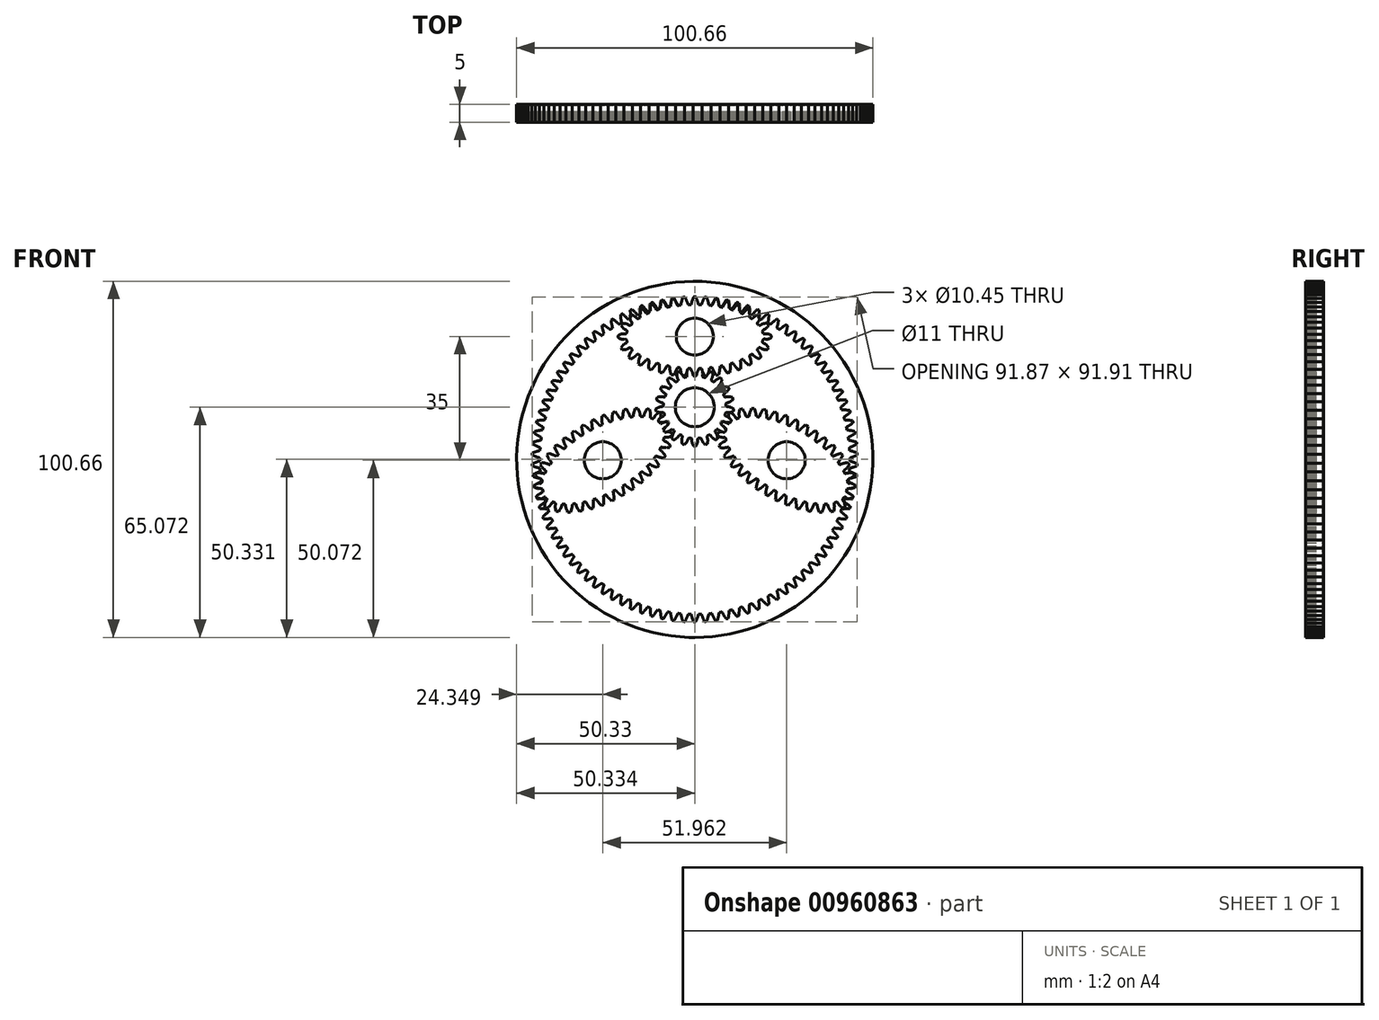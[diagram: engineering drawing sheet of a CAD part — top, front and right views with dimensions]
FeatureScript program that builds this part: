
annotation { "Feature Type Name" : "Feature", "Feature Type Description" : "" }
export const myFeature = defineFeature(function(context is Context, id is Id, definition is map)
    precondition{}
    {
        {
            var Q0;
            Q0=qCreatedBy(makeId("Front.planeOp"),FACE);
            var sketch = newSketch(context, id + "F0", { "sketchPlane" : qUnion([Q0])});
            skCircle(sketch, "E0", {"center": v(0, 0) * mm, "radius": 44.74 * mm});
            skCircle(sketch, "E1", {"center": v(0, 14.74) * mm, "radius": 10 * mm});
            skLineSegment(sketch, "E2", {"start": v(0, 14.74) * mm, "end": v(43.52, -10.38) * mm, "construction": true});
            skEllipse(sketch, "E3", {"center": v(0, 34.74) * mm, "majorRadius": 2 * mm, "minorRadius": 1 * mm, "majorAxis": v(1, 0)});
            skPoint(sketch, "E4", {"position": v(8.66, 9.74) * mm});
            skPoint(sketch, "E5", {"position": v(20.98, -8.92) * mm});
            skPoint(sketch, "E6", {"position": v(-20, 34.74) * mm});
            skPoint(sketch, "E7", {"position": v(0, 24.74) * mm});
            skPoint(sketch, "E8.center.orphan", {"position": v(25.98, -0.26) * mm});
            skLineSegment(sketch, "E9", {"start": v(25.98, -0.26) * mm, "end": v(20.98, -8.92) * mm, "construction": true});
            skEllipse(sketch, "E10", {"center": v(25.98, -0.26) * mm, "majorRadius": 2 * mm, "minorRadius": 1 * mm, "majorAxis": v(-0.87, 0.5)});
            skPoint(sketch, "E11", {"position": v(0, 4.74) * mm});
            skPoint(sketch, "E12", {"position": v(43.9, -8.66) * mm});
            skPoint(sketch, "E13", {"position": v(0, -44.74) * mm});
            skEllipse(sketch, "E14.MirrorC", {"center": v(-25.98, -0.26) * mm, "majorRadius": 2 * mm, "minorRadius": 1 * mm, "majorAxis": v(0.87, 0.5)});
            skSolve(sketch);
        }
        {
            var Q0;
            Q0=qCreatedBy(makeId("Front.planeOp"),FACE);
            var sketch = newSketch(context, id + "F1", { "sketchPlane" : qUnion([Q0])});
            skLineSegment(sketch, "E15", {"start": v(0.42, -11.95) * mm, "end": v(0.63, -11.4) * mm});
            skLineSegment(sketch, "E16", {"start": v(0.63, -11.4) * mm, "end": v(0.66, -11.33) * mm});
            skLineSegment(sketch, "E17", {"start": v(0.66, -11.33) * mm, "end": v(0.7, -11.25) * mm});
            skLineSegment(sketch, "E18", {"start": v(0.7, -11.25) * mm, "end": v(0.72, -11.18) * mm});
            skLineSegment(sketch, "E19", {"start": v(0.72, -11.18) * mm, "end": v(0.75, -11.1) * mm});
            skLineSegment(sketch, "E20", {"start": v(0.75, -11.1) * mm, "end": v(0.77, -11.03) * mm});
            skLineSegment(sketch, "E21", {"start": v(0.77, -11.03) * mm, "end": v(0.8, -10.96) * mm});
            skLineSegment(sketch, "E22", {"start": v(0.8, -10.96) * mm, "end": v(0.83, -10.86) * mm});
            skLineSegment(sketch, "E23", {"start": v(0.83, -10.86) * mm, "end": v(0.88, -10.72) * mm});
            skLineSegment(sketch, "E24", {"start": v(0.88, -10.72) * mm, "end": v(0.9, -10.63) * mm});
            skLineSegment(sketch, "E25", {"start": v(0.9, -10.63) * mm, "end": v(0.93, -10.57) * mm});
            skLineSegment(sketch, "E26", {"start": v(0.93, -10.57) * mm, "end": v(0.96, -10.47) * mm});
            skLineSegment(sketch, "E27", {"start": v(0.96, -10.47) * mm, "end": v(1, -10.36) * mm});
            skLineSegment(sketch, "E28", {"start": v(1, -10.36) * mm, "end": v(1.03, -10.24) * mm});
            skLineSegment(sketch, "E29", {"start": v(1.03, -10.24) * mm, "end": v(1.06, -10.14) * mm});
            skLineSegment(sketch, "E30", {"start": v(1.06, -10.14) * mm, "end": v(1.09, -10.04) * mm});
            skLineSegment(sketch, "E31", {"start": v(1.09, -10.04) * mm, "end": v(1.11, -9.94) * mm});
            skLineSegment(sketch, "E32", {"start": v(1.11, -9.94) * mm, "end": v(1.2, -9.64) * mm});
            skLineSegment(sketch, "E33", {"start": v(1.2, -9.64) * mm, "end": v(1.2, -9.62) * mm});
            skLineSegment(sketch, "E34", {"start": v(1.2, -9.62) * mm, "end": v(1.2, -9.6) * mm});
            skLineSegment(sketch, "E35", {"start": v(1.2, -9.6) * mm, "end": v(1.22, -9.58) * mm});
            skLineSegment(sketch, "E36", {"start": v(1.22, -9.58) * mm, "end": v(1.23, -9.57) * mm});
            skLineSegment(sketch, "E37", {"start": v(1.23, -9.57) * mm, "end": v(1.24, -9.55) * mm});
            skLineSegment(sketch, "E38", {"start": v(1.24, -9.55) * mm, "end": v(1.25, -9.54) * mm});
            skLineSegment(sketch, "E39", {"start": v(1.25, -9.54) * mm, "end": v(1.26, -9.54) * mm});
            skLineSegment(sketch, "E40", {"start": v(1.26, -9.54) * mm, "end": v(1.26, -9.54) * mm});
            skLineSegment(sketch, "E41", {"start": v(1.26, -9.54) * mm, "end": v(1.27, -9.54) * mm});
            skLineSegment(sketch, "E42", {"start": v(1.27, -9.54) * mm, "end": v(1.5, -9.53) * mm});
            skLineSegment(sketch, "E43", {"start": v(1.5, -9.53) * mm, "end": v(1.7, -9.52) * mm});
            skLineSegment(sketch, "E44", {"start": v(1.7, -9.52) * mm, "end": v(1.95, -9.51) * mm});
            skLineSegment(sketch, "E45", {"start": v(1.95, -9.51) * mm, "end": v(1.95, -9.51) * mm});
            skLineSegment(sketch, "E46", {"start": v(1.95, -9.51) * mm, "end": v(1.96, -9.52) * mm});
            skLineSegment(sketch, "E47", {"start": v(1.96, -9.52) * mm, "end": v(1.97, -9.53) * mm});
            skLineSegment(sketch, "E48", {"start": v(1.97, -9.53) * mm, "end": v(1.98, -9.54) * mm});
            skLineSegment(sketch, "E49", {"start": v(1.98, -9.54) * mm, "end": v(2, -9.54) * mm});
            skLineSegment(sketch, "E50", {"start": v(2, -9.54) * mm, "end": v(2, -9.55) * mm});
            skLineSegment(sketch, "E51", {"start": v(2, -9.55) * mm, "end": v(2, -9.56) * mm});
            skLineSegment(sketch, "E52", {"start": v(2, -9.56) * mm, "end": v(2.01, -9.57) * mm});
            skLineSegment(sketch, "E53", {"start": v(2.01, -9.57) * mm, "end": v(2.02, -9.59) * mm});
            skLineSegment(sketch, "E54", {"start": v(2.02, -9.59) * mm, "end": v(2.03, -9.6) * mm});
            skLineSegment(sketch, "E55", {"start": v(2.03, -9.6) * mm, "end": v(2.03, -9.6) * mm});
            skLineSegment(sketch, "E56", {"start": v(2.03, -9.6) * mm, "end": v(2.11, -9.86) * mm});
            skLineSegment(sketch, "E57", {"start": v(2.11, -9.86) * mm, "end": v(2.13, -9.91) * mm});
            skLineSegment(sketch, "E58", {"start": v(2.13, -9.91) * mm, "end": v(2.16, -9.98) * mm});
            skLineSegment(sketch, "E59", {"start": v(2.16, -9.98) * mm, "end": v(2.17, -10.03) * mm});
            skLineSegment(sketch, "E60", {"start": v(2.17, -10.03) * mm, "end": v(2.2, -10.1) * mm});
            skLineSegment(sketch, "E61", {"start": v(2.2, -10.1) * mm, "end": v(2.22, -10.16) * mm});
            skLineSegment(sketch, "E62", {"start": v(2.22, -10.16) * mm, "end": v(2.24, -10.2) * mm});
            skLineSegment(sketch, "E63", {"start": v(2.24, -10.2) * mm, "end": v(2.27, -10.3) * mm});
            skLineSegment(sketch, "E64", {"start": v(2.27, -10.3) * mm, "end": v(2.32, -10.42) * mm});
            skLineSegment(sketch, "E65", {"start": v(2.32, -10.42) * mm, "end": v(2.36, -10.5) * mm});
            skLineSegment(sketch, "E66", {"start": v(2.36, -10.5) * mm, "end": v(2.38, -10.57) * mm});
            skLineSegment(sketch, "E67", {"start": v(2.38, -10.57) * mm, "end": v(2.42, -10.66) * mm});
            skLineSegment(sketch, "E68", {"start": v(2.42, -10.66) * mm, "end": v(2.47, -10.78) * mm});
            skLineSegment(sketch, "E69", {"start": v(2.47, -10.78) * mm, "end": v(2.53, -10.9) * mm});
            skLineSegment(sketch, "E70", {"start": v(2.53, -10.9) * mm, "end": v(2.58, -11.03) * mm});
            skLineSegment(sketch, "E71", {"start": v(2.58, -11.03) * mm, "end": v(2.64, -11.15) * mm});
            skLineSegment(sketch, "E72", {"start": v(2.64, -11.15) * mm, "end": v(2.7, -11.28) * mm});
            skLineSegment(sketch, "E73", {"start": v(2.7, -11.28) * mm, "end": v(2.97, -11.85) * mm});
            skLineSegment(sketch, "E74", {"start": v(2.97, -11.85) * mm, "end": v(3.11, -11.84) * mm});
            skLineSegment(sketch, "E75", {"start": v(3.11, -11.84) * mm, "end": v(3.5, -11.81) * mm});
            skLineSegment(sketch, "E76", {"start": v(3.5, -11.81) * mm, "end": v(3.79, -11.8) * mm});
            skLineSegment(sketch, "E77", {"start": v(3.79, -11.8) * mm, "end": v(3.95, -11.28) * mm});
            skLineSegment(sketch, "E78", {"start": v(3.95, -11.28) * mm, "end": v(3.99, -11.13) * mm});
            skLineSegment(sketch, "E79", {"start": v(3.99, -11.13) * mm, "end": v(4.03, -11) * mm});
            skLineSegment(sketch, "E80", {"start": v(4.03, -11) * mm, "end": v(4.06, -10.88) * mm});
            skLineSegment(sketch, "E81", {"start": v(4.06, -10.88) * mm, "end": v(4.1, -10.74) * mm});
            skLineSegment(sketch, "E82", {"start": v(4.1, -10.74) * mm, "end": v(4.13, -10.63) * mm});
            skLineSegment(sketch, "E83", {"start": v(4.13, -10.63) * mm, "end": v(4.16, -10.51) * mm});
            skLineSegment(sketch, "E84", {"start": v(4.16, -10.51) * mm, "end": v(4.18, -10.42) * mm});
            skLineSegment(sketch, "E85", {"start": v(4.18, -10.42) * mm, "end": v(4.19, -10.38) * mm});
            skLineSegment(sketch, "E86", {"start": v(4.19, -10.38) * mm, "end": v(4.2, -10.3) * mm});
            skLineSegment(sketch, "E87", {"start": v(4.2, -10.3) * mm, "end": v(4.23, -10.2) * mm});
            skLineSegment(sketch, "E88", {"start": v(4.23, -10.2) * mm, "end": v(4.25, -10.1) * mm});
            skLineSegment(sketch, "E89", {"start": v(4.25, -10.1) * mm, "end": v(4.27, -10.01) * mm});
            skLineSegment(sketch, "E90", {"start": v(4.27, -10.01) * mm, "end": v(4.29, -9.92) * mm});
            skLineSegment(sketch, "E91", {"start": v(4.29, -9.92) * mm, "end": v(4.3, -9.84) * mm});
            skLineSegment(sketch, "E92", {"start": v(4.3, -9.84) * mm, "end": v(4.32, -9.76) * mm});
            skLineSegment(sketch, "E93", {"start": v(4.32, -9.76) * mm, "end": v(4.33, -9.68) * mm});
            skLineSegment(sketch, "E94", {"start": v(4.33, -9.68) * mm, "end": v(4.37, -9.45) * mm});
            skLineSegment(sketch, "E95", {"start": v(4.37, -9.45) * mm, "end": v(4.37, -9.44) * mm});
            skLineSegment(sketch, "E96", {"start": v(4.37, -9.44) * mm, "end": v(4.38, -9.41) * mm});
            skLineSegment(sketch, "E97", {"start": v(4.38, -9.41) * mm, "end": v(4.39, -9.4) * mm});
            skLineSegment(sketch, "E98", {"start": v(4.39, -9.4) * mm, "end": v(4.4, -9.38) * mm});
            skLineSegment(sketch, "E99", {"start": v(4.4, -9.38) * mm, "end": v(4.4, -9.36) * mm});
            skLineSegment(sketch, "E100", {"start": v(4.4, -9.36) * mm, "end": v(4.41, -9.35) * mm});
            skLineSegment(sketch, "E101", {"start": v(4.41, -9.35) * mm, "end": v(4.42, -9.33) * mm});
            skLineSegment(sketch, "E102", {"start": v(4.42, -9.33) * mm, "end": v(4.43, -9.33) * mm});
            skLineSegment(sketch, "E103", {"start": v(4.43, -9.33) * mm, "end": v(4.44, -9.32) * mm});
            skLineSegment(sketch, "E104", {"start": v(4.44, -9.32) * mm, "end": v(4.44, -9.32) * mm});
            skLineSegment(sketch, "E105", {"start": v(4.44, -9.32) * mm, "end": v(4.7, -9.3) * mm});
            skLineSegment(sketch, "E106", {"start": v(4.7, -9.3) * mm, "end": v(4.87, -9.27) * mm});
            skLineSegment(sketch, "E107", {"start": v(4.87, -9.27) * mm, "end": v(5.12, -9.24) * mm});
            skLineSegment(sketch, "E108", {"start": v(5.12, -9.24) * mm, "end": v(5.12, -9.24) * mm});
            skLineSegment(sketch, "E109", {"start": v(5.12, -9.24) * mm, "end": v(5.13, -9.24) * mm});
            skLineSegment(sketch, "E110", {"start": v(5.13, -9.24) * mm, "end": v(5.13, -9.24) * mm});
            skLineSegment(sketch, "E111", {"start": v(5.13, -9.24) * mm, "end": v(5.15, -9.25) * mm});
            skLineSegment(sketch, "E112", {"start": v(5.15, -9.25) * mm, "end": v(5.16, -9.26) * mm});
            skLineSegment(sketch, "E113", {"start": v(5.16, -9.26) * mm, "end": v(5.17, -9.27) * mm});
            skLineSegment(sketch, "E114", {"start": v(5.17, -9.27) * mm, "end": v(5.19, -9.29) * mm});
            skLineSegment(sketch, "E115", {"start": v(5.19, -9.29) * mm, "end": v(5.2, -9.3) * mm});
            skLineSegment(sketch, "E116", {"start": v(5.2, -9.3) * mm, "end": v(5.21, -9.33) * mm});
            skLineSegment(sketch, "E117", {"start": v(5.21, -9.33) * mm, "end": v(5.22, -9.35) * mm});
            skLineSegment(sketch, "E118", {"start": v(5.22, -9.35) * mm, "end": v(5.3, -9.55) * mm});
            skLineSegment(sketch, "E119", {"start": v(5.3, -9.55) * mm, "end": v(5.35, -9.65) * mm});
            skLineSegment(sketch, "E120", {"start": v(5.35, -9.65) * mm, "end": v(5.4, -9.74) * mm});
            skLineSegment(sketch, "E121", {"start": v(5.4, -9.74) * mm, "end": v(5.43, -9.84) * mm});
            skLineSegment(sketch, "E122", {"start": v(5.43, -9.84) * mm, "end": v(5.48, -9.94) * mm});
            skLineSegment(sketch, "E123", {"start": v(5.48, -9.94) * mm, "end": v(5.53, -10.04) * mm});
            skLineSegment(sketch, "E124", {"start": v(5.53, -10.04) * mm, "end": v(5.57, -10.13) * mm});
            skLineSegment(sketch, "E125", {"start": v(5.57, -10.13) * mm, "end": v(5.6, -10.2) * mm});
            skLineSegment(sketch, "E126", {"start": v(5.6, -10.2) * mm, "end": v(5.64, -10.26) * mm});
            skLineSegment(sketch, "E127", {"start": v(5.64, -10.26) * mm, "end": v(5.68, -10.34) * mm});
            skLineSegment(sketch, "E128", {"start": v(5.68, -10.34) * mm, "end": v(5.73, -10.43) * mm});
            skLineSegment(sketch, "E129", {"start": v(5.73, -10.43) * mm, "end": v(5.78, -10.53) * mm});
            skLineSegment(sketch, "E130", {"start": v(5.78, -10.53) * mm, "end": v(5.83, -10.63) * mm});
            skLineSegment(sketch, "E131", {"start": v(5.83, -10.63) * mm, "end": v(5.88, -10.72) * mm});
            skLineSegment(sketch, "E132", {"start": v(5.88, -10.72) * mm, "end": v(5.94, -10.82) * mm});
            skLineSegment(sketch, "E133", {"start": v(5.94, -10.82) * mm, "end": v(6, -10.92) * mm});
            skLineSegment(sketch, "E134", {"start": v(6, -10.92) * mm, "end": v(6.05, -11.02) * mm});
            skLineSegment(sketch, "E135", {"start": v(6.05, -11.02) * mm, "end": v(6.33, -11.5) * mm});
            skLineSegment(sketch, "E136", {"start": v(6.33, -11.5) * mm, "end": v(6.63, -11.45) * mm});
            skLineSegment(sketch, "E137", {"start": v(6.63, -11.45) * mm, "end": v(6.94, -11.4) * mm});
            skLineSegment(sketch, "E138", {"start": v(6.94, -11.4) * mm, "end": v(7.14, -11.37) * mm});
            skLineSegment(sketch, "E139", {"start": v(7.14, -11.37) * mm, "end": v(7.27, -10.78) * mm});
            skLineSegment(sketch, "E140", {"start": v(7.27, -10.78) * mm, "end": v(7.3, -10.66) * mm});
            skLineSegment(sketch, "E141", {"start": v(7.3, -10.66) * mm, "end": v(7.31, -10.55) * mm});
            skLineSegment(sketch, "E142", {"start": v(7.31, -10.55) * mm, "end": v(7.33, -10.44) * mm});
            skLineSegment(sketch, "E143", {"start": v(7.33, -10.44) * mm, "end": v(7.36, -10.33) * mm});
            skLineSegment(sketch, "E144", {"start": v(7.36, -10.33) * mm, "end": v(7.37, -10.23) * mm});
            skLineSegment(sketch, "E145", {"start": v(7.37, -10.23) * mm, "end": v(7.39, -10.14) * mm});
            skLineSegment(sketch, "E146", {"start": v(7.39, -10.14) * mm, "end": v(7.4, -10.03) * mm});
            skLineSegment(sketch, "E147", {"start": v(7.4, -10.03) * mm, "end": v(7.41, -9.98) * mm});
            skLineSegment(sketch, "E148", {"start": v(7.41, -9.98) * mm, "end": v(7.42, -9.93) * mm});
            skLineSegment(sketch, "E149", {"start": v(7.42, -9.93) * mm, "end": v(7.43, -9.86) * mm});
            skLineSegment(sketch, "E150", {"start": v(7.43, -9.86) * mm, "end": v(7.44, -9.78) * mm});
            skLineSegment(sketch, "E151", {"start": v(7.44, -9.78) * mm, "end": v(7.45, -9.7) * mm});
            skLineSegment(sketch, "E152", {"start": v(7.45, -9.7) * mm, "end": v(7.46, -9.62) * mm});
            skLineSegment(sketch, "E153", {"start": v(7.46, -9.62) * mm, "end": v(7.47, -9.55) * mm});
            skLineSegment(sketch, "E154", {"start": v(7.47, -9.55) * mm, "end": v(7.48, -9.5) * mm});
            skLineSegment(sketch, "E155", {"start": v(7.48, -9.5) * mm, "end": v(7.48, -9.42) * mm});
            skLineSegment(sketch, "E156", {"start": v(7.48, -9.42) * mm, "end": v(7.49, -9.36) * mm});
            skLineSegment(sketch, "E157", {"start": v(7.49, -9.36) * mm, "end": v(7.5, -9.3) * mm});
            skLineSegment(sketch, "E158", {"start": v(7.5, -9.3) * mm, "end": v(7.5, -9.24) * mm});
            skLineSegment(sketch, "E159", {"start": v(7.5, -9.24) * mm, "end": v(7.52, -9) * mm});
            skLineSegment(sketch, "E160", {"start": v(7.52, -9) * mm, "end": v(7.52, -8.99) * mm});
            skLineSegment(sketch, "E161", {"start": v(7.52, -8.99) * mm, "end": v(7.52, -8.97) * mm});
            skLineSegment(sketch, "E162", {"start": v(7.52, -8.97) * mm, "end": v(7.53, -8.95) * mm});
            skLineSegment(sketch, "E163", {"start": v(7.53, -8.95) * mm, "end": v(7.53, -8.93) * mm});
            skLineSegment(sketch, "E164", {"start": v(7.53, -8.93) * mm, "end": v(7.54, -8.91) * mm});
            skLineSegment(sketch, "E165", {"start": v(7.54, -8.91) * mm, "end": v(7.55, -8.9) * mm});
            skLineSegment(sketch, "E166", {"start": v(7.55, -8.9) * mm, "end": v(7.55, -8.88) * mm});
            skLineSegment(sketch, "E167", {"start": v(7.55, -8.88) * mm, "end": v(7.56, -8.87) * mm});
            skLineSegment(sketch, "E168", {"start": v(7.56, -8.87) * mm, "end": v(7.57, -8.86) * mm});
            skLineSegment(sketch, "E169", {"start": v(7.57, -8.86) * mm, "end": v(7.58, -8.86) * mm});
            skLineSegment(sketch, "E170", {"start": v(7.58, -8.86) * mm, "end": v(7.58, -8.85) * mm});
            skLineSegment(sketch, "E171", {"start": v(7.58, -8.85) * mm, "end": v(7.58, -8.85) * mm});
            skLineSegment(sketch, "E172", {"start": v(7.58, -8.85) * mm, "end": v(7.6, -8.85) * mm});
            skLineSegment(sketch, "E173", {"start": v(7.6, -8.85) * mm, "end": v(7.6, -8.85) * mm});
            skLineSegment(sketch, "E174", {"start": v(7.6, -8.85) * mm, "end": v(7.65, -8.84) * mm});
            skLineSegment(sketch, "E175", {"start": v(7.65, -8.84) * mm, "end": v(7.85, -8.8) * mm});
            skLineSegment(sketch, "E176", {"start": v(7.85, -8.8) * mm, "end": v(8, -8.77) * mm});
            skLineSegment(sketch, "E177", {"start": v(8, -8.77) * mm, "end": v(8.18, -8.73) * mm});
            skLineSegment(sketch, "E178", {"start": v(8.18, -8.73) * mm, "end": v(8.25, -8.72) * mm});
            skLineSegment(sketch, "E179", {"start": v(8.25, -8.72) * mm, "end": v(8.25, -8.71) * mm});
            skLineSegment(sketch, "E180", {"start": v(8.25, -8.71) * mm, "end": v(8.26, -8.71) * mm});
            skLineSegment(sketch, "E181", {"start": v(8.26, -8.71) * mm, "end": v(8.26, -8.71) * mm});
            skLineSegment(sketch, "E182", {"start": v(8.26, -8.71) * mm, "end": v(8.27, -8.72) * mm});
            skLineSegment(sketch, "E183", {"start": v(8.27, -8.72) * mm, "end": v(8.28, -8.72) * mm});
            skLineSegment(sketch, "E184", {"start": v(8.28, -8.72) * mm, "end": v(8.29, -8.73) * mm});
            skLineSegment(sketch, "E185", {"start": v(8.29, -8.73) * mm, "end": v(8.3, -8.73) * mm});
            skLineSegment(sketch, "E186", {"start": v(8.3, -8.73) * mm, "end": v(8.31, -8.75) * mm});
            skLineSegment(sketch, "E187", {"start": v(8.31, -8.75) * mm, "end": v(8.33, -8.76) * mm});
            skLineSegment(sketch, "E188", {"start": v(8.33, -8.76) * mm, "end": v(8.34, -8.78) * mm});
            skLineSegment(sketch, "E189", {"start": v(8.34, -8.78) * mm, "end": v(8.36, -8.8) * mm});
            skLineSegment(sketch, "E190", {"start": v(8.36, -8.8) * mm, "end": v(8.36, -8.8) * mm});
            skLineSegment(sketch, "E191", {"start": v(8.36, -8.8) * mm, "end": v(8.5, -9.05) * mm});
            skLineSegment(sketch, "E192", {"start": v(8.5, -9.05) * mm, "end": v(8.53, -9.13) * mm});
            skLineSegment(sketch, "E193", {"start": v(8.53, -9.13) * mm, "end": v(8.57, -9.2) * mm});
            skLineSegment(sketch, "E194", {"start": v(8.57, -9.2) * mm, "end": v(8.62, -9.28) * mm});
            skLineSegment(sketch, "E195", {"start": v(8.62, -9.28) * mm, "end": v(8.66, -9.35) * mm});
            skLineSegment(sketch, "E196", {"start": v(8.66, -9.35) * mm, "end": v(8.7, -9.43) * mm});
            skLineSegment(sketch, "E197", {"start": v(8.7, -9.43) * mm, "end": v(8.75, -9.51) * mm});
            skLineSegment(sketch, "E198", {"start": v(8.75, -9.51) * mm, "end": v(8.8, -9.59) * mm});
            skLineSegment(sketch, "E199", {"start": v(8.8, -9.59) * mm, "end": v(8.83, -9.64) * mm});
            skLineSegment(sketch, "E200", {"start": v(8.83, -9.64) * mm, "end": v(8.85, -9.68) * mm});
            skLineSegment(sketch, "E201", {"start": v(8.85, -9.68) * mm, "end": v(8.89, -9.73) * mm});
            skLineSegment(sketch, "E202", {"start": v(8.89, -9.73) * mm, "end": v(8.94, -9.81) * mm});
            skLineSegment(sketch, "E203", {"start": v(8.94, -9.81) * mm, "end": v(8.98, -9.88) * mm});
            skLineSegment(sketch, "E204", {"start": v(8.98, -9.88) * mm, "end": v(9.03, -9.96) * mm});
            skLineSegment(sketch, "E205", {"start": v(9.03, -9.96) * mm, "end": v(9.08, -10.04) * mm});
            skLineSegment(sketch, "E206", {"start": v(9.08, -10.04) * mm, "end": v(9.13, -10.1) * mm});
            skLineSegment(sketch, "E207", {"start": v(9.13, -10.1) * mm, "end": v(9.18, -10.19) * mm});
            skLineSegment(sketch, "E208", {"start": v(9.18, -10.19) * mm, "end": v(9.23, -10.25) * mm});
            skLineSegment(sketch, "E209", {"start": v(9.23, -10.25) * mm, "end": v(9.28, -10.33) * mm});
            skLineSegment(sketch, "E210", {"start": v(9.28, -10.33) * mm, "end": v(9.34, -10.4) * mm});
            skLineSegment(sketch, "E211", {"start": v(9.34, -10.4) * mm, "end": v(9.66, -10.85) * mm});
            skLineSegment(sketch, "E212", {"start": v(9.66, -10.85) * mm, "end": v(9.74, -10.83) * mm});
            skLineSegment(sketch, "E213", {"start": v(9.74, -10.83) * mm, "end": v(9.98, -10.77) * mm});
            skLineSegment(sketch, "E214", {"start": v(9.98, -10.77) * mm, "end": v(10.23, -10.71) * mm});
            skLineSegment(sketch, "E215", {"start": v(10.23, -10.71) * mm, "end": v(10.45, -10.65) * mm});
            skLineSegment(sketch, "E216", {"start": v(10.45, -10.65) * mm, "end": v(10.53, -10.04) * mm});
            skLineSegment(sketch, "E217", {"start": v(10.53, -10.04) * mm, "end": v(10.54, -9.94) * mm});
            skLineSegment(sketch, "E218", {"start": v(10.54, -9.94) * mm, "end": v(10.55, -9.85) * mm});
            skLineSegment(sketch, "E219", {"start": v(10.55, -9.85) * mm, "end": v(10.56, -9.75) * mm});
            skLineSegment(sketch, "E220", {"start": v(10.56, -9.75) * mm, "end": v(10.56, -9.68) * mm});
            skLineSegment(sketch, "E221", {"start": v(10.56, -9.68) * mm, "end": v(10.57, -9.59) * mm});
            skLineSegment(sketch, "E222", {"start": v(10.57, -9.59) * mm, "end": v(10.58, -9.51) * mm});
            skLineSegment(sketch, "E223", {"start": v(10.58, -9.51) * mm, "end": v(10.58, -9.43) * mm});
            skLineSegment(sketch, "E224", {"start": v(10.58, -9.43) * mm, "end": v(10.6, -9.35) * mm});
            skLineSegment(sketch, "E225", {"start": v(10.6, -9.35) * mm, "end": v(10.6, -9.29) * mm});
            skLineSegment(sketch, "E226", {"start": v(10.6, -9.29) * mm, "end": v(10.6, -9.24) * mm});
            skLineSegment(sketch, "E227", {"start": v(10.6, -9.24) * mm, "end": v(10.6, -9.2) * mm});
            skLineSegment(sketch, "E228", {"start": v(10.6, -9.2) * mm, "end": v(10.6, -9.14) * mm});
            skLineSegment(sketch, "E229", {"start": v(10.6, -9.14) * mm, "end": v(10.6, -9.04) * mm});
            skLineSegment(sketch, "E230", {"start": v(10.6, -9.04) * mm, "end": v(10.6, -8.96) * mm});
            skLineSegment(sketch, "E231", {"start": v(10.6, -8.96) * mm, "end": v(10.6, -8.87) * mm});
            skLineSegment(sketch, "E232", {"start": v(10.6, -8.87) * mm, "end": v(10.6, -8.8) * mm});
            skLineSegment(sketch, "E233", {"start": v(10.6, -8.8) * mm, "end": v(10.6, -8.73) * mm});
            skLineSegment(sketch, "E234", {"start": v(10.6, -8.73) * mm, "end": v(10.6, -8.66) * mm});
            skLineSegment(sketch, "E235", {"start": v(10.6, -8.66) * mm, "end": v(10.6, -8.6) * mm});
            skLineSegment(sketch, "E236", {"start": v(10.6, -8.6) * mm, "end": v(10.6, -8.55) * mm});
            skLineSegment(sketch, "E237", {"start": v(10.6, -8.55) * mm, "end": v(10.6, -8.3) * mm});
            skLineSegment(sketch, "E238", {"start": v(10.6, -8.3) * mm, "end": v(10.6, -8.28) * mm});
            skLineSegment(sketch, "E239", {"start": v(10.6, -8.28) * mm, "end": v(10.6, -8.25) * mm});
            skLineSegment(sketch, "E240", {"start": v(10.6, -8.25) * mm, "end": v(10.6, -8.23) * mm});
            skLineSegment(sketch, "E241", {"start": v(10.6, -8.23) * mm, "end": v(10.6, -8.2) * mm});
            skLineSegment(sketch, "E242", {"start": v(10.6, -8.2) * mm, "end": v(10.61, -8.18) * mm});
            skLineSegment(sketch, "E243", {"start": v(10.61, -8.18) * mm, "end": v(10.62, -8.16) * mm});
            skLineSegment(sketch, "E244", {"start": v(10.62, -8.16) * mm, "end": v(10.63, -8.14) * mm});
            skLineSegment(sketch, "E245", {"start": v(10.63, -8.14) * mm, "end": v(10.64, -8.13) * mm});
            skLineSegment(sketch, "E246", {"start": v(10.64, -8.13) * mm, "end": v(10.65, -8.11) * mm});
            skLineSegment(sketch, "E247", {"start": v(10.65, -8.11) * mm, "end": v(10.65, -8.11) * mm});
            skLineSegment(sketch, "E248", {"start": v(10.65, -8.11) * mm, "end": v(10.66, -8.1) * mm});
            skLineSegment(sketch, "E249", {"start": v(10.66, -8.1) * mm, "end": v(10.66, -8.1) * mm});
            skLineSegment(sketch, "E250", {"start": v(10.66, -8.1) * mm, "end": v(10.67, -8.1) * mm});
            skLineSegment(sketch, "E251", {"start": v(10.67, -8.1) * mm, "end": v(10.78, -8.07) * mm});
            skLineSegment(sketch, "E252", {"start": v(10.78, -8.07) * mm, "end": v(10.93, -8.02) * mm});
            skLineSegment(sketch, "E253", {"start": v(10.93, -8.02) * mm, "end": v(11.04, -8) * mm});
            skLineSegment(sketch, "E254", {"start": v(11.04, -8) * mm, "end": v(11.23, -7.93) * mm});
            skLineSegment(sketch, "E255", {"start": v(11.23, -7.93) * mm, "end": v(11.3, -7.9) * mm});
            skLineSegment(sketch, "E256", {"start": v(11.3, -7.9) * mm, "end": v(11.3, -7.9) * mm});
            skLineSegment(sketch, "E257", {"start": v(11.3, -7.9) * mm, "end": v(11.31, -7.9) * mm});
            skLineSegment(sketch, "E258", {"start": v(11.31, -7.9) * mm, "end": v(11.32, -7.9) * mm});
            skLineSegment(sketch, "E259", {"start": v(11.32, -7.9) * mm, "end": v(11.32, -7.9) * mm});
            skLineSegment(sketch, "E260", {"start": v(11.32, -7.9) * mm, "end": v(11.33, -7.9) * mm});
            skLineSegment(sketch, "E261", {"start": v(11.33, -7.9) * mm, "end": v(11.34, -7.91) * mm});
            skLineSegment(sketch, "E262", {"start": v(11.34, -7.91) * mm, "end": v(11.35, -7.92) * mm});
            skLineSegment(sketch, "E263", {"start": v(11.35, -7.92) * mm, "end": v(11.37, -7.92) * mm});
            skLineSegment(sketch, "E264", {"start": v(11.37, -7.92) * mm, "end": v(11.38, -7.93) * mm});
            skLineSegment(sketch, "E265", {"start": v(11.38, -7.93) * mm, "end": v(11.4, -7.94) * mm});
            skLineSegment(sketch, "E266", {"start": v(11.4, -7.94) * mm, "end": v(11.4, -7.95) * mm});
            skLineSegment(sketch, "E267", {"start": v(11.4, -7.95) * mm, "end": v(11.42, -7.97) * mm});
            skLineSegment(sketch, "E268", {"start": v(11.42, -7.97) * mm, "end": v(11.43, -7.98) * mm});
            skLineSegment(sketch, "E269", {"start": v(11.43, -7.98) * mm, "end": v(11.44, -8) * mm});
            skLineSegment(sketch, "E270", {"start": v(11.44, -8) * mm, "end": v(11.6, -8.24) * mm});
            skLineSegment(sketch, "E271", {"start": v(11.6, -8.24) * mm, "end": v(11.64, -8.3) * mm});
            skLineSegment(sketch, "E272", {"start": v(11.64, -8.3) * mm, "end": v(11.68, -8.36) * mm});
            skLineSegment(sketch, "E273", {"start": v(11.68, -8.36) * mm, "end": v(11.71, -8.41) * mm});
            skLineSegment(sketch, "E274", {"start": v(11.71, -8.41) * mm, "end": v(11.75, -8.47) * mm});
            skLineSegment(sketch, "E275", {"start": v(11.75, -8.47) * mm, "end": v(11.78, -8.51) * mm});
            skLineSegment(sketch, "E276", {"start": v(11.78, -8.51) * mm, "end": v(11.83, -8.58) * mm});
            skLineSegment(sketch, "E277", {"start": v(11.83, -8.58) * mm, "end": v(11.86, -8.63) * mm});
            skLineSegment(sketch, "E278", {"start": v(11.86, -8.63) * mm, "end": v(11.9, -8.69) * mm});
            skLineSegment(sketch, "E279", {"start": v(11.9, -8.69) * mm, "end": v(11.94, -8.73) * mm});
            skLineSegment(sketch, "E280", {"start": v(11.94, -8.73) * mm, "end": v(11.97, -8.78) * mm});
            skLineSegment(sketch, "E281", {"start": v(11.97, -8.78) * mm, "end": v(12, -8.8) * mm});
            skLineSegment(sketch, "E282", {"start": v(12, -8.8) * mm, "end": v(12.04, -8.86) * mm});
            skLineSegment(sketch, "E283", {"start": v(12.04, -8.86) * mm, "end": v(12.1, -8.94) * mm});
            skLineSegment(sketch, "E284", {"start": v(12.1, -8.94) * mm, "end": v(12.16, -9.02) * mm});
            skLineSegment(sketch, "E285", {"start": v(12.16, -9.02) * mm, "end": v(12.22, -9.1) * mm});
            skLineSegment(sketch, "E286", {"start": v(12.22, -9.1) * mm, "end": v(12.3, -9.18) * mm});
            skLineSegment(sketch, "E287", {"start": v(12.3, -9.18) * mm, "end": v(12.35, -9.25) * mm});
            skLineSegment(sketch, "E288", {"start": v(12.35, -9.25) * mm, "end": v(12.42, -9.33) * mm});
            skLineSegment(sketch, "E289", {"start": v(12.42, -9.33) * mm, "end": v(12.49, -9.4) * mm});
            skLineSegment(sketch, "E290", {"start": v(12.49, -9.4) * mm, "end": v(12.55, -9.48) * mm});
            skLineSegment(sketch, "E291", {"start": v(12.55, -9.48) * mm, "end": v(12.93, -9.89) * mm});
            skLineSegment(sketch, "E292", {"start": v(12.93, -9.89) * mm, "end": v(12.96, -9.88) * mm});
            skLineSegment(sketch, "E293", {"start": v(12.96, -9.88) * mm, "end": v(13.14, -9.81) * mm});
            skLineSegment(sketch, "E294", {"start": v(13.14, -9.81) * mm, "end": v(13.32, -9.75) * mm});
            skLineSegment(sketch, "E295", {"start": v(13.32, -9.75) * mm, "end": v(13.5, -9.68) * mm});
            skLineSegment(sketch, "E296", {"start": v(13.5, -9.68) * mm, "end": v(13.67, -9.62) * mm});
            skLineSegment(sketch, "E297", {"start": v(13.67, -9.62) * mm, "end": v(13.68, -9.61) * mm});
            skLineSegment(sketch, "E298", {"start": v(13.68, -9.61) * mm, "end": v(13.7, -9.08) * mm});
            skLineSegment(sketch, "E299", {"start": v(13.7, -9.08) * mm, "end": v(13.7, -8.96) * mm});
            skLineSegment(sketch, "E300", {"start": v(13.7, -8.96) * mm, "end": v(13.7, -8.85) * mm});
            skLineSegment(sketch, "E301", {"start": v(13.7, -8.85) * mm, "end": v(13.7, -8.75) * mm});
            skLineSegment(sketch, "E302", {"start": v(13.7, -8.75) * mm, "end": v(13.7, -8.65) * mm});
            skLineSegment(sketch, "E303", {"start": v(13.7, -8.65) * mm, "end": v(13.7, -8.56) * mm});
            skLineSegment(sketch, "E304", {"start": v(13.7, -8.56) * mm, "end": v(13.7, -8.46) * mm});
            skLineSegment(sketch, "E305", {"start": v(13.7, -8.46) * mm, "end": v(13.7, -8.38) * mm});
            skLineSegment(sketch, "E306", {"start": v(13.7, -8.38) * mm, "end": v(13.69, -8.3) * mm});
            skLineSegment(sketch, "E307", {"start": v(13.69, -8.3) * mm, "end": v(13.68, -8.22) * mm});
            skLineSegment(sketch, "E308", {"start": v(13.68, -8.22) * mm, "end": v(13.68, -8.17) * mm});
            skLineSegment(sketch, "E309", {"start": v(13.68, -8.17) * mm, "end": v(13.68, -8.14) * mm});
            skLineSegment(sketch, "E310", {"start": v(13.68, -8.14) * mm, "end": v(13.68, -8.12) * mm});
            skLineSegment(sketch, "E311", {"start": v(13.68, -8.12) * mm, "end": v(13.67, -8.05) * mm});
            skLineSegment(sketch, "E312", {"start": v(13.67, -8.05) * mm, "end": v(13.66, -7.98) * mm});
            skLineSegment(sketch, "E313", {"start": v(13.66, -7.98) * mm, "end": v(13.66, -7.92) * mm});
            skLineSegment(sketch, "E314", {"start": v(13.66, -7.92) * mm, "end": v(13.65, -7.85) * mm});
            skLineSegment(sketch, "E315", {"start": v(13.65, -7.85) * mm, "end": v(13.64, -7.78) * mm});
            skLineSegment(sketch, "E316", {"start": v(13.64, -7.78) * mm, "end": v(13.63, -7.73) * mm});
            skLineSegment(sketch, "E317", {"start": v(13.63, -7.73) * mm, "end": v(13.63, -7.68) * mm});
            skLineSegment(sketch, "E318", {"start": v(13.63, -7.68) * mm, "end": v(13.62, -7.63) * mm});
            skLineSegment(sketch, "E319", {"start": v(13.62, -7.63) * mm, "end": v(13.61, -7.58) * mm});
            skLineSegment(sketch, "E320", {"start": v(13.61, -7.58) * mm, "end": v(13.6, -7.55) * mm});
            skLineSegment(sketch, "E321", {"start": v(13.6, -7.55) * mm, "end": v(13.56, -7.33) * mm});
            skLineSegment(sketch, "E322", {"start": v(13.56, -7.33) * mm, "end": v(13.56, -7.31) * mm});
            skLineSegment(sketch, "E323", {"start": v(13.56, -7.31) * mm, "end": v(13.56, -7.3) * mm});
            skLineSegment(sketch, "E324", {"start": v(13.56, -7.3) * mm, "end": v(13.55, -7.26) * mm});
            skLineSegment(sketch, "E325", {"start": v(13.55, -7.26) * mm, "end": v(13.56, -7.24) * mm});
            skLineSegment(sketch, "E326", {"start": v(13.56, -7.24) * mm, "end": v(13.56, -7.2) * mm});
            skLineSegment(sketch, "E327", {"start": v(13.56, -7.2) * mm, "end": v(13.56, -7.18) * mm});
            skLineSegment(sketch, "E328", {"start": v(13.56, -7.18) * mm, "end": v(13.56, -7.15) * mm});
            skLineSegment(sketch, "E329", {"start": v(13.56, -7.15) * mm, "end": v(13.57, -7.13) * mm});
            skLineSegment(sketch, "E330", {"start": v(13.57, -7.13) * mm, "end": v(13.58, -7.1) * mm});
            skLineSegment(sketch, "E331", {"start": v(13.58, -7.1) * mm, "end": v(13.58, -7.09) * mm});
            skLineSegment(sketch, "E332", {"start": v(13.58, -7.09) * mm, "end": v(13.6, -7.07) * mm});
            skLineSegment(sketch, "E333", {"start": v(13.6, -7.07) * mm, "end": v(13.6, -7.06) * mm});
            skLineSegment(sketch, "E334", {"start": v(13.6, -7.06) * mm, "end": v(13.6, -7.06) * mm});
            skLineSegment(sketch, "E335", {"start": v(13.6, -7.06) * mm, "end": v(13.61, -7.05) * mm});
            skLineSegment(sketch, "E336", {"start": v(13.61, -7.05) * mm, "end": v(13.62, -7.05) * mm});
            skLineSegment(sketch, "E337", {"start": v(13.62, -7.05) * mm, "end": v(13.76, -6.99) * mm});
            skLineSegment(sketch, "E338", {"start": v(13.76, -6.99) * mm, "end": v(13.87, -6.94) * mm});
            skLineSegment(sketch, "E339", {"start": v(13.87, -6.94) * mm, "end": v(13.96, -6.9) * mm});
            skLineSegment(sketch, "E340", {"start": v(13.96, -6.9) * mm, "end": v(14.08, -6.85) * mm});
            skLineSegment(sketch, "E341", {"start": v(14.08, -6.85) * mm, "end": v(14.22, -6.78) * mm});
            skLineSegment(sketch, "E342", {"start": v(14.22, -6.78) * mm, "end": v(14.22, -6.78) * mm});
            skLineSegment(sketch, "E343", {"start": v(14.22, -6.78) * mm, "end": v(14.23, -6.78) * mm});
            skLineSegment(sketch, "E344", {"start": v(14.23, -6.78) * mm, "end": v(14.23, -6.78) * mm});
            skLineSegment(sketch, "E345", {"start": v(14.23, -6.78) * mm, "end": v(14.24, -6.78) * mm});
            skLineSegment(sketch, "E346", {"start": v(14.24, -6.78) * mm, "end": v(14.25, -6.78) * mm});
            skLineSegment(sketch, "E347", {"start": v(14.25, -6.78) * mm, "end": v(14.27, -6.78) * mm});
            skLineSegment(sketch, "E348", {"start": v(14.27, -6.78) * mm, "end": v(14.29, -6.79) * mm});
            skLineSegment(sketch, "E349", {"start": v(14.29, -6.79) * mm, "end": v(14.3, -6.8) * mm});
            skLineSegment(sketch, "E350", {"start": v(14.3, -6.8) * mm, "end": v(14.32, -6.8) * mm});
            skLineSegment(sketch, "E351", {"start": v(14.32, -6.8) * mm, "end": v(14.34, -6.82) * mm});
            skLineSegment(sketch, "E352", {"start": v(14.34, -6.82) * mm, "end": v(14.36, -6.83) * mm});
            skLineSegment(sketch, "E353", {"start": v(14.36, -6.83) * mm, "end": v(14.38, -6.85) * mm});
            skLineSegment(sketch, "E354", {"start": v(14.38, -6.85) * mm, "end": v(14.4, -6.87) * mm});
            skLineSegment(sketch, "E355", {"start": v(14.4, -6.87) * mm, "end": v(14.42, -6.89) * mm});
            skLineSegment(sketch, "E356", {"start": v(14.42, -6.89) * mm, "end": v(14.55, -7.06) * mm});
            skLineSegment(sketch, "E357", {"start": v(14.55, -7.06) * mm, "end": v(14.6, -7.12) * mm});
            skLineSegment(sketch, "E358", {"start": v(14.6, -7.12) * mm, "end": v(14.64, -7.17) * mm});
            skLineSegment(sketch, "E359", {"start": v(14.64, -7.17) * mm, "end": v(14.69, -7.22) * mm});
            skLineSegment(sketch, "E360", {"start": v(14.69, -7.22) * mm, "end": v(14.73, -7.28) * mm});
            skLineSegment(sketch, "E361", {"start": v(14.73, -7.28) * mm, "end": v(14.77, -7.32) * mm});
            skLineSegment(sketch, "E362", {"start": v(14.77, -7.32) * mm, "end": v(14.82, -7.38) * mm});
            skLineSegment(sketch, "E363", {"start": v(14.82, -7.38) * mm, "end": v(14.87, -7.43) * mm});
            skLineSegment(sketch, "E364", {"start": v(14.87, -7.43) * mm, "end": v(14.92, -7.48) * mm});
            skLineSegment(sketch, "E365", {"start": v(14.92, -7.48) * mm, "end": v(14.97, -7.53) * mm});
            skLineSegment(sketch, "E366", {"start": v(14.97, -7.53) * mm, "end": v(15, -7.57) * mm});
            skLineSegment(sketch, "E367", {"start": v(15, -7.57) * mm, "end": v(15.02, -7.59) * mm});
            skLineSegment(sketch, "E368", {"start": v(15.02, -7.59) * mm, "end": v(15.05, -7.62) * mm});
            skLineSegment(sketch, "E369", {"start": v(15.05, -7.62) * mm, "end": v(15.1, -7.67) * mm});
            skLineSegment(sketch, "E370", {"start": v(15.1, -7.67) * mm, "end": v(15.15, -7.72) * mm});
            skLineSegment(sketch, "E371", {"start": v(15.15, -7.72) * mm, "end": v(15.2, -7.77) * mm});
            skLineSegment(sketch, "E372", {"start": v(15.2, -7.77) * mm, "end": v(15.27, -7.84) * mm});
            skLineSegment(sketch, "E373", {"start": v(15.27, -7.84) * mm, "end": v(15.34, -7.9) * mm});
            skLineSegment(sketch, "E374", {"start": v(15.34, -7.9) * mm, "end": v(15.4, -7.96) * mm});
            skLineSegment(sketch, "E375", {"start": v(15.4, -7.96) * mm, "end": v(15.48, -8.03) * mm});
            skLineSegment(sketch, "E376", {"start": v(15.48, -8.03) * mm, "end": v(15.55, -8.09) * mm});
            skLineSegment(sketch, "E377", {"start": v(15.55, -8.09) * mm, "end": v(15.62, -8.15) * mm});
            skLineSegment(sketch, "E378", {"start": v(15.62, -8.15) * mm, "end": v(15.7, -8.2) * mm});
            skLineSegment(sketch, "E379", {"start": v(15.7, -8.2) * mm, "end": v(16.1, -8.53) * mm});
            skLineSegment(sketch, "E380", {"start": v(16.1, -8.53) * mm, "end": v(16.21, -8.47) * mm});
            skLineSegment(sketch, "E381", {"start": v(16.21, -8.47) * mm, "end": v(16.33, -8.4) * mm});
            skLineSegment(sketch, "E382", {"start": v(16.33, -8.4) * mm, "end": v(16.45, -8.35) * mm});
            skLineSegment(sketch, "E383", {"start": v(16.45, -8.35) * mm, "end": v(16.56, -8.29) * mm});
            skLineSegment(sketch, "E384", {"start": v(16.56, -8.29) * mm, "end": v(16.67, -8.22) * mm});
            skLineSegment(sketch, "E385", {"start": v(16.67, -8.22) * mm, "end": v(16.78, -8.16) * mm});
            skLineSegment(sketch, "E386", {"start": v(16.78, -8.16) * mm, "end": v(16.8, -8.16) * mm});
            skLineSegment(sketch, "E387", {"start": v(16.8, -8.16) * mm, "end": v(16.73, -7.55) * mm});
            skLineSegment(sketch, "E388", {"start": v(16.73, -7.55) * mm, "end": v(16.71, -7.44) * mm});
            skLineSegment(sketch, "E389", {"start": v(16.71, -7.44) * mm, "end": v(16.7, -7.35) * mm});
            skLineSegment(sketch, "E390", {"start": v(16.7, -7.35) * mm, "end": v(16.69, -7.25) * mm});
            skLineSegment(sketch, "E391", {"start": v(16.69, -7.25) * mm, "end": v(16.67, -7.16) * mm});
            skLineSegment(sketch, "E392", {"start": v(16.67, -7.16) * mm, "end": v(16.66, -7.08) * mm});
            skLineSegment(sketch, "E393", {"start": v(16.66, -7.08) * mm, "end": v(16.65, -7) * mm});
            skLineSegment(sketch, "E394", {"start": v(16.65, -7) * mm, "end": v(16.63, -6.93) * mm});
            skLineSegment(sketch, "E395", {"start": v(16.63, -6.93) * mm, "end": v(16.62, -6.85) * mm});
            skLineSegment(sketch, "E396", {"start": v(16.62, -6.85) * mm, "end": v(16.6, -6.78) * mm});
            skLineSegment(sketch, "E397", {"start": v(16.6, -6.78) * mm, "end": v(16.59, -6.73) * mm});
            skLineSegment(sketch, "E398", {"start": v(16.59, -6.73) * mm, "end": v(16.58, -6.71) * mm});
            skLineSegment(sketch, "E399", {"start": v(16.58, -6.71) * mm, "end": v(16.58, -6.68) * mm});
            skLineSegment(sketch, "E400", {"start": v(16.58, -6.68) * mm, "end": v(16.56, -6.62) * mm});
            skLineSegment(sketch, "E401", {"start": v(16.56, -6.62) * mm, "end": v(16.54, -6.56) * mm});
            skLineSegment(sketch, "E402", {"start": v(16.54, -6.56) * mm, "end": v(16.53, -6.51) * mm});
            skLineSegment(sketch, "E403", {"start": v(16.53, -6.51) * mm, "end": v(16.52, -6.46) * mm});
            skLineSegment(sketch, "E404", {"start": v(16.52, -6.46) * mm, "end": v(16.5, -6.42) * mm});
            skLineSegment(sketch, "E405", {"start": v(16.5, -6.42) * mm, "end": v(16.48, -6.37) * mm});
            skLineSegment(sketch, "E406", {"start": v(16.48, -6.37) * mm, "end": v(16.47, -6.34) * mm});
            skLineSegment(sketch, "E407", {"start": v(16.47, -6.34) * mm, "end": v(16.46, -6.31) * mm});
            skLineSegment(sketch, "E408", {"start": v(16.46, -6.31) * mm, "end": v(16.45, -6.29) * mm});
            skLineSegment(sketch, "E409", {"start": v(16.45, -6.29) * mm, "end": v(16.45, -6.27) * mm});
            skLineSegment(sketch, "E410", {"start": v(16.45, -6.27) * mm, "end": v(16.34, -6.04) * mm});
            skLineSegment(sketch, "E411", {"start": v(16.34, -6.04) * mm, "end": v(16.35, -6.04) * mm});
            skLineSegment(sketch, "E412", {"start": v(16.35, -6.04) * mm, "end": v(16.32, -5.99) * mm});
            skLineSegment(sketch, "E413", {"start": v(16.32, -5.99) * mm, "end": v(16.33, -5.98) * mm});
            skLineSegment(sketch, "E414", {"start": v(16.33, -5.98) * mm, "end": v(16.3, -5.93) * mm});
            skLineSegment(sketch, "E415", {"start": v(16.3, -5.93) * mm, "end": v(16.3, -5.9) * mm});
            skLineSegment(sketch, "E416", {"start": v(16.3, -5.9) * mm, "end": v(16.3, -5.88) * mm});
            skLineSegment(sketch, "E417", {"start": v(16.3, -5.88) * mm, "end": v(16.3, -5.84) * mm});
            skLineSegment(sketch, "E418", {"start": v(16.3, -5.84) * mm, "end": v(16.3, -5.82) * mm});
            skLineSegment(sketch, "E419", {"start": v(16.3, -5.82) * mm, "end": v(16.3, -5.8) * mm});
            skLineSegment(sketch, "E420", {"start": v(16.3, -5.8) * mm, "end": v(16.29, -5.77) * mm});
            skLineSegment(sketch, "E421", {"start": v(16.29, -5.77) * mm, "end": v(16.3, -5.75) * mm});
            skLineSegment(sketch, "E422", {"start": v(16.3, -5.75) * mm, "end": v(16.3, -5.72) * mm});
            skLineSegment(sketch, "E423", {"start": v(16.3, -5.72) * mm, "end": v(16.3, -5.7) * mm});
            skLineSegment(sketch, "E424", {"start": v(16.3, -5.7) * mm, "end": v(16.32, -5.67) * mm});
            skLineSegment(sketch, "E425", {"start": v(16.32, -5.67) * mm, "end": v(16.33, -5.65) * mm});
            skLineSegment(sketch, "E426", {"start": v(16.33, -5.65) * mm, "end": v(16.33, -5.65) * mm});
            skLineSegment(sketch, "E427", {"start": v(16.33, -5.65) * mm, "end": v(16.34, -5.64) * mm});
            skLineSegment(sketch, "E428", {"start": v(16.34, -5.64) * mm, "end": v(16.35, -5.63) * mm});
            skLineSegment(sketch, "E429", {"start": v(16.35, -5.63) * mm, "end": v(16.48, -5.54) * mm});
            skLineSegment(sketch, "E430", {"start": v(16.48, -5.54) * mm, "end": v(16.6, -5.47) * mm});
            skLineSegment(sketch, "E431", {"start": v(16.6, -5.47) * mm, "end": v(16.64, -5.44) * mm});
            skLineSegment(sketch, "E432", {"start": v(16.64, -5.44) * mm, "end": v(16.74, -5.37) * mm});
            skLineSegment(sketch, "E433", {"start": v(16.74, -5.37) * mm, "end": v(16.88, -5.27) * mm});
            skLineSegment(sketch, "E434", {"start": v(16.88, -5.27) * mm, "end": v(16.9, -5.27) * mm});
            skLineSegment(sketch, "E435", {"start": v(16.9, -5.27) * mm, "end": v(16.9, -5.27) * mm});
            skLineSegment(sketch, "E436", {"start": v(16.9, -5.27) * mm, "end": v(16.91, -5.27) * mm});
            skLineSegment(sketch, "E437", {"start": v(16.91, -5.27) * mm, "end": v(16.93, -5.26) * mm});
            skLineSegment(sketch, "E438", {"start": v(16.93, -5.26) * mm, "end": v(16.96, -5.26) * mm});
            skLineSegment(sketch, "E439", {"start": v(16.96, -5.26) * mm, "end": v(16.98, -5.27) * mm});
            skLineSegment(sketch, "E440", {"start": v(16.98, -5.27) * mm, "end": v(17, -5.27) * mm});
            skLineSegment(sketch, "E441", {"start": v(17, -5.27) * mm, "end": v(17.02, -5.28) * mm});
            skLineSegment(sketch, "E442", {"start": v(17.02, -5.28) * mm, "end": v(17.05, -5.3) * mm});
            skLineSegment(sketch, "E443", {"start": v(17.05, -5.3) * mm, "end": v(17.08, -5.3) * mm});
            skLineSegment(sketch, "E444", {"start": v(17.08, -5.3) * mm, "end": v(17.1, -5.32) * mm});
            skLineSegment(sketch, "E445", {"start": v(17.1, -5.32) * mm, "end": v(17.12, -5.33) * mm});
            skLineSegment(sketch, "E446", {"start": v(17.12, -5.33) * mm, "end": v(17.15, -5.36) * mm});
            skLineSegment(sketch, "E447", {"start": v(17.15, -5.36) * mm, "end": v(17.15, -5.35) * mm});
            skLineSegment(sketch, "E448", {"start": v(17.15, -5.35) * mm, "end": v(17.36, -5.56) * mm});
            skLineSegment(sketch, "E449", {"start": v(17.36, -5.56) * mm, "end": v(17.4, -5.6) * mm});
            skLineSegment(sketch, "E450", {"start": v(17.4, -5.6) * mm, "end": v(17.44, -5.63) * mm});
            skLineSegment(sketch, "E451", {"start": v(17.44, -5.63) * mm, "end": v(17.48, -5.67) * mm});
            skLineSegment(sketch, "E452", {"start": v(17.48, -5.67) * mm, "end": v(17.52, -5.7) * mm});
            skLineSegment(sketch, "E453", {"start": v(17.52, -5.7) * mm, "end": v(17.57, -5.74) * mm});
            skLineSegment(sketch, "E454", {"start": v(17.57, -5.74) * mm, "end": v(17.6, -5.78) * mm});
            skLineSegment(sketch, "E455", {"start": v(17.6, -5.78) * mm, "end": v(17.65, -5.81) * mm});
            skLineSegment(sketch, "E456", {"start": v(17.65, -5.81) * mm, "end": v(17.7, -5.85) * mm});
            skLineSegment(sketch, "E457", {"start": v(17.7, -5.85) * mm, "end": v(17.76, -5.9) * mm});
            skLineSegment(sketch, "E458", {"start": v(17.76, -5.9) * mm, "end": v(17.78, -5.92) * mm});
            skLineSegment(sketch, "E459", {"start": v(17.78, -5.92) * mm, "end": v(17.8, -5.93) * mm});
            skLineSegment(sketch, "E460", {"start": v(17.8, -5.93) * mm, "end": v(17.84, -5.96) * mm});
            skLineSegment(sketch, "E461", {"start": v(17.84, -5.96) * mm, "end": v(17.9, -6) * mm});
            skLineSegment(sketch, "E462", {"start": v(17.9, -6) * mm, "end": v(17.96, -6.04) * mm});
            skLineSegment(sketch, "E463", {"start": v(17.96, -6.04) * mm, "end": v(18.02, -6.08) * mm});
            skLineSegment(sketch, "E464", {"start": v(18.02, -6.08) * mm, "end": v(18.08, -6.12) * mm});
            skLineSegment(sketch, "E465", {"start": v(18.08, -6.12) * mm, "end": v(18.16, -6.17) * mm});
            skLineSegment(sketch, "E466", {"start": v(18.16, -6.17) * mm, "end": v(18.24, -6.22) * mm});
            skLineSegment(sketch, "E467", {"start": v(18.24, -6.22) * mm, "end": v(18.31, -6.26) * mm});
            skLineSegment(sketch, "E468", {"start": v(18.31, -6.26) * mm, "end": v(18.4, -6.3) * mm});
            skLineSegment(sketch, "E469", {"start": v(18.4, -6.3) * mm, "end": v(18.48, -6.35) * mm});
            skLineSegment(sketch, "E470", {"start": v(18.48, -6.35) * mm, "end": v(18.58, -6.4) * mm});
            skLineSegment(sketch, "E471", {"start": v(18.58, -6.4) * mm, "end": v(19.07, -6.64) * mm});
            skLineSegment(sketch, "E472", {"start": v(19.07, -6.64) * mm, "end": v(19.07, -6.63) * mm});
            skLineSegment(sketch, "E473", {"start": v(19.07, -6.63) * mm, "end": v(19.14, -6.58) * mm});
            skLineSegment(sketch, "E474", {"start": v(19.14, -6.58) * mm, "end": v(19.2, -6.53) * mm});
            skLineSegment(sketch, "E475", {"start": v(19.2, -6.53) * mm, "end": v(19.27, -6.47) * mm});
            skLineSegment(sketch, "E476", {"start": v(19.27, -6.47) * mm, "end": v(19.33, -6.42) * mm});
            skLineSegment(sketch, "E477", {"start": v(19.33, -6.42) * mm, "end": v(19.4, -6.37) * mm});
            skLineSegment(sketch, "E478", {"start": v(19.4, -6.37) * mm, "end": v(19.45, -6.32) * mm});
            skLineSegment(sketch, "E479", {"start": v(19.45, -6.32) * mm, "end": v(19.51, -6.27) * mm});
            skLineSegment(sketch, "E480", {"start": v(19.51, -6.27) * mm, "end": v(19.57, -6.22) * mm});
            skLineSegment(sketch, "E481", {"start": v(19.57, -6.22) * mm, "end": v(19.63, -6.17) * mm});
            skLineSegment(sketch, "E482", {"start": v(19.63, -6.17) * mm, "end": v(19.65, -6.15) * mm});
            skLineSegment(sketch, "E483", {"start": v(19.65, -6.15) * mm, "end": v(19.49, -5.61) * mm});
            skLineSegment(sketch, "E484", {"start": v(19.49, -5.61) * mm, "end": v(19.46, -5.51) * mm});
            skLineSegment(sketch, "E485", {"start": v(19.46, -5.51) * mm, "end": v(19.43, -5.42) * mm});
            skLineSegment(sketch, "E486", {"start": v(19.43, -5.42) * mm, "end": v(19.4, -5.33) * mm});
            skLineSegment(sketch, "E487", {"start": v(19.4, -5.33) * mm, "end": v(19.36, -5.25) * mm});
            skLineSegment(sketch, "E488", {"start": v(19.36, -5.25) * mm, "end": v(19.33, -5.17) * mm});
            skLineSegment(sketch, "E489", {"start": v(19.33, -5.17) * mm, "end": v(19.3, -5.1) * mm});
            skLineSegment(sketch, "E490", {"start": v(19.3, -5.1) * mm, "end": v(19.27, -5.02) * mm});
            skLineSegment(sketch, "E491", {"start": v(19.27, -5.02) * mm, "end": v(19.24, -4.95) * mm});
            skLineSegment(sketch, "E492", {"start": v(19.24, -4.95) * mm, "end": v(19.21, -4.89) * mm});
            skLineSegment(sketch, "E493", {"start": v(19.21, -4.89) * mm, "end": v(19.18, -4.83) * mm});
            skLineSegment(sketch, "E494", {"start": v(19.18, -4.83) * mm, "end": v(19.16, -4.8) * mm});
            skLineSegment(sketch, "E495", {"start": v(19.16, -4.8) * mm, "end": v(19.14, -4.76) * mm});
            skLineSegment(sketch, "E496", {"start": v(19.14, -4.76) * mm, "end": v(19.12, -4.72) * mm});
            skLineSegment(sketch, "E497", {"start": v(19.12, -4.72) * mm, "end": v(19.1, -4.67) * mm});
            skLineSegment(sketch, "E498", {"start": v(19.1, -4.67) * mm, "end": v(19.07, -4.64) * mm});
            skLineSegment(sketch, "E499", {"start": v(19.07, -4.64) * mm, "end": v(19.05, -4.61) * mm});
            skLineSegment(sketch, "E500", {"start": v(19.05, -4.61) * mm, "end": v(19.03, -4.59) * mm});
            skLineSegment(sketch, "E501", {"start": v(19.03, -4.59) * mm, "end": v(19.03, -4.58) * mm});
            skLineSegment(sketch, "E502", {"start": v(19.03, -4.58) * mm, "end": v(18.86, -4.41) * mm});
            skLineSegment(sketch, "E503", {"start": v(18.86, -4.41) * mm, "end": v(18.86, -4.4) * mm});
            skLineSegment(sketch, "E504", {"start": v(18.86, -4.4) * mm, "end": v(18.8, -4.33) * mm});
            skLineSegment(sketch, "E505", {"start": v(18.8, -4.33) * mm, "end": v(18.8, -4.32) * mm});
            skLineSegment(sketch, "E506", {"start": v(18.8, -4.32) * mm, "end": v(18.74, -4.26) * mm});
            skLineSegment(sketch, "E507", {"start": v(18.74, -4.26) * mm, "end": v(18.75, -4.25) * mm});
            skLineSegment(sketch, "E508", {"start": v(18.75, -4.25) * mm, "end": v(18.7, -4.2) * mm});
            skLineSegment(sketch, "E509", {"start": v(18.7, -4.2) * mm, "end": v(18.7, -4.18) * mm});
            skLineSegment(sketch, "E510", {"start": v(18.7, -4.18) * mm, "end": v(18.67, -4.13) * mm});
            skLineSegment(sketch, "E511", {"start": v(18.67, -4.13) * mm, "end": v(18.68, -4.11) * mm});
            skLineSegment(sketch, "E512", {"start": v(18.68, -4.11) * mm, "end": v(18.64, -4.07) * mm});
            skLineSegment(sketch, "E513", {"start": v(18.64, -4.07) * mm, "end": v(18.66, -4.06) * mm});
            skLineSegment(sketch, "E514", {"start": v(18.66, -4.06) * mm, "end": v(18.63, -4.02) * mm});
            skLineSegment(sketch, "E515", {"start": v(18.63, -4.02) * mm, "end": v(18.64, -4) * mm});
            skLineSegment(sketch, "E516", {"start": v(18.64, -4) * mm, "end": v(18.62, -3.97) * mm});
            skLineSegment(sketch, "E517", {"start": v(18.62, -3.97) * mm, "end": v(18.63, -3.95) * mm});
            skLineSegment(sketch, "E518", {"start": v(18.63, -3.95) * mm, "end": v(18.61, -3.92) * mm});
            skLineSegment(sketch, "E519", {"start": v(18.61, -3.92) * mm, "end": v(18.63, -3.9) * mm});
            skLineSegment(sketch, "E520", {"start": v(18.63, -3.9) * mm, "end": v(18.62, -3.88) * mm});
            skLineSegment(sketch, "E521", {"start": v(18.62, -3.88) * mm, "end": v(18.63, -3.86) * mm});
            skLineSegment(sketch, "E522", {"start": v(18.63, -3.86) * mm, "end": v(18.63, -3.84) * mm});
            skLineSegment(sketch, "E523", {"start": v(18.63, -3.84) * mm, "end": v(18.63, -3.82) * mm});
            skLineSegment(sketch, "E524", {"start": v(18.63, -3.82) * mm, "end": v(18.64, -3.81) * mm});
            skLineSegment(sketch, "E525", {"start": v(18.64, -3.81) * mm, "end": v(18.65, -3.8) * mm});
            skLineSegment(sketch, "E526", {"start": v(18.65, -3.8) * mm, "end": v(18.65, -3.79) * mm});
            skLineSegment(sketch, "E527", {"start": v(18.65, -3.79) * mm, "end": v(18.78, -3.65) * mm});
            skLineSegment(sketch, "E528", {"start": v(18.78, -3.65) * mm, "end": v(18.85, -3.57) * mm});
            skLineSegment(sketch, "E529", {"start": v(18.85, -3.57) * mm, "end": v(18.88, -3.54) * mm});
            skLineSegment(sketch, "E530", {"start": v(18.88, -3.54) * mm, "end": v(18.94, -3.47) * mm});
            skLineSegment(sketch, "E531", {"start": v(18.94, -3.47) * mm, "end": v(19.07, -3.32) * mm});
            skLineSegment(sketch, "E532", {"start": v(19.07, -3.32) * mm, "end": v(19.08, -3.3) * mm});
            skLineSegment(sketch, "E533", {"start": v(19.08, -3.3) * mm, "end": v(19.1, -3.3) * mm});
            skLineSegment(sketch, "E534", {"start": v(19.1, -3.3) * mm, "end": v(19.1, -3.3) * mm});
            skLineSegment(sketch, "E535", {"start": v(19.1, -3.3) * mm, "end": v(19.13, -3.28) * mm});
            skLineSegment(sketch, "E536", {"start": v(19.13, -3.28) * mm, "end": v(19.15, -3.28) * mm});
            skLineSegment(sketch, "E537", {"start": v(19.15, -3.28) * mm, "end": v(19.18, -3.28) * mm});
            skLineSegment(sketch, "E538", {"start": v(19.18, -3.28) * mm, "end": v(19.2, -3.27) * mm});
            skLineSegment(sketch, "E539", {"start": v(19.2, -3.27) * mm, "end": v(19.23, -3.26) * mm});
            skLineSegment(sketch, "E540", {"start": v(19.23, -3.26) * mm, "end": v(19.25, -3.28) * mm});
            skLineSegment(sketch, "E541", {"start": v(19.25, -3.28) * mm, "end": v(19.28, -3.27) * mm});
            skLineSegment(sketch, "E542", {"start": v(19.28, -3.27) * mm, "end": v(19.3, -3.27) * mm});
            skLineSegment(sketch, "E543", {"start": v(19.3, -3.27) * mm, "end": v(19.33, -3.29) * mm});
            skLineSegment(sketch, "E544", {"start": v(19.33, -3.29) * mm, "end": v(19.35, -3.3) * mm});
            skLineSegment(sketch, "E545", {"start": v(19.35, -3.3) * mm, "end": v(19.38, -3.3) * mm});
            skLineSegment(sketch, "E546", {"start": v(19.38, -3.3) * mm, "end": v(19.41, -3.32) * mm});
            skLineSegment(sketch, "E547", {"start": v(19.41, -3.32) * mm, "end": v(19.44, -3.32) * mm});
            skLineSegment(sketch, "E548", {"start": v(19.44, -3.32) * mm, "end": v(19.46, -3.33) * mm});
            skLineSegment(sketch, "E549", {"start": v(19.46, -3.33) * mm, "end": v(19.5, -3.36) * mm});
            skLineSegment(sketch, "E550", {"start": v(19.5, -3.36) * mm, "end": v(19.5, -3.35) * mm});
            skLineSegment(sketch, "E551", {"start": v(19.5, -3.35) * mm, "end": v(19.72, -3.5) * mm});
            skLineSegment(sketch, "E552", {"start": v(19.72, -3.5) * mm, "end": v(19.75, -3.52) * mm});
            skLineSegment(sketch, "E553", {"start": v(19.75, -3.52) * mm, "end": v(19.78, -3.54) * mm});
            skLineSegment(sketch, "E554", {"start": v(19.78, -3.54) * mm, "end": v(19.8, -3.55) * mm});
            skLineSegment(sketch, "E555", {"start": v(19.8, -3.55) * mm, "end": v(19.84, -3.57) * mm});
            skLineSegment(sketch, "E556", {"start": v(19.84, -3.57) * mm, "end": v(19.88, -3.6) * mm});
            skLineSegment(sketch, "E557", {"start": v(19.88, -3.6) * mm, "end": v(19.9, -3.6) * mm});
            skLineSegment(sketch, "E558", {"start": v(19.9, -3.6) * mm, "end": v(19.95, -3.63) * mm});
            skLineSegment(sketch, "E559", {"start": v(19.95, -3.63) * mm, "end": v(20, -3.65) * mm});
            skLineSegment(sketch, "E560", {"start": v(20, -3.65) * mm, "end": v(20.04, -3.67) * mm});
            skLineSegment(sketch, "E561", {"start": v(20.04, -3.67) * mm, "end": v(20.1, -3.7) * mm});
            skLineSegment(sketch, "E562", {"start": v(20.1, -3.7) * mm, "end": v(20.13, -3.7) * mm});
            skLineSegment(sketch, "E563", {"start": v(20.13, -3.7) * mm, "end": v(20.14, -3.71) * mm});
            skLineSegment(sketch, "E564", {"start": v(20.14, -3.71) * mm, "end": v(20.16, -3.72) * mm});
            skLineSegment(sketch, "E565", {"start": v(20.16, -3.72) * mm, "end": v(20.22, -3.74) * mm});
            skLineSegment(sketch, "E566", {"start": v(20.22, -3.74) * mm, "end": v(20.3, -3.77) * mm});
            skLineSegment(sketch, "E567", {"start": v(20.3, -3.77) * mm, "end": v(20.36, -3.79) * mm});
            skLineSegment(sketch, "E568", {"start": v(20.36, -3.79) * mm, "end": v(20.44, -3.81) * mm});
            skLineSegment(sketch, "E569", {"start": v(20.44, -3.81) * mm, "end": v(20.52, -3.83) * mm});
            skLineSegment(sketch, "E570", {"start": v(20.52, -3.83) * mm, "end": v(20.6, -3.85) * mm});
            skLineSegment(sketch, "E571", {"start": v(20.6, -3.85) * mm, "end": v(20.7, -3.87) * mm});
            skLineSegment(sketch, "E572", {"start": v(20.7, -3.87) * mm, "end": v(20.8, -3.89) * mm});
            skLineSegment(sketch, "E573", {"start": v(20.8, -3.89) * mm, "end": v(20.9, -3.9) * mm});
            skLineSegment(sketch, "E574", {"start": v(20.9, -3.9) * mm, "end": v(21.03, -3.92) * mm});
            skLineSegment(sketch, "E575", {"start": v(21.03, -3.92) * mm, "end": v(21.57, -3.95) * mm});
            skLineSegment(sketch, "E576", {"start": v(21.57, -3.95) * mm, "end": v(21.59, -3.93) * mm});
            skLineSegment(sketch, "E577", {"start": v(21.59, -3.93) * mm, "end": v(21.61, -3.9) * mm});
            skLineSegment(sketch, "E578", {"start": v(21.61, -3.9) * mm, "end": v(21.64, -3.85) * mm});
            skLineSegment(sketch, "E579", {"start": v(21.64, -3.85) * mm, "end": v(21.67, -3.8) * mm});
            skLineSegment(sketch, "E580", {"start": v(21.67, -3.8) * mm, "end": v(21.7, -3.77) * mm});
            skLineSegment(sketch, "E581", {"start": v(21.7, -3.77) * mm, "end": v(21.72, -3.73) * mm});
            skLineSegment(sketch, "E582", {"start": v(21.72, -3.73) * mm, "end": v(21.74, -3.69) * mm});
            skLineSegment(sketch, "E583", {"start": v(21.74, -3.69) * mm, "end": v(21.77, -3.65) * mm});
            skLineSegment(sketch, "E584", {"start": v(21.77, -3.65) * mm, "end": v(21.79, -3.6) * mm});
            skLineSegment(sketch, "E585", {"start": v(21.79, -3.6) * mm, "end": v(21.81, -3.56) * mm});
            skLineSegment(sketch, "E586", {"start": v(21.81, -3.56) * mm, "end": v(21.84, -3.52) * mm});
            skLineSegment(sketch, "E587", {"start": v(21.84, -3.52) * mm, "end": v(21.86, -3.48) * mm});
            skLineSegment(sketch, "E588", {"start": v(21.86, -3.48) * mm, "end": v(21.88, -3.44) * mm});
            skLineSegment(sketch, "E589", {"start": v(21.88, -3.44) * mm, "end": v(21.9, -3.4) * mm});
            skLineSegment(sketch, "E590", {"start": v(21.9, -3.4) * mm, "end": v(21.92, -3.37) * mm});
            skLineSegment(sketch, "E591", {"start": v(21.92, -3.37) * mm, "end": v(21.68, -2.97) * mm});
            skLineSegment(sketch, "E592", {"start": v(21.68, -2.97) * mm, "end": v(21.61, -2.88) * mm});
            skLineSegment(sketch, "E593", {"start": v(21.61, -2.88) * mm, "end": v(21.55, -2.78) * mm});
            skLineSegment(sketch, "E594", {"start": v(21.55, -2.78) * mm, "end": v(21.48, -2.7) * mm});
            skLineSegment(sketch, "E595", {"start": v(21.48, -2.7) * mm, "end": v(21.42, -2.62) * mm});
            skLineSegment(sketch, "E596", {"start": v(21.42, -2.62) * mm, "end": v(21.36, -2.55) * mm});
            skLineSegment(sketch, "E597", {"start": v(21.36, -2.55) * mm, "end": v(21.3, -2.48) * mm});
            skLineSegment(sketch, "E598", {"start": v(21.3, -2.48) * mm, "end": v(21.24, -2.42) * mm});
            skLineSegment(sketch, "E599", {"start": v(21.24, -2.42) * mm, "end": v(21.2, -2.37) * mm});
            skLineSegment(sketch, "E600", {"start": v(21.2, -2.37) * mm, "end": v(21.14, -2.32) * mm});
            skLineSegment(sketch, "E601", {"start": v(21.14, -2.32) * mm, "end": v(21.09, -2.28) * mm});
            skLineSegment(sketch, "E602", {"start": v(21.09, -2.28) * mm, "end": v(21.05, -2.24) * mm});
            skLineSegment(sketch, "E603", {"start": v(21.05, -2.24) * mm, "end": v(21.03, -2.23) * mm});
            skLineSegment(sketch, "E604", {"start": v(21.03, -2.23) * mm, "end": v(21.02, -2.22) * mm});
            skLineSegment(sketch, "E605", {"start": v(21.02, -2.22) * mm, "end": v(21, -2.21) * mm});
            skLineSegment(sketch, "E606", {"start": v(21, -2.21) * mm, "end": v(20.97, -2.2) * mm});
            skLineSegment(sketch, "E607", {"start": v(20.97, -2.2) * mm, "end": v(20.96, -2.18) * mm});
            skLineSegment(sketch, "E608", {"start": v(20.96, -2.18) * mm, "end": v(20.89, -2.17) * mm});
            skLineSegment(sketch, "E609", {"start": v(20.89, -2.17) * mm, "end": v(20.88, -2.16) * mm});
            skLineSegment(sketch, "E610", {"start": v(20.88, -2.16) * mm, "end": v(20.77, -2.14) * mm});
            skLineSegment(sketch, "E611", {"start": v(20.77, -2.14) * mm, "end": v(20.77, -2.13) * mm});
            skLineSegment(sketch, "E612", {"start": v(20.77, -2.13) * mm, "end": v(20.66, -2.1) * mm});
            skLineSegment(sketch, "E613", {"start": v(20.66, -2.1) * mm, "end": v(20.66, -2.09) * mm});
            skLineSegment(sketch, "E614", {"start": v(20.66, -2.09) * mm, "end": v(20.56, -2.06) * mm});
            skLineSegment(sketch, "E615", {"start": v(20.56, -2.06) * mm, "end": v(20.56, -2.04) * mm});
            skLineSegment(sketch, "E616", {"start": v(20.56, -2.04) * mm, "end": v(20.47, -2) * mm});
            skLineSegment(sketch, "E617", {"start": v(20.47, -2) * mm, "end": v(20.47, -1.99) * mm});
            skLineSegment(sketch, "E618", {"start": v(20.47, -1.99) * mm, "end": v(20.39, -1.96) * mm});
            skLineSegment(sketch, "E619", {"start": v(20.39, -1.96) * mm, "end": v(20.39, -1.93) * mm});
            skLineSegment(sketch, "E620", {"start": v(20.39, -1.93) * mm, "end": v(20.32, -1.9) * mm});
            skLineSegment(sketch, "E621", {"start": v(20.32, -1.9) * mm, "end": v(20.32, -1.87) * mm});
            skLineSegment(sketch, "E622", {"start": v(20.32, -1.87) * mm, "end": v(20.26, -1.84) * mm});
            skLineSegment(sketch, "E623", {"start": v(20.26, -1.84) * mm, "end": v(20.26, -1.81) * mm});
            skLineSegment(sketch, "E624", {"start": v(20.26, -1.81) * mm, "end": v(20.21, -1.78) * mm});
            skLineSegment(sketch, "E625", {"start": v(20.21, -1.78) * mm, "end": v(20.22, -1.75) * mm});
            skLineSegment(sketch, "E626", {"start": v(20.22, -1.75) * mm, "end": v(20.18, -1.73) * mm});
            skLineSegment(sketch, "E627", {"start": v(20.18, -1.73) * mm, "end": v(20.18, -1.7) * mm});
            skLineSegment(sketch, "E628", {"start": v(20.18, -1.7) * mm, "end": v(20.15, -1.67) * mm});
            skLineSegment(sketch, "E629", {"start": v(20.15, -1.67) * mm, "end": v(20.16, -1.64) * mm});
            skLineSegment(sketch, "E630", {"start": v(20.16, -1.64) * mm, "end": v(20.14, -1.62) * mm});
            skLineSegment(sketch, "E631", {"start": v(20.14, -1.62) * mm, "end": v(20.15, -1.58) * mm});
            skLineSegment(sketch, "E632", {"start": v(20.15, -1.58) * mm, "end": v(20.14, -1.57) * mm});
            skLineSegment(sketch, "E633", {"start": v(20.14, -1.57) * mm, "end": v(20.14, -1.56) * mm});
            skLineSegment(sketch, "E634", {"start": v(20.14, -1.56) * mm, "end": v(20.14, -1.54) * mm});
            skLineSegment(sketch, "E635", {"start": v(20.14, -1.54) * mm, "end": v(20.14, -1.51) * mm});
            skLineSegment(sketch, "E636", {"start": v(20.14, -1.51) * mm, "end": v(20.2, -1.32) * mm});
            skLineSegment(sketch, "E637", {"start": v(20.2, -1.32) * mm, "end": v(20.23, -1.25) * mm});
            skLineSegment(sketch, "E638", {"start": v(20.23, -1.25) * mm, "end": v(20.24, -1.21) * mm});
            skLineSegment(sketch, "E639", {"start": v(20.24, -1.21) * mm, "end": v(20.26, -1.14) * mm});
            skLineSegment(sketch, "E640", {"start": v(20.26, -1.14) * mm, "end": v(20.31, -0.95) * mm});
            skLineSegment(sketch, "E641", {"start": v(20.31, -0.95) * mm, "end": v(20.32, -0.93) * mm});
            skLineSegment(sketch, "E642", {"start": v(20.32, -0.93) * mm, "end": v(20.33, -0.9) * mm});
            skLineSegment(sketch, "E643", {"start": v(20.33, -0.9) * mm, "end": v(20.33, -0.9) * mm});
            skLineSegment(sketch, "E644", {"start": v(20.33, -0.9) * mm, "end": v(20.34, -0.9) * mm});
            skLineSegment(sketch, "E645", {"start": v(20.34, -0.9) * mm, "end": v(20.36, -0.86) * mm});
            skLineSegment(sketch, "E646", {"start": v(20.36, -0.86) * mm, "end": v(20.39, -0.86) * mm});
            skLineSegment(sketch, "E647", {"start": v(20.39, -0.86) * mm, "end": v(20.4, -0.83) * mm});
            skLineSegment(sketch, "E648", {"start": v(20.4, -0.83) * mm, "end": v(20.44, -0.83) * mm});
            skLineSegment(sketch, "E649", {"start": v(20.44, -0.83) * mm, "end": v(20.45, -0.8) * mm});
            skLineSegment(sketch, "E650", {"start": v(20.45, -0.8) * mm, "end": v(20.49, -0.8) * mm});
            skLineSegment(sketch, "E651", {"start": v(20.49, -0.8) * mm, "end": v(20.5, -0.77) * mm});
            skLineSegment(sketch, "E652", {"start": v(20.5, -0.77) * mm, "end": v(20.55, -0.77) * mm});
            skLineSegment(sketch, "E653", {"start": v(20.55, -0.77) * mm, "end": v(20.56, -0.75) * mm});
            skLineSegment(sketch, "E654", {"start": v(20.56, -0.75) * mm, "end": v(20.6, -0.76) * mm});
            skLineSegment(sketch, "E655", {"start": v(20.6, -0.76) * mm, "end": v(20.62, -0.74) * mm});
            skLineSegment(sketch, "E656", {"start": v(20.62, -0.74) * mm, "end": v(20.67, -0.75) * mm});
            skLineSegment(sketch, "E657", {"start": v(20.67, -0.75) * mm, "end": v(20.68, -0.73) * mm});
            skLineSegment(sketch, "E658", {"start": v(20.68, -0.73) * mm, "end": v(20.75, -0.74) * mm});
            skLineSegment(sketch, "E659", {"start": v(20.75, -0.74) * mm, "end": v(20.75, -0.73) * mm});
            skLineSegment(sketch, "E660", {"start": v(20.75, -0.73) * mm, "end": v(20.82, -0.74) * mm});
            skLineSegment(sketch, "E661", {"start": v(20.82, -0.74) * mm, "end": v(20.83, -0.73) * mm});
            skLineSegment(sketch, "E662", {"start": v(20.83, -0.73) * mm, "end": v(20.9, -0.74) * mm});
            skLineSegment(sketch, "E663", {"start": v(20.9, -0.74) * mm, "end": v(20.9, -0.74) * mm});
            skLineSegment(sketch, "E664", {"start": v(20.9, -0.74) * mm, "end": v(20.98, -0.76) * mm});
            skLineSegment(sketch, "E665", {"start": v(20.98, -0.76) * mm, "end": v(20.98, -0.75) * mm});
            skLineSegment(sketch, "E666", {"start": v(20.98, -0.75) * mm, "end": v(21.05, -0.77) * mm});
            skLineSegment(sketch, "E667", {"start": v(21.05, -0.77) * mm, "end": v(21.06, -0.77) * mm});
            skLineSegment(sketch, "E668", {"start": v(21.06, -0.77) * mm, "end": v(21.25, -0.83) * mm});
            skLineSegment(sketch, "E669", {"start": v(21.25, -0.83) * mm, "end": v(21.25, -0.83) * mm});
            skLineSegment(sketch, "E670", {"start": v(21.25, -0.83) * mm, "end": v(21.26, -0.83) * mm});
            skLineSegment(sketch, "E671", {"start": v(21.26, -0.83) * mm, "end": v(21.26, -0.83) * mm});
            skLineSegment(sketch, "E672", {"start": v(21.26, -0.83) * mm, "end": v(21.28, -0.83) * mm});
            skLineSegment(sketch, "E673", {"start": v(21.28, -0.83) * mm, "end": v(21.3, -0.84) * mm});
            skLineSegment(sketch, "E674", {"start": v(21.3, -0.84) * mm, "end": v(21.32, -0.84) * mm});
            skLineSegment(sketch, "E675", {"start": v(21.32, -0.84) * mm, "end": v(21.35, -0.84) * mm});
            skLineSegment(sketch, "E676", {"start": v(21.35, -0.84) * mm, "end": v(21.38, -0.84) * mm});
            skLineSegment(sketch, "E677", {"start": v(21.38, -0.84) * mm, "end": v(21.42, -0.84) * mm});
            skLineSegment(sketch, "E678", {"start": v(21.42, -0.84) * mm, "end": v(21.45, -0.84) * mm});
            skLineSegment(sketch, "E679", {"start": v(21.45, -0.84) * mm, "end": v(21.47, -0.84) * mm});
            skLineSegment(sketch, "E680", {"start": v(21.47, -0.84) * mm, "end": v(21.53, -0.83) * mm});
            skLineSegment(sketch, "E681", {"start": v(21.53, -0.83) * mm, "end": v(21.58, -0.82) * mm});
            skLineSegment(sketch, "E682", {"start": v(21.58, -0.82) * mm, "end": v(21.65, -0.81) * mm});
            skLineSegment(sketch, "E683", {"start": v(21.65, -0.81) * mm, "end": v(21.73, -0.8) * mm});
            skLineSegment(sketch, "E684", {"start": v(21.73, -0.8) * mm, "end": v(21.8, -0.77) * mm});
            skLineSegment(sketch, "E685", {"start": v(21.8, -0.77) * mm, "end": v(21.9, -0.75) * mm});
            skLineSegment(sketch, "E686", {"start": v(21.9, -0.75) * mm, "end": v(22, -0.71) * mm});
            skLineSegment(sketch, "E687", {"start": v(22, -0.71) * mm, "end": v(22.1, -0.67) * mm});
            skLineSegment(sketch, "E688", {"start": v(22.1, -0.67) * mm, "end": v(22.2, -0.62) * mm});
            skLineSegment(sketch, "E689", {"start": v(22.2, -0.62) * mm, "end": v(22.32, -0.57) * mm});
            skLineSegment(sketch, "E690", {"start": v(22.32, -0.57) * mm, "end": v(22.44, -0.5) * mm});
            skLineSegment(sketch, "E691", {"start": v(22.44, -0.5) * mm, "end": v(22.8, -0.29) * mm});
            skLineSegment(sketch, "E692", {"start": v(22.8, -0.29) * mm, "end": v(22.81, -0.26) * mm});
            skLineSegment(sketch, "E693", {"start": v(22.81, -0.26) * mm, "end": v(22.81, -0.22) * mm});
            skLineSegment(sketch, "E694", {"start": v(22.81, -0.22) * mm, "end": v(22.81, -0.19) * mm});
            skLineSegment(sketch, "E695", {"start": v(22.81, -0.19) * mm, "end": v(22.81, -0.15) * mm});
            skLineSegment(sketch, "E696", {"start": v(22.81, -0.15) * mm, "end": v(22.81, -0.12) * mm});
            skLineSegment(sketch, "E697", {"start": v(22.81, -0.12) * mm, "end": v(22.81, -0.08) * mm});
            skLineSegment(sketch, "E698", {"start": v(22.81, -0.08) * mm, "end": v(22.82, -0.05) * mm});
            skLineSegment(sketch, "E699", {"start": v(22.82, -0.05) * mm, "end": v(22.82, -0.01) * mm});
            skLineSegment(sketch, "E700", {"start": v(22.82, -0.01) * mm, "end": v(22.82, 0) * mm});
            skLineSegment(sketch, "E701", {"start": v(22.82, 0) * mm, "end": v(22.82, 0.03) * mm});
            skLineSegment(sketch, "E702", {"start": v(22.82, 0.03) * mm, "end": v(22.81, 0.07) * mm});
            skLineSegment(sketch, "E703", {"start": v(22.81, 0.07) * mm, "end": v(22.81, 0.1) * mm});
            skLineSegment(sketch, "E704", {"start": v(22.81, 0.1) * mm, "end": v(22.81, 0.14) * mm});
            skLineSegment(sketch, "E705", {"start": v(22.81, 0.14) * mm, "end": v(22.81, 0.17) * mm});
            skLineSegment(sketch, "E706", {"start": v(22.81, 0.17) * mm, "end": v(22.81, 0.2) * mm});
            skLineSegment(sketch, "E707", {"start": v(22.81, 0.2) * mm, "end": v(22.81, 0.24) * mm});
            skLineSegment(sketch, "E708", {"start": v(22.81, 0.24) * mm, "end": v(22.8, 0.28) * mm});
            skLineSegment(sketch, "E709", {"start": v(22.8, 0.28) * mm, "end": v(22.8, 0.3) * mm});
            skLineSegment(sketch, "E710", {"start": v(22.8, 0.3) * mm, "end": v(22.44, 0.52) * mm});
            skLineSegment(sketch, "E711", {"start": v(22.44, 0.52) * mm, "end": v(22.32, 0.58) * mm});
            skLineSegment(sketch, "E712", {"start": v(22.32, 0.58) * mm, "end": v(22.2, 0.64) * mm});
            skLineSegment(sketch, "E713", {"start": v(22.2, 0.64) * mm, "end": v(22.1, 0.69) * mm});
            skLineSegment(sketch, "E714", {"start": v(22.1, 0.69) * mm, "end": v(22, 0.73) * mm});
            skLineSegment(sketch, "E715", {"start": v(22, 0.73) * mm, "end": v(21.9, 0.76) * mm});
            skLineSegment(sketch, "E716", {"start": v(21.9, 0.76) * mm, "end": v(21.8, 0.79) * mm});
            skLineSegment(sketch, "E717", {"start": v(21.8, 0.79) * mm, "end": v(21.72, 0.8) * mm});
            skLineSegment(sketch, "E718", {"start": v(21.72, 0.8) * mm, "end": v(21.65, 0.82) * mm});
            skLineSegment(sketch, "E719", {"start": v(21.65, 0.82) * mm, "end": v(21.58, 0.83) * mm});
            skLineSegment(sketch, "E720", {"start": v(21.58, 0.83) * mm, "end": v(21.52, 0.84) * mm});
            skLineSegment(sketch, "E721", {"start": v(21.52, 0.84) * mm, "end": v(21.47, 0.85) * mm});
            skLineSegment(sketch, "E722", {"start": v(21.47, 0.85) * mm, "end": v(21.45, 0.85) * mm});
            skLineSegment(sketch, "E723", {"start": v(21.45, 0.85) * mm, "end": v(21.43, 0.85) * mm});
            skLineSegment(sketch, "E724", {"start": v(21.43, 0.85) * mm, "end": v(21.42, 0.85) * mm});
            skLineSegment(sketch, "E725", {"start": v(21.42, 0.85) * mm, "end": v(21.38, 0.85) * mm});
            skLineSegment(sketch, "E726", {"start": v(21.38, 0.85) * mm, "end": v(21.34, 0.85) * mm});
            skLineSegment(sketch, "E727", {"start": v(21.34, 0.85) * mm, "end": v(21.31, 0.85) * mm});
            skLineSegment(sketch, "E728", {"start": v(21.31, 0.85) * mm, "end": v(21.3, 0.85) * mm});
            skLineSegment(sketch, "E729", {"start": v(21.3, 0.85) * mm, "end": v(21.27, 0.84) * mm});
            skLineSegment(sketch, "E730", {"start": v(21.27, 0.84) * mm, "end": v(21.26, 0.84) * mm});
            skLineSegment(sketch, "E731", {"start": v(21.26, 0.84) * mm, "end": v(21.25, 0.84) * mm});
            skLineSegment(sketch, "E732", {"start": v(21.25, 0.84) * mm, "end": v(21.25, 0.84) * mm});
            skLineSegment(sketch, "E733", {"start": v(21.25, 0.84) * mm, "end": v(21.24, 0.84) * mm});
            skLineSegment(sketch, "E734", {"start": v(21.24, 0.84) * mm, "end": v(21.05, 0.78) * mm});
            skLineSegment(sketch, "E735", {"start": v(21.05, 0.78) * mm, "end": v(21.05, 0.78) * mm});
            skLineSegment(sketch, "E736", {"start": v(21.05, 0.78) * mm, "end": v(20.97, 0.76) * mm});
            skLineSegment(sketch, "E737", {"start": v(20.97, 0.76) * mm, "end": v(20.97, 0.77) * mm});
            skLineSegment(sketch, "E738", {"start": v(20.97, 0.77) * mm, "end": v(20.9, 0.75) * mm});
            skLineSegment(sketch, "E739", {"start": v(20.9, 0.75) * mm, "end": v(20.9, 0.76) * mm});
            skLineSegment(sketch, "E740", {"start": v(20.9, 0.76) * mm, "end": v(20.82, 0.74) * mm});
            skLineSegment(sketch, "E741", {"start": v(20.82, 0.74) * mm, "end": v(20.82, 0.75) * mm});
            skLineSegment(sketch, "E742", {"start": v(20.82, 0.75) * mm, "end": v(20.75, 0.74) * mm});
            skLineSegment(sketch, "E743", {"start": v(20.75, 0.74) * mm, "end": v(20.74, 0.75) * mm});
            skLineSegment(sketch, "E744", {"start": v(20.74, 0.75) * mm, "end": v(20.68, 0.74) * mm});
            skLineSegment(sketch, "E745", {"start": v(20.68, 0.74) * mm, "end": v(20.67, 0.76) * mm});
            skLineSegment(sketch, "E746", {"start": v(20.67, 0.76) * mm, "end": v(20.62, 0.75) * mm});
            skLineSegment(sketch, "E747", {"start": v(20.62, 0.75) * mm, "end": v(20.6, 0.77) * mm});
            skLineSegment(sketch, "E748", {"start": v(20.6, 0.77) * mm, "end": v(20.56, 0.76) * mm});
            skLineSegment(sketch, "E749", {"start": v(20.56, 0.76) * mm, "end": v(20.54, 0.78) * mm});
            skLineSegment(sketch, "E750", {"start": v(20.54, 0.78) * mm, "end": v(20.5, 0.78) * mm});
            skLineSegment(sketch, "E751", {"start": v(20.5, 0.78) * mm, "end": v(20.49, 0.8) * mm});
            skLineSegment(sketch, "E752", {"start": v(20.49, 0.8) * mm, "end": v(20.45, 0.8) * mm});
            skLineSegment(sketch, "E753", {"start": v(20.45, 0.8) * mm, "end": v(20.43, 0.84) * mm});
            skLineSegment(sketch, "E754", {"start": v(20.43, 0.84) * mm, "end": v(20.4, 0.83) * mm});
            skLineSegment(sketch, "E755", {"start": v(20.4, 0.83) * mm, "end": v(20.39, 0.87) * mm});
            skLineSegment(sketch, "E756", {"start": v(20.39, 0.87) * mm, "end": v(20.36, 0.87) * mm});
            skLineSegment(sketch, "E757", {"start": v(20.36, 0.87) * mm, "end": v(20.34, 0.9) * mm});
            skLineSegment(sketch, "E758", {"start": v(20.34, 0.9) * mm, "end": v(20.33, 0.91) * mm});
            skLineSegment(sketch, "E759", {"start": v(20.33, 0.91) * mm, "end": v(20.33, 0.91) * mm});
            skLineSegment(sketch, "E760", {"start": v(20.33, 0.91) * mm, "end": v(20.32, 0.94) * mm});
            skLineSegment(sketch, "E761", {"start": v(20.32, 0.94) * mm, "end": v(20.3, 0.96) * mm});
            skLineSegment(sketch, "E762", {"start": v(20.3, 0.96) * mm, "end": v(20.26, 1.15) * mm});
            skLineSegment(sketch, "E763", {"start": v(20.26, 1.15) * mm, "end": v(20.24, 1.22) * mm});
            skLineSegment(sketch, "E764", {"start": v(20.24, 1.22) * mm, "end": v(20.22, 1.26) * mm});
            skLineSegment(sketch, "E765", {"start": v(20.22, 1.26) * mm, "end": v(20.2, 1.33) * mm});
            skLineSegment(sketch, "E766", {"start": v(20.2, 1.33) * mm, "end": v(20.14, 1.52) * mm});
            skLineSegment(sketch, "E767", {"start": v(20.14, 1.52) * mm, "end": v(20.14, 1.55) * mm});
            skLineSegment(sketch, "E768", {"start": v(20.14, 1.55) * mm, "end": v(20.13, 1.57) * mm});
            skLineSegment(sketch, "E769", {"start": v(20.13, 1.57) * mm, "end": v(20.13, 1.57) * mm});
            skLineSegment(sketch, "E770", {"start": v(20.13, 1.57) * mm, "end": v(20.13, 1.58) * mm});
            skLineSegment(sketch, "E771", {"start": v(20.13, 1.58) * mm, "end": v(20.15, 1.59) * mm});
            skLineSegment(sketch, "E772", {"start": v(20.15, 1.59) * mm, "end": v(20.13, 1.63) * mm});
            skLineSegment(sketch, "E773", {"start": v(20.13, 1.63) * mm, "end": v(20.16, 1.64) * mm});
            skLineSegment(sketch, "E774", {"start": v(20.16, 1.64) * mm, "end": v(20.15, 1.68) * mm});
            skLineSegment(sketch, "E775", {"start": v(20.15, 1.68) * mm, "end": v(20.18, 1.7) * mm});
            skLineSegment(sketch, "E776", {"start": v(20.18, 1.7) * mm, "end": v(20.17, 1.74) * mm});
            skLineSegment(sketch, "E777", {"start": v(20.17, 1.74) * mm, "end": v(20.21, 1.76) * mm});
            skLineSegment(sketch, "E778", {"start": v(20.21, 1.76) * mm, "end": v(20.2, 1.8) * mm});
            skLineSegment(sketch, "E779", {"start": v(20.2, 1.8) * mm, "end": v(20.26, 1.82) * mm});
            skLineSegment(sketch, "E780", {"start": v(20.26, 1.82) * mm, "end": v(20.25, 1.85) * mm});
            skLineSegment(sketch, "E781", {"start": v(20.25, 1.85) * mm, "end": v(20.31, 1.88) * mm});
            skLineSegment(sketch, "E782", {"start": v(20.31, 1.88) * mm, "end": v(20.31, 1.9) * mm});
            skLineSegment(sketch, "E783", {"start": v(20.31, 1.9) * mm, "end": v(20.38, 1.94) * mm});
            skLineSegment(sketch, "E784", {"start": v(20.38, 1.94) * mm, "end": v(20.38, 1.96) * mm});
            skLineSegment(sketch, "E785", {"start": v(20.38, 1.96) * mm, "end": v(20.46, 2) * mm});
            skLineSegment(sketch, "E786", {"start": v(20.46, 2) * mm, "end": v(20.46, 2.02) * mm});
            skLineSegment(sketch, "E787", {"start": v(20.46, 2.02) * mm, "end": v(20.55, 2.05) * mm});
            skLineSegment(sketch, "E788", {"start": v(20.55, 2.05) * mm, "end": v(20.55, 2.07) * mm});
            skLineSegment(sketch, "E789", {"start": v(20.55, 2.07) * mm, "end": v(20.65, 2.1) * mm});
            skLineSegment(sketch, "E790", {"start": v(20.65, 2.1) * mm, "end": v(20.65, 2.11) * mm});
            skLineSegment(sketch, "E791", {"start": v(20.65, 2.11) * mm, "end": v(20.77, 2.14) * mm});
            skLineSegment(sketch, "E792", {"start": v(20.77, 2.14) * mm, "end": v(20.77, 2.15) * mm});
            skLineSegment(sketch, "E793", {"start": v(20.77, 2.15) * mm, "end": v(20.88, 2.17) * mm});
            skLineSegment(sketch, "E794", {"start": v(20.88, 2.17) * mm, "end": v(20.88, 2.18) * mm});
            skLineSegment(sketch, "E795", {"start": v(20.88, 2.18) * mm, "end": v(20.96, 2.2) * mm});
            skLineSegment(sketch, "E796", {"start": v(20.96, 2.2) * mm, "end": v(20.97, 2.2) * mm});
            skLineSegment(sketch, "E797", {"start": v(20.97, 2.2) * mm, "end": v(21, 2.22) * mm});
            skLineSegment(sketch, "E798", {"start": v(21, 2.22) * mm, "end": v(21.03, 2.25) * mm});
            skLineSegment(sketch, "E799", {"start": v(21.03, 2.25) * mm, "end": v(21.04, 2.26) * mm});
            skLineSegment(sketch, "E800", {"start": v(21.04, 2.26) * mm, "end": v(21.09, 2.29) * mm});
            skLineSegment(sketch, "E801", {"start": v(21.09, 2.29) * mm, "end": v(21.13, 2.33) * mm});
            skLineSegment(sketch, "E802", {"start": v(21.13, 2.33) * mm, "end": v(21.18, 2.38) * mm});
            skLineSegment(sketch, "E803", {"start": v(21.18, 2.38) * mm, "end": v(21.24, 2.44) * mm});
            skLineSegment(sketch, "E804", {"start": v(21.24, 2.44) * mm, "end": v(21.3, 2.5) * mm});
            skLineSegment(sketch, "E805", {"start": v(21.3, 2.5) * mm, "end": v(21.35, 2.56) * mm});
            skLineSegment(sketch, "E806", {"start": v(21.35, 2.56) * mm, "end": v(21.42, 2.63) * mm});
            skLineSegment(sketch, "E807", {"start": v(21.42, 2.63) * mm, "end": v(21.48, 2.71) * mm});
            skLineSegment(sketch, "E808", {"start": v(21.48, 2.71) * mm, "end": v(21.54, 2.8) * mm});
            skLineSegment(sketch, "E809", {"start": v(21.54, 2.8) * mm, "end": v(21.6, 2.88) * mm});
            skLineSegment(sketch, "E810", {"start": v(21.6, 2.88) * mm, "end": v(21.66, 2.98) * mm});
            skLineSegment(sketch, "E811", {"start": v(21.66, 2.98) * mm, "end": v(21.92, 3.38) * mm});
            skLineSegment(sketch, "E812", {"start": v(21.92, 3.38) * mm, "end": v(21.91, 3.4) * mm});
            skLineSegment(sketch, "E813", {"start": v(21.91, 3.4) * mm, "end": v(21.89, 3.43) * mm});
            skLineSegment(sketch, "E814", {"start": v(21.89, 3.43) * mm, "end": v(21.87, 3.47) * mm});
            skLineSegment(sketch, "E815", {"start": v(21.87, 3.47) * mm, "end": v(21.84, 3.51) * mm});
            skLineSegment(sketch, "E816", {"start": v(21.84, 3.51) * mm, "end": v(21.82, 3.55) * mm});
            skLineSegment(sketch, "E817", {"start": v(21.82, 3.55) * mm, "end": v(21.8, 3.6) * mm});
            skLineSegment(sketch, "E818", {"start": v(21.8, 3.6) * mm, "end": v(21.77, 3.63) * mm});
            skLineSegment(sketch, "E819", {"start": v(21.77, 3.63) * mm, "end": v(21.75, 3.67) * mm});
            skLineSegment(sketch, "E820", {"start": v(21.75, 3.67) * mm, "end": v(21.72, 3.71) * mm});
            skLineSegment(sketch, "E821", {"start": v(21.72, 3.71) * mm, "end": v(21.7, 3.75) * mm});
            skLineSegment(sketch, "E822", {"start": v(21.7, 3.75) * mm, "end": v(21.67, 3.8) * mm});
            skLineSegment(sketch, "E823", {"start": v(21.67, 3.8) * mm, "end": v(21.65, 3.84) * mm});
            skLineSegment(sketch, "E824", {"start": v(21.65, 3.84) * mm, "end": v(21.62, 3.88) * mm});
            skLineSegment(sketch, "E825", {"start": v(21.62, 3.88) * mm, "end": v(21.6, 3.92) * mm});
            skLineSegment(sketch, "E826", {"start": v(21.6, 3.92) * mm, "end": v(21.57, 3.96) * mm});
            skLineSegment(sketch, "E827", {"start": v(21.57, 3.96) * mm, "end": v(21.57, 3.97) * mm});
            skLineSegment(sketch, "E828", {"start": v(21.57, 3.97) * mm, "end": v(21.02, 3.93) * mm});
            skLineSegment(sketch, "E829", {"start": v(21.02, 3.93) * mm, "end": v(20.9, 3.91) * mm});
            skLineSegment(sketch, "E830", {"start": v(20.9, 3.91) * mm, "end": v(20.8, 3.9) * mm});
            skLineSegment(sketch, "E831", {"start": v(20.8, 3.9) * mm, "end": v(20.7, 3.88) * mm});
            skLineSegment(sketch, "E832", {"start": v(20.7, 3.88) * mm, "end": v(20.6, 3.86) * mm});
            skLineSegment(sketch, "E833", {"start": v(20.6, 3.86) * mm, "end": v(20.51, 3.84) * mm});
            skLineSegment(sketch, "E834", {"start": v(20.51, 3.84) * mm, "end": v(20.43, 3.82) * mm});
            skLineSegment(sketch, "E835", {"start": v(20.43, 3.82) * mm, "end": v(20.35, 3.8) * mm});
            skLineSegment(sketch, "E836", {"start": v(20.35, 3.8) * mm, "end": v(20.28, 3.78) * mm});
            skLineSegment(sketch, "E837", {"start": v(20.28, 3.78) * mm, "end": v(20.22, 3.75) * mm});
            skLineSegment(sketch, "E838", {"start": v(20.22, 3.75) * mm, "end": v(20.16, 3.73) * mm});
            skLineSegment(sketch, "E839", {"start": v(20.16, 3.73) * mm, "end": v(20.12, 3.72) * mm});
            skLineSegment(sketch, "E840", {"start": v(20.12, 3.72) * mm, "end": v(20.09, 3.7) * mm});
            skLineSegment(sketch, "E841", {"start": v(20.09, 3.7) * mm, "end": v(20.03, 3.68) * mm});
            skLineSegment(sketch, "E842", {"start": v(20.03, 3.68) * mm, "end": v(19.99, 3.66) * mm});
            skLineSegment(sketch, "E843", {"start": v(19.99, 3.66) * mm, "end": v(19.94, 3.64) * mm});
            skLineSegment(sketch, "E844", {"start": v(19.94, 3.64) * mm, "end": v(19.9, 3.62) * mm});
            skLineSegment(sketch, "E845", {"start": v(19.9, 3.62) * mm, "end": v(19.87, 3.6) * mm});
            skLineSegment(sketch, "E846", {"start": v(19.87, 3.6) * mm, "end": v(19.83, 3.58) * mm});
            skLineSegment(sketch, "E847", {"start": v(19.83, 3.58) * mm, "end": v(19.8, 3.56) * mm});
            skLineSegment(sketch, "E848", {"start": v(19.8, 3.56) * mm, "end": v(19.77, 3.54) * mm});
            skLineSegment(sketch, "E849", {"start": v(19.77, 3.54) * mm, "end": v(19.74, 3.52) * mm});
            skLineSegment(sketch, "E850", {"start": v(19.74, 3.52) * mm, "end": v(19.71, 3.5) * mm});
            skLineSegment(sketch, "E851", {"start": v(19.71, 3.5) * mm, "end": v(19.5, 3.36) * mm});
            skLineSegment(sketch, "E852", {"start": v(19.5, 3.36) * mm, "end": v(19.5, 3.37) * mm});
            skLineSegment(sketch, "E853", {"start": v(19.5, 3.37) * mm, "end": v(19.46, 3.34) * mm});
            skLineSegment(sketch, "E854", {"start": v(19.46, 3.34) * mm, "end": v(19.45, 3.35) * mm});
            skLineSegment(sketch, "E855", {"start": v(19.45, 3.35) * mm, "end": v(19.41, 3.32) * mm});
            skLineSegment(sketch, "E856", {"start": v(19.41, 3.32) * mm, "end": v(19.4, 3.33) * mm});
            skLineSegment(sketch, "E857", {"start": v(19.4, 3.33) * mm, "end": v(19.37, 3.3) * mm});
            skLineSegment(sketch, "E858", {"start": v(19.37, 3.3) * mm, "end": v(19.36, 3.31) * mm});
            skLineSegment(sketch, "E859", {"start": v(19.36, 3.31) * mm, "end": v(19.33, 3.3) * mm});
            skLineSegment(sketch, "E860", {"start": v(19.33, 3.3) * mm, "end": v(19.32, 3.3) * mm});
            skLineSegment(sketch, "E861", {"start": v(19.32, 3.3) * mm, "end": v(19.3, 3.28) * mm});
            skLineSegment(sketch, "E862", {"start": v(19.3, 3.28) * mm, "end": v(19.28, 3.29) * mm});
            skLineSegment(sketch, "E863", {"start": v(19.28, 3.29) * mm, "end": v(19.26, 3.28) * mm});
            skLineSegment(sketch, "E864", {"start": v(19.26, 3.28) * mm, "end": v(19.24, 3.29) * mm});
            skLineSegment(sketch, "E865", {"start": v(19.24, 3.29) * mm, "end": v(19.22, 3.27) * mm});
            skLineSegment(sketch, "E866", {"start": v(19.22, 3.27) * mm, "end": v(19.2, 3.28) * mm});
            skLineSegment(sketch, "E867", {"start": v(19.2, 3.28) * mm, "end": v(19.17, 3.29) * mm});
            skLineSegment(sketch, "E868", {"start": v(19.17, 3.29) * mm, "end": v(19.15, 3.28) * mm});
            skLineSegment(sketch, "E869", {"start": v(19.15, 3.28) * mm, "end": v(19.14, 3.3) * mm});
            skLineSegment(sketch, "E870", {"start": v(19.14, 3.3) * mm, "end": v(19.12, 3.29) * mm});
            skLineSegment(sketch, "E871", {"start": v(19.12, 3.29) * mm, "end": v(19.1, 3.3) * mm});
            skLineSegment(sketch, "E872", {"start": v(19.1, 3.3) * mm, "end": v(19.09, 3.3) * mm});
            skLineSegment(sketch, "E873", {"start": v(19.09, 3.3) * mm, "end": v(19.09, 3.3) * mm});
            skLineSegment(sketch, "E874", {"start": v(19.09, 3.3) * mm, "end": v(19.07, 3.33) * mm});
            skLineSegment(sketch, "E875", {"start": v(19.07, 3.33) * mm, "end": v(19.06, 3.33) * mm});
            skLineSegment(sketch, "E876", {"start": v(19.06, 3.33) * mm, "end": v(18.94, 3.48) * mm});
            skLineSegment(sketch, "E877", {"start": v(18.94, 3.48) * mm, "end": v(18.87, 3.55) * mm});
            skLineSegment(sketch, "E878", {"start": v(18.87, 3.55) * mm, "end": v(18.84, 3.58) * mm});
            skLineSegment(sketch, "E879", {"start": v(18.84, 3.58) * mm, "end": v(18.78, 3.66) * mm});
            skLineSegment(sketch, "E880", {"start": v(18.78, 3.66) * mm, "end": v(18.65, 3.8) * mm});
            skLineSegment(sketch, "E881", {"start": v(18.65, 3.8) * mm, "end": v(18.64, 3.8) * mm});
            skLineSegment(sketch, "E882", {"start": v(18.64, 3.8) * mm, "end": v(18.63, 3.82) * mm});
            skLineSegment(sketch, "E883", {"start": v(18.63, 3.82) * mm, "end": v(18.63, 3.82) * mm});
            skLineSegment(sketch, "E884", {"start": v(18.63, 3.82) * mm, "end": v(18.63, 3.83) * mm});
            skLineSegment(sketch, "E885", {"start": v(18.63, 3.83) * mm, "end": v(18.61, 3.85) * mm});
            skLineSegment(sketch, "E886", {"start": v(18.61, 3.85) * mm, "end": v(18.62, 3.87) * mm});
            skLineSegment(sketch, "E887", {"start": v(18.62, 3.87) * mm, "end": v(18.6, 3.89) * mm});
            skLineSegment(sketch, "E888", {"start": v(18.6, 3.89) * mm, "end": v(18.62, 3.91) * mm});
            skLineSegment(sketch, "E889", {"start": v(18.62, 3.91) * mm, "end": v(18.6, 3.93) * mm});
            skLineSegment(sketch, "E890", {"start": v(18.6, 3.93) * mm, "end": v(18.62, 3.96) * mm});
            skLineSegment(sketch, "E891", {"start": v(18.62, 3.96) * mm, "end": v(18.6, 3.97) * mm});
            skLineSegment(sketch, "E892", {"start": v(18.6, 3.97) * mm, "end": v(18.63, 4) * mm});
            skLineSegment(sketch, "E893", {"start": v(18.63, 4) * mm, "end": v(18.62, 4.02) * mm});
            skLineSegment(sketch, "E894", {"start": v(18.62, 4.02) * mm, "end": v(18.65, 4.06) * mm});
            skLineSegment(sketch, "E895", {"start": v(18.65, 4.06) * mm, "end": v(18.64, 4.08) * mm});
            skLineSegment(sketch, "E896", {"start": v(18.64, 4.08) * mm, "end": v(18.67, 4.12) * mm});
            skLineSegment(sketch, "E897", {"start": v(18.67, 4.12) * mm, "end": v(18.66, 4.14) * mm});
            skLineSegment(sketch, "E898", {"start": v(18.66, 4.14) * mm, "end": v(18.7, 4.19) * mm});
            skLineSegment(sketch, "E899", {"start": v(18.7, 4.19) * mm, "end": v(18.7, 4.2) * mm});
            skLineSegment(sketch, "E900", {"start": v(18.7, 4.2) * mm, "end": v(18.74, 4.26) * mm});
            skLineSegment(sketch, "E901", {"start": v(18.74, 4.26) * mm, "end": v(18.73, 4.27) * mm});
            skLineSegment(sketch, "E902", {"start": v(18.73, 4.27) * mm, "end": v(18.8, 4.33) * mm});
            skLineSegment(sketch, "E903", {"start": v(18.8, 4.33) * mm, "end": v(18.79, 4.34) * mm});
            skLineSegment(sketch, "E904", {"start": v(18.79, 4.34) * mm, "end": v(18.85, 4.41) * mm});
            skLineSegment(sketch, "E905", {"start": v(18.85, 4.41) * mm, "end": v(18.85, 4.42) * mm});
            skLineSegment(sketch, "E906", {"start": v(18.85, 4.42) * mm, "end": v(19.02, 4.58) * mm});
            skLineSegment(sketch, "E907", {"start": v(19.02, 4.58) * mm, "end": v(19.02, 4.58) * mm});
            skLineSegment(sketch, "E908", {"start": v(19.02, 4.58) * mm, "end": v(19.03, 4.6) * mm});
            skLineSegment(sketch, "E909", {"start": v(19.03, 4.6) * mm, "end": v(19.04, 4.62) * mm});
            skLineSegment(sketch, "E910", {"start": v(19.04, 4.62) * mm, "end": v(19.06, 4.65) * mm});
            skLineSegment(sketch, "E911", {"start": v(19.06, 4.65) * mm, "end": v(19.08, 4.68) * mm});
            skLineSegment(sketch, "E912", {"start": v(19.08, 4.68) * mm, "end": v(19.11, 4.72) * mm});
            skLineSegment(sketch, "E913", {"start": v(19.11, 4.72) * mm, "end": v(19.13, 4.77) * mm});
            skLineSegment(sketch, "E914", {"start": v(19.13, 4.77) * mm, "end": v(19.15, 4.8) * mm});
            skLineSegment(sketch, "E915", {"start": v(19.15, 4.8) * mm, "end": v(19.16, 4.8) * mm});
            skLineSegment(sketch, "E916", {"start": v(19.16, 4.8) * mm, "end": v(19.17, 4.83) * mm});
            skLineSegment(sketch, "E917", {"start": v(19.17, 4.83) * mm, "end": v(19.2, 4.9) * mm});
            skLineSegment(sketch, "E918", {"start": v(19.2, 4.9) * mm, "end": v(19.23, 4.96) * mm});
            skLineSegment(sketch, "E919", {"start": v(19.23, 4.96) * mm, "end": v(19.26, 5.03) * mm});
            skLineSegment(sketch, "E920", {"start": v(19.26, 5.03) * mm, "end": v(19.3, 5.1) * mm});
            skLineSegment(sketch, "E921", {"start": v(19.3, 5.1) * mm, "end": v(19.33, 5.18) * mm});
            skLineSegment(sketch, "E922", {"start": v(19.33, 5.18) * mm, "end": v(19.36, 5.26) * mm});
            skLineSegment(sketch, "E923", {"start": v(19.36, 5.26) * mm, "end": v(19.39, 5.34) * mm});
            skLineSegment(sketch, "E924", {"start": v(19.39, 5.34) * mm, "end": v(19.42, 5.43) * mm});
            skLineSegment(sketch, "E925", {"start": v(19.42, 5.43) * mm, "end": v(19.45, 5.52) * mm});
            skLineSegment(sketch, "E926", {"start": v(19.45, 5.52) * mm, "end": v(19.48, 5.63) * mm});
            skLineSegment(sketch, "E927", {"start": v(19.48, 5.63) * mm, "end": v(19.64, 6.16) * mm});
            skLineSegment(sketch, "E928", {"start": v(19.64, 6.16) * mm, "end": v(19.6, 6.2) * mm});
            skLineSegment(sketch, "E929", {"start": v(19.6, 6.2) * mm, "end": v(19.53, 6.25) * mm});
            skLineSegment(sketch, "E930", {"start": v(19.53, 6.25) * mm, "end": v(19.47, 6.3) * mm});
            skLineSegment(sketch, "E931", {"start": v(19.47, 6.3) * mm, "end": v(19.41, 6.35) * mm});
            skLineSegment(sketch, "E932", {"start": v(19.41, 6.35) * mm, "end": v(19.35, 6.4) * mm});
            skLineSegment(sketch, "E933", {"start": v(19.35, 6.4) * mm, "end": v(19.29, 6.46) * mm});
            skLineSegment(sketch, "E934", {"start": v(19.29, 6.46) * mm, "end": v(19.23, 6.5) * mm});
            skLineSegment(sketch, "E935", {"start": v(19.23, 6.5) * mm, "end": v(19.16, 6.56) * mm});
            skLineSegment(sketch, "E936", {"start": v(19.16, 6.56) * mm, "end": v(19.1, 6.62) * mm});
            skLineSegment(sketch, "E937", {"start": v(19.1, 6.62) * mm, "end": v(19.06, 6.64) * mm});
            skLineSegment(sketch, "E938", {"start": v(19.06, 6.64) * mm, "end": v(18.57, 6.4) * mm});
            skLineSegment(sketch, "E939", {"start": v(18.57, 6.4) * mm, "end": v(18.47, 6.36) * mm});
            skLineSegment(sketch, "E940", {"start": v(18.47, 6.36) * mm, "end": v(18.38, 6.31) * mm});
            skLineSegment(sketch, "E941", {"start": v(18.38, 6.31) * mm, "end": v(18.3, 6.27) * mm});
            skLineSegment(sketch, "E942", {"start": v(18.3, 6.27) * mm, "end": v(18.23, 6.23) * mm});
            skLineSegment(sketch, "E943", {"start": v(18.23, 6.23) * mm, "end": v(18.15, 6.18) * mm});
            skLineSegment(sketch, "E944", {"start": v(18.15, 6.18) * mm, "end": v(18.08, 6.13) * mm});
            skLineSegment(sketch, "E945", {"start": v(18.08, 6.13) * mm, "end": v(18, 6.09) * mm});
            skLineSegment(sketch, "E946", {"start": v(18, 6.09) * mm, "end": v(17.95, 6.05) * mm});
            skLineSegment(sketch, "E947", {"start": v(17.95, 6.05) * mm, "end": v(17.89, 6) * mm});
            skLineSegment(sketch, "E948", {"start": v(17.89, 6) * mm, "end": v(17.83, 5.96) * mm});
            skLineSegment(sketch, "E949", {"start": v(17.83, 5.96) * mm, "end": v(17.8, 5.94) * mm});
            skLineSegment(sketch, "E950", {"start": v(17.8, 5.94) * mm, "end": v(17.78, 5.92) * mm});
            skLineSegment(sketch, "E951", {"start": v(17.78, 5.92) * mm, "end": v(17.75, 5.9) * mm});
            skLineSegment(sketch, "E952", {"start": v(17.75, 5.9) * mm, "end": v(17.7, 5.86) * mm});
            skLineSegment(sketch, "E953", {"start": v(17.7, 5.86) * mm, "end": v(17.64, 5.82) * mm});
            skLineSegment(sketch, "E954", {"start": v(17.64, 5.82) * mm, "end": v(17.6, 5.79) * mm});
            skLineSegment(sketch, "E955", {"start": v(17.6, 5.79) * mm, "end": v(17.56, 5.75) * mm});
            skLineSegment(sketch, "E956", {"start": v(17.56, 5.75) * mm, "end": v(17.5, 5.7) * mm});
            skLineSegment(sketch, "E957", {"start": v(17.5, 5.7) * mm, "end": v(17.47, 5.68) * mm});
            skLineSegment(sketch, "E958", {"start": v(17.47, 5.68) * mm, "end": v(17.43, 5.64) * mm});
            skLineSegment(sketch, "E959", {"start": v(17.43, 5.64) * mm, "end": v(17.39, 5.6) * mm});
            skLineSegment(sketch, "E960", {"start": v(17.39, 5.6) * mm, "end": v(17.35, 5.56) * mm});
            skLineSegment(sketch, "E961", {"start": v(17.35, 5.56) * mm, "end": v(17.14, 5.36) * mm});
            skLineSegment(sketch, "E962", {"start": v(17.14, 5.36) * mm, "end": v(17.14, 5.36) * mm});
            skLineSegment(sketch, "E963", {"start": v(17.14, 5.36) * mm, "end": v(17.1, 5.34) * mm});
            skLineSegment(sketch, "E964", {"start": v(17.1, 5.34) * mm, "end": v(17.1, 5.34) * mm});
            skLineSegment(sketch, "E965", {"start": v(17.1, 5.34) * mm, "end": v(17.08, 5.32) * mm});
            skLineSegment(sketch, "E966", {"start": v(17.08, 5.32) * mm, "end": v(17.08, 5.32) * mm});
            skLineSegment(sketch, "E967", {"start": v(17.08, 5.32) * mm, "end": v(17.05, 5.3) * mm});
            skLineSegment(sketch, "E968", {"start": v(17.05, 5.3) * mm, "end": v(17.05, 5.3) * mm});
            skLineSegment(sketch, "E969", {"start": v(17.05, 5.3) * mm, "end": v(17.03, 5.3) * mm});
            skLineSegment(sketch, "E970", {"start": v(17.03, 5.3) * mm, "end": v(17, 5.28) * mm});
            skLineSegment(sketch, "E971", {"start": v(17, 5.28) * mm, "end": v(16.98, 5.27) * mm});
            skLineSegment(sketch, "E972", {"start": v(16.98, 5.27) * mm, "end": v(16.96, 5.27) * mm});
            skLineSegment(sketch, "E973", {"start": v(16.96, 5.27) * mm, "end": v(16.94, 5.27) * mm});
            skLineSegment(sketch, "E974", {"start": v(16.94, 5.27) * mm, "end": v(16.92, 5.27) * mm});
            skLineSegment(sketch, "E975", {"start": v(16.92, 5.27) * mm, "end": v(16.9, 5.27) * mm});
            skLineSegment(sketch, "E976", {"start": v(16.9, 5.27) * mm, "end": v(16.9, 5.27) * mm});
            skLineSegment(sketch, "E977", {"start": v(16.9, 5.27) * mm, "end": v(16.88, 5.28) * mm});
            skLineSegment(sketch, "E978", {"start": v(16.88, 5.28) * mm, "end": v(16.87, 5.28) * mm});
            skLineSegment(sketch, "E979", {"start": v(16.87, 5.28) * mm, "end": v(16.74, 5.38) * mm});
            skLineSegment(sketch, "E980", {"start": v(16.74, 5.38) * mm, "end": v(16.63, 5.45) * mm});
            skLineSegment(sketch, "E981", {"start": v(16.63, 5.45) * mm, "end": v(16.58, 5.48) * mm});
            skLineSegment(sketch, "E982", {"start": v(16.58, 5.48) * mm, "end": v(16.47, 5.55) * mm});
            skLineSegment(sketch, "E983", {"start": v(16.47, 5.55) * mm, "end": v(16.34, 5.64) * mm});
            skLineSegment(sketch, "E984", {"start": v(16.34, 5.64) * mm, "end": v(16.33, 5.64) * mm});
            skLineSegment(sketch, "E985", {"start": v(16.33, 5.64) * mm, "end": v(16.32, 5.65) * mm});
            skLineSegment(sketch, "E986", {"start": v(16.32, 5.65) * mm, "end": v(16.32, 5.65) * mm});
            skLineSegment(sketch, "E987", {"start": v(16.32, 5.65) * mm, "end": v(16.32, 5.66) * mm});
            skLineSegment(sketch, "E988", {"start": v(16.32, 5.66) * mm, "end": v(16.3, 5.68) * mm});
            skLineSegment(sketch, "E989", {"start": v(16.3, 5.68) * mm, "end": v(16.3, 5.7) * mm});
            skLineSegment(sketch, "E990", {"start": v(16.3, 5.7) * mm, "end": v(16.29, 5.72) * mm});
            skLineSegment(sketch, "E991", {"start": v(16.29, 5.72) * mm, "end": v(16.29, 5.75) * mm});
            skLineSegment(sketch, "E992", {"start": v(16.29, 5.75) * mm, "end": v(16.28, 5.77) * mm});
            skLineSegment(sketch, "E993", {"start": v(16.28, 5.77) * mm, "end": v(16.29, 5.8) * mm});
            skLineSegment(sketch, "E994", {"start": v(16.29, 5.8) * mm, "end": v(16.28, 5.83) * mm});
            skLineSegment(sketch, "E995", {"start": v(16.28, 5.83) * mm, "end": v(16.28, 5.85) * mm});
            skLineSegment(sketch, "E996", {"start": v(16.28, 5.85) * mm, "end": v(16.3, 5.89) * mm});
            skLineSegment(sketch, "E997", {"start": v(16.3, 5.89) * mm, "end": v(16.3, 5.91) * mm});
            skLineSegment(sketch, "E998", {"start": v(16.3, 5.91) * mm, "end": v(16.3, 5.94) * mm});
            skLineSegment(sketch, "E999", {"start": v(16.3, 5.94) * mm, "end": v(16.32, 5.99) * mm});
            skLineSegment(sketch, "E1000", {"start": v(16.32, 5.99) * mm, "end": v(16.31, 6) * mm});
            skLineSegment(sketch, "E1001", {"start": v(16.31, 6) * mm, "end": v(16.34, 6.05) * mm});
            skLineSegment(sketch, "E1002", {"start": v(16.34, 6.05) * mm, "end": v(16.33, 6.05) * mm});
            skLineSegment(sketch, "E1003", {"start": v(16.33, 6.05) * mm, "end": v(16.43, 6.28) * mm});
            skLineSegment(sketch, "E1004", {"start": v(16.43, 6.28) * mm, "end": v(16.44, 6.3) * mm});
            skLineSegment(sketch, "E1005", {"start": v(16.44, 6.3) * mm, "end": v(16.45, 6.32) * mm});
            skLineSegment(sketch, "E1006", {"start": v(16.45, 6.32) * mm, "end": v(16.46, 6.34) * mm});
            skLineSegment(sketch, "E1007", {"start": v(16.46, 6.34) * mm, "end": v(16.48, 6.38) * mm});
            skLineSegment(sketch, "E1008", {"start": v(16.48, 6.38) * mm, "end": v(16.49, 6.42) * mm});
            skLineSegment(sketch, "E1009", {"start": v(16.49, 6.42) * mm, "end": v(16.5, 6.47) * mm});
            skLineSegment(sketch, "E1010", {"start": v(16.5, 6.47) * mm, "end": v(16.52, 6.51) * mm});
            skLineSegment(sketch, "E1011", {"start": v(16.52, 6.51) * mm, "end": v(16.53, 6.57) * mm});
            skLineSegment(sketch, "E1012", {"start": v(16.53, 6.57) * mm, "end": v(16.55, 6.63) * mm});
            skLineSegment(sketch, "E1013", {"start": v(16.55, 6.63) * mm, "end": v(16.56, 6.68) * mm});
            skLineSegment(sketch, "E1014", {"start": v(16.56, 6.68) * mm, "end": v(16.57, 6.72) * mm});
            skLineSegment(sketch, "E1015", {"start": v(16.57, 6.72) * mm, "end": v(16.58, 6.74) * mm});
            skLineSegment(sketch, "E1016", {"start": v(16.58, 6.74) * mm, "end": v(16.59, 6.79) * mm});
            skLineSegment(sketch, "E1017", {"start": v(16.59, 6.79) * mm, "end": v(16.6, 6.86) * mm});
            skLineSegment(sketch, "E1018", {"start": v(16.6, 6.86) * mm, "end": v(16.62, 6.93) * mm});
            skLineSegment(sketch, "E1019", {"start": v(16.62, 6.93) * mm, "end": v(16.64, 7.01) * mm});
            skLineSegment(sketch, "E1020", {"start": v(16.64, 7.01) * mm, "end": v(16.65, 7.1) * mm});
            skLineSegment(sketch, "E1021", {"start": v(16.65, 7.1) * mm, "end": v(16.66, 7.17) * mm});
            skLineSegment(sketch, "E1022", {"start": v(16.66, 7.17) * mm, "end": v(16.68, 7.26) * mm});
            skLineSegment(sketch, "E1023", {"start": v(16.68, 7.26) * mm, "end": v(16.7, 7.35) * mm});
            skLineSegment(sketch, "E1024", {"start": v(16.7, 7.35) * mm, "end": v(16.7, 7.45) * mm});
            skLineSegment(sketch, "E1025", {"start": v(16.7, 7.45) * mm, "end": v(16.72, 7.56) * mm});
            skLineSegment(sketch, "E1026", {"start": v(16.72, 7.56) * mm, "end": v(16.78, 8.16) * mm});
            skLineSegment(sketch, "E1027", {"start": v(16.78, 8.16) * mm, "end": v(16.7, 8.2) * mm});
            skLineSegment(sketch, "E1028", {"start": v(16.7, 8.2) * mm, "end": v(16.6, 8.27) * mm});
            skLineSegment(sketch, "E1029", {"start": v(16.6, 8.27) * mm, "end": v(16.48, 8.33) * mm});
            skLineSegment(sketch, "E1030", {"start": v(16.48, 8.33) * mm, "end": v(16.37, 8.39) * mm});
            skLineSegment(sketch, "E1031", {"start": v(16.37, 8.39) * mm, "end": v(16.25, 8.45) * mm});
            skLineSegment(sketch, "E1032", {"start": v(16.25, 8.45) * mm, "end": v(16.13, 8.51) * mm});
            skLineSegment(sketch, "E1033", {"start": v(16.13, 8.51) * mm, "end": v(16.09, 8.53) * mm});
            skLineSegment(sketch, "E1034", {"start": v(16.09, 8.53) * mm, "end": v(15.69, 8.21) * mm});
            skLineSegment(sketch, "E1035", {"start": v(15.69, 8.21) * mm, "end": v(15.61, 8.15) * mm});
            skLineSegment(sketch, "E1036", {"start": v(15.61, 8.15) * mm, "end": v(15.54, 8.1) * mm});
            skLineSegment(sketch, "E1037", {"start": v(15.54, 8.1) * mm, "end": v(15.47, 8.03) * mm});
            skLineSegment(sketch, "E1038", {"start": v(15.47, 8.03) * mm, "end": v(15.4, 7.97) * mm});
            skLineSegment(sketch, "E1039", {"start": v(15.4, 7.97) * mm, "end": v(15.33, 7.9) * mm});
            skLineSegment(sketch, "E1040", {"start": v(15.33, 7.9) * mm, "end": v(15.26, 7.84) * mm});
            skLineSegment(sketch, "E1041", {"start": v(15.26, 7.84) * mm, "end": v(15.2, 7.78) * mm});
            skLineSegment(sketch, "E1042", {"start": v(15.2, 7.78) * mm, "end": v(15.13, 7.72) * mm});
            skLineSegment(sketch, "E1043", {"start": v(15.13, 7.72) * mm, "end": v(15.09, 7.67) * mm});
            skLineSegment(sketch, "E1044", {"start": v(15.09, 7.67) * mm, "end": v(15.03, 7.62) * mm});
            skLineSegment(sketch, "E1045", {"start": v(15.03, 7.62) * mm, "end": v(15, 7.6) * mm});
            skLineSegment(sketch, "E1046", {"start": v(15, 7.6) * mm, "end": v(14.99, 7.57) * mm});
            skLineSegment(sketch, "E1047", {"start": v(14.99, 7.57) * mm, "end": v(14.95, 7.54) * mm});
            skLineSegment(sketch, "E1048", {"start": v(14.95, 7.54) * mm, "end": v(14.9, 7.5) * mm});
            skLineSegment(sketch, "E1049", {"start": v(14.9, 7.5) * mm, "end": v(14.86, 7.44) * mm});
            skLineSegment(sketch, "E1050", {"start": v(14.86, 7.44) * mm, "end": v(14.8, 7.38) * mm});
            skLineSegment(sketch, "E1051", {"start": v(14.8, 7.38) * mm, "end": v(14.77, 7.33) * mm});
            skLineSegment(sketch, "E1052", {"start": v(14.77, 7.33) * mm, "end": v(14.72, 7.28) * mm});
            skLineSegment(sketch, "E1053", {"start": v(14.72, 7.28) * mm, "end": v(14.68, 7.23) * mm});
            skLineSegment(sketch, "E1054", {"start": v(14.68, 7.23) * mm, "end": v(14.63, 7.17) * mm});
            skLineSegment(sketch, "E1055", {"start": v(14.63, 7.17) * mm, "end": v(14.59, 7.12) * mm});
            skLineSegment(sketch, "E1056", {"start": v(14.59, 7.12) * mm, "end": v(14.55, 7.07) * mm});
            skLineSegment(sketch, "E1057", {"start": v(14.55, 7.07) * mm, "end": v(14.4, 6.9) * mm});
            skLineSegment(sketch, "E1058", {"start": v(14.4, 6.9) * mm, "end": v(14.4, 6.9) * mm});
            skLineSegment(sketch, "E1059", {"start": v(14.4, 6.9) * mm, "end": v(14.38, 6.87) * mm});
            skLineSegment(sketch, "E1060", {"start": v(14.38, 6.87) * mm, "end": v(14.38, 6.87) * mm});
            skLineSegment(sketch, "E1061", {"start": v(14.38, 6.87) * mm, "end": v(14.36, 6.85) * mm});
            skLineSegment(sketch, "E1062", {"start": v(14.36, 6.85) * mm, "end": v(14.34, 6.83) * mm});
            skLineSegment(sketch, "E1063", {"start": v(14.34, 6.83) * mm, "end": v(14.32, 6.82) * mm});
            skLineSegment(sketch, "E1064", {"start": v(14.32, 6.82) * mm, "end": v(14.3, 6.8) * mm});
            skLineSegment(sketch, "E1065", {"start": v(14.3, 6.8) * mm, "end": v(14.28, 6.8) * mm});
            skLineSegment(sketch, "E1066", {"start": v(14.28, 6.8) * mm, "end": v(14.27, 6.79) * mm});
            skLineSegment(sketch, "E1067", {"start": v(14.27, 6.79) * mm, "end": v(14.25, 6.78) * mm});
            skLineSegment(sketch, "E1068", {"start": v(14.25, 6.78) * mm, "end": v(14.24, 6.78) * mm});
            skLineSegment(sketch, "E1069", {"start": v(14.24, 6.78) * mm, "end": v(14.23, 6.78) * mm});
            skLineSegment(sketch, "E1070", {"start": v(14.23, 6.78) * mm, "end": v(14.22, 6.78) * mm});
            skLineSegment(sketch, "E1071", {"start": v(14.22, 6.78) * mm, "end": v(14.22, 6.78) * mm});
            skLineSegment(sketch, "E1072", {"start": v(14.22, 6.78) * mm, "end": v(14.2, 6.79) * mm});
            skLineSegment(sketch, "E1073", {"start": v(14.2, 6.79) * mm, "end": v(14.2, 6.79) * mm});
            skLineSegment(sketch, "E1074", {"start": v(14.2, 6.79) * mm, "end": v(14.07, 6.85) * mm});
            skLineSegment(sketch, "E1075", {"start": v(14.07, 6.85) * mm, "end": v(13.95, 6.9) * mm});
            skLineSegment(sketch, "E1076", {"start": v(13.95, 6.9) * mm, "end": v(13.86, 6.94) * mm});
            skLineSegment(sketch, "E1077", {"start": v(13.86, 6.94) * mm, "end": v(13.74, 7) * mm});
            skLineSegment(sketch, "E1078", {"start": v(13.74, 7) * mm, "end": v(13.6, 7.05) * mm});
            skLineSegment(sketch, "E1079", {"start": v(13.6, 7.05) * mm, "end": v(13.6, 7.06) * mm});
            skLineSegment(sketch, "E1080", {"start": v(13.6, 7.06) * mm, "end": v(13.6, 7.06) * mm});
            skLineSegment(sketch, "E1081", {"start": v(13.6, 7.06) * mm, "end": v(13.59, 7.07) * mm});
            skLineSegment(sketch, "E1082", {"start": v(13.59, 7.07) * mm, "end": v(13.58, 7.08) * mm});
            skLineSegment(sketch, "E1083", {"start": v(13.58, 7.08) * mm, "end": v(13.57, 7.1) * mm});
            skLineSegment(sketch, "E1084", {"start": v(13.57, 7.1) * mm, "end": v(13.56, 7.1) * mm});
            skLineSegment(sketch, "E1085", {"start": v(13.56, 7.1) * mm, "end": v(13.56, 7.13) * mm});
            skLineSegment(sketch, "E1086", {"start": v(13.56, 7.13) * mm, "end": v(13.55, 7.16) * mm});
            skLineSegment(sketch, "E1087", {"start": v(13.55, 7.16) * mm, "end": v(13.55, 7.18) * mm});
            skLineSegment(sketch, "E1088", {"start": v(13.55, 7.18) * mm, "end": v(13.54, 7.21) * mm});
            skLineSegment(sketch, "E1089", {"start": v(13.54, 7.21) * mm, "end": v(13.54, 7.25) * mm});
            skLineSegment(sketch, "E1090", {"start": v(13.54, 7.25) * mm, "end": v(13.55, 7.28) * mm});
            skLineSegment(sketch, "E1091", {"start": v(13.55, 7.28) * mm, "end": v(13.54, 7.3) * mm});
            skLineSegment(sketch, "E1092", {"start": v(13.54, 7.3) * mm, "end": v(13.55, 7.34) * mm});
            skLineSegment(sketch, "E1093", {"start": v(13.55, 7.34) * mm, "end": v(13.55, 7.34) * mm});
            skLineSegment(sketch, "E1094", {"start": v(13.55, 7.34) * mm, "end": v(13.6, 7.56) * mm});
            skLineSegment(sketch, "E1095", {"start": v(13.6, 7.56) * mm, "end": v(13.6, 7.59) * mm});
            skLineSegment(sketch, "E1096", {"start": v(13.6, 7.59) * mm, "end": v(13.6, 7.63) * mm});
            skLineSegment(sketch, "E1097", {"start": v(13.6, 7.63) * mm, "end": v(13.62, 7.68) * mm});
            skLineSegment(sketch, "E1098", {"start": v(13.62, 7.68) * mm, "end": v(13.62, 7.73) * mm});
            skLineSegment(sketch, "E1099", {"start": v(13.62, 7.73) * mm, "end": v(13.63, 7.79) * mm});
            skLineSegment(sketch, "E1100", {"start": v(13.63, 7.79) * mm, "end": v(13.64, 7.86) * mm});
            skLineSegment(sketch, "E1101", {"start": v(13.64, 7.86) * mm, "end": v(13.65, 7.92) * mm});
            skLineSegment(sketch, "E1102", {"start": v(13.65, 7.92) * mm, "end": v(13.65, 7.99) * mm});
            skLineSegment(sketch, "E1103", {"start": v(13.65, 7.99) * mm, "end": v(13.66, 8.05) * mm});
            skLineSegment(sketch, "E1104", {"start": v(13.66, 8.05) * mm, "end": v(13.66, 8.12) * mm});
            skLineSegment(sketch, "E1105", {"start": v(13.66, 8.12) * mm, "end": v(13.67, 8.16) * mm});
            skLineSegment(sketch, "E1106", {"start": v(13.67, 8.16) * mm, "end": v(13.67, 8.19) * mm});
            skLineSegment(sketch, "E1107", {"start": v(13.67, 8.19) * mm, "end": v(13.67, 8.23) * mm});
            skLineSegment(sketch, "E1108", {"start": v(13.67, 8.23) * mm, "end": v(13.68, 8.31) * mm});
            skLineSegment(sketch, "E1109", {"start": v(13.68, 8.31) * mm, "end": v(13.68, 8.39) * mm});
            skLineSegment(sketch, "E1110", {"start": v(13.68, 8.39) * mm, "end": v(13.68, 8.47) * mm});
            skLineSegment(sketch, "E1111", {"start": v(13.68, 8.47) * mm, "end": v(13.69, 8.56) * mm});
            skLineSegment(sketch, "E1112", {"start": v(13.69, 8.56) * mm, "end": v(13.69, 8.66) * mm});
            skLineSegment(sketch, "E1113", {"start": v(13.69, 8.66) * mm, "end": v(13.69, 8.75) * mm});
            skLineSegment(sketch, "E1114", {"start": v(13.69, 8.75) * mm, "end": v(13.69, 8.86) * mm});
            skLineSegment(sketch, "E1115", {"start": v(13.69, 8.86) * mm, "end": v(13.69, 8.97) * mm});
            skLineSegment(sketch, "E1116", {"start": v(13.69, 8.97) * mm, "end": v(13.68, 9.08) * mm});
            skLineSegment(sketch, "E1117", {"start": v(13.68, 9.08) * mm, "end": v(13.67, 9.62) * mm});
            skLineSegment(sketch, "E1118", {"start": v(13.67, 9.62) * mm, "end": v(13.55, 9.66) * mm});
            skLineSegment(sketch, "E1119", {"start": v(13.55, 9.66) * mm, "end": v(13.38, 9.73) * mm});
            skLineSegment(sketch, "E1120", {"start": v(13.38, 9.73) * mm, "end": v(13.2, 9.8) * mm});
            skLineSegment(sketch, "E1121", {"start": v(13.2, 9.8) * mm, "end": v(13.02, 9.86) * mm});
            skLineSegment(sketch, "E1122", {"start": v(13.02, 9.86) * mm, "end": v(12.92, 9.9) * mm});
            skLineSegment(sketch, "E1123", {"start": v(12.92, 9.9) * mm, "end": v(12.54, 9.48) * mm});
            skLineSegment(sketch, "E1124", {"start": v(12.54, 9.48) * mm, "end": v(12.47, 9.4) * mm});
            skLineSegment(sketch, "E1125", {"start": v(12.47, 9.4) * mm, "end": v(12.4, 9.33) * mm});
            skLineSegment(sketch, "E1126", {"start": v(12.4, 9.33) * mm, "end": v(12.34, 9.26) * mm});
            skLineSegment(sketch, "E1127", {"start": v(12.34, 9.26) * mm, "end": v(12.28, 9.18) * mm});
            skLineSegment(sketch, "E1128", {"start": v(12.28, 9.18) * mm, "end": v(12.21, 9.1) * mm});
            skLineSegment(sketch, "E1129", {"start": v(12.21, 9.1) * mm, "end": v(12.15, 9.02) * mm});
            skLineSegment(sketch, "E1130", {"start": v(12.15, 9.02) * mm, "end": v(12.09, 8.95) * mm});
            skLineSegment(sketch, "E1131", {"start": v(12.09, 8.95) * mm, "end": v(12.03, 8.87) * mm});
            skLineSegment(sketch, "E1132", {"start": v(12.03, 8.87) * mm, "end": v(11.98, 8.8) * mm});
            skLineSegment(sketch, "E1133", {"start": v(11.98, 8.8) * mm, "end": v(11.97, 8.78) * mm});
            skLineSegment(sketch, "E1134", {"start": v(11.97, 8.78) * mm, "end": v(11.93, 8.74) * mm});
            skLineSegment(sketch, "E1135", {"start": v(11.93, 8.74) * mm, "end": v(11.9, 8.7) * mm});
            skLineSegment(sketch, "E1136", {"start": v(11.9, 8.7) * mm, "end": v(11.86, 8.64) * mm});
            skLineSegment(sketch, "E1137", {"start": v(11.86, 8.64) * mm, "end": v(11.81, 8.57) * mm});
            skLineSegment(sketch, "E1138", {"start": v(11.81, 8.57) * mm, "end": v(11.78, 8.53) * mm});
            skLineSegment(sketch, "E1139", {"start": v(11.78, 8.53) * mm, "end": v(11.74, 8.47) * mm});
            skLineSegment(sketch, "E1140", {"start": v(11.74, 8.47) * mm, "end": v(11.7, 8.41) * mm});
            skLineSegment(sketch, "E1141", {"start": v(11.7, 8.41) * mm, "end": v(11.66, 8.36) * mm});
            skLineSegment(sketch, "E1142", {"start": v(11.66, 8.36) * mm, "end": v(11.63, 8.3) * mm});
            skLineSegment(sketch, "E1143", {"start": v(11.63, 8.3) * mm, "end": v(11.59, 8.25) * mm});
            skLineSegment(sketch, "E1144", {"start": v(11.59, 8.25) * mm, "end": v(11.43, 8) * mm});
            skLineSegment(sketch, "E1145", {"start": v(11.43, 8) * mm, "end": v(11.43, 8) * mm});
            skLineSegment(sketch, "E1146", {"start": v(11.43, 8) * mm, "end": v(11.41, 7.98) * mm});
            skLineSegment(sketch, "E1147", {"start": v(11.41, 7.98) * mm, "end": v(11.4, 7.96) * mm});
            skLineSegment(sketch, "E1148", {"start": v(11.4, 7.96) * mm, "end": v(11.39, 7.95) * mm});
            skLineSegment(sketch, "E1149", {"start": v(11.39, 7.95) * mm, "end": v(11.37, 7.94) * mm});
            skLineSegment(sketch, "E1150", {"start": v(11.37, 7.94) * mm, "end": v(11.36, 7.93) * mm});
            skLineSegment(sketch, "E1151", {"start": v(11.36, 7.93) * mm, "end": v(11.35, 7.92) * mm});
            skLineSegment(sketch, "E1152", {"start": v(11.35, 7.92) * mm, "end": v(11.34, 7.92) * mm});
            skLineSegment(sketch, "E1153", {"start": v(11.34, 7.92) * mm, "end": v(11.33, 7.91) * mm});
            skLineSegment(sketch, "E1154", {"start": v(11.33, 7.91) * mm, "end": v(11.32, 7.91) * mm});
            skLineSegment(sketch, "E1155", {"start": v(11.32, 7.91) * mm, "end": v(11.3, 7.9) * mm});
            skLineSegment(sketch, "E1156", {"start": v(11.3, 7.9) * mm, "end": v(11.3, 7.9) * mm});
            skLineSegment(sketch, "E1157", {"start": v(11.3, 7.9) * mm, "end": v(11.29, 7.91) * mm});
            skLineSegment(sketch, "E1158", {"start": v(11.29, 7.91) * mm, "end": v(11.29, 7.91) * mm});
            skLineSegment(sketch, "E1159", {"start": v(11.29, 7.91) * mm, "end": v(11.21, 7.94) * mm});
            skLineSegment(sketch, "E1160", {"start": v(11.21, 7.94) * mm, "end": v(11.02, 8) * mm});
            skLineSegment(sketch, "E1161", {"start": v(11.02, 8) * mm, "end": v(10.92, 8.03) * mm});
            skLineSegment(sketch, "E1162", {"start": v(10.92, 8.03) * mm, "end": v(10.77, 8.07) * mm});
            skLineSegment(sketch, "E1163", {"start": v(10.77, 8.07) * mm, "end": v(10.66, 8.1) * mm});
            skLineSegment(sketch, "E1164", {"start": v(10.66, 8.1) * mm, "end": v(10.65, 8.1) * mm});
            skLineSegment(sketch, "E1165", {"start": v(10.65, 8.1) * mm, "end": v(10.65, 8.11) * mm});
            skLineSegment(sketch, "E1166", {"start": v(10.65, 8.11) * mm, "end": v(10.64, 8.11) * mm});
            skLineSegment(sketch, "E1167", {"start": v(10.64, 8.11) * mm, "end": v(10.64, 8.12) * mm});
            skLineSegment(sketch, "E1168", {"start": v(10.64, 8.12) * mm, "end": v(10.63, 8.13) * mm});
            skLineSegment(sketch, "E1169", {"start": v(10.63, 8.13) * mm, "end": v(10.62, 8.14) * mm});
            skLineSegment(sketch, "E1170", {"start": v(10.62, 8.14) * mm, "end": v(10.6, 8.16) * mm});
            skLineSegment(sketch, "E1171", {"start": v(10.6, 8.16) * mm, "end": v(10.6, 8.18) * mm});
            skLineSegment(sketch, "E1172", {"start": v(10.6, 8.18) * mm, "end": v(10.6, 8.2) * mm});
            skLineSegment(sketch, "E1173", {"start": v(10.6, 8.2) * mm, "end": v(10.6, 8.23) * mm});
            skLineSegment(sketch, "E1174", {"start": v(10.6, 8.23) * mm, "end": v(10.59, 8.26) * mm});
            skLineSegment(sketch, "E1175", {"start": v(10.59, 8.26) * mm, "end": v(10.59, 8.29) * mm});
            skLineSegment(sketch, "E1176", {"start": v(10.59, 8.29) * mm, "end": v(10.58, 8.3) * mm});
            skLineSegment(sketch, "E1177", {"start": v(10.58, 8.3) * mm, "end": v(10.6, 8.55) * mm});
            skLineSegment(sketch, "E1178", {"start": v(10.6, 8.55) * mm, "end": v(10.6, 8.6) * mm});
            skLineSegment(sketch, "E1179", {"start": v(10.6, 8.6) * mm, "end": v(10.6, 8.66) * mm});
            skLineSegment(sketch, "E1180", {"start": v(10.6, 8.66) * mm, "end": v(10.6, 8.73) * mm});
            skLineSegment(sketch, "E1181", {"start": v(10.6, 8.73) * mm, "end": v(10.6, 8.8) * mm});
            skLineSegment(sketch, "E1182", {"start": v(10.6, 8.8) * mm, "end": v(10.6, 8.88) * mm});
            skLineSegment(sketch, "E1183", {"start": v(10.6, 8.88) * mm, "end": v(10.6, 8.96) * mm});
            skLineSegment(sketch, "E1184", {"start": v(10.6, 8.96) * mm, "end": v(10.6, 9.04) * mm});
            skLineSegment(sketch, "E1185", {"start": v(10.6, 9.04) * mm, "end": v(10.59, 9.14) * mm});
            skLineSegment(sketch, "E1186", {"start": v(10.59, 9.14) * mm, "end": v(10.59, 9.22) * mm});
            skLineSegment(sketch, "E1187", {"start": v(10.59, 9.22) * mm, "end": v(10.58, 9.24) * mm});
            skLineSegment(sketch, "E1188", {"start": v(10.58, 9.24) * mm, "end": v(10.58, 9.3) * mm});
            skLineSegment(sketch, "E1189", {"start": v(10.58, 9.3) * mm, "end": v(10.58, 9.36) * mm});
            skLineSegment(sketch, "E1190", {"start": v(10.58, 9.36) * mm, "end": v(10.57, 9.44) * mm});
            skLineSegment(sketch, "E1191", {"start": v(10.57, 9.44) * mm, "end": v(10.57, 9.52) * mm});
            skLineSegment(sketch, "E1192", {"start": v(10.57, 9.52) * mm, "end": v(10.56, 9.6) * mm});
            skLineSegment(sketch, "E1193", {"start": v(10.56, 9.6) * mm, "end": v(10.55, 9.68) * mm});
            skLineSegment(sketch, "E1194", {"start": v(10.55, 9.68) * mm, "end": v(10.54, 9.76) * mm});
            skLineSegment(sketch, "E1195", {"start": v(10.54, 9.76) * mm, "end": v(10.53, 9.85) * mm});
            skLineSegment(sketch, "E1196", {"start": v(10.53, 9.85) * mm, "end": v(10.52, 9.95) * mm});
            skLineSegment(sketch, "E1197", {"start": v(10.52, 9.95) * mm, "end": v(10.51, 10.04) * mm});
            skLineSegment(sketch, "E1198", {"start": v(10.51, 10.04) * mm, "end": v(10.43, 10.66) * mm});
            skLineSegment(sketch, "E1199", {"start": v(10.43, 10.66) * mm, "end": v(10.3, 10.7) * mm});
            skLineSegment(sketch, "E1200", {"start": v(10.3, 10.7) * mm, "end": v(10.06, 10.75) * mm});
            skLineSegment(sketch, "E1201", {"start": v(10.06, 10.75) * mm, "end": v(9.82, 10.81) * mm});
            skLineSegment(sketch, "E1202", {"start": v(9.82, 10.81) * mm, "end": v(9.65, 10.85) * mm});
            skLineSegment(sketch, "E1203", {"start": v(9.65, 10.85) * mm, "end": v(9.32, 10.4) * mm});
            skLineSegment(sketch, "E1204", {"start": v(9.32, 10.4) * mm, "end": v(9.27, 10.33) * mm});
            skLineSegment(sketch, "E1205", {"start": v(9.27, 10.33) * mm, "end": v(9.22, 10.26) * mm});
            skLineSegment(sketch, "E1206", {"start": v(9.22, 10.26) * mm, "end": v(9.17, 10.19) * mm});
            skLineSegment(sketch, "E1207", {"start": v(9.17, 10.19) * mm, "end": v(9.12, 10.11) * mm});
            skLineSegment(sketch, "E1208", {"start": v(9.12, 10.11) * mm, "end": v(9.07, 10.04) * mm});
            skLineSegment(sketch, "E1209", {"start": v(9.07, 10.04) * mm, "end": v(9.02, 9.96) * mm});
            skLineSegment(sketch, "E1210", {"start": v(9.02, 9.96) * mm, "end": v(8.97, 9.9) * mm});
            skLineSegment(sketch, "E1211", {"start": v(8.97, 9.9) * mm, "end": v(8.92, 9.81) * mm});
            skLineSegment(sketch, "E1212", {"start": v(8.92, 9.81) * mm, "end": v(8.88, 9.74) * mm});
            skLineSegment(sketch, "E1213", {"start": v(8.88, 9.74) * mm, "end": v(8.85, 9.7) * mm});
            skLineSegment(sketch, "E1214", {"start": v(8.85, 9.7) * mm, "end": v(8.81, 9.64) * mm});
            skLineSegment(sketch, "E1215", {"start": v(8.81, 9.64) * mm, "end": v(8.78, 9.59) * mm});
            skLineSegment(sketch, "E1216", {"start": v(8.78, 9.59) * mm, "end": v(8.74, 9.52) * mm});
            skLineSegment(sketch, "E1217", {"start": v(8.74, 9.52) * mm, "end": v(8.7, 9.44) * mm});
            skLineSegment(sketch, "E1218", {"start": v(8.7, 9.44) * mm, "end": v(8.65, 9.36) * mm});
            skLineSegment(sketch, "E1219", {"start": v(8.65, 9.36) * mm, "end": v(8.6, 9.28) * mm});
            skLineSegment(sketch, "E1220", {"start": v(8.6, 9.28) * mm, "end": v(8.56, 9.2) * mm});
            skLineSegment(sketch, "E1221", {"start": v(8.56, 9.2) * mm, "end": v(8.52, 9.13) * mm});
            skLineSegment(sketch, "E1222", {"start": v(8.52, 9.13) * mm, "end": v(8.48, 9.06) * mm});
            skLineSegment(sketch, "E1223", {"start": v(8.48, 9.06) * mm, "end": v(8.35, 8.8) * mm});
            skLineSegment(sketch, "E1224", {"start": v(8.35, 8.8) * mm, "end": v(8.35, 8.8) * mm});
            skLineSegment(sketch, "E1225", {"start": v(8.35, 8.8) * mm, "end": v(8.34, 8.79) * mm});
            skLineSegment(sketch, "E1226", {"start": v(8.34, 8.79) * mm, "end": v(8.32, 8.77) * mm});
            skLineSegment(sketch, "E1227", {"start": v(8.32, 8.77) * mm, "end": v(8.3, 8.75) * mm});
            skLineSegment(sketch, "E1228", {"start": v(8.3, 8.75) * mm, "end": v(8.3, 8.74) * mm});
            skLineSegment(sketch, "E1229", {"start": v(8.3, 8.74) * mm, "end": v(8.28, 8.73) * mm});
            skLineSegment(sketch, "E1230", {"start": v(8.28, 8.73) * mm, "end": v(8.27, 8.72) * mm});
            skLineSegment(sketch, "E1231", {"start": v(8.27, 8.72) * mm, "end": v(8.26, 8.72) * mm});
            skLineSegment(sketch, "E1232", {"start": v(8.26, 8.72) * mm, "end": v(8.25, 8.72) * mm});
            skLineSegment(sketch, "E1233", {"start": v(8.25, 8.72) * mm, "end": v(8.25, 8.72) * mm});
            skLineSegment(sketch, "E1234", {"start": v(8.25, 8.72) * mm, "end": v(8.24, 8.72) * mm});
            skLineSegment(sketch, "E1235", {"start": v(8.24, 8.72) * mm, "end": v(8.23, 8.72) * mm});
            skLineSegment(sketch, "E1236", {"start": v(8.23, 8.72) * mm, "end": v(8.23, 8.72) * mm});
            skLineSegment(sketch, "E1237", {"start": v(8.23, 8.72) * mm, "end": v(8.17, 8.73) * mm});
            skLineSegment(sketch, "E1238", {"start": v(8.17, 8.73) * mm, "end": v(7.98, 8.77) * mm});
            skLineSegment(sketch, "E1239", {"start": v(7.98, 8.77) * mm, "end": v(7.84, 8.8) * mm});
            skLineSegment(sketch, "E1240", {"start": v(7.84, 8.8) * mm, "end": v(7.64, 8.84) * mm});
            skLineSegment(sketch, "E1241", {"start": v(7.64, 8.84) * mm, "end": v(7.58, 8.85) * mm});
            skLineSegment(sketch, "E1242", {"start": v(7.58, 8.85) * mm, "end": v(7.58, 8.85) * mm});
            skLineSegment(sketch, "E1243", {"start": v(7.58, 8.85) * mm, "end": v(7.57, 8.85) * mm});
            skLineSegment(sketch, "E1244", {"start": v(7.57, 8.85) * mm, "end": v(7.57, 8.85) * mm});
            skLineSegment(sketch, "E1245", {"start": v(7.57, 8.85) * mm, "end": v(7.57, 8.86) * mm});
            skLineSegment(sketch, "E1246", {"start": v(7.57, 8.86) * mm, "end": v(7.56, 8.87) * mm});
            skLineSegment(sketch, "E1247", {"start": v(7.56, 8.87) * mm, "end": v(7.55, 8.88) * mm});
            skLineSegment(sketch, "E1248", {"start": v(7.55, 8.88) * mm, "end": v(7.54, 8.89) * mm});
            skLineSegment(sketch, "E1249", {"start": v(7.54, 8.89) * mm, "end": v(7.53, 8.9) * mm});
            skLineSegment(sketch, "E1250", {"start": v(7.53, 8.9) * mm, "end": v(7.53, 8.91) * mm});
            skLineSegment(sketch, "E1251", {"start": v(7.53, 8.91) * mm, "end": v(7.52, 8.93) * mm});
            skLineSegment(sketch, "E1252", {"start": v(7.52, 8.93) * mm, "end": v(7.52, 8.95) * mm});
            skLineSegment(sketch, "E1253", {"start": v(7.52, 8.95) * mm, "end": v(7.51, 8.97) * mm});
            skLineSegment(sketch, "E1254", {"start": v(7.51, 8.97) * mm, "end": v(7.5, 9) * mm});
            skLineSegment(sketch, "E1255", {"start": v(7.5, 9) * mm, "end": v(7.5, 9) * mm});
            skLineSegment(sketch, "E1256", {"start": v(7.5, 9) * mm, "end": v(7.49, 9.24) * mm});
            skLineSegment(sketch, "E1257", {"start": v(7.49, 9.24) * mm, "end": v(7.48, 9.3) * mm});
            skLineSegment(sketch, "E1258", {"start": v(7.48, 9.3) * mm, "end": v(7.48, 9.35) * mm});
            skLineSegment(sketch, "E1259", {"start": v(7.48, 9.35) * mm, "end": v(7.47, 9.42) * mm});
            skLineSegment(sketch, "E1260", {"start": v(7.47, 9.42) * mm, "end": v(7.46, 9.5) * mm});
            skLineSegment(sketch, "E1261", {"start": v(7.46, 9.5) * mm, "end": v(7.46, 9.55) * mm});
            skLineSegment(sketch, "E1262", {"start": v(7.46, 9.55) * mm, "end": v(7.45, 9.63) * mm});
            skLineSegment(sketch, "E1263", {"start": v(7.45, 9.63) * mm, "end": v(7.44, 9.7) * mm});
            skLineSegment(sketch, "E1264", {"start": v(7.44, 9.7) * mm, "end": v(7.43, 9.79) * mm});
            skLineSegment(sketch, "E1265", {"start": v(7.43, 9.79) * mm, "end": v(7.42, 9.86) * mm});
            skLineSegment(sketch, "E1266", {"start": v(7.42, 9.86) * mm, "end": v(7.4, 9.94) * mm});
            skLineSegment(sketch, "E1267", {"start": v(7.4, 9.94) * mm, "end": v(7.4, 9.98) * mm});
            skLineSegment(sketch, "E1268", {"start": v(7.4, 9.98) * mm, "end": v(7.4, 10.04) * mm});
            skLineSegment(sketch, "E1269", {"start": v(7.4, 10.04) * mm, "end": v(7.38, 10.13) * mm});
            skLineSegment(sketch, "E1270", {"start": v(7.38, 10.13) * mm, "end": v(7.36, 10.23) * mm});
            skLineSegment(sketch, "E1271", {"start": v(7.36, 10.23) * mm, "end": v(7.34, 10.33) * mm});
            skLineSegment(sketch, "E1272", {"start": v(7.34, 10.33) * mm, "end": v(7.32, 10.44) * mm});
            skLineSegment(sketch, "E1273", {"start": v(7.32, 10.44) * mm, "end": v(7.3, 10.54) * mm});
            skLineSegment(sketch, "E1274", {"start": v(7.3, 10.54) * mm, "end": v(7.28, 10.66) * mm});
            skLineSegment(sketch, "E1275", {"start": v(7.28, 10.66) * mm, "end": v(7.25, 10.78) * mm});
            skLineSegment(sketch, "E1276", {"start": v(7.25, 10.78) * mm, "end": v(7.13, 11.37) * mm});
            skLineSegment(sketch, "E1277", {"start": v(7.13, 11.37) * mm, "end": v(7.04, 11.38) * mm});
            skLineSegment(sketch, "E1278", {"start": v(7.04, 11.38) * mm, "end": v(6.73, 11.43) * mm});
            skLineSegment(sketch, "E1279", {"start": v(6.73, 11.43) * mm, "end": v(6.41, 11.48) * mm});
            skLineSegment(sketch, "E1280", {"start": v(6.41, 11.48) * mm, "end": v(6.32, 11.5) * mm});
            skLineSegment(sketch, "E1281", {"start": v(6.32, 11.5) * mm, "end": v(6.04, 11.02) * mm});
            skLineSegment(sketch, "E1282", {"start": v(6.04, 11.02) * mm, "end": v(5.98, 10.92) * mm});
            skLineSegment(sketch, "E1283", {"start": v(5.98, 10.92) * mm, "end": v(5.93, 10.82) * mm});
            skLineSegment(sketch, "E1284", {"start": v(5.93, 10.82) * mm, "end": v(5.87, 10.73) * mm});
            skLineSegment(sketch, "E1285", {"start": v(5.87, 10.73) * mm, "end": v(5.82, 10.63) * mm});
            skLineSegment(sketch, "E1286", {"start": v(5.82, 10.63) * mm, "end": v(5.77, 10.53) * mm});
            skLineSegment(sketch, "E1287", {"start": v(5.77, 10.53) * mm, "end": v(5.71, 10.43) * mm});
            skLineSegment(sketch, "E1288", {"start": v(5.71, 10.43) * mm, "end": v(5.66, 10.34) * mm});
            skLineSegment(sketch, "E1289", {"start": v(5.66, 10.34) * mm, "end": v(5.62, 10.26) * mm});
            skLineSegment(sketch, "E1290", {"start": v(5.62, 10.26) * mm, "end": v(5.6, 10.2) * mm});
            skLineSegment(sketch, "E1291", {"start": v(5.6, 10.2) * mm, "end": v(5.56, 10.14) * mm});
            skLineSegment(sketch, "E1292", {"start": v(5.56, 10.14) * mm, "end": v(5.51, 10.04) * mm});
            skLineSegment(sketch, "E1293", {"start": v(5.51, 10.04) * mm, "end": v(5.47, 9.94) * mm});
            skLineSegment(sketch, "E1294", {"start": v(5.47, 9.94) * mm, "end": v(5.42, 9.84) * mm});
            skLineSegment(sketch, "E1295", {"start": v(5.42, 9.84) * mm, "end": v(5.38, 9.74) * mm});
            skLineSegment(sketch, "E1296", {"start": v(5.38, 9.74) * mm, "end": v(5.34, 9.65) * mm});
            skLineSegment(sketch, "E1297", {"start": v(5.34, 9.65) * mm, "end": v(5.3, 9.55) * mm});
            skLineSegment(sketch, "E1298", {"start": v(5.3, 9.55) * mm, "end": v(5.2, 9.35) * mm});
            skLineSegment(sketch, "E1299", {"start": v(5.2, 9.35) * mm, "end": v(5.2, 9.35) * mm});
            skLineSegment(sketch, "E1300", {"start": v(5.2, 9.35) * mm, "end": v(5.2, 9.32) * mm});
            skLineSegment(sketch, "E1301", {"start": v(5.2, 9.32) * mm, "end": v(5.18, 9.3) * mm});
            skLineSegment(sketch, "E1302", {"start": v(5.18, 9.3) * mm, "end": v(5.17, 9.28) * mm});
            skLineSegment(sketch, "E1303", {"start": v(5.17, 9.28) * mm, "end": v(5.15, 9.27) * mm});
            skLineSegment(sketch, "E1304", {"start": v(5.15, 9.27) * mm, "end": v(5.14, 9.26) * mm});
            skLineSegment(sketch, "E1305", {"start": v(5.14, 9.26) * mm, "end": v(5.13, 9.25) * mm});
            skLineSegment(sketch, "E1306", {"start": v(5.13, 9.25) * mm, "end": v(5.12, 9.24) * mm});
            skLineSegment(sketch, "E1307", {"start": v(5.12, 9.24) * mm, "end": v(5.11, 9.24) * mm});
            skLineSegment(sketch, "E1308", {"start": v(5.11, 9.24) * mm, "end": v(5.1, 9.24) * mm});
            skLineSegment(sketch, "E1309", {"start": v(5.1, 9.24) * mm, "end": v(4.85, 9.27) * mm});
            skLineSegment(sketch, "E1310", {"start": v(4.85, 9.27) * mm, "end": v(4.69, 9.3) * mm});
            skLineSegment(sketch, "E1311", {"start": v(4.69, 9.3) * mm, "end": v(4.43, 9.32) * mm});
            skLineSegment(sketch, "E1312", {"start": v(4.43, 9.32) * mm, "end": v(4.43, 9.32) * mm});
            skLineSegment(sketch, "E1313", {"start": v(4.43, 9.32) * mm, "end": v(4.42, 9.33) * mm});
            skLineSegment(sketch, "E1314", {"start": v(4.42, 9.33) * mm, "end": v(4.41, 9.34) * mm});
            skLineSegment(sketch, "E1315", {"start": v(4.41, 9.34) * mm, "end": v(4.4, 9.35) * mm});
            skLineSegment(sketch, "E1316", {"start": v(4.4, 9.35) * mm, "end": v(4.4, 9.36) * mm});
            skLineSegment(sketch, "E1317", {"start": v(4.4, 9.36) * mm, "end": v(4.38, 9.38) * mm});
            skLineSegment(sketch, "E1318", {"start": v(4.38, 9.38) * mm, "end": v(4.38, 9.4) * mm});
            skLineSegment(sketch, "E1319", {"start": v(4.38, 9.4) * mm, "end": v(4.37, 9.41) * mm});
            skLineSegment(sketch, "E1320", {"start": v(4.37, 9.41) * mm, "end": v(4.36, 9.44) * mm});
            skLineSegment(sketch, "E1321", {"start": v(4.36, 9.44) * mm, "end": v(4.36, 9.45) * mm});
            skLineSegment(sketch, "E1322", {"start": v(4.36, 9.45) * mm, "end": v(4.32, 9.68) * mm});
            skLineSegment(sketch, "E1323", {"start": v(4.32, 9.68) * mm, "end": v(4.3, 9.76) * mm});
            skLineSegment(sketch, "E1324", {"start": v(4.3, 9.76) * mm, "end": v(4.3, 9.84) * mm});
            skLineSegment(sketch, "E1325", {"start": v(4.3, 9.84) * mm, "end": v(4.27, 9.92) * mm});
            skLineSegment(sketch, "E1326", {"start": v(4.27, 9.92) * mm, "end": v(4.26, 10) * mm});
            skLineSegment(sketch, "E1327", {"start": v(4.26, 10) * mm, "end": v(4.24, 10.1) * mm});
            skLineSegment(sketch, "E1328", {"start": v(4.24, 10.1) * mm, "end": v(4.22, 10.2) * mm});
            skLineSegment(sketch, "E1329", {"start": v(4.22, 10.2) * mm, "end": v(4.2, 10.3) * mm});
            skLineSegment(sketch, "E1330", {"start": v(4.2, 10.3) * mm, "end": v(4.17, 10.39) * mm});
            skLineSegment(sketch, "E1331", {"start": v(4.17, 10.39) * mm, "end": v(4.16, 10.43) * mm});
            skLineSegment(sketch, "E1332", {"start": v(4.16, 10.43) * mm, "end": v(4.14, 10.5) * mm});
            skLineSegment(sketch, "E1333", {"start": v(4.14, 10.5) * mm, "end": v(4.11, 10.63) * mm});
            skLineSegment(sketch, "E1334", {"start": v(4.11, 10.63) * mm, "end": v(4.08, 10.75) * mm});
            skLineSegment(sketch, "E1335", {"start": v(4.08, 10.75) * mm, "end": v(4.05, 10.87) * mm});
            skLineSegment(sketch, "E1336", {"start": v(4.05, 10.87) * mm, "end": v(4.01, 11) * mm});
            skLineSegment(sketch, "E1337", {"start": v(4.01, 11) * mm, "end": v(3.98, 11.13) * mm});
            skLineSegment(sketch, "E1338", {"start": v(3.98, 11.13) * mm, "end": v(3.93, 11.28) * mm});
            skLineSegment(sketch, "E1339", {"start": v(3.93, 11.28) * mm, "end": v(3.77, 11.8) * mm});
            skLineSegment(sketch, "E1340", {"start": v(3.77, 11.8) * mm, "end": v(3.62, 11.8) * mm});
            skLineSegment(sketch, "E1341", {"start": v(3.62, 11.8) * mm, "end": v(3.24, 11.83) * mm});
            skLineSegment(sketch, "E1342", {"start": v(3.24, 11.83) * mm, "end": v(2.96, 11.85) * mm});
            skLineSegment(sketch, "E1343", {"start": v(2.96, 11.85) * mm, "end": v(2.68, 11.28) * mm});
            skLineSegment(sketch, "E1344", {"start": v(2.68, 11.28) * mm, "end": v(2.63, 11.16) * mm});
            skLineSegment(sketch, "E1345", {"start": v(2.63, 11.16) * mm, "end": v(2.57, 11.03) * mm});
            skLineSegment(sketch, "E1346", {"start": v(2.57, 11.03) * mm, "end": v(2.51, 10.91) * mm});
            skLineSegment(sketch, "E1347", {"start": v(2.51, 10.91) * mm, "end": v(2.46, 10.78) * mm});
            skLineSegment(sketch, "E1348", {"start": v(2.46, 10.78) * mm, "end": v(2.4, 10.66) * mm});
            skLineSegment(sketch, "E1349", {"start": v(2.4, 10.66) * mm, "end": v(2.37, 10.57) * mm});
            skLineSegment(sketch, "E1350", {"start": v(2.37, 10.57) * mm, "end": v(2.34, 10.5) * mm});
            skLineSegment(sketch, "E1351", {"start": v(2.34, 10.5) * mm, "end": v(2.31, 10.43) * mm});
            skLineSegment(sketch, "E1352", {"start": v(2.31, 10.43) * mm, "end": v(2.26, 10.3) * mm});
            skLineSegment(sketch, "E1353", {"start": v(2.26, 10.3) * mm, "end": v(2.23, 10.21) * mm});
            skLineSegment(sketch, "E1354", {"start": v(2.23, 10.21) * mm, "end": v(2.2, 10.14) * mm});
            skLineSegment(sketch, "E1355", {"start": v(2.2, 10.14) * mm, "end": v(2.19, 10.1) * mm});
            skLineSegment(sketch, "E1356", {"start": v(2.19, 10.1) * mm, "end": v(2.16, 10.03) * mm});
            skLineSegment(sketch, "E1357", {"start": v(2.16, 10.03) * mm, "end": v(2.14, 9.97) * mm});
            skLineSegment(sketch, "E1358", {"start": v(2.14, 9.97) * mm, "end": v(2.12, 9.92) * mm});
            skLineSegment(sketch, "E1359", {"start": v(2.12, 9.92) * mm, "end": v(2.1, 9.85) * mm});
            skLineSegment(sketch, "E1360", {"start": v(2.1, 9.85) * mm, "end": v(2.02, 9.6) * mm});
            skLineSegment(sketch, "E1361", {"start": v(2.02, 9.6) * mm, "end": v(2.01, 9.6) * mm});
            skLineSegment(sketch, "E1362", {"start": v(2.01, 9.6) * mm, "end": v(2, 9.59) * mm});
            skLineSegment(sketch, "E1363", {"start": v(2, 9.59) * mm, "end": v(2, 9.57) * mm});
            skLineSegment(sketch, "E1364", {"start": v(2, 9.57) * mm, "end": v(2, 9.56) * mm});
            skLineSegment(sketch, "E1365", {"start": v(2, 9.56) * mm, "end": v(1.99, 9.55) * mm});
            skLineSegment(sketch, "E1366", {"start": v(1.99, 9.55) * mm, "end": v(1.98, 9.54) * mm});
            skLineSegment(sketch, "E1367", {"start": v(1.98, 9.54) * mm, "end": v(1.97, 9.54) * mm});
            skLineSegment(sketch, "E1368", {"start": v(1.97, 9.54) * mm, "end": v(1.97, 9.53) * mm});
            skLineSegment(sketch, "E1369", {"start": v(1.97, 9.53) * mm, "end": v(1.95, 9.52) * mm});
            skLineSegment(sketch, "E1370", {"start": v(1.95, 9.52) * mm, "end": v(1.94, 9.51) * mm});
            skLineSegment(sketch, "E1371", {"start": v(1.94, 9.51) * mm, "end": v(1.94, 9.51) * mm});
            skLineSegment(sketch, "E1372", {"start": v(1.94, 9.51) * mm, "end": v(1.93, 9.51) * mm});
            skLineSegment(sketch, "E1373", {"start": v(1.93, 9.51) * mm, "end": v(1.7, 9.52) * mm});
            skLineSegment(sketch, "E1374", {"start": v(1.7, 9.52) * mm, "end": v(1.5, 9.53) * mm});
            skLineSegment(sketch, "E1375", {"start": v(1.5, 9.53) * mm, "end": v(1.25, 9.54) * mm});
            skLineSegment(sketch, "E1376", {"start": v(1.25, 9.54) * mm, "end": v(1.25, 9.54) * mm});
            skLineSegment(sketch, "E1377", {"start": v(1.25, 9.54) * mm, "end": v(1.24, 9.54) * mm});
            skLineSegment(sketch, "E1378", {"start": v(1.24, 9.54) * mm, "end": v(1.23, 9.55) * mm});
            skLineSegment(sketch, "E1379", {"start": v(1.23, 9.55) * mm, "end": v(1.22, 9.57) * mm});
            skLineSegment(sketch, "E1380", {"start": v(1.22, 9.57) * mm, "end": v(1.2, 9.58) * mm});
            skLineSegment(sketch, "E1381", {"start": v(1.2, 9.58) * mm, "end": v(1.2, 9.6) * mm});
            skLineSegment(sketch, "E1382", {"start": v(1.2, 9.6) * mm, "end": v(1.18, 9.62) * mm});
            skLineSegment(sketch, "E1383", {"start": v(1.18, 9.62) * mm, "end": v(1.18, 9.64) * mm});
            skLineSegment(sketch, "E1384", {"start": v(1.18, 9.64) * mm, "end": v(1.1, 9.94) * mm});
            skLineSegment(sketch, "E1385", {"start": v(1.1, 9.94) * mm, "end": v(1.07, 10.04) * mm});
            skLineSegment(sketch, "E1386", {"start": v(1.07, 10.04) * mm, "end": v(1.05, 10.14) * mm});
            skLineSegment(sketch, "E1387", {"start": v(1.05, 10.14) * mm, "end": v(1.02, 10.25) * mm});
            skLineSegment(sketch, "E1388", {"start": v(1.02, 10.25) * mm, "end": v(0.98, 10.36) * mm});
            skLineSegment(sketch, "E1389", {"start": v(0.98, 10.36) * mm, "end": v(0.95, 10.47) * mm});
            skLineSegment(sketch, "E1390", {"start": v(0.95, 10.47) * mm, "end": v(0.92, 10.56) * mm});
            skLineSegment(sketch, "E1391", {"start": v(0.92, 10.56) * mm, "end": v(0.9, 10.63) * mm});
            skLineSegment(sketch, "E1392", {"start": v(0.9, 10.63) * mm, "end": v(0.87, 10.73) * mm});
            skLineSegment(sketch, "E1393", {"start": v(0.87, 10.73) * mm, "end": v(0.82, 10.86) * mm});
            skLineSegment(sketch, "E1394", {"start": v(0.82, 10.86) * mm, "end": v(0.78, 10.97) * mm});
            skLineSegment(sketch, "E1395", {"start": v(0.78, 10.97) * mm, "end": v(0.76, 11.03) * mm});
            skLineSegment(sketch, "E1396", {"start": v(0.76, 11.03) * mm, "end": v(0.73, 11.1) * mm});
            skLineSegment(sketch, "E1397", {"start": v(0.73, 11.1) * mm, "end": v(0.7, 11.17) * mm});
            skLineSegment(sketch, "E1398", {"start": v(0.7, 11.17) * mm, "end": v(0.68, 11.25) * mm});
            skLineSegment(sketch, "E1399", {"start": v(0.68, 11.25) * mm, "end": v(0.65, 11.32) * mm});
            skLineSegment(sketch, "E1400", {"start": v(0.65, 11.32) * mm, "end": v(0.62, 11.41) * mm});
            skLineSegment(sketch, "E1401", {"start": v(0.62, 11.41) * mm, "end": v(0.4, 11.95) * mm});
            skLineSegment(sketch, "E1402", {"start": v(0.4, 11.95) * mm, "end": v(0.35, 11.95) * mm});
            skLineSegment(sketch, "E1403", {"start": v(0.35, 11.95) * mm, "end": v(-0.1, 11.95) * mm});
            skLineSegment(sketch, "E1404", {"start": v(-0.1, 11.95) * mm, "end": v(-0.41, 11.95) * mm});
            skLineSegment(sketch, "E1405", {"start": v(-0.41, 11.95) * mm, "end": v(-0.62, 11.43) * mm});
            skLineSegment(sketch, "E1406", {"start": v(-0.62, 11.43) * mm, "end": v(-0.64, 11.36) * mm});
            skLineSegment(sketch, "E1407", {"start": v(-0.64, 11.36) * mm, "end": v(-0.67, 11.3) * mm});
            skLineSegment(sketch, "E1408", {"start": v(-0.67, 11.3) * mm, "end": v(-0.7, 11.2) * mm});
            skLineSegment(sketch, "E1409", {"start": v(-0.7, 11.2) * mm, "end": v(-0.72, 11.15) * mm});
            skLineSegment(sketch, "E1410", {"start": v(-0.72, 11.15) * mm, "end": v(-0.75, 11.06) * mm});
            skLineSegment(sketch, "E1411", {"start": v(-0.75, 11.06) * mm, "end": v(-0.78, 11) * mm});
            skLineSegment(sketch, "E1412", {"start": v(-0.78, 11) * mm, "end": v(-0.8, 10.92) * mm});
            skLineSegment(sketch, "E1413", {"start": v(-0.8, 10.92) * mm, "end": v(-0.83, 10.85) * mm});
            skLineSegment(sketch, "E1414", {"start": v(-0.83, 10.85) * mm, "end": v(-0.85, 10.78) * mm});
            skLineSegment(sketch, "E1415", {"start": v(-0.85, 10.78) * mm, "end": v(-0.88, 10.7) * mm});
            skLineSegment(sketch, "E1416", {"start": v(-0.88, 10.7) * mm, "end": v(-0.9, 10.63) * mm});
            skLineSegment(sketch, "E1417", {"start": v(-0.9, 10.63) * mm, "end": v(-0.92, 10.56) * mm});
            skLineSegment(sketch, "E1418", {"start": v(-0.92, 10.56) * mm, "end": v(-0.94, 10.5) * mm});
            skLineSegment(sketch, "E1419", {"start": v(-0.94, 10.5) * mm, "end": v(-0.96, 10.42) * mm});
            skLineSegment(sketch, "E1420", {"start": v(-0.96, 10.42) * mm, "end": v(-0.99, 10.35) * mm});
            skLineSegment(sketch, "E1421", {"start": v(-0.99, 10.35) * mm, "end": v(-1, 10.28) * mm});
            skLineSegment(sketch, "E1422", {"start": v(-1, 10.28) * mm, "end": v(-1.03, 10.21) * mm});
            skLineSegment(sketch, "E1423", {"start": v(-1.03, 10.21) * mm, "end": v(-1.05, 10.14) * mm});
            skLineSegment(sketch, "E1424", {"start": v(-1.05, 10.14) * mm, "end": v(-1.07, 10.07) * mm});
            skLineSegment(sketch, "E1425", {"start": v(-1.07, 10.07) * mm, "end": v(-1.08, 10) * mm});
            skLineSegment(sketch, "E1426", {"start": v(-1.08, 10) * mm, "end": v(-1.1, 9.94) * mm});
            skLineSegment(sketch, "E1427", {"start": v(-1.1, 9.94) * mm, "end": v(-1.12, 9.87) * mm});
            skLineSegment(sketch, "E1428", {"start": v(-1.12, 9.87) * mm, "end": v(-1.18, 9.65) * mm});
            skLineSegment(sketch, "E1429", {"start": v(-1.18, 9.65) * mm, "end": v(-1.18, 9.64) * mm});
            skLineSegment(sketch, "E1430", {"start": v(-1.18, 9.64) * mm, "end": v(-1.19, 9.62) * mm});
            skLineSegment(sketch, "E1431", {"start": v(-1.19, 9.62) * mm, "end": v(-1.2, 9.6) * mm});
            skLineSegment(sketch, "E1432", {"start": v(-1.2, 9.6) * mm, "end": v(-1.2, 9.6) * mm});
            skLineSegment(sketch, "E1433", {"start": v(-1.2, 9.6) * mm, "end": v(-1.2, 9.58) * mm});
            skLineSegment(sketch, "E1434", {"start": v(-1.2, 9.58) * mm, "end": v(-1.21, 9.57) * mm});
            skLineSegment(sketch, "E1435", {"start": v(-1.21, 9.57) * mm, "end": v(-1.22, 9.56) * mm});
            skLineSegment(sketch, "E1436", {"start": v(-1.22, 9.56) * mm, "end": v(-1.23, 9.55) * mm});
            skLineSegment(sketch, "E1437", {"start": v(-1.23, 9.55) * mm, "end": v(-1.24, 9.55) * mm});
            skLineSegment(sketch, "E1438", {"start": v(-1.24, 9.55) * mm, "end": v(-1.24, 9.54) * mm});
            skLineSegment(sketch, "E1439", {"start": v(-1.24, 9.54) * mm, "end": v(-1.25, 9.54) * mm});
            skLineSegment(sketch, "E1440", {"start": v(-1.25, 9.54) * mm, "end": v(-1.26, 9.54) * mm});
            skLineSegment(sketch, "E1441", {"start": v(-1.26, 9.54) * mm, "end": v(-1.26, 9.54) * mm});
            skLineSegment(sketch, "E1442", {"start": v(-1.26, 9.54) * mm, "end": v(-1.48, 9.53) * mm});
            skLineSegment(sketch, "E1443", {"start": v(-1.48, 9.53) * mm, "end": v(-1.71, 9.52) * mm});
            skLineSegment(sketch, "E1444", {"start": v(-1.71, 9.52) * mm, "end": v(-1.93, 9.51) * mm});
            skLineSegment(sketch, "E1445", {"start": v(-1.93, 9.51) * mm, "end": v(-1.94, 9.51) * mm});
            skLineSegment(sketch, "E1446", {"start": v(-1.94, 9.51) * mm, "end": v(-1.95, 9.51) * mm});
            skLineSegment(sketch, "E1447", {"start": v(-1.95, 9.51) * mm, "end": v(-1.95, 9.52) * mm});
            skLineSegment(sketch, "E1448", {"start": v(-1.95, 9.52) * mm, "end": v(-1.96, 9.52) * mm});
            skLineSegment(sketch, "E1449", {"start": v(-1.96, 9.52) * mm, "end": v(-1.97, 9.53) * mm});
            skLineSegment(sketch, "E1450", {"start": v(-1.97, 9.53) * mm, "end": v(-1.97, 9.54) * mm});
            skLineSegment(sketch, "E1451", {"start": v(-1.97, 9.54) * mm, "end": v(-1.98, 9.54) * mm});
            skLineSegment(sketch, "E1452", {"start": v(-1.98, 9.54) * mm, "end": v(-1.99, 9.55) * mm});
            skLineSegment(sketch, "E1453", {"start": v(-1.99, 9.55) * mm, "end": v(-2, 9.56) * mm});
            skLineSegment(sketch, "E1454", {"start": v(-2, 9.56) * mm, "end": v(-2, 9.57) * mm});
            skLineSegment(sketch, "E1455", {"start": v(-2, 9.57) * mm, "end": v(-2, 9.59) * mm});
            skLineSegment(sketch, "E1456", {"start": v(-2, 9.59) * mm, "end": v(-2.01, 9.6) * mm});
            skLineSegment(sketch, "E1457", {"start": v(-2.01, 9.6) * mm, "end": v(-2.02, 9.61) * mm});
            skLineSegment(sketch, "E1458", {"start": v(-2.02, 9.61) * mm, "end": v(-2.02, 9.61) * mm});
            skLineSegment(sketch, "E1459", {"start": v(-2.02, 9.61) * mm, "end": v(-2.1, 9.84) * mm});
            skLineSegment(sketch, "E1460", {"start": v(-2.1, 9.84) * mm, "end": v(-2.12, 9.9) * mm});
            skLineSegment(sketch, "E1461", {"start": v(-2.12, 9.9) * mm, "end": v(-2.14, 9.95) * mm});
            skLineSegment(sketch, "E1462", {"start": v(-2.14, 9.95) * mm, "end": v(-2.16, 10) * mm});
            skLineSegment(sketch, "E1463", {"start": v(-2.16, 10) * mm, "end": v(-2.17, 10.06) * mm});
            skLineSegment(sketch, "E1464", {"start": v(-2.17, 10.06) * mm, "end": v(-2.2, 10.12) * mm});
            skLineSegment(sketch, "E1465", {"start": v(-2.2, 10.12) * mm, "end": v(-2.22, 10.18) * mm});
            skLineSegment(sketch, "E1466", {"start": v(-2.22, 10.18) * mm, "end": v(-2.25, 10.25) * mm});
            skLineSegment(sketch, "E1467", {"start": v(-2.25, 10.25) * mm, "end": v(-2.27, 10.3) * mm});
            skLineSegment(sketch, "E1468", {"start": v(-2.27, 10.3) * mm, "end": v(-2.3, 10.37) * mm});
            skLineSegment(sketch, "E1469", {"start": v(-2.3, 10.37) * mm, "end": v(-2.32, 10.44) * mm});
            skLineSegment(sketch, "E1470", {"start": v(-2.32, 10.44) * mm, "end": v(-2.34, 10.5) * mm});
            skLineSegment(sketch, "E1471", {"start": v(-2.34, 10.5) * mm, "end": v(-2.38, 10.58) * mm});
            skLineSegment(sketch, "E1472", {"start": v(-2.38, 10.58) * mm, "end": v(-2.4, 10.64) * mm});
            skLineSegment(sketch, "E1473", {"start": v(-2.4, 10.64) * mm, "end": v(-2.44, 10.72) * mm});
            skLineSegment(sketch, "E1474", {"start": v(-2.44, 10.72) * mm, "end": v(-2.47, 10.8) * mm});
            skLineSegment(sketch, "E1475", {"start": v(-2.47, 10.8) * mm, "end": v(-2.5, 10.87) * mm});
            skLineSegment(sketch, "E1476", {"start": v(-2.5, 10.87) * mm, "end": v(-2.53, 10.94) * mm});
            skLineSegment(sketch, "E1477", {"start": v(-2.53, 10.94) * mm, "end": v(-2.57, 11.03) * mm});
            skLineSegment(sketch, "E1478", {"start": v(-2.57, 11.03) * mm, "end": v(-2.6, 11.11) * mm});
            skLineSegment(sketch, "E1479", {"start": v(-2.6, 11.11) * mm, "end": v(-2.64, 11.18) * mm});
            skLineSegment(sketch, "E1480", {"start": v(-2.64, 11.18) * mm, "end": v(-2.68, 11.26) * mm});
            skLineSegment(sketch, "E1481", {"start": v(-2.68, 11.26) * mm, "end": v(-2.72, 11.35) * mm});
            skLineSegment(sketch, "E1482", {"start": v(-2.72, 11.35) * mm, "end": v(-2.96, 11.85) * mm});
            skLineSegment(sketch, "E1483", {"start": v(-2.96, 11.85) * mm, "end": v(-3.4, 11.82) * mm});
            skLineSegment(sketch, "E1484", {"start": v(-3.4, 11.82) * mm, "end": v(-3.78, 11.8) * mm});
            skLineSegment(sketch, "E1485", {"start": v(-3.78, 11.8) * mm, "end": v(-3.93, 11.28) * mm});
            skLineSegment(sketch, "E1486", {"start": v(-3.93, 11.28) * mm, "end": v(-3.96, 11.2) * mm});
            skLineSegment(sketch, "E1487", {"start": v(-3.96, 11.2) * mm, "end": v(-3.98, 11.11) * mm});
            skLineSegment(sketch, "E1488", {"start": v(-3.98, 11.11) * mm, "end": v(-4, 11.03) * mm});
            skLineSegment(sketch, "E1489", {"start": v(-4, 11.03) * mm, "end": v(-4.03, 10.94) * mm});
            skLineSegment(sketch, "E1490", {"start": v(-4.03, 10.94) * mm, "end": v(-4.06, 10.85) * mm});
            skLineSegment(sketch, "E1491", {"start": v(-4.06, 10.85) * mm, "end": v(-4.08, 10.77) * mm});
            skLineSegment(sketch, "E1492", {"start": v(-4.08, 10.77) * mm, "end": v(-4.1, 10.7) * mm});
            skLineSegment(sketch, "E1493", {"start": v(-4.1, 10.7) * mm, "end": v(-4.12, 10.6) * mm});
            skLineSegment(sketch, "E1494", {"start": v(-4.12, 10.6) * mm, "end": v(-4.14, 10.52) * mm});
            skLineSegment(sketch, "E1495", {"start": v(-4.14, 10.52) * mm, "end": v(-4.16, 10.45) * mm});
            skLineSegment(sketch, "E1496", {"start": v(-4.16, 10.45) * mm, "end": v(-4.18, 10.36) * mm});
            skLineSegment(sketch, "E1497", {"start": v(-4.18, 10.36) * mm, "end": v(-4.2, 10.28) * mm});
            skLineSegment(sketch, "E1498", {"start": v(-4.2, 10.28) * mm, "end": v(-4.22, 10.2) * mm});
            skLineSegment(sketch, "E1499", {"start": v(-4.22, 10.2) * mm, "end": v(-4.23, 10.13) * mm});
            skLineSegment(sketch, "E1500", {"start": v(-4.23, 10.13) * mm, "end": v(-4.25, 10.05) * mm});
            skLineSegment(sketch, "E1501", {"start": v(-4.25, 10.05) * mm, "end": v(-4.27, 9.97) * mm});
            skLineSegment(sketch, "E1502", {"start": v(-4.27, 9.97) * mm, "end": v(-4.28, 9.9) * mm});
            skLineSegment(sketch, "E1503", {"start": v(-4.28, 9.9) * mm, "end": v(-4.3, 9.83) * mm});
            skLineSegment(sketch, "E1504", {"start": v(-4.3, 9.83) * mm, "end": v(-4.3, 9.76) * mm});
            skLineSegment(sketch, "E1505", {"start": v(-4.3, 9.76) * mm, "end": v(-4.32, 9.7) * mm});
            skLineSegment(sketch, "E1506", {"start": v(-4.32, 9.7) * mm, "end": v(-4.36, 9.44) * mm});
            skLineSegment(sketch, "E1507", {"start": v(-4.36, 9.44) * mm, "end": v(-4.36, 9.43) * mm});
            skLineSegment(sketch, "E1508", {"start": v(-4.36, 9.43) * mm, "end": v(-4.37, 9.41) * mm});
            skLineSegment(sketch, "E1509", {"start": v(-4.37, 9.41) * mm, "end": v(-4.38, 9.4) * mm});
            skLineSegment(sketch, "E1510", {"start": v(-4.38, 9.4) * mm, "end": v(-4.38, 9.38) * mm});
            skLineSegment(sketch, "E1511", {"start": v(-4.38, 9.38) * mm, "end": v(-4.4, 9.37) * mm});
            skLineSegment(sketch, "E1512", {"start": v(-4.4, 9.37) * mm, "end": v(-4.4, 9.35) * mm});
            skLineSegment(sketch, "E1513", {"start": v(-4.4, 9.35) * mm, "end": v(-4.4, 9.34) * mm});
            skLineSegment(sketch, "E1514", {"start": v(-4.4, 9.34) * mm, "end": v(-4.41, 9.33) * mm});
            skLineSegment(sketch, "E1515", {"start": v(-4.41, 9.33) * mm, "end": v(-4.42, 9.33) * mm});
            skLineSegment(sketch, "E1516", {"start": v(-4.42, 9.33) * mm, "end": v(-4.43, 9.32) * mm});
            skLineSegment(sketch, "E1517", {"start": v(-4.43, 9.32) * mm, "end": v(-4.44, 9.32) * mm});
            skLineSegment(sketch, "E1518", {"start": v(-4.44, 9.32) * mm, "end": v(-4.44, 9.32) * mm});
            skLineSegment(sketch, "E1519", {"start": v(-4.44, 9.32) * mm, "end": v(-4.64, 9.3) * mm});
            skLineSegment(sketch, "E1520", {"start": v(-4.64, 9.3) * mm, "end": v(-4.9, 9.27) * mm});
            skLineSegment(sketch, "E1521", {"start": v(-4.9, 9.27) * mm, "end": v(-5.1, 9.24) * mm});
            skLineSegment(sketch, "E1522", {"start": v(-5.1, 9.24) * mm, "end": v(-5.11, 9.24) * mm});
            skLineSegment(sketch, "E1523", {"start": v(-5.11, 9.24) * mm, "end": v(-5.12, 9.24) * mm});
            skLineSegment(sketch, "E1524", {"start": v(-5.12, 9.24) * mm, "end": v(-5.13, 9.25) * mm});
            skLineSegment(sketch, "E1525", {"start": v(-5.13, 9.25) * mm, "end": v(-5.14, 9.25) * mm});
            skLineSegment(sketch, "E1526", {"start": v(-5.14, 9.25) * mm, "end": v(-5.15, 9.26) * mm});
            skLineSegment(sketch, "E1527", {"start": v(-5.15, 9.26) * mm, "end": v(-5.16, 9.27) * mm});
            skLineSegment(sketch, "E1528", {"start": v(-5.16, 9.27) * mm, "end": v(-5.17, 9.28) * mm});
            skLineSegment(sketch, "E1529", {"start": v(-5.17, 9.28) * mm, "end": v(-5.17, 9.29) * mm});
            skLineSegment(sketch, "E1530", {"start": v(-5.17, 9.29) * mm, "end": v(-5.18, 9.3) * mm});
            skLineSegment(sketch, "E1531", {"start": v(-5.18, 9.3) * mm, "end": v(-5.2, 9.31) * mm});
            skLineSegment(sketch, "E1532", {"start": v(-5.2, 9.31) * mm, "end": v(-5.2, 9.33) * mm});
            skLineSegment(sketch, "E1533", {"start": v(-5.2, 9.33) * mm, "end": v(-5.2, 9.34) * mm});
            skLineSegment(sketch, "E1534", {"start": v(-5.2, 9.34) * mm, "end": v(-5.2, 9.34) * mm});
            skLineSegment(sketch, "E1535", {"start": v(-5.2, 9.34) * mm, "end": v(-5.3, 9.54) * mm});
            skLineSegment(sketch, "E1536", {"start": v(-5.3, 9.54) * mm, "end": v(-5.33, 9.62) * mm});
            skLineSegment(sketch, "E1537", {"start": v(-5.33, 9.62) * mm, "end": v(-5.34, 9.66) * mm});
            skLineSegment(sketch, "E1538", {"start": v(-5.34, 9.66) * mm, "end": v(-5.38, 9.73) * mm});
            skLineSegment(sketch, "E1539", {"start": v(-5.38, 9.73) * mm, "end": v(-5.4, 9.78) * mm});
            skLineSegment(sketch, "E1540", {"start": v(-5.4, 9.78) * mm, "end": v(-5.43, 9.86) * mm});
            skLineSegment(sketch, "E1541", {"start": v(-5.43, 9.86) * mm, "end": v(-5.46, 9.92) * mm});
            skLineSegment(sketch, "E1542", {"start": v(-5.46, 9.92) * mm, "end": v(-5.5, 9.98) * mm});
            skLineSegment(sketch, "E1543", {"start": v(-5.5, 9.98) * mm, "end": v(-5.53, 10.06) * mm});
            skLineSegment(sketch, "E1544", {"start": v(-5.53, 10.06) * mm, "end": v(-5.56, 10.13) * mm});
            skLineSegment(sketch, "E1545", {"start": v(-5.56, 10.13) * mm, "end": v(-5.6, 10.2) * mm});
            skLineSegment(sketch, "E1546", {"start": v(-5.6, 10.2) * mm, "end": v(-5.63, 10.27) * mm});
            skLineSegment(sketch, "E1547", {"start": v(-5.63, 10.27) * mm, "end": v(-5.67, 10.35) * mm});
            skLineSegment(sketch, "E1548", {"start": v(-5.67, 10.35) * mm, "end": v(-5.71, 10.43) * mm});
            skLineSegment(sketch, "E1549", {"start": v(-5.71, 10.43) * mm, "end": v(-5.75, 10.5) * mm});
            skLineSegment(sketch, "E1550", {"start": v(-5.75, 10.5) * mm, "end": v(-5.8, 10.58) * mm});
            skLineSegment(sketch, "E1551", {"start": v(-5.8, 10.58) * mm, "end": v(-5.84, 10.67) * mm});
            skLineSegment(sketch, "E1552", {"start": v(-5.84, 10.67) * mm, "end": v(-5.89, 10.75) * mm});
            skLineSegment(sketch, "E1553", {"start": v(-5.89, 10.75) * mm, "end": v(-5.93, 10.83) * mm});
            skLineSegment(sketch, "E1554", {"start": v(-5.93, 10.83) * mm, "end": v(-5.98, 10.92) * mm});
            skLineSegment(sketch, "E1555", {"start": v(-5.98, 10.92) * mm, "end": v(-6.03, 11) * mm});
            skLineSegment(sketch, "E1556", {"start": v(-6.03, 11) * mm, "end": v(-6.32, 11.5) * mm});
            skLineSegment(sketch, "E1557", {"start": v(-6.32, 11.5) * mm, "end": v(-6.51, 11.47) * mm});
            skLineSegment(sketch, "E1558", {"start": v(-6.51, 11.47) * mm, "end": v(-7.05, 11.38) * mm});
            skLineSegment(sketch, "E1559", {"start": v(-7.05, 11.38) * mm, "end": v(-7.13, 11.37) * mm});
            skLineSegment(sketch, "E1560", {"start": v(-7.13, 11.37) * mm, "end": v(-7.25, 10.82) * mm});
            skLineSegment(sketch, "E1561", {"start": v(-7.25, 10.82) * mm, "end": v(-7.27, 10.73) * mm});
            skLineSegment(sketch, "E1562", {"start": v(-7.27, 10.73) * mm, "end": v(-7.29, 10.63) * mm});
            skLineSegment(sketch, "E1563", {"start": v(-7.29, 10.63) * mm, "end": v(-7.3, 10.54) * mm});
            skLineSegment(sketch, "E1564", {"start": v(-7.3, 10.54) * mm, "end": v(-7.32, 10.44) * mm});
            skLineSegment(sketch, "E1565", {"start": v(-7.32, 10.44) * mm, "end": v(-7.34, 10.36) * mm});
            skLineSegment(sketch, "E1566", {"start": v(-7.34, 10.36) * mm, "end": v(-7.36, 10.26) * mm});
            skLineSegment(sketch, "E1567", {"start": v(-7.36, 10.26) * mm, "end": v(-7.37, 10.18) * mm});
            skLineSegment(sketch, "E1568", {"start": v(-7.37, 10.18) * mm, "end": v(-7.39, 10.08) * mm});
            skLineSegment(sketch, "E1569", {"start": v(-7.39, 10.08) * mm, "end": v(-7.4, 10) * mm});
            skLineSegment(sketch, "E1570", {"start": v(-7.4, 10) * mm, "end": v(-7.41, 9.9) * mm});
            skLineSegment(sketch, "E1571", {"start": v(-7.41, 9.9) * mm, "end": v(-7.43, 9.83) * mm});
            skLineSegment(sketch, "E1572", {"start": v(-7.43, 9.83) * mm, "end": v(-7.44, 9.75) * mm});
            skLineSegment(sketch, "E1573", {"start": v(-7.44, 9.75) * mm, "end": v(-7.45, 9.66) * mm});
            skLineSegment(sketch, "E1574", {"start": v(-7.45, 9.66) * mm, "end": v(-7.46, 9.58) * mm});
            skLineSegment(sketch, "E1575", {"start": v(-7.46, 9.58) * mm, "end": v(-7.47, 9.5) * mm});
            skLineSegment(sketch, "E1576", {"start": v(-7.47, 9.5) * mm, "end": v(-7.47, 9.43) * mm});
            skLineSegment(sketch, "E1577", {"start": v(-7.47, 9.43) * mm, "end": v(-7.48, 9.35) * mm});
            skLineSegment(sketch, "E1578", {"start": v(-7.48, 9.35) * mm, "end": v(-7.49, 9.28) * mm});
            skLineSegment(sketch, "E1579", {"start": v(-7.49, 9.28) * mm, "end": v(-7.5, 8.99) * mm});
            skLineSegment(sketch, "E1580", {"start": v(-7.5, 8.99) * mm, "end": v(-7.51, 8.97) * mm});
            skLineSegment(sketch, "E1581", {"start": v(-7.51, 8.97) * mm, "end": v(-7.52, 8.95) * mm});
            skLineSegment(sketch, "E1582", {"start": v(-7.52, 8.95) * mm, "end": v(-7.52, 8.93) * mm});
            skLineSegment(sketch, "E1583", {"start": v(-7.52, 8.93) * mm, "end": v(-7.53, 8.91) * mm});
            skLineSegment(sketch, "E1584", {"start": v(-7.53, 8.91) * mm, "end": v(-7.54, 8.9) * mm});
            skLineSegment(sketch, "E1585", {"start": v(-7.54, 8.9) * mm, "end": v(-7.55, 8.88) * mm});
            skLineSegment(sketch, "E1586", {"start": v(-7.55, 8.88) * mm, "end": v(-7.55, 8.87) * mm});
            skLineSegment(sketch, "E1587", {"start": v(-7.55, 8.87) * mm, "end": v(-7.56, 8.86) * mm});
            skLineSegment(sketch, "E1588", {"start": v(-7.56, 8.86) * mm, "end": v(-7.57, 8.85) * mm});
            skLineSegment(sketch, "E1589", {"start": v(-7.57, 8.85) * mm, "end": v(-7.58, 8.85) * mm});
            skLineSegment(sketch, "E1590", {"start": v(-7.58, 8.85) * mm, "end": v(-7.58, 8.85) * mm});
            skLineSegment(sketch, "E1591", {"start": v(-7.58, 8.85) * mm, "end": v(-7.78, 8.81) * mm});
            skLineSegment(sketch, "E1592", {"start": v(-7.78, 8.81) * mm, "end": v(-8.05, 8.76) * mm});
            skLineSegment(sketch, "E1593", {"start": v(-8.05, 8.76) * mm, "end": v(-8.24, 8.72) * mm});
            skLineSegment(sketch, "E1594", {"start": v(-8.24, 8.72) * mm, "end": v(-8.24, 8.72) * mm});
            skLineSegment(sketch, "E1595", {"start": v(-8.24, 8.72) * mm, "end": v(-8.25, 8.72) * mm});
            skLineSegment(sketch, "E1596", {"start": v(-8.25, 8.72) * mm, "end": v(-8.26, 8.72) * mm});
            skLineSegment(sketch, "E1597", {"start": v(-8.26, 8.72) * mm, "end": v(-8.27, 8.72) * mm});
            skLineSegment(sketch, "E1598", {"start": v(-8.27, 8.72) * mm, "end": v(-8.28, 8.73) * mm});
            skLineSegment(sketch, "E1599", {"start": v(-8.28, 8.73) * mm, "end": v(-8.29, 8.73) * mm});
            skLineSegment(sketch, "E1600", {"start": v(-8.29, 8.73) * mm, "end": v(-8.3, 8.74) * mm});
            skLineSegment(sketch, "E1601", {"start": v(-8.3, 8.74) * mm, "end": v(-8.31, 8.75) * mm});
            skLineSegment(sketch, "E1602", {"start": v(-8.31, 8.75) * mm, "end": v(-8.32, 8.77) * mm});
            skLineSegment(sketch, "E1603", {"start": v(-8.32, 8.77) * mm, "end": v(-8.33, 8.78) * mm});
            skLineSegment(sketch, "E1604", {"start": v(-8.33, 8.78) * mm, "end": v(-8.35, 8.8) * mm});
            skLineSegment(sketch, "E1605", {"start": v(-8.35, 8.8) * mm, "end": v(-8.36, 8.81) * mm});
            skLineSegment(sketch, "E1606", {"start": v(-8.36, 8.81) * mm, "end": v(-8.36, 8.81) * mm});
            skLineSegment(sketch, "E1607", {"start": v(-8.36, 8.81) * mm, "end": v(-8.47, 9.02) * mm});
            skLineSegment(sketch, "E1608", {"start": v(-8.47, 9.02) * mm, "end": v(-8.5, 9.09) * mm});
            skLineSegment(sketch, "E1609", {"start": v(-8.5, 9.09) * mm, "end": v(-8.53, 9.15) * mm});
            skLineSegment(sketch, "E1610", {"start": v(-8.53, 9.15) * mm, "end": v(-8.57, 9.2) * mm});
            skLineSegment(sketch, "E1611", {"start": v(-8.57, 9.2) * mm, "end": v(-8.6, 9.28) * mm});
            skLineSegment(sketch, "E1612", {"start": v(-8.6, 9.28) * mm, "end": v(-8.64, 9.35) * mm});
            skLineSegment(sketch, "E1613", {"start": v(-8.64, 9.35) * mm, "end": v(-8.68, 9.42) * mm});
            skLineSegment(sketch, "E1614", {"start": v(-8.68, 9.42) * mm, "end": v(-8.72, 9.48) * mm});
            skLineSegment(sketch, "E1615", {"start": v(-8.72, 9.48) * mm, "end": v(-8.76, 9.55) * mm});
            skLineSegment(sketch, "E1616", {"start": v(-8.76, 9.55) * mm, "end": v(-8.8, 9.62) * mm});
            skLineSegment(sketch, "E1617", {"start": v(-8.8, 9.62) * mm, "end": v(-8.85, 9.7) * mm});
            skLineSegment(sketch, "E1618", {"start": v(-8.85, 9.7) * mm, "end": v(-8.9, 9.78) * mm});
            skLineSegment(sketch, "E1619", {"start": v(-8.9, 9.78) * mm, "end": v(-8.95, 9.86) * mm});
            skLineSegment(sketch, "E1620", {"start": v(-8.95, 9.86) * mm, "end": v(-9, 9.93) * mm});
            skLineSegment(sketch, "E1621", {"start": v(-9, 9.93) * mm, "end": v(-9.06, 10.02) * mm});
            skLineSegment(sketch, "E1622", {"start": v(-9.06, 10.02) * mm, "end": v(-9.11, 10.1) * mm});
            skLineSegment(sketch, "E1623", {"start": v(-9.11, 10.1) * mm, "end": v(-9.17, 10.18) * mm});
            skLineSegment(sketch, "E1624", {"start": v(-9.17, 10.18) * mm, "end": v(-9.23, 10.27) * mm});
            skLineSegment(sketch, "E1625", {"start": v(-9.23, 10.27) * mm, "end": v(-9.29, 10.35) * mm});
            skLineSegment(sketch, "E1626", {"start": v(-9.29, 10.35) * mm, "end": v(-9.65, 10.85) * mm});
            skLineSegment(sketch, "E1627", {"start": v(-9.65, 10.85) * mm, "end": v(-9.8, 10.82) * mm});
            skLineSegment(sketch, "E1628", {"start": v(-9.8, 10.82) * mm, "end": v(-10.35, 10.68) * mm});
            skLineSegment(sketch, "E1629", {"start": v(-10.35, 10.68) * mm, "end": v(-10.44, 10.66) * mm});
            skLineSegment(sketch, "E1630", {"start": v(-10.44, 10.66) * mm, "end": v(-10.51, 10.05) * mm});
            skLineSegment(sketch, "E1631", {"start": v(-10.51, 10.05) * mm, "end": v(-10.53, 9.95) * mm});
            skLineSegment(sketch, "E1632", {"start": v(-10.53, 9.95) * mm, "end": v(-10.54, 9.85) * mm});
            skLineSegment(sketch, "E1633", {"start": v(-10.54, 9.85) * mm, "end": v(-10.55, 9.74) * mm});
            skLineSegment(sketch, "E1634", {"start": v(-10.55, 9.74) * mm, "end": v(-10.56, 9.64) * mm});
            skLineSegment(sketch, "E1635", {"start": v(-10.56, 9.64) * mm, "end": v(-10.57, 9.55) * mm});
            skLineSegment(sketch, "E1636", {"start": v(-10.57, 9.55) * mm, "end": v(-10.57, 9.45) * mm});
            skLineSegment(sketch, "E1637", {"start": v(-10.57, 9.45) * mm, "end": v(-10.58, 9.36) * mm});
            skLineSegment(sketch, "E1638", {"start": v(-10.58, 9.36) * mm, "end": v(-10.59, 9.26) * mm});
            skLineSegment(sketch, "E1639", {"start": v(-10.59, 9.26) * mm, "end": v(-10.6, 9.17) * mm});
            skLineSegment(sketch, "E1640", {"start": v(-10.6, 9.17) * mm, "end": v(-10.6, 9.1) * mm});
            skLineSegment(sketch, "E1641", {"start": v(-10.6, 9.1) * mm, "end": v(-10.6, 9) * mm});
            skLineSegment(sketch, "E1642", {"start": v(-10.6, 9) * mm, "end": v(-10.6, 8.93) * mm});
            skLineSegment(sketch, "E1643", {"start": v(-10.6, 8.93) * mm, "end": v(-10.6, 8.85) * mm});
            skLineSegment(sketch, "E1644", {"start": v(-10.6, 8.85) * mm, "end": v(-10.6, 8.77) * mm});
            skLineSegment(sketch, "E1645", {"start": v(-10.6, 8.77) * mm, "end": v(-10.6, 8.7) * mm});
            skLineSegment(sketch, "E1646", {"start": v(-10.6, 8.7) * mm, "end": v(-10.6, 8.63) * mm});
            skLineSegment(sketch, "E1647", {"start": v(-10.6, 8.63) * mm, "end": v(-10.6, 8.57) * mm});
            skLineSegment(sketch, "E1648", {"start": v(-10.6, 8.57) * mm, "end": v(-10.59, 8.3) * mm});
            skLineSegment(sketch, "E1649", {"start": v(-10.59, 8.3) * mm, "end": v(-10.59, 8.27) * mm});
            skLineSegment(sketch, "E1650", {"start": v(-10.59, 8.27) * mm, "end": v(-10.6, 8.24) * mm});
            skLineSegment(sketch, "E1651", {"start": v(-10.6, 8.24) * mm, "end": v(-10.6, 8.21) * mm});
            skLineSegment(sketch, "E1652", {"start": v(-10.6, 8.21) * mm, "end": v(-10.6, 8.2) * mm});
            skLineSegment(sketch, "E1653", {"start": v(-10.6, 8.2) * mm, "end": v(-10.6, 8.17) * mm});
            skLineSegment(sketch, "E1654", {"start": v(-10.6, 8.17) * mm, "end": v(-10.62, 8.15) * mm});
            skLineSegment(sketch, "E1655", {"start": v(-10.62, 8.15) * mm, "end": v(-10.63, 8.14) * mm});
            skLineSegment(sketch, "E1656", {"start": v(-10.63, 8.14) * mm, "end": v(-10.63, 8.12) * mm});
            skLineSegment(sketch, "E1657", {"start": v(-10.63, 8.12) * mm, "end": v(-10.65, 8.11) * mm});
            skLineSegment(sketch, "E1658", {"start": v(-10.65, 8.11) * mm, "end": v(-10.66, 8.1) * mm});
            skLineSegment(sketch, "E1659", {"start": v(-10.66, 8.1) * mm, "end": v(-10.66, 8.1) * mm});
            skLineSegment(sketch, "E1660", {"start": v(-10.66, 8.1) * mm, "end": v(-10.85, 8.05) * mm});
            skLineSegment(sketch, "E1661", {"start": v(-10.85, 8.05) * mm, "end": v(-11.1, 7.97) * mm});
            skLineSegment(sketch, "E1662", {"start": v(-11.1, 7.97) * mm, "end": v(-11.3, 7.91) * mm});
            skLineSegment(sketch, "E1663", {"start": v(-11.3, 7.91) * mm, "end": v(-11.3, 7.91) * mm});
            skLineSegment(sketch, "E1664", {"start": v(-11.3, 7.91) * mm, "end": v(-11.3, 7.9) * mm});
            skLineSegment(sketch, "E1665", {"start": v(-11.3, 7.9) * mm, "end": v(-11.31, 7.91) * mm});
            skLineSegment(sketch, "E1666", {"start": v(-11.31, 7.91) * mm, "end": v(-11.33, 7.91) * mm});
            skLineSegment(sketch, "E1667", {"start": v(-11.33, 7.91) * mm, "end": v(-11.34, 7.92) * mm});
            skLineSegment(sketch, "E1668", {"start": v(-11.34, 7.92) * mm, "end": v(-11.36, 7.93) * mm});
            skLineSegment(sketch, "E1669", {"start": v(-11.36, 7.93) * mm, "end": v(-11.37, 7.94) * mm});
            skLineSegment(sketch, "E1670", {"start": v(-11.37, 7.94) * mm, "end": v(-11.39, 7.95) * mm});
            skLineSegment(sketch, "E1671", {"start": v(-11.39, 7.95) * mm, "end": v(-11.4, 7.96) * mm});
            skLineSegment(sketch, "E1672", {"start": v(-11.4, 7.96) * mm, "end": v(-11.42, 7.98) * mm});
            skLineSegment(sketch, "E1673", {"start": v(-11.42, 7.98) * mm, "end": v(-11.43, 8) * mm});
            skLineSegment(sketch, "E1674", {"start": v(-11.43, 8) * mm, "end": v(-11.43, 8) * mm});
            skLineSegment(sketch, "E1675", {"start": v(-11.43, 8) * mm, "end": v(-11.59, 8.24) * mm});
            skLineSegment(sketch, "E1676", {"start": v(-11.59, 8.24) * mm, "end": v(-11.63, 8.3) * mm});
            skLineSegment(sketch, "E1677", {"start": v(-11.63, 8.3) * mm, "end": v(-11.67, 8.36) * mm});
            skLineSegment(sketch, "E1678", {"start": v(-11.67, 8.36) * mm, "end": v(-11.71, 8.43) * mm});
            skLineSegment(sketch, "E1679", {"start": v(-11.71, 8.43) * mm, "end": v(-11.75, 8.48) * mm});
            skLineSegment(sketch, "E1680", {"start": v(-11.75, 8.48) * mm, "end": v(-11.8, 8.56) * mm});
            skLineSegment(sketch, "E1681", {"start": v(-11.8, 8.56) * mm, "end": v(-11.85, 8.62) * mm});
            skLineSegment(sketch, "E1682", {"start": v(-11.85, 8.62) * mm, "end": v(-11.9, 8.7) * mm});
            skLineSegment(sketch, "E1683", {"start": v(-11.9, 8.7) * mm, "end": v(-11.95, 8.76) * mm});
            skLineSegment(sketch, "E1684", {"start": v(-11.95, 8.76) * mm, "end": v(-12, 8.83) * mm});
            skLineSegment(sketch, "E1685", {"start": v(-12, 8.83) * mm, "end": v(-12.06, 8.9) * mm});
            skLineSegment(sketch, "E1686", {"start": v(-12.06, 8.9) * mm, "end": v(-12.12, 8.98) * mm});
            skLineSegment(sketch, "E1687", {"start": v(-12.12, 8.98) * mm, "end": v(-12.18, 9.05) * mm});
            skLineSegment(sketch, "E1688", {"start": v(-12.18, 9.05) * mm, "end": v(-12.24, 9.13) * mm});
            skLineSegment(sketch, "E1689", {"start": v(-12.24, 9.13) * mm, "end": v(-12.3, 9.21) * mm});
            skLineSegment(sketch, "E1690", {"start": v(-12.3, 9.21) * mm, "end": v(-12.37, 9.29) * mm});
            skLineSegment(sketch, "E1691", {"start": v(-12.37, 9.29) * mm, "end": v(-12.44, 9.37) * mm});
            skLineSegment(sketch, "E1692", {"start": v(-12.44, 9.37) * mm, "end": v(-12.52, 9.46) * mm});
            skLineSegment(sketch, "E1693", {"start": v(-12.52, 9.46) * mm, "end": v(-12.92, 9.9) * mm});
            skLineSegment(sketch, "E1694", {"start": v(-12.92, 9.9) * mm, "end": v(-13.13, 9.82) * mm});
            skLineSegment(sketch, "E1695", {"start": v(-13.13, 9.82) * mm, "end": v(-13.67, 9.61) * mm});
            skLineSegment(sketch, "E1696", {"start": v(-13.67, 9.61) * mm, "end": v(-13.69, 9.01) * mm});
            skLineSegment(sketch, "E1697", {"start": v(-13.69, 9.01) * mm, "end": v(-13.7, 8.91) * mm});
            skLineSegment(sketch, "E1698", {"start": v(-13.7, 8.91) * mm, "end": v(-13.7, 8.8) * mm});
            skLineSegment(sketch, "E1699", {"start": v(-13.7, 8.8) * mm, "end": v(-13.7, 8.7) * mm});
            skLineSegment(sketch, "E1700", {"start": v(-13.7, 8.7) * mm, "end": v(-13.69, 8.6) * mm});
            skLineSegment(sketch, "E1701", {"start": v(-13.69, 8.6) * mm, "end": v(-13.69, 8.49) * mm});
            skLineSegment(sketch, "E1702", {"start": v(-13.69, 8.49) * mm, "end": v(-13.68, 8.4) * mm});
            skLineSegment(sketch, "E1703", {"start": v(-13.68, 8.4) * mm, "end": v(-13.68, 8.3) * mm});
            skLineSegment(sketch, "E1704", {"start": v(-13.68, 8.3) * mm, "end": v(-13.67, 8.22) * mm});
            skLineSegment(sketch, "E1705", {"start": v(-13.67, 8.22) * mm, "end": v(-13.67, 8.13) * mm});
            skLineSegment(sketch, "E1706", {"start": v(-13.67, 8.13) * mm, "end": v(-13.66, 8.04) * mm});
            skLineSegment(sketch, "E1707", {"start": v(-13.66, 8.04) * mm, "end": v(-13.65, 7.97) * mm});
            skLineSegment(sketch, "E1708", {"start": v(-13.65, 7.97) * mm, "end": v(-13.65, 7.89) * mm});
            skLineSegment(sketch, "E1709", {"start": v(-13.65, 7.89) * mm, "end": v(-13.64, 7.82) * mm});
            skLineSegment(sketch, "E1710", {"start": v(-13.64, 7.82) * mm, "end": v(-13.63, 7.76) * mm});
            skLineSegment(sketch, "E1711", {"start": v(-13.63, 7.76) * mm, "end": v(-13.62, 7.7) * mm});
            skLineSegment(sketch, "E1712", {"start": v(-13.62, 7.7) * mm, "end": v(-13.61, 7.64) * mm});
            skLineSegment(sketch, "E1713", {"start": v(-13.61, 7.64) * mm, "end": v(-13.6, 7.58) * mm});
            skLineSegment(sketch, "E1714", {"start": v(-13.6, 7.58) * mm, "end": v(-13.55, 7.3) * mm});
            skLineSegment(sketch, "E1715", {"start": v(-13.55, 7.3) * mm, "end": v(-13.55, 7.28) * mm});
            skLineSegment(sketch, "E1716", {"start": v(-13.55, 7.28) * mm, "end": v(-13.55, 7.26) * mm});
            skLineSegment(sketch, "E1717", {"start": v(-13.55, 7.26) * mm, "end": v(-13.54, 7.22) * mm});
            skLineSegment(sketch, "E1718", {"start": v(-13.54, 7.22) * mm, "end": v(-13.55, 7.2) * mm});
            skLineSegment(sketch, "E1719", {"start": v(-13.55, 7.2) * mm, "end": v(-13.55, 7.17) * mm});
            skLineSegment(sketch, "E1720", {"start": v(-13.55, 7.17) * mm, "end": v(-13.56, 7.14) * mm});
            skLineSegment(sketch, "E1721", {"start": v(-13.56, 7.14) * mm, "end": v(-13.56, 7.12) * mm});
            skLineSegment(sketch, "E1722", {"start": v(-13.56, 7.12) * mm, "end": v(-13.57, 7.1) * mm});
            skLineSegment(sketch, "E1723", {"start": v(-13.57, 7.1) * mm, "end": v(-13.58, 7.08) * mm});
            skLineSegment(sketch, "E1724", {"start": v(-13.58, 7.08) * mm, "end": v(-13.6, 7.07) * mm});
            skLineSegment(sketch, "E1725", {"start": v(-13.6, 7.07) * mm, "end": v(-13.6, 7.06) * mm});
            skLineSegment(sketch, "E1726", {"start": v(-13.6, 7.06) * mm, "end": v(-13.6, 7.05) * mm});
            skLineSegment(sketch, "E1727", {"start": v(-13.6, 7.05) * mm, "end": v(-13.79, 6.98) * mm});
            skLineSegment(sketch, "E1728", {"start": v(-13.79, 6.98) * mm, "end": v(-14.03, 6.87) * mm});
            skLineSegment(sketch, "E1729", {"start": v(-14.03, 6.87) * mm, "end": v(-14.21, 6.78) * mm});
            skLineSegment(sketch, "E1730", {"start": v(-14.21, 6.78) * mm, "end": v(-14.21, 6.79) * mm});
            skLineSegment(sketch, "E1731", {"start": v(-14.21, 6.79) * mm, "end": v(-14.23, 6.78) * mm});
            skLineSegment(sketch, "E1732", {"start": v(-14.23, 6.78) * mm, "end": v(-14.24, 6.78) * mm});
            skLineSegment(sketch, "E1733", {"start": v(-14.24, 6.78) * mm, "end": v(-14.25, 6.78) * mm});
            skLineSegment(sketch, "E1734", {"start": v(-14.25, 6.78) * mm, "end": v(-14.27, 6.79) * mm});
            skLineSegment(sketch, "E1735", {"start": v(-14.27, 6.79) * mm, "end": v(-14.3, 6.8) * mm});
            skLineSegment(sketch, "E1736", {"start": v(-14.3, 6.8) * mm, "end": v(-14.31, 6.8) * mm});
            skLineSegment(sketch, "E1737", {"start": v(-14.31, 6.8) * mm, "end": v(-14.33, 6.82) * mm});
            skLineSegment(sketch, "E1738", {"start": v(-14.33, 6.82) * mm, "end": v(-14.35, 6.84) * mm});
            skLineSegment(sketch, "E1739", {"start": v(-14.35, 6.84) * mm, "end": v(-14.37, 6.86) * mm});
            skLineSegment(sketch, "E1740", {"start": v(-14.37, 6.86) * mm, "end": v(-14.37, 6.86) * mm});
            skLineSegment(sketch, "E1741", {"start": v(-14.37, 6.86) * mm, "end": v(-14.4, 6.88) * mm});
            skLineSegment(sketch, "E1742", {"start": v(-14.4, 6.88) * mm, "end": v(-14.4, 6.88) * mm});
            skLineSegment(sketch, "E1743", {"start": v(-14.4, 6.88) * mm, "end": v(-14.57, 7.1) * mm});
            skLineSegment(sketch, "E1744", {"start": v(-14.57, 7.1) * mm, "end": v(-14.61, 7.15) * mm});
            skLineSegment(sketch, "E1745", {"start": v(-14.61, 7.15) * mm, "end": v(-14.66, 7.2) * mm});
            skLineSegment(sketch, "E1746", {"start": v(-14.66, 7.2) * mm, "end": v(-14.7, 7.26) * mm});
            skLineSegment(sketch, "E1747", {"start": v(-14.7, 7.26) * mm, "end": v(-14.75, 7.31) * mm});
            skLineSegment(sketch, "E1748", {"start": v(-14.75, 7.31) * mm, "end": v(-14.8, 7.37) * mm});
            skLineSegment(sketch, "E1749", {"start": v(-14.8, 7.37) * mm, "end": v(-14.86, 7.43) * mm});
            skLineSegment(sketch, "E1750", {"start": v(-14.86, 7.43) * mm, "end": v(-14.91, 7.49) * mm});
            skLineSegment(sketch, "E1751", {"start": v(-14.91, 7.49) * mm, "end": v(-14.97, 7.55) * mm});
            skLineSegment(sketch, "E1752", {"start": v(-14.97, 7.55) * mm, "end": v(-15.03, 7.61) * mm});
            skLineSegment(sketch, "E1753", {"start": v(-15.03, 7.61) * mm, "end": v(-15.1, 7.68) * mm});
            skLineSegment(sketch, "E1754", {"start": v(-15.1, 7.68) * mm, "end": v(-15.15, 7.74) * mm});
            skLineSegment(sketch, "E1755", {"start": v(-15.15, 7.74) * mm, "end": v(-15.22, 7.8) * mm});
            skLineSegment(sketch, "E1756", {"start": v(-15.22, 7.8) * mm, "end": v(-15.3, 7.87) * mm});
            skLineSegment(sketch, "E1757", {"start": v(-15.3, 7.87) * mm, "end": v(-15.37, 7.94) * mm});
            skLineSegment(sketch, "E1758", {"start": v(-15.37, 7.94) * mm, "end": v(-15.45, 8.01) * mm});
            skLineSegment(sketch, "E1759", {"start": v(-15.45, 8.01) * mm, "end": v(-15.53, 8.08) * mm});
            skLineSegment(sketch, "E1760", {"start": v(-15.53, 8.08) * mm, "end": v(-15.62, 8.16) * mm});
            skLineSegment(sketch, "E1761", {"start": v(-15.62, 8.16) * mm, "end": v(-16.08, 8.53) * mm});
            skLineSegment(sketch, "E1762", {"start": v(-16.08, 8.53) * mm, "end": v(-16.34, 8.4) * mm});
            skLineSegment(sketch, "E1763", {"start": v(-16.34, 8.4) * mm, "end": v(-16.78, 8.16) * mm});
            skLineSegment(sketch, "E1764", {"start": v(-16.78, 8.16) * mm, "end": v(-16.73, 7.66) * mm});
            skLineSegment(sketch, "E1765", {"start": v(-16.73, 7.66) * mm, "end": v(-16.72, 7.54) * mm});
            skLineSegment(sketch, "E1766", {"start": v(-16.72, 7.54) * mm, "end": v(-16.7, 7.43) * mm});
            skLineSegment(sketch, "E1767", {"start": v(-16.7, 7.43) * mm, "end": v(-16.69, 7.32) * mm});
            skLineSegment(sketch, "E1768", {"start": v(-16.69, 7.32) * mm, "end": v(-16.68, 7.22) * mm});
            skLineSegment(sketch, "E1769", {"start": v(-16.68, 7.22) * mm, "end": v(-16.66, 7.12) * mm});
            skLineSegment(sketch, "E1770", {"start": v(-16.66, 7.12) * mm, "end": v(-16.64, 7.03) * mm});
            skLineSegment(sketch, "E1771", {"start": v(-16.64, 7.03) * mm, "end": v(-16.62, 6.94) * mm});
            skLineSegment(sketch, "E1772", {"start": v(-16.62, 6.94) * mm, "end": v(-16.6, 6.85) * mm});
            skLineSegment(sketch, "E1773", {"start": v(-16.6, 6.85) * mm, "end": v(-16.59, 6.77) * mm});
            skLineSegment(sketch, "E1774", {"start": v(-16.59, 6.77) * mm, "end": v(-16.57, 6.7) * mm});
            skLineSegment(sketch, "E1775", {"start": v(-16.57, 6.7) * mm, "end": v(-16.55, 6.62) * mm});
            skLineSegment(sketch, "E1776", {"start": v(-16.55, 6.62) * mm, "end": v(-16.53, 6.56) * mm});
            skLineSegment(sketch, "E1777", {"start": v(-16.53, 6.56) * mm, "end": v(-16.52, 6.5) * mm});
            skLineSegment(sketch, "E1778", {"start": v(-16.52, 6.5) * mm, "end": v(-16.5, 6.44) * mm});
            skLineSegment(sketch, "E1779", {"start": v(-16.5, 6.44) * mm, "end": v(-16.48, 6.4) * mm});
            skLineSegment(sketch, "E1780", {"start": v(-16.48, 6.4) * mm, "end": v(-16.47, 6.36) * mm});
            skLineSegment(sketch, "E1781", {"start": v(-16.47, 6.36) * mm, "end": v(-16.46, 6.32) * mm});
            skLineSegment(sketch, "E1782", {"start": v(-16.46, 6.32) * mm, "end": v(-16.44, 6.3) * mm});
            skLineSegment(sketch, "E1783", {"start": v(-16.44, 6.3) * mm, "end": v(-16.44, 6.27) * mm});
            skLineSegment(sketch, "E1784", {"start": v(-16.44, 6.27) * mm, "end": v(-16.34, 6.05) * mm});
            skLineSegment(sketch, "E1785", {"start": v(-16.34, 6.05) * mm, "end": v(-16.34, 6.05) * mm});
            skLineSegment(sketch, "E1786", {"start": v(-16.34, 6.05) * mm, "end": v(-16.32, 5.99) * mm});
            skLineSegment(sketch, "E1787", {"start": v(-16.32, 5.99) * mm, "end": v(-16.32, 5.98) * mm});
            skLineSegment(sketch, "E1788", {"start": v(-16.32, 5.98) * mm, "end": v(-16.3, 5.93) * mm});
            skLineSegment(sketch, "E1789", {"start": v(-16.3, 5.93) * mm, "end": v(-16.3, 5.92) * mm});
            skLineSegment(sketch, "E1790", {"start": v(-16.3, 5.92) * mm, "end": v(-16.29, 5.88) * mm});
            skLineSegment(sketch, "E1791", {"start": v(-16.29, 5.88) * mm, "end": v(-16.3, 5.85) * mm});
            skLineSegment(sketch, "E1792", {"start": v(-16.3, 5.85) * mm, "end": v(-16.3, 5.82) * mm});
            skLineSegment(sketch, "E1793", {"start": v(-16.3, 5.82) * mm, "end": v(-16.28, 5.79) * mm});
            skLineSegment(sketch, "E1794", {"start": v(-16.28, 5.79) * mm, "end": v(-16.29, 5.77) * mm});
            skLineSegment(sketch, "E1795", {"start": v(-16.29, 5.77) * mm, "end": v(-16.3, 5.74) * mm});
            skLineSegment(sketch, "E1796", {"start": v(-16.3, 5.74) * mm, "end": v(-16.3, 5.72) * mm});
            skLineSegment(sketch, "E1797", {"start": v(-16.3, 5.72) * mm, "end": v(-16.3, 5.69) * mm});
            skLineSegment(sketch, "E1798", {"start": v(-16.3, 5.69) * mm, "end": v(-16.31, 5.66) * mm});
            skLineSegment(sketch, "E1799", {"start": v(-16.31, 5.66) * mm, "end": v(-16.33, 5.65) * mm});
            skLineSegment(sketch, "E1800", {"start": v(-16.33, 5.65) * mm, "end": v(-16.34, 5.64) * mm});
            skLineSegment(sketch, "E1801", {"start": v(-16.34, 5.64) * mm, "end": v(-16.5, 5.53) * mm});
            skLineSegment(sketch, "E1802", {"start": v(-16.5, 5.53) * mm, "end": v(-16.71, 5.4) * mm});
            skLineSegment(sketch, "E1803", {"start": v(-16.71, 5.4) * mm, "end": v(-16.88, 5.28) * mm});
            skLineSegment(sketch, "E1804", {"start": v(-16.88, 5.28) * mm, "end": v(-16.88, 5.28) * mm});
            skLineSegment(sketch, "E1805", {"start": v(-16.88, 5.28) * mm, "end": v(-16.9, 5.27) * mm});
            skLineSegment(sketch, "E1806", {"start": v(-16.9, 5.27) * mm, "end": v(-16.92, 5.26) * mm});
            skLineSegment(sketch, "E1807", {"start": v(-16.92, 5.26) * mm, "end": v(-16.93, 5.27) * mm});
            skLineSegment(sketch, "E1808", {"start": v(-16.93, 5.27) * mm, "end": v(-16.94, 5.26) * mm});
            skLineSegment(sketch, "E1809", {"start": v(-16.94, 5.26) * mm, "end": v(-16.96, 5.27) * mm});
            skLineSegment(sketch, "E1810", {"start": v(-16.96, 5.27) * mm, "end": v(-16.99, 5.28) * mm});
            skLineSegment(sketch, "E1811", {"start": v(-16.99, 5.28) * mm, "end": v(-17.01, 5.29) * mm});
            skLineSegment(sketch, "E1812", {"start": v(-17.01, 5.29) * mm, "end": v(-17.02, 5.28) * mm});
            skLineSegment(sketch, "E1813", {"start": v(-17.02, 5.28) * mm, "end": v(-17.04, 5.3) * mm});
            skLineSegment(sketch, "E1814", {"start": v(-17.04, 5.3) * mm, "end": v(-17.05, 5.3) * mm});
            skLineSegment(sketch, "E1815", {"start": v(-17.05, 5.3) * mm, "end": v(-17.07, 5.32) * mm});
            skLineSegment(sketch, "E1816", {"start": v(-17.07, 5.32) * mm, "end": v(-17.08, 5.31) * mm});
            skLineSegment(sketch, "E1817", {"start": v(-17.08, 5.31) * mm, "end": v(-17.1, 5.34) * mm});
            skLineSegment(sketch, "E1818", {"start": v(-17.1, 5.34) * mm, "end": v(-17.1, 5.33) * mm});
            skLineSegment(sketch, "E1819", {"start": v(-17.1, 5.33) * mm, "end": v(-17.13, 5.36) * mm});
            skLineSegment(sketch, "E1820", {"start": v(-17.13, 5.36) * mm, "end": v(-17.14, 5.36) * mm});
            skLineSegment(sketch, "E1821", {"start": v(-17.14, 5.36) * mm, "end": v(-17.17, 5.38) * mm});
            skLineSegment(sketch, "E1822", {"start": v(-17.17, 5.38) * mm, "end": v(-17.17, 5.38) * mm});
            skLineSegment(sketch, "E1823", {"start": v(-17.17, 5.38) * mm, "end": v(-17.32, 5.53) * mm});
            skLineSegment(sketch, "E1824", {"start": v(-17.32, 5.53) * mm, "end": v(-17.35, 5.56) * mm});
            skLineSegment(sketch, "E1825", {"start": v(-17.35, 5.56) * mm, "end": v(-17.4, 5.6) * mm});
            skLineSegment(sketch, "E1826", {"start": v(-17.4, 5.6) * mm, "end": v(-17.44, 5.65) * mm});
            skLineSegment(sketch, "E1827", {"start": v(-17.44, 5.65) * mm, "end": v(-17.48, 5.68) * mm});
            skLineSegment(sketch, "E1828", {"start": v(-17.48, 5.68) * mm, "end": v(-17.54, 5.73) * mm});
            skLineSegment(sketch, "E1829", {"start": v(-17.54, 5.73) * mm, "end": v(-17.6, 5.78) * mm});
            skLineSegment(sketch, "E1830", {"start": v(-17.6, 5.78) * mm, "end": v(-17.64, 5.82) * mm});
            skLineSegment(sketch, "E1831", {"start": v(-17.64, 5.82) * mm, "end": v(-17.7, 5.86) * mm});
            skLineSegment(sketch, "E1832", {"start": v(-17.7, 5.86) * mm, "end": v(-17.76, 5.9) * mm});
            skLineSegment(sketch, "E1833", {"start": v(-17.76, 5.9) * mm, "end": v(-17.82, 5.96) * mm});
            skLineSegment(sketch, "E1834", {"start": v(-17.82, 5.96) * mm, "end": v(-17.89, 6) * mm});
            skLineSegment(sketch, "E1835", {"start": v(-17.89, 6) * mm, "end": v(-17.96, 6.05) * mm});
            skLineSegment(sketch, "E1836", {"start": v(-17.96, 6.05) * mm, "end": v(-18.03, 6.1) * mm});
            skLineSegment(sketch, "E1837", {"start": v(-18.03, 6.1) * mm, "end": v(-18.11, 6.15) * mm});
            skLineSegment(sketch, "E1838", {"start": v(-18.11, 6.15) * mm, "end": v(-18.2, 6.2) * mm});
            skLineSegment(sketch, "E1839", {"start": v(-18.2, 6.2) * mm, "end": v(-18.28, 6.25) * mm});
            skLineSegment(sketch, "E1840", {"start": v(-18.28, 6.25) * mm, "end": v(-18.37, 6.3) * mm});
            skLineSegment(sketch, "E1841", {"start": v(-18.37, 6.3) * mm, "end": v(-18.47, 6.35) * mm});
            skLineSegment(sketch, "E1842", {"start": v(-18.47, 6.35) * mm, "end": v(-18.57, 6.4) * mm});
            skLineSegment(sketch, "E1843", {"start": v(-18.57, 6.4) * mm, "end": v(-19.06, 6.64) * mm});
            skLineSegment(sketch, "E1844", {"start": v(-19.06, 6.64) * mm, "end": v(-19.18, 6.54) * mm});
            skLineSegment(sketch, "E1845", {"start": v(-19.18, 6.54) * mm, "end": v(-19.6, 6.2) * mm});
            skLineSegment(sketch, "E1846", {"start": v(-19.6, 6.2) * mm, "end": v(-19.64, 6.16) * mm});
            skLineSegment(sketch, "E1847", {"start": v(-19.64, 6.16) * mm, "end": v(-19.47, 5.6) * mm});
            skLineSegment(sketch, "E1848", {"start": v(-19.47, 5.6) * mm, "end": v(-19.44, 5.5) * mm});
            skLineSegment(sketch, "E1849", {"start": v(-19.44, 5.5) * mm, "end": v(-19.4, 5.39) * mm});
            skLineSegment(sketch, "E1850", {"start": v(-19.4, 5.39) * mm, "end": v(-19.37, 5.3) * mm});
            skLineSegment(sketch, "E1851", {"start": v(-19.37, 5.3) * mm, "end": v(-19.34, 5.2) * mm});
            skLineSegment(sketch, "E1852", {"start": v(-19.34, 5.2) * mm, "end": v(-19.3, 5.11) * mm});
            skLineSegment(sketch, "E1853", {"start": v(-19.3, 5.11) * mm, "end": v(-19.27, 5.03) * mm});
            skLineSegment(sketch, "E1854", {"start": v(-19.27, 5.03) * mm, "end": v(-19.23, 4.96) * mm});
            skLineSegment(sketch, "E1855", {"start": v(-19.23, 4.96) * mm, "end": v(-19.2, 4.89) * mm});
            skLineSegment(sketch, "E1856", {"start": v(-19.2, 4.89) * mm, "end": v(-19.17, 4.83) * mm});
            skLineSegment(sketch, "E1857", {"start": v(-19.17, 4.83) * mm, "end": v(-19.14, 4.77) * mm});
            skLineSegment(sketch, "E1858", {"start": v(-19.14, 4.77) * mm, "end": v(-19.11, 4.72) * mm});
            skLineSegment(sketch, "E1859", {"start": v(-19.11, 4.72) * mm, "end": v(-19.09, 4.68) * mm});
            skLineSegment(sketch, "E1860", {"start": v(-19.09, 4.68) * mm, "end": v(-19.07, 4.65) * mm});
            skLineSegment(sketch, "E1861", {"start": v(-19.07, 4.65) * mm, "end": v(-19.05, 4.62) * mm});
            skLineSegment(sketch, "E1862", {"start": v(-19.05, 4.62) * mm, "end": v(-19.03, 4.6) * mm});
            skLineSegment(sketch, "E1863", {"start": v(-19.03, 4.6) * mm, "end": v(-19.02, 4.58) * mm});
            skLineSegment(sketch, "E1864", {"start": v(-19.02, 4.58) * mm, "end": v(-18.85, 4.42) * mm});
            skLineSegment(sketch, "E1865", {"start": v(-18.85, 4.42) * mm, "end": v(-18.86, 4.41) * mm});
            skLineSegment(sketch, "E1866", {"start": v(-18.86, 4.41) * mm, "end": v(-18.8, 4.35) * mm});
            skLineSegment(sketch, "E1867", {"start": v(-18.8, 4.35) * mm, "end": v(-18.8, 4.34) * mm});
            skLineSegment(sketch, "E1868", {"start": v(-18.8, 4.34) * mm, "end": v(-18.74, 4.27) * mm});
            skLineSegment(sketch, "E1869", {"start": v(-18.74, 4.27) * mm, "end": v(-18.75, 4.26) * mm});
            skLineSegment(sketch, "E1870", {"start": v(-18.75, 4.26) * mm, "end": v(-18.7, 4.2) * mm});
            skLineSegment(sketch, "E1871", {"start": v(-18.7, 4.2) * mm, "end": v(-18.7, 4.2) * mm});
            skLineSegment(sketch, "E1872", {"start": v(-18.7, 4.2) * mm, "end": v(-18.67, 4.14) * mm});
            skLineSegment(sketch, "E1873", {"start": v(-18.67, 4.14) * mm, "end": v(-18.67, 4.13) * mm});
            skLineSegment(sketch, "E1874", {"start": v(-18.67, 4.13) * mm, "end": v(-18.64, 4.08) * mm});
            skLineSegment(sketch, "E1875", {"start": v(-18.64, 4.08) * mm, "end": v(-18.65, 4.06) * mm});
            skLineSegment(sketch, "E1876", {"start": v(-18.65, 4.06) * mm, "end": v(-18.62, 4.03) * mm});
            skLineSegment(sketch, "E1877", {"start": v(-18.62, 4.03) * mm, "end": v(-18.63, 4) * mm});
            skLineSegment(sketch, "E1878", {"start": v(-18.63, 4) * mm, "end": v(-18.61, 3.97) * mm});
            skLineSegment(sketch, "E1879", {"start": v(-18.61, 3.97) * mm, "end": v(-18.63, 3.96) * mm});
            skLineSegment(sketch, "E1880", {"start": v(-18.63, 3.96) * mm, "end": v(-18.6, 3.93) * mm});
            skLineSegment(sketch, "E1881", {"start": v(-18.6, 3.93) * mm, "end": v(-18.62, 3.9) * mm});
            skLineSegment(sketch, "E1882", {"start": v(-18.62, 3.9) * mm, "end": v(-18.61, 3.89) * mm});
            skLineSegment(sketch, "E1883", {"start": v(-18.61, 3.89) * mm, "end": v(-18.63, 3.87) * mm});
            skLineSegment(sketch, "E1884", {"start": v(-18.63, 3.87) * mm, "end": v(-18.63, 3.84) * mm});
            skLineSegment(sketch, "E1885", {"start": v(-18.63, 3.84) * mm, "end": v(-18.64, 3.8) * mm});
            skLineSegment(sketch, "E1886", {"start": v(-18.64, 3.8) * mm, "end": v(-18.65, 3.8) * mm});
            skLineSegment(sketch, "E1887", {"start": v(-18.65, 3.8) * mm, "end": v(-18.8, 3.64) * mm});
            skLineSegment(sketch, "E1888", {"start": v(-18.8, 3.64) * mm, "end": v(-18.93, 3.48) * mm});
            skLineSegment(sketch, "E1889", {"start": v(-18.93, 3.48) * mm, "end": v(-19.07, 3.32) * mm});
            skLineSegment(sketch, "E1890", {"start": v(-19.07, 3.32) * mm, "end": v(-19.07, 3.33) * mm});
            skLineSegment(sketch, "E1891", {"start": v(-19.07, 3.33) * mm, "end": v(-19.1, 3.3) * mm});
            skLineSegment(sketch, "E1892", {"start": v(-19.1, 3.3) * mm, "end": v(-19.1, 3.3) * mm});
            skLineSegment(sketch, "E1893", {"start": v(-19.1, 3.3) * mm, "end": v(-19.12, 3.29) * mm});
            skLineSegment(sketch, "E1894", {"start": v(-19.12, 3.29) * mm, "end": v(-19.14, 3.3) * mm});
            skLineSegment(sketch, "E1895", {"start": v(-19.14, 3.3) * mm, "end": v(-19.15, 3.28) * mm});
            skLineSegment(sketch, "E1896", {"start": v(-19.15, 3.28) * mm, "end": v(-19.17, 3.29) * mm});
            skLineSegment(sketch, "E1897", {"start": v(-19.17, 3.29) * mm, "end": v(-19.19, 3.27) * mm});
            skLineSegment(sketch, "E1898", {"start": v(-19.19, 3.27) * mm, "end": v(-19.21, 3.28) * mm});
            skLineSegment(sketch, "E1899", {"start": v(-19.21, 3.28) * mm, "end": v(-19.23, 3.27) * mm});
            skLineSegment(sketch, "E1900", {"start": v(-19.23, 3.27) * mm, "end": v(-19.25, 3.29) * mm});
            skLineSegment(sketch, "E1901", {"start": v(-19.25, 3.29) * mm, "end": v(-19.27, 3.27) * mm});
            skLineSegment(sketch, "E1902", {"start": v(-19.27, 3.27) * mm, "end": v(-19.3, 3.3) * mm});
            skLineSegment(sketch, "E1903", {"start": v(-19.3, 3.3) * mm, "end": v(-19.3, 3.28) * mm});
            skLineSegment(sketch, "E1904", {"start": v(-19.3, 3.28) * mm, "end": v(-19.34, 3.3) * mm});
            skLineSegment(sketch, "E1905", {"start": v(-19.34, 3.3) * mm, "end": v(-19.35, 3.3) * mm});
            skLineSegment(sketch, "E1906", {"start": v(-19.35, 3.3) * mm, "end": v(-19.4, 3.32) * mm});
            skLineSegment(sketch, "E1907", {"start": v(-19.4, 3.32) * mm, "end": v(-19.4, 3.31) * mm});
            skLineSegment(sketch, "E1908", {"start": v(-19.4, 3.31) * mm, "end": v(-19.44, 3.34) * mm});
            skLineSegment(sketch, "E1909", {"start": v(-19.44, 3.34) * mm, "end": v(-19.44, 3.33) * mm});
            skLineSegment(sketch, "E1910", {"start": v(-19.44, 3.33) * mm, "end": v(-19.49, 3.36) * mm});
            skLineSegment(sketch, "E1911", {"start": v(-19.49, 3.36) * mm, "end": v(-19.5, 3.36) * mm});
            skLineSegment(sketch, "E1912", {"start": v(-19.5, 3.36) * mm, "end": v(-19.72, 3.51) * mm});
            skLineSegment(sketch, "E1913", {"start": v(-19.72, 3.51) * mm, "end": v(-19.75, 3.53) * mm});
            skLineSegment(sketch, "E1914", {"start": v(-19.75, 3.53) * mm, "end": v(-19.79, 3.55) * mm});
            skLineSegment(sketch, "E1915", {"start": v(-19.79, 3.55) * mm, "end": v(-19.82, 3.57) * mm});
            skLineSegment(sketch, "E1916", {"start": v(-19.82, 3.57) * mm, "end": v(-19.86, 3.6) * mm});
            skLineSegment(sketch, "E1917", {"start": v(-19.86, 3.6) * mm, "end": v(-19.9, 3.61) * mm});
            skLineSegment(sketch, "E1918", {"start": v(-19.9, 3.61) * mm, "end": v(-19.94, 3.64) * mm});
            skLineSegment(sketch, "E1919", {"start": v(-19.94, 3.64) * mm, "end": v(-19.99, 3.66) * mm});
            skLineSegment(sketch, "E1920", {"start": v(-19.99, 3.66) * mm, "end": v(-20.04, 3.68) * mm});
            skLineSegment(sketch, "E1921", {"start": v(-20.04, 3.68) * mm, "end": v(-20.1, 3.7) * mm});
            skLineSegment(sketch, "E1922", {"start": v(-20.1, 3.7) * mm, "end": v(-20.15, 3.73) * mm});
            skLineSegment(sketch, "E1923", {"start": v(-20.15, 3.73) * mm, "end": v(-20.22, 3.75) * mm});
            skLineSegment(sketch, "E1924", {"start": v(-20.22, 3.75) * mm, "end": v(-20.28, 3.77) * mm});
            skLineSegment(sketch, "E1925", {"start": v(-20.28, 3.77) * mm, "end": v(-20.36, 3.8) * mm});
            skLineSegment(sketch, "E1926", {"start": v(-20.36, 3.8) * mm, "end": v(-20.43, 3.82) * mm});
            skLineSegment(sketch, "E1927", {"start": v(-20.43, 3.82) * mm, "end": v(-20.52, 3.84) * mm});
            skLineSegment(sketch, "E1928", {"start": v(-20.52, 3.84) * mm, "end": v(-20.6, 3.86) * mm});
            skLineSegment(sketch, "E1929", {"start": v(-20.6, 3.86) * mm, "end": v(-20.7, 3.88) * mm});
            skLineSegment(sketch, "E1930", {"start": v(-20.7, 3.88) * mm, "end": v(-20.8, 3.9) * mm});
            skLineSegment(sketch, "E1931", {"start": v(-20.8, 3.9) * mm, "end": v(-20.92, 3.91) * mm});
            skLineSegment(sketch, "E1932", {"start": v(-20.92, 3.91) * mm, "end": v(-21.03, 3.92) * mm});
            skLineSegment(sketch, "E1933", {"start": v(-21.03, 3.92) * mm, "end": v(-21.56, 3.96) * mm});
            skLineSegment(sketch, "E1934", {"start": v(-21.56, 3.96) * mm, "end": v(-21.67, 3.81) * mm});
            skLineSegment(sketch, "E1935", {"start": v(-21.67, 3.81) * mm, "end": v(-21.92, 3.37) * mm});
            skLineSegment(sketch, "E1936", {"start": v(-21.92, 3.37) * mm, "end": v(-21.66, 2.97) * mm});
            skLineSegment(sketch, "E1937", {"start": v(-21.66, 2.97) * mm, "end": v(-21.6, 2.87) * mm});
            skLineSegment(sketch, "E1938", {"start": v(-21.6, 2.87) * mm, "end": v(-21.53, 2.78) * mm});
            skLineSegment(sketch, "E1939", {"start": v(-21.53, 2.78) * mm, "end": v(-21.47, 2.7) * mm});
            skLineSegment(sketch, "E1940", {"start": v(-21.47, 2.7) * mm, "end": v(-21.4, 2.61) * mm});
            skLineSegment(sketch, "E1941", {"start": v(-21.4, 2.61) * mm, "end": v(-21.34, 2.54) * mm});
            skLineSegment(sketch, "E1942", {"start": v(-21.34, 2.54) * mm, "end": v(-21.29, 2.48) * mm});
            skLineSegment(sketch, "E1943", {"start": v(-21.29, 2.48) * mm, "end": v(-21.23, 2.42) * mm});
            skLineSegment(sketch, "E1944", {"start": v(-21.23, 2.42) * mm, "end": v(-21.18, 2.37) * mm});
            skLineSegment(sketch, "E1945", {"start": v(-21.18, 2.37) * mm, "end": v(-21.13, 2.32) * mm});
            skLineSegment(sketch, "E1946", {"start": v(-21.13, 2.32) * mm, "end": v(-21.08, 2.28) * mm});
            skLineSegment(sketch, "E1947", {"start": v(-21.08, 2.28) * mm, "end": v(-21.04, 2.25) * mm});
            skLineSegment(sketch, "E1948", {"start": v(-21.04, 2.25) * mm, "end": v(-21, 2.22) * mm});
            skLineSegment(sketch, "E1949", {"start": v(-21, 2.22) * mm, "end": v(-20.96, 2.2) * mm});
            skLineSegment(sketch, "E1950", {"start": v(-20.96, 2.2) * mm, "end": v(-20.96, 2.2) * mm});
            skLineSegment(sketch, "E1951", {"start": v(-20.96, 2.2) * mm, "end": v(-20.9, 2.18) * mm});
            skLineSegment(sketch, "E1952", {"start": v(-20.9, 2.18) * mm, "end": v(-20.9, 2.17) * mm});
            skLineSegment(sketch, "E1953", {"start": v(-20.9, 2.17) * mm, "end": v(-20.68, 2.12) * mm});
            skLineSegment(sketch, "E1954", {"start": v(-20.68, 2.12) * mm, "end": v(-20.68, 2.1) * mm});
            skLineSegment(sketch, "E1955", {"start": v(-20.68, 2.1) * mm, "end": v(-20.5, 2.03) * mm});
            skLineSegment(sketch, "E1956", {"start": v(-20.5, 2.03) * mm, "end": v(-20.5, 2) * mm});
            skLineSegment(sketch, "E1957", {"start": v(-20.5, 2) * mm, "end": v(-20.35, 1.93) * mm});
            skLineSegment(sketch, "E1958", {"start": v(-20.35, 1.93) * mm, "end": v(-20.35, 1.88) * mm});
            skLineSegment(sketch, "E1959", {"start": v(-20.35, 1.88) * mm, "end": v(-20.24, 1.83) * mm});
            skLineSegment(sketch, "E1960", {"start": v(-20.24, 1.83) * mm, "end": v(-20.25, 1.77) * mm});
            skLineSegment(sketch, "E1961", {"start": v(-20.25, 1.77) * mm, "end": v(-20.17, 1.72) * mm});
            skLineSegment(sketch, "E1962", {"start": v(-20.17, 1.72) * mm, "end": v(-20.18, 1.65) * mm});
            skLineSegment(sketch, "E1963", {"start": v(-20.18, 1.65) * mm, "end": v(-20.14, 1.62) * mm});
            skLineSegment(sketch, "E1964", {"start": v(-20.14, 1.62) * mm, "end": v(-20.15, 1.58) * mm});
            skLineSegment(sketch, "E1965", {"start": v(-20.15, 1.58) * mm, "end": v(-20.13, 1.57) * mm});
            skLineSegment(sketch, "E1966", {"start": v(-20.13, 1.57) * mm, "end": v(-20.15, 1.53) * mm});
            skLineSegment(sketch, "E1967", {"start": v(-20.15, 1.53) * mm, "end": v(-20.15, 1.5) * mm});
            skLineSegment(sketch, "E1968", {"start": v(-20.15, 1.5) * mm, "end": v(-20.15, 1.48) * mm});
            skLineSegment(sketch, "E1969", {"start": v(-20.15, 1.48) * mm, "end": v(-20.16, 1.47) * mm});
            skLineSegment(sketch, "E1970", {"start": v(-20.16, 1.47) * mm, "end": v(-20.2, 1.32) * mm});
            skLineSegment(sketch, "E1971", {"start": v(-20.2, 1.32) * mm, "end": v(-20.26, 1.16) * mm});
            skLineSegment(sketch, "E1972", {"start": v(-20.26, 1.16) * mm, "end": v(-20.31, 0.95) * mm});
            skLineSegment(sketch, "E1973", {"start": v(-20.31, 0.95) * mm, "end": v(-20.32, 0.95) * mm});
            skLineSegment(sketch, "E1974", {"start": v(-20.32, 0.95) * mm, "end": v(-20.33, 0.9) * mm});
            skLineSegment(sketch, "E1975", {"start": v(-20.33, 0.9) * mm, "end": v(-20.35, 0.9) * mm});
            skLineSegment(sketch, "E1976", {"start": v(-20.35, 0.9) * mm, "end": v(-20.36, 0.87) * mm});
            skLineSegment(sketch, "E1977", {"start": v(-20.36, 0.87) * mm, "end": v(-20.38, 0.87) * mm});
            skLineSegment(sketch, "E1978", {"start": v(-20.38, 0.87) * mm, "end": v(-20.4, 0.84) * mm});
            skLineSegment(sketch, "E1979", {"start": v(-20.4, 0.84) * mm, "end": v(-20.43, 0.84) * mm});
            skLineSegment(sketch, "E1980", {"start": v(-20.43, 0.84) * mm, "end": v(-20.44, 0.8) * mm});
            skLineSegment(sketch, "E1981", {"start": v(-20.44, 0.8) * mm, "end": v(-20.48, 0.8) * mm});
            skLineSegment(sketch, "E1982", {"start": v(-20.48, 0.8) * mm, "end": v(-20.49, 0.78) * mm});
            skLineSegment(sketch, "E1983", {"start": v(-20.49, 0.78) * mm, "end": v(-20.53, 0.78) * mm});
            skLineSegment(sketch, "E1984", {"start": v(-20.53, 0.78) * mm, "end": v(-20.54, 0.76) * mm});
            skLineSegment(sketch, "E1985", {"start": v(-20.54, 0.76) * mm, "end": v(-20.6, 0.77) * mm});
            skLineSegment(sketch, "E1986", {"start": v(-20.6, 0.77) * mm, "end": v(-20.6, 0.75) * mm});
            skLineSegment(sketch, "E1987", {"start": v(-20.6, 0.75) * mm, "end": v(-20.66, 0.75) * mm});
            skLineSegment(sketch, "E1988", {"start": v(-20.66, 0.75) * mm, "end": v(-20.67, 0.74) * mm});
            skLineSegment(sketch, "E1989", {"start": v(-20.67, 0.74) * mm, "end": v(-20.73, 0.75) * mm});
            skLineSegment(sketch, "E1990", {"start": v(-20.73, 0.75) * mm, "end": v(-20.74, 0.73) * mm});
            skLineSegment(sketch, "E1991", {"start": v(-20.74, 0.73) * mm, "end": v(-20.8, 0.75) * mm});
            skLineSegment(sketch, "E1992", {"start": v(-20.8, 0.75) * mm, "end": v(-20.81, 0.73) * mm});
            skLineSegment(sketch, "E1993", {"start": v(-20.81, 0.73) * mm, "end": v(-20.88, 0.75) * mm});
            skLineSegment(sketch, "E1994", {"start": v(-20.88, 0.75) * mm, "end": v(-20.89, 0.74) * mm});
            skLineSegment(sketch, "E1995", {"start": v(-20.89, 0.74) * mm, "end": v(-20.96, 0.76) * mm});
            skLineSegment(sketch, "E1996", {"start": v(-20.96, 0.76) * mm, "end": v(-20.97, 0.75) * mm});
            skLineSegment(sketch, "E1997", {"start": v(-20.97, 0.75) * mm, "end": v(-21.04, 0.78) * mm});
            skLineSegment(sketch, "E1998", {"start": v(-21.04, 0.78) * mm, "end": v(-21.05, 0.77) * mm});
            skLineSegment(sketch, "E1999", {"start": v(-21.05, 0.77) * mm, "end": v(-21.25, 0.84) * mm});
            skLineSegment(sketch, "E2000", {"start": v(-21.25, 0.84) * mm, "end": v(-21.25, 0.84) * mm});
            skLineSegment(sketch, "E2001", {"start": v(-21.25, 0.84) * mm, "end": v(-21.26, 0.84) * mm});
            skLineSegment(sketch, "E2002", {"start": v(-21.26, 0.84) * mm, "end": v(-21.27, 0.84) * mm});
            skLineSegment(sketch, "E2003", {"start": v(-21.27, 0.84) * mm, "end": v(-21.28, 0.84) * mm});
            skLineSegment(sketch, "E2004", {"start": v(-21.28, 0.84) * mm, "end": v(-21.3, 0.84) * mm});
            skLineSegment(sketch, "E2005", {"start": v(-21.3, 0.84) * mm, "end": v(-21.32, 0.84) * mm});
            skLineSegment(sketch, "E2006", {"start": v(-21.32, 0.84) * mm, "end": v(-21.35, 0.85) * mm});
            skLineSegment(sketch, "E2007", {"start": v(-21.35, 0.85) * mm, "end": v(-21.38, 0.85) * mm});
            skLineSegment(sketch, "E2008", {"start": v(-21.38, 0.85) * mm, "end": v(-21.42, 0.85) * mm});
            skLineSegment(sketch, "E2009", {"start": v(-21.42, 0.85) * mm, "end": v(-21.46, 0.84) * mm});
            skLineSegment(sketch, "E2010", {"start": v(-21.46, 0.84) * mm, "end": v(-21.54, 0.84) * mm});
            skLineSegment(sketch, "E2011", {"start": v(-21.54, 0.84) * mm, "end": v(-21.67, 0.82) * mm});
            skLineSegment(sketch, "E2012", {"start": v(-21.67, 0.82) * mm, "end": v(-21.82, 0.78) * mm});
            skLineSegment(sketch, "E2013", {"start": v(-21.82, 0.78) * mm, "end": v(-21.99, 0.72) * mm});
            skLineSegment(sketch, "E2014", {"start": v(-21.99, 0.72) * mm, "end": v(-22.18, 0.64) * mm});
            skLineSegment(sketch, "E2015", {"start": v(-22.18, 0.64) * mm, "end": v(-22.4, 0.54) * mm});
            skLineSegment(sketch, "E2016", {"start": v(-22.4, 0.54) * mm, "end": v(-22.8, 0.3) * mm});
            skLineSegment(sketch, "E2017", {"start": v(-22.8, 0.3) * mm, "end": v(-22.82, 0.08) * mm});
            skLineSegment(sketch, "E2018", {"start": v(-22.82, 0.08) * mm, "end": v(-22.8, -0.31) * mm});
            skLineSegment(sketch, "E2019", {"start": v(-22.8, -0.31) * mm, "end": v(-22.4, -0.55) * mm});
            skLineSegment(sketch, "E2020", {"start": v(-22.4, -0.55) * mm, "end": v(-22.18, -0.66) * mm});
            skLineSegment(sketch, "E2021", {"start": v(-22.18, -0.66) * mm, "end": v(-21.99, -0.74) * mm});
            skLineSegment(sketch, "E2022", {"start": v(-21.99, -0.74) * mm, "end": v(-21.82, -0.8) * mm});
            skLineSegment(sketch, "E2023", {"start": v(-21.82, -0.8) * mm, "end": v(-21.66, -0.83) * mm});
            skLineSegment(sketch, "E2024", {"start": v(-21.66, -0.83) * mm, "end": v(-21.54, -0.85) * mm});
            skLineSegment(sketch, "E2025", {"start": v(-21.54, -0.85) * mm, "end": v(-21.46, -0.86) * mm});
            skLineSegment(sketch, "E2026", {"start": v(-21.46, -0.86) * mm, "end": v(-21.42, -0.86) * mm});
            skLineSegment(sketch, "E2027", {"start": v(-21.42, -0.86) * mm, "end": v(-21.38, -0.86) * mm});
            skLineSegment(sketch, "E2028", {"start": v(-21.38, -0.86) * mm, "end": v(-21.35, -0.86) * mm});
            skLineSegment(sketch, "E2029", {"start": v(-21.35, -0.86) * mm, "end": v(-21.32, -0.86) * mm});
            skLineSegment(sketch, "E2030", {"start": v(-21.32, -0.86) * mm, "end": v(-21.3, -0.86) * mm});
            skLineSegment(sketch, "E2031", {"start": v(-21.3, -0.86) * mm, "end": v(-21.28, -0.85) * mm});
            skLineSegment(sketch, "E2032", {"start": v(-21.28, -0.85) * mm, "end": v(-21.26, -0.85) * mm});
            skLineSegment(sketch, "E2033", {"start": v(-21.26, -0.85) * mm, "end": v(-21.25, -0.85) * mm});
            skLineSegment(sketch, "E2034", {"start": v(-21.25, -0.85) * mm, "end": v(-21.25, -0.85) * mm});
            skLineSegment(sketch, "E2035", {"start": v(-21.25, -0.85) * mm, "end": v(-21.24, -0.85) * mm});
            skLineSegment(sketch, "E2036", {"start": v(-21.24, -0.85) * mm, "end": v(-21.04, -0.78) * mm});
            skLineSegment(sketch, "E2037", {"start": v(-21.04, -0.78) * mm, "end": v(-21.04, -0.79) * mm});
            skLineSegment(sketch, "E2038", {"start": v(-21.04, -0.79) * mm, "end": v(-20.96, -0.77) * mm});
            skLineSegment(sketch, "E2039", {"start": v(-20.96, -0.77) * mm, "end": v(-20.96, -0.77) * mm});
            skLineSegment(sketch, "E2040", {"start": v(-20.96, -0.77) * mm, "end": v(-20.88, -0.75) * mm});
            skLineSegment(sketch, "E2041", {"start": v(-20.88, -0.75) * mm, "end": v(-20.88, -0.76) * mm});
            skLineSegment(sketch, "E2042", {"start": v(-20.88, -0.76) * mm, "end": v(-20.8, -0.75) * mm});
            skLineSegment(sketch, "E2043", {"start": v(-20.8, -0.75) * mm, "end": v(-20.8, -0.76) * mm});
            skLineSegment(sketch, "E2044", {"start": v(-20.8, -0.76) * mm, "end": v(-20.74, -0.74) * mm});
            skLineSegment(sketch, "E2045", {"start": v(-20.74, -0.74) * mm, "end": v(-20.73, -0.76) * mm});
            skLineSegment(sketch, "E2046", {"start": v(-20.73, -0.76) * mm, "end": v(-20.67, -0.75) * mm});
            skLineSegment(sketch, "E2047", {"start": v(-20.67, -0.75) * mm, "end": v(-20.66, -0.76) * mm});
            skLineSegment(sketch, "E2048", {"start": v(-20.66, -0.76) * mm, "end": v(-20.6, -0.76) * mm});
            skLineSegment(sketch, "E2049", {"start": v(-20.6, -0.76) * mm, "end": v(-20.6, -0.78) * mm});
            skLineSegment(sketch, "E2050", {"start": v(-20.6, -0.78) * mm, "end": v(-20.54, -0.77) * mm});
            skLineSegment(sketch, "E2051", {"start": v(-20.54, -0.77) * mm, "end": v(-20.53, -0.8) * mm});
            skLineSegment(sketch, "E2052", {"start": v(-20.53, -0.8) * mm, "end": v(-20.49, -0.8) * mm});
            skLineSegment(sketch, "E2053", {"start": v(-20.49, -0.8) * mm, "end": v(-20.47, -0.82) * mm});
            skLineSegment(sketch, "E2054", {"start": v(-20.47, -0.82) * mm, "end": v(-20.44, -0.82) * mm});
            skLineSegment(sketch, "E2055", {"start": v(-20.44, -0.82) * mm, "end": v(-20.43, -0.85) * mm});
            skLineSegment(sketch, "E2056", {"start": v(-20.43, -0.85) * mm, "end": v(-20.4, -0.85) * mm});
            skLineSegment(sketch, "E2057", {"start": v(-20.4, -0.85) * mm, "end": v(-20.38, -0.88) * mm});
            skLineSegment(sketch, "E2058", {"start": v(-20.38, -0.88) * mm, "end": v(-20.36, -0.88) * mm});
            skLineSegment(sketch, "E2059", {"start": v(-20.36, -0.88) * mm, "end": v(-20.35, -0.92) * mm});
            skLineSegment(sketch, "E2060", {"start": v(-20.35, -0.92) * mm, "end": v(-20.33, -0.92) * mm});
            skLineSegment(sketch, "E2061", {"start": v(-20.33, -0.92) * mm, "end": v(-20.32, -0.96) * mm});
            skLineSegment(sketch, "E2062", {"start": v(-20.32, -0.96) * mm, "end": v(-20.3, -0.96) * mm});
            skLineSegment(sketch, "E2063", {"start": v(-20.3, -0.96) * mm, "end": v(-20.25, -1.17) * mm});
            skLineSegment(sketch, "E2064", {"start": v(-20.25, -1.17) * mm, "end": v(-20.2, -1.33) * mm});
            skLineSegment(sketch, "E2065", {"start": v(-20.2, -1.33) * mm, "end": v(-20.15, -1.48) * mm});
            skLineSegment(sketch, "E2066", {"start": v(-20.15, -1.48) * mm, "end": v(-20.15, -1.5) * mm});
            skLineSegment(sketch, "E2067", {"start": v(-20.15, -1.5) * mm, "end": v(-20.14, -1.53) * mm});
            skLineSegment(sketch, "E2068", {"start": v(-20.14, -1.53) * mm, "end": v(-20.14, -1.54) * mm});
            skLineSegment(sketch, "E2069", {"start": v(-20.14, -1.54) * mm, "end": v(-20.13, -1.58) * mm});
            skLineSegment(sketch, "E2070", {"start": v(-20.13, -1.58) * mm, "end": v(-20.14, -1.59) * mm});
            skLineSegment(sketch, "E2071", {"start": v(-20.14, -1.59) * mm, "end": v(-20.13, -1.63) * mm});
            skLineSegment(sketch, "E2072", {"start": v(-20.13, -1.63) * mm, "end": v(-20.18, -1.66) * mm});
            skLineSegment(sketch, "E2073", {"start": v(-20.18, -1.66) * mm, "end": v(-20.16, -1.73) * mm});
            skLineSegment(sketch, "E2074", {"start": v(-20.16, -1.73) * mm, "end": v(-20.24, -1.78) * mm});
            skLineSegment(sketch, "E2075", {"start": v(-20.24, -1.78) * mm, "end": v(-20.23, -1.84) * mm});
            skLineSegment(sketch, "E2076", {"start": v(-20.23, -1.84) * mm, "end": v(-20.35, -1.9) * mm});
            skLineSegment(sketch, "E2077", {"start": v(-20.35, -1.9) * mm, "end": v(-20.34, -1.94) * mm});
            skLineSegment(sketch, "E2078", {"start": v(-20.34, -1.94) * mm, "end": v(-20.5, -2) * mm});
            skLineSegment(sketch, "E2079", {"start": v(-20.5, -2) * mm, "end": v(-20.5, -2.04) * mm});
            skLineSegment(sketch, "E2080", {"start": v(-20.5, -2.04) * mm, "end": v(-20.67, -2.1) * mm});
            skLineSegment(sketch, "E2081", {"start": v(-20.67, -2.1) * mm, "end": v(-20.68, -2.13) * mm});
            skLineSegment(sketch, "E2082", {"start": v(-20.68, -2.13) * mm, "end": v(-20.89, -2.18) * mm});
            skLineSegment(sketch, "E2083", {"start": v(-20.89, -2.18) * mm, "end": v(-20.9, -2.2) * mm});
            skLineSegment(sketch, "E2084", {"start": v(-20.9, -2.2) * mm, "end": v(-20.95, -2.2) * mm});
            skLineSegment(sketch, "E2085", {"start": v(-20.95, -2.2) * mm, "end": v(-20.96, -2.2) * mm});
            skLineSegment(sketch, "E2086", {"start": v(-20.96, -2.2) * mm, "end": v(-21, -2.23) * mm});
            skLineSegment(sketch, "E2087", {"start": v(-21, -2.23) * mm, "end": v(-21.04, -2.26) * mm});
            skLineSegment(sketch, "E2088", {"start": v(-21.04, -2.26) * mm, "end": v(-21.08, -2.3) * mm});
            skLineSegment(sketch, "E2089", {"start": v(-21.08, -2.3) * mm, "end": v(-21.12, -2.33) * mm});
            skLineSegment(sketch, "E2090", {"start": v(-21.12, -2.33) * mm, "end": v(-21.17, -2.38) * mm});
            skLineSegment(sketch, "E2091", {"start": v(-21.17, -2.38) * mm, "end": v(-21.22, -2.43) * mm});
            skLineSegment(sketch, "E2092", {"start": v(-21.22, -2.43) * mm, "end": v(-21.28, -2.49) * mm});
            skLineSegment(sketch, "E2093", {"start": v(-21.28, -2.49) * mm, "end": v(-21.34, -2.55) * mm});
            skLineSegment(sketch, "E2094", {"start": v(-21.34, -2.55) * mm, "end": v(-21.4, -2.63) * mm});
            skLineSegment(sketch, "E2095", {"start": v(-21.4, -2.63) * mm, "end": v(-21.46, -2.7) * mm});
            skLineSegment(sketch, "E2096", {"start": v(-21.46, -2.7) * mm, "end": v(-21.53, -2.8) * mm});
            skLineSegment(sketch, "E2097", {"start": v(-21.53, -2.8) * mm, "end": v(-21.6, -2.88) * mm});
            skLineSegment(sketch, "E2098", {"start": v(-21.6, -2.88) * mm, "end": v(-21.66, -2.98) * mm});
            skLineSegment(sketch, "E2099", {"start": v(-21.66, -2.98) * mm, "end": v(-21.91, -3.38) * mm});
            skLineSegment(sketch, "E2100", {"start": v(-21.91, -3.38) * mm, "end": v(-21.75, -3.67) * mm});
            skLineSegment(sketch, "E2101", {"start": v(-21.75, -3.67) * mm, "end": v(-21.56, -3.98) * mm});
            skLineSegment(sketch, "E2102", {"start": v(-21.56, -3.98) * mm, "end": v(-21.02, -3.94) * mm});
            skLineSegment(sketch, "E2103", {"start": v(-21.02, -3.94) * mm, "end": v(-20.9, -3.92) * mm});
            skLineSegment(sketch, "E2104", {"start": v(-20.9, -3.92) * mm, "end": v(-20.8, -3.9) * mm});
            skLineSegment(sketch, "E2105", {"start": v(-20.8, -3.9) * mm, "end": v(-20.7, -3.9) * mm});
            skLineSegment(sketch, "E2106", {"start": v(-20.7, -3.9) * mm, "end": v(-20.6, -3.87) * mm});
            skLineSegment(sketch, "E2107", {"start": v(-20.6, -3.87) * mm, "end": v(-20.5, -3.85) * mm});
            skLineSegment(sketch, "E2108", {"start": v(-20.5, -3.85) * mm, "end": v(-20.43, -3.83) * mm});
            skLineSegment(sketch, "E2109", {"start": v(-20.43, -3.83) * mm, "end": v(-20.35, -3.8) * mm});
            skLineSegment(sketch, "E2110", {"start": v(-20.35, -3.8) * mm, "end": v(-20.28, -3.79) * mm});
            skLineSegment(sketch, "E2111", {"start": v(-20.28, -3.79) * mm, "end": v(-20.2, -3.76) * mm});
            skLineSegment(sketch, "E2112", {"start": v(-20.2, -3.76) * mm, "end": v(-20.15, -3.74) * mm});
            skLineSegment(sketch, "E2113", {"start": v(-20.15, -3.74) * mm, "end": v(-20.09, -3.71) * mm});
            skLineSegment(sketch, "E2114", {"start": v(-20.09, -3.71) * mm, "end": v(-20.03, -3.7) * mm});
            skLineSegment(sketch, "E2115", {"start": v(-20.03, -3.7) * mm, "end": v(-19.98, -3.67) * mm});
            skLineSegment(sketch, "E2116", {"start": v(-19.98, -3.67) * mm, "end": v(-19.93, -3.65) * mm});
            skLineSegment(sketch, "E2117", {"start": v(-19.93, -3.65) * mm, "end": v(-19.9, -3.62) * mm});
            skLineSegment(sketch, "E2118", {"start": v(-19.9, -3.62) * mm, "end": v(-19.85, -3.6) * mm});
            skLineSegment(sketch, "E2119", {"start": v(-19.85, -3.6) * mm, "end": v(-19.81, -3.58) * mm});
            skLineSegment(sketch, "E2120", {"start": v(-19.81, -3.58) * mm, "end": v(-19.78, -3.56) * mm});
            skLineSegment(sketch, "E2121", {"start": v(-19.78, -3.56) * mm, "end": v(-19.74, -3.54) * mm});
            skLineSegment(sketch, "E2122", {"start": v(-19.74, -3.54) * mm, "end": v(-19.71, -3.52) * mm});
            skLineSegment(sketch, "E2123", {"start": v(-19.71, -3.52) * mm, "end": v(-19.48, -3.37) * mm});
            skLineSegment(sketch, "E2124", {"start": v(-19.48, -3.37) * mm, "end": v(-19.48, -3.37) * mm});
            skLineSegment(sketch, "E2125", {"start": v(-19.48, -3.37) * mm, "end": v(-19.44, -3.34) * mm});
            skLineSegment(sketch, "E2126", {"start": v(-19.44, -3.34) * mm, "end": v(-19.43, -3.35) * mm});
            skLineSegment(sketch, "E2127", {"start": v(-19.43, -3.35) * mm, "end": v(-19.4, -3.32) * mm});
            skLineSegment(sketch, "E2128", {"start": v(-19.4, -3.32) * mm, "end": v(-19.38, -3.33) * mm});
            skLineSegment(sketch, "E2129", {"start": v(-19.38, -3.33) * mm, "end": v(-19.34, -3.3) * mm});
            skLineSegment(sketch, "E2130", {"start": v(-19.34, -3.3) * mm, "end": v(-19.32, -3.3) * mm});
            skLineSegment(sketch, "E2131", {"start": v(-19.32, -3.3) * mm, "end": v(-19.3, -3.3) * mm});
            skLineSegment(sketch, "E2132", {"start": v(-19.3, -3.3) * mm, "end": v(-19.26, -3.28) * mm});
            skLineSegment(sketch, "E2133", {"start": v(-19.26, -3.28) * mm, "end": v(-19.23, -3.29) * mm});
            skLineSegment(sketch, "E2134", {"start": v(-19.23, -3.29) * mm, "end": v(-19.2, -3.3) * mm});
            skLineSegment(sketch, "E2135", {"start": v(-19.2, -3.3) * mm, "end": v(-19.18, -3.28) * mm});
            skLineSegment(sketch, "E2136", {"start": v(-19.18, -3.28) * mm, "end": v(-19.17, -3.3) * mm});
            skLineSegment(sketch, "E2137", {"start": v(-19.17, -3.3) * mm, "end": v(-19.14, -3.3) * mm});
            skLineSegment(sketch, "E2138", {"start": v(-19.14, -3.3) * mm, "end": v(-19.11, -3.3) * mm});
            skLineSegment(sketch, "E2139", {"start": v(-19.11, -3.3) * mm, "end": v(-19.1, -3.32) * mm});
            skLineSegment(sketch, "E2140", {"start": v(-19.1, -3.32) * mm, "end": v(-19.07, -3.32) * mm});
            skLineSegment(sketch, "E2141", {"start": v(-19.07, -3.32) * mm, "end": v(-19.06, -3.33) * mm});
            skLineSegment(sketch, "E2142", {"start": v(-19.06, -3.33) * mm, "end": v(-18.92, -3.5) * mm});
            skLineSegment(sketch, "E2143", {"start": v(-18.92, -3.5) * mm, "end": v(-18.78, -3.65) * mm});
            skLineSegment(sketch, "E2144", {"start": v(-18.78, -3.65) * mm, "end": v(-18.64, -3.8) * mm});
            skLineSegment(sketch, "E2145", {"start": v(-18.64, -3.8) * mm, "end": v(-18.63, -3.82) * mm});
            skLineSegment(sketch, "E2146", {"start": v(-18.63, -3.82) * mm, "end": v(-18.63, -3.84) * mm});
            skLineSegment(sketch, "E2147", {"start": v(-18.63, -3.84) * mm, "end": v(-18.6, -3.86) * mm});
            skLineSegment(sketch, "E2148", {"start": v(-18.6, -3.86) * mm, "end": v(-18.62, -3.87) * mm});
            skLineSegment(sketch, "E2149", {"start": v(-18.62, -3.87) * mm, "end": v(-18.6, -3.9) * mm});
            skLineSegment(sketch, "E2150", {"start": v(-18.6, -3.9) * mm, "end": v(-18.62, -3.92) * mm});
            skLineSegment(sketch, "E2151", {"start": v(-18.62, -3.92) * mm, "end": v(-18.6, -3.94) * mm});
            skLineSegment(sketch, "E2152", {"start": v(-18.6, -3.94) * mm, "end": v(-18.62, -3.96) * mm});
            skLineSegment(sketch, "E2153", {"start": v(-18.62, -3.96) * mm, "end": v(-18.6, -3.98) * mm});
            skLineSegment(sketch, "E2154", {"start": v(-18.6, -3.98) * mm, "end": v(-18.63, -4.02) * mm});
            skLineSegment(sketch, "E2155", {"start": v(-18.63, -4.02) * mm, "end": v(-18.61, -4.03) * mm});
            skLineSegment(sketch, "E2156", {"start": v(-18.61, -4.03) * mm, "end": v(-18.64, -4.07) * mm});
            skLineSegment(sketch, "E2157", {"start": v(-18.64, -4.07) * mm, "end": v(-18.63, -4.09) * mm});
            skLineSegment(sketch, "E2158", {"start": v(-18.63, -4.09) * mm, "end": v(-18.67, -4.13) * mm});
            skLineSegment(sketch, "E2159", {"start": v(-18.67, -4.13) * mm, "end": v(-18.66, -4.15) * mm});
            skLineSegment(sketch, "E2160", {"start": v(-18.66, -4.15) * mm, "end": v(-18.7, -4.2) * mm});
            skLineSegment(sketch, "E2161", {"start": v(-18.7, -4.2) * mm, "end": v(-18.7, -4.21) * mm});
            skLineSegment(sketch, "E2162", {"start": v(-18.7, -4.21) * mm, "end": v(-18.74, -4.27) * mm});
            skLineSegment(sketch, "E2163", {"start": v(-18.74, -4.27) * mm, "end": v(-18.73, -4.28) * mm});
            skLineSegment(sketch, "E2164", {"start": v(-18.73, -4.28) * mm, "end": v(-18.79, -4.34) * mm});
            skLineSegment(sketch, "E2165", {"start": v(-18.79, -4.34) * mm, "end": v(-18.78, -4.35) * mm});
            skLineSegment(sketch, "E2166", {"start": v(-18.78, -4.35) * mm, "end": v(-18.85, -4.42) * mm});
            skLineSegment(sketch, "E2167", {"start": v(-18.85, -4.42) * mm, "end": v(-18.84, -4.43) * mm});
            skLineSegment(sketch, "E2168", {"start": v(-18.84, -4.43) * mm, "end": v(-19.01, -4.6) * mm});
            skLineSegment(sketch, "E2169", {"start": v(-19.01, -4.6) * mm, "end": v(-19.01, -4.6) * mm});
            skLineSegment(sketch, "E2170", {"start": v(-19.01, -4.6) * mm, "end": v(-19.02, -4.6) * mm});
            skLineSegment(sketch, "E2171", {"start": v(-19.02, -4.6) * mm, "end": v(-19.04, -4.63) * mm});
            skLineSegment(sketch, "E2172", {"start": v(-19.04, -4.63) * mm, "end": v(-19.06, -4.66) * mm});
            skLineSegment(sketch, "E2173", {"start": v(-19.06, -4.66) * mm, "end": v(-19.08, -4.69) * mm});
            skLineSegment(sketch, "E2174", {"start": v(-19.08, -4.69) * mm, "end": v(-19.1, -4.73) * mm});
            skLineSegment(sketch, "E2175", {"start": v(-19.1, -4.73) * mm, "end": v(-19.13, -4.78) * mm});
            skLineSegment(sketch, "E2176", {"start": v(-19.13, -4.78) * mm, "end": v(-19.16, -4.84) * mm});
            skLineSegment(sketch, "E2177", {"start": v(-19.16, -4.84) * mm, "end": v(-19.2, -4.9) * mm});
            skLineSegment(sketch, "E2178", {"start": v(-19.2, -4.9) * mm, "end": v(-19.23, -4.97) * mm});
            skLineSegment(sketch, "E2179", {"start": v(-19.23, -4.97) * mm, "end": v(-19.26, -5.04) * mm});
            skLineSegment(sketch, "E2180", {"start": v(-19.26, -5.04) * mm, "end": v(-19.3, -5.12) * mm});
            skLineSegment(sketch, "E2181", {"start": v(-19.3, -5.12) * mm, "end": v(-19.33, -5.21) * mm});
            skLineSegment(sketch, "E2182", {"start": v(-19.33, -5.21) * mm, "end": v(-19.36, -5.3) * mm});
            skLineSegment(sketch, "E2183", {"start": v(-19.36, -5.3) * mm, "end": v(-19.4, -5.4) * mm});
            skLineSegment(sketch, "E2184", {"start": v(-19.4, -5.4) * mm, "end": v(-19.43, -5.5) * mm});
            skLineSegment(sketch, "E2185", {"start": v(-19.43, -5.5) * mm, "end": v(-19.46, -5.6) * mm});
            skLineSegment(sketch, "E2186", {"start": v(-19.46, -5.6) * mm, "end": v(-19.63, -6.17) * mm});
            skLineSegment(sketch, "E2187", {"start": v(-19.63, -6.17) * mm, "end": v(-19.32, -6.43) * mm});
            skLineSegment(sketch, "E2188", {"start": v(-19.32, -6.43) * mm, "end": v(-19.05, -6.65) * mm});
            skLineSegment(sketch, "E2189", {"start": v(-19.05, -6.65) * mm, "end": v(-18.56, -6.41) * mm});
            skLineSegment(sketch, "E2190", {"start": v(-18.56, -6.41) * mm, "end": v(-18.46, -6.36) * mm});
            skLineSegment(sketch, "E2191", {"start": v(-18.46, -6.36) * mm, "end": v(-18.36, -6.3) * mm});
            skLineSegment(sketch, "E2192", {"start": v(-18.36, -6.3) * mm, "end": v(-18.27, -6.26) * mm});
            skLineSegment(sketch, "E2193", {"start": v(-18.27, -6.26) * mm, "end": v(-18.18, -6.2) * mm});
            skLineSegment(sketch, "E2194", {"start": v(-18.18, -6.2) * mm, "end": v(-18.1, -6.16) * mm});
            skLineSegment(sketch, "E2195", {"start": v(-18.1, -6.16) * mm, "end": v(-18.02, -6.1) * mm});
            skLineSegment(sketch, "E2196", {"start": v(-18.02, -6.1) * mm, "end": v(-17.95, -6.06) * mm});
            skLineSegment(sketch, "E2197", {"start": v(-17.95, -6.06) * mm, "end": v(-17.88, -6.01) * mm});
            skLineSegment(sketch, "E2198", {"start": v(-17.88, -6.01) * mm, "end": v(-17.81, -5.96) * mm});
            skLineSegment(sketch, "E2199", {"start": v(-17.81, -5.96) * mm, "end": v(-17.75, -5.92) * mm});
            skLineSegment(sketch, "E2200", {"start": v(-17.75, -5.92) * mm, "end": v(-17.69, -5.87) * mm});
            skLineSegment(sketch, "E2201", {"start": v(-17.69, -5.87) * mm, "end": v(-17.63, -5.83) * mm});
            skLineSegment(sketch, "E2202", {"start": v(-17.63, -5.83) * mm, "end": v(-17.58, -5.78) * mm});
            skLineSegment(sketch, "E2203", {"start": v(-17.58, -5.78) * mm, "end": v(-17.53, -5.74) * mm});
            skLineSegment(sketch, "E2204", {"start": v(-17.53, -5.74) * mm, "end": v(-17.48, -5.7) * mm});
            skLineSegment(sketch, "E2205", {"start": v(-17.48, -5.7) * mm, "end": v(-17.43, -5.65) * mm});
            skLineSegment(sketch, "E2206", {"start": v(-17.43, -5.65) * mm, "end": v(-17.39, -5.61) * mm});
            skLineSegment(sketch, "E2207", {"start": v(-17.39, -5.61) * mm, "end": v(-17.35, -5.58) * mm});
            skLineSegment(sketch, "E2208", {"start": v(-17.35, -5.58) * mm, "end": v(-17.3, -5.53) * mm});
            skLineSegment(sketch, "E2209", {"start": v(-17.3, -5.53) * mm, "end": v(-17.16, -5.4) * mm});
            skLineSegment(sketch, "E2210", {"start": v(-17.16, -5.4) * mm, "end": v(-17.14, -5.38) * mm});
            skLineSegment(sketch, "E2211", {"start": v(-17.14, -5.38) * mm, "end": v(-17.12, -5.37) * mm});
            skLineSegment(sketch, "E2212", {"start": v(-17.12, -5.37) * mm, "end": v(-17.1, -5.34) * mm});
            skLineSegment(sketch, "E2213", {"start": v(-17.1, -5.34) * mm, "end": v(-17.08, -5.33) * mm});
            skLineSegment(sketch, "E2214", {"start": v(-17.08, -5.33) * mm, "end": v(-17.05, -5.31) * mm});
            skLineSegment(sketch, "E2215", {"start": v(-17.05, -5.31) * mm, "end": v(-17.02, -5.3) * mm});
            skLineSegment(sketch, "E2216", {"start": v(-17.02, -5.3) * mm, "end": v(-17, -5.29) * mm});
            skLineSegment(sketch, "E2217", {"start": v(-17, -5.29) * mm, "end": v(-16.97, -5.28) * mm});
            skLineSegment(sketch, "E2218", {"start": v(-16.97, -5.28) * mm, "end": v(-16.94, -5.28) * mm});
            skLineSegment(sketch, "E2219", {"start": v(-16.94, -5.28) * mm, "end": v(-16.91, -5.28) * mm});
            skLineSegment(sketch, "E2220", {"start": v(-16.91, -5.28) * mm, "end": v(-16.9, -5.28) * mm});
            skLineSegment(sketch, "E2221", {"start": v(-16.9, -5.28) * mm, "end": v(-16.87, -5.29) * mm});
            skLineSegment(sketch, "E2222", {"start": v(-16.87, -5.29) * mm, "end": v(-16.87, -5.29) * mm});
            skLineSegment(sketch, "E2223", {"start": v(-16.87, -5.29) * mm, "end": v(-16.7, -5.4) * mm});
            skLineSegment(sketch, "E2224", {"start": v(-16.7, -5.4) * mm, "end": v(-16.5, -5.54) * mm});
            skLineSegment(sketch, "E2225", {"start": v(-16.5, -5.54) * mm, "end": v(-16.33, -5.64) * mm});
            skLineSegment(sketch, "E2226", {"start": v(-16.33, -5.64) * mm, "end": v(-16.32, -5.65) * mm});
            skLineSegment(sketch, "E2227", {"start": v(-16.32, -5.65) * mm, "end": v(-16.3, -5.67) * mm});
            skLineSegment(sketch, "E2228", {"start": v(-16.3, -5.67) * mm, "end": v(-16.3, -5.7) * mm});
            skLineSegment(sketch, "E2229", {"start": v(-16.3, -5.7) * mm, "end": v(-16.3, -5.72) * mm});
            skLineSegment(sketch, "E2230", {"start": v(-16.3, -5.72) * mm, "end": v(-16.28, -5.74) * mm});
            skLineSegment(sketch, "E2231", {"start": v(-16.28, -5.74) * mm, "end": v(-16.27, -5.76) * mm});
            skLineSegment(sketch, "E2232", {"start": v(-16.27, -5.76) * mm, "end": v(-16.28, -5.79) * mm});
            skLineSegment(sketch, "E2233", {"start": v(-16.28, -5.79) * mm, "end": v(-16.28, -5.81) * mm});
            skLineSegment(sketch, "E2234", {"start": v(-16.28, -5.81) * mm, "end": v(-16.27, -5.84) * mm});
            skLineSegment(sketch, "E2235", {"start": v(-16.27, -5.84) * mm, "end": v(-16.29, -5.88) * mm});
            skLineSegment(sketch, "E2236", {"start": v(-16.29, -5.88) * mm, "end": v(-16.28, -5.88) * mm});
            skLineSegment(sketch, "E2237", {"start": v(-16.28, -5.88) * mm, "end": v(-16.3, -5.93) * mm});
            skLineSegment(sketch, "E2238", {"start": v(-16.3, -5.93) * mm, "end": v(-16.29, -5.94) * mm});
            skLineSegment(sketch, "E2239", {"start": v(-16.29, -5.94) * mm, "end": v(-16.31, -5.99) * mm});
            skLineSegment(sketch, "E2240", {"start": v(-16.31, -5.99) * mm, "end": v(-16.3, -6) * mm});
            skLineSegment(sketch, "E2241", {"start": v(-16.3, -6) * mm, "end": v(-16.33, -6.05) * mm});
            skLineSegment(sketch, "E2242", {"start": v(-16.33, -6.05) * mm, "end": v(-16.33, -6.06) * mm});
            skLineSegment(sketch, "E2243", {"start": v(-16.33, -6.06) * mm, "end": v(-16.43, -6.28) * mm});
            skLineSegment(sketch, "E2244", {"start": v(-16.43, -6.28) * mm, "end": v(-16.43, -6.3) * mm});
            skLineSegment(sketch, "E2245", {"start": v(-16.43, -6.3) * mm, "end": v(-16.45, -6.33) * mm});
            skLineSegment(sketch, "E2246", {"start": v(-16.45, -6.33) * mm, "end": v(-16.46, -6.36) * mm});
            skLineSegment(sketch, "E2247", {"start": v(-16.46, -6.36) * mm, "end": v(-16.47, -6.4) * mm});
            skLineSegment(sketch, "E2248", {"start": v(-16.47, -6.4) * mm, "end": v(-16.49, -6.45) * mm});
            skLineSegment(sketch, "E2249", {"start": v(-16.49, -6.45) * mm, "end": v(-16.5, -6.5) * mm});
            skLineSegment(sketch, "E2250", {"start": v(-16.5, -6.5) * mm, "end": v(-16.52, -6.56) * mm});
            skLineSegment(sketch, "E2251", {"start": v(-16.52, -6.56) * mm, "end": v(-16.54, -6.63) * mm});
            skLineSegment(sketch, "E2252", {"start": v(-16.54, -6.63) * mm, "end": v(-16.56, -6.7) * mm});
            skLineSegment(sketch, "E2253", {"start": v(-16.56, -6.7) * mm, "end": v(-16.58, -6.78) * mm});
            skLineSegment(sketch, "E2254", {"start": v(-16.58, -6.78) * mm, "end": v(-16.6, -6.86) * mm});
            skLineSegment(sketch, "E2255", {"start": v(-16.6, -6.86) * mm, "end": v(-16.61, -6.95) * mm});
            skLineSegment(sketch, "E2256", {"start": v(-16.61, -6.95) * mm, "end": v(-16.63, -7.03) * mm});
            skLineSegment(sketch, "E2257", {"start": v(-16.63, -7.03) * mm, "end": v(-16.65, -7.13) * mm});
            skLineSegment(sketch, "E2258", {"start": v(-16.65, -7.13) * mm, "end": v(-16.66, -7.23) * mm});
            skLineSegment(sketch, "E2259", {"start": v(-16.66, -7.23) * mm, "end": v(-16.68, -7.34) * mm});
            skLineSegment(sketch, "E2260", {"start": v(-16.68, -7.34) * mm, "end": v(-16.7, -7.44) * mm});
            skLineSegment(sketch, "E2261", {"start": v(-16.7, -7.44) * mm, "end": v(-16.7, -7.55) * mm});
            skLineSegment(sketch, "E2262", {"start": v(-16.7, -7.55) * mm, "end": v(-16.72, -7.66) * mm});
            skLineSegment(sketch, "E2263", {"start": v(-16.72, -7.66) * mm, "end": v(-16.77, -8.17) * mm});
            skLineSegment(sketch, "E2264", {"start": v(-16.77, -8.17) * mm, "end": v(-16.5, -8.32) * mm});
            skLineSegment(sketch, "E2265", {"start": v(-16.5, -8.32) * mm, "end": v(-16.07, -8.54) * mm});
            skLineSegment(sketch, "E2266", {"start": v(-16.07, -8.54) * mm, "end": v(-15.6, -8.16) * mm});
            skLineSegment(sketch, "E2267", {"start": v(-15.6, -8.16) * mm, "end": v(-15.52, -8.09) * mm});
            skLineSegment(sketch, "E2268", {"start": v(-15.52, -8.09) * mm, "end": v(-15.44, -8.02) * mm});
            skLineSegment(sketch, "E2269", {"start": v(-15.44, -8.02) * mm, "end": v(-15.36, -7.95) * mm});
            skLineSegment(sketch, "E2270", {"start": v(-15.36, -7.95) * mm, "end": v(-15.28, -7.88) * mm});
            skLineSegment(sketch, "E2271", {"start": v(-15.28, -7.88) * mm, "end": v(-15.21, -7.81) * mm});
            skLineSegment(sketch, "E2272", {"start": v(-15.21, -7.81) * mm, "end": v(-15.14, -7.75) * mm});
            skLineSegment(sketch, "E2273", {"start": v(-15.14, -7.75) * mm, "end": v(-15.08, -7.68) * mm});
            skLineSegment(sketch, "E2274", {"start": v(-15.08, -7.68) * mm, "end": v(-15.02, -7.62) * mm});
            skLineSegment(sketch, "E2275", {"start": v(-15.02, -7.62) * mm, "end": v(-14.96, -7.55) * mm});
            skLineSegment(sketch, "E2276", {"start": v(-14.96, -7.55) * mm, "end": v(-14.9, -7.5) * mm});
            skLineSegment(sketch, "E2277", {"start": v(-14.9, -7.5) * mm, "end": v(-14.84, -7.44) * mm});
            skLineSegment(sketch, "E2278", {"start": v(-14.84, -7.44) * mm, "end": v(-14.8, -7.38) * mm});
            skLineSegment(sketch, "E2279", {"start": v(-14.8, -7.38) * mm, "end": v(-14.74, -7.32) * mm});
            skLineSegment(sketch, "E2280", {"start": v(-14.74, -7.32) * mm, "end": v(-14.69, -7.26) * mm});
            skLineSegment(sketch, "E2281", {"start": v(-14.69, -7.26) * mm, "end": v(-14.64, -7.2) * mm});
            skLineSegment(sketch, "E2282", {"start": v(-14.64, -7.2) * mm, "end": v(-14.6, -7.15) * mm});
            skLineSegment(sketch, "E2283", {"start": v(-14.6, -7.15) * mm, "end": v(-14.56, -7.1) * mm});
            skLineSegment(sketch, "E2284", {"start": v(-14.56, -7.1) * mm, "end": v(-14.38, -6.88) * mm});
            skLineSegment(sketch, "E2285", {"start": v(-14.38, -6.88) * mm, "end": v(-14.37, -6.87) * mm});
            skLineSegment(sketch, "E2286", {"start": v(-14.37, -6.87) * mm, "end": v(-14.35, -6.85) * mm});
            skLineSegment(sketch, "E2287", {"start": v(-14.35, -6.85) * mm, "end": v(-14.33, -6.83) * mm});
            skLineSegment(sketch, "E2288", {"start": v(-14.33, -6.83) * mm, "end": v(-14.31, -6.82) * mm});
            skLineSegment(sketch, "E2289", {"start": v(-14.31, -6.82) * mm, "end": v(-14.3, -6.8) * mm});
            skLineSegment(sketch, "E2290", {"start": v(-14.3, -6.8) * mm, "end": v(-14.27, -6.8) * mm});
            skLineSegment(sketch, "E2291", {"start": v(-14.27, -6.8) * mm, "end": v(-14.25, -6.8) * mm});
            skLineSegment(sketch, "E2292", {"start": v(-14.25, -6.8) * mm, "end": v(-14.23, -6.79) * mm});
            skLineSegment(sketch, "E2293", {"start": v(-14.23, -6.79) * mm, "end": v(-14.22, -6.79) * mm});
            skLineSegment(sketch, "E2294", {"start": v(-14.22, -6.79) * mm, "end": v(-14.2, -6.8) * mm});
            skLineSegment(sketch, "E2295", {"start": v(-14.2, -6.8) * mm, "end": v(-14.2, -6.8) * mm});
            skLineSegment(sketch, "E2296", {"start": v(-14.2, -6.8) * mm, "end": v(-14.02, -6.87) * mm});
            skLineSegment(sketch, "E2297", {"start": v(-14.02, -6.87) * mm, "end": v(-13.78, -6.98) * mm});
            skLineSegment(sketch, "E2298", {"start": v(-13.78, -6.98) * mm, "end": v(-13.6, -7.06) * mm});
            skLineSegment(sketch, "E2299", {"start": v(-13.6, -7.06) * mm, "end": v(-13.59, -7.06) * mm});
            skLineSegment(sketch, "E2300", {"start": v(-13.59, -7.06) * mm, "end": v(-13.58, -7.08) * mm});
            skLineSegment(sketch, "E2301", {"start": v(-13.58, -7.08) * mm, "end": v(-13.57, -7.1) * mm});
            skLineSegment(sketch, "E2302", {"start": v(-13.57, -7.1) * mm, "end": v(-13.56, -7.11) * mm});
            skLineSegment(sketch, "E2303", {"start": v(-13.56, -7.11) * mm, "end": v(-13.55, -7.13) * mm});
            skLineSegment(sketch, "E2304", {"start": v(-13.55, -7.13) * mm, "end": v(-13.55, -7.16) * mm});
            skLineSegment(sketch, "E2305", {"start": v(-13.55, -7.16) * mm, "end": v(-13.54, -7.18) * mm});
            skLineSegment(sketch, "E2306", {"start": v(-13.54, -7.18) * mm, "end": v(-13.54, -7.2) * mm});
            skLineSegment(sketch, "E2307", {"start": v(-13.54, -7.2) * mm, "end": v(-13.53, -7.23) * mm});
            skLineSegment(sketch, "E2308", {"start": v(-13.53, -7.23) * mm, "end": v(-13.54, -7.26) * mm});
            skLineSegment(sketch, "E2309", {"start": v(-13.54, -7.26) * mm, "end": v(-13.54, -7.29) * mm});
            skLineSegment(sketch, "E2310", {"start": v(-13.54, -7.29) * mm, "end": v(-13.54, -7.31) * mm});
            skLineSegment(sketch, "E2311", {"start": v(-13.54, -7.31) * mm, "end": v(-13.6, -7.6) * mm});
            skLineSegment(sketch, "E2312", {"start": v(-13.6, -7.6) * mm, "end": v(-13.6, -7.64) * mm});
            skLineSegment(sketch, "E2313", {"start": v(-13.6, -7.64) * mm, "end": v(-13.6, -7.7) * mm});
            skLineSegment(sketch, "E2314", {"start": v(-13.6, -7.7) * mm, "end": v(-13.62, -7.76) * mm});
            skLineSegment(sketch, "E2315", {"start": v(-13.62, -7.76) * mm, "end": v(-13.63, -7.83) * mm});
            skLineSegment(sketch, "E2316", {"start": v(-13.63, -7.83) * mm, "end": v(-13.63, -7.9) * mm});
            skLineSegment(sketch, "E2317", {"start": v(-13.63, -7.9) * mm, "end": v(-13.64, -7.97) * mm});
            skLineSegment(sketch, "E2318", {"start": v(-13.64, -7.97) * mm, "end": v(-13.65, -8.05) * mm});
            skLineSegment(sketch, "E2319", {"start": v(-13.65, -8.05) * mm, "end": v(-13.66, -8.13) * mm});
            skLineSegment(sketch, "E2320", {"start": v(-13.66, -8.13) * mm, "end": v(-13.66, -8.22) * mm});
            skLineSegment(sketch, "E2321", {"start": v(-13.66, -8.22) * mm, "end": v(-13.67, -8.31) * mm});
            skLineSegment(sketch, "E2322", {"start": v(-13.67, -8.31) * mm, "end": v(-13.67, -8.4) * mm});
            skLineSegment(sketch, "E2323", {"start": v(-13.67, -8.4) * mm, "end": v(-13.67, -8.5) * mm});
            skLineSegment(sketch, "E2324", {"start": v(-13.67, -8.5) * mm, "end": v(-13.68, -8.6) * mm});
            skLineSegment(sketch, "E2325", {"start": v(-13.68, -8.6) * mm, "end": v(-13.68, -8.7) * mm});
            skLineSegment(sketch, "E2326", {"start": v(-13.68, -8.7) * mm, "end": v(-13.68, -8.8) * mm});
            skLineSegment(sketch, "E2327", {"start": v(-13.68, -8.8) * mm, "end": v(-13.68, -8.91) * mm});
            skLineSegment(sketch, "E2328", {"start": v(-13.68, -8.91) * mm, "end": v(-13.68, -9.02) * mm});
            skLineSegment(sketch, "E2329", {"start": v(-13.68, -9.02) * mm, "end": v(-13.66, -9.62) * mm});
            skLineSegment(sketch, "E2330", {"start": v(-13.66, -9.62) * mm, "end": v(-13.3, -9.75) * mm});
            skLineSegment(sketch, "E2331", {"start": v(-13.3, -9.75) * mm, "end": v(-12.9, -9.9) * mm});
            skLineSegment(sketch, "E2332", {"start": v(-12.9, -9.9) * mm, "end": v(-12.5, -9.46) * mm});
            skLineSegment(sketch, "E2333", {"start": v(-12.5, -9.46) * mm, "end": v(-12.43, -9.38) * mm});
            skLineSegment(sketch, "E2334", {"start": v(-12.43, -9.38) * mm, "end": v(-12.36, -9.3) * mm});
            skLineSegment(sketch, "E2335", {"start": v(-12.36, -9.3) * mm, "end": v(-12.3, -9.21) * mm});
            skLineSegment(sketch, "E2336", {"start": v(-12.3, -9.21) * mm, "end": v(-12.23, -9.14) * mm});
            skLineSegment(sketch, "E2337", {"start": v(-12.23, -9.14) * mm, "end": v(-12.17, -9.06) * mm});
            skLineSegment(sketch, "E2338", {"start": v(-12.17, -9.06) * mm, "end": v(-12.1, -8.98) * mm});
            skLineSegment(sketch, "E2339", {"start": v(-12.1, -8.98) * mm, "end": v(-12.05, -8.9) * mm});
            skLineSegment(sketch, "E2340", {"start": v(-12.05, -8.9) * mm, "end": v(-12, -8.84) * mm});
            skLineSegment(sketch, "E2341", {"start": v(-12, -8.84) * mm, "end": v(-11.94, -8.76) * mm});
            skLineSegment(sketch, "E2342", {"start": v(-11.94, -8.76) * mm, "end": v(-11.89, -8.7) * mm});
            skLineSegment(sketch, "E2343", {"start": v(-11.89, -8.7) * mm, "end": v(-11.84, -8.63) * mm});
            skLineSegment(sketch, "E2344", {"start": v(-11.84, -8.63) * mm, "end": v(-11.79, -8.56) * mm});
            skLineSegment(sketch, "E2345", {"start": v(-11.79, -8.56) * mm, "end": v(-11.74, -8.5) * mm});
            skLineSegment(sketch, "E2346", {"start": v(-11.74, -8.5) * mm, "end": v(-11.7, -8.43) * mm});
            skLineSegment(sketch, "E2347", {"start": v(-11.7, -8.43) * mm, "end": v(-11.66, -8.37) * mm});
            skLineSegment(sketch, "E2348", {"start": v(-11.66, -8.37) * mm, "end": v(-11.62, -8.3) * mm});
            skLineSegment(sketch, "E2349", {"start": v(-11.62, -8.3) * mm, "end": v(-11.57, -8.24) * mm});
            skLineSegment(sketch, "E2350", {"start": v(-11.57, -8.24) * mm, "end": v(-11.42, -8) * mm});
            skLineSegment(sketch, "E2351", {"start": v(-11.42, -8) * mm, "end": v(-11.41, -8) * mm});
            skLineSegment(sketch, "E2352", {"start": v(-11.41, -8) * mm, "end": v(-11.4, -7.98) * mm});
            skLineSegment(sketch, "E2353", {"start": v(-11.4, -7.98) * mm, "end": v(-11.38, -7.96) * mm});
            skLineSegment(sketch, "E2354", {"start": v(-11.38, -7.96) * mm, "end": v(-11.37, -7.95) * mm});
            skLineSegment(sketch, "E2355", {"start": v(-11.37, -7.95) * mm, "end": v(-11.35, -7.94) * mm});
            skLineSegment(sketch, "E2356", {"start": v(-11.35, -7.94) * mm, "end": v(-11.34, -7.93) * mm});
            skLineSegment(sketch, "E2357", {"start": v(-11.34, -7.93) * mm, "end": v(-11.32, -7.92) * mm});
            skLineSegment(sketch, "E2358", {"start": v(-11.32, -7.92) * mm, "end": v(-11.3, -7.92) * mm});
            skLineSegment(sketch, "E2359", {"start": v(-11.3, -7.92) * mm, "end": v(-11.3, -7.91) * mm});
            skLineSegment(sketch, "E2360", {"start": v(-11.3, -7.91) * mm, "end": v(-11.28, -7.92) * mm});
            skLineSegment(sketch, "E2361", {"start": v(-11.28, -7.92) * mm, "end": v(-11.28, -7.91) * mm});
            skLineSegment(sketch, "E2362", {"start": v(-11.28, -7.91) * mm, "end": v(-11.1, -7.97) * mm});
            skLineSegment(sketch, "E2363", {"start": v(-11.1, -7.97) * mm, "end": v(-10.83, -8.05) * mm});
            skLineSegment(sketch, "E2364", {"start": v(-10.83, -8.05) * mm, "end": v(-10.64, -8.11) * mm});
            skLineSegment(sketch, "E2365", {"start": v(-10.64, -8.11) * mm, "end": v(-10.64, -8.11) * mm});
            skLineSegment(sketch, "E2366", {"start": v(-10.64, -8.11) * mm, "end": v(-10.63, -8.12) * mm});
            skLineSegment(sketch, "E2367", {"start": v(-10.63, -8.12) * mm, "end": v(-10.62, -8.13) * mm});
            skLineSegment(sketch, "E2368", {"start": v(-10.62, -8.13) * mm, "end": v(-10.6, -8.15) * mm});
            skLineSegment(sketch, "E2369", {"start": v(-10.6, -8.15) * mm, "end": v(-10.6, -8.16) * mm});
            skLineSegment(sketch, "E2370", {"start": v(-10.6, -8.16) * mm, "end": v(-10.6, -8.18) * mm});
            skLineSegment(sketch, "E2371", {"start": v(-10.6, -8.18) * mm, "end": v(-10.59, -8.2) * mm});
            skLineSegment(sketch, "E2372", {"start": v(-10.59, -8.2) * mm, "end": v(-10.58, -8.23) * mm});
            skLineSegment(sketch, "E2373", {"start": v(-10.58, -8.23) * mm, "end": v(-10.58, -8.25) * mm});
            skLineSegment(sketch, "E2374", {"start": v(-10.58, -8.25) * mm, "end": v(-10.58, -8.28) * mm});
            skLineSegment(sketch, "E2375", {"start": v(-10.58, -8.28) * mm, "end": v(-10.57, -8.3) * mm});
            skLineSegment(sketch, "E2376", {"start": v(-10.57, -8.3) * mm, "end": v(-10.58, -8.56) * mm});
            skLineSegment(sketch, "E2377", {"start": v(-10.58, -8.56) * mm, "end": v(-10.59, -8.64) * mm});
            skLineSegment(sketch, "E2378", {"start": v(-10.59, -8.64) * mm, "end": v(-10.59, -8.7) * mm});
            skLineSegment(sketch, "E2379", {"start": v(-10.59, -8.7) * mm, "end": v(-10.59, -8.77) * mm});
            skLineSegment(sketch, "E2380", {"start": v(-10.59, -8.77) * mm, "end": v(-10.59, -8.85) * mm});
            skLineSegment(sketch, "E2381", {"start": v(-10.59, -8.85) * mm, "end": v(-10.59, -8.93) * mm});
            skLineSegment(sketch, "E2382", {"start": v(-10.59, -8.93) * mm, "end": v(-10.58, -9.01) * mm});
            skLineSegment(sketch, "E2383", {"start": v(-10.58, -9.01) * mm, "end": v(-10.58, -9.1) * mm});
            skLineSegment(sketch, "E2384", {"start": v(-10.58, -9.1) * mm, "end": v(-10.58, -9.18) * mm});
            skLineSegment(sketch, "E2385", {"start": v(-10.58, -9.18) * mm, "end": v(-10.57, -9.27) * mm});
            skLineSegment(sketch, "E2386", {"start": v(-10.57, -9.27) * mm, "end": v(-10.57, -9.36) * mm});
            skLineSegment(sketch, "E2387", {"start": v(-10.57, -9.36) * mm, "end": v(-10.56, -9.45) * mm});
            skLineSegment(sketch, "E2388", {"start": v(-10.56, -9.45) * mm, "end": v(-10.55, -9.55) * mm});
            skLineSegment(sketch, "E2389", {"start": v(-10.55, -9.55) * mm, "end": v(-10.54, -9.65) * mm});
            skLineSegment(sketch, "E2390", {"start": v(-10.54, -9.65) * mm, "end": v(-10.54, -9.75) * mm});
            skLineSegment(sketch, "E2391", {"start": v(-10.54, -9.75) * mm, "end": v(-10.53, -9.84) * mm});
            skLineSegment(sketch, "E2392", {"start": v(-10.53, -9.84) * mm, "end": v(-10.51, -9.95) * mm});
            skLineSegment(sketch, "E2393", {"start": v(-10.51, -9.95) * mm, "end": v(-10.5, -10.05) * mm});
            skLineSegment(sketch, "E2394", {"start": v(-10.5, -10.05) * mm, "end": v(-10.42, -10.66) * mm});
            skLineSegment(sketch, "E2395", {"start": v(-10.42, -10.66) * mm, "end": v(-9.97, -10.78) * mm});
            skLineSegment(sketch, "E2396", {"start": v(-9.97, -10.78) * mm, "end": v(-9.63, -10.86) * mm});
            skLineSegment(sketch, "E2397", {"start": v(-9.63, -10.86) * mm, "end": v(-9.27, -10.36) * mm});
            skLineSegment(sketch, "E2398", {"start": v(-9.27, -10.36) * mm, "end": v(-9.21, -10.27) * mm});
            skLineSegment(sketch, "E2399", {"start": v(-9.21, -10.27) * mm, "end": v(-9.15, -10.19) * mm});
            skLineSegment(sketch, "E2400", {"start": v(-9.15, -10.19) * mm, "end": v(-9.1, -10.1) * mm});
            skLineSegment(sketch, "E2401", {"start": v(-9.1, -10.1) * mm, "end": v(-9.04, -10.02) * mm});
            skLineSegment(sketch, "E2402", {"start": v(-9.04, -10.02) * mm, "end": v(-8.99, -9.94) * mm});
            skLineSegment(sketch, "E2403", {"start": v(-8.99, -9.94) * mm, "end": v(-8.94, -9.86) * mm});
            skLineSegment(sketch, "E2404", {"start": v(-8.94, -9.86) * mm, "end": v(-8.89, -9.78) * mm});
            skLineSegment(sketch, "E2405", {"start": v(-8.89, -9.78) * mm, "end": v(-8.85, -9.71) * mm});
            skLineSegment(sketch, "E2406", {"start": v(-8.85, -9.71) * mm, "end": v(-8.8, -9.63) * mm});
            skLineSegment(sketch, "E2407", {"start": v(-8.8, -9.63) * mm, "end": v(-8.75, -9.55) * mm});
            skLineSegment(sketch, "E2408", {"start": v(-8.75, -9.55) * mm, "end": v(-8.7, -9.48) * mm});
            skLineSegment(sketch, "E2409", {"start": v(-8.7, -9.48) * mm, "end": v(-8.67, -9.42) * mm});
            skLineSegment(sketch, "E2410", {"start": v(-8.67, -9.42) * mm, "end": v(-8.63, -9.34) * mm});
            skLineSegment(sketch, "E2411", {"start": v(-8.63, -9.34) * mm, "end": v(-8.6, -9.28) * mm});
            skLineSegment(sketch, "E2412", {"start": v(-8.6, -9.28) * mm, "end": v(-8.56, -9.22) * mm});
            skLineSegment(sketch, "E2413", {"start": v(-8.56, -9.22) * mm, "end": v(-8.52, -9.15) * mm});
            skLineSegment(sketch, "E2414", {"start": v(-8.52, -9.15) * mm, "end": v(-8.48, -9.08) * mm});
            skLineSegment(sketch, "E2415", {"start": v(-8.48, -9.08) * mm, "end": v(-8.45, -9.02) * mm});
            skLineSegment(sketch, "E2416", {"start": v(-8.45, -9.02) * mm, "end": v(-8.34, -8.82) * mm});
            skLineSegment(sketch, "E2417", {"start": v(-8.34, -8.82) * mm, "end": v(-8.34, -8.8) * mm});
            skLineSegment(sketch, "E2418", {"start": v(-8.34, -8.8) * mm, "end": v(-8.33, -8.8) * mm});
            skLineSegment(sketch, "E2419", {"start": v(-8.33, -8.8) * mm, "end": v(-8.32, -8.78) * mm});
            skLineSegment(sketch, "E2420", {"start": v(-8.32, -8.78) * mm, "end": v(-8.3, -8.76) * mm});
            skLineSegment(sketch, "E2421", {"start": v(-8.3, -8.76) * mm, "end": v(-8.3, -8.75) * mm});
            skLineSegment(sketch, "E2422", {"start": v(-8.3, -8.75) * mm, "end": v(-8.28, -8.74) * mm});
            skLineSegment(sketch, "E2423", {"start": v(-8.28, -8.74) * mm, "end": v(-8.27, -8.73) * mm});
            skLineSegment(sketch, "E2424", {"start": v(-8.27, -8.73) * mm, "end": v(-8.26, -8.73) * mm});
            skLineSegment(sketch, "E2425", {"start": v(-8.26, -8.73) * mm, "end": v(-8.25, -8.72) * mm});
            skLineSegment(sketch, "E2426", {"start": v(-8.25, -8.72) * mm, "end": v(-8.24, -8.72) * mm});
            skLineSegment(sketch, "E2427", {"start": v(-8.24, -8.72) * mm, "end": v(-8.23, -8.72) * mm});
            skLineSegment(sketch, "E2428", {"start": v(-8.23, -8.72) * mm, "end": v(-8.23, -8.72) * mm});
            skLineSegment(sketch, "E2429", {"start": v(-8.23, -8.72) * mm, "end": v(-8.04, -8.76) * mm});
            skLineSegment(sketch, "E2430", {"start": v(-8.04, -8.76) * mm, "end": v(-7.77, -8.81) * mm});
            skLineSegment(sketch, "E2431", {"start": v(-7.77, -8.81) * mm, "end": v(-7.57, -8.85) * mm});
            skLineSegment(sketch, "E2432", {"start": v(-7.57, -8.85) * mm, "end": v(-7.56, -8.85) * mm});
            skLineSegment(sketch, "E2433", {"start": v(-7.56, -8.85) * mm, "end": v(-7.56, -8.86) * mm});
            skLineSegment(sketch, "E2434", {"start": v(-7.56, -8.86) * mm, "end": v(-7.55, -8.87) * mm});
            skLineSegment(sketch, "E2435", {"start": v(-7.55, -8.87) * mm, "end": v(-7.54, -8.88) * mm});
            skLineSegment(sketch, "E2436", {"start": v(-7.54, -8.88) * mm, "end": v(-7.53, -8.9) * mm});
            skLineSegment(sketch, "E2437", {"start": v(-7.53, -8.9) * mm, "end": v(-7.52, -8.9) * mm});
            skLineSegment(sketch, "E2438", {"start": v(-7.52, -8.9) * mm, "end": v(-7.52, -8.92) * mm});
            skLineSegment(sketch, "E2439", {"start": v(-7.52, -8.92) * mm, "end": v(-7.5, -8.94) * mm});
            skLineSegment(sketch, "E2440", {"start": v(-7.5, -8.94) * mm, "end": v(-7.5, -8.96) * mm});
            skLineSegment(sketch, "E2441", {"start": v(-7.5, -8.96) * mm, "end": v(-7.5, -8.99) * mm});
            skLineSegment(sketch, "E2442", {"start": v(-7.5, -8.99) * mm, "end": v(-7.5, -9) * mm});
            skLineSegment(sketch, "E2443", {"start": v(-7.5, -9) * mm, "end": v(-7.47, -9.28) * mm});
            skLineSegment(sketch, "E2444", {"start": v(-7.47, -9.28) * mm, "end": v(-7.47, -9.36) * mm});
            skLineSegment(sketch, "E2445", {"start": v(-7.47, -9.36) * mm, "end": v(-7.46, -9.43) * mm});
            skLineSegment(sketch, "E2446", {"start": v(-7.46, -9.43) * mm, "end": v(-7.45, -9.5) * mm});
            skLineSegment(sketch, "E2447", {"start": v(-7.45, -9.5) * mm, "end": v(-7.44, -9.58) * mm});
            skLineSegment(sketch, "E2448", {"start": v(-7.44, -9.58) * mm, "end": v(-7.44, -9.66) * mm});
            skLineSegment(sketch, "E2449", {"start": v(-7.44, -9.66) * mm, "end": v(-7.43, -9.74) * mm});
            skLineSegment(sketch, "E2450", {"start": v(-7.43, -9.74) * mm, "end": v(-7.41, -9.82) * mm});
            skLineSegment(sketch, "E2451", {"start": v(-7.41, -9.82) * mm, "end": v(-7.4, -9.9) * mm});
            skLineSegment(sketch, "E2452", {"start": v(-7.4, -9.9) * mm, "end": v(-7.39, -10) * mm});
            skLineSegment(sketch, "E2453", {"start": v(-7.39, -10) * mm, "end": v(-7.37, -10.09) * mm});
            skLineSegment(sketch, "E2454", {"start": v(-7.37, -10.09) * mm, "end": v(-7.36, -10.18) * mm});
            skLineSegment(sketch, "E2455", {"start": v(-7.36, -10.18) * mm, "end": v(-7.34, -10.27) * mm});
            skLineSegment(sketch, "E2456", {"start": v(-7.34, -10.27) * mm, "end": v(-7.33, -10.35) * mm});
            skLineSegment(sketch, "E2457", {"start": v(-7.33, -10.35) * mm, "end": v(-7.3, -10.46) * mm});
            skLineSegment(sketch, "E2458", {"start": v(-7.3, -10.46) * mm, "end": v(-7.3, -10.54) * mm});
            skLineSegment(sketch, "E2459", {"start": v(-7.3, -10.54) * mm, "end": v(-7.27, -10.64) * mm});
            skLineSegment(sketch, "E2460", {"start": v(-7.27, -10.64) * mm, "end": v(-7.25, -10.73) * mm});
            skLineSegment(sketch, "E2461", {"start": v(-7.25, -10.73) * mm, "end": v(-7.23, -10.84) * mm});
            skLineSegment(sketch, "E2462", {"start": v(-7.23, -10.84) * mm, "end": v(-7.11, -11.37) * mm});
            skLineSegment(sketch, "E2463", {"start": v(-7.11, -11.37) * mm, "end": v(-6.68, -11.44) * mm});
            skLineSegment(sketch, "E2464", {"start": v(-6.68, -11.44) * mm, "end": v(-6.3, -11.5) * mm});
            skLineSegment(sketch, "E2465", {"start": v(-6.3, -11.5) * mm, "end": v(-6.02, -11) * mm});
            skLineSegment(sketch, "E2466", {"start": v(-6.02, -11) * mm, "end": v(-5.97, -10.92) * mm});
            skLineSegment(sketch, "E2467", {"start": v(-5.97, -10.92) * mm, "end": v(-5.92, -10.84) * mm});
            skLineSegment(sketch, "E2468", {"start": v(-5.92, -10.84) * mm, "end": v(-5.87, -10.75) * mm});
            skLineSegment(sketch, "E2469", {"start": v(-5.87, -10.75) * mm, "end": v(-5.83, -10.67) * mm});
            skLineSegment(sketch, "E2470", {"start": v(-5.83, -10.67) * mm, "end": v(-5.78, -10.58) * mm});
            skLineSegment(sketch, "E2471", {"start": v(-5.78, -10.58) * mm, "end": v(-5.74, -10.5) * mm});
            skLineSegment(sketch, "E2472", {"start": v(-5.74, -10.5) * mm, "end": v(-5.7, -10.43) * mm});
            skLineSegment(sketch, "E2473", {"start": v(-5.7, -10.43) * mm, "end": v(-5.66, -10.35) * mm});
            skLineSegment(sketch, "E2474", {"start": v(-5.66, -10.35) * mm, "end": v(-5.62, -10.27) * mm});
            skLineSegment(sketch, "E2475", {"start": v(-5.62, -10.27) * mm, "end": v(-5.58, -10.2) * mm});
            skLineSegment(sketch, "E2476", {"start": v(-5.58, -10.2) * mm, "end": v(-5.54, -10.12) * mm});
            skLineSegment(sketch, "E2477", {"start": v(-5.54, -10.12) * mm, "end": v(-5.52, -10.07) * mm});
            skLineSegment(sketch, "E2478", {"start": v(-5.52, -10.07) * mm, "end": v(-5.48, -9.99) * mm});
            skLineSegment(sketch, "E2479", {"start": v(-5.48, -9.99) * mm, "end": v(-5.45, -9.92) * mm});
            skLineSegment(sketch, "E2480", {"start": v(-5.45, -9.92) * mm, "end": v(-5.42, -9.86) * mm});
            skLineSegment(sketch, "E2481", {"start": v(-5.42, -9.86) * mm, "end": v(-5.39, -9.8) * mm});
            skLineSegment(sketch, "E2482", {"start": v(-5.39, -9.8) * mm, "end": v(-5.36, -9.73) * mm});
            skLineSegment(sketch, "E2483", {"start": v(-5.36, -9.73) * mm, "end": v(-5.33, -9.66) * mm});
            skLineSegment(sketch, "E2484", {"start": v(-5.33, -9.66) * mm, "end": v(-5.3, -9.6) * mm});
            skLineSegment(sketch, "E2485", {"start": v(-5.3, -9.6) * mm, "end": v(-5.28, -9.55) * mm});
            skLineSegment(sketch, "E2486", {"start": v(-5.28, -9.55) * mm, "end": v(-5.2, -9.34) * mm});
            skLineSegment(sketch, "E2487", {"start": v(-5.2, -9.34) * mm, "end": v(-5.2, -9.34) * mm});
            skLineSegment(sketch, "E2488", {"start": v(-5.2, -9.34) * mm, "end": v(-5.18, -9.32) * mm});
            skLineSegment(sketch, "E2489", {"start": v(-5.18, -9.32) * mm, "end": v(-5.17, -9.3) * mm});
            skLineSegment(sketch, "E2490", {"start": v(-5.17, -9.3) * mm, "end": v(-5.17, -9.3) * mm});
            skLineSegment(sketch, "E2491", {"start": v(-5.17, -9.3) * mm, "end": v(-5.16, -9.28) * mm});
            skLineSegment(sketch, "E2492", {"start": v(-5.16, -9.28) * mm, "end": v(-5.15, -9.27) * mm});
            skLineSegment(sketch, "E2493", {"start": v(-5.15, -9.27) * mm, "end": v(-5.14, -9.27) * mm});
            skLineSegment(sketch, "E2494", {"start": v(-5.14, -9.27) * mm, "end": v(-5.13, -9.26) * mm});
            skLineSegment(sketch, "E2495", {"start": v(-5.13, -9.26) * mm, "end": v(-5.12, -9.25) * mm});
            skLineSegment(sketch, "E2496", {"start": v(-5.12, -9.25) * mm, "end": v(-5.11, -9.25) * mm});
            skLineSegment(sketch, "E2497", {"start": v(-5.11, -9.25) * mm, "end": v(-5.1, -9.25) * mm});
            skLineSegment(sketch, "E2498", {"start": v(-5.1, -9.25) * mm, "end": v(-5.1, -9.24) * mm});
            skLineSegment(sketch, "E2499", {"start": v(-5.1, -9.24) * mm, "end": v(-5.1, -9.24) * mm});
            skLineSegment(sketch, "E2500", {"start": v(-5.1, -9.24) * mm, "end": v(-4.88, -9.27) * mm});
            skLineSegment(sketch, "E2501", {"start": v(-4.88, -9.27) * mm, "end": v(-4.63, -9.3) * mm});
            skLineSegment(sketch, "E2502", {"start": v(-4.63, -9.3) * mm, "end": v(-4.42, -9.32) * mm});
            skLineSegment(sketch, "E2503", {"start": v(-4.42, -9.32) * mm, "end": v(-4.42, -9.32) * mm});
            skLineSegment(sketch, "E2504", {"start": v(-4.42, -9.32) * mm, "end": v(-4.41, -9.33) * mm});
            skLineSegment(sketch, "E2505", {"start": v(-4.41, -9.33) * mm, "end": v(-4.4, -9.33) * mm});
            skLineSegment(sketch, "E2506", {"start": v(-4.4, -9.33) * mm, "end": v(-4.4, -9.34) * mm});
            skLineSegment(sketch, "E2507", {"start": v(-4.4, -9.34) * mm, "end": v(-4.39, -9.35) * mm});
            skLineSegment(sketch, "E2508", {"start": v(-4.39, -9.35) * mm, "end": v(-4.38, -9.36) * mm});
            skLineSegment(sketch, "E2509", {"start": v(-4.38, -9.36) * mm, "end": v(-4.37, -9.37) * mm});
            skLineSegment(sketch, "E2510", {"start": v(-4.37, -9.37) * mm, "end": v(-4.37, -9.39) * mm});
            skLineSegment(sketch, "E2511", {"start": v(-4.37, -9.39) * mm, "end": v(-4.36, -9.4) * mm});
            skLineSegment(sketch, "E2512", {"start": v(-4.36, -9.4) * mm, "end": v(-4.36, -9.42) * mm});
            skLineSegment(sketch, "E2513", {"start": v(-4.36, -9.42) * mm, "end": v(-4.35, -9.45) * mm});
            skLineSegment(sketch, "E2514", {"start": v(-4.35, -9.45) * mm, "end": v(-4.35, -9.45) * mm});
            skLineSegment(sketch, "E2515", {"start": v(-4.35, -9.45) * mm, "end": v(-4.3, -9.7) * mm});
            skLineSegment(sketch, "E2516", {"start": v(-4.3, -9.7) * mm, "end": v(-4.3, -9.76) * mm});
            skLineSegment(sketch, "E2517", {"start": v(-4.3, -9.76) * mm, "end": v(-4.28, -9.83) * mm});
            skLineSegment(sketch, "E2518", {"start": v(-4.28, -9.83) * mm, "end": v(-4.27, -9.9) * mm});
            skLineSegment(sketch, "E2519", {"start": v(-4.27, -9.9) * mm, "end": v(-4.25, -9.98) * mm});
            skLineSegment(sketch, "E2520", {"start": v(-4.25, -9.98) * mm, "end": v(-4.24, -10.06) * mm});
            skLineSegment(sketch, "E2521", {"start": v(-4.24, -10.06) * mm, "end": v(-4.22, -10.13) * mm});
            skLineSegment(sketch, "E2522", {"start": v(-4.22, -10.13) * mm, "end": v(-4.2, -10.2) * mm});
            skLineSegment(sketch, "E2523", {"start": v(-4.2, -10.2) * mm, "end": v(-4.19, -10.28) * mm});
            skLineSegment(sketch, "E2524", {"start": v(-4.19, -10.28) * mm, "end": v(-4.17, -10.36) * mm});
            skLineSegment(sketch, "E2525", {"start": v(-4.17, -10.36) * mm, "end": v(-4.15, -10.45) * mm});
            skLineSegment(sketch, "E2526", {"start": v(-4.15, -10.45) * mm, "end": v(-4.13, -10.53) * mm});
            skLineSegment(sketch, "E2527", {"start": v(-4.13, -10.53) * mm, "end": v(-4.11, -10.6) * mm});
            skLineSegment(sketch, "E2528", {"start": v(-4.11, -10.6) * mm, "end": v(-4.09, -10.7) * mm});
            skLineSegment(sketch, "E2529", {"start": v(-4.09, -10.7) * mm, "end": v(-4.07, -10.78) * mm});
            skLineSegment(sketch, "E2530", {"start": v(-4.07, -10.78) * mm, "end": v(-4.04, -10.86) * mm});
            skLineSegment(sketch, "E2531", {"start": v(-4.04, -10.86) * mm, "end": v(-4.02, -10.95) * mm});
            skLineSegment(sketch, "E2532", {"start": v(-4.02, -10.95) * mm, "end": v(-4, -11.02) * mm});
            skLineSegment(sketch, "E2533", {"start": v(-4, -11.02) * mm, "end": v(-3.97, -11.1) * mm});
            skLineSegment(sketch, "E2534", {"start": v(-3.97, -11.1) * mm, "end": v(-3.95, -11.2) * mm});
            skLineSegment(sketch, "E2535", {"start": v(-3.95, -11.2) * mm, "end": v(-3.92, -11.28) * mm});
            skLineSegment(sketch, "E2536", {"start": v(-3.92, -11.28) * mm, "end": v(-3.76, -11.8) * mm});
            skLineSegment(sketch, "E2537", {"start": v(-3.76, -11.8) * mm, "end": v(-3.56, -11.8) * mm});
            skLineSegment(sketch, "E2538", {"start": v(-3.56, -11.8) * mm, "end": v(-3.07, -11.85) * mm});
            skLineSegment(sketch, "E2539", {"start": v(-3.07, -11.85) * mm, "end": v(-2.95, -11.85) * mm});
            skLineSegment(sketch, "E2540", {"start": v(-2.95, -11.85) * mm, "end": v(-2.7, -11.36) * mm});
            skLineSegment(sketch, "E2541", {"start": v(-2.7, -11.36) * mm, "end": v(-2.67, -11.27) * mm});
            skLineSegment(sketch, "E2542", {"start": v(-2.67, -11.27) * mm, "end": v(-2.63, -11.19) * mm});
            skLineSegment(sketch, "E2543", {"start": v(-2.63, -11.19) * mm, "end": v(-2.6, -11.1) * mm});
            skLineSegment(sketch, "E2544", {"start": v(-2.6, -11.1) * mm, "end": v(-2.56, -11.03) * mm});
            skLineSegment(sketch, "E2545", {"start": v(-2.56, -11.03) * mm, "end": v(-2.52, -10.94) * mm});
            skLineSegment(sketch, "E2546", {"start": v(-2.52, -10.94) * mm, "end": v(-2.49, -10.87) * mm});
            skLineSegment(sketch, "E2547", {"start": v(-2.49, -10.87) * mm, "end": v(-2.45, -10.8) * mm});
            skLineSegment(sketch, "E2548", {"start": v(-2.45, -10.8) * mm, "end": v(-2.42, -10.72) * mm});
            skLineSegment(sketch, "E2549", {"start": v(-2.42, -10.72) * mm, "end": v(-2.4, -10.65) * mm});
            skLineSegment(sketch, "E2550", {"start": v(-2.4, -10.65) * mm, "end": v(-2.36, -10.58) * mm});
            skLineSegment(sketch, "E2551", {"start": v(-2.36, -10.58) * mm, "end": v(-2.33, -10.5) * mm});
            skLineSegment(sketch, "E2552", {"start": v(-2.33, -10.5) * mm, "end": v(-2.3, -10.44) * mm});
            skLineSegment(sketch, "E2553", {"start": v(-2.3, -10.44) * mm, "end": v(-2.28, -10.37) * mm});
            skLineSegment(sketch, "E2554", {"start": v(-2.28, -10.37) * mm, "end": v(-2.26, -10.31) * mm});
            skLineSegment(sketch, "E2555", {"start": v(-2.26, -10.31) * mm, "end": v(-2.23, -10.24) * mm});
            skLineSegment(sketch, "E2556", {"start": v(-2.23, -10.24) * mm, "end": v(-2.21, -10.2) * mm});
            skLineSegment(sketch, "E2557", {"start": v(-2.21, -10.2) * mm, "end": v(-2.18, -10.11) * mm});
            skLineSegment(sketch, "E2558", {"start": v(-2.18, -10.11) * mm, "end": v(-2.17, -10.07) * mm});
            skLineSegment(sketch, "E2559", {"start": v(-2.17, -10.07) * mm, "end": v(-2.14, -10) * mm});
            skLineSegment(sketch, "E2560", {"start": v(-2.14, -10) * mm, "end": v(-2.12, -9.95) * mm});
            skLineSegment(sketch, "E2561", {"start": v(-2.12, -9.95) * mm, "end": v(-2.1, -9.89) * mm});
            skLineSegment(sketch, "E2562", {"start": v(-2.1, -9.89) * mm, "end": v(-2.08, -9.82) * mm});
            skLineSegment(sketch, "E2563", {"start": v(-2.08, -9.82) * mm, "end": v(-2.01, -9.63) * mm});
            skLineSegment(sketch, "E2564", {"start": v(-2.01, -9.63) * mm, "end": v(-2, -9.61) * mm});
            skLineSegment(sketch, "E2565", {"start": v(-2, -9.61) * mm, "end": v(-2, -9.6) * mm});
            skLineSegment(sketch, "E2566", {"start": v(-2, -9.6) * mm, "end": v(-2, -9.59) * mm});
            skLineSegment(sketch, "E2567", {"start": v(-2, -9.59) * mm, "end": v(-1.99, -9.57) * mm});
            skLineSegment(sketch, "E2568", {"start": v(-1.99, -9.57) * mm, "end": v(-1.98, -9.56) * mm});
            skLineSegment(sketch, "E2569", {"start": v(-1.98, -9.56) * mm, "end": v(-1.98, -9.55) * mm});
            skLineSegment(sketch, "E2570", {"start": v(-1.98, -9.55) * mm, "end": v(-1.97, -9.54) * mm});
            skLineSegment(sketch, "E2571", {"start": v(-1.97, -9.54) * mm, "end": v(-1.96, -9.54) * mm});
            skLineSegment(sketch, "E2572", {"start": v(-1.96, -9.54) * mm, "end": v(-1.95, -9.53) * mm});
            skLineSegment(sketch, "E2573", {"start": v(-1.95, -9.53) * mm, "end": v(-1.95, -9.52) * mm});
            skLineSegment(sketch, "E2574", {"start": v(-1.95, -9.52) * mm, "end": v(-1.94, -9.52) * mm});
            skLineSegment(sketch, "E2575", {"start": v(-1.94, -9.52) * mm, "end": v(-1.93, -9.52) * mm});
            skLineSegment(sketch, "E2576", {"start": v(-1.93, -9.52) * mm, "end": v(-1.93, -9.51) * mm});
            skLineSegment(sketch, "E2577", {"start": v(-1.93, -9.51) * mm, "end": v(-1.92, -9.51) * mm});
            skLineSegment(sketch, "E2578", {"start": v(-1.92, -9.51) * mm, "end": v(-1.7, -9.52) * mm});
            skLineSegment(sketch, "E2579", {"start": v(-1.7, -9.52) * mm, "end": v(-1.47, -9.53) * mm});
            skLineSegment(sketch, "E2580", {"start": v(-1.47, -9.53) * mm, "end": v(-1.24, -9.54) * mm});
            skLineSegment(sketch, "E2581", {"start": v(-1.24, -9.54) * mm, "end": v(-1.24, -9.54) * mm});
            skLineSegment(sketch, "E2582", {"start": v(-1.24, -9.54) * mm, "end": v(-1.23, -9.54) * mm});
            skLineSegment(sketch, "E2583", {"start": v(-1.23, -9.54) * mm, "end": v(-1.23, -9.55) * mm});
            skLineSegment(sketch, "E2584", {"start": v(-1.23, -9.55) * mm, "end": v(-1.22, -9.55) * mm});
            skLineSegment(sketch, "E2585", {"start": v(-1.22, -9.55) * mm, "end": v(-1.21, -9.56) * mm});
            skLineSegment(sketch, "E2586", {"start": v(-1.21, -9.56) * mm, "end": v(-1.2, -9.57) * mm});
            skLineSegment(sketch, "E2587", {"start": v(-1.2, -9.57) * mm, "end": v(-1.2, -9.58) * mm});
            skLineSegment(sketch, "E2588", {"start": v(-1.2, -9.58) * mm, "end": v(-1.2, -9.59) * mm});
            skLineSegment(sketch, "E2589", {"start": v(-1.2, -9.59) * mm, "end": v(-1.18, -9.6) * mm});
            skLineSegment(sketch, "E2590", {"start": v(-1.18, -9.6) * mm, "end": v(-1.18, -9.62) * mm});
            skLineSegment(sketch, "E2591", {"start": v(-1.18, -9.62) * mm, "end": v(-1.17, -9.63) * mm});
            skLineSegment(sketch, "E2592", {"start": v(-1.17, -9.63) * mm, "end": v(-1.17, -9.65) * mm});
            skLineSegment(sketch, "E2593", {"start": v(-1.17, -9.65) * mm, "end": v(-1.16, -9.65) * mm});
            skLineSegment(sketch, "E2594", {"start": v(-1.16, -9.65) * mm, "end": v(-1.1, -9.88) * mm});
            skLineSegment(sketch, "E2595", {"start": v(-1.1, -9.88) * mm, "end": v(-1.09, -9.95) * mm});
            skLineSegment(sketch, "E2596", {"start": v(-1.09, -9.95) * mm, "end": v(-1.07, -10.01) * mm});
            skLineSegment(sketch, "E2597", {"start": v(-1.07, -10.01) * mm, "end": v(-1.05, -10.08) * mm});
            skLineSegment(sketch, "E2598", {"start": v(-1.05, -10.08) * mm, "end": v(-1.03, -10.15) * mm});
            skLineSegment(sketch, "E2599", {"start": v(-1.03, -10.15) * mm, "end": v(-1.02, -10.21) * mm});
            skLineSegment(sketch, "E2600", {"start": v(-1.02, -10.21) * mm, "end": v(-1, -10.28) * mm});
            skLineSegment(sketch, "E2601", {"start": v(-1, -10.28) * mm, "end": v(-0.97, -10.35) * mm});
            skLineSegment(sketch, "E2602", {"start": v(-0.97, -10.35) * mm, "end": v(-0.95, -10.42) * mm});
            skLineSegment(sketch, "E2603", {"start": v(-0.95, -10.42) * mm, "end": v(-0.93, -10.5) * mm});
            skLineSegment(sketch, "E2604", {"start": v(-0.93, -10.5) * mm, "end": v(-0.91, -10.56) * mm});
            skLineSegment(sketch, "E2605", {"start": v(-0.91, -10.56) * mm, "end": v(-0.89, -10.63) * mm});
            skLineSegment(sketch, "E2606", {"start": v(-0.89, -10.63) * mm, "end": v(-0.86, -10.7) * mm});
            skLineSegment(sketch, "E2607", {"start": v(-0.86, -10.7) * mm, "end": v(-0.84, -10.78) * mm});
            skLineSegment(sketch, "E2608", {"start": v(-0.84, -10.78) * mm, "end": v(-0.82, -10.84) * mm});
            skLineSegment(sketch, "E2609", {"start": v(-0.82, -10.84) * mm, "end": v(-0.79, -10.92) * mm});
            skLineSegment(sketch, "E2610", {"start": v(-0.79, -10.92) * mm, "end": v(-0.76, -11) * mm});
            skLineSegment(sketch, "E2611", {"start": v(-0.76, -11) * mm, "end": v(-0.74, -11.07) * mm});
            skLineSegment(sketch, "E2612", {"start": v(-0.74, -11.07) * mm, "end": v(-0.71, -11.14) * mm});
            skLineSegment(sketch, "E2613", {"start": v(-0.71, -11.14) * mm, "end": v(-0.68, -11.22) * mm});
            skLineSegment(sketch, "E2614", {"start": v(-0.68, -11.22) * mm, "end": v(-0.66, -11.28) * mm});
            skLineSegment(sketch, "E2615", {"start": v(-0.66, -11.28) * mm, "end": v(-0.63, -11.36) * mm});
            skLineSegment(sketch, "E2616", {"start": v(-0.63, -11.36) * mm, "end": v(-0.58, -11.48) * mm});
            skLineSegment(sketch, "E2617", {"start": v(-0.58, -11.48) * mm, "end": v(-0.4, -11.95) * mm});
            skLineSegment(sketch, "E2618", {"start": v(-0.4, -11.95) * mm, "end": v(-0.23, -11.95) * mm});
            skLineSegment(sketch, "E2619", {"start": v(-0.23, -11.95) * mm, "end": v(0.21, -11.95) * mm});
            skLineSegment(sketch, "E2620", {"start": v(0.21, -11.95) * mm, "end": v(0.42, -11.95) * mm});
            skPoint(sketch, "E2621", {"position": v(0, 0) * mm});
            skCircle(sketch, "E2622", {"center": v(0, 0) * mm, "radius": 5.5 * mm});
            skSolve(sketch);
        }
        {
            var Q0;
            Q0=qSketchRegion(id+"F1",true);
            extrude(context, id + "F2", {"entities" : qUnion([Q0]), "endBound" : BoundingType.SYMMETRIC, "depth" : 5 * mm, "offsetDistance" : 25 * mm});
        }
        {
            var Q0;
            Q0=makeQuery(id+"F2.opExtrude","SWEPT_BODY",BODY,{"disambiguationData":[OSD([sQuery(id+"F1.wireOp",EDGE,"E15"),sQuery(id+"F1.wireOp",EDGE,"E16"),sQuery(id+"F1.wireOp",EDGE,"E17"),sQuery(id+"F1.wireOp",EDGE,"E18"),sQuery(id+"F1.wireOp",EDGE,"E19"),sQuery(id+"F1.wireOp",EDGE,"E20"),sQuery(id+"F1.wireOp",EDGE,"E21"),sQuery(id+"F1.wireOp",EDGE,"E22"),sQuery(id+"F1.wireOp",EDGE,"E23"),sQuery(id+"F1.wireOp",EDGE,"E24"),sQuery(id+"F1.wireOp",EDGE,"E25"),sQuery(id+"F1.wireOp",EDGE,"E26"),sQuery(id+"F1.wireOp",EDGE,"E27"),sQuery(id+"F1.wireOp",EDGE,"E28"),sQuery(id+"F1.wireOp",EDGE,"E29"),sQuery(id+"F1.wireOp",EDGE,"E30"),sQuery(id+"F1.wireOp",EDGE,"E31"),sQuery(id+"F1.wireOp",EDGE,"E32"),sQuery(id+"F1.wireOp",EDGE,"E33"),sQuery(id+"F1.wireOp",EDGE,"E34"),sQuery(id+"F1.wireOp",EDGE,"E35"),sQuery(id+"F1.wireOp",EDGE,"E36"),sQuery(id+"F1.wireOp",EDGE,"E37"),sQuery(id+"F1.wireOp",EDGE,"E38"),sQuery(id+"F1.wireOp",EDGE,"E39"),sQuery(id+"F1.wireOp",EDGE,"E40"),sQuery(id+"F1.wireOp",EDGE,"E41"),sQuery(id+"F1.wireOp",EDGE,"E42"),sQuery(id+"F1.wireOp",EDGE,"E43"),sQuery(id+"F1.wireOp",EDGE,"E44"),sQuery(id+"F1.wireOp",EDGE,"E45"),sQuery(id+"F1.wireOp",EDGE,"E45"),sQuery(id+"F1.wireOp",EDGE,"E46"),sQuery(id+"F1.wireOp",EDGE,"E47"),sQuery(id+"F1.wireOp",EDGE,"E48"),sQuery(id+"F1.wireOp",EDGE,"E49"),sQuery(id+"F1.wireOp",EDGE,"E50"),sQuery(id+"F1.wireOp",EDGE,"E51"),sQuery(id+"F1.wireOp",EDGE,"E52"),sQuery(id+"F1.wireOp",EDGE,"E53"),sQuery(id+"F1.wireOp",EDGE,"E54"),sQuery(id+"F1.wireOp",EDGE,"E55"),sQuery(id+"F1.wireOp",EDGE,"E56"),sQuery(id+"F1.wireOp",EDGE,"E57"),sQuery(id+"F1.wireOp",EDGE,"E58"),sQuery(id+"F1.wireOp",EDGE,"E59"),sQuery(id+"F1.wireOp",EDGE,"E60"),sQuery(id+"F1.wireOp",EDGE,"E61"),sQuery(id+"F1.wireOp",EDGE,"E62"),sQuery(id+"F1.wireOp",EDGE,"E63"),sQuery(id+"F1.wireOp",EDGE,"E64"),sQuery(id+"F1.wireOp",EDGE,"E65"),sQuery(id+"F1.wireOp",EDGE,"E66"),sQuery(id+"F1.wireOp",EDGE,"E67"),sQuery(id+"F1.wireOp",EDGE,"E68"),sQuery(id+"F1.wireOp",EDGE,"E69"),sQuery(id+"F1.wireOp",EDGE,"E70"),sQuery(id+"F1.wireOp",EDGE,"E71"),sQuery(id+"F1.wireOp",EDGE,"E72"),sQuery(id+"F1.wireOp",EDGE,"E73"),sQuery(id+"F1.wireOp",EDGE,"E74"),sQuery(id+"F1.wireOp",EDGE,"E75"),sQuery(id+"F1.wireOp",EDGE,"E76"),sQuery(id+"F1.wireOp",EDGE,"E77"),sQuery(id+"F1.wireOp",EDGE,"E78"),sQuery(id+"F1.wireOp",EDGE,"E79"),sQuery(id+"F1.wireOp",EDGE,"E80"),sQuery(id+"F1.wireOp",EDGE,"E81"),sQuery(id+"F1.wireOp",EDGE,"E82"),sQuery(id+"F1.wireOp",EDGE,"E83"),sQuery(id+"F1.wireOp",EDGE,"E84"),sQuery(id+"F1.wireOp",EDGE,"E85"),sQuery(id+"F1.wireOp",EDGE,"E86"),sQuery(id+"F1.wireOp",EDGE,"E87"),sQuery(id+"F1.wireOp",EDGE,"E88"),sQuery(id+"F1.wireOp",EDGE,"E89"),sQuery(id+"F1.wireOp",EDGE,"E90"),sQuery(id+"F1.wireOp",EDGE,"E91"),sQuery(id+"F1.wireOp",EDGE,"E92"),sQuery(id+"F1.wireOp",EDGE,"E93"),sQuery(id+"F1.wireOp",EDGE,"E94"),sQuery(id+"F1.wireOp",EDGE,"E95"),sQuery(id+"F1.wireOp",EDGE,"E96"),sQuery(id+"F1.wireOp",EDGE,"E97"),sQuery(id+"F1.wireOp",EDGE,"E98"),sQuery(id+"F1.wireOp",EDGE,"E99"),sQuery(id+"F1.wireOp",EDGE,"E100"),sQuery(id+"F1.wireOp",EDGE,"E101"),sQuery(id+"F1.wireOp",EDGE,"E102"),sQuery(id+"F1.wireOp",EDGE,"E103"),sQuery(id+"F1.wireOp",EDGE,"E104"),sQuery(id+"F1.wireOp",EDGE,"E104"),sQuery(id+"F1.wireOp",EDGE,"E105"),sQuery(id+"F1.wireOp",EDGE,"E106"),sQuery(id+"F1.wireOp",EDGE,"E107"),sQuery(id+"F1.wireOp",EDGE,"E108"),sQuery(id+"F1.wireOp",EDGE,"E109"),sQuery(id+"F1.wireOp",EDGE,"E110"),sQuery(id+"F1.wireOp",EDGE,"E111"),sQuery(id+"F1.wireOp",EDGE,"E112"),sQuery(id+"F1.wireOp",EDGE,"E113"),sQuery(id+"F1.wireOp",EDGE,"E114"),sQuery(id+"F1.wireOp",EDGE,"E115"),sQuery(id+"F1.wireOp",EDGE,"E116"),sQuery(id+"F1.wireOp",EDGE,"E117"),sQuery(id+"F1.wireOp",EDGE,"E118"),sQuery(id+"F1.wireOp",EDGE,"E119"),sQuery(id+"F1.wireOp",EDGE,"E120"),sQuery(id+"F1.wireOp",EDGE,"E121"),sQuery(id+"F1.wireOp",EDGE,"E122"),sQuery(id+"F1.wireOp",EDGE,"E123"),sQuery(id+"F1.wireOp",EDGE,"E124"),sQuery(id+"F1.wireOp",EDGE,"E125"),sQuery(id+"F1.wireOp",EDGE,"E126"),sQuery(id+"F1.wireOp",EDGE,"E127"),sQuery(id+"F1.wireOp",EDGE,"E128"),sQuery(id+"F1.wireOp",EDGE,"E129"),sQuery(id+"F1.wireOp",EDGE,"E130"),sQuery(id+"F1.wireOp",EDGE,"E131"),sQuery(id+"F1.wireOp",EDGE,"E132"),sQuery(id+"F1.wireOp",EDGE,"E133"),sQuery(id+"F1.wireOp",EDGE,"E134"),sQuery(id+"F1.wireOp",EDGE,"E135"),sQuery(id+"F1.wireOp",EDGE,"E136"),sQuery(id+"F1.wireOp",EDGE,"E137"),sQuery(id+"F1.wireOp",EDGE,"E138"),sQuery(id+"F1.wireOp",EDGE,"E139"),sQuery(id+"F1.wireOp",EDGE,"E140"),sQuery(id+"F1.wireOp",EDGE,"E141"),sQuery(id+"F1.wireOp",EDGE,"E142"),sQuery(id+"F1.wireOp",EDGE,"E143"),sQuery(id+"F1.wireOp",EDGE,"E144"),sQuery(id+"F1.wireOp",EDGE,"E145"),sQuery(id+"F1.wireOp",EDGE,"E146"),sQuery(id+"F1.wireOp",EDGE,"E147"),sQuery(id+"F1.wireOp",EDGE,"E148"),sQuery(id+"F1.wireOp",EDGE,"E149"),sQuery(id+"F1.wireOp",EDGE,"E150"),sQuery(id+"F1.wireOp",EDGE,"E151"),sQuery(id+"F1.wireOp",EDGE,"E152"),sQuery(id+"F1.wireOp",EDGE,"E153"),sQuery(id+"F1.wireOp",EDGE,"E154"),sQuery(id+"F1.wireOp",EDGE,"E155"),sQuery(id+"F1.wireOp",EDGE,"E156"),sQuery(id+"F1.wireOp",EDGE,"E157"),sQuery(id+"F1.wireOp",EDGE,"E158"),sQuery(id+"F1.wireOp",EDGE,"E159"),sQuery(id+"F1.wireOp",EDGE,"E160"),sQuery(id+"F1.wireOp",EDGE,"E161"),sQuery(id+"F1.wireOp",EDGE,"E162"),sQuery(id+"F1.wireOp",EDGE,"E163"),sQuery(id+"F1.wireOp",EDGE,"E164"),sQuery(id+"F1.wireOp",EDGE,"E165"),sQuery(id+"F1.wireOp",EDGE,"E166"),sQuery(id+"F1.wireOp",EDGE,"E167"),sQuery(id+"F1.wireOp",EDGE,"E168"),sQuery(id+"F1.wireOp",EDGE,"E169"),sQuery(id+"F1.wireOp",EDGE,"E170"),sQuery(id+"F1.wireOp",EDGE,"E171"),sQuery(id+"F1.wireOp",EDGE,"E172"),sQuery(id+"F1.wireOp",EDGE,"E173"),sQuery(id+"F1.wireOp",EDGE,"E174"),sQuery(id+"F1.wireOp",EDGE,"E175"),sQuery(id+"F1.wireOp",EDGE,"E176"),sQuery(id+"F1.wireOp",EDGE,"E177"),sQuery(id+"F1.wireOp",EDGE,"E178"),sQuery(id+"F1.wireOp",EDGE,"E179"),sQuery(id+"F1.wireOp",EDGE,"E180"),sQuery(id+"F1.wireOp",EDGE,"E181"),sQuery(id+"F1.wireOp",EDGE,"E182"),sQuery(id+"F1.wireOp",EDGE,"E183"),sQuery(id+"F1.wireOp",EDGE,"E184"),sQuery(id+"F1.wireOp",EDGE,"E185"),sQuery(id+"F1.wireOp",EDGE,"E186"),sQuery(id+"F1.wireOp",EDGE,"E187"),sQuery(id+"F1.wireOp",EDGE,"E188"),sQuery(id+"F1.wireOp",EDGE,"E189"),sQuery(id+"F1.wireOp",EDGE,"E190"),sQuery(id+"F1.wireOp",EDGE,"E191"),sQuery(id+"F1.wireOp",EDGE,"E192"),sQuery(id+"F1.wireOp",EDGE,"E193"),sQuery(id+"F1.wireOp",EDGE,"E194"),sQuery(id+"F1.wireOp",EDGE,"E195"),sQuery(id+"F1.wireOp",EDGE,"E196"),sQuery(id+"F1.wireOp",EDGE,"E197"),sQuery(id+"F1.wireOp",EDGE,"E198"),sQuery(id+"F1.wireOp",EDGE,"E199"),sQuery(id+"F1.wireOp",EDGE,"E200"),sQuery(id+"F1.wireOp",EDGE,"E201"),sQuery(id+"F1.wireOp",EDGE,"E202"),sQuery(id+"F1.wireOp",EDGE,"E203"),sQuery(id+"F1.wireOp",EDGE,"E204"),sQuery(id+"F1.wireOp",EDGE,"E205"),sQuery(id+"F1.wireOp",EDGE,"E206"),sQuery(id+"F1.wireOp",EDGE,"E207"),sQuery(id+"F1.wireOp",EDGE,"E208"),sQuery(id+"F1.wireOp",EDGE,"E209"),sQuery(id+"F1.wireOp",EDGE,"E210"),sQuery(id+"F1.wireOp",EDGE,"E211"),sQuery(id+"F1.wireOp",EDGE,"E212"),sQuery(id+"F1.wireOp",EDGE,"E213"),sQuery(id+"F1.wireOp",EDGE,"E214"),sQuery(id+"F1.wireOp",EDGE,"E215"),sQuery(id+"F1.wireOp",EDGE,"E216"),sQuery(id+"F1.wireOp",EDGE,"E217"),sQuery(id+"F1.wireOp",EDGE,"E218"),sQuery(id+"F1.wireOp",EDGE,"E219"),sQuery(id+"F1.wireOp",EDGE,"E220"),sQuery(id+"F1.wireOp",EDGE,"E221"),sQuery(id+"F1.wireOp",EDGE,"E222"),sQuery(id+"F1.wireOp",EDGE,"E223"),sQuery(id+"F1.wireOp",EDGE,"E224"),sQuery(id+"F1.wireOp",EDGE,"E225"),sQuery(id+"F1.wireOp",EDGE,"E226"),sQuery(id+"F1.wireOp",EDGE,"E227"),sQuery(id+"F1.wireOp",EDGE,"E228"),sQuery(id+"F1.wireOp",EDGE,"E229"),sQuery(id+"F1.wireOp",EDGE,"E230"),sQuery(id+"F1.wireOp",EDGE,"E231"),sQuery(id+"F1.wireOp",EDGE,"E232"),sQuery(id+"F1.wireOp",EDGE,"E233"),sQuery(id+"F1.wireOp",EDGE,"E234"),sQuery(id+"F1.wireOp",EDGE,"E235"),sQuery(id+"F1.wireOp",EDGE,"E236"),sQuery(id+"F1.wireOp",EDGE,"E237"),sQuery(id+"F1.wireOp",EDGE,"E238"),sQuery(id+"F1.wireOp",EDGE,"E239"),sQuery(id+"F1.wireOp",EDGE,"E240"),sQuery(id+"F1.wireOp",EDGE,"E241"),sQuery(id+"F1.wireOp",EDGE,"E242"),sQuery(id+"F1.wireOp",EDGE,"E243"),sQuery(id+"F1.wireOp",EDGE,"E244"),sQuery(id+"F1.wireOp",EDGE,"E245"),sQuery(id+"F1.wireOp",EDGE,"E246"),sQuery(id+"F1.wireOp",EDGE,"E247"),sQuery(id+"F1.wireOp",EDGE,"E248"),sQuery(id+"F1.wireOp",EDGE,"E249"),sQuery(id+"F1.wireOp",EDGE,"E250"),sQuery(id+"F1.wireOp",EDGE,"E251"),sQuery(id+"F1.wireOp",EDGE,"E252"),sQuery(id+"F1.wireOp",EDGE,"E253"),sQuery(id+"F1.wireOp",EDGE,"E254"),sQuery(id+"F1.wireOp",EDGE,"E255"),sQuery(id+"F1.wireOp",EDGE,"E256"),sQuery(id+"F1.wireOp",EDGE,"E257"),sQuery(id+"F1.wireOp",EDGE,"E258"),sQuery(id+"F1.wireOp",EDGE,"E259"),sQuery(id+"F1.wireOp",EDGE,"E260"),sQuery(id+"F1.wireOp",EDGE,"E261"),sQuery(id+"F1.wireOp",EDGE,"E262"),sQuery(id+"F1.wireOp",EDGE,"E263"),sQuery(id+"F1.wireOp",EDGE,"E264"),sQuery(id+"F1.wireOp",EDGE,"E265"),sQuery(id+"F1.wireOp",EDGE,"E266"),sQuery(id+"F1.wireOp",EDGE,"E267"),sQuery(id+"F1.wireOp",EDGE,"E268"),sQuery(id+"F1.wireOp",EDGE,"E269"),sQuery(id+"F1.wireOp",EDGE,"E270"),sQuery(id+"F1.wireOp",EDGE,"E271"),sQuery(id+"F1.wireOp",EDGE,"E272"),sQuery(id+"F1.wireOp",EDGE,"E273"),sQuery(id+"F1.wireOp",EDGE,"E274"),sQuery(id+"F1.wireOp",EDGE,"E275"),sQuery(id+"F1.wireOp",EDGE,"E276"),sQuery(id+"F1.wireOp",EDGE,"E277"),sQuery(id+"F1.wireOp",EDGE,"E278"),sQuery(id+"F1.wireOp",EDGE,"E279"),sQuery(id+"F1.wireOp",EDGE,"E280"),sQuery(id+"F1.wireOp",EDGE,"E281"),sQuery(id+"F1.wireOp",EDGE,"E282"),sQuery(id+"F1.wireOp",EDGE,"E283"),sQuery(id+"F1.wireOp",EDGE,"E284"),sQuery(id+"F1.wireOp",EDGE,"E285"),sQuery(id+"F1.wireOp",EDGE,"E286"),sQuery(id+"F1.wireOp",EDGE,"E287"),sQuery(id+"F1.wireOp",EDGE,"E288"),sQuery(id+"F1.wireOp",EDGE,"E289"),sQuery(id+"F1.wireOp",EDGE,"E290"),sQuery(id+"F1.wireOp",EDGE,"E291"),sQuery(id+"F1.wireOp",EDGE,"E292"),sQuery(id+"F1.wireOp",EDGE,"E293"),sQuery(id+"F1.wireOp",EDGE,"E294"),sQuery(id+"F1.wireOp",EDGE,"E295"),sQuery(id+"F1.wireOp",EDGE,"E296"),sQuery(id+"F1.wireOp",EDGE,"E297"),sQuery(id+"F1.wireOp",EDGE,"E298"),sQuery(id+"F1.wireOp",EDGE,"E299"),sQuery(id+"F1.wireOp",EDGE,"E300"),sQuery(id+"F1.wireOp",EDGE,"E301"),sQuery(id+"F1.wireOp",EDGE,"E302"),sQuery(id+"F1.wireOp",EDGE,"E303"),sQuery(id+"F1.wireOp",EDGE,"E304"),sQuery(id+"F1.wireOp",EDGE,"E305"),sQuery(id+"F1.wireOp",EDGE,"E306"),sQuery(id+"F1.wireOp",EDGE,"E307"),sQuery(id+"F1.wireOp",EDGE,"E308"),sQuery(id+"F1.wireOp",EDGE,"E309"),sQuery(id+"F1.wireOp",EDGE,"E310"),sQuery(id+"F1.wireOp",EDGE,"E311"),sQuery(id+"F1.wireOp",EDGE,"E312"),sQuery(id+"F1.wireOp",EDGE,"E313"),sQuery(id+"F1.wireOp",EDGE,"E314"),sQuery(id+"F1.wireOp",EDGE,"E315"),sQuery(id+"F1.wireOp",EDGE,"E316"),sQuery(id+"F1.wireOp",EDGE,"E317"),sQuery(id+"F1.wireOp",EDGE,"E318"),sQuery(id+"F1.wireOp",EDGE,"E319"),sQuery(id+"F1.wireOp",EDGE,"E320"),sQuery(id+"F1.wireOp",EDGE,"E321"),sQuery(id+"F1.wireOp",EDGE,"E322"),sQuery(id+"F1.wireOp",EDGE,"E323"),sQuery(id+"F1.wireOp",EDGE,"E324"),sQuery(id+"F1.wireOp",EDGE,"E325"),sQuery(id+"F1.wireOp",EDGE,"E326"),sQuery(id+"F1.wireOp",EDGE,"E327"),sQuery(id+"F1.wireOp",EDGE,"E328"),sQuery(id+"F1.wireOp",EDGE,"E329"),sQuery(id+"F1.wireOp",EDGE,"E330"),sQuery(id+"F1.wireOp",EDGE,"E331"),sQuery(id+"F1.wireOp",EDGE,"E332"),sQuery(id+"F1.wireOp",EDGE,"E333"),sQuery(id+"F1.wireOp",EDGE,"E334"),sQuery(id+"F1.wireOp",EDGE,"E334"),sQuery(id+"F1.wireOp",EDGE,"E335"),sQuery(id+"F1.wireOp",EDGE,"E336"),sQuery(id+"F1.wireOp",EDGE,"E337"),sQuery(id+"F1.wireOp",EDGE,"E338"),sQuery(id+"F1.wireOp",EDGE,"E339"),sQuery(id+"F1.wireOp",EDGE,"E340"),sQuery(id+"F1.wireOp",EDGE,"E341"),sQuery(id+"F1.wireOp",EDGE,"E342"),sQuery(id+"F1.wireOp",EDGE,"E343"),sQuery(id+"F1.wireOp",EDGE,"E344"),sQuery(id+"F1.wireOp",EDGE,"E345"),sQuery(id+"F1.wireOp",EDGE,"E346"),sQuery(id+"F1.wireOp",EDGE,"E347"),sQuery(id+"F1.wireOp",EDGE,"E348"),sQuery(id+"F1.wireOp",EDGE,"E349"),sQuery(id+"F1.wireOp",EDGE,"E350"),sQuery(id+"F1.wireOp",EDGE,"E351"),sQuery(id+"F1.wireOp",EDGE,"E352"),sQuery(id+"F1.wireOp",EDGE,"E353"),sQuery(id+"F1.wireOp",EDGE,"E354"),sQuery(id+"F1.wireOp",EDGE,"E355"),sQuery(id+"F1.wireOp",EDGE,"E356"),sQuery(id+"F1.wireOp",EDGE,"E357"),sQuery(id+"F1.wireOp",EDGE,"E358"),sQuery(id+"F1.wireOp",EDGE,"E359"),sQuery(id+"F1.wireOp",EDGE,"E360"),sQuery(id+"F1.wireOp",EDGE,"E361"),sQuery(id+"F1.wireOp",EDGE,"E362"),sQuery(id+"F1.wireOp",EDGE,"E363"),sQuery(id+"F1.wireOp",EDGE,"E364"),sQuery(id+"F1.wireOp",EDGE,"E365"),sQuery(id+"F1.wireOp",EDGE,"E366"),sQuery(id+"F1.wireOp",EDGE,"E367"),sQuery(id+"F1.wireOp",EDGE,"E368"),sQuery(id+"F1.wireOp",EDGE,"E369"),sQuery(id+"F1.wireOp",EDGE,"E370"),sQuery(id+"F1.wireOp",EDGE,"E371"),sQuery(id+"F1.wireOp",EDGE,"E372"),sQuery(id+"F1.wireOp",EDGE,"E373"),sQuery(id+"F1.wireOp",EDGE,"E374"),sQuery(id+"F1.wireOp",EDGE,"E375"),sQuery(id+"F1.wireOp",EDGE,"E376"),sQuery(id+"F1.wireOp",EDGE,"E377"),sQuery(id+"F1.wireOp",EDGE,"E378"),sQuery(id+"F1.wireOp",EDGE,"E379"),sQuery(id+"F1.wireOp",EDGE,"E380"),sQuery(id+"F1.wireOp",EDGE,"E381"),sQuery(id+"F1.wireOp",EDGE,"E382"),sQuery(id+"F1.wireOp",EDGE,"E383"),sQuery(id+"F1.wireOp",EDGE,"E384"),sQuery(id+"F1.wireOp",EDGE,"E385"),sQuery(id+"F1.wireOp",EDGE,"E386"),sQuery(id+"F1.wireOp",EDGE,"E387"),sQuery(id+"F1.wireOp",EDGE,"E388"),sQuery(id+"F1.wireOp",EDGE,"E389"),sQuery(id+"F1.wireOp",EDGE,"E390"),sQuery(id+"F1.wireOp",EDGE,"E391"),sQuery(id+"F1.wireOp",EDGE,"E392"),sQuery(id+"F1.wireOp",EDGE,"E393"),sQuery(id+"F1.wireOp",EDGE,"E394"),sQuery(id+"F1.wireOp",EDGE,"E395"),sQuery(id+"F1.wireOp",EDGE,"E396"),sQuery(id+"F1.wireOp",EDGE,"E397"),sQuery(id+"F1.wireOp",EDGE,"E398"),sQuery(id+"F1.wireOp",EDGE,"E399"),sQuery(id+"F1.wireOp",EDGE,"E400"),sQuery(id+"F1.wireOp",EDGE,"E401"),sQuery(id+"F1.wireOp",EDGE,"E402"),sQuery(id+"F1.wireOp",EDGE,"E403"),sQuery(id+"F1.wireOp",EDGE,"E404"),sQuery(id+"F1.wireOp",EDGE,"E405"),sQuery(id+"F1.wireOp",EDGE,"E406"),sQuery(id+"F1.wireOp",EDGE,"E407"),sQuery(id+"F1.wireOp",EDGE,"E408"),sQuery(id+"F1.wireOp",EDGE,"E409"),sQuery(id+"F1.wireOp",EDGE,"E410"),sQuery(id+"F1.wireOp",EDGE,"E411"),sQuery(id+"F1.wireOp",EDGE,"E412"),sQuery(id+"F1.wireOp",EDGE,"E413"),sQuery(id+"F1.wireOp",EDGE,"E414"),sQuery(id+"F1.wireOp",EDGE,"E415"),sQuery(id+"F1.wireOp",EDGE,"E416"),sQuery(id+"F1.wireOp",EDGE,"E417"),sQuery(id+"F1.wireOp",EDGE,"E418"),sQuery(id+"F1.wireOp",EDGE,"E419"),sQuery(id+"F1.wireOp",EDGE,"E420"),sQuery(id+"F1.wireOp",EDGE,"E421"),sQuery(id+"F1.wireOp",EDGE,"E422"),sQuery(id+"F1.wireOp",EDGE,"E423"),sQuery(id+"F1.wireOp",EDGE,"E424"),sQuery(id+"F1.wireOp",EDGE,"E425"),sQuery(id+"F1.wireOp",EDGE,"E426"),sQuery(id+"F1.wireOp",EDGE,"E426"),sQuery(id+"F1.wireOp",EDGE,"E427"),sQuery(id+"F1.wireOp",EDGE,"E428"),sQuery(id+"F1.wireOp",EDGE,"E429"),sQuery(id+"F1.wireOp",EDGE,"E430"),sQuery(id+"F1.wireOp",EDGE,"E431"),sQuery(id+"F1.wireOp",EDGE,"E432"),sQuery(id+"F1.wireOp",EDGE,"E433"),sQuery(id+"F1.wireOp",EDGE,"E434"),sQuery(id+"F1.wireOp",EDGE,"E435"),sQuery(id+"F1.wireOp",EDGE,"E435"),sQuery(id+"F1.wireOp",EDGE,"E436"),sQuery(id+"F1.wireOp",EDGE,"E437"),sQuery(id+"F1.wireOp",EDGE,"E438"),sQuery(id+"F1.wireOp",EDGE,"E439"),sQuery(id+"F1.wireOp",EDGE,"E440"),sQuery(id+"F1.wireOp",EDGE,"E441"),sQuery(id+"F1.wireOp",EDGE,"E442"),sQuery(id+"F1.wireOp",EDGE,"E443"),sQuery(id+"F1.wireOp",EDGE,"E444"),sQuery(id+"F1.wireOp",EDGE,"E445"),sQuery(id+"F1.wireOp",EDGE,"E446"),sQuery(id+"F1.wireOp",EDGE,"E447"),sQuery(id+"F1.wireOp",EDGE,"E448"),sQuery(id+"F1.wireOp",EDGE,"E449"),sQuery(id+"F1.wireOp",EDGE,"E450"),sQuery(id+"F1.wireOp",EDGE,"E451"),sQuery(id+"F1.wireOp",EDGE,"E452"),sQuery(id+"F1.wireOp",EDGE,"E453"),sQuery(id+"F1.wireOp",EDGE,"E454"),sQuery(id+"F1.wireOp",EDGE,"E455"),sQuery(id+"F1.wireOp",EDGE,"E456"),sQuery(id+"F1.wireOp",EDGE,"E457"),sQuery(id+"F1.wireOp",EDGE,"E458"),sQuery(id+"F1.wireOp",EDGE,"E459"),sQuery(id+"F1.wireOp",EDGE,"E460"),sQuery(id+"F1.wireOp",EDGE,"E461"),sQuery(id+"F1.wireOp",EDGE,"E462"),sQuery(id+"F1.wireOp",EDGE,"E463"),sQuery(id+"F1.wireOp",EDGE,"E464"),sQuery(id+"F1.wireOp",EDGE,"E465"),sQuery(id+"F1.wireOp",EDGE,"E466"),sQuery(id+"F1.wireOp",EDGE,"E467"),sQuery(id+"F1.wireOp",EDGE,"E468"),sQuery(id+"F1.wireOp",EDGE,"E469"),sQuery(id+"F1.wireOp",EDGE,"E470"),sQuery(id+"F1.wireOp",EDGE,"E471"),sQuery(id+"F1.wireOp",EDGE,"E472"),sQuery(id+"F1.wireOp",EDGE,"E473"),sQuery(id+"F1.wireOp",EDGE,"E474"),sQuery(id+"F1.wireOp",EDGE,"E475"),sQuery(id+"F1.wireOp",EDGE,"E476"),sQuery(id+"F1.wireOp",EDGE,"E477"),sQuery(id+"F1.wireOp",EDGE,"E478"),sQuery(id+"F1.wireOp",EDGE,"E479"),sQuery(id+"F1.wireOp",EDGE,"E480"),sQuery(id+"F1.wireOp",EDGE,"E481"),sQuery(id+"F1.wireOp",EDGE,"E482"),sQuery(id+"F1.wireOp",EDGE,"E483"),sQuery(id+"F1.wireOp",EDGE,"E484"),sQuery(id+"F1.wireOp",EDGE,"E485"),sQuery(id+"F1.wireOp",EDGE,"E486"),sQuery(id+"F1.wireOp",EDGE,"E487"),sQuery(id+"F1.wireOp",EDGE,"E488"),sQuery(id+"F1.wireOp",EDGE,"E489"),sQuery(id+"F1.wireOp",EDGE,"E490"),sQuery(id+"F1.wireOp",EDGE,"E491"),sQuery(id+"F1.wireOp",EDGE,"E492"),sQuery(id+"F1.wireOp",EDGE,"E493"),sQuery(id+"F1.wireOp",EDGE,"E494"),sQuery(id+"F1.wireOp",EDGE,"E495"),sQuery(id+"F1.wireOp",EDGE,"E496"),sQuery(id+"F1.wireOp",EDGE,"E497"),sQuery(id+"F1.wireOp",EDGE,"E498"),sQuery(id+"F1.wireOp",EDGE,"E499"),sQuery(id+"F1.wireOp",EDGE,"E500"),sQuery(id+"F1.wireOp",EDGE,"E501"),sQuery(id+"F1.wireOp",EDGE,"E502"),sQuery(id+"F1.wireOp",EDGE,"E503"),sQuery(id+"F1.wireOp",EDGE,"E504"),sQuery(id+"F1.wireOp",EDGE,"E505"),sQuery(id+"F1.wireOp",EDGE,"E506"),sQuery(id+"F1.wireOp",EDGE,"E507"),sQuery(id+"F1.wireOp",EDGE,"E508"),sQuery(id+"F1.wireOp",EDGE,"E509"),sQuery(id+"F1.wireOp",EDGE,"E510"),sQuery(id+"F1.wireOp",EDGE,"E511"),sQuery(id+"F1.wireOp",EDGE,"E512"),sQuery(id+"F1.wireOp",EDGE,"E513"),sQuery(id+"F1.wireOp",EDGE,"E514"),sQuery(id+"F1.wireOp",EDGE,"E515"),sQuery(id+"F1.wireOp",EDGE,"E516"),sQuery(id+"F1.wireOp",EDGE,"E517"),sQuery(id+"F1.wireOp",EDGE,"E518"),sQuery(id+"F1.wireOp",EDGE,"E519"),sQuery(id+"F1.wireOp",EDGE,"E520"),sQuery(id+"F1.wireOp",EDGE,"E521"),sQuery(id+"F1.wireOp",EDGE,"E522"),sQuery(id+"F1.wireOp",EDGE,"E523"),sQuery(id+"F1.wireOp",EDGE,"E524"),sQuery(id+"F1.wireOp",EDGE,"E525"),sQuery(id+"F1.wireOp",EDGE,"E526"),sQuery(id+"F1.wireOp",EDGE,"E527"),sQuery(id+"F1.wireOp",EDGE,"E528"),sQuery(id+"F1.wireOp",EDGE,"E529"),sQuery(id+"F1.wireOp",EDGE,"E530"),sQuery(id+"F1.wireOp",EDGE,"E531"),sQuery(id+"F1.wireOp",EDGE,"E532"),sQuery(id+"F1.wireOp",EDGE,"E533"),sQuery(id+"F1.wireOp",EDGE,"E534"),sQuery(id+"F1.wireOp",EDGE,"E534"),sQuery(id+"F1.wireOp",EDGE,"E535"),sQuery(id+"F1.wireOp",EDGE,"E536"),sQuery(id+"F1.wireOp",EDGE,"E537"),sQuery(id+"F1.wireOp",EDGE,"E538"),sQuery(id+"F1.wireOp",EDGE,"E539"),sQuery(id+"F1.wireOp",EDGE,"E540"),sQuery(id+"F1.wireOp",EDGE,"E541"),sQuery(id+"F1.wireOp",EDGE,"E542"),sQuery(id+"F1.wireOp",EDGE,"E543"),sQuery(id+"F1.wireOp",EDGE,"E544"),sQuery(id+"F1.wireOp",EDGE,"E545"),sQuery(id+"F1.wireOp",EDGE,"E546"),sQuery(id+"F1.wireOp",EDGE,"E547"),sQuery(id+"F1.wireOp",EDGE,"E548"),sQuery(id+"F1.wireOp",EDGE,"E549"),sQuery(id+"F1.wireOp",EDGE,"E550"),sQuery(id+"F1.wireOp",EDGE,"E551"),sQuery(id+"F1.wireOp",EDGE,"E552"),sQuery(id+"F1.wireOp",EDGE,"E553"),sQuery(id+"F1.wireOp",EDGE,"E554"),sQuery(id+"F1.wireOp",EDGE,"E555"),sQuery(id+"F1.wireOp",EDGE,"E556"),sQuery(id+"F1.wireOp",EDGE,"E557"),sQuery(id+"F1.wireOp",EDGE,"E558"),sQuery(id+"F1.wireOp",EDGE,"E559"),sQuery(id+"F1.wireOp",EDGE,"E560"),sQuery(id+"F1.wireOp",EDGE,"E561"),sQuery(id+"F1.wireOp",EDGE,"E562"),sQuery(id+"F1.wireOp",EDGE,"E563"),sQuery(id+"F1.wireOp",EDGE,"E564"),sQuery(id+"F1.wireOp",EDGE,"E565"),sQuery(id+"F1.wireOp",EDGE,"E566"),sQuery(id+"F1.wireOp",EDGE,"E567"),sQuery(id+"F1.wireOp",EDGE,"E568"),sQuery(id+"F1.wireOp",EDGE,"E569"),sQuery(id+"F1.wireOp",EDGE,"E570"),sQuery(id+"F1.wireOp",EDGE,"E571"),sQuery(id+"F1.wireOp",EDGE,"E572"),sQuery(id+"F1.wireOp",EDGE,"E573"),sQuery(id+"F1.wireOp",EDGE,"E574"),sQuery(id+"F1.wireOp",EDGE,"E575"),sQuery(id+"F1.wireOp",EDGE,"E576"),sQuery(id+"F1.wireOp",EDGE,"E577"),sQuery(id+"F1.wireOp",EDGE,"E578"),sQuery(id+"F1.wireOp",EDGE,"E579"),sQuery(id+"F1.wireOp",EDGE,"E580"),sQuery(id+"F1.wireOp",EDGE,"E581"),sQuery(id+"F1.wireOp",EDGE,"E582"),sQuery(id+"F1.wireOp",EDGE,"E583"),sQuery(id+"F1.wireOp",EDGE,"E584"),sQuery(id+"F1.wireOp",EDGE,"E585"),sQuery(id+"F1.wireOp",EDGE,"E586"),sQuery(id+"F1.wireOp",EDGE,"E587"),sQuery(id+"F1.wireOp",EDGE,"E588"),sQuery(id+"F1.wireOp",EDGE,"E589"),sQuery(id+"F1.wireOp",EDGE,"E590"),sQuery(id+"F1.wireOp",EDGE,"E591"),sQuery(id+"F1.wireOp",EDGE,"E592"),sQuery(id+"F1.wireOp",EDGE,"E593"),sQuery(id+"F1.wireOp",EDGE,"E594"),sQuery(id+"F1.wireOp",EDGE,"E595"),sQuery(id+"F1.wireOp",EDGE,"E596"),sQuery(id+"F1.wireOp",EDGE,"E597"),sQuery(id+"F1.wireOp",EDGE,"E598"),sQuery(id+"F1.wireOp",EDGE,"E599"),sQuery(id+"F1.wireOp",EDGE,"E600"),sQuery(id+"F1.wireOp",EDGE,"E601"),sQuery(id+"F1.wireOp",EDGE,"E602"),sQuery(id+"F1.wireOp",EDGE,"E603"),sQuery(id+"F1.wireOp",EDGE,"E604"),sQuery(id+"F1.wireOp",EDGE,"E605"),sQuery(id+"F1.wireOp",EDGE,"E606"),sQuery(id+"F1.wireOp",EDGE,"E607"),sQuery(id+"F1.wireOp",EDGE,"E608"),sQuery(id+"F1.wireOp",EDGE,"E609"),sQuery(id+"F1.wireOp",EDGE,"E610"),sQuery(id+"F1.wireOp",EDGE,"E611"),sQuery(id+"F1.wireOp",EDGE,"E612"),sQuery(id+"F1.wireOp",EDGE,"E613"),sQuery(id+"F1.wireOp",EDGE,"E614"),sQuery(id+"F1.wireOp",EDGE,"E615"),sQuery(id+"F1.wireOp",EDGE,"E616"),sQuery(id+"F1.wireOp",EDGE,"E617"),sQuery(id+"F1.wireOp",EDGE,"E618"),sQuery(id+"F1.wireOp",EDGE,"E619"),sQuery(id+"F1.wireOp",EDGE,"E620"),sQuery(id+"F1.wireOp",EDGE,"E621"),sQuery(id+"F1.wireOp",EDGE,"E622"),sQuery(id+"F1.wireOp",EDGE,"E623"),sQuery(id+"F1.wireOp",EDGE,"E624"),sQuery(id+"F1.wireOp",EDGE,"E625"),sQuery(id+"F1.wireOp",EDGE,"E626"),sQuery(id+"F1.wireOp",EDGE,"E627"),sQuery(id+"F1.wireOp",EDGE,"E628"),sQuery(id+"F1.wireOp",EDGE,"E629"),sQuery(id+"F1.wireOp",EDGE,"E630"),sQuery(id+"F1.wireOp",EDGE,"E631"),sQuery(id+"F1.wireOp",EDGE,"E632"),sQuery(id+"F1.wireOp",EDGE,"E633"),sQuery(id+"F1.wireOp",EDGE,"E634"),sQuery(id+"F1.wireOp",EDGE,"E635"),sQuery(id+"F1.wireOp",EDGE,"E636"),sQuery(id+"F1.wireOp",EDGE,"E637"),sQuery(id+"F1.wireOp",EDGE,"E638"),sQuery(id+"F1.wireOp",EDGE,"E639"),sQuery(id+"F1.wireOp",EDGE,"E640"),sQuery(id+"F1.wireOp",EDGE,"E641"),sQuery(id+"F1.wireOp",EDGE,"E642"),sQuery(id+"F1.wireOp",EDGE,"E643"),sQuery(id+"F1.wireOp",EDGE,"E644"),sQuery(id+"F1.wireOp",EDGE,"E645"),sQuery(id+"F1.wireOp",EDGE,"E646"),sQuery(id+"F1.wireOp",EDGE,"E647"),sQuery(id+"F1.wireOp",EDGE,"E648"),sQuery(id+"F1.wireOp",EDGE,"E649"),sQuery(id+"F1.wireOp",EDGE,"E650"),sQuery(id+"F1.wireOp",EDGE,"E651"),sQuery(id+"F1.wireOp",EDGE,"E652"),sQuery(id+"F1.wireOp",EDGE,"E653"),sQuery(id+"F1.wireOp",EDGE,"E654"),sQuery(id+"F1.wireOp",EDGE,"E655"),sQuery(id+"F1.wireOp",EDGE,"E656"),sQuery(id+"F1.wireOp",EDGE,"E657"),sQuery(id+"F1.wireOp",EDGE,"E658"),sQuery(id+"F1.wireOp",EDGE,"E659"),sQuery(id+"F1.wireOp",EDGE,"E660"),sQuery(id+"F1.wireOp",EDGE,"E661"),sQuery(id+"F1.wireOp",EDGE,"E662"),sQuery(id+"F1.wireOp",EDGE,"E663"),sQuery(id+"F1.wireOp",EDGE,"E664"),sQuery(id+"F1.wireOp",EDGE,"E665"),sQuery(id+"F1.wireOp",EDGE,"E666"),sQuery(id+"F1.wireOp",EDGE,"E667"),sQuery(id+"F1.wireOp",EDGE,"E668"),sQuery(id+"F1.wireOp",EDGE,"E669"),sQuery(id+"F1.wireOp",EDGE,"E670"),sQuery(id+"F1.wireOp",EDGE,"E671"),sQuery(id+"F1.wireOp",EDGE,"E672"),sQuery(id+"F1.wireOp",EDGE,"E673"),sQuery(id+"F1.wireOp",EDGE,"E674"),sQuery(id+"F1.wireOp",EDGE,"E675"),sQuery(id+"F1.wireOp",EDGE,"E676"),sQuery(id+"F1.wireOp",EDGE,"E677"),sQuery(id+"F1.wireOp",EDGE,"E678"),sQuery(id+"F1.wireOp",EDGE,"E679"),sQuery(id+"F1.wireOp",EDGE,"E680"),sQuery(id+"F1.wireOp",EDGE,"E681"),sQuery(id+"F1.wireOp",EDGE,"E682"),sQuery(id+"F1.wireOp",EDGE,"E683"),sQuery(id+"F1.wireOp",EDGE,"E684"),sQuery(id+"F1.wireOp",EDGE,"E685"),sQuery(id+"F1.wireOp",EDGE,"E686"),sQuery(id+"F1.wireOp",EDGE,"E687"),sQuery(id+"F1.wireOp",EDGE,"E688"),sQuery(id+"F1.wireOp",EDGE,"E689"),sQuery(id+"F1.wireOp",EDGE,"E690"),sQuery(id+"F1.wireOp",EDGE,"E691"),sQuery(id+"F1.wireOp",EDGE,"E692"),sQuery(id+"F1.wireOp",EDGE,"E693"),sQuery(id+"F1.wireOp",EDGE,"E694"),sQuery(id+"F1.wireOp",EDGE,"E695"),sQuery(id+"F1.wireOp",EDGE,"E696"),sQuery(id+"F1.wireOp",EDGE,"E697"),sQuery(id+"F1.wireOp",EDGE,"E698"),sQuery(id+"F1.wireOp",EDGE,"E699"),sQuery(id+"F1.wireOp",EDGE,"E700"),sQuery(id+"F1.wireOp",EDGE,"E701"),sQuery(id+"F1.wireOp",EDGE,"E702"),sQuery(id+"F1.wireOp",EDGE,"E703"),sQuery(id+"F1.wireOp",EDGE,"E704"),sQuery(id+"F1.wireOp",EDGE,"E705"),sQuery(id+"F1.wireOp",EDGE,"E706"),sQuery(id+"F1.wireOp",EDGE,"E707"),sQuery(id+"F1.wireOp",EDGE,"E708"),sQuery(id+"F1.wireOp",EDGE,"E709"),sQuery(id+"F1.wireOp",EDGE,"E710"),sQuery(id+"F1.wireOp",EDGE,"E711"),sQuery(id+"F1.wireOp",EDGE,"E712"),sQuery(id+"F1.wireOp",EDGE,"E713"),sQuery(id+"F1.wireOp",EDGE,"E714"),sQuery(id+"F1.wireOp",EDGE,"E715"),sQuery(id+"F1.wireOp",EDGE,"E716"),sQuery(id+"F1.wireOp",EDGE,"E717"),sQuery(id+"F1.wireOp",EDGE,"E718"),sQuery(id+"F1.wireOp",EDGE,"E719"),sQuery(id+"F1.wireOp",EDGE,"E720"),sQuery(id+"F1.wireOp",EDGE,"E721"),sQuery(id+"F1.wireOp",EDGE,"E722"),sQuery(id+"F1.wireOp",EDGE,"E723"),sQuery(id+"F1.wireOp",EDGE,"E724"),sQuery(id+"F1.wireOp",EDGE,"E725"),sQuery(id+"F1.wireOp",EDGE,"E726"),sQuery(id+"F1.wireOp",EDGE,"E727"),sQuery(id+"F1.wireOp",EDGE,"E728"),sQuery(id+"F1.wireOp",EDGE,"E729"),sQuery(id+"F1.wireOp",EDGE,"E730"),sQuery(id+"F1.wireOp",EDGE,"E731"),sQuery(id+"F1.wireOp",EDGE,"E732"),sQuery(id+"F1.wireOp",EDGE,"E733"),sQuery(id+"F1.wireOp",EDGE,"E734"),sQuery(id+"F1.wireOp",EDGE,"E735"),sQuery(id+"F1.wireOp",EDGE,"E736"),sQuery(id+"F1.wireOp",EDGE,"E737"),sQuery(id+"F1.wireOp",EDGE,"E738"),sQuery(id+"F1.wireOp",EDGE,"E739"),sQuery(id+"F1.wireOp",EDGE,"E740"),sQuery(id+"F1.wireOp",EDGE,"E741"),sQuery(id+"F1.wireOp",EDGE,"E742"),sQuery(id+"F1.wireOp",EDGE,"E743"),sQuery(id+"F1.wireOp",EDGE,"E744"),sQuery(id+"F1.wireOp",EDGE,"E745"),sQuery(id+"F1.wireOp",EDGE,"E746"),sQuery(id+"F1.wireOp",EDGE,"E747"),sQuery(id+"F1.wireOp",EDGE,"E748"),sQuery(id+"F1.wireOp",EDGE,"E749"),sQuery(id+"F1.wireOp",EDGE,"E750"),sQuery(id+"F1.wireOp",EDGE,"E751"),sQuery(id+"F1.wireOp",EDGE,"E752"),sQuery(id+"F1.wireOp",EDGE,"E753"),sQuery(id+"F1.wireOp",EDGE,"E754"),sQuery(id+"F1.wireOp",EDGE,"E755"),sQuery(id+"F1.wireOp",EDGE,"E756"),sQuery(id+"F1.wireOp",EDGE,"E757"),sQuery(id+"F1.wireOp",EDGE,"E758"),sQuery(id+"F1.wireOp",EDGE,"E759"),sQuery(id+"F1.wireOp",EDGE,"E760"),sQuery(id+"F1.wireOp",EDGE,"E761"),sQuery(id+"F1.wireOp",EDGE,"E762"),sQuery(id+"F1.wireOp",EDGE,"E763"),sQuery(id+"F1.wireOp",EDGE,"E764"),sQuery(id+"F1.wireOp",EDGE,"E765"),sQuery(id+"F1.wireOp",EDGE,"E766"),sQuery(id+"F1.wireOp",EDGE,"E767"),sQuery(id+"F1.wireOp",EDGE,"E768"),sQuery(id+"F1.wireOp",EDGE,"E769"),sQuery(id+"F1.wireOp",EDGE,"E770"),sQuery(id+"F1.wireOp",EDGE,"E771"),sQuery(id+"F1.wireOp",EDGE,"E772"),sQuery(id+"F1.wireOp",EDGE,"E773"),sQuery(id+"F1.wireOp",EDGE,"E774"),sQuery(id+"F1.wireOp",EDGE,"E775"),sQuery(id+"F1.wireOp",EDGE,"E776"),sQuery(id+"F1.wireOp",EDGE,"E777"),sQuery(id+"F1.wireOp",EDGE,"E778"),sQuery(id+"F1.wireOp",EDGE,"E779"),sQuery(id+"F1.wireOp",EDGE,"E780"),sQuery(id+"F1.wireOp",EDGE,"E781"),sQuery(id+"F1.wireOp",EDGE,"E782"),sQuery(id+"F1.wireOp",EDGE,"E783"),sQuery(id+"F1.wireOp",EDGE,"E784"),sQuery(id+"F1.wireOp",EDGE,"E785"),sQuery(id+"F1.wireOp",EDGE,"E786"),sQuery(id+"F1.wireOp",EDGE,"E787"),sQuery(id+"F1.wireOp",EDGE,"E788"),sQuery(id+"F1.wireOp",EDGE,"E789"),sQuery(id+"F1.wireOp",EDGE,"E790"),sQuery(id+"F1.wireOp",EDGE,"E791"),sQuery(id+"F1.wireOp",EDGE,"E792"),sQuery(id+"F1.wireOp",EDGE,"E793"),sQuery(id+"F1.wireOp",EDGE,"E794"),sQuery(id+"F1.wireOp",EDGE,"E795"),sQuery(id+"F1.wireOp",EDGE,"E796"),sQuery(id+"F1.wireOp",EDGE,"E797"),sQuery(id+"F1.wireOp",EDGE,"E798"),sQuery(id+"F1.wireOp",EDGE,"E799"),sQuery(id+"F1.wireOp",EDGE,"E800"),sQuery(id+"F1.wireOp",EDGE,"E801"),sQuery(id+"F1.wireOp",EDGE,"E802"),sQuery(id+"F1.wireOp",EDGE,"E803"),sQuery(id+"F1.wireOp",EDGE,"E804"),sQuery(id+"F1.wireOp",EDGE,"E805"),sQuery(id+"F1.wireOp",EDGE,"E806"),sQuery(id+"F1.wireOp",EDGE,"E807"),sQuery(id+"F1.wireOp",EDGE,"E808"),sQuery(id+"F1.wireOp",EDGE,"E809"),sQuery(id+"F1.wireOp",EDGE,"E810"),sQuery(id+"F1.wireOp",EDGE,"E811"),sQuery(id+"F1.wireOp",EDGE,"E812"),sQuery(id+"F1.wireOp",EDGE,"E813"),sQuery(id+"F1.wireOp",EDGE,"E814"),sQuery(id+"F1.wireOp",EDGE,"E815"),sQuery(id+"F1.wireOp",EDGE,"E816"),sQuery(id+"F1.wireOp",EDGE,"E817"),sQuery(id+"F1.wireOp",EDGE,"E818"),sQuery(id+"F1.wireOp",EDGE,"E819"),sQuery(id+"F1.wireOp",EDGE,"E820"),sQuery(id+"F1.wireOp",EDGE,"E821"),sQuery(id+"F1.wireOp",EDGE,"E822"),sQuery(id+"F1.wireOp",EDGE,"E823"),sQuery(id+"F1.wireOp",EDGE,"E824"),sQuery(id+"F1.wireOp",EDGE,"E825"),sQuery(id+"F1.wireOp",EDGE,"E826"),sQuery(id+"F1.wireOp",EDGE,"E827"),sQuery(id+"F1.wireOp",EDGE,"E828"),sQuery(id+"F1.wireOp",EDGE,"E829"),sQuery(id+"F1.wireOp",EDGE,"E830"),sQuery(id+"F1.wireOp",EDGE,"E831"),sQuery(id+"F1.wireOp",EDGE,"E832"),sQuery(id+"F1.wireOp",EDGE,"E833"),sQuery(id+"F1.wireOp",EDGE,"E834"),sQuery(id+"F1.wireOp",EDGE,"E835"),sQuery(id+"F1.wireOp",EDGE,"E836"),sQuery(id+"F1.wireOp",EDGE,"E837"),sQuery(id+"F1.wireOp",EDGE,"E838"),sQuery(id+"F1.wireOp",EDGE,"E839"),sQuery(id+"F1.wireOp",EDGE,"E840"),sQuery(id+"F1.wireOp",EDGE,"E841"),sQuery(id+"F1.wireOp",EDGE,"E842"),sQuery(id+"F1.wireOp",EDGE,"E843"),sQuery(id+"F1.wireOp",EDGE,"E844"),sQuery(id+"F1.wireOp",EDGE,"E845"),sQuery(id+"F1.wireOp",EDGE,"E846"),sQuery(id+"F1.wireOp",EDGE,"E847"),sQuery(id+"F1.wireOp",EDGE,"E848"),sQuery(id+"F1.wireOp",EDGE,"E849"),sQuery(id+"F1.wireOp",EDGE,"E850"),sQuery(id+"F1.wireOp",EDGE,"E851"),sQuery(id+"F1.wireOp",EDGE,"E852"),sQuery(id+"F1.wireOp",EDGE,"E853"),sQuery(id+"F1.wireOp",EDGE,"E854"),sQuery(id+"F1.wireOp",EDGE,"E855"),sQuery(id+"F1.wireOp",EDGE,"E856"),sQuery(id+"F1.wireOp",EDGE,"E857"),sQuery(id+"F1.wireOp",EDGE,"E858"),sQuery(id+"F1.wireOp",EDGE,"E859"),sQuery(id+"F1.wireOp",EDGE,"E860"),sQuery(id+"F1.wireOp",EDGE,"E861"),sQuery(id+"F1.wireOp",EDGE,"E862"),sQuery(id+"F1.wireOp",EDGE,"E863"),sQuery(id+"F1.wireOp",EDGE,"E864"),sQuery(id+"F1.wireOp",EDGE,"E865"),sQuery(id+"F1.wireOp",EDGE,"E866"),sQuery(id+"F1.wireOp",EDGE,"E867"),sQuery(id+"F1.wireOp",EDGE,"E868"),sQuery(id+"F1.wireOp",EDGE,"E869"),sQuery(id+"F1.wireOp",EDGE,"E870"),sQuery(id+"F1.wireOp",EDGE,"E871"),sQuery(id+"F1.wireOp",EDGE,"E872"),sQuery(id+"F1.wireOp",EDGE,"E873"),sQuery(id+"F1.wireOp",EDGE,"E873"),sQuery(id+"F1.wireOp",EDGE,"E874"),sQuery(id+"F1.wireOp",EDGE,"E875"),sQuery(id+"F1.wireOp",EDGE,"E876"),sQuery(id+"F1.wireOp",EDGE,"E877"),sQuery(id+"F1.wireOp",EDGE,"E878"),sQuery(id+"F1.wireOp",EDGE,"E879"),sQuery(id+"F1.wireOp",EDGE,"E880"),sQuery(id+"F1.wireOp",EDGE,"E881"),sQuery(id+"F1.wireOp",EDGE,"E882"),sQuery(id+"F1.wireOp",EDGE,"E883"),sQuery(id+"F1.wireOp",EDGE,"E884"),sQuery(id+"F1.wireOp",EDGE,"E885"),sQuery(id+"F1.wireOp",EDGE,"E886"),sQuery(id+"F1.wireOp",EDGE,"E887"),sQuery(id+"F1.wireOp",EDGE,"E888"),sQuery(id+"F1.wireOp",EDGE,"E889"),sQuery(id+"F1.wireOp",EDGE,"E890"),sQuery(id+"F1.wireOp",EDGE,"E891"),sQuery(id+"F1.wireOp",EDGE,"E892"),sQuery(id+"F1.wireOp",EDGE,"E893"),sQuery(id+"F1.wireOp",EDGE,"E894"),sQuery(id+"F1.wireOp",EDGE,"E895"),sQuery(id+"F1.wireOp",EDGE,"E896"),sQuery(id+"F1.wireOp",EDGE,"E897"),sQuery(id+"F1.wireOp",EDGE,"E898"),sQuery(id+"F1.wireOp",EDGE,"E899"),sQuery(id+"F1.wireOp",EDGE,"E900"),sQuery(id+"F1.wireOp",EDGE,"E901"),sQuery(id+"F1.wireOp",EDGE,"E902"),sQuery(id+"F1.wireOp",EDGE,"E903"),sQuery(id+"F1.wireOp",EDGE,"E904"),sQuery(id+"F1.wireOp",EDGE,"E905"),sQuery(id+"F1.wireOp",EDGE,"E906"),sQuery(id+"F1.wireOp",EDGE,"E907"),sQuery(id+"F1.wireOp",EDGE,"E908"),sQuery(id+"F1.wireOp",EDGE,"E909"),sQuery(id+"F1.wireOp",EDGE,"E910"),sQuery(id+"F1.wireOp",EDGE,"E911"),sQuery(id+"F1.wireOp",EDGE,"E912"),sQuery(id+"F1.wireOp",EDGE,"E913"),sQuery(id+"F1.wireOp",EDGE,"E914"),sQuery(id+"F1.wireOp",EDGE,"E915"),sQuery(id+"F1.wireOp",EDGE,"E916"),sQuery(id+"F1.wireOp",EDGE,"E917"),sQuery(id+"F1.wireOp",EDGE,"E918"),sQuery(id+"F1.wireOp",EDGE,"E919"),sQuery(id+"F1.wireOp",EDGE,"E920"),sQuery(id+"F1.wireOp",EDGE,"E921"),sQuery(id+"F1.wireOp",EDGE,"E922"),sQuery(id+"F1.wireOp",EDGE,"E923"),sQuery(id+"F1.wireOp",EDGE,"E924"),sQuery(id+"F1.wireOp",EDGE,"E925"),sQuery(id+"F1.wireOp",EDGE,"E926"),sQuery(id+"F1.wireOp",EDGE,"E927"),sQuery(id+"F1.wireOp",EDGE,"E928"),sQuery(id+"F1.wireOp",EDGE,"E929"),sQuery(id+"F1.wireOp",EDGE,"E930"),sQuery(id+"F1.wireOp",EDGE,"E931"),sQuery(id+"F1.wireOp",EDGE,"E932"),sQuery(id+"F1.wireOp",EDGE,"E933"),sQuery(id+"F1.wireOp",EDGE,"E934"),sQuery(id+"F1.wireOp",EDGE,"E935"),sQuery(id+"F1.wireOp",EDGE,"E936"),sQuery(id+"F1.wireOp",EDGE,"E937"),sQuery(id+"F1.wireOp",EDGE,"E938"),sQuery(id+"F1.wireOp",EDGE,"E939"),sQuery(id+"F1.wireOp",EDGE,"E940"),sQuery(id+"F1.wireOp",EDGE,"E941"),sQuery(id+"F1.wireOp",EDGE,"E942"),sQuery(id+"F1.wireOp",EDGE,"E943"),sQuery(id+"F1.wireOp",EDGE,"E944"),sQuery(id+"F1.wireOp",EDGE,"E945"),sQuery(id+"F1.wireOp",EDGE,"E946"),sQuery(id+"F1.wireOp",EDGE,"E947"),sQuery(id+"F1.wireOp",EDGE,"E948"),sQuery(id+"F1.wireOp",EDGE,"E949"),sQuery(id+"F1.wireOp",EDGE,"E950"),sQuery(id+"F1.wireOp",EDGE,"E951"),sQuery(id+"F1.wireOp",EDGE,"E952"),sQuery(id+"F1.wireOp",EDGE,"E953"),sQuery(id+"F1.wireOp",EDGE,"E954"),sQuery(id+"F1.wireOp",EDGE,"E955"),sQuery(id+"F1.wireOp",EDGE,"E956"),sQuery(id+"F1.wireOp",EDGE,"E957"),sQuery(id+"F1.wireOp",EDGE,"E958"),sQuery(id+"F1.wireOp",EDGE,"E959"),sQuery(id+"F1.wireOp",EDGE,"E960"),sQuery(id+"F1.wireOp",EDGE,"E961"),sQuery(id+"F1.wireOp",EDGE,"E962"),sQuery(id+"F1.wireOp",EDGE,"E963"),sQuery(id+"F1.wireOp",EDGE,"E964"),sQuery(id+"F1.wireOp",EDGE,"E965"),sQuery(id+"F1.wireOp",EDGE,"E966"),sQuery(id+"F1.wireOp",EDGE,"E967"),sQuery(id+"F1.wireOp",EDGE,"E968"),sQuery(id+"F1.wireOp",EDGE,"E969"),sQuery(id+"F1.wireOp",EDGE,"E970"),sQuery(id+"F1.wireOp",EDGE,"E971"),sQuery(id+"F1.wireOp",EDGE,"E972"),sQuery(id+"F1.wireOp",EDGE,"E973"),sQuery(id+"F1.wireOp",EDGE,"E974"),sQuery(id+"F1.wireOp",EDGE,"E975"),sQuery(id+"F1.wireOp",EDGE,"E976"),sQuery(id+"F1.wireOp",EDGE,"E976"),sQuery(id+"F1.wireOp",EDGE,"E976"),sQuery(id+"F1.wireOp",EDGE,"E977"),sQuery(id+"F1.wireOp",EDGE,"E978"),sQuery(id+"F1.wireOp",EDGE,"E979"),sQuery(id+"F1.wireOp",EDGE,"E980"),sQuery(id+"F1.wireOp",EDGE,"E981"),sQuery(id+"F1.wireOp",EDGE,"E982"),sQuery(id+"F1.wireOp",EDGE,"E983"),sQuery(id+"F1.wireOp",EDGE,"E984"),sQuery(id+"F1.wireOp",EDGE,"E985"),sQuery(id+"F1.wireOp",EDGE,"E986"),sQuery(id+"F1.wireOp",EDGE,"E987"),sQuery(id+"F1.wireOp",EDGE,"E988"),sQuery(id+"F1.wireOp",EDGE,"E989"),sQuery(id+"F1.wireOp",EDGE,"E990"),sQuery(id+"F1.wireOp",EDGE,"E991"),sQuery(id+"F1.wireOp",EDGE,"E992"),sQuery(id+"F1.wireOp",EDGE,"E993"),sQuery(id+"F1.wireOp",EDGE,"E994"),sQuery(id+"F1.wireOp",EDGE,"E995"),sQuery(id+"F1.wireOp",EDGE,"E996"),sQuery(id+"F1.wireOp",EDGE,"E997"),sQuery(id+"F1.wireOp",EDGE,"E998"),sQuery(id+"F1.wireOp",EDGE,"E999"),sQuery(id+"F1.wireOp",EDGE,"E1000"),sQuery(id+"F1.wireOp",EDGE,"E1001"),sQuery(id+"F1.wireOp",EDGE,"E1002"),sQuery(id+"F1.wireOp",EDGE,"E1003"),sQuery(id+"F1.wireOp",EDGE,"E1004"),sQuery(id+"F1.wireOp",EDGE,"E1005"),sQuery(id+"F1.wireOp",EDGE,"E1006"),sQuery(id+"F1.wireOp",EDGE,"E1007"),sQuery(id+"F1.wireOp",EDGE,"E1008"),sQuery(id+"F1.wireOp",EDGE,"E1009"),sQuery(id+"F1.wireOp",EDGE,"E1010"),sQuery(id+"F1.wireOp",EDGE,"E1011"),sQuery(id+"F1.wireOp",EDGE,"E1012"),sQuery(id+"F1.wireOp",EDGE,"E1013"),sQuery(id+"F1.wireOp",EDGE,"E1014"),sQuery(id+"F1.wireOp",EDGE,"E1015"),sQuery(id+"F1.wireOp",EDGE,"E1016"),sQuery(id+"F1.wireOp",EDGE,"E1017"),sQuery(id+"F1.wireOp",EDGE,"E1018"),sQuery(id+"F1.wireOp",EDGE,"E1019"),sQuery(id+"F1.wireOp",EDGE,"E1020"),sQuery(id+"F1.wireOp",EDGE,"E1021"),sQuery(id+"F1.wireOp",EDGE,"E1022"),sQuery(id+"F1.wireOp",EDGE,"E1023"),sQuery(id+"F1.wireOp",EDGE,"E1024"),sQuery(id+"F1.wireOp",EDGE,"E1025"),sQuery(id+"F1.wireOp",EDGE,"E1026"),sQuery(id+"F1.wireOp",EDGE,"E1027"),sQuery(id+"F1.wireOp",EDGE,"E1028"),sQuery(id+"F1.wireOp",EDGE,"E1029"),sQuery(id+"F1.wireOp",EDGE,"E1030"),sQuery(id+"F1.wireOp",EDGE,"E1031"),sQuery(id+"F1.wireOp",EDGE,"E1032"),sQuery(id+"F1.wireOp",EDGE,"E1033"),sQuery(id+"F1.wireOp",EDGE,"E1034"),sQuery(id+"F1.wireOp",EDGE,"E1035"),sQuery(id+"F1.wireOp",EDGE,"E1036"),sQuery(id+"F1.wireOp",EDGE,"E1037"),sQuery(id+"F1.wireOp",EDGE,"E1038"),sQuery(id+"F1.wireOp",EDGE,"E1039"),sQuery(id+"F1.wireOp",EDGE,"E1040"),sQuery(id+"F1.wireOp",EDGE,"E1041"),sQuery(id+"F1.wireOp",EDGE,"E1042"),sQuery(id+"F1.wireOp",EDGE,"E1043"),sQuery(id+"F1.wireOp",EDGE,"E1044"),sQuery(id+"F1.wireOp",EDGE,"E1045"),sQuery(id+"F1.wireOp",EDGE,"E1046"),sQuery(id+"F1.wireOp",EDGE,"E1047"),sQuery(id+"F1.wireOp",EDGE,"E1048"),sQuery(id+"F1.wireOp",EDGE,"E1049"),sQuery(id+"F1.wireOp",EDGE,"E1050"),sQuery(id+"F1.wireOp",EDGE,"E1051"),sQuery(id+"F1.wireOp",EDGE,"E1052"),sQuery(id+"F1.wireOp",EDGE,"E1053"),sQuery(id+"F1.wireOp",EDGE,"E1054"),sQuery(id+"F1.wireOp",EDGE,"E1055"),sQuery(id+"F1.wireOp",EDGE,"E1056"),sQuery(id+"F1.wireOp",EDGE,"E1057"),sQuery(id+"F1.wireOp",EDGE,"E1058"),sQuery(id+"F1.wireOp",EDGE,"E1059"),sQuery(id+"F1.wireOp",EDGE,"E1060"),sQuery(id+"F1.wireOp",EDGE,"E1061"),sQuery(id+"F1.wireOp",EDGE,"E1062"),sQuery(id+"F1.wireOp",EDGE,"E1063"),sQuery(id+"F1.wireOp",EDGE,"E1064"),sQuery(id+"F1.wireOp",EDGE,"E1065"),sQuery(id+"F1.wireOp",EDGE,"E1066"),sQuery(id+"F1.wireOp",EDGE,"E1067"),sQuery(id+"F1.wireOp",EDGE,"E1068"),sQuery(id+"F1.wireOp",EDGE,"E1069"),sQuery(id+"F1.wireOp",EDGE,"E1070"),sQuery(id+"F1.wireOp",EDGE,"E1071"),sQuery(id+"F1.wireOp",EDGE,"E1071"),sQuery(id+"F1.wireOp",EDGE,"E1072"),sQuery(id+"F1.wireOp",EDGE,"E1073"),sQuery(id+"F1.wireOp",EDGE,"E1074"),sQuery(id+"F1.wireOp",EDGE,"E1075"),sQuery(id+"F1.wireOp",EDGE,"E1076"),sQuery(id+"F1.wireOp",EDGE,"E1077"),sQuery(id+"F1.wireOp",EDGE,"E1078"),sQuery(id+"F1.wireOp",EDGE,"E1079"),sQuery(id+"F1.wireOp",EDGE,"E1080"),sQuery(id+"F1.wireOp",EDGE,"E1080"),sQuery(id+"F1.wireOp",EDGE,"E1081"),sQuery(id+"F1.wireOp",EDGE,"E1082"),sQuery(id+"F1.wireOp",EDGE,"E1083"),sQuery(id+"F1.wireOp",EDGE,"E1084"),sQuery(id+"F1.wireOp",EDGE,"E1085"),sQuery(id+"F1.wireOp",EDGE,"E1086"),sQuery(id+"F1.wireOp",EDGE,"E1087"),sQuery(id+"F1.wireOp",EDGE,"E1088"),sQuery(id+"F1.wireOp",EDGE,"E1089"),sQuery(id+"F1.wireOp",EDGE,"E1090"),sQuery(id+"F1.wireOp",EDGE,"E1091"),sQuery(id+"F1.wireOp",EDGE,"E1092"),sQuery(id+"F1.wireOp",EDGE,"E1093"),sQuery(id+"F1.wireOp",EDGE,"E1094"),sQuery(id+"F1.wireOp",EDGE,"E1095"),sQuery(id+"F1.wireOp",EDGE,"E1096"),sQuery(id+"F1.wireOp",EDGE,"E1097"),sQuery(id+"F1.wireOp",EDGE,"E1098"),sQuery(id+"F1.wireOp",EDGE,"E1099"),sQuery(id+"F1.wireOp",EDGE,"E1100"),sQuery(id+"F1.wireOp",EDGE,"E1101"),sQuery(id+"F1.wireOp",EDGE,"E1102"),sQuery(id+"F1.wireOp",EDGE,"E1103"),sQuery(id+"F1.wireOp",EDGE,"E1104"),sQuery(id+"F1.wireOp",EDGE,"E1105"),sQuery(id+"F1.wireOp",EDGE,"E1106"),sQuery(id+"F1.wireOp",EDGE,"E1107"),sQuery(id+"F1.wireOp",EDGE,"E1108"),sQuery(id+"F1.wireOp",EDGE,"E1109"),sQuery(id+"F1.wireOp",EDGE,"E1110"),sQuery(id+"F1.wireOp",EDGE,"E1111"),sQuery(id+"F1.wireOp",EDGE,"E1112"),sQuery(id+"F1.wireOp",EDGE,"E1113"),sQuery(id+"F1.wireOp",EDGE,"E1114"),sQuery(id+"F1.wireOp",EDGE,"E1115"),sQuery(id+"F1.wireOp",EDGE,"E1116"),sQuery(id+"F1.wireOp",EDGE,"E1117"),sQuery(id+"F1.wireOp",EDGE,"E1118"),sQuery(id+"F1.wireOp",EDGE,"E1119"),sQuery(id+"F1.wireOp",EDGE,"E1120"),sQuery(id+"F1.wireOp",EDGE,"E1121"),sQuery(id+"F1.wireOp",EDGE,"E1122"),sQuery(id+"F1.wireOp",EDGE,"E1123"),sQuery(id+"F1.wireOp",EDGE,"E1124"),sQuery(id+"F1.wireOp",EDGE,"E1125"),sQuery(id+"F1.wireOp",EDGE,"E1126"),sQuery(id+"F1.wireOp",EDGE,"E1127"),sQuery(id+"F1.wireOp",EDGE,"E1128"),sQuery(id+"F1.wireOp",EDGE,"E1129"),sQuery(id+"F1.wireOp",EDGE,"E1130"),sQuery(id+"F1.wireOp",EDGE,"E1131"),sQuery(id+"F1.wireOp",EDGE,"E1132"),sQuery(id+"F1.wireOp",EDGE,"E1133"),sQuery(id+"F1.wireOp",EDGE,"E1134"),sQuery(id+"F1.wireOp",EDGE,"E1135"),sQuery(id+"F1.wireOp",EDGE,"E1136"),sQuery(id+"F1.wireOp",EDGE,"E1137"),sQuery(id+"F1.wireOp",EDGE,"E1138"),sQuery(id+"F1.wireOp",EDGE,"E1139"),sQuery(id+"F1.wireOp",EDGE,"E1140"),sQuery(id+"F1.wireOp",EDGE,"E1141"),sQuery(id+"F1.wireOp",EDGE,"E1142"),sQuery(id+"F1.wireOp",EDGE,"E1143"),sQuery(id+"F1.wireOp",EDGE,"E1144"),sQuery(id+"F1.wireOp",EDGE,"E1145"),sQuery(id+"F1.wireOp",EDGE,"E1146"),sQuery(id+"F1.wireOp",EDGE,"E1147"),sQuery(id+"F1.wireOp",EDGE,"E1148"),sQuery(id+"F1.wireOp",EDGE,"E1149"),sQuery(id+"F1.wireOp",EDGE,"E1150"),sQuery(id+"F1.wireOp",EDGE,"E1151"),sQuery(id+"F1.wireOp",EDGE,"E1152"),sQuery(id+"F1.wireOp",EDGE,"E1153"),sQuery(id+"F1.wireOp",EDGE,"E1154"),sQuery(id+"F1.wireOp",EDGE,"E1155"),sQuery(id+"F1.wireOp",EDGE,"E1156"),sQuery(id+"F1.wireOp",EDGE,"E1156"),sQuery(id+"F1.wireOp",EDGE,"E1157"),sQuery(id+"F1.wireOp",EDGE,"E1158"),sQuery(id+"F1.wireOp",EDGE,"E1159"),sQuery(id+"F1.wireOp",EDGE,"E1160"),sQuery(id+"F1.wireOp",EDGE,"E1161"),sQuery(id+"F1.wireOp",EDGE,"E1162"),sQuery(id+"F1.wireOp",EDGE,"E1163"),sQuery(id+"F1.wireOp",EDGE,"E1164"),sQuery(id+"F1.wireOp",EDGE,"E1165"),sQuery(id+"F1.wireOp",EDGE,"E1166"),sQuery(id+"F1.wireOp",EDGE,"E1167"),sQuery(id+"F1.wireOp",EDGE,"E1168"),sQuery(id+"F1.wireOp",EDGE,"E1169"),sQuery(id+"F1.wireOp",EDGE,"E1170"),sQuery(id+"F1.wireOp",EDGE,"E1171"),sQuery(id+"F1.wireOp",EDGE,"E1172"),sQuery(id+"F1.wireOp",EDGE,"E1173"),sQuery(id+"F1.wireOp",EDGE,"E1174"),sQuery(id+"F1.wireOp",EDGE,"E1175"),sQuery(id+"F1.wireOp",EDGE,"E1176"),sQuery(id+"F1.wireOp",EDGE,"E1177"),sQuery(id+"F1.wireOp",EDGE,"E1178"),sQuery(id+"F1.wireOp",EDGE,"E1179"),sQuery(id+"F1.wireOp",EDGE,"E1180"),sQuery(id+"F1.wireOp",EDGE,"E1181"),sQuery(id+"F1.wireOp",EDGE,"E1182"),sQuery(id+"F1.wireOp",EDGE,"E1183"),sQuery(id+"F1.wireOp",EDGE,"E1184"),sQuery(id+"F1.wireOp",EDGE,"E1185"),sQuery(id+"F1.wireOp",EDGE,"E1186"),sQuery(id+"F1.wireOp",EDGE,"E1187"),sQuery(id+"F1.wireOp",EDGE,"E1188"),sQuery(id+"F1.wireOp",EDGE,"E1189"),sQuery(id+"F1.wireOp",EDGE,"E1190"),sQuery(id+"F1.wireOp",EDGE,"E1191"),sQuery(id+"F1.wireOp",EDGE,"E1192"),sQuery(id+"F1.wireOp",EDGE,"E1193"),sQuery(id+"F1.wireOp",EDGE,"E1194"),sQuery(id+"F1.wireOp",EDGE,"E1195"),sQuery(id+"F1.wireOp",EDGE,"E1196"),sQuery(id+"F1.wireOp",EDGE,"E1197"),sQuery(id+"F1.wireOp",EDGE,"E1198"),sQuery(id+"F1.wireOp",EDGE,"E1199"),sQuery(id+"F1.wireOp",EDGE,"E1200"),sQuery(id+"F1.wireOp",EDGE,"E1201"),sQuery(id+"F1.wireOp",EDGE,"E1202"),sQuery(id+"F1.wireOp",EDGE,"E1203"),sQuery(id+"F1.wireOp",EDGE,"E1204"),sQuery(id+"F1.wireOp",EDGE,"E1205"),sQuery(id+"F1.wireOp",EDGE,"E1206"),sQuery(id+"F1.wireOp",EDGE,"E1207"),sQuery(id+"F1.wireOp",EDGE,"E1208"),sQuery(id+"F1.wireOp",EDGE,"E1209"),sQuery(id+"F1.wireOp",EDGE,"E1210"),sQuery(id+"F1.wireOp",EDGE,"E1211"),sQuery(id+"F1.wireOp",EDGE,"E1212"),sQuery(id+"F1.wireOp",EDGE,"E1213"),sQuery(id+"F1.wireOp",EDGE,"E1214"),sQuery(id+"F1.wireOp",EDGE,"E1215"),sQuery(id+"F1.wireOp",EDGE,"E1216"),sQuery(id+"F1.wireOp",EDGE,"E1217"),sQuery(id+"F1.wireOp",EDGE,"E1218"),sQuery(id+"F1.wireOp",EDGE,"E1219"),sQuery(id+"F1.wireOp",EDGE,"E1220"),sQuery(id+"F1.wireOp",EDGE,"E1221"),sQuery(id+"F1.wireOp",EDGE,"E1222"),sQuery(id+"F1.wireOp",EDGE,"E1223"),sQuery(id+"F1.wireOp",EDGE,"E1224"),sQuery(id+"F1.wireOp",EDGE,"E1225"),sQuery(id+"F1.wireOp",EDGE,"E1226"),sQuery(id+"F1.wireOp",EDGE,"E1227"),sQuery(id+"F1.wireOp",EDGE,"E1228"),sQuery(id+"F1.wireOp",EDGE,"E1229"),sQuery(id+"F1.wireOp",EDGE,"E1230"),sQuery(id+"F1.wireOp",EDGE,"E1231"),sQuery(id+"F1.wireOp",EDGE,"E1232"),sQuery(id+"F1.wireOp",EDGE,"E1233"),sQuery(id+"F1.wireOp",EDGE,"E1234"),sQuery(id+"F1.wireOp",EDGE,"E1235"),sQuery(id+"F1.wireOp",EDGE,"E1236"),sQuery(id+"F1.wireOp",EDGE,"E1237"),sQuery(id+"F1.wireOp",EDGE,"E1238"),sQuery(id+"F1.wireOp",EDGE,"E1239"),sQuery(id+"F1.wireOp",EDGE,"E1240"),sQuery(id+"F1.wireOp",EDGE,"E1241"),sQuery(id+"F1.wireOp",EDGE,"E1242"),sQuery(id+"F1.wireOp",EDGE,"E1243"),sQuery(id+"F1.wireOp",EDGE,"E1244"),sQuery(id+"F1.wireOp",EDGE,"E1245"),sQuery(id+"F1.wireOp",EDGE,"E1246"),sQuery(id+"F1.wireOp",EDGE,"E1247"),sQuery(id+"F1.wireOp",EDGE,"E1248"),sQuery(id+"F1.wireOp",EDGE,"E1249"),sQuery(id+"F1.wireOp",EDGE,"E1250"),sQuery(id+"F1.wireOp",EDGE,"E1251"),sQuery(id+"F1.wireOp",EDGE,"E1252"),sQuery(id+"F1.wireOp",EDGE,"E1253"),sQuery(id+"F1.wireOp",EDGE,"E1254"),sQuery(id+"F1.wireOp",EDGE,"E1255"),sQuery(id+"F1.wireOp",EDGE,"E1256"),sQuery(id+"F1.wireOp",EDGE,"E1257"),sQuery(id+"F1.wireOp",EDGE,"E1258"),sQuery(id+"F1.wireOp",EDGE,"E1259"),sQuery(id+"F1.wireOp",EDGE,"E1260"),sQuery(id+"F1.wireOp",EDGE,"E1261"),sQuery(id+"F1.wireOp",EDGE,"E1262"),sQuery(id+"F1.wireOp",EDGE,"E1263"),sQuery(id+"F1.wireOp",EDGE,"E1264"),sQuery(id+"F1.wireOp",EDGE,"E1265"),sQuery(id+"F1.wireOp",EDGE,"E1266"),sQuery(id+"F1.wireOp",EDGE,"E1267"),sQuery(id+"F1.wireOp",EDGE,"E1268"),sQuery(id+"F1.wireOp",EDGE,"E1269"),sQuery(id+"F1.wireOp",EDGE,"E1270"),sQuery(id+"F1.wireOp",EDGE,"E1271"),sQuery(id+"F1.wireOp",EDGE,"E1272"),sQuery(id+"F1.wireOp",EDGE,"E1273"),sQuery(id+"F1.wireOp",EDGE,"E1274"),sQuery(id+"F1.wireOp",EDGE,"E1275"),sQuery(id+"F1.wireOp",EDGE,"E1276"),sQuery(id+"F1.wireOp",EDGE,"E1277"),sQuery(id+"F1.wireOp",EDGE,"E1278"),sQuery(id+"F1.wireOp",EDGE,"E1279"),sQuery(id+"F1.wireOp",EDGE,"E1280"),sQuery(id+"F1.wireOp",EDGE,"E1281"),sQuery(id+"F1.wireOp",EDGE,"E1282"),sQuery(id+"F1.wireOp",EDGE,"E1283"),sQuery(id+"F1.wireOp",EDGE,"E1284"),sQuery(id+"F1.wireOp",EDGE,"E1285"),sQuery(id+"F1.wireOp",EDGE,"E1286"),sQuery(id+"F1.wireOp",EDGE,"E1287"),sQuery(id+"F1.wireOp",EDGE,"E1288"),sQuery(id+"F1.wireOp",EDGE,"E1289"),sQuery(id+"F1.wireOp",EDGE,"E1290"),sQuery(id+"F1.wireOp",EDGE,"E1291"),sQuery(id+"F1.wireOp",EDGE,"E1292"),sQuery(id+"F1.wireOp",EDGE,"E1293"),sQuery(id+"F1.wireOp",EDGE,"E1294"),sQuery(id+"F1.wireOp",EDGE,"E1295"),sQuery(id+"F1.wireOp",EDGE,"E1296"),sQuery(id+"F1.wireOp",EDGE,"E1297"),sQuery(id+"F1.wireOp",EDGE,"E1298"),sQuery(id+"F1.wireOp",EDGE,"E1299"),sQuery(id+"F1.wireOp",EDGE,"E1300"),sQuery(id+"F1.wireOp",EDGE,"E1301"),sQuery(id+"F1.wireOp",EDGE,"E1302"),sQuery(id+"F1.wireOp",EDGE,"E1303"),sQuery(id+"F1.wireOp",EDGE,"E1304"),sQuery(id+"F1.wireOp",EDGE,"E1305"),sQuery(id+"F1.wireOp",EDGE,"E1306"),sQuery(id+"F1.wireOp",EDGE,"E1307"),sQuery(id+"F1.wireOp",EDGE,"E1308"),sQuery(id+"F1.wireOp",EDGE,"E1309"),sQuery(id+"F1.wireOp",EDGE,"E1310"),sQuery(id+"F1.wireOp",EDGE,"E1311"),sQuery(id+"F1.wireOp",EDGE,"E1312"),sQuery(id+"F1.wireOp",EDGE,"E1312"),sQuery(id+"F1.wireOp",EDGE,"E1313"),sQuery(id+"F1.wireOp",EDGE,"E1314"),sQuery(id+"F1.wireOp",EDGE,"E1315"),sQuery(id+"F1.wireOp",EDGE,"E1316"),sQuery(id+"F1.wireOp",EDGE,"E1317"),sQuery(id+"F1.wireOp",EDGE,"E1318"),sQuery(id+"F1.wireOp",EDGE,"E1319"),sQuery(id+"F1.wireOp",EDGE,"E1320"),sQuery(id+"F1.wireOp",EDGE,"E1321"),sQuery(id+"F1.wireOp",EDGE,"E1322"),sQuery(id+"F1.wireOp",EDGE,"E1323"),sQuery(id+"F1.wireOp",EDGE,"E1324"),sQuery(id+"F1.wireOp",EDGE,"E1325"),sQuery(id+"F1.wireOp",EDGE,"E1326"),sQuery(id+"F1.wireOp",EDGE,"E1327"),sQuery(id+"F1.wireOp",EDGE,"E1328"),sQuery(id+"F1.wireOp",EDGE,"E1329"),sQuery(id+"F1.wireOp",EDGE,"E1330"),sQuery(id+"F1.wireOp",EDGE,"E1331"),sQuery(id+"F1.wireOp",EDGE,"E1332"),sQuery(id+"F1.wireOp",EDGE,"E1333"),sQuery(id+"F1.wireOp",EDGE,"E1334"),sQuery(id+"F1.wireOp",EDGE,"E1335"),sQuery(id+"F1.wireOp",EDGE,"E1336"),sQuery(id+"F1.wireOp",EDGE,"E1337"),sQuery(id+"F1.wireOp",EDGE,"E1338"),sQuery(id+"F1.wireOp",EDGE,"E1339"),sQuery(id+"F1.wireOp",EDGE,"E1340"),sQuery(id+"F1.wireOp",EDGE,"E1341"),sQuery(id+"F1.wireOp",EDGE,"E1342"),sQuery(id+"F1.wireOp",EDGE,"E1343"),sQuery(id+"F1.wireOp",EDGE,"E1344"),sQuery(id+"F1.wireOp",EDGE,"E1345"),sQuery(id+"F1.wireOp",EDGE,"E1346"),sQuery(id+"F1.wireOp",EDGE,"E1347"),sQuery(id+"F1.wireOp",EDGE,"E1348"),sQuery(id+"F1.wireOp",EDGE,"E1349"),sQuery(id+"F1.wireOp",EDGE,"E1350"),sQuery(id+"F1.wireOp",EDGE,"E1351"),sQuery(id+"F1.wireOp",EDGE,"E1352"),sQuery(id+"F1.wireOp",EDGE,"E1353"),sQuery(id+"F1.wireOp",EDGE,"E1354"),sQuery(id+"F1.wireOp",EDGE,"E1355"),sQuery(id+"F1.wireOp",EDGE,"E1356"),sQuery(id+"F1.wireOp",EDGE,"E1357"),sQuery(id+"F1.wireOp",EDGE,"E1358"),sQuery(id+"F1.wireOp",EDGE,"E1359"),sQuery(id+"F1.wireOp",EDGE,"E1360"),sQuery(id+"F1.wireOp",EDGE,"E1361"),sQuery(id+"F1.wireOp",EDGE,"E1362"),sQuery(id+"F1.wireOp",EDGE,"E1363"),sQuery(id+"F1.wireOp",EDGE,"E1364"),sQuery(id+"F1.wireOp",EDGE,"E1365"),sQuery(id+"F1.wireOp",EDGE,"E1366"),sQuery(id+"F1.wireOp",EDGE,"E1367"),sQuery(id+"F1.wireOp",EDGE,"E1368"),sQuery(id+"F1.wireOp",EDGE,"E1369"),sQuery(id+"F1.wireOp",EDGE,"E1370"),sQuery(id+"F1.wireOp",EDGE,"E1371"),sQuery(id+"F1.wireOp",EDGE,"E1372"),sQuery(id+"F1.wireOp",EDGE,"E1373"),sQuery(id+"F1.wireOp",EDGE,"E1374"),sQuery(id+"F1.wireOp",EDGE,"E1375"),sQuery(id+"F1.wireOp",EDGE,"E1376"),sQuery(id+"F1.wireOp",EDGE,"E1376"),sQuery(id+"F1.wireOp",EDGE,"E1377"),sQuery(id+"F1.wireOp",EDGE,"E1378"),sQuery(id+"F1.wireOp",EDGE,"E1379"),sQuery(id+"F1.wireOp",EDGE,"E1380"),sQuery(id+"F1.wireOp",EDGE,"E1381"),sQuery(id+"F1.wireOp",EDGE,"E1382"),sQuery(id+"F1.wireOp",EDGE,"E1383"),sQuery(id+"F1.wireOp",EDGE,"E1384"),sQuery(id+"F1.wireOp",EDGE,"E1385"),sQuery(id+"F1.wireOp",EDGE,"E1386"),sQuery(id+"F1.wireOp",EDGE,"E1387"),sQuery(id+"F1.wireOp",EDGE,"E1388"),sQuery(id+"F1.wireOp",EDGE,"E1389"),sQuery(id+"F1.wireOp",EDGE,"E1390"),sQuery(id+"F1.wireOp",EDGE,"E1391"),sQuery(id+"F1.wireOp",EDGE,"E1392"),sQuery(id+"F1.wireOp",EDGE,"E1393"),sQuery(id+"F1.wireOp",EDGE,"E1394"),sQuery(id+"F1.wireOp",EDGE,"E1395"),sQuery(id+"F1.wireOp",EDGE,"E1396"),sQuery(id+"F1.wireOp",EDGE,"E1397"),sQuery(id+"F1.wireOp",EDGE,"E1398"),sQuery(id+"F1.wireOp",EDGE,"E1399"),sQuery(id+"F1.wireOp",EDGE,"E1400"),sQuery(id+"F1.wireOp",EDGE,"E1401"),sQuery(id+"F1.wireOp",EDGE,"E1402"),sQuery(id+"F1.wireOp",EDGE,"E1403"),sQuery(id+"F1.wireOp",EDGE,"E1404"),sQuery(id+"F1.wireOp",EDGE,"E1405"),sQuery(id+"F1.wireOp",EDGE,"E1406"),sQuery(id+"F1.wireOp",EDGE,"E1407"),sQuery(id+"F1.wireOp",EDGE,"E1408"),sQuery(id+"F1.wireOp",EDGE,"E1409"),sQuery(id+"F1.wireOp",EDGE,"E1410"),sQuery(id+"F1.wireOp",EDGE,"E1411"),sQuery(id+"F1.wireOp",EDGE,"E1412"),sQuery(id+"F1.wireOp",EDGE,"E1413"),sQuery(id+"F1.wireOp",EDGE,"E1414"),sQuery(id+"F1.wireOp",EDGE,"E1415"),sQuery(id+"F1.wireOp",EDGE,"E1416"),sQuery(id+"F1.wireOp",EDGE,"E1417"),sQuery(id+"F1.wireOp",EDGE,"E1418"),sQuery(id+"F1.wireOp",EDGE,"E1419"),sQuery(id+"F1.wireOp",EDGE,"E1420"),sQuery(id+"F1.wireOp",EDGE,"E1421"),sQuery(id+"F1.wireOp",EDGE,"E1422"),sQuery(id+"F1.wireOp",EDGE,"E1423"),sQuery(id+"F1.wireOp",EDGE,"E1424"),sQuery(id+"F1.wireOp",EDGE,"E1425"),sQuery(id+"F1.wireOp",EDGE,"E1426"),sQuery(id+"F1.wireOp",EDGE,"E1427"),sQuery(id+"F1.wireOp",EDGE,"E1428"),sQuery(id+"F1.wireOp",EDGE,"E1429"),sQuery(id+"F1.wireOp",EDGE,"E1430"),sQuery(id+"F1.wireOp",EDGE,"E1431"),sQuery(id+"F1.wireOp",EDGE,"E1432"),sQuery(id+"F1.wireOp",EDGE,"E1433"),sQuery(id+"F1.wireOp",EDGE,"E1434"),sQuery(id+"F1.wireOp",EDGE,"E1435"),sQuery(id+"F1.wireOp",EDGE,"E1436"),sQuery(id+"F1.wireOp",EDGE,"E1437"),sQuery(id+"F1.wireOp",EDGE,"E1438"),sQuery(id+"F1.wireOp",EDGE,"E1439"),sQuery(id+"F1.wireOp",EDGE,"E1440"),sQuery(id+"F1.wireOp",EDGE,"E1441"),sQuery(id+"F1.wireOp",EDGE,"E1442"),sQuery(id+"F1.wireOp",EDGE,"E1443"),sQuery(id+"F1.wireOp",EDGE,"E1444"),sQuery(id+"F1.wireOp",EDGE,"E1445"),sQuery(id+"F1.wireOp",EDGE,"E1446"),sQuery(id+"F1.wireOp",EDGE,"E1447"),sQuery(id+"F1.wireOp",EDGE,"E1448"),sQuery(id+"F1.wireOp",EDGE,"E1449"),sQuery(id+"F1.wireOp",EDGE,"E1450"),sQuery(id+"F1.wireOp",EDGE,"E1451"),sQuery(id+"F1.wireOp",EDGE,"E1452"),sQuery(id+"F1.wireOp",EDGE,"E1453"),sQuery(id+"F1.wireOp",EDGE,"E1454"),sQuery(id+"F1.wireOp",EDGE,"E1455"),sQuery(id+"F1.wireOp",EDGE,"E1456"),sQuery(id+"F1.wireOp",EDGE,"E1457"),sQuery(id+"F1.wireOp",EDGE,"E1458"),sQuery(id+"F1.wireOp",EDGE,"E1459"),sQuery(id+"F1.wireOp",EDGE,"E1460"),sQuery(id+"F1.wireOp",EDGE,"E1461"),sQuery(id+"F1.wireOp",EDGE,"E1462"),sQuery(id+"F1.wireOp",EDGE,"E1463"),sQuery(id+"F1.wireOp",EDGE,"E1464"),sQuery(id+"F1.wireOp",EDGE,"E1465"),sQuery(id+"F1.wireOp",EDGE,"E1466"),sQuery(id+"F1.wireOp",EDGE,"E1467"),sQuery(id+"F1.wireOp",EDGE,"E1468"),sQuery(id+"F1.wireOp",EDGE,"E1469"),sQuery(id+"F1.wireOp",EDGE,"E1470"),sQuery(id+"F1.wireOp",EDGE,"E1471"),sQuery(id+"F1.wireOp",EDGE,"E1472"),sQuery(id+"F1.wireOp",EDGE,"E1473"),sQuery(id+"F1.wireOp",EDGE,"E1474"),sQuery(id+"F1.wireOp",EDGE,"E1475"),sQuery(id+"F1.wireOp",EDGE,"E1476"),sQuery(id+"F1.wireOp",EDGE,"E1477"),sQuery(id+"F1.wireOp",EDGE,"E1478"),sQuery(id+"F1.wireOp",EDGE,"E1479"),sQuery(id+"F1.wireOp",EDGE,"E1480"),sQuery(id+"F1.wireOp",EDGE,"E1481"),sQuery(id+"F1.wireOp",EDGE,"E1482"),sQuery(id+"F1.wireOp",EDGE,"E1483"),sQuery(id+"F1.wireOp",EDGE,"E1484"),sQuery(id+"F1.wireOp",EDGE,"E1485"),sQuery(id+"F1.wireOp",EDGE,"E1486"),sQuery(id+"F1.wireOp",EDGE,"E1487"),sQuery(id+"F1.wireOp",EDGE,"E1488"),sQuery(id+"F1.wireOp",EDGE,"E1489"),sQuery(id+"F1.wireOp",EDGE,"E1490"),sQuery(id+"F1.wireOp",EDGE,"E1491"),sQuery(id+"F1.wireOp",EDGE,"E1492"),sQuery(id+"F1.wireOp",EDGE,"E1493"),sQuery(id+"F1.wireOp",EDGE,"E1494"),sQuery(id+"F1.wireOp",EDGE,"E1495"),sQuery(id+"F1.wireOp",EDGE,"E1496"),sQuery(id+"F1.wireOp",EDGE,"E1497"),sQuery(id+"F1.wireOp",EDGE,"E1498"),sQuery(id+"F1.wireOp",EDGE,"E1499"),sQuery(id+"F1.wireOp",EDGE,"E1500"),sQuery(id+"F1.wireOp",EDGE,"E1501"),sQuery(id+"F1.wireOp",EDGE,"E1502"),sQuery(id+"F1.wireOp",EDGE,"E1503"),sQuery(id+"F1.wireOp",EDGE,"E1504"),sQuery(id+"F1.wireOp",EDGE,"E1505"),sQuery(id+"F1.wireOp",EDGE,"E1506"),sQuery(id+"F1.wireOp",EDGE,"E1507"),sQuery(id+"F1.wireOp",EDGE,"E1508"),sQuery(id+"F1.wireOp",EDGE,"E1509"),sQuery(id+"F1.wireOp",EDGE,"E1510"),sQuery(id+"F1.wireOp",EDGE,"E1511"),sQuery(id+"F1.wireOp",EDGE,"E1512"),sQuery(id+"F1.wireOp",EDGE,"E1513"),sQuery(id+"F1.wireOp",EDGE,"E1514"),sQuery(id+"F1.wireOp",EDGE,"E1515"),sQuery(id+"F1.wireOp",EDGE,"E1516"),sQuery(id+"F1.wireOp",EDGE,"E1517"),sQuery(id+"F1.wireOp",EDGE,"E1518"),sQuery(id+"F1.wireOp",EDGE,"E1519"),sQuery(id+"F1.wireOp",EDGE,"E1520"),sQuery(id+"F1.wireOp",EDGE,"E1521"),sQuery(id+"F1.wireOp",EDGE,"E1522"),sQuery(id+"F1.wireOp",EDGE,"E1523"),sQuery(id+"F1.wireOp",EDGE,"E1524"),sQuery(id+"F1.wireOp",EDGE,"E1525"),sQuery(id+"F1.wireOp",EDGE,"E1526"),sQuery(id+"F1.wireOp",EDGE,"E1527"),sQuery(id+"F1.wireOp",EDGE,"E1528"),sQuery(id+"F1.wireOp",EDGE,"E1529"),sQuery(id+"F1.wireOp",EDGE,"E1530"),sQuery(id+"F1.wireOp",EDGE,"E1531"),sQuery(id+"F1.wireOp",EDGE,"E1532"),sQuery(id+"F1.wireOp",EDGE,"E1533"),sQuery(id+"F1.wireOp",EDGE,"E1534"),sQuery(id+"F1.wireOp",EDGE,"E1535"),sQuery(id+"F1.wireOp",EDGE,"E1536"),sQuery(id+"F1.wireOp",EDGE,"E1537"),sQuery(id+"F1.wireOp",EDGE,"E1538"),sQuery(id+"F1.wireOp",EDGE,"E1539"),sQuery(id+"F1.wireOp",EDGE,"E1540"),sQuery(id+"F1.wireOp",EDGE,"E1541"),sQuery(id+"F1.wireOp",EDGE,"E1542"),sQuery(id+"F1.wireOp",EDGE,"E1543"),sQuery(id+"F1.wireOp",EDGE,"E1544"),sQuery(id+"F1.wireOp",EDGE,"E1545"),sQuery(id+"F1.wireOp",EDGE,"E1546"),sQuery(id+"F1.wireOp",EDGE,"E1547"),sQuery(id+"F1.wireOp",EDGE,"E1548"),sQuery(id+"F1.wireOp",EDGE,"E1549"),sQuery(id+"F1.wireOp",EDGE,"E1550"),sQuery(id+"F1.wireOp",EDGE,"E1551"),sQuery(id+"F1.wireOp",EDGE,"E1552"),sQuery(id+"F1.wireOp",EDGE,"E1553"),sQuery(id+"F1.wireOp",EDGE,"E1554"),sQuery(id+"F1.wireOp",EDGE,"E1555"),sQuery(id+"F1.wireOp",EDGE,"E1556"),sQuery(id+"F1.wireOp",EDGE,"E1557"),sQuery(id+"F1.wireOp",EDGE,"E1558"),sQuery(id+"F1.wireOp",EDGE,"E1559"),sQuery(id+"F1.wireOp",EDGE,"E1560"),sQuery(id+"F1.wireOp",EDGE,"E1561"),sQuery(id+"F1.wireOp",EDGE,"E1562"),sQuery(id+"F1.wireOp",EDGE,"E1563"),sQuery(id+"F1.wireOp",EDGE,"E1564"),sQuery(id+"F1.wireOp",EDGE,"E1565"),sQuery(id+"F1.wireOp",EDGE,"E1566"),sQuery(id+"F1.wireOp",EDGE,"E1567"),sQuery(id+"F1.wireOp",EDGE,"E1568"),sQuery(id+"F1.wireOp",EDGE,"E1569"),sQuery(id+"F1.wireOp",EDGE,"E1570"),sQuery(id+"F1.wireOp",EDGE,"E1571"),sQuery(id+"F1.wireOp",EDGE,"E1572"),sQuery(id+"F1.wireOp",EDGE,"E1573"),sQuery(id+"F1.wireOp",EDGE,"E1574"),sQuery(id+"F1.wireOp",EDGE,"E1575"),sQuery(id+"F1.wireOp",EDGE,"E1576"),sQuery(id+"F1.wireOp",EDGE,"E1577"),sQuery(id+"F1.wireOp",EDGE,"E1578"),sQuery(id+"F1.wireOp",EDGE,"E1579"),sQuery(id+"F1.wireOp",EDGE,"E1580"),sQuery(id+"F1.wireOp",EDGE,"E1581"),sQuery(id+"F1.wireOp",EDGE,"E1582"),sQuery(id+"F1.wireOp",EDGE,"E1583"),sQuery(id+"F1.wireOp",EDGE,"E1584"),sQuery(id+"F1.wireOp",EDGE,"E1585"),sQuery(id+"F1.wireOp",EDGE,"E1586"),sQuery(id+"F1.wireOp",EDGE,"E1587"),sQuery(id+"F1.wireOp",EDGE,"E1588"),sQuery(id+"F1.wireOp",EDGE,"E1589"),sQuery(id+"F1.wireOp",EDGE,"E1590"),sQuery(id+"F1.wireOp",EDGE,"E1591"),sQuery(id+"F1.wireOp",EDGE,"E1592"),sQuery(id+"F1.wireOp",EDGE,"E1593"),sQuery(id+"F1.wireOp",EDGE,"E1594"),sQuery(id+"F1.wireOp",EDGE,"E1595"),sQuery(id+"F1.wireOp",EDGE,"E1596"),sQuery(id+"F1.wireOp",EDGE,"E1597"),sQuery(id+"F1.wireOp",EDGE,"E1598"),sQuery(id+"F1.wireOp",EDGE,"E1599"),sQuery(id+"F1.wireOp",EDGE,"E1600"),sQuery(id+"F1.wireOp",EDGE,"E1601"),sQuery(id+"F1.wireOp",EDGE,"E1602"),sQuery(id+"F1.wireOp",EDGE,"E1603"),sQuery(id+"F1.wireOp",EDGE,"E1604"),sQuery(id+"F1.wireOp",EDGE,"E1605"),sQuery(id+"F1.wireOp",EDGE,"E1606"),sQuery(id+"F1.wireOp",EDGE,"E1607"),sQuery(id+"F1.wireOp",EDGE,"E1608"),sQuery(id+"F1.wireOp",EDGE,"E1609"),sQuery(id+"F1.wireOp",EDGE,"E1610"),sQuery(id+"F1.wireOp",EDGE,"E1611"),sQuery(id+"F1.wireOp",EDGE,"E1612"),sQuery(id+"F1.wireOp",EDGE,"E1613"),sQuery(id+"F1.wireOp",EDGE,"E1614"),sQuery(id+"F1.wireOp",EDGE,"E1615"),sQuery(id+"F1.wireOp",EDGE,"E1616"),sQuery(id+"F1.wireOp",EDGE,"E1617"),sQuery(id+"F1.wireOp",EDGE,"E1618"),sQuery(id+"F1.wireOp",EDGE,"E1619"),sQuery(id+"F1.wireOp",EDGE,"E1620"),sQuery(id+"F1.wireOp",EDGE,"E1621"),sQuery(id+"F1.wireOp",EDGE,"E1622"),sQuery(id+"F1.wireOp",EDGE,"E1623"),sQuery(id+"F1.wireOp",EDGE,"E1624"),sQuery(id+"F1.wireOp",EDGE,"E1625"),sQuery(id+"F1.wireOp",EDGE,"E1626"),sQuery(id+"F1.wireOp",EDGE,"E1627"),sQuery(id+"F1.wireOp",EDGE,"E1628"),sQuery(id+"F1.wireOp",EDGE,"E1629"),sQuery(id+"F1.wireOp",EDGE,"E1630"),sQuery(id+"F1.wireOp",EDGE,"E1631"),sQuery(id+"F1.wireOp",EDGE,"E1632"),sQuery(id+"F1.wireOp",EDGE,"E1633"),sQuery(id+"F1.wireOp",EDGE,"E1634"),sQuery(id+"F1.wireOp",EDGE,"E1635"),sQuery(id+"F1.wireOp",EDGE,"E1636"),sQuery(id+"F1.wireOp",EDGE,"E1637"),sQuery(id+"F1.wireOp",EDGE,"E1638"),sQuery(id+"F1.wireOp",EDGE,"E1639"),sQuery(id+"F1.wireOp",EDGE,"E1640"),sQuery(id+"F1.wireOp",EDGE,"E1641"),sQuery(id+"F1.wireOp",EDGE,"E1642"),sQuery(id+"F1.wireOp",EDGE,"E1643"),sQuery(id+"F1.wireOp",EDGE,"E1644"),sQuery(id+"F1.wireOp",EDGE,"E1645"),sQuery(id+"F1.wireOp",EDGE,"E1646"),sQuery(id+"F1.wireOp",EDGE,"E1647"),sQuery(id+"F1.wireOp",EDGE,"E1648"),sQuery(id+"F1.wireOp",EDGE,"E1649"),sQuery(id+"F1.wireOp",EDGE,"E1650"),sQuery(id+"F1.wireOp",EDGE,"E1651"),sQuery(id+"F1.wireOp",EDGE,"E1652"),sQuery(id+"F1.wireOp",EDGE,"E1653"),sQuery(id+"F1.wireOp",EDGE,"E1654"),sQuery(id+"F1.wireOp",EDGE,"E1655"),sQuery(id+"F1.wireOp",EDGE,"E1656"),sQuery(id+"F1.wireOp",EDGE,"E1657"),sQuery(id+"F1.wireOp",EDGE,"E1658"),sQuery(id+"F1.wireOp",EDGE,"E1659"),sQuery(id+"F1.wireOp",EDGE,"E1660"),sQuery(id+"F1.wireOp",EDGE,"E1661"),sQuery(id+"F1.wireOp",EDGE,"E1662"),sQuery(id+"F1.wireOp",EDGE,"E1663"),sQuery(id+"F1.wireOp",EDGE,"E1664"),sQuery(id+"F1.wireOp",EDGE,"E1665"),sQuery(id+"F1.wireOp",EDGE,"E1666"),sQuery(id+"F1.wireOp",EDGE,"E1667"),sQuery(id+"F1.wireOp",EDGE,"E1668"),sQuery(id+"F1.wireOp",EDGE,"E1669"),sQuery(id+"F1.wireOp",EDGE,"E1670"),sQuery(id+"F1.wireOp",EDGE,"E1671"),sQuery(id+"F1.wireOp",EDGE,"E1672"),sQuery(id+"F1.wireOp",EDGE,"E1673"),sQuery(id+"F1.wireOp",EDGE,"E1674"),sQuery(id+"F1.wireOp",EDGE,"E1675"),sQuery(id+"F1.wireOp",EDGE,"E1676"),sQuery(id+"F1.wireOp",EDGE,"E1677"),sQuery(id+"F1.wireOp",EDGE,"E1678"),sQuery(id+"F1.wireOp",EDGE,"E1679"),sQuery(id+"F1.wireOp",EDGE,"E1680"),sQuery(id+"F1.wireOp",EDGE,"E1681"),sQuery(id+"F1.wireOp",EDGE,"E1682"),sQuery(id+"F1.wireOp",EDGE,"E1683"),sQuery(id+"F1.wireOp",EDGE,"E1684"),sQuery(id+"F1.wireOp",EDGE,"E1685"),sQuery(id+"F1.wireOp",EDGE,"E1686"),sQuery(id+"F1.wireOp",EDGE,"E1687"),sQuery(id+"F1.wireOp",EDGE,"E1688"),sQuery(id+"F1.wireOp",EDGE,"E1689"),sQuery(id+"F1.wireOp",EDGE,"E1690"),sQuery(id+"F1.wireOp",EDGE,"E1691"),sQuery(id+"F1.wireOp",EDGE,"E1692"),sQuery(id+"F1.wireOp",EDGE,"E1693"),sQuery(id+"F1.wireOp",EDGE,"E1694"),sQuery(id+"F1.wireOp",EDGE,"E1695"),sQuery(id+"F1.wireOp",EDGE,"E1696"),sQuery(id+"F1.wireOp",EDGE,"E1697"),sQuery(id+"F1.wireOp",EDGE,"E1698"),sQuery(id+"F1.wireOp",EDGE,"E1699"),sQuery(id+"F1.wireOp",EDGE,"E1700"),sQuery(id+"F1.wireOp",EDGE,"E1701"),sQuery(id+"F1.wireOp",EDGE,"E1702"),sQuery(id+"F1.wireOp",EDGE,"E1703"),sQuery(id+"F1.wireOp",EDGE,"E1704"),sQuery(id+"F1.wireOp",EDGE,"E1705"),sQuery(id+"F1.wireOp",EDGE,"E1706"),sQuery(id+"F1.wireOp",EDGE,"E1707"),sQuery(id+"F1.wireOp",EDGE,"E1708"),sQuery(id+"F1.wireOp",EDGE,"E1709"),sQuery(id+"F1.wireOp",EDGE,"E1710"),sQuery(id+"F1.wireOp",EDGE,"E1711"),sQuery(id+"F1.wireOp",EDGE,"E1712"),sQuery(id+"F1.wireOp",EDGE,"E1713"),sQuery(id+"F1.wireOp",EDGE,"E1714"),sQuery(id+"F1.wireOp",EDGE,"E1715"),sQuery(id+"F1.wireOp",EDGE,"E1716"),sQuery(id+"F1.wireOp",EDGE,"E1717"),sQuery(id+"F1.wireOp",EDGE,"E1718"),sQuery(id+"F1.wireOp",EDGE,"E1719"),sQuery(id+"F1.wireOp",EDGE,"E1720"),sQuery(id+"F1.wireOp",EDGE,"E1721"),sQuery(id+"F1.wireOp",EDGE,"E1722"),sQuery(id+"F1.wireOp",EDGE,"E1723"),sQuery(id+"F1.wireOp",EDGE,"E1724"),sQuery(id+"F1.wireOp",EDGE,"E1725"),sQuery(id+"F1.wireOp",EDGE,"E1726"),sQuery(id+"F1.wireOp",EDGE,"E1727"),sQuery(id+"F1.wireOp",EDGE,"E1728"),sQuery(id+"F1.wireOp",EDGE,"E1729"),sQuery(id+"F1.wireOp",EDGE,"E1730"),sQuery(id+"F1.wireOp",EDGE,"E1731"),sQuery(id+"F1.wireOp",EDGE,"E1732"),sQuery(id+"F1.wireOp",EDGE,"E1733"),sQuery(id+"F1.wireOp",EDGE,"E1734"),sQuery(id+"F1.wireOp",EDGE,"E1735"),sQuery(id+"F1.wireOp",EDGE,"E1736"),sQuery(id+"F1.wireOp",EDGE,"E1737"),sQuery(id+"F1.wireOp",EDGE,"E1738"),sQuery(id+"F1.wireOp",EDGE,"E1739"),sQuery(id+"F1.wireOp",EDGE,"E1740"),sQuery(id+"F1.wireOp",EDGE,"E1741"),sQuery(id+"F1.wireOp",EDGE,"E1742"),sQuery(id+"F1.wireOp",EDGE,"E1743"),sQuery(id+"F1.wireOp",EDGE,"E1744"),sQuery(id+"F1.wireOp",EDGE,"E1745"),sQuery(id+"F1.wireOp",EDGE,"E1746"),sQuery(id+"F1.wireOp",EDGE,"E1747"),sQuery(id+"F1.wireOp",EDGE,"E1748"),sQuery(id+"F1.wireOp",EDGE,"E1749"),sQuery(id+"F1.wireOp",EDGE,"E1750"),sQuery(id+"F1.wireOp",EDGE,"E1751"),sQuery(id+"F1.wireOp",EDGE,"E1752"),sQuery(id+"F1.wireOp",EDGE,"E1753"),sQuery(id+"F1.wireOp",EDGE,"E1754"),sQuery(id+"F1.wireOp",EDGE,"E1755"),sQuery(id+"F1.wireOp",EDGE,"E1756"),sQuery(id+"F1.wireOp",EDGE,"E1757"),sQuery(id+"F1.wireOp",EDGE,"E1758"),sQuery(id+"F1.wireOp",EDGE,"E1759"),sQuery(id+"F1.wireOp",EDGE,"E1760"),sQuery(id+"F1.wireOp",EDGE,"E1761"),sQuery(id+"F1.wireOp",EDGE,"E1762"),sQuery(id+"F1.wireOp",EDGE,"E1763"),sQuery(id+"F1.wireOp",EDGE,"E1764"),sQuery(id+"F1.wireOp",EDGE,"E1765"),sQuery(id+"F1.wireOp",EDGE,"E1766"),sQuery(id+"F1.wireOp",EDGE,"E1767"),sQuery(id+"F1.wireOp",EDGE,"E1768"),sQuery(id+"F1.wireOp",EDGE,"E1769"),sQuery(id+"F1.wireOp",EDGE,"E1770"),sQuery(id+"F1.wireOp",EDGE,"E1771"),sQuery(id+"F1.wireOp",EDGE,"E1772"),sQuery(id+"F1.wireOp",EDGE,"E1773"),sQuery(id+"F1.wireOp",EDGE,"E1774"),sQuery(id+"F1.wireOp",EDGE,"E1775"),sQuery(id+"F1.wireOp",EDGE,"E1776"),sQuery(id+"F1.wireOp",EDGE,"E1777"),sQuery(id+"F1.wireOp",EDGE,"E1778"),sQuery(id+"F1.wireOp",EDGE,"E1779"),sQuery(id+"F1.wireOp",EDGE,"E1780"),sQuery(id+"F1.wireOp",EDGE,"E1781"),sQuery(id+"F1.wireOp",EDGE,"E1782"),sQuery(id+"F1.wireOp",EDGE,"E1783"),sQuery(id+"F1.wireOp",EDGE,"E1784"),sQuery(id+"F1.wireOp",EDGE,"E1785"),sQuery(id+"F1.wireOp",EDGE,"E1786"),sQuery(id+"F1.wireOp",EDGE,"E1787"),sQuery(id+"F1.wireOp",EDGE,"E1788"),sQuery(id+"F1.wireOp",EDGE,"E1789"),sQuery(id+"F1.wireOp",EDGE,"E1790"),sQuery(id+"F1.wireOp",EDGE,"E1791"),sQuery(id+"F1.wireOp",EDGE,"E1792"),sQuery(id+"F1.wireOp",EDGE,"E1793"),sQuery(id+"F1.wireOp",EDGE,"E1794"),sQuery(id+"F1.wireOp",EDGE,"E1795"),sQuery(id+"F1.wireOp",EDGE,"E1796"),sQuery(id+"F1.wireOp",EDGE,"E1797"),sQuery(id+"F1.wireOp",EDGE,"E1798"),sQuery(id+"F1.wireOp",EDGE,"E1799"),sQuery(id+"F1.wireOp",EDGE,"E1800"),sQuery(id+"F1.wireOp",EDGE,"E1801"),sQuery(id+"F1.wireOp",EDGE,"E1802"),sQuery(id+"F1.wireOp",EDGE,"E1803"),sQuery(id+"F1.wireOp",EDGE,"E1804"),sQuery(id+"F1.wireOp",EDGE,"E1805"),sQuery(id+"F1.wireOp",EDGE,"E1806"),sQuery(id+"F1.wireOp",EDGE,"E1807"),sQuery(id+"F1.wireOp",EDGE,"E1808"),sQuery(id+"F1.wireOp",EDGE,"E1809"),sQuery(id+"F1.wireOp",EDGE,"E1810"),sQuery(id+"F1.wireOp",EDGE,"E1811"),sQuery(id+"F1.wireOp",EDGE,"E1812"),sQuery(id+"F1.wireOp",EDGE,"E1813"),sQuery(id+"F1.wireOp",EDGE,"E1814"),sQuery(id+"F1.wireOp",EDGE,"E1815"),sQuery(id+"F1.wireOp",EDGE,"E1816"),sQuery(id+"F1.wireOp",EDGE,"E1817"),sQuery(id+"F1.wireOp",EDGE,"E1818"),sQuery(id+"F1.wireOp",EDGE,"E1819"),sQuery(id+"F1.wireOp",EDGE,"E1820"),sQuery(id+"F1.wireOp",EDGE,"E1821"),sQuery(id+"F1.wireOp",EDGE,"E1822"),sQuery(id+"F1.wireOp",EDGE,"E1823"),sQuery(id+"F1.wireOp",EDGE,"E1824"),sQuery(id+"F1.wireOp",EDGE,"E1825"),sQuery(id+"F1.wireOp",EDGE,"E1826"),sQuery(id+"F1.wireOp",EDGE,"E1827"),sQuery(id+"F1.wireOp",EDGE,"E1828"),sQuery(id+"F1.wireOp",EDGE,"E1829"),sQuery(id+"F1.wireOp",EDGE,"E1830"),sQuery(id+"F1.wireOp",EDGE,"E1831"),sQuery(id+"F1.wireOp",EDGE,"E1832"),sQuery(id+"F1.wireOp",EDGE,"E1833"),sQuery(id+"F1.wireOp",EDGE,"E1834"),sQuery(id+"F1.wireOp",EDGE,"E1835"),sQuery(id+"F1.wireOp",EDGE,"E1836"),sQuery(id+"F1.wireOp",EDGE,"E1837"),sQuery(id+"F1.wireOp",EDGE,"E1838"),sQuery(id+"F1.wireOp",EDGE,"E1839"),sQuery(id+"F1.wireOp",EDGE,"E1840"),sQuery(id+"F1.wireOp",EDGE,"E1841"),sQuery(id+"F1.wireOp",EDGE,"E1842"),sQuery(id+"F1.wireOp",EDGE,"E1843"),sQuery(id+"F1.wireOp",EDGE,"E1844"),sQuery(id+"F1.wireOp",EDGE,"E1845"),sQuery(id+"F1.wireOp",EDGE,"E1846"),sQuery(id+"F1.wireOp",EDGE,"E1847"),sQuery(id+"F1.wireOp",EDGE,"E1848"),sQuery(id+"F1.wireOp",EDGE,"E1849"),sQuery(id+"F1.wireOp",EDGE,"E1850"),sQuery(id+"F1.wireOp",EDGE,"E1851"),sQuery(id+"F1.wireOp",EDGE,"E1852"),sQuery(id+"F1.wireOp",EDGE,"E1853"),sQuery(id+"F1.wireOp",EDGE,"E1854"),sQuery(id+"F1.wireOp",EDGE,"E1855"),sQuery(id+"F1.wireOp",EDGE,"E1856"),sQuery(id+"F1.wireOp",EDGE,"E1857"),sQuery(id+"F1.wireOp",EDGE,"E1858"),sQuery(id+"F1.wireOp",EDGE,"E1859"),sQuery(id+"F1.wireOp",EDGE,"E1860"),sQuery(id+"F1.wireOp",EDGE,"E1861"),sQuery(id+"F1.wireOp",EDGE,"E1862"),sQuery(id+"F1.wireOp",EDGE,"E1863"),sQuery(id+"F1.wireOp",EDGE,"E1864"),sQuery(id+"F1.wireOp",EDGE,"E1865"),sQuery(id+"F1.wireOp",EDGE,"E1866"),sQuery(id+"F1.wireOp",EDGE,"E1867"),sQuery(id+"F1.wireOp",EDGE,"E1868"),sQuery(id+"F1.wireOp",EDGE,"E1869"),sQuery(id+"F1.wireOp",EDGE,"E1870"),sQuery(id+"F1.wireOp",EDGE,"E1871"),sQuery(id+"F1.wireOp",EDGE,"E1872"),sQuery(id+"F1.wireOp",EDGE,"E1873"),sQuery(id+"F1.wireOp",EDGE,"E1874"),sQuery(id+"F1.wireOp",EDGE,"E1875"),sQuery(id+"F1.wireOp",EDGE,"E1876"),sQuery(id+"F1.wireOp",EDGE,"E1877"),sQuery(id+"F1.wireOp",EDGE,"E1878"),sQuery(id+"F1.wireOp",EDGE,"E1879"),sQuery(id+"F1.wireOp",EDGE,"E1880"),sQuery(id+"F1.wireOp",EDGE,"E1881"),sQuery(id+"F1.wireOp",EDGE,"E1882"),sQuery(id+"F1.wireOp",EDGE,"E1883"),sQuery(id+"F1.wireOp",EDGE,"E1884"),sQuery(id+"F1.wireOp",EDGE,"E1885"),sQuery(id+"F1.wireOp",EDGE,"E1886"),sQuery(id+"F1.wireOp",EDGE,"E1887"),sQuery(id+"F1.wireOp",EDGE,"E1888"),sQuery(id+"F1.wireOp",EDGE,"E1889"),sQuery(id+"F1.wireOp",EDGE,"E1890"),sQuery(id+"F1.wireOp",EDGE,"E1891"),sQuery(id+"F1.wireOp",EDGE,"E1892"),sQuery(id+"F1.wireOp",EDGE,"E1893"),sQuery(id+"F1.wireOp",EDGE,"E1894"),sQuery(id+"F1.wireOp",EDGE,"E1895"),sQuery(id+"F1.wireOp",EDGE,"E1896"),sQuery(id+"F1.wireOp",EDGE,"E1897"),sQuery(id+"F1.wireOp",EDGE,"E1898"),sQuery(id+"F1.wireOp",EDGE,"E1899"),sQuery(id+"F1.wireOp",EDGE,"E1900"),sQuery(id+"F1.wireOp",EDGE,"E1901"),sQuery(id+"F1.wireOp",EDGE,"E1902"),sQuery(id+"F1.wireOp",EDGE,"E1903"),sQuery(id+"F1.wireOp",EDGE,"E1904"),sQuery(id+"F1.wireOp",EDGE,"E1905"),sQuery(id+"F1.wireOp",EDGE,"E1906"),sQuery(id+"F1.wireOp",EDGE,"E1907"),sQuery(id+"F1.wireOp",EDGE,"E1908"),sQuery(id+"F1.wireOp",EDGE,"E1909"),sQuery(id+"F1.wireOp",EDGE,"E1910"),sQuery(id+"F1.wireOp",EDGE,"E1911"),sQuery(id+"F1.wireOp",EDGE,"E1912"),sQuery(id+"F1.wireOp",EDGE,"E1913"),sQuery(id+"F1.wireOp",EDGE,"E1914"),sQuery(id+"F1.wireOp",EDGE,"E1915"),sQuery(id+"F1.wireOp",EDGE,"E1916"),sQuery(id+"F1.wireOp",EDGE,"E1917"),sQuery(id+"F1.wireOp",EDGE,"E1918"),sQuery(id+"F1.wireOp",EDGE,"E1919"),sQuery(id+"F1.wireOp",EDGE,"E1920"),sQuery(id+"F1.wireOp",EDGE,"E1921"),sQuery(id+"F1.wireOp",EDGE,"E1922"),sQuery(id+"F1.wireOp",EDGE,"E1923"),sQuery(id+"F1.wireOp",EDGE,"E1924"),sQuery(id+"F1.wireOp",EDGE,"E1925"),sQuery(id+"F1.wireOp",EDGE,"E1926"),sQuery(id+"F1.wireOp",EDGE,"E1927"),sQuery(id+"F1.wireOp",EDGE,"E1928"),sQuery(id+"F1.wireOp",EDGE,"E1929"),sQuery(id+"F1.wireOp",EDGE,"E1930"),sQuery(id+"F1.wireOp",EDGE,"E1931"),sQuery(id+"F1.wireOp",EDGE,"E1932"),sQuery(id+"F1.wireOp",EDGE,"E1933"),sQuery(id+"F1.wireOp",EDGE,"E1934"),sQuery(id+"F1.wireOp",EDGE,"E1935"),sQuery(id+"F1.wireOp",EDGE,"E1936"),sQuery(id+"F1.wireOp",EDGE,"E1937"),sQuery(id+"F1.wireOp",EDGE,"E1938"),sQuery(id+"F1.wireOp",EDGE,"E1939"),sQuery(id+"F1.wireOp",EDGE,"E1940"),sQuery(id+"F1.wireOp",EDGE,"E1941"),sQuery(id+"F1.wireOp",EDGE,"E1942"),sQuery(id+"F1.wireOp",EDGE,"E1943"),sQuery(id+"F1.wireOp",EDGE,"E1944"),sQuery(id+"F1.wireOp",EDGE,"E1945"),sQuery(id+"F1.wireOp",EDGE,"E1946"),sQuery(id+"F1.wireOp",EDGE,"E1947"),sQuery(id+"F1.wireOp",EDGE,"E1948"),sQuery(id+"F1.wireOp",EDGE,"E1949"),sQuery(id+"F1.wireOp",EDGE,"E1950"),sQuery(id+"F1.wireOp",EDGE,"E1951"),sQuery(id+"F1.wireOp",EDGE,"E1952"),sQuery(id+"F1.wireOp",EDGE,"E1953"),sQuery(id+"F1.wireOp",EDGE,"E1954"),sQuery(id+"F1.wireOp",EDGE,"E1955"),sQuery(id+"F1.wireOp",EDGE,"E1956"),sQuery(id+"F1.wireOp",EDGE,"E1957"),sQuery(id+"F1.wireOp",EDGE,"E1958"),sQuery(id+"F1.wireOp",EDGE,"E1959"),sQuery(id+"F1.wireOp",EDGE,"E1960"),sQuery(id+"F1.wireOp",EDGE,"E1961"),sQuery(id+"F1.wireOp",EDGE,"E1962"),sQuery(id+"F1.wireOp",EDGE,"E1963"),sQuery(id+"F1.wireOp",EDGE,"E1964"),sQuery(id+"F1.wireOp",EDGE,"E1965"),sQuery(id+"F1.wireOp",EDGE,"E1966"),sQuery(id+"F1.wireOp",EDGE,"E1967"),sQuery(id+"F1.wireOp",EDGE,"E1968"),sQuery(id+"F1.wireOp",EDGE,"E1969"),sQuery(id+"F1.wireOp",EDGE,"E1970"),sQuery(id+"F1.wireOp",EDGE,"E1971"),sQuery(id+"F1.wireOp",EDGE,"E1972"),sQuery(id+"F1.wireOp",EDGE,"E1973"),sQuery(id+"F1.wireOp",EDGE,"E1974"),sQuery(id+"F1.wireOp",EDGE,"E1975"),sQuery(id+"F1.wireOp",EDGE,"E1976"),sQuery(id+"F1.wireOp",EDGE,"E1977"),sQuery(id+"F1.wireOp",EDGE,"E1978"),sQuery(id+"F1.wireOp",EDGE,"E1979"),sQuery(id+"F1.wireOp",EDGE,"E1980"),sQuery(id+"F1.wireOp",EDGE,"E1981"),sQuery(id+"F1.wireOp",EDGE,"E1982"),sQuery(id+"F1.wireOp",EDGE,"E1983"),sQuery(id+"F1.wireOp",EDGE,"E1984"),sQuery(id+"F1.wireOp",EDGE,"E1985"),sQuery(id+"F1.wireOp",EDGE,"E1986"),sQuery(id+"F1.wireOp",EDGE,"E1987"),sQuery(id+"F1.wireOp",EDGE,"E1988"),sQuery(id+"F1.wireOp",EDGE,"E1989"),sQuery(id+"F1.wireOp",EDGE,"E1990"),sQuery(id+"F1.wireOp",EDGE,"E1991"),sQuery(id+"F1.wireOp",EDGE,"E1992"),sQuery(id+"F1.wireOp",EDGE,"E1993"),sQuery(id+"F1.wireOp",EDGE,"E1994"),sQuery(id+"F1.wireOp",EDGE,"E1995"),sQuery(id+"F1.wireOp",EDGE,"E1996"),sQuery(id+"F1.wireOp",EDGE,"E1997"),sQuery(id+"F1.wireOp",EDGE,"E1998"),sQuery(id+"F1.wireOp",EDGE,"E1999"),sQuery(id+"F1.wireOp",EDGE,"E2000"),sQuery(id+"F1.wireOp",EDGE,"E2000"),sQuery(id+"F1.wireOp",EDGE,"E2001"),sQuery(id+"F1.wireOp",EDGE,"E2002"),sQuery(id+"F1.wireOp",EDGE,"E2003"),sQuery(id+"F1.wireOp",EDGE,"E2004"),sQuery(id+"F1.wireOp",EDGE,"E2005"),sQuery(id+"F1.wireOp",EDGE,"E2006"),sQuery(id+"F1.wireOp",EDGE,"E2007"),sQuery(id+"F1.wireOp",EDGE,"E2008"),sQuery(id+"F1.wireOp",EDGE,"E2009"),sQuery(id+"F1.wireOp",EDGE,"E2010"),sQuery(id+"F1.wireOp",EDGE,"E2011"),sQuery(id+"F1.wireOp",EDGE,"E2012"),sQuery(id+"F1.wireOp",EDGE,"E2013"),sQuery(id+"F1.wireOp",EDGE,"E2014"),sQuery(id+"F1.wireOp",EDGE,"E2015"),sQuery(id+"F1.wireOp",EDGE,"E2016"),sQuery(id+"F1.wireOp",EDGE,"E2017"),sQuery(id+"F1.wireOp",EDGE,"E2018"),sQuery(id+"F1.wireOp",EDGE,"E2019"),sQuery(id+"F1.wireOp",EDGE,"E2020"),sQuery(id+"F1.wireOp",EDGE,"E2021"),sQuery(id+"F1.wireOp",EDGE,"E2022"),sQuery(id+"F1.wireOp",EDGE,"E2023"),sQuery(id+"F1.wireOp",EDGE,"E2024"),sQuery(id+"F1.wireOp",EDGE,"E2025"),sQuery(id+"F1.wireOp",EDGE,"E2026"),sQuery(id+"F1.wireOp",EDGE,"E2027"),sQuery(id+"F1.wireOp",EDGE,"E2028"),sQuery(id+"F1.wireOp",EDGE,"E2029"),sQuery(id+"F1.wireOp",EDGE,"E2030"),sQuery(id+"F1.wireOp",EDGE,"E2031"),sQuery(id+"F1.wireOp",EDGE,"E2032"),sQuery(id+"F1.wireOp",EDGE,"E2033"),sQuery(id+"F1.wireOp",EDGE,"E2034"),sQuery(id+"F1.wireOp",EDGE,"E2035"),sQuery(id+"F1.wireOp",EDGE,"E2036"),sQuery(id+"F1.wireOp",EDGE,"E2037"),sQuery(id+"F1.wireOp",EDGE,"E2038"),sQuery(id+"F1.wireOp",EDGE,"E2039"),sQuery(id+"F1.wireOp",EDGE,"E2040"),sQuery(id+"F1.wireOp",EDGE,"E2041"),sQuery(id+"F1.wireOp",EDGE,"E2042"),sQuery(id+"F1.wireOp",EDGE,"E2043"),sQuery(id+"F1.wireOp",EDGE,"E2044"),sQuery(id+"F1.wireOp",EDGE,"E2045"),sQuery(id+"F1.wireOp",EDGE,"E2046"),sQuery(id+"F1.wireOp",EDGE,"E2047"),sQuery(id+"F1.wireOp",EDGE,"E2048"),sQuery(id+"F1.wireOp",EDGE,"E2049"),sQuery(id+"F1.wireOp",EDGE,"E2050"),sQuery(id+"F1.wireOp",EDGE,"E2051"),sQuery(id+"F1.wireOp",EDGE,"E2052"),sQuery(id+"F1.wireOp",EDGE,"E2053"),sQuery(id+"F1.wireOp",EDGE,"E2054"),sQuery(id+"F1.wireOp",EDGE,"E2055"),sQuery(id+"F1.wireOp",EDGE,"E2056"),sQuery(id+"F1.wireOp",EDGE,"E2057"),sQuery(id+"F1.wireOp",EDGE,"E2058"),sQuery(id+"F1.wireOp",EDGE,"E2059"),sQuery(id+"F1.wireOp",EDGE,"E2060"),sQuery(id+"F1.wireOp",EDGE,"E2061"),sQuery(id+"F1.wireOp",EDGE,"E2062"),sQuery(id+"F1.wireOp",EDGE,"E2063"),sQuery(id+"F1.wireOp",EDGE,"E2064"),sQuery(id+"F1.wireOp",EDGE,"E2065"),sQuery(id+"F1.wireOp",EDGE,"E2066"),sQuery(id+"F1.wireOp",EDGE,"E2067"),sQuery(id+"F1.wireOp",EDGE,"E2068"),sQuery(id+"F1.wireOp",EDGE,"E2069"),sQuery(id+"F1.wireOp",EDGE,"E2070"),sQuery(id+"F1.wireOp",EDGE,"E2071"),sQuery(id+"F1.wireOp",EDGE,"E2072"),sQuery(id+"F1.wireOp",EDGE,"E2073"),sQuery(id+"F1.wireOp",EDGE,"E2074"),sQuery(id+"F1.wireOp",EDGE,"E2075"),sQuery(id+"F1.wireOp",EDGE,"E2076"),sQuery(id+"F1.wireOp",EDGE,"E2077"),sQuery(id+"F1.wireOp",EDGE,"E2078"),sQuery(id+"F1.wireOp",EDGE,"E2079"),sQuery(id+"F1.wireOp",EDGE,"E2080"),sQuery(id+"F1.wireOp",EDGE,"E2081"),sQuery(id+"F1.wireOp",EDGE,"E2082"),sQuery(id+"F1.wireOp",EDGE,"E2083"),sQuery(id+"F1.wireOp",EDGE,"E2084"),sQuery(id+"F1.wireOp",EDGE,"E2085"),sQuery(id+"F1.wireOp",EDGE,"E2086"),sQuery(id+"F1.wireOp",EDGE,"E2087"),sQuery(id+"F1.wireOp",EDGE,"E2088"),sQuery(id+"F1.wireOp",EDGE,"E2089"),sQuery(id+"F1.wireOp",EDGE,"E2090"),sQuery(id+"F1.wireOp",EDGE,"E2091"),sQuery(id+"F1.wireOp",EDGE,"E2092"),sQuery(id+"F1.wireOp",EDGE,"E2093"),sQuery(id+"F1.wireOp",EDGE,"E2094"),sQuery(id+"F1.wireOp",EDGE,"E2095"),sQuery(id+"F1.wireOp",EDGE,"E2096"),sQuery(id+"F1.wireOp",EDGE,"E2097"),sQuery(id+"F1.wireOp",EDGE,"E2098"),sQuery(id+"F1.wireOp",EDGE,"E2099"),sQuery(id+"F1.wireOp",EDGE,"E2100"),sQuery(id+"F1.wireOp",EDGE,"E2101"),sQuery(id+"F1.wireOp",EDGE,"E2102"),sQuery(id+"F1.wireOp",EDGE,"E2103"),sQuery(id+"F1.wireOp",EDGE,"E2104"),sQuery(id+"F1.wireOp",EDGE,"E2105"),sQuery(id+"F1.wireOp",EDGE,"E2106"),sQuery(id+"F1.wireOp",EDGE,"E2107"),sQuery(id+"F1.wireOp",EDGE,"E2108"),sQuery(id+"F1.wireOp",EDGE,"E2109"),sQuery(id+"F1.wireOp",EDGE,"E2110"),sQuery(id+"F1.wireOp",EDGE,"E2111"),sQuery(id+"F1.wireOp",EDGE,"E2112"),sQuery(id+"F1.wireOp",EDGE,"E2113"),sQuery(id+"F1.wireOp",EDGE,"E2114"),sQuery(id+"F1.wireOp",EDGE,"E2115"),sQuery(id+"F1.wireOp",EDGE,"E2116"),sQuery(id+"F1.wireOp",EDGE,"E2117"),sQuery(id+"F1.wireOp",EDGE,"E2118"),sQuery(id+"F1.wireOp",EDGE,"E2119"),sQuery(id+"F1.wireOp",EDGE,"E2120"),sQuery(id+"F1.wireOp",EDGE,"E2121"),sQuery(id+"F1.wireOp",EDGE,"E2122"),sQuery(id+"F1.wireOp",EDGE,"E2123"),sQuery(id+"F1.wireOp",EDGE,"E2124"),sQuery(id+"F1.wireOp",EDGE,"E2125"),sQuery(id+"F1.wireOp",EDGE,"E2126"),sQuery(id+"F1.wireOp",EDGE,"E2127"),sQuery(id+"F1.wireOp",EDGE,"E2128"),sQuery(id+"F1.wireOp",EDGE,"E2129"),sQuery(id+"F1.wireOp",EDGE,"E2130"),sQuery(id+"F1.wireOp",EDGE,"E2131"),sQuery(id+"F1.wireOp",EDGE,"E2132"),sQuery(id+"F1.wireOp",EDGE,"E2133"),sQuery(id+"F1.wireOp",EDGE,"E2134"),sQuery(id+"F1.wireOp",EDGE,"E2135"),sQuery(id+"F1.wireOp",EDGE,"E2136"),sQuery(id+"F1.wireOp",EDGE,"E2137"),sQuery(id+"F1.wireOp",EDGE,"E2138"),sQuery(id+"F1.wireOp",EDGE,"E2139"),sQuery(id+"F1.wireOp",EDGE,"E2140"),sQuery(id+"F1.wireOp",EDGE,"E2141"),sQuery(id+"F1.wireOp",EDGE,"E2142"),sQuery(id+"F1.wireOp",EDGE,"E2143"),sQuery(id+"F1.wireOp",EDGE,"E2144"),sQuery(id+"F1.wireOp",EDGE,"E2145"),sQuery(id+"F1.wireOp",EDGE,"E2146"),sQuery(id+"F1.wireOp",EDGE,"E2147"),sQuery(id+"F1.wireOp",EDGE,"E2148"),sQuery(id+"F1.wireOp",EDGE,"E2149"),sQuery(id+"F1.wireOp",EDGE,"E2150"),sQuery(id+"F1.wireOp",EDGE,"E2151"),sQuery(id+"F1.wireOp",EDGE,"E2152"),sQuery(id+"F1.wireOp",EDGE,"E2153"),sQuery(id+"F1.wireOp",EDGE,"E2154"),sQuery(id+"F1.wireOp",EDGE,"E2155"),sQuery(id+"F1.wireOp",EDGE,"E2156"),sQuery(id+"F1.wireOp",EDGE,"E2157"),sQuery(id+"F1.wireOp",EDGE,"E2158"),sQuery(id+"F1.wireOp",EDGE,"E2159"),sQuery(id+"F1.wireOp",EDGE,"E2160"),sQuery(id+"F1.wireOp",EDGE,"E2161"),sQuery(id+"F1.wireOp",EDGE,"E2162"),sQuery(id+"F1.wireOp",EDGE,"E2163"),sQuery(id+"F1.wireOp",EDGE,"E2164"),sQuery(id+"F1.wireOp",EDGE,"E2165"),sQuery(id+"F1.wireOp",EDGE,"E2166"),sQuery(id+"F1.wireOp",EDGE,"E2167"),sQuery(id+"F1.wireOp",EDGE,"E2168"),sQuery(id+"F1.wireOp",EDGE,"E2169"),sQuery(id+"F1.wireOp",EDGE,"E2170"),sQuery(id+"F1.wireOp",EDGE,"E2171"),sQuery(id+"F1.wireOp",EDGE,"E2172"),sQuery(id+"F1.wireOp",EDGE,"E2173"),sQuery(id+"F1.wireOp",EDGE,"E2174"),sQuery(id+"F1.wireOp",EDGE,"E2175"),sQuery(id+"F1.wireOp",EDGE,"E2176"),sQuery(id+"F1.wireOp",EDGE,"E2177"),sQuery(id+"F1.wireOp",EDGE,"E2178"),sQuery(id+"F1.wireOp",EDGE,"E2179"),sQuery(id+"F1.wireOp",EDGE,"E2180"),sQuery(id+"F1.wireOp",EDGE,"E2181"),sQuery(id+"F1.wireOp",EDGE,"E2182"),sQuery(id+"F1.wireOp",EDGE,"E2183"),sQuery(id+"F1.wireOp",EDGE,"E2184"),sQuery(id+"F1.wireOp",EDGE,"E2185"),sQuery(id+"F1.wireOp",EDGE,"E2186"),sQuery(id+"F1.wireOp",EDGE,"E2187"),sQuery(id+"F1.wireOp",EDGE,"E2188"),sQuery(id+"F1.wireOp",EDGE,"E2189"),sQuery(id+"F1.wireOp",EDGE,"E2190"),sQuery(id+"F1.wireOp",EDGE,"E2191"),sQuery(id+"F1.wireOp",EDGE,"E2192"),sQuery(id+"F1.wireOp",EDGE,"E2193"),sQuery(id+"F1.wireOp",EDGE,"E2194"),sQuery(id+"F1.wireOp",EDGE,"E2195"),sQuery(id+"F1.wireOp",EDGE,"E2196"),sQuery(id+"F1.wireOp",EDGE,"E2197"),sQuery(id+"F1.wireOp",EDGE,"E2198"),sQuery(id+"F1.wireOp",EDGE,"E2199"),sQuery(id+"F1.wireOp",EDGE,"E2200"),sQuery(id+"F1.wireOp",EDGE,"E2201"),sQuery(id+"F1.wireOp",EDGE,"E2202"),sQuery(id+"F1.wireOp",EDGE,"E2203"),sQuery(id+"F1.wireOp",EDGE,"E2204"),sQuery(id+"F1.wireOp",EDGE,"E2205"),sQuery(id+"F1.wireOp",EDGE,"E2206"),sQuery(id+"F1.wireOp",EDGE,"E2207"),sQuery(id+"F1.wireOp",EDGE,"E2208"),sQuery(id+"F1.wireOp",EDGE,"E2209"),sQuery(id+"F1.wireOp",EDGE,"E2210"),sQuery(id+"F1.wireOp",EDGE,"E2211"),sQuery(id+"F1.wireOp",EDGE,"E2212"),sQuery(id+"F1.wireOp",EDGE,"E2213"),sQuery(id+"F1.wireOp",EDGE,"E2214"),sQuery(id+"F1.wireOp",EDGE,"E2215"),sQuery(id+"F1.wireOp",EDGE,"E2216"),sQuery(id+"F1.wireOp",EDGE,"E2217"),sQuery(id+"F1.wireOp",EDGE,"E2218"),sQuery(id+"F1.wireOp",EDGE,"E2219"),sQuery(id+"F1.wireOp",EDGE,"E2220"),sQuery(id+"F1.wireOp",EDGE,"E2221"),sQuery(id+"F1.wireOp",EDGE,"E2222"),sQuery(id+"F1.wireOp",EDGE,"E2223"),sQuery(id+"F1.wireOp",EDGE,"E2224"),sQuery(id+"F1.wireOp",EDGE,"E2225"),sQuery(id+"F1.wireOp",EDGE,"E2226"),sQuery(id+"F1.wireOp",EDGE,"E2227"),sQuery(id+"F1.wireOp",EDGE,"E2228"),sQuery(id+"F1.wireOp",EDGE,"E2229"),sQuery(id+"F1.wireOp",EDGE,"E2230"),sQuery(id+"F1.wireOp",EDGE,"E2231"),sQuery(id+"F1.wireOp",EDGE,"E2232"),sQuery(id+"F1.wireOp",EDGE,"E2233"),sQuery(id+"F1.wireOp",EDGE,"E2234"),sQuery(id+"F1.wireOp",EDGE,"E2235"),sQuery(id+"F1.wireOp",EDGE,"E2236"),sQuery(id+"F1.wireOp",EDGE,"E2237"),sQuery(id+"F1.wireOp",EDGE,"E2238"),sQuery(id+"F1.wireOp",EDGE,"E2239"),sQuery(id+"F1.wireOp",EDGE,"E2240"),sQuery(id+"F1.wireOp",EDGE,"E2241"),sQuery(id+"F1.wireOp",EDGE,"E2242"),sQuery(id+"F1.wireOp",EDGE,"E2243"),sQuery(id+"F1.wireOp",EDGE,"E2244"),sQuery(id+"F1.wireOp",EDGE,"E2245"),sQuery(id+"F1.wireOp",EDGE,"E2246"),sQuery(id+"F1.wireOp",EDGE,"E2247"),sQuery(id+"F1.wireOp",EDGE,"E2248"),sQuery(id+"F1.wireOp",EDGE,"E2249"),sQuery(id+"F1.wireOp",EDGE,"E2250"),sQuery(id+"F1.wireOp",EDGE,"E2251"),sQuery(id+"F1.wireOp",EDGE,"E2252"),sQuery(id+"F1.wireOp",EDGE,"E2253"),sQuery(id+"F1.wireOp",EDGE,"E2254"),sQuery(id+"F1.wireOp",EDGE,"E2255"),sQuery(id+"F1.wireOp",EDGE,"E2256"),sQuery(id+"F1.wireOp",EDGE,"E2257"),sQuery(id+"F1.wireOp",EDGE,"E2258"),sQuery(id+"F1.wireOp",EDGE,"E2259"),sQuery(id+"F1.wireOp",EDGE,"E2260"),sQuery(id+"F1.wireOp",EDGE,"E2261"),sQuery(id+"F1.wireOp",EDGE,"E2262"),sQuery(id+"F1.wireOp",EDGE,"E2263"),sQuery(id+"F1.wireOp",EDGE,"E2264"),sQuery(id+"F1.wireOp",EDGE,"E2265"),sQuery(id+"F1.wireOp",EDGE,"E2266"),sQuery(id+"F1.wireOp",EDGE,"E2267"),sQuery(id+"F1.wireOp",EDGE,"E2268"),sQuery(id+"F1.wireOp",EDGE,"E2269"),sQuery(id+"F1.wireOp",EDGE,"E2270"),sQuery(id+"F1.wireOp",EDGE,"E2271"),sQuery(id+"F1.wireOp",EDGE,"E2272"),sQuery(id+"F1.wireOp",EDGE,"E2273"),sQuery(id+"F1.wireOp",EDGE,"E2274"),sQuery(id+"F1.wireOp",EDGE,"E2275"),sQuery(id+"F1.wireOp",EDGE,"E2276"),sQuery(id+"F1.wireOp",EDGE,"E2277"),sQuery(id+"F1.wireOp",EDGE,"E2278"),sQuery(id+"F1.wireOp",EDGE,"E2279"),sQuery(id+"F1.wireOp",EDGE,"E2280"),sQuery(id+"F1.wireOp",EDGE,"E2281"),sQuery(id+"F1.wireOp",EDGE,"E2282"),sQuery(id+"F1.wireOp",EDGE,"E2283"),sQuery(id+"F1.wireOp",EDGE,"E2284"),sQuery(id+"F1.wireOp",EDGE,"E2285"),sQuery(id+"F1.wireOp",EDGE,"E2286"),sQuery(id+"F1.wireOp",EDGE,"E2287"),sQuery(id+"F1.wireOp",EDGE,"E2288"),sQuery(id+"F1.wireOp",EDGE,"E2289"),sQuery(id+"F1.wireOp",EDGE,"E2290"),sQuery(id+"F1.wireOp",EDGE,"E2291"),sQuery(id+"F1.wireOp",EDGE,"E2292"),sQuery(id+"F1.wireOp",EDGE,"E2293"),sQuery(id+"F1.wireOp",EDGE,"E2294"),sQuery(id+"F1.wireOp",EDGE,"E2295"),sQuery(id+"F1.wireOp",EDGE,"E2296"),sQuery(id+"F1.wireOp",EDGE,"E2297"),sQuery(id+"F1.wireOp",EDGE,"E2298"),sQuery(id+"F1.wireOp",EDGE,"E2299"),sQuery(id+"F1.wireOp",EDGE,"E2300"),sQuery(id+"F1.wireOp",EDGE,"E2301"),sQuery(id+"F1.wireOp",EDGE,"E2302"),sQuery(id+"F1.wireOp",EDGE,"E2303"),sQuery(id+"F1.wireOp",EDGE,"E2304"),sQuery(id+"F1.wireOp",EDGE,"E2305"),sQuery(id+"F1.wireOp",EDGE,"E2306"),sQuery(id+"F1.wireOp",EDGE,"E2307"),sQuery(id+"F1.wireOp",EDGE,"E2308"),sQuery(id+"F1.wireOp",EDGE,"E2309"),sQuery(id+"F1.wireOp",EDGE,"E2310"),sQuery(id+"F1.wireOp",EDGE,"E2311"),sQuery(id+"F1.wireOp",EDGE,"E2312"),sQuery(id+"F1.wireOp",EDGE,"E2313"),sQuery(id+"F1.wireOp",EDGE,"E2314"),sQuery(id+"F1.wireOp",EDGE,"E2315"),sQuery(id+"F1.wireOp",EDGE,"E2316"),sQuery(id+"F1.wireOp",EDGE,"E2317"),sQuery(id+"F1.wireOp",EDGE,"E2318"),sQuery(id+"F1.wireOp",EDGE,"E2319"),sQuery(id+"F1.wireOp",EDGE,"E2320"),sQuery(id+"F1.wireOp",EDGE,"E2321"),sQuery(id+"F1.wireOp",EDGE,"E2322"),sQuery(id+"F1.wireOp",EDGE,"E2323"),sQuery(id+"F1.wireOp",EDGE,"E2324"),sQuery(id+"F1.wireOp",EDGE,"E2325"),sQuery(id+"F1.wireOp",EDGE,"E2326"),sQuery(id+"F1.wireOp",EDGE,"E2327"),sQuery(id+"F1.wireOp",EDGE,"E2328"),sQuery(id+"F1.wireOp",EDGE,"E2329"),sQuery(id+"F1.wireOp",EDGE,"E2330"),sQuery(id+"F1.wireOp",EDGE,"E2331"),sQuery(id+"F1.wireOp",EDGE,"E2332"),sQuery(id+"F1.wireOp",EDGE,"E2333"),sQuery(id+"F1.wireOp",EDGE,"E2334"),sQuery(id+"F1.wireOp",EDGE,"E2335"),sQuery(id+"F1.wireOp",EDGE,"E2336"),sQuery(id+"F1.wireOp",EDGE,"E2337"),sQuery(id+"F1.wireOp",EDGE,"E2338"),sQuery(id+"F1.wireOp",EDGE,"E2339"),sQuery(id+"F1.wireOp",EDGE,"E2340"),sQuery(id+"F1.wireOp",EDGE,"E2341"),sQuery(id+"F1.wireOp",EDGE,"E2342"),sQuery(id+"F1.wireOp",EDGE,"E2343"),sQuery(id+"F1.wireOp",EDGE,"E2344"),sQuery(id+"F1.wireOp",EDGE,"E2345"),sQuery(id+"F1.wireOp",EDGE,"E2346"),sQuery(id+"F1.wireOp",EDGE,"E2347"),sQuery(id+"F1.wireOp",EDGE,"E2348"),sQuery(id+"F1.wireOp",EDGE,"E2349"),sQuery(id+"F1.wireOp",EDGE,"E2350"),sQuery(id+"F1.wireOp",EDGE,"E2351"),sQuery(id+"F1.wireOp",EDGE,"E2352"),sQuery(id+"F1.wireOp",EDGE,"E2353"),sQuery(id+"F1.wireOp",EDGE,"E2354"),sQuery(id+"F1.wireOp",EDGE,"E2355"),sQuery(id+"F1.wireOp",EDGE,"E2356"),sQuery(id+"F1.wireOp",EDGE,"E2357"),sQuery(id+"F1.wireOp",EDGE,"E2358"),sQuery(id+"F1.wireOp",EDGE,"E2359"),sQuery(id+"F1.wireOp",EDGE,"E2360"),sQuery(id+"F1.wireOp",EDGE,"E2361"),sQuery(id+"F1.wireOp",EDGE,"E2362"),sQuery(id+"F1.wireOp",EDGE,"E2363"),sQuery(id+"F1.wireOp",EDGE,"E2364"),sQuery(id+"F1.wireOp",EDGE,"E2365"),sQuery(id+"F1.wireOp",EDGE,"E2366"),sQuery(id+"F1.wireOp",EDGE,"E2367"),sQuery(id+"F1.wireOp",EDGE,"E2368"),sQuery(id+"F1.wireOp",EDGE,"E2369"),sQuery(id+"F1.wireOp",EDGE,"E2370"),sQuery(id+"F1.wireOp",EDGE,"E2371"),sQuery(id+"F1.wireOp",EDGE,"E2372"),sQuery(id+"F1.wireOp",EDGE,"E2373"),sQuery(id+"F1.wireOp",EDGE,"E2374"),sQuery(id+"F1.wireOp",EDGE,"E2375"),sQuery(id+"F1.wireOp",EDGE,"E2376"),sQuery(id+"F1.wireOp",EDGE,"E2377"),sQuery(id+"F1.wireOp",EDGE,"E2378"),sQuery(id+"F1.wireOp",EDGE,"E2379"),sQuery(id+"F1.wireOp",EDGE,"E2380"),sQuery(id+"F1.wireOp",EDGE,"E2381"),sQuery(id+"F1.wireOp",EDGE,"E2382"),sQuery(id+"F1.wireOp",EDGE,"E2383"),sQuery(id+"F1.wireOp",EDGE,"E2384"),sQuery(id+"F1.wireOp",EDGE,"E2385"),sQuery(id+"F1.wireOp",EDGE,"E2386"),sQuery(id+"F1.wireOp",EDGE,"E2387"),sQuery(id+"F1.wireOp",EDGE,"E2388"),sQuery(id+"F1.wireOp",EDGE,"E2389"),sQuery(id+"F1.wireOp",EDGE,"E2390"),sQuery(id+"F1.wireOp",EDGE,"E2391"),sQuery(id+"F1.wireOp",EDGE,"E2392"),sQuery(id+"F1.wireOp",EDGE,"E2393"),sQuery(id+"F1.wireOp",EDGE,"E2394"),sQuery(id+"F1.wireOp",EDGE,"E2395"),sQuery(id+"F1.wireOp",EDGE,"E2396"),sQuery(id+"F1.wireOp",EDGE,"E2397"),sQuery(id+"F1.wireOp",EDGE,"E2398"),sQuery(id+"F1.wireOp",EDGE,"E2399"),sQuery(id+"F1.wireOp",EDGE,"E2400"),sQuery(id+"F1.wireOp",EDGE,"E2401"),sQuery(id+"F1.wireOp",EDGE,"E2402"),sQuery(id+"F1.wireOp",EDGE,"E2403"),sQuery(id+"F1.wireOp",EDGE,"E2404"),sQuery(id+"F1.wireOp",EDGE,"E2405"),sQuery(id+"F1.wireOp",EDGE,"E2406"),sQuery(id+"F1.wireOp",EDGE,"E2407"),sQuery(id+"F1.wireOp",EDGE,"E2408"),sQuery(id+"F1.wireOp",EDGE,"E2409"),sQuery(id+"F1.wireOp",EDGE,"E2410"),sQuery(id+"F1.wireOp",EDGE,"E2411"),sQuery(id+"F1.wireOp",EDGE,"E2412"),sQuery(id+"F1.wireOp",EDGE,"E2413"),sQuery(id+"F1.wireOp",EDGE,"E2414"),sQuery(id+"F1.wireOp",EDGE,"E2415"),sQuery(id+"F1.wireOp",EDGE,"E2416"),sQuery(id+"F1.wireOp",EDGE,"E2417"),sQuery(id+"F1.wireOp",EDGE,"E2418"),sQuery(id+"F1.wireOp",EDGE,"E2419"),sQuery(id+"F1.wireOp",EDGE,"E2420"),sQuery(id+"F1.wireOp",EDGE,"E2421"),sQuery(id+"F1.wireOp",EDGE,"E2422"),sQuery(id+"F1.wireOp",EDGE,"E2423"),sQuery(id+"F1.wireOp",EDGE,"E2424"),sQuery(id+"F1.wireOp",EDGE,"E2425"),sQuery(id+"F1.wireOp",EDGE,"E2426"),sQuery(id+"F1.wireOp",EDGE,"E2427"),sQuery(id+"F1.wireOp",EDGE,"E2428"),sQuery(id+"F1.wireOp",EDGE,"E2429"),sQuery(id+"F1.wireOp",EDGE,"E2430"),sQuery(id+"F1.wireOp",EDGE,"E2431"),sQuery(id+"F1.wireOp",EDGE,"E2432"),sQuery(id+"F1.wireOp",EDGE,"E2433"),sQuery(id+"F1.wireOp",EDGE,"E2434"),sQuery(id+"F1.wireOp",EDGE,"E2435"),sQuery(id+"F1.wireOp",EDGE,"E2436"),sQuery(id+"F1.wireOp",EDGE,"E2437"),sQuery(id+"F1.wireOp",EDGE,"E2438"),sQuery(id+"F1.wireOp",EDGE,"E2439"),sQuery(id+"F1.wireOp",EDGE,"E2440"),sQuery(id+"F1.wireOp",EDGE,"E2441"),sQuery(id+"F1.wireOp",EDGE,"E2442"),sQuery(id+"F1.wireOp",EDGE,"E2443"),sQuery(id+"F1.wireOp",EDGE,"E2444"),sQuery(id+"F1.wireOp",EDGE,"E2445"),sQuery(id+"F1.wireOp",EDGE,"E2446"),sQuery(id+"F1.wireOp",EDGE,"E2447"),sQuery(id+"F1.wireOp",EDGE,"E2448"),sQuery(id+"F1.wireOp",EDGE,"E2449"),sQuery(id+"F1.wireOp",EDGE,"E2450"),sQuery(id+"F1.wireOp",EDGE,"E2451"),sQuery(id+"F1.wireOp",EDGE,"E2452"),sQuery(id+"F1.wireOp",EDGE,"E2453"),sQuery(id+"F1.wireOp",EDGE,"E2454"),sQuery(id+"F1.wireOp",EDGE,"E2455"),sQuery(id+"F1.wireOp",EDGE,"E2456"),sQuery(id+"F1.wireOp",EDGE,"E2457"),sQuery(id+"F1.wireOp",EDGE,"E2458"),sQuery(id+"F1.wireOp",EDGE,"E2459"),sQuery(id+"F1.wireOp",EDGE,"E2460"),sQuery(id+"F1.wireOp",EDGE,"E2461"),sQuery(id+"F1.wireOp",EDGE,"E2462"),sQuery(id+"F1.wireOp",EDGE,"E2463"),sQuery(id+"F1.wireOp",EDGE,"E2464"),sQuery(id+"F1.wireOp",EDGE,"E2465"),sQuery(id+"F1.wireOp",EDGE,"E2466"),sQuery(id+"F1.wireOp",EDGE,"E2467"),sQuery(id+"F1.wireOp",EDGE,"E2468"),sQuery(id+"F1.wireOp",EDGE,"E2469"),sQuery(id+"F1.wireOp",EDGE,"E2470"),sQuery(id+"F1.wireOp",EDGE,"E2471"),sQuery(id+"F1.wireOp",EDGE,"E2472"),sQuery(id+"F1.wireOp",EDGE,"E2473"),sQuery(id+"F1.wireOp",EDGE,"E2474"),sQuery(id+"F1.wireOp",EDGE,"E2475"),sQuery(id+"F1.wireOp",EDGE,"E2476"),sQuery(id+"F1.wireOp",EDGE,"E2477"),sQuery(id+"F1.wireOp",EDGE,"E2478"),sQuery(id+"F1.wireOp",EDGE,"E2479"),sQuery(id+"F1.wireOp",EDGE,"E2480"),sQuery(id+"F1.wireOp",EDGE,"E2481"),sQuery(id+"F1.wireOp",EDGE,"E2482"),sQuery(id+"F1.wireOp",EDGE,"E2483"),sQuery(id+"F1.wireOp",EDGE,"E2484"),sQuery(id+"F1.wireOp",EDGE,"E2485"),sQuery(id+"F1.wireOp",EDGE,"E2486"),sQuery(id+"F1.wireOp",EDGE,"E2487"),sQuery(id+"F1.wireOp",EDGE,"E2488"),sQuery(id+"F1.wireOp",EDGE,"E2489"),sQuery(id+"F1.wireOp",EDGE,"E2490"),sQuery(id+"F1.wireOp",EDGE,"E2491"),sQuery(id+"F1.wireOp",EDGE,"E2492"),sQuery(id+"F1.wireOp",EDGE,"E2493"),sQuery(id+"F1.wireOp",EDGE,"E2494"),sQuery(id+"F1.wireOp",EDGE,"E2495"),sQuery(id+"F1.wireOp",EDGE,"E2496"),sQuery(id+"F1.wireOp",EDGE,"E2497"),sQuery(id+"F1.wireOp",EDGE,"E2498"),sQuery(id+"F1.wireOp",EDGE,"E2499"),sQuery(id+"F1.wireOp",EDGE,"E2500"),sQuery(id+"F1.wireOp",EDGE,"E2501"),sQuery(id+"F1.wireOp",EDGE,"E2502"),sQuery(id+"F1.wireOp",EDGE,"E2503"),sQuery(id+"F1.wireOp",EDGE,"E2504"),sQuery(id+"F1.wireOp",EDGE,"E2505"),sQuery(id+"F1.wireOp",EDGE,"E2506"),sQuery(id+"F1.wireOp",EDGE,"E2507"),sQuery(id+"F1.wireOp",EDGE,"E2508"),sQuery(id+"F1.wireOp",EDGE,"E2509"),sQuery(id+"F1.wireOp",EDGE,"E2510"),sQuery(id+"F1.wireOp",EDGE,"E2511"),sQuery(id+"F1.wireOp",EDGE,"E2512"),sQuery(id+"F1.wireOp",EDGE,"E2513"),sQuery(id+"F1.wireOp",EDGE,"E2514"),sQuery(id+"F1.wireOp",EDGE,"E2515"),sQuery(id+"F1.wireOp",EDGE,"E2516"),sQuery(id+"F1.wireOp",EDGE,"E2517"),sQuery(id+"F1.wireOp",EDGE,"E2518"),sQuery(id+"F1.wireOp",EDGE,"E2519"),sQuery(id+"F1.wireOp",EDGE,"E2520"),sQuery(id+"F1.wireOp",EDGE,"E2521"),sQuery(id+"F1.wireOp",EDGE,"E2522"),sQuery(id+"F1.wireOp",EDGE,"E2523"),sQuery(id+"F1.wireOp",EDGE,"E2524"),sQuery(id+"F1.wireOp",EDGE,"E2525"),sQuery(id+"F1.wireOp",EDGE,"E2526"),sQuery(id+"F1.wireOp",EDGE,"E2527"),sQuery(id+"F1.wireOp",EDGE,"E2528"),sQuery(id+"F1.wireOp",EDGE,"E2529"),sQuery(id+"F1.wireOp",EDGE,"E2530"),sQuery(id+"F1.wireOp",EDGE,"E2531"),sQuery(id+"F1.wireOp",EDGE,"E2532"),sQuery(id+"F1.wireOp",EDGE,"E2533"),sQuery(id+"F1.wireOp",EDGE,"E2534"),sQuery(id+"F1.wireOp",EDGE,"E2535"),sQuery(id+"F1.wireOp",EDGE,"E2536"),sQuery(id+"F1.wireOp",EDGE,"E2537"),sQuery(id+"F1.wireOp",EDGE,"E2538"),sQuery(id+"F1.wireOp",EDGE,"E2539"),sQuery(id+"F1.wireOp",EDGE,"E2540"),sQuery(id+"F1.wireOp",EDGE,"E2541"),sQuery(id+"F1.wireOp",EDGE,"E2542"),sQuery(id+"F1.wireOp",EDGE,"E2543"),sQuery(id+"F1.wireOp",EDGE,"E2544"),sQuery(id+"F1.wireOp",EDGE,"E2545"),sQuery(id+"F1.wireOp",EDGE,"E2546"),sQuery(id+"F1.wireOp",EDGE,"E2547"),sQuery(id+"F1.wireOp",EDGE,"E2548"),sQuery(id+"F1.wireOp",EDGE,"E2549"),sQuery(id+"F1.wireOp",EDGE,"E2550"),sQuery(id+"F1.wireOp",EDGE,"E2551"),sQuery(id+"F1.wireOp",EDGE,"E2552"),sQuery(id+"F1.wireOp",EDGE,"E2553"),sQuery(id+"F1.wireOp",EDGE,"E2554"),sQuery(id+"F1.wireOp",EDGE,"E2555"),sQuery(id+"F1.wireOp",EDGE,"E2556"),sQuery(id+"F1.wireOp",EDGE,"E2557"),sQuery(id+"F1.wireOp",EDGE,"E2558"),sQuery(id+"F1.wireOp",EDGE,"E2559"),sQuery(id+"F1.wireOp",EDGE,"E2560"),sQuery(id+"F1.wireOp",EDGE,"E2561"),sQuery(id+"F1.wireOp",EDGE,"E2562"),sQuery(id+"F1.wireOp",EDGE,"E2563"),sQuery(id+"F1.wireOp",EDGE,"E2564"),sQuery(id+"F1.wireOp",EDGE,"E2565"),sQuery(id+"F1.wireOp",EDGE,"E2566"),sQuery(id+"F1.wireOp",EDGE,"E2567"),sQuery(id+"F1.wireOp",EDGE,"E2568"),sQuery(id+"F1.wireOp",EDGE,"E2569"),sQuery(id+"F1.wireOp",EDGE,"E2570"),sQuery(id+"F1.wireOp",EDGE,"E2571"),sQuery(id+"F1.wireOp",EDGE,"E2572"),sQuery(id+"F1.wireOp",EDGE,"E2573"),sQuery(id+"F1.wireOp",EDGE,"E2574"),sQuery(id+"F1.wireOp",EDGE,"E2575"),sQuery(id+"F1.wireOp",EDGE,"E2576"),sQuery(id+"F1.wireOp",EDGE,"E2577"),sQuery(id+"F1.wireOp",EDGE,"E2578"),sQuery(id+"F1.wireOp",EDGE,"E2579"),sQuery(id+"F1.wireOp",EDGE,"E2580"),sQuery(id+"F1.wireOp",EDGE,"E2581"),sQuery(id+"F1.wireOp",EDGE,"E2582"),sQuery(id+"F1.wireOp",EDGE,"E2583"),sQuery(id+"F1.wireOp",EDGE,"E2584"),sQuery(id+"F1.wireOp",EDGE,"E2585"),sQuery(id+"F1.wireOp",EDGE,"E2586"),sQuery(id+"F1.wireOp",EDGE,"E2587"),sQuery(id+"F1.wireOp",EDGE,"E2588"),sQuery(id+"F1.wireOp",EDGE,"E2589"),sQuery(id+"F1.wireOp",EDGE,"E2590"),sQuery(id+"F1.wireOp",EDGE,"E2591"),sQuery(id+"F1.wireOp",EDGE,"E2592"),sQuery(id+"F1.wireOp",EDGE,"E2593"),sQuery(id+"F1.wireOp",EDGE,"E2594"),sQuery(id+"F1.wireOp",EDGE,"E2595"),sQuery(id+"F1.wireOp",EDGE,"E2596"),sQuery(id+"F1.wireOp",EDGE,"E2597"),sQuery(id+"F1.wireOp",EDGE,"E2598"),sQuery(id+"F1.wireOp",EDGE,"E2599"),sQuery(id+"F1.wireOp",EDGE,"E2600"),sQuery(id+"F1.wireOp",EDGE,"E2601"),sQuery(id+"F1.wireOp",EDGE,"E2602"),sQuery(id+"F1.wireOp",EDGE,"E2603"),sQuery(id+"F1.wireOp",EDGE,"E2604"),sQuery(id+"F1.wireOp",EDGE,"E2605"),sQuery(id+"F1.wireOp",EDGE,"E2606"),sQuery(id+"F1.wireOp",EDGE,"E2607"),sQuery(id+"F1.wireOp",EDGE,"E2608"),sQuery(id+"F1.wireOp",EDGE,"E2609"),sQuery(id+"F1.wireOp",EDGE,"E2610"),sQuery(id+"F1.wireOp",EDGE,"E2611"),sQuery(id+"F1.wireOp",EDGE,"E2612"),sQuery(id+"F1.wireOp",EDGE,"E2613"),sQuery(id+"F1.wireOp",EDGE,"E2614"),sQuery(id+"F1.wireOp",EDGE,"E2615"),sQuery(id+"F1.wireOp",EDGE,"E2616"),sQuery(id+"F1.wireOp",EDGE,"E2617"),sQuery(id+"F1.wireOp",EDGE,"E2618"),sQuery(id+"F1.wireOp",EDGE,"E2619"),sQuery(id+"F1.wireOp",EDGE,"E2620"),sQuery(id+"F1.wireOp",EDGE,"E2622")])]});
            var Q1;
            Q1=sQuery(id+"F0.wireOp",VERTEX,"E0.center");
            transform(context, id + "F3", {"entities" : qUnion([Q0]), "transformType" : TransformType.SCALE_UNIFORMLY, "scale" : 0.95, "scalePoint" : qUnion([Q1]), "makeCopy" : false});
        }
        {
            var Q0;
            Q0=makeQuery(id+"F2.opExtrude","SWEPT_BODY",BODY,{"disambiguationData":[OSD([sQuery(id+"F1.wireOp",EDGE,"E15"),sQuery(id+"F1.wireOp",EDGE,"E16"),sQuery(id+"F1.wireOp",EDGE,"E17"),sQuery(id+"F1.wireOp",EDGE,"E18"),sQuery(id+"F1.wireOp",EDGE,"E19"),sQuery(id+"F1.wireOp",EDGE,"E20"),sQuery(id+"F1.wireOp",EDGE,"E21"),sQuery(id+"F1.wireOp",EDGE,"E22"),sQuery(id+"F1.wireOp",EDGE,"E23"),sQuery(id+"F1.wireOp",EDGE,"E24"),sQuery(id+"F1.wireOp",EDGE,"E25"),sQuery(id+"F1.wireOp",EDGE,"E26"),sQuery(id+"F1.wireOp",EDGE,"E27"),sQuery(id+"F1.wireOp",EDGE,"E28"),sQuery(id+"F1.wireOp",EDGE,"E29"),sQuery(id+"F1.wireOp",EDGE,"E30"),sQuery(id+"F1.wireOp",EDGE,"E31"),sQuery(id+"F1.wireOp",EDGE,"E32"),sQuery(id+"F1.wireOp",EDGE,"E33"),sQuery(id+"F1.wireOp",EDGE,"E34"),sQuery(id+"F1.wireOp",EDGE,"E35"),sQuery(id+"F1.wireOp",EDGE,"E36"),sQuery(id+"F1.wireOp",EDGE,"E37"),sQuery(id+"F1.wireOp",EDGE,"E38"),sQuery(id+"F1.wireOp",EDGE,"E39"),sQuery(id+"F1.wireOp",EDGE,"E40"),sQuery(id+"F1.wireOp",EDGE,"E41"),sQuery(id+"F1.wireOp",EDGE,"E42"),sQuery(id+"F1.wireOp",EDGE,"E43"),sQuery(id+"F1.wireOp",EDGE,"E44"),sQuery(id+"F1.wireOp",EDGE,"E45"),sQuery(id+"F1.wireOp",EDGE,"E45"),sQuery(id+"F1.wireOp",EDGE,"E46"),sQuery(id+"F1.wireOp",EDGE,"E47"),sQuery(id+"F1.wireOp",EDGE,"E48"),sQuery(id+"F1.wireOp",EDGE,"E49"),sQuery(id+"F1.wireOp",EDGE,"E50"),sQuery(id+"F1.wireOp",EDGE,"E51"),sQuery(id+"F1.wireOp",EDGE,"E52"),sQuery(id+"F1.wireOp",EDGE,"E53"),sQuery(id+"F1.wireOp",EDGE,"E54"),sQuery(id+"F1.wireOp",EDGE,"E55"),sQuery(id+"F1.wireOp",EDGE,"E56"),sQuery(id+"F1.wireOp",EDGE,"E57"),sQuery(id+"F1.wireOp",EDGE,"E58"),sQuery(id+"F1.wireOp",EDGE,"E59"),sQuery(id+"F1.wireOp",EDGE,"E60"),sQuery(id+"F1.wireOp",EDGE,"E61"),sQuery(id+"F1.wireOp",EDGE,"E62"),sQuery(id+"F1.wireOp",EDGE,"E63"),sQuery(id+"F1.wireOp",EDGE,"E64"),sQuery(id+"F1.wireOp",EDGE,"E65"),sQuery(id+"F1.wireOp",EDGE,"E66"),sQuery(id+"F1.wireOp",EDGE,"E67"),sQuery(id+"F1.wireOp",EDGE,"E68"),sQuery(id+"F1.wireOp",EDGE,"E69"),sQuery(id+"F1.wireOp",EDGE,"E70"),sQuery(id+"F1.wireOp",EDGE,"E71"),sQuery(id+"F1.wireOp",EDGE,"E72"),sQuery(id+"F1.wireOp",EDGE,"E73"),sQuery(id+"F1.wireOp",EDGE,"E74"),sQuery(id+"F1.wireOp",EDGE,"E75"),sQuery(id+"F1.wireOp",EDGE,"E76"),sQuery(id+"F1.wireOp",EDGE,"E77"),sQuery(id+"F1.wireOp",EDGE,"E78"),sQuery(id+"F1.wireOp",EDGE,"E79"),sQuery(id+"F1.wireOp",EDGE,"E80"),sQuery(id+"F1.wireOp",EDGE,"E81"),sQuery(id+"F1.wireOp",EDGE,"E82"),sQuery(id+"F1.wireOp",EDGE,"E83"),sQuery(id+"F1.wireOp",EDGE,"E84"),sQuery(id+"F1.wireOp",EDGE,"E85"),sQuery(id+"F1.wireOp",EDGE,"E86"),sQuery(id+"F1.wireOp",EDGE,"E87"),sQuery(id+"F1.wireOp",EDGE,"E88"),sQuery(id+"F1.wireOp",EDGE,"E89"),sQuery(id+"F1.wireOp",EDGE,"E90"),sQuery(id+"F1.wireOp",EDGE,"E91"),sQuery(id+"F1.wireOp",EDGE,"E92"),sQuery(id+"F1.wireOp",EDGE,"E93"),sQuery(id+"F1.wireOp",EDGE,"E94"),sQuery(id+"F1.wireOp",EDGE,"E95"),sQuery(id+"F1.wireOp",EDGE,"E96"),sQuery(id+"F1.wireOp",EDGE,"E97"),sQuery(id+"F1.wireOp",EDGE,"E98"),sQuery(id+"F1.wireOp",EDGE,"E99"),sQuery(id+"F1.wireOp",EDGE,"E100"),sQuery(id+"F1.wireOp",EDGE,"E101"),sQuery(id+"F1.wireOp",EDGE,"E102"),sQuery(id+"F1.wireOp",EDGE,"E103"),sQuery(id+"F1.wireOp",EDGE,"E104"),sQuery(id+"F1.wireOp",EDGE,"E104"),sQuery(id+"F1.wireOp",EDGE,"E105"),sQuery(id+"F1.wireOp",EDGE,"E106"),sQuery(id+"F1.wireOp",EDGE,"E107"),sQuery(id+"F1.wireOp",EDGE,"E108"),sQuery(id+"F1.wireOp",EDGE,"E109"),sQuery(id+"F1.wireOp",EDGE,"E110"),sQuery(id+"F1.wireOp",EDGE,"E111"),sQuery(id+"F1.wireOp",EDGE,"E112"),sQuery(id+"F1.wireOp",EDGE,"E113"),sQuery(id+"F1.wireOp",EDGE,"E114"),sQuery(id+"F1.wireOp",EDGE,"E115"),sQuery(id+"F1.wireOp",EDGE,"E116"),sQuery(id+"F1.wireOp",EDGE,"E117"),sQuery(id+"F1.wireOp",EDGE,"E118"),sQuery(id+"F1.wireOp",EDGE,"E119"),sQuery(id+"F1.wireOp",EDGE,"E120"),sQuery(id+"F1.wireOp",EDGE,"E121"),sQuery(id+"F1.wireOp",EDGE,"E122"),sQuery(id+"F1.wireOp",EDGE,"E123"),sQuery(id+"F1.wireOp",EDGE,"E124"),sQuery(id+"F1.wireOp",EDGE,"E125"),sQuery(id+"F1.wireOp",EDGE,"E126"),sQuery(id+"F1.wireOp",EDGE,"E127"),sQuery(id+"F1.wireOp",EDGE,"E128"),sQuery(id+"F1.wireOp",EDGE,"E129"),sQuery(id+"F1.wireOp",EDGE,"E130"),sQuery(id+"F1.wireOp",EDGE,"E131"),sQuery(id+"F1.wireOp",EDGE,"E132"),sQuery(id+"F1.wireOp",EDGE,"E133"),sQuery(id+"F1.wireOp",EDGE,"E134"),sQuery(id+"F1.wireOp",EDGE,"E135"),sQuery(id+"F1.wireOp",EDGE,"E136"),sQuery(id+"F1.wireOp",EDGE,"E137"),sQuery(id+"F1.wireOp",EDGE,"E138"),sQuery(id+"F1.wireOp",EDGE,"E139"),sQuery(id+"F1.wireOp",EDGE,"E140"),sQuery(id+"F1.wireOp",EDGE,"E141"),sQuery(id+"F1.wireOp",EDGE,"E142"),sQuery(id+"F1.wireOp",EDGE,"E143"),sQuery(id+"F1.wireOp",EDGE,"E144"),sQuery(id+"F1.wireOp",EDGE,"E145"),sQuery(id+"F1.wireOp",EDGE,"E146"),sQuery(id+"F1.wireOp",EDGE,"E147"),sQuery(id+"F1.wireOp",EDGE,"E148"),sQuery(id+"F1.wireOp",EDGE,"E149"),sQuery(id+"F1.wireOp",EDGE,"E150"),sQuery(id+"F1.wireOp",EDGE,"E151"),sQuery(id+"F1.wireOp",EDGE,"E152"),sQuery(id+"F1.wireOp",EDGE,"E153"),sQuery(id+"F1.wireOp",EDGE,"E154"),sQuery(id+"F1.wireOp",EDGE,"E155"),sQuery(id+"F1.wireOp",EDGE,"E156"),sQuery(id+"F1.wireOp",EDGE,"E157"),sQuery(id+"F1.wireOp",EDGE,"E158"),sQuery(id+"F1.wireOp",EDGE,"E159"),sQuery(id+"F1.wireOp",EDGE,"E160"),sQuery(id+"F1.wireOp",EDGE,"E161"),sQuery(id+"F1.wireOp",EDGE,"E162"),sQuery(id+"F1.wireOp",EDGE,"E163"),sQuery(id+"F1.wireOp",EDGE,"E164"),sQuery(id+"F1.wireOp",EDGE,"E165"),sQuery(id+"F1.wireOp",EDGE,"E166"),sQuery(id+"F1.wireOp",EDGE,"E167"),sQuery(id+"F1.wireOp",EDGE,"E168"),sQuery(id+"F1.wireOp",EDGE,"E169"),sQuery(id+"F1.wireOp",EDGE,"E170"),sQuery(id+"F1.wireOp",EDGE,"E171"),sQuery(id+"F1.wireOp",EDGE,"E172"),sQuery(id+"F1.wireOp",EDGE,"E173"),sQuery(id+"F1.wireOp",EDGE,"E174"),sQuery(id+"F1.wireOp",EDGE,"E175"),sQuery(id+"F1.wireOp",EDGE,"E176"),sQuery(id+"F1.wireOp",EDGE,"E177"),sQuery(id+"F1.wireOp",EDGE,"E178"),sQuery(id+"F1.wireOp",EDGE,"E179"),sQuery(id+"F1.wireOp",EDGE,"E180"),sQuery(id+"F1.wireOp",EDGE,"E181"),sQuery(id+"F1.wireOp",EDGE,"E182"),sQuery(id+"F1.wireOp",EDGE,"E183"),sQuery(id+"F1.wireOp",EDGE,"E184"),sQuery(id+"F1.wireOp",EDGE,"E185"),sQuery(id+"F1.wireOp",EDGE,"E186"),sQuery(id+"F1.wireOp",EDGE,"E187"),sQuery(id+"F1.wireOp",EDGE,"E188"),sQuery(id+"F1.wireOp",EDGE,"E189"),sQuery(id+"F1.wireOp",EDGE,"E190"),sQuery(id+"F1.wireOp",EDGE,"E191"),sQuery(id+"F1.wireOp",EDGE,"E192"),sQuery(id+"F1.wireOp",EDGE,"E193"),sQuery(id+"F1.wireOp",EDGE,"E194"),sQuery(id+"F1.wireOp",EDGE,"E195"),sQuery(id+"F1.wireOp",EDGE,"E196"),sQuery(id+"F1.wireOp",EDGE,"E197"),sQuery(id+"F1.wireOp",EDGE,"E198"),sQuery(id+"F1.wireOp",EDGE,"E199"),sQuery(id+"F1.wireOp",EDGE,"E200"),sQuery(id+"F1.wireOp",EDGE,"E201"),sQuery(id+"F1.wireOp",EDGE,"E202"),sQuery(id+"F1.wireOp",EDGE,"E203"),sQuery(id+"F1.wireOp",EDGE,"E204"),sQuery(id+"F1.wireOp",EDGE,"E205"),sQuery(id+"F1.wireOp",EDGE,"E206"),sQuery(id+"F1.wireOp",EDGE,"E207"),sQuery(id+"F1.wireOp",EDGE,"E208"),sQuery(id+"F1.wireOp",EDGE,"E209"),sQuery(id+"F1.wireOp",EDGE,"E210"),sQuery(id+"F1.wireOp",EDGE,"E211"),sQuery(id+"F1.wireOp",EDGE,"E212"),sQuery(id+"F1.wireOp",EDGE,"E213"),sQuery(id+"F1.wireOp",EDGE,"E214"),sQuery(id+"F1.wireOp",EDGE,"E215"),sQuery(id+"F1.wireOp",EDGE,"E216"),sQuery(id+"F1.wireOp",EDGE,"E217"),sQuery(id+"F1.wireOp",EDGE,"E218"),sQuery(id+"F1.wireOp",EDGE,"E219"),sQuery(id+"F1.wireOp",EDGE,"E220"),sQuery(id+"F1.wireOp",EDGE,"E221"),sQuery(id+"F1.wireOp",EDGE,"E222"),sQuery(id+"F1.wireOp",EDGE,"E223"),sQuery(id+"F1.wireOp",EDGE,"E224"),sQuery(id+"F1.wireOp",EDGE,"E225"),sQuery(id+"F1.wireOp",EDGE,"E226"),sQuery(id+"F1.wireOp",EDGE,"E227"),sQuery(id+"F1.wireOp",EDGE,"E228"),sQuery(id+"F1.wireOp",EDGE,"E229"),sQuery(id+"F1.wireOp",EDGE,"E230"),sQuery(id+"F1.wireOp",EDGE,"E231"),sQuery(id+"F1.wireOp",EDGE,"E232"),sQuery(id+"F1.wireOp",EDGE,"E233"),sQuery(id+"F1.wireOp",EDGE,"E234"),sQuery(id+"F1.wireOp",EDGE,"E235"),sQuery(id+"F1.wireOp",EDGE,"E236"),sQuery(id+"F1.wireOp",EDGE,"E237"),sQuery(id+"F1.wireOp",EDGE,"E238"),sQuery(id+"F1.wireOp",EDGE,"E239"),sQuery(id+"F1.wireOp",EDGE,"E240"),sQuery(id+"F1.wireOp",EDGE,"E241"),sQuery(id+"F1.wireOp",EDGE,"E242"),sQuery(id+"F1.wireOp",EDGE,"E243"),sQuery(id+"F1.wireOp",EDGE,"E244"),sQuery(id+"F1.wireOp",EDGE,"E245"),sQuery(id+"F1.wireOp",EDGE,"E246"),sQuery(id+"F1.wireOp",EDGE,"E247"),sQuery(id+"F1.wireOp",EDGE,"E248"),sQuery(id+"F1.wireOp",EDGE,"E249"),sQuery(id+"F1.wireOp",EDGE,"E250"),sQuery(id+"F1.wireOp",EDGE,"E251"),sQuery(id+"F1.wireOp",EDGE,"E252"),sQuery(id+"F1.wireOp",EDGE,"E253"),sQuery(id+"F1.wireOp",EDGE,"E254"),sQuery(id+"F1.wireOp",EDGE,"E255"),sQuery(id+"F1.wireOp",EDGE,"E256"),sQuery(id+"F1.wireOp",EDGE,"E257"),sQuery(id+"F1.wireOp",EDGE,"E258"),sQuery(id+"F1.wireOp",EDGE,"E259"),sQuery(id+"F1.wireOp",EDGE,"E260"),sQuery(id+"F1.wireOp",EDGE,"E261"),sQuery(id+"F1.wireOp",EDGE,"E262"),sQuery(id+"F1.wireOp",EDGE,"E263"),sQuery(id+"F1.wireOp",EDGE,"E264"),sQuery(id+"F1.wireOp",EDGE,"E265"),sQuery(id+"F1.wireOp",EDGE,"E266"),sQuery(id+"F1.wireOp",EDGE,"E267"),sQuery(id+"F1.wireOp",EDGE,"E268"),sQuery(id+"F1.wireOp",EDGE,"E269"),sQuery(id+"F1.wireOp",EDGE,"E270"),sQuery(id+"F1.wireOp",EDGE,"E271"),sQuery(id+"F1.wireOp",EDGE,"E272"),sQuery(id+"F1.wireOp",EDGE,"E273"),sQuery(id+"F1.wireOp",EDGE,"E274"),sQuery(id+"F1.wireOp",EDGE,"E275"),sQuery(id+"F1.wireOp",EDGE,"E276"),sQuery(id+"F1.wireOp",EDGE,"E277"),sQuery(id+"F1.wireOp",EDGE,"E278"),sQuery(id+"F1.wireOp",EDGE,"E279"),sQuery(id+"F1.wireOp",EDGE,"E280"),sQuery(id+"F1.wireOp",EDGE,"E281"),sQuery(id+"F1.wireOp",EDGE,"E282"),sQuery(id+"F1.wireOp",EDGE,"E283"),sQuery(id+"F1.wireOp",EDGE,"E284"),sQuery(id+"F1.wireOp",EDGE,"E285"),sQuery(id+"F1.wireOp",EDGE,"E286"),sQuery(id+"F1.wireOp",EDGE,"E287"),sQuery(id+"F1.wireOp",EDGE,"E288"),sQuery(id+"F1.wireOp",EDGE,"E289"),sQuery(id+"F1.wireOp",EDGE,"E290"),sQuery(id+"F1.wireOp",EDGE,"E291"),sQuery(id+"F1.wireOp",EDGE,"E292"),sQuery(id+"F1.wireOp",EDGE,"E293"),sQuery(id+"F1.wireOp",EDGE,"E294"),sQuery(id+"F1.wireOp",EDGE,"E295"),sQuery(id+"F1.wireOp",EDGE,"E296"),sQuery(id+"F1.wireOp",EDGE,"E297"),sQuery(id+"F1.wireOp",EDGE,"E298"),sQuery(id+"F1.wireOp",EDGE,"E299"),sQuery(id+"F1.wireOp",EDGE,"E300"),sQuery(id+"F1.wireOp",EDGE,"E301"),sQuery(id+"F1.wireOp",EDGE,"E302"),sQuery(id+"F1.wireOp",EDGE,"E303"),sQuery(id+"F1.wireOp",EDGE,"E304"),sQuery(id+"F1.wireOp",EDGE,"E305"),sQuery(id+"F1.wireOp",EDGE,"E306"),sQuery(id+"F1.wireOp",EDGE,"E307"),sQuery(id+"F1.wireOp",EDGE,"E308"),sQuery(id+"F1.wireOp",EDGE,"E309"),sQuery(id+"F1.wireOp",EDGE,"E310"),sQuery(id+"F1.wireOp",EDGE,"E311"),sQuery(id+"F1.wireOp",EDGE,"E312"),sQuery(id+"F1.wireOp",EDGE,"E313"),sQuery(id+"F1.wireOp",EDGE,"E314"),sQuery(id+"F1.wireOp",EDGE,"E315"),sQuery(id+"F1.wireOp",EDGE,"E316"),sQuery(id+"F1.wireOp",EDGE,"E317"),sQuery(id+"F1.wireOp",EDGE,"E318"),sQuery(id+"F1.wireOp",EDGE,"E319"),sQuery(id+"F1.wireOp",EDGE,"E320"),sQuery(id+"F1.wireOp",EDGE,"E321"),sQuery(id+"F1.wireOp",EDGE,"E322"),sQuery(id+"F1.wireOp",EDGE,"E323"),sQuery(id+"F1.wireOp",EDGE,"E324"),sQuery(id+"F1.wireOp",EDGE,"E325"),sQuery(id+"F1.wireOp",EDGE,"E326"),sQuery(id+"F1.wireOp",EDGE,"E327"),sQuery(id+"F1.wireOp",EDGE,"E328"),sQuery(id+"F1.wireOp",EDGE,"E329"),sQuery(id+"F1.wireOp",EDGE,"E330"),sQuery(id+"F1.wireOp",EDGE,"E331"),sQuery(id+"F1.wireOp",EDGE,"E332"),sQuery(id+"F1.wireOp",EDGE,"E333"),sQuery(id+"F1.wireOp",EDGE,"E334"),sQuery(id+"F1.wireOp",EDGE,"E334"),sQuery(id+"F1.wireOp",EDGE,"E335"),sQuery(id+"F1.wireOp",EDGE,"E336"),sQuery(id+"F1.wireOp",EDGE,"E337"),sQuery(id+"F1.wireOp",EDGE,"E338"),sQuery(id+"F1.wireOp",EDGE,"E339"),sQuery(id+"F1.wireOp",EDGE,"E340"),sQuery(id+"F1.wireOp",EDGE,"E341"),sQuery(id+"F1.wireOp",EDGE,"E342"),sQuery(id+"F1.wireOp",EDGE,"E343"),sQuery(id+"F1.wireOp",EDGE,"E344"),sQuery(id+"F1.wireOp",EDGE,"E345"),sQuery(id+"F1.wireOp",EDGE,"E346"),sQuery(id+"F1.wireOp",EDGE,"E347"),sQuery(id+"F1.wireOp",EDGE,"E348"),sQuery(id+"F1.wireOp",EDGE,"E349"),sQuery(id+"F1.wireOp",EDGE,"E350"),sQuery(id+"F1.wireOp",EDGE,"E351"),sQuery(id+"F1.wireOp",EDGE,"E352"),sQuery(id+"F1.wireOp",EDGE,"E353"),sQuery(id+"F1.wireOp",EDGE,"E354"),sQuery(id+"F1.wireOp",EDGE,"E355"),sQuery(id+"F1.wireOp",EDGE,"E356"),sQuery(id+"F1.wireOp",EDGE,"E357"),sQuery(id+"F1.wireOp",EDGE,"E358"),sQuery(id+"F1.wireOp",EDGE,"E359"),sQuery(id+"F1.wireOp",EDGE,"E360"),sQuery(id+"F1.wireOp",EDGE,"E361"),sQuery(id+"F1.wireOp",EDGE,"E362"),sQuery(id+"F1.wireOp",EDGE,"E363"),sQuery(id+"F1.wireOp",EDGE,"E364"),sQuery(id+"F1.wireOp",EDGE,"E365"),sQuery(id+"F1.wireOp",EDGE,"E366"),sQuery(id+"F1.wireOp",EDGE,"E367"),sQuery(id+"F1.wireOp",EDGE,"E368"),sQuery(id+"F1.wireOp",EDGE,"E369"),sQuery(id+"F1.wireOp",EDGE,"E370"),sQuery(id+"F1.wireOp",EDGE,"E371"),sQuery(id+"F1.wireOp",EDGE,"E372"),sQuery(id+"F1.wireOp",EDGE,"E373"),sQuery(id+"F1.wireOp",EDGE,"E374"),sQuery(id+"F1.wireOp",EDGE,"E375"),sQuery(id+"F1.wireOp",EDGE,"E376"),sQuery(id+"F1.wireOp",EDGE,"E377"),sQuery(id+"F1.wireOp",EDGE,"E378"),sQuery(id+"F1.wireOp",EDGE,"E379"),sQuery(id+"F1.wireOp",EDGE,"E380"),sQuery(id+"F1.wireOp",EDGE,"E381"),sQuery(id+"F1.wireOp",EDGE,"E382"),sQuery(id+"F1.wireOp",EDGE,"E383"),sQuery(id+"F1.wireOp",EDGE,"E384"),sQuery(id+"F1.wireOp",EDGE,"E385"),sQuery(id+"F1.wireOp",EDGE,"E386"),sQuery(id+"F1.wireOp",EDGE,"E387"),sQuery(id+"F1.wireOp",EDGE,"E388"),sQuery(id+"F1.wireOp",EDGE,"E389"),sQuery(id+"F1.wireOp",EDGE,"E390"),sQuery(id+"F1.wireOp",EDGE,"E391"),sQuery(id+"F1.wireOp",EDGE,"E392"),sQuery(id+"F1.wireOp",EDGE,"E393"),sQuery(id+"F1.wireOp",EDGE,"E394"),sQuery(id+"F1.wireOp",EDGE,"E395"),sQuery(id+"F1.wireOp",EDGE,"E396"),sQuery(id+"F1.wireOp",EDGE,"E397"),sQuery(id+"F1.wireOp",EDGE,"E398"),sQuery(id+"F1.wireOp",EDGE,"E399"),sQuery(id+"F1.wireOp",EDGE,"E400"),sQuery(id+"F1.wireOp",EDGE,"E401"),sQuery(id+"F1.wireOp",EDGE,"E402"),sQuery(id+"F1.wireOp",EDGE,"E403"),sQuery(id+"F1.wireOp",EDGE,"E404"),sQuery(id+"F1.wireOp",EDGE,"E405"),sQuery(id+"F1.wireOp",EDGE,"E406"),sQuery(id+"F1.wireOp",EDGE,"E407"),sQuery(id+"F1.wireOp",EDGE,"E408"),sQuery(id+"F1.wireOp",EDGE,"E409"),sQuery(id+"F1.wireOp",EDGE,"E410"),sQuery(id+"F1.wireOp",EDGE,"E411"),sQuery(id+"F1.wireOp",EDGE,"E412"),sQuery(id+"F1.wireOp",EDGE,"E413"),sQuery(id+"F1.wireOp",EDGE,"E414"),sQuery(id+"F1.wireOp",EDGE,"E415"),sQuery(id+"F1.wireOp",EDGE,"E416"),sQuery(id+"F1.wireOp",EDGE,"E417"),sQuery(id+"F1.wireOp",EDGE,"E418"),sQuery(id+"F1.wireOp",EDGE,"E419"),sQuery(id+"F1.wireOp",EDGE,"E420"),sQuery(id+"F1.wireOp",EDGE,"E421"),sQuery(id+"F1.wireOp",EDGE,"E422"),sQuery(id+"F1.wireOp",EDGE,"E423"),sQuery(id+"F1.wireOp",EDGE,"E424"),sQuery(id+"F1.wireOp",EDGE,"E425"),sQuery(id+"F1.wireOp",EDGE,"E426"),sQuery(id+"F1.wireOp",EDGE,"E426"),sQuery(id+"F1.wireOp",EDGE,"E427"),sQuery(id+"F1.wireOp",EDGE,"E428"),sQuery(id+"F1.wireOp",EDGE,"E429"),sQuery(id+"F1.wireOp",EDGE,"E430"),sQuery(id+"F1.wireOp",EDGE,"E431"),sQuery(id+"F1.wireOp",EDGE,"E432"),sQuery(id+"F1.wireOp",EDGE,"E433"),sQuery(id+"F1.wireOp",EDGE,"E434"),sQuery(id+"F1.wireOp",EDGE,"E435"),sQuery(id+"F1.wireOp",EDGE,"E435"),sQuery(id+"F1.wireOp",EDGE,"E436"),sQuery(id+"F1.wireOp",EDGE,"E437"),sQuery(id+"F1.wireOp",EDGE,"E438"),sQuery(id+"F1.wireOp",EDGE,"E439"),sQuery(id+"F1.wireOp",EDGE,"E440"),sQuery(id+"F1.wireOp",EDGE,"E441"),sQuery(id+"F1.wireOp",EDGE,"E442"),sQuery(id+"F1.wireOp",EDGE,"E443"),sQuery(id+"F1.wireOp",EDGE,"E444"),sQuery(id+"F1.wireOp",EDGE,"E445"),sQuery(id+"F1.wireOp",EDGE,"E446"),sQuery(id+"F1.wireOp",EDGE,"E447"),sQuery(id+"F1.wireOp",EDGE,"E448"),sQuery(id+"F1.wireOp",EDGE,"E449"),sQuery(id+"F1.wireOp",EDGE,"E450"),sQuery(id+"F1.wireOp",EDGE,"E451"),sQuery(id+"F1.wireOp",EDGE,"E452"),sQuery(id+"F1.wireOp",EDGE,"E453"),sQuery(id+"F1.wireOp",EDGE,"E454"),sQuery(id+"F1.wireOp",EDGE,"E455"),sQuery(id+"F1.wireOp",EDGE,"E456"),sQuery(id+"F1.wireOp",EDGE,"E457"),sQuery(id+"F1.wireOp",EDGE,"E458"),sQuery(id+"F1.wireOp",EDGE,"E459"),sQuery(id+"F1.wireOp",EDGE,"E460"),sQuery(id+"F1.wireOp",EDGE,"E461"),sQuery(id+"F1.wireOp",EDGE,"E462"),sQuery(id+"F1.wireOp",EDGE,"E463"),sQuery(id+"F1.wireOp",EDGE,"E464"),sQuery(id+"F1.wireOp",EDGE,"E465"),sQuery(id+"F1.wireOp",EDGE,"E466"),sQuery(id+"F1.wireOp",EDGE,"E467"),sQuery(id+"F1.wireOp",EDGE,"E468"),sQuery(id+"F1.wireOp",EDGE,"E469"),sQuery(id+"F1.wireOp",EDGE,"E470"),sQuery(id+"F1.wireOp",EDGE,"E471"),sQuery(id+"F1.wireOp",EDGE,"E472"),sQuery(id+"F1.wireOp",EDGE,"E473"),sQuery(id+"F1.wireOp",EDGE,"E474"),sQuery(id+"F1.wireOp",EDGE,"E475"),sQuery(id+"F1.wireOp",EDGE,"E476"),sQuery(id+"F1.wireOp",EDGE,"E477"),sQuery(id+"F1.wireOp",EDGE,"E478"),sQuery(id+"F1.wireOp",EDGE,"E479"),sQuery(id+"F1.wireOp",EDGE,"E480"),sQuery(id+"F1.wireOp",EDGE,"E481"),sQuery(id+"F1.wireOp",EDGE,"E482"),sQuery(id+"F1.wireOp",EDGE,"E483"),sQuery(id+"F1.wireOp",EDGE,"E484"),sQuery(id+"F1.wireOp",EDGE,"E485"),sQuery(id+"F1.wireOp",EDGE,"E486"),sQuery(id+"F1.wireOp",EDGE,"E487"),sQuery(id+"F1.wireOp",EDGE,"E488"),sQuery(id+"F1.wireOp",EDGE,"E489"),sQuery(id+"F1.wireOp",EDGE,"E490"),sQuery(id+"F1.wireOp",EDGE,"E491"),sQuery(id+"F1.wireOp",EDGE,"E492"),sQuery(id+"F1.wireOp",EDGE,"E493"),sQuery(id+"F1.wireOp",EDGE,"E494"),sQuery(id+"F1.wireOp",EDGE,"E495"),sQuery(id+"F1.wireOp",EDGE,"E496"),sQuery(id+"F1.wireOp",EDGE,"E497"),sQuery(id+"F1.wireOp",EDGE,"E498"),sQuery(id+"F1.wireOp",EDGE,"E499"),sQuery(id+"F1.wireOp",EDGE,"E500"),sQuery(id+"F1.wireOp",EDGE,"E501"),sQuery(id+"F1.wireOp",EDGE,"E502"),sQuery(id+"F1.wireOp",EDGE,"E503"),sQuery(id+"F1.wireOp",EDGE,"E504"),sQuery(id+"F1.wireOp",EDGE,"E505"),sQuery(id+"F1.wireOp",EDGE,"E506"),sQuery(id+"F1.wireOp",EDGE,"E507"),sQuery(id+"F1.wireOp",EDGE,"E508"),sQuery(id+"F1.wireOp",EDGE,"E509"),sQuery(id+"F1.wireOp",EDGE,"E510"),sQuery(id+"F1.wireOp",EDGE,"E511"),sQuery(id+"F1.wireOp",EDGE,"E512"),sQuery(id+"F1.wireOp",EDGE,"E513"),sQuery(id+"F1.wireOp",EDGE,"E514"),sQuery(id+"F1.wireOp",EDGE,"E515"),sQuery(id+"F1.wireOp",EDGE,"E516"),sQuery(id+"F1.wireOp",EDGE,"E517"),sQuery(id+"F1.wireOp",EDGE,"E518"),sQuery(id+"F1.wireOp",EDGE,"E519"),sQuery(id+"F1.wireOp",EDGE,"E520"),sQuery(id+"F1.wireOp",EDGE,"E521"),sQuery(id+"F1.wireOp",EDGE,"E522"),sQuery(id+"F1.wireOp",EDGE,"E523"),sQuery(id+"F1.wireOp",EDGE,"E524"),sQuery(id+"F1.wireOp",EDGE,"E525"),sQuery(id+"F1.wireOp",EDGE,"E526"),sQuery(id+"F1.wireOp",EDGE,"E527"),sQuery(id+"F1.wireOp",EDGE,"E528"),sQuery(id+"F1.wireOp",EDGE,"E529"),sQuery(id+"F1.wireOp",EDGE,"E530"),sQuery(id+"F1.wireOp",EDGE,"E531"),sQuery(id+"F1.wireOp",EDGE,"E532"),sQuery(id+"F1.wireOp",EDGE,"E533"),sQuery(id+"F1.wireOp",EDGE,"E534"),sQuery(id+"F1.wireOp",EDGE,"E534"),sQuery(id+"F1.wireOp",EDGE,"E535"),sQuery(id+"F1.wireOp",EDGE,"E536"),sQuery(id+"F1.wireOp",EDGE,"E537"),sQuery(id+"F1.wireOp",EDGE,"E538"),sQuery(id+"F1.wireOp",EDGE,"E539"),sQuery(id+"F1.wireOp",EDGE,"E540"),sQuery(id+"F1.wireOp",EDGE,"E541"),sQuery(id+"F1.wireOp",EDGE,"E542"),sQuery(id+"F1.wireOp",EDGE,"E543"),sQuery(id+"F1.wireOp",EDGE,"E544"),sQuery(id+"F1.wireOp",EDGE,"E545"),sQuery(id+"F1.wireOp",EDGE,"E546"),sQuery(id+"F1.wireOp",EDGE,"E547"),sQuery(id+"F1.wireOp",EDGE,"E548"),sQuery(id+"F1.wireOp",EDGE,"E549"),sQuery(id+"F1.wireOp",EDGE,"E550"),sQuery(id+"F1.wireOp",EDGE,"E551"),sQuery(id+"F1.wireOp",EDGE,"E552"),sQuery(id+"F1.wireOp",EDGE,"E553"),sQuery(id+"F1.wireOp",EDGE,"E554"),sQuery(id+"F1.wireOp",EDGE,"E555"),sQuery(id+"F1.wireOp",EDGE,"E556"),sQuery(id+"F1.wireOp",EDGE,"E557"),sQuery(id+"F1.wireOp",EDGE,"E558"),sQuery(id+"F1.wireOp",EDGE,"E559"),sQuery(id+"F1.wireOp",EDGE,"E560"),sQuery(id+"F1.wireOp",EDGE,"E561"),sQuery(id+"F1.wireOp",EDGE,"E562"),sQuery(id+"F1.wireOp",EDGE,"E563"),sQuery(id+"F1.wireOp",EDGE,"E564"),sQuery(id+"F1.wireOp",EDGE,"E565"),sQuery(id+"F1.wireOp",EDGE,"E566"),sQuery(id+"F1.wireOp",EDGE,"E567"),sQuery(id+"F1.wireOp",EDGE,"E568"),sQuery(id+"F1.wireOp",EDGE,"E569"),sQuery(id+"F1.wireOp",EDGE,"E570"),sQuery(id+"F1.wireOp",EDGE,"E571"),sQuery(id+"F1.wireOp",EDGE,"E572"),sQuery(id+"F1.wireOp",EDGE,"E573"),sQuery(id+"F1.wireOp",EDGE,"E574"),sQuery(id+"F1.wireOp",EDGE,"E575"),sQuery(id+"F1.wireOp",EDGE,"E576"),sQuery(id+"F1.wireOp",EDGE,"E577"),sQuery(id+"F1.wireOp",EDGE,"E578"),sQuery(id+"F1.wireOp",EDGE,"E579"),sQuery(id+"F1.wireOp",EDGE,"E580"),sQuery(id+"F1.wireOp",EDGE,"E581"),sQuery(id+"F1.wireOp",EDGE,"E582"),sQuery(id+"F1.wireOp",EDGE,"E583"),sQuery(id+"F1.wireOp",EDGE,"E584"),sQuery(id+"F1.wireOp",EDGE,"E585"),sQuery(id+"F1.wireOp",EDGE,"E586"),sQuery(id+"F1.wireOp",EDGE,"E587"),sQuery(id+"F1.wireOp",EDGE,"E588"),sQuery(id+"F1.wireOp",EDGE,"E589"),sQuery(id+"F1.wireOp",EDGE,"E590"),sQuery(id+"F1.wireOp",EDGE,"E591"),sQuery(id+"F1.wireOp",EDGE,"E592"),sQuery(id+"F1.wireOp",EDGE,"E593"),sQuery(id+"F1.wireOp",EDGE,"E594"),sQuery(id+"F1.wireOp",EDGE,"E595"),sQuery(id+"F1.wireOp",EDGE,"E596"),sQuery(id+"F1.wireOp",EDGE,"E597"),sQuery(id+"F1.wireOp",EDGE,"E598"),sQuery(id+"F1.wireOp",EDGE,"E599"),sQuery(id+"F1.wireOp",EDGE,"E600"),sQuery(id+"F1.wireOp",EDGE,"E601"),sQuery(id+"F1.wireOp",EDGE,"E602"),sQuery(id+"F1.wireOp",EDGE,"E603"),sQuery(id+"F1.wireOp",EDGE,"E604"),sQuery(id+"F1.wireOp",EDGE,"E605"),sQuery(id+"F1.wireOp",EDGE,"E606"),sQuery(id+"F1.wireOp",EDGE,"E607"),sQuery(id+"F1.wireOp",EDGE,"E608"),sQuery(id+"F1.wireOp",EDGE,"E609"),sQuery(id+"F1.wireOp",EDGE,"E610"),sQuery(id+"F1.wireOp",EDGE,"E611"),sQuery(id+"F1.wireOp",EDGE,"E612"),sQuery(id+"F1.wireOp",EDGE,"E613"),sQuery(id+"F1.wireOp",EDGE,"E614"),sQuery(id+"F1.wireOp",EDGE,"E615"),sQuery(id+"F1.wireOp",EDGE,"E616"),sQuery(id+"F1.wireOp",EDGE,"E617"),sQuery(id+"F1.wireOp",EDGE,"E618"),sQuery(id+"F1.wireOp",EDGE,"E619"),sQuery(id+"F1.wireOp",EDGE,"E620"),sQuery(id+"F1.wireOp",EDGE,"E621"),sQuery(id+"F1.wireOp",EDGE,"E622"),sQuery(id+"F1.wireOp",EDGE,"E623"),sQuery(id+"F1.wireOp",EDGE,"E624"),sQuery(id+"F1.wireOp",EDGE,"E625"),sQuery(id+"F1.wireOp",EDGE,"E626"),sQuery(id+"F1.wireOp",EDGE,"E627"),sQuery(id+"F1.wireOp",EDGE,"E628"),sQuery(id+"F1.wireOp",EDGE,"E629"),sQuery(id+"F1.wireOp",EDGE,"E630"),sQuery(id+"F1.wireOp",EDGE,"E631"),sQuery(id+"F1.wireOp",EDGE,"E632"),sQuery(id+"F1.wireOp",EDGE,"E633"),sQuery(id+"F1.wireOp",EDGE,"E634"),sQuery(id+"F1.wireOp",EDGE,"E635"),sQuery(id+"F1.wireOp",EDGE,"E636"),sQuery(id+"F1.wireOp",EDGE,"E637"),sQuery(id+"F1.wireOp",EDGE,"E638"),sQuery(id+"F1.wireOp",EDGE,"E639"),sQuery(id+"F1.wireOp",EDGE,"E640"),sQuery(id+"F1.wireOp",EDGE,"E641"),sQuery(id+"F1.wireOp",EDGE,"E642"),sQuery(id+"F1.wireOp",EDGE,"E643"),sQuery(id+"F1.wireOp",EDGE,"E644"),sQuery(id+"F1.wireOp",EDGE,"E645"),sQuery(id+"F1.wireOp",EDGE,"E646"),sQuery(id+"F1.wireOp",EDGE,"E647"),sQuery(id+"F1.wireOp",EDGE,"E648"),sQuery(id+"F1.wireOp",EDGE,"E649"),sQuery(id+"F1.wireOp",EDGE,"E650"),sQuery(id+"F1.wireOp",EDGE,"E651"),sQuery(id+"F1.wireOp",EDGE,"E652"),sQuery(id+"F1.wireOp",EDGE,"E653"),sQuery(id+"F1.wireOp",EDGE,"E654"),sQuery(id+"F1.wireOp",EDGE,"E655"),sQuery(id+"F1.wireOp",EDGE,"E656"),sQuery(id+"F1.wireOp",EDGE,"E657"),sQuery(id+"F1.wireOp",EDGE,"E658"),sQuery(id+"F1.wireOp",EDGE,"E659"),sQuery(id+"F1.wireOp",EDGE,"E660"),sQuery(id+"F1.wireOp",EDGE,"E661"),sQuery(id+"F1.wireOp",EDGE,"E662"),sQuery(id+"F1.wireOp",EDGE,"E663"),sQuery(id+"F1.wireOp",EDGE,"E664"),sQuery(id+"F1.wireOp",EDGE,"E665"),sQuery(id+"F1.wireOp",EDGE,"E666"),sQuery(id+"F1.wireOp",EDGE,"E667"),sQuery(id+"F1.wireOp",EDGE,"E668"),sQuery(id+"F1.wireOp",EDGE,"E669"),sQuery(id+"F1.wireOp",EDGE,"E670"),sQuery(id+"F1.wireOp",EDGE,"E671"),sQuery(id+"F1.wireOp",EDGE,"E672"),sQuery(id+"F1.wireOp",EDGE,"E673"),sQuery(id+"F1.wireOp",EDGE,"E674"),sQuery(id+"F1.wireOp",EDGE,"E675"),sQuery(id+"F1.wireOp",EDGE,"E676"),sQuery(id+"F1.wireOp",EDGE,"E677"),sQuery(id+"F1.wireOp",EDGE,"E678"),sQuery(id+"F1.wireOp",EDGE,"E679"),sQuery(id+"F1.wireOp",EDGE,"E680"),sQuery(id+"F1.wireOp",EDGE,"E681"),sQuery(id+"F1.wireOp",EDGE,"E682"),sQuery(id+"F1.wireOp",EDGE,"E683"),sQuery(id+"F1.wireOp",EDGE,"E684"),sQuery(id+"F1.wireOp",EDGE,"E685"),sQuery(id+"F1.wireOp",EDGE,"E686"),sQuery(id+"F1.wireOp",EDGE,"E687"),sQuery(id+"F1.wireOp",EDGE,"E688"),sQuery(id+"F1.wireOp",EDGE,"E689"),sQuery(id+"F1.wireOp",EDGE,"E690"),sQuery(id+"F1.wireOp",EDGE,"E691"),sQuery(id+"F1.wireOp",EDGE,"E692"),sQuery(id+"F1.wireOp",EDGE,"E693"),sQuery(id+"F1.wireOp",EDGE,"E694"),sQuery(id+"F1.wireOp",EDGE,"E695"),sQuery(id+"F1.wireOp",EDGE,"E696"),sQuery(id+"F1.wireOp",EDGE,"E697"),sQuery(id+"F1.wireOp",EDGE,"E698"),sQuery(id+"F1.wireOp",EDGE,"E699"),sQuery(id+"F1.wireOp",EDGE,"E700"),sQuery(id+"F1.wireOp",EDGE,"E701"),sQuery(id+"F1.wireOp",EDGE,"E702"),sQuery(id+"F1.wireOp",EDGE,"E703"),sQuery(id+"F1.wireOp",EDGE,"E704"),sQuery(id+"F1.wireOp",EDGE,"E705"),sQuery(id+"F1.wireOp",EDGE,"E706"),sQuery(id+"F1.wireOp",EDGE,"E707"),sQuery(id+"F1.wireOp",EDGE,"E708"),sQuery(id+"F1.wireOp",EDGE,"E709"),sQuery(id+"F1.wireOp",EDGE,"E710"),sQuery(id+"F1.wireOp",EDGE,"E711"),sQuery(id+"F1.wireOp",EDGE,"E712"),sQuery(id+"F1.wireOp",EDGE,"E713"),sQuery(id+"F1.wireOp",EDGE,"E714"),sQuery(id+"F1.wireOp",EDGE,"E715"),sQuery(id+"F1.wireOp",EDGE,"E716"),sQuery(id+"F1.wireOp",EDGE,"E717"),sQuery(id+"F1.wireOp",EDGE,"E718"),sQuery(id+"F1.wireOp",EDGE,"E719"),sQuery(id+"F1.wireOp",EDGE,"E720"),sQuery(id+"F1.wireOp",EDGE,"E721"),sQuery(id+"F1.wireOp",EDGE,"E722"),sQuery(id+"F1.wireOp",EDGE,"E723"),sQuery(id+"F1.wireOp",EDGE,"E724"),sQuery(id+"F1.wireOp",EDGE,"E725"),sQuery(id+"F1.wireOp",EDGE,"E726"),sQuery(id+"F1.wireOp",EDGE,"E727"),sQuery(id+"F1.wireOp",EDGE,"E728"),sQuery(id+"F1.wireOp",EDGE,"E729"),sQuery(id+"F1.wireOp",EDGE,"E730"),sQuery(id+"F1.wireOp",EDGE,"E731"),sQuery(id+"F1.wireOp",EDGE,"E732"),sQuery(id+"F1.wireOp",EDGE,"E733"),sQuery(id+"F1.wireOp",EDGE,"E734"),sQuery(id+"F1.wireOp",EDGE,"E735"),sQuery(id+"F1.wireOp",EDGE,"E736"),sQuery(id+"F1.wireOp",EDGE,"E737"),sQuery(id+"F1.wireOp",EDGE,"E738"),sQuery(id+"F1.wireOp",EDGE,"E739"),sQuery(id+"F1.wireOp",EDGE,"E740"),sQuery(id+"F1.wireOp",EDGE,"E741"),sQuery(id+"F1.wireOp",EDGE,"E742"),sQuery(id+"F1.wireOp",EDGE,"E743"),sQuery(id+"F1.wireOp",EDGE,"E744"),sQuery(id+"F1.wireOp",EDGE,"E745"),sQuery(id+"F1.wireOp",EDGE,"E746"),sQuery(id+"F1.wireOp",EDGE,"E747"),sQuery(id+"F1.wireOp",EDGE,"E748"),sQuery(id+"F1.wireOp",EDGE,"E749"),sQuery(id+"F1.wireOp",EDGE,"E750"),sQuery(id+"F1.wireOp",EDGE,"E751"),sQuery(id+"F1.wireOp",EDGE,"E752"),sQuery(id+"F1.wireOp",EDGE,"E753"),sQuery(id+"F1.wireOp",EDGE,"E754"),sQuery(id+"F1.wireOp",EDGE,"E755"),sQuery(id+"F1.wireOp",EDGE,"E756"),sQuery(id+"F1.wireOp",EDGE,"E757"),sQuery(id+"F1.wireOp",EDGE,"E758"),sQuery(id+"F1.wireOp",EDGE,"E759"),sQuery(id+"F1.wireOp",EDGE,"E760"),sQuery(id+"F1.wireOp",EDGE,"E761"),sQuery(id+"F1.wireOp",EDGE,"E762"),sQuery(id+"F1.wireOp",EDGE,"E763"),sQuery(id+"F1.wireOp",EDGE,"E764"),sQuery(id+"F1.wireOp",EDGE,"E765"),sQuery(id+"F1.wireOp",EDGE,"E766"),sQuery(id+"F1.wireOp",EDGE,"E767"),sQuery(id+"F1.wireOp",EDGE,"E768"),sQuery(id+"F1.wireOp",EDGE,"E769"),sQuery(id+"F1.wireOp",EDGE,"E770"),sQuery(id+"F1.wireOp",EDGE,"E771"),sQuery(id+"F1.wireOp",EDGE,"E772"),sQuery(id+"F1.wireOp",EDGE,"E773"),sQuery(id+"F1.wireOp",EDGE,"E774"),sQuery(id+"F1.wireOp",EDGE,"E775"),sQuery(id+"F1.wireOp",EDGE,"E776"),sQuery(id+"F1.wireOp",EDGE,"E777"),sQuery(id+"F1.wireOp",EDGE,"E778"),sQuery(id+"F1.wireOp",EDGE,"E779"),sQuery(id+"F1.wireOp",EDGE,"E780"),sQuery(id+"F1.wireOp",EDGE,"E781"),sQuery(id+"F1.wireOp",EDGE,"E782"),sQuery(id+"F1.wireOp",EDGE,"E783"),sQuery(id+"F1.wireOp",EDGE,"E784"),sQuery(id+"F1.wireOp",EDGE,"E785"),sQuery(id+"F1.wireOp",EDGE,"E786"),sQuery(id+"F1.wireOp",EDGE,"E787"),sQuery(id+"F1.wireOp",EDGE,"E788"),sQuery(id+"F1.wireOp",EDGE,"E789"),sQuery(id+"F1.wireOp",EDGE,"E790"),sQuery(id+"F1.wireOp",EDGE,"E791"),sQuery(id+"F1.wireOp",EDGE,"E792"),sQuery(id+"F1.wireOp",EDGE,"E793"),sQuery(id+"F1.wireOp",EDGE,"E794"),sQuery(id+"F1.wireOp",EDGE,"E795"),sQuery(id+"F1.wireOp",EDGE,"E796"),sQuery(id+"F1.wireOp",EDGE,"E797"),sQuery(id+"F1.wireOp",EDGE,"E798"),sQuery(id+"F1.wireOp",EDGE,"E799"),sQuery(id+"F1.wireOp",EDGE,"E800"),sQuery(id+"F1.wireOp",EDGE,"E801"),sQuery(id+"F1.wireOp",EDGE,"E802"),sQuery(id+"F1.wireOp",EDGE,"E803"),sQuery(id+"F1.wireOp",EDGE,"E804"),sQuery(id+"F1.wireOp",EDGE,"E805"),sQuery(id+"F1.wireOp",EDGE,"E806"),sQuery(id+"F1.wireOp",EDGE,"E807"),sQuery(id+"F1.wireOp",EDGE,"E808"),sQuery(id+"F1.wireOp",EDGE,"E809"),sQuery(id+"F1.wireOp",EDGE,"E810"),sQuery(id+"F1.wireOp",EDGE,"E811"),sQuery(id+"F1.wireOp",EDGE,"E812"),sQuery(id+"F1.wireOp",EDGE,"E813"),sQuery(id+"F1.wireOp",EDGE,"E814"),sQuery(id+"F1.wireOp",EDGE,"E815"),sQuery(id+"F1.wireOp",EDGE,"E816"),sQuery(id+"F1.wireOp",EDGE,"E817"),sQuery(id+"F1.wireOp",EDGE,"E818"),sQuery(id+"F1.wireOp",EDGE,"E819"),sQuery(id+"F1.wireOp",EDGE,"E820"),sQuery(id+"F1.wireOp",EDGE,"E821"),sQuery(id+"F1.wireOp",EDGE,"E822"),sQuery(id+"F1.wireOp",EDGE,"E823"),sQuery(id+"F1.wireOp",EDGE,"E824"),sQuery(id+"F1.wireOp",EDGE,"E825"),sQuery(id+"F1.wireOp",EDGE,"E826"),sQuery(id+"F1.wireOp",EDGE,"E827"),sQuery(id+"F1.wireOp",EDGE,"E828"),sQuery(id+"F1.wireOp",EDGE,"E829"),sQuery(id+"F1.wireOp",EDGE,"E830"),sQuery(id+"F1.wireOp",EDGE,"E831"),sQuery(id+"F1.wireOp",EDGE,"E832"),sQuery(id+"F1.wireOp",EDGE,"E833"),sQuery(id+"F1.wireOp",EDGE,"E834"),sQuery(id+"F1.wireOp",EDGE,"E835"),sQuery(id+"F1.wireOp",EDGE,"E836"),sQuery(id+"F1.wireOp",EDGE,"E837"),sQuery(id+"F1.wireOp",EDGE,"E838"),sQuery(id+"F1.wireOp",EDGE,"E839"),sQuery(id+"F1.wireOp",EDGE,"E840"),sQuery(id+"F1.wireOp",EDGE,"E841"),sQuery(id+"F1.wireOp",EDGE,"E842"),sQuery(id+"F1.wireOp",EDGE,"E843"),sQuery(id+"F1.wireOp",EDGE,"E844"),sQuery(id+"F1.wireOp",EDGE,"E845"),sQuery(id+"F1.wireOp",EDGE,"E846"),sQuery(id+"F1.wireOp",EDGE,"E847"),sQuery(id+"F1.wireOp",EDGE,"E848"),sQuery(id+"F1.wireOp",EDGE,"E849"),sQuery(id+"F1.wireOp",EDGE,"E850"),sQuery(id+"F1.wireOp",EDGE,"E851"),sQuery(id+"F1.wireOp",EDGE,"E852"),sQuery(id+"F1.wireOp",EDGE,"E853"),sQuery(id+"F1.wireOp",EDGE,"E854"),sQuery(id+"F1.wireOp",EDGE,"E855"),sQuery(id+"F1.wireOp",EDGE,"E856"),sQuery(id+"F1.wireOp",EDGE,"E857"),sQuery(id+"F1.wireOp",EDGE,"E858"),sQuery(id+"F1.wireOp",EDGE,"E859"),sQuery(id+"F1.wireOp",EDGE,"E860"),sQuery(id+"F1.wireOp",EDGE,"E861"),sQuery(id+"F1.wireOp",EDGE,"E862"),sQuery(id+"F1.wireOp",EDGE,"E863"),sQuery(id+"F1.wireOp",EDGE,"E864"),sQuery(id+"F1.wireOp",EDGE,"E865"),sQuery(id+"F1.wireOp",EDGE,"E866"),sQuery(id+"F1.wireOp",EDGE,"E867"),sQuery(id+"F1.wireOp",EDGE,"E868"),sQuery(id+"F1.wireOp",EDGE,"E869"),sQuery(id+"F1.wireOp",EDGE,"E870"),sQuery(id+"F1.wireOp",EDGE,"E871"),sQuery(id+"F1.wireOp",EDGE,"E872"),sQuery(id+"F1.wireOp",EDGE,"E873"),sQuery(id+"F1.wireOp",EDGE,"E873"),sQuery(id+"F1.wireOp",EDGE,"E874"),sQuery(id+"F1.wireOp",EDGE,"E875"),sQuery(id+"F1.wireOp",EDGE,"E876"),sQuery(id+"F1.wireOp",EDGE,"E877"),sQuery(id+"F1.wireOp",EDGE,"E878"),sQuery(id+"F1.wireOp",EDGE,"E879"),sQuery(id+"F1.wireOp",EDGE,"E880"),sQuery(id+"F1.wireOp",EDGE,"E881"),sQuery(id+"F1.wireOp",EDGE,"E882"),sQuery(id+"F1.wireOp",EDGE,"E883"),sQuery(id+"F1.wireOp",EDGE,"E884"),sQuery(id+"F1.wireOp",EDGE,"E885"),sQuery(id+"F1.wireOp",EDGE,"E886"),sQuery(id+"F1.wireOp",EDGE,"E887"),sQuery(id+"F1.wireOp",EDGE,"E888"),sQuery(id+"F1.wireOp",EDGE,"E889"),sQuery(id+"F1.wireOp",EDGE,"E890"),sQuery(id+"F1.wireOp",EDGE,"E891"),sQuery(id+"F1.wireOp",EDGE,"E892"),sQuery(id+"F1.wireOp",EDGE,"E893"),sQuery(id+"F1.wireOp",EDGE,"E894"),sQuery(id+"F1.wireOp",EDGE,"E895"),sQuery(id+"F1.wireOp",EDGE,"E896"),sQuery(id+"F1.wireOp",EDGE,"E897"),sQuery(id+"F1.wireOp",EDGE,"E898"),sQuery(id+"F1.wireOp",EDGE,"E899"),sQuery(id+"F1.wireOp",EDGE,"E900"),sQuery(id+"F1.wireOp",EDGE,"E901"),sQuery(id+"F1.wireOp",EDGE,"E902"),sQuery(id+"F1.wireOp",EDGE,"E903"),sQuery(id+"F1.wireOp",EDGE,"E904"),sQuery(id+"F1.wireOp",EDGE,"E905"),sQuery(id+"F1.wireOp",EDGE,"E906"),sQuery(id+"F1.wireOp",EDGE,"E907"),sQuery(id+"F1.wireOp",EDGE,"E908"),sQuery(id+"F1.wireOp",EDGE,"E909"),sQuery(id+"F1.wireOp",EDGE,"E910"),sQuery(id+"F1.wireOp",EDGE,"E911"),sQuery(id+"F1.wireOp",EDGE,"E912"),sQuery(id+"F1.wireOp",EDGE,"E913"),sQuery(id+"F1.wireOp",EDGE,"E914"),sQuery(id+"F1.wireOp",EDGE,"E915"),sQuery(id+"F1.wireOp",EDGE,"E916"),sQuery(id+"F1.wireOp",EDGE,"E917"),sQuery(id+"F1.wireOp",EDGE,"E918"),sQuery(id+"F1.wireOp",EDGE,"E919"),sQuery(id+"F1.wireOp",EDGE,"E920"),sQuery(id+"F1.wireOp",EDGE,"E921"),sQuery(id+"F1.wireOp",EDGE,"E922"),sQuery(id+"F1.wireOp",EDGE,"E923"),sQuery(id+"F1.wireOp",EDGE,"E924"),sQuery(id+"F1.wireOp",EDGE,"E925"),sQuery(id+"F1.wireOp",EDGE,"E926"),sQuery(id+"F1.wireOp",EDGE,"E927"),sQuery(id+"F1.wireOp",EDGE,"E928"),sQuery(id+"F1.wireOp",EDGE,"E929"),sQuery(id+"F1.wireOp",EDGE,"E930"),sQuery(id+"F1.wireOp",EDGE,"E931"),sQuery(id+"F1.wireOp",EDGE,"E932"),sQuery(id+"F1.wireOp",EDGE,"E933"),sQuery(id+"F1.wireOp",EDGE,"E934"),sQuery(id+"F1.wireOp",EDGE,"E935"),sQuery(id+"F1.wireOp",EDGE,"E936"),sQuery(id+"F1.wireOp",EDGE,"E937"),sQuery(id+"F1.wireOp",EDGE,"E938"),sQuery(id+"F1.wireOp",EDGE,"E939"),sQuery(id+"F1.wireOp",EDGE,"E940"),sQuery(id+"F1.wireOp",EDGE,"E941"),sQuery(id+"F1.wireOp",EDGE,"E942"),sQuery(id+"F1.wireOp",EDGE,"E943"),sQuery(id+"F1.wireOp",EDGE,"E944"),sQuery(id+"F1.wireOp",EDGE,"E945"),sQuery(id+"F1.wireOp",EDGE,"E946"),sQuery(id+"F1.wireOp",EDGE,"E947"),sQuery(id+"F1.wireOp",EDGE,"E948"),sQuery(id+"F1.wireOp",EDGE,"E949"),sQuery(id+"F1.wireOp",EDGE,"E950"),sQuery(id+"F1.wireOp",EDGE,"E951"),sQuery(id+"F1.wireOp",EDGE,"E952"),sQuery(id+"F1.wireOp",EDGE,"E953"),sQuery(id+"F1.wireOp",EDGE,"E954"),sQuery(id+"F1.wireOp",EDGE,"E955"),sQuery(id+"F1.wireOp",EDGE,"E956"),sQuery(id+"F1.wireOp",EDGE,"E957"),sQuery(id+"F1.wireOp",EDGE,"E958"),sQuery(id+"F1.wireOp",EDGE,"E959"),sQuery(id+"F1.wireOp",EDGE,"E960"),sQuery(id+"F1.wireOp",EDGE,"E961"),sQuery(id+"F1.wireOp",EDGE,"E962"),sQuery(id+"F1.wireOp",EDGE,"E963"),sQuery(id+"F1.wireOp",EDGE,"E964"),sQuery(id+"F1.wireOp",EDGE,"E965"),sQuery(id+"F1.wireOp",EDGE,"E966"),sQuery(id+"F1.wireOp",EDGE,"E967"),sQuery(id+"F1.wireOp",EDGE,"E968"),sQuery(id+"F1.wireOp",EDGE,"E969"),sQuery(id+"F1.wireOp",EDGE,"E970"),sQuery(id+"F1.wireOp",EDGE,"E971"),sQuery(id+"F1.wireOp",EDGE,"E972"),sQuery(id+"F1.wireOp",EDGE,"E973"),sQuery(id+"F1.wireOp",EDGE,"E974"),sQuery(id+"F1.wireOp",EDGE,"E975"),sQuery(id+"F1.wireOp",EDGE,"E976"),sQuery(id+"F1.wireOp",EDGE,"E976"),sQuery(id+"F1.wireOp",EDGE,"E976"),sQuery(id+"F1.wireOp",EDGE,"E977"),sQuery(id+"F1.wireOp",EDGE,"E978"),sQuery(id+"F1.wireOp",EDGE,"E979"),sQuery(id+"F1.wireOp",EDGE,"E980"),sQuery(id+"F1.wireOp",EDGE,"E981"),sQuery(id+"F1.wireOp",EDGE,"E982"),sQuery(id+"F1.wireOp",EDGE,"E983"),sQuery(id+"F1.wireOp",EDGE,"E984"),sQuery(id+"F1.wireOp",EDGE,"E985"),sQuery(id+"F1.wireOp",EDGE,"E986"),sQuery(id+"F1.wireOp",EDGE,"E987"),sQuery(id+"F1.wireOp",EDGE,"E988"),sQuery(id+"F1.wireOp",EDGE,"E989"),sQuery(id+"F1.wireOp",EDGE,"E990"),sQuery(id+"F1.wireOp",EDGE,"E991"),sQuery(id+"F1.wireOp",EDGE,"E992"),sQuery(id+"F1.wireOp",EDGE,"E993"),sQuery(id+"F1.wireOp",EDGE,"E994"),sQuery(id+"F1.wireOp",EDGE,"E995"),sQuery(id+"F1.wireOp",EDGE,"E996"),sQuery(id+"F1.wireOp",EDGE,"E997"),sQuery(id+"F1.wireOp",EDGE,"E998"),sQuery(id+"F1.wireOp",EDGE,"E999"),sQuery(id+"F1.wireOp",EDGE,"E1000"),sQuery(id+"F1.wireOp",EDGE,"E1001"),sQuery(id+"F1.wireOp",EDGE,"E1002"),sQuery(id+"F1.wireOp",EDGE,"E1003"),sQuery(id+"F1.wireOp",EDGE,"E1004"),sQuery(id+"F1.wireOp",EDGE,"E1005"),sQuery(id+"F1.wireOp",EDGE,"E1006"),sQuery(id+"F1.wireOp",EDGE,"E1007"),sQuery(id+"F1.wireOp",EDGE,"E1008"),sQuery(id+"F1.wireOp",EDGE,"E1009"),sQuery(id+"F1.wireOp",EDGE,"E1010"),sQuery(id+"F1.wireOp",EDGE,"E1011"),sQuery(id+"F1.wireOp",EDGE,"E1012"),sQuery(id+"F1.wireOp",EDGE,"E1013"),sQuery(id+"F1.wireOp",EDGE,"E1014"),sQuery(id+"F1.wireOp",EDGE,"E1015"),sQuery(id+"F1.wireOp",EDGE,"E1016"),sQuery(id+"F1.wireOp",EDGE,"E1017"),sQuery(id+"F1.wireOp",EDGE,"E1018"),sQuery(id+"F1.wireOp",EDGE,"E1019"),sQuery(id+"F1.wireOp",EDGE,"E1020"),sQuery(id+"F1.wireOp",EDGE,"E1021"),sQuery(id+"F1.wireOp",EDGE,"E1022"),sQuery(id+"F1.wireOp",EDGE,"E1023"),sQuery(id+"F1.wireOp",EDGE,"E1024"),sQuery(id+"F1.wireOp",EDGE,"E1025"),sQuery(id+"F1.wireOp",EDGE,"E1026"),sQuery(id+"F1.wireOp",EDGE,"E1027"),sQuery(id+"F1.wireOp",EDGE,"E1028"),sQuery(id+"F1.wireOp",EDGE,"E1029"),sQuery(id+"F1.wireOp",EDGE,"E1030"),sQuery(id+"F1.wireOp",EDGE,"E1031"),sQuery(id+"F1.wireOp",EDGE,"E1032"),sQuery(id+"F1.wireOp",EDGE,"E1033"),sQuery(id+"F1.wireOp",EDGE,"E1034"),sQuery(id+"F1.wireOp",EDGE,"E1035"),sQuery(id+"F1.wireOp",EDGE,"E1036"),sQuery(id+"F1.wireOp",EDGE,"E1037"),sQuery(id+"F1.wireOp",EDGE,"E1038"),sQuery(id+"F1.wireOp",EDGE,"E1039"),sQuery(id+"F1.wireOp",EDGE,"E1040"),sQuery(id+"F1.wireOp",EDGE,"E1041"),sQuery(id+"F1.wireOp",EDGE,"E1042"),sQuery(id+"F1.wireOp",EDGE,"E1043"),sQuery(id+"F1.wireOp",EDGE,"E1044"),sQuery(id+"F1.wireOp",EDGE,"E1045"),sQuery(id+"F1.wireOp",EDGE,"E1046"),sQuery(id+"F1.wireOp",EDGE,"E1047"),sQuery(id+"F1.wireOp",EDGE,"E1048"),sQuery(id+"F1.wireOp",EDGE,"E1049"),sQuery(id+"F1.wireOp",EDGE,"E1050"),sQuery(id+"F1.wireOp",EDGE,"E1051"),sQuery(id+"F1.wireOp",EDGE,"E1052"),sQuery(id+"F1.wireOp",EDGE,"E1053"),sQuery(id+"F1.wireOp",EDGE,"E1054"),sQuery(id+"F1.wireOp",EDGE,"E1055"),sQuery(id+"F1.wireOp",EDGE,"E1056"),sQuery(id+"F1.wireOp",EDGE,"E1057"),sQuery(id+"F1.wireOp",EDGE,"E1058"),sQuery(id+"F1.wireOp",EDGE,"E1059"),sQuery(id+"F1.wireOp",EDGE,"E1060"),sQuery(id+"F1.wireOp",EDGE,"E1061"),sQuery(id+"F1.wireOp",EDGE,"E1062"),sQuery(id+"F1.wireOp",EDGE,"E1063"),sQuery(id+"F1.wireOp",EDGE,"E1064"),sQuery(id+"F1.wireOp",EDGE,"E1065"),sQuery(id+"F1.wireOp",EDGE,"E1066"),sQuery(id+"F1.wireOp",EDGE,"E1067"),sQuery(id+"F1.wireOp",EDGE,"E1068"),sQuery(id+"F1.wireOp",EDGE,"E1069"),sQuery(id+"F1.wireOp",EDGE,"E1070"),sQuery(id+"F1.wireOp",EDGE,"E1071"),sQuery(id+"F1.wireOp",EDGE,"E1071"),sQuery(id+"F1.wireOp",EDGE,"E1072"),sQuery(id+"F1.wireOp",EDGE,"E1073"),sQuery(id+"F1.wireOp",EDGE,"E1074"),sQuery(id+"F1.wireOp",EDGE,"E1075"),sQuery(id+"F1.wireOp",EDGE,"E1076"),sQuery(id+"F1.wireOp",EDGE,"E1077"),sQuery(id+"F1.wireOp",EDGE,"E1078"),sQuery(id+"F1.wireOp",EDGE,"E1079"),sQuery(id+"F1.wireOp",EDGE,"E1080"),sQuery(id+"F1.wireOp",EDGE,"E1080"),sQuery(id+"F1.wireOp",EDGE,"E1081"),sQuery(id+"F1.wireOp",EDGE,"E1082"),sQuery(id+"F1.wireOp",EDGE,"E1083"),sQuery(id+"F1.wireOp",EDGE,"E1084"),sQuery(id+"F1.wireOp",EDGE,"E1085"),sQuery(id+"F1.wireOp",EDGE,"E1086"),sQuery(id+"F1.wireOp",EDGE,"E1087"),sQuery(id+"F1.wireOp",EDGE,"E1088"),sQuery(id+"F1.wireOp",EDGE,"E1089"),sQuery(id+"F1.wireOp",EDGE,"E1090"),sQuery(id+"F1.wireOp",EDGE,"E1091"),sQuery(id+"F1.wireOp",EDGE,"E1092"),sQuery(id+"F1.wireOp",EDGE,"E1093"),sQuery(id+"F1.wireOp",EDGE,"E1094"),sQuery(id+"F1.wireOp",EDGE,"E1095"),sQuery(id+"F1.wireOp",EDGE,"E1096"),sQuery(id+"F1.wireOp",EDGE,"E1097"),sQuery(id+"F1.wireOp",EDGE,"E1098"),sQuery(id+"F1.wireOp",EDGE,"E1099"),sQuery(id+"F1.wireOp",EDGE,"E1100"),sQuery(id+"F1.wireOp",EDGE,"E1101"),sQuery(id+"F1.wireOp",EDGE,"E1102"),sQuery(id+"F1.wireOp",EDGE,"E1103"),sQuery(id+"F1.wireOp",EDGE,"E1104"),sQuery(id+"F1.wireOp",EDGE,"E1105"),sQuery(id+"F1.wireOp",EDGE,"E1106"),sQuery(id+"F1.wireOp",EDGE,"E1107"),sQuery(id+"F1.wireOp",EDGE,"E1108"),sQuery(id+"F1.wireOp",EDGE,"E1109"),sQuery(id+"F1.wireOp",EDGE,"E1110"),sQuery(id+"F1.wireOp",EDGE,"E1111"),sQuery(id+"F1.wireOp",EDGE,"E1112"),sQuery(id+"F1.wireOp",EDGE,"E1113"),sQuery(id+"F1.wireOp",EDGE,"E1114"),sQuery(id+"F1.wireOp",EDGE,"E1115"),sQuery(id+"F1.wireOp",EDGE,"E1116"),sQuery(id+"F1.wireOp",EDGE,"E1117"),sQuery(id+"F1.wireOp",EDGE,"E1118"),sQuery(id+"F1.wireOp",EDGE,"E1119"),sQuery(id+"F1.wireOp",EDGE,"E1120"),sQuery(id+"F1.wireOp",EDGE,"E1121"),sQuery(id+"F1.wireOp",EDGE,"E1122"),sQuery(id+"F1.wireOp",EDGE,"E1123"),sQuery(id+"F1.wireOp",EDGE,"E1124"),sQuery(id+"F1.wireOp",EDGE,"E1125"),sQuery(id+"F1.wireOp",EDGE,"E1126"),sQuery(id+"F1.wireOp",EDGE,"E1127"),sQuery(id+"F1.wireOp",EDGE,"E1128"),sQuery(id+"F1.wireOp",EDGE,"E1129"),sQuery(id+"F1.wireOp",EDGE,"E1130"),sQuery(id+"F1.wireOp",EDGE,"E1131"),sQuery(id+"F1.wireOp",EDGE,"E1132"),sQuery(id+"F1.wireOp",EDGE,"E1133"),sQuery(id+"F1.wireOp",EDGE,"E1134"),sQuery(id+"F1.wireOp",EDGE,"E1135"),sQuery(id+"F1.wireOp",EDGE,"E1136"),sQuery(id+"F1.wireOp",EDGE,"E1137"),sQuery(id+"F1.wireOp",EDGE,"E1138"),sQuery(id+"F1.wireOp",EDGE,"E1139"),sQuery(id+"F1.wireOp",EDGE,"E1140"),sQuery(id+"F1.wireOp",EDGE,"E1141"),sQuery(id+"F1.wireOp",EDGE,"E1142"),sQuery(id+"F1.wireOp",EDGE,"E1143"),sQuery(id+"F1.wireOp",EDGE,"E1144"),sQuery(id+"F1.wireOp",EDGE,"E1145"),sQuery(id+"F1.wireOp",EDGE,"E1146"),sQuery(id+"F1.wireOp",EDGE,"E1147"),sQuery(id+"F1.wireOp",EDGE,"E1148"),sQuery(id+"F1.wireOp",EDGE,"E1149"),sQuery(id+"F1.wireOp",EDGE,"E1150"),sQuery(id+"F1.wireOp",EDGE,"E1151"),sQuery(id+"F1.wireOp",EDGE,"E1152"),sQuery(id+"F1.wireOp",EDGE,"E1153"),sQuery(id+"F1.wireOp",EDGE,"E1154"),sQuery(id+"F1.wireOp",EDGE,"E1155"),sQuery(id+"F1.wireOp",EDGE,"E1156"),sQuery(id+"F1.wireOp",EDGE,"E1156"),sQuery(id+"F1.wireOp",EDGE,"E1157"),sQuery(id+"F1.wireOp",EDGE,"E1158"),sQuery(id+"F1.wireOp",EDGE,"E1159"),sQuery(id+"F1.wireOp",EDGE,"E1160"),sQuery(id+"F1.wireOp",EDGE,"E1161"),sQuery(id+"F1.wireOp",EDGE,"E1162"),sQuery(id+"F1.wireOp",EDGE,"E1163"),sQuery(id+"F1.wireOp",EDGE,"E1164"),sQuery(id+"F1.wireOp",EDGE,"E1165"),sQuery(id+"F1.wireOp",EDGE,"E1166"),sQuery(id+"F1.wireOp",EDGE,"E1167"),sQuery(id+"F1.wireOp",EDGE,"E1168"),sQuery(id+"F1.wireOp",EDGE,"E1169"),sQuery(id+"F1.wireOp",EDGE,"E1170"),sQuery(id+"F1.wireOp",EDGE,"E1171"),sQuery(id+"F1.wireOp",EDGE,"E1172"),sQuery(id+"F1.wireOp",EDGE,"E1173"),sQuery(id+"F1.wireOp",EDGE,"E1174"),sQuery(id+"F1.wireOp",EDGE,"E1175"),sQuery(id+"F1.wireOp",EDGE,"E1176"),sQuery(id+"F1.wireOp",EDGE,"E1177"),sQuery(id+"F1.wireOp",EDGE,"E1178"),sQuery(id+"F1.wireOp",EDGE,"E1179"),sQuery(id+"F1.wireOp",EDGE,"E1180"),sQuery(id+"F1.wireOp",EDGE,"E1181"),sQuery(id+"F1.wireOp",EDGE,"E1182"),sQuery(id+"F1.wireOp",EDGE,"E1183"),sQuery(id+"F1.wireOp",EDGE,"E1184"),sQuery(id+"F1.wireOp",EDGE,"E1185"),sQuery(id+"F1.wireOp",EDGE,"E1186"),sQuery(id+"F1.wireOp",EDGE,"E1187"),sQuery(id+"F1.wireOp",EDGE,"E1188"),sQuery(id+"F1.wireOp",EDGE,"E1189"),sQuery(id+"F1.wireOp",EDGE,"E1190"),sQuery(id+"F1.wireOp",EDGE,"E1191"),sQuery(id+"F1.wireOp",EDGE,"E1192"),sQuery(id+"F1.wireOp",EDGE,"E1193"),sQuery(id+"F1.wireOp",EDGE,"E1194"),sQuery(id+"F1.wireOp",EDGE,"E1195"),sQuery(id+"F1.wireOp",EDGE,"E1196"),sQuery(id+"F1.wireOp",EDGE,"E1197"),sQuery(id+"F1.wireOp",EDGE,"E1198"),sQuery(id+"F1.wireOp",EDGE,"E1199"),sQuery(id+"F1.wireOp",EDGE,"E1200"),sQuery(id+"F1.wireOp",EDGE,"E1201"),sQuery(id+"F1.wireOp",EDGE,"E1202"),sQuery(id+"F1.wireOp",EDGE,"E1203"),sQuery(id+"F1.wireOp",EDGE,"E1204"),sQuery(id+"F1.wireOp",EDGE,"E1205"),sQuery(id+"F1.wireOp",EDGE,"E1206"),sQuery(id+"F1.wireOp",EDGE,"E1207"),sQuery(id+"F1.wireOp",EDGE,"E1208"),sQuery(id+"F1.wireOp",EDGE,"E1209"),sQuery(id+"F1.wireOp",EDGE,"E1210"),sQuery(id+"F1.wireOp",EDGE,"E1211"),sQuery(id+"F1.wireOp",EDGE,"E1212"),sQuery(id+"F1.wireOp",EDGE,"E1213"),sQuery(id+"F1.wireOp",EDGE,"E1214"),sQuery(id+"F1.wireOp",EDGE,"E1215"),sQuery(id+"F1.wireOp",EDGE,"E1216"),sQuery(id+"F1.wireOp",EDGE,"E1217"),sQuery(id+"F1.wireOp",EDGE,"E1218"),sQuery(id+"F1.wireOp",EDGE,"E1219"),sQuery(id+"F1.wireOp",EDGE,"E1220"),sQuery(id+"F1.wireOp",EDGE,"E1221"),sQuery(id+"F1.wireOp",EDGE,"E1222"),sQuery(id+"F1.wireOp",EDGE,"E1223"),sQuery(id+"F1.wireOp",EDGE,"E1224"),sQuery(id+"F1.wireOp",EDGE,"E1225"),sQuery(id+"F1.wireOp",EDGE,"E1226"),sQuery(id+"F1.wireOp",EDGE,"E1227"),sQuery(id+"F1.wireOp",EDGE,"E1228"),sQuery(id+"F1.wireOp",EDGE,"E1229"),sQuery(id+"F1.wireOp",EDGE,"E1230"),sQuery(id+"F1.wireOp",EDGE,"E1231"),sQuery(id+"F1.wireOp",EDGE,"E1232"),sQuery(id+"F1.wireOp",EDGE,"E1233"),sQuery(id+"F1.wireOp",EDGE,"E1234"),sQuery(id+"F1.wireOp",EDGE,"E1235"),sQuery(id+"F1.wireOp",EDGE,"E1236"),sQuery(id+"F1.wireOp",EDGE,"E1237"),sQuery(id+"F1.wireOp",EDGE,"E1238"),sQuery(id+"F1.wireOp",EDGE,"E1239"),sQuery(id+"F1.wireOp",EDGE,"E1240"),sQuery(id+"F1.wireOp",EDGE,"E1241"),sQuery(id+"F1.wireOp",EDGE,"E1242"),sQuery(id+"F1.wireOp",EDGE,"E1243"),sQuery(id+"F1.wireOp",EDGE,"E1244"),sQuery(id+"F1.wireOp",EDGE,"E1245"),sQuery(id+"F1.wireOp",EDGE,"E1246"),sQuery(id+"F1.wireOp",EDGE,"E1247"),sQuery(id+"F1.wireOp",EDGE,"E1248"),sQuery(id+"F1.wireOp",EDGE,"E1249"),sQuery(id+"F1.wireOp",EDGE,"E1250"),sQuery(id+"F1.wireOp",EDGE,"E1251"),sQuery(id+"F1.wireOp",EDGE,"E1252"),sQuery(id+"F1.wireOp",EDGE,"E1253"),sQuery(id+"F1.wireOp",EDGE,"E1254"),sQuery(id+"F1.wireOp",EDGE,"E1255"),sQuery(id+"F1.wireOp",EDGE,"E1256"),sQuery(id+"F1.wireOp",EDGE,"E1257"),sQuery(id+"F1.wireOp",EDGE,"E1258"),sQuery(id+"F1.wireOp",EDGE,"E1259"),sQuery(id+"F1.wireOp",EDGE,"E1260"),sQuery(id+"F1.wireOp",EDGE,"E1261"),sQuery(id+"F1.wireOp",EDGE,"E1262"),sQuery(id+"F1.wireOp",EDGE,"E1263"),sQuery(id+"F1.wireOp",EDGE,"E1264"),sQuery(id+"F1.wireOp",EDGE,"E1265"),sQuery(id+"F1.wireOp",EDGE,"E1266"),sQuery(id+"F1.wireOp",EDGE,"E1267"),sQuery(id+"F1.wireOp",EDGE,"E1268"),sQuery(id+"F1.wireOp",EDGE,"E1269"),sQuery(id+"F1.wireOp",EDGE,"E1270"),sQuery(id+"F1.wireOp",EDGE,"E1271"),sQuery(id+"F1.wireOp",EDGE,"E1272"),sQuery(id+"F1.wireOp",EDGE,"E1273"),sQuery(id+"F1.wireOp",EDGE,"E1274"),sQuery(id+"F1.wireOp",EDGE,"E1275"),sQuery(id+"F1.wireOp",EDGE,"E1276"),sQuery(id+"F1.wireOp",EDGE,"E1277"),sQuery(id+"F1.wireOp",EDGE,"E1278"),sQuery(id+"F1.wireOp",EDGE,"E1279"),sQuery(id+"F1.wireOp",EDGE,"E1280"),sQuery(id+"F1.wireOp",EDGE,"E1281"),sQuery(id+"F1.wireOp",EDGE,"E1282"),sQuery(id+"F1.wireOp",EDGE,"E1283"),sQuery(id+"F1.wireOp",EDGE,"E1284"),sQuery(id+"F1.wireOp",EDGE,"E1285"),sQuery(id+"F1.wireOp",EDGE,"E1286"),sQuery(id+"F1.wireOp",EDGE,"E1287"),sQuery(id+"F1.wireOp",EDGE,"E1288"),sQuery(id+"F1.wireOp",EDGE,"E1289"),sQuery(id+"F1.wireOp",EDGE,"E1290"),sQuery(id+"F1.wireOp",EDGE,"E1291"),sQuery(id+"F1.wireOp",EDGE,"E1292"),sQuery(id+"F1.wireOp",EDGE,"E1293"),sQuery(id+"F1.wireOp",EDGE,"E1294"),sQuery(id+"F1.wireOp",EDGE,"E1295"),sQuery(id+"F1.wireOp",EDGE,"E1296"),sQuery(id+"F1.wireOp",EDGE,"E1297"),sQuery(id+"F1.wireOp",EDGE,"E1298"),sQuery(id+"F1.wireOp",EDGE,"E1299"),sQuery(id+"F1.wireOp",EDGE,"E1300"),sQuery(id+"F1.wireOp",EDGE,"E1301"),sQuery(id+"F1.wireOp",EDGE,"E1302"),sQuery(id+"F1.wireOp",EDGE,"E1303"),sQuery(id+"F1.wireOp",EDGE,"E1304"),sQuery(id+"F1.wireOp",EDGE,"E1305"),sQuery(id+"F1.wireOp",EDGE,"E1306"),sQuery(id+"F1.wireOp",EDGE,"E1307"),sQuery(id+"F1.wireOp",EDGE,"E1308"),sQuery(id+"F1.wireOp",EDGE,"E1309"),sQuery(id+"F1.wireOp",EDGE,"E1310"),sQuery(id+"F1.wireOp",EDGE,"E1311"),sQuery(id+"F1.wireOp",EDGE,"E1312"),sQuery(id+"F1.wireOp",EDGE,"E1312"),sQuery(id+"F1.wireOp",EDGE,"E1313"),sQuery(id+"F1.wireOp",EDGE,"E1314"),sQuery(id+"F1.wireOp",EDGE,"E1315"),sQuery(id+"F1.wireOp",EDGE,"E1316"),sQuery(id+"F1.wireOp",EDGE,"E1317"),sQuery(id+"F1.wireOp",EDGE,"E1318"),sQuery(id+"F1.wireOp",EDGE,"E1319"),sQuery(id+"F1.wireOp",EDGE,"E1320"),sQuery(id+"F1.wireOp",EDGE,"E1321"),sQuery(id+"F1.wireOp",EDGE,"E1322"),sQuery(id+"F1.wireOp",EDGE,"E1323"),sQuery(id+"F1.wireOp",EDGE,"E1324"),sQuery(id+"F1.wireOp",EDGE,"E1325"),sQuery(id+"F1.wireOp",EDGE,"E1326"),sQuery(id+"F1.wireOp",EDGE,"E1327"),sQuery(id+"F1.wireOp",EDGE,"E1328"),sQuery(id+"F1.wireOp",EDGE,"E1329"),sQuery(id+"F1.wireOp",EDGE,"E1330"),sQuery(id+"F1.wireOp",EDGE,"E1331"),sQuery(id+"F1.wireOp",EDGE,"E1332"),sQuery(id+"F1.wireOp",EDGE,"E1333"),sQuery(id+"F1.wireOp",EDGE,"E1334"),sQuery(id+"F1.wireOp",EDGE,"E1335"),sQuery(id+"F1.wireOp",EDGE,"E1336"),sQuery(id+"F1.wireOp",EDGE,"E1337"),sQuery(id+"F1.wireOp",EDGE,"E1338"),sQuery(id+"F1.wireOp",EDGE,"E1339"),sQuery(id+"F1.wireOp",EDGE,"E1340"),sQuery(id+"F1.wireOp",EDGE,"E1341"),sQuery(id+"F1.wireOp",EDGE,"E1342"),sQuery(id+"F1.wireOp",EDGE,"E1343"),sQuery(id+"F1.wireOp",EDGE,"E1344"),sQuery(id+"F1.wireOp",EDGE,"E1345"),sQuery(id+"F1.wireOp",EDGE,"E1346"),sQuery(id+"F1.wireOp",EDGE,"E1347"),sQuery(id+"F1.wireOp",EDGE,"E1348"),sQuery(id+"F1.wireOp",EDGE,"E1349"),sQuery(id+"F1.wireOp",EDGE,"E1350"),sQuery(id+"F1.wireOp",EDGE,"E1351"),sQuery(id+"F1.wireOp",EDGE,"E1352"),sQuery(id+"F1.wireOp",EDGE,"E1353"),sQuery(id+"F1.wireOp",EDGE,"E1354"),sQuery(id+"F1.wireOp",EDGE,"E1355"),sQuery(id+"F1.wireOp",EDGE,"E1356"),sQuery(id+"F1.wireOp",EDGE,"E1357"),sQuery(id+"F1.wireOp",EDGE,"E1358"),sQuery(id+"F1.wireOp",EDGE,"E1359"),sQuery(id+"F1.wireOp",EDGE,"E1360"),sQuery(id+"F1.wireOp",EDGE,"E1361"),sQuery(id+"F1.wireOp",EDGE,"E1362"),sQuery(id+"F1.wireOp",EDGE,"E1363"),sQuery(id+"F1.wireOp",EDGE,"E1364"),sQuery(id+"F1.wireOp",EDGE,"E1365"),sQuery(id+"F1.wireOp",EDGE,"E1366"),sQuery(id+"F1.wireOp",EDGE,"E1367"),sQuery(id+"F1.wireOp",EDGE,"E1368"),sQuery(id+"F1.wireOp",EDGE,"E1369"),sQuery(id+"F1.wireOp",EDGE,"E1370"),sQuery(id+"F1.wireOp",EDGE,"E1371"),sQuery(id+"F1.wireOp",EDGE,"E1372"),sQuery(id+"F1.wireOp",EDGE,"E1373"),sQuery(id+"F1.wireOp",EDGE,"E1374"),sQuery(id+"F1.wireOp",EDGE,"E1375"),sQuery(id+"F1.wireOp",EDGE,"E1376"),sQuery(id+"F1.wireOp",EDGE,"E1376"),sQuery(id+"F1.wireOp",EDGE,"E1377"),sQuery(id+"F1.wireOp",EDGE,"E1378"),sQuery(id+"F1.wireOp",EDGE,"E1379"),sQuery(id+"F1.wireOp",EDGE,"E1380"),sQuery(id+"F1.wireOp",EDGE,"E1381"),sQuery(id+"F1.wireOp",EDGE,"E1382"),sQuery(id+"F1.wireOp",EDGE,"E1383"),sQuery(id+"F1.wireOp",EDGE,"E1384"),sQuery(id+"F1.wireOp",EDGE,"E1385"),sQuery(id+"F1.wireOp",EDGE,"E1386"),sQuery(id+"F1.wireOp",EDGE,"E1387"),sQuery(id+"F1.wireOp",EDGE,"E1388"),sQuery(id+"F1.wireOp",EDGE,"E1389"),sQuery(id+"F1.wireOp",EDGE,"E1390"),sQuery(id+"F1.wireOp",EDGE,"E1391"),sQuery(id+"F1.wireOp",EDGE,"E1392"),sQuery(id+"F1.wireOp",EDGE,"E1393"),sQuery(id+"F1.wireOp",EDGE,"E1394"),sQuery(id+"F1.wireOp",EDGE,"E1395"),sQuery(id+"F1.wireOp",EDGE,"E1396"),sQuery(id+"F1.wireOp",EDGE,"E1397"),sQuery(id+"F1.wireOp",EDGE,"E1398"),sQuery(id+"F1.wireOp",EDGE,"E1399"),sQuery(id+"F1.wireOp",EDGE,"E1400"),sQuery(id+"F1.wireOp",EDGE,"E1401"),sQuery(id+"F1.wireOp",EDGE,"E1402"),sQuery(id+"F1.wireOp",EDGE,"E1403"),sQuery(id+"F1.wireOp",EDGE,"E1404"),sQuery(id+"F1.wireOp",EDGE,"E1405"),sQuery(id+"F1.wireOp",EDGE,"E1406"),sQuery(id+"F1.wireOp",EDGE,"E1407"),sQuery(id+"F1.wireOp",EDGE,"E1408"),sQuery(id+"F1.wireOp",EDGE,"E1409"),sQuery(id+"F1.wireOp",EDGE,"E1410"),sQuery(id+"F1.wireOp",EDGE,"E1411"),sQuery(id+"F1.wireOp",EDGE,"E1412"),sQuery(id+"F1.wireOp",EDGE,"E1413"),sQuery(id+"F1.wireOp",EDGE,"E1414"),sQuery(id+"F1.wireOp",EDGE,"E1415"),sQuery(id+"F1.wireOp",EDGE,"E1416"),sQuery(id+"F1.wireOp",EDGE,"E1417"),sQuery(id+"F1.wireOp",EDGE,"E1418"),sQuery(id+"F1.wireOp",EDGE,"E1419"),sQuery(id+"F1.wireOp",EDGE,"E1420"),sQuery(id+"F1.wireOp",EDGE,"E1421"),sQuery(id+"F1.wireOp",EDGE,"E1422"),sQuery(id+"F1.wireOp",EDGE,"E1423"),sQuery(id+"F1.wireOp",EDGE,"E1424"),sQuery(id+"F1.wireOp",EDGE,"E1425"),sQuery(id+"F1.wireOp",EDGE,"E1426"),sQuery(id+"F1.wireOp",EDGE,"E1427"),sQuery(id+"F1.wireOp",EDGE,"E1428"),sQuery(id+"F1.wireOp",EDGE,"E1429"),sQuery(id+"F1.wireOp",EDGE,"E1430"),sQuery(id+"F1.wireOp",EDGE,"E1431"),sQuery(id+"F1.wireOp",EDGE,"E1432"),sQuery(id+"F1.wireOp",EDGE,"E1433"),sQuery(id+"F1.wireOp",EDGE,"E1434"),sQuery(id+"F1.wireOp",EDGE,"E1435"),sQuery(id+"F1.wireOp",EDGE,"E1436"),sQuery(id+"F1.wireOp",EDGE,"E1437"),sQuery(id+"F1.wireOp",EDGE,"E1438"),sQuery(id+"F1.wireOp",EDGE,"E1439"),sQuery(id+"F1.wireOp",EDGE,"E1440"),sQuery(id+"F1.wireOp",EDGE,"E1441"),sQuery(id+"F1.wireOp",EDGE,"E1442"),sQuery(id+"F1.wireOp",EDGE,"E1443"),sQuery(id+"F1.wireOp",EDGE,"E1444"),sQuery(id+"F1.wireOp",EDGE,"E1445"),sQuery(id+"F1.wireOp",EDGE,"E1446"),sQuery(id+"F1.wireOp",EDGE,"E1447"),sQuery(id+"F1.wireOp",EDGE,"E1448"),sQuery(id+"F1.wireOp",EDGE,"E1449"),sQuery(id+"F1.wireOp",EDGE,"E1450"),sQuery(id+"F1.wireOp",EDGE,"E1451"),sQuery(id+"F1.wireOp",EDGE,"E1452"),sQuery(id+"F1.wireOp",EDGE,"E1453"),sQuery(id+"F1.wireOp",EDGE,"E1454"),sQuery(id+"F1.wireOp",EDGE,"E1455"),sQuery(id+"F1.wireOp",EDGE,"E1456"),sQuery(id+"F1.wireOp",EDGE,"E1457"),sQuery(id+"F1.wireOp",EDGE,"E1458"),sQuery(id+"F1.wireOp",EDGE,"E1459"),sQuery(id+"F1.wireOp",EDGE,"E1460"),sQuery(id+"F1.wireOp",EDGE,"E1461"),sQuery(id+"F1.wireOp",EDGE,"E1462"),sQuery(id+"F1.wireOp",EDGE,"E1463"),sQuery(id+"F1.wireOp",EDGE,"E1464"),sQuery(id+"F1.wireOp",EDGE,"E1465"),sQuery(id+"F1.wireOp",EDGE,"E1466"),sQuery(id+"F1.wireOp",EDGE,"E1467"),sQuery(id+"F1.wireOp",EDGE,"E1468"),sQuery(id+"F1.wireOp",EDGE,"E1469"),sQuery(id+"F1.wireOp",EDGE,"E1470"),sQuery(id+"F1.wireOp",EDGE,"E1471"),sQuery(id+"F1.wireOp",EDGE,"E1472"),sQuery(id+"F1.wireOp",EDGE,"E1473"),sQuery(id+"F1.wireOp",EDGE,"E1474"),sQuery(id+"F1.wireOp",EDGE,"E1475"),sQuery(id+"F1.wireOp",EDGE,"E1476"),sQuery(id+"F1.wireOp",EDGE,"E1477"),sQuery(id+"F1.wireOp",EDGE,"E1478"),sQuery(id+"F1.wireOp",EDGE,"E1479"),sQuery(id+"F1.wireOp",EDGE,"E1480"),sQuery(id+"F1.wireOp",EDGE,"E1481"),sQuery(id+"F1.wireOp",EDGE,"E1482"),sQuery(id+"F1.wireOp",EDGE,"E1483"),sQuery(id+"F1.wireOp",EDGE,"E1484"),sQuery(id+"F1.wireOp",EDGE,"E1485"),sQuery(id+"F1.wireOp",EDGE,"E1486"),sQuery(id+"F1.wireOp",EDGE,"E1487"),sQuery(id+"F1.wireOp",EDGE,"E1488"),sQuery(id+"F1.wireOp",EDGE,"E1489"),sQuery(id+"F1.wireOp",EDGE,"E1490"),sQuery(id+"F1.wireOp",EDGE,"E1491"),sQuery(id+"F1.wireOp",EDGE,"E1492"),sQuery(id+"F1.wireOp",EDGE,"E1493"),sQuery(id+"F1.wireOp",EDGE,"E1494"),sQuery(id+"F1.wireOp",EDGE,"E1495"),sQuery(id+"F1.wireOp",EDGE,"E1496"),sQuery(id+"F1.wireOp",EDGE,"E1497"),sQuery(id+"F1.wireOp",EDGE,"E1498"),sQuery(id+"F1.wireOp",EDGE,"E1499"),sQuery(id+"F1.wireOp",EDGE,"E1500"),sQuery(id+"F1.wireOp",EDGE,"E1501"),sQuery(id+"F1.wireOp",EDGE,"E1502"),sQuery(id+"F1.wireOp",EDGE,"E1503"),sQuery(id+"F1.wireOp",EDGE,"E1504"),sQuery(id+"F1.wireOp",EDGE,"E1505"),sQuery(id+"F1.wireOp",EDGE,"E1506"),sQuery(id+"F1.wireOp",EDGE,"E1507"),sQuery(id+"F1.wireOp",EDGE,"E1508"),sQuery(id+"F1.wireOp",EDGE,"E1509"),sQuery(id+"F1.wireOp",EDGE,"E1510"),sQuery(id+"F1.wireOp",EDGE,"E1511"),sQuery(id+"F1.wireOp",EDGE,"E1512"),sQuery(id+"F1.wireOp",EDGE,"E1513"),sQuery(id+"F1.wireOp",EDGE,"E1514"),sQuery(id+"F1.wireOp",EDGE,"E1515"),sQuery(id+"F1.wireOp",EDGE,"E1516"),sQuery(id+"F1.wireOp",EDGE,"E1517"),sQuery(id+"F1.wireOp",EDGE,"E1518"),sQuery(id+"F1.wireOp",EDGE,"E1519"),sQuery(id+"F1.wireOp",EDGE,"E1520"),sQuery(id+"F1.wireOp",EDGE,"E1521"),sQuery(id+"F1.wireOp",EDGE,"E1522"),sQuery(id+"F1.wireOp",EDGE,"E1523"),sQuery(id+"F1.wireOp",EDGE,"E1524"),sQuery(id+"F1.wireOp",EDGE,"E1525"),sQuery(id+"F1.wireOp",EDGE,"E1526"),sQuery(id+"F1.wireOp",EDGE,"E1527"),sQuery(id+"F1.wireOp",EDGE,"E1528"),sQuery(id+"F1.wireOp",EDGE,"E1529"),sQuery(id+"F1.wireOp",EDGE,"E1530"),sQuery(id+"F1.wireOp",EDGE,"E1531"),sQuery(id+"F1.wireOp",EDGE,"E1532"),sQuery(id+"F1.wireOp",EDGE,"E1533"),sQuery(id+"F1.wireOp",EDGE,"E1534"),sQuery(id+"F1.wireOp",EDGE,"E1535"),sQuery(id+"F1.wireOp",EDGE,"E1536"),sQuery(id+"F1.wireOp",EDGE,"E1537"),sQuery(id+"F1.wireOp",EDGE,"E1538"),sQuery(id+"F1.wireOp",EDGE,"E1539"),sQuery(id+"F1.wireOp",EDGE,"E1540"),sQuery(id+"F1.wireOp",EDGE,"E1541"),sQuery(id+"F1.wireOp",EDGE,"E1542"),sQuery(id+"F1.wireOp",EDGE,"E1543"),sQuery(id+"F1.wireOp",EDGE,"E1544"),sQuery(id+"F1.wireOp",EDGE,"E1545"),sQuery(id+"F1.wireOp",EDGE,"E1546"),sQuery(id+"F1.wireOp",EDGE,"E1547"),sQuery(id+"F1.wireOp",EDGE,"E1548"),sQuery(id+"F1.wireOp",EDGE,"E1549"),sQuery(id+"F1.wireOp",EDGE,"E1550"),sQuery(id+"F1.wireOp",EDGE,"E1551"),sQuery(id+"F1.wireOp",EDGE,"E1552"),sQuery(id+"F1.wireOp",EDGE,"E1553"),sQuery(id+"F1.wireOp",EDGE,"E1554"),sQuery(id+"F1.wireOp",EDGE,"E1555"),sQuery(id+"F1.wireOp",EDGE,"E1556"),sQuery(id+"F1.wireOp",EDGE,"E1557"),sQuery(id+"F1.wireOp",EDGE,"E1558"),sQuery(id+"F1.wireOp",EDGE,"E1559"),sQuery(id+"F1.wireOp",EDGE,"E1560"),sQuery(id+"F1.wireOp",EDGE,"E1561"),sQuery(id+"F1.wireOp",EDGE,"E1562"),sQuery(id+"F1.wireOp",EDGE,"E1563"),sQuery(id+"F1.wireOp",EDGE,"E1564"),sQuery(id+"F1.wireOp",EDGE,"E1565"),sQuery(id+"F1.wireOp",EDGE,"E1566"),sQuery(id+"F1.wireOp",EDGE,"E1567"),sQuery(id+"F1.wireOp",EDGE,"E1568"),sQuery(id+"F1.wireOp",EDGE,"E1569"),sQuery(id+"F1.wireOp",EDGE,"E1570"),sQuery(id+"F1.wireOp",EDGE,"E1571"),sQuery(id+"F1.wireOp",EDGE,"E1572"),sQuery(id+"F1.wireOp",EDGE,"E1573"),sQuery(id+"F1.wireOp",EDGE,"E1574"),sQuery(id+"F1.wireOp",EDGE,"E1575"),sQuery(id+"F1.wireOp",EDGE,"E1576"),sQuery(id+"F1.wireOp",EDGE,"E1577"),sQuery(id+"F1.wireOp",EDGE,"E1578"),sQuery(id+"F1.wireOp",EDGE,"E1579"),sQuery(id+"F1.wireOp",EDGE,"E1580"),sQuery(id+"F1.wireOp",EDGE,"E1581"),sQuery(id+"F1.wireOp",EDGE,"E1582"),sQuery(id+"F1.wireOp",EDGE,"E1583"),sQuery(id+"F1.wireOp",EDGE,"E1584"),sQuery(id+"F1.wireOp",EDGE,"E1585"),sQuery(id+"F1.wireOp",EDGE,"E1586"),sQuery(id+"F1.wireOp",EDGE,"E1587"),sQuery(id+"F1.wireOp",EDGE,"E1588"),sQuery(id+"F1.wireOp",EDGE,"E1589"),sQuery(id+"F1.wireOp",EDGE,"E1590"),sQuery(id+"F1.wireOp",EDGE,"E1591"),sQuery(id+"F1.wireOp",EDGE,"E1592"),sQuery(id+"F1.wireOp",EDGE,"E1593"),sQuery(id+"F1.wireOp",EDGE,"E1594"),sQuery(id+"F1.wireOp",EDGE,"E1595"),sQuery(id+"F1.wireOp",EDGE,"E1596"),sQuery(id+"F1.wireOp",EDGE,"E1597"),sQuery(id+"F1.wireOp",EDGE,"E1598"),sQuery(id+"F1.wireOp",EDGE,"E1599"),sQuery(id+"F1.wireOp",EDGE,"E1600"),sQuery(id+"F1.wireOp",EDGE,"E1601"),sQuery(id+"F1.wireOp",EDGE,"E1602"),sQuery(id+"F1.wireOp",EDGE,"E1603"),sQuery(id+"F1.wireOp",EDGE,"E1604"),sQuery(id+"F1.wireOp",EDGE,"E1605"),sQuery(id+"F1.wireOp",EDGE,"E1606"),sQuery(id+"F1.wireOp",EDGE,"E1607"),sQuery(id+"F1.wireOp",EDGE,"E1608"),sQuery(id+"F1.wireOp",EDGE,"E1609"),sQuery(id+"F1.wireOp",EDGE,"E1610"),sQuery(id+"F1.wireOp",EDGE,"E1611"),sQuery(id+"F1.wireOp",EDGE,"E1612"),sQuery(id+"F1.wireOp",EDGE,"E1613"),sQuery(id+"F1.wireOp",EDGE,"E1614"),sQuery(id+"F1.wireOp",EDGE,"E1615"),sQuery(id+"F1.wireOp",EDGE,"E1616"),sQuery(id+"F1.wireOp",EDGE,"E1617"),sQuery(id+"F1.wireOp",EDGE,"E1618"),sQuery(id+"F1.wireOp",EDGE,"E1619"),sQuery(id+"F1.wireOp",EDGE,"E1620"),sQuery(id+"F1.wireOp",EDGE,"E1621"),sQuery(id+"F1.wireOp",EDGE,"E1622"),sQuery(id+"F1.wireOp",EDGE,"E1623"),sQuery(id+"F1.wireOp",EDGE,"E1624"),sQuery(id+"F1.wireOp",EDGE,"E1625"),sQuery(id+"F1.wireOp",EDGE,"E1626"),sQuery(id+"F1.wireOp",EDGE,"E1627"),sQuery(id+"F1.wireOp",EDGE,"E1628"),sQuery(id+"F1.wireOp",EDGE,"E1629"),sQuery(id+"F1.wireOp",EDGE,"E1630"),sQuery(id+"F1.wireOp",EDGE,"E1631"),sQuery(id+"F1.wireOp",EDGE,"E1632"),sQuery(id+"F1.wireOp",EDGE,"E1633"),sQuery(id+"F1.wireOp",EDGE,"E1634"),sQuery(id+"F1.wireOp",EDGE,"E1635"),sQuery(id+"F1.wireOp",EDGE,"E1636"),sQuery(id+"F1.wireOp",EDGE,"E1637"),sQuery(id+"F1.wireOp",EDGE,"E1638"),sQuery(id+"F1.wireOp",EDGE,"E1639"),sQuery(id+"F1.wireOp",EDGE,"E1640"),sQuery(id+"F1.wireOp",EDGE,"E1641"),sQuery(id+"F1.wireOp",EDGE,"E1642"),sQuery(id+"F1.wireOp",EDGE,"E1643"),sQuery(id+"F1.wireOp",EDGE,"E1644"),sQuery(id+"F1.wireOp",EDGE,"E1645"),sQuery(id+"F1.wireOp",EDGE,"E1646"),sQuery(id+"F1.wireOp",EDGE,"E1647"),sQuery(id+"F1.wireOp",EDGE,"E1648"),sQuery(id+"F1.wireOp",EDGE,"E1649"),sQuery(id+"F1.wireOp",EDGE,"E1650"),sQuery(id+"F1.wireOp",EDGE,"E1651"),sQuery(id+"F1.wireOp",EDGE,"E1652"),sQuery(id+"F1.wireOp",EDGE,"E1653"),sQuery(id+"F1.wireOp",EDGE,"E1654"),sQuery(id+"F1.wireOp",EDGE,"E1655"),sQuery(id+"F1.wireOp",EDGE,"E1656"),sQuery(id+"F1.wireOp",EDGE,"E1657"),sQuery(id+"F1.wireOp",EDGE,"E1658"),sQuery(id+"F1.wireOp",EDGE,"E1659"),sQuery(id+"F1.wireOp",EDGE,"E1660"),sQuery(id+"F1.wireOp",EDGE,"E1661"),sQuery(id+"F1.wireOp",EDGE,"E1662"),sQuery(id+"F1.wireOp",EDGE,"E1663"),sQuery(id+"F1.wireOp",EDGE,"E1664"),sQuery(id+"F1.wireOp",EDGE,"E1665"),sQuery(id+"F1.wireOp",EDGE,"E1666"),sQuery(id+"F1.wireOp",EDGE,"E1667"),sQuery(id+"F1.wireOp",EDGE,"E1668"),sQuery(id+"F1.wireOp",EDGE,"E1669"),sQuery(id+"F1.wireOp",EDGE,"E1670"),sQuery(id+"F1.wireOp",EDGE,"E1671"),sQuery(id+"F1.wireOp",EDGE,"E1672"),sQuery(id+"F1.wireOp",EDGE,"E1673"),sQuery(id+"F1.wireOp",EDGE,"E1674"),sQuery(id+"F1.wireOp",EDGE,"E1675"),sQuery(id+"F1.wireOp",EDGE,"E1676"),sQuery(id+"F1.wireOp",EDGE,"E1677"),sQuery(id+"F1.wireOp",EDGE,"E1678"),sQuery(id+"F1.wireOp",EDGE,"E1679"),sQuery(id+"F1.wireOp",EDGE,"E1680"),sQuery(id+"F1.wireOp",EDGE,"E1681"),sQuery(id+"F1.wireOp",EDGE,"E1682"),sQuery(id+"F1.wireOp",EDGE,"E1683"),sQuery(id+"F1.wireOp",EDGE,"E1684"),sQuery(id+"F1.wireOp",EDGE,"E1685"),sQuery(id+"F1.wireOp",EDGE,"E1686"),sQuery(id+"F1.wireOp",EDGE,"E1687"),sQuery(id+"F1.wireOp",EDGE,"E1688"),sQuery(id+"F1.wireOp",EDGE,"E1689"),sQuery(id+"F1.wireOp",EDGE,"E1690"),sQuery(id+"F1.wireOp",EDGE,"E1691"),sQuery(id+"F1.wireOp",EDGE,"E1692"),sQuery(id+"F1.wireOp",EDGE,"E1693"),sQuery(id+"F1.wireOp",EDGE,"E1694"),sQuery(id+"F1.wireOp",EDGE,"E1695"),sQuery(id+"F1.wireOp",EDGE,"E1696"),sQuery(id+"F1.wireOp",EDGE,"E1697"),sQuery(id+"F1.wireOp",EDGE,"E1698"),sQuery(id+"F1.wireOp",EDGE,"E1699"),sQuery(id+"F1.wireOp",EDGE,"E1700"),sQuery(id+"F1.wireOp",EDGE,"E1701"),sQuery(id+"F1.wireOp",EDGE,"E1702"),sQuery(id+"F1.wireOp",EDGE,"E1703"),sQuery(id+"F1.wireOp",EDGE,"E1704"),sQuery(id+"F1.wireOp",EDGE,"E1705"),sQuery(id+"F1.wireOp",EDGE,"E1706"),sQuery(id+"F1.wireOp",EDGE,"E1707"),sQuery(id+"F1.wireOp",EDGE,"E1708"),sQuery(id+"F1.wireOp",EDGE,"E1709"),sQuery(id+"F1.wireOp",EDGE,"E1710"),sQuery(id+"F1.wireOp",EDGE,"E1711"),sQuery(id+"F1.wireOp",EDGE,"E1712"),sQuery(id+"F1.wireOp",EDGE,"E1713"),sQuery(id+"F1.wireOp",EDGE,"E1714"),sQuery(id+"F1.wireOp",EDGE,"E1715"),sQuery(id+"F1.wireOp",EDGE,"E1716"),sQuery(id+"F1.wireOp",EDGE,"E1717"),sQuery(id+"F1.wireOp",EDGE,"E1718"),sQuery(id+"F1.wireOp",EDGE,"E1719"),sQuery(id+"F1.wireOp",EDGE,"E1720"),sQuery(id+"F1.wireOp",EDGE,"E1721"),sQuery(id+"F1.wireOp",EDGE,"E1722"),sQuery(id+"F1.wireOp",EDGE,"E1723"),sQuery(id+"F1.wireOp",EDGE,"E1724"),sQuery(id+"F1.wireOp",EDGE,"E1725"),sQuery(id+"F1.wireOp",EDGE,"E1726"),sQuery(id+"F1.wireOp",EDGE,"E1727"),sQuery(id+"F1.wireOp",EDGE,"E1728"),sQuery(id+"F1.wireOp",EDGE,"E1729"),sQuery(id+"F1.wireOp",EDGE,"E1730"),sQuery(id+"F1.wireOp",EDGE,"E1731"),sQuery(id+"F1.wireOp",EDGE,"E1732"),sQuery(id+"F1.wireOp",EDGE,"E1733"),sQuery(id+"F1.wireOp",EDGE,"E1734"),sQuery(id+"F1.wireOp",EDGE,"E1735"),sQuery(id+"F1.wireOp",EDGE,"E1736"),sQuery(id+"F1.wireOp",EDGE,"E1737"),sQuery(id+"F1.wireOp",EDGE,"E1738"),sQuery(id+"F1.wireOp",EDGE,"E1739"),sQuery(id+"F1.wireOp",EDGE,"E1740"),sQuery(id+"F1.wireOp",EDGE,"E1741"),sQuery(id+"F1.wireOp",EDGE,"E1742"),sQuery(id+"F1.wireOp",EDGE,"E1743"),sQuery(id+"F1.wireOp",EDGE,"E1744"),sQuery(id+"F1.wireOp",EDGE,"E1745"),sQuery(id+"F1.wireOp",EDGE,"E1746"),sQuery(id+"F1.wireOp",EDGE,"E1747"),sQuery(id+"F1.wireOp",EDGE,"E1748"),sQuery(id+"F1.wireOp",EDGE,"E1749"),sQuery(id+"F1.wireOp",EDGE,"E1750"),sQuery(id+"F1.wireOp",EDGE,"E1751"),sQuery(id+"F1.wireOp",EDGE,"E1752"),sQuery(id+"F1.wireOp",EDGE,"E1753"),sQuery(id+"F1.wireOp",EDGE,"E1754"),sQuery(id+"F1.wireOp",EDGE,"E1755"),sQuery(id+"F1.wireOp",EDGE,"E1756"),sQuery(id+"F1.wireOp",EDGE,"E1757"),sQuery(id+"F1.wireOp",EDGE,"E1758"),sQuery(id+"F1.wireOp",EDGE,"E1759"),sQuery(id+"F1.wireOp",EDGE,"E1760"),sQuery(id+"F1.wireOp",EDGE,"E1761"),sQuery(id+"F1.wireOp",EDGE,"E1762"),sQuery(id+"F1.wireOp",EDGE,"E1763"),sQuery(id+"F1.wireOp",EDGE,"E1764"),sQuery(id+"F1.wireOp",EDGE,"E1765"),sQuery(id+"F1.wireOp",EDGE,"E1766"),sQuery(id+"F1.wireOp",EDGE,"E1767"),sQuery(id+"F1.wireOp",EDGE,"E1768"),sQuery(id+"F1.wireOp",EDGE,"E1769"),sQuery(id+"F1.wireOp",EDGE,"E1770"),sQuery(id+"F1.wireOp",EDGE,"E1771"),sQuery(id+"F1.wireOp",EDGE,"E1772"),sQuery(id+"F1.wireOp",EDGE,"E1773"),sQuery(id+"F1.wireOp",EDGE,"E1774"),sQuery(id+"F1.wireOp",EDGE,"E1775"),sQuery(id+"F1.wireOp",EDGE,"E1776"),sQuery(id+"F1.wireOp",EDGE,"E1777"),sQuery(id+"F1.wireOp",EDGE,"E1778"),sQuery(id+"F1.wireOp",EDGE,"E1779"),sQuery(id+"F1.wireOp",EDGE,"E1780"),sQuery(id+"F1.wireOp",EDGE,"E1781"),sQuery(id+"F1.wireOp",EDGE,"E1782"),sQuery(id+"F1.wireOp",EDGE,"E1783"),sQuery(id+"F1.wireOp",EDGE,"E1784"),sQuery(id+"F1.wireOp",EDGE,"E1785"),sQuery(id+"F1.wireOp",EDGE,"E1786"),sQuery(id+"F1.wireOp",EDGE,"E1787"),sQuery(id+"F1.wireOp",EDGE,"E1788"),sQuery(id+"F1.wireOp",EDGE,"E1789"),sQuery(id+"F1.wireOp",EDGE,"E1790"),sQuery(id+"F1.wireOp",EDGE,"E1791"),sQuery(id+"F1.wireOp",EDGE,"E1792"),sQuery(id+"F1.wireOp",EDGE,"E1793"),sQuery(id+"F1.wireOp",EDGE,"E1794"),sQuery(id+"F1.wireOp",EDGE,"E1795"),sQuery(id+"F1.wireOp",EDGE,"E1796"),sQuery(id+"F1.wireOp",EDGE,"E1797"),sQuery(id+"F1.wireOp",EDGE,"E1798"),sQuery(id+"F1.wireOp",EDGE,"E1799"),sQuery(id+"F1.wireOp",EDGE,"E1800"),sQuery(id+"F1.wireOp",EDGE,"E1801"),sQuery(id+"F1.wireOp",EDGE,"E1802"),sQuery(id+"F1.wireOp",EDGE,"E1803"),sQuery(id+"F1.wireOp",EDGE,"E1804"),sQuery(id+"F1.wireOp",EDGE,"E1805"),sQuery(id+"F1.wireOp",EDGE,"E1806"),sQuery(id+"F1.wireOp",EDGE,"E1807"),sQuery(id+"F1.wireOp",EDGE,"E1808"),sQuery(id+"F1.wireOp",EDGE,"E1809"),sQuery(id+"F1.wireOp",EDGE,"E1810"),sQuery(id+"F1.wireOp",EDGE,"E1811"),sQuery(id+"F1.wireOp",EDGE,"E1812"),sQuery(id+"F1.wireOp",EDGE,"E1813"),sQuery(id+"F1.wireOp",EDGE,"E1814"),sQuery(id+"F1.wireOp",EDGE,"E1815"),sQuery(id+"F1.wireOp",EDGE,"E1816"),sQuery(id+"F1.wireOp",EDGE,"E1817"),sQuery(id+"F1.wireOp",EDGE,"E1818"),sQuery(id+"F1.wireOp",EDGE,"E1819"),sQuery(id+"F1.wireOp",EDGE,"E1820"),sQuery(id+"F1.wireOp",EDGE,"E1821"),sQuery(id+"F1.wireOp",EDGE,"E1822"),sQuery(id+"F1.wireOp",EDGE,"E1823"),sQuery(id+"F1.wireOp",EDGE,"E1824"),sQuery(id+"F1.wireOp",EDGE,"E1825"),sQuery(id+"F1.wireOp",EDGE,"E1826"),sQuery(id+"F1.wireOp",EDGE,"E1827"),sQuery(id+"F1.wireOp",EDGE,"E1828"),sQuery(id+"F1.wireOp",EDGE,"E1829"),sQuery(id+"F1.wireOp",EDGE,"E1830"),sQuery(id+"F1.wireOp",EDGE,"E1831"),sQuery(id+"F1.wireOp",EDGE,"E1832"),sQuery(id+"F1.wireOp",EDGE,"E1833"),sQuery(id+"F1.wireOp",EDGE,"E1834"),sQuery(id+"F1.wireOp",EDGE,"E1835"),sQuery(id+"F1.wireOp",EDGE,"E1836"),sQuery(id+"F1.wireOp",EDGE,"E1837"),sQuery(id+"F1.wireOp",EDGE,"E1838"),sQuery(id+"F1.wireOp",EDGE,"E1839"),sQuery(id+"F1.wireOp",EDGE,"E1840"),sQuery(id+"F1.wireOp",EDGE,"E1841"),sQuery(id+"F1.wireOp",EDGE,"E1842"),sQuery(id+"F1.wireOp",EDGE,"E1843"),sQuery(id+"F1.wireOp",EDGE,"E1844"),sQuery(id+"F1.wireOp",EDGE,"E1845"),sQuery(id+"F1.wireOp",EDGE,"E1846"),sQuery(id+"F1.wireOp",EDGE,"E1847"),sQuery(id+"F1.wireOp",EDGE,"E1848"),sQuery(id+"F1.wireOp",EDGE,"E1849"),sQuery(id+"F1.wireOp",EDGE,"E1850"),sQuery(id+"F1.wireOp",EDGE,"E1851"),sQuery(id+"F1.wireOp",EDGE,"E1852"),sQuery(id+"F1.wireOp",EDGE,"E1853"),sQuery(id+"F1.wireOp",EDGE,"E1854"),sQuery(id+"F1.wireOp",EDGE,"E1855"),sQuery(id+"F1.wireOp",EDGE,"E1856"),sQuery(id+"F1.wireOp",EDGE,"E1857"),sQuery(id+"F1.wireOp",EDGE,"E1858"),sQuery(id+"F1.wireOp",EDGE,"E1859"),sQuery(id+"F1.wireOp",EDGE,"E1860"),sQuery(id+"F1.wireOp",EDGE,"E1861"),sQuery(id+"F1.wireOp",EDGE,"E1862"),sQuery(id+"F1.wireOp",EDGE,"E1863"),sQuery(id+"F1.wireOp",EDGE,"E1864"),sQuery(id+"F1.wireOp",EDGE,"E1865"),sQuery(id+"F1.wireOp",EDGE,"E1866"),sQuery(id+"F1.wireOp",EDGE,"E1867"),sQuery(id+"F1.wireOp",EDGE,"E1868"),sQuery(id+"F1.wireOp",EDGE,"E1869"),sQuery(id+"F1.wireOp",EDGE,"E1870"),sQuery(id+"F1.wireOp",EDGE,"E1871"),sQuery(id+"F1.wireOp",EDGE,"E1872"),sQuery(id+"F1.wireOp",EDGE,"E1873"),sQuery(id+"F1.wireOp",EDGE,"E1874"),sQuery(id+"F1.wireOp",EDGE,"E1875"),sQuery(id+"F1.wireOp",EDGE,"E1876"),sQuery(id+"F1.wireOp",EDGE,"E1877"),sQuery(id+"F1.wireOp",EDGE,"E1878"),sQuery(id+"F1.wireOp",EDGE,"E1879"),sQuery(id+"F1.wireOp",EDGE,"E1880"),sQuery(id+"F1.wireOp",EDGE,"E1881"),sQuery(id+"F1.wireOp",EDGE,"E1882"),sQuery(id+"F1.wireOp",EDGE,"E1883"),sQuery(id+"F1.wireOp",EDGE,"E1884"),sQuery(id+"F1.wireOp",EDGE,"E1885"),sQuery(id+"F1.wireOp",EDGE,"E1886"),sQuery(id+"F1.wireOp",EDGE,"E1887"),sQuery(id+"F1.wireOp",EDGE,"E1888"),sQuery(id+"F1.wireOp",EDGE,"E1889"),sQuery(id+"F1.wireOp",EDGE,"E1890"),sQuery(id+"F1.wireOp",EDGE,"E1891"),sQuery(id+"F1.wireOp",EDGE,"E1892"),sQuery(id+"F1.wireOp",EDGE,"E1893"),sQuery(id+"F1.wireOp",EDGE,"E1894"),sQuery(id+"F1.wireOp",EDGE,"E1895"),sQuery(id+"F1.wireOp",EDGE,"E1896"),sQuery(id+"F1.wireOp",EDGE,"E1897"),sQuery(id+"F1.wireOp",EDGE,"E1898"),sQuery(id+"F1.wireOp",EDGE,"E1899"),sQuery(id+"F1.wireOp",EDGE,"E1900"),sQuery(id+"F1.wireOp",EDGE,"E1901"),sQuery(id+"F1.wireOp",EDGE,"E1902"),sQuery(id+"F1.wireOp",EDGE,"E1903"),sQuery(id+"F1.wireOp",EDGE,"E1904"),sQuery(id+"F1.wireOp",EDGE,"E1905"),sQuery(id+"F1.wireOp",EDGE,"E1906"),sQuery(id+"F1.wireOp",EDGE,"E1907"),sQuery(id+"F1.wireOp",EDGE,"E1908"),sQuery(id+"F1.wireOp",EDGE,"E1909"),sQuery(id+"F1.wireOp",EDGE,"E1910"),sQuery(id+"F1.wireOp",EDGE,"E1911"),sQuery(id+"F1.wireOp",EDGE,"E1912"),sQuery(id+"F1.wireOp",EDGE,"E1913"),sQuery(id+"F1.wireOp",EDGE,"E1914"),sQuery(id+"F1.wireOp",EDGE,"E1915"),sQuery(id+"F1.wireOp",EDGE,"E1916"),sQuery(id+"F1.wireOp",EDGE,"E1917"),sQuery(id+"F1.wireOp",EDGE,"E1918"),sQuery(id+"F1.wireOp",EDGE,"E1919"),sQuery(id+"F1.wireOp",EDGE,"E1920"),sQuery(id+"F1.wireOp",EDGE,"E1921"),sQuery(id+"F1.wireOp",EDGE,"E1922"),sQuery(id+"F1.wireOp",EDGE,"E1923"),sQuery(id+"F1.wireOp",EDGE,"E1924"),sQuery(id+"F1.wireOp",EDGE,"E1925"),sQuery(id+"F1.wireOp",EDGE,"E1926"),sQuery(id+"F1.wireOp",EDGE,"E1927"),sQuery(id+"F1.wireOp",EDGE,"E1928"),sQuery(id+"F1.wireOp",EDGE,"E1929"),sQuery(id+"F1.wireOp",EDGE,"E1930"),sQuery(id+"F1.wireOp",EDGE,"E1931"),sQuery(id+"F1.wireOp",EDGE,"E1932"),sQuery(id+"F1.wireOp",EDGE,"E1933"),sQuery(id+"F1.wireOp",EDGE,"E1934"),sQuery(id+"F1.wireOp",EDGE,"E1935"),sQuery(id+"F1.wireOp",EDGE,"E1936"),sQuery(id+"F1.wireOp",EDGE,"E1937"),sQuery(id+"F1.wireOp",EDGE,"E1938"),sQuery(id+"F1.wireOp",EDGE,"E1939"),sQuery(id+"F1.wireOp",EDGE,"E1940"),sQuery(id+"F1.wireOp",EDGE,"E1941"),sQuery(id+"F1.wireOp",EDGE,"E1942"),sQuery(id+"F1.wireOp",EDGE,"E1943"),sQuery(id+"F1.wireOp",EDGE,"E1944"),sQuery(id+"F1.wireOp",EDGE,"E1945"),sQuery(id+"F1.wireOp",EDGE,"E1946"),sQuery(id+"F1.wireOp",EDGE,"E1947"),sQuery(id+"F1.wireOp",EDGE,"E1948"),sQuery(id+"F1.wireOp",EDGE,"E1949"),sQuery(id+"F1.wireOp",EDGE,"E1950"),sQuery(id+"F1.wireOp",EDGE,"E1951"),sQuery(id+"F1.wireOp",EDGE,"E1952"),sQuery(id+"F1.wireOp",EDGE,"E1953"),sQuery(id+"F1.wireOp",EDGE,"E1954"),sQuery(id+"F1.wireOp",EDGE,"E1955"),sQuery(id+"F1.wireOp",EDGE,"E1956"),sQuery(id+"F1.wireOp",EDGE,"E1957"),sQuery(id+"F1.wireOp",EDGE,"E1958"),sQuery(id+"F1.wireOp",EDGE,"E1959"),sQuery(id+"F1.wireOp",EDGE,"E1960"),sQuery(id+"F1.wireOp",EDGE,"E1961"),sQuery(id+"F1.wireOp",EDGE,"E1962"),sQuery(id+"F1.wireOp",EDGE,"E1963"),sQuery(id+"F1.wireOp",EDGE,"E1964"),sQuery(id+"F1.wireOp",EDGE,"E1965"),sQuery(id+"F1.wireOp",EDGE,"E1966"),sQuery(id+"F1.wireOp",EDGE,"E1967"),sQuery(id+"F1.wireOp",EDGE,"E1968"),sQuery(id+"F1.wireOp",EDGE,"E1969"),sQuery(id+"F1.wireOp",EDGE,"E1970"),sQuery(id+"F1.wireOp",EDGE,"E1971"),sQuery(id+"F1.wireOp",EDGE,"E1972"),sQuery(id+"F1.wireOp",EDGE,"E1973"),sQuery(id+"F1.wireOp",EDGE,"E1974"),sQuery(id+"F1.wireOp",EDGE,"E1975"),sQuery(id+"F1.wireOp",EDGE,"E1976"),sQuery(id+"F1.wireOp",EDGE,"E1977"),sQuery(id+"F1.wireOp",EDGE,"E1978"),sQuery(id+"F1.wireOp",EDGE,"E1979"),sQuery(id+"F1.wireOp",EDGE,"E1980"),sQuery(id+"F1.wireOp",EDGE,"E1981"),sQuery(id+"F1.wireOp",EDGE,"E1982"),sQuery(id+"F1.wireOp",EDGE,"E1983"),sQuery(id+"F1.wireOp",EDGE,"E1984"),sQuery(id+"F1.wireOp",EDGE,"E1985"),sQuery(id+"F1.wireOp",EDGE,"E1986"),sQuery(id+"F1.wireOp",EDGE,"E1987"),sQuery(id+"F1.wireOp",EDGE,"E1988"),sQuery(id+"F1.wireOp",EDGE,"E1989"),sQuery(id+"F1.wireOp",EDGE,"E1990"),sQuery(id+"F1.wireOp",EDGE,"E1991"),sQuery(id+"F1.wireOp",EDGE,"E1992"),sQuery(id+"F1.wireOp",EDGE,"E1993"),sQuery(id+"F1.wireOp",EDGE,"E1994"),sQuery(id+"F1.wireOp",EDGE,"E1995"),sQuery(id+"F1.wireOp",EDGE,"E1996"),sQuery(id+"F1.wireOp",EDGE,"E1997"),sQuery(id+"F1.wireOp",EDGE,"E1998"),sQuery(id+"F1.wireOp",EDGE,"E1999"),sQuery(id+"F1.wireOp",EDGE,"E2000"),sQuery(id+"F1.wireOp",EDGE,"E2000"),sQuery(id+"F1.wireOp",EDGE,"E2001"),sQuery(id+"F1.wireOp",EDGE,"E2002"),sQuery(id+"F1.wireOp",EDGE,"E2003"),sQuery(id+"F1.wireOp",EDGE,"E2004"),sQuery(id+"F1.wireOp",EDGE,"E2005"),sQuery(id+"F1.wireOp",EDGE,"E2006"),sQuery(id+"F1.wireOp",EDGE,"E2007"),sQuery(id+"F1.wireOp",EDGE,"E2008"),sQuery(id+"F1.wireOp",EDGE,"E2009"),sQuery(id+"F1.wireOp",EDGE,"E2010"),sQuery(id+"F1.wireOp",EDGE,"E2011"),sQuery(id+"F1.wireOp",EDGE,"E2012"),sQuery(id+"F1.wireOp",EDGE,"E2013"),sQuery(id+"F1.wireOp",EDGE,"E2014"),sQuery(id+"F1.wireOp",EDGE,"E2015"),sQuery(id+"F1.wireOp",EDGE,"E2016"),sQuery(id+"F1.wireOp",EDGE,"E2017"),sQuery(id+"F1.wireOp",EDGE,"E2018"),sQuery(id+"F1.wireOp",EDGE,"E2019"),sQuery(id+"F1.wireOp",EDGE,"E2020"),sQuery(id+"F1.wireOp",EDGE,"E2021"),sQuery(id+"F1.wireOp",EDGE,"E2022"),sQuery(id+"F1.wireOp",EDGE,"E2023"),sQuery(id+"F1.wireOp",EDGE,"E2024"),sQuery(id+"F1.wireOp",EDGE,"E2025"),sQuery(id+"F1.wireOp",EDGE,"E2026"),sQuery(id+"F1.wireOp",EDGE,"E2027"),sQuery(id+"F1.wireOp",EDGE,"E2028"),sQuery(id+"F1.wireOp",EDGE,"E2029"),sQuery(id+"F1.wireOp",EDGE,"E2030"),sQuery(id+"F1.wireOp",EDGE,"E2031"),sQuery(id+"F1.wireOp",EDGE,"E2032"),sQuery(id+"F1.wireOp",EDGE,"E2033"),sQuery(id+"F1.wireOp",EDGE,"E2034"),sQuery(id+"F1.wireOp",EDGE,"E2035"),sQuery(id+"F1.wireOp",EDGE,"E2036"),sQuery(id+"F1.wireOp",EDGE,"E2037"),sQuery(id+"F1.wireOp",EDGE,"E2038"),sQuery(id+"F1.wireOp",EDGE,"E2039"),sQuery(id+"F1.wireOp",EDGE,"E2040"),sQuery(id+"F1.wireOp",EDGE,"E2041"),sQuery(id+"F1.wireOp",EDGE,"E2042"),sQuery(id+"F1.wireOp",EDGE,"E2043"),sQuery(id+"F1.wireOp",EDGE,"E2044"),sQuery(id+"F1.wireOp",EDGE,"E2045"),sQuery(id+"F1.wireOp",EDGE,"E2046"),sQuery(id+"F1.wireOp",EDGE,"E2047"),sQuery(id+"F1.wireOp",EDGE,"E2048"),sQuery(id+"F1.wireOp",EDGE,"E2049"),sQuery(id+"F1.wireOp",EDGE,"E2050"),sQuery(id+"F1.wireOp",EDGE,"E2051"),sQuery(id+"F1.wireOp",EDGE,"E2052"),sQuery(id+"F1.wireOp",EDGE,"E2053"),sQuery(id+"F1.wireOp",EDGE,"E2054"),sQuery(id+"F1.wireOp",EDGE,"E2055"),sQuery(id+"F1.wireOp",EDGE,"E2056"),sQuery(id+"F1.wireOp",EDGE,"E2057"),sQuery(id+"F1.wireOp",EDGE,"E2058"),sQuery(id+"F1.wireOp",EDGE,"E2059"),sQuery(id+"F1.wireOp",EDGE,"E2060"),sQuery(id+"F1.wireOp",EDGE,"E2061"),sQuery(id+"F1.wireOp",EDGE,"E2062"),sQuery(id+"F1.wireOp",EDGE,"E2063"),sQuery(id+"F1.wireOp",EDGE,"E2064"),sQuery(id+"F1.wireOp",EDGE,"E2065"),sQuery(id+"F1.wireOp",EDGE,"E2066"),sQuery(id+"F1.wireOp",EDGE,"E2067"),sQuery(id+"F1.wireOp",EDGE,"E2068"),sQuery(id+"F1.wireOp",EDGE,"E2069"),sQuery(id+"F1.wireOp",EDGE,"E2070"),sQuery(id+"F1.wireOp",EDGE,"E2071"),sQuery(id+"F1.wireOp",EDGE,"E2072"),sQuery(id+"F1.wireOp",EDGE,"E2073"),sQuery(id+"F1.wireOp",EDGE,"E2074"),sQuery(id+"F1.wireOp",EDGE,"E2075"),sQuery(id+"F1.wireOp",EDGE,"E2076"),sQuery(id+"F1.wireOp",EDGE,"E2077"),sQuery(id+"F1.wireOp",EDGE,"E2078"),sQuery(id+"F1.wireOp",EDGE,"E2079"),sQuery(id+"F1.wireOp",EDGE,"E2080"),sQuery(id+"F1.wireOp",EDGE,"E2081"),sQuery(id+"F1.wireOp",EDGE,"E2082"),sQuery(id+"F1.wireOp",EDGE,"E2083"),sQuery(id+"F1.wireOp",EDGE,"E2084"),sQuery(id+"F1.wireOp",EDGE,"E2085"),sQuery(id+"F1.wireOp",EDGE,"E2086"),sQuery(id+"F1.wireOp",EDGE,"E2087"),sQuery(id+"F1.wireOp",EDGE,"E2088"),sQuery(id+"F1.wireOp",EDGE,"E2089"),sQuery(id+"F1.wireOp",EDGE,"E2090"),sQuery(id+"F1.wireOp",EDGE,"E2091"),sQuery(id+"F1.wireOp",EDGE,"E2092"),sQuery(id+"F1.wireOp",EDGE,"E2093"),sQuery(id+"F1.wireOp",EDGE,"E2094"),sQuery(id+"F1.wireOp",EDGE,"E2095"),sQuery(id+"F1.wireOp",EDGE,"E2096"),sQuery(id+"F1.wireOp",EDGE,"E2097"),sQuery(id+"F1.wireOp",EDGE,"E2098"),sQuery(id+"F1.wireOp",EDGE,"E2099"),sQuery(id+"F1.wireOp",EDGE,"E2100"),sQuery(id+"F1.wireOp",EDGE,"E2101"),sQuery(id+"F1.wireOp",EDGE,"E2102"),sQuery(id+"F1.wireOp",EDGE,"E2103"),sQuery(id+"F1.wireOp",EDGE,"E2104"),sQuery(id+"F1.wireOp",EDGE,"E2105"),sQuery(id+"F1.wireOp",EDGE,"E2106"),sQuery(id+"F1.wireOp",EDGE,"E2107"),sQuery(id+"F1.wireOp",EDGE,"E2108"),sQuery(id+"F1.wireOp",EDGE,"E2109"),sQuery(id+"F1.wireOp",EDGE,"E2110"),sQuery(id+"F1.wireOp",EDGE,"E2111"),sQuery(id+"F1.wireOp",EDGE,"E2112"),sQuery(id+"F1.wireOp",EDGE,"E2113"),sQuery(id+"F1.wireOp",EDGE,"E2114"),sQuery(id+"F1.wireOp",EDGE,"E2115"),sQuery(id+"F1.wireOp",EDGE,"E2116"),sQuery(id+"F1.wireOp",EDGE,"E2117"),sQuery(id+"F1.wireOp",EDGE,"E2118"),sQuery(id+"F1.wireOp",EDGE,"E2119"),sQuery(id+"F1.wireOp",EDGE,"E2120"),sQuery(id+"F1.wireOp",EDGE,"E2121"),sQuery(id+"F1.wireOp",EDGE,"E2122"),sQuery(id+"F1.wireOp",EDGE,"E2123"),sQuery(id+"F1.wireOp",EDGE,"E2124"),sQuery(id+"F1.wireOp",EDGE,"E2125"),sQuery(id+"F1.wireOp",EDGE,"E2126"),sQuery(id+"F1.wireOp",EDGE,"E2127"),sQuery(id+"F1.wireOp",EDGE,"E2128"),sQuery(id+"F1.wireOp",EDGE,"E2129"),sQuery(id+"F1.wireOp",EDGE,"E2130"),sQuery(id+"F1.wireOp",EDGE,"E2131"),sQuery(id+"F1.wireOp",EDGE,"E2132"),sQuery(id+"F1.wireOp",EDGE,"E2133"),sQuery(id+"F1.wireOp",EDGE,"E2134"),sQuery(id+"F1.wireOp",EDGE,"E2135"),sQuery(id+"F1.wireOp",EDGE,"E2136"),sQuery(id+"F1.wireOp",EDGE,"E2137"),sQuery(id+"F1.wireOp",EDGE,"E2138"),sQuery(id+"F1.wireOp",EDGE,"E2139"),sQuery(id+"F1.wireOp",EDGE,"E2140"),sQuery(id+"F1.wireOp",EDGE,"E2141"),sQuery(id+"F1.wireOp",EDGE,"E2142"),sQuery(id+"F1.wireOp",EDGE,"E2143"),sQuery(id+"F1.wireOp",EDGE,"E2144"),sQuery(id+"F1.wireOp",EDGE,"E2145"),sQuery(id+"F1.wireOp",EDGE,"E2146"),sQuery(id+"F1.wireOp",EDGE,"E2147"),sQuery(id+"F1.wireOp",EDGE,"E2148"),sQuery(id+"F1.wireOp",EDGE,"E2149"),sQuery(id+"F1.wireOp",EDGE,"E2150"),sQuery(id+"F1.wireOp",EDGE,"E2151"),sQuery(id+"F1.wireOp",EDGE,"E2152"),sQuery(id+"F1.wireOp",EDGE,"E2153"),sQuery(id+"F1.wireOp",EDGE,"E2154"),sQuery(id+"F1.wireOp",EDGE,"E2155"),sQuery(id+"F1.wireOp",EDGE,"E2156"),sQuery(id+"F1.wireOp",EDGE,"E2157"),sQuery(id+"F1.wireOp",EDGE,"E2158"),sQuery(id+"F1.wireOp",EDGE,"E2159"),sQuery(id+"F1.wireOp",EDGE,"E2160"),sQuery(id+"F1.wireOp",EDGE,"E2161"),sQuery(id+"F1.wireOp",EDGE,"E2162"),sQuery(id+"F1.wireOp",EDGE,"E2163"),sQuery(id+"F1.wireOp",EDGE,"E2164"),sQuery(id+"F1.wireOp",EDGE,"E2165"),sQuery(id+"F1.wireOp",EDGE,"E2166"),sQuery(id+"F1.wireOp",EDGE,"E2167"),sQuery(id+"F1.wireOp",EDGE,"E2168"),sQuery(id+"F1.wireOp",EDGE,"E2169"),sQuery(id+"F1.wireOp",EDGE,"E2170"),sQuery(id+"F1.wireOp",EDGE,"E2171"),sQuery(id+"F1.wireOp",EDGE,"E2172"),sQuery(id+"F1.wireOp",EDGE,"E2173"),sQuery(id+"F1.wireOp",EDGE,"E2174"),sQuery(id+"F1.wireOp",EDGE,"E2175"),sQuery(id+"F1.wireOp",EDGE,"E2176"),sQuery(id+"F1.wireOp",EDGE,"E2177"),sQuery(id+"F1.wireOp",EDGE,"E2178"),sQuery(id+"F1.wireOp",EDGE,"E2179"),sQuery(id+"F1.wireOp",EDGE,"E2180"),sQuery(id+"F1.wireOp",EDGE,"E2181"),sQuery(id+"F1.wireOp",EDGE,"E2182"),sQuery(id+"F1.wireOp",EDGE,"E2183"),sQuery(id+"F1.wireOp",EDGE,"E2184"),sQuery(id+"F1.wireOp",EDGE,"E2185"),sQuery(id+"F1.wireOp",EDGE,"E2186"),sQuery(id+"F1.wireOp",EDGE,"E2187"),sQuery(id+"F1.wireOp",EDGE,"E2188"),sQuery(id+"F1.wireOp",EDGE,"E2189"),sQuery(id+"F1.wireOp",EDGE,"E2190"),sQuery(id+"F1.wireOp",EDGE,"E2191"),sQuery(id+"F1.wireOp",EDGE,"E2192"),sQuery(id+"F1.wireOp",EDGE,"E2193"),sQuery(id+"F1.wireOp",EDGE,"E2194"),sQuery(id+"F1.wireOp",EDGE,"E2195"),sQuery(id+"F1.wireOp",EDGE,"E2196"),sQuery(id+"F1.wireOp",EDGE,"E2197"),sQuery(id+"F1.wireOp",EDGE,"E2198"),sQuery(id+"F1.wireOp",EDGE,"E2199"),sQuery(id+"F1.wireOp",EDGE,"E2200"),sQuery(id+"F1.wireOp",EDGE,"E2201"),sQuery(id+"F1.wireOp",EDGE,"E2202"),sQuery(id+"F1.wireOp",EDGE,"E2203"),sQuery(id+"F1.wireOp",EDGE,"E2204"),sQuery(id+"F1.wireOp",EDGE,"E2205"),sQuery(id+"F1.wireOp",EDGE,"E2206"),sQuery(id+"F1.wireOp",EDGE,"E2207"),sQuery(id+"F1.wireOp",EDGE,"E2208"),sQuery(id+"F1.wireOp",EDGE,"E2209"),sQuery(id+"F1.wireOp",EDGE,"E2210"),sQuery(id+"F1.wireOp",EDGE,"E2211"),sQuery(id+"F1.wireOp",EDGE,"E2212"),sQuery(id+"F1.wireOp",EDGE,"E2213"),sQuery(id+"F1.wireOp",EDGE,"E2214"),sQuery(id+"F1.wireOp",EDGE,"E2215"),sQuery(id+"F1.wireOp",EDGE,"E2216"),sQuery(id+"F1.wireOp",EDGE,"E2217"),sQuery(id+"F1.wireOp",EDGE,"E2218"),sQuery(id+"F1.wireOp",EDGE,"E2219"),sQuery(id+"F1.wireOp",EDGE,"E2220"),sQuery(id+"F1.wireOp",EDGE,"E2221"),sQuery(id+"F1.wireOp",EDGE,"E2222"),sQuery(id+"F1.wireOp",EDGE,"E2223"),sQuery(id+"F1.wireOp",EDGE,"E2224"),sQuery(id+"F1.wireOp",EDGE,"E2225"),sQuery(id+"F1.wireOp",EDGE,"E2226"),sQuery(id+"F1.wireOp",EDGE,"E2227"),sQuery(id+"F1.wireOp",EDGE,"E2228"),sQuery(id+"F1.wireOp",EDGE,"E2229"),sQuery(id+"F1.wireOp",EDGE,"E2230"),sQuery(id+"F1.wireOp",EDGE,"E2231"),sQuery(id+"F1.wireOp",EDGE,"E2232"),sQuery(id+"F1.wireOp",EDGE,"E2233"),sQuery(id+"F1.wireOp",EDGE,"E2234"),sQuery(id+"F1.wireOp",EDGE,"E2235"),sQuery(id+"F1.wireOp",EDGE,"E2236"),sQuery(id+"F1.wireOp",EDGE,"E2237"),sQuery(id+"F1.wireOp",EDGE,"E2238"),sQuery(id+"F1.wireOp",EDGE,"E2239"),sQuery(id+"F1.wireOp",EDGE,"E2240"),sQuery(id+"F1.wireOp",EDGE,"E2241"),sQuery(id+"F1.wireOp",EDGE,"E2242"),sQuery(id+"F1.wireOp",EDGE,"E2243"),sQuery(id+"F1.wireOp",EDGE,"E2244"),sQuery(id+"F1.wireOp",EDGE,"E2245"),sQuery(id+"F1.wireOp",EDGE,"E2246"),sQuery(id+"F1.wireOp",EDGE,"E2247"),sQuery(id+"F1.wireOp",EDGE,"E2248"),sQuery(id+"F1.wireOp",EDGE,"E2249"),sQuery(id+"F1.wireOp",EDGE,"E2250"),sQuery(id+"F1.wireOp",EDGE,"E2251"),sQuery(id+"F1.wireOp",EDGE,"E2252"),sQuery(id+"F1.wireOp",EDGE,"E2253"),sQuery(id+"F1.wireOp",EDGE,"E2254"),sQuery(id+"F1.wireOp",EDGE,"E2255"),sQuery(id+"F1.wireOp",EDGE,"E2256"),sQuery(id+"F1.wireOp",EDGE,"E2257"),sQuery(id+"F1.wireOp",EDGE,"E2258"),sQuery(id+"F1.wireOp",EDGE,"E2259"),sQuery(id+"F1.wireOp",EDGE,"E2260"),sQuery(id+"F1.wireOp",EDGE,"E2261"),sQuery(id+"F1.wireOp",EDGE,"E2262"),sQuery(id+"F1.wireOp",EDGE,"E2263"),sQuery(id+"F1.wireOp",EDGE,"E2264"),sQuery(id+"F1.wireOp",EDGE,"E2265"),sQuery(id+"F1.wireOp",EDGE,"E2266"),sQuery(id+"F1.wireOp",EDGE,"E2267"),sQuery(id+"F1.wireOp",EDGE,"E2268"),sQuery(id+"F1.wireOp",EDGE,"E2269"),sQuery(id+"F1.wireOp",EDGE,"E2270"),sQuery(id+"F1.wireOp",EDGE,"E2271"),sQuery(id+"F1.wireOp",EDGE,"E2272"),sQuery(id+"F1.wireOp",EDGE,"E2273"),sQuery(id+"F1.wireOp",EDGE,"E2274"),sQuery(id+"F1.wireOp",EDGE,"E2275"),sQuery(id+"F1.wireOp",EDGE,"E2276"),sQuery(id+"F1.wireOp",EDGE,"E2277"),sQuery(id+"F1.wireOp",EDGE,"E2278"),sQuery(id+"F1.wireOp",EDGE,"E2279"),sQuery(id+"F1.wireOp",EDGE,"E2280"),sQuery(id+"F1.wireOp",EDGE,"E2281"),sQuery(id+"F1.wireOp",EDGE,"E2282"),sQuery(id+"F1.wireOp",EDGE,"E2283"),sQuery(id+"F1.wireOp",EDGE,"E2284"),sQuery(id+"F1.wireOp",EDGE,"E2285"),sQuery(id+"F1.wireOp",EDGE,"E2286"),sQuery(id+"F1.wireOp",EDGE,"E2287"),sQuery(id+"F1.wireOp",EDGE,"E2288"),sQuery(id+"F1.wireOp",EDGE,"E2289"),sQuery(id+"F1.wireOp",EDGE,"E2290"),sQuery(id+"F1.wireOp",EDGE,"E2291"),sQuery(id+"F1.wireOp",EDGE,"E2292"),sQuery(id+"F1.wireOp",EDGE,"E2293"),sQuery(id+"F1.wireOp",EDGE,"E2294"),sQuery(id+"F1.wireOp",EDGE,"E2295"),sQuery(id+"F1.wireOp",EDGE,"E2296"),sQuery(id+"F1.wireOp",EDGE,"E2297"),sQuery(id+"F1.wireOp",EDGE,"E2298"),sQuery(id+"F1.wireOp",EDGE,"E2299"),sQuery(id+"F1.wireOp",EDGE,"E2300"),sQuery(id+"F1.wireOp",EDGE,"E2301"),sQuery(id+"F1.wireOp",EDGE,"E2302"),sQuery(id+"F1.wireOp",EDGE,"E2303"),sQuery(id+"F1.wireOp",EDGE,"E2304"),sQuery(id+"F1.wireOp",EDGE,"E2305"),sQuery(id+"F1.wireOp",EDGE,"E2306"),sQuery(id+"F1.wireOp",EDGE,"E2307"),sQuery(id+"F1.wireOp",EDGE,"E2308"),sQuery(id+"F1.wireOp",EDGE,"E2309"),sQuery(id+"F1.wireOp",EDGE,"E2310"),sQuery(id+"F1.wireOp",EDGE,"E2311"),sQuery(id+"F1.wireOp",EDGE,"E2312"),sQuery(id+"F1.wireOp",EDGE,"E2313"),sQuery(id+"F1.wireOp",EDGE,"E2314"),sQuery(id+"F1.wireOp",EDGE,"E2315"),sQuery(id+"F1.wireOp",EDGE,"E2316"),sQuery(id+"F1.wireOp",EDGE,"E2317"),sQuery(id+"F1.wireOp",EDGE,"E2318"),sQuery(id+"F1.wireOp",EDGE,"E2319"),sQuery(id+"F1.wireOp",EDGE,"E2320"),sQuery(id+"F1.wireOp",EDGE,"E2321"),sQuery(id+"F1.wireOp",EDGE,"E2322"),sQuery(id+"F1.wireOp",EDGE,"E2323"),sQuery(id+"F1.wireOp",EDGE,"E2324"),sQuery(id+"F1.wireOp",EDGE,"E2325"),sQuery(id+"F1.wireOp",EDGE,"E2326"),sQuery(id+"F1.wireOp",EDGE,"E2327"),sQuery(id+"F1.wireOp",EDGE,"E2328"),sQuery(id+"F1.wireOp",EDGE,"E2329"),sQuery(id+"F1.wireOp",EDGE,"E2330"),sQuery(id+"F1.wireOp",EDGE,"E2331"),sQuery(id+"F1.wireOp",EDGE,"E2332"),sQuery(id+"F1.wireOp",EDGE,"E2333"),sQuery(id+"F1.wireOp",EDGE,"E2334"),sQuery(id+"F1.wireOp",EDGE,"E2335"),sQuery(id+"F1.wireOp",EDGE,"E2336"),sQuery(id+"F1.wireOp",EDGE,"E2337"),sQuery(id+"F1.wireOp",EDGE,"E2338"),sQuery(id+"F1.wireOp",EDGE,"E2339"),sQuery(id+"F1.wireOp",EDGE,"E2340"),sQuery(id+"F1.wireOp",EDGE,"E2341"),sQuery(id+"F1.wireOp",EDGE,"E2342"),sQuery(id+"F1.wireOp",EDGE,"E2343"),sQuery(id+"F1.wireOp",EDGE,"E2344"),sQuery(id+"F1.wireOp",EDGE,"E2345"),sQuery(id+"F1.wireOp",EDGE,"E2346"),sQuery(id+"F1.wireOp",EDGE,"E2347"),sQuery(id+"F1.wireOp",EDGE,"E2348"),sQuery(id+"F1.wireOp",EDGE,"E2349"),sQuery(id+"F1.wireOp",EDGE,"E2350"),sQuery(id+"F1.wireOp",EDGE,"E2351"),sQuery(id+"F1.wireOp",EDGE,"E2352"),sQuery(id+"F1.wireOp",EDGE,"E2353"),sQuery(id+"F1.wireOp",EDGE,"E2354"),sQuery(id+"F1.wireOp",EDGE,"E2355"),sQuery(id+"F1.wireOp",EDGE,"E2356"),sQuery(id+"F1.wireOp",EDGE,"E2357"),sQuery(id+"F1.wireOp",EDGE,"E2358"),sQuery(id+"F1.wireOp",EDGE,"E2359"),sQuery(id+"F1.wireOp",EDGE,"E2360"),sQuery(id+"F1.wireOp",EDGE,"E2361"),sQuery(id+"F1.wireOp",EDGE,"E2362"),sQuery(id+"F1.wireOp",EDGE,"E2363"),sQuery(id+"F1.wireOp",EDGE,"E2364"),sQuery(id+"F1.wireOp",EDGE,"E2365"),sQuery(id+"F1.wireOp",EDGE,"E2366"),sQuery(id+"F1.wireOp",EDGE,"E2367"),sQuery(id+"F1.wireOp",EDGE,"E2368"),sQuery(id+"F1.wireOp",EDGE,"E2369"),sQuery(id+"F1.wireOp",EDGE,"E2370"),sQuery(id+"F1.wireOp",EDGE,"E2371"),sQuery(id+"F1.wireOp",EDGE,"E2372"),sQuery(id+"F1.wireOp",EDGE,"E2373"),sQuery(id+"F1.wireOp",EDGE,"E2374"),sQuery(id+"F1.wireOp",EDGE,"E2375"),sQuery(id+"F1.wireOp",EDGE,"E2376"),sQuery(id+"F1.wireOp",EDGE,"E2377"),sQuery(id+"F1.wireOp",EDGE,"E2378"),sQuery(id+"F1.wireOp",EDGE,"E2379"),sQuery(id+"F1.wireOp",EDGE,"E2380"),sQuery(id+"F1.wireOp",EDGE,"E2381"),sQuery(id+"F1.wireOp",EDGE,"E2382"),sQuery(id+"F1.wireOp",EDGE,"E2383"),sQuery(id+"F1.wireOp",EDGE,"E2384"),sQuery(id+"F1.wireOp",EDGE,"E2385"),sQuery(id+"F1.wireOp",EDGE,"E2386"),sQuery(id+"F1.wireOp",EDGE,"E2387"),sQuery(id+"F1.wireOp",EDGE,"E2388"),sQuery(id+"F1.wireOp",EDGE,"E2389"),sQuery(id+"F1.wireOp",EDGE,"E2390"),sQuery(id+"F1.wireOp",EDGE,"E2391"),sQuery(id+"F1.wireOp",EDGE,"E2392"),sQuery(id+"F1.wireOp",EDGE,"E2393"),sQuery(id+"F1.wireOp",EDGE,"E2394"),sQuery(id+"F1.wireOp",EDGE,"E2395"),sQuery(id+"F1.wireOp",EDGE,"E2396"),sQuery(id+"F1.wireOp",EDGE,"E2397"),sQuery(id+"F1.wireOp",EDGE,"E2398"),sQuery(id+"F1.wireOp",EDGE,"E2399"),sQuery(id+"F1.wireOp",EDGE,"E2400"),sQuery(id+"F1.wireOp",EDGE,"E2401"),sQuery(id+"F1.wireOp",EDGE,"E2402"),sQuery(id+"F1.wireOp",EDGE,"E2403"),sQuery(id+"F1.wireOp",EDGE,"E2404"),sQuery(id+"F1.wireOp",EDGE,"E2405"),sQuery(id+"F1.wireOp",EDGE,"E2406"),sQuery(id+"F1.wireOp",EDGE,"E2407"),sQuery(id+"F1.wireOp",EDGE,"E2408"),sQuery(id+"F1.wireOp",EDGE,"E2409"),sQuery(id+"F1.wireOp",EDGE,"E2410"),sQuery(id+"F1.wireOp",EDGE,"E2411"),sQuery(id+"F1.wireOp",EDGE,"E2412"),sQuery(id+"F1.wireOp",EDGE,"E2413"),sQuery(id+"F1.wireOp",EDGE,"E2414"),sQuery(id+"F1.wireOp",EDGE,"E2415"),sQuery(id+"F1.wireOp",EDGE,"E2416"),sQuery(id+"F1.wireOp",EDGE,"E2417"),sQuery(id+"F1.wireOp",EDGE,"E2418"),sQuery(id+"F1.wireOp",EDGE,"E2419"),sQuery(id+"F1.wireOp",EDGE,"E2420"),sQuery(id+"F1.wireOp",EDGE,"E2421"),sQuery(id+"F1.wireOp",EDGE,"E2422"),sQuery(id+"F1.wireOp",EDGE,"E2423"),sQuery(id+"F1.wireOp",EDGE,"E2424"),sQuery(id+"F1.wireOp",EDGE,"E2425"),sQuery(id+"F1.wireOp",EDGE,"E2426"),sQuery(id+"F1.wireOp",EDGE,"E2427"),sQuery(id+"F1.wireOp",EDGE,"E2428"),sQuery(id+"F1.wireOp",EDGE,"E2429"),sQuery(id+"F1.wireOp",EDGE,"E2430"),sQuery(id+"F1.wireOp",EDGE,"E2431"),sQuery(id+"F1.wireOp",EDGE,"E2432"),sQuery(id+"F1.wireOp",EDGE,"E2433"),sQuery(id+"F1.wireOp",EDGE,"E2434"),sQuery(id+"F1.wireOp",EDGE,"E2435"),sQuery(id+"F1.wireOp",EDGE,"E2436"),sQuery(id+"F1.wireOp",EDGE,"E2437"),sQuery(id+"F1.wireOp",EDGE,"E2438"),sQuery(id+"F1.wireOp",EDGE,"E2439"),sQuery(id+"F1.wireOp",EDGE,"E2440"),sQuery(id+"F1.wireOp",EDGE,"E2441"),sQuery(id+"F1.wireOp",EDGE,"E2442"),sQuery(id+"F1.wireOp",EDGE,"E2443"),sQuery(id+"F1.wireOp",EDGE,"E2444"),sQuery(id+"F1.wireOp",EDGE,"E2445"),sQuery(id+"F1.wireOp",EDGE,"E2446"),sQuery(id+"F1.wireOp",EDGE,"E2447"),sQuery(id+"F1.wireOp",EDGE,"E2448"),sQuery(id+"F1.wireOp",EDGE,"E2449"),sQuery(id+"F1.wireOp",EDGE,"E2450"),sQuery(id+"F1.wireOp",EDGE,"E2451"),sQuery(id+"F1.wireOp",EDGE,"E2452"),sQuery(id+"F1.wireOp",EDGE,"E2453"),sQuery(id+"F1.wireOp",EDGE,"E2454"),sQuery(id+"F1.wireOp",EDGE,"E2455"),sQuery(id+"F1.wireOp",EDGE,"E2456"),sQuery(id+"F1.wireOp",EDGE,"E2457"),sQuery(id+"F1.wireOp",EDGE,"E2458"),sQuery(id+"F1.wireOp",EDGE,"E2459"),sQuery(id+"F1.wireOp",EDGE,"E2460"),sQuery(id+"F1.wireOp",EDGE,"E2461"),sQuery(id+"F1.wireOp",EDGE,"E2462"),sQuery(id+"F1.wireOp",EDGE,"E2463"),sQuery(id+"F1.wireOp",EDGE,"E2464"),sQuery(id+"F1.wireOp",EDGE,"E2465"),sQuery(id+"F1.wireOp",EDGE,"E2466"),sQuery(id+"F1.wireOp",EDGE,"E2467"),sQuery(id+"F1.wireOp",EDGE,"E2468"),sQuery(id+"F1.wireOp",EDGE,"E2469"),sQuery(id+"F1.wireOp",EDGE,"E2470"),sQuery(id+"F1.wireOp",EDGE,"E2471"),sQuery(id+"F1.wireOp",EDGE,"E2472"),sQuery(id+"F1.wireOp",EDGE,"E2473"),sQuery(id+"F1.wireOp",EDGE,"E2474"),sQuery(id+"F1.wireOp",EDGE,"E2475"),sQuery(id+"F1.wireOp",EDGE,"E2476"),sQuery(id+"F1.wireOp",EDGE,"E2477"),sQuery(id+"F1.wireOp",EDGE,"E2478"),sQuery(id+"F1.wireOp",EDGE,"E2479"),sQuery(id+"F1.wireOp",EDGE,"E2480"),sQuery(id+"F1.wireOp",EDGE,"E2481"),sQuery(id+"F1.wireOp",EDGE,"E2482"),sQuery(id+"F1.wireOp",EDGE,"E2483"),sQuery(id+"F1.wireOp",EDGE,"E2484"),sQuery(id+"F1.wireOp",EDGE,"E2485"),sQuery(id+"F1.wireOp",EDGE,"E2486"),sQuery(id+"F1.wireOp",EDGE,"E2487"),sQuery(id+"F1.wireOp",EDGE,"E2488"),sQuery(id+"F1.wireOp",EDGE,"E2489"),sQuery(id+"F1.wireOp",EDGE,"E2490"),sQuery(id+"F1.wireOp",EDGE,"E2491"),sQuery(id+"F1.wireOp",EDGE,"E2492"),sQuery(id+"F1.wireOp",EDGE,"E2493"),sQuery(id+"F1.wireOp",EDGE,"E2494"),sQuery(id+"F1.wireOp",EDGE,"E2495"),sQuery(id+"F1.wireOp",EDGE,"E2496"),sQuery(id+"F1.wireOp",EDGE,"E2497"),sQuery(id+"F1.wireOp",EDGE,"E2498"),sQuery(id+"F1.wireOp",EDGE,"E2499"),sQuery(id+"F1.wireOp",EDGE,"E2500"),sQuery(id+"F1.wireOp",EDGE,"E2501"),sQuery(id+"F1.wireOp",EDGE,"E2502"),sQuery(id+"F1.wireOp",EDGE,"E2503"),sQuery(id+"F1.wireOp",EDGE,"E2504"),sQuery(id+"F1.wireOp",EDGE,"E2505"),sQuery(id+"F1.wireOp",EDGE,"E2506"),sQuery(id+"F1.wireOp",EDGE,"E2507"),sQuery(id+"F1.wireOp",EDGE,"E2508"),sQuery(id+"F1.wireOp",EDGE,"E2509"),sQuery(id+"F1.wireOp",EDGE,"E2510"),sQuery(id+"F1.wireOp",EDGE,"E2511"),sQuery(id+"F1.wireOp",EDGE,"E2512"),sQuery(id+"F1.wireOp",EDGE,"E2513"),sQuery(id+"F1.wireOp",EDGE,"E2514"),sQuery(id+"F1.wireOp",EDGE,"E2515"),sQuery(id+"F1.wireOp",EDGE,"E2516"),sQuery(id+"F1.wireOp",EDGE,"E2517"),sQuery(id+"F1.wireOp",EDGE,"E2518"),sQuery(id+"F1.wireOp",EDGE,"E2519"),sQuery(id+"F1.wireOp",EDGE,"E2520"),sQuery(id+"F1.wireOp",EDGE,"E2521"),sQuery(id+"F1.wireOp",EDGE,"E2522"),sQuery(id+"F1.wireOp",EDGE,"E2523"),sQuery(id+"F1.wireOp",EDGE,"E2524"),sQuery(id+"F1.wireOp",EDGE,"E2525"),sQuery(id+"F1.wireOp",EDGE,"E2526"),sQuery(id+"F1.wireOp",EDGE,"E2527"),sQuery(id+"F1.wireOp",EDGE,"E2528"),sQuery(id+"F1.wireOp",EDGE,"E2529"),sQuery(id+"F1.wireOp",EDGE,"E2530"),sQuery(id+"F1.wireOp",EDGE,"E2531"),sQuery(id+"F1.wireOp",EDGE,"E2532"),sQuery(id+"F1.wireOp",EDGE,"E2533"),sQuery(id+"F1.wireOp",EDGE,"E2534"),sQuery(id+"F1.wireOp",EDGE,"E2535"),sQuery(id+"F1.wireOp",EDGE,"E2536"),sQuery(id+"F1.wireOp",EDGE,"E2537"),sQuery(id+"F1.wireOp",EDGE,"E2538"),sQuery(id+"F1.wireOp",EDGE,"E2539"),sQuery(id+"F1.wireOp",EDGE,"E2540"),sQuery(id+"F1.wireOp",EDGE,"E2541"),sQuery(id+"F1.wireOp",EDGE,"E2542"),sQuery(id+"F1.wireOp",EDGE,"E2543"),sQuery(id+"F1.wireOp",EDGE,"E2544"),sQuery(id+"F1.wireOp",EDGE,"E2545"),sQuery(id+"F1.wireOp",EDGE,"E2546"),sQuery(id+"F1.wireOp",EDGE,"E2547"),sQuery(id+"F1.wireOp",EDGE,"E2548"),sQuery(id+"F1.wireOp",EDGE,"E2549"),sQuery(id+"F1.wireOp",EDGE,"E2550"),sQuery(id+"F1.wireOp",EDGE,"E2551"),sQuery(id+"F1.wireOp",EDGE,"E2552"),sQuery(id+"F1.wireOp",EDGE,"E2553"),sQuery(id+"F1.wireOp",EDGE,"E2554"),sQuery(id+"F1.wireOp",EDGE,"E2555"),sQuery(id+"F1.wireOp",EDGE,"E2556"),sQuery(id+"F1.wireOp",EDGE,"E2557"),sQuery(id+"F1.wireOp",EDGE,"E2558"),sQuery(id+"F1.wireOp",EDGE,"E2559"),sQuery(id+"F1.wireOp",EDGE,"E2560"),sQuery(id+"F1.wireOp",EDGE,"E2561"),sQuery(id+"F1.wireOp",EDGE,"E2562"),sQuery(id+"F1.wireOp",EDGE,"E2563"),sQuery(id+"F1.wireOp",EDGE,"E2564"),sQuery(id+"F1.wireOp",EDGE,"E2565"),sQuery(id+"F1.wireOp",EDGE,"E2566"),sQuery(id+"F1.wireOp",EDGE,"E2567"),sQuery(id+"F1.wireOp",EDGE,"E2568"),sQuery(id+"F1.wireOp",EDGE,"E2569"),sQuery(id+"F1.wireOp",EDGE,"E2570"),sQuery(id+"F1.wireOp",EDGE,"E2571"),sQuery(id+"F1.wireOp",EDGE,"E2572"),sQuery(id+"F1.wireOp",EDGE,"E2573"),sQuery(id+"F1.wireOp",EDGE,"E2574"),sQuery(id+"F1.wireOp",EDGE,"E2575"),sQuery(id+"F1.wireOp",EDGE,"E2576"),sQuery(id+"F1.wireOp",EDGE,"E2577"),sQuery(id+"F1.wireOp",EDGE,"E2578"),sQuery(id+"F1.wireOp",EDGE,"E2579"),sQuery(id+"F1.wireOp",EDGE,"E2580"),sQuery(id+"F1.wireOp",EDGE,"E2581"),sQuery(id+"F1.wireOp",EDGE,"E2582"),sQuery(id+"F1.wireOp",EDGE,"E2583"),sQuery(id+"F1.wireOp",EDGE,"E2584"),sQuery(id+"F1.wireOp",EDGE,"E2585"),sQuery(id+"F1.wireOp",EDGE,"E2586"),sQuery(id+"F1.wireOp",EDGE,"E2587"),sQuery(id+"F1.wireOp",EDGE,"E2588"),sQuery(id+"F1.wireOp",EDGE,"E2589"),sQuery(id+"F1.wireOp",EDGE,"E2590"),sQuery(id+"F1.wireOp",EDGE,"E2591"),sQuery(id+"F1.wireOp",EDGE,"E2592"),sQuery(id+"F1.wireOp",EDGE,"E2593"),sQuery(id+"F1.wireOp",EDGE,"E2594"),sQuery(id+"F1.wireOp",EDGE,"E2595"),sQuery(id+"F1.wireOp",EDGE,"E2596"),sQuery(id+"F1.wireOp",EDGE,"E2597"),sQuery(id+"F1.wireOp",EDGE,"E2598"),sQuery(id+"F1.wireOp",EDGE,"E2599"),sQuery(id+"F1.wireOp",EDGE,"E2600"),sQuery(id+"F1.wireOp",EDGE,"E2601"),sQuery(id+"F1.wireOp",EDGE,"E2602"),sQuery(id+"F1.wireOp",EDGE,"E2603"),sQuery(id+"F1.wireOp",EDGE,"E2604"),sQuery(id+"F1.wireOp",EDGE,"E2605"),sQuery(id+"F1.wireOp",EDGE,"E2606"),sQuery(id+"F1.wireOp",EDGE,"E2607"),sQuery(id+"F1.wireOp",EDGE,"E2608"),sQuery(id+"F1.wireOp",EDGE,"E2609"),sQuery(id+"F1.wireOp",EDGE,"E2610"),sQuery(id+"F1.wireOp",EDGE,"E2611"),sQuery(id+"F1.wireOp",EDGE,"E2612"),sQuery(id+"F1.wireOp",EDGE,"E2613"),sQuery(id+"F1.wireOp",EDGE,"E2614"),sQuery(id+"F1.wireOp",EDGE,"E2615"),sQuery(id+"F1.wireOp",EDGE,"E2616"),sQuery(id+"F1.wireOp",EDGE,"E2617"),sQuery(id+"F1.wireOp",EDGE,"E2618"),sQuery(id+"F1.wireOp",EDGE,"E2619"),sQuery(id+"F1.wireOp",EDGE,"E2620"),sQuery(id+"F1.wireOp",EDGE,"E2622")])]});
            var Q1;
            Q1=sQuery(id+"F0.wireOp",VERTEX,"E0.center");
            var Q2;
            Q2=sQuery(id+"F0.wireOp",VERTEX,"E3.center");
            transform(context, id + "F4", {"entities" : qUnion([Q0]), "transformType" : TransformType.TRANSLATION_ENTITY, "oppositeDirectionEntity" : false, "transformLine" : qUnion([Q1, Q2]), "makeCopy" : true});
        }
        {
            var Q0;
            Q0=qCreatedBy(makeId("Top.planeOp"),FACE);
            var sketch = newSketch(context, id + "F5", { "sketchPlane" : qUnion([Q0])});
            skLineSegment(sketch, "E2623", {"start": v(0, 2.38) * mm, "end": v(0, -2.38) * mm});
            skSolve(sketch);
        }
        {
            var Q0;
            Q0=makeQuery(id+"F2.opExtrude","SWEPT_BODY",BODY,{"disambiguationData":[OSD([sQuery(id+"F1.wireOp",EDGE,"E15"),sQuery(id+"F1.wireOp",EDGE,"E16"),sQuery(id+"F1.wireOp",EDGE,"E17"),sQuery(id+"F1.wireOp",EDGE,"E18"),sQuery(id+"F1.wireOp",EDGE,"E19"),sQuery(id+"F1.wireOp",EDGE,"E20"),sQuery(id+"F1.wireOp",EDGE,"E21"),sQuery(id+"F1.wireOp",EDGE,"E22"),sQuery(id+"F1.wireOp",EDGE,"E23"),sQuery(id+"F1.wireOp",EDGE,"E24"),sQuery(id+"F1.wireOp",EDGE,"E25"),sQuery(id+"F1.wireOp",EDGE,"E26"),sQuery(id+"F1.wireOp",EDGE,"E27"),sQuery(id+"F1.wireOp",EDGE,"E28"),sQuery(id+"F1.wireOp",EDGE,"E29"),sQuery(id+"F1.wireOp",EDGE,"E30"),sQuery(id+"F1.wireOp",EDGE,"E31"),sQuery(id+"F1.wireOp",EDGE,"E32"),sQuery(id+"F1.wireOp",EDGE,"E33"),sQuery(id+"F1.wireOp",EDGE,"E34"),sQuery(id+"F1.wireOp",EDGE,"E35"),sQuery(id+"F1.wireOp",EDGE,"E36"),sQuery(id+"F1.wireOp",EDGE,"E37"),sQuery(id+"F1.wireOp",EDGE,"E38"),sQuery(id+"F1.wireOp",EDGE,"E39"),sQuery(id+"F1.wireOp",EDGE,"E40"),sQuery(id+"F1.wireOp",EDGE,"E41"),sQuery(id+"F1.wireOp",EDGE,"E42"),sQuery(id+"F1.wireOp",EDGE,"E43"),sQuery(id+"F1.wireOp",EDGE,"E44"),sQuery(id+"F1.wireOp",EDGE,"E45"),sQuery(id+"F1.wireOp",EDGE,"E45"),sQuery(id+"F1.wireOp",EDGE,"E46"),sQuery(id+"F1.wireOp",EDGE,"E47"),sQuery(id+"F1.wireOp",EDGE,"E48"),sQuery(id+"F1.wireOp",EDGE,"E49"),sQuery(id+"F1.wireOp",EDGE,"E50"),sQuery(id+"F1.wireOp",EDGE,"E51"),sQuery(id+"F1.wireOp",EDGE,"E52"),sQuery(id+"F1.wireOp",EDGE,"E53"),sQuery(id+"F1.wireOp",EDGE,"E54"),sQuery(id+"F1.wireOp",EDGE,"E55"),sQuery(id+"F1.wireOp",EDGE,"E56"),sQuery(id+"F1.wireOp",EDGE,"E57"),sQuery(id+"F1.wireOp",EDGE,"E58"),sQuery(id+"F1.wireOp",EDGE,"E59"),sQuery(id+"F1.wireOp",EDGE,"E60"),sQuery(id+"F1.wireOp",EDGE,"E61"),sQuery(id+"F1.wireOp",EDGE,"E62"),sQuery(id+"F1.wireOp",EDGE,"E63"),sQuery(id+"F1.wireOp",EDGE,"E64"),sQuery(id+"F1.wireOp",EDGE,"E65"),sQuery(id+"F1.wireOp",EDGE,"E66"),sQuery(id+"F1.wireOp",EDGE,"E67"),sQuery(id+"F1.wireOp",EDGE,"E68"),sQuery(id+"F1.wireOp",EDGE,"E69"),sQuery(id+"F1.wireOp",EDGE,"E70"),sQuery(id+"F1.wireOp",EDGE,"E71"),sQuery(id+"F1.wireOp",EDGE,"E72"),sQuery(id+"F1.wireOp",EDGE,"E73"),sQuery(id+"F1.wireOp",EDGE,"E74"),sQuery(id+"F1.wireOp",EDGE,"E75"),sQuery(id+"F1.wireOp",EDGE,"E76"),sQuery(id+"F1.wireOp",EDGE,"E77"),sQuery(id+"F1.wireOp",EDGE,"E78"),sQuery(id+"F1.wireOp",EDGE,"E79"),sQuery(id+"F1.wireOp",EDGE,"E80"),sQuery(id+"F1.wireOp",EDGE,"E81"),sQuery(id+"F1.wireOp",EDGE,"E82"),sQuery(id+"F1.wireOp",EDGE,"E83"),sQuery(id+"F1.wireOp",EDGE,"E84"),sQuery(id+"F1.wireOp",EDGE,"E85"),sQuery(id+"F1.wireOp",EDGE,"E86"),sQuery(id+"F1.wireOp",EDGE,"E87"),sQuery(id+"F1.wireOp",EDGE,"E88"),sQuery(id+"F1.wireOp",EDGE,"E89"),sQuery(id+"F1.wireOp",EDGE,"E90"),sQuery(id+"F1.wireOp",EDGE,"E91"),sQuery(id+"F1.wireOp",EDGE,"E92"),sQuery(id+"F1.wireOp",EDGE,"E93"),sQuery(id+"F1.wireOp",EDGE,"E94"),sQuery(id+"F1.wireOp",EDGE,"E95"),sQuery(id+"F1.wireOp",EDGE,"E96"),sQuery(id+"F1.wireOp",EDGE,"E97"),sQuery(id+"F1.wireOp",EDGE,"E98"),sQuery(id+"F1.wireOp",EDGE,"E99"),sQuery(id+"F1.wireOp",EDGE,"E100"),sQuery(id+"F1.wireOp",EDGE,"E101"),sQuery(id+"F1.wireOp",EDGE,"E102"),sQuery(id+"F1.wireOp",EDGE,"E103"),sQuery(id+"F1.wireOp",EDGE,"E104"),sQuery(id+"F1.wireOp",EDGE,"E104"),sQuery(id+"F1.wireOp",EDGE,"E105"),sQuery(id+"F1.wireOp",EDGE,"E106"),sQuery(id+"F1.wireOp",EDGE,"E107"),sQuery(id+"F1.wireOp",EDGE,"E108"),sQuery(id+"F1.wireOp",EDGE,"E109"),sQuery(id+"F1.wireOp",EDGE,"E110"),sQuery(id+"F1.wireOp",EDGE,"E111"),sQuery(id+"F1.wireOp",EDGE,"E112"),sQuery(id+"F1.wireOp",EDGE,"E113"),sQuery(id+"F1.wireOp",EDGE,"E114"),sQuery(id+"F1.wireOp",EDGE,"E115"),sQuery(id+"F1.wireOp",EDGE,"E116"),sQuery(id+"F1.wireOp",EDGE,"E117"),sQuery(id+"F1.wireOp",EDGE,"E118"),sQuery(id+"F1.wireOp",EDGE,"E119"),sQuery(id+"F1.wireOp",EDGE,"E120"),sQuery(id+"F1.wireOp",EDGE,"E121"),sQuery(id+"F1.wireOp",EDGE,"E122"),sQuery(id+"F1.wireOp",EDGE,"E123"),sQuery(id+"F1.wireOp",EDGE,"E124"),sQuery(id+"F1.wireOp",EDGE,"E125"),sQuery(id+"F1.wireOp",EDGE,"E126"),sQuery(id+"F1.wireOp",EDGE,"E127"),sQuery(id+"F1.wireOp",EDGE,"E128"),sQuery(id+"F1.wireOp",EDGE,"E129"),sQuery(id+"F1.wireOp",EDGE,"E130"),sQuery(id+"F1.wireOp",EDGE,"E131"),sQuery(id+"F1.wireOp",EDGE,"E132"),sQuery(id+"F1.wireOp",EDGE,"E133"),sQuery(id+"F1.wireOp",EDGE,"E134"),sQuery(id+"F1.wireOp",EDGE,"E135"),sQuery(id+"F1.wireOp",EDGE,"E136"),sQuery(id+"F1.wireOp",EDGE,"E137"),sQuery(id+"F1.wireOp",EDGE,"E138"),sQuery(id+"F1.wireOp",EDGE,"E139"),sQuery(id+"F1.wireOp",EDGE,"E140"),sQuery(id+"F1.wireOp",EDGE,"E141"),sQuery(id+"F1.wireOp",EDGE,"E142"),sQuery(id+"F1.wireOp",EDGE,"E143"),sQuery(id+"F1.wireOp",EDGE,"E144"),sQuery(id+"F1.wireOp",EDGE,"E145"),sQuery(id+"F1.wireOp",EDGE,"E146"),sQuery(id+"F1.wireOp",EDGE,"E147"),sQuery(id+"F1.wireOp",EDGE,"E148"),sQuery(id+"F1.wireOp",EDGE,"E149"),sQuery(id+"F1.wireOp",EDGE,"E150"),sQuery(id+"F1.wireOp",EDGE,"E151"),sQuery(id+"F1.wireOp",EDGE,"E152"),sQuery(id+"F1.wireOp",EDGE,"E153"),sQuery(id+"F1.wireOp",EDGE,"E154"),sQuery(id+"F1.wireOp",EDGE,"E155"),sQuery(id+"F1.wireOp",EDGE,"E156"),sQuery(id+"F1.wireOp",EDGE,"E157"),sQuery(id+"F1.wireOp",EDGE,"E158"),sQuery(id+"F1.wireOp",EDGE,"E159"),sQuery(id+"F1.wireOp",EDGE,"E160"),sQuery(id+"F1.wireOp",EDGE,"E161"),sQuery(id+"F1.wireOp",EDGE,"E162"),sQuery(id+"F1.wireOp",EDGE,"E163"),sQuery(id+"F1.wireOp",EDGE,"E164"),sQuery(id+"F1.wireOp",EDGE,"E165"),sQuery(id+"F1.wireOp",EDGE,"E166"),sQuery(id+"F1.wireOp",EDGE,"E167"),sQuery(id+"F1.wireOp",EDGE,"E168"),sQuery(id+"F1.wireOp",EDGE,"E169"),sQuery(id+"F1.wireOp",EDGE,"E170"),sQuery(id+"F1.wireOp",EDGE,"E171"),sQuery(id+"F1.wireOp",EDGE,"E172"),sQuery(id+"F1.wireOp",EDGE,"E173"),sQuery(id+"F1.wireOp",EDGE,"E174"),sQuery(id+"F1.wireOp",EDGE,"E175"),sQuery(id+"F1.wireOp",EDGE,"E176"),sQuery(id+"F1.wireOp",EDGE,"E177"),sQuery(id+"F1.wireOp",EDGE,"E178"),sQuery(id+"F1.wireOp",EDGE,"E179"),sQuery(id+"F1.wireOp",EDGE,"E180"),sQuery(id+"F1.wireOp",EDGE,"E181"),sQuery(id+"F1.wireOp",EDGE,"E182"),sQuery(id+"F1.wireOp",EDGE,"E183"),sQuery(id+"F1.wireOp",EDGE,"E184"),sQuery(id+"F1.wireOp",EDGE,"E185"),sQuery(id+"F1.wireOp",EDGE,"E186"),sQuery(id+"F1.wireOp",EDGE,"E187"),sQuery(id+"F1.wireOp",EDGE,"E188"),sQuery(id+"F1.wireOp",EDGE,"E189"),sQuery(id+"F1.wireOp",EDGE,"E190"),sQuery(id+"F1.wireOp",EDGE,"E191"),sQuery(id+"F1.wireOp",EDGE,"E192"),sQuery(id+"F1.wireOp",EDGE,"E193"),sQuery(id+"F1.wireOp",EDGE,"E194"),sQuery(id+"F1.wireOp",EDGE,"E195"),sQuery(id+"F1.wireOp",EDGE,"E196"),sQuery(id+"F1.wireOp",EDGE,"E197"),sQuery(id+"F1.wireOp",EDGE,"E198"),sQuery(id+"F1.wireOp",EDGE,"E199"),sQuery(id+"F1.wireOp",EDGE,"E200"),sQuery(id+"F1.wireOp",EDGE,"E201"),sQuery(id+"F1.wireOp",EDGE,"E202"),sQuery(id+"F1.wireOp",EDGE,"E203"),sQuery(id+"F1.wireOp",EDGE,"E204"),sQuery(id+"F1.wireOp",EDGE,"E205"),sQuery(id+"F1.wireOp",EDGE,"E206"),sQuery(id+"F1.wireOp",EDGE,"E207"),sQuery(id+"F1.wireOp",EDGE,"E208"),sQuery(id+"F1.wireOp",EDGE,"E209"),sQuery(id+"F1.wireOp",EDGE,"E210"),sQuery(id+"F1.wireOp",EDGE,"E211"),sQuery(id+"F1.wireOp",EDGE,"E212"),sQuery(id+"F1.wireOp",EDGE,"E213"),sQuery(id+"F1.wireOp",EDGE,"E214"),sQuery(id+"F1.wireOp",EDGE,"E215"),sQuery(id+"F1.wireOp",EDGE,"E216"),sQuery(id+"F1.wireOp",EDGE,"E217"),sQuery(id+"F1.wireOp",EDGE,"E218"),sQuery(id+"F1.wireOp",EDGE,"E219"),sQuery(id+"F1.wireOp",EDGE,"E220"),sQuery(id+"F1.wireOp",EDGE,"E221"),sQuery(id+"F1.wireOp",EDGE,"E222"),sQuery(id+"F1.wireOp",EDGE,"E223"),sQuery(id+"F1.wireOp",EDGE,"E224"),sQuery(id+"F1.wireOp",EDGE,"E225"),sQuery(id+"F1.wireOp",EDGE,"E226"),sQuery(id+"F1.wireOp",EDGE,"E227"),sQuery(id+"F1.wireOp",EDGE,"E228"),sQuery(id+"F1.wireOp",EDGE,"E229"),sQuery(id+"F1.wireOp",EDGE,"E230"),sQuery(id+"F1.wireOp",EDGE,"E231"),sQuery(id+"F1.wireOp",EDGE,"E232"),sQuery(id+"F1.wireOp",EDGE,"E233"),sQuery(id+"F1.wireOp",EDGE,"E234"),sQuery(id+"F1.wireOp",EDGE,"E235"),sQuery(id+"F1.wireOp",EDGE,"E236"),sQuery(id+"F1.wireOp",EDGE,"E237"),sQuery(id+"F1.wireOp",EDGE,"E238"),sQuery(id+"F1.wireOp",EDGE,"E239"),sQuery(id+"F1.wireOp",EDGE,"E240"),sQuery(id+"F1.wireOp",EDGE,"E241"),sQuery(id+"F1.wireOp",EDGE,"E242"),sQuery(id+"F1.wireOp",EDGE,"E243"),sQuery(id+"F1.wireOp",EDGE,"E244"),sQuery(id+"F1.wireOp",EDGE,"E245"),sQuery(id+"F1.wireOp",EDGE,"E246"),sQuery(id+"F1.wireOp",EDGE,"E247"),sQuery(id+"F1.wireOp",EDGE,"E248"),sQuery(id+"F1.wireOp",EDGE,"E249"),sQuery(id+"F1.wireOp",EDGE,"E250"),sQuery(id+"F1.wireOp",EDGE,"E251"),sQuery(id+"F1.wireOp",EDGE,"E252"),sQuery(id+"F1.wireOp",EDGE,"E253"),sQuery(id+"F1.wireOp",EDGE,"E254"),sQuery(id+"F1.wireOp",EDGE,"E255"),sQuery(id+"F1.wireOp",EDGE,"E256"),sQuery(id+"F1.wireOp",EDGE,"E257"),sQuery(id+"F1.wireOp",EDGE,"E258"),sQuery(id+"F1.wireOp",EDGE,"E259"),sQuery(id+"F1.wireOp",EDGE,"E260"),sQuery(id+"F1.wireOp",EDGE,"E261"),sQuery(id+"F1.wireOp",EDGE,"E262"),sQuery(id+"F1.wireOp",EDGE,"E263"),sQuery(id+"F1.wireOp",EDGE,"E264"),sQuery(id+"F1.wireOp",EDGE,"E265"),sQuery(id+"F1.wireOp",EDGE,"E266"),sQuery(id+"F1.wireOp",EDGE,"E267"),sQuery(id+"F1.wireOp",EDGE,"E268"),sQuery(id+"F1.wireOp",EDGE,"E269"),sQuery(id+"F1.wireOp",EDGE,"E270"),sQuery(id+"F1.wireOp",EDGE,"E271"),sQuery(id+"F1.wireOp",EDGE,"E272"),sQuery(id+"F1.wireOp",EDGE,"E273"),sQuery(id+"F1.wireOp",EDGE,"E274"),sQuery(id+"F1.wireOp",EDGE,"E275"),sQuery(id+"F1.wireOp",EDGE,"E276"),sQuery(id+"F1.wireOp",EDGE,"E277"),sQuery(id+"F1.wireOp",EDGE,"E278"),sQuery(id+"F1.wireOp",EDGE,"E279"),sQuery(id+"F1.wireOp",EDGE,"E280"),sQuery(id+"F1.wireOp",EDGE,"E281"),sQuery(id+"F1.wireOp",EDGE,"E282"),sQuery(id+"F1.wireOp",EDGE,"E283"),sQuery(id+"F1.wireOp",EDGE,"E284"),sQuery(id+"F1.wireOp",EDGE,"E285"),sQuery(id+"F1.wireOp",EDGE,"E286"),sQuery(id+"F1.wireOp",EDGE,"E287"),sQuery(id+"F1.wireOp",EDGE,"E288"),sQuery(id+"F1.wireOp",EDGE,"E289"),sQuery(id+"F1.wireOp",EDGE,"E290"),sQuery(id+"F1.wireOp",EDGE,"E291"),sQuery(id+"F1.wireOp",EDGE,"E292"),sQuery(id+"F1.wireOp",EDGE,"E293"),sQuery(id+"F1.wireOp",EDGE,"E294"),sQuery(id+"F1.wireOp",EDGE,"E295"),sQuery(id+"F1.wireOp",EDGE,"E296"),sQuery(id+"F1.wireOp",EDGE,"E297"),sQuery(id+"F1.wireOp",EDGE,"E298"),sQuery(id+"F1.wireOp",EDGE,"E299"),sQuery(id+"F1.wireOp",EDGE,"E300"),sQuery(id+"F1.wireOp",EDGE,"E301"),sQuery(id+"F1.wireOp",EDGE,"E302"),sQuery(id+"F1.wireOp",EDGE,"E303"),sQuery(id+"F1.wireOp",EDGE,"E304"),sQuery(id+"F1.wireOp",EDGE,"E305"),sQuery(id+"F1.wireOp",EDGE,"E306"),sQuery(id+"F1.wireOp",EDGE,"E307"),sQuery(id+"F1.wireOp",EDGE,"E308"),sQuery(id+"F1.wireOp",EDGE,"E309"),sQuery(id+"F1.wireOp",EDGE,"E310"),sQuery(id+"F1.wireOp",EDGE,"E311"),sQuery(id+"F1.wireOp",EDGE,"E312"),sQuery(id+"F1.wireOp",EDGE,"E313"),sQuery(id+"F1.wireOp",EDGE,"E314"),sQuery(id+"F1.wireOp",EDGE,"E315"),sQuery(id+"F1.wireOp",EDGE,"E316"),sQuery(id+"F1.wireOp",EDGE,"E317"),sQuery(id+"F1.wireOp",EDGE,"E318"),sQuery(id+"F1.wireOp",EDGE,"E319"),sQuery(id+"F1.wireOp",EDGE,"E320"),sQuery(id+"F1.wireOp",EDGE,"E321"),sQuery(id+"F1.wireOp",EDGE,"E322"),sQuery(id+"F1.wireOp",EDGE,"E323"),sQuery(id+"F1.wireOp",EDGE,"E324"),sQuery(id+"F1.wireOp",EDGE,"E325"),sQuery(id+"F1.wireOp",EDGE,"E326"),sQuery(id+"F1.wireOp",EDGE,"E327"),sQuery(id+"F1.wireOp",EDGE,"E328"),sQuery(id+"F1.wireOp",EDGE,"E329"),sQuery(id+"F1.wireOp",EDGE,"E330"),sQuery(id+"F1.wireOp",EDGE,"E331"),sQuery(id+"F1.wireOp",EDGE,"E332"),sQuery(id+"F1.wireOp",EDGE,"E333"),sQuery(id+"F1.wireOp",EDGE,"E334"),sQuery(id+"F1.wireOp",EDGE,"E334"),sQuery(id+"F1.wireOp",EDGE,"E335"),sQuery(id+"F1.wireOp",EDGE,"E336"),sQuery(id+"F1.wireOp",EDGE,"E337"),sQuery(id+"F1.wireOp",EDGE,"E338"),sQuery(id+"F1.wireOp",EDGE,"E339"),sQuery(id+"F1.wireOp",EDGE,"E340"),sQuery(id+"F1.wireOp",EDGE,"E341"),sQuery(id+"F1.wireOp",EDGE,"E342"),sQuery(id+"F1.wireOp",EDGE,"E343"),sQuery(id+"F1.wireOp",EDGE,"E344"),sQuery(id+"F1.wireOp",EDGE,"E345"),sQuery(id+"F1.wireOp",EDGE,"E346"),sQuery(id+"F1.wireOp",EDGE,"E347"),sQuery(id+"F1.wireOp",EDGE,"E348"),sQuery(id+"F1.wireOp",EDGE,"E349"),sQuery(id+"F1.wireOp",EDGE,"E350"),sQuery(id+"F1.wireOp",EDGE,"E351"),sQuery(id+"F1.wireOp",EDGE,"E352"),sQuery(id+"F1.wireOp",EDGE,"E353"),sQuery(id+"F1.wireOp",EDGE,"E354"),sQuery(id+"F1.wireOp",EDGE,"E355"),sQuery(id+"F1.wireOp",EDGE,"E356"),sQuery(id+"F1.wireOp",EDGE,"E357"),sQuery(id+"F1.wireOp",EDGE,"E358"),sQuery(id+"F1.wireOp",EDGE,"E359"),sQuery(id+"F1.wireOp",EDGE,"E360"),sQuery(id+"F1.wireOp",EDGE,"E361"),sQuery(id+"F1.wireOp",EDGE,"E362"),sQuery(id+"F1.wireOp",EDGE,"E363"),sQuery(id+"F1.wireOp",EDGE,"E364"),sQuery(id+"F1.wireOp",EDGE,"E365"),sQuery(id+"F1.wireOp",EDGE,"E366"),sQuery(id+"F1.wireOp",EDGE,"E367"),sQuery(id+"F1.wireOp",EDGE,"E368"),sQuery(id+"F1.wireOp",EDGE,"E369"),sQuery(id+"F1.wireOp",EDGE,"E370"),sQuery(id+"F1.wireOp",EDGE,"E371"),sQuery(id+"F1.wireOp",EDGE,"E372"),sQuery(id+"F1.wireOp",EDGE,"E373"),sQuery(id+"F1.wireOp",EDGE,"E374"),sQuery(id+"F1.wireOp",EDGE,"E375"),sQuery(id+"F1.wireOp",EDGE,"E376"),sQuery(id+"F1.wireOp",EDGE,"E377"),sQuery(id+"F1.wireOp",EDGE,"E378"),sQuery(id+"F1.wireOp",EDGE,"E379"),sQuery(id+"F1.wireOp",EDGE,"E380"),sQuery(id+"F1.wireOp",EDGE,"E381"),sQuery(id+"F1.wireOp",EDGE,"E382"),sQuery(id+"F1.wireOp",EDGE,"E383"),sQuery(id+"F1.wireOp",EDGE,"E384"),sQuery(id+"F1.wireOp",EDGE,"E385"),sQuery(id+"F1.wireOp",EDGE,"E386"),sQuery(id+"F1.wireOp",EDGE,"E387"),sQuery(id+"F1.wireOp",EDGE,"E388"),sQuery(id+"F1.wireOp",EDGE,"E389"),sQuery(id+"F1.wireOp",EDGE,"E390"),sQuery(id+"F1.wireOp",EDGE,"E391"),sQuery(id+"F1.wireOp",EDGE,"E392"),sQuery(id+"F1.wireOp",EDGE,"E393"),sQuery(id+"F1.wireOp",EDGE,"E394"),sQuery(id+"F1.wireOp",EDGE,"E395"),sQuery(id+"F1.wireOp",EDGE,"E396"),sQuery(id+"F1.wireOp",EDGE,"E397"),sQuery(id+"F1.wireOp",EDGE,"E398"),sQuery(id+"F1.wireOp",EDGE,"E399"),sQuery(id+"F1.wireOp",EDGE,"E400"),sQuery(id+"F1.wireOp",EDGE,"E401"),sQuery(id+"F1.wireOp",EDGE,"E402"),sQuery(id+"F1.wireOp",EDGE,"E403"),sQuery(id+"F1.wireOp",EDGE,"E404"),sQuery(id+"F1.wireOp",EDGE,"E405"),sQuery(id+"F1.wireOp",EDGE,"E406"),sQuery(id+"F1.wireOp",EDGE,"E407"),sQuery(id+"F1.wireOp",EDGE,"E408"),sQuery(id+"F1.wireOp",EDGE,"E409"),sQuery(id+"F1.wireOp",EDGE,"E410"),sQuery(id+"F1.wireOp",EDGE,"E411"),sQuery(id+"F1.wireOp",EDGE,"E412"),sQuery(id+"F1.wireOp",EDGE,"E413"),sQuery(id+"F1.wireOp",EDGE,"E414"),sQuery(id+"F1.wireOp",EDGE,"E415"),sQuery(id+"F1.wireOp",EDGE,"E416"),sQuery(id+"F1.wireOp",EDGE,"E417"),sQuery(id+"F1.wireOp",EDGE,"E418"),sQuery(id+"F1.wireOp",EDGE,"E419"),sQuery(id+"F1.wireOp",EDGE,"E420"),sQuery(id+"F1.wireOp",EDGE,"E421"),sQuery(id+"F1.wireOp",EDGE,"E422"),sQuery(id+"F1.wireOp",EDGE,"E423"),sQuery(id+"F1.wireOp",EDGE,"E424"),sQuery(id+"F1.wireOp",EDGE,"E425"),sQuery(id+"F1.wireOp",EDGE,"E426"),sQuery(id+"F1.wireOp",EDGE,"E426"),sQuery(id+"F1.wireOp",EDGE,"E427"),sQuery(id+"F1.wireOp",EDGE,"E428"),sQuery(id+"F1.wireOp",EDGE,"E429"),sQuery(id+"F1.wireOp",EDGE,"E430"),sQuery(id+"F1.wireOp",EDGE,"E431"),sQuery(id+"F1.wireOp",EDGE,"E432"),sQuery(id+"F1.wireOp",EDGE,"E433"),sQuery(id+"F1.wireOp",EDGE,"E434"),sQuery(id+"F1.wireOp",EDGE,"E435"),sQuery(id+"F1.wireOp",EDGE,"E435"),sQuery(id+"F1.wireOp",EDGE,"E436"),sQuery(id+"F1.wireOp",EDGE,"E437"),sQuery(id+"F1.wireOp",EDGE,"E438"),sQuery(id+"F1.wireOp",EDGE,"E439"),sQuery(id+"F1.wireOp",EDGE,"E440"),sQuery(id+"F1.wireOp",EDGE,"E441"),sQuery(id+"F1.wireOp",EDGE,"E442"),sQuery(id+"F1.wireOp",EDGE,"E443"),sQuery(id+"F1.wireOp",EDGE,"E444"),sQuery(id+"F1.wireOp",EDGE,"E445"),sQuery(id+"F1.wireOp",EDGE,"E446"),sQuery(id+"F1.wireOp",EDGE,"E447"),sQuery(id+"F1.wireOp",EDGE,"E448"),sQuery(id+"F1.wireOp",EDGE,"E449"),sQuery(id+"F1.wireOp",EDGE,"E450"),sQuery(id+"F1.wireOp",EDGE,"E451"),sQuery(id+"F1.wireOp",EDGE,"E452"),sQuery(id+"F1.wireOp",EDGE,"E453"),sQuery(id+"F1.wireOp",EDGE,"E454"),sQuery(id+"F1.wireOp",EDGE,"E455"),sQuery(id+"F1.wireOp",EDGE,"E456"),sQuery(id+"F1.wireOp",EDGE,"E457"),sQuery(id+"F1.wireOp",EDGE,"E458"),sQuery(id+"F1.wireOp",EDGE,"E459"),sQuery(id+"F1.wireOp",EDGE,"E460"),sQuery(id+"F1.wireOp",EDGE,"E461"),sQuery(id+"F1.wireOp",EDGE,"E462"),sQuery(id+"F1.wireOp",EDGE,"E463"),sQuery(id+"F1.wireOp",EDGE,"E464"),sQuery(id+"F1.wireOp",EDGE,"E465"),sQuery(id+"F1.wireOp",EDGE,"E466"),sQuery(id+"F1.wireOp",EDGE,"E467"),sQuery(id+"F1.wireOp",EDGE,"E468"),sQuery(id+"F1.wireOp",EDGE,"E469"),sQuery(id+"F1.wireOp",EDGE,"E470"),sQuery(id+"F1.wireOp",EDGE,"E471"),sQuery(id+"F1.wireOp",EDGE,"E472"),sQuery(id+"F1.wireOp",EDGE,"E473"),sQuery(id+"F1.wireOp",EDGE,"E474"),sQuery(id+"F1.wireOp",EDGE,"E475"),sQuery(id+"F1.wireOp",EDGE,"E476"),sQuery(id+"F1.wireOp",EDGE,"E477"),sQuery(id+"F1.wireOp",EDGE,"E478"),sQuery(id+"F1.wireOp",EDGE,"E479"),sQuery(id+"F1.wireOp",EDGE,"E480"),sQuery(id+"F1.wireOp",EDGE,"E481"),sQuery(id+"F1.wireOp",EDGE,"E482"),sQuery(id+"F1.wireOp",EDGE,"E483"),sQuery(id+"F1.wireOp",EDGE,"E484"),sQuery(id+"F1.wireOp",EDGE,"E485"),sQuery(id+"F1.wireOp",EDGE,"E486"),sQuery(id+"F1.wireOp",EDGE,"E487"),sQuery(id+"F1.wireOp",EDGE,"E488"),sQuery(id+"F1.wireOp",EDGE,"E489"),sQuery(id+"F1.wireOp",EDGE,"E490"),sQuery(id+"F1.wireOp",EDGE,"E491"),sQuery(id+"F1.wireOp",EDGE,"E492"),sQuery(id+"F1.wireOp",EDGE,"E493"),sQuery(id+"F1.wireOp",EDGE,"E494"),sQuery(id+"F1.wireOp",EDGE,"E495"),sQuery(id+"F1.wireOp",EDGE,"E496"),sQuery(id+"F1.wireOp",EDGE,"E497"),sQuery(id+"F1.wireOp",EDGE,"E498"),sQuery(id+"F1.wireOp",EDGE,"E499"),sQuery(id+"F1.wireOp",EDGE,"E500"),sQuery(id+"F1.wireOp",EDGE,"E501"),sQuery(id+"F1.wireOp",EDGE,"E502"),sQuery(id+"F1.wireOp",EDGE,"E503"),sQuery(id+"F1.wireOp",EDGE,"E504"),sQuery(id+"F1.wireOp",EDGE,"E505"),sQuery(id+"F1.wireOp",EDGE,"E506"),sQuery(id+"F1.wireOp",EDGE,"E507"),sQuery(id+"F1.wireOp",EDGE,"E508"),sQuery(id+"F1.wireOp",EDGE,"E509"),sQuery(id+"F1.wireOp",EDGE,"E510"),sQuery(id+"F1.wireOp",EDGE,"E511"),sQuery(id+"F1.wireOp",EDGE,"E512"),sQuery(id+"F1.wireOp",EDGE,"E513"),sQuery(id+"F1.wireOp",EDGE,"E514"),sQuery(id+"F1.wireOp",EDGE,"E515"),sQuery(id+"F1.wireOp",EDGE,"E516"),sQuery(id+"F1.wireOp",EDGE,"E517"),sQuery(id+"F1.wireOp",EDGE,"E518"),sQuery(id+"F1.wireOp",EDGE,"E519"),sQuery(id+"F1.wireOp",EDGE,"E520"),sQuery(id+"F1.wireOp",EDGE,"E521"),sQuery(id+"F1.wireOp",EDGE,"E522"),sQuery(id+"F1.wireOp",EDGE,"E523"),sQuery(id+"F1.wireOp",EDGE,"E524"),sQuery(id+"F1.wireOp",EDGE,"E525"),sQuery(id+"F1.wireOp",EDGE,"E526"),sQuery(id+"F1.wireOp",EDGE,"E527"),sQuery(id+"F1.wireOp",EDGE,"E528"),sQuery(id+"F1.wireOp",EDGE,"E529"),sQuery(id+"F1.wireOp",EDGE,"E530"),sQuery(id+"F1.wireOp",EDGE,"E531"),sQuery(id+"F1.wireOp",EDGE,"E532"),sQuery(id+"F1.wireOp",EDGE,"E533"),sQuery(id+"F1.wireOp",EDGE,"E534"),sQuery(id+"F1.wireOp",EDGE,"E534"),sQuery(id+"F1.wireOp",EDGE,"E535"),sQuery(id+"F1.wireOp",EDGE,"E536"),sQuery(id+"F1.wireOp",EDGE,"E537"),sQuery(id+"F1.wireOp",EDGE,"E538"),sQuery(id+"F1.wireOp",EDGE,"E539"),sQuery(id+"F1.wireOp",EDGE,"E540"),sQuery(id+"F1.wireOp",EDGE,"E541"),sQuery(id+"F1.wireOp",EDGE,"E542"),sQuery(id+"F1.wireOp",EDGE,"E543"),sQuery(id+"F1.wireOp",EDGE,"E544"),sQuery(id+"F1.wireOp",EDGE,"E545"),sQuery(id+"F1.wireOp",EDGE,"E546"),sQuery(id+"F1.wireOp",EDGE,"E547"),sQuery(id+"F1.wireOp",EDGE,"E548"),sQuery(id+"F1.wireOp",EDGE,"E549"),sQuery(id+"F1.wireOp",EDGE,"E550"),sQuery(id+"F1.wireOp",EDGE,"E551"),sQuery(id+"F1.wireOp",EDGE,"E552"),sQuery(id+"F1.wireOp",EDGE,"E553"),sQuery(id+"F1.wireOp",EDGE,"E554"),sQuery(id+"F1.wireOp",EDGE,"E555"),sQuery(id+"F1.wireOp",EDGE,"E556"),sQuery(id+"F1.wireOp",EDGE,"E557"),sQuery(id+"F1.wireOp",EDGE,"E558"),sQuery(id+"F1.wireOp",EDGE,"E559"),sQuery(id+"F1.wireOp",EDGE,"E560"),sQuery(id+"F1.wireOp",EDGE,"E561"),sQuery(id+"F1.wireOp",EDGE,"E562"),sQuery(id+"F1.wireOp",EDGE,"E563"),sQuery(id+"F1.wireOp",EDGE,"E564"),sQuery(id+"F1.wireOp",EDGE,"E565"),sQuery(id+"F1.wireOp",EDGE,"E566"),sQuery(id+"F1.wireOp",EDGE,"E567"),sQuery(id+"F1.wireOp",EDGE,"E568"),sQuery(id+"F1.wireOp",EDGE,"E569"),sQuery(id+"F1.wireOp",EDGE,"E570"),sQuery(id+"F1.wireOp",EDGE,"E571"),sQuery(id+"F1.wireOp",EDGE,"E572"),sQuery(id+"F1.wireOp",EDGE,"E573"),sQuery(id+"F1.wireOp",EDGE,"E574"),sQuery(id+"F1.wireOp",EDGE,"E575"),sQuery(id+"F1.wireOp",EDGE,"E576"),sQuery(id+"F1.wireOp",EDGE,"E577"),sQuery(id+"F1.wireOp",EDGE,"E578"),sQuery(id+"F1.wireOp",EDGE,"E579"),sQuery(id+"F1.wireOp",EDGE,"E580"),sQuery(id+"F1.wireOp",EDGE,"E581"),sQuery(id+"F1.wireOp",EDGE,"E582"),sQuery(id+"F1.wireOp",EDGE,"E583"),sQuery(id+"F1.wireOp",EDGE,"E584"),sQuery(id+"F1.wireOp",EDGE,"E585"),sQuery(id+"F1.wireOp",EDGE,"E586"),sQuery(id+"F1.wireOp",EDGE,"E587"),sQuery(id+"F1.wireOp",EDGE,"E588"),sQuery(id+"F1.wireOp",EDGE,"E589"),sQuery(id+"F1.wireOp",EDGE,"E590"),sQuery(id+"F1.wireOp",EDGE,"E591"),sQuery(id+"F1.wireOp",EDGE,"E592"),sQuery(id+"F1.wireOp",EDGE,"E593"),sQuery(id+"F1.wireOp",EDGE,"E594"),sQuery(id+"F1.wireOp",EDGE,"E595"),sQuery(id+"F1.wireOp",EDGE,"E596"),sQuery(id+"F1.wireOp",EDGE,"E597"),sQuery(id+"F1.wireOp",EDGE,"E598"),sQuery(id+"F1.wireOp",EDGE,"E599"),sQuery(id+"F1.wireOp",EDGE,"E600"),sQuery(id+"F1.wireOp",EDGE,"E601"),sQuery(id+"F1.wireOp",EDGE,"E602"),sQuery(id+"F1.wireOp",EDGE,"E603"),sQuery(id+"F1.wireOp",EDGE,"E604"),sQuery(id+"F1.wireOp",EDGE,"E605"),sQuery(id+"F1.wireOp",EDGE,"E606"),sQuery(id+"F1.wireOp",EDGE,"E607"),sQuery(id+"F1.wireOp",EDGE,"E608"),sQuery(id+"F1.wireOp",EDGE,"E609"),sQuery(id+"F1.wireOp",EDGE,"E610"),sQuery(id+"F1.wireOp",EDGE,"E611"),sQuery(id+"F1.wireOp",EDGE,"E612"),sQuery(id+"F1.wireOp",EDGE,"E613"),sQuery(id+"F1.wireOp",EDGE,"E614"),sQuery(id+"F1.wireOp",EDGE,"E615"),sQuery(id+"F1.wireOp",EDGE,"E616"),sQuery(id+"F1.wireOp",EDGE,"E617"),sQuery(id+"F1.wireOp",EDGE,"E618"),sQuery(id+"F1.wireOp",EDGE,"E619"),sQuery(id+"F1.wireOp",EDGE,"E620"),sQuery(id+"F1.wireOp",EDGE,"E621"),sQuery(id+"F1.wireOp",EDGE,"E622"),sQuery(id+"F1.wireOp",EDGE,"E623"),sQuery(id+"F1.wireOp",EDGE,"E624"),sQuery(id+"F1.wireOp",EDGE,"E625"),sQuery(id+"F1.wireOp",EDGE,"E626"),sQuery(id+"F1.wireOp",EDGE,"E627"),sQuery(id+"F1.wireOp",EDGE,"E628"),sQuery(id+"F1.wireOp",EDGE,"E629"),sQuery(id+"F1.wireOp",EDGE,"E630"),sQuery(id+"F1.wireOp",EDGE,"E631"),sQuery(id+"F1.wireOp",EDGE,"E632"),sQuery(id+"F1.wireOp",EDGE,"E633"),sQuery(id+"F1.wireOp",EDGE,"E634"),sQuery(id+"F1.wireOp",EDGE,"E635"),sQuery(id+"F1.wireOp",EDGE,"E636"),sQuery(id+"F1.wireOp",EDGE,"E637"),sQuery(id+"F1.wireOp",EDGE,"E638"),sQuery(id+"F1.wireOp",EDGE,"E639"),sQuery(id+"F1.wireOp",EDGE,"E640"),sQuery(id+"F1.wireOp",EDGE,"E641"),sQuery(id+"F1.wireOp",EDGE,"E642"),sQuery(id+"F1.wireOp",EDGE,"E643"),sQuery(id+"F1.wireOp",EDGE,"E644"),sQuery(id+"F1.wireOp",EDGE,"E645"),sQuery(id+"F1.wireOp",EDGE,"E646"),sQuery(id+"F1.wireOp",EDGE,"E647"),sQuery(id+"F1.wireOp",EDGE,"E648"),sQuery(id+"F1.wireOp",EDGE,"E649"),sQuery(id+"F1.wireOp",EDGE,"E650"),sQuery(id+"F1.wireOp",EDGE,"E651"),sQuery(id+"F1.wireOp",EDGE,"E652"),sQuery(id+"F1.wireOp",EDGE,"E653"),sQuery(id+"F1.wireOp",EDGE,"E654"),sQuery(id+"F1.wireOp",EDGE,"E655"),sQuery(id+"F1.wireOp",EDGE,"E656"),sQuery(id+"F1.wireOp",EDGE,"E657"),sQuery(id+"F1.wireOp",EDGE,"E658"),sQuery(id+"F1.wireOp",EDGE,"E659"),sQuery(id+"F1.wireOp",EDGE,"E660"),sQuery(id+"F1.wireOp",EDGE,"E661"),sQuery(id+"F1.wireOp",EDGE,"E662"),sQuery(id+"F1.wireOp",EDGE,"E663"),sQuery(id+"F1.wireOp",EDGE,"E664"),sQuery(id+"F1.wireOp",EDGE,"E665"),sQuery(id+"F1.wireOp",EDGE,"E666"),sQuery(id+"F1.wireOp",EDGE,"E667"),sQuery(id+"F1.wireOp",EDGE,"E668"),sQuery(id+"F1.wireOp",EDGE,"E669"),sQuery(id+"F1.wireOp",EDGE,"E670"),sQuery(id+"F1.wireOp",EDGE,"E671"),sQuery(id+"F1.wireOp",EDGE,"E672"),sQuery(id+"F1.wireOp",EDGE,"E673"),sQuery(id+"F1.wireOp",EDGE,"E674"),sQuery(id+"F1.wireOp",EDGE,"E675"),sQuery(id+"F1.wireOp",EDGE,"E676"),sQuery(id+"F1.wireOp",EDGE,"E677"),sQuery(id+"F1.wireOp",EDGE,"E678"),sQuery(id+"F1.wireOp",EDGE,"E679"),sQuery(id+"F1.wireOp",EDGE,"E680"),sQuery(id+"F1.wireOp",EDGE,"E681"),sQuery(id+"F1.wireOp",EDGE,"E682"),sQuery(id+"F1.wireOp",EDGE,"E683"),sQuery(id+"F1.wireOp",EDGE,"E684"),sQuery(id+"F1.wireOp",EDGE,"E685"),sQuery(id+"F1.wireOp",EDGE,"E686"),sQuery(id+"F1.wireOp",EDGE,"E687"),sQuery(id+"F1.wireOp",EDGE,"E688"),sQuery(id+"F1.wireOp",EDGE,"E689"),sQuery(id+"F1.wireOp",EDGE,"E690"),sQuery(id+"F1.wireOp",EDGE,"E691"),sQuery(id+"F1.wireOp",EDGE,"E692"),sQuery(id+"F1.wireOp",EDGE,"E693"),sQuery(id+"F1.wireOp",EDGE,"E694"),sQuery(id+"F1.wireOp",EDGE,"E695"),sQuery(id+"F1.wireOp",EDGE,"E696"),sQuery(id+"F1.wireOp",EDGE,"E697"),sQuery(id+"F1.wireOp",EDGE,"E698"),sQuery(id+"F1.wireOp",EDGE,"E699"),sQuery(id+"F1.wireOp",EDGE,"E700"),sQuery(id+"F1.wireOp",EDGE,"E701"),sQuery(id+"F1.wireOp",EDGE,"E702"),sQuery(id+"F1.wireOp",EDGE,"E703"),sQuery(id+"F1.wireOp",EDGE,"E704"),sQuery(id+"F1.wireOp",EDGE,"E705"),sQuery(id+"F1.wireOp",EDGE,"E706"),sQuery(id+"F1.wireOp",EDGE,"E707"),sQuery(id+"F1.wireOp",EDGE,"E708"),sQuery(id+"F1.wireOp",EDGE,"E709"),sQuery(id+"F1.wireOp",EDGE,"E710"),sQuery(id+"F1.wireOp",EDGE,"E711"),sQuery(id+"F1.wireOp",EDGE,"E712"),sQuery(id+"F1.wireOp",EDGE,"E713"),sQuery(id+"F1.wireOp",EDGE,"E714"),sQuery(id+"F1.wireOp",EDGE,"E715"),sQuery(id+"F1.wireOp",EDGE,"E716"),sQuery(id+"F1.wireOp",EDGE,"E717"),sQuery(id+"F1.wireOp",EDGE,"E718"),sQuery(id+"F1.wireOp",EDGE,"E719"),sQuery(id+"F1.wireOp",EDGE,"E720"),sQuery(id+"F1.wireOp",EDGE,"E721"),sQuery(id+"F1.wireOp",EDGE,"E722"),sQuery(id+"F1.wireOp",EDGE,"E723"),sQuery(id+"F1.wireOp",EDGE,"E724"),sQuery(id+"F1.wireOp",EDGE,"E725"),sQuery(id+"F1.wireOp",EDGE,"E726"),sQuery(id+"F1.wireOp",EDGE,"E727"),sQuery(id+"F1.wireOp",EDGE,"E728"),sQuery(id+"F1.wireOp",EDGE,"E729"),sQuery(id+"F1.wireOp",EDGE,"E730"),sQuery(id+"F1.wireOp",EDGE,"E731"),sQuery(id+"F1.wireOp",EDGE,"E732"),sQuery(id+"F1.wireOp",EDGE,"E733"),sQuery(id+"F1.wireOp",EDGE,"E734"),sQuery(id+"F1.wireOp",EDGE,"E735"),sQuery(id+"F1.wireOp",EDGE,"E736"),sQuery(id+"F1.wireOp",EDGE,"E737"),sQuery(id+"F1.wireOp",EDGE,"E738"),sQuery(id+"F1.wireOp",EDGE,"E739"),sQuery(id+"F1.wireOp",EDGE,"E740"),sQuery(id+"F1.wireOp",EDGE,"E741"),sQuery(id+"F1.wireOp",EDGE,"E742"),sQuery(id+"F1.wireOp",EDGE,"E743"),sQuery(id+"F1.wireOp",EDGE,"E744"),sQuery(id+"F1.wireOp",EDGE,"E745"),sQuery(id+"F1.wireOp",EDGE,"E746"),sQuery(id+"F1.wireOp",EDGE,"E747"),sQuery(id+"F1.wireOp",EDGE,"E748"),sQuery(id+"F1.wireOp",EDGE,"E749"),sQuery(id+"F1.wireOp",EDGE,"E750"),sQuery(id+"F1.wireOp",EDGE,"E751"),sQuery(id+"F1.wireOp",EDGE,"E752"),sQuery(id+"F1.wireOp",EDGE,"E753"),sQuery(id+"F1.wireOp",EDGE,"E754"),sQuery(id+"F1.wireOp",EDGE,"E755"),sQuery(id+"F1.wireOp",EDGE,"E756"),sQuery(id+"F1.wireOp",EDGE,"E757"),sQuery(id+"F1.wireOp",EDGE,"E758"),sQuery(id+"F1.wireOp",EDGE,"E759"),sQuery(id+"F1.wireOp",EDGE,"E760"),sQuery(id+"F1.wireOp",EDGE,"E761"),sQuery(id+"F1.wireOp",EDGE,"E762"),sQuery(id+"F1.wireOp",EDGE,"E763"),sQuery(id+"F1.wireOp",EDGE,"E764"),sQuery(id+"F1.wireOp",EDGE,"E765"),sQuery(id+"F1.wireOp",EDGE,"E766"),sQuery(id+"F1.wireOp",EDGE,"E767"),sQuery(id+"F1.wireOp",EDGE,"E768"),sQuery(id+"F1.wireOp",EDGE,"E769"),sQuery(id+"F1.wireOp",EDGE,"E770"),sQuery(id+"F1.wireOp",EDGE,"E771"),sQuery(id+"F1.wireOp",EDGE,"E772"),sQuery(id+"F1.wireOp",EDGE,"E773"),sQuery(id+"F1.wireOp",EDGE,"E774"),sQuery(id+"F1.wireOp",EDGE,"E775"),sQuery(id+"F1.wireOp",EDGE,"E776"),sQuery(id+"F1.wireOp",EDGE,"E777"),sQuery(id+"F1.wireOp",EDGE,"E778"),sQuery(id+"F1.wireOp",EDGE,"E779"),sQuery(id+"F1.wireOp",EDGE,"E780"),sQuery(id+"F1.wireOp",EDGE,"E781"),sQuery(id+"F1.wireOp",EDGE,"E782"),sQuery(id+"F1.wireOp",EDGE,"E783"),sQuery(id+"F1.wireOp",EDGE,"E784"),sQuery(id+"F1.wireOp",EDGE,"E785"),sQuery(id+"F1.wireOp",EDGE,"E786"),sQuery(id+"F1.wireOp",EDGE,"E787"),sQuery(id+"F1.wireOp",EDGE,"E788"),sQuery(id+"F1.wireOp",EDGE,"E789"),sQuery(id+"F1.wireOp",EDGE,"E790"),sQuery(id+"F1.wireOp",EDGE,"E791"),sQuery(id+"F1.wireOp",EDGE,"E792"),sQuery(id+"F1.wireOp",EDGE,"E793"),sQuery(id+"F1.wireOp",EDGE,"E794"),sQuery(id+"F1.wireOp",EDGE,"E795"),sQuery(id+"F1.wireOp",EDGE,"E796"),sQuery(id+"F1.wireOp",EDGE,"E797"),sQuery(id+"F1.wireOp",EDGE,"E798"),sQuery(id+"F1.wireOp",EDGE,"E799"),sQuery(id+"F1.wireOp",EDGE,"E800"),sQuery(id+"F1.wireOp",EDGE,"E801"),sQuery(id+"F1.wireOp",EDGE,"E802"),sQuery(id+"F1.wireOp",EDGE,"E803"),sQuery(id+"F1.wireOp",EDGE,"E804"),sQuery(id+"F1.wireOp",EDGE,"E805"),sQuery(id+"F1.wireOp",EDGE,"E806"),sQuery(id+"F1.wireOp",EDGE,"E807"),sQuery(id+"F1.wireOp",EDGE,"E808"),sQuery(id+"F1.wireOp",EDGE,"E809"),sQuery(id+"F1.wireOp",EDGE,"E810"),sQuery(id+"F1.wireOp",EDGE,"E811"),sQuery(id+"F1.wireOp",EDGE,"E812"),sQuery(id+"F1.wireOp",EDGE,"E813"),sQuery(id+"F1.wireOp",EDGE,"E814"),sQuery(id+"F1.wireOp",EDGE,"E815"),sQuery(id+"F1.wireOp",EDGE,"E816"),sQuery(id+"F1.wireOp",EDGE,"E817"),sQuery(id+"F1.wireOp",EDGE,"E818"),sQuery(id+"F1.wireOp",EDGE,"E819"),sQuery(id+"F1.wireOp",EDGE,"E820"),sQuery(id+"F1.wireOp",EDGE,"E821"),sQuery(id+"F1.wireOp",EDGE,"E822"),sQuery(id+"F1.wireOp",EDGE,"E823"),sQuery(id+"F1.wireOp",EDGE,"E824"),sQuery(id+"F1.wireOp",EDGE,"E825"),sQuery(id+"F1.wireOp",EDGE,"E826"),sQuery(id+"F1.wireOp",EDGE,"E827"),sQuery(id+"F1.wireOp",EDGE,"E828"),sQuery(id+"F1.wireOp",EDGE,"E829"),sQuery(id+"F1.wireOp",EDGE,"E830"),sQuery(id+"F1.wireOp",EDGE,"E831"),sQuery(id+"F1.wireOp",EDGE,"E832"),sQuery(id+"F1.wireOp",EDGE,"E833"),sQuery(id+"F1.wireOp",EDGE,"E834"),sQuery(id+"F1.wireOp",EDGE,"E835"),sQuery(id+"F1.wireOp",EDGE,"E836"),sQuery(id+"F1.wireOp",EDGE,"E837"),sQuery(id+"F1.wireOp",EDGE,"E838"),sQuery(id+"F1.wireOp",EDGE,"E839"),sQuery(id+"F1.wireOp",EDGE,"E840"),sQuery(id+"F1.wireOp",EDGE,"E841"),sQuery(id+"F1.wireOp",EDGE,"E842"),sQuery(id+"F1.wireOp",EDGE,"E843"),sQuery(id+"F1.wireOp",EDGE,"E844"),sQuery(id+"F1.wireOp",EDGE,"E845"),sQuery(id+"F1.wireOp",EDGE,"E846"),sQuery(id+"F1.wireOp",EDGE,"E847"),sQuery(id+"F1.wireOp",EDGE,"E848"),sQuery(id+"F1.wireOp",EDGE,"E849"),sQuery(id+"F1.wireOp",EDGE,"E850"),sQuery(id+"F1.wireOp",EDGE,"E851"),sQuery(id+"F1.wireOp",EDGE,"E852"),sQuery(id+"F1.wireOp",EDGE,"E853"),sQuery(id+"F1.wireOp",EDGE,"E854"),sQuery(id+"F1.wireOp",EDGE,"E855"),sQuery(id+"F1.wireOp",EDGE,"E856"),sQuery(id+"F1.wireOp",EDGE,"E857"),sQuery(id+"F1.wireOp",EDGE,"E858"),sQuery(id+"F1.wireOp",EDGE,"E859"),sQuery(id+"F1.wireOp",EDGE,"E860"),sQuery(id+"F1.wireOp",EDGE,"E861"),sQuery(id+"F1.wireOp",EDGE,"E862"),sQuery(id+"F1.wireOp",EDGE,"E863"),sQuery(id+"F1.wireOp",EDGE,"E864"),sQuery(id+"F1.wireOp",EDGE,"E865"),sQuery(id+"F1.wireOp",EDGE,"E866"),sQuery(id+"F1.wireOp",EDGE,"E867"),sQuery(id+"F1.wireOp",EDGE,"E868"),sQuery(id+"F1.wireOp",EDGE,"E869"),sQuery(id+"F1.wireOp",EDGE,"E870"),sQuery(id+"F1.wireOp",EDGE,"E871"),sQuery(id+"F1.wireOp",EDGE,"E872"),sQuery(id+"F1.wireOp",EDGE,"E873"),sQuery(id+"F1.wireOp",EDGE,"E873"),sQuery(id+"F1.wireOp",EDGE,"E874"),sQuery(id+"F1.wireOp",EDGE,"E875"),sQuery(id+"F1.wireOp",EDGE,"E876"),sQuery(id+"F1.wireOp",EDGE,"E877"),sQuery(id+"F1.wireOp",EDGE,"E878"),sQuery(id+"F1.wireOp",EDGE,"E879"),sQuery(id+"F1.wireOp",EDGE,"E880"),sQuery(id+"F1.wireOp",EDGE,"E881"),sQuery(id+"F1.wireOp",EDGE,"E882"),sQuery(id+"F1.wireOp",EDGE,"E883"),sQuery(id+"F1.wireOp",EDGE,"E884"),sQuery(id+"F1.wireOp",EDGE,"E885"),sQuery(id+"F1.wireOp",EDGE,"E886"),sQuery(id+"F1.wireOp",EDGE,"E887"),sQuery(id+"F1.wireOp",EDGE,"E888"),sQuery(id+"F1.wireOp",EDGE,"E889"),sQuery(id+"F1.wireOp",EDGE,"E890"),sQuery(id+"F1.wireOp",EDGE,"E891"),sQuery(id+"F1.wireOp",EDGE,"E892"),sQuery(id+"F1.wireOp",EDGE,"E893"),sQuery(id+"F1.wireOp",EDGE,"E894"),sQuery(id+"F1.wireOp",EDGE,"E895"),sQuery(id+"F1.wireOp",EDGE,"E896"),sQuery(id+"F1.wireOp",EDGE,"E897"),sQuery(id+"F1.wireOp",EDGE,"E898"),sQuery(id+"F1.wireOp",EDGE,"E899"),sQuery(id+"F1.wireOp",EDGE,"E900"),sQuery(id+"F1.wireOp",EDGE,"E901"),sQuery(id+"F1.wireOp",EDGE,"E902"),sQuery(id+"F1.wireOp",EDGE,"E903"),sQuery(id+"F1.wireOp",EDGE,"E904"),sQuery(id+"F1.wireOp",EDGE,"E905"),sQuery(id+"F1.wireOp",EDGE,"E906"),sQuery(id+"F1.wireOp",EDGE,"E907"),sQuery(id+"F1.wireOp",EDGE,"E908"),sQuery(id+"F1.wireOp",EDGE,"E909"),sQuery(id+"F1.wireOp",EDGE,"E910"),sQuery(id+"F1.wireOp",EDGE,"E911"),sQuery(id+"F1.wireOp",EDGE,"E912"),sQuery(id+"F1.wireOp",EDGE,"E913"),sQuery(id+"F1.wireOp",EDGE,"E914"),sQuery(id+"F1.wireOp",EDGE,"E915"),sQuery(id+"F1.wireOp",EDGE,"E916"),sQuery(id+"F1.wireOp",EDGE,"E917"),sQuery(id+"F1.wireOp",EDGE,"E918"),sQuery(id+"F1.wireOp",EDGE,"E919"),sQuery(id+"F1.wireOp",EDGE,"E920"),sQuery(id+"F1.wireOp",EDGE,"E921"),sQuery(id+"F1.wireOp",EDGE,"E922"),sQuery(id+"F1.wireOp",EDGE,"E923"),sQuery(id+"F1.wireOp",EDGE,"E924"),sQuery(id+"F1.wireOp",EDGE,"E925"),sQuery(id+"F1.wireOp",EDGE,"E926"),sQuery(id+"F1.wireOp",EDGE,"E927"),sQuery(id+"F1.wireOp",EDGE,"E928"),sQuery(id+"F1.wireOp",EDGE,"E929"),sQuery(id+"F1.wireOp",EDGE,"E930"),sQuery(id+"F1.wireOp",EDGE,"E931"),sQuery(id+"F1.wireOp",EDGE,"E932"),sQuery(id+"F1.wireOp",EDGE,"E933"),sQuery(id+"F1.wireOp",EDGE,"E934"),sQuery(id+"F1.wireOp",EDGE,"E935"),sQuery(id+"F1.wireOp",EDGE,"E936"),sQuery(id+"F1.wireOp",EDGE,"E937"),sQuery(id+"F1.wireOp",EDGE,"E938"),sQuery(id+"F1.wireOp",EDGE,"E939"),sQuery(id+"F1.wireOp",EDGE,"E940"),sQuery(id+"F1.wireOp",EDGE,"E941"),sQuery(id+"F1.wireOp",EDGE,"E942"),sQuery(id+"F1.wireOp",EDGE,"E943"),sQuery(id+"F1.wireOp",EDGE,"E944"),sQuery(id+"F1.wireOp",EDGE,"E945"),sQuery(id+"F1.wireOp",EDGE,"E946"),sQuery(id+"F1.wireOp",EDGE,"E947"),sQuery(id+"F1.wireOp",EDGE,"E948"),sQuery(id+"F1.wireOp",EDGE,"E949"),sQuery(id+"F1.wireOp",EDGE,"E950"),sQuery(id+"F1.wireOp",EDGE,"E951"),sQuery(id+"F1.wireOp",EDGE,"E952"),sQuery(id+"F1.wireOp",EDGE,"E953"),sQuery(id+"F1.wireOp",EDGE,"E954"),sQuery(id+"F1.wireOp",EDGE,"E955"),sQuery(id+"F1.wireOp",EDGE,"E956"),sQuery(id+"F1.wireOp",EDGE,"E957"),sQuery(id+"F1.wireOp",EDGE,"E958"),sQuery(id+"F1.wireOp",EDGE,"E959"),sQuery(id+"F1.wireOp",EDGE,"E960"),sQuery(id+"F1.wireOp",EDGE,"E961"),sQuery(id+"F1.wireOp",EDGE,"E962"),sQuery(id+"F1.wireOp",EDGE,"E963"),sQuery(id+"F1.wireOp",EDGE,"E964"),sQuery(id+"F1.wireOp",EDGE,"E965"),sQuery(id+"F1.wireOp",EDGE,"E966"),sQuery(id+"F1.wireOp",EDGE,"E967"),sQuery(id+"F1.wireOp",EDGE,"E968"),sQuery(id+"F1.wireOp",EDGE,"E969"),sQuery(id+"F1.wireOp",EDGE,"E970"),sQuery(id+"F1.wireOp",EDGE,"E971"),sQuery(id+"F1.wireOp",EDGE,"E972"),sQuery(id+"F1.wireOp",EDGE,"E973"),sQuery(id+"F1.wireOp",EDGE,"E974"),sQuery(id+"F1.wireOp",EDGE,"E975"),sQuery(id+"F1.wireOp",EDGE,"E976"),sQuery(id+"F1.wireOp",EDGE,"E976"),sQuery(id+"F1.wireOp",EDGE,"E976"),sQuery(id+"F1.wireOp",EDGE,"E977"),sQuery(id+"F1.wireOp",EDGE,"E978"),sQuery(id+"F1.wireOp",EDGE,"E979"),sQuery(id+"F1.wireOp",EDGE,"E980"),sQuery(id+"F1.wireOp",EDGE,"E981"),sQuery(id+"F1.wireOp",EDGE,"E982"),sQuery(id+"F1.wireOp",EDGE,"E983"),sQuery(id+"F1.wireOp",EDGE,"E984"),sQuery(id+"F1.wireOp",EDGE,"E985"),sQuery(id+"F1.wireOp",EDGE,"E986"),sQuery(id+"F1.wireOp",EDGE,"E987"),sQuery(id+"F1.wireOp",EDGE,"E988"),sQuery(id+"F1.wireOp",EDGE,"E989"),sQuery(id+"F1.wireOp",EDGE,"E990"),sQuery(id+"F1.wireOp",EDGE,"E991"),sQuery(id+"F1.wireOp",EDGE,"E992"),sQuery(id+"F1.wireOp",EDGE,"E993"),sQuery(id+"F1.wireOp",EDGE,"E994"),sQuery(id+"F1.wireOp",EDGE,"E995"),sQuery(id+"F1.wireOp",EDGE,"E996"),sQuery(id+"F1.wireOp",EDGE,"E997"),sQuery(id+"F1.wireOp",EDGE,"E998"),sQuery(id+"F1.wireOp",EDGE,"E999"),sQuery(id+"F1.wireOp",EDGE,"E1000"),sQuery(id+"F1.wireOp",EDGE,"E1001"),sQuery(id+"F1.wireOp",EDGE,"E1002"),sQuery(id+"F1.wireOp",EDGE,"E1003"),sQuery(id+"F1.wireOp",EDGE,"E1004"),sQuery(id+"F1.wireOp",EDGE,"E1005"),sQuery(id+"F1.wireOp",EDGE,"E1006"),sQuery(id+"F1.wireOp",EDGE,"E1007"),sQuery(id+"F1.wireOp",EDGE,"E1008"),sQuery(id+"F1.wireOp",EDGE,"E1009"),sQuery(id+"F1.wireOp",EDGE,"E1010"),sQuery(id+"F1.wireOp",EDGE,"E1011"),sQuery(id+"F1.wireOp",EDGE,"E1012"),sQuery(id+"F1.wireOp",EDGE,"E1013"),sQuery(id+"F1.wireOp",EDGE,"E1014"),sQuery(id+"F1.wireOp",EDGE,"E1015"),sQuery(id+"F1.wireOp",EDGE,"E1016"),sQuery(id+"F1.wireOp",EDGE,"E1017"),sQuery(id+"F1.wireOp",EDGE,"E1018"),sQuery(id+"F1.wireOp",EDGE,"E1019"),sQuery(id+"F1.wireOp",EDGE,"E1020"),sQuery(id+"F1.wireOp",EDGE,"E1021"),sQuery(id+"F1.wireOp",EDGE,"E1022"),sQuery(id+"F1.wireOp",EDGE,"E1023"),sQuery(id+"F1.wireOp",EDGE,"E1024"),sQuery(id+"F1.wireOp",EDGE,"E1025"),sQuery(id+"F1.wireOp",EDGE,"E1026"),sQuery(id+"F1.wireOp",EDGE,"E1027"),sQuery(id+"F1.wireOp",EDGE,"E1028"),sQuery(id+"F1.wireOp",EDGE,"E1029"),sQuery(id+"F1.wireOp",EDGE,"E1030"),sQuery(id+"F1.wireOp",EDGE,"E1031"),sQuery(id+"F1.wireOp",EDGE,"E1032"),sQuery(id+"F1.wireOp",EDGE,"E1033"),sQuery(id+"F1.wireOp",EDGE,"E1034"),sQuery(id+"F1.wireOp",EDGE,"E1035"),sQuery(id+"F1.wireOp",EDGE,"E1036"),sQuery(id+"F1.wireOp",EDGE,"E1037"),sQuery(id+"F1.wireOp",EDGE,"E1038"),sQuery(id+"F1.wireOp",EDGE,"E1039"),sQuery(id+"F1.wireOp",EDGE,"E1040"),sQuery(id+"F1.wireOp",EDGE,"E1041"),sQuery(id+"F1.wireOp",EDGE,"E1042"),sQuery(id+"F1.wireOp",EDGE,"E1043"),sQuery(id+"F1.wireOp",EDGE,"E1044"),sQuery(id+"F1.wireOp",EDGE,"E1045"),sQuery(id+"F1.wireOp",EDGE,"E1046"),sQuery(id+"F1.wireOp",EDGE,"E1047"),sQuery(id+"F1.wireOp",EDGE,"E1048"),sQuery(id+"F1.wireOp",EDGE,"E1049"),sQuery(id+"F1.wireOp",EDGE,"E1050"),sQuery(id+"F1.wireOp",EDGE,"E1051"),sQuery(id+"F1.wireOp",EDGE,"E1052"),sQuery(id+"F1.wireOp",EDGE,"E1053"),sQuery(id+"F1.wireOp",EDGE,"E1054"),sQuery(id+"F1.wireOp",EDGE,"E1055"),sQuery(id+"F1.wireOp",EDGE,"E1056"),sQuery(id+"F1.wireOp",EDGE,"E1057"),sQuery(id+"F1.wireOp",EDGE,"E1058"),sQuery(id+"F1.wireOp",EDGE,"E1059"),sQuery(id+"F1.wireOp",EDGE,"E1060"),sQuery(id+"F1.wireOp",EDGE,"E1061"),sQuery(id+"F1.wireOp",EDGE,"E1062"),sQuery(id+"F1.wireOp",EDGE,"E1063"),sQuery(id+"F1.wireOp",EDGE,"E1064"),sQuery(id+"F1.wireOp",EDGE,"E1065"),sQuery(id+"F1.wireOp",EDGE,"E1066"),sQuery(id+"F1.wireOp",EDGE,"E1067"),sQuery(id+"F1.wireOp",EDGE,"E1068"),sQuery(id+"F1.wireOp",EDGE,"E1069"),sQuery(id+"F1.wireOp",EDGE,"E1070"),sQuery(id+"F1.wireOp",EDGE,"E1071"),sQuery(id+"F1.wireOp",EDGE,"E1071"),sQuery(id+"F1.wireOp",EDGE,"E1072"),sQuery(id+"F1.wireOp",EDGE,"E1073"),sQuery(id+"F1.wireOp",EDGE,"E1074"),sQuery(id+"F1.wireOp",EDGE,"E1075"),sQuery(id+"F1.wireOp",EDGE,"E1076"),sQuery(id+"F1.wireOp",EDGE,"E1077"),sQuery(id+"F1.wireOp",EDGE,"E1078"),sQuery(id+"F1.wireOp",EDGE,"E1079"),sQuery(id+"F1.wireOp",EDGE,"E1080"),sQuery(id+"F1.wireOp",EDGE,"E1080"),sQuery(id+"F1.wireOp",EDGE,"E1081"),sQuery(id+"F1.wireOp",EDGE,"E1082"),sQuery(id+"F1.wireOp",EDGE,"E1083"),sQuery(id+"F1.wireOp",EDGE,"E1084"),sQuery(id+"F1.wireOp",EDGE,"E1085"),sQuery(id+"F1.wireOp",EDGE,"E1086"),sQuery(id+"F1.wireOp",EDGE,"E1087"),sQuery(id+"F1.wireOp",EDGE,"E1088"),sQuery(id+"F1.wireOp",EDGE,"E1089"),sQuery(id+"F1.wireOp",EDGE,"E1090"),sQuery(id+"F1.wireOp",EDGE,"E1091"),sQuery(id+"F1.wireOp",EDGE,"E1092"),sQuery(id+"F1.wireOp",EDGE,"E1093"),sQuery(id+"F1.wireOp",EDGE,"E1094"),sQuery(id+"F1.wireOp",EDGE,"E1095"),sQuery(id+"F1.wireOp",EDGE,"E1096"),sQuery(id+"F1.wireOp",EDGE,"E1097"),sQuery(id+"F1.wireOp",EDGE,"E1098"),sQuery(id+"F1.wireOp",EDGE,"E1099"),sQuery(id+"F1.wireOp",EDGE,"E1100"),sQuery(id+"F1.wireOp",EDGE,"E1101"),sQuery(id+"F1.wireOp",EDGE,"E1102"),sQuery(id+"F1.wireOp",EDGE,"E1103"),sQuery(id+"F1.wireOp",EDGE,"E1104"),sQuery(id+"F1.wireOp",EDGE,"E1105"),sQuery(id+"F1.wireOp",EDGE,"E1106"),sQuery(id+"F1.wireOp",EDGE,"E1107"),sQuery(id+"F1.wireOp",EDGE,"E1108"),sQuery(id+"F1.wireOp",EDGE,"E1109"),sQuery(id+"F1.wireOp",EDGE,"E1110"),sQuery(id+"F1.wireOp",EDGE,"E1111"),sQuery(id+"F1.wireOp",EDGE,"E1112"),sQuery(id+"F1.wireOp",EDGE,"E1113"),sQuery(id+"F1.wireOp",EDGE,"E1114"),sQuery(id+"F1.wireOp",EDGE,"E1115"),sQuery(id+"F1.wireOp",EDGE,"E1116"),sQuery(id+"F1.wireOp",EDGE,"E1117"),sQuery(id+"F1.wireOp",EDGE,"E1118"),sQuery(id+"F1.wireOp",EDGE,"E1119"),sQuery(id+"F1.wireOp",EDGE,"E1120"),sQuery(id+"F1.wireOp",EDGE,"E1121"),sQuery(id+"F1.wireOp",EDGE,"E1122"),sQuery(id+"F1.wireOp",EDGE,"E1123"),sQuery(id+"F1.wireOp",EDGE,"E1124"),sQuery(id+"F1.wireOp",EDGE,"E1125"),sQuery(id+"F1.wireOp",EDGE,"E1126"),sQuery(id+"F1.wireOp",EDGE,"E1127"),sQuery(id+"F1.wireOp",EDGE,"E1128"),sQuery(id+"F1.wireOp",EDGE,"E1129"),sQuery(id+"F1.wireOp",EDGE,"E1130"),sQuery(id+"F1.wireOp",EDGE,"E1131"),sQuery(id+"F1.wireOp",EDGE,"E1132"),sQuery(id+"F1.wireOp",EDGE,"E1133"),sQuery(id+"F1.wireOp",EDGE,"E1134"),sQuery(id+"F1.wireOp",EDGE,"E1135"),sQuery(id+"F1.wireOp",EDGE,"E1136"),sQuery(id+"F1.wireOp",EDGE,"E1137"),sQuery(id+"F1.wireOp",EDGE,"E1138"),sQuery(id+"F1.wireOp",EDGE,"E1139"),sQuery(id+"F1.wireOp",EDGE,"E1140"),sQuery(id+"F1.wireOp",EDGE,"E1141"),sQuery(id+"F1.wireOp",EDGE,"E1142"),sQuery(id+"F1.wireOp",EDGE,"E1143"),sQuery(id+"F1.wireOp",EDGE,"E1144"),sQuery(id+"F1.wireOp",EDGE,"E1145"),sQuery(id+"F1.wireOp",EDGE,"E1146"),sQuery(id+"F1.wireOp",EDGE,"E1147"),sQuery(id+"F1.wireOp",EDGE,"E1148"),sQuery(id+"F1.wireOp",EDGE,"E1149"),sQuery(id+"F1.wireOp",EDGE,"E1150"),sQuery(id+"F1.wireOp",EDGE,"E1151"),sQuery(id+"F1.wireOp",EDGE,"E1152"),sQuery(id+"F1.wireOp",EDGE,"E1153"),sQuery(id+"F1.wireOp",EDGE,"E1154"),sQuery(id+"F1.wireOp",EDGE,"E1155"),sQuery(id+"F1.wireOp",EDGE,"E1156"),sQuery(id+"F1.wireOp",EDGE,"E1156"),sQuery(id+"F1.wireOp",EDGE,"E1157"),sQuery(id+"F1.wireOp",EDGE,"E1158"),sQuery(id+"F1.wireOp",EDGE,"E1159"),sQuery(id+"F1.wireOp",EDGE,"E1160"),sQuery(id+"F1.wireOp",EDGE,"E1161"),sQuery(id+"F1.wireOp",EDGE,"E1162"),sQuery(id+"F1.wireOp",EDGE,"E1163"),sQuery(id+"F1.wireOp",EDGE,"E1164"),sQuery(id+"F1.wireOp",EDGE,"E1165"),sQuery(id+"F1.wireOp",EDGE,"E1166"),sQuery(id+"F1.wireOp",EDGE,"E1167"),sQuery(id+"F1.wireOp",EDGE,"E1168"),sQuery(id+"F1.wireOp",EDGE,"E1169"),sQuery(id+"F1.wireOp",EDGE,"E1170"),sQuery(id+"F1.wireOp",EDGE,"E1171"),sQuery(id+"F1.wireOp",EDGE,"E1172"),sQuery(id+"F1.wireOp",EDGE,"E1173"),sQuery(id+"F1.wireOp",EDGE,"E1174"),sQuery(id+"F1.wireOp",EDGE,"E1175"),sQuery(id+"F1.wireOp",EDGE,"E1176"),sQuery(id+"F1.wireOp",EDGE,"E1177"),sQuery(id+"F1.wireOp",EDGE,"E1178"),sQuery(id+"F1.wireOp",EDGE,"E1179"),sQuery(id+"F1.wireOp",EDGE,"E1180"),sQuery(id+"F1.wireOp",EDGE,"E1181"),sQuery(id+"F1.wireOp",EDGE,"E1182"),sQuery(id+"F1.wireOp",EDGE,"E1183"),sQuery(id+"F1.wireOp",EDGE,"E1184"),sQuery(id+"F1.wireOp",EDGE,"E1185"),sQuery(id+"F1.wireOp",EDGE,"E1186"),sQuery(id+"F1.wireOp",EDGE,"E1187"),sQuery(id+"F1.wireOp",EDGE,"E1188"),sQuery(id+"F1.wireOp",EDGE,"E1189"),sQuery(id+"F1.wireOp",EDGE,"E1190"),sQuery(id+"F1.wireOp",EDGE,"E1191"),sQuery(id+"F1.wireOp",EDGE,"E1192"),sQuery(id+"F1.wireOp",EDGE,"E1193"),sQuery(id+"F1.wireOp",EDGE,"E1194"),sQuery(id+"F1.wireOp",EDGE,"E1195"),sQuery(id+"F1.wireOp",EDGE,"E1196"),sQuery(id+"F1.wireOp",EDGE,"E1197"),sQuery(id+"F1.wireOp",EDGE,"E1198"),sQuery(id+"F1.wireOp",EDGE,"E1199"),sQuery(id+"F1.wireOp",EDGE,"E1200"),sQuery(id+"F1.wireOp",EDGE,"E1201"),sQuery(id+"F1.wireOp",EDGE,"E1202"),sQuery(id+"F1.wireOp",EDGE,"E1203"),sQuery(id+"F1.wireOp",EDGE,"E1204"),sQuery(id+"F1.wireOp",EDGE,"E1205"),sQuery(id+"F1.wireOp",EDGE,"E1206"),sQuery(id+"F1.wireOp",EDGE,"E1207"),sQuery(id+"F1.wireOp",EDGE,"E1208"),sQuery(id+"F1.wireOp",EDGE,"E1209"),sQuery(id+"F1.wireOp",EDGE,"E1210"),sQuery(id+"F1.wireOp",EDGE,"E1211"),sQuery(id+"F1.wireOp",EDGE,"E1212"),sQuery(id+"F1.wireOp",EDGE,"E1213"),sQuery(id+"F1.wireOp",EDGE,"E1214"),sQuery(id+"F1.wireOp",EDGE,"E1215"),sQuery(id+"F1.wireOp",EDGE,"E1216"),sQuery(id+"F1.wireOp",EDGE,"E1217"),sQuery(id+"F1.wireOp",EDGE,"E1218"),sQuery(id+"F1.wireOp",EDGE,"E1219"),sQuery(id+"F1.wireOp",EDGE,"E1220"),sQuery(id+"F1.wireOp",EDGE,"E1221"),sQuery(id+"F1.wireOp",EDGE,"E1222"),sQuery(id+"F1.wireOp",EDGE,"E1223"),sQuery(id+"F1.wireOp",EDGE,"E1224"),sQuery(id+"F1.wireOp",EDGE,"E1225"),sQuery(id+"F1.wireOp",EDGE,"E1226"),sQuery(id+"F1.wireOp",EDGE,"E1227"),sQuery(id+"F1.wireOp",EDGE,"E1228"),sQuery(id+"F1.wireOp",EDGE,"E1229"),sQuery(id+"F1.wireOp",EDGE,"E1230"),sQuery(id+"F1.wireOp",EDGE,"E1231"),sQuery(id+"F1.wireOp",EDGE,"E1232"),sQuery(id+"F1.wireOp",EDGE,"E1233"),sQuery(id+"F1.wireOp",EDGE,"E1234"),sQuery(id+"F1.wireOp",EDGE,"E1235"),sQuery(id+"F1.wireOp",EDGE,"E1236"),sQuery(id+"F1.wireOp",EDGE,"E1237"),sQuery(id+"F1.wireOp",EDGE,"E1238"),sQuery(id+"F1.wireOp",EDGE,"E1239"),sQuery(id+"F1.wireOp",EDGE,"E1240"),sQuery(id+"F1.wireOp",EDGE,"E1241"),sQuery(id+"F1.wireOp",EDGE,"E1242"),sQuery(id+"F1.wireOp",EDGE,"E1243"),sQuery(id+"F1.wireOp",EDGE,"E1244"),sQuery(id+"F1.wireOp",EDGE,"E1245"),sQuery(id+"F1.wireOp",EDGE,"E1246"),sQuery(id+"F1.wireOp",EDGE,"E1247"),sQuery(id+"F1.wireOp",EDGE,"E1248"),sQuery(id+"F1.wireOp",EDGE,"E1249"),sQuery(id+"F1.wireOp",EDGE,"E1250"),sQuery(id+"F1.wireOp",EDGE,"E1251"),sQuery(id+"F1.wireOp",EDGE,"E1252"),sQuery(id+"F1.wireOp",EDGE,"E1253"),sQuery(id+"F1.wireOp",EDGE,"E1254"),sQuery(id+"F1.wireOp",EDGE,"E1255"),sQuery(id+"F1.wireOp",EDGE,"E1256"),sQuery(id+"F1.wireOp",EDGE,"E1257"),sQuery(id+"F1.wireOp",EDGE,"E1258"),sQuery(id+"F1.wireOp",EDGE,"E1259"),sQuery(id+"F1.wireOp",EDGE,"E1260"),sQuery(id+"F1.wireOp",EDGE,"E1261"),sQuery(id+"F1.wireOp",EDGE,"E1262"),sQuery(id+"F1.wireOp",EDGE,"E1263"),sQuery(id+"F1.wireOp",EDGE,"E1264"),sQuery(id+"F1.wireOp",EDGE,"E1265"),sQuery(id+"F1.wireOp",EDGE,"E1266"),sQuery(id+"F1.wireOp",EDGE,"E1267"),sQuery(id+"F1.wireOp",EDGE,"E1268"),sQuery(id+"F1.wireOp",EDGE,"E1269"),sQuery(id+"F1.wireOp",EDGE,"E1270"),sQuery(id+"F1.wireOp",EDGE,"E1271"),sQuery(id+"F1.wireOp",EDGE,"E1272"),sQuery(id+"F1.wireOp",EDGE,"E1273"),sQuery(id+"F1.wireOp",EDGE,"E1274"),sQuery(id+"F1.wireOp",EDGE,"E1275"),sQuery(id+"F1.wireOp",EDGE,"E1276"),sQuery(id+"F1.wireOp",EDGE,"E1277"),sQuery(id+"F1.wireOp",EDGE,"E1278"),sQuery(id+"F1.wireOp",EDGE,"E1279"),sQuery(id+"F1.wireOp",EDGE,"E1280"),sQuery(id+"F1.wireOp",EDGE,"E1281"),sQuery(id+"F1.wireOp",EDGE,"E1282"),sQuery(id+"F1.wireOp",EDGE,"E1283"),sQuery(id+"F1.wireOp",EDGE,"E1284"),sQuery(id+"F1.wireOp",EDGE,"E1285"),sQuery(id+"F1.wireOp",EDGE,"E1286"),sQuery(id+"F1.wireOp",EDGE,"E1287"),sQuery(id+"F1.wireOp",EDGE,"E1288"),sQuery(id+"F1.wireOp",EDGE,"E1289"),sQuery(id+"F1.wireOp",EDGE,"E1290"),sQuery(id+"F1.wireOp",EDGE,"E1291"),sQuery(id+"F1.wireOp",EDGE,"E1292"),sQuery(id+"F1.wireOp",EDGE,"E1293"),sQuery(id+"F1.wireOp",EDGE,"E1294"),sQuery(id+"F1.wireOp",EDGE,"E1295"),sQuery(id+"F1.wireOp",EDGE,"E1296"),sQuery(id+"F1.wireOp",EDGE,"E1297"),sQuery(id+"F1.wireOp",EDGE,"E1298"),sQuery(id+"F1.wireOp",EDGE,"E1299"),sQuery(id+"F1.wireOp",EDGE,"E1300"),sQuery(id+"F1.wireOp",EDGE,"E1301"),sQuery(id+"F1.wireOp",EDGE,"E1302"),sQuery(id+"F1.wireOp",EDGE,"E1303"),sQuery(id+"F1.wireOp",EDGE,"E1304"),sQuery(id+"F1.wireOp",EDGE,"E1305"),sQuery(id+"F1.wireOp",EDGE,"E1306"),sQuery(id+"F1.wireOp",EDGE,"E1307"),sQuery(id+"F1.wireOp",EDGE,"E1308"),sQuery(id+"F1.wireOp",EDGE,"E1309"),sQuery(id+"F1.wireOp",EDGE,"E1310"),sQuery(id+"F1.wireOp",EDGE,"E1311"),sQuery(id+"F1.wireOp",EDGE,"E1312"),sQuery(id+"F1.wireOp",EDGE,"E1312"),sQuery(id+"F1.wireOp",EDGE,"E1313"),sQuery(id+"F1.wireOp",EDGE,"E1314"),sQuery(id+"F1.wireOp",EDGE,"E1315"),sQuery(id+"F1.wireOp",EDGE,"E1316"),sQuery(id+"F1.wireOp",EDGE,"E1317"),sQuery(id+"F1.wireOp",EDGE,"E1318"),sQuery(id+"F1.wireOp",EDGE,"E1319"),sQuery(id+"F1.wireOp",EDGE,"E1320"),sQuery(id+"F1.wireOp",EDGE,"E1321"),sQuery(id+"F1.wireOp",EDGE,"E1322"),sQuery(id+"F1.wireOp",EDGE,"E1323"),sQuery(id+"F1.wireOp",EDGE,"E1324"),sQuery(id+"F1.wireOp",EDGE,"E1325"),sQuery(id+"F1.wireOp",EDGE,"E1326"),sQuery(id+"F1.wireOp",EDGE,"E1327"),sQuery(id+"F1.wireOp",EDGE,"E1328"),sQuery(id+"F1.wireOp",EDGE,"E1329"),sQuery(id+"F1.wireOp",EDGE,"E1330"),sQuery(id+"F1.wireOp",EDGE,"E1331"),sQuery(id+"F1.wireOp",EDGE,"E1332"),sQuery(id+"F1.wireOp",EDGE,"E1333"),sQuery(id+"F1.wireOp",EDGE,"E1334"),sQuery(id+"F1.wireOp",EDGE,"E1335"),sQuery(id+"F1.wireOp",EDGE,"E1336"),sQuery(id+"F1.wireOp",EDGE,"E1337"),sQuery(id+"F1.wireOp",EDGE,"E1338"),sQuery(id+"F1.wireOp",EDGE,"E1339"),sQuery(id+"F1.wireOp",EDGE,"E1340"),sQuery(id+"F1.wireOp",EDGE,"E1341"),sQuery(id+"F1.wireOp",EDGE,"E1342"),sQuery(id+"F1.wireOp",EDGE,"E1343"),sQuery(id+"F1.wireOp",EDGE,"E1344"),sQuery(id+"F1.wireOp",EDGE,"E1345"),sQuery(id+"F1.wireOp",EDGE,"E1346"),sQuery(id+"F1.wireOp",EDGE,"E1347"),sQuery(id+"F1.wireOp",EDGE,"E1348"),sQuery(id+"F1.wireOp",EDGE,"E1349"),sQuery(id+"F1.wireOp",EDGE,"E1350"),sQuery(id+"F1.wireOp",EDGE,"E1351"),sQuery(id+"F1.wireOp",EDGE,"E1352"),sQuery(id+"F1.wireOp",EDGE,"E1353"),sQuery(id+"F1.wireOp",EDGE,"E1354"),sQuery(id+"F1.wireOp",EDGE,"E1355"),sQuery(id+"F1.wireOp",EDGE,"E1356"),sQuery(id+"F1.wireOp",EDGE,"E1357"),sQuery(id+"F1.wireOp",EDGE,"E1358"),sQuery(id+"F1.wireOp",EDGE,"E1359"),sQuery(id+"F1.wireOp",EDGE,"E1360"),sQuery(id+"F1.wireOp",EDGE,"E1361"),sQuery(id+"F1.wireOp",EDGE,"E1362"),sQuery(id+"F1.wireOp",EDGE,"E1363"),sQuery(id+"F1.wireOp",EDGE,"E1364"),sQuery(id+"F1.wireOp",EDGE,"E1365"),sQuery(id+"F1.wireOp",EDGE,"E1366"),sQuery(id+"F1.wireOp",EDGE,"E1367"),sQuery(id+"F1.wireOp",EDGE,"E1368"),sQuery(id+"F1.wireOp",EDGE,"E1369"),sQuery(id+"F1.wireOp",EDGE,"E1370"),sQuery(id+"F1.wireOp",EDGE,"E1371"),sQuery(id+"F1.wireOp",EDGE,"E1372"),sQuery(id+"F1.wireOp",EDGE,"E1373"),sQuery(id+"F1.wireOp",EDGE,"E1374"),sQuery(id+"F1.wireOp",EDGE,"E1375"),sQuery(id+"F1.wireOp",EDGE,"E1376"),sQuery(id+"F1.wireOp",EDGE,"E1376"),sQuery(id+"F1.wireOp",EDGE,"E1377"),sQuery(id+"F1.wireOp",EDGE,"E1378"),sQuery(id+"F1.wireOp",EDGE,"E1379"),sQuery(id+"F1.wireOp",EDGE,"E1380"),sQuery(id+"F1.wireOp",EDGE,"E1381"),sQuery(id+"F1.wireOp",EDGE,"E1382"),sQuery(id+"F1.wireOp",EDGE,"E1383"),sQuery(id+"F1.wireOp",EDGE,"E1384"),sQuery(id+"F1.wireOp",EDGE,"E1385"),sQuery(id+"F1.wireOp",EDGE,"E1386"),sQuery(id+"F1.wireOp",EDGE,"E1387"),sQuery(id+"F1.wireOp",EDGE,"E1388"),sQuery(id+"F1.wireOp",EDGE,"E1389"),sQuery(id+"F1.wireOp",EDGE,"E1390"),sQuery(id+"F1.wireOp",EDGE,"E1391"),sQuery(id+"F1.wireOp",EDGE,"E1392"),sQuery(id+"F1.wireOp",EDGE,"E1393"),sQuery(id+"F1.wireOp",EDGE,"E1394"),sQuery(id+"F1.wireOp",EDGE,"E1395"),sQuery(id+"F1.wireOp",EDGE,"E1396"),sQuery(id+"F1.wireOp",EDGE,"E1397"),sQuery(id+"F1.wireOp",EDGE,"E1398"),sQuery(id+"F1.wireOp",EDGE,"E1399"),sQuery(id+"F1.wireOp",EDGE,"E1400"),sQuery(id+"F1.wireOp",EDGE,"E1401"),sQuery(id+"F1.wireOp",EDGE,"E1402"),sQuery(id+"F1.wireOp",EDGE,"E1403"),sQuery(id+"F1.wireOp",EDGE,"E1404"),sQuery(id+"F1.wireOp",EDGE,"E1405"),sQuery(id+"F1.wireOp",EDGE,"E1406"),sQuery(id+"F1.wireOp",EDGE,"E1407"),sQuery(id+"F1.wireOp",EDGE,"E1408"),sQuery(id+"F1.wireOp",EDGE,"E1409"),sQuery(id+"F1.wireOp",EDGE,"E1410"),sQuery(id+"F1.wireOp",EDGE,"E1411"),sQuery(id+"F1.wireOp",EDGE,"E1412"),sQuery(id+"F1.wireOp",EDGE,"E1413"),sQuery(id+"F1.wireOp",EDGE,"E1414"),sQuery(id+"F1.wireOp",EDGE,"E1415"),sQuery(id+"F1.wireOp",EDGE,"E1416"),sQuery(id+"F1.wireOp",EDGE,"E1417"),sQuery(id+"F1.wireOp",EDGE,"E1418"),sQuery(id+"F1.wireOp",EDGE,"E1419"),sQuery(id+"F1.wireOp",EDGE,"E1420"),sQuery(id+"F1.wireOp",EDGE,"E1421"),sQuery(id+"F1.wireOp",EDGE,"E1422"),sQuery(id+"F1.wireOp",EDGE,"E1423"),sQuery(id+"F1.wireOp",EDGE,"E1424"),sQuery(id+"F1.wireOp",EDGE,"E1425"),sQuery(id+"F1.wireOp",EDGE,"E1426"),sQuery(id+"F1.wireOp",EDGE,"E1427"),sQuery(id+"F1.wireOp",EDGE,"E1428"),sQuery(id+"F1.wireOp",EDGE,"E1429"),sQuery(id+"F1.wireOp",EDGE,"E1430"),sQuery(id+"F1.wireOp",EDGE,"E1431"),sQuery(id+"F1.wireOp",EDGE,"E1432"),sQuery(id+"F1.wireOp",EDGE,"E1433"),sQuery(id+"F1.wireOp",EDGE,"E1434"),sQuery(id+"F1.wireOp",EDGE,"E1435"),sQuery(id+"F1.wireOp",EDGE,"E1436"),sQuery(id+"F1.wireOp",EDGE,"E1437"),sQuery(id+"F1.wireOp",EDGE,"E1438"),sQuery(id+"F1.wireOp",EDGE,"E1439"),sQuery(id+"F1.wireOp",EDGE,"E1440"),sQuery(id+"F1.wireOp",EDGE,"E1441"),sQuery(id+"F1.wireOp",EDGE,"E1442"),sQuery(id+"F1.wireOp",EDGE,"E1443"),sQuery(id+"F1.wireOp",EDGE,"E1444"),sQuery(id+"F1.wireOp",EDGE,"E1445"),sQuery(id+"F1.wireOp",EDGE,"E1446"),sQuery(id+"F1.wireOp",EDGE,"E1447"),sQuery(id+"F1.wireOp",EDGE,"E1448"),sQuery(id+"F1.wireOp",EDGE,"E1449"),sQuery(id+"F1.wireOp",EDGE,"E1450"),sQuery(id+"F1.wireOp",EDGE,"E1451"),sQuery(id+"F1.wireOp",EDGE,"E1452"),sQuery(id+"F1.wireOp",EDGE,"E1453"),sQuery(id+"F1.wireOp",EDGE,"E1454"),sQuery(id+"F1.wireOp",EDGE,"E1455"),sQuery(id+"F1.wireOp",EDGE,"E1456"),sQuery(id+"F1.wireOp",EDGE,"E1457"),sQuery(id+"F1.wireOp",EDGE,"E1458"),sQuery(id+"F1.wireOp",EDGE,"E1459"),sQuery(id+"F1.wireOp",EDGE,"E1460"),sQuery(id+"F1.wireOp",EDGE,"E1461"),sQuery(id+"F1.wireOp",EDGE,"E1462"),sQuery(id+"F1.wireOp",EDGE,"E1463"),sQuery(id+"F1.wireOp",EDGE,"E1464"),sQuery(id+"F1.wireOp",EDGE,"E1465"),sQuery(id+"F1.wireOp",EDGE,"E1466"),sQuery(id+"F1.wireOp",EDGE,"E1467"),sQuery(id+"F1.wireOp",EDGE,"E1468"),sQuery(id+"F1.wireOp",EDGE,"E1469"),sQuery(id+"F1.wireOp",EDGE,"E1470"),sQuery(id+"F1.wireOp",EDGE,"E1471"),sQuery(id+"F1.wireOp",EDGE,"E1472"),sQuery(id+"F1.wireOp",EDGE,"E1473"),sQuery(id+"F1.wireOp",EDGE,"E1474"),sQuery(id+"F1.wireOp",EDGE,"E1475"),sQuery(id+"F1.wireOp",EDGE,"E1476"),sQuery(id+"F1.wireOp",EDGE,"E1477"),sQuery(id+"F1.wireOp",EDGE,"E1478"),sQuery(id+"F1.wireOp",EDGE,"E1479"),sQuery(id+"F1.wireOp",EDGE,"E1480"),sQuery(id+"F1.wireOp",EDGE,"E1481"),sQuery(id+"F1.wireOp",EDGE,"E1482"),sQuery(id+"F1.wireOp",EDGE,"E1483"),sQuery(id+"F1.wireOp",EDGE,"E1484"),sQuery(id+"F1.wireOp",EDGE,"E1485"),sQuery(id+"F1.wireOp",EDGE,"E1486"),sQuery(id+"F1.wireOp",EDGE,"E1487"),sQuery(id+"F1.wireOp",EDGE,"E1488"),sQuery(id+"F1.wireOp",EDGE,"E1489"),sQuery(id+"F1.wireOp",EDGE,"E1490"),sQuery(id+"F1.wireOp",EDGE,"E1491"),sQuery(id+"F1.wireOp",EDGE,"E1492"),sQuery(id+"F1.wireOp",EDGE,"E1493"),sQuery(id+"F1.wireOp",EDGE,"E1494"),sQuery(id+"F1.wireOp",EDGE,"E1495"),sQuery(id+"F1.wireOp",EDGE,"E1496"),sQuery(id+"F1.wireOp",EDGE,"E1497"),sQuery(id+"F1.wireOp",EDGE,"E1498"),sQuery(id+"F1.wireOp",EDGE,"E1499"),sQuery(id+"F1.wireOp",EDGE,"E1500"),sQuery(id+"F1.wireOp",EDGE,"E1501"),sQuery(id+"F1.wireOp",EDGE,"E1502"),sQuery(id+"F1.wireOp",EDGE,"E1503"),sQuery(id+"F1.wireOp",EDGE,"E1504"),sQuery(id+"F1.wireOp",EDGE,"E1505"),sQuery(id+"F1.wireOp",EDGE,"E1506"),sQuery(id+"F1.wireOp",EDGE,"E1507"),sQuery(id+"F1.wireOp",EDGE,"E1508"),sQuery(id+"F1.wireOp",EDGE,"E1509"),sQuery(id+"F1.wireOp",EDGE,"E1510"),sQuery(id+"F1.wireOp",EDGE,"E1511"),sQuery(id+"F1.wireOp",EDGE,"E1512"),sQuery(id+"F1.wireOp",EDGE,"E1513"),sQuery(id+"F1.wireOp",EDGE,"E1514"),sQuery(id+"F1.wireOp",EDGE,"E1515"),sQuery(id+"F1.wireOp",EDGE,"E1516"),sQuery(id+"F1.wireOp",EDGE,"E1517"),sQuery(id+"F1.wireOp",EDGE,"E1518"),sQuery(id+"F1.wireOp",EDGE,"E1519"),sQuery(id+"F1.wireOp",EDGE,"E1520"),sQuery(id+"F1.wireOp",EDGE,"E1521"),sQuery(id+"F1.wireOp",EDGE,"E1522"),sQuery(id+"F1.wireOp",EDGE,"E1523"),sQuery(id+"F1.wireOp",EDGE,"E1524"),sQuery(id+"F1.wireOp",EDGE,"E1525"),sQuery(id+"F1.wireOp",EDGE,"E1526"),sQuery(id+"F1.wireOp",EDGE,"E1527"),sQuery(id+"F1.wireOp",EDGE,"E1528"),sQuery(id+"F1.wireOp",EDGE,"E1529"),sQuery(id+"F1.wireOp",EDGE,"E1530"),sQuery(id+"F1.wireOp",EDGE,"E1531"),sQuery(id+"F1.wireOp",EDGE,"E1532"),sQuery(id+"F1.wireOp",EDGE,"E1533"),sQuery(id+"F1.wireOp",EDGE,"E1534"),sQuery(id+"F1.wireOp",EDGE,"E1535"),sQuery(id+"F1.wireOp",EDGE,"E1536"),sQuery(id+"F1.wireOp",EDGE,"E1537"),sQuery(id+"F1.wireOp",EDGE,"E1538"),sQuery(id+"F1.wireOp",EDGE,"E1539"),sQuery(id+"F1.wireOp",EDGE,"E1540"),sQuery(id+"F1.wireOp",EDGE,"E1541"),sQuery(id+"F1.wireOp",EDGE,"E1542"),sQuery(id+"F1.wireOp",EDGE,"E1543"),sQuery(id+"F1.wireOp",EDGE,"E1544"),sQuery(id+"F1.wireOp",EDGE,"E1545"),sQuery(id+"F1.wireOp",EDGE,"E1546"),sQuery(id+"F1.wireOp",EDGE,"E1547"),sQuery(id+"F1.wireOp",EDGE,"E1548"),sQuery(id+"F1.wireOp",EDGE,"E1549"),sQuery(id+"F1.wireOp",EDGE,"E1550"),sQuery(id+"F1.wireOp",EDGE,"E1551"),sQuery(id+"F1.wireOp",EDGE,"E1552"),sQuery(id+"F1.wireOp",EDGE,"E1553"),sQuery(id+"F1.wireOp",EDGE,"E1554"),sQuery(id+"F1.wireOp",EDGE,"E1555"),sQuery(id+"F1.wireOp",EDGE,"E1556"),sQuery(id+"F1.wireOp",EDGE,"E1557"),sQuery(id+"F1.wireOp",EDGE,"E1558"),sQuery(id+"F1.wireOp",EDGE,"E1559"),sQuery(id+"F1.wireOp",EDGE,"E1560"),sQuery(id+"F1.wireOp",EDGE,"E1561"),sQuery(id+"F1.wireOp",EDGE,"E1562"),sQuery(id+"F1.wireOp",EDGE,"E1563"),sQuery(id+"F1.wireOp",EDGE,"E1564"),sQuery(id+"F1.wireOp",EDGE,"E1565"),sQuery(id+"F1.wireOp",EDGE,"E1566"),sQuery(id+"F1.wireOp",EDGE,"E1567"),sQuery(id+"F1.wireOp",EDGE,"E1568"),sQuery(id+"F1.wireOp",EDGE,"E1569"),sQuery(id+"F1.wireOp",EDGE,"E1570"),sQuery(id+"F1.wireOp",EDGE,"E1571"),sQuery(id+"F1.wireOp",EDGE,"E1572"),sQuery(id+"F1.wireOp",EDGE,"E1573"),sQuery(id+"F1.wireOp",EDGE,"E1574"),sQuery(id+"F1.wireOp",EDGE,"E1575"),sQuery(id+"F1.wireOp",EDGE,"E1576"),sQuery(id+"F1.wireOp",EDGE,"E1577"),sQuery(id+"F1.wireOp",EDGE,"E1578"),sQuery(id+"F1.wireOp",EDGE,"E1579"),sQuery(id+"F1.wireOp",EDGE,"E1580"),sQuery(id+"F1.wireOp",EDGE,"E1581"),sQuery(id+"F1.wireOp",EDGE,"E1582"),sQuery(id+"F1.wireOp",EDGE,"E1583"),sQuery(id+"F1.wireOp",EDGE,"E1584"),sQuery(id+"F1.wireOp",EDGE,"E1585"),sQuery(id+"F1.wireOp",EDGE,"E1586"),sQuery(id+"F1.wireOp",EDGE,"E1587"),sQuery(id+"F1.wireOp",EDGE,"E1588"),sQuery(id+"F1.wireOp",EDGE,"E1589"),sQuery(id+"F1.wireOp",EDGE,"E1590"),sQuery(id+"F1.wireOp",EDGE,"E1591"),sQuery(id+"F1.wireOp",EDGE,"E1592"),sQuery(id+"F1.wireOp",EDGE,"E1593"),sQuery(id+"F1.wireOp",EDGE,"E1594"),sQuery(id+"F1.wireOp",EDGE,"E1595"),sQuery(id+"F1.wireOp",EDGE,"E1596"),sQuery(id+"F1.wireOp",EDGE,"E1597"),sQuery(id+"F1.wireOp",EDGE,"E1598"),sQuery(id+"F1.wireOp",EDGE,"E1599"),sQuery(id+"F1.wireOp",EDGE,"E1600"),sQuery(id+"F1.wireOp",EDGE,"E1601"),sQuery(id+"F1.wireOp",EDGE,"E1602"),sQuery(id+"F1.wireOp",EDGE,"E1603"),sQuery(id+"F1.wireOp",EDGE,"E1604"),sQuery(id+"F1.wireOp",EDGE,"E1605"),sQuery(id+"F1.wireOp",EDGE,"E1606"),sQuery(id+"F1.wireOp",EDGE,"E1607"),sQuery(id+"F1.wireOp",EDGE,"E1608"),sQuery(id+"F1.wireOp",EDGE,"E1609"),sQuery(id+"F1.wireOp",EDGE,"E1610"),sQuery(id+"F1.wireOp",EDGE,"E1611"),sQuery(id+"F1.wireOp",EDGE,"E1612"),sQuery(id+"F1.wireOp",EDGE,"E1613"),sQuery(id+"F1.wireOp",EDGE,"E1614"),sQuery(id+"F1.wireOp",EDGE,"E1615"),sQuery(id+"F1.wireOp",EDGE,"E1616"),sQuery(id+"F1.wireOp",EDGE,"E1617"),sQuery(id+"F1.wireOp",EDGE,"E1618"),sQuery(id+"F1.wireOp",EDGE,"E1619"),sQuery(id+"F1.wireOp",EDGE,"E1620"),sQuery(id+"F1.wireOp",EDGE,"E1621"),sQuery(id+"F1.wireOp",EDGE,"E1622"),sQuery(id+"F1.wireOp",EDGE,"E1623"),sQuery(id+"F1.wireOp",EDGE,"E1624"),sQuery(id+"F1.wireOp",EDGE,"E1625"),sQuery(id+"F1.wireOp",EDGE,"E1626"),sQuery(id+"F1.wireOp",EDGE,"E1627"),sQuery(id+"F1.wireOp",EDGE,"E1628"),sQuery(id+"F1.wireOp",EDGE,"E1629"),sQuery(id+"F1.wireOp",EDGE,"E1630"),sQuery(id+"F1.wireOp",EDGE,"E1631"),sQuery(id+"F1.wireOp",EDGE,"E1632"),sQuery(id+"F1.wireOp",EDGE,"E1633"),sQuery(id+"F1.wireOp",EDGE,"E1634"),sQuery(id+"F1.wireOp",EDGE,"E1635"),sQuery(id+"F1.wireOp",EDGE,"E1636"),sQuery(id+"F1.wireOp",EDGE,"E1637"),sQuery(id+"F1.wireOp",EDGE,"E1638"),sQuery(id+"F1.wireOp",EDGE,"E1639"),sQuery(id+"F1.wireOp",EDGE,"E1640"),sQuery(id+"F1.wireOp",EDGE,"E1641"),sQuery(id+"F1.wireOp",EDGE,"E1642"),sQuery(id+"F1.wireOp",EDGE,"E1643"),sQuery(id+"F1.wireOp",EDGE,"E1644"),sQuery(id+"F1.wireOp",EDGE,"E1645"),sQuery(id+"F1.wireOp",EDGE,"E1646"),sQuery(id+"F1.wireOp",EDGE,"E1647"),sQuery(id+"F1.wireOp",EDGE,"E1648"),sQuery(id+"F1.wireOp",EDGE,"E1649"),sQuery(id+"F1.wireOp",EDGE,"E1650"),sQuery(id+"F1.wireOp",EDGE,"E1651"),sQuery(id+"F1.wireOp",EDGE,"E1652"),sQuery(id+"F1.wireOp",EDGE,"E1653"),sQuery(id+"F1.wireOp",EDGE,"E1654"),sQuery(id+"F1.wireOp",EDGE,"E1655"),sQuery(id+"F1.wireOp",EDGE,"E1656"),sQuery(id+"F1.wireOp",EDGE,"E1657"),sQuery(id+"F1.wireOp",EDGE,"E1658"),sQuery(id+"F1.wireOp",EDGE,"E1659"),sQuery(id+"F1.wireOp",EDGE,"E1660"),sQuery(id+"F1.wireOp",EDGE,"E1661"),sQuery(id+"F1.wireOp",EDGE,"E1662"),sQuery(id+"F1.wireOp",EDGE,"E1663"),sQuery(id+"F1.wireOp",EDGE,"E1664"),sQuery(id+"F1.wireOp",EDGE,"E1665"),sQuery(id+"F1.wireOp",EDGE,"E1666"),sQuery(id+"F1.wireOp",EDGE,"E1667"),sQuery(id+"F1.wireOp",EDGE,"E1668"),sQuery(id+"F1.wireOp",EDGE,"E1669"),sQuery(id+"F1.wireOp",EDGE,"E1670"),sQuery(id+"F1.wireOp",EDGE,"E1671"),sQuery(id+"F1.wireOp",EDGE,"E1672"),sQuery(id+"F1.wireOp",EDGE,"E1673"),sQuery(id+"F1.wireOp",EDGE,"E1674"),sQuery(id+"F1.wireOp",EDGE,"E1675"),sQuery(id+"F1.wireOp",EDGE,"E1676"),sQuery(id+"F1.wireOp",EDGE,"E1677"),sQuery(id+"F1.wireOp",EDGE,"E1678"),sQuery(id+"F1.wireOp",EDGE,"E1679"),sQuery(id+"F1.wireOp",EDGE,"E1680"),sQuery(id+"F1.wireOp",EDGE,"E1681"),sQuery(id+"F1.wireOp",EDGE,"E1682"),sQuery(id+"F1.wireOp",EDGE,"E1683"),sQuery(id+"F1.wireOp",EDGE,"E1684"),sQuery(id+"F1.wireOp",EDGE,"E1685"),sQuery(id+"F1.wireOp",EDGE,"E1686"),sQuery(id+"F1.wireOp",EDGE,"E1687"),sQuery(id+"F1.wireOp",EDGE,"E1688"),sQuery(id+"F1.wireOp",EDGE,"E1689"),sQuery(id+"F1.wireOp",EDGE,"E1690"),sQuery(id+"F1.wireOp",EDGE,"E1691"),sQuery(id+"F1.wireOp",EDGE,"E1692"),sQuery(id+"F1.wireOp",EDGE,"E1693"),sQuery(id+"F1.wireOp",EDGE,"E1694"),sQuery(id+"F1.wireOp",EDGE,"E1695"),sQuery(id+"F1.wireOp",EDGE,"E1696"),sQuery(id+"F1.wireOp",EDGE,"E1697"),sQuery(id+"F1.wireOp",EDGE,"E1698"),sQuery(id+"F1.wireOp",EDGE,"E1699"),sQuery(id+"F1.wireOp",EDGE,"E1700"),sQuery(id+"F1.wireOp",EDGE,"E1701"),sQuery(id+"F1.wireOp",EDGE,"E1702"),sQuery(id+"F1.wireOp",EDGE,"E1703"),sQuery(id+"F1.wireOp",EDGE,"E1704"),sQuery(id+"F1.wireOp",EDGE,"E1705"),sQuery(id+"F1.wireOp",EDGE,"E1706"),sQuery(id+"F1.wireOp",EDGE,"E1707"),sQuery(id+"F1.wireOp",EDGE,"E1708"),sQuery(id+"F1.wireOp",EDGE,"E1709"),sQuery(id+"F1.wireOp",EDGE,"E1710"),sQuery(id+"F1.wireOp",EDGE,"E1711"),sQuery(id+"F1.wireOp",EDGE,"E1712"),sQuery(id+"F1.wireOp",EDGE,"E1713"),sQuery(id+"F1.wireOp",EDGE,"E1714"),sQuery(id+"F1.wireOp",EDGE,"E1715"),sQuery(id+"F1.wireOp",EDGE,"E1716"),sQuery(id+"F1.wireOp",EDGE,"E1717"),sQuery(id+"F1.wireOp",EDGE,"E1718"),sQuery(id+"F1.wireOp",EDGE,"E1719"),sQuery(id+"F1.wireOp",EDGE,"E1720"),sQuery(id+"F1.wireOp",EDGE,"E1721"),sQuery(id+"F1.wireOp",EDGE,"E1722"),sQuery(id+"F1.wireOp",EDGE,"E1723"),sQuery(id+"F1.wireOp",EDGE,"E1724"),sQuery(id+"F1.wireOp",EDGE,"E1725"),sQuery(id+"F1.wireOp",EDGE,"E1726"),sQuery(id+"F1.wireOp",EDGE,"E1727"),sQuery(id+"F1.wireOp",EDGE,"E1728"),sQuery(id+"F1.wireOp",EDGE,"E1729"),sQuery(id+"F1.wireOp",EDGE,"E1730"),sQuery(id+"F1.wireOp",EDGE,"E1731"),sQuery(id+"F1.wireOp",EDGE,"E1732"),sQuery(id+"F1.wireOp",EDGE,"E1733"),sQuery(id+"F1.wireOp",EDGE,"E1734"),sQuery(id+"F1.wireOp",EDGE,"E1735"),sQuery(id+"F1.wireOp",EDGE,"E1736"),sQuery(id+"F1.wireOp",EDGE,"E1737"),sQuery(id+"F1.wireOp",EDGE,"E1738"),sQuery(id+"F1.wireOp",EDGE,"E1739"),sQuery(id+"F1.wireOp",EDGE,"E1740"),sQuery(id+"F1.wireOp",EDGE,"E1741"),sQuery(id+"F1.wireOp",EDGE,"E1742"),sQuery(id+"F1.wireOp",EDGE,"E1743"),sQuery(id+"F1.wireOp",EDGE,"E1744"),sQuery(id+"F1.wireOp",EDGE,"E1745"),sQuery(id+"F1.wireOp",EDGE,"E1746"),sQuery(id+"F1.wireOp",EDGE,"E1747"),sQuery(id+"F1.wireOp",EDGE,"E1748"),sQuery(id+"F1.wireOp",EDGE,"E1749"),sQuery(id+"F1.wireOp",EDGE,"E1750"),sQuery(id+"F1.wireOp",EDGE,"E1751"),sQuery(id+"F1.wireOp",EDGE,"E1752"),sQuery(id+"F1.wireOp",EDGE,"E1753"),sQuery(id+"F1.wireOp",EDGE,"E1754"),sQuery(id+"F1.wireOp",EDGE,"E1755"),sQuery(id+"F1.wireOp",EDGE,"E1756"),sQuery(id+"F1.wireOp",EDGE,"E1757"),sQuery(id+"F1.wireOp",EDGE,"E1758"),sQuery(id+"F1.wireOp",EDGE,"E1759"),sQuery(id+"F1.wireOp",EDGE,"E1760"),sQuery(id+"F1.wireOp",EDGE,"E1761"),sQuery(id+"F1.wireOp",EDGE,"E1762"),sQuery(id+"F1.wireOp",EDGE,"E1763"),sQuery(id+"F1.wireOp",EDGE,"E1764"),sQuery(id+"F1.wireOp",EDGE,"E1765"),sQuery(id+"F1.wireOp",EDGE,"E1766"),sQuery(id+"F1.wireOp",EDGE,"E1767"),sQuery(id+"F1.wireOp",EDGE,"E1768"),sQuery(id+"F1.wireOp",EDGE,"E1769"),sQuery(id+"F1.wireOp",EDGE,"E1770"),sQuery(id+"F1.wireOp",EDGE,"E1771"),sQuery(id+"F1.wireOp",EDGE,"E1772"),sQuery(id+"F1.wireOp",EDGE,"E1773"),sQuery(id+"F1.wireOp",EDGE,"E1774"),sQuery(id+"F1.wireOp",EDGE,"E1775"),sQuery(id+"F1.wireOp",EDGE,"E1776"),sQuery(id+"F1.wireOp",EDGE,"E1777"),sQuery(id+"F1.wireOp",EDGE,"E1778"),sQuery(id+"F1.wireOp",EDGE,"E1779"),sQuery(id+"F1.wireOp",EDGE,"E1780"),sQuery(id+"F1.wireOp",EDGE,"E1781"),sQuery(id+"F1.wireOp",EDGE,"E1782"),sQuery(id+"F1.wireOp",EDGE,"E1783"),sQuery(id+"F1.wireOp",EDGE,"E1784"),sQuery(id+"F1.wireOp",EDGE,"E1785"),sQuery(id+"F1.wireOp",EDGE,"E1786"),sQuery(id+"F1.wireOp",EDGE,"E1787"),sQuery(id+"F1.wireOp",EDGE,"E1788"),sQuery(id+"F1.wireOp",EDGE,"E1789"),sQuery(id+"F1.wireOp",EDGE,"E1790"),sQuery(id+"F1.wireOp",EDGE,"E1791"),sQuery(id+"F1.wireOp",EDGE,"E1792"),sQuery(id+"F1.wireOp",EDGE,"E1793"),sQuery(id+"F1.wireOp",EDGE,"E1794"),sQuery(id+"F1.wireOp",EDGE,"E1795"),sQuery(id+"F1.wireOp",EDGE,"E1796"),sQuery(id+"F1.wireOp",EDGE,"E1797"),sQuery(id+"F1.wireOp",EDGE,"E1798"),sQuery(id+"F1.wireOp",EDGE,"E1799"),sQuery(id+"F1.wireOp",EDGE,"E1800"),sQuery(id+"F1.wireOp",EDGE,"E1801"),sQuery(id+"F1.wireOp",EDGE,"E1802"),sQuery(id+"F1.wireOp",EDGE,"E1803"),sQuery(id+"F1.wireOp",EDGE,"E1804"),sQuery(id+"F1.wireOp",EDGE,"E1805"),sQuery(id+"F1.wireOp",EDGE,"E1806"),sQuery(id+"F1.wireOp",EDGE,"E1807"),sQuery(id+"F1.wireOp",EDGE,"E1808"),sQuery(id+"F1.wireOp",EDGE,"E1809"),sQuery(id+"F1.wireOp",EDGE,"E1810"),sQuery(id+"F1.wireOp",EDGE,"E1811"),sQuery(id+"F1.wireOp",EDGE,"E1812"),sQuery(id+"F1.wireOp",EDGE,"E1813"),sQuery(id+"F1.wireOp",EDGE,"E1814"),sQuery(id+"F1.wireOp",EDGE,"E1815"),sQuery(id+"F1.wireOp",EDGE,"E1816"),sQuery(id+"F1.wireOp",EDGE,"E1817"),sQuery(id+"F1.wireOp",EDGE,"E1818"),sQuery(id+"F1.wireOp",EDGE,"E1819"),sQuery(id+"F1.wireOp",EDGE,"E1820"),sQuery(id+"F1.wireOp",EDGE,"E1821"),sQuery(id+"F1.wireOp",EDGE,"E1822"),sQuery(id+"F1.wireOp",EDGE,"E1823"),sQuery(id+"F1.wireOp",EDGE,"E1824"),sQuery(id+"F1.wireOp",EDGE,"E1825"),sQuery(id+"F1.wireOp",EDGE,"E1826"),sQuery(id+"F1.wireOp",EDGE,"E1827"),sQuery(id+"F1.wireOp",EDGE,"E1828"),sQuery(id+"F1.wireOp",EDGE,"E1829"),sQuery(id+"F1.wireOp",EDGE,"E1830"),sQuery(id+"F1.wireOp",EDGE,"E1831"),sQuery(id+"F1.wireOp",EDGE,"E1832"),sQuery(id+"F1.wireOp",EDGE,"E1833"),sQuery(id+"F1.wireOp",EDGE,"E1834"),sQuery(id+"F1.wireOp",EDGE,"E1835"),sQuery(id+"F1.wireOp",EDGE,"E1836"),sQuery(id+"F1.wireOp",EDGE,"E1837"),sQuery(id+"F1.wireOp",EDGE,"E1838"),sQuery(id+"F1.wireOp",EDGE,"E1839"),sQuery(id+"F1.wireOp",EDGE,"E1840"),sQuery(id+"F1.wireOp",EDGE,"E1841"),sQuery(id+"F1.wireOp",EDGE,"E1842"),sQuery(id+"F1.wireOp",EDGE,"E1843"),sQuery(id+"F1.wireOp",EDGE,"E1844"),sQuery(id+"F1.wireOp",EDGE,"E1845"),sQuery(id+"F1.wireOp",EDGE,"E1846"),sQuery(id+"F1.wireOp",EDGE,"E1847"),sQuery(id+"F1.wireOp",EDGE,"E1848"),sQuery(id+"F1.wireOp",EDGE,"E1849"),sQuery(id+"F1.wireOp",EDGE,"E1850"),sQuery(id+"F1.wireOp",EDGE,"E1851"),sQuery(id+"F1.wireOp",EDGE,"E1852"),sQuery(id+"F1.wireOp",EDGE,"E1853"),sQuery(id+"F1.wireOp",EDGE,"E1854"),sQuery(id+"F1.wireOp",EDGE,"E1855"),sQuery(id+"F1.wireOp",EDGE,"E1856"),sQuery(id+"F1.wireOp",EDGE,"E1857"),sQuery(id+"F1.wireOp",EDGE,"E1858"),sQuery(id+"F1.wireOp",EDGE,"E1859"),sQuery(id+"F1.wireOp",EDGE,"E1860"),sQuery(id+"F1.wireOp",EDGE,"E1861"),sQuery(id+"F1.wireOp",EDGE,"E1862"),sQuery(id+"F1.wireOp",EDGE,"E1863"),sQuery(id+"F1.wireOp",EDGE,"E1864"),sQuery(id+"F1.wireOp",EDGE,"E1865"),sQuery(id+"F1.wireOp",EDGE,"E1866"),sQuery(id+"F1.wireOp",EDGE,"E1867"),sQuery(id+"F1.wireOp",EDGE,"E1868"),sQuery(id+"F1.wireOp",EDGE,"E1869"),sQuery(id+"F1.wireOp",EDGE,"E1870"),sQuery(id+"F1.wireOp",EDGE,"E1871"),sQuery(id+"F1.wireOp",EDGE,"E1872"),sQuery(id+"F1.wireOp",EDGE,"E1873"),sQuery(id+"F1.wireOp",EDGE,"E1874"),sQuery(id+"F1.wireOp",EDGE,"E1875"),sQuery(id+"F1.wireOp",EDGE,"E1876"),sQuery(id+"F1.wireOp",EDGE,"E1877"),sQuery(id+"F1.wireOp",EDGE,"E1878"),sQuery(id+"F1.wireOp",EDGE,"E1879"),sQuery(id+"F1.wireOp",EDGE,"E1880"),sQuery(id+"F1.wireOp",EDGE,"E1881"),sQuery(id+"F1.wireOp",EDGE,"E1882"),sQuery(id+"F1.wireOp",EDGE,"E1883"),sQuery(id+"F1.wireOp",EDGE,"E1884"),sQuery(id+"F1.wireOp",EDGE,"E1885"),sQuery(id+"F1.wireOp",EDGE,"E1886"),sQuery(id+"F1.wireOp",EDGE,"E1887"),sQuery(id+"F1.wireOp",EDGE,"E1888"),sQuery(id+"F1.wireOp",EDGE,"E1889"),sQuery(id+"F1.wireOp",EDGE,"E1890"),sQuery(id+"F1.wireOp",EDGE,"E1891"),sQuery(id+"F1.wireOp",EDGE,"E1892"),sQuery(id+"F1.wireOp",EDGE,"E1893"),sQuery(id+"F1.wireOp",EDGE,"E1894"),sQuery(id+"F1.wireOp",EDGE,"E1895"),sQuery(id+"F1.wireOp",EDGE,"E1896"),sQuery(id+"F1.wireOp",EDGE,"E1897"),sQuery(id+"F1.wireOp",EDGE,"E1898"),sQuery(id+"F1.wireOp",EDGE,"E1899"),sQuery(id+"F1.wireOp",EDGE,"E1900"),sQuery(id+"F1.wireOp",EDGE,"E1901"),sQuery(id+"F1.wireOp",EDGE,"E1902"),sQuery(id+"F1.wireOp",EDGE,"E1903"),sQuery(id+"F1.wireOp",EDGE,"E1904"),sQuery(id+"F1.wireOp",EDGE,"E1905"),sQuery(id+"F1.wireOp",EDGE,"E1906"),sQuery(id+"F1.wireOp",EDGE,"E1907"),sQuery(id+"F1.wireOp",EDGE,"E1908"),sQuery(id+"F1.wireOp",EDGE,"E1909"),sQuery(id+"F1.wireOp",EDGE,"E1910"),sQuery(id+"F1.wireOp",EDGE,"E1911"),sQuery(id+"F1.wireOp",EDGE,"E1912"),sQuery(id+"F1.wireOp",EDGE,"E1913"),sQuery(id+"F1.wireOp",EDGE,"E1914"),sQuery(id+"F1.wireOp",EDGE,"E1915"),sQuery(id+"F1.wireOp",EDGE,"E1916"),sQuery(id+"F1.wireOp",EDGE,"E1917"),sQuery(id+"F1.wireOp",EDGE,"E1918"),sQuery(id+"F1.wireOp",EDGE,"E1919"),sQuery(id+"F1.wireOp",EDGE,"E1920"),sQuery(id+"F1.wireOp",EDGE,"E1921"),sQuery(id+"F1.wireOp",EDGE,"E1922"),sQuery(id+"F1.wireOp",EDGE,"E1923"),sQuery(id+"F1.wireOp",EDGE,"E1924"),sQuery(id+"F1.wireOp",EDGE,"E1925"),sQuery(id+"F1.wireOp",EDGE,"E1926"),sQuery(id+"F1.wireOp",EDGE,"E1927"),sQuery(id+"F1.wireOp",EDGE,"E1928"),sQuery(id+"F1.wireOp",EDGE,"E1929"),sQuery(id+"F1.wireOp",EDGE,"E1930"),sQuery(id+"F1.wireOp",EDGE,"E1931"),sQuery(id+"F1.wireOp",EDGE,"E1932"),sQuery(id+"F1.wireOp",EDGE,"E1933"),sQuery(id+"F1.wireOp",EDGE,"E1934"),sQuery(id+"F1.wireOp",EDGE,"E1935"),sQuery(id+"F1.wireOp",EDGE,"E1936"),sQuery(id+"F1.wireOp",EDGE,"E1937"),sQuery(id+"F1.wireOp",EDGE,"E1938"),sQuery(id+"F1.wireOp",EDGE,"E1939"),sQuery(id+"F1.wireOp",EDGE,"E1940"),sQuery(id+"F1.wireOp",EDGE,"E1941"),sQuery(id+"F1.wireOp",EDGE,"E1942"),sQuery(id+"F1.wireOp",EDGE,"E1943"),sQuery(id+"F1.wireOp",EDGE,"E1944"),sQuery(id+"F1.wireOp",EDGE,"E1945"),sQuery(id+"F1.wireOp",EDGE,"E1946"),sQuery(id+"F1.wireOp",EDGE,"E1947"),sQuery(id+"F1.wireOp",EDGE,"E1948"),sQuery(id+"F1.wireOp",EDGE,"E1949"),sQuery(id+"F1.wireOp",EDGE,"E1950"),sQuery(id+"F1.wireOp",EDGE,"E1951"),sQuery(id+"F1.wireOp",EDGE,"E1952"),sQuery(id+"F1.wireOp",EDGE,"E1953"),sQuery(id+"F1.wireOp",EDGE,"E1954"),sQuery(id+"F1.wireOp",EDGE,"E1955"),sQuery(id+"F1.wireOp",EDGE,"E1956"),sQuery(id+"F1.wireOp",EDGE,"E1957"),sQuery(id+"F1.wireOp",EDGE,"E1958"),sQuery(id+"F1.wireOp",EDGE,"E1959"),sQuery(id+"F1.wireOp",EDGE,"E1960"),sQuery(id+"F1.wireOp",EDGE,"E1961"),sQuery(id+"F1.wireOp",EDGE,"E1962"),sQuery(id+"F1.wireOp",EDGE,"E1963"),sQuery(id+"F1.wireOp",EDGE,"E1964"),sQuery(id+"F1.wireOp",EDGE,"E1965"),sQuery(id+"F1.wireOp",EDGE,"E1966"),sQuery(id+"F1.wireOp",EDGE,"E1967"),sQuery(id+"F1.wireOp",EDGE,"E1968"),sQuery(id+"F1.wireOp",EDGE,"E1969"),sQuery(id+"F1.wireOp",EDGE,"E1970"),sQuery(id+"F1.wireOp",EDGE,"E1971"),sQuery(id+"F1.wireOp",EDGE,"E1972"),sQuery(id+"F1.wireOp",EDGE,"E1973"),sQuery(id+"F1.wireOp",EDGE,"E1974"),sQuery(id+"F1.wireOp",EDGE,"E1975"),sQuery(id+"F1.wireOp",EDGE,"E1976"),sQuery(id+"F1.wireOp",EDGE,"E1977"),sQuery(id+"F1.wireOp",EDGE,"E1978"),sQuery(id+"F1.wireOp",EDGE,"E1979"),sQuery(id+"F1.wireOp",EDGE,"E1980"),sQuery(id+"F1.wireOp",EDGE,"E1981"),sQuery(id+"F1.wireOp",EDGE,"E1982"),sQuery(id+"F1.wireOp",EDGE,"E1983"),sQuery(id+"F1.wireOp",EDGE,"E1984"),sQuery(id+"F1.wireOp",EDGE,"E1985"),sQuery(id+"F1.wireOp",EDGE,"E1986"),sQuery(id+"F1.wireOp",EDGE,"E1987"),sQuery(id+"F1.wireOp",EDGE,"E1988"),sQuery(id+"F1.wireOp",EDGE,"E1989"),sQuery(id+"F1.wireOp",EDGE,"E1990"),sQuery(id+"F1.wireOp",EDGE,"E1991"),sQuery(id+"F1.wireOp",EDGE,"E1992"),sQuery(id+"F1.wireOp",EDGE,"E1993"),sQuery(id+"F1.wireOp",EDGE,"E1994"),sQuery(id+"F1.wireOp",EDGE,"E1995"),sQuery(id+"F1.wireOp",EDGE,"E1996"),sQuery(id+"F1.wireOp",EDGE,"E1997"),sQuery(id+"F1.wireOp",EDGE,"E1998"),sQuery(id+"F1.wireOp",EDGE,"E1999"),sQuery(id+"F1.wireOp",EDGE,"E2000"),sQuery(id+"F1.wireOp",EDGE,"E2000"),sQuery(id+"F1.wireOp",EDGE,"E2001"),sQuery(id+"F1.wireOp",EDGE,"E2002"),sQuery(id+"F1.wireOp",EDGE,"E2003"),sQuery(id+"F1.wireOp",EDGE,"E2004"),sQuery(id+"F1.wireOp",EDGE,"E2005"),sQuery(id+"F1.wireOp",EDGE,"E2006"),sQuery(id+"F1.wireOp",EDGE,"E2007"),sQuery(id+"F1.wireOp",EDGE,"E2008"),sQuery(id+"F1.wireOp",EDGE,"E2009"),sQuery(id+"F1.wireOp",EDGE,"E2010"),sQuery(id+"F1.wireOp",EDGE,"E2011"),sQuery(id+"F1.wireOp",EDGE,"E2012"),sQuery(id+"F1.wireOp",EDGE,"E2013"),sQuery(id+"F1.wireOp",EDGE,"E2014"),sQuery(id+"F1.wireOp",EDGE,"E2015"),sQuery(id+"F1.wireOp",EDGE,"E2016"),sQuery(id+"F1.wireOp",EDGE,"E2017"),sQuery(id+"F1.wireOp",EDGE,"E2018"),sQuery(id+"F1.wireOp",EDGE,"E2019"),sQuery(id+"F1.wireOp",EDGE,"E2020"),sQuery(id+"F1.wireOp",EDGE,"E2021"),sQuery(id+"F1.wireOp",EDGE,"E2022"),sQuery(id+"F1.wireOp",EDGE,"E2023"),sQuery(id+"F1.wireOp",EDGE,"E2024"),sQuery(id+"F1.wireOp",EDGE,"E2025"),sQuery(id+"F1.wireOp",EDGE,"E2026"),sQuery(id+"F1.wireOp",EDGE,"E2027"),sQuery(id+"F1.wireOp",EDGE,"E2028"),sQuery(id+"F1.wireOp",EDGE,"E2029"),sQuery(id+"F1.wireOp",EDGE,"E2030"),sQuery(id+"F1.wireOp",EDGE,"E2031"),sQuery(id+"F1.wireOp",EDGE,"E2032"),sQuery(id+"F1.wireOp",EDGE,"E2033"),sQuery(id+"F1.wireOp",EDGE,"E2034"),sQuery(id+"F1.wireOp",EDGE,"E2035"),sQuery(id+"F1.wireOp",EDGE,"E2036"),sQuery(id+"F1.wireOp",EDGE,"E2037"),sQuery(id+"F1.wireOp",EDGE,"E2038"),sQuery(id+"F1.wireOp",EDGE,"E2039"),sQuery(id+"F1.wireOp",EDGE,"E2040"),sQuery(id+"F1.wireOp",EDGE,"E2041"),sQuery(id+"F1.wireOp",EDGE,"E2042"),sQuery(id+"F1.wireOp",EDGE,"E2043"),sQuery(id+"F1.wireOp",EDGE,"E2044"),sQuery(id+"F1.wireOp",EDGE,"E2045"),sQuery(id+"F1.wireOp",EDGE,"E2046"),sQuery(id+"F1.wireOp",EDGE,"E2047"),sQuery(id+"F1.wireOp",EDGE,"E2048"),sQuery(id+"F1.wireOp",EDGE,"E2049"),sQuery(id+"F1.wireOp",EDGE,"E2050"),sQuery(id+"F1.wireOp",EDGE,"E2051"),sQuery(id+"F1.wireOp",EDGE,"E2052"),sQuery(id+"F1.wireOp",EDGE,"E2053"),sQuery(id+"F1.wireOp",EDGE,"E2054"),sQuery(id+"F1.wireOp",EDGE,"E2055"),sQuery(id+"F1.wireOp",EDGE,"E2056"),sQuery(id+"F1.wireOp",EDGE,"E2057"),sQuery(id+"F1.wireOp",EDGE,"E2058"),sQuery(id+"F1.wireOp",EDGE,"E2059"),sQuery(id+"F1.wireOp",EDGE,"E2060"),sQuery(id+"F1.wireOp",EDGE,"E2061"),sQuery(id+"F1.wireOp",EDGE,"E2062"),sQuery(id+"F1.wireOp",EDGE,"E2063"),sQuery(id+"F1.wireOp",EDGE,"E2064"),sQuery(id+"F1.wireOp",EDGE,"E2065"),sQuery(id+"F1.wireOp",EDGE,"E2066"),sQuery(id+"F1.wireOp",EDGE,"E2067"),sQuery(id+"F1.wireOp",EDGE,"E2068"),sQuery(id+"F1.wireOp",EDGE,"E2069"),sQuery(id+"F1.wireOp",EDGE,"E2070"),sQuery(id+"F1.wireOp",EDGE,"E2071"),sQuery(id+"F1.wireOp",EDGE,"E2072"),sQuery(id+"F1.wireOp",EDGE,"E2073"),sQuery(id+"F1.wireOp",EDGE,"E2074"),sQuery(id+"F1.wireOp",EDGE,"E2075"),sQuery(id+"F1.wireOp",EDGE,"E2076"),sQuery(id+"F1.wireOp",EDGE,"E2077"),sQuery(id+"F1.wireOp",EDGE,"E2078"),sQuery(id+"F1.wireOp",EDGE,"E2079"),sQuery(id+"F1.wireOp",EDGE,"E2080"),sQuery(id+"F1.wireOp",EDGE,"E2081"),sQuery(id+"F1.wireOp",EDGE,"E2082"),sQuery(id+"F1.wireOp",EDGE,"E2083"),sQuery(id+"F1.wireOp",EDGE,"E2084"),sQuery(id+"F1.wireOp",EDGE,"E2085"),sQuery(id+"F1.wireOp",EDGE,"E2086"),sQuery(id+"F1.wireOp",EDGE,"E2087"),sQuery(id+"F1.wireOp",EDGE,"E2088"),sQuery(id+"F1.wireOp",EDGE,"E2089"),sQuery(id+"F1.wireOp",EDGE,"E2090"),sQuery(id+"F1.wireOp",EDGE,"E2091"),sQuery(id+"F1.wireOp",EDGE,"E2092"),sQuery(id+"F1.wireOp",EDGE,"E2093"),sQuery(id+"F1.wireOp",EDGE,"E2094"),sQuery(id+"F1.wireOp",EDGE,"E2095"),sQuery(id+"F1.wireOp",EDGE,"E2096"),sQuery(id+"F1.wireOp",EDGE,"E2097"),sQuery(id+"F1.wireOp",EDGE,"E2098"),sQuery(id+"F1.wireOp",EDGE,"E2099"),sQuery(id+"F1.wireOp",EDGE,"E2100"),sQuery(id+"F1.wireOp",EDGE,"E2101"),sQuery(id+"F1.wireOp",EDGE,"E2102"),sQuery(id+"F1.wireOp",EDGE,"E2103"),sQuery(id+"F1.wireOp",EDGE,"E2104"),sQuery(id+"F1.wireOp",EDGE,"E2105"),sQuery(id+"F1.wireOp",EDGE,"E2106"),sQuery(id+"F1.wireOp",EDGE,"E2107"),sQuery(id+"F1.wireOp",EDGE,"E2108"),sQuery(id+"F1.wireOp",EDGE,"E2109"),sQuery(id+"F1.wireOp",EDGE,"E2110"),sQuery(id+"F1.wireOp",EDGE,"E2111"),sQuery(id+"F1.wireOp",EDGE,"E2112"),sQuery(id+"F1.wireOp",EDGE,"E2113"),sQuery(id+"F1.wireOp",EDGE,"E2114"),sQuery(id+"F1.wireOp",EDGE,"E2115"),sQuery(id+"F1.wireOp",EDGE,"E2116"),sQuery(id+"F1.wireOp",EDGE,"E2117"),sQuery(id+"F1.wireOp",EDGE,"E2118"),sQuery(id+"F1.wireOp",EDGE,"E2119"),sQuery(id+"F1.wireOp",EDGE,"E2120"),sQuery(id+"F1.wireOp",EDGE,"E2121"),sQuery(id+"F1.wireOp",EDGE,"E2122"),sQuery(id+"F1.wireOp",EDGE,"E2123"),sQuery(id+"F1.wireOp",EDGE,"E2124"),sQuery(id+"F1.wireOp",EDGE,"E2125"),sQuery(id+"F1.wireOp",EDGE,"E2126"),sQuery(id+"F1.wireOp",EDGE,"E2127"),sQuery(id+"F1.wireOp",EDGE,"E2128"),sQuery(id+"F1.wireOp",EDGE,"E2129"),sQuery(id+"F1.wireOp",EDGE,"E2130"),sQuery(id+"F1.wireOp",EDGE,"E2131"),sQuery(id+"F1.wireOp",EDGE,"E2132"),sQuery(id+"F1.wireOp",EDGE,"E2133"),sQuery(id+"F1.wireOp",EDGE,"E2134"),sQuery(id+"F1.wireOp",EDGE,"E2135"),sQuery(id+"F1.wireOp",EDGE,"E2136"),sQuery(id+"F1.wireOp",EDGE,"E2137"),sQuery(id+"F1.wireOp",EDGE,"E2138"),sQuery(id+"F1.wireOp",EDGE,"E2139"),sQuery(id+"F1.wireOp",EDGE,"E2140"),sQuery(id+"F1.wireOp",EDGE,"E2141"),sQuery(id+"F1.wireOp",EDGE,"E2142"),sQuery(id+"F1.wireOp",EDGE,"E2143"),sQuery(id+"F1.wireOp",EDGE,"E2144"),sQuery(id+"F1.wireOp",EDGE,"E2145"),sQuery(id+"F1.wireOp",EDGE,"E2146"),sQuery(id+"F1.wireOp",EDGE,"E2147"),sQuery(id+"F1.wireOp",EDGE,"E2148"),sQuery(id+"F1.wireOp",EDGE,"E2149"),sQuery(id+"F1.wireOp",EDGE,"E2150"),sQuery(id+"F1.wireOp",EDGE,"E2151"),sQuery(id+"F1.wireOp",EDGE,"E2152"),sQuery(id+"F1.wireOp",EDGE,"E2153"),sQuery(id+"F1.wireOp",EDGE,"E2154"),sQuery(id+"F1.wireOp",EDGE,"E2155"),sQuery(id+"F1.wireOp",EDGE,"E2156"),sQuery(id+"F1.wireOp",EDGE,"E2157"),sQuery(id+"F1.wireOp",EDGE,"E2158"),sQuery(id+"F1.wireOp",EDGE,"E2159"),sQuery(id+"F1.wireOp",EDGE,"E2160"),sQuery(id+"F1.wireOp",EDGE,"E2161"),sQuery(id+"F1.wireOp",EDGE,"E2162"),sQuery(id+"F1.wireOp",EDGE,"E2163"),sQuery(id+"F1.wireOp",EDGE,"E2164"),sQuery(id+"F1.wireOp",EDGE,"E2165"),sQuery(id+"F1.wireOp",EDGE,"E2166"),sQuery(id+"F1.wireOp",EDGE,"E2167"),sQuery(id+"F1.wireOp",EDGE,"E2168"),sQuery(id+"F1.wireOp",EDGE,"E2169"),sQuery(id+"F1.wireOp",EDGE,"E2170"),sQuery(id+"F1.wireOp",EDGE,"E2171"),sQuery(id+"F1.wireOp",EDGE,"E2172"),sQuery(id+"F1.wireOp",EDGE,"E2173"),sQuery(id+"F1.wireOp",EDGE,"E2174"),sQuery(id+"F1.wireOp",EDGE,"E2175"),sQuery(id+"F1.wireOp",EDGE,"E2176"),sQuery(id+"F1.wireOp",EDGE,"E2177"),sQuery(id+"F1.wireOp",EDGE,"E2178"),sQuery(id+"F1.wireOp",EDGE,"E2179"),sQuery(id+"F1.wireOp",EDGE,"E2180"),sQuery(id+"F1.wireOp",EDGE,"E2181"),sQuery(id+"F1.wireOp",EDGE,"E2182"),sQuery(id+"F1.wireOp",EDGE,"E2183"),sQuery(id+"F1.wireOp",EDGE,"E2184"),sQuery(id+"F1.wireOp",EDGE,"E2185"),sQuery(id+"F1.wireOp",EDGE,"E2186"),sQuery(id+"F1.wireOp",EDGE,"E2187"),sQuery(id+"F1.wireOp",EDGE,"E2188"),sQuery(id+"F1.wireOp",EDGE,"E2189"),sQuery(id+"F1.wireOp",EDGE,"E2190"),sQuery(id+"F1.wireOp",EDGE,"E2191"),sQuery(id+"F1.wireOp",EDGE,"E2192"),sQuery(id+"F1.wireOp",EDGE,"E2193"),sQuery(id+"F1.wireOp",EDGE,"E2194"),sQuery(id+"F1.wireOp",EDGE,"E2195"),sQuery(id+"F1.wireOp",EDGE,"E2196"),sQuery(id+"F1.wireOp",EDGE,"E2197"),sQuery(id+"F1.wireOp",EDGE,"E2198"),sQuery(id+"F1.wireOp",EDGE,"E2199"),sQuery(id+"F1.wireOp",EDGE,"E2200"),sQuery(id+"F1.wireOp",EDGE,"E2201"),sQuery(id+"F1.wireOp",EDGE,"E2202"),sQuery(id+"F1.wireOp",EDGE,"E2203"),sQuery(id+"F1.wireOp",EDGE,"E2204"),sQuery(id+"F1.wireOp",EDGE,"E2205"),sQuery(id+"F1.wireOp",EDGE,"E2206"),sQuery(id+"F1.wireOp",EDGE,"E2207"),sQuery(id+"F1.wireOp",EDGE,"E2208"),sQuery(id+"F1.wireOp",EDGE,"E2209"),sQuery(id+"F1.wireOp",EDGE,"E2210"),sQuery(id+"F1.wireOp",EDGE,"E2211"),sQuery(id+"F1.wireOp",EDGE,"E2212"),sQuery(id+"F1.wireOp",EDGE,"E2213"),sQuery(id+"F1.wireOp",EDGE,"E2214"),sQuery(id+"F1.wireOp",EDGE,"E2215"),sQuery(id+"F1.wireOp",EDGE,"E2216"),sQuery(id+"F1.wireOp",EDGE,"E2217"),sQuery(id+"F1.wireOp",EDGE,"E2218"),sQuery(id+"F1.wireOp",EDGE,"E2219"),sQuery(id+"F1.wireOp",EDGE,"E2220"),sQuery(id+"F1.wireOp",EDGE,"E2221"),sQuery(id+"F1.wireOp",EDGE,"E2222"),sQuery(id+"F1.wireOp",EDGE,"E2223"),sQuery(id+"F1.wireOp",EDGE,"E2224"),sQuery(id+"F1.wireOp",EDGE,"E2225"),sQuery(id+"F1.wireOp",EDGE,"E2226"),sQuery(id+"F1.wireOp",EDGE,"E2227"),sQuery(id+"F1.wireOp",EDGE,"E2228"),sQuery(id+"F1.wireOp",EDGE,"E2229"),sQuery(id+"F1.wireOp",EDGE,"E2230"),sQuery(id+"F1.wireOp",EDGE,"E2231"),sQuery(id+"F1.wireOp",EDGE,"E2232"),sQuery(id+"F1.wireOp",EDGE,"E2233"),sQuery(id+"F1.wireOp",EDGE,"E2234"),sQuery(id+"F1.wireOp",EDGE,"E2235"),sQuery(id+"F1.wireOp",EDGE,"E2236"),sQuery(id+"F1.wireOp",EDGE,"E2237"),sQuery(id+"F1.wireOp",EDGE,"E2238"),sQuery(id+"F1.wireOp",EDGE,"E2239"),sQuery(id+"F1.wireOp",EDGE,"E2240"),sQuery(id+"F1.wireOp",EDGE,"E2241"),sQuery(id+"F1.wireOp",EDGE,"E2242"),sQuery(id+"F1.wireOp",EDGE,"E2243"),sQuery(id+"F1.wireOp",EDGE,"E2244"),sQuery(id+"F1.wireOp",EDGE,"E2245"),sQuery(id+"F1.wireOp",EDGE,"E2246"),sQuery(id+"F1.wireOp",EDGE,"E2247"),sQuery(id+"F1.wireOp",EDGE,"E2248"),sQuery(id+"F1.wireOp",EDGE,"E2249"),sQuery(id+"F1.wireOp",EDGE,"E2250"),sQuery(id+"F1.wireOp",EDGE,"E2251"),sQuery(id+"F1.wireOp",EDGE,"E2252"),sQuery(id+"F1.wireOp",EDGE,"E2253"),sQuery(id+"F1.wireOp",EDGE,"E2254"),sQuery(id+"F1.wireOp",EDGE,"E2255"),sQuery(id+"F1.wireOp",EDGE,"E2256"),sQuery(id+"F1.wireOp",EDGE,"E2257"),sQuery(id+"F1.wireOp",EDGE,"E2258"),sQuery(id+"F1.wireOp",EDGE,"E2259"),sQuery(id+"F1.wireOp",EDGE,"E2260"),sQuery(id+"F1.wireOp",EDGE,"E2261"),sQuery(id+"F1.wireOp",EDGE,"E2262"),sQuery(id+"F1.wireOp",EDGE,"E2263"),sQuery(id+"F1.wireOp",EDGE,"E2264"),sQuery(id+"F1.wireOp",EDGE,"E2265"),sQuery(id+"F1.wireOp",EDGE,"E2266"),sQuery(id+"F1.wireOp",EDGE,"E2267"),sQuery(id+"F1.wireOp",EDGE,"E2268"),sQuery(id+"F1.wireOp",EDGE,"E2269"),sQuery(id+"F1.wireOp",EDGE,"E2270"),sQuery(id+"F1.wireOp",EDGE,"E2271"),sQuery(id+"F1.wireOp",EDGE,"E2272"),sQuery(id+"F1.wireOp",EDGE,"E2273"),sQuery(id+"F1.wireOp",EDGE,"E2274"),sQuery(id+"F1.wireOp",EDGE,"E2275"),sQuery(id+"F1.wireOp",EDGE,"E2276"),sQuery(id+"F1.wireOp",EDGE,"E2277"),sQuery(id+"F1.wireOp",EDGE,"E2278"),sQuery(id+"F1.wireOp",EDGE,"E2279"),sQuery(id+"F1.wireOp",EDGE,"E2280"),sQuery(id+"F1.wireOp",EDGE,"E2281"),sQuery(id+"F1.wireOp",EDGE,"E2282"),sQuery(id+"F1.wireOp",EDGE,"E2283"),sQuery(id+"F1.wireOp",EDGE,"E2284"),sQuery(id+"F1.wireOp",EDGE,"E2285"),sQuery(id+"F1.wireOp",EDGE,"E2286"),sQuery(id+"F1.wireOp",EDGE,"E2287"),sQuery(id+"F1.wireOp",EDGE,"E2288"),sQuery(id+"F1.wireOp",EDGE,"E2289"),sQuery(id+"F1.wireOp",EDGE,"E2290"),sQuery(id+"F1.wireOp",EDGE,"E2291"),sQuery(id+"F1.wireOp",EDGE,"E2292"),sQuery(id+"F1.wireOp",EDGE,"E2293"),sQuery(id+"F1.wireOp",EDGE,"E2294"),sQuery(id+"F1.wireOp",EDGE,"E2295"),sQuery(id+"F1.wireOp",EDGE,"E2296"),sQuery(id+"F1.wireOp",EDGE,"E2297"),sQuery(id+"F1.wireOp",EDGE,"E2298"),sQuery(id+"F1.wireOp",EDGE,"E2299"),sQuery(id+"F1.wireOp",EDGE,"E2300"),sQuery(id+"F1.wireOp",EDGE,"E2301"),sQuery(id+"F1.wireOp",EDGE,"E2302"),sQuery(id+"F1.wireOp",EDGE,"E2303"),sQuery(id+"F1.wireOp",EDGE,"E2304"),sQuery(id+"F1.wireOp",EDGE,"E2305"),sQuery(id+"F1.wireOp",EDGE,"E2306"),sQuery(id+"F1.wireOp",EDGE,"E2307"),sQuery(id+"F1.wireOp",EDGE,"E2308"),sQuery(id+"F1.wireOp",EDGE,"E2309"),sQuery(id+"F1.wireOp",EDGE,"E2310"),sQuery(id+"F1.wireOp",EDGE,"E2311"),sQuery(id+"F1.wireOp",EDGE,"E2312"),sQuery(id+"F1.wireOp",EDGE,"E2313"),sQuery(id+"F1.wireOp",EDGE,"E2314"),sQuery(id+"F1.wireOp",EDGE,"E2315"),sQuery(id+"F1.wireOp",EDGE,"E2316"),sQuery(id+"F1.wireOp",EDGE,"E2317"),sQuery(id+"F1.wireOp",EDGE,"E2318"),sQuery(id+"F1.wireOp",EDGE,"E2319"),sQuery(id+"F1.wireOp",EDGE,"E2320"),sQuery(id+"F1.wireOp",EDGE,"E2321"),sQuery(id+"F1.wireOp",EDGE,"E2322"),sQuery(id+"F1.wireOp",EDGE,"E2323"),sQuery(id+"F1.wireOp",EDGE,"E2324"),sQuery(id+"F1.wireOp",EDGE,"E2325"),sQuery(id+"F1.wireOp",EDGE,"E2326"),sQuery(id+"F1.wireOp",EDGE,"E2327"),sQuery(id+"F1.wireOp",EDGE,"E2328"),sQuery(id+"F1.wireOp",EDGE,"E2329"),sQuery(id+"F1.wireOp",EDGE,"E2330"),sQuery(id+"F1.wireOp",EDGE,"E2331"),sQuery(id+"F1.wireOp",EDGE,"E2332"),sQuery(id+"F1.wireOp",EDGE,"E2333"),sQuery(id+"F1.wireOp",EDGE,"E2334"),sQuery(id+"F1.wireOp",EDGE,"E2335"),sQuery(id+"F1.wireOp",EDGE,"E2336"),sQuery(id+"F1.wireOp",EDGE,"E2337"),sQuery(id+"F1.wireOp",EDGE,"E2338"),sQuery(id+"F1.wireOp",EDGE,"E2339"),sQuery(id+"F1.wireOp",EDGE,"E2340"),sQuery(id+"F1.wireOp",EDGE,"E2341"),sQuery(id+"F1.wireOp",EDGE,"E2342"),sQuery(id+"F1.wireOp",EDGE,"E2343"),sQuery(id+"F1.wireOp",EDGE,"E2344"),sQuery(id+"F1.wireOp",EDGE,"E2345"),sQuery(id+"F1.wireOp",EDGE,"E2346"),sQuery(id+"F1.wireOp",EDGE,"E2347"),sQuery(id+"F1.wireOp",EDGE,"E2348"),sQuery(id+"F1.wireOp",EDGE,"E2349"),sQuery(id+"F1.wireOp",EDGE,"E2350"),sQuery(id+"F1.wireOp",EDGE,"E2351"),sQuery(id+"F1.wireOp",EDGE,"E2352"),sQuery(id+"F1.wireOp",EDGE,"E2353"),sQuery(id+"F1.wireOp",EDGE,"E2354"),sQuery(id+"F1.wireOp",EDGE,"E2355"),sQuery(id+"F1.wireOp",EDGE,"E2356"),sQuery(id+"F1.wireOp",EDGE,"E2357"),sQuery(id+"F1.wireOp",EDGE,"E2358"),sQuery(id+"F1.wireOp",EDGE,"E2359"),sQuery(id+"F1.wireOp",EDGE,"E2360"),sQuery(id+"F1.wireOp",EDGE,"E2361"),sQuery(id+"F1.wireOp",EDGE,"E2362"),sQuery(id+"F1.wireOp",EDGE,"E2363"),sQuery(id+"F1.wireOp",EDGE,"E2364"),sQuery(id+"F1.wireOp",EDGE,"E2365"),sQuery(id+"F1.wireOp",EDGE,"E2366"),sQuery(id+"F1.wireOp",EDGE,"E2367"),sQuery(id+"F1.wireOp",EDGE,"E2368"),sQuery(id+"F1.wireOp",EDGE,"E2369"),sQuery(id+"F1.wireOp",EDGE,"E2370"),sQuery(id+"F1.wireOp",EDGE,"E2371"),sQuery(id+"F1.wireOp",EDGE,"E2372"),sQuery(id+"F1.wireOp",EDGE,"E2373"),sQuery(id+"F1.wireOp",EDGE,"E2374"),sQuery(id+"F1.wireOp",EDGE,"E2375"),sQuery(id+"F1.wireOp",EDGE,"E2376"),sQuery(id+"F1.wireOp",EDGE,"E2377"),sQuery(id+"F1.wireOp",EDGE,"E2378"),sQuery(id+"F1.wireOp",EDGE,"E2379"),sQuery(id+"F1.wireOp",EDGE,"E2380"),sQuery(id+"F1.wireOp",EDGE,"E2381"),sQuery(id+"F1.wireOp",EDGE,"E2382"),sQuery(id+"F1.wireOp",EDGE,"E2383"),sQuery(id+"F1.wireOp",EDGE,"E2384"),sQuery(id+"F1.wireOp",EDGE,"E2385"),sQuery(id+"F1.wireOp",EDGE,"E2386"),sQuery(id+"F1.wireOp",EDGE,"E2387"),sQuery(id+"F1.wireOp",EDGE,"E2388"),sQuery(id+"F1.wireOp",EDGE,"E2389"),sQuery(id+"F1.wireOp",EDGE,"E2390"),sQuery(id+"F1.wireOp",EDGE,"E2391"),sQuery(id+"F1.wireOp",EDGE,"E2392"),sQuery(id+"F1.wireOp",EDGE,"E2393"),sQuery(id+"F1.wireOp",EDGE,"E2394"),sQuery(id+"F1.wireOp",EDGE,"E2395"),sQuery(id+"F1.wireOp",EDGE,"E2396"),sQuery(id+"F1.wireOp",EDGE,"E2397"),sQuery(id+"F1.wireOp",EDGE,"E2398"),sQuery(id+"F1.wireOp",EDGE,"E2399"),sQuery(id+"F1.wireOp",EDGE,"E2400"),sQuery(id+"F1.wireOp",EDGE,"E2401"),sQuery(id+"F1.wireOp",EDGE,"E2402"),sQuery(id+"F1.wireOp",EDGE,"E2403"),sQuery(id+"F1.wireOp",EDGE,"E2404"),sQuery(id+"F1.wireOp",EDGE,"E2405"),sQuery(id+"F1.wireOp",EDGE,"E2406"),sQuery(id+"F1.wireOp",EDGE,"E2407"),sQuery(id+"F1.wireOp",EDGE,"E2408"),sQuery(id+"F1.wireOp",EDGE,"E2409"),sQuery(id+"F1.wireOp",EDGE,"E2410"),sQuery(id+"F1.wireOp",EDGE,"E2411"),sQuery(id+"F1.wireOp",EDGE,"E2412"),sQuery(id+"F1.wireOp",EDGE,"E2413"),sQuery(id+"F1.wireOp",EDGE,"E2414"),sQuery(id+"F1.wireOp",EDGE,"E2415"),sQuery(id+"F1.wireOp",EDGE,"E2416"),sQuery(id+"F1.wireOp",EDGE,"E2417"),sQuery(id+"F1.wireOp",EDGE,"E2418"),sQuery(id+"F1.wireOp",EDGE,"E2419"),sQuery(id+"F1.wireOp",EDGE,"E2420"),sQuery(id+"F1.wireOp",EDGE,"E2421"),sQuery(id+"F1.wireOp",EDGE,"E2422"),sQuery(id+"F1.wireOp",EDGE,"E2423"),sQuery(id+"F1.wireOp",EDGE,"E2424"),sQuery(id+"F1.wireOp",EDGE,"E2425"),sQuery(id+"F1.wireOp",EDGE,"E2426"),sQuery(id+"F1.wireOp",EDGE,"E2427"),sQuery(id+"F1.wireOp",EDGE,"E2428"),sQuery(id+"F1.wireOp",EDGE,"E2429"),sQuery(id+"F1.wireOp",EDGE,"E2430"),sQuery(id+"F1.wireOp",EDGE,"E2431"),sQuery(id+"F1.wireOp",EDGE,"E2432"),sQuery(id+"F1.wireOp",EDGE,"E2433"),sQuery(id+"F1.wireOp",EDGE,"E2434"),sQuery(id+"F1.wireOp",EDGE,"E2435"),sQuery(id+"F1.wireOp",EDGE,"E2436"),sQuery(id+"F1.wireOp",EDGE,"E2437"),sQuery(id+"F1.wireOp",EDGE,"E2438"),sQuery(id+"F1.wireOp",EDGE,"E2439"),sQuery(id+"F1.wireOp",EDGE,"E2440"),sQuery(id+"F1.wireOp",EDGE,"E2441"),sQuery(id+"F1.wireOp",EDGE,"E2442"),sQuery(id+"F1.wireOp",EDGE,"E2443"),sQuery(id+"F1.wireOp",EDGE,"E2444"),sQuery(id+"F1.wireOp",EDGE,"E2445"),sQuery(id+"F1.wireOp",EDGE,"E2446"),sQuery(id+"F1.wireOp",EDGE,"E2447"),sQuery(id+"F1.wireOp",EDGE,"E2448"),sQuery(id+"F1.wireOp",EDGE,"E2449"),sQuery(id+"F1.wireOp",EDGE,"E2450"),sQuery(id+"F1.wireOp",EDGE,"E2451"),sQuery(id+"F1.wireOp",EDGE,"E2452"),sQuery(id+"F1.wireOp",EDGE,"E2453"),sQuery(id+"F1.wireOp",EDGE,"E2454"),sQuery(id+"F1.wireOp",EDGE,"E2455"),sQuery(id+"F1.wireOp",EDGE,"E2456"),sQuery(id+"F1.wireOp",EDGE,"E2457"),sQuery(id+"F1.wireOp",EDGE,"E2458"),sQuery(id+"F1.wireOp",EDGE,"E2459"),sQuery(id+"F1.wireOp",EDGE,"E2460"),sQuery(id+"F1.wireOp",EDGE,"E2461"),sQuery(id+"F1.wireOp",EDGE,"E2462"),sQuery(id+"F1.wireOp",EDGE,"E2463"),sQuery(id+"F1.wireOp",EDGE,"E2464"),sQuery(id+"F1.wireOp",EDGE,"E2465"),sQuery(id+"F1.wireOp",EDGE,"E2466"),sQuery(id+"F1.wireOp",EDGE,"E2467"),sQuery(id+"F1.wireOp",EDGE,"E2468"),sQuery(id+"F1.wireOp",EDGE,"E2469"),sQuery(id+"F1.wireOp",EDGE,"E2470"),sQuery(id+"F1.wireOp",EDGE,"E2471"),sQuery(id+"F1.wireOp",EDGE,"E2472"),sQuery(id+"F1.wireOp",EDGE,"E2473"),sQuery(id+"F1.wireOp",EDGE,"E2474"),sQuery(id+"F1.wireOp",EDGE,"E2475"),sQuery(id+"F1.wireOp",EDGE,"E2476"),sQuery(id+"F1.wireOp",EDGE,"E2477"),sQuery(id+"F1.wireOp",EDGE,"E2478"),sQuery(id+"F1.wireOp",EDGE,"E2479"),sQuery(id+"F1.wireOp",EDGE,"E2480"),sQuery(id+"F1.wireOp",EDGE,"E2481"),sQuery(id+"F1.wireOp",EDGE,"E2482"),sQuery(id+"F1.wireOp",EDGE,"E2483"),sQuery(id+"F1.wireOp",EDGE,"E2484"),sQuery(id+"F1.wireOp",EDGE,"E2485"),sQuery(id+"F1.wireOp",EDGE,"E2486"),sQuery(id+"F1.wireOp",EDGE,"E2487"),sQuery(id+"F1.wireOp",EDGE,"E2488"),sQuery(id+"F1.wireOp",EDGE,"E2489"),sQuery(id+"F1.wireOp",EDGE,"E2490"),sQuery(id+"F1.wireOp",EDGE,"E2491"),sQuery(id+"F1.wireOp",EDGE,"E2492"),sQuery(id+"F1.wireOp",EDGE,"E2493"),sQuery(id+"F1.wireOp",EDGE,"E2494"),sQuery(id+"F1.wireOp",EDGE,"E2495"),sQuery(id+"F1.wireOp",EDGE,"E2496"),sQuery(id+"F1.wireOp",EDGE,"E2497"),sQuery(id+"F1.wireOp",EDGE,"E2498"),sQuery(id+"F1.wireOp",EDGE,"E2499"),sQuery(id+"F1.wireOp",EDGE,"E2500"),sQuery(id+"F1.wireOp",EDGE,"E2501"),sQuery(id+"F1.wireOp",EDGE,"E2502"),sQuery(id+"F1.wireOp",EDGE,"E2503"),sQuery(id+"F1.wireOp",EDGE,"E2504"),sQuery(id+"F1.wireOp",EDGE,"E2505"),sQuery(id+"F1.wireOp",EDGE,"E2506"),sQuery(id+"F1.wireOp",EDGE,"E2507"),sQuery(id+"F1.wireOp",EDGE,"E2508"),sQuery(id+"F1.wireOp",EDGE,"E2509"),sQuery(id+"F1.wireOp",EDGE,"E2510"),sQuery(id+"F1.wireOp",EDGE,"E2511"),sQuery(id+"F1.wireOp",EDGE,"E2512"),sQuery(id+"F1.wireOp",EDGE,"E2513"),sQuery(id+"F1.wireOp",EDGE,"E2514"),sQuery(id+"F1.wireOp",EDGE,"E2515"),sQuery(id+"F1.wireOp",EDGE,"E2516"),sQuery(id+"F1.wireOp",EDGE,"E2517"),sQuery(id+"F1.wireOp",EDGE,"E2518"),sQuery(id+"F1.wireOp",EDGE,"E2519"),sQuery(id+"F1.wireOp",EDGE,"E2520"),sQuery(id+"F1.wireOp",EDGE,"E2521"),sQuery(id+"F1.wireOp",EDGE,"E2522"),sQuery(id+"F1.wireOp",EDGE,"E2523"),sQuery(id+"F1.wireOp",EDGE,"E2524"),sQuery(id+"F1.wireOp",EDGE,"E2525"),sQuery(id+"F1.wireOp",EDGE,"E2526"),sQuery(id+"F1.wireOp",EDGE,"E2527"),sQuery(id+"F1.wireOp",EDGE,"E2528"),sQuery(id+"F1.wireOp",EDGE,"E2529"),sQuery(id+"F1.wireOp",EDGE,"E2530"),sQuery(id+"F1.wireOp",EDGE,"E2531"),sQuery(id+"F1.wireOp",EDGE,"E2532"),sQuery(id+"F1.wireOp",EDGE,"E2533"),sQuery(id+"F1.wireOp",EDGE,"E2534"),sQuery(id+"F1.wireOp",EDGE,"E2535"),sQuery(id+"F1.wireOp",EDGE,"E2536"),sQuery(id+"F1.wireOp",EDGE,"E2537"),sQuery(id+"F1.wireOp",EDGE,"E2538"),sQuery(id+"F1.wireOp",EDGE,"E2539"),sQuery(id+"F1.wireOp",EDGE,"E2540"),sQuery(id+"F1.wireOp",EDGE,"E2541"),sQuery(id+"F1.wireOp",EDGE,"E2542"),sQuery(id+"F1.wireOp",EDGE,"E2543"),sQuery(id+"F1.wireOp",EDGE,"E2544"),sQuery(id+"F1.wireOp",EDGE,"E2545"),sQuery(id+"F1.wireOp",EDGE,"E2546"),sQuery(id+"F1.wireOp",EDGE,"E2547"),sQuery(id+"F1.wireOp",EDGE,"E2548"),sQuery(id+"F1.wireOp",EDGE,"E2549"),sQuery(id+"F1.wireOp",EDGE,"E2550"),sQuery(id+"F1.wireOp",EDGE,"E2551"),sQuery(id+"F1.wireOp",EDGE,"E2552"),sQuery(id+"F1.wireOp",EDGE,"E2553"),sQuery(id+"F1.wireOp",EDGE,"E2554"),sQuery(id+"F1.wireOp",EDGE,"E2555"),sQuery(id+"F1.wireOp",EDGE,"E2556"),sQuery(id+"F1.wireOp",EDGE,"E2557"),sQuery(id+"F1.wireOp",EDGE,"E2558"),sQuery(id+"F1.wireOp",EDGE,"E2559"),sQuery(id+"F1.wireOp",EDGE,"E2560"),sQuery(id+"F1.wireOp",EDGE,"E2561"),sQuery(id+"F1.wireOp",EDGE,"E2562"),sQuery(id+"F1.wireOp",EDGE,"E2563"),sQuery(id+"F1.wireOp",EDGE,"E2564"),sQuery(id+"F1.wireOp",EDGE,"E2565"),sQuery(id+"F1.wireOp",EDGE,"E2566"),sQuery(id+"F1.wireOp",EDGE,"E2567"),sQuery(id+"F1.wireOp",EDGE,"E2568"),sQuery(id+"F1.wireOp",EDGE,"E2569"),sQuery(id+"F1.wireOp",EDGE,"E2570"),sQuery(id+"F1.wireOp",EDGE,"E2571"),sQuery(id+"F1.wireOp",EDGE,"E2572"),sQuery(id+"F1.wireOp",EDGE,"E2573"),sQuery(id+"F1.wireOp",EDGE,"E2574"),sQuery(id+"F1.wireOp",EDGE,"E2575"),sQuery(id+"F1.wireOp",EDGE,"E2576"),sQuery(id+"F1.wireOp",EDGE,"E2577"),sQuery(id+"F1.wireOp",EDGE,"E2578"),sQuery(id+"F1.wireOp",EDGE,"E2579"),sQuery(id+"F1.wireOp",EDGE,"E2580"),sQuery(id+"F1.wireOp",EDGE,"E2581"),sQuery(id+"F1.wireOp",EDGE,"E2582"),sQuery(id+"F1.wireOp",EDGE,"E2583"),sQuery(id+"F1.wireOp",EDGE,"E2584"),sQuery(id+"F1.wireOp",EDGE,"E2585"),sQuery(id+"F1.wireOp",EDGE,"E2586"),sQuery(id+"F1.wireOp",EDGE,"E2587"),sQuery(id+"F1.wireOp",EDGE,"E2588"),sQuery(id+"F1.wireOp",EDGE,"E2589"),sQuery(id+"F1.wireOp",EDGE,"E2590"),sQuery(id+"F1.wireOp",EDGE,"E2591"),sQuery(id+"F1.wireOp",EDGE,"E2592"),sQuery(id+"F1.wireOp",EDGE,"E2593"),sQuery(id+"F1.wireOp",EDGE,"E2594"),sQuery(id+"F1.wireOp",EDGE,"E2595"),sQuery(id+"F1.wireOp",EDGE,"E2596"),sQuery(id+"F1.wireOp",EDGE,"E2597"),sQuery(id+"F1.wireOp",EDGE,"E2598"),sQuery(id+"F1.wireOp",EDGE,"E2599"),sQuery(id+"F1.wireOp",EDGE,"E2600"),sQuery(id+"F1.wireOp",EDGE,"E2601"),sQuery(id+"F1.wireOp",EDGE,"E2602"),sQuery(id+"F1.wireOp",EDGE,"E2603"),sQuery(id+"F1.wireOp",EDGE,"E2604"),sQuery(id+"F1.wireOp",EDGE,"E2605"),sQuery(id+"F1.wireOp",EDGE,"E2606"),sQuery(id+"F1.wireOp",EDGE,"E2607"),sQuery(id+"F1.wireOp",EDGE,"E2608"),sQuery(id+"F1.wireOp",EDGE,"E2609"),sQuery(id+"F1.wireOp",EDGE,"E2610"),sQuery(id+"F1.wireOp",EDGE,"E2611"),sQuery(id+"F1.wireOp",EDGE,"E2612"),sQuery(id+"F1.wireOp",EDGE,"E2613"),sQuery(id+"F1.wireOp",EDGE,"E2614"),sQuery(id+"F1.wireOp",EDGE,"E2615"),sQuery(id+"F1.wireOp",EDGE,"E2616"),sQuery(id+"F1.wireOp",EDGE,"E2617"),sQuery(id+"F1.wireOp",EDGE,"E2618"),sQuery(id+"F1.wireOp",EDGE,"E2619"),sQuery(id+"F1.wireOp",EDGE,"E2620"),sQuery(id+"F1.wireOp",EDGE,"E2622")])]});
            var Q1;
            Q1=sQuery(id+"F5.wireOp",EDGE,"E2623");
            transform(context, id + "F6", {"entities" : qUnion([Q0]), "transformType" : TransformType.ROTATION, "transformAxis" : qUnion([Q1]), "angle" : 30 * degree, "makeCopy" : true});
        }
        {
            var Q0;
            Q0=makeQuery(id+"F6.opPattern","COPY",BODY,{"derivedFrom":makeQuery(id+"F2.opExtrude","SWEPT_BODY",BODY,{"disambiguationData":[OSD([sQuery(id+"F1.wireOp",EDGE,"E15"),sQuery(id+"F1.wireOp",EDGE,"E16"),sQuery(id+"F1.wireOp",EDGE,"E17"),sQuery(id+"F1.wireOp",EDGE,"E18"),sQuery(id+"F1.wireOp",EDGE,"E19"),sQuery(id+"F1.wireOp",EDGE,"E20"),sQuery(id+"F1.wireOp",EDGE,"E21"),sQuery(id+"F1.wireOp",EDGE,"E22"),sQuery(id+"F1.wireOp",EDGE,"E23"),sQuery(id+"F1.wireOp",EDGE,"E24"),sQuery(id+"F1.wireOp",EDGE,"E25"),sQuery(id+"F1.wireOp",EDGE,"E26"),sQuery(id+"F1.wireOp",EDGE,"E27"),sQuery(id+"F1.wireOp",EDGE,"E28"),sQuery(id+"F1.wireOp",EDGE,"E29"),sQuery(id+"F1.wireOp",EDGE,"E30"),sQuery(id+"F1.wireOp",EDGE,"E31"),sQuery(id+"F1.wireOp",EDGE,"E32"),sQuery(id+"F1.wireOp",EDGE,"E33"),sQuery(id+"F1.wireOp",EDGE,"E34"),sQuery(id+"F1.wireOp",EDGE,"E35"),sQuery(id+"F1.wireOp",EDGE,"E36"),sQuery(id+"F1.wireOp",EDGE,"E37"),sQuery(id+"F1.wireOp",EDGE,"E38"),sQuery(id+"F1.wireOp",EDGE,"E39"),sQuery(id+"F1.wireOp",EDGE,"E40"),sQuery(id+"F1.wireOp",EDGE,"E41"),sQuery(id+"F1.wireOp",EDGE,"E42"),sQuery(id+"F1.wireOp",EDGE,"E43"),sQuery(id+"F1.wireOp",EDGE,"E44"),sQuery(id+"F1.wireOp",EDGE,"E45"),sQuery(id+"F1.wireOp",EDGE,"E45"),sQuery(id+"F1.wireOp",EDGE,"E46"),sQuery(id+"F1.wireOp",EDGE,"E47"),sQuery(id+"F1.wireOp",EDGE,"E48"),sQuery(id+"F1.wireOp",EDGE,"E49"),sQuery(id+"F1.wireOp",EDGE,"E50"),sQuery(id+"F1.wireOp",EDGE,"E51"),sQuery(id+"F1.wireOp",EDGE,"E52"),sQuery(id+"F1.wireOp",EDGE,"E53"),sQuery(id+"F1.wireOp",EDGE,"E54"),sQuery(id+"F1.wireOp",EDGE,"E55"),sQuery(id+"F1.wireOp",EDGE,"E56"),sQuery(id+"F1.wireOp",EDGE,"E57"),sQuery(id+"F1.wireOp",EDGE,"E58"),sQuery(id+"F1.wireOp",EDGE,"E59"),sQuery(id+"F1.wireOp",EDGE,"E60"),sQuery(id+"F1.wireOp",EDGE,"E61"),sQuery(id+"F1.wireOp",EDGE,"E62"),sQuery(id+"F1.wireOp",EDGE,"E63"),sQuery(id+"F1.wireOp",EDGE,"E64"),sQuery(id+"F1.wireOp",EDGE,"E65"),sQuery(id+"F1.wireOp",EDGE,"E66"),sQuery(id+"F1.wireOp",EDGE,"E67"),sQuery(id+"F1.wireOp",EDGE,"E68"),sQuery(id+"F1.wireOp",EDGE,"E69"),sQuery(id+"F1.wireOp",EDGE,"E70"),sQuery(id+"F1.wireOp",EDGE,"E71"),sQuery(id+"F1.wireOp",EDGE,"E72"),sQuery(id+"F1.wireOp",EDGE,"E73"),sQuery(id+"F1.wireOp",EDGE,"E74"),sQuery(id+"F1.wireOp",EDGE,"E75"),sQuery(id+"F1.wireOp",EDGE,"E76"),sQuery(id+"F1.wireOp",EDGE,"E77"),sQuery(id+"F1.wireOp",EDGE,"E78"),sQuery(id+"F1.wireOp",EDGE,"E79"),sQuery(id+"F1.wireOp",EDGE,"E80"),sQuery(id+"F1.wireOp",EDGE,"E81"),sQuery(id+"F1.wireOp",EDGE,"E82"),sQuery(id+"F1.wireOp",EDGE,"E83"),sQuery(id+"F1.wireOp",EDGE,"E84"),sQuery(id+"F1.wireOp",EDGE,"E85"),sQuery(id+"F1.wireOp",EDGE,"E86"),sQuery(id+"F1.wireOp",EDGE,"E87"),sQuery(id+"F1.wireOp",EDGE,"E88"),sQuery(id+"F1.wireOp",EDGE,"E89"),sQuery(id+"F1.wireOp",EDGE,"E90"),sQuery(id+"F1.wireOp",EDGE,"E91"),sQuery(id+"F1.wireOp",EDGE,"E92"),sQuery(id+"F1.wireOp",EDGE,"E93"),sQuery(id+"F1.wireOp",EDGE,"E94"),sQuery(id+"F1.wireOp",EDGE,"E95"),sQuery(id+"F1.wireOp",EDGE,"E96"),sQuery(id+"F1.wireOp",EDGE,"E97"),sQuery(id+"F1.wireOp",EDGE,"E98"),sQuery(id+"F1.wireOp",EDGE,"E99"),sQuery(id+"F1.wireOp",EDGE,"E100"),sQuery(id+"F1.wireOp",EDGE,"E101"),sQuery(id+"F1.wireOp",EDGE,"E102"),sQuery(id+"F1.wireOp",EDGE,"E103"),sQuery(id+"F1.wireOp",EDGE,"E104"),sQuery(id+"F1.wireOp",EDGE,"E104"),sQuery(id+"F1.wireOp",EDGE,"E105"),sQuery(id+"F1.wireOp",EDGE,"E106"),sQuery(id+"F1.wireOp",EDGE,"E107"),sQuery(id+"F1.wireOp",EDGE,"E108"),sQuery(id+"F1.wireOp",EDGE,"E109"),sQuery(id+"F1.wireOp",EDGE,"E110"),sQuery(id+"F1.wireOp",EDGE,"E111"),sQuery(id+"F1.wireOp",EDGE,"E112"),sQuery(id+"F1.wireOp",EDGE,"E113"),sQuery(id+"F1.wireOp",EDGE,"E114"),sQuery(id+"F1.wireOp",EDGE,"E115"),sQuery(id+"F1.wireOp",EDGE,"E116"),sQuery(id+"F1.wireOp",EDGE,"E117"),sQuery(id+"F1.wireOp",EDGE,"E118"),sQuery(id+"F1.wireOp",EDGE,"E119"),sQuery(id+"F1.wireOp",EDGE,"E120"),sQuery(id+"F1.wireOp",EDGE,"E121"),sQuery(id+"F1.wireOp",EDGE,"E122"),sQuery(id+"F1.wireOp",EDGE,"E123"),sQuery(id+"F1.wireOp",EDGE,"E124"),sQuery(id+"F1.wireOp",EDGE,"E125"),sQuery(id+"F1.wireOp",EDGE,"E126"),sQuery(id+"F1.wireOp",EDGE,"E127"),sQuery(id+"F1.wireOp",EDGE,"E128"),sQuery(id+"F1.wireOp",EDGE,"E129"),sQuery(id+"F1.wireOp",EDGE,"E130"),sQuery(id+"F1.wireOp",EDGE,"E131"),sQuery(id+"F1.wireOp",EDGE,"E132"),sQuery(id+"F1.wireOp",EDGE,"E133"),sQuery(id+"F1.wireOp",EDGE,"E134"),sQuery(id+"F1.wireOp",EDGE,"E135"),sQuery(id+"F1.wireOp",EDGE,"E136"),sQuery(id+"F1.wireOp",EDGE,"E137"),sQuery(id+"F1.wireOp",EDGE,"E138"),sQuery(id+"F1.wireOp",EDGE,"E139"),sQuery(id+"F1.wireOp",EDGE,"E140"),sQuery(id+"F1.wireOp",EDGE,"E141"),sQuery(id+"F1.wireOp",EDGE,"E142"),sQuery(id+"F1.wireOp",EDGE,"E143"),sQuery(id+"F1.wireOp",EDGE,"E144"),sQuery(id+"F1.wireOp",EDGE,"E145"),sQuery(id+"F1.wireOp",EDGE,"E146"),sQuery(id+"F1.wireOp",EDGE,"E147"),sQuery(id+"F1.wireOp",EDGE,"E148"),sQuery(id+"F1.wireOp",EDGE,"E149"),sQuery(id+"F1.wireOp",EDGE,"E150"),sQuery(id+"F1.wireOp",EDGE,"E151"),sQuery(id+"F1.wireOp",EDGE,"E152"),sQuery(id+"F1.wireOp",EDGE,"E153"),sQuery(id+"F1.wireOp",EDGE,"E154"),sQuery(id+"F1.wireOp",EDGE,"E155"),sQuery(id+"F1.wireOp",EDGE,"E156"),sQuery(id+"F1.wireOp",EDGE,"E157"),sQuery(id+"F1.wireOp",EDGE,"E158"),sQuery(id+"F1.wireOp",EDGE,"E159"),sQuery(id+"F1.wireOp",EDGE,"E160"),sQuery(id+"F1.wireOp",EDGE,"E161"),sQuery(id+"F1.wireOp",EDGE,"E162"),sQuery(id+"F1.wireOp",EDGE,"E163"),sQuery(id+"F1.wireOp",EDGE,"E164"),sQuery(id+"F1.wireOp",EDGE,"E165"),sQuery(id+"F1.wireOp",EDGE,"E166"),sQuery(id+"F1.wireOp",EDGE,"E167"),sQuery(id+"F1.wireOp",EDGE,"E168"),sQuery(id+"F1.wireOp",EDGE,"E169"),sQuery(id+"F1.wireOp",EDGE,"E170"),sQuery(id+"F1.wireOp",EDGE,"E171"),sQuery(id+"F1.wireOp",EDGE,"E172"),sQuery(id+"F1.wireOp",EDGE,"E173"),sQuery(id+"F1.wireOp",EDGE,"E174"),sQuery(id+"F1.wireOp",EDGE,"E175"),sQuery(id+"F1.wireOp",EDGE,"E176"),sQuery(id+"F1.wireOp",EDGE,"E177"),sQuery(id+"F1.wireOp",EDGE,"E178"),sQuery(id+"F1.wireOp",EDGE,"E179"),sQuery(id+"F1.wireOp",EDGE,"E180"),sQuery(id+"F1.wireOp",EDGE,"E181"),sQuery(id+"F1.wireOp",EDGE,"E182"),sQuery(id+"F1.wireOp",EDGE,"E183"),sQuery(id+"F1.wireOp",EDGE,"E184"),sQuery(id+"F1.wireOp",EDGE,"E185"),sQuery(id+"F1.wireOp",EDGE,"E186"),sQuery(id+"F1.wireOp",EDGE,"E187"),sQuery(id+"F1.wireOp",EDGE,"E188"),sQuery(id+"F1.wireOp",EDGE,"E189"),sQuery(id+"F1.wireOp",EDGE,"E190"),sQuery(id+"F1.wireOp",EDGE,"E191"),sQuery(id+"F1.wireOp",EDGE,"E192"),sQuery(id+"F1.wireOp",EDGE,"E193"),sQuery(id+"F1.wireOp",EDGE,"E194"),sQuery(id+"F1.wireOp",EDGE,"E195"),sQuery(id+"F1.wireOp",EDGE,"E196"),sQuery(id+"F1.wireOp",EDGE,"E197"),sQuery(id+"F1.wireOp",EDGE,"E198"),sQuery(id+"F1.wireOp",EDGE,"E199"),sQuery(id+"F1.wireOp",EDGE,"E200"),sQuery(id+"F1.wireOp",EDGE,"E201"),sQuery(id+"F1.wireOp",EDGE,"E202"),sQuery(id+"F1.wireOp",EDGE,"E203"),sQuery(id+"F1.wireOp",EDGE,"E204"),sQuery(id+"F1.wireOp",EDGE,"E205"),sQuery(id+"F1.wireOp",EDGE,"E206"),sQuery(id+"F1.wireOp",EDGE,"E207"),sQuery(id+"F1.wireOp",EDGE,"E208"),sQuery(id+"F1.wireOp",EDGE,"E209"),sQuery(id+"F1.wireOp",EDGE,"E210"),sQuery(id+"F1.wireOp",EDGE,"E211"),sQuery(id+"F1.wireOp",EDGE,"E212"),sQuery(id+"F1.wireOp",EDGE,"E213"),sQuery(id+"F1.wireOp",EDGE,"E214"),sQuery(id+"F1.wireOp",EDGE,"E215"),sQuery(id+"F1.wireOp",EDGE,"E216"),sQuery(id+"F1.wireOp",EDGE,"E217"),sQuery(id+"F1.wireOp",EDGE,"E218"),sQuery(id+"F1.wireOp",EDGE,"E219"),sQuery(id+"F1.wireOp",EDGE,"E220"),sQuery(id+"F1.wireOp",EDGE,"E221"),sQuery(id+"F1.wireOp",EDGE,"E222"),sQuery(id+"F1.wireOp",EDGE,"E223"),sQuery(id+"F1.wireOp",EDGE,"E224"),sQuery(id+"F1.wireOp",EDGE,"E225"),sQuery(id+"F1.wireOp",EDGE,"E226"),sQuery(id+"F1.wireOp",EDGE,"E227"),sQuery(id+"F1.wireOp",EDGE,"E228"),sQuery(id+"F1.wireOp",EDGE,"E229"),sQuery(id+"F1.wireOp",EDGE,"E230"),sQuery(id+"F1.wireOp",EDGE,"E231"),sQuery(id+"F1.wireOp",EDGE,"E232"),sQuery(id+"F1.wireOp",EDGE,"E233"),sQuery(id+"F1.wireOp",EDGE,"E234"),sQuery(id+"F1.wireOp",EDGE,"E235"),sQuery(id+"F1.wireOp",EDGE,"E236"),sQuery(id+"F1.wireOp",EDGE,"E237"),sQuery(id+"F1.wireOp",EDGE,"E238"),sQuery(id+"F1.wireOp",EDGE,"E239"),sQuery(id+"F1.wireOp",EDGE,"E240"),sQuery(id+"F1.wireOp",EDGE,"E241"),sQuery(id+"F1.wireOp",EDGE,"E242"),sQuery(id+"F1.wireOp",EDGE,"E243"),sQuery(id+"F1.wireOp",EDGE,"E244"),sQuery(id+"F1.wireOp",EDGE,"E245"),sQuery(id+"F1.wireOp",EDGE,"E246"),sQuery(id+"F1.wireOp",EDGE,"E247"),sQuery(id+"F1.wireOp",EDGE,"E248"),sQuery(id+"F1.wireOp",EDGE,"E249"),sQuery(id+"F1.wireOp",EDGE,"E250"),sQuery(id+"F1.wireOp",EDGE,"E251"),sQuery(id+"F1.wireOp",EDGE,"E252"),sQuery(id+"F1.wireOp",EDGE,"E253"),sQuery(id+"F1.wireOp",EDGE,"E254"),sQuery(id+"F1.wireOp",EDGE,"E255"),sQuery(id+"F1.wireOp",EDGE,"E256"),sQuery(id+"F1.wireOp",EDGE,"E257"),sQuery(id+"F1.wireOp",EDGE,"E258"),sQuery(id+"F1.wireOp",EDGE,"E259"),sQuery(id+"F1.wireOp",EDGE,"E260"),sQuery(id+"F1.wireOp",EDGE,"E261"),sQuery(id+"F1.wireOp",EDGE,"E262"),sQuery(id+"F1.wireOp",EDGE,"E263"),sQuery(id+"F1.wireOp",EDGE,"E264"),sQuery(id+"F1.wireOp",EDGE,"E265"),sQuery(id+"F1.wireOp",EDGE,"E266"),sQuery(id+"F1.wireOp",EDGE,"E267"),sQuery(id+"F1.wireOp",EDGE,"E268"),sQuery(id+"F1.wireOp",EDGE,"E269"),sQuery(id+"F1.wireOp",EDGE,"E270"),sQuery(id+"F1.wireOp",EDGE,"E271"),sQuery(id+"F1.wireOp",EDGE,"E272"),sQuery(id+"F1.wireOp",EDGE,"E273"),sQuery(id+"F1.wireOp",EDGE,"E274"),sQuery(id+"F1.wireOp",EDGE,"E275"),sQuery(id+"F1.wireOp",EDGE,"E276"),sQuery(id+"F1.wireOp",EDGE,"E277"),sQuery(id+"F1.wireOp",EDGE,"E278"),sQuery(id+"F1.wireOp",EDGE,"E279"),sQuery(id+"F1.wireOp",EDGE,"E280"),sQuery(id+"F1.wireOp",EDGE,"E281"),sQuery(id+"F1.wireOp",EDGE,"E282"),sQuery(id+"F1.wireOp",EDGE,"E283"),sQuery(id+"F1.wireOp",EDGE,"E284"),sQuery(id+"F1.wireOp",EDGE,"E285"),sQuery(id+"F1.wireOp",EDGE,"E286"),sQuery(id+"F1.wireOp",EDGE,"E287"),sQuery(id+"F1.wireOp",EDGE,"E288"),sQuery(id+"F1.wireOp",EDGE,"E289"),sQuery(id+"F1.wireOp",EDGE,"E290"),sQuery(id+"F1.wireOp",EDGE,"E291"),sQuery(id+"F1.wireOp",EDGE,"E292"),sQuery(id+"F1.wireOp",EDGE,"E293"),sQuery(id+"F1.wireOp",EDGE,"E294"),sQuery(id+"F1.wireOp",EDGE,"E295"),sQuery(id+"F1.wireOp",EDGE,"E296"),sQuery(id+"F1.wireOp",EDGE,"E297"),sQuery(id+"F1.wireOp",EDGE,"E298"),sQuery(id+"F1.wireOp",EDGE,"E299"),sQuery(id+"F1.wireOp",EDGE,"E300"),sQuery(id+"F1.wireOp",EDGE,"E301"),sQuery(id+"F1.wireOp",EDGE,"E302"),sQuery(id+"F1.wireOp",EDGE,"E303"),sQuery(id+"F1.wireOp",EDGE,"E304"),sQuery(id+"F1.wireOp",EDGE,"E305"),sQuery(id+"F1.wireOp",EDGE,"E306"),sQuery(id+"F1.wireOp",EDGE,"E307"),sQuery(id+"F1.wireOp",EDGE,"E308"),sQuery(id+"F1.wireOp",EDGE,"E309"),sQuery(id+"F1.wireOp",EDGE,"E310"),sQuery(id+"F1.wireOp",EDGE,"E311"),sQuery(id+"F1.wireOp",EDGE,"E312"),sQuery(id+"F1.wireOp",EDGE,"E313"),sQuery(id+"F1.wireOp",EDGE,"E314"),sQuery(id+"F1.wireOp",EDGE,"E315"),sQuery(id+"F1.wireOp",EDGE,"E316"),sQuery(id+"F1.wireOp",EDGE,"E317"),sQuery(id+"F1.wireOp",EDGE,"E318"),sQuery(id+"F1.wireOp",EDGE,"E319"),sQuery(id+"F1.wireOp",EDGE,"E320"),sQuery(id+"F1.wireOp",EDGE,"E321"),sQuery(id+"F1.wireOp",EDGE,"E322"),sQuery(id+"F1.wireOp",EDGE,"E323"),sQuery(id+"F1.wireOp",EDGE,"E324"),sQuery(id+"F1.wireOp",EDGE,"E325"),sQuery(id+"F1.wireOp",EDGE,"E326"),sQuery(id+"F1.wireOp",EDGE,"E327"),sQuery(id+"F1.wireOp",EDGE,"E328"),sQuery(id+"F1.wireOp",EDGE,"E329"),sQuery(id+"F1.wireOp",EDGE,"E330"),sQuery(id+"F1.wireOp",EDGE,"E331"),sQuery(id+"F1.wireOp",EDGE,"E332"),sQuery(id+"F1.wireOp",EDGE,"E333"),sQuery(id+"F1.wireOp",EDGE,"E334"),sQuery(id+"F1.wireOp",EDGE,"E334"),sQuery(id+"F1.wireOp",EDGE,"E335"),sQuery(id+"F1.wireOp",EDGE,"E336"),sQuery(id+"F1.wireOp",EDGE,"E337"),sQuery(id+"F1.wireOp",EDGE,"E338"),sQuery(id+"F1.wireOp",EDGE,"E339"),sQuery(id+"F1.wireOp",EDGE,"E340"),sQuery(id+"F1.wireOp",EDGE,"E341"),sQuery(id+"F1.wireOp",EDGE,"E342"),sQuery(id+"F1.wireOp",EDGE,"E343"),sQuery(id+"F1.wireOp",EDGE,"E344"),sQuery(id+"F1.wireOp",EDGE,"E345"),sQuery(id+"F1.wireOp",EDGE,"E346"),sQuery(id+"F1.wireOp",EDGE,"E347"),sQuery(id+"F1.wireOp",EDGE,"E348"),sQuery(id+"F1.wireOp",EDGE,"E349"),sQuery(id+"F1.wireOp",EDGE,"E350"),sQuery(id+"F1.wireOp",EDGE,"E351"),sQuery(id+"F1.wireOp",EDGE,"E352"),sQuery(id+"F1.wireOp",EDGE,"E353"),sQuery(id+"F1.wireOp",EDGE,"E354"),sQuery(id+"F1.wireOp",EDGE,"E355"),sQuery(id+"F1.wireOp",EDGE,"E356"),sQuery(id+"F1.wireOp",EDGE,"E357"),sQuery(id+"F1.wireOp",EDGE,"E358"),sQuery(id+"F1.wireOp",EDGE,"E359"),sQuery(id+"F1.wireOp",EDGE,"E360"),sQuery(id+"F1.wireOp",EDGE,"E361"),sQuery(id+"F1.wireOp",EDGE,"E362"),sQuery(id+"F1.wireOp",EDGE,"E363"),sQuery(id+"F1.wireOp",EDGE,"E364"),sQuery(id+"F1.wireOp",EDGE,"E365"),sQuery(id+"F1.wireOp",EDGE,"E366"),sQuery(id+"F1.wireOp",EDGE,"E367"),sQuery(id+"F1.wireOp",EDGE,"E368"),sQuery(id+"F1.wireOp",EDGE,"E369"),sQuery(id+"F1.wireOp",EDGE,"E370"),sQuery(id+"F1.wireOp",EDGE,"E371"),sQuery(id+"F1.wireOp",EDGE,"E372"),sQuery(id+"F1.wireOp",EDGE,"E373"),sQuery(id+"F1.wireOp",EDGE,"E374"),sQuery(id+"F1.wireOp",EDGE,"E375"),sQuery(id+"F1.wireOp",EDGE,"E376"),sQuery(id+"F1.wireOp",EDGE,"E377"),sQuery(id+"F1.wireOp",EDGE,"E378"),sQuery(id+"F1.wireOp",EDGE,"E379"),sQuery(id+"F1.wireOp",EDGE,"E380"),sQuery(id+"F1.wireOp",EDGE,"E381"),sQuery(id+"F1.wireOp",EDGE,"E382"),sQuery(id+"F1.wireOp",EDGE,"E383"),sQuery(id+"F1.wireOp",EDGE,"E384"),sQuery(id+"F1.wireOp",EDGE,"E385"),sQuery(id+"F1.wireOp",EDGE,"E386"),sQuery(id+"F1.wireOp",EDGE,"E387"),sQuery(id+"F1.wireOp",EDGE,"E388"),sQuery(id+"F1.wireOp",EDGE,"E389"),sQuery(id+"F1.wireOp",EDGE,"E390"),sQuery(id+"F1.wireOp",EDGE,"E391"),sQuery(id+"F1.wireOp",EDGE,"E392"),sQuery(id+"F1.wireOp",EDGE,"E393"),sQuery(id+"F1.wireOp",EDGE,"E394"),sQuery(id+"F1.wireOp",EDGE,"E395"),sQuery(id+"F1.wireOp",EDGE,"E396"),sQuery(id+"F1.wireOp",EDGE,"E397"),sQuery(id+"F1.wireOp",EDGE,"E398"),sQuery(id+"F1.wireOp",EDGE,"E399"),sQuery(id+"F1.wireOp",EDGE,"E400"),sQuery(id+"F1.wireOp",EDGE,"E401"),sQuery(id+"F1.wireOp",EDGE,"E402"),sQuery(id+"F1.wireOp",EDGE,"E403"),sQuery(id+"F1.wireOp",EDGE,"E404"),sQuery(id+"F1.wireOp",EDGE,"E405"),sQuery(id+"F1.wireOp",EDGE,"E406"),sQuery(id+"F1.wireOp",EDGE,"E407"),sQuery(id+"F1.wireOp",EDGE,"E408"),sQuery(id+"F1.wireOp",EDGE,"E409"),sQuery(id+"F1.wireOp",EDGE,"E410"),sQuery(id+"F1.wireOp",EDGE,"E411"),sQuery(id+"F1.wireOp",EDGE,"E412"),sQuery(id+"F1.wireOp",EDGE,"E413"),sQuery(id+"F1.wireOp",EDGE,"E414"),sQuery(id+"F1.wireOp",EDGE,"E415"),sQuery(id+"F1.wireOp",EDGE,"E416"),sQuery(id+"F1.wireOp",EDGE,"E417"),sQuery(id+"F1.wireOp",EDGE,"E418"),sQuery(id+"F1.wireOp",EDGE,"E419"),sQuery(id+"F1.wireOp",EDGE,"E420"),sQuery(id+"F1.wireOp",EDGE,"E421"),sQuery(id+"F1.wireOp",EDGE,"E422"),sQuery(id+"F1.wireOp",EDGE,"E423"),sQuery(id+"F1.wireOp",EDGE,"E424"),sQuery(id+"F1.wireOp",EDGE,"E425"),sQuery(id+"F1.wireOp",EDGE,"E426"),sQuery(id+"F1.wireOp",EDGE,"E426"),sQuery(id+"F1.wireOp",EDGE,"E427"),sQuery(id+"F1.wireOp",EDGE,"E428"),sQuery(id+"F1.wireOp",EDGE,"E429"),sQuery(id+"F1.wireOp",EDGE,"E430"),sQuery(id+"F1.wireOp",EDGE,"E431"),sQuery(id+"F1.wireOp",EDGE,"E432"),sQuery(id+"F1.wireOp",EDGE,"E433"),sQuery(id+"F1.wireOp",EDGE,"E434"),sQuery(id+"F1.wireOp",EDGE,"E435"),sQuery(id+"F1.wireOp",EDGE,"E435"),sQuery(id+"F1.wireOp",EDGE,"E436"),sQuery(id+"F1.wireOp",EDGE,"E437"),sQuery(id+"F1.wireOp",EDGE,"E438"),sQuery(id+"F1.wireOp",EDGE,"E439"),sQuery(id+"F1.wireOp",EDGE,"E440"),sQuery(id+"F1.wireOp",EDGE,"E441"),sQuery(id+"F1.wireOp",EDGE,"E442"),sQuery(id+"F1.wireOp",EDGE,"E443"),sQuery(id+"F1.wireOp",EDGE,"E444"),sQuery(id+"F1.wireOp",EDGE,"E445"),sQuery(id+"F1.wireOp",EDGE,"E446"),sQuery(id+"F1.wireOp",EDGE,"E447"),sQuery(id+"F1.wireOp",EDGE,"E448"),sQuery(id+"F1.wireOp",EDGE,"E449"),sQuery(id+"F1.wireOp",EDGE,"E450"),sQuery(id+"F1.wireOp",EDGE,"E451"),sQuery(id+"F1.wireOp",EDGE,"E452"),sQuery(id+"F1.wireOp",EDGE,"E453"),sQuery(id+"F1.wireOp",EDGE,"E454"),sQuery(id+"F1.wireOp",EDGE,"E455"),sQuery(id+"F1.wireOp",EDGE,"E456"),sQuery(id+"F1.wireOp",EDGE,"E457"),sQuery(id+"F1.wireOp",EDGE,"E458"),sQuery(id+"F1.wireOp",EDGE,"E459"),sQuery(id+"F1.wireOp",EDGE,"E460"),sQuery(id+"F1.wireOp",EDGE,"E461"),sQuery(id+"F1.wireOp",EDGE,"E462"),sQuery(id+"F1.wireOp",EDGE,"E463"),sQuery(id+"F1.wireOp",EDGE,"E464"),sQuery(id+"F1.wireOp",EDGE,"E465"),sQuery(id+"F1.wireOp",EDGE,"E466"),sQuery(id+"F1.wireOp",EDGE,"E467"),sQuery(id+"F1.wireOp",EDGE,"E468"),sQuery(id+"F1.wireOp",EDGE,"E469"),sQuery(id+"F1.wireOp",EDGE,"E470"),sQuery(id+"F1.wireOp",EDGE,"E471"),sQuery(id+"F1.wireOp",EDGE,"E472"),sQuery(id+"F1.wireOp",EDGE,"E473"),sQuery(id+"F1.wireOp",EDGE,"E474"),sQuery(id+"F1.wireOp",EDGE,"E475"),sQuery(id+"F1.wireOp",EDGE,"E476"),sQuery(id+"F1.wireOp",EDGE,"E477"),sQuery(id+"F1.wireOp",EDGE,"E478"),sQuery(id+"F1.wireOp",EDGE,"E479"),sQuery(id+"F1.wireOp",EDGE,"E480"),sQuery(id+"F1.wireOp",EDGE,"E481"),sQuery(id+"F1.wireOp",EDGE,"E482"),sQuery(id+"F1.wireOp",EDGE,"E483"),sQuery(id+"F1.wireOp",EDGE,"E484"),sQuery(id+"F1.wireOp",EDGE,"E485"),sQuery(id+"F1.wireOp",EDGE,"E486"),sQuery(id+"F1.wireOp",EDGE,"E487"),sQuery(id+"F1.wireOp",EDGE,"E488"),sQuery(id+"F1.wireOp",EDGE,"E489"),sQuery(id+"F1.wireOp",EDGE,"E490"),sQuery(id+"F1.wireOp",EDGE,"E491"),sQuery(id+"F1.wireOp",EDGE,"E492"),sQuery(id+"F1.wireOp",EDGE,"E493"),sQuery(id+"F1.wireOp",EDGE,"E494"),sQuery(id+"F1.wireOp",EDGE,"E495"),sQuery(id+"F1.wireOp",EDGE,"E496"),sQuery(id+"F1.wireOp",EDGE,"E497"),sQuery(id+"F1.wireOp",EDGE,"E498"),sQuery(id+"F1.wireOp",EDGE,"E499"),sQuery(id+"F1.wireOp",EDGE,"E500"),sQuery(id+"F1.wireOp",EDGE,"E501"),sQuery(id+"F1.wireOp",EDGE,"E502"),sQuery(id+"F1.wireOp",EDGE,"E503"),sQuery(id+"F1.wireOp",EDGE,"E504"),sQuery(id+"F1.wireOp",EDGE,"E505"),sQuery(id+"F1.wireOp",EDGE,"E506"),sQuery(id+"F1.wireOp",EDGE,"E507"),sQuery(id+"F1.wireOp",EDGE,"E508"),sQuery(id+"F1.wireOp",EDGE,"E509"),sQuery(id+"F1.wireOp",EDGE,"E510"),sQuery(id+"F1.wireOp",EDGE,"E511"),sQuery(id+"F1.wireOp",EDGE,"E512"),sQuery(id+"F1.wireOp",EDGE,"E513"),sQuery(id+"F1.wireOp",EDGE,"E514"),sQuery(id+"F1.wireOp",EDGE,"E515"),sQuery(id+"F1.wireOp",EDGE,"E516"),sQuery(id+"F1.wireOp",EDGE,"E517"),sQuery(id+"F1.wireOp",EDGE,"E518"),sQuery(id+"F1.wireOp",EDGE,"E519"),sQuery(id+"F1.wireOp",EDGE,"E520"),sQuery(id+"F1.wireOp",EDGE,"E521"),sQuery(id+"F1.wireOp",EDGE,"E522"),sQuery(id+"F1.wireOp",EDGE,"E523"),sQuery(id+"F1.wireOp",EDGE,"E524"),sQuery(id+"F1.wireOp",EDGE,"E525"),sQuery(id+"F1.wireOp",EDGE,"E526"),sQuery(id+"F1.wireOp",EDGE,"E527"),sQuery(id+"F1.wireOp",EDGE,"E528"),sQuery(id+"F1.wireOp",EDGE,"E529"),sQuery(id+"F1.wireOp",EDGE,"E530"),sQuery(id+"F1.wireOp",EDGE,"E531"),sQuery(id+"F1.wireOp",EDGE,"E532"),sQuery(id+"F1.wireOp",EDGE,"E533"),sQuery(id+"F1.wireOp",EDGE,"E534"),sQuery(id+"F1.wireOp",EDGE,"E534"),sQuery(id+"F1.wireOp",EDGE,"E535"),sQuery(id+"F1.wireOp",EDGE,"E536"),sQuery(id+"F1.wireOp",EDGE,"E537"),sQuery(id+"F1.wireOp",EDGE,"E538"),sQuery(id+"F1.wireOp",EDGE,"E539"),sQuery(id+"F1.wireOp",EDGE,"E540"),sQuery(id+"F1.wireOp",EDGE,"E541"),sQuery(id+"F1.wireOp",EDGE,"E542"),sQuery(id+"F1.wireOp",EDGE,"E543"),sQuery(id+"F1.wireOp",EDGE,"E544"),sQuery(id+"F1.wireOp",EDGE,"E545"),sQuery(id+"F1.wireOp",EDGE,"E546"),sQuery(id+"F1.wireOp",EDGE,"E547"),sQuery(id+"F1.wireOp",EDGE,"E548"),sQuery(id+"F1.wireOp",EDGE,"E549"),sQuery(id+"F1.wireOp",EDGE,"E550"),sQuery(id+"F1.wireOp",EDGE,"E551"),sQuery(id+"F1.wireOp",EDGE,"E552"),sQuery(id+"F1.wireOp",EDGE,"E553"),sQuery(id+"F1.wireOp",EDGE,"E554"),sQuery(id+"F1.wireOp",EDGE,"E555"),sQuery(id+"F1.wireOp",EDGE,"E556"),sQuery(id+"F1.wireOp",EDGE,"E557"),sQuery(id+"F1.wireOp",EDGE,"E558"),sQuery(id+"F1.wireOp",EDGE,"E559"),sQuery(id+"F1.wireOp",EDGE,"E560"),sQuery(id+"F1.wireOp",EDGE,"E561"),sQuery(id+"F1.wireOp",EDGE,"E562"),sQuery(id+"F1.wireOp",EDGE,"E563"),sQuery(id+"F1.wireOp",EDGE,"E564"),sQuery(id+"F1.wireOp",EDGE,"E565"),sQuery(id+"F1.wireOp",EDGE,"E566"),sQuery(id+"F1.wireOp",EDGE,"E567"),sQuery(id+"F1.wireOp",EDGE,"E568"),sQuery(id+"F1.wireOp",EDGE,"E569"),sQuery(id+"F1.wireOp",EDGE,"E570"),sQuery(id+"F1.wireOp",EDGE,"E571"),sQuery(id+"F1.wireOp",EDGE,"E572"),sQuery(id+"F1.wireOp",EDGE,"E573"),sQuery(id+"F1.wireOp",EDGE,"E574"),sQuery(id+"F1.wireOp",EDGE,"E575"),sQuery(id+"F1.wireOp",EDGE,"E576"),sQuery(id+"F1.wireOp",EDGE,"E577"),sQuery(id+"F1.wireOp",EDGE,"E578"),sQuery(id+"F1.wireOp",EDGE,"E579"),sQuery(id+"F1.wireOp",EDGE,"E580"),sQuery(id+"F1.wireOp",EDGE,"E581"),sQuery(id+"F1.wireOp",EDGE,"E582"),sQuery(id+"F1.wireOp",EDGE,"E583"),sQuery(id+"F1.wireOp",EDGE,"E584"),sQuery(id+"F1.wireOp",EDGE,"E585"),sQuery(id+"F1.wireOp",EDGE,"E586"),sQuery(id+"F1.wireOp",EDGE,"E587"),sQuery(id+"F1.wireOp",EDGE,"E588"),sQuery(id+"F1.wireOp",EDGE,"E589"),sQuery(id+"F1.wireOp",EDGE,"E590"),sQuery(id+"F1.wireOp",EDGE,"E591"),sQuery(id+"F1.wireOp",EDGE,"E592"),sQuery(id+"F1.wireOp",EDGE,"E593"),sQuery(id+"F1.wireOp",EDGE,"E594"),sQuery(id+"F1.wireOp",EDGE,"E595"),sQuery(id+"F1.wireOp",EDGE,"E596"),sQuery(id+"F1.wireOp",EDGE,"E597"),sQuery(id+"F1.wireOp",EDGE,"E598"),sQuery(id+"F1.wireOp",EDGE,"E599"),sQuery(id+"F1.wireOp",EDGE,"E600"),sQuery(id+"F1.wireOp",EDGE,"E601"),sQuery(id+"F1.wireOp",EDGE,"E602"),sQuery(id+"F1.wireOp",EDGE,"E603"),sQuery(id+"F1.wireOp",EDGE,"E604"),sQuery(id+"F1.wireOp",EDGE,"E605"),sQuery(id+"F1.wireOp",EDGE,"E606"),sQuery(id+"F1.wireOp",EDGE,"E607"),sQuery(id+"F1.wireOp",EDGE,"E608"),sQuery(id+"F1.wireOp",EDGE,"E609"),sQuery(id+"F1.wireOp",EDGE,"E610"),sQuery(id+"F1.wireOp",EDGE,"E611"),sQuery(id+"F1.wireOp",EDGE,"E612"),sQuery(id+"F1.wireOp",EDGE,"E613"),sQuery(id+"F1.wireOp",EDGE,"E614"),sQuery(id+"F1.wireOp",EDGE,"E615"),sQuery(id+"F1.wireOp",EDGE,"E616"),sQuery(id+"F1.wireOp",EDGE,"E617"),sQuery(id+"F1.wireOp",EDGE,"E618"),sQuery(id+"F1.wireOp",EDGE,"E619"),sQuery(id+"F1.wireOp",EDGE,"E620"),sQuery(id+"F1.wireOp",EDGE,"E621"),sQuery(id+"F1.wireOp",EDGE,"E622"),sQuery(id+"F1.wireOp",EDGE,"E623"),sQuery(id+"F1.wireOp",EDGE,"E624"),sQuery(id+"F1.wireOp",EDGE,"E625"),sQuery(id+"F1.wireOp",EDGE,"E626"),sQuery(id+"F1.wireOp",EDGE,"E627"),sQuery(id+"F1.wireOp",EDGE,"E628"),sQuery(id+"F1.wireOp",EDGE,"E629"),sQuery(id+"F1.wireOp",EDGE,"E630"),sQuery(id+"F1.wireOp",EDGE,"E631"),sQuery(id+"F1.wireOp",EDGE,"E632"),sQuery(id+"F1.wireOp",EDGE,"E633"),sQuery(id+"F1.wireOp",EDGE,"E634"),sQuery(id+"F1.wireOp",EDGE,"E635"),sQuery(id+"F1.wireOp",EDGE,"E636"),sQuery(id+"F1.wireOp",EDGE,"E637"),sQuery(id+"F1.wireOp",EDGE,"E638"),sQuery(id+"F1.wireOp",EDGE,"E639"),sQuery(id+"F1.wireOp",EDGE,"E640"),sQuery(id+"F1.wireOp",EDGE,"E641"),sQuery(id+"F1.wireOp",EDGE,"E642"),sQuery(id+"F1.wireOp",EDGE,"E643"),sQuery(id+"F1.wireOp",EDGE,"E644"),sQuery(id+"F1.wireOp",EDGE,"E645"),sQuery(id+"F1.wireOp",EDGE,"E646"),sQuery(id+"F1.wireOp",EDGE,"E647"),sQuery(id+"F1.wireOp",EDGE,"E648"),sQuery(id+"F1.wireOp",EDGE,"E649"),sQuery(id+"F1.wireOp",EDGE,"E650"),sQuery(id+"F1.wireOp",EDGE,"E651"),sQuery(id+"F1.wireOp",EDGE,"E652"),sQuery(id+"F1.wireOp",EDGE,"E653"),sQuery(id+"F1.wireOp",EDGE,"E654"),sQuery(id+"F1.wireOp",EDGE,"E655"),sQuery(id+"F1.wireOp",EDGE,"E656"),sQuery(id+"F1.wireOp",EDGE,"E657"),sQuery(id+"F1.wireOp",EDGE,"E658"),sQuery(id+"F1.wireOp",EDGE,"E659"),sQuery(id+"F1.wireOp",EDGE,"E660"),sQuery(id+"F1.wireOp",EDGE,"E661"),sQuery(id+"F1.wireOp",EDGE,"E662"),sQuery(id+"F1.wireOp",EDGE,"E663"),sQuery(id+"F1.wireOp",EDGE,"E664"),sQuery(id+"F1.wireOp",EDGE,"E665"),sQuery(id+"F1.wireOp",EDGE,"E666"),sQuery(id+"F1.wireOp",EDGE,"E667"),sQuery(id+"F1.wireOp",EDGE,"E668"),sQuery(id+"F1.wireOp",EDGE,"E669"),sQuery(id+"F1.wireOp",EDGE,"E670"),sQuery(id+"F1.wireOp",EDGE,"E671"),sQuery(id+"F1.wireOp",EDGE,"E672"),sQuery(id+"F1.wireOp",EDGE,"E673"),sQuery(id+"F1.wireOp",EDGE,"E674"),sQuery(id+"F1.wireOp",EDGE,"E675"),sQuery(id+"F1.wireOp",EDGE,"E676"),sQuery(id+"F1.wireOp",EDGE,"E677"),sQuery(id+"F1.wireOp",EDGE,"E678"),sQuery(id+"F1.wireOp",EDGE,"E679"),sQuery(id+"F1.wireOp",EDGE,"E680"),sQuery(id+"F1.wireOp",EDGE,"E681"),sQuery(id+"F1.wireOp",EDGE,"E682"),sQuery(id+"F1.wireOp",EDGE,"E683"),sQuery(id+"F1.wireOp",EDGE,"E684"),sQuery(id+"F1.wireOp",EDGE,"E685"),sQuery(id+"F1.wireOp",EDGE,"E686"),sQuery(id+"F1.wireOp",EDGE,"E687"),sQuery(id+"F1.wireOp",EDGE,"E688"),sQuery(id+"F1.wireOp",EDGE,"E689"),sQuery(id+"F1.wireOp",EDGE,"E690"),sQuery(id+"F1.wireOp",EDGE,"E691"),sQuery(id+"F1.wireOp",EDGE,"E692"),sQuery(id+"F1.wireOp",EDGE,"E693"),sQuery(id+"F1.wireOp",EDGE,"E694"),sQuery(id+"F1.wireOp",EDGE,"E695"),sQuery(id+"F1.wireOp",EDGE,"E696"),sQuery(id+"F1.wireOp",EDGE,"E697"),sQuery(id+"F1.wireOp",EDGE,"E698"),sQuery(id+"F1.wireOp",EDGE,"E699"),sQuery(id+"F1.wireOp",EDGE,"E700"),sQuery(id+"F1.wireOp",EDGE,"E701"),sQuery(id+"F1.wireOp",EDGE,"E702"),sQuery(id+"F1.wireOp",EDGE,"E703"),sQuery(id+"F1.wireOp",EDGE,"E704"),sQuery(id+"F1.wireOp",EDGE,"E705"),sQuery(id+"F1.wireOp",EDGE,"E706"),sQuery(id+"F1.wireOp",EDGE,"E707"),sQuery(id+"F1.wireOp",EDGE,"E708"),sQuery(id+"F1.wireOp",EDGE,"E709"),sQuery(id+"F1.wireOp",EDGE,"E710"),sQuery(id+"F1.wireOp",EDGE,"E711"),sQuery(id+"F1.wireOp",EDGE,"E712"),sQuery(id+"F1.wireOp",EDGE,"E713"),sQuery(id+"F1.wireOp",EDGE,"E714"),sQuery(id+"F1.wireOp",EDGE,"E715"),sQuery(id+"F1.wireOp",EDGE,"E716"),sQuery(id+"F1.wireOp",EDGE,"E717"),sQuery(id+"F1.wireOp",EDGE,"E718"),sQuery(id+"F1.wireOp",EDGE,"E719"),sQuery(id+"F1.wireOp",EDGE,"E720"),sQuery(id+"F1.wireOp",EDGE,"E721"),sQuery(id+"F1.wireOp",EDGE,"E722"),sQuery(id+"F1.wireOp",EDGE,"E723"),sQuery(id+"F1.wireOp",EDGE,"E724"),sQuery(id+"F1.wireOp",EDGE,"E725"),sQuery(id+"F1.wireOp",EDGE,"E726"),sQuery(id+"F1.wireOp",EDGE,"E727"),sQuery(id+"F1.wireOp",EDGE,"E728"),sQuery(id+"F1.wireOp",EDGE,"E729"),sQuery(id+"F1.wireOp",EDGE,"E730"),sQuery(id+"F1.wireOp",EDGE,"E731"),sQuery(id+"F1.wireOp",EDGE,"E732"),sQuery(id+"F1.wireOp",EDGE,"E733"),sQuery(id+"F1.wireOp",EDGE,"E734"),sQuery(id+"F1.wireOp",EDGE,"E735"),sQuery(id+"F1.wireOp",EDGE,"E736"),sQuery(id+"F1.wireOp",EDGE,"E737"),sQuery(id+"F1.wireOp",EDGE,"E738"),sQuery(id+"F1.wireOp",EDGE,"E739"),sQuery(id+"F1.wireOp",EDGE,"E740"),sQuery(id+"F1.wireOp",EDGE,"E741"),sQuery(id+"F1.wireOp",EDGE,"E742"),sQuery(id+"F1.wireOp",EDGE,"E743"),sQuery(id+"F1.wireOp",EDGE,"E744"),sQuery(id+"F1.wireOp",EDGE,"E745"),sQuery(id+"F1.wireOp",EDGE,"E746"),sQuery(id+"F1.wireOp",EDGE,"E747"),sQuery(id+"F1.wireOp",EDGE,"E748"),sQuery(id+"F1.wireOp",EDGE,"E749"),sQuery(id+"F1.wireOp",EDGE,"E750"),sQuery(id+"F1.wireOp",EDGE,"E751"),sQuery(id+"F1.wireOp",EDGE,"E752"),sQuery(id+"F1.wireOp",EDGE,"E753"),sQuery(id+"F1.wireOp",EDGE,"E754"),sQuery(id+"F1.wireOp",EDGE,"E755"),sQuery(id+"F1.wireOp",EDGE,"E756"),sQuery(id+"F1.wireOp",EDGE,"E757"),sQuery(id+"F1.wireOp",EDGE,"E758"),sQuery(id+"F1.wireOp",EDGE,"E759"),sQuery(id+"F1.wireOp",EDGE,"E760"),sQuery(id+"F1.wireOp",EDGE,"E761"),sQuery(id+"F1.wireOp",EDGE,"E762"),sQuery(id+"F1.wireOp",EDGE,"E763"),sQuery(id+"F1.wireOp",EDGE,"E764"),sQuery(id+"F1.wireOp",EDGE,"E765"),sQuery(id+"F1.wireOp",EDGE,"E766"),sQuery(id+"F1.wireOp",EDGE,"E767"),sQuery(id+"F1.wireOp",EDGE,"E768"),sQuery(id+"F1.wireOp",EDGE,"E769"),sQuery(id+"F1.wireOp",EDGE,"E770"),sQuery(id+"F1.wireOp",EDGE,"E771"),sQuery(id+"F1.wireOp",EDGE,"E772"),sQuery(id+"F1.wireOp",EDGE,"E773"),sQuery(id+"F1.wireOp",EDGE,"E774"),sQuery(id+"F1.wireOp",EDGE,"E775"),sQuery(id+"F1.wireOp",EDGE,"E776"),sQuery(id+"F1.wireOp",EDGE,"E777"),sQuery(id+"F1.wireOp",EDGE,"E778"),sQuery(id+"F1.wireOp",EDGE,"E779"),sQuery(id+"F1.wireOp",EDGE,"E780"),sQuery(id+"F1.wireOp",EDGE,"E781"),sQuery(id+"F1.wireOp",EDGE,"E782"),sQuery(id+"F1.wireOp",EDGE,"E783"),sQuery(id+"F1.wireOp",EDGE,"E784"),sQuery(id+"F1.wireOp",EDGE,"E785"),sQuery(id+"F1.wireOp",EDGE,"E786"),sQuery(id+"F1.wireOp",EDGE,"E787"),sQuery(id+"F1.wireOp",EDGE,"E788"),sQuery(id+"F1.wireOp",EDGE,"E789"),sQuery(id+"F1.wireOp",EDGE,"E790"),sQuery(id+"F1.wireOp",EDGE,"E791"),sQuery(id+"F1.wireOp",EDGE,"E792"),sQuery(id+"F1.wireOp",EDGE,"E793"),sQuery(id+"F1.wireOp",EDGE,"E794"),sQuery(id+"F1.wireOp",EDGE,"E795"),sQuery(id+"F1.wireOp",EDGE,"E796"),sQuery(id+"F1.wireOp",EDGE,"E797"),sQuery(id+"F1.wireOp",EDGE,"E798"),sQuery(id+"F1.wireOp",EDGE,"E799"),sQuery(id+"F1.wireOp",EDGE,"E800"),sQuery(id+"F1.wireOp",EDGE,"E801"),sQuery(id+"F1.wireOp",EDGE,"E802"),sQuery(id+"F1.wireOp",EDGE,"E803"),sQuery(id+"F1.wireOp",EDGE,"E804"),sQuery(id+"F1.wireOp",EDGE,"E805"),sQuery(id+"F1.wireOp",EDGE,"E806"),sQuery(id+"F1.wireOp",EDGE,"E807"),sQuery(id+"F1.wireOp",EDGE,"E808"),sQuery(id+"F1.wireOp",EDGE,"E809"),sQuery(id+"F1.wireOp",EDGE,"E810"),sQuery(id+"F1.wireOp",EDGE,"E811"),sQuery(id+"F1.wireOp",EDGE,"E812"),sQuery(id+"F1.wireOp",EDGE,"E813"),sQuery(id+"F1.wireOp",EDGE,"E814"),sQuery(id+"F1.wireOp",EDGE,"E815"),sQuery(id+"F1.wireOp",EDGE,"E816"),sQuery(id+"F1.wireOp",EDGE,"E817"),sQuery(id+"F1.wireOp",EDGE,"E818"),sQuery(id+"F1.wireOp",EDGE,"E819"),sQuery(id+"F1.wireOp",EDGE,"E820"),sQuery(id+"F1.wireOp",EDGE,"E821"),sQuery(id+"F1.wireOp",EDGE,"E822"),sQuery(id+"F1.wireOp",EDGE,"E823"),sQuery(id+"F1.wireOp",EDGE,"E824"),sQuery(id+"F1.wireOp",EDGE,"E825"),sQuery(id+"F1.wireOp",EDGE,"E826"),sQuery(id+"F1.wireOp",EDGE,"E827"),sQuery(id+"F1.wireOp",EDGE,"E828"),sQuery(id+"F1.wireOp",EDGE,"E829"),sQuery(id+"F1.wireOp",EDGE,"E830"),sQuery(id+"F1.wireOp",EDGE,"E831"),sQuery(id+"F1.wireOp",EDGE,"E832"),sQuery(id+"F1.wireOp",EDGE,"E833"),sQuery(id+"F1.wireOp",EDGE,"E834"),sQuery(id+"F1.wireOp",EDGE,"E835"),sQuery(id+"F1.wireOp",EDGE,"E836"),sQuery(id+"F1.wireOp",EDGE,"E837"),sQuery(id+"F1.wireOp",EDGE,"E838"),sQuery(id+"F1.wireOp",EDGE,"E839"),sQuery(id+"F1.wireOp",EDGE,"E840"),sQuery(id+"F1.wireOp",EDGE,"E841"),sQuery(id+"F1.wireOp",EDGE,"E842"),sQuery(id+"F1.wireOp",EDGE,"E843"),sQuery(id+"F1.wireOp",EDGE,"E844"),sQuery(id+"F1.wireOp",EDGE,"E845"),sQuery(id+"F1.wireOp",EDGE,"E846"),sQuery(id+"F1.wireOp",EDGE,"E847"),sQuery(id+"F1.wireOp",EDGE,"E848"),sQuery(id+"F1.wireOp",EDGE,"E849"),sQuery(id+"F1.wireOp",EDGE,"E850"),sQuery(id+"F1.wireOp",EDGE,"E851"),sQuery(id+"F1.wireOp",EDGE,"E852"),sQuery(id+"F1.wireOp",EDGE,"E853"),sQuery(id+"F1.wireOp",EDGE,"E854"),sQuery(id+"F1.wireOp",EDGE,"E855"),sQuery(id+"F1.wireOp",EDGE,"E856"),sQuery(id+"F1.wireOp",EDGE,"E857"),sQuery(id+"F1.wireOp",EDGE,"E858"),sQuery(id+"F1.wireOp",EDGE,"E859"),sQuery(id+"F1.wireOp",EDGE,"E860"),sQuery(id+"F1.wireOp",EDGE,"E861"),sQuery(id+"F1.wireOp",EDGE,"E862"),sQuery(id+"F1.wireOp",EDGE,"E863"),sQuery(id+"F1.wireOp",EDGE,"E864"),sQuery(id+"F1.wireOp",EDGE,"E865"),sQuery(id+"F1.wireOp",EDGE,"E866"),sQuery(id+"F1.wireOp",EDGE,"E867"),sQuery(id+"F1.wireOp",EDGE,"E868"),sQuery(id+"F1.wireOp",EDGE,"E869"),sQuery(id+"F1.wireOp",EDGE,"E870"),sQuery(id+"F1.wireOp",EDGE,"E871"),sQuery(id+"F1.wireOp",EDGE,"E872"),sQuery(id+"F1.wireOp",EDGE,"E873"),sQuery(id+"F1.wireOp",EDGE,"E873"),sQuery(id+"F1.wireOp",EDGE,"E874"),sQuery(id+"F1.wireOp",EDGE,"E875"),sQuery(id+"F1.wireOp",EDGE,"E876"),sQuery(id+"F1.wireOp",EDGE,"E877"),sQuery(id+"F1.wireOp",EDGE,"E878"),sQuery(id+"F1.wireOp",EDGE,"E879"),sQuery(id+"F1.wireOp",EDGE,"E880"),sQuery(id+"F1.wireOp",EDGE,"E881"),sQuery(id+"F1.wireOp",EDGE,"E882"),sQuery(id+"F1.wireOp",EDGE,"E883"),sQuery(id+"F1.wireOp",EDGE,"E884"),sQuery(id+"F1.wireOp",EDGE,"E885"),sQuery(id+"F1.wireOp",EDGE,"E886"),sQuery(id+"F1.wireOp",EDGE,"E887"),sQuery(id+"F1.wireOp",EDGE,"E888"),sQuery(id+"F1.wireOp",EDGE,"E889"),sQuery(id+"F1.wireOp",EDGE,"E890"),sQuery(id+"F1.wireOp",EDGE,"E891"),sQuery(id+"F1.wireOp",EDGE,"E892"),sQuery(id+"F1.wireOp",EDGE,"E893"),sQuery(id+"F1.wireOp",EDGE,"E894"),sQuery(id+"F1.wireOp",EDGE,"E895"),sQuery(id+"F1.wireOp",EDGE,"E896"),sQuery(id+"F1.wireOp",EDGE,"E897"),sQuery(id+"F1.wireOp",EDGE,"E898"),sQuery(id+"F1.wireOp",EDGE,"E899"),sQuery(id+"F1.wireOp",EDGE,"E900"),sQuery(id+"F1.wireOp",EDGE,"E901"),sQuery(id+"F1.wireOp",EDGE,"E902"),sQuery(id+"F1.wireOp",EDGE,"E903"),sQuery(id+"F1.wireOp",EDGE,"E904"),sQuery(id+"F1.wireOp",EDGE,"E905"),sQuery(id+"F1.wireOp",EDGE,"E906"),sQuery(id+"F1.wireOp",EDGE,"E907"),sQuery(id+"F1.wireOp",EDGE,"E908"),sQuery(id+"F1.wireOp",EDGE,"E909"),sQuery(id+"F1.wireOp",EDGE,"E910"),sQuery(id+"F1.wireOp",EDGE,"E911"),sQuery(id+"F1.wireOp",EDGE,"E912"),sQuery(id+"F1.wireOp",EDGE,"E913"),sQuery(id+"F1.wireOp",EDGE,"E914"),sQuery(id+"F1.wireOp",EDGE,"E915"),sQuery(id+"F1.wireOp",EDGE,"E916"),sQuery(id+"F1.wireOp",EDGE,"E917"),sQuery(id+"F1.wireOp",EDGE,"E918"),sQuery(id+"F1.wireOp",EDGE,"E919"),sQuery(id+"F1.wireOp",EDGE,"E920"),sQuery(id+"F1.wireOp",EDGE,"E921"),sQuery(id+"F1.wireOp",EDGE,"E922"),sQuery(id+"F1.wireOp",EDGE,"E923"),sQuery(id+"F1.wireOp",EDGE,"E924"),sQuery(id+"F1.wireOp",EDGE,"E925"),sQuery(id+"F1.wireOp",EDGE,"E926"),sQuery(id+"F1.wireOp",EDGE,"E927"),sQuery(id+"F1.wireOp",EDGE,"E928"),sQuery(id+"F1.wireOp",EDGE,"E929"),sQuery(id+"F1.wireOp",EDGE,"E930"),sQuery(id+"F1.wireOp",EDGE,"E931"),sQuery(id+"F1.wireOp",EDGE,"E932"),sQuery(id+"F1.wireOp",EDGE,"E933"),sQuery(id+"F1.wireOp",EDGE,"E934"),sQuery(id+"F1.wireOp",EDGE,"E935"),sQuery(id+"F1.wireOp",EDGE,"E936"),sQuery(id+"F1.wireOp",EDGE,"E937"),sQuery(id+"F1.wireOp",EDGE,"E938"),sQuery(id+"F1.wireOp",EDGE,"E939"),sQuery(id+"F1.wireOp",EDGE,"E940"),sQuery(id+"F1.wireOp",EDGE,"E941"),sQuery(id+"F1.wireOp",EDGE,"E942"),sQuery(id+"F1.wireOp",EDGE,"E943"),sQuery(id+"F1.wireOp",EDGE,"E944"),sQuery(id+"F1.wireOp",EDGE,"E945"),sQuery(id+"F1.wireOp",EDGE,"E946"),sQuery(id+"F1.wireOp",EDGE,"E947"),sQuery(id+"F1.wireOp",EDGE,"E948"),sQuery(id+"F1.wireOp",EDGE,"E949"),sQuery(id+"F1.wireOp",EDGE,"E950"),sQuery(id+"F1.wireOp",EDGE,"E951"),sQuery(id+"F1.wireOp",EDGE,"E952"),sQuery(id+"F1.wireOp",EDGE,"E953"),sQuery(id+"F1.wireOp",EDGE,"E954"),sQuery(id+"F1.wireOp",EDGE,"E955"),sQuery(id+"F1.wireOp",EDGE,"E956"),sQuery(id+"F1.wireOp",EDGE,"E957"),sQuery(id+"F1.wireOp",EDGE,"E958"),sQuery(id+"F1.wireOp",EDGE,"E959"),sQuery(id+"F1.wireOp",EDGE,"E960"),sQuery(id+"F1.wireOp",EDGE,"E961"),sQuery(id+"F1.wireOp",EDGE,"E962"),sQuery(id+"F1.wireOp",EDGE,"E963"),sQuery(id+"F1.wireOp",EDGE,"E964"),sQuery(id+"F1.wireOp",EDGE,"E965"),sQuery(id+"F1.wireOp",EDGE,"E966"),sQuery(id+"F1.wireOp",EDGE,"E967"),sQuery(id+"F1.wireOp",EDGE,"E968"),sQuery(id+"F1.wireOp",EDGE,"E969"),sQuery(id+"F1.wireOp",EDGE,"E970"),sQuery(id+"F1.wireOp",EDGE,"E971"),sQuery(id+"F1.wireOp",EDGE,"E972"),sQuery(id+"F1.wireOp",EDGE,"E973"),sQuery(id+"F1.wireOp",EDGE,"E974"),sQuery(id+"F1.wireOp",EDGE,"E975"),sQuery(id+"F1.wireOp",EDGE,"E976"),sQuery(id+"F1.wireOp",EDGE,"E976"),sQuery(id+"F1.wireOp",EDGE,"E976"),sQuery(id+"F1.wireOp",EDGE,"E977"),sQuery(id+"F1.wireOp",EDGE,"E978"),sQuery(id+"F1.wireOp",EDGE,"E979"),sQuery(id+"F1.wireOp",EDGE,"E980"),sQuery(id+"F1.wireOp",EDGE,"E981"),sQuery(id+"F1.wireOp",EDGE,"E982"),sQuery(id+"F1.wireOp",EDGE,"E983"),sQuery(id+"F1.wireOp",EDGE,"E984"),sQuery(id+"F1.wireOp",EDGE,"E985"),sQuery(id+"F1.wireOp",EDGE,"E986"),sQuery(id+"F1.wireOp",EDGE,"E987"),sQuery(id+"F1.wireOp",EDGE,"E988"),sQuery(id+"F1.wireOp",EDGE,"E989"),sQuery(id+"F1.wireOp",EDGE,"E990"),sQuery(id+"F1.wireOp",EDGE,"E991"),sQuery(id+"F1.wireOp",EDGE,"E992"),sQuery(id+"F1.wireOp",EDGE,"E993"),sQuery(id+"F1.wireOp",EDGE,"E994"),sQuery(id+"F1.wireOp",EDGE,"E995"),sQuery(id+"F1.wireOp",EDGE,"E996"),sQuery(id+"F1.wireOp",EDGE,"E997"),sQuery(id+"F1.wireOp",EDGE,"E998"),sQuery(id+"F1.wireOp",EDGE,"E999"),sQuery(id+"F1.wireOp",EDGE,"E1000"),sQuery(id+"F1.wireOp",EDGE,"E1001"),sQuery(id+"F1.wireOp",EDGE,"E1002"),sQuery(id+"F1.wireOp",EDGE,"E1003"),sQuery(id+"F1.wireOp",EDGE,"E1004"),sQuery(id+"F1.wireOp",EDGE,"E1005"),sQuery(id+"F1.wireOp",EDGE,"E1006"),sQuery(id+"F1.wireOp",EDGE,"E1007"),sQuery(id+"F1.wireOp",EDGE,"E1008"),sQuery(id+"F1.wireOp",EDGE,"E1009"),sQuery(id+"F1.wireOp",EDGE,"E1010"),sQuery(id+"F1.wireOp",EDGE,"E1011"),sQuery(id+"F1.wireOp",EDGE,"E1012"),sQuery(id+"F1.wireOp",EDGE,"E1013"),sQuery(id+"F1.wireOp",EDGE,"E1014"),sQuery(id+"F1.wireOp",EDGE,"E1015"),sQuery(id+"F1.wireOp",EDGE,"E1016"),sQuery(id+"F1.wireOp",EDGE,"E1017"),sQuery(id+"F1.wireOp",EDGE,"E1018"),sQuery(id+"F1.wireOp",EDGE,"E1019"),sQuery(id+"F1.wireOp",EDGE,"E1020"),sQuery(id+"F1.wireOp",EDGE,"E1021"),sQuery(id+"F1.wireOp",EDGE,"E1022"),sQuery(id+"F1.wireOp",EDGE,"E1023"),sQuery(id+"F1.wireOp",EDGE,"E1024"),sQuery(id+"F1.wireOp",EDGE,"E1025"),sQuery(id+"F1.wireOp",EDGE,"E1026"),sQuery(id+"F1.wireOp",EDGE,"E1027"),sQuery(id+"F1.wireOp",EDGE,"E1028"),sQuery(id+"F1.wireOp",EDGE,"E1029"),sQuery(id+"F1.wireOp",EDGE,"E1030"),sQuery(id+"F1.wireOp",EDGE,"E1031"),sQuery(id+"F1.wireOp",EDGE,"E1032"),sQuery(id+"F1.wireOp",EDGE,"E1033"),sQuery(id+"F1.wireOp",EDGE,"E1034"),sQuery(id+"F1.wireOp",EDGE,"E1035"),sQuery(id+"F1.wireOp",EDGE,"E1036"),sQuery(id+"F1.wireOp",EDGE,"E1037"),sQuery(id+"F1.wireOp",EDGE,"E1038"),sQuery(id+"F1.wireOp",EDGE,"E1039"),sQuery(id+"F1.wireOp",EDGE,"E1040"),sQuery(id+"F1.wireOp",EDGE,"E1041"),sQuery(id+"F1.wireOp",EDGE,"E1042"),sQuery(id+"F1.wireOp",EDGE,"E1043"),sQuery(id+"F1.wireOp",EDGE,"E1044"),sQuery(id+"F1.wireOp",EDGE,"E1045"),sQuery(id+"F1.wireOp",EDGE,"E1046"),sQuery(id+"F1.wireOp",EDGE,"E1047"),sQuery(id+"F1.wireOp",EDGE,"E1048"),sQuery(id+"F1.wireOp",EDGE,"E1049"),sQuery(id+"F1.wireOp",EDGE,"E1050"),sQuery(id+"F1.wireOp",EDGE,"E1051"),sQuery(id+"F1.wireOp",EDGE,"E1052"),sQuery(id+"F1.wireOp",EDGE,"E1053"),sQuery(id+"F1.wireOp",EDGE,"E1054"),sQuery(id+"F1.wireOp",EDGE,"E1055"),sQuery(id+"F1.wireOp",EDGE,"E1056"),sQuery(id+"F1.wireOp",EDGE,"E1057"),sQuery(id+"F1.wireOp",EDGE,"E1058"),sQuery(id+"F1.wireOp",EDGE,"E1059"),sQuery(id+"F1.wireOp",EDGE,"E1060"),sQuery(id+"F1.wireOp",EDGE,"E1061"),sQuery(id+"F1.wireOp",EDGE,"E1062"),sQuery(id+"F1.wireOp",EDGE,"E1063"),sQuery(id+"F1.wireOp",EDGE,"E1064"),sQuery(id+"F1.wireOp",EDGE,"E1065"),sQuery(id+"F1.wireOp",EDGE,"E1066"),sQuery(id+"F1.wireOp",EDGE,"E1067"),sQuery(id+"F1.wireOp",EDGE,"E1068"),sQuery(id+"F1.wireOp",EDGE,"E1069"),sQuery(id+"F1.wireOp",EDGE,"E1070"),sQuery(id+"F1.wireOp",EDGE,"E1071"),sQuery(id+"F1.wireOp",EDGE,"E1071"),sQuery(id+"F1.wireOp",EDGE,"E1072"),sQuery(id+"F1.wireOp",EDGE,"E1073"),sQuery(id+"F1.wireOp",EDGE,"E1074"),sQuery(id+"F1.wireOp",EDGE,"E1075"),sQuery(id+"F1.wireOp",EDGE,"E1076"),sQuery(id+"F1.wireOp",EDGE,"E1077"),sQuery(id+"F1.wireOp",EDGE,"E1078"),sQuery(id+"F1.wireOp",EDGE,"E1079"),sQuery(id+"F1.wireOp",EDGE,"E1080"),sQuery(id+"F1.wireOp",EDGE,"E1080"),sQuery(id+"F1.wireOp",EDGE,"E1081"),sQuery(id+"F1.wireOp",EDGE,"E1082"),sQuery(id+"F1.wireOp",EDGE,"E1083"),sQuery(id+"F1.wireOp",EDGE,"E1084"),sQuery(id+"F1.wireOp",EDGE,"E1085"),sQuery(id+"F1.wireOp",EDGE,"E1086"),sQuery(id+"F1.wireOp",EDGE,"E1087"),sQuery(id+"F1.wireOp",EDGE,"E1088"),sQuery(id+"F1.wireOp",EDGE,"E1089"),sQuery(id+"F1.wireOp",EDGE,"E1090"),sQuery(id+"F1.wireOp",EDGE,"E1091"),sQuery(id+"F1.wireOp",EDGE,"E1092"),sQuery(id+"F1.wireOp",EDGE,"E1093"),sQuery(id+"F1.wireOp",EDGE,"E1094"),sQuery(id+"F1.wireOp",EDGE,"E1095"),sQuery(id+"F1.wireOp",EDGE,"E1096"),sQuery(id+"F1.wireOp",EDGE,"E1097"),sQuery(id+"F1.wireOp",EDGE,"E1098"),sQuery(id+"F1.wireOp",EDGE,"E1099"),sQuery(id+"F1.wireOp",EDGE,"E1100"),sQuery(id+"F1.wireOp",EDGE,"E1101"),sQuery(id+"F1.wireOp",EDGE,"E1102"),sQuery(id+"F1.wireOp",EDGE,"E1103"),sQuery(id+"F1.wireOp",EDGE,"E1104"),sQuery(id+"F1.wireOp",EDGE,"E1105"),sQuery(id+"F1.wireOp",EDGE,"E1106"),sQuery(id+"F1.wireOp",EDGE,"E1107"),sQuery(id+"F1.wireOp",EDGE,"E1108"),sQuery(id+"F1.wireOp",EDGE,"E1109"),sQuery(id+"F1.wireOp",EDGE,"E1110"),sQuery(id+"F1.wireOp",EDGE,"E1111"),sQuery(id+"F1.wireOp",EDGE,"E1112"),sQuery(id+"F1.wireOp",EDGE,"E1113"),sQuery(id+"F1.wireOp",EDGE,"E1114"),sQuery(id+"F1.wireOp",EDGE,"E1115"),sQuery(id+"F1.wireOp",EDGE,"E1116"),sQuery(id+"F1.wireOp",EDGE,"E1117"),sQuery(id+"F1.wireOp",EDGE,"E1118"),sQuery(id+"F1.wireOp",EDGE,"E1119"),sQuery(id+"F1.wireOp",EDGE,"E1120"),sQuery(id+"F1.wireOp",EDGE,"E1121"),sQuery(id+"F1.wireOp",EDGE,"E1122"),sQuery(id+"F1.wireOp",EDGE,"E1123"),sQuery(id+"F1.wireOp",EDGE,"E1124"),sQuery(id+"F1.wireOp",EDGE,"E1125"),sQuery(id+"F1.wireOp",EDGE,"E1126"),sQuery(id+"F1.wireOp",EDGE,"E1127"),sQuery(id+"F1.wireOp",EDGE,"E1128"),sQuery(id+"F1.wireOp",EDGE,"E1129"),sQuery(id+"F1.wireOp",EDGE,"E1130"),sQuery(id+"F1.wireOp",EDGE,"E1131"),sQuery(id+"F1.wireOp",EDGE,"E1132"),sQuery(id+"F1.wireOp",EDGE,"E1133"),sQuery(id+"F1.wireOp",EDGE,"E1134"),sQuery(id+"F1.wireOp",EDGE,"E1135"),sQuery(id+"F1.wireOp",EDGE,"E1136"),sQuery(id+"F1.wireOp",EDGE,"E1137"),sQuery(id+"F1.wireOp",EDGE,"E1138"),sQuery(id+"F1.wireOp",EDGE,"E1139"),sQuery(id+"F1.wireOp",EDGE,"E1140"),sQuery(id+"F1.wireOp",EDGE,"E1141"),sQuery(id+"F1.wireOp",EDGE,"E1142"),sQuery(id+"F1.wireOp",EDGE,"E1143"),sQuery(id+"F1.wireOp",EDGE,"E1144"),sQuery(id+"F1.wireOp",EDGE,"E1145"),sQuery(id+"F1.wireOp",EDGE,"E1146"),sQuery(id+"F1.wireOp",EDGE,"E1147"),sQuery(id+"F1.wireOp",EDGE,"E1148"),sQuery(id+"F1.wireOp",EDGE,"E1149"),sQuery(id+"F1.wireOp",EDGE,"E1150"),sQuery(id+"F1.wireOp",EDGE,"E1151"),sQuery(id+"F1.wireOp",EDGE,"E1152"),sQuery(id+"F1.wireOp",EDGE,"E1153"),sQuery(id+"F1.wireOp",EDGE,"E1154"),sQuery(id+"F1.wireOp",EDGE,"E1155"),sQuery(id+"F1.wireOp",EDGE,"E1156"),sQuery(id+"F1.wireOp",EDGE,"E1156"),sQuery(id+"F1.wireOp",EDGE,"E1157"),sQuery(id+"F1.wireOp",EDGE,"E1158"),sQuery(id+"F1.wireOp",EDGE,"E1159"),sQuery(id+"F1.wireOp",EDGE,"E1160"),sQuery(id+"F1.wireOp",EDGE,"E1161"),sQuery(id+"F1.wireOp",EDGE,"E1162"),sQuery(id+"F1.wireOp",EDGE,"E1163"),sQuery(id+"F1.wireOp",EDGE,"E1164"),sQuery(id+"F1.wireOp",EDGE,"E1165"),sQuery(id+"F1.wireOp",EDGE,"E1166"),sQuery(id+"F1.wireOp",EDGE,"E1167"),sQuery(id+"F1.wireOp",EDGE,"E1168"),sQuery(id+"F1.wireOp",EDGE,"E1169"),sQuery(id+"F1.wireOp",EDGE,"E1170"),sQuery(id+"F1.wireOp",EDGE,"E1171"),sQuery(id+"F1.wireOp",EDGE,"E1172"),sQuery(id+"F1.wireOp",EDGE,"E1173"),sQuery(id+"F1.wireOp",EDGE,"E1174"),sQuery(id+"F1.wireOp",EDGE,"E1175"),sQuery(id+"F1.wireOp",EDGE,"E1176"),sQuery(id+"F1.wireOp",EDGE,"E1177"),sQuery(id+"F1.wireOp",EDGE,"E1178"),sQuery(id+"F1.wireOp",EDGE,"E1179"),sQuery(id+"F1.wireOp",EDGE,"E1180"),sQuery(id+"F1.wireOp",EDGE,"E1181"),sQuery(id+"F1.wireOp",EDGE,"E1182"),sQuery(id+"F1.wireOp",EDGE,"E1183"),sQuery(id+"F1.wireOp",EDGE,"E1184"),sQuery(id+"F1.wireOp",EDGE,"E1185"),sQuery(id+"F1.wireOp",EDGE,"E1186"),sQuery(id+"F1.wireOp",EDGE,"E1187"),sQuery(id+"F1.wireOp",EDGE,"E1188"),sQuery(id+"F1.wireOp",EDGE,"E1189"),sQuery(id+"F1.wireOp",EDGE,"E1190"),sQuery(id+"F1.wireOp",EDGE,"E1191"),sQuery(id+"F1.wireOp",EDGE,"E1192"),sQuery(id+"F1.wireOp",EDGE,"E1193"),sQuery(id+"F1.wireOp",EDGE,"E1194"),sQuery(id+"F1.wireOp",EDGE,"E1195"),sQuery(id+"F1.wireOp",EDGE,"E1196"),sQuery(id+"F1.wireOp",EDGE,"E1197"),sQuery(id+"F1.wireOp",EDGE,"E1198"),sQuery(id+"F1.wireOp",EDGE,"E1199"),sQuery(id+"F1.wireOp",EDGE,"E1200"),sQuery(id+"F1.wireOp",EDGE,"E1201"),sQuery(id+"F1.wireOp",EDGE,"E1202"),sQuery(id+"F1.wireOp",EDGE,"E1203"),sQuery(id+"F1.wireOp",EDGE,"E1204"),sQuery(id+"F1.wireOp",EDGE,"E1205"),sQuery(id+"F1.wireOp",EDGE,"E1206"),sQuery(id+"F1.wireOp",EDGE,"E1207"),sQuery(id+"F1.wireOp",EDGE,"E1208"),sQuery(id+"F1.wireOp",EDGE,"E1209"),sQuery(id+"F1.wireOp",EDGE,"E1210"),sQuery(id+"F1.wireOp",EDGE,"E1211"),sQuery(id+"F1.wireOp",EDGE,"E1212"),sQuery(id+"F1.wireOp",EDGE,"E1213"),sQuery(id+"F1.wireOp",EDGE,"E1214"),sQuery(id+"F1.wireOp",EDGE,"E1215"),sQuery(id+"F1.wireOp",EDGE,"E1216"),sQuery(id+"F1.wireOp",EDGE,"E1217"),sQuery(id+"F1.wireOp",EDGE,"E1218"),sQuery(id+"F1.wireOp",EDGE,"E1219"),sQuery(id+"F1.wireOp",EDGE,"E1220"),sQuery(id+"F1.wireOp",EDGE,"E1221"),sQuery(id+"F1.wireOp",EDGE,"E1222"),sQuery(id+"F1.wireOp",EDGE,"E1223"),sQuery(id+"F1.wireOp",EDGE,"E1224"),sQuery(id+"F1.wireOp",EDGE,"E1225"),sQuery(id+"F1.wireOp",EDGE,"E1226"),sQuery(id+"F1.wireOp",EDGE,"E1227"),sQuery(id+"F1.wireOp",EDGE,"E1228"),sQuery(id+"F1.wireOp",EDGE,"E1229"),sQuery(id+"F1.wireOp",EDGE,"E1230"),sQuery(id+"F1.wireOp",EDGE,"E1231"),sQuery(id+"F1.wireOp",EDGE,"E1232"),sQuery(id+"F1.wireOp",EDGE,"E1233"),sQuery(id+"F1.wireOp",EDGE,"E1234"),sQuery(id+"F1.wireOp",EDGE,"E1235"),sQuery(id+"F1.wireOp",EDGE,"E1236"),sQuery(id+"F1.wireOp",EDGE,"E1237"),sQuery(id+"F1.wireOp",EDGE,"E1238"),sQuery(id+"F1.wireOp",EDGE,"E1239"),sQuery(id+"F1.wireOp",EDGE,"E1240"),sQuery(id+"F1.wireOp",EDGE,"E1241"),sQuery(id+"F1.wireOp",EDGE,"E1242"),sQuery(id+"F1.wireOp",EDGE,"E1243"),sQuery(id+"F1.wireOp",EDGE,"E1244"),sQuery(id+"F1.wireOp",EDGE,"E1245"),sQuery(id+"F1.wireOp",EDGE,"E1246"),sQuery(id+"F1.wireOp",EDGE,"E1247"),sQuery(id+"F1.wireOp",EDGE,"E1248"),sQuery(id+"F1.wireOp",EDGE,"E1249"),sQuery(id+"F1.wireOp",EDGE,"E1250"),sQuery(id+"F1.wireOp",EDGE,"E1251"),sQuery(id+"F1.wireOp",EDGE,"E1252"),sQuery(id+"F1.wireOp",EDGE,"E1253"),sQuery(id+"F1.wireOp",EDGE,"E1254"),sQuery(id+"F1.wireOp",EDGE,"E1255"),sQuery(id+"F1.wireOp",EDGE,"E1256"),sQuery(id+"F1.wireOp",EDGE,"E1257"),sQuery(id+"F1.wireOp",EDGE,"E1258"),sQuery(id+"F1.wireOp",EDGE,"E1259"),sQuery(id+"F1.wireOp",EDGE,"E1260"),sQuery(id+"F1.wireOp",EDGE,"E1261"),sQuery(id+"F1.wireOp",EDGE,"E1262"),sQuery(id+"F1.wireOp",EDGE,"E1263"),sQuery(id+"F1.wireOp",EDGE,"E1264"),sQuery(id+"F1.wireOp",EDGE,"E1265"),sQuery(id+"F1.wireOp",EDGE,"E1266"),sQuery(id+"F1.wireOp",EDGE,"E1267"),sQuery(id+"F1.wireOp",EDGE,"E1268"),sQuery(id+"F1.wireOp",EDGE,"E1269"),sQuery(id+"F1.wireOp",EDGE,"E1270"),sQuery(id+"F1.wireOp",EDGE,"E1271"),sQuery(id+"F1.wireOp",EDGE,"E1272"),sQuery(id+"F1.wireOp",EDGE,"E1273"),sQuery(id+"F1.wireOp",EDGE,"E1274"),sQuery(id+"F1.wireOp",EDGE,"E1275"),sQuery(id+"F1.wireOp",EDGE,"E1276"),sQuery(id+"F1.wireOp",EDGE,"E1277"),sQuery(id+"F1.wireOp",EDGE,"E1278"),sQuery(id+"F1.wireOp",EDGE,"E1279"),sQuery(id+"F1.wireOp",EDGE,"E1280"),sQuery(id+"F1.wireOp",EDGE,"E1281"),sQuery(id+"F1.wireOp",EDGE,"E1282"),sQuery(id+"F1.wireOp",EDGE,"E1283"),sQuery(id+"F1.wireOp",EDGE,"E1284"),sQuery(id+"F1.wireOp",EDGE,"E1285"),sQuery(id+"F1.wireOp",EDGE,"E1286"),sQuery(id+"F1.wireOp",EDGE,"E1287"),sQuery(id+"F1.wireOp",EDGE,"E1288"),sQuery(id+"F1.wireOp",EDGE,"E1289"),sQuery(id+"F1.wireOp",EDGE,"E1290"),sQuery(id+"F1.wireOp",EDGE,"E1291"),sQuery(id+"F1.wireOp",EDGE,"E1292"),sQuery(id+"F1.wireOp",EDGE,"E1293"),sQuery(id+"F1.wireOp",EDGE,"E1294"),sQuery(id+"F1.wireOp",EDGE,"E1295"),sQuery(id+"F1.wireOp",EDGE,"E1296"),sQuery(id+"F1.wireOp",EDGE,"E1297"),sQuery(id+"F1.wireOp",EDGE,"E1298"),sQuery(id+"F1.wireOp",EDGE,"E1299"),sQuery(id+"F1.wireOp",EDGE,"E1300"),sQuery(id+"F1.wireOp",EDGE,"E1301"),sQuery(id+"F1.wireOp",EDGE,"E1302"),sQuery(id+"F1.wireOp",EDGE,"E1303"),sQuery(id+"F1.wireOp",EDGE,"E1304"),sQuery(id+"F1.wireOp",EDGE,"E1305"),sQuery(id+"F1.wireOp",EDGE,"E1306"),sQuery(id+"F1.wireOp",EDGE,"E1307"),sQuery(id+"F1.wireOp",EDGE,"E1308"),sQuery(id+"F1.wireOp",EDGE,"E1309"),sQuery(id+"F1.wireOp",EDGE,"E1310"),sQuery(id+"F1.wireOp",EDGE,"E1311"),sQuery(id+"F1.wireOp",EDGE,"E1312"),sQuery(id+"F1.wireOp",EDGE,"E1312"),sQuery(id+"F1.wireOp",EDGE,"E1313"),sQuery(id+"F1.wireOp",EDGE,"E1314"),sQuery(id+"F1.wireOp",EDGE,"E1315"),sQuery(id+"F1.wireOp",EDGE,"E1316"),sQuery(id+"F1.wireOp",EDGE,"E1317"),sQuery(id+"F1.wireOp",EDGE,"E1318"),sQuery(id+"F1.wireOp",EDGE,"E1319"),sQuery(id+"F1.wireOp",EDGE,"E1320"),sQuery(id+"F1.wireOp",EDGE,"E1321"),sQuery(id+"F1.wireOp",EDGE,"E1322"),sQuery(id+"F1.wireOp",EDGE,"E1323"),sQuery(id+"F1.wireOp",EDGE,"E1324"),sQuery(id+"F1.wireOp",EDGE,"E1325"),sQuery(id+"F1.wireOp",EDGE,"E1326"),sQuery(id+"F1.wireOp",EDGE,"E1327"),sQuery(id+"F1.wireOp",EDGE,"E1328"),sQuery(id+"F1.wireOp",EDGE,"E1329"),sQuery(id+"F1.wireOp",EDGE,"E1330"),sQuery(id+"F1.wireOp",EDGE,"E1331"),sQuery(id+"F1.wireOp",EDGE,"E1332"),sQuery(id+"F1.wireOp",EDGE,"E1333"),sQuery(id+"F1.wireOp",EDGE,"E1334"),sQuery(id+"F1.wireOp",EDGE,"E1335"),sQuery(id+"F1.wireOp",EDGE,"E1336"),sQuery(id+"F1.wireOp",EDGE,"E1337"),sQuery(id+"F1.wireOp",EDGE,"E1338"),sQuery(id+"F1.wireOp",EDGE,"E1339"),sQuery(id+"F1.wireOp",EDGE,"E1340"),sQuery(id+"F1.wireOp",EDGE,"E1341"),sQuery(id+"F1.wireOp",EDGE,"E1342"),sQuery(id+"F1.wireOp",EDGE,"E1343"),sQuery(id+"F1.wireOp",EDGE,"E1344"),sQuery(id+"F1.wireOp",EDGE,"E1345"),sQuery(id+"F1.wireOp",EDGE,"E1346"),sQuery(id+"F1.wireOp",EDGE,"E1347"),sQuery(id+"F1.wireOp",EDGE,"E1348"),sQuery(id+"F1.wireOp",EDGE,"E1349"),sQuery(id+"F1.wireOp",EDGE,"E1350"),sQuery(id+"F1.wireOp",EDGE,"E1351"),sQuery(id+"F1.wireOp",EDGE,"E1352"),sQuery(id+"F1.wireOp",EDGE,"E1353"),sQuery(id+"F1.wireOp",EDGE,"E1354"),sQuery(id+"F1.wireOp",EDGE,"E1355"),sQuery(id+"F1.wireOp",EDGE,"E1356"),sQuery(id+"F1.wireOp",EDGE,"E1357"),sQuery(id+"F1.wireOp",EDGE,"E1358"),sQuery(id+"F1.wireOp",EDGE,"E1359"),sQuery(id+"F1.wireOp",EDGE,"E1360"),sQuery(id+"F1.wireOp",EDGE,"E1361"),sQuery(id+"F1.wireOp",EDGE,"E1362"),sQuery(id+"F1.wireOp",EDGE,"E1363"),sQuery(id+"F1.wireOp",EDGE,"E1364"),sQuery(id+"F1.wireOp",EDGE,"E1365"),sQuery(id+"F1.wireOp",EDGE,"E1366"),sQuery(id+"F1.wireOp",EDGE,"E1367"),sQuery(id+"F1.wireOp",EDGE,"E1368"),sQuery(id+"F1.wireOp",EDGE,"E1369"),sQuery(id+"F1.wireOp",EDGE,"E1370"),sQuery(id+"F1.wireOp",EDGE,"E1371"),sQuery(id+"F1.wireOp",EDGE,"E1372"),sQuery(id+"F1.wireOp",EDGE,"E1373"),sQuery(id+"F1.wireOp",EDGE,"E1374"),sQuery(id+"F1.wireOp",EDGE,"E1375"),sQuery(id+"F1.wireOp",EDGE,"E1376"),sQuery(id+"F1.wireOp",EDGE,"E1376"),sQuery(id+"F1.wireOp",EDGE,"E1377"),sQuery(id+"F1.wireOp",EDGE,"E1378"),sQuery(id+"F1.wireOp",EDGE,"E1379"),sQuery(id+"F1.wireOp",EDGE,"E1380"),sQuery(id+"F1.wireOp",EDGE,"E1381"),sQuery(id+"F1.wireOp",EDGE,"E1382"),sQuery(id+"F1.wireOp",EDGE,"E1383"),sQuery(id+"F1.wireOp",EDGE,"E1384"),sQuery(id+"F1.wireOp",EDGE,"E1385"),sQuery(id+"F1.wireOp",EDGE,"E1386"),sQuery(id+"F1.wireOp",EDGE,"E1387"),sQuery(id+"F1.wireOp",EDGE,"E1388"),sQuery(id+"F1.wireOp",EDGE,"E1389"),sQuery(id+"F1.wireOp",EDGE,"E1390"),sQuery(id+"F1.wireOp",EDGE,"E1391"),sQuery(id+"F1.wireOp",EDGE,"E1392"),sQuery(id+"F1.wireOp",EDGE,"E1393"),sQuery(id+"F1.wireOp",EDGE,"E1394"),sQuery(id+"F1.wireOp",EDGE,"E1395"),sQuery(id+"F1.wireOp",EDGE,"E1396"),sQuery(id+"F1.wireOp",EDGE,"E1397"),sQuery(id+"F1.wireOp",EDGE,"E1398"),sQuery(id+"F1.wireOp",EDGE,"E1399"),sQuery(id+"F1.wireOp",EDGE,"E1400"),sQuery(id+"F1.wireOp",EDGE,"E1401"),sQuery(id+"F1.wireOp",EDGE,"E1402"),sQuery(id+"F1.wireOp",EDGE,"E1403"),sQuery(id+"F1.wireOp",EDGE,"E1404"),sQuery(id+"F1.wireOp",EDGE,"E1405"),sQuery(id+"F1.wireOp",EDGE,"E1406"),sQuery(id+"F1.wireOp",EDGE,"E1407"),sQuery(id+"F1.wireOp",EDGE,"E1408"),sQuery(id+"F1.wireOp",EDGE,"E1409"),sQuery(id+"F1.wireOp",EDGE,"E1410"),sQuery(id+"F1.wireOp",EDGE,"E1411"),sQuery(id+"F1.wireOp",EDGE,"E1412"),sQuery(id+"F1.wireOp",EDGE,"E1413"),sQuery(id+"F1.wireOp",EDGE,"E1414"),sQuery(id+"F1.wireOp",EDGE,"E1415"),sQuery(id+"F1.wireOp",EDGE,"E1416"),sQuery(id+"F1.wireOp",EDGE,"E1417"),sQuery(id+"F1.wireOp",EDGE,"E1418"),sQuery(id+"F1.wireOp",EDGE,"E1419"),sQuery(id+"F1.wireOp",EDGE,"E1420"),sQuery(id+"F1.wireOp",EDGE,"E1421"),sQuery(id+"F1.wireOp",EDGE,"E1422"),sQuery(id+"F1.wireOp",EDGE,"E1423"),sQuery(id+"F1.wireOp",EDGE,"E1424"),sQuery(id+"F1.wireOp",EDGE,"E1425"),sQuery(id+"F1.wireOp",EDGE,"E1426"),sQuery(id+"F1.wireOp",EDGE,"E1427"),sQuery(id+"F1.wireOp",EDGE,"E1428"),sQuery(id+"F1.wireOp",EDGE,"E1429"),sQuery(id+"F1.wireOp",EDGE,"E1430"),sQuery(id+"F1.wireOp",EDGE,"E1431"),sQuery(id+"F1.wireOp",EDGE,"E1432"),sQuery(id+"F1.wireOp",EDGE,"E1433"),sQuery(id+"F1.wireOp",EDGE,"E1434"),sQuery(id+"F1.wireOp",EDGE,"E1435"),sQuery(id+"F1.wireOp",EDGE,"E1436"),sQuery(id+"F1.wireOp",EDGE,"E1437"),sQuery(id+"F1.wireOp",EDGE,"E1438"),sQuery(id+"F1.wireOp",EDGE,"E1439"),sQuery(id+"F1.wireOp",EDGE,"E1440"),sQuery(id+"F1.wireOp",EDGE,"E1441"),sQuery(id+"F1.wireOp",EDGE,"E1442"),sQuery(id+"F1.wireOp",EDGE,"E1443"),sQuery(id+"F1.wireOp",EDGE,"E1444"),sQuery(id+"F1.wireOp",EDGE,"E1445"),sQuery(id+"F1.wireOp",EDGE,"E1446"),sQuery(id+"F1.wireOp",EDGE,"E1447"),sQuery(id+"F1.wireOp",EDGE,"E1448"),sQuery(id+"F1.wireOp",EDGE,"E1449"),sQuery(id+"F1.wireOp",EDGE,"E1450"),sQuery(id+"F1.wireOp",EDGE,"E1451"),sQuery(id+"F1.wireOp",EDGE,"E1452"),sQuery(id+"F1.wireOp",EDGE,"E1453"),sQuery(id+"F1.wireOp",EDGE,"E1454"),sQuery(id+"F1.wireOp",EDGE,"E1455"),sQuery(id+"F1.wireOp",EDGE,"E1456"),sQuery(id+"F1.wireOp",EDGE,"E1457"),sQuery(id+"F1.wireOp",EDGE,"E1458"),sQuery(id+"F1.wireOp",EDGE,"E1459"),sQuery(id+"F1.wireOp",EDGE,"E1460"),sQuery(id+"F1.wireOp",EDGE,"E1461"),sQuery(id+"F1.wireOp",EDGE,"E1462"),sQuery(id+"F1.wireOp",EDGE,"E1463"),sQuery(id+"F1.wireOp",EDGE,"E1464"),sQuery(id+"F1.wireOp",EDGE,"E1465"),sQuery(id+"F1.wireOp",EDGE,"E1466"),sQuery(id+"F1.wireOp",EDGE,"E1467"),sQuery(id+"F1.wireOp",EDGE,"E1468"),sQuery(id+"F1.wireOp",EDGE,"E1469"),sQuery(id+"F1.wireOp",EDGE,"E1470"),sQuery(id+"F1.wireOp",EDGE,"E1471"),sQuery(id+"F1.wireOp",EDGE,"E1472"),sQuery(id+"F1.wireOp",EDGE,"E1473"),sQuery(id+"F1.wireOp",EDGE,"E1474"),sQuery(id+"F1.wireOp",EDGE,"E1475"),sQuery(id+"F1.wireOp",EDGE,"E1476"),sQuery(id+"F1.wireOp",EDGE,"E1477"),sQuery(id+"F1.wireOp",EDGE,"E1478"),sQuery(id+"F1.wireOp",EDGE,"E1479"),sQuery(id+"F1.wireOp",EDGE,"E1480"),sQuery(id+"F1.wireOp",EDGE,"E1481"),sQuery(id+"F1.wireOp",EDGE,"E1482"),sQuery(id+"F1.wireOp",EDGE,"E1483"),sQuery(id+"F1.wireOp",EDGE,"E1484"),sQuery(id+"F1.wireOp",EDGE,"E1485"),sQuery(id+"F1.wireOp",EDGE,"E1486"),sQuery(id+"F1.wireOp",EDGE,"E1487"),sQuery(id+"F1.wireOp",EDGE,"E1488"),sQuery(id+"F1.wireOp",EDGE,"E1489"),sQuery(id+"F1.wireOp",EDGE,"E1490"),sQuery(id+"F1.wireOp",EDGE,"E1491"),sQuery(id+"F1.wireOp",EDGE,"E1492"),sQuery(id+"F1.wireOp",EDGE,"E1493"),sQuery(id+"F1.wireOp",EDGE,"E1494"),sQuery(id+"F1.wireOp",EDGE,"E1495"),sQuery(id+"F1.wireOp",EDGE,"E1496"),sQuery(id+"F1.wireOp",EDGE,"E1497"),sQuery(id+"F1.wireOp",EDGE,"E1498"),sQuery(id+"F1.wireOp",EDGE,"E1499"),sQuery(id+"F1.wireOp",EDGE,"E1500"),sQuery(id+"F1.wireOp",EDGE,"E1501"),sQuery(id+"F1.wireOp",EDGE,"E1502"),sQuery(id+"F1.wireOp",EDGE,"E1503"),sQuery(id+"F1.wireOp",EDGE,"E1504"),sQuery(id+"F1.wireOp",EDGE,"E1505"),sQuery(id+"F1.wireOp",EDGE,"E1506"),sQuery(id+"F1.wireOp",EDGE,"E1507"),sQuery(id+"F1.wireOp",EDGE,"E1508"),sQuery(id+"F1.wireOp",EDGE,"E1509"),sQuery(id+"F1.wireOp",EDGE,"E1510"),sQuery(id+"F1.wireOp",EDGE,"E1511"),sQuery(id+"F1.wireOp",EDGE,"E1512"),sQuery(id+"F1.wireOp",EDGE,"E1513"),sQuery(id+"F1.wireOp",EDGE,"E1514"),sQuery(id+"F1.wireOp",EDGE,"E1515"),sQuery(id+"F1.wireOp",EDGE,"E1516"),sQuery(id+"F1.wireOp",EDGE,"E1517"),sQuery(id+"F1.wireOp",EDGE,"E1518"),sQuery(id+"F1.wireOp",EDGE,"E1519"),sQuery(id+"F1.wireOp",EDGE,"E1520"),sQuery(id+"F1.wireOp",EDGE,"E1521"),sQuery(id+"F1.wireOp",EDGE,"E1522"),sQuery(id+"F1.wireOp",EDGE,"E1523"),sQuery(id+"F1.wireOp",EDGE,"E1524"),sQuery(id+"F1.wireOp",EDGE,"E1525"),sQuery(id+"F1.wireOp",EDGE,"E1526"),sQuery(id+"F1.wireOp",EDGE,"E1527"),sQuery(id+"F1.wireOp",EDGE,"E1528"),sQuery(id+"F1.wireOp",EDGE,"E1529"),sQuery(id+"F1.wireOp",EDGE,"E1530"),sQuery(id+"F1.wireOp",EDGE,"E1531"),sQuery(id+"F1.wireOp",EDGE,"E1532"),sQuery(id+"F1.wireOp",EDGE,"E1533"),sQuery(id+"F1.wireOp",EDGE,"E1534"),sQuery(id+"F1.wireOp",EDGE,"E1535"),sQuery(id+"F1.wireOp",EDGE,"E1536"),sQuery(id+"F1.wireOp",EDGE,"E1537"),sQuery(id+"F1.wireOp",EDGE,"E1538"),sQuery(id+"F1.wireOp",EDGE,"E1539"),sQuery(id+"F1.wireOp",EDGE,"E1540"),sQuery(id+"F1.wireOp",EDGE,"E1541"),sQuery(id+"F1.wireOp",EDGE,"E1542"),sQuery(id+"F1.wireOp",EDGE,"E1543"),sQuery(id+"F1.wireOp",EDGE,"E1544"),sQuery(id+"F1.wireOp",EDGE,"E1545"),sQuery(id+"F1.wireOp",EDGE,"E1546"),sQuery(id+"F1.wireOp",EDGE,"E1547"),sQuery(id+"F1.wireOp",EDGE,"E1548"),sQuery(id+"F1.wireOp",EDGE,"E1549"),sQuery(id+"F1.wireOp",EDGE,"E1550"),sQuery(id+"F1.wireOp",EDGE,"E1551"),sQuery(id+"F1.wireOp",EDGE,"E1552"),sQuery(id+"F1.wireOp",EDGE,"E1553"),sQuery(id+"F1.wireOp",EDGE,"E1554"),sQuery(id+"F1.wireOp",EDGE,"E1555"),sQuery(id+"F1.wireOp",EDGE,"E1556"),sQuery(id+"F1.wireOp",EDGE,"E1557"),sQuery(id+"F1.wireOp",EDGE,"E1558"),sQuery(id+"F1.wireOp",EDGE,"E1559"),sQuery(id+"F1.wireOp",EDGE,"E1560"),sQuery(id+"F1.wireOp",EDGE,"E1561"),sQuery(id+"F1.wireOp",EDGE,"E1562"),sQuery(id+"F1.wireOp",EDGE,"E1563"),sQuery(id+"F1.wireOp",EDGE,"E1564"),sQuery(id+"F1.wireOp",EDGE,"E1565"),sQuery(id+"F1.wireOp",EDGE,"E1566"),sQuery(id+"F1.wireOp",EDGE,"E1567"),sQuery(id+"F1.wireOp",EDGE,"E1568"),sQuery(id+"F1.wireOp",EDGE,"E1569"),sQuery(id+"F1.wireOp",EDGE,"E1570"),sQuery(id+"F1.wireOp",EDGE,"E1571"),sQuery(id+"F1.wireOp",EDGE,"E1572"),sQuery(id+"F1.wireOp",EDGE,"E1573"),sQuery(id+"F1.wireOp",EDGE,"E1574"),sQuery(id+"F1.wireOp",EDGE,"E1575"),sQuery(id+"F1.wireOp",EDGE,"E1576"),sQuery(id+"F1.wireOp",EDGE,"E1577"),sQuery(id+"F1.wireOp",EDGE,"E1578"),sQuery(id+"F1.wireOp",EDGE,"E1579"),sQuery(id+"F1.wireOp",EDGE,"E1580"),sQuery(id+"F1.wireOp",EDGE,"E1581"),sQuery(id+"F1.wireOp",EDGE,"E1582"),sQuery(id+"F1.wireOp",EDGE,"E1583"),sQuery(id+"F1.wireOp",EDGE,"E1584"),sQuery(id+"F1.wireOp",EDGE,"E1585"),sQuery(id+"F1.wireOp",EDGE,"E1586"),sQuery(id+"F1.wireOp",EDGE,"E1587"),sQuery(id+"F1.wireOp",EDGE,"E1588"),sQuery(id+"F1.wireOp",EDGE,"E1589"),sQuery(id+"F1.wireOp",EDGE,"E1590"),sQuery(id+"F1.wireOp",EDGE,"E1591"),sQuery(id+"F1.wireOp",EDGE,"E1592"),sQuery(id+"F1.wireOp",EDGE,"E1593"),sQuery(id+"F1.wireOp",EDGE,"E1594"),sQuery(id+"F1.wireOp",EDGE,"E1595"),sQuery(id+"F1.wireOp",EDGE,"E1596"),sQuery(id+"F1.wireOp",EDGE,"E1597"),sQuery(id+"F1.wireOp",EDGE,"E1598"),sQuery(id+"F1.wireOp",EDGE,"E1599"),sQuery(id+"F1.wireOp",EDGE,"E1600"),sQuery(id+"F1.wireOp",EDGE,"E1601"),sQuery(id+"F1.wireOp",EDGE,"E1602"),sQuery(id+"F1.wireOp",EDGE,"E1603"),sQuery(id+"F1.wireOp",EDGE,"E1604"),sQuery(id+"F1.wireOp",EDGE,"E1605"),sQuery(id+"F1.wireOp",EDGE,"E1606"),sQuery(id+"F1.wireOp",EDGE,"E1607"),sQuery(id+"F1.wireOp",EDGE,"E1608"),sQuery(id+"F1.wireOp",EDGE,"E1609"),sQuery(id+"F1.wireOp",EDGE,"E1610"),sQuery(id+"F1.wireOp",EDGE,"E1611"),sQuery(id+"F1.wireOp",EDGE,"E1612"),sQuery(id+"F1.wireOp",EDGE,"E1613"),sQuery(id+"F1.wireOp",EDGE,"E1614"),sQuery(id+"F1.wireOp",EDGE,"E1615"),sQuery(id+"F1.wireOp",EDGE,"E1616"),sQuery(id+"F1.wireOp",EDGE,"E1617"),sQuery(id+"F1.wireOp",EDGE,"E1618"),sQuery(id+"F1.wireOp",EDGE,"E1619"),sQuery(id+"F1.wireOp",EDGE,"E1620"),sQuery(id+"F1.wireOp",EDGE,"E1621"),sQuery(id+"F1.wireOp",EDGE,"E1622"),sQuery(id+"F1.wireOp",EDGE,"E1623"),sQuery(id+"F1.wireOp",EDGE,"E1624"),sQuery(id+"F1.wireOp",EDGE,"E1625"),sQuery(id+"F1.wireOp",EDGE,"E1626"),sQuery(id+"F1.wireOp",EDGE,"E1627"),sQuery(id+"F1.wireOp",EDGE,"E1628"),sQuery(id+"F1.wireOp",EDGE,"E1629"),sQuery(id+"F1.wireOp",EDGE,"E1630"),sQuery(id+"F1.wireOp",EDGE,"E1631"),sQuery(id+"F1.wireOp",EDGE,"E1632"),sQuery(id+"F1.wireOp",EDGE,"E1633"),sQuery(id+"F1.wireOp",EDGE,"E1634"),sQuery(id+"F1.wireOp",EDGE,"E1635"),sQuery(id+"F1.wireOp",EDGE,"E1636"),sQuery(id+"F1.wireOp",EDGE,"E1637"),sQuery(id+"F1.wireOp",EDGE,"E1638"),sQuery(id+"F1.wireOp",EDGE,"E1639"),sQuery(id+"F1.wireOp",EDGE,"E1640"),sQuery(id+"F1.wireOp",EDGE,"E1641"),sQuery(id+"F1.wireOp",EDGE,"E1642"),sQuery(id+"F1.wireOp",EDGE,"E1643"),sQuery(id+"F1.wireOp",EDGE,"E1644"),sQuery(id+"F1.wireOp",EDGE,"E1645"),sQuery(id+"F1.wireOp",EDGE,"E1646"),sQuery(id+"F1.wireOp",EDGE,"E1647"),sQuery(id+"F1.wireOp",EDGE,"E1648"),sQuery(id+"F1.wireOp",EDGE,"E1649"),sQuery(id+"F1.wireOp",EDGE,"E1650"),sQuery(id+"F1.wireOp",EDGE,"E1651"),sQuery(id+"F1.wireOp",EDGE,"E1652"),sQuery(id+"F1.wireOp",EDGE,"E1653"),sQuery(id+"F1.wireOp",EDGE,"E1654"),sQuery(id+"F1.wireOp",EDGE,"E1655"),sQuery(id+"F1.wireOp",EDGE,"E1656"),sQuery(id+"F1.wireOp",EDGE,"E1657"),sQuery(id+"F1.wireOp",EDGE,"E1658"),sQuery(id+"F1.wireOp",EDGE,"E1659"),sQuery(id+"F1.wireOp",EDGE,"E1660"),sQuery(id+"F1.wireOp",EDGE,"E1661"),sQuery(id+"F1.wireOp",EDGE,"E1662"),sQuery(id+"F1.wireOp",EDGE,"E1663"),sQuery(id+"F1.wireOp",EDGE,"E1664"),sQuery(id+"F1.wireOp",EDGE,"E1665"),sQuery(id+"F1.wireOp",EDGE,"E1666"),sQuery(id+"F1.wireOp",EDGE,"E1667"),sQuery(id+"F1.wireOp",EDGE,"E1668"),sQuery(id+"F1.wireOp",EDGE,"E1669"),sQuery(id+"F1.wireOp",EDGE,"E1670"),sQuery(id+"F1.wireOp",EDGE,"E1671"),sQuery(id+"F1.wireOp",EDGE,"E1672"),sQuery(id+"F1.wireOp",EDGE,"E1673"),sQuery(id+"F1.wireOp",EDGE,"E1674"),sQuery(id+"F1.wireOp",EDGE,"E1675"),sQuery(id+"F1.wireOp",EDGE,"E1676"),sQuery(id+"F1.wireOp",EDGE,"E1677"),sQuery(id+"F1.wireOp",EDGE,"E1678"),sQuery(id+"F1.wireOp",EDGE,"E1679"),sQuery(id+"F1.wireOp",EDGE,"E1680"),sQuery(id+"F1.wireOp",EDGE,"E1681"),sQuery(id+"F1.wireOp",EDGE,"E1682"),sQuery(id+"F1.wireOp",EDGE,"E1683"),sQuery(id+"F1.wireOp",EDGE,"E1684"),sQuery(id+"F1.wireOp",EDGE,"E1685"),sQuery(id+"F1.wireOp",EDGE,"E1686"),sQuery(id+"F1.wireOp",EDGE,"E1687"),sQuery(id+"F1.wireOp",EDGE,"E1688"),sQuery(id+"F1.wireOp",EDGE,"E1689"),sQuery(id+"F1.wireOp",EDGE,"E1690"),sQuery(id+"F1.wireOp",EDGE,"E1691"),sQuery(id+"F1.wireOp",EDGE,"E1692"),sQuery(id+"F1.wireOp",EDGE,"E1693"),sQuery(id+"F1.wireOp",EDGE,"E1694"),sQuery(id+"F1.wireOp",EDGE,"E1695"),sQuery(id+"F1.wireOp",EDGE,"E1696"),sQuery(id+"F1.wireOp",EDGE,"E1697"),sQuery(id+"F1.wireOp",EDGE,"E1698"),sQuery(id+"F1.wireOp",EDGE,"E1699"),sQuery(id+"F1.wireOp",EDGE,"E1700"),sQuery(id+"F1.wireOp",EDGE,"E1701"),sQuery(id+"F1.wireOp",EDGE,"E1702"),sQuery(id+"F1.wireOp",EDGE,"E1703"),sQuery(id+"F1.wireOp",EDGE,"E1704"),sQuery(id+"F1.wireOp",EDGE,"E1705"),sQuery(id+"F1.wireOp",EDGE,"E1706"),sQuery(id+"F1.wireOp",EDGE,"E1707"),sQuery(id+"F1.wireOp",EDGE,"E1708"),sQuery(id+"F1.wireOp",EDGE,"E1709"),sQuery(id+"F1.wireOp",EDGE,"E1710"),sQuery(id+"F1.wireOp",EDGE,"E1711"),sQuery(id+"F1.wireOp",EDGE,"E1712"),sQuery(id+"F1.wireOp",EDGE,"E1713"),sQuery(id+"F1.wireOp",EDGE,"E1714"),sQuery(id+"F1.wireOp",EDGE,"E1715"),sQuery(id+"F1.wireOp",EDGE,"E1716"),sQuery(id+"F1.wireOp",EDGE,"E1717"),sQuery(id+"F1.wireOp",EDGE,"E1718"),sQuery(id+"F1.wireOp",EDGE,"E1719"),sQuery(id+"F1.wireOp",EDGE,"E1720"),sQuery(id+"F1.wireOp",EDGE,"E1721"),sQuery(id+"F1.wireOp",EDGE,"E1722"),sQuery(id+"F1.wireOp",EDGE,"E1723"),sQuery(id+"F1.wireOp",EDGE,"E1724"),sQuery(id+"F1.wireOp",EDGE,"E1725"),sQuery(id+"F1.wireOp",EDGE,"E1726"),sQuery(id+"F1.wireOp",EDGE,"E1727"),sQuery(id+"F1.wireOp",EDGE,"E1728"),sQuery(id+"F1.wireOp",EDGE,"E1729"),sQuery(id+"F1.wireOp",EDGE,"E1730"),sQuery(id+"F1.wireOp",EDGE,"E1731"),sQuery(id+"F1.wireOp",EDGE,"E1732"),sQuery(id+"F1.wireOp",EDGE,"E1733"),sQuery(id+"F1.wireOp",EDGE,"E1734"),sQuery(id+"F1.wireOp",EDGE,"E1735"),sQuery(id+"F1.wireOp",EDGE,"E1736"),sQuery(id+"F1.wireOp",EDGE,"E1737"),sQuery(id+"F1.wireOp",EDGE,"E1738"),sQuery(id+"F1.wireOp",EDGE,"E1739"),sQuery(id+"F1.wireOp",EDGE,"E1740"),sQuery(id+"F1.wireOp",EDGE,"E1741"),sQuery(id+"F1.wireOp",EDGE,"E1742"),sQuery(id+"F1.wireOp",EDGE,"E1743"),sQuery(id+"F1.wireOp",EDGE,"E1744"),sQuery(id+"F1.wireOp",EDGE,"E1745"),sQuery(id+"F1.wireOp",EDGE,"E1746"),sQuery(id+"F1.wireOp",EDGE,"E1747"),sQuery(id+"F1.wireOp",EDGE,"E1748"),sQuery(id+"F1.wireOp",EDGE,"E1749"),sQuery(id+"F1.wireOp",EDGE,"E1750"),sQuery(id+"F1.wireOp",EDGE,"E1751"),sQuery(id+"F1.wireOp",EDGE,"E1752"),sQuery(id+"F1.wireOp",EDGE,"E1753"),sQuery(id+"F1.wireOp",EDGE,"E1754"),sQuery(id+"F1.wireOp",EDGE,"E1755"),sQuery(id+"F1.wireOp",EDGE,"E1756"),sQuery(id+"F1.wireOp",EDGE,"E1757"),sQuery(id+"F1.wireOp",EDGE,"E1758"),sQuery(id+"F1.wireOp",EDGE,"E1759"),sQuery(id+"F1.wireOp",EDGE,"E1760"),sQuery(id+"F1.wireOp",EDGE,"E1761"),sQuery(id+"F1.wireOp",EDGE,"E1762"),sQuery(id+"F1.wireOp",EDGE,"E1763"),sQuery(id+"F1.wireOp",EDGE,"E1764"),sQuery(id+"F1.wireOp",EDGE,"E1765"),sQuery(id+"F1.wireOp",EDGE,"E1766"),sQuery(id+"F1.wireOp",EDGE,"E1767"),sQuery(id+"F1.wireOp",EDGE,"E1768"),sQuery(id+"F1.wireOp",EDGE,"E1769"),sQuery(id+"F1.wireOp",EDGE,"E1770"),sQuery(id+"F1.wireOp",EDGE,"E1771"),sQuery(id+"F1.wireOp",EDGE,"E1772"),sQuery(id+"F1.wireOp",EDGE,"E1773"),sQuery(id+"F1.wireOp",EDGE,"E1774"),sQuery(id+"F1.wireOp",EDGE,"E1775"),sQuery(id+"F1.wireOp",EDGE,"E1776"),sQuery(id+"F1.wireOp",EDGE,"E1777"),sQuery(id+"F1.wireOp",EDGE,"E1778"),sQuery(id+"F1.wireOp",EDGE,"E1779"),sQuery(id+"F1.wireOp",EDGE,"E1780"),sQuery(id+"F1.wireOp",EDGE,"E1781"),sQuery(id+"F1.wireOp",EDGE,"E1782"),sQuery(id+"F1.wireOp",EDGE,"E1783"),sQuery(id+"F1.wireOp",EDGE,"E1784"),sQuery(id+"F1.wireOp",EDGE,"E1785"),sQuery(id+"F1.wireOp",EDGE,"E1786"),sQuery(id+"F1.wireOp",EDGE,"E1787"),sQuery(id+"F1.wireOp",EDGE,"E1788"),sQuery(id+"F1.wireOp",EDGE,"E1789"),sQuery(id+"F1.wireOp",EDGE,"E1790"),sQuery(id+"F1.wireOp",EDGE,"E1791"),sQuery(id+"F1.wireOp",EDGE,"E1792"),sQuery(id+"F1.wireOp",EDGE,"E1793"),sQuery(id+"F1.wireOp",EDGE,"E1794"),sQuery(id+"F1.wireOp",EDGE,"E1795"),sQuery(id+"F1.wireOp",EDGE,"E1796"),sQuery(id+"F1.wireOp",EDGE,"E1797"),sQuery(id+"F1.wireOp",EDGE,"E1798"),sQuery(id+"F1.wireOp",EDGE,"E1799"),sQuery(id+"F1.wireOp",EDGE,"E1800"),sQuery(id+"F1.wireOp",EDGE,"E1801"),sQuery(id+"F1.wireOp",EDGE,"E1802"),sQuery(id+"F1.wireOp",EDGE,"E1803"),sQuery(id+"F1.wireOp",EDGE,"E1804"),sQuery(id+"F1.wireOp",EDGE,"E1805"),sQuery(id+"F1.wireOp",EDGE,"E1806"),sQuery(id+"F1.wireOp",EDGE,"E1807"),sQuery(id+"F1.wireOp",EDGE,"E1808"),sQuery(id+"F1.wireOp",EDGE,"E1809"),sQuery(id+"F1.wireOp",EDGE,"E1810"),sQuery(id+"F1.wireOp",EDGE,"E1811"),sQuery(id+"F1.wireOp",EDGE,"E1812"),sQuery(id+"F1.wireOp",EDGE,"E1813"),sQuery(id+"F1.wireOp",EDGE,"E1814"),sQuery(id+"F1.wireOp",EDGE,"E1815"),sQuery(id+"F1.wireOp",EDGE,"E1816"),sQuery(id+"F1.wireOp",EDGE,"E1817"),sQuery(id+"F1.wireOp",EDGE,"E1818"),sQuery(id+"F1.wireOp",EDGE,"E1819"),sQuery(id+"F1.wireOp",EDGE,"E1820"),sQuery(id+"F1.wireOp",EDGE,"E1821"),sQuery(id+"F1.wireOp",EDGE,"E1822"),sQuery(id+"F1.wireOp",EDGE,"E1823"),sQuery(id+"F1.wireOp",EDGE,"E1824"),sQuery(id+"F1.wireOp",EDGE,"E1825"),sQuery(id+"F1.wireOp",EDGE,"E1826"),sQuery(id+"F1.wireOp",EDGE,"E1827"),sQuery(id+"F1.wireOp",EDGE,"E1828"),sQuery(id+"F1.wireOp",EDGE,"E1829"),sQuery(id+"F1.wireOp",EDGE,"E1830"),sQuery(id+"F1.wireOp",EDGE,"E1831"),sQuery(id+"F1.wireOp",EDGE,"E1832"),sQuery(id+"F1.wireOp",EDGE,"E1833"),sQuery(id+"F1.wireOp",EDGE,"E1834"),sQuery(id+"F1.wireOp",EDGE,"E1835"),sQuery(id+"F1.wireOp",EDGE,"E1836"),sQuery(id+"F1.wireOp",EDGE,"E1837"),sQuery(id+"F1.wireOp",EDGE,"E1838"),sQuery(id+"F1.wireOp",EDGE,"E1839"),sQuery(id+"F1.wireOp",EDGE,"E1840"),sQuery(id+"F1.wireOp",EDGE,"E1841"),sQuery(id+"F1.wireOp",EDGE,"E1842"),sQuery(id+"F1.wireOp",EDGE,"E1843"),sQuery(id+"F1.wireOp",EDGE,"E1844"),sQuery(id+"F1.wireOp",EDGE,"E1845"),sQuery(id+"F1.wireOp",EDGE,"E1846"),sQuery(id+"F1.wireOp",EDGE,"E1847"),sQuery(id+"F1.wireOp",EDGE,"E1848"),sQuery(id+"F1.wireOp",EDGE,"E1849"),sQuery(id+"F1.wireOp",EDGE,"E1850"),sQuery(id+"F1.wireOp",EDGE,"E1851"),sQuery(id+"F1.wireOp",EDGE,"E1852"),sQuery(id+"F1.wireOp",EDGE,"E1853"),sQuery(id+"F1.wireOp",EDGE,"E1854"),sQuery(id+"F1.wireOp",EDGE,"E1855"),sQuery(id+"F1.wireOp",EDGE,"E1856"),sQuery(id+"F1.wireOp",EDGE,"E1857"),sQuery(id+"F1.wireOp",EDGE,"E1858"),sQuery(id+"F1.wireOp",EDGE,"E1859"),sQuery(id+"F1.wireOp",EDGE,"E1860"),sQuery(id+"F1.wireOp",EDGE,"E1861"),sQuery(id+"F1.wireOp",EDGE,"E1862"),sQuery(id+"F1.wireOp",EDGE,"E1863"),sQuery(id+"F1.wireOp",EDGE,"E1864"),sQuery(id+"F1.wireOp",EDGE,"E1865"),sQuery(id+"F1.wireOp",EDGE,"E1866"),sQuery(id+"F1.wireOp",EDGE,"E1867"),sQuery(id+"F1.wireOp",EDGE,"E1868"),sQuery(id+"F1.wireOp",EDGE,"E1869"),sQuery(id+"F1.wireOp",EDGE,"E1870"),sQuery(id+"F1.wireOp",EDGE,"E1871"),sQuery(id+"F1.wireOp",EDGE,"E1872"),sQuery(id+"F1.wireOp",EDGE,"E1873"),sQuery(id+"F1.wireOp",EDGE,"E1874"),sQuery(id+"F1.wireOp",EDGE,"E1875"),sQuery(id+"F1.wireOp",EDGE,"E1876"),sQuery(id+"F1.wireOp",EDGE,"E1877"),sQuery(id+"F1.wireOp",EDGE,"E1878"),sQuery(id+"F1.wireOp",EDGE,"E1879"),sQuery(id+"F1.wireOp",EDGE,"E1880"),sQuery(id+"F1.wireOp",EDGE,"E1881"),sQuery(id+"F1.wireOp",EDGE,"E1882"),sQuery(id+"F1.wireOp",EDGE,"E1883"),sQuery(id+"F1.wireOp",EDGE,"E1884"),sQuery(id+"F1.wireOp",EDGE,"E1885"),sQuery(id+"F1.wireOp",EDGE,"E1886"),sQuery(id+"F1.wireOp",EDGE,"E1887"),sQuery(id+"F1.wireOp",EDGE,"E1888"),sQuery(id+"F1.wireOp",EDGE,"E1889"),sQuery(id+"F1.wireOp",EDGE,"E1890"),sQuery(id+"F1.wireOp",EDGE,"E1891"),sQuery(id+"F1.wireOp",EDGE,"E1892"),sQuery(id+"F1.wireOp",EDGE,"E1893"),sQuery(id+"F1.wireOp",EDGE,"E1894"),sQuery(id+"F1.wireOp",EDGE,"E1895"),sQuery(id+"F1.wireOp",EDGE,"E1896"),sQuery(id+"F1.wireOp",EDGE,"E1897"),sQuery(id+"F1.wireOp",EDGE,"E1898"),sQuery(id+"F1.wireOp",EDGE,"E1899"),sQuery(id+"F1.wireOp",EDGE,"E1900"),sQuery(id+"F1.wireOp",EDGE,"E1901"),sQuery(id+"F1.wireOp",EDGE,"E1902"),sQuery(id+"F1.wireOp",EDGE,"E1903"),sQuery(id+"F1.wireOp",EDGE,"E1904"),sQuery(id+"F1.wireOp",EDGE,"E1905"),sQuery(id+"F1.wireOp",EDGE,"E1906"),sQuery(id+"F1.wireOp",EDGE,"E1907"),sQuery(id+"F1.wireOp",EDGE,"E1908"),sQuery(id+"F1.wireOp",EDGE,"E1909"),sQuery(id+"F1.wireOp",EDGE,"E1910"),sQuery(id+"F1.wireOp",EDGE,"E1911"),sQuery(id+"F1.wireOp",EDGE,"E1912"),sQuery(id+"F1.wireOp",EDGE,"E1913"),sQuery(id+"F1.wireOp",EDGE,"E1914"),sQuery(id+"F1.wireOp",EDGE,"E1915"),sQuery(id+"F1.wireOp",EDGE,"E1916"),sQuery(id+"F1.wireOp",EDGE,"E1917"),sQuery(id+"F1.wireOp",EDGE,"E1918"),sQuery(id+"F1.wireOp",EDGE,"E1919"),sQuery(id+"F1.wireOp",EDGE,"E1920"),sQuery(id+"F1.wireOp",EDGE,"E1921"),sQuery(id+"F1.wireOp",EDGE,"E1922"),sQuery(id+"F1.wireOp",EDGE,"E1923"),sQuery(id+"F1.wireOp",EDGE,"E1924"),sQuery(id+"F1.wireOp",EDGE,"E1925"),sQuery(id+"F1.wireOp",EDGE,"E1926"),sQuery(id+"F1.wireOp",EDGE,"E1927"),sQuery(id+"F1.wireOp",EDGE,"E1928"),sQuery(id+"F1.wireOp",EDGE,"E1929"),sQuery(id+"F1.wireOp",EDGE,"E1930"),sQuery(id+"F1.wireOp",EDGE,"E1931"),sQuery(id+"F1.wireOp",EDGE,"E1932"),sQuery(id+"F1.wireOp",EDGE,"E1933"),sQuery(id+"F1.wireOp",EDGE,"E1934"),sQuery(id+"F1.wireOp",EDGE,"E1935"),sQuery(id+"F1.wireOp",EDGE,"E1936"),sQuery(id+"F1.wireOp",EDGE,"E1937"),sQuery(id+"F1.wireOp",EDGE,"E1938"),sQuery(id+"F1.wireOp",EDGE,"E1939"),sQuery(id+"F1.wireOp",EDGE,"E1940"),sQuery(id+"F1.wireOp",EDGE,"E1941"),sQuery(id+"F1.wireOp",EDGE,"E1942"),sQuery(id+"F1.wireOp",EDGE,"E1943"),sQuery(id+"F1.wireOp",EDGE,"E1944"),sQuery(id+"F1.wireOp",EDGE,"E1945"),sQuery(id+"F1.wireOp",EDGE,"E1946"),sQuery(id+"F1.wireOp",EDGE,"E1947"),sQuery(id+"F1.wireOp",EDGE,"E1948"),sQuery(id+"F1.wireOp",EDGE,"E1949"),sQuery(id+"F1.wireOp",EDGE,"E1950"),sQuery(id+"F1.wireOp",EDGE,"E1951"),sQuery(id+"F1.wireOp",EDGE,"E1952"),sQuery(id+"F1.wireOp",EDGE,"E1953"),sQuery(id+"F1.wireOp",EDGE,"E1954"),sQuery(id+"F1.wireOp",EDGE,"E1955"),sQuery(id+"F1.wireOp",EDGE,"E1956"),sQuery(id+"F1.wireOp",EDGE,"E1957"),sQuery(id+"F1.wireOp",EDGE,"E1958"),sQuery(id+"F1.wireOp",EDGE,"E1959"),sQuery(id+"F1.wireOp",EDGE,"E1960"),sQuery(id+"F1.wireOp",EDGE,"E1961"),sQuery(id+"F1.wireOp",EDGE,"E1962"),sQuery(id+"F1.wireOp",EDGE,"E1963"),sQuery(id+"F1.wireOp",EDGE,"E1964"),sQuery(id+"F1.wireOp",EDGE,"E1965"),sQuery(id+"F1.wireOp",EDGE,"E1966"),sQuery(id+"F1.wireOp",EDGE,"E1967"),sQuery(id+"F1.wireOp",EDGE,"E1968"),sQuery(id+"F1.wireOp",EDGE,"E1969"),sQuery(id+"F1.wireOp",EDGE,"E1970"),sQuery(id+"F1.wireOp",EDGE,"E1971"),sQuery(id+"F1.wireOp",EDGE,"E1972"),sQuery(id+"F1.wireOp",EDGE,"E1973"),sQuery(id+"F1.wireOp",EDGE,"E1974"),sQuery(id+"F1.wireOp",EDGE,"E1975"),sQuery(id+"F1.wireOp",EDGE,"E1976"),sQuery(id+"F1.wireOp",EDGE,"E1977"),sQuery(id+"F1.wireOp",EDGE,"E1978"),sQuery(id+"F1.wireOp",EDGE,"E1979"),sQuery(id+"F1.wireOp",EDGE,"E1980"),sQuery(id+"F1.wireOp",EDGE,"E1981"),sQuery(id+"F1.wireOp",EDGE,"E1982"),sQuery(id+"F1.wireOp",EDGE,"E1983"),sQuery(id+"F1.wireOp",EDGE,"E1984"),sQuery(id+"F1.wireOp",EDGE,"E1985"),sQuery(id+"F1.wireOp",EDGE,"E1986"),sQuery(id+"F1.wireOp",EDGE,"E1987"),sQuery(id+"F1.wireOp",EDGE,"E1988"),sQuery(id+"F1.wireOp",EDGE,"E1989"),sQuery(id+"F1.wireOp",EDGE,"E1990"),sQuery(id+"F1.wireOp",EDGE,"E1991"),sQuery(id+"F1.wireOp",EDGE,"E1992"),sQuery(id+"F1.wireOp",EDGE,"E1993"),sQuery(id+"F1.wireOp",EDGE,"E1994"),sQuery(id+"F1.wireOp",EDGE,"E1995"),sQuery(id+"F1.wireOp",EDGE,"E1996"),sQuery(id+"F1.wireOp",EDGE,"E1997"),sQuery(id+"F1.wireOp",EDGE,"E1998"),sQuery(id+"F1.wireOp",EDGE,"E1999"),sQuery(id+"F1.wireOp",EDGE,"E2000"),sQuery(id+"F1.wireOp",EDGE,"E2000"),sQuery(id+"F1.wireOp",EDGE,"E2001"),sQuery(id+"F1.wireOp",EDGE,"E2002"),sQuery(id+"F1.wireOp",EDGE,"E2003"),sQuery(id+"F1.wireOp",EDGE,"E2004"),sQuery(id+"F1.wireOp",EDGE,"E2005"),sQuery(id+"F1.wireOp",EDGE,"E2006"),sQuery(id+"F1.wireOp",EDGE,"E2007"),sQuery(id+"F1.wireOp",EDGE,"E2008"),sQuery(id+"F1.wireOp",EDGE,"E2009"),sQuery(id+"F1.wireOp",EDGE,"E2010"),sQuery(id+"F1.wireOp",EDGE,"E2011"),sQuery(id+"F1.wireOp",EDGE,"E2012"),sQuery(id+"F1.wireOp",EDGE,"E2013"),sQuery(id+"F1.wireOp",EDGE,"E2014"),sQuery(id+"F1.wireOp",EDGE,"E2015"),sQuery(id+"F1.wireOp",EDGE,"E2016"),sQuery(id+"F1.wireOp",EDGE,"E2017"),sQuery(id+"F1.wireOp",EDGE,"E2018"),sQuery(id+"F1.wireOp",EDGE,"E2019"),sQuery(id+"F1.wireOp",EDGE,"E2020"),sQuery(id+"F1.wireOp",EDGE,"E2021"),sQuery(id+"F1.wireOp",EDGE,"E2022"),sQuery(id+"F1.wireOp",EDGE,"E2023"),sQuery(id+"F1.wireOp",EDGE,"E2024"),sQuery(id+"F1.wireOp",EDGE,"E2025"),sQuery(id+"F1.wireOp",EDGE,"E2026"),sQuery(id+"F1.wireOp",EDGE,"E2027"),sQuery(id+"F1.wireOp",EDGE,"E2028"),sQuery(id+"F1.wireOp",EDGE,"E2029"),sQuery(id+"F1.wireOp",EDGE,"E2030"),sQuery(id+"F1.wireOp",EDGE,"E2031"),sQuery(id+"F1.wireOp",EDGE,"E2032"),sQuery(id+"F1.wireOp",EDGE,"E2033"),sQuery(id+"F1.wireOp",EDGE,"E2034"),sQuery(id+"F1.wireOp",EDGE,"E2035"),sQuery(id+"F1.wireOp",EDGE,"E2036"),sQuery(id+"F1.wireOp",EDGE,"E2037"),sQuery(id+"F1.wireOp",EDGE,"E2038"),sQuery(id+"F1.wireOp",EDGE,"E2039"),sQuery(id+"F1.wireOp",EDGE,"E2040"),sQuery(id+"F1.wireOp",EDGE,"E2041"),sQuery(id+"F1.wireOp",EDGE,"E2042"),sQuery(id+"F1.wireOp",EDGE,"E2043"),sQuery(id+"F1.wireOp",EDGE,"E2044"),sQuery(id+"F1.wireOp",EDGE,"E2045"),sQuery(id+"F1.wireOp",EDGE,"E2046"),sQuery(id+"F1.wireOp",EDGE,"E2047"),sQuery(id+"F1.wireOp",EDGE,"E2048"),sQuery(id+"F1.wireOp",EDGE,"E2049"),sQuery(id+"F1.wireOp",EDGE,"E2050"),sQuery(id+"F1.wireOp",EDGE,"E2051"),sQuery(id+"F1.wireOp",EDGE,"E2052"),sQuery(id+"F1.wireOp",EDGE,"E2053"),sQuery(id+"F1.wireOp",EDGE,"E2054"),sQuery(id+"F1.wireOp",EDGE,"E2055"),sQuery(id+"F1.wireOp",EDGE,"E2056"),sQuery(id+"F1.wireOp",EDGE,"E2057"),sQuery(id+"F1.wireOp",EDGE,"E2058"),sQuery(id+"F1.wireOp",EDGE,"E2059"),sQuery(id+"F1.wireOp",EDGE,"E2060"),sQuery(id+"F1.wireOp",EDGE,"E2061"),sQuery(id+"F1.wireOp",EDGE,"E2062"),sQuery(id+"F1.wireOp",EDGE,"E2063"),sQuery(id+"F1.wireOp",EDGE,"E2064"),sQuery(id+"F1.wireOp",EDGE,"E2065"),sQuery(id+"F1.wireOp",EDGE,"E2066"),sQuery(id+"F1.wireOp",EDGE,"E2067"),sQuery(id+"F1.wireOp",EDGE,"E2068"),sQuery(id+"F1.wireOp",EDGE,"E2069"),sQuery(id+"F1.wireOp",EDGE,"E2070"),sQuery(id+"F1.wireOp",EDGE,"E2071"),sQuery(id+"F1.wireOp",EDGE,"E2072"),sQuery(id+"F1.wireOp",EDGE,"E2073"),sQuery(id+"F1.wireOp",EDGE,"E2074"),sQuery(id+"F1.wireOp",EDGE,"E2075"),sQuery(id+"F1.wireOp",EDGE,"E2076"),sQuery(id+"F1.wireOp",EDGE,"E2077"),sQuery(id+"F1.wireOp",EDGE,"E2078"),sQuery(id+"F1.wireOp",EDGE,"E2079"),sQuery(id+"F1.wireOp",EDGE,"E2080"),sQuery(id+"F1.wireOp",EDGE,"E2081"),sQuery(id+"F1.wireOp",EDGE,"E2082"),sQuery(id+"F1.wireOp",EDGE,"E2083"),sQuery(id+"F1.wireOp",EDGE,"E2084"),sQuery(id+"F1.wireOp",EDGE,"E2085"),sQuery(id+"F1.wireOp",EDGE,"E2086"),sQuery(id+"F1.wireOp",EDGE,"E2087"),sQuery(id+"F1.wireOp",EDGE,"E2088"),sQuery(id+"F1.wireOp",EDGE,"E2089"),sQuery(id+"F1.wireOp",EDGE,"E2090"),sQuery(id+"F1.wireOp",EDGE,"E2091"),sQuery(id+"F1.wireOp",EDGE,"E2092"),sQuery(id+"F1.wireOp",EDGE,"E2093"),sQuery(id+"F1.wireOp",EDGE,"E2094"),sQuery(id+"F1.wireOp",EDGE,"E2095"),sQuery(id+"F1.wireOp",EDGE,"E2096"),sQuery(id+"F1.wireOp",EDGE,"E2097"),sQuery(id+"F1.wireOp",EDGE,"E2098"),sQuery(id+"F1.wireOp",EDGE,"E2099"),sQuery(id+"F1.wireOp",EDGE,"E2100"),sQuery(id+"F1.wireOp",EDGE,"E2101"),sQuery(id+"F1.wireOp",EDGE,"E2102"),sQuery(id+"F1.wireOp",EDGE,"E2103"),sQuery(id+"F1.wireOp",EDGE,"E2104"),sQuery(id+"F1.wireOp",EDGE,"E2105"),sQuery(id+"F1.wireOp",EDGE,"E2106"),sQuery(id+"F1.wireOp",EDGE,"E2107"),sQuery(id+"F1.wireOp",EDGE,"E2108"),sQuery(id+"F1.wireOp",EDGE,"E2109"),sQuery(id+"F1.wireOp",EDGE,"E2110"),sQuery(id+"F1.wireOp",EDGE,"E2111"),sQuery(id+"F1.wireOp",EDGE,"E2112"),sQuery(id+"F1.wireOp",EDGE,"E2113"),sQuery(id+"F1.wireOp",EDGE,"E2114"),sQuery(id+"F1.wireOp",EDGE,"E2115"),sQuery(id+"F1.wireOp",EDGE,"E2116"),sQuery(id+"F1.wireOp",EDGE,"E2117"),sQuery(id+"F1.wireOp",EDGE,"E2118"),sQuery(id+"F1.wireOp",EDGE,"E2119"),sQuery(id+"F1.wireOp",EDGE,"E2120"),sQuery(id+"F1.wireOp",EDGE,"E2121"),sQuery(id+"F1.wireOp",EDGE,"E2122"),sQuery(id+"F1.wireOp",EDGE,"E2123"),sQuery(id+"F1.wireOp",EDGE,"E2124"),sQuery(id+"F1.wireOp",EDGE,"E2125"),sQuery(id+"F1.wireOp",EDGE,"E2126"),sQuery(id+"F1.wireOp",EDGE,"E2127"),sQuery(id+"F1.wireOp",EDGE,"E2128"),sQuery(id+"F1.wireOp",EDGE,"E2129"),sQuery(id+"F1.wireOp",EDGE,"E2130"),sQuery(id+"F1.wireOp",EDGE,"E2131"),sQuery(id+"F1.wireOp",EDGE,"E2132"),sQuery(id+"F1.wireOp",EDGE,"E2133"),sQuery(id+"F1.wireOp",EDGE,"E2134"),sQuery(id+"F1.wireOp",EDGE,"E2135"),sQuery(id+"F1.wireOp",EDGE,"E2136"),sQuery(id+"F1.wireOp",EDGE,"E2137"),sQuery(id+"F1.wireOp",EDGE,"E2138"),sQuery(id+"F1.wireOp",EDGE,"E2139"),sQuery(id+"F1.wireOp",EDGE,"E2140"),sQuery(id+"F1.wireOp",EDGE,"E2141"),sQuery(id+"F1.wireOp",EDGE,"E2142"),sQuery(id+"F1.wireOp",EDGE,"E2143"),sQuery(id+"F1.wireOp",EDGE,"E2144"),sQuery(id+"F1.wireOp",EDGE,"E2145"),sQuery(id+"F1.wireOp",EDGE,"E2146"),sQuery(id+"F1.wireOp",EDGE,"E2147"),sQuery(id+"F1.wireOp",EDGE,"E2148"),sQuery(id+"F1.wireOp",EDGE,"E2149"),sQuery(id+"F1.wireOp",EDGE,"E2150"),sQuery(id+"F1.wireOp",EDGE,"E2151"),sQuery(id+"F1.wireOp",EDGE,"E2152"),sQuery(id+"F1.wireOp",EDGE,"E2153"),sQuery(id+"F1.wireOp",EDGE,"E2154"),sQuery(id+"F1.wireOp",EDGE,"E2155"),sQuery(id+"F1.wireOp",EDGE,"E2156"),sQuery(id+"F1.wireOp",EDGE,"E2157"),sQuery(id+"F1.wireOp",EDGE,"E2158"),sQuery(id+"F1.wireOp",EDGE,"E2159"),sQuery(id+"F1.wireOp",EDGE,"E2160"),sQuery(id+"F1.wireOp",EDGE,"E2161"),sQuery(id+"F1.wireOp",EDGE,"E2162"),sQuery(id+"F1.wireOp",EDGE,"E2163"),sQuery(id+"F1.wireOp",EDGE,"E2164"),sQuery(id+"F1.wireOp",EDGE,"E2165"),sQuery(id+"F1.wireOp",EDGE,"E2166"),sQuery(id+"F1.wireOp",EDGE,"E2167"),sQuery(id+"F1.wireOp",EDGE,"E2168"),sQuery(id+"F1.wireOp",EDGE,"E2169"),sQuery(id+"F1.wireOp",EDGE,"E2170"),sQuery(id+"F1.wireOp",EDGE,"E2171"),sQuery(id+"F1.wireOp",EDGE,"E2172"),sQuery(id+"F1.wireOp",EDGE,"E2173"),sQuery(id+"F1.wireOp",EDGE,"E2174"),sQuery(id+"F1.wireOp",EDGE,"E2175"),sQuery(id+"F1.wireOp",EDGE,"E2176"),sQuery(id+"F1.wireOp",EDGE,"E2177"),sQuery(id+"F1.wireOp",EDGE,"E2178"),sQuery(id+"F1.wireOp",EDGE,"E2179"),sQuery(id+"F1.wireOp",EDGE,"E2180"),sQuery(id+"F1.wireOp",EDGE,"E2181"),sQuery(id+"F1.wireOp",EDGE,"E2182"),sQuery(id+"F1.wireOp",EDGE,"E2183"),sQuery(id+"F1.wireOp",EDGE,"E2184"),sQuery(id+"F1.wireOp",EDGE,"E2185"),sQuery(id+"F1.wireOp",EDGE,"E2186"),sQuery(id+"F1.wireOp",EDGE,"E2187"),sQuery(id+"F1.wireOp",EDGE,"E2188"),sQuery(id+"F1.wireOp",EDGE,"E2189"),sQuery(id+"F1.wireOp",EDGE,"E2190"),sQuery(id+"F1.wireOp",EDGE,"E2191"),sQuery(id+"F1.wireOp",EDGE,"E2192"),sQuery(id+"F1.wireOp",EDGE,"E2193"),sQuery(id+"F1.wireOp",EDGE,"E2194"),sQuery(id+"F1.wireOp",EDGE,"E2195"),sQuery(id+"F1.wireOp",EDGE,"E2196"),sQuery(id+"F1.wireOp",EDGE,"E2197"),sQuery(id+"F1.wireOp",EDGE,"E2198"),sQuery(id+"F1.wireOp",EDGE,"E2199"),sQuery(id+"F1.wireOp",EDGE,"E2200"),sQuery(id+"F1.wireOp",EDGE,"E2201"),sQuery(id+"F1.wireOp",EDGE,"E2202"),sQuery(id+"F1.wireOp",EDGE,"E2203"),sQuery(id+"F1.wireOp",EDGE,"E2204"),sQuery(id+"F1.wireOp",EDGE,"E2205"),sQuery(id+"F1.wireOp",EDGE,"E2206"),sQuery(id+"F1.wireOp",EDGE,"E2207"),sQuery(id+"F1.wireOp",EDGE,"E2208"),sQuery(id+"F1.wireOp",EDGE,"E2209"),sQuery(id+"F1.wireOp",EDGE,"E2210"),sQuery(id+"F1.wireOp",EDGE,"E2211"),sQuery(id+"F1.wireOp",EDGE,"E2212"),sQuery(id+"F1.wireOp",EDGE,"E2213"),sQuery(id+"F1.wireOp",EDGE,"E2214"),sQuery(id+"F1.wireOp",EDGE,"E2215"),sQuery(id+"F1.wireOp",EDGE,"E2216"),sQuery(id+"F1.wireOp",EDGE,"E2217"),sQuery(id+"F1.wireOp",EDGE,"E2218"),sQuery(id+"F1.wireOp",EDGE,"E2219"),sQuery(id+"F1.wireOp",EDGE,"E2220"),sQuery(id+"F1.wireOp",EDGE,"E2221"),sQuery(id+"F1.wireOp",EDGE,"E2222"),sQuery(id+"F1.wireOp",EDGE,"E2223"),sQuery(id+"F1.wireOp",EDGE,"E2224"),sQuery(id+"F1.wireOp",EDGE,"E2225"),sQuery(id+"F1.wireOp",EDGE,"E2226"),sQuery(id+"F1.wireOp",EDGE,"E2227"),sQuery(id+"F1.wireOp",EDGE,"E2228"),sQuery(id+"F1.wireOp",EDGE,"E2229"),sQuery(id+"F1.wireOp",EDGE,"E2230"),sQuery(id+"F1.wireOp",EDGE,"E2231"),sQuery(id+"F1.wireOp",EDGE,"E2232"),sQuery(id+"F1.wireOp",EDGE,"E2233"),sQuery(id+"F1.wireOp",EDGE,"E2234"),sQuery(id+"F1.wireOp",EDGE,"E2235"),sQuery(id+"F1.wireOp",EDGE,"E2236"),sQuery(id+"F1.wireOp",EDGE,"E2237"),sQuery(id+"F1.wireOp",EDGE,"E2238"),sQuery(id+"F1.wireOp",EDGE,"E2239"),sQuery(id+"F1.wireOp",EDGE,"E2240"),sQuery(id+"F1.wireOp",EDGE,"E2241"),sQuery(id+"F1.wireOp",EDGE,"E2242"),sQuery(id+"F1.wireOp",EDGE,"E2243"),sQuery(id+"F1.wireOp",EDGE,"E2244"),sQuery(id+"F1.wireOp",EDGE,"E2245"),sQuery(id+"F1.wireOp",EDGE,"E2246"),sQuery(id+"F1.wireOp",EDGE,"E2247"),sQuery(id+"F1.wireOp",EDGE,"E2248"),sQuery(id+"F1.wireOp",EDGE,"E2249"),sQuery(id+"F1.wireOp",EDGE,"E2250"),sQuery(id+"F1.wireOp",EDGE,"E2251"),sQuery(id+"F1.wireOp",EDGE,"E2252"),sQuery(id+"F1.wireOp",EDGE,"E2253"),sQuery(id+"F1.wireOp",EDGE,"E2254"),sQuery(id+"F1.wireOp",EDGE,"E2255"),sQuery(id+"F1.wireOp",EDGE,"E2256"),sQuery(id+"F1.wireOp",EDGE,"E2257"),sQuery(id+"F1.wireOp",EDGE,"E2258"),sQuery(id+"F1.wireOp",EDGE,"E2259"),sQuery(id+"F1.wireOp",EDGE,"E2260"),sQuery(id+"F1.wireOp",EDGE,"E2261"),sQuery(id+"F1.wireOp",EDGE,"E2262"),sQuery(id+"F1.wireOp",EDGE,"E2263"),sQuery(id+"F1.wireOp",EDGE,"E2264"),sQuery(id+"F1.wireOp",EDGE,"E2265"),sQuery(id+"F1.wireOp",EDGE,"E2266"),sQuery(id+"F1.wireOp",EDGE,"E2267"),sQuery(id+"F1.wireOp",EDGE,"E2268"),sQuery(id+"F1.wireOp",EDGE,"E2269"),sQuery(id+"F1.wireOp",EDGE,"E2270"),sQuery(id+"F1.wireOp",EDGE,"E2271"),sQuery(id+"F1.wireOp",EDGE,"E2272"),sQuery(id+"F1.wireOp",EDGE,"E2273"),sQuery(id+"F1.wireOp",EDGE,"E2274"),sQuery(id+"F1.wireOp",EDGE,"E2275"),sQuery(id+"F1.wireOp",EDGE,"E2276"),sQuery(id+"F1.wireOp",EDGE,"E2277"),sQuery(id+"F1.wireOp",EDGE,"E2278"),sQuery(id+"F1.wireOp",EDGE,"E2279"),sQuery(id+"F1.wireOp",EDGE,"E2280"),sQuery(id+"F1.wireOp",EDGE,"E2281"),sQuery(id+"F1.wireOp",EDGE,"E2282"),sQuery(id+"F1.wireOp",EDGE,"E2283"),sQuery(id+"F1.wireOp",EDGE,"E2284"),sQuery(id+"F1.wireOp",EDGE,"E2285"),sQuery(id+"F1.wireOp",EDGE,"E2286"),sQuery(id+"F1.wireOp",EDGE,"E2287"),sQuery(id+"F1.wireOp",EDGE,"E2288"),sQuery(id+"F1.wireOp",EDGE,"E2289"),sQuery(id+"F1.wireOp",EDGE,"E2290"),sQuery(id+"F1.wireOp",EDGE,"E2291"),sQuery(id+"F1.wireOp",EDGE,"E2292"),sQuery(id+"F1.wireOp",EDGE,"E2293"),sQuery(id+"F1.wireOp",EDGE,"E2294"),sQuery(id+"F1.wireOp",EDGE,"E2295"),sQuery(id+"F1.wireOp",EDGE,"E2296"),sQuery(id+"F1.wireOp",EDGE,"E2297"),sQuery(id+"F1.wireOp",EDGE,"E2298"),sQuery(id+"F1.wireOp",EDGE,"E2299"),sQuery(id+"F1.wireOp",EDGE,"E2300"),sQuery(id+"F1.wireOp",EDGE,"E2301"),sQuery(id+"F1.wireOp",EDGE,"E2302"),sQuery(id+"F1.wireOp",EDGE,"E2303"),sQuery(id+"F1.wireOp",EDGE,"E2304"),sQuery(id+"F1.wireOp",EDGE,"E2305"),sQuery(id+"F1.wireOp",EDGE,"E2306"),sQuery(id+"F1.wireOp",EDGE,"E2307"),sQuery(id+"F1.wireOp",EDGE,"E2308"),sQuery(id+"F1.wireOp",EDGE,"E2309"),sQuery(id+"F1.wireOp",EDGE,"E2310"),sQuery(id+"F1.wireOp",EDGE,"E2311"),sQuery(id+"F1.wireOp",EDGE,"E2312"),sQuery(id+"F1.wireOp",EDGE,"E2313"),sQuery(id+"F1.wireOp",EDGE,"E2314"),sQuery(id+"F1.wireOp",EDGE,"E2315"),sQuery(id+"F1.wireOp",EDGE,"E2316"),sQuery(id+"F1.wireOp",EDGE,"E2317"),sQuery(id+"F1.wireOp",EDGE,"E2318"),sQuery(id+"F1.wireOp",EDGE,"E2319"),sQuery(id+"F1.wireOp",EDGE,"E2320"),sQuery(id+"F1.wireOp",EDGE,"E2321"),sQuery(id+"F1.wireOp",EDGE,"E2322"),sQuery(id+"F1.wireOp",EDGE,"E2323"),sQuery(id+"F1.wireOp",EDGE,"E2324"),sQuery(id+"F1.wireOp",EDGE,"E2325"),sQuery(id+"F1.wireOp",EDGE,"E2326"),sQuery(id+"F1.wireOp",EDGE,"E2327"),sQuery(id+"F1.wireOp",EDGE,"E2328"),sQuery(id+"F1.wireOp",EDGE,"E2329"),sQuery(id+"F1.wireOp",EDGE,"E2330"),sQuery(id+"F1.wireOp",EDGE,"E2331"),sQuery(id+"F1.wireOp",EDGE,"E2332"),sQuery(id+"F1.wireOp",EDGE,"E2333"),sQuery(id+"F1.wireOp",EDGE,"E2334"),sQuery(id+"F1.wireOp",EDGE,"E2335"),sQuery(id+"F1.wireOp",EDGE,"E2336"),sQuery(id+"F1.wireOp",EDGE,"E2337"),sQuery(id+"F1.wireOp",EDGE,"E2338"),sQuery(id+"F1.wireOp",EDGE,"E2339"),sQuery(id+"F1.wireOp",EDGE,"E2340"),sQuery(id+"F1.wireOp",EDGE,"E2341"),sQuery(id+"F1.wireOp",EDGE,"E2342"),sQuery(id+"F1.wireOp",EDGE,"E2343"),sQuery(id+"F1.wireOp",EDGE,"E2344"),sQuery(id+"F1.wireOp",EDGE,"E2345"),sQuery(id+"F1.wireOp",EDGE,"E2346"),sQuery(id+"F1.wireOp",EDGE,"E2347"),sQuery(id+"F1.wireOp",EDGE,"E2348"),sQuery(id+"F1.wireOp",EDGE,"E2349"),sQuery(id+"F1.wireOp",EDGE,"E2350"),sQuery(id+"F1.wireOp",EDGE,"E2351"),sQuery(id+"F1.wireOp",EDGE,"E2352"),sQuery(id+"F1.wireOp",EDGE,"E2353"),sQuery(id+"F1.wireOp",EDGE,"E2354"),sQuery(id+"F1.wireOp",EDGE,"E2355"),sQuery(id+"F1.wireOp",EDGE,"E2356"),sQuery(id+"F1.wireOp",EDGE,"E2357"),sQuery(id+"F1.wireOp",EDGE,"E2358"),sQuery(id+"F1.wireOp",EDGE,"E2359"),sQuery(id+"F1.wireOp",EDGE,"E2360"),sQuery(id+"F1.wireOp",EDGE,"E2361"),sQuery(id+"F1.wireOp",EDGE,"E2362"),sQuery(id+"F1.wireOp",EDGE,"E2363"),sQuery(id+"F1.wireOp",EDGE,"E2364"),sQuery(id+"F1.wireOp",EDGE,"E2365"),sQuery(id+"F1.wireOp",EDGE,"E2366"),sQuery(id+"F1.wireOp",EDGE,"E2367"),sQuery(id+"F1.wireOp",EDGE,"E2368"),sQuery(id+"F1.wireOp",EDGE,"E2369"),sQuery(id+"F1.wireOp",EDGE,"E2370"),sQuery(id+"F1.wireOp",EDGE,"E2371"),sQuery(id+"F1.wireOp",EDGE,"E2372"),sQuery(id+"F1.wireOp",EDGE,"E2373"),sQuery(id+"F1.wireOp",EDGE,"E2374"),sQuery(id+"F1.wireOp",EDGE,"E2375"),sQuery(id+"F1.wireOp",EDGE,"E2376"),sQuery(id+"F1.wireOp",EDGE,"E2377"),sQuery(id+"F1.wireOp",EDGE,"E2378"),sQuery(id+"F1.wireOp",EDGE,"E2379"),sQuery(id+"F1.wireOp",EDGE,"E2380"),sQuery(id+"F1.wireOp",EDGE,"E2381"),sQuery(id+"F1.wireOp",EDGE,"E2382"),sQuery(id+"F1.wireOp",EDGE,"E2383"),sQuery(id+"F1.wireOp",EDGE,"E2384"),sQuery(id+"F1.wireOp",EDGE,"E2385"),sQuery(id+"F1.wireOp",EDGE,"E2386"),sQuery(id+"F1.wireOp",EDGE,"E2387"),sQuery(id+"F1.wireOp",EDGE,"E2388"),sQuery(id+"F1.wireOp",EDGE,"E2389"),sQuery(id+"F1.wireOp",EDGE,"E2390"),sQuery(id+"F1.wireOp",EDGE,"E2391"),sQuery(id+"F1.wireOp",EDGE,"E2392"),sQuery(id+"F1.wireOp",EDGE,"E2393"),sQuery(id+"F1.wireOp",EDGE,"E2394"),sQuery(id+"F1.wireOp",EDGE,"E2395"),sQuery(id+"F1.wireOp",EDGE,"E2396"),sQuery(id+"F1.wireOp",EDGE,"E2397"),sQuery(id+"F1.wireOp",EDGE,"E2398"),sQuery(id+"F1.wireOp",EDGE,"E2399"),sQuery(id+"F1.wireOp",EDGE,"E2400"),sQuery(id+"F1.wireOp",EDGE,"E2401"),sQuery(id+"F1.wireOp",EDGE,"E2402"),sQuery(id+"F1.wireOp",EDGE,"E2403"),sQuery(id+"F1.wireOp",EDGE,"E2404"),sQuery(id+"F1.wireOp",EDGE,"E2405"),sQuery(id+"F1.wireOp",EDGE,"E2406"),sQuery(id+"F1.wireOp",EDGE,"E2407"),sQuery(id+"F1.wireOp",EDGE,"E2408"),sQuery(id+"F1.wireOp",EDGE,"E2409"),sQuery(id+"F1.wireOp",EDGE,"E2410"),sQuery(id+"F1.wireOp",EDGE,"E2411"),sQuery(id+"F1.wireOp",EDGE,"E2412"),sQuery(id+"F1.wireOp",EDGE,"E2413"),sQuery(id+"F1.wireOp",EDGE,"E2414"),sQuery(id+"F1.wireOp",EDGE,"E2415"),sQuery(id+"F1.wireOp",EDGE,"E2416"),sQuery(id+"F1.wireOp",EDGE,"E2417"),sQuery(id+"F1.wireOp",EDGE,"E2418"),sQuery(id+"F1.wireOp",EDGE,"E2419"),sQuery(id+"F1.wireOp",EDGE,"E2420"),sQuery(id+"F1.wireOp",EDGE,"E2421"),sQuery(id+"F1.wireOp",EDGE,"E2422"),sQuery(id+"F1.wireOp",EDGE,"E2423"),sQuery(id+"F1.wireOp",EDGE,"E2424"),sQuery(id+"F1.wireOp",EDGE,"E2425"),sQuery(id+"F1.wireOp",EDGE,"E2426"),sQuery(id+"F1.wireOp",EDGE,"E2427"),sQuery(id+"F1.wireOp",EDGE,"E2428"),sQuery(id+"F1.wireOp",EDGE,"E2429"),sQuery(id+"F1.wireOp",EDGE,"E2430"),sQuery(id+"F1.wireOp",EDGE,"E2431"),sQuery(id+"F1.wireOp",EDGE,"E2432"),sQuery(id+"F1.wireOp",EDGE,"E2433"),sQuery(id+"F1.wireOp",EDGE,"E2434"),sQuery(id+"F1.wireOp",EDGE,"E2435"),sQuery(id+"F1.wireOp",EDGE,"E2436"),sQuery(id+"F1.wireOp",EDGE,"E2437"),sQuery(id+"F1.wireOp",EDGE,"E2438"),sQuery(id+"F1.wireOp",EDGE,"E2439"),sQuery(id+"F1.wireOp",EDGE,"E2440"),sQuery(id+"F1.wireOp",EDGE,"E2441"),sQuery(id+"F1.wireOp",EDGE,"E2442"),sQuery(id+"F1.wireOp",EDGE,"E2443"),sQuery(id+"F1.wireOp",EDGE,"E2444"),sQuery(id+"F1.wireOp",EDGE,"E2445"),sQuery(id+"F1.wireOp",EDGE,"E2446"),sQuery(id+"F1.wireOp",EDGE,"E2447"),sQuery(id+"F1.wireOp",EDGE,"E2448"),sQuery(id+"F1.wireOp",EDGE,"E2449"),sQuery(id+"F1.wireOp",EDGE,"E2450"),sQuery(id+"F1.wireOp",EDGE,"E2451"),sQuery(id+"F1.wireOp",EDGE,"E2452"),sQuery(id+"F1.wireOp",EDGE,"E2453"),sQuery(id+"F1.wireOp",EDGE,"E2454"),sQuery(id+"F1.wireOp",EDGE,"E2455"),sQuery(id+"F1.wireOp",EDGE,"E2456"),sQuery(id+"F1.wireOp",EDGE,"E2457"),sQuery(id+"F1.wireOp",EDGE,"E2458"),sQuery(id+"F1.wireOp",EDGE,"E2459"),sQuery(id+"F1.wireOp",EDGE,"E2460"),sQuery(id+"F1.wireOp",EDGE,"E2461"),sQuery(id+"F1.wireOp",EDGE,"E2462"),sQuery(id+"F1.wireOp",EDGE,"E2463"),sQuery(id+"F1.wireOp",EDGE,"E2464"),sQuery(id+"F1.wireOp",EDGE,"E2465"),sQuery(id+"F1.wireOp",EDGE,"E2466"),sQuery(id+"F1.wireOp",EDGE,"E2467"),sQuery(id+"F1.wireOp",EDGE,"E2468"),sQuery(id+"F1.wireOp",EDGE,"E2469"),sQuery(id+"F1.wireOp",EDGE,"E2470"),sQuery(id+"F1.wireOp",EDGE,"E2471"),sQuery(id+"F1.wireOp",EDGE,"E2472"),sQuery(id+"F1.wireOp",EDGE,"E2473"),sQuery(id+"F1.wireOp",EDGE,"E2474"),sQuery(id+"F1.wireOp",EDGE,"E2475"),sQuery(id+"F1.wireOp",EDGE,"E2476"),sQuery(id+"F1.wireOp",EDGE,"E2477"),sQuery(id+"F1.wireOp",EDGE,"E2478"),sQuery(id+"F1.wireOp",EDGE,"E2479"),sQuery(id+"F1.wireOp",EDGE,"E2480"),sQuery(id+"F1.wireOp",EDGE,"E2481"),sQuery(id+"F1.wireOp",EDGE,"E2482"),sQuery(id+"F1.wireOp",EDGE,"E2483"),sQuery(id+"F1.wireOp",EDGE,"E2484"),sQuery(id+"F1.wireOp",EDGE,"E2485"),sQuery(id+"F1.wireOp",EDGE,"E2486"),sQuery(id+"F1.wireOp",EDGE,"E2487"),sQuery(id+"F1.wireOp",EDGE,"E2488"),sQuery(id+"F1.wireOp",EDGE,"E2489"),sQuery(id+"F1.wireOp",EDGE,"E2490"),sQuery(id+"F1.wireOp",EDGE,"E2491"),sQuery(id+"F1.wireOp",EDGE,"E2492"),sQuery(id+"F1.wireOp",EDGE,"E2493"),sQuery(id+"F1.wireOp",EDGE,"E2494"),sQuery(id+"F1.wireOp",EDGE,"E2495"),sQuery(id+"F1.wireOp",EDGE,"E2496"),sQuery(id+"F1.wireOp",EDGE,"E2497"),sQuery(id+"F1.wireOp",EDGE,"E2498"),sQuery(id+"F1.wireOp",EDGE,"E2499"),sQuery(id+"F1.wireOp",EDGE,"E2500"),sQuery(id+"F1.wireOp",EDGE,"E2501"),sQuery(id+"F1.wireOp",EDGE,"E2502"),sQuery(id+"F1.wireOp",EDGE,"E2503"),sQuery(id+"F1.wireOp",EDGE,"E2504"),sQuery(id+"F1.wireOp",EDGE,"E2505"),sQuery(id+"F1.wireOp",EDGE,"E2506"),sQuery(id+"F1.wireOp",EDGE,"E2507"),sQuery(id+"F1.wireOp",EDGE,"E2508"),sQuery(id+"F1.wireOp",EDGE,"E2509"),sQuery(id+"F1.wireOp",EDGE,"E2510"),sQuery(id+"F1.wireOp",EDGE,"E2511"),sQuery(id+"F1.wireOp",EDGE,"E2512"),sQuery(id+"F1.wireOp",EDGE,"E2513"),sQuery(id+"F1.wireOp",EDGE,"E2514"),sQuery(id+"F1.wireOp",EDGE,"E2515"),sQuery(id+"F1.wireOp",EDGE,"E2516"),sQuery(id+"F1.wireOp",EDGE,"E2517"),sQuery(id+"F1.wireOp",EDGE,"E2518"),sQuery(id+"F1.wireOp",EDGE,"E2519"),sQuery(id+"F1.wireOp",EDGE,"E2520"),sQuery(id+"F1.wireOp",EDGE,"E2521"),sQuery(id+"F1.wireOp",EDGE,"E2522"),sQuery(id+"F1.wireOp",EDGE,"E2523"),sQuery(id+"F1.wireOp",EDGE,"E2524"),sQuery(id+"F1.wireOp",EDGE,"E2525"),sQuery(id+"F1.wireOp",EDGE,"E2526"),sQuery(id+"F1.wireOp",EDGE,"E2527"),sQuery(id+"F1.wireOp",EDGE,"E2528"),sQuery(id+"F1.wireOp",EDGE,"E2529"),sQuery(id+"F1.wireOp",EDGE,"E2530"),sQuery(id+"F1.wireOp",EDGE,"E2531"),sQuery(id+"F1.wireOp",EDGE,"E2532"),sQuery(id+"F1.wireOp",EDGE,"E2533"),sQuery(id+"F1.wireOp",EDGE,"E2534"),sQuery(id+"F1.wireOp",EDGE,"E2535"),sQuery(id+"F1.wireOp",EDGE,"E2536"),sQuery(id+"F1.wireOp",EDGE,"E2537"),sQuery(id+"F1.wireOp",EDGE,"E2538"),sQuery(id+"F1.wireOp",EDGE,"E2539"),sQuery(id+"F1.wireOp",EDGE,"E2540"),sQuery(id+"F1.wireOp",EDGE,"E2541"),sQuery(id+"F1.wireOp",EDGE,"E2542"),sQuery(id+"F1.wireOp",EDGE,"E2543"),sQuery(id+"F1.wireOp",EDGE,"E2544"),sQuery(id+"F1.wireOp",EDGE,"E2545"),sQuery(id+"F1.wireOp",EDGE,"E2546"),sQuery(id+"F1.wireOp",EDGE,"E2547"),sQuery(id+"F1.wireOp",EDGE,"E2548"),sQuery(id+"F1.wireOp",EDGE,"E2549"),sQuery(id+"F1.wireOp",EDGE,"E2550"),sQuery(id+"F1.wireOp",EDGE,"E2551"),sQuery(id+"F1.wireOp",EDGE,"E2552"),sQuery(id+"F1.wireOp",EDGE,"E2553"),sQuery(id+"F1.wireOp",EDGE,"E2554"),sQuery(id+"F1.wireOp",EDGE,"E2555"),sQuery(id+"F1.wireOp",EDGE,"E2556"),sQuery(id+"F1.wireOp",EDGE,"E2557"),sQuery(id+"F1.wireOp",EDGE,"E2558"),sQuery(id+"F1.wireOp",EDGE,"E2559"),sQuery(id+"F1.wireOp",EDGE,"E2560"),sQuery(id+"F1.wireOp",EDGE,"E2561"),sQuery(id+"F1.wireOp",EDGE,"E2562"),sQuery(id+"F1.wireOp",EDGE,"E2563"),sQuery(id+"F1.wireOp",EDGE,"E2564"),sQuery(id+"F1.wireOp",EDGE,"E2565"),sQuery(id+"F1.wireOp",EDGE,"E2566"),sQuery(id+"F1.wireOp",EDGE,"E2567"),sQuery(id+"F1.wireOp",EDGE,"E2568"),sQuery(id+"F1.wireOp",EDGE,"E2569"),sQuery(id+"F1.wireOp",EDGE,"E2570"),sQuery(id+"F1.wireOp",EDGE,"E2571"),sQuery(id+"F1.wireOp",EDGE,"E2572"),sQuery(id+"F1.wireOp",EDGE,"E2573"),sQuery(id+"F1.wireOp",EDGE,"E2574"),sQuery(id+"F1.wireOp",EDGE,"E2575"),sQuery(id+"F1.wireOp",EDGE,"E2576"),sQuery(id+"F1.wireOp",EDGE,"E2577"),sQuery(id+"F1.wireOp",EDGE,"E2578"),sQuery(id+"F1.wireOp",EDGE,"E2579"),sQuery(id+"F1.wireOp",EDGE,"E2580"),sQuery(id+"F1.wireOp",EDGE,"E2581"),sQuery(id+"F1.wireOp",EDGE,"E2582"),sQuery(id+"F1.wireOp",EDGE,"E2583"),sQuery(id+"F1.wireOp",EDGE,"E2584"),sQuery(id+"F1.wireOp",EDGE,"E2585"),sQuery(id+"F1.wireOp",EDGE,"E2586"),sQuery(id+"F1.wireOp",EDGE,"E2587"),sQuery(id+"F1.wireOp",EDGE,"E2588"),sQuery(id+"F1.wireOp",EDGE,"E2589"),sQuery(id+"F1.wireOp",EDGE,"E2590"),sQuery(id+"F1.wireOp",EDGE,"E2591"),sQuery(id+"F1.wireOp",EDGE,"E2592"),sQuery(id+"F1.wireOp",EDGE,"E2593"),sQuery(id+"F1.wireOp",EDGE,"E2594"),sQuery(id+"F1.wireOp",EDGE,"E2595"),sQuery(id+"F1.wireOp",EDGE,"E2596"),sQuery(id+"F1.wireOp",EDGE,"E2597"),sQuery(id+"F1.wireOp",EDGE,"E2598"),sQuery(id+"F1.wireOp",EDGE,"E2599"),sQuery(id+"F1.wireOp",EDGE,"E2600"),sQuery(id+"F1.wireOp",EDGE,"E2601"),sQuery(id+"F1.wireOp",EDGE,"E2602"),sQuery(id+"F1.wireOp",EDGE,"E2603"),sQuery(id+"F1.wireOp",EDGE,"E2604"),sQuery(id+"F1.wireOp",EDGE,"E2605"),sQuery(id+"F1.wireOp",EDGE,"E2606"),sQuery(id+"F1.wireOp",EDGE,"E2607"),sQuery(id+"F1.wireOp",EDGE,"E2608"),sQuery(id+"F1.wireOp",EDGE,"E2609"),sQuery(id+"F1.wireOp",EDGE,"E2610"),sQuery(id+"F1.wireOp",EDGE,"E2611"),sQuery(id+"F1.wireOp",EDGE,"E2612"),sQuery(id+"F1.wireOp",EDGE,"E2613"),sQuery(id+"F1.wireOp",EDGE,"E2614"),sQuery(id+"F1.wireOp",EDGE,"E2615"),sQuery(id+"F1.wireOp",EDGE,"E2616"),sQuery(id+"F1.wireOp",EDGE,"E2617"),sQuery(id+"F1.wireOp",EDGE,"E2618"),sQuery(id+"F1.wireOp",EDGE,"E2619"),sQuery(id+"F1.wireOp",EDGE,"E2620"),sQuery(id+"F1.wireOp",EDGE,"E2622")])]}),"instanceName":"1"});
            var Q1;
            Q1=sQuery(id+"F0.wireOp",VERTEX,"E0.center");
            var Q2;
            Q2=sQuery(id+"F0.wireOp",VERTEX,"E14.MirrorC.center");
            transform(context, id + "F7", {"entities" : qUnion([Q0]), "transformType" : TransformType.TRANSLATION_ENTITY, "oppositeDirectionEntity" : false, "transformLine" : qUnion([Q1, Q2]), "makeCopy" : false});
        }
        {
            var Q0;
            Q0=makeQuery(id+"F2.opExtrude","SWEPT_BODY",BODY,{"disambiguationData":[OSD([sQuery(id+"F1.wireOp",EDGE,"E15"),sQuery(id+"F1.wireOp",EDGE,"E16"),sQuery(id+"F1.wireOp",EDGE,"E17"),sQuery(id+"F1.wireOp",EDGE,"E18"),sQuery(id+"F1.wireOp",EDGE,"E19"),sQuery(id+"F1.wireOp",EDGE,"E20"),sQuery(id+"F1.wireOp",EDGE,"E21"),sQuery(id+"F1.wireOp",EDGE,"E22"),sQuery(id+"F1.wireOp",EDGE,"E23"),sQuery(id+"F1.wireOp",EDGE,"E24"),sQuery(id+"F1.wireOp",EDGE,"E25"),sQuery(id+"F1.wireOp",EDGE,"E26"),sQuery(id+"F1.wireOp",EDGE,"E27"),sQuery(id+"F1.wireOp",EDGE,"E28"),sQuery(id+"F1.wireOp",EDGE,"E29"),sQuery(id+"F1.wireOp",EDGE,"E30"),sQuery(id+"F1.wireOp",EDGE,"E31"),sQuery(id+"F1.wireOp",EDGE,"E32"),sQuery(id+"F1.wireOp",EDGE,"E33"),sQuery(id+"F1.wireOp",EDGE,"E34"),sQuery(id+"F1.wireOp",EDGE,"E35"),sQuery(id+"F1.wireOp",EDGE,"E36"),sQuery(id+"F1.wireOp",EDGE,"E37"),sQuery(id+"F1.wireOp",EDGE,"E38"),sQuery(id+"F1.wireOp",EDGE,"E39"),sQuery(id+"F1.wireOp",EDGE,"E40"),sQuery(id+"F1.wireOp",EDGE,"E41"),sQuery(id+"F1.wireOp",EDGE,"E42"),sQuery(id+"F1.wireOp",EDGE,"E43"),sQuery(id+"F1.wireOp",EDGE,"E44"),sQuery(id+"F1.wireOp",EDGE,"E45"),sQuery(id+"F1.wireOp",EDGE,"E45"),sQuery(id+"F1.wireOp",EDGE,"E46"),sQuery(id+"F1.wireOp",EDGE,"E47"),sQuery(id+"F1.wireOp",EDGE,"E48"),sQuery(id+"F1.wireOp",EDGE,"E49"),sQuery(id+"F1.wireOp",EDGE,"E50"),sQuery(id+"F1.wireOp",EDGE,"E51"),sQuery(id+"F1.wireOp",EDGE,"E52"),sQuery(id+"F1.wireOp",EDGE,"E53"),sQuery(id+"F1.wireOp",EDGE,"E54"),sQuery(id+"F1.wireOp",EDGE,"E55"),sQuery(id+"F1.wireOp",EDGE,"E56"),sQuery(id+"F1.wireOp",EDGE,"E57"),sQuery(id+"F1.wireOp",EDGE,"E58"),sQuery(id+"F1.wireOp",EDGE,"E59"),sQuery(id+"F1.wireOp",EDGE,"E60"),sQuery(id+"F1.wireOp",EDGE,"E61"),sQuery(id+"F1.wireOp",EDGE,"E62"),sQuery(id+"F1.wireOp",EDGE,"E63"),sQuery(id+"F1.wireOp",EDGE,"E64"),sQuery(id+"F1.wireOp",EDGE,"E65"),sQuery(id+"F1.wireOp",EDGE,"E66"),sQuery(id+"F1.wireOp",EDGE,"E67"),sQuery(id+"F1.wireOp",EDGE,"E68"),sQuery(id+"F1.wireOp",EDGE,"E69"),sQuery(id+"F1.wireOp",EDGE,"E70"),sQuery(id+"F1.wireOp",EDGE,"E71"),sQuery(id+"F1.wireOp",EDGE,"E72"),sQuery(id+"F1.wireOp",EDGE,"E73"),sQuery(id+"F1.wireOp",EDGE,"E74"),sQuery(id+"F1.wireOp",EDGE,"E75"),sQuery(id+"F1.wireOp",EDGE,"E76"),sQuery(id+"F1.wireOp",EDGE,"E77"),sQuery(id+"F1.wireOp",EDGE,"E78"),sQuery(id+"F1.wireOp",EDGE,"E79"),sQuery(id+"F1.wireOp",EDGE,"E80"),sQuery(id+"F1.wireOp",EDGE,"E81"),sQuery(id+"F1.wireOp",EDGE,"E82"),sQuery(id+"F1.wireOp",EDGE,"E83"),sQuery(id+"F1.wireOp",EDGE,"E84"),sQuery(id+"F1.wireOp",EDGE,"E85"),sQuery(id+"F1.wireOp",EDGE,"E86"),sQuery(id+"F1.wireOp",EDGE,"E87"),sQuery(id+"F1.wireOp",EDGE,"E88"),sQuery(id+"F1.wireOp",EDGE,"E89"),sQuery(id+"F1.wireOp",EDGE,"E90"),sQuery(id+"F1.wireOp",EDGE,"E91"),sQuery(id+"F1.wireOp",EDGE,"E92"),sQuery(id+"F1.wireOp",EDGE,"E93"),sQuery(id+"F1.wireOp",EDGE,"E94"),sQuery(id+"F1.wireOp",EDGE,"E95"),sQuery(id+"F1.wireOp",EDGE,"E96"),sQuery(id+"F1.wireOp",EDGE,"E97"),sQuery(id+"F1.wireOp",EDGE,"E98"),sQuery(id+"F1.wireOp",EDGE,"E99"),sQuery(id+"F1.wireOp",EDGE,"E100"),sQuery(id+"F1.wireOp",EDGE,"E101"),sQuery(id+"F1.wireOp",EDGE,"E102"),sQuery(id+"F1.wireOp",EDGE,"E103"),sQuery(id+"F1.wireOp",EDGE,"E104"),sQuery(id+"F1.wireOp",EDGE,"E104"),sQuery(id+"F1.wireOp",EDGE,"E105"),sQuery(id+"F1.wireOp",EDGE,"E106"),sQuery(id+"F1.wireOp",EDGE,"E107"),sQuery(id+"F1.wireOp",EDGE,"E108"),sQuery(id+"F1.wireOp",EDGE,"E109"),sQuery(id+"F1.wireOp",EDGE,"E110"),sQuery(id+"F1.wireOp",EDGE,"E111"),sQuery(id+"F1.wireOp",EDGE,"E112"),sQuery(id+"F1.wireOp",EDGE,"E113"),sQuery(id+"F1.wireOp",EDGE,"E114"),sQuery(id+"F1.wireOp",EDGE,"E115"),sQuery(id+"F1.wireOp",EDGE,"E116"),sQuery(id+"F1.wireOp",EDGE,"E117"),sQuery(id+"F1.wireOp",EDGE,"E118"),sQuery(id+"F1.wireOp",EDGE,"E119"),sQuery(id+"F1.wireOp",EDGE,"E120"),sQuery(id+"F1.wireOp",EDGE,"E121"),sQuery(id+"F1.wireOp",EDGE,"E122"),sQuery(id+"F1.wireOp",EDGE,"E123"),sQuery(id+"F1.wireOp",EDGE,"E124"),sQuery(id+"F1.wireOp",EDGE,"E125"),sQuery(id+"F1.wireOp",EDGE,"E126"),sQuery(id+"F1.wireOp",EDGE,"E127"),sQuery(id+"F1.wireOp",EDGE,"E128"),sQuery(id+"F1.wireOp",EDGE,"E129"),sQuery(id+"F1.wireOp",EDGE,"E130"),sQuery(id+"F1.wireOp",EDGE,"E131"),sQuery(id+"F1.wireOp",EDGE,"E132"),sQuery(id+"F1.wireOp",EDGE,"E133"),sQuery(id+"F1.wireOp",EDGE,"E134"),sQuery(id+"F1.wireOp",EDGE,"E135"),sQuery(id+"F1.wireOp",EDGE,"E136"),sQuery(id+"F1.wireOp",EDGE,"E137"),sQuery(id+"F1.wireOp",EDGE,"E138"),sQuery(id+"F1.wireOp",EDGE,"E139"),sQuery(id+"F1.wireOp",EDGE,"E140"),sQuery(id+"F1.wireOp",EDGE,"E141"),sQuery(id+"F1.wireOp",EDGE,"E142"),sQuery(id+"F1.wireOp",EDGE,"E143"),sQuery(id+"F1.wireOp",EDGE,"E144"),sQuery(id+"F1.wireOp",EDGE,"E145"),sQuery(id+"F1.wireOp",EDGE,"E146"),sQuery(id+"F1.wireOp",EDGE,"E147"),sQuery(id+"F1.wireOp",EDGE,"E148"),sQuery(id+"F1.wireOp",EDGE,"E149"),sQuery(id+"F1.wireOp",EDGE,"E150"),sQuery(id+"F1.wireOp",EDGE,"E151"),sQuery(id+"F1.wireOp",EDGE,"E152"),sQuery(id+"F1.wireOp",EDGE,"E153"),sQuery(id+"F1.wireOp",EDGE,"E154"),sQuery(id+"F1.wireOp",EDGE,"E155"),sQuery(id+"F1.wireOp",EDGE,"E156"),sQuery(id+"F1.wireOp",EDGE,"E157"),sQuery(id+"F1.wireOp",EDGE,"E158"),sQuery(id+"F1.wireOp",EDGE,"E159"),sQuery(id+"F1.wireOp",EDGE,"E160"),sQuery(id+"F1.wireOp",EDGE,"E161"),sQuery(id+"F1.wireOp",EDGE,"E162"),sQuery(id+"F1.wireOp",EDGE,"E163"),sQuery(id+"F1.wireOp",EDGE,"E164"),sQuery(id+"F1.wireOp",EDGE,"E165"),sQuery(id+"F1.wireOp",EDGE,"E166"),sQuery(id+"F1.wireOp",EDGE,"E167"),sQuery(id+"F1.wireOp",EDGE,"E168"),sQuery(id+"F1.wireOp",EDGE,"E169"),sQuery(id+"F1.wireOp",EDGE,"E170"),sQuery(id+"F1.wireOp",EDGE,"E171"),sQuery(id+"F1.wireOp",EDGE,"E172"),sQuery(id+"F1.wireOp",EDGE,"E173"),sQuery(id+"F1.wireOp",EDGE,"E174"),sQuery(id+"F1.wireOp",EDGE,"E175"),sQuery(id+"F1.wireOp",EDGE,"E176"),sQuery(id+"F1.wireOp",EDGE,"E177"),sQuery(id+"F1.wireOp",EDGE,"E178"),sQuery(id+"F1.wireOp",EDGE,"E179"),sQuery(id+"F1.wireOp",EDGE,"E180"),sQuery(id+"F1.wireOp",EDGE,"E181"),sQuery(id+"F1.wireOp",EDGE,"E182"),sQuery(id+"F1.wireOp",EDGE,"E183"),sQuery(id+"F1.wireOp",EDGE,"E184"),sQuery(id+"F1.wireOp",EDGE,"E185"),sQuery(id+"F1.wireOp",EDGE,"E186"),sQuery(id+"F1.wireOp",EDGE,"E187"),sQuery(id+"F1.wireOp",EDGE,"E188"),sQuery(id+"F1.wireOp",EDGE,"E189"),sQuery(id+"F1.wireOp",EDGE,"E190"),sQuery(id+"F1.wireOp",EDGE,"E191"),sQuery(id+"F1.wireOp",EDGE,"E192"),sQuery(id+"F1.wireOp",EDGE,"E193"),sQuery(id+"F1.wireOp",EDGE,"E194"),sQuery(id+"F1.wireOp",EDGE,"E195"),sQuery(id+"F1.wireOp",EDGE,"E196"),sQuery(id+"F1.wireOp",EDGE,"E197"),sQuery(id+"F1.wireOp",EDGE,"E198"),sQuery(id+"F1.wireOp",EDGE,"E199"),sQuery(id+"F1.wireOp",EDGE,"E200"),sQuery(id+"F1.wireOp",EDGE,"E201"),sQuery(id+"F1.wireOp",EDGE,"E202"),sQuery(id+"F1.wireOp",EDGE,"E203"),sQuery(id+"F1.wireOp",EDGE,"E204"),sQuery(id+"F1.wireOp",EDGE,"E205"),sQuery(id+"F1.wireOp",EDGE,"E206"),sQuery(id+"F1.wireOp",EDGE,"E207"),sQuery(id+"F1.wireOp",EDGE,"E208"),sQuery(id+"F1.wireOp",EDGE,"E209"),sQuery(id+"F1.wireOp",EDGE,"E210"),sQuery(id+"F1.wireOp",EDGE,"E211"),sQuery(id+"F1.wireOp",EDGE,"E212"),sQuery(id+"F1.wireOp",EDGE,"E213"),sQuery(id+"F1.wireOp",EDGE,"E214"),sQuery(id+"F1.wireOp",EDGE,"E215"),sQuery(id+"F1.wireOp",EDGE,"E216"),sQuery(id+"F1.wireOp",EDGE,"E217"),sQuery(id+"F1.wireOp",EDGE,"E218"),sQuery(id+"F1.wireOp",EDGE,"E219"),sQuery(id+"F1.wireOp",EDGE,"E220"),sQuery(id+"F1.wireOp",EDGE,"E221"),sQuery(id+"F1.wireOp",EDGE,"E222"),sQuery(id+"F1.wireOp",EDGE,"E223"),sQuery(id+"F1.wireOp",EDGE,"E224"),sQuery(id+"F1.wireOp",EDGE,"E225"),sQuery(id+"F1.wireOp",EDGE,"E226"),sQuery(id+"F1.wireOp",EDGE,"E227"),sQuery(id+"F1.wireOp",EDGE,"E228"),sQuery(id+"F1.wireOp",EDGE,"E229"),sQuery(id+"F1.wireOp",EDGE,"E230"),sQuery(id+"F1.wireOp",EDGE,"E231"),sQuery(id+"F1.wireOp",EDGE,"E232"),sQuery(id+"F1.wireOp",EDGE,"E233"),sQuery(id+"F1.wireOp",EDGE,"E234"),sQuery(id+"F1.wireOp",EDGE,"E235"),sQuery(id+"F1.wireOp",EDGE,"E236"),sQuery(id+"F1.wireOp",EDGE,"E237"),sQuery(id+"F1.wireOp",EDGE,"E238"),sQuery(id+"F1.wireOp",EDGE,"E239"),sQuery(id+"F1.wireOp",EDGE,"E240"),sQuery(id+"F1.wireOp",EDGE,"E241"),sQuery(id+"F1.wireOp",EDGE,"E242"),sQuery(id+"F1.wireOp",EDGE,"E243"),sQuery(id+"F1.wireOp",EDGE,"E244"),sQuery(id+"F1.wireOp",EDGE,"E245"),sQuery(id+"F1.wireOp",EDGE,"E246"),sQuery(id+"F1.wireOp",EDGE,"E247"),sQuery(id+"F1.wireOp",EDGE,"E248"),sQuery(id+"F1.wireOp",EDGE,"E249"),sQuery(id+"F1.wireOp",EDGE,"E250"),sQuery(id+"F1.wireOp",EDGE,"E251"),sQuery(id+"F1.wireOp",EDGE,"E252"),sQuery(id+"F1.wireOp",EDGE,"E253"),sQuery(id+"F1.wireOp",EDGE,"E254"),sQuery(id+"F1.wireOp",EDGE,"E255"),sQuery(id+"F1.wireOp",EDGE,"E256"),sQuery(id+"F1.wireOp",EDGE,"E257"),sQuery(id+"F1.wireOp",EDGE,"E258"),sQuery(id+"F1.wireOp",EDGE,"E259"),sQuery(id+"F1.wireOp",EDGE,"E260"),sQuery(id+"F1.wireOp",EDGE,"E261"),sQuery(id+"F1.wireOp",EDGE,"E262"),sQuery(id+"F1.wireOp",EDGE,"E263"),sQuery(id+"F1.wireOp",EDGE,"E264"),sQuery(id+"F1.wireOp",EDGE,"E265"),sQuery(id+"F1.wireOp",EDGE,"E266"),sQuery(id+"F1.wireOp",EDGE,"E267"),sQuery(id+"F1.wireOp",EDGE,"E268"),sQuery(id+"F1.wireOp",EDGE,"E269"),sQuery(id+"F1.wireOp",EDGE,"E270"),sQuery(id+"F1.wireOp",EDGE,"E271"),sQuery(id+"F1.wireOp",EDGE,"E272"),sQuery(id+"F1.wireOp",EDGE,"E273"),sQuery(id+"F1.wireOp",EDGE,"E274"),sQuery(id+"F1.wireOp",EDGE,"E275"),sQuery(id+"F1.wireOp",EDGE,"E276"),sQuery(id+"F1.wireOp",EDGE,"E277"),sQuery(id+"F1.wireOp",EDGE,"E278"),sQuery(id+"F1.wireOp",EDGE,"E279"),sQuery(id+"F1.wireOp",EDGE,"E280"),sQuery(id+"F1.wireOp",EDGE,"E281"),sQuery(id+"F1.wireOp",EDGE,"E282"),sQuery(id+"F1.wireOp",EDGE,"E283"),sQuery(id+"F1.wireOp",EDGE,"E284"),sQuery(id+"F1.wireOp",EDGE,"E285"),sQuery(id+"F1.wireOp",EDGE,"E286"),sQuery(id+"F1.wireOp",EDGE,"E287"),sQuery(id+"F1.wireOp",EDGE,"E288"),sQuery(id+"F1.wireOp",EDGE,"E289"),sQuery(id+"F1.wireOp",EDGE,"E290"),sQuery(id+"F1.wireOp",EDGE,"E291"),sQuery(id+"F1.wireOp",EDGE,"E292"),sQuery(id+"F1.wireOp",EDGE,"E293"),sQuery(id+"F1.wireOp",EDGE,"E294"),sQuery(id+"F1.wireOp",EDGE,"E295"),sQuery(id+"F1.wireOp",EDGE,"E296"),sQuery(id+"F1.wireOp",EDGE,"E297"),sQuery(id+"F1.wireOp",EDGE,"E298"),sQuery(id+"F1.wireOp",EDGE,"E299"),sQuery(id+"F1.wireOp",EDGE,"E300"),sQuery(id+"F1.wireOp",EDGE,"E301"),sQuery(id+"F1.wireOp",EDGE,"E302"),sQuery(id+"F1.wireOp",EDGE,"E303"),sQuery(id+"F1.wireOp",EDGE,"E304"),sQuery(id+"F1.wireOp",EDGE,"E305"),sQuery(id+"F1.wireOp",EDGE,"E306"),sQuery(id+"F1.wireOp",EDGE,"E307"),sQuery(id+"F1.wireOp",EDGE,"E308"),sQuery(id+"F1.wireOp",EDGE,"E309"),sQuery(id+"F1.wireOp",EDGE,"E310"),sQuery(id+"F1.wireOp",EDGE,"E311"),sQuery(id+"F1.wireOp",EDGE,"E312"),sQuery(id+"F1.wireOp",EDGE,"E313"),sQuery(id+"F1.wireOp",EDGE,"E314"),sQuery(id+"F1.wireOp",EDGE,"E315"),sQuery(id+"F1.wireOp",EDGE,"E316"),sQuery(id+"F1.wireOp",EDGE,"E317"),sQuery(id+"F1.wireOp",EDGE,"E318"),sQuery(id+"F1.wireOp",EDGE,"E319"),sQuery(id+"F1.wireOp",EDGE,"E320"),sQuery(id+"F1.wireOp",EDGE,"E321"),sQuery(id+"F1.wireOp",EDGE,"E322"),sQuery(id+"F1.wireOp",EDGE,"E323"),sQuery(id+"F1.wireOp",EDGE,"E324"),sQuery(id+"F1.wireOp",EDGE,"E325"),sQuery(id+"F1.wireOp",EDGE,"E326"),sQuery(id+"F1.wireOp",EDGE,"E327"),sQuery(id+"F1.wireOp",EDGE,"E328"),sQuery(id+"F1.wireOp",EDGE,"E329"),sQuery(id+"F1.wireOp",EDGE,"E330"),sQuery(id+"F1.wireOp",EDGE,"E331"),sQuery(id+"F1.wireOp",EDGE,"E332"),sQuery(id+"F1.wireOp",EDGE,"E333"),sQuery(id+"F1.wireOp",EDGE,"E334"),sQuery(id+"F1.wireOp",EDGE,"E334"),sQuery(id+"F1.wireOp",EDGE,"E335"),sQuery(id+"F1.wireOp",EDGE,"E336"),sQuery(id+"F1.wireOp",EDGE,"E337"),sQuery(id+"F1.wireOp",EDGE,"E338"),sQuery(id+"F1.wireOp",EDGE,"E339"),sQuery(id+"F1.wireOp",EDGE,"E340"),sQuery(id+"F1.wireOp",EDGE,"E341"),sQuery(id+"F1.wireOp",EDGE,"E342"),sQuery(id+"F1.wireOp",EDGE,"E343"),sQuery(id+"F1.wireOp",EDGE,"E344"),sQuery(id+"F1.wireOp",EDGE,"E345"),sQuery(id+"F1.wireOp",EDGE,"E346"),sQuery(id+"F1.wireOp",EDGE,"E347"),sQuery(id+"F1.wireOp",EDGE,"E348"),sQuery(id+"F1.wireOp",EDGE,"E349"),sQuery(id+"F1.wireOp",EDGE,"E350"),sQuery(id+"F1.wireOp",EDGE,"E351"),sQuery(id+"F1.wireOp",EDGE,"E352"),sQuery(id+"F1.wireOp",EDGE,"E353"),sQuery(id+"F1.wireOp",EDGE,"E354"),sQuery(id+"F1.wireOp",EDGE,"E355"),sQuery(id+"F1.wireOp",EDGE,"E356"),sQuery(id+"F1.wireOp",EDGE,"E357"),sQuery(id+"F1.wireOp",EDGE,"E358"),sQuery(id+"F1.wireOp",EDGE,"E359"),sQuery(id+"F1.wireOp",EDGE,"E360"),sQuery(id+"F1.wireOp",EDGE,"E361"),sQuery(id+"F1.wireOp",EDGE,"E362"),sQuery(id+"F1.wireOp",EDGE,"E363"),sQuery(id+"F1.wireOp",EDGE,"E364"),sQuery(id+"F1.wireOp",EDGE,"E365"),sQuery(id+"F1.wireOp",EDGE,"E366"),sQuery(id+"F1.wireOp",EDGE,"E367"),sQuery(id+"F1.wireOp",EDGE,"E368"),sQuery(id+"F1.wireOp",EDGE,"E369"),sQuery(id+"F1.wireOp",EDGE,"E370"),sQuery(id+"F1.wireOp",EDGE,"E371"),sQuery(id+"F1.wireOp",EDGE,"E372"),sQuery(id+"F1.wireOp",EDGE,"E373"),sQuery(id+"F1.wireOp",EDGE,"E374"),sQuery(id+"F1.wireOp",EDGE,"E375"),sQuery(id+"F1.wireOp",EDGE,"E376"),sQuery(id+"F1.wireOp",EDGE,"E377"),sQuery(id+"F1.wireOp",EDGE,"E378"),sQuery(id+"F1.wireOp",EDGE,"E379"),sQuery(id+"F1.wireOp",EDGE,"E380"),sQuery(id+"F1.wireOp",EDGE,"E381"),sQuery(id+"F1.wireOp",EDGE,"E382"),sQuery(id+"F1.wireOp",EDGE,"E383"),sQuery(id+"F1.wireOp",EDGE,"E384"),sQuery(id+"F1.wireOp",EDGE,"E385"),sQuery(id+"F1.wireOp",EDGE,"E386"),sQuery(id+"F1.wireOp",EDGE,"E387"),sQuery(id+"F1.wireOp",EDGE,"E388"),sQuery(id+"F1.wireOp",EDGE,"E389"),sQuery(id+"F1.wireOp",EDGE,"E390"),sQuery(id+"F1.wireOp",EDGE,"E391"),sQuery(id+"F1.wireOp",EDGE,"E392"),sQuery(id+"F1.wireOp",EDGE,"E393"),sQuery(id+"F1.wireOp",EDGE,"E394"),sQuery(id+"F1.wireOp",EDGE,"E395"),sQuery(id+"F1.wireOp",EDGE,"E396"),sQuery(id+"F1.wireOp",EDGE,"E397"),sQuery(id+"F1.wireOp",EDGE,"E398"),sQuery(id+"F1.wireOp",EDGE,"E399"),sQuery(id+"F1.wireOp",EDGE,"E400"),sQuery(id+"F1.wireOp",EDGE,"E401"),sQuery(id+"F1.wireOp",EDGE,"E402"),sQuery(id+"F1.wireOp",EDGE,"E403"),sQuery(id+"F1.wireOp",EDGE,"E404"),sQuery(id+"F1.wireOp",EDGE,"E405"),sQuery(id+"F1.wireOp",EDGE,"E406"),sQuery(id+"F1.wireOp",EDGE,"E407"),sQuery(id+"F1.wireOp",EDGE,"E408"),sQuery(id+"F1.wireOp",EDGE,"E409"),sQuery(id+"F1.wireOp",EDGE,"E410"),sQuery(id+"F1.wireOp",EDGE,"E411"),sQuery(id+"F1.wireOp",EDGE,"E412"),sQuery(id+"F1.wireOp",EDGE,"E413"),sQuery(id+"F1.wireOp",EDGE,"E414"),sQuery(id+"F1.wireOp",EDGE,"E415"),sQuery(id+"F1.wireOp",EDGE,"E416"),sQuery(id+"F1.wireOp",EDGE,"E417"),sQuery(id+"F1.wireOp",EDGE,"E418"),sQuery(id+"F1.wireOp",EDGE,"E419"),sQuery(id+"F1.wireOp",EDGE,"E420"),sQuery(id+"F1.wireOp",EDGE,"E421"),sQuery(id+"F1.wireOp",EDGE,"E422"),sQuery(id+"F1.wireOp",EDGE,"E423"),sQuery(id+"F1.wireOp",EDGE,"E424"),sQuery(id+"F1.wireOp",EDGE,"E425"),sQuery(id+"F1.wireOp",EDGE,"E426"),sQuery(id+"F1.wireOp",EDGE,"E426"),sQuery(id+"F1.wireOp",EDGE,"E427"),sQuery(id+"F1.wireOp",EDGE,"E428"),sQuery(id+"F1.wireOp",EDGE,"E429"),sQuery(id+"F1.wireOp",EDGE,"E430"),sQuery(id+"F1.wireOp",EDGE,"E431"),sQuery(id+"F1.wireOp",EDGE,"E432"),sQuery(id+"F1.wireOp",EDGE,"E433"),sQuery(id+"F1.wireOp",EDGE,"E434"),sQuery(id+"F1.wireOp",EDGE,"E435"),sQuery(id+"F1.wireOp",EDGE,"E435"),sQuery(id+"F1.wireOp",EDGE,"E436"),sQuery(id+"F1.wireOp",EDGE,"E437"),sQuery(id+"F1.wireOp",EDGE,"E438"),sQuery(id+"F1.wireOp",EDGE,"E439"),sQuery(id+"F1.wireOp",EDGE,"E440"),sQuery(id+"F1.wireOp",EDGE,"E441"),sQuery(id+"F1.wireOp",EDGE,"E442"),sQuery(id+"F1.wireOp",EDGE,"E443"),sQuery(id+"F1.wireOp",EDGE,"E444"),sQuery(id+"F1.wireOp",EDGE,"E445"),sQuery(id+"F1.wireOp",EDGE,"E446"),sQuery(id+"F1.wireOp",EDGE,"E447"),sQuery(id+"F1.wireOp",EDGE,"E448"),sQuery(id+"F1.wireOp",EDGE,"E449"),sQuery(id+"F1.wireOp",EDGE,"E450"),sQuery(id+"F1.wireOp",EDGE,"E451"),sQuery(id+"F1.wireOp",EDGE,"E452"),sQuery(id+"F1.wireOp",EDGE,"E453"),sQuery(id+"F1.wireOp",EDGE,"E454"),sQuery(id+"F1.wireOp",EDGE,"E455"),sQuery(id+"F1.wireOp",EDGE,"E456"),sQuery(id+"F1.wireOp",EDGE,"E457"),sQuery(id+"F1.wireOp",EDGE,"E458"),sQuery(id+"F1.wireOp",EDGE,"E459"),sQuery(id+"F1.wireOp",EDGE,"E460"),sQuery(id+"F1.wireOp",EDGE,"E461"),sQuery(id+"F1.wireOp",EDGE,"E462"),sQuery(id+"F1.wireOp",EDGE,"E463"),sQuery(id+"F1.wireOp",EDGE,"E464"),sQuery(id+"F1.wireOp",EDGE,"E465"),sQuery(id+"F1.wireOp",EDGE,"E466"),sQuery(id+"F1.wireOp",EDGE,"E467"),sQuery(id+"F1.wireOp",EDGE,"E468"),sQuery(id+"F1.wireOp",EDGE,"E469"),sQuery(id+"F1.wireOp",EDGE,"E470"),sQuery(id+"F1.wireOp",EDGE,"E471"),sQuery(id+"F1.wireOp",EDGE,"E472"),sQuery(id+"F1.wireOp",EDGE,"E473"),sQuery(id+"F1.wireOp",EDGE,"E474"),sQuery(id+"F1.wireOp",EDGE,"E475"),sQuery(id+"F1.wireOp",EDGE,"E476"),sQuery(id+"F1.wireOp",EDGE,"E477"),sQuery(id+"F1.wireOp",EDGE,"E478"),sQuery(id+"F1.wireOp",EDGE,"E479"),sQuery(id+"F1.wireOp",EDGE,"E480"),sQuery(id+"F1.wireOp",EDGE,"E481"),sQuery(id+"F1.wireOp",EDGE,"E482"),sQuery(id+"F1.wireOp",EDGE,"E483"),sQuery(id+"F1.wireOp",EDGE,"E484"),sQuery(id+"F1.wireOp",EDGE,"E485"),sQuery(id+"F1.wireOp",EDGE,"E486"),sQuery(id+"F1.wireOp",EDGE,"E487"),sQuery(id+"F1.wireOp",EDGE,"E488"),sQuery(id+"F1.wireOp",EDGE,"E489"),sQuery(id+"F1.wireOp",EDGE,"E490"),sQuery(id+"F1.wireOp",EDGE,"E491"),sQuery(id+"F1.wireOp",EDGE,"E492"),sQuery(id+"F1.wireOp",EDGE,"E493"),sQuery(id+"F1.wireOp",EDGE,"E494"),sQuery(id+"F1.wireOp",EDGE,"E495"),sQuery(id+"F1.wireOp",EDGE,"E496"),sQuery(id+"F1.wireOp",EDGE,"E497"),sQuery(id+"F1.wireOp",EDGE,"E498"),sQuery(id+"F1.wireOp",EDGE,"E499"),sQuery(id+"F1.wireOp",EDGE,"E500"),sQuery(id+"F1.wireOp",EDGE,"E501"),sQuery(id+"F1.wireOp",EDGE,"E502"),sQuery(id+"F1.wireOp",EDGE,"E503"),sQuery(id+"F1.wireOp",EDGE,"E504"),sQuery(id+"F1.wireOp",EDGE,"E505"),sQuery(id+"F1.wireOp",EDGE,"E506"),sQuery(id+"F1.wireOp",EDGE,"E507"),sQuery(id+"F1.wireOp",EDGE,"E508"),sQuery(id+"F1.wireOp",EDGE,"E509"),sQuery(id+"F1.wireOp",EDGE,"E510"),sQuery(id+"F1.wireOp",EDGE,"E511"),sQuery(id+"F1.wireOp",EDGE,"E512"),sQuery(id+"F1.wireOp",EDGE,"E513"),sQuery(id+"F1.wireOp",EDGE,"E514"),sQuery(id+"F1.wireOp",EDGE,"E515"),sQuery(id+"F1.wireOp",EDGE,"E516"),sQuery(id+"F1.wireOp",EDGE,"E517"),sQuery(id+"F1.wireOp",EDGE,"E518"),sQuery(id+"F1.wireOp",EDGE,"E519"),sQuery(id+"F1.wireOp",EDGE,"E520"),sQuery(id+"F1.wireOp",EDGE,"E521"),sQuery(id+"F1.wireOp",EDGE,"E522"),sQuery(id+"F1.wireOp",EDGE,"E523"),sQuery(id+"F1.wireOp",EDGE,"E524"),sQuery(id+"F1.wireOp",EDGE,"E525"),sQuery(id+"F1.wireOp",EDGE,"E526"),sQuery(id+"F1.wireOp",EDGE,"E527"),sQuery(id+"F1.wireOp",EDGE,"E528"),sQuery(id+"F1.wireOp",EDGE,"E529"),sQuery(id+"F1.wireOp",EDGE,"E530"),sQuery(id+"F1.wireOp",EDGE,"E531"),sQuery(id+"F1.wireOp",EDGE,"E532"),sQuery(id+"F1.wireOp",EDGE,"E533"),sQuery(id+"F1.wireOp",EDGE,"E534"),sQuery(id+"F1.wireOp",EDGE,"E534"),sQuery(id+"F1.wireOp",EDGE,"E535"),sQuery(id+"F1.wireOp",EDGE,"E536"),sQuery(id+"F1.wireOp",EDGE,"E537"),sQuery(id+"F1.wireOp",EDGE,"E538"),sQuery(id+"F1.wireOp",EDGE,"E539"),sQuery(id+"F1.wireOp",EDGE,"E540"),sQuery(id+"F1.wireOp",EDGE,"E541"),sQuery(id+"F1.wireOp",EDGE,"E542"),sQuery(id+"F1.wireOp",EDGE,"E543"),sQuery(id+"F1.wireOp",EDGE,"E544"),sQuery(id+"F1.wireOp",EDGE,"E545"),sQuery(id+"F1.wireOp",EDGE,"E546"),sQuery(id+"F1.wireOp",EDGE,"E547"),sQuery(id+"F1.wireOp",EDGE,"E548"),sQuery(id+"F1.wireOp",EDGE,"E549"),sQuery(id+"F1.wireOp",EDGE,"E550"),sQuery(id+"F1.wireOp",EDGE,"E551"),sQuery(id+"F1.wireOp",EDGE,"E552"),sQuery(id+"F1.wireOp",EDGE,"E553"),sQuery(id+"F1.wireOp",EDGE,"E554"),sQuery(id+"F1.wireOp",EDGE,"E555"),sQuery(id+"F1.wireOp",EDGE,"E556"),sQuery(id+"F1.wireOp",EDGE,"E557"),sQuery(id+"F1.wireOp",EDGE,"E558"),sQuery(id+"F1.wireOp",EDGE,"E559"),sQuery(id+"F1.wireOp",EDGE,"E560"),sQuery(id+"F1.wireOp",EDGE,"E561"),sQuery(id+"F1.wireOp",EDGE,"E562"),sQuery(id+"F1.wireOp",EDGE,"E563"),sQuery(id+"F1.wireOp",EDGE,"E564"),sQuery(id+"F1.wireOp",EDGE,"E565"),sQuery(id+"F1.wireOp",EDGE,"E566"),sQuery(id+"F1.wireOp",EDGE,"E567"),sQuery(id+"F1.wireOp",EDGE,"E568"),sQuery(id+"F1.wireOp",EDGE,"E569"),sQuery(id+"F1.wireOp",EDGE,"E570"),sQuery(id+"F1.wireOp",EDGE,"E571"),sQuery(id+"F1.wireOp",EDGE,"E572"),sQuery(id+"F1.wireOp",EDGE,"E573"),sQuery(id+"F1.wireOp",EDGE,"E574"),sQuery(id+"F1.wireOp",EDGE,"E575"),sQuery(id+"F1.wireOp",EDGE,"E576"),sQuery(id+"F1.wireOp",EDGE,"E577"),sQuery(id+"F1.wireOp",EDGE,"E578"),sQuery(id+"F1.wireOp",EDGE,"E579"),sQuery(id+"F1.wireOp",EDGE,"E580"),sQuery(id+"F1.wireOp",EDGE,"E581"),sQuery(id+"F1.wireOp",EDGE,"E582"),sQuery(id+"F1.wireOp",EDGE,"E583"),sQuery(id+"F1.wireOp",EDGE,"E584"),sQuery(id+"F1.wireOp",EDGE,"E585"),sQuery(id+"F1.wireOp",EDGE,"E586"),sQuery(id+"F1.wireOp",EDGE,"E587"),sQuery(id+"F1.wireOp",EDGE,"E588"),sQuery(id+"F1.wireOp",EDGE,"E589"),sQuery(id+"F1.wireOp",EDGE,"E590"),sQuery(id+"F1.wireOp",EDGE,"E591"),sQuery(id+"F1.wireOp",EDGE,"E592"),sQuery(id+"F1.wireOp",EDGE,"E593"),sQuery(id+"F1.wireOp",EDGE,"E594"),sQuery(id+"F1.wireOp",EDGE,"E595"),sQuery(id+"F1.wireOp",EDGE,"E596"),sQuery(id+"F1.wireOp",EDGE,"E597"),sQuery(id+"F1.wireOp",EDGE,"E598"),sQuery(id+"F1.wireOp",EDGE,"E599"),sQuery(id+"F1.wireOp",EDGE,"E600"),sQuery(id+"F1.wireOp",EDGE,"E601"),sQuery(id+"F1.wireOp",EDGE,"E602"),sQuery(id+"F1.wireOp",EDGE,"E603"),sQuery(id+"F1.wireOp",EDGE,"E604"),sQuery(id+"F1.wireOp",EDGE,"E605"),sQuery(id+"F1.wireOp",EDGE,"E606"),sQuery(id+"F1.wireOp",EDGE,"E607"),sQuery(id+"F1.wireOp",EDGE,"E608"),sQuery(id+"F1.wireOp",EDGE,"E609"),sQuery(id+"F1.wireOp",EDGE,"E610"),sQuery(id+"F1.wireOp",EDGE,"E611"),sQuery(id+"F1.wireOp",EDGE,"E612"),sQuery(id+"F1.wireOp",EDGE,"E613"),sQuery(id+"F1.wireOp",EDGE,"E614"),sQuery(id+"F1.wireOp",EDGE,"E615"),sQuery(id+"F1.wireOp",EDGE,"E616"),sQuery(id+"F1.wireOp",EDGE,"E617"),sQuery(id+"F1.wireOp",EDGE,"E618"),sQuery(id+"F1.wireOp",EDGE,"E619"),sQuery(id+"F1.wireOp",EDGE,"E620"),sQuery(id+"F1.wireOp",EDGE,"E621"),sQuery(id+"F1.wireOp",EDGE,"E622"),sQuery(id+"F1.wireOp",EDGE,"E623"),sQuery(id+"F1.wireOp",EDGE,"E624"),sQuery(id+"F1.wireOp",EDGE,"E625"),sQuery(id+"F1.wireOp",EDGE,"E626"),sQuery(id+"F1.wireOp",EDGE,"E627"),sQuery(id+"F1.wireOp",EDGE,"E628"),sQuery(id+"F1.wireOp",EDGE,"E629"),sQuery(id+"F1.wireOp",EDGE,"E630"),sQuery(id+"F1.wireOp",EDGE,"E631"),sQuery(id+"F1.wireOp",EDGE,"E632"),sQuery(id+"F1.wireOp",EDGE,"E633"),sQuery(id+"F1.wireOp",EDGE,"E634"),sQuery(id+"F1.wireOp",EDGE,"E635"),sQuery(id+"F1.wireOp",EDGE,"E636"),sQuery(id+"F1.wireOp",EDGE,"E637"),sQuery(id+"F1.wireOp",EDGE,"E638"),sQuery(id+"F1.wireOp",EDGE,"E639"),sQuery(id+"F1.wireOp",EDGE,"E640"),sQuery(id+"F1.wireOp",EDGE,"E641"),sQuery(id+"F1.wireOp",EDGE,"E642"),sQuery(id+"F1.wireOp",EDGE,"E643"),sQuery(id+"F1.wireOp",EDGE,"E644"),sQuery(id+"F1.wireOp",EDGE,"E645"),sQuery(id+"F1.wireOp",EDGE,"E646"),sQuery(id+"F1.wireOp",EDGE,"E647"),sQuery(id+"F1.wireOp",EDGE,"E648"),sQuery(id+"F1.wireOp",EDGE,"E649"),sQuery(id+"F1.wireOp",EDGE,"E650"),sQuery(id+"F1.wireOp",EDGE,"E651"),sQuery(id+"F1.wireOp",EDGE,"E652"),sQuery(id+"F1.wireOp",EDGE,"E653"),sQuery(id+"F1.wireOp",EDGE,"E654"),sQuery(id+"F1.wireOp",EDGE,"E655"),sQuery(id+"F1.wireOp",EDGE,"E656"),sQuery(id+"F1.wireOp",EDGE,"E657"),sQuery(id+"F1.wireOp",EDGE,"E658"),sQuery(id+"F1.wireOp",EDGE,"E659"),sQuery(id+"F1.wireOp",EDGE,"E660"),sQuery(id+"F1.wireOp",EDGE,"E661"),sQuery(id+"F1.wireOp",EDGE,"E662"),sQuery(id+"F1.wireOp",EDGE,"E663"),sQuery(id+"F1.wireOp",EDGE,"E664"),sQuery(id+"F1.wireOp",EDGE,"E665"),sQuery(id+"F1.wireOp",EDGE,"E666"),sQuery(id+"F1.wireOp",EDGE,"E667"),sQuery(id+"F1.wireOp",EDGE,"E668"),sQuery(id+"F1.wireOp",EDGE,"E669"),sQuery(id+"F1.wireOp",EDGE,"E670"),sQuery(id+"F1.wireOp",EDGE,"E671"),sQuery(id+"F1.wireOp",EDGE,"E672"),sQuery(id+"F1.wireOp",EDGE,"E673"),sQuery(id+"F1.wireOp",EDGE,"E674"),sQuery(id+"F1.wireOp",EDGE,"E675"),sQuery(id+"F1.wireOp",EDGE,"E676"),sQuery(id+"F1.wireOp",EDGE,"E677"),sQuery(id+"F1.wireOp",EDGE,"E678"),sQuery(id+"F1.wireOp",EDGE,"E679"),sQuery(id+"F1.wireOp",EDGE,"E680"),sQuery(id+"F1.wireOp",EDGE,"E681"),sQuery(id+"F1.wireOp",EDGE,"E682"),sQuery(id+"F1.wireOp",EDGE,"E683"),sQuery(id+"F1.wireOp",EDGE,"E684"),sQuery(id+"F1.wireOp",EDGE,"E685"),sQuery(id+"F1.wireOp",EDGE,"E686"),sQuery(id+"F1.wireOp",EDGE,"E687"),sQuery(id+"F1.wireOp",EDGE,"E688"),sQuery(id+"F1.wireOp",EDGE,"E689"),sQuery(id+"F1.wireOp",EDGE,"E690"),sQuery(id+"F1.wireOp",EDGE,"E691"),sQuery(id+"F1.wireOp",EDGE,"E692"),sQuery(id+"F1.wireOp",EDGE,"E693"),sQuery(id+"F1.wireOp",EDGE,"E694"),sQuery(id+"F1.wireOp",EDGE,"E695"),sQuery(id+"F1.wireOp",EDGE,"E696"),sQuery(id+"F1.wireOp",EDGE,"E697"),sQuery(id+"F1.wireOp",EDGE,"E698"),sQuery(id+"F1.wireOp",EDGE,"E699"),sQuery(id+"F1.wireOp",EDGE,"E700"),sQuery(id+"F1.wireOp",EDGE,"E701"),sQuery(id+"F1.wireOp",EDGE,"E702"),sQuery(id+"F1.wireOp",EDGE,"E703"),sQuery(id+"F1.wireOp",EDGE,"E704"),sQuery(id+"F1.wireOp",EDGE,"E705"),sQuery(id+"F1.wireOp",EDGE,"E706"),sQuery(id+"F1.wireOp",EDGE,"E707"),sQuery(id+"F1.wireOp",EDGE,"E708"),sQuery(id+"F1.wireOp",EDGE,"E709"),sQuery(id+"F1.wireOp",EDGE,"E710"),sQuery(id+"F1.wireOp",EDGE,"E711"),sQuery(id+"F1.wireOp",EDGE,"E712"),sQuery(id+"F1.wireOp",EDGE,"E713"),sQuery(id+"F1.wireOp",EDGE,"E714"),sQuery(id+"F1.wireOp",EDGE,"E715"),sQuery(id+"F1.wireOp",EDGE,"E716"),sQuery(id+"F1.wireOp",EDGE,"E717"),sQuery(id+"F1.wireOp",EDGE,"E718"),sQuery(id+"F1.wireOp",EDGE,"E719"),sQuery(id+"F1.wireOp",EDGE,"E720"),sQuery(id+"F1.wireOp",EDGE,"E721"),sQuery(id+"F1.wireOp",EDGE,"E722"),sQuery(id+"F1.wireOp",EDGE,"E723"),sQuery(id+"F1.wireOp",EDGE,"E724"),sQuery(id+"F1.wireOp",EDGE,"E725"),sQuery(id+"F1.wireOp",EDGE,"E726"),sQuery(id+"F1.wireOp",EDGE,"E727"),sQuery(id+"F1.wireOp",EDGE,"E728"),sQuery(id+"F1.wireOp",EDGE,"E729"),sQuery(id+"F1.wireOp",EDGE,"E730"),sQuery(id+"F1.wireOp",EDGE,"E731"),sQuery(id+"F1.wireOp",EDGE,"E732"),sQuery(id+"F1.wireOp",EDGE,"E733"),sQuery(id+"F1.wireOp",EDGE,"E734"),sQuery(id+"F1.wireOp",EDGE,"E735"),sQuery(id+"F1.wireOp",EDGE,"E736"),sQuery(id+"F1.wireOp",EDGE,"E737"),sQuery(id+"F1.wireOp",EDGE,"E738"),sQuery(id+"F1.wireOp",EDGE,"E739"),sQuery(id+"F1.wireOp",EDGE,"E740"),sQuery(id+"F1.wireOp",EDGE,"E741"),sQuery(id+"F1.wireOp",EDGE,"E742"),sQuery(id+"F1.wireOp",EDGE,"E743"),sQuery(id+"F1.wireOp",EDGE,"E744"),sQuery(id+"F1.wireOp",EDGE,"E745"),sQuery(id+"F1.wireOp",EDGE,"E746"),sQuery(id+"F1.wireOp",EDGE,"E747"),sQuery(id+"F1.wireOp",EDGE,"E748"),sQuery(id+"F1.wireOp",EDGE,"E749"),sQuery(id+"F1.wireOp",EDGE,"E750"),sQuery(id+"F1.wireOp",EDGE,"E751"),sQuery(id+"F1.wireOp",EDGE,"E752"),sQuery(id+"F1.wireOp",EDGE,"E753"),sQuery(id+"F1.wireOp",EDGE,"E754"),sQuery(id+"F1.wireOp",EDGE,"E755"),sQuery(id+"F1.wireOp",EDGE,"E756"),sQuery(id+"F1.wireOp",EDGE,"E757"),sQuery(id+"F1.wireOp",EDGE,"E758"),sQuery(id+"F1.wireOp",EDGE,"E759"),sQuery(id+"F1.wireOp",EDGE,"E760"),sQuery(id+"F1.wireOp",EDGE,"E761"),sQuery(id+"F1.wireOp",EDGE,"E762"),sQuery(id+"F1.wireOp",EDGE,"E763"),sQuery(id+"F1.wireOp",EDGE,"E764"),sQuery(id+"F1.wireOp",EDGE,"E765"),sQuery(id+"F1.wireOp",EDGE,"E766"),sQuery(id+"F1.wireOp",EDGE,"E767"),sQuery(id+"F1.wireOp",EDGE,"E768"),sQuery(id+"F1.wireOp",EDGE,"E769"),sQuery(id+"F1.wireOp",EDGE,"E770"),sQuery(id+"F1.wireOp",EDGE,"E771"),sQuery(id+"F1.wireOp",EDGE,"E772"),sQuery(id+"F1.wireOp",EDGE,"E773"),sQuery(id+"F1.wireOp",EDGE,"E774"),sQuery(id+"F1.wireOp",EDGE,"E775"),sQuery(id+"F1.wireOp",EDGE,"E776"),sQuery(id+"F1.wireOp",EDGE,"E777"),sQuery(id+"F1.wireOp",EDGE,"E778"),sQuery(id+"F1.wireOp",EDGE,"E779"),sQuery(id+"F1.wireOp",EDGE,"E780"),sQuery(id+"F1.wireOp",EDGE,"E781"),sQuery(id+"F1.wireOp",EDGE,"E782"),sQuery(id+"F1.wireOp",EDGE,"E783"),sQuery(id+"F1.wireOp",EDGE,"E784"),sQuery(id+"F1.wireOp",EDGE,"E785"),sQuery(id+"F1.wireOp",EDGE,"E786"),sQuery(id+"F1.wireOp",EDGE,"E787"),sQuery(id+"F1.wireOp",EDGE,"E788"),sQuery(id+"F1.wireOp",EDGE,"E789"),sQuery(id+"F1.wireOp",EDGE,"E790"),sQuery(id+"F1.wireOp",EDGE,"E791"),sQuery(id+"F1.wireOp",EDGE,"E792"),sQuery(id+"F1.wireOp",EDGE,"E793"),sQuery(id+"F1.wireOp",EDGE,"E794"),sQuery(id+"F1.wireOp",EDGE,"E795"),sQuery(id+"F1.wireOp",EDGE,"E796"),sQuery(id+"F1.wireOp",EDGE,"E797"),sQuery(id+"F1.wireOp",EDGE,"E798"),sQuery(id+"F1.wireOp",EDGE,"E799"),sQuery(id+"F1.wireOp",EDGE,"E800"),sQuery(id+"F1.wireOp",EDGE,"E801"),sQuery(id+"F1.wireOp",EDGE,"E802"),sQuery(id+"F1.wireOp",EDGE,"E803"),sQuery(id+"F1.wireOp",EDGE,"E804"),sQuery(id+"F1.wireOp",EDGE,"E805"),sQuery(id+"F1.wireOp",EDGE,"E806"),sQuery(id+"F1.wireOp",EDGE,"E807"),sQuery(id+"F1.wireOp",EDGE,"E808"),sQuery(id+"F1.wireOp",EDGE,"E809"),sQuery(id+"F1.wireOp",EDGE,"E810"),sQuery(id+"F1.wireOp",EDGE,"E811"),sQuery(id+"F1.wireOp",EDGE,"E812"),sQuery(id+"F1.wireOp",EDGE,"E813"),sQuery(id+"F1.wireOp",EDGE,"E814"),sQuery(id+"F1.wireOp",EDGE,"E815"),sQuery(id+"F1.wireOp",EDGE,"E816"),sQuery(id+"F1.wireOp",EDGE,"E817"),sQuery(id+"F1.wireOp",EDGE,"E818"),sQuery(id+"F1.wireOp",EDGE,"E819"),sQuery(id+"F1.wireOp",EDGE,"E820"),sQuery(id+"F1.wireOp",EDGE,"E821"),sQuery(id+"F1.wireOp",EDGE,"E822"),sQuery(id+"F1.wireOp",EDGE,"E823"),sQuery(id+"F1.wireOp",EDGE,"E824"),sQuery(id+"F1.wireOp",EDGE,"E825"),sQuery(id+"F1.wireOp",EDGE,"E826"),sQuery(id+"F1.wireOp",EDGE,"E827"),sQuery(id+"F1.wireOp",EDGE,"E828"),sQuery(id+"F1.wireOp",EDGE,"E829"),sQuery(id+"F1.wireOp",EDGE,"E830"),sQuery(id+"F1.wireOp",EDGE,"E831"),sQuery(id+"F1.wireOp",EDGE,"E832"),sQuery(id+"F1.wireOp",EDGE,"E833"),sQuery(id+"F1.wireOp",EDGE,"E834"),sQuery(id+"F1.wireOp",EDGE,"E835"),sQuery(id+"F1.wireOp",EDGE,"E836"),sQuery(id+"F1.wireOp",EDGE,"E837"),sQuery(id+"F1.wireOp",EDGE,"E838"),sQuery(id+"F1.wireOp",EDGE,"E839"),sQuery(id+"F1.wireOp",EDGE,"E840"),sQuery(id+"F1.wireOp",EDGE,"E841"),sQuery(id+"F1.wireOp",EDGE,"E842"),sQuery(id+"F1.wireOp",EDGE,"E843"),sQuery(id+"F1.wireOp",EDGE,"E844"),sQuery(id+"F1.wireOp",EDGE,"E845"),sQuery(id+"F1.wireOp",EDGE,"E846"),sQuery(id+"F1.wireOp",EDGE,"E847"),sQuery(id+"F1.wireOp",EDGE,"E848"),sQuery(id+"F1.wireOp",EDGE,"E849"),sQuery(id+"F1.wireOp",EDGE,"E850"),sQuery(id+"F1.wireOp",EDGE,"E851"),sQuery(id+"F1.wireOp",EDGE,"E852"),sQuery(id+"F1.wireOp",EDGE,"E853"),sQuery(id+"F1.wireOp",EDGE,"E854"),sQuery(id+"F1.wireOp",EDGE,"E855"),sQuery(id+"F1.wireOp",EDGE,"E856"),sQuery(id+"F1.wireOp",EDGE,"E857"),sQuery(id+"F1.wireOp",EDGE,"E858"),sQuery(id+"F1.wireOp",EDGE,"E859"),sQuery(id+"F1.wireOp",EDGE,"E860"),sQuery(id+"F1.wireOp",EDGE,"E861"),sQuery(id+"F1.wireOp",EDGE,"E862"),sQuery(id+"F1.wireOp",EDGE,"E863"),sQuery(id+"F1.wireOp",EDGE,"E864"),sQuery(id+"F1.wireOp",EDGE,"E865"),sQuery(id+"F1.wireOp",EDGE,"E866"),sQuery(id+"F1.wireOp",EDGE,"E867"),sQuery(id+"F1.wireOp",EDGE,"E868"),sQuery(id+"F1.wireOp",EDGE,"E869"),sQuery(id+"F1.wireOp",EDGE,"E870"),sQuery(id+"F1.wireOp",EDGE,"E871"),sQuery(id+"F1.wireOp",EDGE,"E872"),sQuery(id+"F1.wireOp",EDGE,"E873"),sQuery(id+"F1.wireOp",EDGE,"E873"),sQuery(id+"F1.wireOp",EDGE,"E874"),sQuery(id+"F1.wireOp",EDGE,"E875"),sQuery(id+"F1.wireOp",EDGE,"E876"),sQuery(id+"F1.wireOp",EDGE,"E877"),sQuery(id+"F1.wireOp",EDGE,"E878"),sQuery(id+"F1.wireOp",EDGE,"E879"),sQuery(id+"F1.wireOp",EDGE,"E880"),sQuery(id+"F1.wireOp",EDGE,"E881"),sQuery(id+"F1.wireOp",EDGE,"E882"),sQuery(id+"F1.wireOp",EDGE,"E883"),sQuery(id+"F1.wireOp",EDGE,"E884"),sQuery(id+"F1.wireOp",EDGE,"E885"),sQuery(id+"F1.wireOp",EDGE,"E886"),sQuery(id+"F1.wireOp",EDGE,"E887"),sQuery(id+"F1.wireOp",EDGE,"E888"),sQuery(id+"F1.wireOp",EDGE,"E889"),sQuery(id+"F1.wireOp",EDGE,"E890"),sQuery(id+"F1.wireOp",EDGE,"E891"),sQuery(id+"F1.wireOp",EDGE,"E892"),sQuery(id+"F1.wireOp",EDGE,"E893"),sQuery(id+"F1.wireOp",EDGE,"E894"),sQuery(id+"F1.wireOp",EDGE,"E895"),sQuery(id+"F1.wireOp",EDGE,"E896"),sQuery(id+"F1.wireOp",EDGE,"E897"),sQuery(id+"F1.wireOp",EDGE,"E898"),sQuery(id+"F1.wireOp",EDGE,"E899"),sQuery(id+"F1.wireOp",EDGE,"E900"),sQuery(id+"F1.wireOp",EDGE,"E901"),sQuery(id+"F1.wireOp",EDGE,"E902"),sQuery(id+"F1.wireOp",EDGE,"E903"),sQuery(id+"F1.wireOp",EDGE,"E904"),sQuery(id+"F1.wireOp",EDGE,"E905"),sQuery(id+"F1.wireOp",EDGE,"E906"),sQuery(id+"F1.wireOp",EDGE,"E907"),sQuery(id+"F1.wireOp",EDGE,"E908"),sQuery(id+"F1.wireOp",EDGE,"E909"),sQuery(id+"F1.wireOp",EDGE,"E910"),sQuery(id+"F1.wireOp",EDGE,"E911"),sQuery(id+"F1.wireOp",EDGE,"E912"),sQuery(id+"F1.wireOp",EDGE,"E913"),sQuery(id+"F1.wireOp",EDGE,"E914"),sQuery(id+"F1.wireOp",EDGE,"E915"),sQuery(id+"F1.wireOp",EDGE,"E916"),sQuery(id+"F1.wireOp",EDGE,"E917"),sQuery(id+"F1.wireOp",EDGE,"E918"),sQuery(id+"F1.wireOp",EDGE,"E919"),sQuery(id+"F1.wireOp",EDGE,"E920"),sQuery(id+"F1.wireOp",EDGE,"E921"),sQuery(id+"F1.wireOp",EDGE,"E922"),sQuery(id+"F1.wireOp",EDGE,"E923"),sQuery(id+"F1.wireOp",EDGE,"E924"),sQuery(id+"F1.wireOp",EDGE,"E925"),sQuery(id+"F1.wireOp",EDGE,"E926"),sQuery(id+"F1.wireOp",EDGE,"E927"),sQuery(id+"F1.wireOp",EDGE,"E928"),sQuery(id+"F1.wireOp",EDGE,"E929"),sQuery(id+"F1.wireOp",EDGE,"E930"),sQuery(id+"F1.wireOp",EDGE,"E931"),sQuery(id+"F1.wireOp",EDGE,"E932"),sQuery(id+"F1.wireOp",EDGE,"E933"),sQuery(id+"F1.wireOp",EDGE,"E934"),sQuery(id+"F1.wireOp",EDGE,"E935"),sQuery(id+"F1.wireOp",EDGE,"E936"),sQuery(id+"F1.wireOp",EDGE,"E937"),sQuery(id+"F1.wireOp",EDGE,"E938"),sQuery(id+"F1.wireOp",EDGE,"E939"),sQuery(id+"F1.wireOp",EDGE,"E940"),sQuery(id+"F1.wireOp",EDGE,"E941"),sQuery(id+"F1.wireOp",EDGE,"E942"),sQuery(id+"F1.wireOp",EDGE,"E943"),sQuery(id+"F1.wireOp",EDGE,"E944"),sQuery(id+"F1.wireOp",EDGE,"E945"),sQuery(id+"F1.wireOp",EDGE,"E946"),sQuery(id+"F1.wireOp",EDGE,"E947"),sQuery(id+"F1.wireOp",EDGE,"E948"),sQuery(id+"F1.wireOp",EDGE,"E949"),sQuery(id+"F1.wireOp",EDGE,"E950"),sQuery(id+"F1.wireOp",EDGE,"E951"),sQuery(id+"F1.wireOp",EDGE,"E952"),sQuery(id+"F1.wireOp",EDGE,"E953"),sQuery(id+"F1.wireOp",EDGE,"E954"),sQuery(id+"F1.wireOp",EDGE,"E955"),sQuery(id+"F1.wireOp",EDGE,"E956"),sQuery(id+"F1.wireOp",EDGE,"E957"),sQuery(id+"F1.wireOp",EDGE,"E958"),sQuery(id+"F1.wireOp",EDGE,"E959"),sQuery(id+"F1.wireOp",EDGE,"E960"),sQuery(id+"F1.wireOp",EDGE,"E961"),sQuery(id+"F1.wireOp",EDGE,"E962"),sQuery(id+"F1.wireOp",EDGE,"E963"),sQuery(id+"F1.wireOp",EDGE,"E964"),sQuery(id+"F1.wireOp",EDGE,"E965"),sQuery(id+"F1.wireOp",EDGE,"E966"),sQuery(id+"F1.wireOp",EDGE,"E967"),sQuery(id+"F1.wireOp",EDGE,"E968"),sQuery(id+"F1.wireOp",EDGE,"E969"),sQuery(id+"F1.wireOp",EDGE,"E970"),sQuery(id+"F1.wireOp",EDGE,"E971"),sQuery(id+"F1.wireOp",EDGE,"E972"),sQuery(id+"F1.wireOp",EDGE,"E973"),sQuery(id+"F1.wireOp",EDGE,"E974"),sQuery(id+"F1.wireOp",EDGE,"E975"),sQuery(id+"F1.wireOp",EDGE,"E976"),sQuery(id+"F1.wireOp",EDGE,"E976"),sQuery(id+"F1.wireOp",EDGE,"E976"),sQuery(id+"F1.wireOp",EDGE,"E977"),sQuery(id+"F1.wireOp",EDGE,"E978"),sQuery(id+"F1.wireOp",EDGE,"E979"),sQuery(id+"F1.wireOp",EDGE,"E980"),sQuery(id+"F1.wireOp",EDGE,"E981"),sQuery(id+"F1.wireOp",EDGE,"E982"),sQuery(id+"F1.wireOp",EDGE,"E983"),sQuery(id+"F1.wireOp",EDGE,"E984"),sQuery(id+"F1.wireOp",EDGE,"E985"),sQuery(id+"F1.wireOp",EDGE,"E986"),sQuery(id+"F1.wireOp",EDGE,"E987"),sQuery(id+"F1.wireOp",EDGE,"E988"),sQuery(id+"F1.wireOp",EDGE,"E989"),sQuery(id+"F1.wireOp",EDGE,"E990"),sQuery(id+"F1.wireOp",EDGE,"E991"),sQuery(id+"F1.wireOp",EDGE,"E992"),sQuery(id+"F1.wireOp",EDGE,"E993"),sQuery(id+"F1.wireOp",EDGE,"E994"),sQuery(id+"F1.wireOp",EDGE,"E995"),sQuery(id+"F1.wireOp",EDGE,"E996"),sQuery(id+"F1.wireOp",EDGE,"E997"),sQuery(id+"F1.wireOp",EDGE,"E998"),sQuery(id+"F1.wireOp",EDGE,"E999"),sQuery(id+"F1.wireOp",EDGE,"E1000"),sQuery(id+"F1.wireOp",EDGE,"E1001"),sQuery(id+"F1.wireOp",EDGE,"E1002"),sQuery(id+"F1.wireOp",EDGE,"E1003"),sQuery(id+"F1.wireOp",EDGE,"E1004"),sQuery(id+"F1.wireOp",EDGE,"E1005"),sQuery(id+"F1.wireOp",EDGE,"E1006"),sQuery(id+"F1.wireOp",EDGE,"E1007"),sQuery(id+"F1.wireOp",EDGE,"E1008"),sQuery(id+"F1.wireOp",EDGE,"E1009"),sQuery(id+"F1.wireOp",EDGE,"E1010"),sQuery(id+"F1.wireOp",EDGE,"E1011"),sQuery(id+"F1.wireOp",EDGE,"E1012"),sQuery(id+"F1.wireOp",EDGE,"E1013"),sQuery(id+"F1.wireOp",EDGE,"E1014"),sQuery(id+"F1.wireOp",EDGE,"E1015"),sQuery(id+"F1.wireOp",EDGE,"E1016"),sQuery(id+"F1.wireOp",EDGE,"E1017"),sQuery(id+"F1.wireOp",EDGE,"E1018"),sQuery(id+"F1.wireOp",EDGE,"E1019"),sQuery(id+"F1.wireOp",EDGE,"E1020"),sQuery(id+"F1.wireOp",EDGE,"E1021"),sQuery(id+"F1.wireOp",EDGE,"E1022"),sQuery(id+"F1.wireOp",EDGE,"E1023"),sQuery(id+"F1.wireOp",EDGE,"E1024"),sQuery(id+"F1.wireOp",EDGE,"E1025"),sQuery(id+"F1.wireOp",EDGE,"E1026"),sQuery(id+"F1.wireOp",EDGE,"E1027"),sQuery(id+"F1.wireOp",EDGE,"E1028"),sQuery(id+"F1.wireOp",EDGE,"E1029"),sQuery(id+"F1.wireOp",EDGE,"E1030"),sQuery(id+"F1.wireOp",EDGE,"E1031"),sQuery(id+"F1.wireOp",EDGE,"E1032"),sQuery(id+"F1.wireOp",EDGE,"E1033"),sQuery(id+"F1.wireOp",EDGE,"E1034"),sQuery(id+"F1.wireOp",EDGE,"E1035"),sQuery(id+"F1.wireOp",EDGE,"E1036"),sQuery(id+"F1.wireOp",EDGE,"E1037"),sQuery(id+"F1.wireOp",EDGE,"E1038"),sQuery(id+"F1.wireOp",EDGE,"E1039"),sQuery(id+"F1.wireOp",EDGE,"E1040"),sQuery(id+"F1.wireOp",EDGE,"E1041"),sQuery(id+"F1.wireOp",EDGE,"E1042"),sQuery(id+"F1.wireOp",EDGE,"E1043"),sQuery(id+"F1.wireOp",EDGE,"E1044"),sQuery(id+"F1.wireOp",EDGE,"E1045"),sQuery(id+"F1.wireOp",EDGE,"E1046"),sQuery(id+"F1.wireOp",EDGE,"E1047"),sQuery(id+"F1.wireOp",EDGE,"E1048"),sQuery(id+"F1.wireOp",EDGE,"E1049"),sQuery(id+"F1.wireOp",EDGE,"E1050"),sQuery(id+"F1.wireOp",EDGE,"E1051"),sQuery(id+"F1.wireOp",EDGE,"E1052"),sQuery(id+"F1.wireOp",EDGE,"E1053"),sQuery(id+"F1.wireOp",EDGE,"E1054"),sQuery(id+"F1.wireOp",EDGE,"E1055"),sQuery(id+"F1.wireOp",EDGE,"E1056"),sQuery(id+"F1.wireOp",EDGE,"E1057"),sQuery(id+"F1.wireOp",EDGE,"E1058"),sQuery(id+"F1.wireOp",EDGE,"E1059"),sQuery(id+"F1.wireOp",EDGE,"E1060"),sQuery(id+"F1.wireOp",EDGE,"E1061"),sQuery(id+"F1.wireOp",EDGE,"E1062"),sQuery(id+"F1.wireOp",EDGE,"E1063"),sQuery(id+"F1.wireOp",EDGE,"E1064"),sQuery(id+"F1.wireOp",EDGE,"E1065"),sQuery(id+"F1.wireOp",EDGE,"E1066"),sQuery(id+"F1.wireOp",EDGE,"E1067"),sQuery(id+"F1.wireOp",EDGE,"E1068"),sQuery(id+"F1.wireOp",EDGE,"E1069"),sQuery(id+"F1.wireOp",EDGE,"E1070"),sQuery(id+"F1.wireOp",EDGE,"E1071"),sQuery(id+"F1.wireOp",EDGE,"E1071"),sQuery(id+"F1.wireOp",EDGE,"E1072"),sQuery(id+"F1.wireOp",EDGE,"E1073"),sQuery(id+"F1.wireOp",EDGE,"E1074"),sQuery(id+"F1.wireOp",EDGE,"E1075"),sQuery(id+"F1.wireOp",EDGE,"E1076"),sQuery(id+"F1.wireOp",EDGE,"E1077"),sQuery(id+"F1.wireOp",EDGE,"E1078"),sQuery(id+"F1.wireOp",EDGE,"E1079"),sQuery(id+"F1.wireOp",EDGE,"E1080"),sQuery(id+"F1.wireOp",EDGE,"E1080"),sQuery(id+"F1.wireOp",EDGE,"E1081"),sQuery(id+"F1.wireOp",EDGE,"E1082"),sQuery(id+"F1.wireOp",EDGE,"E1083"),sQuery(id+"F1.wireOp",EDGE,"E1084"),sQuery(id+"F1.wireOp",EDGE,"E1085"),sQuery(id+"F1.wireOp",EDGE,"E1086"),sQuery(id+"F1.wireOp",EDGE,"E1087"),sQuery(id+"F1.wireOp",EDGE,"E1088"),sQuery(id+"F1.wireOp",EDGE,"E1089"),sQuery(id+"F1.wireOp",EDGE,"E1090"),sQuery(id+"F1.wireOp",EDGE,"E1091"),sQuery(id+"F1.wireOp",EDGE,"E1092"),sQuery(id+"F1.wireOp",EDGE,"E1093"),sQuery(id+"F1.wireOp",EDGE,"E1094"),sQuery(id+"F1.wireOp",EDGE,"E1095"),sQuery(id+"F1.wireOp",EDGE,"E1096"),sQuery(id+"F1.wireOp",EDGE,"E1097"),sQuery(id+"F1.wireOp",EDGE,"E1098"),sQuery(id+"F1.wireOp",EDGE,"E1099"),sQuery(id+"F1.wireOp",EDGE,"E1100"),sQuery(id+"F1.wireOp",EDGE,"E1101"),sQuery(id+"F1.wireOp",EDGE,"E1102"),sQuery(id+"F1.wireOp",EDGE,"E1103"),sQuery(id+"F1.wireOp",EDGE,"E1104"),sQuery(id+"F1.wireOp",EDGE,"E1105"),sQuery(id+"F1.wireOp",EDGE,"E1106"),sQuery(id+"F1.wireOp",EDGE,"E1107"),sQuery(id+"F1.wireOp",EDGE,"E1108"),sQuery(id+"F1.wireOp",EDGE,"E1109"),sQuery(id+"F1.wireOp",EDGE,"E1110"),sQuery(id+"F1.wireOp",EDGE,"E1111"),sQuery(id+"F1.wireOp",EDGE,"E1112"),sQuery(id+"F1.wireOp",EDGE,"E1113"),sQuery(id+"F1.wireOp",EDGE,"E1114"),sQuery(id+"F1.wireOp",EDGE,"E1115"),sQuery(id+"F1.wireOp",EDGE,"E1116"),sQuery(id+"F1.wireOp",EDGE,"E1117"),sQuery(id+"F1.wireOp",EDGE,"E1118"),sQuery(id+"F1.wireOp",EDGE,"E1119"),sQuery(id+"F1.wireOp",EDGE,"E1120"),sQuery(id+"F1.wireOp",EDGE,"E1121"),sQuery(id+"F1.wireOp",EDGE,"E1122"),sQuery(id+"F1.wireOp",EDGE,"E1123"),sQuery(id+"F1.wireOp",EDGE,"E1124"),sQuery(id+"F1.wireOp",EDGE,"E1125"),sQuery(id+"F1.wireOp",EDGE,"E1126"),sQuery(id+"F1.wireOp",EDGE,"E1127"),sQuery(id+"F1.wireOp",EDGE,"E1128"),sQuery(id+"F1.wireOp",EDGE,"E1129"),sQuery(id+"F1.wireOp",EDGE,"E1130"),sQuery(id+"F1.wireOp",EDGE,"E1131"),sQuery(id+"F1.wireOp",EDGE,"E1132"),sQuery(id+"F1.wireOp",EDGE,"E1133"),sQuery(id+"F1.wireOp",EDGE,"E1134"),sQuery(id+"F1.wireOp",EDGE,"E1135"),sQuery(id+"F1.wireOp",EDGE,"E1136"),sQuery(id+"F1.wireOp",EDGE,"E1137"),sQuery(id+"F1.wireOp",EDGE,"E1138"),sQuery(id+"F1.wireOp",EDGE,"E1139"),sQuery(id+"F1.wireOp",EDGE,"E1140"),sQuery(id+"F1.wireOp",EDGE,"E1141"),sQuery(id+"F1.wireOp",EDGE,"E1142"),sQuery(id+"F1.wireOp",EDGE,"E1143"),sQuery(id+"F1.wireOp",EDGE,"E1144"),sQuery(id+"F1.wireOp",EDGE,"E1145"),sQuery(id+"F1.wireOp",EDGE,"E1146"),sQuery(id+"F1.wireOp",EDGE,"E1147"),sQuery(id+"F1.wireOp",EDGE,"E1148"),sQuery(id+"F1.wireOp",EDGE,"E1149"),sQuery(id+"F1.wireOp",EDGE,"E1150"),sQuery(id+"F1.wireOp",EDGE,"E1151"),sQuery(id+"F1.wireOp",EDGE,"E1152"),sQuery(id+"F1.wireOp",EDGE,"E1153"),sQuery(id+"F1.wireOp",EDGE,"E1154"),sQuery(id+"F1.wireOp",EDGE,"E1155"),sQuery(id+"F1.wireOp",EDGE,"E1156"),sQuery(id+"F1.wireOp",EDGE,"E1156"),sQuery(id+"F1.wireOp",EDGE,"E1157"),sQuery(id+"F1.wireOp",EDGE,"E1158"),sQuery(id+"F1.wireOp",EDGE,"E1159"),sQuery(id+"F1.wireOp",EDGE,"E1160"),sQuery(id+"F1.wireOp",EDGE,"E1161"),sQuery(id+"F1.wireOp",EDGE,"E1162"),sQuery(id+"F1.wireOp",EDGE,"E1163"),sQuery(id+"F1.wireOp",EDGE,"E1164"),sQuery(id+"F1.wireOp",EDGE,"E1165"),sQuery(id+"F1.wireOp",EDGE,"E1166"),sQuery(id+"F1.wireOp",EDGE,"E1167"),sQuery(id+"F1.wireOp",EDGE,"E1168"),sQuery(id+"F1.wireOp",EDGE,"E1169"),sQuery(id+"F1.wireOp",EDGE,"E1170"),sQuery(id+"F1.wireOp",EDGE,"E1171"),sQuery(id+"F1.wireOp",EDGE,"E1172"),sQuery(id+"F1.wireOp",EDGE,"E1173"),sQuery(id+"F1.wireOp",EDGE,"E1174"),sQuery(id+"F1.wireOp",EDGE,"E1175"),sQuery(id+"F1.wireOp",EDGE,"E1176"),sQuery(id+"F1.wireOp",EDGE,"E1177"),sQuery(id+"F1.wireOp",EDGE,"E1178"),sQuery(id+"F1.wireOp",EDGE,"E1179"),sQuery(id+"F1.wireOp",EDGE,"E1180"),sQuery(id+"F1.wireOp",EDGE,"E1181"),sQuery(id+"F1.wireOp",EDGE,"E1182"),sQuery(id+"F1.wireOp",EDGE,"E1183"),sQuery(id+"F1.wireOp",EDGE,"E1184"),sQuery(id+"F1.wireOp",EDGE,"E1185"),sQuery(id+"F1.wireOp",EDGE,"E1186"),sQuery(id+"F1.wireOp",EDGE,"E1187"),sQuery(id+"F1.wireOp",EDGE,"E1188"),sQuery(id+"F1.wireOp",EDGE,"E1189"),sQuery(id+"F1.wireOp",EDGE,"E1190"),sQuery(id+"F1.wireOp",EDGE,"E1191"),sQuery(id+"F1.wireOp",EDGE,"E1192"),sQuery(id+"F1.wireOp",EDGE,"E1193"),sQuery(id+"F1.wireOp",EDGE,"E1194"),sQuery(id+"F1.wireOp",EDGE,"E1195"),sQuery(id+"F1.wireOp",EDGE,"E1196"),sQuery(id+"F1.wireOp",EDGE,"E1197"),sQuery(id+"F1.wireOp",EDGE,"E1198"),sQuery(id+"F1.wireOp",EDGE,"E1199"),sQuery(id+"F1.wireOp",EDGE,"E1200"),sQuery(id+"F1.wireOp",EDGE,"E1201"),sQuery(id+"F1.wireOp",EDGE,"E1202"),sQuery(id+"F1.wireOp",EDGE,"E1203"),sQuery(id+"F1.wireOp",EDGE,"E1204"),sQuery(id+"F1.wireOp",EDGE,"E1205"),sQuery(id+"F1.wireOp",EDGE,"E1206"),sQuery(id+"F1.wireOp",EDGE,"E1207"),sQuery(id+"F1.wireOp",EDGE,"E1208"),sQuery(id+"F1.wireOp",EDGE,"E1209"),sQuery(id+"F1.wireOp",EDGE,"E1210"),sQuery(id+"F1.wireOp",EDGE,"E1211"),sQuery(id+"F1.wireOp",EDGE,"E1212"),sQuery(id+"F1.wireOp",EDGE,"E1213"),sQuery(id+"F1.wireOp",EDGE,"E1214"),sQuery(id+"F1.wireOp",EDGE,"E1215"),sQuery(id+"F1.wireOp",EDGE,"E1216"),sQuery(id+"F1.wireOp",EDGE,"E1217"),sQuery(id+"F1.wireOp",EDGE,"E1218"),sQuery(id+"F1.wireOp",EDGE,"E1219"),sQuery(id+"F1.wireOp",EDGE,"E1220"),sQuery(id+"F1.wireOp",EDGE,"E1221"),sQuery(id+"F1.wireOp",EDGE,"E1222"),sQuery(id+"F1.wireOp",EDGE,"E1223"),sQuery(id+"F1.wireOp",EDGE,"E1224"),sQuery(id+"F1.wireOp",EDGE,"E1225"),sQuery(id+"F1.wireOp",EDGE,"E1226"),sQuery(id+"F1.wireOp",EDGE,"E1227"),sQuery(id+"F1.wireOp",EDGE,"E1228"),sQuery(id+"F1.wireOp",EDGE,"E1229"),sQuery(id+"F1.wireOp",EDGE,"E1230"),sQuery(id+"F1.wireOp",EDGE,"E1231"),sQuery(id+"F1.wireOp",EDGE,"E1232"),sQuery(id+"F1.wireOp",EDGE,"E1233"),sQuery(id+"F1.wireOp",EDGE,"E1234"),sQuery(id+"F1.wireOp",EDGE,"E1235"),sQuery(id+"F1.wireOp",EDGE,"E1236"),sQuery(id+"F1.wireOp",EDGE,"E1237"),sQuery(id+"F1.wireOp",EDGE,"E1238"),sQuery(id+"F1.wireOp",EDGE,"E1239"),sQuery(id+"F1.wireOp",EDGE,"E1240"),sQuery(id+"F1.wireOp",EDGE,"E1241"),sQuery(id+"F1.wireOp",EDGE,"E1242"),sQuery(id+"F1.wireOp",EDGE,"E1243"),sQuery(id+"F1.wireOp",EDGE,"E1244"),sQuery(id+"F1.wireOp",EDGE,"E1245"),sQuery(id+"F1.wireOp",EDGE,"E1246"),sQuery(id+"F1.wireOp",EDGE,"E1247"),sQuery(id+"F1.wireOp",EDGE,"E1248"),sQuery(id+"F1.wireOp",EDGE,"E1249"),sQuery(id+"F1.wireOp",EDGE,"E1250"),sQuery(id+"F1.wireOp",EDGE,"E1251"),sQuery(id+"F1.wireOp",EDGE,"E1252"),sQuery(id+"F1.wireOp",EDGE,"E1253"),sQuery(id+"F1.wireOp",EDGE,"E1254"),sQuery(id+"F1.wireOp",EDGE,"E1255"),sQuery(id+"F1.wireOp",EDGE,"E1256"),sQuery(id+"F1.wireOp",EDGE,"E1257"),sQuery(id+"F1.wireOp",EDGE,"E1258"),sQuery(id+"F1.wireOp",EDGE,"E1259"),sQuery(id+"F1.wireOp",EDGE,"E1260"),sQuery(id+"F1.wireOp",EDGE,"E1261"),sQuery(id+"F1.wireOp",EDGE,"E1262"),sQuery(id+"F1.wireOp",EDGE,"E1263"),sQuery(id+"F1.wireOp",EDGE,"E1264"),sQuery(id+"F1.wireOp",EDGE,"E1265"),sQuery(id+"F1.wireOp",EDGE,"E1266"),sQuery(id+"F1.wireOp",EDGE,"E1267"),sQuery(id+"F1.wireOp",EDGE,"E1268"),sQuery(id+"F1.wireOp",EDGE,"E1269"),sQuery(id+"F1.wireOp",EDGE,"E1270"),sQuery(id+"F1.wireOp",EDGE,"E1271"),sQuery(id+"F1.wireOp",EDGE,"E1272"),sQuery(id+"F1.wireOp",EDGE,"E1273"),sQuery(id+"F1.wireOp",EDGE,"E1274"),sQuery(id+"F1.wireOp",EDGE,"E1275"),sQuery(id+"F1.wireOp",EDGE,"E1276"),sQuery(id+"F1.wireOp",EDGE,"E1277"),sQuery(id+"F1.wireOp",EDGE,"E1278"),sQuery(id+"F1.wireOp",EDGE,"E1279"),sQuery(id+"F1.wireOp",EDGE,"E1280"),sQuery(id+"F1.wireOp",EDGE,"E1281"),sQuery(id+"F1.wireOp",EDGE,"E1282"),sQuery(id+"F1.wireOp",EDGE,"E1283"),sQuery(id+"F1.wireOp",EDGE,"E1284"),sQuery(id+"F1.wireOp",EDGE,"E1285"),sQuery(id+"F1.wireOp",EDGE,"E1286"),sQuery(id+"F1.wireOp",EDGE,"E1287"),sQuery(id+"F1.wireOp",EDGE,"E1288"),sQuery(id+"F1.wireOp",EDGE,"E1289"),sQuery(id+"F1.wireOp",EDGE,"E1290"),sQuery(id+"F1.wireOp",EDGE,"E1291"),sQuery(id+"F1.wireOp",EDGE,"E1292"),sQuery(id+"F1.wireOp",EDGE,"E1293"),sQuery(id+"F1.wireOp",EDGE,"E1294"),sQuery(id+"F1.wireOp",EDGE,"E1295"),sQuery(id+"F1.wireOp",EDGE,"E1296"),sQuery(id+"F1.wireOp",EDGE,"E1297"),sQuery(id+"F1.wireOp",EDGE,"E1298"),sQuery(id+"F1.wireOp",EDGE,"E1299"),sQuery(id+"F1.wireOp",EDGE,"E1300"),sQuery(id+"F1.wireOp",EDGE,"E1301"),sQuery(id+"F1.wireOp",EDGE,"E1302"),sQuery(id+"F1.wireOp",EDGE,"E1303"),sQuery(id+"F1.wireOp",EDGE,"E1304"),sQuery(id+"F1.wireOp",EDGE,"E1305"),sQuery(id+"F1.wireOp",EDGE,"E1306"),sQuery(id+"F1.wireOp",EDGE,"E1307"),sQuery(id+"F1.wireOp",EDGE,"E1308"),sQuery(id+"F1.wireOp",EDGE,"E1309"),sQuery(id+"F1.wireOp",EDGE,"E1310"),sQuery(id+"F1.wireOp",EDGE,"E1311"),sQuery(id+"F1.wireOp",EDGE,"E1312"),sQuery(id+"F1.wireOp",EDGE,"E1312"),sQuery(id+"F1.wireOp",EDGE,"E1313"),sQuery(id+"F1.wireOp",EDGE,"E1314"),sQuery(id+"F1.wireOp",EDGE,"E1315"),sQuery(id+"F1.wireOp",EDGE,"E1316"),sQuery(id+"F1.wireOp",EDGE,"E1317"),sQuery(id+"F1.wireOp",EDGE,"E1318"),sQuery(id+"F1.wireOp",EDGE,"E1319"),sQuery(id+"F1.wireOp",EDGE,"E1320"),sQuery(id+"F1.wireOp",EDGE,"E1321"),sQuery(id+"F1.wireOp",EDGE,"E1322"),sQuery(id+"F1.wireOp",EDGE,"E1323"),sQuery(id+"F1.wireOp",EDGE,"E1324"),sQuery(id+"F1.wireOp",EDGE,"E1325"),sQuery(id+"F1.wireOp",EDGE,"E1326"),sQuery(id+"F1.wireOp",EDGE,"E1327"),sQuery(id+"F1.wireOp",EDGE,"E1328"),sQuery(id+"F1.wireOp",EDGE,"E1329"),sQuery(id+"F1.wireOp",EDGE,"E1330"),sQuery(id+"F1.wireOp",EDGE,"E1331"),sQuery(id+"F1.wireOp",EDGE,"E1332"),sQuery(id+"F1.wireOp",EDGE,"E1333"),sQuery(id+"F1.wireOp",EDGE,"E1334"),sQuery(id+"F1.wireOp",EDGE,"E1335"),sQuery(id+"F1.wireOp",EDGE,"E1336"),sQuery(id+"F1.wireOp",EDGE,"E1337"),sQuery(id+"F1.wireOp",EDGE,"E1338"),sQuery(id+"F1.wireOp",EDGE,"E1339"),sQuery(id+"F1.wireOp",EDGE,"E1340"),sQuery(id+"F1.wireOp",EDGE,"E1341"),sQuery(id+"F1.wireOp",EDGE,"E1342"),sQuery(id+"F1.wireOp",EDGE,"E1343"),sQuery(id+"F1.wireOp",EDGE,"E1344"),sQuery(id+"F1.wireOp",EDGE,"E1345"),sQuery(id+"F1.wireOp",EDGE,"E1346"),sQuery(id+"F1.wireOp",EDGE,"E1347"),sQuery(id+"F1.wireOp",EDGE,"E1348"),sQuery(id+"F1.wireOp",EDGE,"E1349"),sQuery(id+"F1.wireOp",EDGE,"E1350"),sQuery(id+"F1.wireOp",EDGE,"E1351"),sQuery(id+"F1.wireOp",EDGE,"E1352"),sQuery(id+"F1.wireOp",EDGE,"E1353"),sQuery(id+"F1.wireOp",EDGE,"E1354"),sQuery(id+"F1.wireOp",EDGE,"E1355"),sQuery(id+"F1.wireOp",EDGE,"E1356"),sQuery(id+"F1.wireOp",EDGE,"E1357"),sQuery(id+"F1.wireOp",EDGE,"E1358"),sQuery(id+"F1.wireOp",EDGE,"E1359"),sQuery(id+"F1.wireOp",EDGE,"E1360"),sQuery(id+"F1.wireOp",EDGE,"E1361"),sQuery(id+"F1.wireOp",EDGE,"E1362"),sQuery(id+"F1.wireOp",EDGE,"E1363"),sQuery(id+"F1.wireOp",EDGE,"E1364"),sQuery(id+"F1.wireOp",EDGE,"E1365"),sQuery(id+"F1.wireOp",EDGE,"E1366"),sQuery(id+"F1.wireOp",EDGE,"E1367"),sQuery(id+"F1.wireOp",EDGE,"E1368"),sQuery(id+"F1.wireOp",EDGE,"E1369"),sQuery(id+"F1.wireOp",EDGE,"E1370"),sQuery(id+"F1.wireOp",EDGE,"E1371"),sQuery(id+"F1.wireOp",EDGE,"E1372"),sQuery(id+"F1.wireOp",EDGE,"E1373"),sQuery(id+"F1.wireOp",EDGE,"E1374"),sQuery(id+"F1.wireOp",EDGE,"E1375"),sQuery(id+"F1.wireOp",EDGE,"E1376"),sQuery(id+"F1.wireOp",EDGE,"E1376"),sQuery(id+"F1.wireOp",EDGE,"E1377"),sQuery(id+"F1.wireOp",EDGE,"E1378"),sQuery(id+"F1.wireOp",EDGE,"E1379"),sQuery(id+"F1.wireOp",EDGE,"E1380"),sQuery(id+"F1.wireOp",EDGE,"E1381"),sQuery(id+"F1.wireOp",EDGE,"E1382"),sQuery(id+"F1.wireOp",EDGE,"E1383"),sQuery(id+"F1.wireOp",EDGE,"E1384"),sQuery(id+"F1.wireOp",EDGE,"E1385"),sQuery(id+"F1.wireOp",EDGE,"E1386"),sQuery(id+"F1.wireOp",EDGE,"E1387"),sQuery(id+"F1.wireOp",EDGE,"E1388"),sQuery(id+"F1.wireOp",EDGE,"E1389"),sQuery(id+"F1.wireOp",EDGE,"E1390"),sQuery(id+"F1.wireOp",EDGE,"E1391"),sQuery(id+"F1.wireOp",EDGE,"E1392"),sQuery(id+"F1.wireOp",EDGE,"E1393"),sQuery(id+"F1.wireOp",EDGE,"E1394"),sQuery(id+"F1.wireOp",EDGE,"E1395"),sQuery(id+"F1.wireOp",EDGE,"E1396"),sQuery(id+"F1.wireOp",EDGE,"E1397"),sQuery(id+"F1.wireOp",EDGE,"E1398"),sQuery(id+"F1.wireOp",EDGE,"E1399"),sQuery(id+"F1.wireOp",EDGE,"E1400"),sQuery(id+"F1.wireOp",EDGE,"E1401"),sQuery(id+"F1.wireOp",EDGE,"E1402"),sQuery(id+"F1.wireOp",EDGE,"E1403"),sQuery(id+"F1.wireOp",EDGE,"E1404"),sQuery(id+"F1.wireOp",EDGE,"E1405"),sQuery(id+"F1.wireOp",EDGE,"E1406"),sQuery(id+"F1.wireOp",EDGE,"E1407"),sQuery(id+"F1.wireOp",EDGE,"E1408"),sQuery(id+"F1.wireOp",EDGE,"E1409"),sQuery(id+"F1.wireOp",EDGE,"E1410"),sQuery(id+"F1.wireOp",EDGE,"E1411"),sQuery(id+"F1.wireOp",EDGE,"E1412"),sQuery(id+"F1.wireOp",EDGE,"E1413"),sQuery(id+"F1.wireOp",EDGE,"E1414"),sQuery(id+"F1.wireOp",EDGE,"E1415"),sQuery(id+"F1.wireOp",EDGE,"E1416"),sQuery(id+"F1.wireOp",EDGE,"E1417"),sQuery(id+"F1.wireOp",EDGE,"E1418"),sQuery(id+"F1.wireOp",EDGE,"E1419"),sQuery(id+"F1.wireOp",EDGE,"E1420"),sQuery(id+"F1.wireOp",EDGE,"E1421"),sQuery(id+"F1.wireOp",EDGE,"E1422"),sQuery(id+"F1.wireOp",EDGE,"E1423"),sQuery(id+"F1.wireOp",EDGE,"E1424"),sQuery(id+"F1.wireOp",EDGE,"E1425"),sQuery(id+"F1.wireOp",EDGE,"E1426"),sQuery(id+"F1.wireOp",EDGE,"E1427"),sQuery(id+"F1.wireOp",EDGE,"E1428"),sQuery(id+"F1.wireOp",EDGE,"E1429"),sQuery(id+"F1.wireOp",EDGE,"E1430"),sQuery(id+"F1.wireOp",EDGE,"E1431"),sQuery(id+"F1.wireOp",EDGE,"E1432"),sQuery(id+"F1.wireOp",EDGE,"E1433"),sQuery(id+"F1.wireOp",EDGE,"E1434"),sQuery(id+"F1.wireOp",EDGE,"E1435"),sQuery(id+"F1.wireOp",EDGE,"E1436"),sQuery(id+"F1.wireOp",EDGE,"E1437"),sQuery(id+"F1.wireOp",EDGE,"E1438"),sQuery(id+"F1.wireOp",EDGE,"E1439"),sQuery(id+"F1.wireOp",EDGE,"E1440"),sQuery(id+"F1.wireOp",EDGE,"E1441"),sQuery(id+"F1.wireOp",EDGE,"E1442"),sQuery(id+"F1.wireOp",EDGE,"E1443"),sQuery(id+"F1.wireOp",EDGE,"E1444"),sQuery(id+"F1.wireOp",EDGE,"E1445"),sQuery(id+"F1.wireOp",EDGE,"E1446"),sQuery(id+"F1.wireOp",EDGE,"E1447"),sQuery(id+"F1.wireOp",EDGE,"E1448"),sQuery(id+"F1.wireOp",EDGE,"E1449"),sQuery(id+"F1.wireOp",EDGE,"E1450"),sQuery(id+"F1.wireOp",EDGE,"E1451"),sQuery(id+"F1.wireOp",EDGE,"E1452"),sQuery(id+"F1.wireOp",EDGE,"E1453"),sQuery(id+"F1.wireOp",EDGE,"E1454"),sQuery(id+"F1.wireOp",EDGE,"E1455"),sQuery(id+"F1.wireOp",EDGE,"E1456"),sQuery(id+"F1.wireOp",EDGE,"E1457"),sQuery(id+"F1.wireOp",EDGE,"E1458"),sQuery(id+"F1.wireOp",EDGE,"E1459"),sQuery(id+"F1.wireOp",EDGE,"E1460"),sQuery(id+"F1.wireOp",EDGE,"E1461"),sQuery(id+"F1.wireOp",EDGE,"E1462"),sQuery(id+"F1.wireOp",EDGE,"E1463"),sQuery(id+"F1.wireOp",EDGE,"E1464"),sQuery(id+"F1.wireOp",EDGE,"E1465"),sQuery(id+"F1.wireOp",EDGE,"E1466"),sQuery(id+"F1.wireOp",EDGE,"E1467"),sQuery(id+"F1.wireOp",EDGE,"E1468"),sQuery(id+"F1.wireOp",EDGE,"E1469"),sQuery(id+"F1.wireOp",EDGE,"E1470"),sQuery(id+"F1.wireOp",EDGE,"E1471"),sQuery(id+"F1.wireOp",EDGE,"E1472"),sQuery(id+"F1.wireOp",EDGE,"E1473"),sQuery(id+"F1.wireOp",EDGE,"E1474"),sQuery(id+"F1.wireOp",EDGE,"E1475"),sQuery(id+"F1.wireOp",EDGE,"E1476"),sQuery(id+"F1.wireOp",EDGE,"E1477"),sQuery(id+"F1.wireOp",EDGE,"E1478"),sQuery(id+"F1.wireOp",EDGE,"E1479"),sQuery(id+"F1.wireOp",EDGE,"E1480"),sQuery(id+"F1.wireOp",EDGE,"E1481"),sQuery(id+"F1.wireOp",EDGE,"E1482"),sQuery(id+"F1.wireOp",EDGE,"E1483"),sQuery(id+"F1.wireOp",EDGE,"E1484"),sQuery(id+"F1.wireOp",EDGE,"E1485"),sQuery(id+"F1.wireOp",EDGE,"E1486"),sQuery(id+"F1.wireOp",EDGE,"E1487"),sQuery(id+"F1.wireOp",EDGE,"E1488"),sQuery(id+"F1.wireOp",EDGE,"E1489"),sQuery(id+"F1.wireOp",EDGE,"E1490"),sQuery(id+"F1.wireOp",EDGE,"E1491"),sQuery(id+"F1.wireOp",EDGE,"E1492"),sQuery(id+"F1.wireOp",EDGE,"E1493"),sQuery(id+"F1.wireOp",EDGE,"E1494"),sQuery(id+"F1.wireOp",EDGE,"E1495"),sQuery(id+"F1.wireOp",EDGE,"E1496"),sQuery(id+"F1.wireOp",EDGE,"E1497"),sQuery(id+"F1.wireOp",EDGE,"E1498"),sQuery(id+"F1.wireOp",EDGE,"E1499"),sQuery(id+"F1.wireOp",EDGE,"E1500"),sQuery(id+"F1.wireOp",EDGE,"E1501"),sQuery(id+"F1.wireOp",EDGE,"E1502"),sQuery(id+"F1.wireOp",EDGE,"E1503"),sQuery(id+"F1.wireOp",EDGE,"E1504"),sQuery(id+"F1.wireOp",EDGE,"E1505"),sQuery(id+"F1.wireOp",EDGE,"E1506"),sQuery(id+"F1.wireOp",EDGE,"E1507"),sQuery(id+"F1.wireOp",EDGE,"E1508"),sQuery(id+"F1.wireOp",EDGE,"E1509"),sQuery(id+"F1.wireOp",EDGE,"E1510"),sQuery(id+"F1.wireOp",EDGE,"E1511"),sQuery(id+"F1.wireOp",EDGE,"E1512"),sQuery(id+"F1.wireOp",EDGE,"E1513"),sQuery(id+"F1.wireOp",EDGE,"E1514"),sQuery(id+"F1.wireOp",EDGE,"E1515"),sQuery(id+"F1.wireOp",EDGE,"E1516"),sQuery(id+"F1.wireOp",EDGE,"E1517"),sQuery(id+"F1.wireOp",EDGE,"E1518"),sQuery(id+"F1.wireOp",EDGE,"E1519"),sQuery(id+"F1.wireOp",EDGE,"E1520"),sQuery(id+"F1.wireOp",EDGE,"E1521"),sQuery(id+"F1.wireOp",EDGE,"E1522"),sQuery(id+"F1.wireOp",EDGE,"E1523"),sQuery(id+"F1.wireOp",EDGE,"E1524"),sQuery(id+"F1.wireOp",EDGE,"E1525"),sQuery(id+"F1.wireOp",EDGE,"E1526"),sQuery(id+"F1.wireOp",EDGE,"E1527"),sQuery(id+"F1.wireOp",EDGE,"E1528"),sQuery(id+"F1.wireOp",EDGE,"E1529"),sQuery(id+"F1.wireOp",EDGE,"E1530"),sQuery(id+"F1.wireOp",EDGE,"E1531"),sQuery(id+"F1.wireOp",EDGE,"E1532"),sQuery(id+"F1.wireOp",EDGE,"E1533"),sQuery(id+"F1.wireOp",EDGE,"E1534"),sQuery(id+"F1.wireOp",EDGE,"E1535"),sQuery(id+"F1.wireOp",EDGE,"E1536"),sQuery(id+"F1.wireOp",EDGE,"E1537"),sQuery(id+"F1.wireOp",EDGE,"E1538"),sQuery(id+"F1.wireOp",EDGE,"E1539"),sQuery(id+"F1.wireOp",EDGE,"E1540"),sQuery(id+"F1.wireOp",EDGE,"E1541"),sQuery(id+"F1.wireOp",EDGE,"E1542"),sQuery(id+"F1.wireOp",EDGE,"E1543"),sQuery(id+"F1.wireOp",EDGE,"E1544"),sQuery(id+"F1.wireOp",EDGE,"E1545"),sQuery(id+"F1.wireOp",EDGE,"E1546"),sQuery(id+"F1.wireOp",EDGE,"E1547"),sQuery(id+"F1.wireOp",EDGE,"E1548"),sQuery(id+"F1.wireOp",EDGE,"E1549"),sQuery(id+"F1.wireOp",EDGE,"E1550"),sQuery(id+"F1.wireOp",EDGE,"E1551"),sQuery(id+"F1.wireOp",EDGE,"E1552"),sQuery(id+"F1.wireOp",EDGE,"E1553"),sQuery(id+"F1.wireOp",EDGE,"E1554"),sQuery(id+"F1.wireOp",EDGE,"E1555"),sQuery(id+"F1.wireOp",EDGE,"E1556"),sQuery(id+"F1.wireOp",EDGE,"E1557"),sQuery(id+"F1.wireOp",EDGE,"E1558"),sQuery(id+"F1.wireOp",EDGE,"E1559"),sQuery(id+"F1.wireOp",EDGE,"E1560"),sQuery(id+"F1.wireOp",EDGE,"E1561"),sQuery(id+"F1.wireOp",EDGE,"E1562"),sQuery(id+"F1.wireOp",EDGE,"E1563"),sQuery(id+"F1.wireOp",EDGE,"E1564"),sQuery(id+"F1.wireOp",EDGE,"E1565"),sQuery(id+"F1.wireOp",EDGE,"E1566"),sQuery(id+"F1.wireOp",EDGE,"E1567"),sQuery(id+"F1.wireOp",EDGE,"E1568"),sQuery(id+"F1.wireOp",EDGE,"E1569"),sQuery(id+"F1.wireOp",EDGE,"E1570"),sQuery(id+"F1.wireOp",EDGE,"E1571"),sQuery(id+"F1.wireOp",EDGE,"E1572"),sQuery(id+"F1.wireOp",EDGE,"E1573"),sQuery(id+"F1.wireOp",EDGE,"E1574"),sQuery(id+"F1.wireOp",EDGE,"E1575"),sQuery(id+"F1.wireOp",EDGE,"E1576"),sQuery(id+"F1.wireOp",EDGE,"E1577"),sQuery(id+"F1.wireOp",EDGE,"E1578"),sQuery(id+"F1.wireOp",EDGE,"E1579"),sQuery(id+"F1.wireOp",EDGE,"E1580"),sQuery(id+"F1.wireOp",EDGE,"E1581"),sQuery(id+"F1.wireOp",EDGE,"E1582"),sQuery(id+"F1.wireOp",EDGE,"E1583"),sQuery(id+"F1.wireOp",EDGE,"E1584"),sQuery(id+"F1.wireOp",EDGE,"E1585"),sQuery(id+"F1.wireOp",EDGE,"E1586"),sQuery(id+"F1.wireOp",EDGE,"E1587"),sQuery(id+"F1.wireOp",EDGE,"E1588"),sQuery(id+"F1.wireOp",EDGE,"E1589"),sQuery(id+"F1.wireOp",EDGE,"E1590"),sQuery(id+"F1.wireOp",EDGE,"E1591"),sQuery(id+"F1.wireOp",EDGE,"E1592"),sQuery(id+"F1.wireOp",EDGE,"E1593"),sQuery(id+"F1.wireOp",EDGE,"E1594"),sQuery(id+"F1.wireOp",EDGE,"E1595"),sQuery(id+"F1.wireOp",EDGE,"E1596"),sQuery(id+"F1.wireOp",EDGE,"E1597"),sQuery(id+"F1.wireOp",EDGE,"E1598"),sQuery(id+"F1.wireOp",EDGE,"E1599"),sQuery(id+"F1.wireOp",EDGE,"E1600"),sQuery(id+"F1.wireOp",EDGE,"E1601"),sQuery(id+"F1.wireOp",EDGE,"E1602"),sQuery(id+"F1.wireOp",EDGE,"E1603"),sQuery(id+"F1.wireOp",EDGE,"E1604"),sQuery(id+"F1.wireOp",EDGE,"E1605"),sQuery(id+"F1.wireOp",EDGE,"E1606"),sQuery(id+"F1.wireOp",EDGE,"E1607"),sQuery(id+"F1.wireOp",EDGE,"E1608"),sQuery(id+"F1.wireOp",EDGE,"E1609"),sQuery(id+"F1.wireOp",EDGE,"E1610"),sQuery(id+"F1.wireOp",EDGE,"E1611"),sQuery(id+"F1.wireOp",EDGE,"E1612"),sQuery(id+"F1.wireOp",EDGE,"E1613"),sQuery(id+"F1.wireOp",EDGE,"E1614"),sQuery(id+"F1.wireOp",EDGE,"E1615"),sQuery(id+"F1.wireOp",EDGE,"E1616"),sQuery(id+"F1.wireOp",EDGE,"E1617"),sQuery(id+"F1.wireOp",EDGE,"E1618"),sQuery(id+"F1.wireOp",EDGE,"E1619"),sQuery(id+"F1.wireOp",EDGE,"E1620"),sQuery(id+"F1.wireOp",EDGE,"E1621"),sQuery(id+"F1.wireOp",EDGE,"E1622"),sQuery(id+"F1.wireOp",EDGE,"E1623"),sQuery(id+"F1.wireOp",EDGE,"E1624"),sQuery(id+"F1.wireOp",EDGE,"E1625"),sQuery(id+"F1.wireOp",EDGE,"E1626"),sQuery(id+"F1.wireOp",EDGE,"E1627"),sQuery(id+"F1.wireOp",EDGE,"E1628"),sQuery(id+"F1.wireOp",EDGE,"E1629"),sQuery(id+"F1.wireOp",EDGE,"E1630"),sQuery(id+"F1.wireOp",EDGE,"E1631"),sQuery(id+"F1.wireOp",EDGE,"E1632"),sQuery(id+"F1.wireOp",EDGE,"E1633"),sQuery(id+"F1.wireOp",EDGE,"E1634"),sQuery(id+"F1.wireOp",EDGE,"E1635"),sQuery(id+"F1.wireOp",EDGE,"E1636"),sQuery(id+"F1.wireOp",EDGE,"E1637"),sQuery(id+"F1.wireOp",EDGE,"E1638"),sQuery(id+"F1.wireOp",EDGE,"E1639"),sQuery(id+"F1.wireOp",EDGE,"E1640"),sQuery(id+"F1.wireOp",EDGE,"E1641"),sQuery(id+"F1.wireOp",EDGE,"E1642"),sQuery(id+"F1.wireOp",EDGE,"E1643"),sQuery(id+"F1.wireOp",EDGE,"E1644"),sQuery(id+"F1.wireOp",EDGE,"E1645"),sQuery(id+"F1.wireOp",EDGE,"E1646"),sQuery(id+"F1.wireOp",EDGE,"E1647"),sQuery(id+"F1.wireOp",EDGE,"E1648"),sQuery(id+"F1.wireOp",EDGE,"E1649"),sQuery(id+"F1.wireOp",EDGE,"E1650"),sQuery(id+"F1.wireOp",EDGE,"E1651"),sQuery(id+"F1.wireOp",EDGE,"E1652"),sQuery(id+"F1.wireOp",EDGE,"E1653"),sQuery(id+"F1.wireOp",EDGE,"E1654"),sQuery(id+"F1.wireOp",EDGE,"E1655"),sQuery(id+"F1.wireOp",EDGE,"E1656"),sQuery(id+"F1.wireOp",EDGE,"E1657"),sQuery(id+"F1.wireOp",EDGE,"E1658"),sQuery(id+"F1.wireOp",EDGE,"E1659"),sQuery(id+"F1.wireOp",EDGE,"E1660"),sQuery(id+"F1.wireOp",EDGE,"E1661"),sQuery(id+"F1.wireOp",EDGE,"E1662"),sQuery(id+"F1.wireOp",EDGE,"E1663"),sQuery(id+"F1.wireOp",EDGE,"E1664"),sQuery(id+"F1.wireOp",EDGE,"E1665"),sQuery(id+"F1.wireOp",EDGE,"E1666"),sQuery(id+"F1.wireOp",EDGE,"E1667"),sQuery(id+"F1.wireOp",EDGE,"E1668"),sQuery(id+"F1.wireOp",EDGE,"E1669"),sQuery(id+"F1.wireOp",EDGE,"E1670"),sQuery(id+"F1.wireOp",EDGE,"E1671"),sQuery(id+"F1.wireOp",EDGE,"E1672"),sQuery(id+"F1.wireOp",EDGE,"E1673"),sQuery(id+"F1.wireOp",EDGE,"E1674"),sQuery(id+"F1.wireOp",EDGE,"E1675"),sQuery(id+"F1.wireOp",EDGE,"E1676"),sQuery(id+"F1.wireOp",EDGE,"E1677"),sQuery(id+"F1.wireOp",EDGE,"E1678"),sQuery(id+"F1.wireOp",EDGE,"E1679"),sQuery(id+"F1.wireOp",EDGE,"E1680"),sQuery(id+"F1.wireOp",EDGE,"E1681"),sQuery(id+"F1.wireOp",EDGE,"E1682"),sQuery(id+"F1.wireOp",EDGE,"E1683"),sQuery(id+"F1.wireOp",EDGE,"E1684"),sQuery(id+"F1.wireOp",EDGE,"E1685"),sQuery(id+"F1.wireOp",EDGE,"E1686"),sQuery(id+"F1.wireOp",EDGE,"E1687"),sQuery(id+"F1.wireOp",EDGE,"E1688"),sQuery(id+"F1.wireOp",EDGE,"E1689"),sQuery(id+"F1.wireOp",EDGE,"E1690"),sQuery(id+"F1.wireOp",EDGE,"E1691"),sQuery(id+"F1.wireOp",EDGE,"E1692"),sQuery(id+"F1.wireOp",EDGE,"E1693"),sQuery(id+"F1.wireOp",EDGE,"E1694"),sQuery(id+"F1.wireOp",EDGE,"E1695"),sQuery(id+"F1.wireOp",EDGE,"E1696"),sQuery(id+"F1.wireOp",EDGE,"E1697"),sQuery(id+"F1.wireOp",EDGE,"E1698"),sQuery(id+"F1.wireOp",EDGE,"E1699"),sQuery(id+"F1.wireOp",EDGE,"E1700"),sQuery(id+"F1.wireOp",EDGE,"E1701"),sQuery(id+"F1.wireOp",EDGE,"E1702"),sQuery(id+"F1.wireOp",EDGE,"E1703"),sQuery(id+"F1.wireOp",EDGE,"E1704"),sQuery(id+"F1.wireOp",EDGE,"E1705"),sQuery(id+"F1.wireOp",EDGE,"E1706"),sQuery(id+"F1.wireOp",EDGE,"E1707"),sQuery(id+"F1.wireOp",EDGE,"E1708"),sQuery(id+"F1.wireOp",EDGE,"E1709"),sQuery(id+"F1.wireOp",EDGE,"E1710"),sQuery(id+"F1.wireOp",EDGE,"E1711"),sQuery(id+"F1.wireOp",EDGE,"E1712"),sQuery(id+"F1.wireOp",EDGE,"E1713"),sQuery(id+"F1.wireOp",EDGE,"E1714"),sQuery(id+"F1.wireOp",EDGE,"E1715"),sQuery(id+"F1.wireOp",EDGE,"E1716"),sQuery(id+"F1.wireOp",EDGE,"E1717"),sQuery(id+"F1.wireOp",EDGE,"E1718"),sQuery(id+"F1.wireOp",EDGE,"E1719"),sQuery(id+"F1.wireOp",EDGE,"E1720"),sQuery(id+"F1.wireOp",EDGE,"E1721"),sQuery(id+"F1.wireOp",EDGE,"E1722"),sQuery(id+"F1.wireOp",EDGE,"E1723"),sQuery(id+"F1.wireOp",EDGE,"E1724"),sQuery(id+"F1.wireOp",EDGE,"E1725"),sQuery(id+"F1.wireOp",EDGE,"E1726"),sQuery(id+"F1.wireOp",EDGE,"E1727"),sQuery(id+"F1.wireOp",EDGE,"E1728"),sQuery(id+"F1.wireOp",EDGE,"E1729"),sQuery(id+"F1.wireOp",EDGE,"E1730"),sQuery(id+"F1.wireOp",EDGE,"E1731"),sQuery(id+"F1.wireOp",EDGE,"E1732"),sQuery(id+"F1.wireOp",EDGE,"E1733"),sQuery(id+"F1.wireOp",EDGE,"E1734"),sQuery(id+"F1.wireOp",EDGE,"E1735"),sQuery(id+"F1.wireOp",EDGE,"E1736"),sQuery(id+"F1.wireOp",EDGE,"E1737"),sQuery(id+"F1.wireOp",EDGE,"E1738"),sQuery(id+"F1.wireOp",EDGE,"E1739"),sQuery(id+"F1.wireOp",EDGE,"E1740"),sQuery(id+"F1.wireOp",EDGE,"E1741"),sQuery(id+"F1.wireOp",EDGE,"E1742"),sQuery(id+"F1.wireOp",EDGE,"E1743"),sQuery(id+"F1.wireOp",EDGE,"E1744"),sQuery(id+"F1.wireOp",EDGE,"E1745"),sQuery(id+"F1.wireOp",EDGE,"E1746"),sQuery(id+"F1.wireOp",EDGE,"E1747"),sQuery(id+"F1.wireOp",EDGE,"E1748"),sQuery(id+"F1.wireOp",EDGE,"E1749"),sQuery(id+"F1.wireOp",EDGE,"E1750"),sQuery(id+"F1.wireOp",EDGE,"E1751"),sQuery(id+"F1.wireOp",EDGE,"E1752"),sQuery(id+"F1.wireOp",EDGE,"E1753"),sQuery(id+"F1.wireOp",EDGE,"E1754"),sQuery(id+"F1.wireOp",EDGE,"E1755"),sQuery(id+"F1.wireOp",EDGE,"E1756"),sQuery(id+"F1.wireOp",EDGE,"E1757"),sQuery(id+"F1.wireOp",EDGE,"E1758"),sQuery(id+"F1.wireOp",EDGE,"E1759"),sQuery(id+"F1.wireOp",EDGE,"E1760"),sQuery(id+"F1.wireOp",EDGE,"E1761"),sQuery(id+"F1.wireOp",EDGE,"E1762"),sQuery(id+"F1.wireOp",EDGE,"E1763"),sQuery(id+"F1.wireOp",EDGE,"E1764"),sQuery(id+"F1.wireOp",EDGE,"E1765"),sQuery(id+"F1.wireOp",EDGE,"E1766"),sQuery(id+"F1.wireOp",EDGE,"E1767"),sQuery(id+"F1.wireOp",EDGE,"E1768"),sQuery(id+"F1.wireOp",EDGE,"E1769"),sQuery(id+"F1.wireOp",EDGE,"E1770"),sQuery(id+"F1.wireOp",EDGE,"E1771"),sQuery(id+"F1.wireOp",EDGE,"E1772"),sQuery(id+"F1.wireOp",EDGE,"E1773"),sQuery(id+"F1.wireOp",EDGE,"E1774"),sQuery(id+"F1.wireOp",EDGE,"E1775"),sQuery(id+"F1.wireOp",EDGE,"E1776"),sQuery(id+"F1.wireOp",EDGE,"E1777"),sQuery(id+"F1.wireOp",EDGE,"E1778"),sQuery(id+"F1.wireOp",EDGE,"E1779"),sQuery(id+"F1.wireOp",EDGE,"E1780"),sQuery(id+"F1.wireOp",EDGE,"E1781"),sQuery(id+"F1.wireOp",EDGE,"E1782"),sQuery(id+"F1.wireOp",EDGE,"E1783"),sQuery(id+"F1.wireOp",EDGE,"E1784"),sQuery(id+"F1.wireOp",EDGE,"E1785"),sQuery(id+"F1.wireOp",EDGE,"E1786"),sQuery(id+"F1.wireOp",EDGE,"E1787"),sQuery(id+"F1.wireOp",EDGE,"E1788"),sQuery(id+"F1.wireOp",EDGE,"E1789"),sQuery(id+"F1.wireOp",EDGE,"E1790"),sQuery(id+"F1.wireOp",EDGE,"E1791"),sQuery(id+"F1.wireOp",EDGE,"E1792"),sQuery(id+"F1.wireOp",EDGE,"E1793"),sQuery(id+"F1.wireOp",EDGE,"E1794"),sQuery(id+"F1.wireOp",EDGE,"E1795"),sQuery(id+"F1.wireOp",EDGE,"E1796"),sQuery(id+"F1.wireOp",EDGE,"E1797"),sQuery(id+"F1.wireOp",EDGE,"E1798"),sQuery(id+"F1.wireOp",EDGE,"E1799"),sQuery(id+"F1.wireOp",EDGE,"E1800"),sQuery(id+"F1.wireOp",EDGE,"E1801"),sQuery(id+"F1.wireOp",EDGE,"E1802"),sQuery(id+"F1.wireOp",EDGE,"E1803"),sQuery(id+"F1.wireOp",EDGE,"E1804"),sQuery(id+"F1.wireOp",EDGE,"E1805"),sQuery(id+"F1.wireOp",EDGE,"E1806"),sQuery(id+"F1.wireOp",EDGE,"E1807"),sQuery(id+"F1.wireOp",EDGE,"E1808"),sQuery(id+"F1.wireOp",EDGE,"E1809"),sQuery(id+"F1.wireOp",EDGE,"E1810"),sQuery(id+"F1.wireOp",EDGE,"E1811"),sQuery(id+"F1.wireOp",EDGE,"E1812"),sQuery(id+"F1.wireOp",EDGE,"E1813"),sQuery(id+"F1.wireOp",EDGE,"E1814"),sQuery(id+"F1.wireOp",EDGE,"E1815"),sQuery(id+"F1.wireOp",EDGE,"E1816"),sQuery(id+"F1.wireOp",EDGE,"E1817"),sQuery(id+"F1.wireOp",EDGE,"E1818"),sQuery(id+"F1.wireOp",EDGE,"E1819"),sQuery(id+"F1.wireOp",EDGE,"E1820"),sQuery(id+"F1.wireOp",EDGE,"E1821"),sQuery(id+"F1.wireOp",EDGE,"E1822"),sQuery(id+"F1.wireOp",EDGE,"E1823"),sQuery(id+"F1.wireOp",EDGE,"E1824"),sQuery(id+"F1.wireOp",EDGE,"E1825"),sQuery(id+"F1.wireOp",EDGE,"E1826"),sQuery(id+"F1.wireOp",EDGE,"E1827"),sQuery(id+"F1.wireOp",EDGE,"E1828"),sQuery(id+"F1.wireOp",EDGE,"E1829"),sQuery(id+"F1.wireOp",EDGE,"E1830"),sQuery(id+"F1.wireOp",EDGE,"E1831"),sQuery(id+"F1.wireOp",EDGE,"E1832"),sQuery(id+"F1.wireOp",EDGE,"E1833"),sQuery(id+"F1.wireOp",EDGE,"E1834"),sQuery(id+"F1.wireOp",EDGE,"E1835"),sQuery(id+"F1.wireOp",EDGE,"E1836"),sQuery(id+"F1.wireOp",EDGE,"E1837"),sQuery(id+"F1.wireOp",EDGE,"E1838"),sQuery(id+"F1.wireOp",EDGE,"E1839"),sQuery(id+"F1.wireOp",EDGE,"E1840"),sQuery(id+"F1.wireOp",EDGE,"E1841"),sQuery(id+"F1.wireOp",EDGE,"E1842"),sQuery(id+"F1.wireOp",EDGE,"E1843"),sQuery(id+"F1.wireOp",EDGE,"E1844"),sQuery(id+"F1.wireOp",EDGE,"E1845"),sQuery(id+"F1.wireOp",EDGE,"E1846"),sQuery(id+"F1.wireOp",EDGE,"E1847"),sQuery(id+"F1.wireOp",EDGE,"E1848"),sQuery(id+"F1.wireOp",EDGE,"E1849"),sQuery(id+"F1.wireOp",EDGE,"E1850"),sQuery(id+"F1.wireOp",EDGE,"E1851"),sQuery(id+"F1.wireOp",EDGE,"E1852"),sQuery(id+"F1.wireOp",EDGE,"E1853"),sQuery(id+"F1.wireOp",EDGE,"E1854"),sQuery(id+"F1.wireOp",EDGE,"E1855"),sQuery(id+"F1.wireOp",EDGE,"E1856"),sQuery(id+"F1.wireOp",EDGE,"E1857"),sQuery(id+"F1.wireOp",EDGE,"E1858"),sQuery(id+"F1.wireOp",EDGE,"E1859"),sQuery(id+"F1.wireOp",EDGE,"E1860"),sQuery(id+"F1.wireOp",EDGE,"E1861"),sQuery(id+"F1.wireOp",EDGE,"E1862"),sQuery(id+"F1.wireOp",EDGE,"E1863"),sQuery(id+"F1.wireOp",EDGE,"E1864"),sQuery(id+"F1.wireOp",EDGE,"E1865"),sQuery(id+"F1.wireOp",EDGE,"E1866"),sQuery(id+"F1.wireOp",EDGE,"E1867"),sQuery(id+"F1.wireOp",EDGE,"E1868"),sQuery(id+"F1.wireOp",EDGE,"E1869"),sQuery(id+"F1.wireOp",EDGE,"E1870"),sQuery(id+"F1.wireOp",EDGE,"E1871"),sQuery(id+"F1.wireOp",EDGE,"E1872"),sQuery(id+"F1.wireOp",EDGE,"E1873"),sQuery(id+"F1.wireOp",EDGE,"E1874"),sQuery(id+"F1.wireOp",EDGE,"E1875"),sQuery(id+"F1.wireOp",EDGE,"E1876"),sQuery(id+"F1.wireOp",EDGE,"E1877"),sQuery(id+"F1.wireOp",EDGE,"E1878"),sQuery(id+"F1.wireOp",EDGE,"E1879"),sQuery(id+"F1.wireOp",EDGE,"E1880"),sQuery(id+"F1.wireOp",EDGE,"E1881"),sQuery(id+"F1.wireOp",EDGE,"E1882"),sQuery(id+"F1.wireOp",EDGE,"E1883"),sQuery(id+"F1.wireOp",EDGE,"E1884"),sQuery(id+"F1.wireOp",EDGE,"E1885"),sQuery(id+"F1.wireOp",EDGE,"E1886"),sQuery(id+"F1.wireOp",EDGE,"E1887"),sQuery(id+"F1.wireOp",EDGE,"E1888"),sQuery(id+"F1.wireOp",EDGE,"E1889"),sQuery(id+"F1.wireOp",EDGE,"E1890"),sQuery(id+"F1.wireOp",EDGE,"E1891"),sQuery(id+"F1.wireOp",EDGE,"E1892"),sQuery(id+"F1.wireOp",EDGE,"E1893"),sQuery(id+"F1.wireOp",EDGE,"E1894"),sQuery(id+"F1.wireOp",EDGE,"E1895"),sQuery(id+"F1.wireOp",EDGE,"E1896"),sQuery(id+"F1.wireOp",EDGE,"E1897"),sQuery(id+"F1.wireOp",EDGE,"E1898"),sQuery(id+"F1.wireOp",EDGE,"E1899"),sQuery(id+"F1.wireOp",EDGE,"E1900"),sQuery(id+"F1.wireOp",EDGE,"E1901"),sQuery(id+"F1.wireOp",EDGE,"E1902"),sQuery(id+"F1.wireOp",EDGE,"E1903"),sQuery(id+"F1.wireOp",EDGE,"E1904"),sQuery(id+"F1.wireOp",EDGE,"E1905"),sQuery(id+"F1.wireOp",EDGE,"E1906"),sQuery(id+"F1.wireOp",EDGE,"E1907"),sQuery(id+"F1.wireOp",EDGE,"E1908"),sQuery(id+"F1.wireOp",EDGE,"E1909"),sQuery(id+"F1.wireOp",EDGE,"E1910"),sQuery(id+"F1.wireOp",EDGE,"E1911"),sQuery(id+"F1.wireOp",EDGE,"E1912"),sQuery(id+"F1.wireOp",EDGE,"E1913"),sQuery(id+"F1.wireOp",EDGE,"E1914"),sQuery(id+"F1.wireOp",EDGE,"E1915"),sQuery(id+"F1.wireOp",EDGE,"E1916"),sQuery(id+"F1.wireOp",EDGE,"E1917"),sQuery(id+"F1.wireOp",EDGE,"E1918"),sQuery(id+"F1.wireOp",EDGE,"E1919"),sQuery(id+"F1.wireOp",EDGE,"E1920"),sQuery(id+"F1.wireOp",EDGE,"E1921"),sQuery(id+"F1.wireOp",EDGE,"E1922"),sQuery(id+"F1.wireOp",EDGE,"E1923"),sQuery(id+"F1.wireOp",EDGE,"E1924"),sQuery(id+"F1.wireOp",EDGE,"E1925"),sQuery(id+"F1.wireOp",EDGE,"E1926"),sQuery(id+"F1.wireOp",EDGE,"E1927"),sQuery(id+"F1.wireOp",EDGE,"E1928"),sQuery(id+"F1.wireOp",EDGE,"E1929"),sQuery(id+"F1.wireOp",EDGE,"E1930"),sQuery(id+"F1.wireOp",EDGE,"E1931"),sQuery(id+"F1.wireOp",EDGE,"E1932"),sQuery(id+"F1.wireOp",EDGE,"E1933"),sQuery(id+"F1.wireOp",EDGE,"E1934"),sQuery(id+"F1.wireOp",EDGE,"E1935"),sQuery(id+"F1.wireOp",EDGE,"E1936"),sQuery(id+"F1.wireOp",EDGE,"E1937"),sQuery(id+"F1.wireOp",EDGE,"E1938"),sQuery(id+"F1.wireOp",EDGE,"E1939"),sQuery(id+"F1.wireOp",EDGE,"E1940"),sQuery(id+"F1.wireOp",EDGE,"E1941"),sQuery(id+"F1.wireOp",EDGE,"E1942"),sQuery(id+"F1.wireOp",EDGE,"E1943"),sQuery(id+"F1.wireOp",EDGE,"E1944"),sQuery(id+"F1.wireOp",EDGE,"E1945"),sQuery(id+"F1.wireOp",EDGE,"E1946"),sQuery(id+"F1.wireOp",EDGE,"E1947"),sQuery(id+"F1.wireOp",EDGE,"E1948"),sQuery(id+"F1.wireOp",EDGE,"E1949"),sQuery(id+"F1.wireOp",EDGE,"E1950"),sQuery(id+"F1.wireOp",EDGE,"E1951"),sQuery(id+"F1.wireOp",EDGE,"E1952"),sQuery(id+"F1.wireOp",EDGE,"E1953"),sQuery(id+"F1.wireOp",EDGE,"E1954"),sQuery(id+"F1.wireOp",EDGE,"E1955"),sQuery(id+"F1.wireOp",EDGE,"E1956"),sQuery(id+"F1.wireOp",EDGE,"E1957"),sQuery(id+"F1.wireOp",EDGE,"E1958"),sQuery(id+"F1.wireOp",EDGE,"E1959"),sQuery(id+"F1.wireOp",EDGE,"E1960"),sQuery(id+"F1.wireOp",EDGE,"E1961"),sQuery(id+"F1.wireOp",EDGE,"E1962"),sQuery(id+"F1.wireOp",EDGE,"E1963"),sQuery(id+"F1.wireOp",EDGE,"E1964"),sQuery(id+"F1.wireOp",EDGE,"E1965"),sQuery(id+"F1.wireOp",EDGE,"E1966"),sQuery(id+"F1.wireOp",EDGE,"E1967"),sQuery(id+"F1.wireOp",EDGE,"E1968"),sQuery(id+"F1.wireOp",EDGE,"E1969"),sQuery(id+"F1.wireOp",EDGE,"E1970"),sQuery(id+"F1.wireOp",EDGE,"E1971"),sQuery(id+"F1.wireOp",EDGE,"E1972"),sQuery(id+"F1.wireOp",EDGE,"E1973"),sQuery(id+"F1.wireOp",EDGE,"E1974"),sQuery(id+"F1.wireOp",EDGE,"E1975"),sQuery(id+"F1.wireOp",EDGE,"E1976"),sQuery(id+"F1.wireOp",EDGE,"E1977"),sQuery(id+"F1.wireOp",EDGE,"E1978"),sQuery(id+"F1.wireOp",EDGE,"E1979"),sQuery(id+"F1.wireOp",EDGE,"E1980"),sQuery(id+"F1.wireOp",EDGE,"E1981"),sQuery(id+"F1.wireOp",EDGE,"E1982"),sQuery(id+"F1.wireOp",EDGE,"E1983"),sQuery(id+"F1.wireOp",EDGE,"E1984"),sQuery(id+"F1.wireOp",EDGE,"E1985"),sQuery(id+"F1.wireOp",EDGE,"E1986"),sQuery(id+"F1.wireOp",EDGE,"E1987"),sQuery(id+"F1.wireOp",EDGE,"E1988"),sQuery(id+"F1.wireOp",EDGE,"E1989"),sQuery(id+"F1.wireOp",EDGE,"E1990"),sQuery(id+"F1.wireOp",EDGE,"E1991"),sQuery(id+"F1.wireOp",EDGE,"E1992"),sQuery(id+"F1.wireOp",EDGE,"E1993"),sQuery(id+"F1.wireOp",EDGE,"E1994"),sQuery(id+"F1.wireOp",EDGE,"E1995"),sQuery(id+"F1.wireOp",EDGE,"E1996"),sQuery(id+"F1.wireOp",EDGE,"E1997"),sQuery(id+"F1.wireOp",EDGE,"E1998"),sQuery(id+"F1.wireOp",EDGE,"E1999"),sQuery(id+"F1.wireOp",EDGE,"E2000"),sQuery(id+"F1.wireOp",EDGE,"E2000"),sQuery(id+"F1.wireOp",EDGE,"E2001"),sQuery(id+"F1.wireOp",EDGE,"E2002"),sQuery(id+"F1.wireOp",EDGE,"E2003"),sQuery(id+"F1.wireOp",EDGE,"E2004"),sQuery(id+"F1.wireOp",EDGE,"E2005"),sQuery(id+"F1.wireOp",EDGE,"E2006"),sQuery(id+"F1.wireOp",EDGE,"E2007"),sQuery(id+"F1.wireOp",EDGE,"E2008"),sQuery(id+"F1.wireOp",EDGE,"E2009"),sQuery(id+"F1.wireOp",EDGE,"E2010"),sQuery(id+"F1.wireOp",EDGE,"E2011"),sQuery(id+"F1.wireOp",EDGE,"E2012"),sQuery(id+"F1.wireOp",EDGE,"E2013"),sQuery(id+"F1.wireOp",EDGE,"E2014"),sQuery(id+"F1.wireOp",EDGE,"E2015"),sQuery(id+"F1.wireOp",EDGE,"E2016"),sQuery(id+"F1.wireOp",EDGE,"E2017"),sQuery(id+"F1.wireOp",EDGE,"E2018"),sQuery(id+"F1.wireOp",EDGE,"E2019"),sQuery(id+"F1.wireOp",EDGE,"E2020"),sQuery(id+"F1.wireOp",EDGE,"E2021"),sQuery(id+"F1.wireOp",EDGE,"E2022"),sQuery(id+"F1.wireOp",EDGE,"E2023"),sQuery(id+"F1.wireOp",EDGE,"E2024"),sQuery(id+"F1.wireOp",EDGE,"E2025"),sQuery(id+"F1.wireOp",EDGE,"E2026"),sQuery(id+"F1.wireOp",EDGE,"E2027"),sQuery(id+"F1.wireOp",EDGE,"E2028"),sQuery(id+"F1.wireOp",EDGE,"E2029"),sQuery(id+"F1.wireOp",EDGE,"E2030"),sQuery(id+"F1.wireOp",EDGE,"E2031"),sQuery(id+"F1.wireOp",EDGE,"E2032"),sQuery(id+"F1.wireOp",EDGE,"E2033"),sQuery(id+"F1.wireOp",EDGE,"E2034"),sQuery(id+"F1.wireOp",EDGE,"E2035"),sQuery(id+"F1.wireOp",EDGE,"E2036"),sQuery(id+"F1.wireOp",EDGE,"E2037"),sQuery(id+"F1.wireOp",EDGE,"E2038"),sQuery(id+"F1.wireOp",EDGE,"E2039"),sQuery(id+"F1.wireOp",EDGE,"E2040"),sQuery(id+"F1.wireOp",EDGE,"E2041"),sQuery(id+"F1.wireOp",EDGE,"E2042"),sQuery(id+"F1.wireOp",EDGE,"E2043"),sQuery(id+"F1.wireOp",EDGE,"E2044"),sQuery(id+"F1.wireOp",EDGE,"E2045"),sQuery(id+"F1.wireOp",EDGE,"E2046"),sQuery(id+"F1.wireOp",EDGE,"E2047"),sQuery(id+"F1.wireOp",EDGE,"E2048"),sQuery(id+"F1.wireOp",EDGE,"E2049"),sQuery(id+"F1.wireOp",EDGE,"E2050"),sQuery(id+"F1.wireOp",EDGE,"E2051"),sQuery(id+"F1.wireOp",EDGE,"E2052"),sQuery(id+"F1.wireOp",EDGE,"E2053"),sQuery(id+"F1.wireOp",EDGE,"E2054"),sQuery(id+"F1.wireOp",EDGE,"E2055"),sQuery(id+"F1.wireOp",EDGE,"E2056"),sQuery(id+"F1.wireOp",EDGE,"E2057"),sQuery(id+"F1.wireOp",EDGE,"E2058"),sQuery(id+"F1.wireOp",EDGE,"E2059"),sQuery(id+"F1.wireOp",EDGE,"E2060"),sQuery(id+"F1.wireOp",EDGE,"E2061"),sQuery(id+"F1.wireOp",EDGE,"E2062"),sQuery(id+"F1.wireOp",EDGE,"E2063"),sQuery(id+"F1.wireOp",EDGE,"E2064"),sQuery(id+"F1.wireOp",EDGE,"E2065"),sQuery(id+"F1.wireOp",EDGE,"E2066"),sQuery(id+"F1.wireOp",EDGE,"E2067"),sQuery(id+"F1.wireOp",EDGE,"E2068"),sQuery(id+"F1.wireOp",EDGE,"E2069"),sQuery(id+"F1.wireOp",EDGE,"E2070"),sQuery(id+"F1.wireOp",EDGE,"E2071"),sQuery(id+"F1.wireOp",EDGE,"E2072"),sQuery(id+"F1.wireOp",EDGE,"E2073"),sQuery(id+"F1.wireOp",EDGE,"E2074"),sQuery(id+"F1.wireOp",EDGE,"E2075"),sQuery(id+"F1.wireOp",EDGE,"E2076"),sQuery(id+"F1.wireOp",EDGE,"E2077"),sQuery(id+"F1.wireOp",EDGE,"E2078"),sQuery(id+"F1.wireOp",EDGE,"E2079"),sQuery(id+"F1.wireOp",EDGE,"E2080"),sQuery(id+"F1.wireOp",EDGE,"E2081"),sQuery(id+"F1.wireOp",EDGE,"E2082"),sQuery(id+"F1.wireOp",EDGE,"E2083"),sQuery(id+"F1.wireOp",EDGE,"E2084"),sQuery(id+"F1.wireOp",EDGE,"E2085"),sQuery(id+"F1.wireOp",EDGE,"E2086"),sQuery(id+"F1.wireOp",EDGE,"E2087"),sQuery(id+"F1.wireOp",EDGE,"E2088"),sQuery(id+"F1.wireOp",EDGE,"E2089"),sQuery(id+"F1.wireOp",EDGE,"E2090"),sQuery(id+"F1.wireOp",EDGE,"E2091"),sQuery(id+"F1.wireOp",EDGE,"E2092"),sQuery(id+"F1.wireOp",EDGE,"E2093"),sQuery(id+"F1.wireOp",EDGE,"E2094"),sQuery(id+"F1.wireOp",EDGE,"E2095"),sQuery(id+"F1.wireOp",EDGE,"E2096"),sQuery(id+"F1.wireOp",EDGE,"E2097"),sQuery(id+"F1.wireOp",EDGE,"E2098"),sQuery(id+"F1.wireOp",EDGE,"E2099"),sQuery(id+"F1.wireOp",EDGE,"E2100"),sQuery(id+"F1.wireOp",EDGE,"E2101"),sQuery(id+"F1.wireOp",EDGE,"E2102"),sQuery(id+"F1.wireOp",EDGE,"E2103"),sQuery(id+"F1.wireOp",EDGE,"E2104"),sQuery(id+"F1.wireOp",EDGE,"E2105"),sQuery(id+"F1.wireOp",EDGE,"E2106"),sQuery(id+"F1.wireOp",EDGE,"E2107"),sQuery(id+"F1.wireOp",EDGE,"E2108"),sQuery(id+"F1.wireOp",EDGE,"E2109"),sQuery(id+"F1.wireOp",EDGE,"E2110"),sQuery(id+"F1.wireOp",EDGE,"E2111"),sQuery(id+"F1.wireOp",EDGE,"E2112"),sQuery(id+"F1.wireOp",EDGE,"E2113"),sQuery(id+"F1.wireOp",EDGE,"E2114"),sQuery(id+"F1.wireOp",EDGE,"E2115"),sQuery(id+"F1.wireOp",EDGE,"E2116"),sQuery(id+"F1.wireOp",EDGE,"E2117"),sQuery(id+"F1.wireOp",EDGE,"E2118"),sQuery(id+"F1.wireOp",EDGE,"E2119"),sQuery(id+"F1.wireOp",EDGE,"E2120"),sQuery(id+"F1.wireOp",EDGE,"E2121"),sQuery(id+"F1.wireOp",EDGE,"E2122"),sQuery(id+"F1.wireOp",EDGE,"E2123"),sQuery(id+"F1.wireOp",EDGE,"E2124"),sQuery(id+"F1.wireOp",EDGE,"E2125"),sQuery(id+"F1.wireOp",EDGE,"E2126"),sQuery(id+"F1.wireOp",EDGE,"E2127"),sQuery(id+"F1.wireOp",EDGE,"E2128"),sQuery(id+"F1.wireOp",EDGE,"E2129"),sQuery(id+"F1.wireOp",EDGE,"E2130"),sQuery(id+"F1.wireOp",EDGE,"E2131"),sQuery(id+"F1.wireOp",EDGE,"E2132"),sQuery(id+"F1.wireOp",EDGE,"E2133"),sQuery(id+"F1.wireOp",EDGE,"E2134"),sQuery(id+"F1.wireOp",EDGE,"E2135"),sQuery(id+"F1.wireOp",EDGE,"E2136"),sQuery(id+"F1.wireOp",EDGE,"E2137"),sQuery(id+"F1.wireOp",EDGE,"E2138"),sQuery(id+"F1.wireOp",EDGE,"E2139"),sQuery(id+"F1.wireOp",EDGE,"E2140"),sQuery(id+"F1.wireOp",EDGE,"E2141"),sQuery(id+"F1.wireOp",EDGE,"E2142"),sQuery(id+"F1.wireOp",EDGE,"E2143"),sQuery(id+"F1.wireOp",EDGE,"E2144"),sQuery(id+"F1.wireOp",EDGE,"E2145"),sQuery(id+"F1.wireOp",EDGE,"E2146"),sQuery(id+"F1.wireOp",EDGE,"E2147"),sQuery(id+"F1.wireOp",EDGE,"E2148"),sQuery(id+"F1.wireOp",EDGE,"E2149"),sQuery(id+"F1.wireOp",EDGE,"E2150"),sQuery(id+"F1.wireOp",EDGE,"E2151"),sQuery(id+"F1.wireOp",EDGE,"E2152"),sQuery(id+"F1.wireOp",EDGE,"E2153"),sQuery(id+"F1.wireOp",EDGE,"E2154"),sQuery(id+"F1.wireOp",EDGE,"E2155"),sQuery(id+"F1.wireOp",EDGE,"E2156"),sQuery(id+"F1.wireOp",EDGE,"E2157"),sQuery(id+"F1.wireOp",EDGE,"E2158"),sQuery(id+"F1.wireOp",EDGE,"E2159"),sQuery(id+"F1.wireOp",EDGE,"E2160"),sQuery(id+"F1.wireOp",EDGE,"E2161"),sQuery(id+"F1.wireOp",EDGE,"E2162"),sQuery(id+"F1.wireOp",EDGE,"E2163"),sQuery(id+"F1.wireOp",EDGE,"E2164"),sQuery(id+"F1.wireOp",EDGE,"E2165"),sQuery(id+"F1.wireOp",EDGE,"E2166"),sQuery(id+"F1.wireOp",EDGE,"E2167"),sQuery(id+"F1.wireOp",EDGE,"E2168"),sQuery(id+"F1.wireOp",EDGE,"E2169"),sQuery(id+"F1.wireOp",EDGE,"E2170"),sQuery(id+"F1.wireOp",EDGE,"E2171"),sQuery(id+"F1.wireOp",EDGE,"E2172"),sQuery(id+"F1.wireOp",EDGE,"E2173"),sQuery(id+"F1.wireOp",EDGE,"E2174"),sQuery(id+"F1.wireOp",EDGE,"E2175"),sQuery(id+"F1.wireOp",EDGE,"E2176"),sQuery(id+"F1.wireOp",EDGE,"E2177"),sQuery(id+"F1.wireOp",EDGE,"E2178"),sQuery(id+"F1.wireOp",EDGE,"E2179"),sQuery(id+"F1.wireOp",EDGE,"E2180"),sQuery(id+"F1.wireOp",EDGE,"E2181"),sQuery(id+"F1.wireOp",EDGE,"E2182"),sQuery(id+"F1.wireOp",EDGE,"E2183"),sQuery(id+"F1.wireOp",EDGE,"E2184"),sQuery(id+"F1.wireOp",EDGE,"E2185"),sQuery(id+"F1.wireOp",EDGE,"E2186"),sQuery(id+"F1.wireOp",EDGE,"E2187"),sQuery(id+"F1.wireOp",EDGE,"E2188"),sQuery(id+"F1.wireOp",EDGE,"E2189"),sQuery(id+"F1.wireOp",EDGE,"E2190"),sQuery(id+"F1.wireOp",EDGE,"E2191"),sQuery(id+"F1.wireOp",EDGE,"E2192"),sQuery(id+"F1.wireOp",EDGE,"E2193"),sQuery(id+"F1.wireOp",EDGE,"E2194"),sQuery(id+"F1.wireOp",EDGE,"E2195"),sQuery(id+"F1.wireOp",EDGE,"E2196"),sQuery(id+"F1.wireOp",EDGE,"E2197"),sQuery(id+"F1.wireOp",EDGE,"E2198"),sQuery(id+"F1.wireOp",EDGE,"E2199"),sQuery(id+"F1.wireOp",EDGE,"E2200"),sQuery(id+"F1.wireOp",EDGE,"E2201"),sQuery(id+"F1.wireOp",EDGE,"E2202"),sQuery(id+"F1.wireOp",EDGE,"E2203"),sQuery(id+"F1.wireOp",EDGE,"E2204"),sQuery(id+"F1.wireOp",EDGE,"E2205"),sQuery(id+"F1.wireOp",EDGE,"E2206"),sQuery(id+"F1.wireOp",EDGE,"E2207"),sQuery(id+"F1.wireOp",EDGE,"E2208"),sQuery(id+"F1.wireOp",EDGE,"E2209"),sQuery(id+"F1.wireOp",EDGE,"E2210"),sQuery(id+"F1.wireOp",EDGE,"E2211"),sQuery(id+"F1.wireOp",EDGE,"E2212"),sQuery(id+"F1.wireOp",EDGE,"E2213"),sQuery(id+"F1.wireOp",EDGE,"E2214"),sQuery(id+"F1.wireOp",EDGE,"E2215"),sQuery(id+"F1.wireOp",EDGE,"E2216"),sQuery(id+"F1.wireOp",EDGE,"E2217"),sQuery(id+"F1.wireOp",EDGE,"E2218"),sQuery(id+"F1.wireOp",EDGE,"E2219"),sQuery(id+"F1.wireOp",EDGE,"E2220"),sQuery(id+"F1.wireOp",EDGE,"E2221"),sQuery(id+"F1.wireOp",EDGE,"E2222"),sQuery(id+"F1.wireOp",EDGE,"E2223"),sQuery(id+"F1.wireOp",EDGE,"E2224"),sQuery(id+"F1.wireOp",EDGE,"E2225"),sQuery(id+"F1.wireOp",EDGE,"E2226"),sQuery(id+"F1.wireOp",EDGE,"E2227"),sQuery(id+"F1.wireOp",EDGE,"E2228"),sQuery(id+"F1.wireOp",EDGE,"E2229"),sQuery(id+"F1.wireOp",EDGE,"E2230"),sQuery(id+"F1.wireOp",EDGE,"E2231"),sQuery(id+"F1.wireOp",EDGE,"E2232"),sQuery(id+"F1.wireOp",EDGE,"E2233"),sQuery(id+"F1.wireOp",EDGE,"E2234"),sQuery(id+"F1.wireOp",EDGE,"E2235"),sQuery(id+"F1.wireOp",EDGE,"E2236"),sQuery(id+"F1.wireOp",EDGE,"E2237"),sQuery(id+"F1.wireOp",EDGE,"E2238"),sQuery(id+"F1.wireOp",EDGE,"E2239"),sQuery(id+"F1.wireOp",EDGE,"E2240"),sQuery(id+"F1.wireOp",EDGE,"E2241"),sQuery(id+"F1.wireOp",EDGE,"E2242"),sQuery(id+"F1.wireOp",EDGE,"E2243"),sQuery(id+"F1.wireOp",EDGE,"E2244"),sQuery(id+"F1.wireOp",EDGE,"E2245"),sQuery(id+"F1.wireOp",EDGE,"E2246"),sQuery(id+"F1.wireOp",EDGE,"E2247"),sQuery(id+"F1.wireOp",EDGE,"E2248"),sQuery(id+"F1.wireOp",EDGE,"E2249"),sQuery(id+"F1.wireOp",EDGE,"E2250"),sQuery(id+"F1.wireOp",EDGE,"E2251"),sQuery(id+"F1.wireOp",EDGE,"E2252"),sQuery(id+"F1.wireOp",EDGE,"E2253"),sQuery(id+"F1.wireOp",EDGE,"E2254"),sQuery(id+"F1.wireOp",EDGE,"E2255"),sQuery(id+"F1.wireOp",EDGE,"E2256"),sQuery(id+"F1.wireOp",EDGE,"E2257"),sQuery(id+"F1.wireOp",EDGE,"E2258"),sQuery(id+"F1.wireOp",EDGE,"E2259"),sQuery(id+"F1.wireOp",EDGE,"E2260"),sQuery(id+"F1.wireOp",EDGE,"E2261"),sQuery(id+"F1.wireOp",EDGE,"E2262"),sQuery(id+"F1.wireOp",EDGE,"E2263"),sQuery(id+"F1.wireOp",EDGE,"E2264"),sQuery(id+"F1.wireOp",EDGE,"E2265"),sQuery(id+"F1.wireOp",EDGE,"E2266"),sQuery(id+"F1.wireOp",EDGE,"E2267"),sQuery(id+"F1.wireOp",EDGE,"E2268"),sQuery(id+"F1.wireOp",EDGE,"E2269"),sQuery(id+"F1.wireOp",EDGE,"E2270"),sQuery(id+"F1.wireOp",EDGE,"E2271"),sQuery(id+"F1.wireOp",EDGE,"E2272"),sQuery(id+"F1.wireOp",EDGE,"E2273"),sQuery(id+"F1.wireOp",EDGE,"E2274"),sQuery(id+"F1.wireOp",EDGE,"E2275"),sQuery(id+"F1.wireOp",EDGE,"E2276"),sQuery(id+"F1.wireOp",EDGE,"E2277"),sQuery(id+"F1.wireOp",EDGE,"E2278"),sQuery(id+"F1.wireOp",EDGE,"E2279"),sQuery(id+"F1.wireOp",EDGE,"E2280"),sQuery(id+"F1.wireOp",EDGE,"E2281"),sQuery(id+"F1.wireOp",EDGE,"E2282"),sQuery(id+"F1.wireOp",EDGE,"E2283"),sQuery(id+"F1.wireOp",EDGE,"E2284"),sQuery(id+"F1.wireOp",EDGE,"E2285"),sQuery(id+"F1.wireOp",EDGE,"E2286"),sQuery(id+"F1.wireOp",EDGE,"E2287"),sQuery(id+"F1.wireOp",EDGE,"E2288"),sQuery(id+"F1.wireOp",EDGE,"E2289"),sQuery(id+"F1.wireOp",EDGE,"E2290"),sQuery(id+"F1.wireOp",EDGE,"E2291"),sQuery(id+"F1.wireOp",EDGE,"E2292"),sQuery(id+"F1.wireOp",EDGE,"E2293"),sQuery(id+"F1.wireOp",EDGE,"E2294"),sQuery(id+"F1.wireOp",EDGE,"E2295"),sQuery(id+"F1.wireOp",EDGE,"E2296"),sQuery(id+"F1.wireOp",EDGE,"E2297"),sQuery(id+"F1.wireOp",EDGE,"E2298"),sQuery(id+"F1.wireOp",EDGE,"E2299"),sQuery(id+"F1.wireOp",EDGE,"E2300"),sQuery(id+"F1.wireOp",EDGE,"E2301"),sQuery(id+"F1.wireOp",EDGE,"E2302"),sQuery(id+"F1.wireOp",EDGE,"E2303"),sQuery(id+"F1.wireOp",EDGE,"E2304"),sQuery(id+"F1.wireOp",EDGE,"E2305"),sQuery(id+"F1.wireOp",EDGE,"E2306"),sQuery(id+"F1.wireOp",EDGE,"E2307"),sQuery(id+"F1.wireOp",EDGE,"E2308"),sQuery(id+"F1.wireOp",EDGE,"E2309"),sQuery(id+"F1.wireOp",EDGE,"E2310"),sQuery(id+"F1.wireOp",EDGE,"E2311"),sQuery(id+"F1.wireOp",EDGE,"E2312"),sQuery(id+"F1.wireOp",EDGE,"E2313"),sQuery(id+"F1.wireOp",EDGE,"E2314"),sQuery(id+"F1.wireOp",EDGE,"E2315"),sQuery(id+"F1.wireOp",EDGE,"E2316"),sQuery(id+"F1.wireOp",EDGE,"E2317"),sQuery(id+"F1.wireOp",EDGE,"E2318"),sQuery(id+"F1.wireOp",EDGE,"E2319"),sQuery(id+"F1.wireOp",EDGE,"E2320"),sQuery(id+"F1.wireOp",EDGE,"E2321"),sQuery(id+"F1.wireOp",EDGE,"E2322"),sQuery(id+"F1.wireOp",EDGE,"E2323"),sQuery(id+"F1.wireOp",EDGE,"E2324"),sQuery(id+"F1.wireOp",EDGE,"E2325"),sQuery(id+"F1.wireOp",EDGE,"E2326"),sQuery(id+"F1.wireOp",EDGE,"E2327"),sQuery(id+"F1.wireOp",EDGE,"E2328"),sQuery(id+"F1.wireOp",EDGE,"E2329"),sQuery(id+"F1.wireOp",EDGE,"E2330"),sQuery(id+"F1.wireOp",EDGE,"E2331"),sQuery(id+"F1.wireOp",EDGE,"E2332"),sQuery(id+"F1.wireOp",EDGE,"E2333"),sQuery(id+"F1.wireOp",EDGE,"E2334"),sQuery(id+"F1.wireOp",EDGE,"E2335"),sQuery(id+"F1.wireOp",EDGE,"E2336"),sQuery(id+"F1.wireOp",EDGE,"E2337"),sQuery(id+"F1.wireOp",EDGE,"E2338"),sQuery(id+"F1.wireOp",EDGE,"E2339"),sQuery(id+"F1.wireOp",EDGE,"E2340"),sQuery(id+"F1.wireOp",EDGE,"E2341"),sQuery(id+"F1.wireOp",EDGE,"E2342"),sQuery(id+"F1.wireOp",EDGE,"E2343"),sQuery(id+"F1.wireOp",EDGE,"E2344"),sQuery(id+"F1.wireOp",EDGE,"E2345"),sQuery(id+"F1.wireOp",EDGE,"E2346"),sQuery(id+"F1.wireOp",EDGE,"E2347"),sQuery(id+"F1.wireOp",EDGE,"E2348"),sQuery(id+"F1.wireOp",EDGE,"E2349"),sQuery(id+"F1.wireOp",EDGE,"E2350"),sQuery(id+"F1.wireOp",EDGE,"E2351"),sQuery(id+"F1.wireOp",EDGE,"E2352"),sQuery(id+"F1.wireOp",EDGE,"E2353"),sQuery(id+"F1.wireOp",EDGE,"E2354"),sQuery(id+"F1.wireOp",EDGE,"E2355"),sQuery(id+"F1.wireOp",EDGE,"E2356"),sQuery(id+"F1.wireOp",EDGE,"E2357"),sQuery(id+"F1.wireOp",EDGE,"E2358"),sQuery(id+"F1.wireOp",EDGE,"E2359"),sQuery(id+"F1.wireOp",EDGE,"E2360"),sQuery(id+"F1.wireOp",EDGE,"E2361"),sQuery(id+"F1.wireOp",EDGE,"E2362"),sQuery(id+"F1.wireOp",EDGE,"E2363"),sQuery(id+"F1.wireOp",EDGE,"E2364"),sQuery(id+"F1.wireOp",EDGE,"E2365"),sQuery(id+"F1.wireOp",EDGE,"E2366"),sQuery(id+"F1.wireOp",EDGE,"E2367"),sQuery(id+"F1.wireOp",EDGE,"E2368"),sQuery(id+"F1.wireOp",EDGE,"E2369"),sQuery(id+"F1.wireOp",EDGE,"E2370"),sQuery(id+"F1.wireOp",EDGE,"E2371"),sQuery(id+"F1.wireOp",EDGE,"E2372"),sQuery(id+"F1.wireOp",EDGE,"E2373"),sQuery(id+"F1.wireOp",EDGE,"E2374"),sQuery(id+"F1.wireOp",EDGE,"E2375"),sQuery(id+"F1.wireOp",EDGE,"E2376"),sQuery(id+"F1.wireOp",EDGE,"E2377"),sQuery(id+"F1.wireOp",EDGE,"E2378"),sQuery(id+"F1.wireOp",EDGE,"E2379"),sQuery(id+"F1.wireOp",EDGE,"E2380"),sQuery(id+"F1.wireOp",EDGE,"E2381"),sQuery(id+"F1.wireOp",EDGE,"E2382"),sQuery(id+"F1.wireOp",EDGE,"E2383"),sQuery(id+"F1.wireOp",EDGE,"E2384"),sQuery(id+"F1.wireOp",EDGE,"E2385"),sQuery(id+"F1.wireOp",EDGE,"E2386"),sQuery(id+"F1.wireOp",EDGE,"E2387"),sQuery(id+"F1.wireOp",EDGE,"E2388"),sQuery(id+"F1.wireOp",EDGE,"E2389"),sQuery(id+"F1.wireOp",EDGE,"E2390"),sQuery(id+"F1.wireOp",EDGE,"E2391"),sQuery(id+"F1.wireOp",EDGE,"E2392"),sQuery(id+"F1.wireOp",EDGE,"E2393"),sQuery(id+"F1.wireOp",EDGE,"E2394"),sQuery(id+"F1.wireOp",EDGE,"E2395"),sQuery(id+"F1.wireOp",EDGE,"E2396"),sQuery(id+"F1.wireOp",EDGE,"E2397"),sQuery(id+"F1.wireOp",EDGE,"E2398"),sQuery(id+"F1.wireOp",EDGE,"E2399"),sQuery(id+"F1.wireOp",EDGE,"E2400"),sQuery(id+"F1.wireOp",EDGE,"E2401"),sQuery(id+"F1.wireOp",EDGE,"E2402"),sQuery(id+"F1.wireOp",EDGE,"E2403"),sQuery(id+"F1.wireOp",EDGE,"E2404"),sQuery(id+"F1.wireOp",EDGE,"E2405"),sQuery(id+"F1.wireOp",EDGE,"E2406"),sQuery(id+"F1.wireOp",EDGE,"E2407"),sQuery(id+"F1.wireOp",EDGE,"E2408"),sQuery(id+"F1.wireOp",EDGE,"E2409"),sQuery(id+"F1.wireOp",EDGE,"E2410"),sQuery(id+"F1.wireOp",EDGE,"E2411"),sQuery(id+"F1.wireOp",EDGE,"E2412"),sQuery(id+"F1.wireOp",EDGE,"E2413"),sQuery(id+"F1.wireOp",EDGE,"E2414"),sQuery(id+"F1.wireOp",EDGE,"E2415"),sQuery(id+"F1.wireOp",EDGE,"E2416"),sQuery(id+"F1.wireOp",EDGE,"E2417"),sQuery(id+"F1.wireOp",EDGE,"E2418"),sQuery(id+"F1.wireOp",EDGE,"E2419"),sQuery(id+"F1.wireOp",EDGE,"E2420"),sQuery(id+"F1.wireOp",EDGE,"E2421"),sQuery(id+"F1.wireOp",EDGE,"E2422"),sQuery(id+"F1.wireOp",EDGE,"E2423"),sQuery(id+"F1.wireOp",EDGE,"E2424"),sQuery(id+"F1.wireOp",EDGE,"E2425"),sQuery(id+"F1.wireOp",EDGE,"E2426"),sQuery(id+"F1.wireOp",EDGE,"E2427"),sQuery(id+"F1.wireOp",EDGE,"E2428"),sQuery(id+"F1.wireOp",EDGE,"E2429"),sQuery(id+"F1.wireOp",EDGE,"E2430"),sQuery(id+"F1.wireOp",EDGE,"E2431"),sQuery(id+"F1.wireOp",EDGE,"E2432"),sQuery(id+"F1.wireOp",EDGE,"E2433"),sQuery(id+"F1.wireOp",EDGE,"E2434"),sQuery(id+"F1.wireOp",EDGE,"E2435"),sQuery(id+"F1.wireOp",EDGE,"E2436"),sQuery(id+"F1.wireOp",EDGE,"E2437"),sQuery(id+"F1.wireOp",EDGE,"E2438"),sQuery(id+"F1.wireOp",EDGE,"E2439"),sQuery(id+"F1.wireOp",EDGE,"E2440"),sQuery(id+"F1.wireOp",EDGE,"E2441"),sQuery(id+"F1.wireOp",EDGE,"E2442"),sQuery(id+"F1.wireOp",EDGE,"E2443"),sQuery(id+"F1.wireOp",EDGE,"E2444"),sQuery(id+"F1.wireOp",EDGE,"E2445"),sQuery(id+"F1.wireOp",EDGE,"E2446"),sQuery(id+"F1.wireOp",EDGE,"E2447"),sQuery(id+"F1.wireOp",EDGE,"E2448"),sQuery(id+"F1.wireOp",EDGE,"E2449"),sQuery(id+"F1.wireOp",EDGE,"E2450"),sQuery(id+"F1.wireOp",EDGE,"E2451"),sQuery(id+"F1.wireOp",EDGE,"E2452"),sQuery(id+"F1.wireOp",EDGE,"E2453"),sQuery(id+"F1.wireOp",EDGE,"E2454"),sQuery(id+"F1.wireOp",EDGE,"E2455"),sQuery(id+"F1.wireOp",EDGE,"E2456"),sQuery(id+"F1.wireOp",EDGE,"E2457"),sQuery(id+"F1.wireOp",EDGE,"E2458"),sQuery(id+"F1.wireOp",EDGE,"E2459"),sQuery(id+"F1.wireOp",EDGE,"E2460"),sQuery(id+"F1.wireOp",EDGE,"E2461"),sQuery(id+"F1.wireOp",EDGE,"E2462"),sQuery(id+"F1.wireOp",EDGE,"E2463"),sQuery(id+"F1.wireOp",EDGE,"E2464"),sQuery(id+"F1.wireOp",EDGE,"E2465"),sQuery(id+"F1.wireOp",EDGE,"E2466"),sQuery(id+"F1.wireOp",EDGE,"E2467"),sQuery(id+"F1.wireOp",EDGE,"E2468"),sQuery(id+"F1.wireOp",EDGE,"E2469"),sQuery(id+"F1.wireOp",EDGE,"E2470"),sQuery(id+"F1.wireOp",EDGE,"E2471"),sQuery(id+"F1.wireOp",EDGE,"E2472"),sQuery(id+"F1.wireOp",EDGE,"E2473"),sQuery(id+"F1.wireOp",EDGE,"E2474"),sQuery(id+"F1.wireOp",EDGE,"E2475"),sQuery(id+"F1.wireOp",EDGE,"E2476"),sQuery(id+"F1.wireOp",EDGE,"E2477"),sQuery(id+"F1.wireOp",EDGE,"E2478"),sQuery(id+"F1.wireOp",EDGE,"E2479"),sQuery(id+"F1.wireOp",EDGE,"E2480"),sQuery(id+"F1.wireOp",EDGE,"E2481"),sQuery(id+"F1.wireOp",EDGE,"E2482"),sQuery(id+"F1.wireOp",EDGE,"E2483"),sQuery(id+"F1.wireOp",EDGE,"E2484"),sQuery(id+"F1.wireOp",EDGE,"E2485"),sQuery(id+"F1.wireOp",EDGE,"E2486"),sQuery(id+"F1.wireOp",EDGE,"E2487"),sQuery(id+"F1.wireOp",EDGE,"E2488"),sQuery(id+"F1.wireOp",EDGE,"E2489"),sQuery(id+"F1.wireOp",EDGE,"E2490"),sQuery(id+"F1.wireOp",EDGE,"E2491"),sQuery(id+"F1.wireOp",EDGE,"E2492"),sQuery(id+"F1.wireOp",EDGE,"E2493"),sQuery(id+"F1.wireOp",EDGE,"E2494"),sQuery(id+"F1.wireOp",EDGE,"E2495"),sQuery(id+"F1.wireOp",EDGE,"E2496"),sQuery(id+"F1.wireOp",EDGE,"E2497"),sQuery(id+"F1.wireOp",EDGE,"E2498"),sQuery(id+"F1.wireOp",EDGE,"E2499"),sQuery(id+"F1.wireOp",EDGE,"E2500"),sQuery(id+"F1.wireOp",EDGE,"E2501"),sQuery(id+"F1.wireOp",EDGE,"E2502"),sQuery(id+"F1.wireOp",EDGE,"E2503"),sQuery(id+"F1.wireOp",EDGE,"E2504"),sQuery(id+"F1.wireOp",EDGE,"E2505"),sQuery(id+"F1.wireOp",EDGE,"E2506"),sQuery(id+"F1.wireOp",EDGE,"E2507"),sQuery(id+"F1.wireOp",EDGE,"E2508"),sQuery(id+"F1.wireOp",EDGE,"E2509"),sQuery(id+"F1.wireOp",EDGE,"E2510"),sQuery(id+"F1.wireOp",EDGE,"E2511"),sQuery(id+"F1.wireOp",EDGE,"E2512"),sQuery(id+"F1.wireOp",EDGE,"E2513"),sQuery(id+"F1.wireOp",EDGE,"E2514"),sQuery(id+"F1.wireOp",EDGE,"E2515"),sQuery(id+"F1.wireOp",EDGE,"E2516"),sQuery(id+"F1.wireOp",EDGE,"E2517"),sQuery(id+"F1.wireOp",EDGE,"E2518"),sQuery(id+"F1.wireOp",EDGE,"E2519"),sQuery(id+"F1.wireOp",EDGE,"E2520"),sQuery(id+"F1.wireOp",EDGE,"E2521"),sQuery(id+"F1.wireOp",EDGE,"E2522"),sQuery(id+"F1.wireOp",EDGE,"E2523"),sQuery(id+"F1.wireOp",EDGE,"E2524"),sQuery(id+"F1.wireOp",EDGE,"E2525"),sQuery(id+"F1.wireOp",EDGE,"E2526"),sQuery(id+"F1.wireOp",EDGE,"E2527"),sQuery(id+"F1.wireOp",EDGE,"E2528"),sQuery(id+"F1.wireOp",EDGE,"E2529"),sQuery(id+"F1.wireOp",EDGE,"E2530"),sQuery(id+"F1.wireOp",EDGE,"E2531"),sQuery(id+"F1.wireOp",EDGE,"E2532"),sQuery(id+"F1.wireOp",EDGE,"E2533"),sQuery(id+"F1.wireOp",EDGE,"E2534"),sQuery(id+"F1.wireOp",EDGE,"E2535"),sQuery(id+"F1.wireOp",EDGE,"E2536"),sQuery(id+"F1.wireOp",EDGE,"E2537"),sQuery(id+"F1.wireOp",EDGE,"E2538"),sQuery(id+"F1.wireOp",EDGE,"E2539"),sQuery(id+"F1.wireOp",EDGE,"E2540"),sQuery(id+"F1.wireOp",EDGE,"E2541"),sQuery(id+"F1.wireOp",EDGE,"E2542"),sQuery(id+"F1.wireOp",EDGE,"E2543"),sQuery(id+"F1.wireOp",EDGE,"E2544"),sQuery(id+"F1.wireOp",EDGE,"E2545"),sQuery(id+"F1.wireOp",EDGE,"E2546"),sQuery(id+"F1.wireOp",EDGE,"E2547"),sQuery(id+"F1.wireOp",EDGE,"E2548"),sQuery(id+"F1.wireOp",EDGE,"E2549"),sQuery(id+"F1.wireOp",EDGE,"E2550"),sQuery(id+"F1.wireOp",EDGE,"E2551"),sQuery(id+"F1.wireOp",EDGE,"E2552"),sQuery(id+"F1.wireOp",EDGE,"E2553"),sQuery(id+"F1.wireOp",EDGE,"E2554"),sQuery(id+"F1.wireOp",EDGE,"E2555"),sQuery(id+"F1.wireOp",EDGE,"E2556"),sQuery(id+"F1.wireOp",EDGE,"E2557"),sQuery(id+"F1.wireOp",EDGE,"E2558"),sQuery(id+"F1.wireOp",EDGE,"E2559"),sQuery(id+"F1.wireOp",EDGE,"E2560"),sQuery(id+"F1.wireOp",EDGE,"E2561"),sQuery(id+"F1.wireOp",EDGE,"E2562"),sQuery(id+"F1.wireOp",EDGE,"E2563"),sQuery(id+"F1.wireOp",EDGE,"E2564"),sQuery(id+"F1.wireOp",EDGE,"E2565"),sQuery(id+"F1.wireOp",EDGE,"E2566"),sQuery(id+"F1.wireOp",EDGE,"E2567"),sQuery(id+"F1.wireOp",EDGE,"E2568"),sQuery(id+"F1.wireOp",EDGE,"E2569"),sQuery(id+"F1.wireOp",EDGE,"E2570"),sQuery(id+"F1.wireOp",EDGE,"E2571"),sQuery(id+"F1.wireOp",EDGE,"E2572"),sQuery(id+"F1.wireOp",EDGE,"E2573"),sQuery(id+"F1.wireOp",EDGE,"E2574"),sQuery(id+"F1.wireOp",EDGE,"E2575"),sQuery(id+"F1.wireOp",EDGE,"E2576"),sQuery(id+"F1.wireOp",EDGE,"E2577"),sQuery(id+"F1.wireOp",EDGE,"E2578"),sQuery(id+"F1.wireOp",EDGE,"E2579"),sQuery(id+"F1.wireOp",EDGE,"E2580"),sQuery(id+"F1.wireOp",EDGE,"E2581"),sQuery(id+"F1.wireOp",EDGE,"E2582"),sQuery(id+"F1.wireOp",EDGE,"E2583"),sQuery(id+"F1.wireOp",EDGE,"E2584"),sQuery(id+"F1.wireOp",EDGE,"E2585"),sQuery(id+"F1.wireOp",EDGE,"E2586"),sQuery(id+"F1.wireOp",EDGE,"E2587"),sQuery(id+"F1.wireOp",EDGE,"E2588"),sQuery(id+"F1.wireOp",EDGE,"E2589"),sQuery(id+"F1.wireOp",EDGE,"E2590"),sQuery(id+"F1.wireOp",EDGE,"E2591"),sQuery(id+"F1.wireOp",EDGE,"E2592"),sQuery(id+"F1.wireOp",EDGE,"E2593"),sQuery(id+"F1.wireOp",EDGE,"E2594"),sQuery(id+"F1.wireOp",EDGE,"E2595"),sQuery(id+"F1.wireOp",EDGE,"E2596"),sQuery(id+"F1.wireOp",EDGE,"E2597"),sQuery(id+"F1.wireOp",EDGE,"E2598"),sQuery(id+"F1.wireOp",EDGE,"E2599"),sQuery(id+"F1.wireOp",EDGE,"E2600"),sQuery(id+"F1.wireOp",EDGE,"E2601"),sQuery(id+"F1.wireOp",EDGE,"E2602"),sQuery(id+"F1.wireOp",EDGE,"E2603"),sQuery(id+"F1.wireOp",EDGE,"E2604"),sQuery(id+"F1.wireOp",EDGE,"E2605"),sQuery(id+"F1.wireOp",EDGE,"E2606"),sQuery(id+"F1.wireOp",EDGE,"E2607"),sQuery(id+"F1.wireOp",EDGE,"E2608"),sQuery(id+"F1.wireOp",EDGE,"E2609"),sQuery(id+"F1.wireOp",EDGE,"E2610"),sQuery(id+"F1.wireOp",EDGE,"E2611"),sQuery(id+"F1.wireOp",EDGE,"E2612"),sQuery(id+"F1.wireOp",EDGE,"E2613"),sQuery(id+"F1.wireOp",EDGE,"E2614"),sQuery(id+"F1.wireOp",EDGE,"E2615"),sQuery(id+"F1.wireOp",EDGE,"E2616"),sQuery(id+"F1.wireOp",EDGE,"E2617"),sQuery(id+"F1.wireOp",EDGE,"E2618"),sQuery(id+"F1.wireOp",EDGE,"E2619"),sQuery(id+"F1.wireOp",EDGE,"E2620"),sQuery(id+"F1.wireOp",EDGE,"E2622")])]});
            var Q1;
            Q1=sQuery(id+"F5.wireOp",EDGE,"E2623");
            transform(context, id + "F8", {"entities" : qUnion([Q0]), "transformType" : TransformType.ROTATION, "transformAxis" : qUnion([Q1]), "angle" : 30 * degree, "oppositeDirection" : true, "makeCopy" : false});
        }
        {
            var Q0;
            Q0=makeQuery(id+"F2.opExtrude","SWEPT_BODY",BODY,{"disambiguationData":[OSD([sQuery(id+"F1.wireOp",EDGE,"E15"),sQuery(id+"F1.wireOp",EDGE,"E16"),sQuery(id+"F1.wireOp",EDGE,"E17"),sQuery(id+"F1.wireOp",EDGE,"E18"),sQuery(id+"F1.wireOp",EDGE,"E19"),sQuery(id+"F1.wireOp",EDGE,"E20"),sQuery(id+"F1.wireOp",EDGE,"E21"),sQuery(id+"F1.wireOp",EDGE,"E22"),sQuery(id+"F1.wireOp",EDGE,"E23"),sQuery(id+"F1.wireOp",EDGE,"E24"),sQuery(id+"F1.wireOp",EDGE,"E25"),sQuery(id+"F1.wireOp",EDGE,"E26"),sQuery(id+"F1.wireOp",EDGE,"E27"),sQuery(id+"F1.wireOp",EDGE,"E28"),sQuery(id+"F1.wireOp",EDGE,"E29"),sQuery(id+"F1.wireOp",EDGE,"E30"),sQuery(id+"F1.wireOp",EDGE,"E31"),sQuery(id+"F1.wireOp",EDGE,"E32"),sQuery(id+"F1.wireOp",EDGE,"E33"),sQuery(id+"F1.wireOp",EDGE,"E34"),sQuery(id+"F1.wireOp",EDGE,"E35"),sQuery(id+"F1.wireOp",EDGE,"E36"),sQuery(id+"F1.wireOp",EDGE,"E37"),sQuery(id+"F1.wireOp",EDGE,"E38"),sQuery(id+"F1.wireOp",EDGE,"E39"),sQuery(id+"F1.wireOp",EDGE,"E40"),sQuery(id+"F1.wireOp",EDGE,"E41"),sQuery(id+"F1.wireOp",EDGE,"E42"),sQuery(id+"F1.wireOp",EDGE,"E43"),sQuery(id+"F1.wireOp",EDGE,"E44"),sQuery(id+"F1.wireOp",EDGE,"E45"),sQuery(id+"F1.wireOp",EDGE,"E45"),sQuery(id+"F1.wireOp",EDGE,"E46"),sQuery(id+"F1.wireOp",EDGE,"E47"),sQuery(id+"F1.wireOp",EDGE,"E48"),sQuery(id+"F1.wireOp",EDGE,"E49"),sQuery(id+"F1.wireOp",EDGE,"E50"),sQuery(id+"F1.wireOp",EDGE,"E51"),sQuery(id+"F1.wireOp",EDGE,"E52"),sQuery(id+"F1.wireOp",EDGE,"E53"),sQuery(id+"F1.wireOp",EDGE,"E54"),sQuery(id+"F1.wireOp",EDGE,"E55"),sQuery(id+"F1.wireOp",EDGE,"E56"),sQuery(id+"F1.wireOp",EDGE,"E57"),sQuery(id+"F1.wireOp",EDGE,"E58"),sQuery(id+"F1.wireOp",EDGE,"E59"),sQuery(id+"F1.wireOp",EDGE,"E60"),sQuery(id+"F1.wireOp",EDGE,"E61"),sQuery(id+"F1.wireOp",EDGE,"E62"),sQuery(id+"F1.wireOp",EDGE,"E63"),sQuery(id+"F1.wireOp",EDGE,"E64"),sQuery(id+"F1.wireOp",EDGE,"E65"),sQuery(id+"F1.wireOp",EDGE,"E66"),sQuery(id+"F1.wireOp",EDGE,"E67"),sQuery(id+"F1.wireOp",EDGE,"E68"),sQuery(id+"F1.wireOp",EDGE,"E69"),sQuery(id+"F1.wireOp",EDGE,"E70"),sQuery(id+"F1.wireOp",EDGE,"E71"),sQuery(id+"F1.wireOp",EDGE,"E72"),sQuery(id+"F1.wireOp",EDGE,"E73"),sQuery(id+"F1.wireOp",EDGE,"E74"),sQuery(id+"F1.wireOp",EDGE,"E75"),sQuery(id+"F1.wireOp",EDGE,"E76"),sQuery(id+"F1.wireOp",EDGE,"E77"),sQuery(id+"F1.wireOp",EDGE,"E78"),sQuery(id+"F1.wireOp",EDGE,"E79"),sQuery(id+"F1.wireOp",EDGE,"E80"),sQuery(id+"F1.wireOp",EDGE,"E81"),sQuery(id+"F1.wireOp",EDGE,"E82"),sQuery(id+"F1.wireOp",EDGE,"E83"),sQuery(id+"F1.wireOp",EDGE,"E84"),sQuery(id+"F1.wireOp",EDGE,"E85"),sQuery(id+"F1.wireOp",EDGE,"E86"),sQuery(id+"F1.wireOp",EDGE,"E87"),sQuery(id+"F1.wireOp",EDGE,"E88"),sQuery(id+"F1.wireOp",EDGE,"E89"),sQuery(id+"F1.wireOp",EDGE,"E90"),sQuery(id+"F1.wireOp",EDGE,"E91"),sQuery(id+"F1.wireOp",EDGE,"E92"),sQuery(id+"F1.wireOp",EDGE,"E93"),sQuery(id+"F1.wireOp",EDGE,"E94"),sQuery(id+"F1.wireOp",EDGE,"E95"),sQuery(id+"F1.wireOp",EDGE,"E96"),sQuery(id+"F1.wireOp",EDGE,"E97"),sQuery(id+"F1.wireOp",EDGE,"E98"),sQuery(id+"F1.wireOp",EDGE,"E99"),sQuery(id+"F1.wireOp",EDGE,"E100"),sQuery(id+"F1.wireOp",EDGE,"E101"),sQuery(id+"F1.wireOp",EDGE,"E102"),sQuery(id+"F1.wireOp",EDGE,"E103"),sQuery(id+"F1.wireOp",EDGE,"E104"),sQuery(id+"F1.wireOp",EDGE,"E104"),sQuery(id+"F1.wireOp",EDGE,"E105"),sQuery(id+"F1.wireOp",EDGE,"E106"),sQuery(id+"F1.wireOp",EDGE,"E107"),sQuery(id+"F1.wireOp",EDGE,"E108"),sQuery(id+"F1.wireOp",EDGE,"E109"),sQuery(id+"F1.wireOp",EDGE,"E110"),sQuery(id+"F1.wireOp",EDGE,"E111"),sQuery(id+"F1.wireOp",EDGE,"E112"),sQuery(id+"F1.wireOp",EDGE,"E113"),sQuery(id+"F1.wireOp",EDGE,"E114"),sQuery(id+"F1.wireOp",EDGE,"E115"),sQuery(id+"F1.wireOp",EDGE,"E116"),sQuery(id+"F1.wireOp",EDGE,"E117"),sQuery(id+"F1.wireOp",EDGE,"E118"),sQuery(id+"F1.wireOp",EDGE,"E119"),sQuery(id+"F1.wireOp",EDGE,"E120"),sQuery(id+"F1.wireOp",EDGE,"E121"),sQuery(id+"F1.wireOp",EDGE,"E122"),sQuery(id+"F1.wireOp",EDGE,"E123"),sQuery(id+"F1.wireOp",EDGE,"E124"),sQuery(id+"F1.wireOp",EDGE,"E125"),sQuery(id+"F1.wireOp",EDGE,"E126"),sQuery(id+"F1.wireOp",EDGE,"E127"),sQuery(id+"F1.wireOp",EDGE,"E128"),sQuery(id+"F1.wireOp",EDGE,"E129"),sQuery(id+"F1.wireOp",EDGE,"E130"),sQuery(id+"F1.wireOp",EDGE,"E131"),sQuery(id+"F1.wireOp",EDGE,"E132"),sQuery(id+"F1.wireOp",EDGE,"E133"),sQuery(id+"F1.wireOp",EDGE,"E134"),sQuery(id+"F1.wireOp",EDGE,"E135"),sQuery(id+"F1.wireOp",EDGE,"E136"),sQuery(id+"F1.wireOp",EDGE,"E137"),sQuery(id+"F1.wireOp",EDGE,"E138"),sQuery(id+"F1.wireOp",EDGE,"E139"),sQuery(id+"F1.wireOp",EDGE,"E140"),sQuery(id+"F1.wireOp",EDGE,"E141"),sQuery(id+"F1.wireOp",EDGE,"E142"),sQuery(id+"F1.wireOp",EDGE,"E143"),sQuery(id+"F1.wireOp",EDGE,"E144"),sQuery(id+"F1.wireOp",EDGE,"E145"),sQuery(id+"F1.wireOp",EDGE,"E146"),sQuery(id+"F1.wireOp",EDGE,"E147"),sQuery(id+"F1.wireOp",EDGE,"E148"),sQuery(id+"F1.wireOp",EDGE,"E149"),sQuery(id+"F1.wireOp",EDGE,"E150"),sQuery(id+"F1.wireOp",EDGE,"E151"),sQuery(id+"F1.wireOp",EDGE,"E152"),sQuery(id+"F1.wireOp",EDGE,"E153"),sQuery(id+"F1.wireOp",EDGE,"E154"),sQuery(id+"F1.wireOp",EDGE,"E155"),sQuery(id+"F1.wireOp",EDGE,"E156"),sQuery(id+"F1.wireOp",EDGE,"E157"),sQuery(id+"F1.wireOp",EDGE,"E158"),sQuery(id+"F1.wireOp",EDGE,"E159"),sQuery(id+"F1.wireOp",EDGE,"E160"),sQuery(id+"F1.wireOp",EDGE,"E161"),sQuery(id+"F1.wireOp",EDGE,"E162"),sQuery(id+"F1.wireOp",EDGE,"E163"),sQuery(id+"F1.wireOp",EDGE,"E164"),sQuery(id+"F1.wireOp",EDGE,"E165"),sQuery(id+"F1.wireOp",EDGE,"E166"),sQuery(id+"F1.wireOp",EDGE,"E167"),sQuery(id+"F1.wireOp",EDGE,"E168"),sQuery(id+"F1.wireOp",EDGE,"E169"),sQuery(id+"F1.wireOp",EDGE,"E170"),sQuery(id+"F1.wireOp",EDGE,"E171"),sQuery(id+"F1.wireOp",EDGE,"E172"),sQuery(id+"F1.wireOp",EDGE,"E173"),sQuery(id+"F1.wireOp",EDGE,"E174"),sQuery(id+"F1.wireOp",EDGE,"E175"),sQuery(id+"F1.wireOp",EDGE,"E176"),sQuery(id+"F1.wireOp",EDGE,"E177"),sQuery(id+"F1.wireOp",EDGE,"E178"),sQuery(id+"F1.wireOp",EDGE,"E179"),sQuery(id+"F1.wireOp",EDGE,"E180"),sQuery(id+"F1.wireOp",EDGE,"E181"),sQuery(id+"F1.wireOp",EDGE,"E182"),sQuery(id+"F1.wireOp",EDGE,"E183"),sQuery(id+"F1.wireOp",EDGE,"E184"),sQuery(id+"F1.wireOp",EDGE,"E185"),sQuery(id+"F1.wireOp",EDGE,"E186"),sQuery(id+"F1.wireOp",EDGE,"E187"),sQuery(id+"F1.wireOp",EDGE,"E188"),sQuery(id+"F1.wireOp",EDGE,"E189"),sQuery(id+"F1.wireOp",EDGE,"E190"),sQuery(id+"F1.wireOp",EDGE,"E191"),sQuery(id+"F1.wireOp",EDGE,"E192"),sQuery(id+"F1.wireOp",EDGE,"E193"),sQuery(id+"F1.wireOp",EDGE,"E194"),sQuery(id+"F1.wireOp",EDGE,"E195"),sQuery(id+"F1.wireOp",EDGE,"E196"),sQuery(id+"F1.wireOp",EDGE,"E197"),sQuery(id+"F1.wireOp",EDGE,"E198"),sQuery(id+"F1.wireOp",EDGE,"E199"),sQuery(id+"F1.wireOp",EDGE,"E200"),sQuery(id+"F1.wireOp",EDGE,"E201"),sQuery(id+"F1.wireOp",EDGE,"E202"),sQuery(id+"F1.wireOp",EDGE,"E203"),sQuery(id+"F1.wireOp",EDGE,"E204"),sQuery(id+"F1.wireOp",EDGE,"E205"),sQuery(id+"F1.wireOp",EDGE,"E206"),sQuery(id+"F1.wireOp",EDGE,"E207"),sQuery(id+"F1.wireOp",EDGE,"E208"),sQuery(id+"F1.wireOp",EDGE,"E209"),sQuery(id+"F1.wireOp",EDGE,"E210"),sQuery(id+"F1.wireOp",EDGE,"E211"),sQuery(id+"F1.wireOp",EDGE,"E212"),sQuery(id+"F1.wireOp",EDGE,"E213"),sQuery(id+"F1.wireOp",EDGE,"E214"),sQuery(id+"F1.wireOp",EDGE,"E215"),sQuery(id+"F1.wireOp",EDGE,"E216"),sQuery(id+"F1.wireOp",EDGE,"E217"),sQuery(id+"F1.wireOp",EDGE,"E218"),sQuery(id+"F1.wireOp",EDGE,"E219"),sQuery(id+"F1.wireOp",EDGE,"E220"),sQuery(id+"F1.wireOp",EDGE,"E221"),sQuery(id+"F1.wireOp",EDGE,"E222"),sQuery(id+"F1.wireOp",EDGE,"E223"),sQuery(id+"F1.wireOp",EDGE,"E224"),sQuery(id+"F1.wireOp",EDGE,"E225"),sQuery(id+"F1.wireOp",EDGE,"E226"),sQuery(id+"F1.wireOp",EDGE,"E227"),sQuery(id+"F1.wireOp",EDGE,"E228"),sQuery(id+"F1.wireOp",EDGE,"E229"),sQuery(id+"F1.wireOp",EDGE,"E230"),sQuery(id+"F1.wireOp",EDGE,"E231"),sQuery(id+"F1.wireOp",EDGE,"E232"),sQuery(id+"F1.wireOp",EDGE,"E233"),sQuery(id+"F1.wireOp",EDGE,"E234"),sQuery(id+"F1.wireOp",EDGE,"E235"),sQuery(id+"F1.wireOp",EDGE,"E236"),sQuery(id+"F1.wireOp",EDGE,"E237"),sQuery(id+"F1.wireOp",EDGE,"E238"),sQuery(id+"F1.wireOp",EDGE,"E239"),sQuery(id+"F1.wireOp",EDGE,"E240"),sQuery(id+"F1.wireOp",EDGE,"E241"),sQuery(id+"F1.wireOp",EDGE,"E242"),sQuery(id+"F1.wireOp",EDGE,"E243"),sQuery(id+"F1.wireOp",EDGE,"E244"),sQuery(id+"F1.wireOp",EDGE,"E245"),sQuery(id+"F1.wireOp",EDGE,"E246"),sQuery(id+"F1.wireOp",EDGE,"E247"),sQuery(id+"F1.wireOp",EDGE,"E248"),sQuery(id+"F1.wireOp",EDGE,"E249"),sQuery(id+"F1.wireOp",EDGE,"E250"),sQuery(id+"F1.wireOp",EDGE,"E251"),sQuery(id+"F1.wireOp",EDGE,"E252"),sQuery(id+"F1.wireOp",EDGE,"E253"),sQuery(id+"F1.wireOp",EDGE,"E254"),sQuery(id+"F1.wireOp",EDGE,"E255"),sQuery(id+"F1.wireOp",EDGE,"E256"),sQuery(id+"F1.wireOp",EDGE,"E257"),sQuery(id+"F1.wireOp",EDGE,"E258"),sQuery(id+"F1.wireOp",EDGE,"E259"),sQuery(id+"F1.wireOp",EDGE,"E260"),sQuery(id+"F1.wireOp",EDGE,"E261"),sQuery(id+"F1.wireOp",EDGE,"E262"),sQuery(id+"F1.wireOp",EDGE,"E263"),sQuery(id+"F1.wireOp",EDGE,"E264"),sQuery(id+"F1.wireOp",EDGE,"E265"),sQuery(id+"F1.wireOp",EDGE,"E266"),sQuery(id+"F1.wireOp",EDGE,"E267"),sQuery(id+"F1.wireOp",EDGE,"E268"),sQuery(id+"F1.wireOp",EDGE,"E269"),sQuery(id+"F1.wireOp",EDGE,"E270"),sQuery(id+"F1.wireOp",EDGE,"E271"),sQuery(id+"F1.wireOp",EDGE,"E272"),sQuery(id+"F1.wireOp",EDGE,"E273"),sQuery(id+"F1.wireOp",EDGE,"E274"),sQuery(id+"F1.wireOp",EDGE,"E275"),sQuery(id+"F1.wireOp",EDGE,"E276"),sQuery(id+"F1.wireOp",EDGE,"E277"),sQuery(id+"F1.wireOp",EDGE,"E278"),sQuery(id+"F1.wireOp",EDGE,"E279"),sQuery(id+"F1.wireOp",EDGE,"E280"),sQuery(id+"F1.wireOp",EDGE,"E281"),sQuery(id+"F1.wireOp",EDGE,"E282"),sQuery(id+"F1.wireOp",EDGE,"E283"),sQuery(id+"F1.wireOp",EDGE,"E284"),sQuery(id+"F1.wireOp",EDGE,"E285"),sQuery(id+"F1.wireOp",EDGE,"E286"),sQuery(id+"F1.wireOp",EDGE,"E287"),sQuery(id+"F1.wireOp",EDGE,"E288"),sQuery(id+"F1.wireOp",EDGE,"E289"),sQuery(id+"F1.wireOp",EDGE,"E290"),sQuery(id+"F1.wireOp",EDGE,"E291"),sQuery(id+"F1.wireOp",EDGE,"E292"),sQuery(id+"F1.wireOp",EDGE,"E293"),sQuery(id+"F1.wireOp",EDGE,"E294"),sQuery(id+"F1.wireOp",EDGE,"E295"),sQuery(id+"F1.wireOp",EDGE,"E296"),sQuery(id+"F1.wireOp",EDGE,"E297"),sQuery(id+"F1.wireOp",EDGE,"E298"),sQuery(id+"F1.wireOp",EDGE,"E299"),sQuery(id+"F1.wireOp",EDGE,"E300"),sQuery(id+"F1.wireOp",EDGE,"E301"),sQuery(id+"F1.wireOp",EDGE,"E302"),sQuery(id+"F1.wireOp",EDGE,"E303"),sQuery(id+"F1.wireOp",EDGE,"E304"),sQuery(id+"F1.wireOp",EDGE,"E305"),sQuery(id+"F1.wireOp",EDGE,"E306"),sQuery(id+"F1.wireOp",EDGE,"E307"),sQuery(id+"F1.wireOp",EDGE,"E308"),sQuery(id+"F1.wireOp",EDGE,"E309"),sQuery(id+"F1.wireOp",EDGE,"E310"),sQuery(id+"F1.wireOp",EDGE,"E311"),sQuery(id+"F1.wireOp",EDGE,"E312"),sQuery(id+"F1.wireOp",EDGE,"E313"),sQuery(id+"F1.wireOp",EDGE,"E314"),sQuery(id+"F1.wireOp",EDGE,"E315"),sQuery(id+"F1.wireOp",EDGE,"E316"),sQuery(id+"F1.wireOp",EDGE,"E317"),sQuery(id+"F1.wireOp",EDGE,"E318"),sQuery(id+"F1.wireOp",EDGE,"E319"),sQuery(id+"F1.wireOp",EDGE,"E320"),sQuery(id+"F1.wireOp",EDGE,"E321"),sQuery(id+"F1.wireOp",EDGE,"E322"),sQuery(id+"F1.wireOp",EDGE,"E323"),sQuery(id+"F1.wireOp",EDGE,"E324"),sQuery(id+"F1.wireOp",EDGE,"E325"),sQuery(id+"F1.wireOp",EDGE,"E326"),sQuery(id+"F1.wireOp",EDGE,"E327"),sQuery(id+"F1.wireOp",EDGE,"E328"),sQuery(id+"F1.wireOp",EDGE,"E329"),sQuery(id+"F1.wireOp",EDGE,"E330"),sQuery(id+"F1.wireOp",EDGE,"E331"),sQuery(id+"F1.wireOp",EDGE,"E332"),sQuery(id+"F1.wireOp",EDGE,"E333"),sQuery(id+"F1.wireOp",EDGE,"E334"),sQuery(id+"F1.wireOp",EDGE,"E334"),sQuery(id+"F1.wireOp",EDGE,"E335"),sQuery(id+"F1.wireOp",EDGE,"E336"),sQuery(id+"F1.wireOp",EDGE,"E337"),sQuery(id+"F1.wireOp",EDGE,"E338"),sQuery(id+"F1.wireOp",EDGE,"E339"),sQuery(id+"F1.wireOp",EDGE,"E340"),sQuery(id+"F1.wireOp",EDGE,"E341"),sQuery(id+"F1.wireOp",EDGE,"E342"),sQuery(id+"F1.wireOp",EDGE,"E343"),sQuery(id+"F1.wireOp",EDGE,"E344"),sQuery(id+"F1.wireOp",EDGE,"E345"),sQuery(id+"F1.wireOp",EDGE,"E346"),sQuery(id+"F1.wireOp",EDGE,"E347"),sQuery(id+"F1.wireOp",EDGE,"E348"),sQuery(id+"F1.wireOp",EDGE,"E349"),sQuery(id+"F1.wireOp",EDGE,"E350"),sQuery(id+"F1.wireOp",EDGE,"E351"),sQuery(id+"F1.wireOp",EDGE,"E352"),sQuery(id+"F1.wireOp",EDGE,"E353"),sQuery(id+"F1.wireOp",EDGE,"E354"),sQuery(id+"F1.wireOp",EDGE,"E355"),sQuery(id+"F1.wireOp",EDGE,"E356"),sQuery(id+"F1.wireOp",EDGE,"E357"),sQuery(id+"F1.wireOp",EDGE,"E358"),sQuery(id+"F1.wireOp",EDGE,"E359"),sQuery(id+"F1.wireOp",EDGE,"E360"),sQuery(id+"F1.wireOp",EDGE,"E361"),sQuery(id+"F1.wireOp",EDGE,"E362"),sQuery(id+"F1.wireOp",EDGE,"E363"),sQuery(id+"F1.wireOp",EDGE,"E364"),sQuery(id+"F1.wireOp",EDGE,"E365"),sQuery(id+"F1.wireOp",EDGE,"E366"),sQuery(id+"F1.wireOp",EDGE,"E367"),sQuery(id+"F1.wireOp",EDGE,"E368"),sQuery(id+"F1.wireOp",EDGE,"E369"),sQuery(id+"F1.wireOp",EDGE,"E370"),sQuery(id+"F1.wireOp",EDGE,"E371"),sQuery(id+"F1.wireOp",EDGE,"E372"),sQuery(id+"F1.wireOp",EDGE,"E373"),sQuery(id+"F1.wireOp",EDGE,"E374"),sQuery(id+"F1.wireOp",EDGE,"E375"),sQuery(id+"F1.wireOp",EDGE,"E376"),sQuery(id+"F1.wireOp",EDGE,"E377"),sQuery(id+"F1.wireOp",EDGE,"E378"),sQuery(id+"F1.wireOp",EDGE,"E379"),sQuery(id+"F1.wireOp",EDGE,"E380"),sQuery(id+"F1.wireOp",EDGE,"E381"),sQuery(id+"F1.wireOp",EDGE,"E382"),sQuery(id+"F1.wireOp",EDGE,"E383"),sQuery(id+"F1.wireOp",EDGE,"E384"),sQuery(id+"F1.wireOp",EDGE,"E385"),sQuery(id+"F1.wireOp",EDGE,"E386"),sQuery(id+"F1.wireOp",EDGE,"E387"),sQuery(id+"F1.wireOp",EDGE,"E388"),sQuery(id+"F1.wireOp",EDGE,"E389"),sQuery(id+"F1.wireOp",EDGE,"E390"),sQuery(id+"F1.wireOp",EDGE,"E391"),sQuery(id+"F1.wireOp",EDGE,"E392"),sQuery(id+"F1.wireOp",EDGE,"E393"),sQuery(id+"F1.wireOp",EDGE,"E394"),sQuery(id+"F1.wireOp",EDGE,"E395"),sQuery(id+"F1.wireOp",EDGE,"E396"),sQuery(id+"F1.wireOp",EDGE,"E397"),sQuery(id+"F1.wireOp",EDGE,"E398"),sQuery(id+"F1.wireOp",EDGE,"E399"),sQuery(id+"F1.wireOp",EDGE,"E400"),sQuery(id+"F1.wireOp",EDGE,"E401"),sQuery(id+"F1.wireOp",EDGE,"E402"),sQuery(id+"F1.wireOp",EDGE,"E403"),sQuery(id+"F1.wireOp",EDGE,"E404"),sQuery(id+"F1.wireOp",EDGE,"E405"),sQuery(id+"F1.wireOp",EDGE,"E406"),sQuery(id+"F1.wireOp",EDGE,"E407"),sQuery(id+"F1.wireOp",EDGE,"E408"),sQuery(id+"F1.wireOp",EDGE,"E409"),sQuery(id+"F1.wireOp",EDGE,"E410"),sQuery(id+"F1.wireOp",EDGE,"E411"),sQuery(id+"F1.wireOp",EDGE,"E412"),sQuery(id+"F1.wireOp",EDGE,"E413"),sQuery(id+"F1.wireOp",EDGE,"E414"),sQuery(id+"F1.wireOp",EDGE,"E415"),sQuery(id+"F1.wireOp",EDGE,"E416"),sQuery(id+"F1.wireOp",EDGE,"E417"),sQuery(id+"F1.wireOp",EDGE,"E418"),sQuery(id+"F1.wireOp",EDGE,"E419"),sQuery(id+"F1.wireOp",EDGE,"E420"),sQuery(id+"F1.wireOp",EDGE,"E421"),sQuery(id+"F1.wireOp",EDGE,"E422"),sQuery(id+"F1.wireOp",EDGE,"E423"),sQuery(id+"F1.wireOp",EDGE,"E424"),sQuery(id+"F1.wireOp",EDGE,"E425"),sQuery(id+"F1.wireOp",EDGE,"E426"),sQuery(id+"F1.wireOp",EDGE,"E426"),sQuery(id+"F1.wireOp",EDGE,"E427"),sQuery(id+"F1.wireOp",EDGE,"E428"),sQuery(id+"F1.wireOp",EDGE,"E429"),sQuery(id+"F1.wireOp",EDGE,"E430"),sQuery(id+"F1.wireOp",EDGE,"E431"),sQuery(id+"F1.wireOp",EDGE,"E432"),sQuery(id+"F1.wireOp",EDGE,"E433"),sQuery(id+"F1.wireOp",EDGE,"E434"),sQuery(id+"F1.wireOp",EDGE,"E435"),sQuery(id+"F1.wireOp",EDGE,"E435"),sQuery(id+"F1.wireOp",EDGE,"E436"),sQuery(id+"F1.wireOp",EDGE,"E437"),sQuery(id+"F1.wireOp",EDGE,"E438"),sQuery(id+"F1.wireOp",EDGE,"E439"),sQuery(id+"F1.wireOp",EDGE,"E440"),sQuery(id+"F1.wireOp",EDGE,"E441"),sQuery(id+"F1.wireOp",EDGE,"E442"),sQuery(id+"F1.wireOp",EDGE,"E443"),sQuery(id+"F1.wireOp",EDGE,"E444"),sQuery(id+"F1.wireOp",EDGE,"E445"),sQuery(id+"F1.wireOp",EDGE,"E446"),sQuery(id+"F1.wireOp",EDGE,"E447"),sQuery(id+"F1.wireOp",EDGE,"E448"),sQuery(id+"F1.wireOp",EDGE,"E449"),sQuery(id+"F1.wireOp",EDGE,"E450"),sQuery(id+"F1.wireOp",EDGE,"E451"),sQuery(id+"F1.wireOp",EDGE,"E452"),sQuery(id+"F1.wireOp",EDGE,"E453"),sQuery(id+"F1.wireOp",EDGE,"E454"),sQuery(id+"F1.wireOp",EDGE,"E455"),sQuery(id+"F1.wireOp",EDGE,"E456"),sQuery(id+"F1.wireOp",EDGE,"E457"),sQuery(id+"F1.wireOp",EDGE,"E458"),sQuery(id+"F1.wireOp",EDGE,"E459"),sQuery(id+"F1.wireOp",EDGE,"E460"),sQuery(id+"F1.wireOp",EDGE,"E461"),sQuery(id+"F1.wireOp",EDGE,"E462"),sQuery(id+"F1.wireOp",EDGE,"E463"),sQuery(id+"F1.wireOp",EDGE,"E464"),sQuery(id+"F1.wireOp",EDGE,"E465"),sQuery(id+"F1.wireOp",EDGE,"E466"),sQuery(id+"F1.wireOp",EDGE,"E467"),sQuery(id+"F1.wireOp",EDGE,"E468"),sQuery(id+"F1.wireOp",EDGE,"E469"),sQuery(id+"F1.wireOp",EDGE,"E470"),sQuery(id+"F1.wireOp",EDGE,"E471"),sQuery(id+"F1.wireOp",EDGE,"E472"),sQuery(id+"F1.wireOp",EDGE,"E473"),sQuery(id+"F1.wireOp",EDGE,"E474"),sQuery(id+"F1.wireOp",EDGE,"E475"),sQuery(id+"F1.wireOp",EDGE,"E476"),sQuery(id+"F1.wireOp",EDGE,"E477"),sQuery(id+"F1.wireOp",EDGE,"E478"),sQuery(id+"F1.wireOp",EDGE,"E479"),sQuery(id+"F1.wireOp",EDGE,"E480"),sQuery(id+"F1.wireOp",EDGE,"E481"),sQuery(id+"F1.wireOp",EDGE,"E482"),sQuery(id+"F1.wireOp",EDGE,"E483"),sQuery(id+"F1.wireOp",EDGE,"E484"),sQuery(id+"F1.wireOp",EDGE,"E485"),sQuery(id+"F1.wireOp",EDGE,"E486"),sQuery(id+"F1.wireOp",EDGE,"E487"),sQuery(id+"F1.wireOp",EDGE,"E488"),sQuery(id+"F1.wireOp",EDGE,"E489"),sQuery(id+"F1.wireOp",EDGE,"E490"),sQuery(id+"F1.wireOp",EDGE,"E491"),sQuery(id+"F1.wireOp",EDGE,"E492"),sQuery(id+"F1.wireOp",EDGE,"E493"),sQuery(id+"F1.wireOp",EDGE,"E494"),sQuery(id+"F1.wireOp",EDGE,"E495"),sQuery(id+"F1.wireOp",EDGE,"E496"),sQuery(id+"F1.wireOp",EDGE,"E497"),sQuery(id+"F1.wireOp",EDGE,"E498"),sQuery(id+"F1.wireOp",EDGE,"E499"),sQuery(id+"F1.wireOp",EDGE,"E500"),sQuery(id+"F1.wireOp",EDGE,"E501"),sQuery(id+"F1.wireOp",EDGE,"E502"),sQuery(id+"F1.wireOp",EDGE,"E503"),sQuery(id+"F1.wireOp",EDGE,"E504"),sQuery(id+"F1.wireOp",EDGE,"E505"),sQuery(id+"F1.wireOp",EDGE,"E506"),sQuery(id+"F1.wireOp",EDGE,"E507"),sQuery(id+"F1.wireOp",EDGE,"E508"),sQuery(id+"F1.wireOp",EDGE,"E509"),sQuery(id+"F1.wireOp",EDGE,"E510"),sQuery(id+"F1.wireOp",EDGE,"E511"),sQuery(id+"F1.wireOp",EDGE,"E512"),sQuery(id+"F1.wireOp",EDGE,"E513"),sQuery(id+"F1.wireOp",EDGE,"E514"),sQuery(id+"F1.wireOp",EDGE,"E515"),sQuery(id+"F1.wireOp",EDGE,"E516"),sQuery(id+"F1.wireOp",EDGE,"E517"),sQuery(id+"F1.wireOp",EDGE,"E518"),sQuery(id+"F1.wireOp",EDGE,"E519"),sQuery(id+"F1.wireOp",EDGE,"E520"),sQuery(id+"F1.wireOp",EDGE,"E521"),sQuery(id+"F1.wireOp",EDGE,"E522"),sQuery(id+"F1.wireOp",EDGE,"E523"),sQuery(id+"F1.wireOp",EDGE,"E524"),sQuery(id+"F1.wireOp",EDGE,"E525"),sQuery(id+"F1.wireOp",EDGE,"E526"),sQuery(id+"F1.wireOp",EDGE,"E527"),sQuery(id+"F1.wireOp",EDGE,"E528"),sQuery(id+"F1.wireOp",EDGE,"E529"),sQuery(id+"F1.wireOp",EDGE,"E530"),sQuery(id+"F1.wireOp",EDGE,"E531"),sQuery(id+"F1.wireOp",EDGE,"E532"),sQuery(id+"F1.wireOp",EDGE,"E533"),sQuery(id+"F1.wireOp",EDGE,"E534"),sQuery(id+"F1.wireOp",EDGE,"E534"),sQuery(id+"F1.wireOp",EDGE,"E535"),sQuery(id+"F1.wireOp",EDGE,"E536"),sQuery(id+"F1.wireOp",EDGE,"E537"),sQuery(id+"F1.wireOp",EDGE,"E538"),sQuery(id+"F1.wireOp",EDGE,"E539"),sQuery(id+"F1.wireOp",EDGE,"E540"),sQuery(id+"F1.wireOp",EDGE,"E541"),sQuery(id+"F1.wireOp",EDGE,"E542"),sQuery(id+"F1.wireOp",EDGE,"E543"),sQuery(id+"F1.wireOp",EDGE,"E544"),sQuery(id+"F1.wireOp",EDGE,"E545"),sQuery(id+"F1.wireOp",EDGE,"E546"),sQuery(id+"F1.wireOp",EDGE,"E547"),sQuery(id+"F1.wireOp",EDGE,"E548"),sQuery(id+"F1.wireOp",EDGE,"E549"),sQuery(id+"F1.wireOp",EDGE,"E550"),sQuery(id+"F1.wireOp",EDGE,"E551"),sQuery(id+"F1.wireOp",EDGE,"E552"),sQuery(id+"F1.wireOp",EDGE,"E553"),sQuery(id+"F1.wireOp",EDGE,"E554"),sQuery(id+"F1.wireOp",EDGE,"E555"),sQuery(id+"F1.wireOp",EDGE,"E556"),sQuery(id+"F1.wireOp",EDGE,"E557"),sQuery(id+"F1.wireOp",EDGE,"E558"),sQuery(id+"F1.wireOp",EDGE,"E559"),sQuery(id+"F1.wireOp",EDGE,"E560"),sQuery(id+"F1.wireOp",EDGE,"E561"),sQuery(id+"F1.wireOp",EDGE,"E562"),sQuery(id+"F1.wireOp",EDGE,"E563"),sQuery(id+"F1.wireOp",EDGE,"E564"),sQuery(id+"F1.wireOp",EDGE,"E565"),sQuery(id+"F1.wireOp",EDGE,"E566"),sQuery(id+"F1.wireOp",EDGE,"E567"),sQuery(id+"F1.wireOp",EDGE,"E568"),sQuery(id+"F1.wireOp",EDGE,"E569"),sQuery(id+"F1.wireOp",EDGE,"E570"),sQuery(id+"F1.wireOp",EDGE,"E571"),sQuery(id+"F1.wireOp",EDGE,"E572"),sQuery(id+"F1.wireOp",EDGE,"E573"),sQuery(id+"F1.wireOp",EDGE,"E574"),sQuery(id+"F1.wireOp",EDGE,"E575"),sQuery(id+"F1.wireOp",EDGE,"E576"),sQuery(id+"F1.wireOp",EDGE,"E577"),sQuery(id+"F1.wireOp",EDGE,"E578"),sQuery(id+"F1.wireOp",EDGE,"E579"),sQuery(id+"F1.wireOp",EDGE,"E580"),sQuery(id+"F1.wireOp",EDGE,"E581"),sQuery(id+"F1.wireOp",EDGE,"E582"),sQuery(id+"F1.wireOp",EDGE,"E583"),sQuery(id+"F1.wireOp",EDGE,"E584"),sQuery(id+"F1.wireOp",EDGE,"E585"),sQuery(id+"F1.wireOp",EDGE,"E586"),sQuery(id+"F1.wireOp",EDGE,"E587"),sQuery(id+"F1.wireOp",EDGE,"E588"),sQuery(id+"F1.wireOp",EDGE,"E589"),sQuery(id+"F1.wireOp",EDGE,"E590"),sQuery(id+"F1.wireOp",EDGE,"E591"),sQuery(id+"F1.wireOp",EDGE,"E592"),sQuery(id+"F1.wireOp",EDGE,"E593"),sQuery(id+"F1.wireOp",EDGE,"E594"),sQuery(id+"F1.wireOp",EDGE,"E595"),sQuery(id+"F1.wireOp",EDGE,"E596"),sQuery(id+"F1.wireOp",EDGE,"E597"),sQuery(id+"F1.wireOp",EDGE,"E598"),sQuery(id+"F1.wireOp",EDGE,"E599"),sQuery(id+"F1.wireOp",EDGE,"E600"),sQuery(id+"F1.wireOp",EDGE,"E601"),sQuery(id+"F1.wireOp",EDGE,"E602"),sQuery(id+"F1.wireOp",EDGE,"E603"),sQuery(id+"F1.wireOp",EDGE,"E604"),sQuery(id+"F1.wireOp",EDGE,"E605"),sQuery(id+"F1.wireOp",EDGE,"E606"),sQuery(id+"F1.wireOp",EDGE,"E607"),sQuery(id+"F1.wireOp",EDGE,"E608"),sQuery(id+"F1.wireOp",EDGE,"E609"),sQuery(id+"F1.wireOp",EDGE,"E610"),sQuery(id+"F1.wireOp",EDGE,"E611"),sQuery(id+"F1.wireOp",EDGE,"E612"),sQuery(id+"F1.wireOp",EDGE,"E613"),sQuery(id+"F1.wireOp",EDGE,"E614"),sQuery(id+"F1.wireOp",EDGE,"E615"),sQuery(id+"F1.wireOp",EDGE,"E616"),sQuery(id+"F1.wireOp",EDGE,"E617"),sQuery(id+"F1.wireOp",EDGE,"E618"),sQuery(id+"F1.wireOp",EDGE,"E619"),sQuery(id+"F1.wireOp",EDGE,"E620"),sQuery(id+"F1.wireOp",EDGE,"E621"),sQuery(id+"F1.wireOp",EDGE,"E622"),sQuery(id+"F1.wireOp",EDGE,"E623"),sQuery(id+"F1.wireOp",EDGE,"E624"),sQuery(id+"F1.wireOp",EDGE,"E625"),sQuery(id+"F1.wireOp",EDGE,"E626"),sQuery(id+"F1.wireOp",EDGE,"E627"),sQuery(id+"F1.wireOp",EDGE,"E628"),sQuery(id+"F1.wireOp",EDGE,"E629"),sQuery(id+"F1.wireOp",EDGE,"E630"),sQuery(id+"F1.wireOp",EDGE,"E631"),sQuery(id+"F1.wireOp",EDGE,"E632"),sQuery(id+"F1.wireOp",EDGE,"E633"),sQuery(id+"F1.wireOp",EDGE,"E634"),sQuery(id+"F1.wireOp",EDGE,"E635"),sQuery(id+"F1.wireOp",EDGE,"E636"),sQuery(id+"F1.wireOp",EDGE,"E637"),sQuery(id+"F1.wireOp",EDGE,"E638"),sQuery(id+"F1.wireOp",EDGE,"E639"),sQuery(id+"F1.wireOp",EDGE,"E640"),sQuery(id+"F1.wireOp",EDGE,"E641"),sQuery(id+"F1.wireOp",EDGE,"E642"),sQuery(id+"F1.wireOp",EDGE,"E643"),sQuery(id+"F1.wireOp",EDGE,"E644"),sQuery(id+"F1.wireOp",EDGE,"E645"),sQuery(id+"F1.wireOp",EDGE,"E646"),sQuery(id+"F1.wireOp",EDGE,"E647"),sQuery(id+"F1.wireOp",EDGE,"E648"),sQuery(id+"F1.wireOp",EDGE,"E649"),sQuery(id+"F1.wireOp",EDGE,"E650"),sQuery(id+"F1.wireOp",EDGE,"E651"),sQuery(id+"F1.wireOp",EDGE,"E652"),sQuery(id+"F1.wireOp",EDGE,"E653"),sQuery(id+"F1.wireOp",EDGE,"E654"),sQuery(id+"F1.wireOp",EDGE,"E655"),sQuery(id+"F1.wireOp",EDGE,"E656"),sQuery(id+"F1.wireOp",EDGE,"E657"),sQuery(id+"F1.wireOp",EDGE,"E658"),sQuery(id+"F1.wireOp",EDGE,"E659"),sQuery(id+"F1.wireOp",EDGE,"E660"),sQuery(id+"F1.wireOp",EDGE,"E661"),sQuery(id+"F1.wireOp",EDGE,"E662"),sQuery(id+"F1.wireOp",EDGE,"E663"),sQuery(id+"F1.wireOp",EDGE,"E664"),sQuery(id+"F1.wireOp",EDGE,"E665"),sQuery(id+"F1.wireOp",EDGE,"E666"),sQuery(id+"F1.wireOp",EDGE,"E667"),sQuery(id+"F1.wireOp",EDGE,"E668"),sQuery(id+"F1.wireOp",EDGE,"E669"),sQuery(id+"F1.wireOp",EDGE,"E670"),sQuery(id+"F1.wireOp",EDGE,"E671"),sQuery(id+"F1.wireOp",EDGE,"E672"),sQuery(id+"F1.wireOp",EDGE,"E673"),sQuery(id+"F1.wireOp",EDGE,"E674"),sQuery(id+"F1.wireOp",EDGE,"E675"),sQuery(id+"F1.wireOp",EDGE,"E676"),sQuery(id+"F1.wireOp",EDGE,"E677"),sQuery(id+"F1.wireOp",EDGE,"E678"),sQuery(id+"F1.wireOp",EDGE,"E679"),sQuery(id+"F1.wireOp",EDGE,"E680"),sQuery(id+"F1.wireOp",EDGE,"E681"),sQuery(id+"F1.wireOp",EDGE,"E682"),sQuery(id+"F1.wireOp",EDGE,"E683"),sQuery(id+"F1.wireOp",EDGE,"E684"),sQuery(id+"F1.wireOp",EDGE,"E685"),sQuery(id+"F1.wireOp",EDGE,"E686"),sQuery(id+"F1.wireOp",EDGE,"E687"),sQuery(id+"F1.wireOp",EDGE,"E688"),sQuery(id+"F1.wireOp",EDGE,"E689"),sQuery(id+"F1.wireOp",EDGE,"E690"),sQuery(id+"F1.wireOp",EDGE,"E691"),sQuery(id+"F1.wireOp",EDGE,"E692"),sQuery(id+"F1.wireOp",EDGE,"E693"),sQuery(id+"F1.wireOp",EDGE,"E694"),sQuery(id+"F1.wireOp",EDGE,"E695"),sQuery(id+"F1.wireOp",EDGE,"E696"),sQuery(id+"F1.wireOp",EDGE,"E697"),sQuery(id+"F1.wireOp",EDGE,"E698"),sQuery(id+"F1.wireOp",EDGE,"E699"),sQuery(id+"F1.wireOp",EDGE,"E700"),sQuery(id+"F1.wireOp",EDGE,"E701"),sQuery(id+"F1.wireOp",EDGE,"E702"),sQuery(id+"F1.wireOp",EDGE,"E703"),sQuery(id+"F1.wireOp",EDGE,"E704"),sQuery(id+"F1.wireOp",EDGE,"E705"),sQuery(id+"F1.wireOp",EDGE,"E706"),sQuery(id+"F1.wireOp",EDGE,"E707"),sQuery(id+"F1.wireOp",EDGE,"E708"),sQuery(id+"F1.wireOp",EDGE,"E709"),sQuery(id+"F1.wireOp",EDGE,"E710"),sQuery(id+"F1.wireOp",EDGE,"E711"),sQuery(id+"F1.wireOp",EDGE,"E712"),sQuery(id+"F1.wireOp",EDGE,"E713"),sQuery(id+"F1.wireOp",EDGE,"E714"),sQuery(id+"F1.wireOp",EDGE,"E715"),sQuery(id+"F1.wireOp",EDGE,"E716"),sQuery(id+"F1.wireOp",EDGE,"E717"),sQuery(id+"F1.wireOp",EDGE,"E718"),sQuery(id+"F1.wireOp",EDGE,"E719"),sQuery(id+"F1.wireOp",EDGE,"E720"),sQuery(id+"F1.wireOp",EDGE,"E721"),sQuery(id+"F1.wireOp",EDGE,"E722"),sQuery(id+"F1.wireOp",EDGE,"E723"),sQuery(id+"F1.wireOp",EDGE,"E724"),sQuery(id+"F1.wireOp",EDGE,"E725"),sQuery(id+"F1.wireOp",EDGE,"E726"),sQuery(id+"F1.wireOp",EDGE,"E727"),sQuery(id+"F1.wireOp",EDGE,"E728"),sQuery(id+"F1.wireOp",EDGE,"E729"),sQuery(id+"F1.wireOp",EDGE,"E730"),sQuery(id+"F1.wireOp",EDGE,"E731"),sQuery(id+"F1.wireOp",EDGE,"E732"),sQuery(id+"F1.wireOp",EDGE,"E733"),sQuery(id+"F1.wireOp",EDGE,"E734"),sQuery(id+"F1.wireOp",EDGE,"E735"),sQuery(id+"F1.wireOp",EDGE,"E736"),sQuery(id+"F1.wireOp",EDGE,"E737"),sQuery(id+"F1.wireOp",EDGE,"E738"),sQuery(id+"F1.wireOp",EDGE,"E739"),sQuery(id+"F1.wireOp",EDGE,"E740"),sQuery(id+"F1.wireOp",EDGE,"E741"),sQuery(id+"F1.wireOp",EDGE,"E742"),sQuery(id+"F1.wireOp",EDGE,"E743"),sQuery(id+"F1.wireOp",EDGE,"E744"),sQuery(id+"F1.wireOp",EDGE,"E745"),sQuery(id+"F1.wireOp",EDGE,"E746"),sQuery(id+"F1.wireOp",EDGE,"E747"),sQuery(id+"F1.wireOp",EDGE,"E748"),sQuery(id+"F1.wireOp",EDGE,"E749"),sQuery(id+"F1.wireOp",EDGE,"E750"),sQuery(id+"F1.wireOp",EDGE,"E751"),sQuery(id+"F1.wireOp",EDGE,"E752"),sQuery(id+"F1.wireOp",EDGE,"E753"),sQuery(id+"F1.wireOp",EDGE,"E754"),sQuery(id+"F1.wireOp",EDGE,"E755"),sQuery(id+"F1.wireOp",EDGE,"E756"),sQuery(id+"F1.wireOp",EDGE,"E757"),sQuery(id+"F1.wireOp",EDGE,"E758"),sQuery(id+"F1.wireOp",EDGE,"E759"),sQuery(id+"F1.wireOp",EDGE,"E760"),sQuery(id+"F1.wireOp",EDGE,"E761"),sQuery(id+"F1.wireOp",EDGE,"E762"),sQuery(id+"F1.wireOp",EDGE,"E763"),sQuery(id+"F1.wireOp",EDGE,"E764"),sQuery(id+"F1.wireOp",EDGE,"E765"),sQuery(id+"F1.wireOp",EDGE,"E766"),sQuery(id+"F1.wireOp",EDGE,"E767"),sQuery(id+"F1.wireOp",EDGE,"E768"),sQuery(id+"F1.wireOp",EDGE,"E769"),sQuery(id+"F1.wireOp",EDGE,"E770"),sQuery(id+"F1.wireOp",EDGE,"E771"),sQuery(id+"F1.wireOp",EDGE,"E772"),sQuery(id+"F1.wireOp",EDGE,"E773"),sQuery(id+"F1.wireOp",EDGE,"E774"),sQuery(id+"F1.wireOp",EDGE,"E775"),sQuery(id+"F1.wireOp",EDGE,"E776"),sQuery(id+"F1.wireOp",EDGE,"E777"),sQuery(id+"F1.wireOp",EDGE,"E778"),sQuery(id+"F1.wireOp",EDGE,"E779"),sQuery(id+"F1.wireOp",EDGE,"E780"),sQuery(id+"F1.wireOp",EDGE,"E781"),sQuery(id+"F1.wireOp",EDGE,"E782"),sQuery(id+"F1.wireOp",EDGE,"E783"),sQuery(id+"F1.wireOp",EDGE,"E784"),sQuery(id+"F1.wireOp",EDGE,"E785"),sQuery(id+"F1.wireOp",EDGE,"E786"),sQuery(id+"F1.wireOp",EDGE,"E787"),sQuery(id+"F1.wireOp",EDGE,"E788"),sQuery(id+"F1.wireOp",EDGE,"E789"),sQuery(id+"F1.wireOp",EDGE,"E790"),sQuery(id+"F1.wireOp",EDGE,"E791"),sQuery(id+"F1.wireOp",EDGE,"E792"),sQuery(id+"F1.wireOp",EDGE,"E793"),sQuery(id+"F1.wireOp",EDGE,"E794"),sQuery(id+"F1.wireOp",EDGE,"E795"),sQuery(id+"F1.wireOp",EDGE,"E796"),sQuery(id+"F1.wireOp",EDGE,"E797"),sQuery(id+"F1.wireOp",EDGE,"E798"),sQuery(id+"F1.wireOp",EDGE,"E799"),sQuery(id+"F1.wireOp",EDGE,"E800"),sQuery(id+"F1.wireOp",EDGE,"E801"),sQuery(id+"F1.wireOp",EDGE,"E802"),sQuery(id+"F1.wireOp",EDGE,"E803"),sQuery(id+"F1.wireOp",EDGE,"E804"),sQuery(id+"F1.wireOp",EDGE,"E805"),sQuery(id+"F1.wireOp",EDGE,"E806"),sQuery(id+"F1.wireOp",EDGE,"E807"),sQuery(id+"F1.wireOp",EDGE,"E808"),sQuery(id+"F1.wireOp",EDGE,"E809"),sQuery(id+"F1.wireOp",EDGE,"E810"),sQuery(id+"F1.wireOp",EDGE,"E811"),sQuery(id+"F1.wireOp",EDGE,"E812"),sQuery(id+"F1.wireOp",EDGE,"E813"),sQuery(id+"F1.wireOp",EDGE,"E814"),sQuery(id+"F1.wireOp",EDGE,"E815"),sQuery(id+"F1.wireOp",EDGE,"E816"),sQuery(id+"F1.wireOp",EDGE,"E817"),sQuery(id+"F1.wireOp",EDGE,"E818"),sQuery(id+"F1.wireOp",EDGE,"E819"),sQuery(id+"F1.wireOp",EDGE,"E820"),sQuery(id+"F1.wireOp",EDGE,"E821"),sQuery(id+"F1.wireOp",EDGE,"E822"),sQuery(id+"F1.wireOp",EDGE,"E823"),sQuery(id+"F1.wireOp",EDGE,"E824"),sQuery(id+"F1.wireOp",EDGE,"E825"),sQuery(id+"F1.wireOp",EDGE,"E826"),sQuery(id+"F1.wireOp",EDGE,"E827"),sQuery(id+"F1.wireOp",EDGE,"E828"),sQuery(id+"F1.wireOp",EDGE,"E829"),sQuery(id+"F1.wireOp",EDGE,"E830"),sQuery(id+"F1.wireOp",EDGE,"E831"),sQuery(id+"F1.wireOp",EDGE,"E832"),sQuery(id+"F1.wireOp",EDGE,"E833"),sQuery(id+"F1.wireOp",EDGE,"E834"),sQuery(id+"F1.wireOp",EDGE,"E835"),sQuery(id+"F1.wireOp",EDGE,"E836"),sQuery(id+"F1.wireOp",EDGE,"E837"),sQuery(id+"F1.wireOp",EDGE,"E838"),sQuery(id+"F1.wireOp",EDGE,"E839"),sQuery(id+"F1.wireOp",EDGE,"E840"),sQuery(id+"F1.wireOp",EDGE,"E841"),sQuery(id+"F1.wireOp",EDGE,"E842"),sQuery(id+"F1.wireOp",EDGE,"E843"),sQuery(id+"F1.wireOp",EDGE,"E844"),sQuery(id+"F1.wireOp",EDGE,"E845"),sQuery(id+"F1.wireOp",EDGE,"E846"),sQuery(id+"F1.wireOp",EDGE,"E847"),sQuery(id+"F1.wireOp",EDGE,"E848"),sQuery(id+"F1.wireOp",EDGE,"E849"),sQuery(id+"F1.wireOp",EDGE,"E850"),sQuery(id+"F1.wireOp",EDGE,"E851"),sQuery(id+"F1.wireOp",EDGE,"E852"),sQuery(id+"F1.wireOp",EDGE,"E853"),sQuery(id+"F1.wireOp",EDGE,"E854"),sQuery(id+"F1.wireOp",EDGE,"E855"),sQuery(id+"F1.wireOp",EDGE,"E856"),sQuery(id+"F1.wireOp",EDGE,"E857"),sQuery(id+"F1.wireOp",EDGE,"E858"),sQuery(id+"F1.wireOp",EDGE,"E859"),sQuery(id+"F1.wireOp",EDGE,"E860"),sQuery(id+"F1.wireOp",EDGE,"E861"),sQuery(id+"F1.wireOp",EDGE,"E862"),sQuery(id+"F1.wireOp",EDGE,"E863"),sQuery(id+"F1.wireOp",EDGE,"E864"),sQuery(id+"F1.wireOp",EDGE,"E865"),sQuery(id+"F1.wireOp",EDGE,"E866"),sQuery(id+"F1.wireOp",EDGE,"E867"),sQuery(id+"F1.wireOp",EDGE,"E868"),sQuery(id+"F1.wireOp",EDGE,"E869"),sQuery(id+"F1.wireOp",EDGE,"E870"),sQuery(id+"F1.wireOp",EDGE,"E871"),sQuery(id+"F1.wireOp",EDGE,"E872"),sQuery(id+"F1.wireOp",EDGE,"E873"),sQuery(id+"F1.wireOp",EDGE,"E873"),sQuery(id+"F1.wireOp",EDGE,"E874"),sQuery(id+"F1.wireOp",EDGE,"E875"),sQuery(id+"F1.wireOp",EDGE,"E876"),sQuery(id+"F1.wireOp",EDGE,"E877"),sQuery(id+"F1.wireOp",EDGE,"E878"),sQuery(id+"F1.wireOp",EDGE,"E879"),sQuery(id+"F1.wireOp",EDGE,"E880"),sQuery(id+"F1.wireOp",EDGE,"E881"),sQuery(id+"F1.wireOp",EDGE,"E882"),sQuery(id+"F1.wireOp",EDGE,"E883"),sQuery(id+"F1.wireOp",EDGE,"E884"),sQuery(id+"F1.wireOp",EDGE,"E885"),sQuery(id+"F1.wireOp",EDGE,"E886"),sQuery(id+"F1.wireOp",EDGE,"E887"),sQuery(id+"F1.wireOp",EDGE,"E888"),sQuery(id+"F1.wireOp",EDGE,"E889"),sQuery(id+"F1.wireOp",EDGE,"E890"),sQuery(id+"F1.wireOp",EDGE,"E891"),sQuery(id+"F1.wireOp",EDGE,"E892"),sQuery(id+"F1.wireOp",EDGE,"E893"),sQuery(id+"F1.wireOp",EDGE,"E894"),sQuery(id+"F1.wireOp",EDGE,"E895"),sQuery(id+"F1.wireOp",EDGE,"E896"),sQuery(id+"F1.wireOp",EDGE,"E897"),sQuery(id+"F1.wireOp",EDGE,"E898"),sQuery(id+"F1.wireOp",EDGE,"E899"),sQuery(id+"F1.wireOp",EDGE,"E900"),sQuery(id+"F1.wireOp",EDGE,"E901"),sQuery(id+"F1.wireOp",EDGE,"E902"),sQuery(id+"F1.wireOp",EDGE,"E903"),sQuery(id+"F1.wireOp",EDGE,"E904"),sQuery(id+"F1.wireOp",EDGE,"E905"),sQuery(id+"F1.wireOp",EDGE,"E906"),sQuery(id+"F1.wireOp",EDGE,"E907"),sQuery(id+"F1.wireOp",EDGE,"E908"),sQuery(id+"F1.wireOp",EDGE,"E909"),sQuery(id+"F1.wireOp",EDGE,"E910"),sQuery(id+"F1.wireOp",EDGE,"E911"),sQuery(id+"F1.wireOp",EDGE,"E912"),sQuery(id+"F1.wireOp",EDGE,"E913"),sQuery(id+"F1.wireOp",EDGE,"E914"),sQuery(id+"F1.wireOp",EDGE,"E915"),sQuery(id+"F1.wireOp",EDGE,"E916"),sQuery(id+"F1.wireOp",EDGE,"E917"),sQuery(id+"F1.wireOp",EDGE,"E918"),sQuery(id+"F1.wireOp",EDGE,"E919"),sQuery(id+"F1.wireOp",EDGE,"E920"),sQuery(id+"F1.wireOp",EDGE,"E921"),sQuery(id+"F1.wireOp",EDGE,"E922"),sQuery(id+"F1.wireOp",EDGE,"E923"),sQuery(id+"F1.wireOp",EDGE,"E924"),sQuery(id+"F1.wireOp",EDGE,"E925"),sQuery(id+"F1.wireOp",EDGE,"E926"),sQuery(id+"F1.wireOp",EDGE,"E927"),sQuery(id+"F1.wireOp",EDGE,"E928"),sQuery(id+"F1.wireOp",EDGE,"E929"),sQuery(id+"F1.wireOp",EDGE,"E930"),sQuery(id+"F1.wireOp",EDGE,"E931"),sQuery(id+"F1.wireOp",EDGE,"E932"),sQuery(id+"F1.wireOp",EDGE,"E933"),sQuery(id+"F1.wireOp",EDGE,"E934"),sQuery(id+"F1.wireOp",EDGE,"E935"),sQuery(id+"F1.wireOp",EDGE,"E936"),sQuery(id+"F1.wireOp",EDGE,"E937"),sQuery(id+"F1.wireOp",EDGE,"E938"),sQuery(id+"F1.wireOp",EDGE,"E939"),sQuery(id+"F1.wireOp",EDGE,"E940"),sQuery(id+"F1.wireOp",EDGE,"E941"),sQuery(id+"F1.wireOp",EDGE,"E942"),sQuery(id+"F1.wireOp",EDGE,"E943"),sQuery(id+"F1.wireOp",EDGE,"E944"),sQuery(id+"F1.wireOp",EDGE,"E945"),sQuery(id+"F1.wireOp",EDGE,"E946"),sQuery(id+"F1.wireOp",EDGE,"E947"),sQuery(id+"F1.wireOp",EDGE,"E948"),sQuery(id+"F1.wireOp",EDGE,"E949"),sQuery(id+"F1.wireOp",EDGE,"E950"),sQuery(id+"F1.wireOp",EDGE,"E951"),sQuery(id+"F1.wireOp",EDGE,"E952"),sQuery(id+"F1.wireOp",EDGE,"E953"),sQuery(id+"F1.wireOp",EDGE,"E954"),sQuery(id+"F1.wireOp",EDGE,"E955"),sQuery(id+"F1.wireOp",EDGE,"E956"),sQuery(id+"F1.wireOp",EDGE,"E957"),sQuery(id+"F1.wireOp",EDGE,"E958"),sQuery(id+"F1.wireOp",EDGE,"E959"),sQuery(id+"F1.wireOp",EDGE,"E960"),sQuery(id+"F1.wireOp",EDGE,"E961"),sQuery(id+"F1.wireOp",EDGE,"E962"),sQuery(id+"F1.wireOp",EDGE,"E963"),sQuery(id+"F1.wireOp",EDGE,"E964"),sQuery(id+"F1.wireOp",EDGE,"E965"),sQuery(id+"F1.wireOp",EDGE,"E966"),sQuery(id+"F1.wireOp",EDGE,"E967"),sQuery(id+"F1.wireOp",EDGE,"E968"),sQuery(id+"F1.wireOp",EDGE,"E969"),sQuery(id+"F1.wireOp",EDGE,"E970"),sQuery(id+"F1.wireOp",EDGE,"E971"),sQuery(id+"F1.wireOp",EDGE,"E972"),sQuery(id+"F1.wireOp",EDGE,"E973"),sQuery(id+"F1.wireOp",EDGE,"E974"),sQuery(id+"F1.wireOp",EDGE,"E975"),sQuery(id+"F1.wireOp",EDGE,"E976"),sQuery(id+"F1.wireOp",EDGE,"E976"),sQuery(id+"F1.wireOp",EDGE,"E976"),sQuery(id+"F1.wireOp",EDGE,"E977"),sQuery(id+"F1.wireOp",EDGE,"E978"),sQuery(id+"F1.wireOp",EDGE,"E979"),sQuery(id+"F1.wireOp",EDGE,"E980"),sQuery(id+"F1.wireOp",EDGE,"E981"),sQuery(id+"F1.wireOp",EDGE,"E982"),sQuery(id+"F1.wireOp",EDGE,"E983"),sQuery(id+"F1.wireOp",EDGE,"E984"),sQuery(id+"F1.wireOp",EDGE,"E985"),sQuery(id+"F1.wireOp",EDGE,"E986"),sQuery(id+"F1.wireOp",EDGE,"E987"),sQuery(id+"F1.wireOp",EDGE,"E988"),sQuery(id+"F1.wireOp",EDGE,"E989"),sQuery(id+"F1.wireOp",EDGE,"E990"),sQuery(id+"F1.wireOp",EDGE,"E991"),sQuery(id+"F1.wireOp",EDGE,"E992"),sQuery(id+"F1.wireOp",EDGE,"E993"),sQuery(id+"F1.wireOp",EDGE,"E994"),sQuery(id+"F1.wireOp",EDGE,"E995"),sQuery(id+"F1.wireOp",EDGE,"E996"),sQuery(id+"F1.wireOp",EDGE,"E997"),sQuery(id+"F1.wireOp",EDGE,"E998"),sQuery(id+"F1.wireOp",EDGE,"E999"),sQuery(id+"F1.wireOp",EDGE,"E1000"),sQuery(id+"F1.wireOp",EDGE,"E1001"),sQuery(id+"F1.wireOp",EDGE,"E1002"),sQuery(id+"F1.wireOp",EDGE,"E1003"),sQuery(id+"F1.wireOp",EDGE,"E1004"),sQuery(id+"F1.wireOp",EDGE,"E1005"),sQuery(id+"F1.wireOp",EDGE,"E1006"),sQuery(id+"F1.wireOp",EDGE,"E1007"),sQuery(id+"F1.wireOp",EDGE,"E1008"),sQuery(id+"F1.wireOp",EDGE,"E1009"),sQuery(id+"F1.wireOp",EDGE,"E1010"),sQuery(id+"F1.wireOp",EDGE,"E1011"),sQuery(id+"F1.wireOp",EDGE,"E1012"),sQuery(id+"F1.wireOp",EDGE,"E1013"),sQuery(id+"F1.wireOp",EDGE,"E1014"),sQuery(id+"F1.wireOp",EDGE,"E1015"),sQuery(id+"F1.wireOp",EDGE,"E1016"),sQuery(id+"F1.wireOp",EDGE,"E1017"),sQuery(id+"F1.wireOp",EDGE,"E1018"),sQuery(id+"F1.wireOp",EDGE,"E1019"),sQuery(id+"F1.wireOp",EDGE,"E1020"),sQuery(id+"F1.wireOp",EDGE,"E1021"),sQuery(id+"F1.wireOp",EDGE,"E1022"),sQuery(id+"F1.wireOp",EDGE,"E1023"),sQuery(id+"F1.wireOp",EDGE,"E1024"),sQuery(id+"F1.wireOp",EDGE,"E1025"),sQuery(id+"F1.wireOp",EDGE,"E1026"),sQuery(id+"F1.wireOp",EDGE,"E1027"),sQuery(id+"F1.wireOp",EDGE,"E1028"),sQuery(id+"F1.wireOp",EDGE,"E1029"),sQuery(id+"F1.wireOp",EDGE,"E1030"),sQuery(id+"F1.wireOp",EDGE,"E1031"),sQuery(id+"F1.wireOp",EDGE,"E1032"),sQuery(id+"F1.wireOp",EDGE,"E1033"),sQuery(id+"F1.wireOp",EDGE,"E1034"),sQuery(id+"F1.wireOp",EDGE,"E1035"),sQuery(id+"F1.wireOp",EDGE,"E1036"),sQuery(id+"F1.wireOp",EDGE,"E1037"),sQuery(id+"F1.wireOp",EDGE,"E1038"),sQuery(id+"F1.wireOp",EDGE,"E1039"),sQuery(id+"F1.wireOp",EDGE,"E1040"),sQuery(id+"F1.wireOp",EDGE,"E1041"),sQuery(id+"F1.wireOp",EDGE,"E1042"),sQuery(id+"F1.wireOp",EDGE,"E1043"),sQuery(id+"F1.wireOp",EDGE,"E1044"),sQuery(id+"F1.wireOp",EDGE,"E1045"),sQuery(id+"F1.wireOp",EDGE,"E1046"),sQuery(id+"F1.wireOp",EDGE,"E1047"),sQuery(id+"F1.wireOp",EDGE,"E1048"),sQuery(id+"F1.wireOp",EDGE,"E1049"),sQuery(id+"F1.wireOp",EDGE,"E1050"),sQuery(id+"F1.wireOp",EDGE,"E1051"),sQuery(id+"F1.wireOp",EDGE,"E1052"),sQuery(id+"F1.wireOp",EDGE,"E1053"),sQuery(id+"F1.wireOp",EDGE,"E1054"),sQuery(id+"F1.wireOp",EDGE,"E1055"),sQuery(id+"F1.wireOp",EDGE,"E1056"),sQuery(id+"F1.wireOp",EDGE,"E1057"),sQuery(id+"F1.wireOp",EDGE,"E1058"),sQuery(id+"F1.wireOp",EDGE,"E1059"),sQuery(id+"F1.wireOp",EDGE,"E1060"),sQuery(id+"F1.wireOp",EDGE,"E1061"),sQuery(id+"F1.wireOp",EDGE,"E1062"),sQuery(id+"F1.wireOp",EDGE,"E1063"),sQuery(id+"F1.wireOp",EDGE,"E1064"),sQuery(id+"F1.wireOp",EDGE,"E1065"),sQuery(id+"F1.wireOp",EDGE,"E1066"),sQuery(id+"F1.wireOp",EDGE,"E1067"),sQuery(id+"F1.wireOp",EDGE,"E1068"),sQuery(id+"F1.wireOp",EDGE,"E1069"),sQuery(id+"F1.wireOp",EDGE,"E1070"),sQuery(id+"F1.wireOp",EDGE,"E1071"),sQuery(id+"F1.wireOp",EDGE,"E1071"),sQuery(id+"F1.wireOp",EDGE,"E1072"),sQuery(id+"F1.wireOp",EDGE,"E1073"),sQuery(id+"F1.wireOp",EDGE,"E1074"),sQuery(id+"F1.wireOp",EDGE,"E1075"),sQuery(id+"F1.wireOp",EDGE,"E1076"),sQuery(id+"F1.wireOp",EDGE,"E1077"),sQuery(id+"F1.wireOp",EDGE,"E1078"),sQuery(id+"F1.wireOp",EDGE,"E1079"),sQuery(id+"F1.wireOp",EDGE,"E1080"),sQuery(id+"F1.wireOp",EDGE,"E1080"),sQuery(id+"F1.wireOp",EDGE,"E1081"),sQuery(id+"F1.wireOp",EDGE,"E1082"),sQuery(id+"F1.wireOp",EDGE,"E1083"),sQuery(id+"F1.wireOp",EDGE,"E1084"),sQuery(id+"F1.wireOp",EDGE,"E1085"),sQuery(id+"F1.wireOp",EDGE,"E1086"),sQuery(id+"F1.wireOp",EDGE,"E1087"),sQuery(id+"F1.wireOp",EDGE,"E1088"),sQuery(id+"F1.wireOp",EDGE,"E1089"),sQuery(id+"F1.wireOp",EDGE,"E1090"),sQuery(id+"F1.wireOp",EDGE,"E1091"),sQuery(id+"F1.wireOp",EDGE,"E1092"),sQuery(id+"F1.wireOp",EDGE,"E1093"),sQuery(id+"F1.wireOp",EDGE,"E1094"),sQuery(id+"F1.wireOp",EDGE,"E1095"),sQuery(id+"F1.wireOp",EDGE,"E1096"),sQuery(id+"F1.wireOp",EDGE,"E1097"),sQuery(id+"F1.wireOp",EDGE,"E1098"),sQuery(id+"F1.wireOp",EDGE,"E1099"),sQuery(id+"F1.wireOp",EDGE,"E1100"),sQuery(id+"F1.wireOp",EDGE,"E1101"),sQuery(id+"F1.wireOp",EDGE,"E1102"),sQuery(id+"F1.wireOp",EDGE,"E1103"),sQuery(id+"F1.wireOp",EDGE,"E1104"),sQuery(id+"F1.wireOp",EDGE,"E1105"),sQuery(id+"F1.wireOp",EDGE,"E1106"),sQuery(id+"F1.wireOp",EDGE,"E1107"),sQuery(id+"F1.wireOp",EDGE,"E1108"),sQuery(id+"F1.wireOp",EDGE,"E1109"),sQuery(id+"F1.wireOp",EDGE,"E1110"),sQuery(id+"F1.wireOp",EDGE,"E1111"),sQuery(id+"F1.wireOp",EDGE,"E1112"),sQuery(id+"F1.wireOp",EDGE,"E1113"),sQuery(id+"F1.wireOp",EDGE,"E1114"),sQuery(id+"F1.wireOp",EDGE,"E1115"),sQuery(id+"F1.wireOp",EDGE,"E1116"),sQuery(id+"F1.wireOp",EDGE,"E1117"),sQuery(id+"F1.wireOp",EDGE,"E1118"),sQuery(id+"F1.wireOp",EDGE,"E1119"),sQuery(id+"F1.wireOp",EDGE,"E1120"),sQuery(id+"F1.wireOp",EDGE,"E1121"),sQuery(id+"F1.wireOp",EDGE,"E1122"),sQuery(id+"F1.wireOp",EDGE,"E1123"),sQuery(id+"F1.wireOp",EDGE,"E1124"),sQuery(id+"F1.wireOp",EDGE,"E1125"),sQuery(id+"F1.wireOp",EDGE,"E1126"),sQuery(id+"F1.wireOp",EDGE,"E1127"),sQuery(id+"F1.wireOp",EDGE,"E1128"),sQuery(id+"F1.wireOp",EDGE,"E1129"),sQuery(id+"F1.wireOp",EDGE,"E1130"),sQuery(id+"F1.wireOp",EDGE,"E1131"),sQuery(id+"F1.wireOp",EDGE,"E1132"),sQuery(id+"F1.wireOp",EDGE,"E1133"),sQuery(id+"F1.wireOp",EDGE,"E1134"),sQuery(id+"F1.wireOp",EDGE,"E1135"),sQuery(id+"F1.wireOp",EDGE,"E1136"),sQuery(id+"F1.wireOp",EDGE,"E1137"),sQuery(id+"F1.wireOp",EDGE,"E1138"),sQuery(id+"F1.wireOp",EDGE,"E1139"),sQuery(id+"F1.wireOp",EDGE,"E1140"),sQuery(id+"F1.wireOp",EDGE,"E1141"),sQuery(id+"F1.wireOp",EDGE,"E1142"),sQuery(id+"F1.wireOp",EDGE,"E1143"),sQuery(id+"F1.wireOp",EDGE,"E1144"),sQuery(id+"F1.wireOp",EDGE,"E1145"),sQuery(id+"F1.wireOp",EDGE,"E1146"),sQuery(id+"F1.wireOp",EDGE,"E1147"),sQuery(id+"F1.wireOp",EDGE,"E1148"),sQuery(id+"F1.wireOp",EDGE,"E1149"),sQuery(id+"F1.wireOp",EDGE,"E1150"),sQuery(id+"F1.wireOp",EDGE,"E1151"),sQuery(id+"F1.wireOp",EDGE,"E1152"),sQuery(id+"F1.wireOp",EDGE,"E1153"),sQuery(id+"F1.wireOp",EDGE,"E1154"),sQuery(id+"F1.wireOp",EDGE,"E1155"),sQuery(id+"F1.wireOp",EDGE,"E1156"),sQuery(id+"F1.wireOp",EDGE,"E1156"),sQuery(id+"F1.wireOp",EDGE,"E1157"),sQuery(id+"F1.wireOp",EDGE,"E1158"),sQuery(id+"F1.wireOp",EDGE,"E1159"),sQuery(id+"F1.wireOp",EDGE,"E1160"),sQuery(id+"F1.wireOp",EDGE,"E1161"),sQuery(id+"F1.wireOp",EDGE,"E1162"),sQuery(id+"F1.wireOp",EDGE,"E1163"),sQuery(id+"F1.wireOp",EDGE,"E1164"),sQuery(id+"F1.wireOp",EDGE,"E1165"),sQuery(id+"F1.wireOp",EDGE,"E1166"),sQuery(id+"F1.wireOp",EDGE,"E1167"),sQuery(id+"F1.wireOp",EDGE,"E1168"),sQuery(id+"F1.wireOp",EDGE,"E1169"),sQuery(id+"F1.wireOp",EDGE,"E1170"),sQuery(id+"F1.wireOp",EDGE,"E1171"),sQuery(id+"F1.wireOp",EDGE,"E1172"),sQuery(id+"F1.wireOp",EDGE,"E1173"),sQuery(id+"F1.wireOp",EDGE,"E1174"),sQuery(id+"F1.wireOp",EDGE,"E1175"),sQuery(id+"F1.wireOp",EDGE,"E1176"),sQuery(id+"F1.wireOp",EDGE,"E1177"),sQuery(id+"F1.wireOp",EDGE,"E1178"),sQuery(id+"F1.wireOp",EDGE,"E1179"),sQuery(id+"F1.wireOp",EDGE,"E1180"),sQuery(id+"F1.wireOp",EDGE,"E1181"),sQuery(id+"F1.wireOp",EDGE,"E1182"),sQuery(id+"F1.wireOp",EDGE,"E1183"),sQuery(id+"F1.wireOp",EDGE,"E1184"),sQuery(id+"F1.wireOp",EDGE,"E1185"),sQuery(id+"F1.wireOp",EDGE,"E1186"),sQuery(id+"F1.wireOp",EDGE,"E1187"),sQuery(id+"F1.wireOp",EDGE,"E1188"),sQuery(id+"F1.wireOp",EDGE,"E1189"),sQuery(id+"F1.wireOp",EDGE,"E1190"),sQuery(id+"F1.wireOp",EDGE,"E1191"),sQuery(id+"F1.wireOp",EDGE,"E1192"),sQuery(id+"F1.wireOp",EDGE,"E1193"),sQuery(id+"F1.wireOp",EDGE,"E1194"),sQuery(id+"F1.wireOp",EDGE,"E1195"),sQuery(id+"F1.wireOp",EDGE,"E1196"),sQuery(id+"F1.wireOp",EDGE,"E1197"),sQuery(id+"F1.wireOp",EDGE,"E1198"),sQuery(id+"F1.wireOp",EDGE,"E1199"),sQuery(id+"F1.wireOp",EDGE,"E1200"),sQuery(id+"F1.wireOp",EDGE,"E1201"),sQuery(id+"F1.wireOp",EDGE,"E1202"),sQuery(id+"F1.wireOp",EDGE,"E1203"),sQuery(id+"F1.wireOp",EDGE,"E1204"),sQuery(id+"F1.wireOp",EDGE,"E1205"),sQuery(id+"F1.wireOp",EDGE,"E1206"),sQuery(id+"F1.wireOp",EDGE,"E1207"),sQuery(id+"F1.wireOp",EDGE,"E1208"),sQuery(id+"F1.wireOp",EDGE,"E1209"),sQuery(id+"F1.wireOp",EDGE,"E1210"),sQuery(id+"F1.wireOp",EDGE,"E1211"),sQuery(id+"F1.wireOp",EDGE,"E1212"),sQuery(id+"F1.wireOp",EDGE,"E1213"),sQuery(id+"F1.wireOp",EDGE,"E1214"),sQuery(id+"F1.wireOp",EDGE,"E1215"),sQuery(id+"F1.wireOp",EDGE,"E1216"),sQuery(id+"F1.wireOp",EDGE,"E1217"),sQuery(id+"F1.wireOp",EDGE,"E1218"),sQuery(id+"F1.wireOp",EDGE,"E1219"),sQuery(id+"F1.wireOp",EDGE,"E1220"),sQuery(id+"F1.wireOp",EDGE,"E1221"),sQuery(id+"F1.wireOp",EDGE,"E1222"),sQuery(id+"F1.wireOp",EDGE,"E1223"),sQuery(id+"F1.wireOp",EDGE,"E1224"),sQuery(id+"F1.wireOp",EDGE,"E1225"),sQuery(id+"F1.wireOp",EDGE,"E1226"),sQuery(id+"F1.wireOp",EDGE,"E1227"),sQuery(id+"F1.wireOp",EDGE,"E1228"),sQuery(id+"F1.wireOp",EDGE,"E1229"),sQuery(id+"F1.wireOp",EDGE,"E1230"),sQuery(id+"F1.wireOp",EDGE,"E1231"),sQuery(id+"F1.wireOp",EDGE,"E1232"),sQuery(id+"F1.wireOp",EDGE,"E1233"),sQuery(id+"F1.wireOp",EDGE,"E1234"),sQuery(id+"F1.wireOp",EDGE,"E1235"),sQuery(id+"F1.wireOp",EDGE,"E1236"),sQuery(id+"F1.wireOp",EDGE,"E1237"),sQuery(id+"F1.wireOp",EDGE,"E1238"),sQuery(id+"F1.wireOp",EDGE,"E1239"),sQuery(id+"F1.wireOp",EDGE,"E1240"),sQuery(id+"F1.wireOp",EDGE,"E1241"),sQuery(id+"F1.wireOp",EDGE,"E1242"),sQuery(id+"F1.wireOp",EDGE,"E1243"),sQuery(id+"F1.wireOp",EDGE,"E1244"),sQuery(id+"F1.wireOp",EDGE,"E1245"),sQuery(id+"F1.wireOp",EDGE,"E1246"),sQuery(id+"F1.wireOp",EDGE,"E1247"),sQuery(id+"F1.wireOp",EDGE,"E1248"),sQuery(id+"F1.wireOp",EDGE,"E1249"),sQuery(id+"F1.wireOp",EDGE,"E1250"),sQuery(id+"F1.wireOp",EDGE,"E1251"),sQuery(id+"F1.wireOp",EDGE,"E1252"),sQuery(id+"F1.wireOp",EDGE,"E1253"),sQuery(id+"F1.wireOp",EDGE,"E1254"),sQuery(id+"F1.wireOp",EDGE,"E1255"),sQuery(id+"F1.wireOp",EDGE,"E1256"),sQuery(id+"F1.wireOp",EDGE,"E1257"),sQuery(id+"F1.wireOp",EDGE,"E1258"),sQuery(id+"F1.wireOp",EDGE,"E1259"),sQuery(id+"F1.wireOp",EDGE,"E1260"),sQuery(id+"F1.wireOp",EDGE,"E1261"),sQuery(id+"F1.wireOp",EDGE,"E1262"),sQuery(id+"F1.wireOp",EDGE,"E1263"),sQuery(id+"F1.wireOp",EDGE,"E1264"),sQuery(id+"F1.wireOp",EDGE,"E1265"),sQuery(id+"F1.wireOp",EDGE,"E1266"),sQuery(id+"F1.wireOp",EDGE,"E1267"),sQuery(id+"F1.wireOp",EDGE,"E1268"),sQuery(id+"F1.wireOp",EDGE,"E1269"),sQuery(id+"F1.wireOp",EDGE,"E1270"),sQuery(id+"F1.wireOp",EDGE,"E1271"),sQuery(id+"F1.wireOp",EDGE,"E1272"),sQuery(id+"F1.wireOp",EDGE,"E1273"),sQuery(id+"F1.wireOp",EDGE,"E1274"),sQuery(id+"F1.wireOp",EDGE,"E1275"),sQuery(id+"F1.wireOp",EDGE,"E1276"),sQuery(id+"F1.wireOp",EDGE,"E1277"),sQuery(id+"F1.wireOp",EDGE,"E1278"),sQuery(id+"F1.wireOp",EDGE,"E1279"),sQuery(id+"F1.wireOp",EDGE,"E1280"),sQuery(id+"F1.wireOp",EDGE,"E1281"),sQuery(id+"F1.wireOp",EDGE,"E1282"),sQuery(id+"F1.wireOp",EDGE,"E1283"),sQuery(id+"F1.wireOp",EDGE,"E1284"),sQuery(id+"F1.wireOp",EDGE,"E1285"),sQuery(id+"F1.wireOp",EDGE,"E1286"),sQuery(id+"F1.wireOp",EDGE,"E1287"),sQuery(id+"F1.wireOp",EDGE,"E1288"),sQuery(id+"F1.wireOp",EDGE,"E1289"),sQuery(id+"F1.wireOp",EDGE,"E1290"),sQuery(id+"F1.wireOp",EDGE,"E1291"),sQuery(id+"F1.wireOp",EDGE,"E1292"),sQuery(id+"F1.wireOp",EDGE,"E1293"),sQuery(id+"F1.wireOp",EDGE,"E1294"),sQuery(id+"F1.wireOp",EDGE,"E1295"),sQuery(id+"F1.wireOp",EDGE,"E1296"),sQuery(id+"F1.wireOp",EDGE,"E1297"),sQuery(id+"F1.wireOp",EDGE,"E1298"),sQuery(id+"F1.wireOp",EDGE,"E1299"),sQuery(id+"F1.wireOp",EDGE,"E1300"),sQuery(id+"F1.wireOp",EDGE,"E1301"),sQuery(id+"F1.wireOp",EDGE,"E1302"),sQuery(id+"F1.wireOp",EDGE,"E1303"),sQuery(id+"F1.wireOp",EDGE,"E1304"),sQuery(id+"F1.wireOp",EDGE,"E1305"),sQuery(id+"F1.wireOp",EDGE,"E1306"),sQuery(id+"F1.wireOp",EDGE,"E1307"),sQuery(id+"F1.wireOp",EDGE,"E1308"),sQuery(id+"F1.wireOp",EDGE,"E1309"),sQuery(id+"F1.wireOp",EDGE,"E1310"),sQuery(id+"F1.wireOp",EDGE,"E1311"),sQuery(id+"F1.wireOp",EDGE,"E1312"),sQuery(id+"F1.wireOp",EDGE,"E1312"),sQuery(id+"F1.wireOp",EDGE,"E1313"),sQuery(id+"F1.wireOp",EDGE,"E1314"),sQuery(id+"F1.wireOp",EDGE,"E1315"),sQuery(id+"F1.wireOp",EDGE,"E1316"),sQuery(id+"F1.wireOp",EDGE,"E1317"),sQuery(id+"F1.wireOp",EDGE,"E1318"),sQuery(id+"F1.wireOp",EDGE,"E1319"),sQuery(id+"F1.wireOp",EDGE,"E1320"),sQuery(id+"F1.wireOp",EDGE,"E1321"),sQuery(id+"F1.wireOp",EDGE,"E1322"),sQuery(id+"F1.wireOp",EDGE,"E1323"),sQuery(id+"F1.wireOp",EDGE,"E1324"),sQuery(id+"F1.wireOp",EDGE,"E1325"),sQuery(id+"F1.wireOp",EDGE,"E1326"),sQuery(id+"F1.wireOp",EDGE,"E1327"),sQuery(id+"F1.wireOp",EDGE,"E1328"),sQuery(id+"F1.wireOp",EDGE,"E1329"),sQuery(id+"F1.wireOp",EDGE,"E1330"),sQuery(id+"F1.wireOp",EDGE,"E1331"),sQuery(id+"F1.wireOp",EDGE,"E1332"),sQuery(id+"F1.wireOp",EDGE,"E1333"),sQuery(id+"F1.wireOp",EDGE,"E1334"),sQuery(id+"F1.wireOp",EDGE,"E1335"),sQuery(id+"F1.wireOp",EDGE,"E1336"),sQuery(id+"F1.wireOp",EDGE,"E1337"),sQuery(id+"F1.wireOp",EDGE,"E1338"),sQuery(id+"F1.wireOp",EDGE,"E1339"),sQuery(id+"F1.wireOp",EDGE,"E1340"),sQuery(id+"F1.wireOp",EDGE,"E1341"),sQuery(id+"F1.wireOp",EDGE,"E1342"),sQuery(id+"F1.wireOp",EDGE,"E1343"),sQuery(id+"F1.wireOp",EDGE,"E1344"),sQuery(id+"F1.wireOp",EDGE,"E1345"),sQuery(id+"F1.wireOp",EDGE,"E1346"),sQuery(id+"F1.wireOp",EDGE,"E1347"),sQuery(id+"F1.wireOp",EDGE,"E1348"),sQuery(id+"F1.wireOp",EDGE,"E1349"),sQuery(id+"F1.wireOp",EDGE,"E1350"),sQuery(id+"F1.wireOp",EDGE,"E1351"),sQuery(id+"F1.wireOp",EDGE,"E1352"),sQuery(id+"F1.wireOp",EDGE,"E1353"),sQuery(id+"F1.wireOp",EDGE,"E1354"),sQuery(id+"F1.wireOp",EDGE,"E1355"),sQuery(id+"F1.wireOp",EDGE,"E1356"),sQuery(id+"F1.wireOp",EDGE,"E1357"),sQuery(id+"F1.wireOp",EDGE,"E1358"),sQuery(id+"F1.wireOp",EDGE,"E1359"),sQuery(id+"F1.wireOp",EDGE,"E1360"),sQuery(id+"F1.wireOp",EDGE,"E1361"),sQuery(id+"F1.wireOp",EDGE,"E1362"),sQuery(id+"F1.wireOp",EDGE,"E1363"),sQuery(id+"F1.wireOp",EDGE,"E1364"),sQuery(id+"F1.wireOp",EDGE,"E1365"),sQuery(id+"F1.wireOp",EDGE,"E1366"),sQuery(id+"F1.wireOp",EDGE,"E1367"),sQuery(id+"F1.wireOp",EDGE,"E1368"),sQuery(id+"F1.wireOp",EDGE,"E1369"),sQuery(id+"F1.wireOp",EDGE,"E1370"),sQuery(id+"F1.wireOp",EDGE,"E1371"),sQuery(id+"F1.wireOp",EDGE,"E1372"),sQuery(id+"F1.wireOp",EDGE,"E1373"),sQuery(id+"F1.wireOp",EDGE,"E1374"),sQuery(id+"F1.wireOp",EDGE,"E1375"),sQuery(id+"F1.wireOp",EDGE,"E1376"),sQuery(id+"F1.wireOp",EDGE,"E1376"),sQuery(id+"F1.wireOp",EDGE,"E1377"),sQuery(id+"F1.wireOp",EDGE,"E1378"),sQuery(id+"F1.wireOp",EDGE,"E1379"),sQuery(id+"F1.wireOp",EDGE,"E1380"),sQuery(id+"F1.wireOp",EDGE,"E1381"),sQuery(id+"F1.wireOp",EDGE,"E1382"),sQuery(id+"F1.wireOp",EDGE,"E1383"),sQuery(id+"F1.wireOp",EDGE,"E1384"),sQuery(id+"F1.wireOp",EDGE,"E1385"),sQuery(id+"F1.wireOp",EDGE,"E1386"),sQuery(id+"F1.wireOp",EDGE,"E1387"),sQuery(id+"F1.wireOp",EDGE,"E1388"),sQuery(id+"F1.wireOp",EDGE,"E1389"),sQuery(id+"F1.wireOp",EDGE,"E1390"),sQuery(id+"F1.wireOp",EDGE,"E1391"),sQuery(id+"F1.wireOp",EDGE,"E1392"),sQuery(id+"F1.wireOp",EDGE,"E1393"),sQuery(id+"F1.wireOp",EDGE,"E1394"),sQuery(id+"F1.wireOp",EDGE,"E1395"),sQuery(id+"F1.wireOp",EDGE,"E1396"),sQuery(id+"F1.wireOp",EDGE,"E1397"),sQuery(id+"F1.wireOp",EDGE,"E1398"),sQuery(id+"F1.wireOp",EDGE,"E1399"),sQuery(id+"F1.wireOp",EDGE,"E1400"),sQuery(id+"F1.wireOp",EDGE,"E1401"),sQuery(id+"F1.wireOp",EDGE,"E1402"),sQuery(id+"F1.wireOp",EDGE,"E1403"),sQuery(id+"F1.wireOp",EDGE,"E1404"),sQuery(id+"F1.wireOp",EDGE,"E1405"),sQuery(id+"F1.wireOp",EDGE,"E1406"),sQuery(id+"F1.wireOp",EDGE,"E1407"),sQuery(id+"F1.wireOp",EDGE,"E1408"),sQuery(id+"F1.wireOp",EDGE,"E1409"),sQuery(id+"F1.wireOp",EDGE,"E1410"),sQuery(id+"F1.wireOp",EDGE,"E1411"),sQuery(id+"F1.wireOp",EDGE,"E1412"),sQuery(id+"F1.wireOp",EDGE,"E1413"),sQuery(id+"F1.wireOp",EDGE,"E1414"),sQuery(id+"F1.wireOp",EDGE,"E1415"),sQuery(id+"F1.wireOp",EDGE,"E1416"),sQuery(id+"F1.wireOp",EDGE,"E1417"),sQuery(id+"F1.wireOp",EDGE,"E1418"),sQuery(id+"F1.wireOp",EDGE,"E1419"),sQuery(id+"F1.wireOp",EDGE,"E1420"),sQuery(id+"F1.wireOp",EDGE,"E1421"),sQuery(id+"F1.wireOp",EDGE,"E1422"),sQuery(id+"F1.wireOp",EDGE,"E1423"),sQuery(id+"F1.wireOp",EDGE,"E1424"),sQuery(id+"F1.wireOp",EDGE,"E1425"),sQuery(id+"F1.wireOp",EDGE,"E1426"),sQuery(id+"F1.wireOp",EDGE,"E1427"),sQuery(id+"F1.wireOp",EDGE,"E1428"),sQuery(id+"F1.wireOp",EDGE,"E1429"),sQuery(id+"F1.wireOp",EDGE,"E1430"),sQuery(id+"F1.wireOp",EDGE,"E1431"),sQuery(id+"F1.wireOp",EDGE,"E1432"),sQuery(id+"F1.wireOp",EDGE,"E1433"),sQuery(id+"F1.wireOp",EDGE,"E1434"),sQuery(id+"F1.wireOp",EDGE,"E1435"),sQuery(id+"F1.wireOp",EDGE,"E1436"),sQuery(id+"F1.wireOp",EDGE,"E1437"),sQuery(id+"F1.wireOp",EDGE,"E1438"),sQuery(id+"F1.wireOp",EDGE,"E1439"),sQuery(id+"F1.wireOp",EDGE,"E1440"),sQuery(id+"F1.wireOp",EDGE,"E1441"),sQuery(id+"F1.wireOp",EDGE,"E1442"),sQuery(id+"F1.wireOp",EDGE,"E1443"),sQuery(id+"F1.wireOp",EDGE,"E1444"),sQuery(id+"F1.wireOp",EDGE,"E1445"),sQuery(id+"F1.wireOp",EDGE,"E1446"),sQuery(id+"F1.wireOp",EDGE,"E1447"),sQuery(id+"F1.wireOp",EDGE,"E1448"),sQuery(id+"F1.wireOp",EDGE,"E1449"),sQuery(id+"F1.wireOp",EDGE,"E1450"),sQuery(id+"F1.wireOp",EDGE,"E1451"),sQuery(id+"F1.wireOp",EDGE,"E1452"),sQuery(id+"F1.wireOp",EDGE,"E1453"),sQuery(id+"F1.wireOp",EDGE,"E1454"),sQuery(id+"F1.wireOp",EDGE,"E1455"),sQuery(id+"F1.wireOp",EDGE,"E1456"),sQuery(id+"F1.wireOp",EDGE,"E1457"),sQuery(id+"F1.wireOp",EDGE,"E1458"),sQuery(id+"F1.wireOp",EDGE,"E1459"),sQuery(id+"F1.wireOp",EDGE,"E1460"),sQuery(id+"F1.wireOp",EDGE,"E1461"),sQuery(id+"F1.wireOp",EDGE,"E1462"),sQuery(id+"F1.wireOp",EDGE,"E1463"),sQuery(id+"F1.wireOp",EDGE,"E1464"),sQuery(id+"F1.wireOp",EDGE,"E1465"),sQuery(id+"F1.wireOp",EDGE,"E1466"),sQuery(id+"F1.wireOp",EDGE,"E1467"),sQuery(id+"F1.wireOp",EDGE,"E1468"),sQuery(id+"F1.wireOp",EDGE,"E1469"),sQuery(id+"F1.wireOp",EDGE,"E1470"),sQuery(id+"F1.wireOp",EDGE,"E1471"),sQuery(id+"F1.wireOp",EDGE,"E1472"),sQuery(id+"F1.wireOp",EDGE,"E1473"),sQuery(id+"F1.wireOp",EDGE,"E1474"),sQuery(id+"F1.wireOp",EDGE,"E1475"),sQuery(id+"F1.wireOp",EDGE,"E1476"),sQuery(id+"F1.wireOp",EDGE,"E1477"),sQuery(id+"F1.wireOp",EDGE,"E1478"),sQuery(id+"F1.wireOp",EDGE,"E1479"),sQuery(id+"F1.wireOp",EDGE,"E1480"),sQuery(id+"F1.wireOp",EDGE,"E1481"),sQuery(id+"F1.wireOp",EDGE,"E1482"),sQuery(id+"F1.wireOp",EDGE,"E1483"),sQuery(id+"F1.wireOp",EDGE,"E1484"),sQuery(id+"F1.wireOp",EDGE,"E1485"),sQuery(id+"F1.wireOp",EDGE,"E1486"),sQuery(id+"F1.wireOp",EDGE,"E1487"),sQuery(id+"F1.wireOp",EDGE,"E1488"),sQuery(id+"F1.wireOp",EDGE,"E1489"),sQuery(id+"F1.wireOp",EDGE,"E1490"),sQuery(id+"F1.wireOp",EDGE,"E1491"),sQuery(id+"F1.wireOp",EDGE,"E1492"),sQuery(id+"F1.wireOp",EDGE,"E1493"),sQuery(id+"F1.wireOp",EDGE,"E1494"),sQuery(id+"F1.wireOp",EDGE,"E1495"),sQuery(id+"F1.wireOp",EDGE,"E1496"),sQuery(id+"F1.wireOp",EDGE,"E1497"),sQuery(id+"F1.wireOp",EDGE,"E1498"),sQuery(id+"F1.wireOp",EDGE,"E1499"),sQuery(id+"F1.wireOp",EDGE,"E1500"),sQuery(id+"F1.wireOp",EDGE,"E1501"),sQuery(id+"F1.wireOp",EDGE,"E1502"),sQuery(id+"F1.wireOp",EDGE,"E1503"),sQuery(id+"F1.wireOp",EDGE,"E1504"),sQuery(id+"F1.wireOp",EDGE,"E1505"),sQuery(id+"F1.wireOp",EDGE,"E1506"),sQuery(id+"F1.wireOp",EDGE,"E1507"),sQuery(id+"F1.wireOp",EDGE,"E1508"),sQuery(id+"F1.wireOp",EDGE,"E1509"),sQuery(id+"F1.wireOp",EDGE,"E1510"),sQuery(id+"F1.wireOp",EDGE,"E1511"),sQuery(id+"F1.wireOp",EDGE,"E1512"),sQuery(id+"F1.wireOp",EDGE,"E1513"),sQuery(id+"F1.wireOp",EDGE,"E1514"),sQuery(id+"F1.wireOp",EDGE,"E1515"),sQuery(id+"F1.wireOp",EDGE,"E1516"),sQuery(id+"F1.wireOp",EDGE,"E1517"),sQuery(id+"F1.wireOp",EDGE,"E1518"),sQuery(id+"F1.wireOp",EDGE,"E1519"),sQuery(id+"F1.wireOp",EDGE,"E1520"),sQuery(id+"F1.wireOp",EDGE,"E1521"),sQuery(id+"F1.wireOp",EDGE,"E1522"),sQuery(id+"F1.wireOp",EDGE,"E1523"),sQuery(id+"F1.wireOp",EDGE,"E1524"),sQuery(id+"F1.wireOp",EDGE,"E1525"),sQuery(id+"F1.wireOp",EDGE,"E1526"),sQuery(id+"F1.wireOp",EDGE,"E1527"),sQuery(id+"F1.wireOp",EDGE,"E1528"),sQuery(id+"F1.wireOp",EDGE,"E1529"),sQuery(id+"F1.wireOp",EDGE,"E1530"),sQuery(id+"F1.wireOp",EDGE,"E1531"),sQuery(id+"F1.wireOp",EDGE,"E1532"),sQuery(id+"F1.wireOp",EDGE,"E1533"),sQuery(id+"F1.wireOp",EDGE,"E1534"),sQuery(id+"F1.wireOp",EDGE,"E1535"),sQuery(id+"F1.wireOp",EDGE,"E1536"),sQuery(id+"F1.wireOp",EDGE,"E1537"),sQuery(id+"F1.wireOp",EDGE,"E1538"),sQuery(id+"F1.wireOp",EDGE,"E1539"),sQuery(id+"F1.wireOp",EDGE,"E1540"),sQuery(id+"F1.wireOp",EDGE,"E1541"),sQuery(id+"F1.wireOp",EDGE,"E1542"),sQuery(id+"F1.wireOp",EDGE,"E1543"),sQuery(id+"F1.wireOp",EDGE,"E1544"),sQuery(id+"F1.wireOp",EDGE,"E1545"),sQuery(id+"F1.wireOp",EDGE,"E1546"),sQuery(id+"F1.wireOp",EDGE,"E1547"),sQuery(id+"F1.wireOp",EDGE,"E1548"),sQuery(id+"F1.wireOp",EDGE,"E1549"),sQuery(id+"F1.wireOp",EDGE,"E1550"),sQuery(id+"F1.wireOp",EDGE,"E1551"),sQuery(id+"F1.wireOp",EDGE,"E1552"),sQuery(id+"F1.wireOp",EDGE,"E1553"),sQuery(id+"F1.wireOp",EDGE,"E1554"),sQuery(id+"F1.wireOp",EDGE,"E1555"),sQuery(id+"F1.wireOp",EDGE,"E1556"),sQuery(id+"F1.wireOp",EDGE,"E1557"),sQuery(id+"F1.wireOp",EDGE,"E1558"),sQuery(id+"F1.wireOp",EDGE,"E1559"),sQuery(id+"F1.wireOp",EDGE,"E1560"),sQuery(id+"F1.wireOp",EDGE,"E1561"),sQuery(id+"F1.wireOp",EDGE,"E1562"),sQuery(id+"F1.wireOp",EDGE,"E1563"),sQuery(id+"F1.wireOp",EDGE,"E1564"),sQuery(id+"F1.wireOp",EDGE,"E1565"),sQuery(id+"F1.wireOp",EDGE,"E1566"),sQuery(id+"F1.wireOp",EDGE,"E1567"),sQuery(id+"F1.wireOp",EDGE,"E1568"),sQuery(id+"F1.wireOp",EDGE,"E1569"),sQuery(id+"F1.wireOp",EDGE,"E1570"),sQuery(id+"F1.wireOp",EDGE,"E1571"),sQuery(id+"F1.wireOp",EDGE,"E1572"),sQuery(id+"F1.wireOp",EDGE,"E1573"),sQuery(id+"F1.wireOp",EDGE,"E1574"),sQuery(id+"F1.wireOp",EDGE,"E1575"),sQuery(id+"F1.wireOp",EDGE,"E1576"),sQuery(id+"F1.wireOp",EDGE,"E1577"),sQuery(id+"F1.wireOp",EDGE,"E1578"),sQuery(id+"F1.wireOp",EDGE,"E1579"),sQuery(id+"F1.wireOp",EDGE,"E1580"),sQuery(id+"F1.wireOp",EDGE,"E1581"),sQuery(id+"F1.wireOp",EDGE,"E1582"),sQuery(id+"F1.wireOp",EDGE,"E1583"),sQuery(id+"F1.wireOp",EDGE,"E1584"),sQuery(id+"F1.wireOp",EDGE,"E1585"),sQuery(id+"F1.wireOp",EDGE,"E1586"),sQuery(id+"F1.wireOp",EDGE,"E1587"),sQuery(id+"F1.wireOp",EDGE,"E1588"),sQuery(id+"F1.wireOp",EDGE,"E1589"),sQuery(id+"F1.wireOp",EDGE,"E1590"),sQuery(id+"F1.wireOp",EDGE,"E1591"),sQuery(id+"F1.wireOp",EDGE,"E1592"),sQuery(id+"F1.wireOp",EDGE,"E1593"),sQuery(id+"F1.wireOp",EDGE,"E1594"),sQuery(id+"F1.wireOp",EDGE,"E1595"),sQuery(id+"F1.wireOp",EDGE,"E1596"),sQuery(id+"F1.wireOp",EDGE,"E1597"),sQuery(id+"F1.wireOp",EDGE,"E1598"),sQuery(id+"F1.wireOp",EDGE,"E1599"),sQuery(id+"F1.wireOp",EDGE,"E1600"),sQuery(id+"F1.wireOp",EDGE,"E1601"),sQuery(id+"F1.wireOp",EDGE,"E1602"),sQuery(id+"F1.wireOp",EDGE,"E1603"),sQuery(id+"F1.wireOp",EDGE,"E1604"),sQuery(id+"F1.wireOp",EDGE,"E1605"),sQuery(id+"F1.wireOp",EDGE,"E1606"),sQuery(id+"F1.wireOp",EDGE,"E1607"),sQuery(id+"F1.wireOp",EDGE,"E1608"),sQuery(id+"F1.wireOp",EDGE,"E1609"),sQuery(id+"F1.wireOp",EDGE,"E1610"),sQuery(id+"F1.wireOp",EDGE,"E1611"),sQuery(id+"F1.wireOp",EDGE,"E1612"),sQuery(id+"F1.wireOp",EDGE,"E1613"),sQuery(id+"F1.wireOp",EDGE,"E1614"),sQuery(id+"F1.wireOp",EDGE,"E1615"),sQuery(id+"F1.wireOp",EDGE,"E1616"),sQuery(id+"F1.wireOp",EDGE,"E1617"),sQuery(id+"F1.wireOp",EDGE,"E1618"),sQuery(id+"F1.wireOp",EDGE,"E1619"),sQuery(id+"F1.wireOp",EDGE,"E1620"),sQuery(id+"F1.wireOp",EDGE,"E1621"),sQuery(id+"F1.wireOp",EDGE,"E1622"),sQuery(id+"F1.wireOp",EDGE,"E1623"),sQuery(id+"F1.wireOp",EDGE,"E1624"),sQuery(id+"F1.wireOp",EDGE,"E1625"),sQuery(id+"F1.wireOp",EDGE,"E1626"),sQuery(id+"F1.wireOp",EDGE,"E1627"),sQuery(id+"F1.wireOp",EDGE,"E1628"),sQuery(id+"F1.wireOp",EDGE,"E1629"),sQuery(id+"F1.wireOp",EDGE,"E1630"),sQuery(id+"F1.wireOp",EDGE,"E1631"),sQuery(id+"F1.wireOp",EDGE,"E1632"),sQuery(id+"F1.wireOp",EDGE,"E1633"),sQuery(id+"F1.wireOp",EDGE,"E1634"),sQuery(id+"F1.wireOp",EDGE,"E1635"),sQuery(id+"F1.wireOp",EDGE,"E1636"),sQuery(id+"F1.wireOp",EDGE,"E1637"),sQuery(id+"F1.wireOp",EDGE,"E1638"),sQuery(id+"F1.wireOp",EDGE,"E1639"),sQuery(id+"F1.wireOp",EDGE,"E1640"),sQuery(id+"F1.wireOp",EDGE,"E1641"),sQuery(id+"F1.wireOp",EDGE,"E1642"),sQuery(id+"F1.wireOp",EDGE,"E1643"),sQuery(id+"F1.wireOp",EDGE,"E1644"),sQuery(id+"F1.wireOp",EDGE,"E1645"),sQuery(id+"F1.wireOp",EDGE,"E1646"),sQuery(id+"F1.wireOp",EDGE,"E1647"),sQuery(id+"F1.wireOp",EDGE,"E1648"),sQuery(id+"F1.wireOp",EDGE,"E1649"),sQuery(id+"F1.wireOp",EDGE,"E1650"),sQuery(id+"F1.wireOp",EDGE,"E1651"),sQuery(id+"F1.wireOp",EDGE,"E1652"),sQuery(id+"F1.wireOp",EDGE,"E1653"),sQuery(id+"F1.wireOp",EDGE,"E1654"),sQuery(id+"F1.wireOp",EDGE,"E1655"),sQuery(id+"F1.wireOp",EDGE,"E1656"),sQuery(id+"F1.wireOp",EDGE,"E1657"),sQuery(id+"F1.wireOp",EDGE,"E1658"),sQuery(id+"F1.wireOp",EDGE,"E1659"),sQuery(id+"F1.wireOp",EDGE,"E1660"),sQuery(id+"F1.wireOp",EDGE,"E1661"),sQuery(id+"F1.wireOp",EDGE,"E1662"),sQuery(id+"F1.wireOp",EDGE,"E1663"),sQuery(id+"F1.wireOp",EDGE,"E1664"),sQuery(id+"F1.wireOp",EDGE,"E1665"),sQuery(id+"F1.wireOp",EDGE,"E1666"),sQuery(id+"F1.wireOp",EDGE,"E1667"),sQuery(id+"F1.wireOp",EDGE,"E1668"),sQuery(id+"F1.wireOp",EDGE,"E1669"),sQuery(id+"F1.wireOp",EDGE,"E1670"),sQuery(id+"F1.wireOp",EDGE,"E1671"),sQuery(id+"F1.wireOp",EDGE,"E1672"),sQuery(id+"F1.wireOp",EDGE,"E1673"),sQuery(id+"F1.wireOp",EDGE,"E1674"),sQuery(id+"F1.wireOp",EDGE,"E1675"),sQuery(id+"F1.wireOp",EDGE,"E1676"),sQuery(id+"F1.wireOp",EDGE,"E1677"),sQuery(id+"F1.wireOp",EDGE,"E1678"),sQuery(id+"F1.wireOp",EDGE,"E1679"),sQuery(id+"F1.wireOp",EDGE,"E1680"),sQuery(id+"F1.wireOp",EDGE,"E1681"),sQuery(id+"F1.wireOp",EDGE,"E1682"),sQuery(id+"F1.wireOp",EDGE,"E1683"),sQuery(id+"F1.wireOp",EDGE,"E1684"),sQuery(id+"F1.wireOp",EDGE,"E1685"),sQuery(id+"F1.wireOp",EDGE,"E1686"),sQuery(id+"F1.wireOp",EDGE,"E1687"),sQuery(id+"F1.wireOp",EDGE,"E1688"),sQuery(id+"F1.wireOp",EDGE,"E1689"),sQuery(id+"F1.wireOp",EDGE,"E1690"),sQuery(id+"F1.wireOp",EDGE,"E1691"),sQuery(id+"F1.wireOp",EDGE,"E1692"),sQuery(id+"F1.wireOp",EDGE,"E1693"),sQuery(id+"F1.wireOp",EDGE,"E1694"),sQuery(id+"F1.wireOp",EDGE,"E1695"),sQuery(id+"F1.wireOp",EDGE,"E1696"),sQuery(id+"F1.wireOp",EDGE,"E1697"),sQuery(id+"F1.wireOp",EDGE,"E1698"),sQuery(id+"F1.wireOp",EDGE,"E1699"),sQuery(id+"F1.wireOp",EDGE,"E1700"),sQuery(id+"F1.wireOp",EDGE,"E1701"),sQuery(id+"F1.wireOp",EDGE,"E1702"),sQuery(id+"F1.wireOp",EDGE,"E1703"),sQuery(id+"F1.wireOp",EDGE,"E1704"),sQuery(id+"F1.wireOp",EDGE,"E1705"),sQuery(id+"F1.wireOp",EDGE,"E1706"),sQuery(id+"F1.wireOp",EDGE,"E1707"),sQuery(id+"F1.wireOp",EDGE,"E1708"),sQuery(id+"F1.wireOp",EDGE,"E1709"),sQuery(id+"F1.wireOp",EDGE,"E1710"),sQuery(id+"F1.wireOp",EDGE,"E1711"),sQuery(id+"F1.wireOp",EDGE,"E1712"),sQuery(id+"F1.wireOp",EDGE,"E1713"),sQuery(id+"F1.wireOp",EDGE,"E1714"),sQuery(id+"F1.wireOp",EDGE,"E1715"),sQuery(id+"F1.wireOp",EDGE,"E1716"),sQuery(id+"F1.wireOp",EDGE,"E1717"),sQuery(id+"F1.wireOp",EDGE,"E1718"),sQuery(id+"F1.wireOp",EDGE,"E1719"),sQuery(id+"F1.wireOp",EDGE,"E1720"),sQuery(id+"F1.wireOp",EDGE,"E1721"),sQuery(id+"F1.wireOp",EDGE,"E1722"),sQuery(id+"F1.wireOp",EDGE,"E1723"),sQuery(id+"F1.wireOp",EDGE,"E1724"),sQuery(id+"F1.wireOp",EDGE,"E1725"),sQuery(id+"F1.wireOp",EDGE,"E1726"),sQuery(id+"F1.wireOp",EDGE,"E1727"),sQuery(id+"F1.wireOp",EDGE,"E1728"),sQuery(id+"F1.wireOp",EDGE,"E1729"),sQuery(id+"F1.wireOp",EDGE,"E1730"),sQuery(id+"F1.wireOp",EDGE,"E1731"),sQuery(id+"F1.wireOp",EDGE,"E1732"),sQuery(id+"F1.wireOp",EDGE,"E1733"),sQuery(id+"F1.wireOp",EDGE,"E1734"),sQuery(id+"F1.wireOp",EDGE,"E1735"),sQuery(id+"F1.wireOp",EDGE,"E1736"),sQuery(id+"F1.wireOp",EDGE,"E1737"),sQuery(id+"F1.wireOp",EDGE,"E1738"),sQuery(id+"F1.wireOp",EDGE,"E1739"),sQuery(id+"F1.wireOp",EDGE,"E1740"),sQuery(id+"F1.wireOp",EDGE,"E1741"),sQuery(id+"F1.wireOp",EDGE,"E1742"),sQuery(id+"F1.wireOp",EDGE,"E1743"),sQuery(id+"F1.wireOp",EDGE,"E1744"),sQuery(id+"F1.wireOp",EDGE,"E1745"),sQuery(id+"F1.wireOp",EDGE,"E1746"),sQuery(id+"F1.wireOp",EDGE,"E1747"),sQuery(id+"F1.wireOp",EDGE,"E1748"),sQuery(id+"F1.wireOp",EDGE,"E1749"),sQuery(id+"F1.wireOp",EDGE,"E1750"),sQuery(id+"F1.wireOp",EDGE,"E1751"),sQuery(id+"F1.wireOp",EDGE,"E1752"),sQuery(id+"F1.wireOp",EDGE,"E1753"),sQuery(id+"F1.wireOp",EDGE,"E1754"),sQuery(id+"F1.wireOp",EDGE,"E1755"),sQuery(id+"F1.wireOp",EDGE,"E1756"),sQuery(id+"F1.wireOp",EDGE,"E1757"),sQuery(id+"F1.wireOp",EDGE,"E1758"),sQuery(id+"F1.wireOp",EDGE,"E1759"),sQuery(id+"F1.wireOp",EDGE,"E1760"),sQuery(id+"F1.wireOp",EDGE,"E1761"),sQuery(id+"F1.wireOp",EDGE,"E1762"),sQuery(id+"F1.wireOp",EDGE,"E1763"),sQuery(id+"F1.wireOp",EDGE,"E1764"),sQuery(id+"F1.wireOp",EDGE,"E1765"),sQuery(id+"F1.wireOp",EDGE,"E1766"),sQuery(id+"F1.wireOp",EDGE,"E1767"),sQuery(id+"F1.wireOp",EDGE,"E1768"),sQuery(id+"F1.wireOp",EDGE,"E1769"),sQuery(id+"F1.wireOp",EDGE,"E1770"),sQuery(id+"F1.wireOp",EDGE,"E1771"),sQuery(id+"F1.wireOp",EDGE,"E1772"),sQuery(id+"F1.wireOp",EDGE,"E1773"),sQuery(id+"F1.wireOp",EDGE,"E1774"),sQuery(id+"F1.wireOp",EDGE,"E1775"),sQuery(id+"F1.wireOp",EDGE,"E1776"),sQuery(id+"F1.wireOp",EDGE,"E1777"),sQuery(id+"F1.wireOp",EDGE,"E1778"),sQuery(id+"F1.wireOp",EDGE,"E1779"),sQuery(id+"F1.wireOp",EDGE,"E1780"),sQuery(id+"F1.wireOp",EDGE,"E1781"),sQuery(id+"F1.wireOp",EDGE,"E1782"),sQuery(id+"F1.wireOp",EDGE,"E1783"),sQuery(id+"F1.wireOp",EDGE,"E1784"),sQuery(id+"F1.wireOp",EDGE,"E1785"),sQuery(id+"F1.wireOp",EDGE,"E1786"),sQuery(id+"F1.wireOp",EDGE,"E1787"),sQuery(id+"F1.wireOp",EDGE,"E1788"),sQuery(id+"F1.wireOp",EDGE,"E1789"),sQuery(id+"F1.wireOp",EDGE,"E1790"),sQuery(id+"F1.wireOp",EDGE,"E1791"),sQuery(id+"F1.wireOp",EDGE,"E1792"),sQuery(id+"F1.wireOp",EDGE,"E1793"),sQuery(id+"F1.wireOp",EDGE,"E1794"),sQuery(id+"F1.wireOp",EDGE,"E1795"),sQuery(id+"F1.wireOp",EDGE,"E1796"),sQuery(id+"F1.wireOp",EDGE,"E1797"),sQuery(id+"F1.wireOp",EDGE,"E1798"),sQuery(id+"F1.wireOp",EDGE,"E1799"),sQuery(id+"F1.wireOp",EDGE,"E1800"),sQuery(id+"F1.wireOp",EDGE,"E1801"),sQuery(id+"F1.wireOp",EDGE,"E1802"),sQuery(id+"F1.wireOp",EDGE,"E1803"),sQuery(id+"F1.wireOp",EDGE,"E1804"),sQuery(id+"F1.wireOp",EDGE,"E1805"),sQuery(id+"F1.wireOp",EDGE,"E1806"),sQuery(id+"F1.wireOp",EDGE,"E1807"),sQuery(id+"F1.wireOp",EDGE,"E1808"),sQuery(id+"F1.wireOp",EDGE,"E1809"),sQuery(id+"F1.wireOp",EDGE,"E1810"),sQuery(id+"F1.wireOp",EDGE,"E1811"),sQuery(id+"F1.wireOp",EDGE,"E1812"),sQuery(id+"F1.wireOp",EDGE,"E1813"),sQuery(id+"F1.wireOp",EDGE,"E1814"),sQuery(id+"F1.wireOp",EDGE,"E1815"),sQuery(id+"F1.wireOp",EDGE,"E1816"),sQuery(id+"F1.wireOp",EDGE,"E1817"),sQuery(id+"F1.wireOp",EDGE,"E1818"),sQuery(id+"F1.wireOp",EDGE,"E1819"),sQuery(id+"F1.wireOp",EDGE,"E1820"),sQuery(id+"F1.wireOp",EDGE,"E1821"),sQuery(id+"F1.wireOp",EDGE,"E1822"),sQuery(id+"F1.wireOp",EDGE,"E1823"),sQuery(id+"F1.wireOp",EDGE,"E1824"),sQuery(id+"F1.wireOp",EDGE,"E1825"),sQuery(id+"F1.wireOp",EDGE,"E1826"),sQuery(id+"F1.wireOp",EDGE,"E1827"),sQuery(id+"F1.wireOp",EDGE,"E1828"),sQuery(id+"F1.wireOp",EDGE,"E1829"),sQuery(id+"F1.wireOp",EDGE,"E1830"),sQuery(id+"F1.wireOp",EDGE,"E1831"),sQuery(id+"F1.wireOp",EDGE,"E1832"),sQuery(id+"F1.wireOp",EDGE,"E1833"),sQuery(id+"F1.wireOp",EDGE,"E1834"),sQuery(id+"F1.wireOp",EDGE,"E1835"),sQuery(id+"F1.wireOp",EDGE,"E1836"),sQuery(id+"F1.wireOp",EDGE,"E1837"),sQuery(id+"F1.wireOp",EDGE,"E1838"),sQuery(id+"F1.wireOp",EDGE,"E1839"),sQuery(id+"F1.wireOp",EDGE,"E1840"),sQuery(id+"F1.wireOp",EDGE,"E1841"),sQuery(id+"F1.wireOp",EDGE,"E1842"),sQuery(id+"F1.wireOp",EDGE,"E1843"),sQuery(id+"F1.wireOp",EDGE,"E1844"),sQuery(id+"F1.wireOp",EDGE,"E1845"),sQuery(id+"F1.wireOp",EDGE,"E1846"),sQuery(id+"F1.wireOp",EDGE,"E1847"),sQuery(id+"F1.wireOp",EDGE,"E1848"),sQuery(id+"F1.wireOp",EDGE,"E1849"),sQuery(id+"F1.wireOp",EDGE,"E1850"),sQuery(id+"F1.wireOp",EDGE,"E1851"),sQuery(id+"F1.wireOp",EDGE,"E1852"),sQuery(id+"F1.wireOp",EDGE,"E1853"),sQuery(id+"F1.wireOp",EDGE,"E1854"),sQuery(id+"F1.wireOp",EDGE,"E1855"),sQuery(id+"F1.wireOp",EDGE,"E1856"),sQuery(id+"F1.wireOp",EDGE,"E1857"),sQuery(id+"F1.wireOp",EDGE,"E1858"),sQuery(id+"F1.wireOp",EDGE,"E1859"),sQuery(id+"F1.wireOp",EDGE,"E1860"),sQuery(id+"F1.wireOp",EDGE,"E1861"),sQuery(id+"F1.wireOp",EDGE,"E1862"),sQuery(id+"F1.wireOp",EDGE,"E1863"),sQuery(id+"F1.wireOp",EDGE,"E1864"),sQuery(id+"F1.wireOp",EDGE,"E1865"),sQuery(id+"F1.wireOp",EDGE,"E1866"),sQuery(id+"F1.wireOp",EDGE,"E1867"),sQuery(id+"F1.wireOp",EDGE,"E1868"),sQuery(id+"F1.wireOp",EDGE,"E1869"),sQuery(id+"F1.wireOp",EDGE,"E1870"),sQuery(id+"F1.wireOp",EDGE,"E1871"),sQuery(id+"F1.wireOp",EDGE,"E1872"),sQuery(id+"F1.wireOp",EDGE,"E1873"),sQuery(id+"F1.wireOp",EDGE,"E1874"),sQuery(id+"F1.wireOp",EDGE,"E1875"),sQuery(id+"F1.wireOp",EDGE,"E1876"),sQuery(id+"F1.wireOp",EDGE,"E1877"),sQuery(id+"F1.wireOp",EDGE,"E1878"),sQuery(id+"F1.wireOp",EDGE,"E1879"),sQuery(id+"F1.wireOp",EDGE,"E1880"),sQuery(id+"F1.wireOp",EDGE,"E1881"),sQuery(id+"F1.wireOp",EDGE,"E1882"),sQuery(id+"F1.wireOp",EDGE,"E1883"),sQuery(id+"F1.wireOp",EDGE,"E1884"),sQuery(id+"F1.wireOp",EDGE,"E1885"),sQuery(id+"F1.wireOp",EDGE,"E1886"),sQuery(id+"F1.wireOp",EDGE,"E1887"),sQuery(id+"F1.wireOp",EDGE,"E1888"),sQuery(id+"F1.wireOp",EDGE,"E1889"),sQuery(id+"F1.wireOp",EDGE,"E1890"),sQuery(id+"F1.wireOp",EDGE,"E1891"),sQuery(id+"F1.wireOp",EDGE,"E1892"),sQuery(id+"F1.wireOp",EDGE,"E1893"),sQuery(id+"F1.wireOp",EDGE,"E1894"),sQuery(id+"F1.wireOp",EDGE,"E1895"),sQuery(id+"F1.wireOp",EDGE,"E1896"),sQuery(id+"F1.wireOp",EDGE,"E1897"),sQuery(id+"F1.wireOp",EDGE,"E1898"),sQuery(id+"F1.wireOp",EDGE,"E1899"),sQuery(id+"F1.wireOp",EDGE,"E1900"),sQuery(id+"F1.wireOp",EDGE,"E1901"),sQuery(id+"F1.wireOp",EDGE,"E1902"),sQuery(id+"F1.wireOp",EDGE,"E1903"),sQuery(id+"F1.wireOp",EDGE,"E1904"),sQuery(id+"F1.wireOp",EDGE,"E1905"),sQuery(id+"F1.wireOp",EDGE,"E1906"),sQuery(id+"F1.wireOp",EDGE,"E1907"),sQuery(id+"F1.wireOp",EDGE,"E1908"),sQuery(id+"F1.wireOp",EDGE,"E1909"),sQuery(id+"F1.wireOp",EDGE,"E1910"),sQuery(id+"F1.wireOp",EDGE,"E1911"),sQuery(id+"F1.wireOp",EDGE,"E1912"),sQuery(id+"F1.wireOp",EDGE,"E1913"),sQuery(id+"F1.wireOp",EDGE,"E1914"),sQuery(id+"F1.wireOp",EDGE,"E1915"),sQuery(id+"F1.wireOp",EDGE,"E1916"),sQuery(id+"F1.wireOp",EDGE,"E1917"),sQuery(id+"F1.wireOp",EDGE,"E1918"),sQuery(id+"F1.wireOp",EDGE,"E1919"),sQuery(id+"F1.wireOp",EDGE,"E1920"),sQuery(id+"F1.wireOp",EDGE,"E1921"),sQuery(id+"F1.wireOp",EDGE,"E1922"),sQuery(id+"F1.wireOp",EDGE,"E1923"),sQuery(id+"F1.wireOp",EDGE,"E1924"),sQuery(id+"F1.wireOp",EDGE,"E1925"),sQuery(id+"F1.wireOp",EDGE,"E1926"),sQuery(id+"F1.wireOp",EDGE,"E1927"),sQuery(id+"F1.wireOp",EDGE,"E1928"),sQuery(id+"F1.wireOp",EDGE,"E1929"),sQuery(id+"F1.wireOp",EDGE,"E1930"),sQuery(id+"F1.wireOp",EDGE,"E1931"),sQuery(id+"F1.wireOp",EDGE,"E1932"),sQuery(id+"F1.wireOp",EDGE,"E1933"),sQuery(id+"F1.wireOp",EDGE,"E1934"),sQuery(id+"F1.wireOp",EDGE,"E1935"),sQuery(id+"F1.wireOp",EDGE,"E1936"),sQuery(id+"F1.wireOp",EDGE,"E1937"),sQuery(id+"F1.wireOp",EDGE,"E1938"),sQuery(id+"F1.wireOp",EDGE,"E1939"),sQuery(id+"F1.wireOp",EDGE,"E1940"),sQuery(id+"F1.wireOp",EDGE,"E1941"),sQuery(id+"F1.wireOp",EDGE,"E1942"),sQuery(id+"F1.wireOp",EDGE,"E1943"),sQuery(id+"F1.wireOp",EDGE,"E1944"),sQuery(id+"F1.wireOp",EDGE,"E1945"),sQuery(id+"F1.wireOp",EDGE,"E1946"),sQuery(id+"F1.wireOp",EDGE,"E1947"),sQuery(id+"F1.wireOp",EDGE,"E1948"),sQuery(id+"F1.wireOp",EDGE,"E1949"),sQuery(id+"F1.wireOp",EDGE,"E1950"),sQuery(id+"F1.wireOp",EDGE,"E1951"),sQuery(id+"F1.wireOp",EDGE,"E1952"),sQuery(id+"F1.wireOp",EDGE,"E1953"),sQuery(id+"F1.wireOp",EDGE,"E1954"),sQuery(id+"F1.wireOp",EDGE,"E1955"),sQuery(id+"F1.wireOp",EDGE,"E1956"),sQuery(id+"F1.wireOp",EDGE,"E1957"),sQuery(id+"F1.wireOp",EDGE,"E1958"),sQuery(id+"F1.wireOp",EDGE,"E1959"),sQuery(id+"F1.wireOp",EDGE,"E1960"),sQuery(id+"F1.wireOp",EDGE,"E1961"),sQuery(id+"F1.wireOp",EDGE,"E1962"),sQuery(id+"F1.wireOp",EDGE,"E1963"),sQuery(id+"F1.wireOp",EDGE,"E1964"),sQuery(id+"F1.wireOp",EDGE,"E1965"),sQuery(id+"F1.wireOp",EDGE,"E1966"),sQuery(id+"F1.wireOp",EDGE,"E1967"),sQuery(id+"F1.wireOp",EDGE,"E1968"),sQuery(id+"F1.wireOp",EDGE,"E1969"),sQuery(id+"F1.wireOp",EDGE,"E1970"),sQuery(id+"F1.wireOp",EDGE,"E1971"),sQuery(id+"F1.wireOp",EDGE,"E1972"),sQuery(id+"F1.wireOp",EDGE,"E1973"),sQuery(id+"F1.wireOp",EDGE,"E1974"),sQuery(id+"F1.wireOp",EDGE,"E1975"),sQuery(id+"F1.wireOp",EDGE,"E1976"),sQuery(id+"F1.wireOp",EDGE,"E1977"),sQuery(id+"F1.wireOp",EDGE,"E1978"),sQuery(id+"F1.wireOp",EDGE,"E1979"),sQuery(id+"F1.wireOp",EDGE,"E1980"),sQuery(id+"F1.wireOp",EDGE,"E1981"),sQuery(id+"F1.wireOp",EDGE,"E1982"),sQuery(id+"F1.wireOp",EDGE,"E1983"),sQuery(id+"F1.wireOp",EDGE,"E1984"),sQuery(id+"F1.wireOp",EDGE,"E1985"),sQuery(id+"F1.wireOp",EDGE,"E1986"),sQuery(id+"F1.wireOp",EDGE,"E1987"),sQuery(id+"F1.wireOp",EDGE,"E1988"),sQuery(id+"F1.wireOp",EDGE,"E1989"),sQuery(id+"F1.wireOp",EDGE,"E1990"),sQuery(id+"F1.wireOp",EDGE,"E1991"),sQuery(id+"F1.wireOp",EDGE,"E1992"),sQuery(id+"F1.wireOp",EDGE,"E1993"),sQuery(id+"F1.wireOp",EDGE,"E1994"),sQuery(id+"F1.wireOp",EDGE,"E1995"),sQuery(id+"F1.wireOp",EDGE,"E1996"),sQuery(id+"F1.wireOp",EDGE,"E1997"),sQuery(id+"F1.wireOp",EDGE,"E1998"),sQuery(id+"F1.wireOp",EDGE,"E1999"),sQuery(id+"F1.wireOp",EDGE,"E2000"),sQuery(id+"F1.wireOp",EDGE,"E2000"),sQuery(id+"F1.wireOp",EDGE,"E2001"),sQuery(id+"F1.wireOp",EDGE,"E2002"),sQuery(id+"F1.wireOp",EDGE,"E2003"),sQuery(id+"F1.wireOp",EDGE,"E2004"),sQuery(id+"F1.wireOp",EDGE,"E2005"),sQuery(id+"F1.wireOp",EDGE,"E2006"),sQuery(id+"F1.wireOp",EDGE,"E2007"),sQuery(id+"F1.wireOp",EDGE,"E2008"),sQuery(id+"F1.wireOp",EDGE,"E2009"),sQuery(id+"F1.wireOp",EDGE,"E2010"),sQuery(id+"F1.wireOp",EDGE,"E2011"),sQuery(id+"F1.wireOp",EDGE,"E2012"),sQuery(id+"F1.wireOp",EDGE,"E2013"),sQuery(id+"F1.wireOp",EDGE,"E2014"),sQuery(id+"F1.wireOp",EDGE,"E2015"),sQuery(id+"F1.wireOp",EDGE,"E2016"),sQuery(id+"F1.wireOp",EDGE,"E2017"),sQuery(id+"F1.wireOp",EDGE,"E2018"),sQuery(id+"F1.wireOp",EDGE,"E2019"),sQuery(id+"F1.wireOp",EDGE,"E2020"),sQuery(id+"F1.wireOp",EDGE,"E2021"),sQuery(id+"F1.wireOp",EDGE,"E2022"),sQuery(id+"F1.wireOp",EDGE,"E2023"),sQuery(id+"F1.wireOp",EDGE,"E2024"),sQuery(id+"F1.wireOp",EDGE,"E2025"),sQuery(id+"F1.wireOp",EDGE,"E2026"),sQuery(id+"F1.wireOp",EDGE,"E2027"),sQuery(id+"F1.wireOp",EDGE,"E2028"),sQuery(id+"F1.wireOp",EDGE,"E2029"),sQuery(id+"F1.wireOp",EDGE,"E2030"),sQuery(id+"F1.wireOp",EDGE,"E2031"),sQuery(id+"F1.wireOp",EDGE,"E2032"),sQuery(id+"F1.wireOp",EDGE,"E2033"),sQuery(id+"F1.wireOp",EDGE,"E2034"),sQuery(id+"F1.wireOp",EDGE,"E2035"),sQuery(id+"F1.wireOp",EDGE,"E2036"),sQuery(id+"F1.wireOp",EDGE,"E2037"),sQuery(id+"F1.wireOp",EDGE,"E2038"),sQuery(id+"F1.wireOp",EDGE,"E2039"),sQuery(id+"F1.wireOp",EDGE,"E2040"),sQuery(id+"F1.wireOp",EDGE,"E2041"),sQuery(id+"F1.wireOp",EDGE,"E2042"),sQuery(id+"F1.wireOp",EDGE,"E2043"),sQuery(id+"F1.wireOp",EDGE,"E2044"),sQuery(id+"F1.wireOp",EDGE,"E2045"),sQuery(id+"F1.wireOp",EDGE,"E2046"),sQuery(id+"F1.wireOp",EDGE,"E2047"),sQuery(id+"F1.wireOp",EDGE,"E2048"),sQuery(id+"F1.wireOp",EDGE,"E2049"),sQuery(id+"F1.wireOp",EDGE,"E2050"),sQuery(id+"F1.wireOp",EDGE,"E2051"),sQuery(id+"F1.wireOp",EDGE,"E2052"),sQuery(id+"F1.wireOp",EDGE,"E2053"),sQuery(id+"F1.wireOp",EDGE,"E2054"),sQuery(id+"F1.wireOp",EDGE,"E2055"),sQuery(id+"F1.wireOp",EDGE,"E2056"),sQuery(id+"F1.wireOp",EDGE,"E2057"),sQuery(id+"F1.wireOp",EDGE,"E2058"),sQuery(id+"F1.wireOp",EDGE,"E2059"),sQuery(id+"F1.wireOp",EDGE,"E2060"),sQuery(id+"F1.wireOp",EDGE,"E2061"),sQuery(id+"F1.wireOp",EDGE,"E2062"),sQuery(id+"F1.wireOp",EDGE,"E2063"),sQuery(id+"F1.wireOp",EDGE,"E2064"),sQuery(id+"F1.wireOp",EDGE,"E2065"),sQuery(id+"F1.wireOp",EDGE,"E2066"),sQuery(id+"F1.wireOp",EDGE,"E2067"),sQuery(id+"F1.wireOp",EDGE,"E2068"),sQuery(id+"F1.wireOp",EDGE,"E2069"),sQuery(id+"F1.wireOp",EDGE,"E2070"),sQuery(id+"F1.wireOp",EDGE,"E2071"),sQuery(id+"F1.wireOp",EDGE,"E2072"),sQuery(id+"F1.wireOp",EDGE,"E2073"),sQuery(id+"F1.wireOp",EDGE,"E2074"),sQuery(id+"F1.wireOp",EDGE,"E2075"),sQuery(id+"F1.wireOp",EDGE,"E2076"),sQuery(id+"F1.wireOp",EDGE,"E2077"),sQuery(id+"F1.wireOp",EDGE,"E2078"),sQuery(id+"F1.wireOp",EDGE,"E2079"),sQuery(id+"F1.wireOp",EDGE,"E2080"),sQuery(id+"F1.wireOp",EDGE,"E2081"),sQuery(id+"F1.wireOp",EDGE,"E2082"),sQuery(id+"F1.wireOp",EDGE,"E2083"),sQuery(id+"F1.wireOp",EDGE,"E2084"),sQuery(id+"F1.wireOp",EDGE,"E2085"),sQuery(id+"F1.wireOp",EDGE,"E2086"),sQuery(id+"F1.wireOp",EDGE,"E2087"),sQuery(id+"F1.wireOp",EDGE,"E2088"),sQuery(id+"F1.wireOp",EDGE,"E2089"),sQuery(id+"F1.wireOp",EDGE,"E2090"),sQuery(id+"F1.wireOp",EDGE,"E2091"),sQuery(id+"F1.wireOp",EDGE,"E2092"),sQuery(id+"F1.wireOp",EDGE,"E2093"),sQuery(id+"F1.wireOp",EDGE,"E2094"),sQuery(id+"F1.wireOp",EDGE,"E2095"),sQuery(id+"F1.wireOp",EDGE,"E2096"),sQuery(id+"F1.wireOp",EDGE,"E2097"),sQuery(id+"F1.wireOp",EDGE,"E2098"),sQuery(id+"F1.wireOp",EDGE,"E2099"),sQuery(id+"F1.wireOp",EDGE,"E2100"),sQuery(id+"F1.wireOp",EDGE,"E2101"),sQuery(id+"F1.wireOp",EDGE,"E2102"),sQuery(id+"F1.wireOp",EDGE,"E2103"),sQuery(id+"F1.wireOp",EDGE,"E2104"),sQuery(id+"F1.wireOp",EDGE,"E2105"),sQuery(id+"F1.wireOp",EDGE,"E2106"),sQuery(id+"F1.wireOp",EDGE,"E2107"),sQuery(id+"F1.wireOp",EDGE,"E2108"),sQuery(id+"F1.wireOp",EDGE,"E2109"),sQuery(id+"F1.wireOp",EDGE,"E2110"),sQuery(id+"F1.wireOp",EDGE,"E2111"),sQuery(id+"F1.wireOp",EDGE,"E2112"),sQuery(id+"F1.wireOp",EDGE,"E2113"),sQuery(id+"F1.wireOp",EDGE,"E2114"),sQuery(id+"F1.wireOp",EDGE,"E2115"),sQuery(id+"F1.wireOp",EDGE,"E2116"),sQuery(id+"F1.wireOp",EDGE,"E2117"),sQuery(id+"F1.wireOp",EDGE,"E2118"),sQuery(id+"F1.wireOp",EDGE,"E2119"),sQuery(id+"F1.wireOp",EDGE,"E2120"),sQuery(id+"F1.wireOp",EDGE,"E2121"),sQuery(id+"F1.wireOp",EDGE,"E2122"),sQuery(id+"F1.wireOp",EDGE,"E2123"),sQuery(id+"F1.wireOp",EDGE,"E2124"),sQuery(id+"F1.wireOp",EDGE,"E2125"),sQuery(id+"F1.wireOp",EDGE,"E2126"),sQuery(id+"F1.wireOp",EDGE,"E2127"),sQuery(id+"F1.wireOp",EDGE,"E2128"),sQuery(id+"F1.wireOp",EDGE,"E2129"),sQuery(id+"F1.wireOp",EDGE,"E2130"),sQuery(id+"F1.wireOp",EDGE,"E2131"),sQuery(id+"F1.wireOp",EDGE,"E2132"),sQuery(id+"F1.wireOp",EDGE,"E2133"),sQuery(id+"F1.wireOp",EDGE,"E2134"),sQuery(id+"F1.wireOp",EDGE,"E2135"),sQuery(id+"F1.wireOp",EDGE,"E2136"),sQuery(id+"F1.wireOp",EDGE,"E2137"),sQuery(id+"F1.wireOp",EDGE,"E2138"),sQuery(id+"F1.wireOp",EDGE,"E2139"),sQuery(id+"F1.wireOp",EDGE,"E2140"),sQuery(id+"F1.wireOp",EDGE,"E2141"),sQuery(id+"F1.wireOp",EDGE,"E2142"),sQuery(id+"F1.wireOp",EDGE,"E2143"),sQuery(id+"F1.wireOp",EDGE,"E2144"),sQuery(id+"F1.wireOp",EDGE,"E2145"),sQuery(id+"F1.wireOp",EDGE,"E2146"),sQuery(id+"F1.wireOp",EDGE,"E2147"),sQuery(id+"F1.wireOp",EDGE,"E2148"),sQuery(id+"F1.wireOp",EDGE,"E2149"),sQuery(id+"F1.wireOp",EDGE,"E2150"),sQuery(id+"F1.wireOp",EDGE,"E2151"),sQuery(id+"F1.wireOp",EDGE,"E2152"),sQuery(id+"F1.wireOp",EDGE,"E2153"),sQuery(id+"F1.wireOp",EDGE,"E2154"),sQuery(id+"F1.wireOp",EDGE,"E2155"),sQuery(id+"F1.wireOp",EDGE,"E2156"),sQuery(id+"F1.wireOp",EDGE,"E2157"),sQuery(id+"F1.wireOp",EDGE,"E2158"),sQuery(id+"F1.wireOp",EDGE,"E2159"),sQuery(id+"F1.wireOp",EDGE,"E2160"),sQuery(id+"F1.wireOp",EDGE,"E2161"),sQuery(id+"F1.wireOp",EDGE,"E2162"),sQuery(id+"F1.wireOp",EDGE,"E2163"),sQuery(id+"F1.wireOp",EDGE,"E2164"),sQuery(id+"F1.wireOp",EDGE,"E2165"),sQuery(id+"F1.wireOp",EDGE,"E2166"),sQuery(id+"F1.wireOp",EDGE,"E2167"),sQuery(id+"F1.wireOp",EDGE,"E2168"),sQuery(id+"F1.wireOp",EDGE,"E2169"),sQuery(id+"F1.wireOp",EDGE,"E2170"),sQuery(id+"F1.wireOp",EDGE,"E2171"),sQuery(id+"F1.wireOp",EDGE,"E2172"),sQuery(id+"F1.wireOp",EDGE,"E2173"),sQuery(id+"F1.wireOp",EDGE,"E2174"),sQuery(id+"F1.wireOp",EDGE,"E2175"),sQuery(id+"F1.wireOp",EDGE,"E2176"),sQuery(id+"F1.wireOp",EDGE,"E2177"),sQuery(id+"F1.wireOp",EDGE,"E2178"),sQuery(id+"F1.wireOp",EDGE,"E2179"),sQuery(id+"F1.wireOp",EDGE,"E2180"),sQuery(id+"F1.wireOp",EDGE,"E2181"),sQuery(id+"F1.wireOp",EDGE,"E2182"),sQuery(id+"F1.wireOp",EDGE,"E2183"),sQuery(id+"F1.wireOp",EDGE,"E2184"),sQuery(id+"F1.wireOp",EDGE,"E2185"),sQuery(id+"F1.wireOp",EDGE,"E2186"),sQuery(id+"F1.wireOp",EDGE,"E2187"),sQuery(id+"F1.wireOp",EDGE,"E2188"),sQuery(id+"F1.wireOp",EDGE,"E2189"),sQuery(id+"F1.wireOp",EDGE,"E2190"),sQuery(id+"F1.wireOp",EDGE,"E2191"),sQuery(id+"F1.wireOp",EDGE,"E2192"),sQuery(id+"F1.wireOp",EDGE,"E2193"),sQuery(id+"F1.wireOp",EDGE,"E2194"),sQuery(id+"F1.wireOp",EDGE,"E2195"),sQuery(id+"F1.wireOp",EDGE,"E2196"),sQuery(id+"F1.wireOp",EDGE,"E2197"),sQuery(id+"F1.wireOp",EDGE,"E2198"),sQuery(id+"F1.wireOp",EDGE,"E2199"),sQuery(id+"F1.wireOp",EDGE,"E2200"),sQuery(id+"F1.wireOp",EDGE,"E2201"),sQuery(id+"F1.wireOp",EDGE,"E2202"),sQuery(id+"F1.wireOp",EDGE,"E2203"),sQuery(id+"F1.wireOp",EDGE,"E2204"),sQuery(id+"F1.wireOp",EDGE,"E2205"),sQuery(id+"F1.wireOp",EDGE,"E2206"),sQuery(id+"F1.wireOp",EDGE,"E2207"),sQuery(id+"F1.wireOp",EDGE,"E2208"),sQuery(id+"F1.wireOp",EDGE,"E2209"),sQuery(id+"F1.wireOp",EDGE,"E2210"),sQuery(id+"F1.wireOp",EDGE,"E2211"),sQuery(id+"F1.wireOp",EDGE,"E2212"),sQuery(id+"F1.wireOp",EDGE,"E2213"),sQuery(id+"F1.wireOp",EDGE,"E2214"),sQuery(id+"F1.wireOp",EDGE,"E2215"),sQuery(id+"F1.wireOp",EDGE,"E2216"),sQuery(id+"F1.wireOp",EDGE,"E2217"),sQuery(id+"F1.wireOp",EDGE,"E2218"),sQuery(id+"F1.wireOp",EDGE,"E2219"),sQuery(id+"F1.wireOp",EDGE,"E2220"),sQuery(id+"F1.wireOp",EDGE,"E2221"),sQuery(id+"F1.wireOp",EDGE,"E2222"),sQuery(id+"F1.wireOp",EDGE,"E2223"),sQuery(id+"F1.wireOp",EDGE,"E2224"),sQuery(id+"F1.wireOp",EDGE,"E2225"),sQuery(id+"F1.wireOp",EDGE,"E2226"),sQuery(id+"F1.wireOp",EDGE,"E2227"),sQuery(id+"F1.wireOp",EDGE,"E2228"),sQuery(id+"F1.wireOp",EDGE,"E2229"),sQuery(id+"F1.wireOp",EDGE,"E2230"),sQuery(id+"F1.wireOp",EDGE,"E2231"),sQuery(id+"F1.wireOp",EDGE,"E2232"),sQuery(id+"F1.wireOp",EDGE,"E2233"),sQuery(id+"F1.wireOp",EDGE,"E2234"),sQuery(id+"F1.wireOp",EDGE,"E2235"),sQuery(id+"F1.wireOp",EDGE,"E2236"),sQuery(id+"F1.wireOp",EDGE,"E2237"),sQuery(id+"F1.wireOp",EDGE,"E2238"),sQuery(id+"F1.wireOp",EDGE,"E2239"),sQuery(id+"F1.wireOp",EDGE,"E2240"),sQuery(id+"F1.wireOp",EDGE,"E2241"),sQuery(id+"F1.wireOp",EDGE,"E2242"),sQuery(id+"F1.wireOp",EDGE,"E2243"),sQuery(id+"F1.wireOp",EDGE,"E2244"),sQuery(id+"F1.wireOp",EDGE,"E2245"),sQuery(id+"F1.wireOp",EDGE,"E2246"),sQuery(id+"F1.wireOp",EDGE,"E2247"),sQuery(id+"F1.wireOp",EDGE,"E2248"),sQuery(id+"F1.wireOp",EDGE,"E2249"),sQuery(id+"F1.wireOp",EDGE,"E2250"),sQuery(id+"F1.wireOp",EDGE,"E2251"),sQuery(id+"F1.wireOp",EDGE,"E2252"),sQuery(id+"F1.wireOp",EDGE,"E2253"),sQuery(id+"F1.wireOp",EDGE,"E2254"),sQuery(id+"F1.wireOp",EDGE,"E2255"),sQuery(id+"F1.wireOp",EDGE,"E2256"),sQuery(id+"F1.wireOp",EDGE,"E2257"),sQuery(id+"F1.wireOp",EDGE,"E2258"),sQuery(id+"F1.wireOp",EDGE,"E2259"),sQuery(id+"F1.wireOp",EDGE,"E2260"),sQuery(id+"F1.wireOp",EDGE,"E2261"),sQuery(id+"F1.wireOp",EDGE,"E2262"),sQuery(id+"F1.wireOp",EDGE,"E2263"),sQuery(id+"F1.wireOp",EDGE,"E2264"),sQuery(id+"F1.wireOp",EDGE,"E2265"),sQuery(id+"F1.wireOp",EDGE,"E2266"),sQuery(id+"F1.wireOp",EDGE,"E2267"),sQuery(id+"F1.wireOp",EDGE,"E2268"),sQuery(id+"F1.wireOp",EDGE,"E2269"),sQuery(id+"F1.wireOp",EDGE,"E2270"),sQuery(id+"F1.wireOp",EDGE,"E2271"),sQuery(id+"F1.wireOp",EDGE,"E2272"),sQuery(id+"F1.wireOp",EDGE,"E2273"),sQuery(id+"F1.wireOp",EDGE,"E2274"),sQuery(id+"F1.wireOp",EDGE,"E2275"),sQuery(id+"F1.wireOp",EDGE,"E2276"),sQuery(id+"F1.wireOp",EDGE,"E2277"),sQuery(id+"F1.wireOp",EDGE,"E2278"),sQuery(id+"F1.wireOp",EDGE,"E2279"),sQuery(id+"F1.wireOp",EDGE,"E2280"),sQuery(id+"F1.wireOp",EDGE,"E2281"),sQuery(id+"F1.wireOp",EDGE,"E2282"),sQuery(id+"F1.wireOp",EDGE,"E2283"),sQuery(id+"F1.wireOp",EDGE,"E2284"),sQuery(id+"F1.wireOp",EDGE,"E2285"),sQuery(id+"F1.wireOp",EDGE,"E2286"),sQuery(id+"F1.wireOp",EDGE,"E2287"),sQuery(id+"F1.wireOp",EDGE,"E2288"),sQuery(id+"F1.wireOp",EDGE,"E2289"),sQuery(id+"F1.wireOp",EDGE,"E2290"),sQuery(id+"F1.wireOp",EDGE,"E2291"),sQuery(id+"F1.wireOp",EDGE,"E2292"),sQuery(id+"F1.wireOp",EDGE,"E2293"),sQuery(id+"F1.wireOp",EDGE,"E2294"),sQuery(id+"F1.wireOp",EDGE,"E2295"),sQuery(id+"F1.wireOp",EDGE,"E2296"),sQuery(id+"F1.wireOp",EDGE,"E2297"),sQuery(id+"F1.wireOp",EDGE,"E2298"),sQuery(id+"F1.wireOp",EDGE,"E2299"),sQuery(id+"F1.wireOp",EDGE,"E2300"),sQuery(id+"F1.wireOp",EDGE,"E2301"),sQuery(id+"F1.wireOp",EDGE,"E2302"),sQuery(id+"F1.wireOp",EDGE,"E2303"),sQuery(id+"F1.wireOp",EDGE,"E2304"),sQuery(id+"F1.wireOp",EDGE,"E2305"),sQuery(id+"F1.wireOp",EDGE,"E2306"),sQuery(id+"F1.wireOp",EDGE,"E2307"),sQuery(id+"F1.wireOp",EDGE,"E2308"),sQuery(id+"F1.wireOp",EDGE,"E2309"),sQuery(id+"F1.wireOp",EDGE,"E2310"),sQuery(id+"F1.wireOp",EDGE,"E2311"),sQuery(id+"F1.wireOp",EDGE,"E2312"),sQuery(id+"F1.wireOp",EDGE,"E2313"),sQuery(id+"F1.wireOp",EDGE,"E2314"),sQuery(id+"F1.wireOp",EDGE,"E2315"),sQuery(id+"F1.wireOp",EDGE,"E2316"),sQuery(id+"F1.wireOp",EDGE,"E2317"),sQuery(id+"F1.wireOp",EDGE,"E2318"),sQuery(id+"F1.wireOp",EDGE,"E2319"),sQuery(id+"F1.wireOp",EDGE,"E2320"),sQuery(id+"F1.wireOp",EDGE,"E2321"),sQuery(id+"F1.wireOp",EDGE,"E2322"),sQuery(id+"F1.wireOp",EDGE,"E2323"),sQuery(id+"F1.wireOp",EDGE,"E2324"),sQuery(id+"F1.wireOp",EDGE,"E2325"),sQuery(id+"F1.wireOp",EDGE,"E2326"),sQuery(id+"F1.wireOp",EDGE,"E2327"),sQuery(id+"F1.wireOp",EDGE,"E2328"),sQuery(id+"F1.wireOp",EDGE,"E2329"),sQuery(id+"F1.wireOp",EDGE,"E2330"),sQuery(id+"F1.wireOp",EDGE,"E2331"),sQuery(id+"F1.wireOp",EDGE,"E2332"),sQuery(id+"F1.wireOp",EDGE,"E2333"),sQuery(id+"F1.wireOp",EDGE,"E2334"),sQuery(id+"F1.wireOp",EDGE,"E2335"),sQuery(id+"F1.wireOp",EDGE,"E2336"),sQuery(id+"F1.wireOp",EDGE,"E2337"),sQuery(id+"F1.wireOp",EDGE,"E2338"),sQuery(id+"F1.wireOp",EDGE,"E2339"),sQuery(id+"F1.wireOp",EDGE,"E2340"),sQuery(id+"F1.wireOp",EDGE,"E2341"),sQuery(id+"F1.wireOp",EDGE,"E2342"),sQuery(id+"F1.wireOp",EDGE,"E2343"),sQuery(id+"F1.wireOp",EDGE,"E2344"),sQuery(id+"F1.wireOp",EDGE,"E2345"),sQuery(id+"F1.wireOp",EDGE,"E2346"),sQuery(id+"F1.wireOp",EDGE,"E2347"),sQuery(id+"F1.wireOp",EDGE,"E2348"),sQuery(id+"F1.wireOp",EDGE,"E2349"),sQuery(id+"F1.wireOp",EDGE,"E2350"),sQuery(id+"F1.wireOp",EDGE,"E2351"),sQuery(id+"F1.wireOp",EDGE,"E2352"),sQuery(id+"F1.wireOp",EDGE,"E2353"),sQuery(id+"F1.wireOp",EDGE,"E2354"),sQuery(id+"F1.wireOp",EDGE,"E2355"),sQuery(id+"F1.wireOp",EDGE,"E2356"),sQuery(id+"F1.wireOp",EDGE,"E2357"),sQuery(id+"F1.wireOp",EDGE,"E2358"),sQuery(id+"F1.wireOp",EDGE,"E2359"),sQuery(id+"F1.wireOp",EDGE,"E2360"),sQuery(id+"F1.wireOp",EDGE,"E2361"),sQuery(id+"F1.wireOp",EDGE,"E2362"),sQuery(id+"F1.wireOp",EDGE,"E2363"),sQuery(id+"F1.wireOp",EDGE,"E2364"),sQuery(id+"F1.wireOp",EDGE,"E2365"),sQuery(id+"F1.wireOp",EDGE,"E2366"),sQuery(id+"F1.wireOp",EDGE,"E2367"),sQuery(id+"F1.wireOp",EDGE,"E2368"),sQuery(id+"F1.wireOp",EDGE,"E2369"),sQuery(id+"F1.wireOp",EDGE,"E2370"),sQuery(id+"F1.wireOp",EDGE,"E2371"),sQuery(id+"F1.wireOp",EDGE,"E2372"),sQuery(id+"F1.wireOp",EDGE,"E2373"),sQuery(id+"F1.wireOp",EDGE,"E2374"),sQuery(id+"F1.wireOp",EDGE,"E2375"),sQuery(id+"F1.wireOp",EDGE,"E2376"),sQuery(id+"F1.wireOp",EDGE,"E2377"),sQuery(id+"F1.wireOp",EDGE,"E2378"),sQuery(id+"F1.wireOp",EDGE,"E2379"),sQuery(id+"F1.wireOp",EDGE,"E2380"),sQuery(id+"F1.wireOp",EDGE,"E2381"),sQuery(id+"F1.wireOp",EDGE,"E2382"),sQuery(id+"F1.wireOp",EDGE,"E2383"),sQuery(id+"F1.wireOp",EDGE,"E2384"),sQuery(id+"F1.wireOp",EDGE,"E2385"),sQuery(id+"F1.wireOp",EDGE,"E2386"),sQuery(id+"F1.wireOp",EDGE,"E2387"),sQuery(id+"F1.wireOp",EDGE,"E2388"),sQuery(id+"F1.wireOp",EDGE,"E2389"),sQuery(id+"F1.wireOp",EDGE,"E2390"),sQuery(id+"F1.wireOp",EDGE,"E2391"),sQuery(id+"F1.wireOp",EDGE,"E2392"),sQuery(id+"F1.wireOp",EDGE,"E2393"),sQuery(id+"F1.wireOp",EDGE,"E2394"),sQuery(id+"F1.wireOp",EDGE,"E2395"),sQuery(id+"F1.wireOp",EDGE,"E2396"),sQuery(id+"F1.wireOp",EDGE,"E2397"),sQuery(id+"F1.wireOp",EDGE,"E2398"),sQuery(id+"F1.wireOp",EDGE,"E2399"),sQuery(id+"F1.wireOp",EDGE,"E2400"),sQuery(id+"F1.wireOp",EDGE,"E2401"),sQuery(id+"F1.wireOp",EDGE,"E2402"),sQuery(id+"F1.wireOp",EDGE,"E2403"),sQuery(id+"F1.wireOp",EDGE,"E2404"),sQuery(id+"F1.wireOp",EDGE,"E2405"),sQuery(id+"F1.wireOp",EDGE,"E2406"),sQuery(id+"F1.wireOp",EDGE,"E2407"),sQuery(id+"F1.wireOp",EDGE,"E2408"),sQuery(id+"F1.wireOp",EDGE,"E2409"),sQuery(id+"F1.wireOp",EDGE,"E2410"),sQuery(id+"F1.wireOp",EDGE,"E2411"),sQuery(id+"F1.wireOp",EDGE,"E2412"),sQuery(id+"F1.wireOp",EDGE,"E2413"),sQuery(id+"F1.wireOp",EDGE,"E2414"),sQuery(id+"F1.wireOp",EDGE,"E2415"),sQuery(id+"F1.wireOp",EDGE,"E2416"),sQuery(id+"F1.wireOp",EDGE,"E2417"),sQuery(id+"F1.wireOp",EDGE,"E2418"),sQuery(id+"F1.wireOp",EDGE,"E2419"),sQuery(id+"F1.wireOp",EDGE,"E2420"),sQuery(id+"F1.wireOp",EDGE,"E2421"),sQuery(id+"F1.wireOp",EDGE,"E2422"),sQuery(id+"F1.wireOp",EDGE,"E2423"),sQuery(id+"F1.wireOp",EDGE,"E2424"),sQuery(id+"F1.wireOp",EDGE,"E2425"),sQuery(id+"F1.wireOp",EDGE,"E2426"),sQuery(id+"F1.wireOp",EDGE,"E2427"),sQuery(id+"F1.wireOp",EDGE,"E2428"),sQuery(id+"F1.wireOp",EDGE,"E2429"),sQuery(id+"F1.wireOp",EDGE,"E2430"),sQuery(id+"F1.wireOp",EDGE,"E2431"),sQuery(id+"F1.wireOp",EDGE,"E2432"),sQuery(id+"F1.wireOp",EDGE,"E2433"),sQuery(id+"F1.wireOp",EDGE,"E2434"),sQuery(id+"F1.wireOp",EDGE,"E2435"),sQuery(id+"F1.wireOp",EDGE,"E2436"),sQuery(id+"F1.wireOp",EDGE,"E2437"),sQuery(id+"F1.wireOp",EDGE,"E2438"),sQuery(id+"F1.wireOp",EDGE,"E2439"),sQuery(id+"F1.wireOp",EDGE,"E2440"),sQuery(id+"F1.wireOp",EDGE,"E2441"),sQuery(id+"F1.wireOp",EDGE,"E2442"),sQuery(id+"F1.wireOp",EDGE,"E2443"),sQuery(id+"F1.wireOp",EDGE,"E2444"),sQuery(id+"F1.wireOp",EDGE,"E2445"),sQuery(id+"F1.wireOp",EDGE,"E2446"),sQuery(id+"F1.wireOp",EDGE,"E2447"),sQuery(id+"F1.wireOp",EDGE,"E2448"),sQuery(id+"F1.wireOp",EDGE,"E2449"),sQuery(id+"F1.wireOp",EDGE,"E2450"),sQuery(id+"F1.wireOp",EDGE,"E2451"),sQuery(id+"F1.wireOp",EDGE,"E2452"),sQuery(id+"F1.wireOp",EDGE,"E2453"),sQuery(id+"F1.wireOp",EDGE,"E2454"),sQuery(id+"F1.wireOp",EDGE,"E2455"),sQuery(id+"F1.wireOp",EDGE,"E2456"),sQuery(id+"F1.wireOp",EDGE,"E2457"),sQuery(id+"F1.wireOp",EDGE,"E2458"),sQuery(id+"F1.wireOp",EDGE,"E2459"),sQuery(id+"F1.wireOp",EDGE,"E2460"),sQuery(id+"F1.wireOp",EDGE,"E2461"),sQuery(id+"F1.wireOp",EDGE,"E2462"),sQuery(id+"F1.wireOp",EDGE,"E2463"),sQuery(id+"F1.wireOp",EDGE,"E2464"),sQuery(id+"F1.wireOp",EDGE,"E2465"),sQuery(id+"F1.wireOp",EDGE,"E2466"),sQuery(id+"F1.wireOp",EDGE,"E2467"),sQuery(id+"F1.wireOp",EDGE,"E2468"),sQuery(id+"F1.wireOp",EDGE,"E2469"),sQuery(id+"F1.wireOp",EDGE,"E2470"),sQuery(id+"F1.wireOp",EDGE,"E2471"),sQuery(id+"F1.wireOp",EDGE,"E2472"),sQuery(id+"F1.wireOp",EDGE,"E2473"),sQuery(id+"F1.wireOp",EDGE,"E2474"),sQuery(id+"F1.wireOp",EDGE,"E2475"),sQuery(id+"F1.wireOp",EDGE,"E2476"),sQuery(id+"F1.wireOp",EDGE,"E2477"),sQuery(id+"F1.wireOp",EDGE,"E2478"),sQuery(id+"F1.wireOp",EDGE,"E2479"),sQuery(id+"F1.wireOp",EDGE,"E2480"),sQuery(id+"F1.wireOp",EDGE,"E2481"),sQuery(id+"F1.wireOp",EDGE,"E2482"),sQuery(id+"F1.wireOp",EDGE,"E2483"),sQuery(id+"F1.wireOp",EDGE,"E2484"),sQuery(id+"F1.wireOp",EDGE,"E2485"),sQuery(id+"F1.wireOp",EDGE,"E2486"),sQuery(id+"F1.wireOp",EDGE,"E2487"),sQuery(id+"F1.wireOp",EDGE,"E2488"),sQuery(id+"F1.wireOp",EDGE,"E2489"),sQuery(id+"F1.wireOp",EDGE,"E2490"),sQuery(id+"F1.wireOp",EDGE,"E2491"),sQuery(id+"F1.wireOp",EDGE,"E2492"),sQuery(id+"F1.wireOp",EDGE,"E2493"),sQuery(id+"F1.wireOp",EDGE,"E2494"),sQuery(id+"F1.wireOp",EDGE,"E2495"),sQuery(id+"F1.wireOp",EDGE,"E2496"),sQuery(id+"F1.wireOp",EDGE,"E2497"),sQuery(id+"F1.wireOp",EDGE,"E2498"),sQuery(id+"F1.wireOp",EDGE,"E2499"),sQuery(id+"F1.wireOp",EDGE,"E2500"),sQuery(id+"F1.wireOp",EDGE,"E2501"),sQuery(id+"F1.wireOp",EDGE,"E2502"),sQuery(id+"F1.wireOp",EDGE,"E2503"),sQuery(id+"F1.wireOp",EDGE,"E2504"),sQuery(id+"F1.wireOp",EDGE,"E2505"),sQuery(id+"F1.wireOp",EDGE,"E2506"),sQuery(id+"F1.wireOp",EDGE,"E2507"),sQuery(id+"F1.wireOp",EDGE,"E2508"),sQuery(id+"F1.wireOp",EDGE,"E2509"),sQuery(id+"F1.wireOp",EDGE,"E2510"),sQuery(id+"F1.wireOp",EDGE,"E2511"),sQuery(id+"F1.wireOp",EDGE,"E2512"),sQuery(id+"F1.wireOp",EDGE,"E2513"),sQuery(id+"F1.wireOp",EDGE,"E2514"),sQuery(id+"F1.wireOp",EDGE,"E2515"),sQuery(id+"F1.wireOp",EDGE,"E2516"),sQuery(id+"F1.wireOp",EDGE,"E2517"),sQuery(id+"F1.wireOp",EDGE,"E2518"),sQuery(id+"F1.wireOp",EDGE,"E2519"),sQuery(id+"F1.wireOp",EDGE,"E2520"),sQuery(id+"F1.wireOp",EDGE,"E2521"),sQuery(id+"F1.wireOp",EDGE,"E2522"),sQuery(id+"F1.wireOp",EDGE,"E2523"),sQuery(id+"F1.wireOp",EDGE,"E2524"),sQuery(id+"F1.wireOp",EDGE,"E2525"),sQuery(id+"F1.wireOp",EDGE,"E2526"),sQuery(id+"F1.wireOp",EDGE,"E2527"),sQuery(id+"F1.wireOp",EDGE,"E2528"),sQuery(id+"F1.wireOp",EDGE,"E2529"),sQuery(id+"F1.wireOp",EDGE,"E2530"),sQuery(id+"F1.wireOp",EDGE,"E2531"),sQuery(id+"F1.wireOp",EDGE,"E2532"),sQuery(id+"F1.wireOp",EDGE,"E2533"),sQuery(id+"F1.wireOp",EDGE,"E2534"),sQuery(id+"F1.wireOp",EDGE,"E2535"),sQuery(id+"F1.wireOp",EDGE,"E2536"),sQuery(id+"F1.wireOp",EDGE,"E2537"),sQuery(id+"F1.wireOp",EDGE,"E2538"),sQuery(id+"F1.wireOp",EDGE,"E2539"),sQuery(id+"F1.wireOp",EDGE,"E2540"),sQuery(id+"F1.wireOp",EDGE,"E2541"),sQuery(id+"F1.wireOp",EDGE,"E2542"),sQuery(id+"F1.wireOp",EDGE,"E2543"),sQuery(id+"F1.wireOp",EDGE,"E2544"),sQuery(id+"F1.wireOp",EDGE,"E2545"),sQuery(id+"F1.wireOp",EDGE,"E2546"),sQuery(id+"F1.wireOp",EDGE,"E2547"),sQuery(id+"F1.wireOp",EDGE,"E2548"),sQuery(id+"F1.wireOp",EDGE,"E2549"),sQuery(id+"F1.wireOp",EDGE,"E2550"),sQuery(id+"F1.wireOp",EDGE,"E2551"),sQuery(id+"F1.wireOp",EDGE,"E2552"),sQuery(id+"F1.wireOp",EDGE,"E2553"),sQuery(id+"F1.wireOp",EDGE,"E2554"),sQuery(id+"F1.wireOp",EDGE,"E2555"),sQuery(id+"F1.wireOp",EDGE,"E2556"),sQuery(id+"F1.wireOp",EDGE,"E2557"),sQuery(id+"F1.wireOp",EDGE,"E2558"),sQuery(id+"F1.wireOp",EDGE,"E2559"),sQuery(id+"F1.wireOp",EDGE,"E2560"),sQuery(id+"F1.wireOp",EDGE,"E2561"),sQuery(id+"F1.wireOp",EDGE,"E2562"),sQuery(id+"F1.wireOp",EDGE,"E2563"),sQuery(id+"F1.wireOp",EDGE,"E2564"),sQuery(id+"F1.wireOp",EDGE,"E2565"),sQuery(id+"F1.wireOp",EDGE,"E2566"),sQuery(id+"F1.wireOp",EDGE,"E2567"),sQuery(id+"F1.wireOp",EDGE,"E2568"),sQuery(id+"F1.wireOp",EDGE,"E2569"),sQuery(id+"F1.wireOp",EDGE,"E2570"),sQuery(id+"F1.wireOp",EDGE,"E2571"),sQuery(id+"F1.wireOp",EDGE,"E2572"),sQuery(id+"F1.wireOp",EDGE,"E2573"),sQuery(id+"F1.wireOp",EDGE,"E2574"),sQuery(id+"F1.wireOp",EDGE,"E2575"),sQuery(id+"F1.wireOp",EDGE,"E2576"),sQuery(id+"F1.wireOp",EDGE,"E2577"),sQuery(id+"F1.wireOp",EDGE,"E2578"),sQuery(id+"F1.wireOp",EDGE,"E2579"),sQuery(id+"F1.wireOp",EDGE,"E2580"),sQuery(id+"F1.wireOp",EDGE,"E2581"),sQuery(id+"F1.wireOp",EDGE,"E2582"),sQuery(id+"F1.wireOp",EDGE,"E2583"),sQuery(id+"F1.wireOp",EDGE,"E2584"),sQuery(id+"F1.wireOp",EDGE,"E2585"),sQuery(id+"F1.wireOp",EDGE,"E2586"),sQuery(id+"F1.wireOp",EDGE,"E2587"),sQuery(id+"F1.wireOp",EDGE,"E2588"),sQuery(id+"F1.wireOp",EDGE,"E2589"),sQuery(id+"F1.wireOp",EDGE,"E2590"),sQuery(id+"F1.wireOp",EDGE,"E2591"),sQuery(id+"F1.wireOp",EDGE,"E2592"),sQuery(id+"F1.wireOp",EDGE,"E2593"),sQuery(id+"F1.wireOp",EDGE,"E2594"),sQuery(id+"F1.wireOp",EDGE,"E2595"),sQuery(id+"F1.wireOp",EDGE,"E2596"),sQuery(id+"F1.wireOp",EDGE,"E2597"),sQuery(id+"F1.wireOp",EDGE,"E2598"),sQuery(id+"F1.wireOp",EDGE,"E2599"),sQuery(id+"F1.wireOp",EDGE,"E2600"),sQuery(id+"F1.wireOp",EDGE,"E2601"),sQuery(id+"F1.wireOp",EDGE,"E2602"),sQuery(id+"F1.wireOp",EDGE,"E2603"),sQuery(id+"F1.wireOp",EDGE,"E2604"),sQuery(id+"F1.wireOp",EDGE,"E2605"),sQuery(id+"F1.wireOp",EDGE,"E2606"),sQuery(id+"F1.wireOp",EDGE,"E2607"),sQuery(id+"F1.wireOp",EDGE,"E2608"),sQuery(id+"F1.wireOp",EDGE,"E2609"),sQuery(id+"F1.wireOp",EDGE,"E2610"),sQuery(id+"F1.wireOp",EDGE,"E2611"),sQuery(id+"F1.wireOp",EDGE,"E2612"),sQuery(id+"F1.wireOp",EDGE,"E2613"),sQuery(id+"F1.wireOp",EDGE,"E2614"),sQuery(id+"F1.wireOp",EDGE,"E2615"),sQuery(id+"F1.wireOp",EDGE,"E2616"),sQuery(id+"F1.wireOp",EDGE,"E2617"),sQuery(id+"F1.wireOp",EDGE,"E2618"),sQuery(id+"F1.wireOp",EDGE,"E2619"),sQuery(id+"F1.wireOp",EDGE,"E2620"),sQuery(id+"F1.wireOp",EDGE,"E2622")])]});
            var Q1;
            Q1=sQuery(id+"F0.wireOp",VERTEX,"E0.center");
            var Q2;
            Q2=sQuery(id+"F0.wireOp",VERTEX,"E8.center.orphan");
            transform(context, id + "F9", {"entities" : qUnion([Q0]), "transformType" : TransformType.TRANSLATION_ENTITY, "oppositeDirectionEntity" : false, "transformLine" : qUnion([Q1, Q2]), "makeCopy" : false});
        }
        {
            var Q0;
            Q0=qCreatedBy(makeId("Front.planeOp"),FACE);
            var sketch = newSketch(context, id + "F10", { "sketchPlane" : qUnion([Q0])});
            skLineSegment(sketch, "E2624", {"start": v(9.36, -0.85) * mm, "end": v(9.47, -0.84) * mm});
            skLineSegment(sketch, "E2625", {"start": v(9.47, -0.84) * mm, "end": v(9.58, -0.83) * mm});
            skLineSegment(sketch, "E2626", {"start": v(9.58, -0.83) * mm, "end": v(9.69, -0.82) * mm});
            skLineSegment(sketch, "E2627", {"start": v(9.69, -0.82) * mm, "end": v(9.8, -0.8) * mm});
            skLineSegment(sketch, "E2628", {"start": v(9.8, -0.8) * mm, "end": v(9.9, -0.77) * mm});
            skLineSegment(sketch, "E2629", {"start": v(9.9, -0.77) * mm, "end": v(10.01, -0.74) * mm});
            skLineSegment(sketch, "E2630", {"start": v(10.01, -0.74) * mm, "end": v(10.11, -0.7) * mm});
            skLineSegment(sketch, "E2631", {"start": v(10.11, -0.7) * mm, "end": v(10.22, -0.67) * mm});
            skLineSegment(sketch, "E2632", {"start": v(10.22, -0.67) * mm, "end": v(10.32, -0.63) * mm});
            skLineSegment(sketch, "E2633", {"start": v(10.32, -0.63) * mm, "end": v(10.42, -0.6) * mm});
            skLineSegment(sketch, "E2634", {"start": v(10.42, -0.6) * mm, "end": v(10.53, -0.55) * mm});
            skLineSegment(sketch, "E2635", {"start": v(10.53, -0.55) * mm, "end": v(10.63, -0.5) * mm});
            skLineSegment(sketch, "E2636", {"start": v(10.63, -0.5) * mm, "end": v(10.73, -0.45) * mm});
            skLineSegment(sketch, "E2637", {"start": v(10.73, -0.45) * mm, "end": v(10.83, -0.4) * mm});
            skLineSegment(sketch, "E2638", {"start": v(10.83, -0.4) * mm, "end": v(10.93, -0.34) * mm});
            skLineSegment(sketch, "E2639", {"start": v(10.93, -0.34) * mm, "end": v(10.95, -0.33) * mm});
            skLineSegment(sketch, "E2640", {"start": v(10.95, -0.33) * mm, "end": v(10.95, -0.22) * mm});
            skLineSegment(sketch, "E2641", {"start": v(10.95, -0.22) * mm, "end": v(10.96, -0.1) * mm});
            skLineSegment(sketch, "E2642", {"start": v(10.96, -0.1) * mm, "end": v(10.96, 0.03) * mm});
            skLineSegment(sketch, "E2643", {"start": v(10.96, 0.03) * mm, "end": v(10.96, 0.15) * mm});
            skLineSegment(sketch, "E2644", {"start": v(10.96, 0.15) * mm, "end": v(10.95, 0.27) * mm});
            skLineSegment(sketch, "E2645", {"start": v(10.95, 0.27) * mm, "end": v(10.95, 0.33) * mm});
            skLineSegment(sketch, "E2646", {"start": v(10.95, 0.33) * mm, "end": v(10.85, 0.4) * mm});
            skLineSegment(sketch, "E2647", {"start": v(10.85, 0.4) * mm, "end": v(10.75, 0.44) * mm});
            skLineSegment(sketch, "E2648", {"start": v(10.75, 0.44) * mm, "end": v(10.64, 0.5) * mm});
            skLineSegment(sketch, "E2649", {"start": v(10.64, 0.5) * mm, "end": v(10.53, 0.55) * mm});
            skLineSegment(sketch, "E2650", {"start": v(10.53, 0.55) * mm, "end": v(10.43, 0.59) * mm});
            skLineSegment(sketch, "E2651", {"start": v(10.43, 0.59) * mm, "end": v(10.32, 0.63) * mm});
            skLineSegment(sketch, "E2652", {"start": v(10.32, 0.63) * mm, "end": v(10.21, 0.67) * mm});
            skLineSegment(sketch, "E2653", {"start": v(10.21, 0.67) * mm, "end": v(10.1, 0.71) * mm});
            skLineSegment(sketch, "E2654", {"start": v(10.1, 0.71) * mm, "end": v(10, 0.74) * mm});
            skLineSegment(sketch, "E2655", {"start": v(10, 0.74) * mm, "end": v(9.88, 0.77) * mm});
            skLineSegment(sketch, "E2656", {"start": v(9.88, 0.77) * mm, "end": v(9.76, 0.8) * mm});
            skLineSegment(sketch, "E2657", {"start": v(9.76, 0.8) * mm, "end": v(9.64, 0.82) * mm});
            skLineSegment(sketch, "E2658", {"start": v(9.64, 0.82) * mm, "end": v(9.53, 0.84) * mm});
            skLineSegment(sketch, "E2659", {"start": v(9.53, 0.84) * mm, "end": v(9.42, 0.85) * mm});
            skLineSegment(sketch, "E2660", {"start": v(9.42, 0.85) * mm, "end": v(9.4, 0.85) * mm});
            skLineSegment(sketch, "E2661", {"start": v(9.4, 0.85) * mm, "end": v(9.28, 0.84) * mm});
            skLineSegment(sketch, "E2662", {"start": v(9.28, 0.84) * mm, "end": v(9.15, 0.84) * mm});
            skLineSegment(sketch, "E2663", {"start": v(9.15, 0.84) * mm, "end": v(9.04, 0.85) * mm});
            skLineSegment(sketch, "E2664", {"start": v(9.04, 0.85) * mm, "end": v(8.93, 0.88) * mm});
            skLineSegment(sketch, "E2665", {"start": v(8.93, 0.88) * mm, "end": v(8.83, 0.92) * mm});
            skLineSegment(sketch, "E2666", {"start": v(8.83, 0.92) * mm, "end": v(8.77, 0.98) * mm});
            skLineSegment(sketch, "E2667", {"start": v(8.77, 0.98) * mm, "end": v(8.75, 1.1) * mm});
            skLineSegment(sketch, "E2668", {"start": v(8.75, 1.1) * mm, "end": v(8.73, 1.22) * mm});
            skLineSegment(sketch, "E2669", {"start": v(8.73, 1.22) * mm, "end": v(8.7, 1.34) * mm});
            skLineSegment(sketch, "E2670", {"start": v(8.7, 1.34) * mm, "end": v(8.68, 1.45) * mm});
            skLineSegment(sketch, "E2671", {"start": v(8.68, 1.45) * mm, "end": v(8.66, 1.57) * mm});
            skLineSegment(sketch, "E2672", {"start": v(8.66, 1.57) * mm, "end": v(8.66, 1.64) * mm});
            skLineSegment(sketch, "E2673", {"start": v(8.66, 1.64) * mm, "end": v(8.71, 1.74) * mm});
            skLineSegment(sketch, "E2674", {"start": v(8.71, 1.74) * mm, "end": v(8.8, 1.81) * mm});
            skLineSegment(sketch, "E2675", {"start": v(8.8, 1.81) * mm, "end": v(8.9, 1.87) * mm});
            skLineSegment(sketch, "E2676", {"start": v(8.9, 1.87) * mm, "end": v(9, 1.9) * mm});
            skLineSegment(sketch, "E2677", {"start": v(9, 1.9) * mm, "end": v(9.12, 1.94) * mm});
            skLineSegment(sketch, "E2678", {"start": v(9.12, 1.94) * mm, "end": v(9.22, 1.97) * mm});
            skLineSegment(sketch, "E2679", {"start": v(9.22, 1.97) * mm, "end": v(9.33, 2) * mm});
            skLineSegment(sketch, "E2680", {"start": v(9.33, 2) * mm, "end": v(9.43, 2.05) * mm});
            skLineSegment(sketch, "E2681", {"start": v(9.43, 2.05) * mm, "end": v(9.53, 2.1) * mm});
            skLineSegment(sketch, "E2682", {"start": v(9.53, 2.1) * mm, "end": v(9.62, 2.16) * mm});
            skLineSegment(sketch, "E2683", {"start": v(9.62, 2.16) * mm, "end": v(9.72, 2.21) * mm});
            skLineSegment(sketch, "E2684", {"start": v(9.72, 2.21) * mm, "end": v(9.8, 2.27) * mm});
            skLineSegment(sketch, "E2685", {"start": v(9.8, 2.27) * mm, "end": v(9.9, 2.34) * mm});
            skLineSegment(sketch, "E2686", {"start": v(9.9, 2.34) * mm, "end": v(10, 2.4) * mm});
            skLineSegment(sketch, "E2687", {"start": v(10, 2.4) * mm, "end": v(10.08, 2.47) * mm});
            skLineSegment(sketch, "E2688", {"start": v(10.08, 2.47) * mm, "end": v(10.16, 2.54) * mm});
            skLineSegment(sketch, "E2689", {"start": v(10.16, 2.54) * mm, "end": v(10.25, 2.62) * mm});
            skLineSegment(sketch, "E2690", {"start": v(10.25, 2.62) * mm, "end": v(10.34, 2.7) * mm});
            skLineSegment(sketch, "E2691", {"start": v(10.34, 2.7) * mm, "end": v(10.41, 2.77) * mm});
            skLineSegment(sketch, "E2692", {"start": v(10.41, 2.77) * mm, "end": v(10.5, 2.85) * mm});
            skLineSegment(sketch, "E2693", {"start": v(10.5, 2.85) * mm, "end": v(10.56, 2.92) * mm});
            skLineSegment(sketch, "E2694", {"start": v(10.56, 2.92) * mm, "end": v(10.53, 3.03) * mm});
            skLineSegment(sketch, "E2695", {"start": v(10.53, 3.03) * mm, "end": v(10.5, 3.15) * mm});
            skLineSegment(sketch, "E2696", {"start": v(10.5, 3.15) * mm, "end": v(10.46, 3.27) * mm});
            skLineSegment(sketch, "E2697", {"start": v(10.46, 3.27) * mm, "end": v(10.42, 3.39) * mm});
            skLineSegment(sketch, "E2698", {"start": v(10.42, 3.39) * mm, "end": v(10.38, 3.5) * mm});
            skLineSegment(sketch, "E2699", {"start": v(10.38, 3.5) * mm, "end": v(10.36, 3.56) * mm});
            skLineSegment(sketch, "E2700", {"start": v(10.36, 3.56) * mm, "end": v(10.25, 3.58) * mm});
            skLineSegment(sketch, "E2701", {"start": v(10.25, 3.58) * mm, "end": v(10.14, 3.6) * mm});
            skLineSegment(sketch, "E2702", {"start": v(10.14, 3.6) * mm, "end": v(10.02, 3.62) * mm});
            skLineSegment(sketch, "E2703", {"start": v(10.02, 3.62) * mm, "end": v(9.9, 3.64) * mm});
            skLineSegment(sketch, "E2704", {"start": v(9.9, 3.64) * mm, "end": v(9.8, 3.65) * mm});
            skLineSegment(sketch, "E2705", {"start": v(9.8, 3.65) * mm, "end": v(9.67, 3.66) * mm});
            skLineSegment(sketch, "E2706", {"start": v(9.67, 3.66) * mm, "end": v(9.56, 3.67) * mm});
            skLineSegment(sketch, "E2707", {"start": v(9.56, 3.67) * mm, "end": v(9.44, 3.67) * mm});
            skLineSegment(sketch, "E2708", {"start": v(9.44, 3.67) * mm, "end": v(9.4, 3.67) * mm});
            skLineSegment(sketch, "E2709", {"start": v(9.4, 3.67) * mm, "end": v(9.27, 3.67) * mm});
            skLineSegment(sketch, "E2710", {"start": v(9.27, 3.67) * mm, "end": v(9.16, 3.66) * mm});
            skLineSegment(sketch, "E2711", {"start": v(9.16, 3.66) * mm, "end": v(9.04, 3.65) * mm});
            skLineSegment(sketch, "E2712", {"start": v(9.04, 3.65) * mm, "end": v(8.93, 3.63) * mm});
            skLineSegment(sketch, "E2713", {"start": v(8.93, 3.63) * mm, "end": v(8.82, 3.61) * mm});
            skLineSegment(sketch, "E2714", {"start": v(8.82, 3.61) * mm, "end": v(8.71, 3.59) * mm});
            skLineSegment(sketch, "E2715", {"start": v(8.71, 3.59) * mm, "end": v(8.6, 3.55) * mm});
            skLineSegment(sketch, "E2716", {"start": v(8.6, 3.55) * mm, "end": v(8.5, 3.51) * mm});
            skLineSegment(sketch, "E2717", {"start": v(8.5, 3.51) * mm, "end": v(8.38, 3.49) * mm});
            skLineSegment(sketch, "E2718", {"start": v(8.38, 3.49) * mm, "end": v(8.28, 3.48) * mm});
            skLineSegment(sketch, "E2719", {"start": v(8.28, 3.48) * mm, "end": v(8.17, 3.5) * mm});
            skLineSegment(sketch, "E2720", {"start": v(8.17, 3.5) * mm, "end": v(8.09, 3.53) * mm});
            skLineSegment(sketch, "E2721", {"start": v(8.09, 3.53) * mm, "end": v(8.03, 3.64) * mm});
            skLineSegment(sketch, "E2722", {"start": v(8.03, 3.64) * mm, "end": v(7.98, 3.75) * mm});
            skLineSegment(sketch, "E2723", {"start": v(7.98, 3.75) * mm, "end": v(7.92, 3.85) * mm});
            skLineSegment(sketch, "E2724", {"start": v(7.92, 3.85) * mm, "end": v(7.87, 3.96) * mm});
            skLineSegment(sketch, "E2725", {"start": v(7.87, 3.96) * mm, "end": v(7.81, 4.07) * mm});
            skLineSegment(sketch, "E2726", {"start": v(7.81, 4.07) * mm, "end": v(7.8, 4.13) * mm});
            skLineSegment(sketch, "E2727", {"start": v(7.8, 4.13) * mm, "end": v(7.81, 4.24) * mm});
            skLineSegment(sketch, "E2728", {"start": v(7.81, 4.24) * mm, "end": v(7.87, 4.34) * mm});
            skLineSegment(sketch, "E2729", {"start": v(7.87, 4.34) * mm, "end": v(7.94, 4.42) * mm});
            skLineSegment(sketch, "E2730", {"start": v(7.94, 4.42) * mm, "end": v(8.04, 4.48) * mm});
            skLineSegment(sketch, "E2731", {"start": v(8.04, 4.48) * mm, "end": v(8.14, 4.55) * mm});
            skLineSegment(sketch, "E2732", {"start": v(8.14, 4.55) * mm, "end": v(8.23, 4.61) * mm});
            skLineSegment(sketch, "E2733", {"start": v(8.23, 4.61) * mm, "end": v(8.32, 4.68) * mm});
            skLineSegment(sketch, "E2734", {"start": v(8.32, 4.68) * mm, "end": v(8.4, 4.75) * mm});
            skLineSegment(sketch, "E2735", {"start": v(8.4, 4.75) * mm, "end": v(8.48, 4.83) * mm});
            skLineSegment(sketch, "E2736", {"start": v(8.48, 4.83) * mm, "end": v(8.56, 4.9) * mm});
            skLineSegment(sketch, "E2737", {"start": v(8.56, 4.9) * mm, "end": v(8.63, 5) * mm});
            skLineSegment(sketch, "E2738", {"start": v(8.63, 5) * mm, "end": v(8.7, 5.07) * mm});
            skLineSegment(sketch, "E2739", {"start": v(8.7, 5.07) * mm, "end": v(8.77, 5.16) * mm});
            skLineSegment(sketch, "E2740", {"start": v(8.77, 5.16) * mm, "end": v(8.84, 5.25) * mm});
            skLineSegment(sketch, "E2741", {"start": v(8.84, 5.25) * mm, "end": v(8.9, 5.35) * mm});
            skLineSegment(sketch, "E2742", {"start": v(8.9, 5.35) * mm, "end": v(8.96, 5.44) * mm});
            skLineSegment(sketch, "E2743", {"start": v(8.96, 5.44) * mm, "end": v(9.02, 5.54) * mm});
            skLineSegment(sketch, "E2744", {"start": v(9.02, 5.54) * mm, "end": v(9.08, 5.63) * mm});
            skLineSegment(sketch, "E2745", {"start": v(9.08, 5.63) * mm, "end": v(9.13, 5.73) * mm});
            skLineSegment(sketch, "E2746", {"start": v(9.13, 5.73) * mm, "end": v(9.19, 5.83) * mm});
            skLineSegment(sketch, "E2747", {"start": v(9.19, 5.83) * mm, "end": v(9.23, 5.91) * mm});
            skLineSegment(sketch, "E2748", {"start": v(9.23, 5.91) * mm, "end": v(9.17, 6.02) * mm});
            skLineSegment(sketch, "E2749", {"start": v(9.17, 6.02) * mm, "end": v(9.1, 6.12) * mm});
            skLineSegment(sketch, "E2750", {"start": v(9.1, 6.12) * mm, "end": v(9.03, 6.22) * mm});
            skLineSegment(sketch, "E2751", {"start": v(9.03, 6.22) * mm, "end": v(8.96, 6.32) * mm});
            skLineSegment(sketch, "E2752", {"start": v(8.96, 6.32) * mm, "end": v(8.89, 6.42) * mm});
            skLineSegment(sketch, "E2753", {"start": v(8.89, 6.42) * mm, "end": v(8.85, 6.47) * mm});
            skLineSegment(sketch, "E2754", {"start": v(8.85, 6.47) * mm, "end": v(8.73, 6.46) * mm});
            skLineSegment(sketch, "E2755", {"start": v(8.73, 6.46) * mm, "end": v(8.63, 6.44) * mm});
            skLineSegment(sketch, "E2756", {"start": v(8.63, 6.44) * mm, "end": v(8.5, 6.43) * mm});
            skLineSegment(sketch, "E2757", {"start": v(8.5, 6.43) * mm, "end": v(8.39, 6.4) * mm});
            skLineSegment(sketch, "E2758", {"start": v(8.39, 6.4) * mm, "end": v(8.28, 6.38) * mm});
            skLineSegment(sketch, "E2759", {"start": v(8.28, 6.38) * mm, "end": v(8.16, 6.36) * mm});
            skLineSegment(sketch, "E2760", {"start": v(8.16, 6.36) * mm, "end": v(8.05, 6.33) * mm});
            skLineSegment(sketch, "E2761", {"start": v(8.05, 6.33) * mm, "end": v(7.94, 6.3) * mm});
            skLineSegment(sketch, "E2762", {"start": v(7.94, 6.3) * mm, "end": v(7.83, 6.27) * mm});
            skLineSegment(sketch, "E2763", {"start": v(7.83, 6.27) * mm, "end": v(7.72, 6.23) * mm});
            skLineSegment(sketch, "E2764", {"start": v(7.72, 6.23) * mm, "end": v(7.6, 6.18) * mm});
            skLineSegment(sketch, "E2765", {"start": v(7.6, 6.18) * mm, "end": v(7.5, 6.13) * mm});
            skLineSegment(sketch, "E2766", {"start": v(7.5, 6.13) * mm, "end": v(7.4, 6.08) * mm});
            skLineSegment(sketch, "E2767", {"start": v(7.4, 6.08) * mm, "end": v(7.3, 6.03) * mm});
            skLineSegment(sketch, "E2768", {"start": v(7.3, 6.03) * mm, "end": v(7.2, 5.96) * mm});
            skLineSegment(sketch, "E2769", {"start": v(7.2, 5.96) * mm, "end": v(7.1, 5.89) * mm});
            skLineSegment(sketch, "E2770", {"start": v(7.1, 5.89) * mm, "end": v(7.01, 5.83) * mm});
            skLineSegment(sketch, "E2771", {"start": v(7.01, 5.83) * mm, "end": v(6.9, 5.78) * mm});
            skLineSegment(sketch, "E2772", {"start": v(6.9, 5.78) * mm, "end": v(6.79, 5.76) * mm});
            skLineSegment(sketch, "E2773", {"start": v(6.79, 5.76) * mm, "end": v(6.77, 5.76) * mm});
            skLineSegment(sketch, "E2774", {"start": v(6.77, 5.76) * mm, "end": v(6.68, 5.77) * mm});
            skLineSegment(sketch, "E2775", {"start": v(6.68, 5.77) * mm, "end": v(6.6, 5.86) * mm});
            skLineSegment(sketch, "E2776", {"start": v(6.6, 5.86) * mm, "end": v(6.52, 5.94) * mm});
            skLineSegment(sketch, "E2777", {"start": v(6.52, 5.94) * mm, "end": v(6.43, 6.03) * mm});
            skLineSegment(sketch, "E2778", {"start": v(6.43, 6.03) * mm, "end": v(6.35, 6.12) * mm});
            skLineSegment(sketch, "E2779", {"start": v(6.35, 6.12) * mm, "end": v(6.27, 6.2) * mm});
            skLineSegment(sketch, "E2780", {"start": v(6.27, 6.2) * mm, "end": v(6.23, 6.25) * mm});
            skLineSegment(sketch, "E2781", {"start": v(6.23, 6.25) * mm, "end": v(6.21, 6.37) * mm});
            skLineSegment(sketch, "E2782", {"start": v(6.21, 6.37) * mm, "end": v(6.24, 6.47) * mm});
            skLineSegment(sketch, "E2783", {"start": v(6.24, 6.47) * mm, "end": v(6.29, 6.57) * mm});
            skLineSegment(sketch, "E2784", {"start": v(6.29, 6.57) * mm, "end": v(6.36, 6.67) * mm});
            skLineSegment(sketch, "E2785", {"start": v(6.36, 6.67) * mm, "end": v(6.44, 6.76) * mm});
            skLineSegment(sketch, "E2786", {"start": v(6.44, 6.76) * mm, "end": v(6.5, 6.85) * mm});
            skLineSegment(sketch, "E2787", {"start": v(6.5, 6.85) * mm, "end": v(6.57, 6.94) * mm});
            skLineSegment(sketch, "E2788", {"start": v(6.57, 6.94) * mm, "end": v(6.63, 7.03) * mm});
            skLineSegment(sketch, "E2789", {"start": v(6.63, 7.03) * mm, "end": v(6.68, 7.13) * mm});
            skLineSegment(sketch, "E2790", {"start": v(6.68, 7.13) * mm, "end": v(6.73, 7.22) * mm});
            skLineSegment(sketch, "E2791", {"start": v(6.73, 7.22) * mm, "end": v(6.77, 7.32) * mm});
            skLineSegment(sketch, "E2792", {"start": v(6.77, 7.32) * mm, "end": v(6.82, 7.42) * mm});
            skLineSegment(sketch, "E2793", {"start": v(6.82, 7.42) * mm, "end": v(6.86, 7.53) * mm});
            skLineSegment(sketch, "E2794", {"start": v(6.86, 7.53) * mm, "end": v(6.9, 7.64) * mm});
            skLineSegment(sketch, "E2795", {"start": v(6.9, 7.64) * mm, "end": v(6.93, 7.74) * mm});
            skLineSegment(sketch, "E2796", {"start": v(6.93, 7.74) * mm, "end": v(6.96, 7.85) * mm});
            skLineSegment(sketch, "E2797", {"start": v(6.96, 7.85) * mm, "end": v(6.99, 7.96) * mm});
            skLineSegment(sketch, "E2798", {"start": v(6.99, 7.96) * mm, "end": v(7.01, 8.07) * mm});
            skLineSegment(sketch, "E2799", {"start": v(7.01, 8.07) * mm, "end": v(7.04, 8.18) * mm});
            skLineSegment(sketch, "E2800", {"start": v(7.04, 8.18) * mm, "end": v(7.06, 8.29) * mm});
            skLineSegment(sketch, "E2801", {"start": v(7.06, 8.29) * mm, "end": v(7.08, 8.38) * mm});
            skLineSegment(sketch, "E2802", {"start": v(7.08, 8.38) * mm, "end": v(6.98, 8.46) * mm});
            skLineSegment(sketch, "E2803", {"start": v(6.98, 8.46) * mm, "end": v(6.9, 8.54) * mm});
            skLineSegment(sketch, "E2804", {"start": v(6.9, 8.54) * mm, "end": v(6.79, 8.62) * mm});
            skLineSegment(sketch, "E2805", {"start": v(6.79, 8.62) * mm, "end": v(6.7, 8.7) * mm});
            skLineSegment(sketch, "E2806", {"start": v(6.7, 8.7) * mm, "end": v(6.6, 8.77) * mm});
            skLineSegment(sketch, "E2807", {"start": v(6.6, 8.77) * mm, "end": v(6.55, 8.8) * mm});
            skLineSegment(sketch, "E2808", {"start": v(6.55, 8.8) * mm, "end": v(6.44, 8.76) * mm});
            skLineSegment(sketch, "E2809", {"start": v(6.44, 8.76) * mm, "end": v(6.34, 8.71) * mm});
            skLineSegment(sketch, "E2810", {"start": v(6.34, 8.71) * mm, "end": v(6.23, 8.66) * mm});
            skLineSegment(sketch, "E2811", {"start": v(6.23, 8.66) * mm, "end": v(6.13, 8.6) * mm});
            skLineSegment(sketch, "E2812", {"start": v(6.13, 8.6) * mm, "end": v(6.03, 8.55) * mm});
            skLineSegment(sketch, "E2813", {"start": v(6.03, 8.55) * mm, "end": v(5.92, 8.5) * mm});
            skLineSegment(sketch, "E2814", {"start": v(5.92, 8.5) * mm, "end": v(5.83, 8.43) * mm});
            skLineSegment(sketch, "E2815", {"start": v(5.83, 8.43) * mm, "end": v(5.73, 8.37) * mm});
            skLineSegment(sketch, "E2816", {"start": v(5.73, 8.37) * mm, "end": v(5.64, 8.3) * mm});
            skLineSegment(sketch, "E2817", {"start": v(5.64, 8.3) * mm, "end": v(5.54, 8.24) * mm});
            skLineSegment(sketch, "E2818", {"start": v(5.54, 8.24) * mm, "end": v(5.44, 8.16) * mm});
            skLineSegment(sketch, "E2819", {"start": v(5.44, 8.16) * mm, "end": v(5.35, 8.08) * mm});
            skLineSegment(sketch, "E2820", {"start": v(5.35, 8.08) * mm, "end": v(5.27, 8) * mm});
            skLineSegment(sketch, "E2821", {"start": v(5.27, 8) * mm, "end": v(5.2, 7.92) * mm});
            skLineSegment(sketch, "E2822", {"start": v(5.2, 7.92) * mm, "end": v(5.12, 7.83) * mm});
            skLineSegment(sketch, "E2823", {"start": v(5.12, 7.83) * mm, "end": v(5.05, 7.73) * mm});
            skLineSegment(sketch, "E2824", {"start": v(5.05, 7.73) * mm, "end": v(4.98, 7.65) * mm});
            skLineSegment(sketch, "E2825", {"start": v(4.98, 7.65) * mm, "end": v(4.9, 7.57) * mm});
            skLineSegment(sketch, "E2826", {"start": v(4.9, 7.57) * mm, "end": v(4.79, 7.52) * mm});
            skLineSegment(sketch, "E2827", {"start": v(4.79, 7.52) * mm, "end": v(4.7, 7.5) * mm});
            skLineSegment(sketch, "E2828", {"start": v(4.7, 7.5) * mm, "end": v(4.66, 7.5) * mm});
            skLineSegment(sketch, "E2829", {"start": v(4.66, 7.5) * mm, "end": v(4.56, 7.56) * mm});
            skLineSegment(sketch, "E2830", {"start": v(4.56, 7.56) * mm, "end": v(4.46, 7.62) * mm});
            skLineSegment(sketch, "E2831", {"start": v(4.46, 7.62) * mm, "end": v(4.35, 7.68) * mm});
            skLineSegment(sketch, "E2832", {"start": v(4.35, 7.68) * mm, "end": v(4.25, 7.74) * mm});
            skLineSegment(sketch, "E2833", {"start": v(4.25, 7.74) * mm, "end": v(4.14, 7.8) * mm});
            skLineSegment(sketch, "E2834", {"start": v(4.14, 7.8) * mm, "end": v(4.1, 7.84) * mm});
            skLineSegment(sketch, "E2835", {"start": v(4.1, 7.84) * mm, "end": v(4.05, 7.95) * mm});
            skLineSegment(sketch, "E2836", {"start": v(4.05, 7.95) * mm, "end": v(4.06, 8.06) * mm});
            skLineSegment(sketch, "E2837", {"start": v(4.06, 8.06) * mm, "end": v(4.08, 8.18) * mm});
            skLineSegment(sketch, "E2838", {"start": v(4.08, 8.18) * mm, "end": v(4.12, 8.29) * mm});
            skLineSegment(sketch, "E2839", {"start": v(4.12, 8.29) * mm, "end": v(4.17, 8.4) * mm});
            skLineSegment(sketch, "E2840", {"start": v(4.17, 8.4) * mm, "end": v(4.2, 8.5) * mm});
            skLineSegment(sketch, "E2841", {"start": v(4.2, 8.5) * mm, "end": v(4.24, 8.6) * mm});
            skLineSegment(sketch, "E2842", {"start": v(4.24, 8.6) * mm, "end": v(4.26, 8.71) * mm});
            skLineSegment(sketch, "E2843", {"start": v(4.26, 8.71) * mm, "end": v(4.29, 8.82) * mm});
            skLineSegment(sketch, "E2844", {"start": v(4.29, 8.82) * mm, "end": v(4.3, 8.93) * mm});
            skLineSegment(sketch, "E2845", {"start": v(4.3, 8.93) * mm, "end": v(4.32, 9.04) * mm});
            skLineSegment(sketch, "E2846", {"start": v(4.32, 9.04) * mm, "end": v(4.33, 9.15) * mm});
            skLineSegment(sketch, "E2847", {"start": v(4.33, 9.15) * mm, "end": v(4.33, 9.27) * mm});
            skLineSegment(sketch, "E2848", {"start": v(4.33, 9.27) * mm, "end": v(4.34, 9.38) * mm});
            skLineSegment(sketch, "E2849", {"start": v(4.34, 9.38) * mm, "end": v(4.34, 9.5) * mm});
            skLineSegment(sketch, "E2850", {"start": v(4.34, 9.5) * mm, "end": v(4.33, 9.6) * mm});
            skLineSegment(sketch, "E2851", {"start": v(4.33, 9.6) * mm, "end": v(4.33, 9.71) * mm});
            skLineSegment(sketch, "E2852", {"start": v(4.33, 9.71) * mm, "end": v(4.32, 9.83) * mm});
            skLineSegment(sketch, "E2853", {"start": v(4.32, 9.83) * mm, "end": v(4.3, 9.94) * mm});
            skLineSegment(sketch, "E2854", {"start": v(4.3, 9.94) * mm, "end": v(4.3, 10.05) * mm});
            skLineSegment(sketch, "E2855", {"start": v(4.3, 10.05) * mm, "end": v(4.29, 10.1) * mm});
            skLineSegment(sketch, "E2856", {"start": v(4.29, 10.1) * mm, "end": v(4.18, 10.16) * mm});
            skLineSegment(sketch, "E2857", {"start": v(4.18, 10.16) * mm, "end": v(4.07, 10.2) * mm});
            skLineSegment(sketch, "E2858", {"start": v(4.07, 10.2) * mm, "end": v(3.95, 10.25) * mm});
            skLineSegment(sketch, "E2859", {"start": v(3.95, 10.25) * mm, "end": v(3.83, 10.3) * mm});
            skLineSegment(sketch, "E2860", {"start": v(3.83, 10.3) * mm, "end": v(3.72, 10.33) * mm});
            skLineSegment(sketch, "E2861", {"start": v(3.72, 10.33) * mm, "end": v(3.66, 10.35) * mm});
            skLineSegment(sketch, "E2862", {"start": v(3.66, 10.35) * mm, "end": v(3.57, 10.28) * mm});
            skLineSegment(sketch, "E2863", {"start": v(3.57, 10.28) * mm, "end": v(3.5, 10.2) * mm});
            skLineSegment(sketch, "E2864", {"start": v(3.5, 10.2) * mm, "end": v(3.4, 10.12) * mm});
            skLineSegment(sketch, "E2865", {"start": v(3.4, 10.12) * mm, "end": v(3.32, 10.04) * mm});
            skLineSegment(sketch, "E2866", {"start": v(3.32, 10.04) * mm, "end": v(3.24, 9.96) * mm});
            skLineSegment(sketch, "E2867", {"start": v(3.24, 9.96) * mm, "end": v(3.15, 9.87) * mm});
            skLineSegment(sketch, "E2868", {"start": v(3.15, 9.87) * mm, "end": v(3.08, 9.79) * mm});
            skLineSegment(sketch, "E2869", {"start": v(3.08, 9.79) * mm, "end": v(3, 9.7) * mm});
            skLineSegment(sketch, "E2870", {"start": v(3, 9.7) * mm, "end": v(2.94, 9.61) * mm});
            skLineSegment(sketch, "E2871", {"start": v(2.94, 9.61) * mm, "end": v(2.86, 9.52) * mm});
            skLineSegment(sketch, "E2872", {"start": v(2.86, 9.52) * mm, "end": v(2.8, 9.41) * mm});
            skLineSegment(sketch, "E2873", {"start": v(2.8, 9.41) * mm, "end": v(2.73, 9.31) * mm});
            skLineSegment(sketch, "E2874", {"start": v(2.73, 9.31) * mm, "end": v(2.68, 9.21) * mm});
            skLineSegment(sketch, "E2875", {"start": v(2.68, 9.21) * mm, "end": v(2.63, 9.11) * mm});
            skLineSegment(sketch, "E2876", {"start": v(2.63, 9.11) * mm, "end": v(2.59, 9) * mm});
            skLineSegment(sketch, "E2877", {"start": v(2.59, 9) * mm, "end": v(2.55, 8.89) * mm});
            skLineSegment(sketch, "E2878", {"start": v(2.55, 8.89) * mm, "end": v(2.5, 8.79) * mm});
            skLineSegment(sketch, "E2879", {"start": v(2.5, 8.79) * mm, "end": v(2.44, 8.69) * mm});
            skLineSegment(sketch, "E2880", {"start": v(2.44, 8.69) * mm, "end": v(2.36, 8.6) * mm});
            skLineSegment(sketch, "E2881", {"start": v(2.36, 8.6) * mm, "end": v(2.26, 8.56) * mm});
            skLineSegment(sketch, "E2882", {"start": v(2.26, 8.56) * mm, "end": v(2.24, 8.55) * mm});
            skLineSegment(sketch, "E2883", {"start": v(2.24, 8.55) * mm, "end": v(2.13, 8.58) * mm});
            skLineSegment(sketch, "E2884", {"start": v(2.13, 8.58) * mm, "end": v(2.01, 8.6) * mm});
            skLineSegment(sketch, "E2885", {"start": v(2.01, 8.6) * mm, "end": v(1.9, 8.63) * mm});
            skLineSegment(sketch, "E2886", {"start": v(1.9, 8.63) * mm, "end": v(1.78, 8.65) * mm});
            skLineSegment(sketch, "E2887", {"start": v(1.78, 8.65) * mm, "end": v(1.66, 8.68) * mm});
            skLineSegment(sketch, "E2888", {"start": v(1.66, 8.68) * mm, "end": v(1.6, 8.7) * mm});
            skLineSegment(sketch, "E2889", {"start": v(1.6, 8.7) * mm, "end": v(1.53, 8.8) * mm});
            skLineSegment(sketch, "E2890", {"start": v(1.53, 8.8) * mm, "end": v(1.5, 8.91) * mm});
            skLineSegment(sketch, "E2891", {"start": v(1.5, 8.91) * mm, "end": v(1.48, 9.03) * mm});
            skLineSegment(sketch, "E2892", {"start": v(1.48, 9.03) * mm, "end": v(1.5, 9.15) * mm});
            skLineSegment(sketch, "E2893", {"start": v(1.5, 9.15) * mm, "end": v(1.5, 9.27) * mm});
            skLineSegment(sketch, "E2894", {"start": v(1.5, 9.27) * mm, "end": v(1.51, 9.38) * mm});
            skLineSegment(sketch, "E2895", {"start": v(1.51, 9.38) * mm, "end": v(1.51, 9.48) * mm});
            skLineSegment(sketch, "E2896", {"start": v(1.51, 9.48) * mm, "end": v(1.5, 9.6) * mm});
            skLineSegment(sketch, "E2897", {"start": v(1.5, 9.6) * mm, "end": v(1.5, 9.7) * mm});
            skLineSegment(sketch, "E2898", {"start": v(1.5, 9.7) * mm, "end": v(1.48, 9.81) * mm});
            skLineSegment(sketch, "E2899", {"start": v(1.48, 9.81) * mm, "end": v(1.46, 9.92) * mm});
            skLineSegment(sketch, "E2900", {"start": v(1.46, 9.92) * mm, "end": v(1.43, 10.03) * mm});
            skLineSegment(sketch, "E2901", {"start": v(1.43, 10.03) * mm, "end": v(1.4, 10.15) * mm});
            skLineSegment(sketch, "E2902", {"start": v(1.4, 10.15) * mm, "end": v(1.38, 10.25) * mm});
            skLineSegment(sketch, "E2903", {"start": v(1.38, 10.25) * mm, "end": v(1.34, 10.36) * mm});
            skLineSegment(sketch, "E2904", {"start": v(1.34, 10.36) * mm, "end": v(1.3, 10.47) * mm});
            skLineSegment(sketch, "E2905", {"start": v(1.3, 10.47) * mm, "end": v(1.27, 10.57) * mm});
            skLineSegment(sketch, "E2906", {"start": v(1.27, 10.57) * mm, "end": v(1.23, 10.68) * mm});
            skLineSegment(sketch, "E2907", {"start": v(1.23, 10.68) * mm, "end": v(1.19, 10.78) * mm});
            skLineSegment(sketch, "E2908", {"start": v(1.19, 10.78) * mm, "end": v(1.14, 10.88) * mm});
            skLineSegment(sketch, "E2909", {"start": v(1.14, 10.88) * mm, "end": v(1.12, 10.94) * mm});
            skLineSegment(sketch, "E2910", {"start": v(1.12, 10.94) * mm, "end": v(1, 10.95) * mm});
            skLineSegment(sketch, "E2911", {"start": v(1, 10.95) * mm, "end": v(0.88, 10.96) * mm});
            skLineSegment(sketch, "E2912", {"start": v(0.88, 10.96) * mm, "end": v(0.75, 10.97) * mm});
            skLineSegment(sketch, "E2913", {"start": v(0.75, 10.97) * mm, "end": v(0.63, 10.98) * mm});
            skLineSegment(sketch, "E2914", {"start": v(0.63, 10.98) * mm, "end": v(0.5, 10.98) * mm});
            skLineSegment(sketch, "E2915", {"start": v(0.5, 10.98) * mm, "end": v(0.45, 10.99) * mm});
            skLineSegment(sketch, "E2916", {"start": v(0.45, 10.99) * mm, "end": v(0.38, 10.88) * mm});
            skLineSegment(sketch, "E2917", {"start": v(0.38, 10.88) * mm, "end": v(0.33, 10.8) * mm});
            skLineSegment(sketch, "E2918", {"start": v(0.33, 10.8) * mm, "end": v(0.26, 10.69) * mm});
            skLineSegment(sketch, "E2919", {"start": v(0.26, 10.69) * mm, "end": v(0.2, 10.58) * mm});
            skLineSegment(sketch, "E2920", {"start": v(0.2, 10.58) * mm, "end": v(0.16, 10.48) * mm});
            skLineSegment(sketch, "E2921", {"start": v(0.16, 10.48) * mm, "end": v(0.1, 10.38) * mm});
            skLineSegment(sketch, "E2922", {"start": v(0.1, 10.38) * mm, "end": v(0.06, 10.27) * mm});
            skLineSegment(sketch, "E2923", {"start": v(0.06, 10.27) * mm, "end": v(0, 10.16) * mm});
            skLineSegment(sketch, "E2924", {"start": v(0, 10.16) * mm, "end": v(-0.03, 10.06) * mm});
            skLineSegment(sketch, "E2925", {"start": v(-0.03, 10.06) * mm, "end": v(-0.07, 9.95) * mm});
            skLineSegment(sketch, "E2926", {"start": v(-0.07, 9.95) * mm, "end": v(-0.1, 9.83) * mm});
            skLineSegment(sketch, "E2927", {"start": v(-0.1, 9.83) * mm, "end": v(-0.14, 9.71) * mm});
            skLineSegment(sketch, "E2928", {"start": v(-0.14, 9.71) * mm, "end": v(-0.16, 9.6) * mm});
            skLineSegment(sketch, "E2929", {"start": v(-0.16, 9.6) * mm, "end": v(-0.18, 9.5) * mm});
            skLineSegment(sketch, "E2930", {"start": v(-0.18, 9.5) * mm, "end": v(-0.18, 9.37) * mm});
            skLineSegment(sketch, "E2931", {"start": v(-0.18, 9.37) * mm, "end": v(-0.19, 9.25) * mm});
            skLineSegment(sketch, "E2932", {"start": v(-0.19, 9.25) * mm, "end": v(-0.2, 9.15) * mm});
            skLineSegment(sketch, "E2933", {"start": v(-0.2, 9.15) * mm, "end": v(-0.23, 9.03) * mm});
            skLineSegment(sketch, "E2934", {"start": v(-0.23, 9.03) * mm, "end": v(-0.28, 8.93) * mm});
            skLineSegment(sketch, "E2935", {"start": v(-0.28, 8.93) * mm, "end": v(-0.36, 8.85) * mm});
            skLineSegment(sketch, "E2936", {"start": v(-0.36, 8.85) * mm, "end": v(-0.48, 8.84) * mm});
            skLineSegment(sketch, "E2937", {"start": v(-0.48, 8.84) * mm, "end": v(-0.6, 8.83) * mm});
            skLineSegment(sketch, "E2938", {"start": v(-0.6, 8.83) * mm, "end": v(-0.72, 8.82) * mm});
            skLineSegment(sketch, "E2939", {"start": v(-0.72, 8.82) * mm, "end": v(-0.84, 8.8) * mm});
            skLineSegment(sketch, "E2940", {"start": v(-0.84, 8.8) * mm, "end": v(-0.96, 8.8) * mm});
            skLineSegment(sketch, "E2941", {"start": v(-0.96, 8.8) * mm, "end": v(-0.98, 8.8) * mm});
            skLineSegment(sketch, "E2942", {"start": v(-0.98, 8.8) * mm, "end": v(-1.04, 8.8) * mm});
            skLineSegment(sketch, "E2943", {"start": v(-1.04, 8.8) * mm, "end": v(-1.13, 8.87) * mm});
            skLineSegment(sketch, "E2944", {"start": v(-1.13, 8.87) * mm, "end": v(-1.2, 8.97) * mm});
            skLineSegment(sketch, "E2945", {"start": v(-1.2, 8.97) * mm, "end": v(-1.24, 9.08) * mm});
            skLineSegment(sketch, "E2946", {"start": v(-1.24, 9.08) * mm, "end": v(-1.27, 9.2) * mm});
            skLineSegment(sketch, "E2947", {"start": v(-1.27, 9.2) * mm, "end": v(-1.3, 9.3) * mm});
            skLineSegment(sketch, "E2948", {"start": v(-1.3, 9.3) * mm, "end": v(-1.32, 9.42) * mm});
            skLineSegment(sketch, "E2949", {"start": v(-1.32, 9.42) * mm, "end": v(-1.35, 9.52) * mm});
            skLineSegment(sketch, "E2950", {"start": v(-1.35, 9.52) * mm, "end": v(-1.39, 9.62) * mm});
            skLineSegment(sketch, "E2951", {"start": v(-1.39, 9.62) * mm, "end": v(-1.43, 9.72) * mm});
            skLineSegment(sketch, "E2952", {"start": v(-1.43, 9.72) * mm, "end": v(-1.48, 9.82) * mm});
            skLineSegment(sketch, "E2953", {"start": v(-1.48, 9.82) * mm, "end": v(-1.53, 9.92) * mm});
            skLineSegment(sketch, "E2954", {"start": v(-1.53, 9.92) * mm, "end": v(-1.59, 10.02) * mm});
            skLineSegment(sketch, "E2955", {"start": v(-1.59, 10.02) * mm, "end": v(-1.65, 10.12) * mm});
            skLineSegment(sketch, "E2956", {"start": v(-1.65, 10.12) * mm, "end": v(-1.7, 10.21) * mm});
            skLineSegment(sketch, "E2957", {"start": v(-1.7, 10.21) * mm, "end": v(-1.77, 10.3) * mm});
            skLineSegment(sketch, "E2958", {"start": v(-1.77, 10.3) * mm, "end": v(-1.84, 10.4) * mm});
            skLineSegment(sketch, "E2959", {"start": v(-1.84, 10.4) * mm, "end": v(-1.9, 10.48) * mm});
            skLineSegment(sketch, "E2960", {"start": v(-1.9, 10.48) * mm, "end": v(-1.97, 10.57) * mm});
            skLineSegment(sketch, "E2961", {"start": v(-1.97, 10.57) * mm, "end": v(-2.04, 10.66) * mm});
            skLineSegment(sketch, "E2962", {"start": v(-2.04, 10.66) * mm, "end": v(-2.12, 10.75) * mm});
            skLineSegment(sketch, "E2963", {"start": v(-2.12, 10.75) * mm, "end": v(-2.16, 10.79) * mm});
            skLineSegment(sketch, "E2964", {"start": v(-2.16, 10.79) * mm, "end": v(-2.28, 10.77) * mm});
            skLineSegment(sketch, "E2965", {"start": v(-2.28, 10.77) * mm, "end": v(-2.4, 10.74) * mm});
            skLineSegment(sketch, "E2966", {"start": v(-2.4, 10.74) * mm, "end": v(-2.52, 10.71) * mm});
            skLineSegment(sketch, "E2967", {"start": v(-2.52, 10.71) * mm, "end": v(-2.64, 10.68) * mm});
            skLineSegment(sketch, "E2968", {"start": v(-2.64, 10.68) * mm, "end": v(-2.75, 10.66) * mm});
            skLineSegment(sketch, "E2969", {"start": v(-2.75, 10.66) * mm, "end": v(-2.81, 10.64) * mm});
            skLineSegment(sketch, "E2970", {"start": v(-2.81, 10.64) * mm, "end": v(-2.84, 10.53) * mm});
            skLineSegment(sketch, "E2971", {"start": v(-2.84, 10.53) * mm, "end": v(-2.87, 10.42) * mm});
            skLineSegment(sketch, "E2972", {"start": v(-2.87, 10.42) * mm, "end": v(-2.9, 10.3) * mm});
            skLineSegment(sketch, "E2973", {"start": v(-2.9, 10.3) * mm, "end": v(-2.92, 10.18) * mm});
            skLineSegment(sketch, "E2974", {"start": v(-2.92, 10.18) * mm, "end": v(-2.94, 10.07) * mm});
            skLineSegment(sketch, "E2975", {"start": v(-2.94, 10.07) * mm, "end": v(-2.96, 9.96) * mm});
            skLineSegment(sketch, "E2976", {"start": v(-2.96, 9.96) * mm, "end": v(-2.98, 9.84) * mm});
            skLineSegment(sketch, "E2977", {"start": v(-2.98, 9.84) * mm, "end": v(-2.99, 9.73) * mm});
            skLineSegment(sketch, "E2978", {"start": v(-2.99, 9.73) * mm, "end": v(-3, 9.62) * mm});
            skLineSegment(sketch, "E2979", {"start": v(-3, 9.62) * mm, "end": v(-3, 9.5) * mm});
            skLineSegment(sketch, "E2980", {"start": v(-3, 9.5) * mm, "end": v(-3, 9.37) * mm});
            skLineSegment(sketch, "E2981", {"start": v(-3, 9.37) * mm, "end": v(-3, 9.25) * mm});
            skLineSegment(sketch, "E2982", {"start": v(-3, 9.25) * mm, "end": v(-2.99, 9.14) * mm});
            skLineSegment(sketch, "E2983", {"start": v(-2.99, 9.14) * mm, "end": v(-2.97, 9.03) * mm});
            skLineSegment(sketch, "E2984", {"start": v(-2.97, 9.03) * mm, "end": v(-2.94, 8.92) * mm});
            skLineSegment(sketch, "E2985", {"start": v(-2.94, 8.92) * mm, "end": v(-2.9, 8.8) * mm});
            skLineSegment(sketch, "E2986", {"start": v(-2.9, 8.8) * mm, "end": v(-2.9, 8.7) * mm});
            skLineSegment(sketch, "E2987", {"start": v(-2.9, 8.7) * mm, "end": v(-2.89, 8.58) * mm});
            skLineSegment(sketch, "E2988", {"start": v(-2.89, 8.58) * mm, "end": v(-2.9, 8.46) * mm});
            skLineSegment(sketch, "E2989", {"start": v(-2.9, 8.46) * mm, "end": v(-2.96, 8.37) * mm});
            skLineSegment(sketch, "E2990", {"start": v(-2.96, 8.37) * mm, "end": v(-3.07, 8.32) * mm});
            skLineSegment(sketch, "E2991", {"start": v(-3.07, 8.32) * mm, "end": v(-3.18, 8.27) * mm});
            skLineSegment(sketch, "E2992", {"start": v(-3.18, 8.27) * mm, "end": v(-3.29, 8.23) * mm});
            skLineSegment(sketch, "E2993", {"start": v(-3.29, 8.23) * mm, "end": v(-3.4, 8.18) * mm});
            skLineSegment(sketch, "E2994", {"start": v(-3.4, 8.18) * mm, "end": v(-3.5, 8.14) * mm});
            skLineSegment(sketch, "E2995", {"start": v(-3.5, 8.14) * mm, "end": v(-3.57, 8.12) * mm});
            skLineSegment(sketch, "E2996", {"start": v(-3.57, 8.12) * mm, "end": v(-3.68, 8.15) * mm});
            skLineSegment(sketch, "E2997", {"start": v(-3.68, 8.15) * mm, "end": v(-3.77, 8.21) * mm});
            skLineSegment(sketch, "E2998", {"start": v(-3.77, 8.21) * mm, "end": v(-3.85, 8.3) * mm});
            skLineSegment(sketch, "E2999", {"start": v(-3.85, 8.3) * mm, "end": v(-3.9, 8.4) * mm});
            skLineSegment(sketch, "E3000", {"start": v(-3.9, 8.4) * mm, "end": v(-3.97, 8.5) * mm});
            skLineSegment(sketch, "E3001", {"start": v(-3.97, 8.5) * mm, "end": v(-4.02, 8.6) * mm});
            skLineSegment(sketch, "E3002", {"start": v(-4.02, 8.6) * mm, "end": v(-4.08, 8.68) * mm});
            skLineSegment(sketch, "E3003", {"start": v(-4.08, 8.68) * mm, "end": v(-4.15, 8.77) * mm});
            skLineSegment(sketch, "E3004", {"start": v(-4.15, 8.77) * mm, "end": v(-4.22, 8.86) * mm});
            skLineSegment(sketch, "E3005", {"start": v(-4.22, 8.86) * mm, "end": v(-4.3, 8.94) * mm});
            skLineSegment(sketch, "E3006", {"start": v(-4.3, 8.94) * mm, "end": v(-4.37, 9.02) * mm});
            skLineSegment(sketch, "E3007", {"start": v(-4.37, 9.02) * mm, "end": v(-4.45, 9.1) * mm});
            skLineSegment(sketch, "E3008", {"start": v(-4.45, 9.1) * mm, "end": v(-4.53, 9.17) * mm});
            skLineSegment(sketch, "E3009", {"start": v(-4.53, 9.17) * mm, "end": v(-4.61, 9.24) * mm});
            skLineSegment(sketch, "E3010", {"start": v(-4.61, 9.24) * mm, "end": v(-4.7, 9.31) * mm});
            skLineSegment(sketch, "E3011", {"start": v(-4.7, 9.31) * mm, "end": v(-4.79, 9.38) * mm});
            skLineSegment(sketch, "E3012", {"start": v(-4.79, 9.38) * mm, "end": v(-4.88, 9.45) * mm});
            skLineSegment(sketch, "E3013", {"start": v(-4.88, 9.45) * mm, "end": v(-4.98, 9.51) * mm});
            skLineSegment(sketch, "E3014", {"start": v(-4.98, 9.51) * mm, "end": v(-5.07, 9.57) * mm});
            skLineSegment(sketch, "E3015", {"start": v(-5.07, 9.57) * mm, "end": v(-5.16, 9.64) * mm});
            skLineSegment(sketch, "E3016", {"start": v(-5.16, 9.64) * mm, "end": v(-5.24, 9.69) * mm});
            skLineSegment(sketch, "E3017", {"start": v(-5.24, 9.69) * mm, "end": v(-5.35, 9.63) * mm});
            skLineSegment(sketch, "E3018", {"start": v(-5.35, 9.63) * mm, "end": v(-5.45, 9.57) * mm});
            skLineSegment(sketch, "E3019", {"start": v(-5.45, 9.57) * mm, "end": v(-5.57, 9.5) * mm});
            skLineSegment(sketch, "E3020", {"start": v(-5.57, 9.5) * mm, "end": v(-5.67, 9.44) * mm});
            skLineSegment(sketch, "E3021", {"start": v(-5.67, 9.44) * mm, "end": v(-5.77, 9.38) * mm});
            skLineSegment(sketch, "E3022", {"start": v(-5.77, 9.38) * mm, "end": v(-5.82, 9.35) * mm});
            skLineSegment(sketch, "E3023", {"start": v(-5.82, 9.35) * mm, "end": v(-5.82, 9.23) * mm});
            skLineSegment(sketch, "E3024", {"start": v(-5.82, 9.23) * mm, "end": v(-5.82, 9.12) * mm});
            skLineSegment(sketch, "E3025", {"start": v(-5.82, 9.12) * mm, "end": v(-5.8, 9) * mm});
            skLineSegment(sketch, "E3026", {"start": v(-5.8, 9) * mm, "end": v(-5.8, 8.88) * mm});
            skLineSegment(sketch, "E3027", {"start": v(-5.8, 8.88) * mm, "end": v(-5.78, 8.77) * mm});
            skLineSegment(sketch, "E3028", {"start": v(-5.78, 8.77) * mm, "end": v(-5.77, 8.65) * mm});
            skLineSegment(sketch, "E3029", {"start": v(-5.77, 8.65) * mm, "end": v(-5.75, 8.54) * mm});
            skLineSegment(sketch, "E3030", {"start": v(-5.75, 8.54) * mm, "end": v(-5.73, 8.43) * mm});
            skLineSegment(sketch, "E3031", {"start": v(-5.73, 8.43) * mm, "end": v(-5.7, 8.32) * mm});
            skLineSegment(sketch, "E3032", {"start": v(-5.7, 8.32) * mm, "end": v(-5.67, 8.2) * mm});
            skLineSegment(sketch, "E3033", {"start": v(-5.67, 8.2) * mm, "end": v(-5.63, 8.09) * mm});
            skLineSegment(sketch, "E3034", {"start": v(-5.63, 8.09) * mm, "end": v(-5.6, 7.97) * mm});
            skLineSegment(sketch, "E3035", {"start": v(-5.6, 7.97) * mm, "end": v(-5.55, 7.87) * mm});
            skLineSegment(sketch, "E3036", {"start": v(-5.55, 7.87) * mm, "end": v(-5.5, 7.77) * mm});
            skLineSegment(sketch, "E3037", {"start": v(-5.5, 7.77) * mm, "end": v(-5.44, 7.67) * mm});
            skLineSegment(sketch, "E3038", {"start": v(-5.44, 7.67) * mm, "end": v(-5.38, 7.56) * mm});
            skLineSegment(sketch, "E3039", {"start": v(-5.38, 7.56) * mm, "end": v(-5.33, 7.47) * mm});
            skLineSegment(sketch, "E3040", {"start": v(-5.33, 7.47) * mm, "end": v(-5.29, 7.36) * mm});
            skLineSegment(sketch, "E3041", {"start": v(-5.29, 7.36) * mm, "end": v(-5.27, 7.24) * mm});
            skLineSegment(sketch, "E3042", {"start": v(-5.27, 7.24) * mm, "end": v(-5.3, 7.14) * mm});
            skLineSegment(sketch, "E3043", {"start": v(-5.3, 7.14) * mm, "end": v(-5.38, 7.06) * mm});
            skLineSegment(sketch, "E3044", {"start": v(-5.38, 7.06) * mm, "end": v(-5.48, 6.98) * mm});
            skLineSegment(sketch, "E3045", {"start": v(-5.48, 6.98) * mm, "end": v(-5.57, 6.9) * mm});
            skLineSegment(sketch, "E3046", {"start": v(-5.57, 6.9) * mm, "end": v(-5.66, 6.83) * mm});
            skLineSegment(sketch, "E3047", {"start": v(-5.66, 6.83) * mm, "end": v(-5.75, 6.75) * mm});
            skLineSegment(sketch, "E3048", {"start": v(-5.75, 6.75) * mm, "end": v(-5.8, 6.72) * mm});
            skLineSegment(sketch, "E3049", {"start": v(-5.8, 6.72) * mm, "end": v(-5.87, 6.7) * mm});
            skLineSegment(sketch, "E3050", {"start": v(-5.87, 6.7) * mm, "end": v(-5.98, 6.73) * mm});
            skLineSegment(sketch, "E3051", {"start": v(-5.98, 6.73) * mm, "end": v(-6.08, 6.77) * mm});
            skLineSegment(sketch, "E3052", {"start": v(-6.08, 6.77) * mm, "end": v(-6.17, 6.84) * mm});
            skLineSegment(sketch, "E3053", {"start": v(-6.17, 6.84) * mm, "end": v(-6.26, 6.92) * mm});
            skLineSegment(sketch, "E3054", {"start": v(-6.26, 6.92) * mm, "end": v(-6.35, 7.01) * mm});
            skLineSegment(sketch, "E3055", {"start": v(-6.35, 7.01) * mm, "end": v(-6.43, 7.08) * mm});
            skLineSegment(sketch, "E3056", {"start": v(-6.43, 7.08) * mm, "end": v(-6.52, 7.15) * mm});
            skLineSegment(sketch, "E3057", {"start": v(-6.52, 7.15) * mm, "end": v(-6.61, 7.21) * mm});
            skLineSegment(sketch, "E3058", {"start": v(-6.61, 7.21) * mm, "end": v(-6.7, 7.27) * mm});
            skLineSegment(sketch, "E3059", {"start": v(-6.7, 7.27) * mm, "end": v(-6.8, 7.33) * mm});
            skLineSegment(sketch, "E3060", {"start": v(-6.8, 7.33) * mm, "end": v(-6.9, 7.38) * mm});
            skLineSegment(sketch, "E3061", {"start": v(-6.9, 7.38) * mm, "end": v(-7, 7.42) * mm});
            skLineSegment(sketch, "E3062", {"start": v(-7, 7.42) * mm, "end": v(-7.1, 7.47) * mm});
            skLineSegment(sketch, "E3063", {"start": v(-7.1, 7.47) * mm, "end": v(-7.2, 7.51) * mm});
            skLineSegment(sketch, "E3064", {"start": v(-7.2, 7.51) * mm, "end": v(-7.3, 7.55) * mm});
            skLineSegment(sketch, "E3065", {"start": v(-7.3, 7.55) * mm, "end": v(-7.41, 7.59) * mm});
            skLineSegment(sketch, "E3066", {"start": v(-7.41, 7.59) * mm, "end": v(-7.52, 7.62) * mm});
            skLineSegment(sketch, "E3067", {"start": v(-7.52, 7.62) * mm, "end": v(-7.63, 7.66) * mm});
            skLineSegment(sketch, "E3068", {"start": v(-7.63, 7.66) * mm, "end": v(-7.74, 7.69) * mm});
            skLineSegment(sketch, "E3069", {"start": v(-7.74, 7.69) * mm, "end": v(-7.85, 7.72) * mm});
            skLineSegment(sketch, "E3070", {"start": v(-7.85, 7.72) * mm, "end": v(-7.87, 7.72) * mm});
            skLineSegment(sketch, "E3071", {"start": v(-7.87, 7.72) * mm, "end": v(-7.95, 7.64) * mm});
            skLineSegment(sketch, "E3072", {"start": v(-7.95, 7.64) * mm, "end": v(-8.03, 7.55) * mm});
            skLineSegment(sketch, "E3073", {"start": v(-8.03, 7.55) * mm, "end": v(-8.12, 7.45) * mm});
            skLineSegment(sketch, "E3074", {"start": v(-8.12, 7.45) * mm, "end": v(-8.2, 7.36) * mm});
            skLineSegment(sketch, "E3075", {"start": v(-8.2, 7.36) * mm, "end": v(-8.28, 7.28) * mm});
            skLineSegment(sketch, "E3076", {"start": v(-8.28, 7.28) * mm, "end": v(-8.32, 7.23) * mm});
            skLineSegment(sketch, "E3077", {"start": v(-8.32, 7.23) * mm, "end": v(-8.29, 7.12) * mm});
            skLineSegment(sketch, "E3078", {"start": v(-8.29, 7.12) * mm, "end": v(-8.25, 7.01) * mm});
            skLineSegment(sketch, "E3079", {"start": v(-8.25, 7.01) * mm, "end": v(-8.2, 6.9) * mm});
            skLineSegment(sketch, "E3080", {"start": v(-8.2, 6.9) * mm, "end": v(-8.16, 6.8) * mm});
            skLineSegment(sketch, "E3081", {"start": v(-8.16, 6.8) * mm, "end": v(-8.11, 6.69) * mm});
            skLineSegment(sketch, "E3082", {"start": v(-8.11, 6.69) * mm, "end": v(-8.06, 6.58) * mm});
            skLineSegment(sketch, "E3083", {"start": v(-8.06, 6.58) * mm, "end": v(-8.01, 6.48) * mm});
            skLineSegment(sketch, "E3084", {"start": v(-8.01, 6.48) * mm, "end": v(-7.96, 6.38) * mm});
            skLineSegment(sketch, "E3085", {"start": v(-7.96, 6.38) * mm, "end": v(-7.9, 6.28) * mm});
            skLineSegment(sketch, "E3086", {"start": v(-7.9, 6.28) * mm, "end": v(-7.84, 6.18) * mm});
            skLineSegment(sketch, "E3087", {"start": v(-7.84, 6.18) * mm, "end": v(-7.77, 6.08) * mm});
            skLineSegment(sketch, "E3088", {"start": v(-7.77, 6.08) * mm, "end": v(-7.7, 5.98) * mm});
            skLineSegment(sketch, "E3089", {"start": v(-7.7, 5.98) * mm, "end": v(-7.62, 5.9) * mm});
            skLineSegment(sketch, "E3090", {"start": v(-7.62, 5.9) * mm, "end": v(-7.55, 5.81) * mm});
            skLineSegment(sketch, "E3091", {"start": v(-7.55, 5.81) * mm, "end": v(-7.46, 5.73) * mm});
            skLineSegment(sketch, "E3092", {"start": v(-7.46, 5.73) * mm, "end": v(-7.37, 5.65) * mm});
            skLineSegment(sketch, "E3093", {"start": v(-7.37, 5.65) * mm, "end": v(-7.3, 5.58) * mm});
            skLineSegment(sketch, "E3094", {"start": v(-7.3, 5.58) * mm, "end": v(-7.22, 5.48) * mm});
            skLineSegment(sketch, "E3095", {"start": v(-7.22, 5.48) * mm, "end": v(-7.17, 5.38) * mm});
            skLineSegment(sketch, "E3096", {"start": v(-7.17, 5.38) * mm, "end": v(-7.16, 5.27) * mm});
            skLineSegment(sketch, "E3097", {"start": v(-7.16, 5.27) * mm, "end": v(-7.23, 5.17) * mm});
            skLineSegment(sketch, "E3098", {"start": v(-7.23, 5.17) * mm, "end": v(-7.3, 5.07) * mm});
            skLineSegment(sketch, "E3099", {"start": v(-7.3, 5.07) * mm, "end": v(-7.36, 4.97) * mm});
            skLineSegment(sketch, "E3100", {"start": v(-7.36, 4.97) * mm, "end": v(-7.42, 4.87) * mm});
            skLineSegment(sketch, "E3101", {"start": v(-7.42, 4.87) * mm, "end": v(-7.49, 4.77) * mm});
            skLineSegment(sketch, "E3102", {"start": v(-7.49, 4.77) * mm, "end": v(-7.53, 4.72) * mm});
            skLineSegment(sketch, "E3103", {"start": v(-7.53, 4.72) * mm, "end": v(-7.64, 4.68) * mm});
            skLineSegment(sketch, "E3104", {"start": v(-7.64, 4.68) * mm, "end": v(-7.68, 4.68) * mm});
            skLineSegment(sketch, "E3105", {"start": v(-7.68, 4.68) * mm, "end": v(-7.8, 4.69) * mm});
            skLineSegment(sketch, "E3106", {"start": v(-7.8, 4.69) * mm, "end": v(-7.9, 4.72) * mm});
            skLineSegment(sketch, "E3107", {"start": v(-7.9, 4.72) * mm, "end": v(-8, 4.77) * mm});
            skLineSegment(sketch, "E3108", {"start": v(-8, 4.77) * mm, "end": v(-8.12, 4.83) * mm});
            skLineSegment(sketch, "E3109", {"start": v(-8.12, 4.83) * mm, "end": v(-8.21, 4.88) * mm});
            skLineSegment(sketch, "E3110", {"start": v(-8.21, 4.88) * mm, "end": v(-8.32, 4.91) * mm});
            skLineSegment(sketch, "E3111", {"start": v(-8.32, 4.91) * mm, "end": v(-8.42, 4.95) * mm});
            skLineSegment(sketch, "E3112", {"start": v(-8.42, 4.95) * mm, "end": v(-8.52, 4.98) * mm});
            skLineSegment(sketch, "E3113", {"start": v(-8.52, 4.98) * mm, "end": v(-8.63, 5) * mm});
            skLineSegment(sketch, "E3114", {"start": v(-8.63, 5) * mm, "end": v(-8.74, 5.02) * mm});
            skLineSegment(sketch, "E3115", {"start": v(-8.74, 5.02) * mm, "end": v(-8.85, 5.04) * mm});
            skLineSegment(sketch, "E3116", {"start": v(-8.85, 5.04) * mm, "end": v(-8.95, 5.05) * mm});
            skLineSegment(sketch, "E3117", {"start": v(-8.95, 5.05) * mm, "end": v(-9.06, 5.06) * mm});
            skLineSegment(sketch, "E3118", {"start": v(-9.06, 5.06) * mm, "end": v(-9.18, 5.07) * mm});
            skLineSegment(sketch, "E3119", {"start": v(-9.18, 5.07) * mm, "end": v(-9.29, 5.08) * mm});
            skLineSegment(sketch, "E3120", {"start": v(-9.29, 5.08) * mm, "end": v(-9.4, 5.08) * mm});
            skLineSegment(sketch, "E3121", {"start": v(-9.4, 5.08) * mm, "end": v(-9.48, 5.08) * mm});
            skLineSegment(sketch, "E3122", {"start": v(-9.48, 5.08) * mm, "end": v(-9.59, 5.08) * mm});
            skLineSegment(sketch, "E3123", {"start": v(-9.59, 5.08) * mm, "end": v(-9.7, 5.08) * mm});
            skLineSegment(sketch, "E3124", {"start": v(-9.7, 5.08) * mm, "end": v(-9.8, 5.07) * mm});
            skLineSegment(sketch, "E3125", {"start": v(-9.8, 5.07) * mm, "end": v(-9.85, 4.96) * mm});
            skLineSegment(sketch, "E3126", {"start": v(-9.85, 4.96) * mm, "end": v(-9.9, 4.86) * mm});
            skLineSegment(sketch, "E3127", {"start": v(-9.9, 4.86) * mm, "end": v(-9.96, 4.74) * mm});
            skLineSegment(sketch, "E3128", {"start": v(-9.96, 4.74) * mm, "end": v(-10.01, 4.63) * mm});
            skLineSegment(sketch, "E3129", {"start": v(-10.01, 4.63) * mm, "end": v(-10.06, 4.52) * mm});
            skLineSegment(sketch, "E3130", {"start": v(-10.06, 4.52) * mm, "end": v(-10.09, 4.47) * mm});
            skLineSegment(sketch, "E3131", {"start": v(-10.09, 4.47) * mm, "end": v(-10.02, 4.37) * mm});
            skLineSegment(sketch, "E3132", {"start": v(-10.02, 4.37) * mm, "end": v(-9.95, 4.28) * mm});
            skLineSegment(sketch, "E3133", {"start": v(-9.95, 4.28) * mm, "end": v(-9.88, 4.19) * mm});
            skLineSegment(sketch, "E3134", {"start": v(-9.88, 4.19) * mm, "end": v(-9.8, 4.1) * mm});
            skLineSegment(sketch, "E3135", {"start": v(-9.8, 4.1) * mm, "end": v(-9.73, 4.01) * mm});
            skLineSegment(sketch, "E3136", {"start": v(-9.73, 4.01) * mm, "end": v(-9.65, 3.92) * mm});
            skLineSegment(sketch, "E3137", {"start": v(-9.65, 3.92) * mm, "end": v(-9.57, 3.84) * mm});
            skLineSegment(sketch, "E3138", {"start": v(-9.57, 3.84) * mm, "end": v(-9.48, 3.76) * mm});
            skLineSegment(sketch, "E3139", {"start": v(-9.48, 3.76) * mm, "end": v(-9.4, 3.68) * mm});
            skLineSegment(sketch, "E3140", {"start": v(-9.4, 3.68) * mm, "end": v(-9.31, 3.6) * mm});
            skLineSegment(sketch, "E3141", {"start": v(-9.31, 3.6) * mm, "end": v(-9.22, 3.53) * mm});
            skLineSegment(sketch, "E3142", {"start": v(-9.22, 3.53) * mm, "end": v(-9.12, 3.46) * mm});
            skLineSegment(sketch, "E3143", {"start": v(-9.12, 3.46) * mm, "end": v(-9.02, 3.4) * mm});
            skLineSegment(sketch, "E3144", {"start": v(-9.02, 3.4) * mm, "end": v(-8.93, 3.34) * mm});
            skLineSegment(sketch, "E3145", {"start": v(-8.93, 3.34) * mm, "end": v(-8.82, 3.3) * mm});
            skLineSegment(sketch, "E3146", {"start": v(-8.82, 3.3) * mm, "end": v(-8.7, 3.24) * mm});
            skLineSegment(sketch, "E3147", {"start": v(-8.7, 3.24) * mm, "end": v(-8.61, 3.19) * mm});
            skLineSegment(sketch, "E3148", {"start": v(-8.61, 3.19) * mm, "end": v(-8.52, 3.12) * mm});
            skLineSegment(sketch, "E3149", {"start": v(-8.52, 3.12) * mm, "end": v(-8.44, 3.03) * mm});
            skLineSegment(sketch, "E3150", {"start": v(-8.44, 3.03) * mm, "end": v(-8.4, 2.94) * mm});
            skLineSegment(sketch, "E3151", {"start": v(-8.4, 2.94) * mm, "end": v(-8.43, 2.82) * mm});
            skLineSegment(sketch, "E3152", {"start": v(-8.43, 2.82) * mm, "end": v(-8.46, 2.7) * mm});
            skLineSegment(sketch, "E3153", {"start": v(-8.46, 2.7) * mm, "end": v(-8.5, 2.59) * mm});
            skLineSegment(sketch, "E3154", {"start": v(-8.5, 2.59) * mm, "end": v(-8.53, 2.47) * mm});
            skLineSegment(sketch, "E3155", {"start": v(-8.53, 2.47) * mm, "end": v(-8.56, 2.36) * mm});
            skLineSegment(sketch, "E3156", {"start": v(-8.56, 2.36) * mm, "end": v(-8.59, 2.3) * mm});
            skLineSegment(sketch, "E3157", {"start": v(-8.59, 2.3) * mm, "end": v(-8.68, 2.23) * mm});
            skLineSegment(sketch, "E3158", {"start": v(-8.68, 2.23) * mm, "end": v(-8.79, 2.2) * mm});
            skLineSegment(sketch, "E3159", {"start": v(-8.79, 2.2) * mm, "end": v(-8.9, 2.2) * mm});
            skLineSegment(sketch, "E3160", {"start": v(-8.9, 2.2) * mm, "end": v(-9.01, 2.2) * mm});
            skLineSegment(sketch, "E3161", {"start": v(-9.01, 2.2) * mm, "end": v(-9.13, 2.23) * mm});
            skLineSegment(sketch, "E3162", {"start": v(-9.13, 2.23) * mm, "end": v(-9.24, 2.24) * mm});
            skLineSegment(sketch, "E3163", {"start": v(-9.24, 2.24) * mm, "end": v(-9.35, 2.25) * mm});
            skLineSegment(sketch, "E3164", {"start": v(-9.35, 2.25) * mm, "end": v(-9.46, 2.26) * mm});
            skLineSegment(sketch, "E3165", {"start": v(-9.46, 2.26) * mm, "end": v(-9.47, 2.26) * mm});
            skLineSegment(sketch, "E3166", {"start": v(-9.47, 2.26) * mm, "end": v(-9.58, 2.26) * mm});
            skLineSegment(sketch, "E3167", {"start": v(-9.58, 2.26) * mm, "end": v(-9.7, 2.25) * mm});
            skLineSegment(sketch, "E3168", {"start": v(-9.7, 2.25) * mm, "end": v(-9.8, 2.24) * mm});
            skLineSegment(sketch, "E3169", {"start": v(-9.8, 2.24) * mm, "end": v(-9.92, 2.22) * mm});
            skLineSegment(sketch, "E3170", {"start": v(-9.92, 2.22) * mm, "end": v(-10.03, 2.2) * mm});
            skLineSegment(sketch, "E3171", {"start": v(-10.03, 2.2) * mm, "end": v(-10.14, 2.18) * mm});
            skLineSegment(sketch, "E3172", {"start": v(-10.14, 2.18) * mm, "end": v(-10.25, 2.16) * mm});
            skLineSegment(sketch, "E3173", {"start": v(-10.25, 2.16) * mm, "end": v(-10.36, 2.13) * mm});
            skLineSegment(sketch, "E3174", {"start": v(-10.36, 2.13) * mm, "end": v(-10.46, 2.1) * mm});
            skLineSegment(sketch, "E3175", {"start": v(-10.46, 2.1) * mm, "end": v(-10.57, 2.07) * mm});
            skLineSegment(sketch, "E3176", {"start": v(-10.57, 2.07) * mm, "end": v(-10.68, 2.03) * mm});
            skLineSegment(sketch, "E3177", {"start": v(-10.68, 2.03) * mm, "end": v(-10.78, 2) * mm});
            skLineSegment(sketch, "E3178", {"start": v(-10.78, 2) * mm, "end": v(-10.86, 1.97) * mm});
            skLineSegment(sketch, "E3179", {"start": v(-10.86, 1.97) * mm, "end": v(-10.88, 1.85) * mm});
            skLineSegment(sketch, "E3180", {"start": v(-10.88, 1.85) * mm, "end": v(-10.9, 1.73) * mm});
            skLineSegment(sketch, "E3181", {"start": v(-10.9, 1.73) * mm, "end": v(-10.92, 1.6) * mm});
            skLineSegment(sketch, "E3182", {"start": v(-10.92, 1.6) * mm, "end": v(-10.93, 1.49) * mm});
            skLineSegment(sketch, "E3183", {"start": v(-10.93, 1.49) * mm, "end": v(-10.95, 1.37) * mm});
            skLineSegment(sketch, "E3184", {"start": v(-10.95, 1.37) * mm, "end": v(-10.96, 1.3) * mm});
            skLineSegment(sketch, "E3185", {"start": v(-10.96, 1.3) * mm, "end": v(-10.86, 1.23) * mm});
            skLineSegment(sketch, "E3186", {"start": v(-10.86, 1.23) * mm, "end": v(-10.77, 1.17) * mm});
            skLineSegment(sketch, "E3187", {"start": v(-10.77, 1.17) * mm, "end": v(-10.67, 1.1) * mm});
            skLineSegment(sketch, "E3188", {"start": v(-10.67, 1.1) * mm, "end": v(-10.57, 1.04) * mm});
            skLineSegment(sketch, "E3189", {"start": v(-10.57, 1.04) * mm, "end": v(-10.48, 0.98) * mm});
            skLineSegment(sketch, "E3190", {"start": v(-10.48, 0.98) * mm, "end": v(-10.37, 0.92) * mm});
            skLineSegment(sketch, "E3191", {"start": v(-10.37, 0.92) * mm, "end": v(-10.28, 0.86) * mm});
            skLineSegment(sketch, "E3192", {"start": v(-10.28, 0.86) * mm, "end": v(-10.17, 0.8) * mm});
            skLineSegment(sketch, "E3193", {"start": v(-10.17, 0.8) * mm, "end": v(-10.07, 0.76) * mm});
            skLineSegment(sketch, "E3194", {"start": v(-10.07, 0.76) * mm, "end": v(-9.96, 0.71) * mm});
            skLineSegment(sketch, "E3195", {"start": v(-9.96, 0.71) * mm, "end": v(-9.85, 0.67) * mm});
            skLineSegment(sketch, "E3196", {"start": v(-9.85, 0.67) * mm, "end": v(-9.73, 0.63) * mm});
            skLineSegment(sketch, "E3197", {"start": v(-9.73, 0.63) * mm, "end": v(-9.63, 0.6) * mm});
            skLineSegment(sketch, "E3198", {"start": v(-9.63, 0.6) * mm, "end": v(-9.52, 0.57) * mm});
            skLineSegment(sketch, "E3199", {"start": v(-9.52, 0.57) * mm, "end": v(-9.4, 0.56) * mm});
            skLineSegment(sketch, "E3200", {"start": v(-9.4, 0.56) * mm, "end": v(-9.28, 0.54) * mm});
            skLineSegment(sketch, "E3201", {"start": v(-9.28, 0.54) * mm, "end": v(-9.17, 0.52) * mm});
            skLineSegment(sketch, "E3202", {"start": v(-9.17, 0.52) * mm, "end": v(-9.06, 0.48) * mm});
            skLineSegment(sketch, "E3203", {"start": v(-9.06, 0.48) * mm, "end": v(-8.96, 0.42) * mm});
            skLineSegment(sketch, "E3204", {"start": v(-8.96, 0.42) * mm, "end": v(-8.9, 0.34) * mm});
            skLineSegment(sketch, "E3205", {"start": v(-8.9, 0.34) * mm, "end": v(-8.9, 0.22) * mm});
            skLineSegment(sketch, "E3206", {"start": v(-8.9, 0.22) * mm, "end": v(-8.89, 0.1) * mm});
            skLineSegment(sketch, "E3207", {"start": v(-8.89, 0.1) * mm, "end": v(-8.88, -0.02) * mm});
            skLineSegment(sketch, "E3208", {"start": v(-8.88, -0.02) * mm, "end": v(-8.88, -0.14) * mm});
            skLineSegment(sketch, "E3209", {"start": v(-8.88, -0.14) * mm, "end": v(-8.88, -0.26) * mm});
            skLineSegment(sketch, "E3210", {"start": v(-8.88, -0.26) * mm, "end": v(-8.89, -0.32) * mm});
            skLineSegment(sketch, "E3211", {"start": v(-8.89, -0.32) * mm, "end": v(-8.95, -0.42) * mm});
            skLineSegment(sketch, "E3212", {"start": v(-8.95, -0.42) * mm, "end": v(-9.05, -0.47) * mm});
            skLineSegment(sketch, "E3213", {"start": v(-9.05, -0.47) * mm, "end": v(-9.15, -0.51) * mm});
            skLineSegment(sketch, "E3214", {"start": v(-9.15, -0.51) * mm, "end": v(-9.27, -0.53) * mm});
            skLineSegment(sketch, "E3215", {"start": v(-9.27, -0.53) * mm, "end": v(-9.38, -0.55) * mm});
            skLineSegment(sketch, "E3216", {"start": v(-9.38, -0.55) * mm, "end": v(-9.5, -0.57) * mm});
            skLineSegment(sketch, "E3217", {"start": v(-9.5, -0.57) * mm, "end": v(-9.6, -0.6) * mm});
            skLineSegment(sketch, "E3218", {"start": v(-9.6, -0.6) * mm, "end": v(-9.7, -0.62) * mm});
            skLineSegment(sketch, "E3219", {"start": v(-9.7, -0.62) * mm, "end": v(-9.81, -0.65) * mm});
            skLineSegment(sketch, "E3220", {"start": v(-9.81, -0.65) * mm, "end": v(-9.91, -0.7) * mm});
            skLineSegment(sketch, "E3221", {"start": v(-9.91, -0.7) * mm, "end": v(-10.02, -0.73) * mm});
            skLineSegment(sketch, "E3222", {"start": v(-10.02, -0.73) * mm, "end": v(-10.11, -0.78) * mm});
            skLineSegment(sketch, "E3223", {"start": v(-10.11, -0.78) * mm, "end": v(-10.21, -0.83) * mm});
            skLineSegment(sketch, "E3224", {"start": v(-10.21, -0.83) * mm, "end": v(-10.31, -0.88) * mm});
            skLineSegment(sketch, "E3225", {"start": v(-10.31, -0.88) * mm, "end": v(-10.41, -0.94) * mm});
            skLineSegment(sketch, "E3226", {"start": v(-10.41, -0.94) * mm, "end": v(-10.5, -1) * mm});
            skLineSegment(sketch, "E3227", {"start": v(-10.5, -1) * mm, "end": v(-10.6, -1.06) * mm});
            skLineSegment(sketch, "E3228", {"start": v(-10.6, -1.06) * mm, "end": v(-10.7, -1.12) * mm});
            skLineSegment(sketch, "E3229", {"start": v(-10.7, -1.12) * mm, "end": v(-10.79, -1.18) * mm});
            skLineSegment(sketch, "E3230", {"start": v(-10.79, -1.18) * mm, "end": v(-10.88, -1.25) * mm});
            skLineSegment(sketch, "E3231", {"start": v(-10.88, -1.25) * mm, "end": v(-10.96, -1.3) * mm});
            skLineSegment(sketch, "E3232", {"start": v(-10.96, -1.3) * mm, "end": v(-10.94, -1.43) * mm});
            skLineSegment(sketch, "E3233", {"start": v(-10.94, -1.43) * mm, "end": v(-10.93, -1.54) * mm});
            skLineSegment(sketch, "E3234", {"start": v(-10.93, -1.54) * mm, "end": v(-10.9, -1.67) * mm});
            skLineSegment(sketch, "E3235", {"start": v(-10.9, -1.67) * mm, "end": v(-10.89, -1.8) * mm});
            skLineSegment(sketch, "E3236", {"start": v(-10.89, -1.8) * mm, "end": v(-10.87, -1.91) * mm});
            skLineSegment(sketch, "E3237", {"start": v(-10.87, -1.91) * mm, "end": v(-10.86, -1.97) * mm});
            skLineSegment(sketch, "E3238", {"start": v(-10.86, -1.97) * mm, "end": v(-10.74, -2.01) * mm});
            skLineSegment(sketch, "E3239", {"start": v(-10.74, -2.01) * mm, "end": v(-10.64, -2.05) * mm});
            skLineSegment(sketch, "E3240", {"start": v(-10.64, -2.05) * mm, "end": v(-10.52, -2.08) * mm});
            skLineSegment(sketch, "E3241", {"start": v(-10.52, -2.08) * mm, "end": v(-10.41, -2.12) * mm});
            skLineSegment(sketch, "E3242", {"start": v(-10.41, -2.12) * mm, "end": v(-10.3, -2.14) * mm});
            skLineSegment(sketch, "E3243", {"start": v(-10.3, -2.14) * mm, "end": v(-10.19, -2.17) * mm});
            skLineSegment(sketch, "E3244", {"start": v(-10.19, -2.17) * mm, "end": v(-10.08, -2.2) * mm});
            skLineSegment(sketch, "E3245", {"start": v(-10.08, -2.2) * mm, "end": v(-9.96, -2.21) * mm});
            skLineSegment(sketch, "E3246", {"start": v(-9.96, -2.21) * mm, "end": v(-9.85, -2.23) * mm});
            skLineSegment(sketch, "E3247", {"start": v(-9.85, -2.23) * mm, "end": v(-9.73, -2.24) * mm});
            skLineSegment(sketch, "E3248", {"start": v(-9.73, -2.24) * mm, "end": v(-9.6, -2.25) * mm});
            skLineSegment(sketch, "E3249", {"start": v(-9.6, -2.25) * mm, "end": v(-9.49, -2.26) * mm});
            skLineSegment(sketch, "E3250", {"start": v(-9.49, -2.26) * mm, "end": v(-9.38, -2.26) * mm});
            skLineSegment(sketch, "E3251", {"start": v(-9.38, -2.26) * mm, "end": v(-9.26, -2.25) * mm});
            skLineSegment(sketch, "E3252", {"start": v(-9.26, -2.25) * mm, "end": v(-9.15, -2.23) * mm});
            skLineSegment(sketch, "E3253", {"start": v(-9.15, -2.23) * mm, "end": v(-9.03, -2.2) * mm});
            skLineSegment(sketch, "E3254", {"start": v(-9.03, -2.2) * mm, "end": v(-8.92, -2.2) * mm});
            skLineSegment(sketch, "E3255", {"start": v(-8.92, -2.2) * mm, "end": v(-8.8, -2.2) * mm});
            skLineSegment(sketch, "E3256", {"start": v(-8.8, -2.2) * mm, "end": v(-8.69, -2.23) * mm});
            skLineSegment(sketch, "E3257", {"start": v(-8.69, -2.23) * mm, "end": v(-8.6, -2.28) * mm});
            skLineSegment(sketch, "E3258", {"start": v(-8.6, -2.28) * mm, "end": v(-8.56, -2.4) * mm});
            skLineSegment(sketch, "E3259", {"start": v(-8.56, -2.4) * mm, "end": v(-8.52, -2.51) * mm});
            skLineSegment(sketch, "E3260", {"start": v(-8.52, -2.51) * mm, "end": v(-8.49, -2.62) * mm});
            skLineSegment(sketch, "E3261", {"start": v(-8.49, -2.62) * mm, "end": v(-8.45, -2.74) * mm});
            skLineSegment(sketch, "E3262", {"start": v(-8.45, -2.74) * mm, "end": v(-8.41, -2.85) * mm});
            skLineSegment(sketch, "E3263", {"start": v(-8.41, -2.85) * mm, "end": v(-8.4, -2.92) * mm});
            skLineSegment(sketch, "E3264", {"start": v(-8.4, -2.92) * mm, "end": v(-8.43, -3.03) * mm});
            skLineSegment(sketch, "E3265", {"start": v(-8.43, -3.03) * mm, "end": v(-8.5, -3.1) * mm});
            skLineSegment(sketch, "E3266", {"start": v(-8.5, -3.1) * mm, "end": v(-8.6, -3.18) * mm});
            skLineSegment(sketch, "E3267", {"start": v(-8.6, -3.18) * mm, "end": v(-8.7, -3.23) * mm});
            skLineSegment(sketch, "E3268", {"start": v(-8.7, -3.23) * mm, "end": v(-8.8, -3.28) * mm});
            skLineSegment(sketch, "E3269", {"start": v(-8.8, -3.28) * mm, "end": v(-8.9, -3.33) * mm});
            skLineSegment(sketch, "E3270", {"start": v(-8.9, -3.33) * mm, "end": v(-9, -3.38) * mm});
            skLineSegment(sketch, "E3271", {"start": v(-9, -3.38) * mm, "end": v(-9.1, -3.44) * mm});
            skLineSegment(sketch, "E3272", {"start": v(-9.1, -3.44) * mm, "end": v(-9.19, -3.5) * mm});
            skLineSegment(sketch, "E3273", {"start": v(-9.19, -3.5) * mm, "end": v(-9.27, -3.57) * mm});
            skLineSegment(sketch, "E3274", {"start": v(-9.27, -3.57) * mm, "end": v(-9.36, -3.64) * mm});
            skLineSegment(sketch, "E3275", {"start": v(-9.36, -3.64) * mm, "end": v(-9.44, -3.72) * mm});
            skLineSegment(sketch, "E3276", {"start": v(-9.44, -3.72) * mm, "end": v(-9.52, -3.8) * mm});
            skLineSegment(sketch, "E3277", {"start": v(-9.52, -3.8) * mm, "end": v(-9.6, -3.87) * mm});
            skLineSegment(sketch, "E3278", {"start": v(-9.6, -3.87) * mm, "end": v(-9.67, -3.95) * mm});
            skLineSegment(sketch, "E3279", {"start": v(-9.67, -3.95) * mm, "end": v(-9.75, -4.04) * mm});
            skLineSegment(sketch, "E3280", {"start": v(-9.75, -4.04) * mm, "end": v(-9.82, -4.12) * mm});
            skLineSegment(sketch, "E3281", {"start": v(-9.82, -4.12) * mm, "end": v(-9.9, -4.21) * mm});
            skLineSegment(sketch, "E3282", {"start": v(-9.9, -4.21) * mm, "end": v(-9.96, -4.3) * mm});
            skLineSegment(sketch, "E3283", {"start": v(-9.96, -4.3) * mm, "end": v(-10.03, -4.39) * mm});
            skLineSegment(sketch, "E3284", {"start": v(-10.03, -4.39) * mm, "end": v(-10.09, -4.47) * mm});
            skLineSegment(sketch, "E3285", {"start": v(-10.09, -4.47) * mm, "end": v(-10.04, -4.58) * mm});
            skLineSegment(sketch, "E3286", {"start": v(-10.04, -4.58) * mm, "end": v(-9.99, -4.69) * mm});
            skLineSegment(sketch, "E3287", {"start": v(-9.99, -4.69) * mm, "end": v(-9.93, -4.8) * mm});
            skLineSegment(sketch, "E3288", {"start": v(-9.93, -4.8) * mm, "end": v(-9.88, -4.9) * mm});
            skLineSegment(sketch, "E3289", {"start": v(-9.88, -4.9) * mm, "end": v(-9.82, -5.02) * mm});
            skLineSegment(sketch, "E3290", {"start": v(-9.82, -5.02) * mm, "end": v(-9.8, -5.07) * mm});
            skLineSegment(sketch, "E3291", {"start": v(-9.8, -5.07) * mm, "end": v(-9.68, -5.08) * mm});
            skLineSegment(sketch, "E3292", {"start": v(-9.68, -5.08) * mm, "end": v(-9.57, -5.08) * mm});
            skLineSegment(sketch, "E3293", {"start": v(-9.57, -5.08) * mm, "end": v(-9.44, -5.08) * mm});
            skLineSegment(sketch, "E3294", {"start": v(-9.44, -5.08) * mm, "end": v(-9.33, -5.08) * mm});
            skLineSegment(sketch, "E3295", {"start": v(-9.33, -5.08) * mm, "end": v(-9.21, -5.07) * mm});
            skLineSegment(sketch, "E3296", {"start": v(-9.21, -5.07) * mm, "end": v(-9.1, -5.07) * mm});
            skLineSegment(sketch, "E3297", {"start": v(-9.1, -5.07) * mm, "end": v(-8.98, -5.05) * mm});
            skLineSegment(sketch, "E3298", {"start": v(-8.98, -5.05) * mm, "end": v(-8.87, -5.04) * mm});
            skLineSegment(sketch, "E3299", {"start": v(-8.87, -5.04) * mm, "end": v(-8.76, -5.02) * mm});
            skLineSegment(sketch, "E3300", {"start": v(-8.76, -5.02) * mm, "end": v(-8.64, -5) * mm});
            skLineSegment(sketch, "E3301", {"start": v(-8.64, -5) * mm, "end": v(-8.52, -4.97) * mm});
            skLineSegment(sketch, "E3302", {"start": v(-8.52, -4.97) * mm, "end": v(-8.4, -4.94) * mm});
            skLineSegment(sketch, "E3303", {"start": v(-8.4, -4.94) * mm, "end": v(-8.3, -4.9) * mm});
            skLineSegment(sketch, "E3304", {"start": v(-8.3, -4.9) * mm, "end": v(-8.2, -4.87) * mm});
            skLineSegment(sketch, "E3305", {"start": v(-8.2, -4.87) * mm, "end": v(-8.09, -4.81) * mm});
            skLineSegment(sketch, "E3306", {"start": v(-8.09, -4.81) * mm, "end": v(-7.98, -4.76) * mm});
            skLineSegment(sketch, "E3307", {"start": v(-7.98, -4.76) * mm, "end": v(-7.88, -4.71) * mm});
            skLineSegment(sketch, "E3308", {"start": v(-7.88, -4.71) * mm, "end": v(-7.77, -4.68) * mm});
            skLineSegment(sketch, "E3309", {"start": v(-7.77, -4.68) * mm, "end": v(-7.65, -4.68) * mm});
            skLineSegment(sketch, "E3310", {"start": v(-7.65, -4.68) * mm, "end": v(-7.55, -4.7) * mm});
            skLineSegment(sketch, "E3311", {"start": v(-7.55, -4.7) * mm, "end": v(-7.48, -4.8) * mm});
            skLineSegment(sketch, "E3312", {"start": v(-7.48, -4.8) * mm, "end": v(-7.4, -4.9) * mm});
            skLineSegment(sketch, "E3313", {"start": v(-7.4, -4.9) * mm, "end": v(-7.34, -5) * mm});
            skLineSegment(sketch, "E3314", {"start": v(-7.34, -5) * mm, "end": v(-7.27, -5.1) * mm});
            skLineSegment(sketch, "E3315", {"start": v(-7.27, -5.1) * mm, "end": v(-7.2, -5.2) * mm});
            skLineSegment(sketch, "E3316", {"start": v(-7.2, -5.2) * mm, "end": v(-7.17, -5.25) * mm});
            skLineSegment(sketch, "E3317", {"start": v(-7.17, -5.25) * mm, "end": v(-7.17, -5.37) * mm});
            skLineSegment(sketch, "E3318", {"start": v(-7.17, -5.37) * mm, "end": v(-7.21, -5.47) * mm});
            skLineSegment(sketch, "E3319", {"start": v(-7.21, -5.47) * mm, "end": v(-7.28, -5.56) * mm});
            skLineSegment(sketch, "E3320", {"start": v(-7.28, -5.56) * mm, "end": v(-7.36, -5.64) * mm});
            skLineSegment(sketch, "E3321", {"start": v(-7.36, -5.64) * mm, "end": v(-7.45, -5.72) * mm});
            skLineSegment(sketch, "E3322", {"start": v(-7.45, -5.72) * mm, "end": v(-7.53, -5.8) * mm});
            skLineSegment(sketch, "E3323", {"start": v(-7.53, -5.8) * mm, "end": v(-7.6, -5.87) * mm});
            skLineSegment(sketch, "E3324", {"start": v(-7.6, -5.87) * mm, "end": v(-7.68, -5.96) * mm});
            skLineSegment(sketch, "E3325", {"start": v(-7.68, -5.96) * mm, "end": v(-7.75, -6.05) * mm});
            skLineSegment(sketch, "E3326", {"start": v(-7.75, -6.05) * mm, "end": v(-7.8, -6.13) * mm});
            skLineSegment(sketch, "E3327", {"start": v(-7.8, -6.13) * mm, "end": v(-7.87, -6.23) * mm});
            skLineSegment(sketch, "E3328", {"start": v(-7.87, -6.23) * mm, "end": v(-7.92, -6.32) * mm});
            skLineSegment(sketch, "E3329", {"start": v(-7.92, -6.32) * mm, "end": v(-7.98, -6.42) * mm});
            skLineSegment(sketch, "E3330", {"start": v(-7.98, -6.42) * mm, "end": v(-8.03, -6.52) * mm});
            skLineSegment(sketch, "E3331", {"start": v(-8.03, -6.52) * mm, "end": v(-8.08, -6.62) * mm});
            skLineSegment(sketch, "E3332", {"start": v(-8.08, -6.62) * mm, "end": v(-8.13, -6.72) * mm});
            skLineSegment(sketch, "E3333", {"start": v(-8.13, -6.72) * mm, "end": v(-8.17, -6.83) * mm});
            skLineSegment(sketch, "E3334", {"start": v(-8.17, -6.83) * mm, "end": v(-8.22, -6.93) * mm});
            skLineSegment(sketch, "E3335", {"start": v(-8.22, -6.93) * mm, "end": v(-8.25, -7.03) * mm});
            skLineSegment(sketch, "E3336", {"start": v(-8.25, -7.03) * mm, "end": v(-8.3, -7.14) * mm});
            skLineSegment(sketch, "E3337", {"start": v(-8.3, -7.14) * mm, "end": v(-8.32, -7.23) * mm});
            skLineSegment(sketch, "E3338", {"start": v(-8.32, -7.23) * mm, "end": v(-8.24, -7.32) * mm});
            skLineSegment(sketch, "E3339", {"start": v(-8.24, -7.32) * mm, "end": v(-8.16, -7.4) * mm});
            skLineSegment(sketch, "E3340", {"start": v(-8.16, -7.4) * mm, "end": v(-8.08, -7.5) * mm});
            skLineSegment(sketch, "E3341", {"start": v(-8.08, -7.5) * mm, "end": v(-8, -7.6) * mm});
            skLineSegment(sketch, "E3342", {"start": v(-8, -7.6) * mm, "end": v(-7.9, -7.68) * mm});
            skLineSegment(sketch, "E3343", {"start": v(-7.9, -7.68) * mm, "end": v(-7.87, -7.72) * mm});
            skLineSegment(sketch, "E3344", {"start": v(-7.87, -7.72) * mm, "end": v(-7.75, -7.7) * mm});
            skLineSegment(sketch, "E3345", {"start": v(-7.75, -7.7) * mm, "end": v(-7.65, -7.66) * mm});
            skLineSegment(sketch, "E3346", {"start": v(-7.65, -7.66) * mm, "end": v(-7.53, -7.63) * mm});
            skLineSegment(sketch, "E3347", {"start": v(-7.53, -7.63) * mm, "end": v(-7.42, -7.6) * mm});
            skLineSegment(sketch, "E3348", {"start": v(-7.42, -7.6) * mm, "end": v(-7.31, -7.55) * mm});
            skLineSegment(sketch, "E3349", {"start": v(-7.31, -7.55) * mm, "end": v(-7.2, -7.5) * mm});
            skLineSegment(sketch, "E3350", {"start": v(-7.2, -7.5) * mm, "end": v(-7.1, -7.47) * mm});
            skLineSegment(sketch, "E3351", {"start": v(-7.1, -7.47) * mm, "end": v(-6.99, -7.42) * mm});
            skLineSegment(sketch, "E3352", {"start": v(-6.99, -7.42) * mm, "end": v(-6.89, -7.37) * mm});
            skLineSegment(sketch, "E3353", {"start": v(-6.89, -7.37) * mm, "end": v(-6.78, -7.32) * mm});
            skLineSegment(sketch, "E3354", {"start": v(-6.78, -7.32) * mm, "end": v(-6.68, -7.25) * mm});
            skLineSegment(sketch, "E3355", {"start": v(-6.68, -7.25) * mm, "end": v(-6.57, -7.19) * mm});
            skLineSegment(sketch, "E3356", {"start": v(-6.57, -7.19) * mm, "end": v(-6.48, -7.12) * mm});
            skLineSegment(sketch, "E3357", {"start": v(-6.48, -7.12) * mm, "end": v(-6.4, -7.05) * mm});
            skLineSegment(sketch, "E3358", {"start": v(-6.4, -7.05) * mm, "end": v(-6.31, -6.97) * mm});
            skLineSegment(sketch, "E3359", {"start": v(-6.31, -6.97) * mm, "end": v(-6.22, -6.89) * mm});
            skLineSegment(sketch, "E3360", {"start": v(-6.22, -6.89) * mm, "end": v(-6.14, -6.82) * mm});
            skLineSegment(sketch, "E3361", {"start": v(-6.14, -6.82) * mm, "end": v(-6.04, -6.75) * mm});
            skLineSegment(sketch, "E3362", {"start": v(-6.04, -6.75) * mm, "end": v(-5.93, -6.71) * mm});
            skLineSegment(sketch, "E3363", {"start": v(-5.93, -6.71) * mm, "end": v(-5.83, -6.7) * mm});
            skLineSegment(sketch, "E3364", {"start": v(-5.83, -6.7) * mm, "end": v(-5.73, -6.78) * mm});
            skLineSegment(sketch, "E3365", {"start": v(-5.73, -6.78) * mm, "end": v(-5.64, -6.85) * mm});
            skLineSegment(sketch, "E3366", {"start": v(-5.64, -6.85) * mm, "end": v(-5.54, -6.93) * mm});
            skLineSegment(sketch, "E3367", {"start": v(-5.54, -6.93) * mm, "end": v(-5.44, -7) * mm});
            skLineSegment(sketch, "E3368", {"start": v(-5.44, -7) * mm, "end": v(-5.35, -7.07) * mm});
            skLineSegment(sketch, "E3369", {"start": v(-5.35, -7.07) * mm, "end": v(-5.3, -7.12) * mm});
            skLineSegment(sketch, "E3370", {"start": v(-5.3, -7.12) * mm, "end": v(-5.27, -7.23) * mm});
            skLineSegment(sketch, "E3371", {"start": v(-5.27, -7.23) * mm, "end": v(-5.28, -7.34) * mm});
            skLineSegment(sketch, "E3372", {"start": v(-5.28, -7.34) * mm, "end": v(-5.32, -7.44) * mm});
            skLineSegment(sketch, "E3373", {"start": v(-5.32, -7.44) * mm, "end": v(-5.37, -7.55) * mm});
            skLineSegment(sketch, "E3374", {"start": v(-5.37, -7.55) * mm, "end": v(-5.43, -7.65) * mm});
            skLineSegment(sketch, "E3375", {"start": v(-5.43, -7.65) * mm, "end": v(-5.49, -7.75) * mm});
            skLineSegment(sketch, "E3376", {"start": v(-5.49, -7.75) * mm, "end": v(-5.54, -7.84) * mm});
            skLineSegment(sketch, "E3377", {"start": v(-5.54, -7.84) * mm, "end": v(-5.58, -7.95) * mm});
            skLineSegment(sketch, "E3378", {"start": v(-5.58, -7.95) * mm, "end": v(-5.62, -8.05) * mm});
            skLineSegment(sketch, "E3379", {"start": v(-5.62, -8.05) * mm, "end": v(-5.65, -8.15) * mm});
            skLineSegment(sketch, "E3380", {"start": v(-5.65, -8.15) * mm, "end": v(-5.68, -8.26) * mm});
            skLineSegment(sketch, "E3381", {"start": v(-5.68, -8.26) * mm, "end": v(-5.71, -8.36) * mm});
            skLineSegment(sketch, "E3382", {"start": v(-5.71, -8.36) * mm, "end": v(-5.74, -8.47) * mm});
            skLineSegment(sketch, "E3383", {"start": v(-5.74, -8.47) * mm, "end": v(-5.76, -8.58) * mm});
            skLineSegment(sketch, "E3384", {"start": v(-5.76, -8.58) * mm, "end": v(-5.77, -8.7) * mm});
            skLineSegment(sketch, "E3385", {"start": v(-5.77, -8.7) * mm, "end": v(-5.79, -8.8) * mm});
            skLineSegment(sketch, "E3386", {"start": v(-5.79, -8.8) * mm, "end": v(-5.8, -8.92) * mm});
            skLineSegment(sketch, "E3387", {"start": v(-5.8, -8.92) * mm, "end": v(-5.81, -9.03) * mm});
            skLineSegment(sketch, "E3388", {"start": v(-5.81, -9.03) * mm, "end": v(-5.82, -9.14) * mm});
            skLineSegment(sketch, "E3389", {"start": v(-5.82, -9.14) * mm, "end": v(-5.82, -9.25) * mm});
            skLineSegment(sketch, "E3390", {"start": v(-5.82, -9.25) * mm, "end": v(-5.82, -9.35) * mm});
            skLineSegment(sketch, "E3391", {"start": v(-5.82, -9.35) * mm, "end": v(-5.72, -9.41) * mm});
            skLineSegment(sketch, "E3392", {"start": v(-5.72, -9.41) * mm, "end": v(-5.62, -9.47) * mm});
            skLineSegment(sketch, "E3393", {"start": v(-5.62, -9.47) * mm, "end": v(-5.5, -9.54) * mm});
            skLineSegment(sketch, "E3394", {"start": v(-5.5, -9.54) * mm, "end": v(-5.4, -9.6) * mm});
            skLineSegment(sketch, "E3395", {"start": v(-5.4, -9.6) * mm, "end": v(-5.3, -9.66) * mm});
            skLineSegment(sketch, "E3396", {"start": v(-5.3, -9.66) * mm, "end": v(-5.24, -9.69) * mm});
            skLineSegment(sketch, "E3397", {"start": v(-5.24, -9.69) * mm, "end": v(-5.14, -9.62) * mm});
            skLineSegment(sketch, "E3398", {"start": v(-5.14, -9.62) * mm, "end": v(-5.05, -9.56) * mm});
            skLineSegment(sketch, "E3399", {"start": v(-5.05, -9.56) * mm, "end": v(-4.95, -9.5) * mm});
            skLineSegment(sketch, "E3400", {"start": v(-4.95, -9.5) * mm, "end": v(-4.85, -9.43) * mm});
            skLineSegment(sketch, "E3401", {"start": v(-4.85, -9.43) * mm, "end": v(-4.76, -9.36) * mm});
            skLineSegment(sketch, "E3402", {"start": v(-4.76, -9.36) * mm, "end": v(-4.67, -9.29) * mm});
            skLineSegment(sketch, "E3403", {"start": v(-4.67, -9.29) * mm, "end": v(-4.58, -9.21) * mm});
            skLineSegment(sketch, "E3404", {"start": v(-4.58, -9.21) * mm, "end": v(-4.5, -9.14) * mm});
            skLineSegment(sketch, "E3405", {"start": v(-4.5, -9.14) * mm, "end": v(-4.41, -9.06) * mm});
            skLineSegment(sketch, "E3406", {"start": v(-4.41, -9.06) * mm, "end": v(-4.33, -8.98) * mm});
            skLineSegment(sketch, "E3407", {"start": v(-4.33, -8.98) * mm, "end": v(-4.24, -8.89) * mm});
            skLineSegment(sketch, "E3408", {"start": v(-4.24, -8.89) * mm, "end": v(-4.16, -8.8) * mm});
            skLineSegment(sketch, "E3409", {"start": v(-4.16, -8.8) * mm, "end": v(-4.1, -8.7) * mm});
            skLineSegment(sketch, "E3410", {"start": v(-4.1, -8.7) * mm, "end": v(-4.03, -8.61) * mm});
            skLineSegment(sketch, "E3411", {"start": v(-4.03, -8.61) * mm, "end": v(-3.98, -8.5) * mm});
            skLineSegment(sketch, "E3412", {"start": v(-3.98, -8.5) * mm, "end": v(-3.92, -8.4) * mm});
            skLineSegment(sketch, "E3413", {"start": v(-3.92, -8.4) * mm, "end": v(-3.86, -8.31) * mm});
            skLineSegment(sketch, "E3414", {"start": v(-3.86, -8.31) * mm, "end": v(-3.78, -8.22) * mm});
            skLineSegment(sketch, "E3415", {"start": v(-3.78, -8.22) * mm, "end": v(-3.7, -8.15) * mm});
            skLineSegment(sketch, "E3416", {"start": v(-3.7, -8.15) * mm, "end": v(-3.6, -8.12) * mm});
            skLineSegment(sketch, "E3417", {"start": v(-3.6, -8.12) * mm, "end": v(-3.48, -8.16) * mm});
            skLineSegment(sketch, "E3418", {"start": v(-3.48, -8.16) * mm, "end": v(-3.37, -8.2) * mm});
            skLineSegment(sketch, "E3419", {"start": v(-3.37, -8.2) * mm, "end": v(-3.25, -8.24) * mm});
            skLineSegment(sketch, "E3420", {"start": v(-3.25, -8.24) * mm, "end": v(-3.14, -8.28) * mm});
            skLineSegment(sketch, "E3421", {"start": v(-3.14, -8.28) * mm, "end": v(-3.03, -8.32) * mm});
            skLineSegment(sketch, "E3422", {"start": v(-3.03, -8.32) * mm, "end": v(-2.97, -8.35) * mm});
            skLineSegment(sketch, "E3423", {"start": v(-2.97, -8.35) * mm, "end": v(-2.9, -8.45) * mm});
            skLineSegment(sketch, "E3424", {"start": v(-2.9, -8.45) * mm, "end": v(-2.89, -8.56) * mm});
            skLineSegment(sketch, "E3425", {"start": v(-2.89, -8.56) * mm, "end": v(-2.89, -8.67) * mm});
            skLineSegment(sketch, "E3426", {"start": v(-2.89, -8.67) * mm, "end": v(-2.91, -8.78) * mm});
            skLineSegment(sketch, "E3427", {"start": v(-2.91, -8.78) * mm, "end": v(-2.94, -8.9) * mm});
            skLineSegment(sketch, "E3428", {"start": v(-2.94, -8.9) * mm, "end": v(-2.96, -9) * mm});
            skLineSegment(sketch, "E3429", {"start": v(-2.96, -9) * mm, "end": v(-2.98, -9.12) * mm});
            skLineSegment(sketch, "E3430", {"start": v(-2.98, -9.12) * mm, "end": v(-3, -9.23) * mm});
            skLineSegment(sketch, "E3431", {"start": v(-3, -9.23) * mm, "end": v(-3, -9.34) * mm});
            skLineSegment(sketch, "E3432", {"start": v(-3, -9.34) * mm, "end": v(-3, -9.44) * mm});
            skLineSegment(sketch, "E3433", {"start": v(-3, -9.44) * mm, "end": v(-3, -9.56) * mm});
            skLineSegment(sketch, "E3434", {"start": v(-3, -9.56) * mm, "end": v(-3, -9.66) * mm});
            skLineSegment(sketch, "E3435", {"start": v(-3, -9.66) * mm, "end": v(-2.98, -9.78) * mm});
            skLineSegment(sketch, "E3436", {"start": v(-2.98, -9.78) * mm, "end": v(-2.97, -9.89) * mm});
            skLineSegment(sketch, "E3437", {"start": v(-2.97, -9.89) * mm, "end": v(-2.96, -10) * mm});
            skLineSegment(sketch, "E3438", {"start": v(-2.96, -10) * mm, "end": v(-2.94, -10.1) * mm});
            skLineSegment(sketch, "E3439", {"start": v(-2.94, -10.1) * mm, "end": v(-2.92, -10.22) * mm});
            skLineSegment(sketch, "E3440", {"start": v(-2.92, -10.22) * mm, "end": v(-2.9, -10.33) * mm});
            skLineSegment(sketch, "E3441", {"start": v(-2.9, -10.33) * mm, "end": v(-2.87, -10.44) * mm});
            skLineSegment(sketch, "E3442", {"start": v(-2.87, -10.44) * mm, "end": v(-2.84, -10.55) * mm});
            skLineSegment(sketch, "E3443", {"start": v(-2.84, -10.55) * mm, "end": v(-2.81, -10.64) * mm});
            skLineSegment(sketch, "E3444", {"start": v(-2.81, -10.64) * mm, "end": v(-2.7, -10.67) * mm});
            skLineSegment(sketch, "E3445", {"start": v(-2.7, -10.67) * mm, "end": v(-2.58, -10.7) * mm});
            skLineSegment(sketch, "E3446", {"start": v(-2.58, -10.7) * mm, "end": v(-2.45, -10.73) * mm});
            skLineSegment(sketch, "E3447", {"start": v(-2.45, -10.73) * mm, "end": v(-2.33, -10.75) * mm});
            skLineSegment(sketch, "E3448", {"start": v(-2.33, -10.75) * mm, "end": v(-2.22, -10.78) * mm});
            skLineSegment(sketch, "E3449", {"start": v(-2.22, -10.78) * mm, "end": v(-2.16, -10.79) * mm});
            skLineSegment(sketch, "E3450", {"start": v(-2.16, -10.79) * mm, "end": v(-2.08, -10.7) * mm});
            skLineSegment(sketch, "E3451", {"start": v(-2.08, -10.7) * mm, "end": v(-2, -10.62) * mm});
            skLineSegment(sketch, "E3452", {"start": v(-2, -10.62) * mm, "end": v(-1.93, -10.52) * mm});
            skLineSegment(sketch, "E3453", {"start": v(-1.93, -10.52) * mm, "end": v(-1.86, -10.43) * mm});
            skLineSegment(sketch, "E3454", {"start": v(-1.86, -10.43) * mm, "end": v(-1.8, -10.34) * mm});
            skLineSegment(sketch, "E3455", {"start": v(-1.8, -10.34) * mm, "end": v(-1.72, -10.24) * mm});
            skLineSegment(sketch, "E3456", {"start": v(-1.72, -10.24) * mm, "end": v(-1.66, -10.14) * mm});
            skLineSegment(sketch, "E3457", {"start": v(-1.66, -10.14) * mm, "end": v(-1.6, -10.04) * mm});
            skLineSegment(sketch, "E3458", {"start": v(-1.6, -10.04) * mm, "end": v(-1.55, -9.95) * mm});
            skLineSegment(sketch, "E3459", {"start": v(-1.55, -9.95) * mm, "end": v(-1.5, -9.84) * mm});
            skLineSegment(sketch, "E3460", {"start": v(-1.5, -9.84) * mm, "end": v(-1.44, -9.73) * mm});
            skLineSegment(sketch, "E3461", {"start": v(-1.44, -9.73) * mm, "end": v(-1.39, -9.62) * mm});
            skLineSegment(sketch, "E3462", {"start": v(-1.39, -9.62) * mm, "end": v(-1.35, -9.52) * mm});
            skLineSegment(sketch, "E3463", {"start": v(-1.35, -9.52) * mm, "end": v(-1.32, -9.4) * mm});
            skLineSegment(sketch, "E3464", {"start": v(-1.32, -9.4) * mm, "end": v(-1.3, -9.3) * mm});
            skLineSegment(sketch, "E3465", {"start": v(-1.3, -9.3) * mm, "end": v(-1.27, -9.17) * mm});
            skLineSegment(sketch, "E3466", {"start": v(-1.27, -9.17) * mm, "end": v(-1.24, -9.07) * mm});
            skLineSegment(sketch, "E3467", {"start": v(-1.24, -9.07) * mm, "end": v(-1.2, -8.96) * mm});
            skLineSegment(sketch, "E3468", {"start": v(-1.2, -8.96) * mm, "end": v(-1.13, -8.87) * mm});
            skLineSegment(sketch, "E3469", {"start": v(-1.13, -8.87) * mm, "end": v(-1.04, -8.8) * mm});
            skLineSegment(sketch, "E3470", {"start": v(-1.04, -8.8) * mm, "end": v(-0.92, -8.8) * mm});
            skLineSegment(sketch, "E3471", {"start": v(-0.92, -8.8) * mm, "end": v(-0.8, -8.82) * mm});
            skLineSegment(sketch, "E3472", {"start": v(-0.8, -8.82) * mm, "end": v(-0.68, -8.82) * mm});
            skLineSegment(sketch, "E3473", {"start": v(-0.68, -8.82) * mm, "end": v(-0.56, -8.83) * mm});
            skLineSegment(sketch, "E3474", {"start": v(-0.56, -8.83) * mm, "end": v(-0.44, -8.84) * mm});
            skLineSegment(sketch, "E3475", {"start": v(-0.44, -8.84) * mm, "end": v(-0.38, -8.85) * mm});
            skLineSegment(sketch, "E3476", {"start": v(-0.38, -8.85) * mm, "end": v(-0.29, -8.92) * mm});
            skLineSegment(sketch, "E3477", {"start": v(-0.29, -8.92) * mm, "end": v(-0.24, -9.02) * mm});
            skLineSegment(sketch, "E3478", {"start": v(-0.24, -9.02) * mm, "end": v(-0.2, -9.12) * mm});
            skLineSegment(sketch, "E3479", {"start": v(-0.2, -9.12) * mm, "end": v(-0.2, -9.24) * mm});
            skLineSegment(sketch, "E3480", {"start": v(-0.2, -9.24) * mm, "end": v(-0.19, -9.36) * mm});
            skLineSegment(sketch, "E3481", {"start": v(-0.19, -9.36) * mm, "end": v(-0.18, -9.47) * mm});
            skLineSegment(sketch, "E3482", {"start": v(-0.18, -9.47) * mm, "end": v(-0.16, -9.58) * mm});
            skLineSegment(sketch, "E3483", {"start": v(-0.16, -9.58) * mm, "end": v(-0.14, -9.69) * mm});
            skLineSegment(sketch, "E3484", {"start": v(-0.14, -9.69) * mm, "end": v(-0.12, -9.8) * mm});
            skLineSegment(sketch, "E3485", {"start": v(-0.12, -9.8) * mm, "end": v(-0.09, -9.9) * mm});
            skLineSegment(sketch, "E3486", {"start": v(-0.09, -9.9) * mm, "end": v(-0.05, -10) * mm});
            skLineSegment(sketch, "E3487", {"start": v(-0.05, -10) * mm, "end": v(-0.01, -10.1) * mm});
            skLineSegment(sketch, "E3488", {"start": v(-0.01, -10.1) * mm, "end": v(0.03, -10.2) * mm});
            skLineSegment(sketch, "E3489", {"start": v(0.03, -10.2) * mm, "end": v(0.07, -10.31) * mm});
            skLineSegment(sketch, "E3490", {"start": v(0.07, -10.31) * mm, "end": v(0.12, -10.41) * mm});
            skLineSegment(sketch, "E3491", {"start": v(0.12, -10.41) * mm, "end": v(0.17, -10.51) * mm});
            skLineSegment(sketch, "E3492", {"start": v(0.17, -10.51) * mm, "end": v(0.23, -10.62) * mm});
            skLineSegment(sketch, "E3493", {"start": v(0.23, -10.62) * mm, "end": v(0.28, -10.71) * mm});
            skLineSegment(sketch, "E3494", {"start": v(0.28, -10.71) * mm, "end": v(0.34, -10.8) * mm});
            skLineSegment(sketch, "E3495", {"start": v(0.34, -10.8) * mm, "end": v(0.4, -10.9) * mm});
            skLineSegment(sketch, "E3496", {"start": v(0.4, -10.9) * mm, "end": v(0.45, -10.99) * mm});
            skLineSegment(sketch, "E3497", {"start": v(0.45, -10.99) * mm, "end": v(0.57, -10.98) * mm});
            skLineSegment(sketch, "E3498", {"start": v(0.57, -10.98) * mm, "end": v(0.69, -10.97) * mm});
            skLineSegment(sketch, "E3499", {"start": v(0.69, -10.97) * mm, "end": v(0.82, -10.96) * mm});
            skLineSegment(sketch, "E3500", {"start": v(0.82, -10.96) * mm, "end": v(0.94, -10.95) * mm});
            skLineSegment(sketch, "E3501", {"start": v(0.94, -10.95) * mm, "end": v(1.06, -10.94) * mm});
            skLineSegment(sketch, "E3502", {"start": v(1.06, -10.94) * mm, "end": v(1.12, -10.94) * mm});
            skLineSegment(sketch, "E3503", {"start": v(1.12, -10.94) * mm, "end": v(1.17, -10.83) * mm});
            skLineSegment(sketch, "E3504", {"start": v(1.17, -10.83) * mm, "end": v(1.2, -10.73) * mm});
            skLineSegment(sketch, "E3505", {"start": v(1.2, -10.73) * mm, "end": v(1.25, -10.61) * mm});
            skLineSegment(sketch, "E3506", {"start": v(1.25, -10.61) * mm, "end": v(1.3, -10.5) * mm});
            skLineSegment(sketch, "E3507", {"start": v(1.3, -10.5) * mm, "end": v(1.33, -10.4) * mm});
            skLineSegment(sketch, "E3508", {"start": v(1.33, -10.4) * mm, "end": v(1.37, -10.28) * mm});
            skLineSegment(sketch, "E3509", {"start": v(1.37, -10.28) * mm, "end": v(1.4, -10.17) * mm});
            skLineSegment(sketch, "E3510", {"start": v(1.4, -10.17) * mm, "end": v(1.43, -10.06) * mm});
            skLineSegment(sketch, "E3511", {"start": v(1.43, -10.06) * mm, "end": v(1.45, -9.95) * mm});
            skLineSegment(sketch, "E3512", {"start": v(1.45, -9.95) * mm, "end": v(1.47, -9.83) * mm});
            skLineSegment(sketch, "E3513", {"start": v(1.47, -9.83) * mm, "end": v(1.5, -9.71) * mm});
            skLineSegment(sketch, "E3514", {"start": v(1.5, -9.71) * mm, "end": v(1.5, -9.6) * mm});
            skLineSegment(sketch, "E3515", {"start": v(1.5, -9.6) * mm, "end": v(1.51, -9.48) * mm});
            skLineSegment(sketch, "E3516", {"start": v(1.51, -9.48) * mm, "end": v(1.51, -9.37) * mm});
            skLineSegment(sketch, "E3517", {"start": v(1.51, -9.37) * mm, "end": v(1.5, -9.25) * mm});
            skLineSegment(sketch, "E3518", {"start": v(1.5, -9.25) * mm, "end": v(1.49, -9.13) * mm});
            skLineSegment(sketch, "E3519", {"start": v(1.49, -9.13) * mm, "end": v(1.49, -9.02) * mm});
            skLineSegment(sketch, "E3520", {"start": v(1.49, -9.02) * mm, "end": v(1.5, -8.9) * mm});
            skLineSegment(sketch, "E3521", {"start": v(1.5, -8.9) * mm, "end": v(1.53, -8.8) * mm});
            skLineSegment(sketch, "E3522", {"start": v(1.53, -8.8) * mm, "end": v(1.6, -8.7) * mm});
            skLineSegment(sketch, "E3523", {"start": v(1.6, -8.7) * mm, "end": v(1.71, -8.68) * mm});
            skLineSegment(sketch, "E3524", {"start": v(1.71, -8.68) * mm, "end": v(1.83, -8.65) * mm});
            skLineSegment(sketch, "E3525", {"start": v(1.83, -8.65) * mm, "end": v(1.95, -8.62) * mm});
            skLineSegment(sketch, "E3526", {"start": v(1.95, -8.62) * mm, "end": v(2.06, -8.6) * mm});
            skLineSegment(sketch, "E3527", {"start": v(2.06, -8.6) * mm, "end": v(2.18, -8.56) * mm});
            skLineSegment(sketch, "E3528", {"start": v(2.18, -8.56) * mm, "end": v(2.24, -8.55) * mm});
            skLineSegment(sketch, "E3529", {"start": v(2.24, -8.55) * mm, "end": v(2.35, -8.6) * mm});
            skLineSegment(sketch, "E3530", {"start": v(2.35, -8.6) * mm, "end": v(2.43, -8.68) * mm});
            skLineSegment(sketch, "E3531", {"start": v(2.43, -8.68) * mm, "end": v(2.49, -8.77) * mm});
            skLineSegment(sketch, "E3532", {"start": v(2.49, -8.77) * mm, "end": v(2.53, -8.88) * mm});
            skLineSegment(sketch, "E3533", {"start": v(2.53, -8.88) * mm, "end": v(2.58, -8.99) * mm});
            skLineSegment(sketch, "E3534", {"start": v(2.58, -8.99) * mm, "end": v(2.62, -9.09) * mm});
            skLineSegment(sketch, "E3535", {"start": v(2.62, -9.09) * mm, "end": v(2.66, -9.2) * mm});
            skLineSegment(sketch, "E3536", {"start": v(2.66, -9.2) * mm, "end": v(2.72, -9.29) * mm});
            skLineSegment(sketch, "E3537", {"start": v(2.72, -9.29) * mm, "end": v(2.77, -9.38) * mm});
            skLineSegment(sketch, "E3538", {"start": v(2.77, -9.38) * mm, "end": v(2.83, -9.47) * mm});
            skLineSegment(sketch, "E3539", {"start": v(2.83, -9.47) * mm, "end": v(2.9, -9.56) * mm});
            skLineSegment(sketch, "E3540", {"start": v(2.9, -9.56) * mm, "end": v(2.96, -9.65) * mm});
            skLineSegment(sketch, "E3541", {"start": v(2.96, -9.65) * mm, "end": v(3.03, -9.74) * mm});
            skLineSegment(sketch, "E3542", {"start": v(3.03, -9.74) * mm, "end": v(3.1, -9.82) * mm});
            skLineSegment(sketch, "E3543", {"start": v(3.1, -9.82) * mm, "end": v(3.18, -9.9) * mm});
            skLineSegment(sketch, "E3544", {"start": v(3.18, -9.9) * mm, "end": v(3.26, -9.98) * mm});
            skLineSegment(sketch, "E3545", {"start": v(3.26, -9.98) * mm, "end": v(3.34, -10.07) * mm});
            skLineSegment(sketch, "E3546", {"start": v(3.34, -10.07) * mm, "end": v(3.42, -10.14) * mm});
            skLineSegment(sketch, "E3547", {"start": v(3.42, -10.14) * mm, "end": v(3.5, -10.22) * mm});
            skLineSegment(sketch, "E3548", {"start": v(3.5, -10.22) * mm, "end": v(3.59, -10.3) * mm});
            skLineSegment(sketch, "E3549", {"start": v(3.59, -10.3) * mm, "end": v(3.66, -10.35) * mm});
            skLineSegment(sketch, "E3550", {"start": v(3.66, -10.35) * mm, "end": v(3.78, -10.31) * mm});
            skLineSegment(sketch, "E3551", {"start": v(3.78, -10.31) * mm, "end": v(3.89, -10.27) * mm});
            skLineSegment(sketch, "E3552", {"start": v(3.89, -10.27) * mm, "end": v(4.01, -10.22) * mm});
            skLineSegment(sketch, "E3553", {"start": v(4.01, -10.22) * mm, "end": v(4.12, -10.18) * mm});
            skLineSegment(sketch, "E3554", {"start": v(4.12, -10.18) * mm, "end": v(4.23, -10.13) * mm});
            skLineSegment(sketch, "E3555", {"start": v(4.23, -10.13) * mm, "end": v(4.29, -10.1) * mm});
            skLineSegment(sketch, "E3556", {"start": v(4.29, -10.1) * mm, "end": v(4.3, -9.99) * mm});
            skLineSegment(sketch, "E3557", {"start": v(4.3, -9.99) * mm, "end": v(4.31, -9.88) * mm});
            skLineSegment(sketch, "E3558", {"start": v(4.31, -9.88) * mm, "end": v(4.32, -9.76) * mm});
            skLineSegment(sketch, "E3559", {"start": v(4.32, -9.76) * mm, "end": v(4.33, -9.64) * mm});
            skLineSegment(sketch, "E3560", {"start": v(4.33, -9.64) * mm, "end": v(4.33, -9.53) * mm});
            skLineSegment(sketch, "E3561", {"start": v(4.33, -9.53) * mm, "end": v(4.34, -9.4) * mm});
            skLineSegment(sketch, "E3562", {"start": v(4.34, -9.4) * mm, "end": v(4.33, -9.3) * mm});
            skLineSegment(sketch, "E3563", {"start": v(4.33, -9.3) * mm, "end": v(4.33, -9.18) * mm});
            skLineSegment(sketch, "E3564", {"start": v(4.33, -9.18) * mm, "end": v(4.32, -9.07) * mm});
            skLineSegment(sketch, "E3565", {"start": v(4.32, -9.07) * mm, "end": v(4.3, -8.95) * mm});
            skLineSegment(sketch, "E3566", {"start": v(4.3, -8.95) * mm, "end": v(4.29, -8.83) * mm});
            skLineSegment(sketch, "E3567", {"start": v(4.29, -8.83) * mm, "end": v(4.26, -8.7) * mm});
            skLineSegment(sketch, "E3568", {"start": v(4.26, -8.7) * mm, "end": v(4.24, -8.6) * mm});
            skLineSegment(sketch, "E3569", {"start": v(4.24, -8.6) * mm, "end": v(4.2, -8.5) * mm});
            skLineSegment(sketch, "E3570", {"start": v(4.2, -8.5) * mm, "end": v(4.16, -8.38) * mm});
            skLineSegment(sketch, "E3571", {"start": v(4.16, -8.38) * mm, "end": v(4.11, -8.27) * mm});
            skLineSegment(sketch, "E3572", {"start": v(4.11, -8.27) * mm, "end": v(4.08, -8.17) * mm});
            skLineSegment(sketch, "E3573", {"start": v(4.08, -8.17) * mm, "end": v(4.05, -8.06) * mm});
            skLineSegment(sketch, "E3574", {"start": v(4.05, -8.06) * mm, "end": v(4.06, -7.94) * mm});
            skLineSegment(sketch, "E3575", {"start": v(4.06, -7.94) * mm, "end": v(4.1, -7.84) * mm});
            skLineSegment(sketch, "E3576", {"start": v(4.1, -7.84) * mm, "end": v(4.2, -7.78) * mm});
            skLineSegment(sketch, "E3577", {"start": v(4.2, -7.78) * mm, "end": v(4.3, -7.71) * mm});
            skLineSegment(sketch, "E3578", {"start": v(4.3, -7.71) * mm, "end": v(4.4, -7.65) * mm});
            skLineSegment(sketch, "E3579", {"start": v(4.4, -7.65) * mm, "end": v(4.5, -7.59) * mm});
            skLineSegment(sketch, "E3580", {"start": v(4.5, -7.59) * mm, "end": v(4.6, -7.53) * mm});
            skLineSegment(sketch, "E3581", {"start": v(4.6, -7.53) * mm, "end": v(4.66, -7.5) * mm});
            skLineSegment(sketch, "E3582", {"start": v(4.66, -7.5) * mm, "end": v(4.78, -7.51) * mm});
            skLineSegment(sketch, "E3583", {"start": v(4.78, -7.51) * mm, "end": v(4.88, -7.56) * mm});
            skLineSegment(sketch, "E3584", {"start": v(4.88, -7.56) * mm, "end": v(4.96, -7.63) * mm});
            skLineSegment(sketch, "E3585", {"start": v(4.96, -7.63) * mm, "end": v(5.04, -7.72) * mm});
            skLineSegment(sketch, "E3586", {"start": v(5.04, -7.72) * mm, "end": v(5.11, -7.82) * mm});
            skLineSegment(sketch, "E3587", {"start": v(5.11, -7.82) * mm, "end": v(5.18, -7.9) * mm});
            skLineSegment(sketch, "E3588", {"start": v(5.18, -7.9) * mm, "end": v(5.25, -7.99) * mm});
            skLineSegment(sketch, "E3589", {"start": v(5.25, -7.99) * mm, "end": v(5.33, -8.06) * mm});
            skLineSegment(sketch, "E3590", {"start": v(5.33, -8.06) * mm, "end": v(5.41, -8.14) * mm});
            skLineSegment(sketch, "E3591", {"start": v(5.41, -8.14) * mm, "end": v(5.5, -8.2) * mm});
            skLineSegment(sketch, "E3592", {"start": v(5.5, -8.2) * mm, "end": v(5.59, -8.27) * mm});
            skLineSegment(sketch, "E3593", {"start": v(5.59, -8.27) * mm, "end": v(5.67, -8.34) * mm});
            skLineSegment(sketch, "E3594", {"start": v(5.67, -8.34) * mm, "end": v(5.77, -8.4) * mm});
            skLineSegment(sketch, "E3595", {"start": v(5.77, -8.4) * mm, "end": v(5.86, -8.46) * mm});
            skLineSegment(sketch, "E3596", {"start": v(5.86, -8.46) * mm, "end": v(5.96, -8.51) * mm});
            skLineSegment(sketch, "E3597", {"start": v(5.96, -8.51) * mm, "end": v(6.06, -8.57) * mm});
            skLineSegment(sketch, "E3598", {"start": v(6.06, -8.57) * mm, "end": v(6.16, -8.62) * mm});
            skLineSegment(sketch, "E3599", {"start": v(6.16, -8.62) * mm, "end": v(6.26, -8.67) * mm});
            skLineSegment(sketch, "E3600", {"start": v(6.26, -8.67) * mm, "end": v(6.36, -8.72) * mm});
            skLineSegment(sketch, "E3601", {"start": v(6.36, -8.72) * mm, "end": v(6.46, -8.76) * mm});
            skLineSegment(sketch, "E3602", {"start": v(6.46, -8.76) * mm, "end": v(6.55, -8.8) * mm});
            skLineSegment(sketch, "E3603", {"start": v(6.55, -8.8) * mm, "end": v(6.65, -8.73) * mm});
            skLineSegment(sketch, "E3604", {"start": v(6.65, -8.73) * mm, "end": v(6.74, -8.66) * mm});
            skLineSegment(sketch, "E3605", {"start": v(6.74, -8.66) * mm, "end": v(6.84, -8.58) * mm});
            skLineSegment(sketch, "E3606", {"start": v(6.84, -8.58) * mm, "end": v(6.94, -8.5) * mm});
            skLineSegment(sketch, "E3607", {"start": v(6.94, -8.5) * mm, "end": v(7.03, -8.42) * mm});
            skLineSegment(sketch, "E3608", {"start": v(7.03, -8.42) * mm, "end": v(7.08, -8.38) * mm});
            skLineSegment(sketch, "E3609", {"start": v(7.08, -8.38) * mm, "end": v(7.05, -8.27) * mm});
            skLineSegment(sketch, "E3610", {"start": v(7.05, -8.27) * mm, "end": v(7.03, -8.16) * mm});
            skLineSegment(sketch, "E3611", {"start": v(7.03, -8.16) * mm, "end": v(7, -8.04) * mm});
            skLineSegment(sketch, "E3612", {"start": v(7, -8.04) * mm, "end": v(6.98, -7.92) * mm});
            skLineSegment(sketch, "E3613", {"start": v(6.98, -7.92) * mm, "end": v(6.95, -7.82) * mm});
            skLineSegment(sketch, "E3614", {"start": v(6.95, -7.82) * mm, "end": v(6.91, -7.7) * mm});
            skLineSegment(sketch, "E3615", {"start": v(6.91, -7.7) * mm, "end": v(6.88, -7.6) * mm});
            skLineSegment(sketch, "E3616", {"start": v(6.88, -7.6) * mm, "end": v(6.84, -7.48) * mm});
            skLineSegment(sketch, "E3617", {"start": v(6.84, -7.48) * mm, "end": v(6.8, -7.38) * mm});
            skLineSegment(sketch, "E3618", {"start": v(6.8, -7.38) * mm, "end": v(6.75, -7.27) * mm});
            skLineSegment(sketch, "E3619", {"start": v(6.75, -7.27) * mm, "end": v(6.7, -7.16) * mm});
            skLineSegment(sketch, "E3620", {"start": v(6.7, -7.16) * mm, "end": v(6.64, -7.05) * mm});
            skLineSegment(sketch, "E3621", {"start": v(6.64, -7.05) * mm, "end": v(6.58, -6.96) * mm});
            skLineSegment(sketch, "E3622", {"start": v(6.58, -6.96) * mm, "end": v(6.52, -6.87) * mm});
            skLineSegment(sketch, "E3623", {"start": v(6.52, -6.87) * mm, "end": v(6.44, -6.77) * mm});
            skLineSegment(sketch, "E3624", {"start": v(6.44, -6.77) * mm, "end": v(6.36, -6.68) * mm});
            skLineSegment(sketch, "E3625", {"start": v(6.36, -6.68) * mm, "end": v(6.3, -6.6) * mm});
            skLineSegment(sketch, "E3626", {"start": v(6.3, -6.6) * mm, "end": v(6.25, -6.5) * mm});
            skLineSegment(sketch, "E3627", {"start": v(6.25, -6.5) * mm, "end": v(6.21, -6.38) * mm});
            skLineSegment(sketch, "E3628", {"start": v(6.21, -6.38) * mm, "end": v(6.22, -6.27) * mm});
            skLineSegment(sketch, "E3629", {"start": v(6.22, -6.27) * mm, "end": v(6.3, -6.18) * mm});
            skLineSegment(sketch, "E3630", {"start": v(6.3, -6.18) * mm, "end": v(6.38, -6.1) * mm});
            skLineSegment(sketch, "E3631", {"start": v(6.38, -6.1) * mm, "end": v(6.46, -6) * mm});
            skLineSegment(sketch, "E3632", {"start": v(6.46, -6) * mm, "end": v(6.54, -5.91) * mm});
            skLineSegment(sketch, "E3633", {"start": v(6.54, -5.91) * mm, "end": v(6.62, -5.82) * mm});
            skLineSegment(sketch, "E3634", {"start": v(6.62, -5.82) * mm, "end": v(6.67, -5.78) * mm});
            skLineSegment(sketch, "E3635", {"start": v(6.67, -5.78) * mm, "end": v(6.78, -5.76) * mm});
            skLineSegment(sketch, "E3636", {"start": v(6.78, -5.76) * mm, "end": v(6.89, -5.78) * mm});
            skLineSegment(sketch, "E3637", {"start": v(6.89, -5.78) * mm, "end": v(6.99, -5.82) * mm});
            skLineSegment(sketch, "E3638", {"start": v(6.99, -5.82) * mm, "end": v(7.09, -5.88) * mm});
            skLineSegment(sketch, "E3639", {"start": v(7.09, -5.88) * mm, "end": v(7.19, -5.95) * mm});
            skLineSegment(sketch, "E3640", {"start": v(7.19, -5.95) * mm, "end": v(7.28, -6.01) * mm});
            skLineSegment(sketch, "E3641", {"start": v(7.28, -6.01) * mm, "end": v(7.37, -6.07) * mm});
            skLineSegment(sketch, "E3642", {"start": v(7.37, -6.07) * mm, "end": v(7.47, -6.12) * mm});
            skLineSegment(sketch, "E3643", {"start": v(7.47, -6.12) * mm, "end": v(7.57, -6.17) * mm});
            skLineSegment(sketch, "E3644", {"start": v(7.57, -6.17) * mm, "end": v(7.67, -6.2) * mm});
            skLineSegment(sketch, "E3645", {"start": v(7.67, -6.2) * mm, "end": v(7.77, -6.25) * mm});
            skLineSegment(sketch, "E3646", {"start": v(7.77, -6.25) * mm, "end": v(7.88, -6.28) * mm});
            skLineSegment(sketch, "E3647", {"start": v(7.88, -6.28) * mm, "end": v(7.98, -6.31) * mm});
            skLineSegment(sketch, "E3648", {"start": v(7.98, -6.31) * mm, "end": v(8.1, -6.34) * mm});
            skLineSegment(sketch, "E3649", {"start": v(8.1, -6.34) * mm, "end": v(8.2, -6.37) * mm});
            skLineSegment(sketch, "E3650", {"start": v(8.2, -6.37) * mm, "end": v(8.31, -6.4) * mm});
            skLineSegment(sketch, "E3651", {"start": v(8.31, -6.4) * mm, "end": v(8.43, -6.41) * mm});
            skLineSegment(sketch, "E3652", {"start": v(8.43, -6.41) * mm, "end": v(8.54, -6.43) * mm});
            skLineSegment(sketch, "E3653", {"start": v(8.54, -6.43) * mm, "end": v(8.64, -6.45) * mm});
            skLineSegment(sketch, "E3654", {"start": v(8.64, -6.45) * mm, "end": v(8.76, -6.46) * mm});
            skLineSegment(sketch, "E3655", {"start": v(8.76, -6.46) * mm, "end": v(8.85, -6.47) * mm});
            skLineSegment(sketch, "E3656", {"start": v(8.85, -6.47) * mm, "end": v(8.92, -6.37) * mm});
            skLineSegment(sketch, "E3657", {"start": v(8.92, -6.37) * mm, "end": v(9, -6.27) * mm});
            skLineSegment(sketch, "E3658", {"start": v(9, -6.27) * mm, "end": v(9.07, -6.17) * mm});
            skLineSegment(sketch, "E3659", {"start": v(9.07, -6.17) * mm, "end": v(9.13, -6.07) * mm});
            skLineSegment(sketch, "E3660", {"start": v(9.13, -6.07) * mm, "end": v(9.2, -5.97) * mm});
            skLineSegment(sketch, "E3661", {"start": v(9.2, -5.97) * mm, "end": v(9.23, -5.91) * mm});
            skLineSegment(sketch, "E3662", {"start": v(9.23, -5.91) * mm, "end": v(9.18, -5.8) * mm});
            skLineSegment(sketch, "E3663", {"start": v(9.18, -5.8) * mm, "end": v(9.12, -5.71) * mm});
            skLineSegment(sketch, "E3664", {"start": v(9.12, -5.71) * mm, "end": v(9.06, -5.6) * mm});
            skLineSegment(sketch, "E3665", {"start": v(9.06, -5.6) * mm, "end": v(9, -5.5) * mm});
            skLineSegment(sketch, "E3666", {"start": v(9, -5.5) * mm, "end": v(8.94, -5.4) * mm});
            skLineSegment(sketch, "E3667", {"start": v(8.94, -5.4) * mm, "end": v(8.88, -5.31) * mm});
            skLineSegment(sketch, "E3668", {"start": v(8.88, -5.31) * mm, "end": v(8.81, -5.22) * mm});
            skLineSegment(sketch, "E3669", {"start": v(8.81, -5.22) * mm, "end": v(8.74, -5.12) * mm});
            skLineSegment(sketch, "E3670", {"start": v(8.74, -5.12) * mm, "end": v(8.67, -5.04) * mm});
            skLineSegment(sketch, "E3671", {"start": v(8.67, -5.04) * mm, "end": v(8.6, -4.95) * mm});
            skLineSegment(sketch, "E3672", {"start": v(8.6, -4.95) * mm, "end": v(8.5, -4.86) * mm});
            skLineSegment(sketch, "E3673", {"start": v(8.5, -4.86) * mm, "end": v(8.42, -4.77) * mm});
            skLineSegment(sketch, "E3674", {"start": v(8.42, -4.77) * mm, "end": v(8.34, -4.7) * mm});
            skLineSegment(sketch, "E3675", {"start": v(8.34, -4.7) * mm, "end": v(8.25, -4.63) * mm});
            skLineSegment(sketch, "E3676", {"start": v(8.25, -4.63) * mm, "end": v(8.15, -4.56) * mm});
            skLineSegment(sketch, "E3677", {"start": v(8.15, -4.56) * mm, "end": v(8.05, -4.5) * mm});
            skLineSegment(sketch, "E3678", {"start": v(8.05, -4.5) * mm, "end": v(7.96, -4.43) * mm});
            skLineSegment(sketch, "E3679", {"start": v(7.96, -4.43) * mm, "end": v(7.88, -4.35) * mm});
            skLineSegment(sketch, "E3680", {"start": v(7.88, -4.35) * mm, "end": v(7.82, -4.25) * mm});
            skLineSegment(sketch, "E3681", {"start": v(7.82, -4.25) * mm, "end": v(7.8, -4.15) * mm});
            skLineSegment(sketch, "E3682", {"start": v(7.8, -4.15) * mm, "end": v(7.84, -4.04) * mm});
            skLineSegment(sketch, "E3683", {"start": v(7.84, -4.04) * mm, "end": v(7.89, -3.93) * mm});
            skLineSegment(sketch, "E3684", {"start": v(7.89, -3.93) * mm, "end": v(7.94, -3.82) * mm});
            skLineSegment(sketch, "E3685", {"start": v(7.94, -3.82) * mm, "end": v(7.99, -3.71) * mm});
            skLineSegment(sketch, "E3686", {"start": v(7.99, -3.71) * mm, "end": v(8.04, -3.6) * mm});
            skLineSegment(sketch, "E3687", {"start": v(8.04, -3.6) * mm, "end": v(8.07, -3.55) * mm});
            skLineSegment(sketch, "E3688", {"start": v(8.07, -3.55) * mm, "end": v(8.17, -3.5) * mm});
            skLineSegment(sketch, "E3689", {"start": v(8.17, -3.5) * mm, "end": v(8.28, -3.48) * mm});
            skLineSegment(sketch, "E3690", {"start": v(8.28, -3.48) * mm, "end": v(8.4, -3.49) * mm});
            skLineSegment(sketch, "E3691", {"start": v(8.4, -3.49) * mm, "end": v(8.5, -3.52) * mm});
            skLineSegment(sketch, "E3692", {"start": v(8.5, -3.52) * mm, "end": v(8.62, -3.56) * mm});
            skLineSegment(sketch, "E3693", {"start": v(8.62, -3.56) * mm, "end": v(8.72, -3.59) * mm});
            skLineSegment(sketch, "E3694", {"start": v(8.72, -3.59) * mm, "end": v(8.83, -3.62) * mm});
            skLineSegment(sketch, "E3695", {"start": v(8.83, -3.62) * mm, "end": v(8.94, -3.64) * mm});
            skLineSegment(sketch, "E3696", {"start": v(8.94, -3.64) * mm, "end": v(9.05, -3.65) * mm});
            skLineSegment(sketch, "E3697", {"start": v(9.05, -3.65) * mm, "end": v(9.16, -3.66) * mm});
            skLineSegment(sketch, "E3698", {"start": v(9.16, -3.66) * mm, "end": v(9.27, -3.67) * mm});
            skLineSegment(sketch, "E3699", {"start": v(9.27, -3.67) * mm, "end": v(9.38, -3.67) * mm});
            skLineSegment(sketch, "E3700", {"start": v(9.38, -3.67) * mm, "end": v(9.49, -3.67) * mm});
            skLineSegment(sketch, "E3701", {"start": v(9.49, -3.67) * mm, "end": v(9.6, -3.66) * mm});
            skLineSegment(sketch, "E3702", {"start": v(9.6, -3.66) * mm, "end": v(9.71, -3.66) * mm});
            skLineSegment(sketch, "E3703", {"start": v(9.71, -3.66) * mm, "end": v(9.82, -3.65) * mm});
            skLineSegment(sketch, "E3704", {"start": v(9.82, -3.65) * mm, "end": v(9.94, -3.63) * mm});
            skLineSegment(sketch, "E3705", {"start": v(9.94, -3.63) * mm, "end": v(10.05, -3.62) * mm});
            skLineSegment(sketch, "E3706", {"start": v(10.05, -3.62) * mm, "end": v(10.16, -3.6) * mm});
            skLineSegment(sketch, "E3707", {"start": v(10.16, -3.6) * mm, "end": v(10.27, -3.58) * mm});
            skLineSegment(sketch, "E3708", {"start": v(10.27, -3.58) * mm, "end": v(10.36, -3.56) * mm});
            skLineSegment(sketch, "E3709", {"start": v(10.36, -3.56) * mm, "end": v(10.4, -3.45) * mm});
            skLineSegment(sketch, "E3710", {"start": v(10.4, -3.45) * mm, "end": v(10.44, -3.33) * mm});
            skLineSegment(sketch, "E3711", {"start": v(10.44, -3.33) * mm, "end": v(10.48, -3.2) * mm});
            skLineSegment(sketch, "E3712", {"start": v(10.48, -3.2) * mm, "end": v(10.51, -3.1) * mm});
            skLineSegment(sketch, "E3713", {"start": v(10.51, -3.1) * mm, "end": v(10.55, -2.98) * mm});
            skLineSegment(sketch, "E3714", {"start": v(10.55, -2.98) * mm, "end": v(10.56, -2.92) * mm});
            skLineSegment(sketch, "E3715", {"start": v(10.56, -2.92) * mm, "end": v(10.48, -2.83) * mm});
            skLineSegment(sketch, "E3716", {"start": v(10.48, -2.83) * mm, "end": v(10.4, -2.76) * mm});
            skLineSegment(sketch, "E3717", {"start": v(10.4, -2.76) * mm, "end": v(10.31, -2.67) * mm});
            skLineSegment(sketch, "E3718", {"start": v(10.31, -2.67) * mm, "end": v(10.22, -2.6) * mm});
            skLineSegment(sketch, "E3719", {"start": v(10.22, -2.6) * mm, "end": v(10.14, -2.52) * mm});
            skLineSegment(sketch, "E3720", {"start": v(10.14, -2.52) * mm, "end": v(10.04, -2.45) * mm});
            skLineSegment(sketch, "E3721", {"start": v(10.04, -2.45) * mm, "end": v(9.96, -2.38) * mm});
            skLineSegment(sketch, "E3722", {"start": v(9.96, -2.38) * mm, "end": v(9.86, -2.3) * mm});
            skLineSegment(sketch, "E3723", {"start": v(9.86, -2.3) * mm, "end": v(9.77, -2.25) * mm});
            skLineSegment(sketch, "E3724", {"start": v(9.77, -2.25) * mm, "end": v(9.67, -2.18) * mm});
            skLineSegment(sketch, "E3725", {"start": v(9.67, -2.18) * mm, "end": v(9.56, -2.12) * mm});
            skLineSegment(sketch, "E3726", {"start": v(9.56, -2.12) * mm, "end": v(9.45, -2.07) * mm});
            skLineSegment(sketch, "E3727", {"start": v(9.45, -2.07) * mm, "end": v(9.35, -2.02) * mm});
            skLineSegment(sketch, "E3728", {"start": v(9.35, -2.02) * mm, "end": v(9.25, -1.98) * mm});
            skLineSegment(sketch, "E3729", {"start": v(9.25, -1.98) * mm, "end": v(9.13, -1.95) * mm});
            skLineSegment(sketch, "E3730", {"start": v(9.13, -1.95) * mm, "end": v(9.02, -1.91) * mm});
            skLineSegment(sketch, "E3731", {"start": v(9.02, -1.91) * mm, "end": v(8.91, -1.88) * mm});
            skLineSegment(sketch, "E3732", {"start": v(8.91, -1.88) * mm, "end": v(8.81, -1.82) * mm});
            skLineSegment(sketch, "E3733", {"start": v(8.81, -1.82) * mm, "end": v(8.72, -1.75) * mm});
            skLineSegment(sketch, "E3734", {"start": v(8.72, -1.75) * mm, "end": v(8.67, -1.66) * mm});
            skLineSegment(sketch, "E3735", {"start": v(8.67, -1.66) * mm, "end": v(8.68, -1.54) * mm});
            skLineSegment(sketch, "E3736", {"start": v(8.68, -1.54) * mm, "end": v(8.7, -1.42) * mm});
            skLineSegment(sketch, "E3737", {"start": v(8.7, -1.42) * mm, "end": v(8.71, -1.3) * mm});
            skLineSegment(sketch, "E3738", {"start": v(8.71, -1.3) * mm, "end": v(8.73, -1.18) * mm});
            skLineSegment(sketch, "E3739", {"start": v(8.73, -1.18) * mm, "end": v(8.74, -1.06) * mm});
            skLineSegment(sketch, "E3740", {"start": v(8.74, -1.06) * mm, "end": v(8.76, -1) * mm});
            skLineSegment(sketch, "E3741", {"start": v(8.76, -1) * mm, "end": v(8.84, -0.92) * mm});
            skLineSegment(sketch, "E3742", {"start": v(8.84, -0.92) * mm, "end": v(8.94, -0.87) * mm});
            skLineSegment(sketch, "E3743", {"start": v(8.94, -0.87) * mm, "end": v(9.04, -0.85) * mm});
            skLineSegment(sketch, "E3744", {"start": v(9.04, -0.85) * mm, "end": v(9.16, -0.85) * mm});
            skLineSegment(sketch, "E3745", {"start": v(9.16, -0.85) * mm, "end": v(9.28, -0.85) * mm});
            skLineSegment(sketch, "E3746", {"start": v(9.28, -0.85) * mm, "end": v(9.36, -0.85) * mm});
            skCircle(sketch, "E3747", {"center": v(0, 0) * mm, "radius": 5.5 * mm});
            skSolve(sketch);
        }
        {
            var Q0;
            Q0=qSketchRegion(id+"F10",true);
            extrude(context, id + "F11", {"entities" : qUnion([Q0]), "endBound" : BoundingType.SYMMETRIC, "depth" : 5 * mm, "offsetDistance" : 25 * mm});
        }
        {
            var Q0;
            Q0=makeQuery(id+"F11.opExtrude","SWEPT_BODY",BODY,{"disambiguationData":[OSD([sQuery(id+"F10.wireOp",EDGE,"E2624"),sQuery(id+"F10.wireOp",EDGE,"E2625"),sQuery(id+"F10.wireOp",EDGE,"E2626"),sQuery(id+"F10.wireOp",EDGE,"E2627"),sQuery(id+"F10.wireOp",EDGE,"E2628"),sQuery(id+"F10.wireOp",EDGE,"E2629"),sQuery(id+"F10.wireOp",EDGE,"E2630"),sQuery(id+"F10.wireOp",EDGE,"E2631"),sQuery(id+"F10.wireOp",EDGE,"E2632"),sQuery(id+"F10.wireOp",EDGE,"E2633"),sQuery(id+"F10.wireOp",EDGE,"E2634"),sQuery(id+"F10.wireOp",EDGE,"E2635"),sQuery(id+"F10.wireOp",EDGE,"E2636"),sQuery(id+"F10.wireOp",EDGE,"E2637"),sQuery(id+"F10.wireOp",EDGE,"E2638"),sQuery(id+"F10.wireOp",EDGE,"E2639"),sQuery(id+"F10.wireOp",EDGE,"E2640"),sQuery(id+"F10.wireOp",EDGE,"E2641"),sQuery(id+"F10.wireOp",EDGE,"E2642"),sQuery(id+"F10.wireOp",EDGE,"E2643"),sQuery(id+"F10.wireOp",EDGE,"E2644"),sQuery(id+"F10.wireOp",EDGE,"E2645"),sQuery(id+"F10.wireOp",EDGE,"E2646"),sQuery(id+"F10.wireOp",EDGE,"E2647"),sQuery(id+"F10.wireOp",EDGE,"E2648"),sQuery(id+"F10.wireOp",EDGE,"E2649"),sQuery(id+"F10.wireOp",EDGE,"E2650"),sQuery(id+"F10.wireOp",EDGE,"E2651"),sQuery(id+"F10.wireOp",EDGE,"E2652"),sQuery(id+"F10.wireOp",EDGE,"E2653"),sQuery(id+"F10.wireOp",EDGE,"E2654"),sQuery(id+"F10.wireOp",EDGE,"E2655"),sQuery(id+"F10.wireOp",EDGE,"E2656"),sQuery(id+"F10.wireOp",EDGE,"E2657"),sQuery(id+"F10.wireOp",EDGE,"E2658"),sQuery(id+"F10.wireOp",EDGE,"E2659"),sQuery(id+"F10.wireOp",EDGE,"E2660"),sQuery(id+"F10.wireOp",EDGE,"E2661"),sQuery(id+"F10.wireOp",EDGE,"E2662"),sQuery(id+"F10.wireOp",EDGE,"E2663"),sQuery(id+"F10.wireOp",EDGE,"E2664"),sQuery(id+"F10.wireOp",EDGE,"E2665"),sQuery(id+"F10.wireOp",EDGE,"E2666"),sQuery(id+"F10.wireOp",EDGE,"E2667"),sQuery(id+"F10.wireOp",EDGE,"E2668"),sQuery(id+"F10.wireOp",EDGE,"E2669"),sQuery(id+"F10.wireOp",EDGE,"E2670"),sQuery(id+"F10.wireOp",EDGE,"E2671"),sQuery(id+"F10.wireOp",EDGE,"E2672"),sQuery(id+"F10.wireOp",EDGE,"E2673"),sQuery(id+"F10.wireOp",EDGE,"E2674"),sQuery(id+"F10.wireOp",EDGE,"E2675"),sQuery(id+"F10.wireOp",EDGE,"E2676"),sQuery(id+"F10.wireOp",EDGE,"E2677"),sQuery(id+"F10.wireOp",EDGE,"E2678"),sQuery(id+"F10.wireOp",EDGE,"E2679"),sQuery(id+"F10.wireOp",EDGE,"E2680"),sQuery(id+"F10.wireOp",EDGE,"E2681"),sQuery(id+"F10.wireOp",EDGE,"E2682"),sQuery(id+"F10.wireOp",EDGE,"E2683"),sQuery(id+"F10.wireOp",EDGE,"E2684"),sQuery(id+"F10.wireOp",EDGE,"E2685"),sQuery(id+"F10.wireOp",EDGE,"E2686"),sQuery(id+"F10.wireOp",EDGE,"E2687"),sQuery(id+"F10.wireOp",EDGE,"E2688"),sQuery(id+"F10.wireOp",EDGE,"E2689"),sQuery(id+"F10.wireOp",EDGE,"E2690"),sQuery(id+"F10.wireOp",EDGE,"E2691"),sQuery(id+"F10.wireOp",EDGE,"E2692"),sQuery(id+"F10.wireOp",EDGE,"E2693"),sQuery(id+"F10.wireOp",EDGE,"E2694"),sQuery(id+"F10.wireOp",EDGE,"E2695"),sQuery(id+"F10.wireOp",EDGE,"E2696"),sQuery(id+"F10.wireOp",EDGE,"E2697"),sQuery(id+"F10.wireOp",EDGE,"E2698"),sQuery(id+"F10.wireOp",EDGE,"E2699"),sQuery(id+"F10.wireOp",EDGE,"E2700"),sQuery(id+"F10.wireOp",EDGE,"E2701"),sQuery(id+"F10.wireOp",EDGE,"E2702"),sQuery(id+"F10.wireOp",EDGE,"E2703"),sQuery(id+"F10.wireOp",EDGE,"E2704"),sQuery(id+"F10.wireOp",EDGE,"E2705"),sQuery(id+"F10.wireOp",EDGE,"E2706"),sQuery(id+"F10.wireOp",EDGE,"E2707"),sQuery(id+"F10.wireOp",EDGE,"E2708"),sQuery(id+"F10.wireOp",EDGE,"E2709"),sQuery(id+"F10.wireOp",EDGE,"E2710"),sQuery(id+"F10.wireOp",EDGE,"E2711"),sQuery(id+"F10.wireOp",EDGE,"E2712"),sQuery(id+"F10.wireOp",EDGE,"E2713"),sQuery(id+"F10.wireOp",EDGE,"E2714"),sQuery(id+"F10.wireOp",EDGE,"E2715"),sQuery(id+"F10.wireOp",EDGE,"E2716"),sQuery(id+"F10.wireOp",EDGE,"E2717"),sQuery(id+"F10.wireOp",EDGE,"E2718"),sQuery(id+"F10.wireOp",EDGE,"E2719"),sQuery(id+"F10.wireOp",EDGE,"E2720"),sQuery(id+"F10.wireOp",EDGE,"E2721"),sQuery(id+"F10.wireOp",EDGE,"E2722"),sQuery(id+"F10.wireOp",EDGE,"E2723"),sQuery(id+"F10.wireOp",EDGE,"E2724"),sQuery(id+"F10.wireOp",EDGE,"E2725"),sQuery(id+"F10.wireOp",EDGE,"E2726"),sQuery(id+"F10.wireOp",EDGE,"E2727"),sQuery(id+"F10.wireOp",EDGE,"E2728"),sQuery(id+"F10.wireOp",EDGE,"E2729"),sQuery(id+"F10.wireOp",EDGE,"E2730"),sQuery(id+"F10.wireOp",EDGE,"E2731"),sQuery(id+"F10.wireOp",EDGE,"E2732"),sQuery(id+"F10.wireOp",EDGE,"E2733"),sQuery(id+"F10.wireOp",EDGE,"E2734"),sQuery(id+"F10.wireOp",EDGE,"E2735"),sQuery(id+"F10.wireOp",EDGE,"E2736"),sQuery(id+"F10.wireOp",EDGE,"E2737"),sQuery(id+"F10.wireOp",EDGE,"E2738"),sQuery(id+"F10.wireOp",EDGE,"E2739"),sQuery(id+"F10.wireOp",EDGE,"E2740"),sQuery(id+"F10.wireOp",EDGE,"E2741"),sQuery(id+"F10.wireOp",EDGE,"E2742"),sQuery(id+"F10.wireOp",EDGE,"E2743"),sQuery(id+"F10.wireOp",EDGE,"E2744"),sQuery(id+"F10.wireOp",EDGE,"E2745"),sQuery(id+"F10.wireOp",EDGE,"E2746"),sQuery(id+"F10.wireOp",EDGE,"E2747"),sQuery(id+"F10.wireOp",EDGE,"E2748"),sQuery(id+"F10.wireOp",EDGE,"E2749"),sQuery(id+"F10.wireOp",EDGE,"E2750"),sQuery(id+"F10.wireOp",EDGE,"E2751"),sQuery(id+"F10.wireOp",EDGE,"E2752"),sQuery(id+"F10.wireOp",EDGE,"E2753"),sQuery(id+"F10.wireOp",EDGE,"E2754"),sQuery(id+"F10.wireOp",EDGE,"E2755"),sQuery(id+"F10.wireOp",EDGE,"E2756"),sQuery(id+"F10.wireOp",EDGE,"E2757"),sQuery(id+"F10.wireOp",EDGE,"E2758"),sQuery(id+"F10.wireOp",EDGE,"E2759"),sQuery(id+"F10.wireOp",EDGE,"E2760"),sQuery(id+"F10.wireOp",EDGE,"E2761"),sQuery(id+"F10.wireOp",EDGE,"E2762"),sQuery(id+"F10.wireOp",EDGE,"E2763"),sQuery(id+"F10.wireOp",EDGE,"E2764"),sQuery(id+"F10.wireOp",EDGE,"E2765"),sQuery(id+"F10.wireOp",EDGE,"E2766"),sQuery(id+"F10.wireOp",EDGE,"E2767"),sQuery(id+"F10.wireOp",EDGE,"E2768"),sQuery(id+"F10.wireOp",EDGE,"E2769"),sQuery(id+"F10.wireOp",EDGE,"E2770"),sQuery(id+"F10.wireOp",EDGE,"E2771"),sQuery(id+"F10.wireOp",EDGE,"E2772"),sQuery(id+"F10.wireOp",EDGE,"E2773"),sQuery(id+"F10.wireOp",EDGE,"E2774"),sQuery(id+"F10.wireOp",EDGE,"E2775"),sQuery(id+"F10.wireOp",EDGE,"E2776"),sQuery(id+"F10.wireOp",EDGE,"E2777"),sQuery(id+"F10.wireOp",EDGE,"E2778"),sQuery(id+"F10.wireOp",EDGE,"E2779"),sQuery(id+"F10.wireOp",EDGE,"E2780"),sQuery(id+"F10.wireOp",EDGE,"E2781"),sQuery(id+"F10.wireOp",EDGE,"E2782"),sQuery(id+"F10.wireOp",EDGE,"E2783"),sQuery(id+"F10.wireOp",EDGE,"E2784"),sQuery(id+"F10.wireOp",EDGE,"E2785"),sQuery(id+"F10.wireOp",EDGE,"E2786"),sQuery(id+"F10.wireOp",EDGE,"E2787"),sQuery(id+"F10.wireOp",EDGE,"E2788"),sQuery(id+"F10.wireOp",EDGE,"E2789"),sQuery(id+"F10.wireOp",EDGE,"E2790"),sQuery(id+"F10.wireOp",EDGE,"E2791"),sQuery(id+"F10.wireOp",EDGE,"E2792"),sQuery(id+"F10.wireOp",EDGE,"E2793"),sQuery(id+"F10.wireOp",EDGE,"E2794"),sQuery(id+"F10.wireOp",EDGE,"E2795"),sQuery(id+"F10.wireOp",EDGE,"E2796"),sQuery(id+"F10.wireOp",EDGE,"E2797"),sQuery(id+"F10.wireOp",EDGE,"E2798"),sQuery(id+"F10.wireOp",EDGE,"E2799"),sQuery(id+"F10.wireOp",EDGE,"E2800"),sQuery(id+"F10.wireOp",EDGE,"E2801"),sQuery(id+"F10.wireOp",EDGE,"E2802"),sQuery(id+"F10.wireOp",EDGE,"E2803"),sQuery(id+"F10.wireOp",EDGE,"E2804"),sQuery(id+"F10.wireOp",EDGE,"E2805"),sQuery(id+"F10.wireOp",EDGE,"E2806"),sQuery(id+"F10.wireOp",EDGE,"E2807"),sQuery(id+"F10.wireOp",EDGE,"E2808"),sQuery(id+"F10.wireOp",EDGE,"E2809"),sQuery(id+"F10.wireOp",EDGE,"E2810"),sQuery(id+"F10.wireOp",EDGE,"E2811"),sQuery(id+"F10.wireOp",EDGE,"E2812"),sQuery(id+"F10.wireOp",EDGE,"E2813"),sQuery(id+"F10.wireOp",EDGE,"E2814"),sQuery(id+"F10.wireOp",EDGE,"E2815"),sQuery(id+"F10.wireOp",EDGE,"E2816"),sQuery(id+"F10.wireOp",EDGE,"E2817"),sQuery(id+"F10.wireOp",EDGE,"E2818"),sQuery(id+"F10.wireOp",EDGE,"E2819"),sQuery(id+"F10.wireOp",EDGE,"E2820"),sQuery(id+"F10.wireOp",EDGE,"E2821"),sQuery(id+"F10.wireOp",EDGE,"E2822"),sQuery(id+"F10.wireOp",EDGE,"E2823"),sQuery(id+"F10.wireOp",EDGE,"E2824"),sQuery(id+"F10.wireOp",EDGE,"E2825"),sQuery(id+"F10.wireOp",EDGE,"E2826"),sQuery(id+"F10.wireOp",EDGE,"E2827"),sQuery(id+"F10.wireOp",EDGE,"E2828"),sQuery(id+"F10.wireOp",EDGE,"E2829"),sQuery(id+"F10.wireOp",EDGE,"E2830"),sQuery(id+"F10.wireOp",EDGE,"E2831"),sQuery(id+"F10.wireOp",EDGE,"E2832"),sQuery(id+"F10.wireOp",EDGE,"E2833"),sQuery(id+"F10.wireOp",EDGE,"E2834"),sQuery(id+"F10.wireOp",EDGE,"E2835"),sQuery(id+"F10.wireOp",EDGE,"E2836"),sQuery(id+"F10.wireOp",EDGE,"E2837"),sQuery(id+"F10.wireOp",EDGE,"E2838"),sQuery(id+"F10.wireOp",EDGE,"E2839"),sQuery(id+"F10.wireOp",EDGE,"E2840"),sQuery(id+"F10.wireOp",EDGE,"E2841"),sQuery(id+"F10.wireOp",EDGE,"E2842"),sQuery(id+"F10.wireOp",EDGE,"E2843"),sQuery(id+"F10.wireOp",EDGE,"E2844"),sQuery(id+"F10.wireOp",EDGE,"E2845"),sQuery(id+"F10.wireOp",EDGE,"E2846"),sQuery(id+"F10.wireOp",EDGE,"E2847"),sQuery(id+"F10.wireOp",EDGE,"E2848"),sQuery(id+"F10.wireOp",EDGE,"E2849"),sQuery(id+"F10.wireOp",EDGE,"E2850"),sQuery(id+"F10.wireOp",EDGE,"E2851"),sQuery(id+"F10.wireOp",EDGE,"E2852"),sQuery(id+"F10.wireOp",EDGE,"E2853"),sQuery(id+"F10.wireOp",EDGE,"E2854"),sQuery(id+"F10.wireOp",EDGE,"E2855"),sQuery(id+"F10.wireOp",EDGE,"E2856"),sQuery(id+"F10.wireOp",EDGE,"E2857"),sQuery(id+"F10.wireOp",EDGE,"E2858"),sQuery(id+"F10.wireOp",EDGE,"E2859"),sQuery(id+"F10.wireOp",EDGE,"E2860"),sQuery(id+"F10.wireOp",EDGE,"E2861"),sQuery(id+"F10.wireOp",EDGE,"E2862"),sQuery(id+"F10.wireOp",EDGE,"E2863"),sQuery(id+"F10.wireOp",EDGE,"E2864"),sQuery(id+"F10.wireOp",EDGE,"E2865"),sQuery(id+"F10.wireOp",EDGE,"E2866"),sQuery(id+"F10.wireOp",EDGE,"E2867"),sQuery(id+"F10.wireOp",EDGE,"E2868"),sQuery(id+"F10.wireOp",EDGE,"E2869"),sQuery(id+"F10.wireOp",EDGE,"E2870"),sQuery(id+"F10.wireOp",EDGE,"E2871"),sQuery(id+"F10.wireOp",EDGE,"E2872"),sQuery(id+"F10.wireOp",EDGE,"E2873"),sQuery(id+"F10.wireOp",EDGE,"E2874"),sQuery(id+"F10.wireOp",EDGE,"E2875"),sQuery(id+"F10.wireOp",EDGE,"E2876"),sQuery(id+"F10.wireOp",EDGE,"E2877"),sQuery(id+"F10.wireOp",EDGE,"E2878"),sQuery(id+"F10.wireOp",EDGE,"E2879"),sQuery(id+"F10.wireOp",EDGE,"E2880"),sQuery(id+"F10.wireOp",EDGE,"E2881"),sQuery(id+"F10.wireOp",EDGE,"E2882"),sQuery(id+"F10.wireOp",EDGE,"E2883"),sQuery(id+"F10.wireOp",EDGE,"E2884"),sQuery(id+"F10.wireOp",EDGE,"E2885"),sQuery(id+"F10.wireOp",EDGE,"E2886"),sQuery(id+"F10.wireOp",EDGE,"E2887"),sQuery(id+"F10.wireOp",EDGE,"E2888"),sQuery(id+"F10.wireOp",EDGE,"E2889"),sQuery(id+"F10.wireOp",EDGE,"E2890"),sQuery(id+"F10.wireOp",EDGE,"E2891"),sQuery(id+"F10.wireOp",EDGE,"E2892"),sQuery(id+"F10.wireOp",EDGE,"E2893"),sQuery(id+"F10.wireOp",EDGE,"E2894"),sQuery(id+"F10.wireOp",EDGE,"E2895"),sQuery(id+"F10.wireOp",EDGE,"E2896"),sQuery(id+"F10.wireOp",EDGE,"E2897"),sQuery(id+"F10.wireOp",EDGE,"E2898"),sQuery(id+"F10.wireOp",EDGE,"E2899"),sQuery(id+"F10.wireOp",EDGE,"E2900"),sQuery(id+"F10.wireOp",EDGE,"E2901"),sQuery(id+"F10.wireOp",EDGE,"E2902"),sQuery(id+"F10.wireOp",EDGE,"E2903"),sQuery(id+"F10.wireOp",EDGE,"E2904"),sQuery(id+"F10.wireOp",EDGE,"E2905"),sQuery(id+"F10.wireOp",EDGE,"E2906"),sQuery(id+"F10.wireOp",EDGE,"E2907"),sQuery(id+"F10.wireOp",EDGE,"E2908"),sQuery(id+"F10.wireOp",EDGE,"E2909"),sQuery(id+"F10.wireOp",EDGE,"E2910"),sQuery(id+"F10.wireOp",EDGE,"E2911"),sQuery(id+"F10.wireOp",EDGE,"E2912"),sQuery(id+"F10.wireOp",EDGE,"E2913"),sQuery(id+"F10.wireOp",EDGE,"E2914"),sQuery(id+"F10.wireOp",EDGE,"E2915"),sQuery(id+"F10.wireOp",EDGE,"E2916"),sQuery(id+"F10.wireOp",EDGE,"E2917"),sQuery(id+"F10.wireOp",EDGE,"E2918"),sQuery(id+"F10.wireOp",EDGE,"E2919"),sQuery(id+"F10.wireOp",EDGE,"E2920"),sQuery(id+"F10.wireOp",EDGE,"E2921"),sQuery(id+"F10.wireOp",EDGE,"E2922"),sQuery(id+"F10.wireOp",EDGE,"E2923"),sQuery(id+"F10.wireOp",EDGE,"E2924"),sQuery(id+"F10.wireOp",EDGE,"E2925"),sQuery(id+"F10.wireOp",EDGE,"E2926"),sQuery(id+"F10.wireOp",EDGE,"E2927"),sQuery(id+"F10.wireOp",EDGE,"E2928"),sQuery(id+"F10.wireOp",EDGE,"E2929"),sQuery(id+"F10.wireOp",EDGE,"E2930"),sQuery(id+"F10.wireOp",EDGE,"E2931"),sQuery(id+"F10.wireOp",EDGE,"E2932"),sQuery(id+"F10.wireOp",EDGE,"E2933"),sQuery(id+"F10.wireOp",EDGE,"E2934"),sQuery(id+"F10.wireOp",EDGE,"E2935"),sQuery(id+"F10.wireOp",EDGE,"E2936"),sQuery(id+"F10.wireOp",EDGE,"E2937"),sQuery(id+"F10.wireOp",EDGE,"E2938"),sQuery(id+"F10.wireOp",EDGE,"E2939"),sQuery(id+"F10.wireOp",EDGE,"E2940"),sQuery(id+"F10.wireOp",EDGE,"E2941"),sQuery(id+"F10.wireOp",EDGE,"E2942"),sQuery(id+"F10.wireOp",EDGE,"E2943"),sQuery(id+"F10.wireOp",EDGE,"E2944"),sQuery(id+"F10.wireOp",EDGE,"E2945"),sQuery(id+"F10.wireOp",EDGE,"E2946"),sQuery(id+"F10.wireOp",EDGE,"E2947"),sQuery(id+"F10.wireOp",EDGE,"E2948"),sQuery(id+"F10.wireOp",EDGE,"E2949"),sQuery(id+"F10.wireOp",EDGE,"E2950"),sQuery(id+"F10.wireOp",EDGE,"E2951"),sQuery(id+"F10.wireOp",EDGE,"E2952"),sQuery(id+"F10.wireOp",EDGE,"E2953"),sQuery(id+"F10.wireOp",EDGE,"E2954"),sQuery(id+"F10.wireOp",EDGE,"E2955"),sQuery(id+"F10.wireOp",EDGE,"E2956"),sQuery(id+"F10.wireOp",EDGE,"E2957"),sQuery(id+"F10.wireOp",EDGE,"E2958"),sQuery(id+"F10.wireOp",EDGE,"E2959"),sQuery(id+"F10.wireOp",EDGE,"E2960"),sQuery(id+"F10.wireOp",EDGE,"E2961"),sQuery(id+"F10.wireOp",EDGE,"E2962"),sQuery(id+"F10.wireOp",EDGE,"E2963"),sQuery(id+"F10.wireOp",EDGE,"E2964"),sQuery(id+"F10.wireOp",EDGE,"E2965"),sQuery(id+"F10.wireOp",EDGE,"E2966"),sQuery(id+"F10.wireOp",EDGE,"E2967"),sQuery(id+"F10.wireOp",EDGE,"E2968"),sQuery(id+"F10.wireOp",EDGE,"E2969"),sQuery(id+"F10.wireOp",EDGE,"E2970"),sQuery(id+"F10.wireOp",EDGE,"E2971"),sQuery(id+"F10.wireOp",EDGE,"E2972"),sQuery(id+"F10.wireOp",EDGE,"E2973"),sQuery(id+"F10.wireOp",EDGE,"E2974"),sQuery(id+"F10.wireOp",EDGE,"E2975"),sQuery(id+"F10.wireOp",EDGE,"E2976"),sQuery(id+"F10.wireOp",EDGE,"E2977"),sQuery(id+"F10.wireOp",EDGE,"E2978"),sQuery(id+"F10.wireOp",EDGE,"E2979"),sQuery(id+"F10.wireOp",EDGE,"E2980"),sQuery(id+"F10.wireOp",EDGE,"E2981"),sQuery(id+"F10.wireOp",EDGE,"E2982"),sQuery(id+"F10.wireOp",EDGE,"E2983"),sQuery(id+"F10.wireOp",EDGE,"E2984"),sQuery(id+"F10.wireOp",EDGE,"E2985"),sQuery(id+"F10.wireOp",EDGE,"E2986"),sQuery(id+"F10.wireOp",EDGE,"E2987"),sQuery(id+"F10.wireOp",EDGE,"E2988"),sQuery(id+"F10.wireOp",EDGE,"E2989"),sQuery(id+"F10.wireOp",EDGE,"E2990"),sQuery(id+"F10.wireOp",EDGE,"E2991"),sQuery(id+"F10.wireOp",EDGE,"E2992"),sQuery(id+"F10.wireOp",EDGE,"E2993"),sQuery(id+"F10.wireOp",EDGE,"E2994"),sQuery(id+"F10.wireOp",EDGE,"E2995"),sQuery(id+"F10.wireOp",EDGE,"E2996"),sQuery(id+"F10.wireOp",EDGE,"E2997"),sQuery(id+"F10.wireOp",EDGE,"E2998"),sQuery(id+"F10.wireOp",EDGE,"E2999"),sQuery(id+"F10.wireOp",EDGE,"E3000"),sQuery(id+"F10.wireOp",EDGE,"E3001"),sQuery(id+"F10.wireOp",EDGE,"E3002"),sQuery(id+"F10.wireOp",EDGE,"E3003"),sQuery(id+"F10.wireOp",EDGE,"E3004"),sQuery(id+"F10.wireOp",EDGE,"E3005"),sQuery(id+"F10.wireOp",EDGE,"E3006"),sQuery(id+"F10.wireOp",EDGE,"E3007"),sQuery(id+"F10.wireOp",EDGE,"E3008"),sQuery(id+"F10.wireOp",EDGE,"E3009"),sQuery(id+"F10.wireOp",EDGE,"E3010"),sQuery(id+"F10.wireOp",EDGE,"E3011"),sQuery(id+"F10.wireOp",EDGE,"E3012"),sQuery(id+"F10.wireOp",EDGE,"E3013"),sQuery(id+"F10.wireOp",EDGE,"E3014"),sQuery(id+"F10.wireOp",EDGE,"E3015"),sQuery(id+"F10.wireOp",EDGE,"E3016"),sQuery(id+"F10.wireOp",EDGE,"E3017"),sQuery(id+"F10.wireOp",EDGE,"E3018"),sQuery(id+"F10.wireOp",EDGE,"E3019"),sQuery(id+"F10.wireOp",EDGE,"E3020"),sQuery(id+"F10.wireOp",EDGE,"E3021"),sQuery(id+"F10.wireOp",EDGE,"E3022"),sQuery(id+"F10.wireOp",EDGE,"E3023"),sQuery(id+"F10.wireOp",EDGE,"E3024"),sQuery(id+"F10.wireOp",EDGE,"E3025"),sQuery(id+"F10.wireOp",EDGE,"E3026"),sQuery(id+"F10.wireOp",EDGE,"E3027"),sQuery(id+"F10.wireOp",EDGE,"E3028"),sQuery(id+"F10.wireOp",EDGE,"E3029"),sQuery(id+"F10.wireOp",EDGE,"E3030"),sQuery(id+"F10.wireOp",EDGE,"E3031"),sQuery(id+"F10.wireOp",EDGE,"E3032"),sQuery(id+"F10.wireOp",EDGE,"E3033"),sQuery(id+"F10.wireOp",EDGE,"E3034"),sQuery(id+"F10.wireOp",EDGE,"E3035"),sQuery(id+"F10.wireOp",EDGE,"E3036"),sQuery(id+"F10.wireOp",EDGE,"E3037"),sQuery(id+"F10.wireOp",EDGE,"E3038"),sQuery(id+"F10.wireOp",EDGE,"E3039"),sQuery(id+"F10.wireOp",EDGE,"E3040"),sQuery(id+"F10.wireOp",EDGE,"E3041"),sQuery(id+"F10.wireOp",EDGE,"E3042"),sQuery(id+"F10.wireOp",EDGE,"E3043"),sQuery(id+"F10.wireOp",EDGE,"E3044"),sQuery(id+"F10.wireOp",EDGE,"E3045"),sQuery(id+"F10.wireOp",EDGE,"E3046"),sQuery(id+"F10.wireOp",EDGE,"E3047"),sQuery(id+"F10.wireOp",EDGE,"E3048"),sQuery(id+"F10.wireOp",EDGE,"E3049"),sQuery(id+"F10.wireOp",EDGE,"E3050"),sQuery(id+"F10.wireOp",EDGE,"E3051"),sQuery(id+"F10.wireOp",EDGE,"E3052"),sQuery(id+"F10.wireOp",EDGE,"E3053"),sQuery(id+"F10.wireOp",EDGE,"E3054"),sQuery(id+"F10.wireOp",EDGE,"E3055"),sQuery(id+"F10.wireOp",EDGE,"E3056"),sQuery(id+"F10.wireOp",EDGE,"E3057"),sQuery(id+"F10.wireOp",EDGE,"E3058"),sQuery(id+"F10.wireOp",EDGE,"E3059"),sQuery(id+"F10.wireOp",EDGE,"E3060"),sQuery(id+"F10.wireOp",EDGE,"E3061"),sQuery(id+"F10.wireOp",EDGE,"E3062"),sQuery(id+"F10.wireOp",EDGE,"E3063"),sQuery(id+"F10.wireOp",EDGE,"E3064"),sQuery(id+"F10.wireOp",EDGE,"E3065"),sQuery(id+"F10.wireOp",EDGE,"E3066"),sQuery(id+"F10.wireOp",EDGE,"E3067"),sQuery(id+"F10.wireOp",EDGE,"E3068"),sQuery(id+"F10.wireOp",EDGE,"E3069"),sQuery(id+"F10.wireOp",EDGE,"E3070"),sQuery(id+"F10.wireOp",EDGE,"E3071"),sQuery(id+"F10.wireOp",EDGE,"E3072"),sQuery(id+"F10.wireOp",EDGE,"E3073"),sQuery(id+"F10.wireOp",EDGE,"E3074"),sQuery(id+"F10.wireOp",EDGE,"E3075"),sQuery(id+"F10.wireOp",EDGE,"E3076"),sQuery(id+"F10.wireOp",EDGE,"E3077"),sQuery(id+"F10.wireOp",EDGE,"E3078"),sQuery(id+"F10.wireOp",EDGE,"E3079"),sQuery(id+"F10.wireOp",EDGE,"E3080"),sQuery(id+"F10.wireOp",EDGE,"E3081"),sQuery(id+"F10.wireOp",EDGE,"E3082"),sQuery(id+"F10.wireOp",EDGE,"E3083"),sQuery(id+"F10.wireOp",EDGE,"E3084"),sQuery(id+"F10.wireOp",EDGE,"E3085"),sQuery(id+"F10.wireOp",EDGE,"E3086"),sQuery(id+"F10.wireOp",EDGE,"E3087"),sQuery(id+"F10.wireOp",EDGE,"E3088"),sQuery(id+"F10.wireOp",EDGE,"E3089"),sQuery(id+"F10.wireOp",EDGE,"E3090"),sQuery(id+"F10.wireOp",EDGE,"E3091"),sQuery(id+"F10.wireOp",EDGE,"E3092"),sQuery(id+"F10.wireOp",EDGE,"E3093"),sQuery(id+"F10.wireOp",EDGE,"E3094"),sQuery(id+"F10.wireOp",EDGE,"E3095"),sQuery(id+"F10.wireOp",EDGE,"E3096"),sQuery(id+"F10.wireOp",EDGE,"E3097"),sQuery(id+"F10.wireOp",EDGE,"E3098"),sQuery(id+"F10.wireOp",EDGE,"E3099"),sQuery(id+"F10.wireOp",EDGE,"E3100"),sQuery(id+"F10.wireOp",EDGE,"E3101"),sQuery(id+"F10.wireOp",EDGE,"E3102"),sQuery(id+"F10.wireOp",EDGE,"E3103"),sQuery(id+"F10.wireOp",EDGE,"E3104"),sQuery(id+"F10.wireOp",EDGE,"E3105"),sQuery(id+"F10.wireOp",EDGE,"E3106"),sQuery(id+"F10.wireOp",EDGE,"E3107"),sQuery(id+"F10.wireOp",EDGE,"E3108"),sQuery(id+"F10.wireOp",EDGE,"E3109"),sQuery(id+"F10.wireOp",EDGE,"E3110"),sQuery(id+"F10.wireOp",EDGE,"E3111"),sQuery(id+"F10.wireOp",EDGE,"E3112"),sQuery(id+"F10.wireOp",EDGE,"E3113"),sQuery(id+"F10.wireOp",EDGE,"E3114"),sQuery(id+"F10.wireOp",EDGE,"E3115"),sQuery(id+"F10.wireOp",EDGE,"E3116"),sQuery(id+"F10.wireOp",EDGE,"E3117"),sQuery(id+"F10.wireOp",EDGE,"E3118"),sQuery(id+"F10.wireOp",EDGE,"E3119"),sQuery(id+"F10.wireOp",EDGE,"E3120"),sQuery(id+"F10.wireOp",EDGE,"E3121"),sQuery(id+"F10.wireOp",EDGE,"E3122"),sQuery(id+"F10.wireOp",EDGE,"E3123"),sQuery(id+"F10.wireOp",EDGE,"E3124"),sQuery(id+"F10.wireOp",EDGE,"E3125"),sQuery(id+"F10.wireOp",EDGE,"E3126"),sQuery(id+"F10.wireOp",EDGE,"E3127"),sQuery(id+"F10.wireOp",EDGE,"E3128"),sQuery(id+"F10.wireOp",EDGE,"E3129"),sQuery(id+"F10.wireOp",EDGE,"E3130"),sQuery(id+"F10.wireOp",EDGE,"E3131"),sQuery(id+"F10.wireOp",EDGE,"E3132"),sQuery(id+"F10.wireOp",EDGE,"E3133"),sQuery(id+"F10.wireOp",EDGE,"E3134"),sQuery(id+"F10.wireOp",EDGE,"E3135"),sQuery(id+"F10.wireOp",EDGE,"E3136"),sQuery(id+"F10.wireOp",EDGE,"E3137"),sQuery(id+"F10.wireOp",EDGE,"E3138"),sQuery(id+"F10.wireOp",EDGE,"E3139"),sQuery(id+"F10.wireOp",EDGE,"E3140"),sQuery(id+"F10.wireOp",EDGE,"E3141"),sQuery(id+"F10.wireOp",EDGE,"E3142"),sQuery(id+"F10.wireOp",EDGE,"E3143"),sQuery(id+"F10.wireOp",EDGE,"E3144"),sQuery(id+"F10.wireOp",EDGE,"E3145"),sQuery(id+"F10.wireOp",EDGE,"E3146"),sQuery(id+"F10.wireOp",EDGE,"E3147"),sQuery(id+"F10.wireOp",EDGE,"E3148"),sQuery(id+"F10.wireOp",EDGE,"E3149"),sQuery(id+"F10.wireOp",EDGE,"E3150"),sQuery(id+"F10.wireOp",EDGE,"E3151"),sQuery(id+"F10.wireOp",EDGE,"E3152"),sQuery(id+"F10.wireOp",EDGE,"E3153"),sQuery(id+"F10.wireOp",EDGE,"E3154"),sQuery(id+"F10.wireOp",EDGE,"E3155"),sQuery(id+"F10.wireOp",EDGE,"E3156"),sQuery(id+"F10.wireOp",EDGE,"E3157"),sQuery(id+"F10.wireOp",EDGE,"E3158"),sQuery(id+"F10.wireOp",EDGE,"E3159"),sQuery(id+"F10.wireOp",EDGE,"E3160"),sQuery(id+"F10.wireOp",EDGE,"E3161"),sQuery(id+"F10.wireOp",EDGE,"E3162"),sQuery(id+"F10.wireOp",EDGE,"E3163"),sQuery(id+"F10.wireOp",EDGE,"E3164"),sQuery(id+"F10.wireOp",EDGE,"E3165"),sQuery(id+"F10.wireOp",EDGE,"E3166"),sQuery(id+"F10.wireOp",EDGE,"E3167"),sQuery(id+"F10.wireOp",EDGE,"E3168"),sQuery(id+"F10.wireOp",EDGE,"E3169"),sQuery(id+"F10.wireOp",EDGE,"E3170"),sQuery(id+"F10.wireOp",EDGE,"E3171"),sQuery(id+"F10.wireOp",EDGE,"E3172"),sQuery(id+"F10.wireOp",EDGE,"E3173"),sQuery(id+"F10.wireOp",EDGE,"E3174"),sQuery(id+"F10.wireOp",EDGE,"E3175"),sQuery(id+"F10.wireOp",EDGE,"E3176"),sQuery(id+"F10.wireOp",EDGE,"E3177"),sQuery(id+"F10.wireOp",EDGE,"E3178"),sQuery(id+"F10.wireOp",EDGE,"E3179"),sQuery(id+"F10.wireOp",EDGE,"E3180"),sQuery(id+"F10.wireOp",EDGE,"E3181"),sQuery(id+"F10.wireOp",EDGE,"E3182"),sQuery(id+"F10.wireOp",EDGE,"E3183"),sQuery(id+"F10.wireOp",EDGE,"E3184"),sQuery(id+"F10.wireOp",EDGE,"E3185"),sQuery(id+"F10.wireOp",EDGE,"E3186"),sQuery(id+"F10.wireOp",EDGE,"E3187"),sQuery(id+"F10.wireOp",EDGE,"E3188"),sQuery(id+"F10.wireOp",EDGE,"E3189"),sQuery(id+"F10.wireOp",EDGE,"E3190"),sQuery(id+"F10.wireOp",EDGE,"E3191"),sQuery(id+"F10.wireOp",EDGE,"E3192"),sQuery(id+"F10.wireOp",EDGE,"E3193"),sQuery(id+"F10.wireOp",EDGE,"E3194"),sQuery(id+"F10.wireOp",EDGE,"E3195"),sQuery(id+"F10.wireOp",EDGE,"E3196"),sQuery(id+"F10.wireOp",EDGE,"E3197"),sQuery(id+"F10.wireOp",EDGE,"E3198"),sQuery(id+"F10.wireOp",EDGE,"E3199"),sQuery(id+"F10.wireOp",EDGE,"E3200"),sQuery(id+"F10.wireOp",EDGE,"E3201"),sQuery(id+"F10.wireOp",EDGE,"E3202"),sQuery(id+"F10.wireOp",EDGE,"E3203"),sQuery(id+"F10.wireOp",EDGE,"E3204"),sQuery(id+"F10.wireOp",EDGE,"E3205"),sQuery(id+"F10.wireOp",EDGE,"E3206"),sQuery(id+"F10.wireOp",EDGE,"E3207"),sQuery(id+"F10.wireOp",EDGE,"E3208"),sQuery(id+"F10.wireOp",EDGE,"E3209"),sQuery(id+"F10.wireOp",EDGE,"E3210"),sQuery(id+"F10.wireOp",EDGE,"E3211"),sQuery(id+"F10.wireOp",EDGE,"E3212"),sQuery(id+"F10.wireOp",EDGE,"E3213"),sQuery(id+"F10.wireOp",EDGE,"E3214"),sQuery(id+"F10.wireOp",EDGE,"E3215"),sQuery(id+"F10.wireOp",EDGE,"E3216"),sQuery(id+"F10.wireOp",EDGE,"E3217"),sQuery(id+"F10.wireOp",EDGE,"E3218"),sQuery(id+"F10.wireOp",EDGE,"E3219"),sQuery(id+"F10.wireOp",EDGE,"E3220"),sQuery(id+"F10.wireOp",EDGE,"E3221"),sQuery(id+"F10.wireOp",EDGE,"E3222"),sQuery(id+"F10.wireOp",EDGE,"E3223"),sQuery(id+"F10.wireOp",EDGE,"E3224"),sQuery(id+"F10.wireOp",EDGE,"E3225"),sQuery(id+"F10.wireOp",EDGE,"E3226"),sQuery(id+"F10.wireOp",EDGE,"E3227"),sQuery(id+"F10.wireOp",EDGE,"E3228"),sQuery(id+"F10.wireOp",EDGE,"E3229"),sQuery(id+"F10.wireOp",EDGE,"E3230"),sQuery(id+"F10.wireOp",EDGE,"E3231"),sQuery(id+"F10.wireOp",EDGE,"E3232"),sQuery(id+"F10.wireOp",EDGE,"E3233"),sQuery(id+"F10.wireOp",EDGE,"E3234"),sQuery(id+"F10.wireOp",EDGE,"E3235"),sQuery(id+"F10.wireOp",EDGE,"E3236"),sQuery(id+"F10.wireOp",EDGE,"E3237"),sQuery(id+"F10.wireOp",EDGE,"E3238"),sQuery(id+"F10.wireOp",EDGE,"E3239"),sQuery(id+"F10.wireOp",EDGE,"E3240"),sQuery(id+"F10.wireOp",EDGE,"E3241"),sQuery(id+"F10.wireOp",EDGE,"E3242"),sQuery(id+"F10.wireOp",EDGE,"E3243"),sQuery(id+"F10.wireOp",EDGE,"E3244"),sQuery(id+"F10.wireOp",EDGE,"E3245"),sQuery(id+"F10.wireOp",EDGE,"E3246"),sQuery(id+"F10.wireOp",EDGE,"E3247"),sQuery(id+"F10.wireOp",EDGE,"E3248"),sQuery(id+"F10.wireOp",EDGE,"E3249"),sQuery(id+"F10.wireOp",EDGE,"E3250"),sQuery(id+"F10.wireOp",EDGE,"E3251"),sQuery(id+"F10.wireOp",EDGE,"E3252"),sQuery(id+"F10.wireOp",EDGE,"E3253"),sQuery(id+"F10.wireOp",EDGE,"E3254"),sQuery(id+"F10.wireOp",EDGE,"E3255"),sQuery(id+"F10.wireOp",EDGE,"E3256"),sQuery(id+"F10.wireOp",EDGE,"E3257"),sQuery(id+"F10.wireOp",EDGE,"E3258"),sQuery(id+"F10.wireOp",EDGE,"E3259"),sQuery(id+"F10.wireOp",EDGE,"E3260"),sQuery(id+"F10.wireOp",EDGE,"E3261"),sQuery(id+"F10.wireOp",EDGE,"E3262"),sQuery(id+"F10.wireOp",EDGE,"E3263"),sQuery(id+"F10.wireOp",EDGE,"E3264"),sQuery(id+"F10.wireOp",EDGE,"E3265"),sQuery(id+"F10.wireOp",EDGE,"E3266"),sQuery(id+"F10.wireOp",EDGE,"E3267"),sQuery(id+"F10.wireOp",EDGE,"E3268"),sQuery(id+"F10.wireOp",EDGE,"E3269"),sQuery(id+"F10.wireOp",EDGE,"E3270"),sQuery(id+"F10.wireOp",EDGE,"E3271"),sQuery(id+"F10.wireOp",EDGE,"E3272"),sQuery(id+"F10.wireOp",EDGE,"E3273"),sQuery(id+"F10.wireOp",EDGE,"E3274"),sQuery(id+"F10.wireOp",EDGE,"E3275"),sQuery(id+"F10.wireOp",EDGE,"E3276"),sQuery(id+"F10.wireOp",EDGE,"E3277"),sQuery(id+"F10.wireOp",EDGE,"E3278"),sQuery(id+"F10.wireOp",EDGE,"E3279"),sQuery(id+"F10.wireOp",EDGE,"E3280"),sQuery(id+"F10.wireOp",EDGE,"E3281"),sQuery(id+"F10.wireOp",EDGE,"E3282"),sQuery(id+"F10.wireOp",EDGE,"E3283"),sQuery(id+"F10.wireOp",EDGE,"E3284"),sQuery(id+"F10.wireOp",EDGE,"E3285"),sQuery(id+"F10.wireOp",EDGE,"E3286"),sQuery(id+"F10.wireOp",EDGE,"E3287"),sQuery(id+"F10.wireOp",EDGE,"E3288"),sQuery(id+"F10.wireOp",EDGE,"E3289"),sQuery(id+"F10.wireOp",EDGE,"E3290"),sQuery(id+"F10.wireOp",EDGE,"E3291"),sQuery(id+"F10.wireOp",EDGE,"E3292"),sQuery(id+"F10.wireOp",EDGE,"E3293"),sQuery(id+"F10.wireOp",EDGE,"E3294"),sQuery(id+"F10.wireOp",EDGE,"E3295"),sQuery(id+"F10.wireOp",EDGE,"E3296"),sQuery(id+"F10.wireOp",EDGE,"E3297"),sQuery(id+"F10.wireOp",EDGE,"E3298"),sQuery(id+"F10.wireOp",EDGE,"E3299"),sQuery(id+"F10.wireOp",EDGE,"E3300"),sQuery(id+"F10.wireOp",EDGE,"E3301"),sQuery(id+"F10.wireOp",EDGE,"E3302"),sQuery(id+"F10.wireOp",EDGE,"E3303"),sQuery(id+"F10.wireOp",EDGE,"E3304"),sQuery(id+"F10.wireOp",EDGE,"E3305"),sQuery(id+"F10.wireOp",EDGE,"E3306"),sQuery(id+"F10.wireOp",EDGE,"E3307"),sQuery(id+"F10.wireOp",EDGE,"E3308"),sQuery(id+"F10.wireOp",EDGE,"E3309"),sQuery(id+"F10.wireOp",EDGE,"E3310"),sQuery(id+"F10.wireOp",EDGE,"E3311"),sQuery(id+"F10.wireOp",EDGE,"E3312"),sQuery(id+"F10.wireOp",EDGE,"E3313"),sQuery(id+"F10.wireOp",EDGE,"E3314"),sQuery(id+"F10.wireOp",EDGE,"E3315"),sQuery(id+"F10.wireOp",EDGE,"E3316"),sQuery(id+"F10.wireOp",EDGE,"E3317"),sQuery(id+"F10.wireOp",EDGE,"E3318"),sQuery(id+"F10.wireOp",EDGE,"E3319"),sQuery(id+"F10.wireOp",EDGE,"E3320"),sQuery(id+"F10.wireOp",EDGE,"E3321"),sQuery(id+"F10.wireOp",EDGE,"E3322"),sQuery(id+"F10.wireOp",EDGE,"E3323"),sQuery(id+"F10.wireOp",EDGE,"E3324"),sQuery(id+"F10.wireOp",EDGE,"E3325"),sQuery(id+"F10.wireOp",EDGE,"E3326"),sQuery(id+"F10.wireOp",EDGE,"E3327"),sQuery(id+"F10.wireOp",EDGE,"E3328"),sQuery(id+"F10.wireOp",EDGE,"E3329"),sQuery(id+"F10.wireOp",EDGE,"E3330"),sQuery(id+"F10.wireOp",EDGE,"E3331"),sQuery(id+"F10.wireOp",EDGE,"E3332"),sQuery(id+"F10.wireOp",EDGE,"E3333"),sQuery(id+"F10.wireOp",EDGE,"E3334"),sQuery(id+"F10.wireOp",EDGE,"E3335"),sQuery(id+"F10.wireOp",EDGE,"E3336"),sQuery(id+"F10.wireOp",EDGE,"E3337"),sQuery(id+"F10.wireOp",EDGE,"E3338"),sQuery(id+"F10.wireOp",EDGE,"E3339"),sQuery(id+"F10.wireOp",EDGE,"E3340"),sQuery(id+"F10.wireOp",EDGE,"E3341"),sQuery(id+"F10.wireOp",EDGE,"E3342"),sQuery(id+"F10.wireOp",EDGE,"E3343"),sQuery(id+"F10.wireOp",EDGE,"E3344"),sQuery(id+"F10.wireOp",EDGE,"E3345"),sQuery(id+"F10.wireOp",EDGE,"E3346"),sQuery(id+"F10.wireOp",EDGE,"E3347"),sQuery(id+"F10.wireOp",EDGE,"E3348"),sQuery(id+"F10.wireOp",EDGE,"E3349"),sQuery(id+"F10.wireOp",EDGE,"E3350"),sQuery(id+"F10.wireOp",EDGE,"E3351"),sQuery(id+"F10.wireOp",EDGE,"E3352"),sQuery(id+"F10.wireOp",EDGE,"E3353"),sQuery(id+"F10.wireOp",EDGE,"E3354"),sQuery(id+"F10.wireOp",EDGE,"E3355"),sQuery(id+"F10.wireOp",EDGE,"E3356"),sQuery(id+"F10.wireOp",EDGE,"E3357"),sQuery(id+"F10.wireOp",EDGE,"E3358"),sQuery(id+"F10.wireOp",EDGE,"E3359"),sQuery(id+"F10.wireOp",EDGE,"E3360"),sQuery(id+"F10.wireOp",EDGE,"E3361"),sQuery(id+"F10.wireOp",EDGE,"E3362"),sQuery(id+"F10.wireOp",EDGE,"E3363"),sQuery(id+"F10.wireOp",EDGE,"E3364"),sQuery(id+"F10.wireOp",EDGE,"E3365"),sQuery(id+"F10.wireOp",EDGE,"E3366"),sQuery(id+"F10.wireOp",EDGE,"E3367"),sQuery(id+"F10.wireOp",EDGE,"E3368"),sQuery(id+"F10.wireOp",EDGE,"E3369"),sQuery(id+"F10.wireOp",EDGE,"E3370"),sQuery(id+"F10.wireOp",EDGE,"E3371"),sQuery(id+"F10.wireOp",EDGE,"E3372"),sQuery(id+"F10.wireOp",EDGE,"E3373"),sQuery(id+"F10.wireOp",EDGE,"E3374"),sQuery(id+"F10.wireOp",EDGE,"E3375"),sQuery(id+"F10.wireOp",EDGE,"E3376"),sQuery(id+"F10.wireOp",EDGE,"E3377"),sQuery(id+"F10.wireOp",EDGE,"E3378"),sQuery(id+"F10.wireOp",EDGE,"E3379"),sQuery(id+"F10.wireOp",EDGE,"E3380"),sQuery(id+"F10.wireOp",EDGE,"E3381"),sQuery(id+"F10.wireOp",EDGE,"E3382"),sQuery(id+"F10.wireOp",EDGE,"E3383"),sQuery(id+"F10.wireOp",EDGE,"E3384"),sQuery(id+"F10.wireOp",EDGE,"E3385"),sQuery(id+"F10.wireOp",EDGE,"E3386"),sQuery(id+"F10.wireOp",EDGE,"E3387"),sQuery(id+"F10.wireOp",EDGE,"E3388"),sQuery(id+"F10.wireOp",EDGE,"E3389"),sQuery(id+"F10.wireOp",EDGE,"E3390"),sQuery(id+"F10.wireOp",EDGE,"E3391"),sQuery(id+"F10.wireOp",EDGE,"E3392"),sQuery(id+"F10.wireOp",EDGE,"E3393"),sQuery(id+"F10.wireOp",EDGE,"E3394"),sQuery(id+"F10.wireOp",EDGE,"E3395"),sQuery(id+"F10.wireOp",EDGE,"E3396"),sQuery(id+"F10.wireOp",EDGE,"E3397"),sQuery(id+"F10.wireOp",EDGE,"E3398"),sQuery(id+"F10.wireOp",EDGE,"E3399"),sQuery(id+"F10.wireOp",EDGE,"E3400"),sQuery(id+"F10.wireOp",EDGE,"E3401"),sQuery(id+"F10.wireOp",EDGE,"E3402"),sQuery(id+"F10.wireOp",EDGE,"E3403"),sQuery(id+"F10.wireOp",EDGE,"E3404"),sQuery(id+"F10.wireOp",EDGE,"E3405"),sQuery(id+"F10.wireOp",EDGE,"E3406"),sQuery(id+"F10.wireOp",EDGE,"E3407"),sQuery(id+"F10.wireOp",EDGE,"E3408"),sQuery(id+"F10.wireOp",EDGE,"E3409"),sQuery(id+"F10.wireOp",EDGE,"E3410"),sQuery(id+"F10.wireOp",EDGE,"E3411"),sQuery(id+"F10.wireOp",EDGE,"E3412"),sQuery(id+"F10.wireOp",EDGE,"E3413"),sQuery(id+"F10.wireOp",EDGE,"E3414"),sQuery(id+"F10.wireOp",EDGE,"E3415"),sQuery(id+"F10.wireOp",EDGE,"E3416"),sQuery(id+"F10.wireOp",EDGE,"E3417"),sQuery(id+"F10.wireOp",EDGE,"E3418"),sQuery(id+"F10.wireOp",EDGE,"E3419"),sQuery(id+"F10.wireOp",EDGE,"E3420"),sQuery(id+"F10.wireOp",EDGE,"E3421"),sQuery(id+"F10.wireOp",EDGE,"E3422"),sQuery(id+"F10.wireOp",EDGE,"E3423"),sQuery(id+"F10.wireOp",EDGE,"E3424"),sQuery(id+"F10.wireOp",EDGE,"E3425"),sQuery(id+"F10.wireOp",EDGE,"E3426"),sQuery(id+"F10.wireOp",EDGE,"E3427"),sQuery(id+"F10.wireOp",EDGE,"E3428"),sQuery(id+"F10.wireOp",EDGE,"E3429"),sQuery(id+"F10.wireOp",EDGE,"E3430"),sQuery(id+"F10.wireOp",EDGE,"E3431"),sQuery(id+"F10.wireOp",EDGE,"E3432"),sQuery(id+"F10.wireOp",EDGE,"E3433"),sQuery(id+"F10.wireOp",EDGE,"E3434"),sQuery(id+"F10.wireOp",EDGE,"E3435"),sQuery(id+"F10.wireOp",EDGE,"E3436"),sQuery(id+"F10.wireOp",EDGE,"E3437"),sQuery(id+"F10.wireOp",EDGE,"E3438"),sQuery(id+"F10.wireOp",EDGE,"E3439"),sQuery(id+"F10.wireOp",EDGE,"E3440"),sQuery(id+"F10.wireOp",EDGE,"E3441"),sQuery(id+"F10.wireOp",EDGE,"E3442"),sQuery(id+"F10.wireOp",EDGE,"E3443"),sQuery(id+"F10.wireOp",EDGE,"E3444"),sQuery(id+"F10.wireOp",EDGE,"E3445"),sQuery(id+"F10.wireOp",EDGE,"E3446"),sQuery(id+"F10.wireOp",EDGE,"E3447"),sQuery(id+"F10.wireOp",EDGE,"E3448"),sQuery(id+"F10.wireOp",EDGE,"E3449"),sQuery(id+"F10.wireOp",EDGE,"E3450"),sQuery(id+"F10.wireOp",EDGE,"E3451"),sQuery(id+"F10.wireOp",EDGE,"E3452"),sQuery(id+"F10.wireOp",EDGE,"E3453"),sQuery(id+"F10.wireOp",EDGE,"E3454"),sQuery(id+"F10.wireOp",EDGE,"E3455"),sQuery(id+"F10.wireOp",EDGE,"E3456"),sQuery(id+"F10.wireOp",EDGE,"E3457"),sQuery(id+"F10.wireOp",EDGE,"E3458"),sQuery(id+"F10.wireOp",EDGE,"E3459"),sQuery(id+"F10.wireOp",EDGE,"E3460"),sQuery(id+"F10.wireOp",EDGE,"E3461"),sQuery(id+"F10.wireOp",EDGE,"E3462"),sQuery(id+"F10.wireOp",EDGE,"E3463"),sQuery(id+"F10.wireOp",EDGE,"E3464"),sQuery(id+"F10.wireOp",EDGE,"E3465"),sQuery(id+"F10.wireOp",EDGE,"E3466"),sQuery(id+"F10.wireOp",EDGE,"E3467"),sQuery(id+"F10.wireOp",EDGE,"E3468"),sQuery(id+"F10.wireOp",EDGE,"E3469"),sQuery(id+"F10.wireOp",EDGE,"E3470"),sQuery(id+"F10.wireOp",EDGE,"E3471"),sQuery(id+"F10.wireOp",EDGE,"E3472"),sQuery(id+"F10.wireOp",EDGE,"E3473"),sQuery(id+"F10.wireOp",EDGE,"E3474"),sQuery(id+"F10.wireOp",EDGE,"E3475"),sQuery(id+"F10.wireOp",EDGE,"E3476"),sQuery(id+"F10.wireOp",EDGE,"E3477"),sQuery(id+"F10.wireOp",EDGE,"E3478"),sQuery(id+"F10.wireOp",EDGE,"E3479"),sQuery(id+"F10.wireOp",EDGE,"E3480"),sQuery(id+"F10.wireOp",EDGE,"E3481"),sQuery(id+"F10.wireOp",EDGE,"E3482"),sQuery(id+"F10.wireOp",EDGE,"E3483"),sQuery(id+"F10.wireOp",EDGE,"E3484"),sQuery(id+"F10.wireOp",EDGE,"E3485"),sQuery(id+"F10.wireOp",EDGE,"E3486"),sQuery(id+"F10.wireOp",EDGE,"E3487"),sQuery(id+"F10.wireOp",EDGE,"E3488"),sQuery(id+"F10.wireOp",EDGE,"E3489"),sQuery(id+"F10.wireOp",EDGE,"E3490"),sQuery(id+"F10.wireOp",EDGE,"E3491"),sQuery(id+"F10.wireOp",EDGE,"E3492"),sQuery(id+"F10.wireOp",EDGE,"E3493"),sQuery(id+"F10.wireOp",EDGE,"E3494"),sQuery(id+"F10.wireOp",EDGE,"E3495"),sQuery(id+"F10.wireOp",EDGE,"E3496"),sQuery(id+"F10.wireOp",EDGE,"E3497"),sQuery(id+"F10.wireOp",EDGE,"E3498"),sQuery(id+"F10.wireOp",EDGE,"E3499"),sQuery(id+"F10.wireOp",EDGE,"E3500"),sQuery(id+"F10.wireOp",EDGE,"E3501"),sQuery(id+"F10.wireOp",EDGE,"E3502"),sQuery(id+"F10.wireOp",EDGE,"E3503"),sQuery(id+"F10.wireOp",EDGE,"E3504"),sQuery(id+"F10.wireOp",EDGE,"E3505"),sQuery(id+"F10.wireOp",EDGE,"E3506"),sQuery(id+"F10.wireOp",EDGE,"E3507"),sQuery(id+"F10.wireOp",EDGE,"E3508"),sQuery(id+"F10.wireOp",EDGE,"E3509"),sQuery(id+"F10.wireOp",EDGE,"E3510"),sQuery(id+"F10.wireOp",EDGE,"E3511"),sQuery(id+"F10.wireOp",EDGE,"E3512"),sQuery(id+"F10.wireOp",EDGE,"E3513"),sQuery(id+"F10.wireOp",EDGE,"E3514"),sQuery(id+"F10.wireOp",EDGE,"E3515"),sQuery(id+"F10.wireOp",EDGE,"E3516"),sQuery(id+"F10.wireOp",EDGE,"E3517"),sQuery(id+"F10.wireOp",EDGE,"E3518"),sQuery(id+"F10.wireOp",EDGE,"E3519"),sQuery(id+"F10.wireOp",EDGE,"E3520"),sQuery(id+"F10.wireOp",EDGE,"E3521"),sQuery(id+"F10.wireOp",EDGE,"E3522"),sQuery(id+"F10.wireOp",EDGE,"E3523"),sQuery(id+"F10.wireOp",EDGE,"E3524"),sQuery(id+"F10.wireOp",EDGE,"E3525"),sQuery(id+"F10.wireOp",EDGE,"E3526"),sQuery(id+"F10.wireOp",EDGE,"E3527"),sQuery(id+"F10.wireOp",EDGE,"E3528"),sQuery(id+"F10.wireOp",EDGE,"E3529"),sQuery(id+"F10.wireOp",EDGE,"E3530"),sQuery(id+"F10.wireOp",EDGE,"E3531"),sQuery(id+"F10.wireOp",EDGE,"E3532"),sQuery(id+"F10.wireOp",EDGE,"E3533"),sQuery(id+"F10.wireOp",EDGE,"E3534"),sQuery(id+"F10.wireOp",EDGE,"E3535"),sQuery(id+"F10.wireOp",EDGE,"E3536"),sQuery(id+"F10.wireOp",EDGE,"E3537"),sQuery(id+"F10.wireOp",EDGE,"E3538"),sQuery(id+"F10.wireOp",EDGE,"E3539"),sQuery(id+"F10.wireOp",EDGE,"E3540"),sQuery(id+"F10.wireOp",EDGE,"E3541"),sQuery(id+"F10.wireOp",EDGE,"E3542"),sQuery(id+"F10.wireOp",EDGE,"E3543"),sQuery(id+"F10.wireOp",EDGE,"E3544"),sQuery(id+"F10.wireOp",EDGE,"E3545"),sQuery(id+"F10.wireOp",EDGE,"E3546"),sQuery(id+"F10.wireOp",EDGE,"E3547"),sQuery(id+"F10.wireOp",EDGE,"E3548"),sQuery(id+"F10.wireOp",EDGE,"E3549"),sQuery(id+"F10.wireOp",EDGE,"E3550"),sQuery(id+"F10.wireOp",EDGE,"E3551"),sQuery(id+"F10.wireOp",EDGE,"E3552"),sQuery(id+"F10.wireOp",EDGE,"E3553"),sQuery(id+"F10.wireOp",EDGE,"E3554"),sQuery(id+"F10.wireOp",EDGE,"E3555"),sQuery(id+"F10.wireOp",EDGE,"E3556"),sQuery(id+"F10.wireOp",EDGE,"E3557"),sQuery(id+"F10.wireOp",EDGE,"E3558"),sQuery(id+"F10.wireOp",EDGE,"E3559"),sQuery(id+"F10.wireOp",EDGE,"E3560"),sQuery(id+"F10.wireOp",EDGE,"E3561"),sQuery(id+"F10.wireOp",EDGE,"E3562"),sQuery(id+"F10.wireOp",EDGE,"E3563"),sQuery(id+"F10.wireOp",EDGE,"E3564"),sQuery(id+"F10.wireOp",EDGE,"E3565"),sQuery(id+"F10.wireOp",EDGE,"E3566"),sQuery(id+"F10.wireOp",EDGE,"E3567"),sQuery(id+"F10.wireOp",EDGE,"E3568"),sQuery(id+"F10.wireOp",EDGE,"E3569"),sQuery(id+"F10.wireOp",EDGE,"E3570"),sQuery(id+"F10.wireOp",EDGE,"E3571"),sQuery(id+"F10.wireOp",EDGE,"E3572"),sQuery(id+"F10.wireOp",EDGE,"E3573"),sQuery(id+"F10.wireOp",EDGE,"E3574"),sQuery(id+"F10.wireOp",EDGE,"E3575"),sQuery(id+"F10.wireOp",EDGE,"E3576"),sQuery(id+"F10.wireOp",EDGE,"E3577"),sQuery(id+"F10.wireOp",EDGE,"E3578"),sQuery(id+"F10.wireOp",EDGE,"E3579"),sQuery(id+"F10.wireOp",EDGE,"E3580"),sQuery(id+"F10.wireOp",EDGE,"E3581"),sQuery(id+"F10.wireOp",EDGE,"E3582"),sQuery(id+"F10.wireOp",EDGE,"E3583"),sQuery(id+"F10.wireOp",EDGE,"E3584"),sQuery(id+"F10.wireOp",EDGE,"E3585"),sQuery(id+"F10.wireOp",EDGE,"E3586"),sQuery(id+"F10.wireOp",EDGE,"E3587"),sQuery(id+"F10.wireOp",EDGE,"E3588"),sQuery(id+"F10.wireOp",EDGE,"E3589"),sQuery(id+"F10.wireOp",EDGE,"E3590"),sQuery(id+"F10.wireOp",EDGE,"E3591"),sQuery(id+"F10.wireOp",EDGE,"E3592"),sQuery(id+"F10.wireOp",EDGE,"E3593"),sQuery(id+"F10.wireOp",EDGE,"E3594"),sQuery(id+"F10.wireOp",EDGE,"E3595"),sQuery(id+"F10.wireOp",EDGE,"E3596"),sQuery(id+"F10.wireOp",EDGE,"E3597"),sQuery(id+"F10.wireOp",EDGE,"E3598"),sQuery(id+"F10.wireOp",EDGE,"E3599"),sQuery(id+"F10.wireOp",EDGE,"E3600"),sQuery(id+"F10.wireOp",EDGE,"E3601"),sQuery(id+"F10.wireOp",EDGE,"E3602"),sQuery(id+"F10.wireOp",EDGE,"E3603"),sQuery(id+"F10.wireOp",EDGE,"E3604"),sQuery(id+"F10.wireOp",EDGE,"E3605"),sQuery(id+"F10.wireOp",EDGE,"E3606"),sQuery(id+"F10.wireOp",EDGE,"E3607"),sQuery(id+"F10.wireOp",EDGE,"E3608"),sQuery(id+"F10.wireOp",EDGE,"E3609"),sQuery(id+"F10.wireOp",EDGE,"E3610"),sQuery(id+"F10.wireOp",EDGE,"E3611"),sQuery(id+"F10.wireOp",EDGE,"E3612"),sQuery(id+"F10.wireOp",EDGE,"E3613"),sQuery(id+"F10.wireOp",EDGE,"E3614"),sQuery(id+"F10.wireOp",EDGE,"E3615"),sQuery(id+"F10.wireOp",EDGE,"E3616"),sQuery(id+"F10.wireOp",EDGE,"E3617"),sQuery(id+"F10.wireOp",EDGE,"E3618"),sQuery(id+"F10.wireOp",EDGE,"E3619"),sQuery(id+"F10.wireOp",EDGE,"E3620"),sQuery(id+"F10.wireOp",EDGE,"E3621"),sQuery(id+"F10.wireOp",EDGE,"E3622"),sQuery(id+"F10.wireOp",EDGE,"E3623"),sQuery(id+"F10.wireOp",EDGE,"E3624"),sQuery(id+"F10.wireOp",EDGE,"E3625"),sQuery(id+"F10.wireOp",EDGE,"E3626"),sQuery(id+"F10.wireOp",EDGE,"E3627"),sQuery(id+"F10.wireOp",EDGE,"E3628"),sQuery(id+"F10.wireOp",EDGE,"E3629"),sQuery(id+"F10.wireOp",EDGE,"E3630"),sQuery(id+"F10.wireOp",EDGE,"E3631"),sQuery(id+"F10.wireOp",EDGE,"E3632"),sQuery(id+"F10.wireOp",EDGE,"E3633"),sQuery(id+"F10.wireOp",EDGE,"E3634"),sQuery(id+"F10.wireOp",EDGE,"E3635"),sQuery(id+"F10.wireOp",EDGE,"E3636"),sQuery(id+"F10.wireOp",EDGE,"E3637"),sQuery(id+"F10.wireOp",EDGE,"E3638"),sQuery(id+"F10.wireOp",EDGE,"E3639"),sQuery(id+"F10.wireOp",EDGE,"E3640"),sQuery(id+"F10.wireOp",EDGE,"E3641"),sQuery(id+"F10.wireOp",EDGE,"E3642"),sQuery(id+"F10.wireOp",EDGE,"E3643"),sQuery(id+"F10.wireOp",EDGE,"E3644"),sQuery(id+"F10.wireOp",EDGE,"E3645"),sQuery(id+"F10.wireOp",EDGE,"E3646"),sQuery(id+"F10.wireOp",EDGE,"E3647"),sQuery(id+"F10.wireOp",EDGE,"E3648"),sQuery(id+"F10.wireOp",EDGE,"E3649"),sQuery(id+"F10.wireOp",EDGE,"E3650"),sQuery(id+"F10.wireOp",EDGE,"E3651"),sQuery(id+"F10.wireOp",EDGE,"E3652"),sQuery(id+"F10.wireOp",EDGE,"E3653"),sQuery(id+"F10.wireOp",EDGE,"E3654"),sQuery(id+"F10.wireOp",EDGE,"E3655"),sQuery(id+"F10.wireOp",EDGE,"E3656"),sQuery(id+"F10.wireOp",EDGE,"E3657"),sQuery(id+"F10.wireOp",EDGE,"E3658"),sQuery(id+"F10.wireOp",EDGE,"E3659"),sQuery(id+"F10.wireOp",EDGE,"E3660"),sQuery(id+"F10.wireOp",EDGE,"E3661"),sQuery(id+"F10.wireOp",EDGE,"E3662"),sQuery(id+"F10.wireOp",EDGE,"E3663"),sQuery(id+"F10.wireOp",EDGE,"E3664"),sQuery(id+"F10.wireOp",EDGE,"E3665"),sQuery(id+"F10.wireOp",EDGE,"E3666"),sQuery(id+"F10.wireOp",EDGE,"E3667"),sQuery(id+"F10.wireOp",EDGE,"E3668"),sQuery(id+"F10.wireOp",EDGE,"E3669"),sQuery(id+"F10.wireOp",EDGE,"E3670"),sQuery(id+"F10.wireOp",EDGE,"E3671"),sQuery(id+"F10.wireOp",EDGE,"E3672"),sQuery(id+"F10.wireOp",EDGE,"E3673"),sQuery(id+"F10.wireOp",EDGE,"E3674"),sQuery(id+"F10.wireOp",EDGE,"E3675"),sQuery(id+"F10.wireOp",EDGE,"E3676"),sQuery(id+"F10.wireOp",EDGE,"E3677"),sQuery(id+"F10.wireOp",EDGE,"E3678"),sQuery(id+"F10.wireOp",EDGE,"E3679"),sQuery(id+"F10.wireOp",EDGE,"E3680"),sQuery(id+"F10.wireOp",EDGE,"E3681"),sQuery(id+"F10.wireOp",EDGE,"E3682"),sQuery(id+"F10.wireOp",EDGE,"E3683"),sQuery(id+"F10.wireOp",EDGE,"E3684"),sQuery(id+"F10.wireOp",EDGE,"E3685"),sQuery(id+"F10.wireOp",EDGE,"E3686"),sQuery(id+"F10.wireOp",EDGE,"E3687"),sQuery(id+"F10.wireOp",EDGE,"E3688"),sQuery(id+"F10.wireOp",EDGE,"E3689"),sQuery(id+"F10.wireOp",EDGE,"E3690"),sQuery(id+"F10.wireOp",EDGE,"E3691"),sQuery(id+"F10.wireOp",EDGE,"E3692"),sQuery(id+"F10.wireOp",EDGE,"E3693"),sQuery(id+"F10.wireOp",EDGE,"E3694"),sQuery(id+"F10.wireOp",EDGE,"E3695"),sQuery(id+"F10.wireOp",EDGE,"E3696"),sQuery(id+"F10.wireOp",EDGE,"E3697"),sQuery(id+"F10.wireOp",EDGE,"E3698"),sQuery(id+"F10.wireOp",EDGE,"E3699"),sQuery(id+"F10.wireOp",EDGE,"E3700"),sQuery(id+"F10.wireOp",EDGE,"E3701"),sQuery(id+"F10.wireOp",EDGE,"E3702"),sQuery(id+"F10.wireOp",EDGE,"E3703"),sQuery(id+"F10.wireOp",EDGE,"E3704"),sQuery(id+"F10.wireOp",EDGE,"E3705"),sQuery(id+"F10.wireOp",EDGE,"E3706"),sQuery(id+"F10.wireOp",EDGE,"E3707"),sQuery(id+"F10.wireOp",EDGE,"E3708"),sQuery(id+"F10.wireOp",EDGE,"E3709"),sQuery(id+"F10.wireOp",EDGE,"E3710"),sQuery(id+"F10.wireOp",EDGE,"E3711"),sQuery(id+"F10.wireOp",EDGE,"E3712"),sQuery(id+"F10.wireOp",EDGE,"E3713"),sQuery(id+"F10.wireOp",EDGE,"E3714"),sQuery(id+"F10.wireOp",EDGE,"E3715"),sQuery(id+"F10.wireOp",EDGE,"E3716"),sQuery(id+"F10.wireOp",EDGE,"E3717"),sQuery(id+"F10.wireOp",EDGE,"E3718"),sQuery(id+"F10.wireOp",EDGE,"E3719"),sQuery(id+"F10.wireOp",EDGE,"E3720"),sQuery(id+"F10.wireOp",EDGE,"E3721"),sQuery(id+"F10.wireOp",EDGE,"E3722"),sQuery(id+"F10.wireOp",EDGE,"E3723"),sQuery(id+"F10.wireOp",EDGE,"E3724"),sQuery(id+"F10.wireOp",EDGE,"E3725"),sQuery(id+"F10.wireOp",EDGE,"E3726"),sQuery(id+"F10.wireOp",EDGE,"E3727"),sQuery(id+"F10.wireOp",EDGE,"E3728"),sQuery(id+"F10.wireOp",EDGE,"E3729"),sQuery(id+"F10.wireOp",EDGE,"E3730"),sQuery(id+"F10.wireOp",EDGE,"E3731"),sQuery(id+"F10.wireOp",EDGE,"E3732"),sQuery(id+"F10.wireOp",EDGE,"E3733"),sQuery(id+"F10.wireOp",EDGE,"E3734"),sQuery(id+"F10.wireOp",EDGE,"E3735"),sQuery(id+"F10.wireOp",EDGE,"E3736"),sQuery(id+"F10.wireOp",EDGE,"E3737"),sQuery(id+"F10.wireOp",EDGE,"E3738"),sQuery(id+"F10.wireOp",EDGE,"E3739"),sQuery(id+"F10.wireOp",EDGE,"E3740"),sQuery(id+"F10.wireOp",EDGE,"E3741"),sQuery(id+"F10.wireOp",EDGE,"E3742"),sQuery(id+"F10.wireOp",EDGE,"E3743"),sQuery(id+"F10.wireOp",EDGE,"E3744"),sQuery(id+"F10.wireOp",EDGE,"E3745"),sQuery(id+"F10.wireOp",EDGE,"E3746"),sQuery(id+"F10.wireOp",EDGE,"E3747")])]});
            var Q1;
            Q1=sQuery(id+"F5.wireOp",EDGE,"E2623");
            transform(context, id + "F12", {"entities" : qUnion([Q0]), "transformType" : TransformType.ROTATION, "transformAxis" : qUnion([Q1]), "angle" : 90 * degree, "oppositeDirection" : true, "makeCopy" : false});
        }
        {
            var Q0;
            Q0=makeQuery(id+"F11.opExtrude","SWEPT_BODY",BODY,{"disambiguationData":[OSD([sQuery(id+"F10.wireOp",EDGE,"E2624"),sQuery(id+"F10.wireOp",EDGE,"E2625"),sQuery(id+"F10.wireOp",EDGE,"E2626"),sQuery(id+"F10.wireOp",EDGE,"E2627"),sQuery(id+"F10.wireOp",EDGE,"E2628"),sQuery(id+"F10.wireOp",EDGE,"E2629"),sQuery(id+"F10.wireOp",EDGE,"E2630"),sQuery(id+"F10.wireOp",EDGE,"E2631"),sQuery(id+"F10.wireOp",EDGE,"E2632"),sQuery(id+"F10.wireOp",EDGE,"E2633"),sQuery(id+"F10.wireOp",EDGE,"E2634"),sQuery(id+"F10.wireOp",EDGE,"E2635"),sQuery(id+"F10.wireOp",EDGE,"E2636"),sQuery(id+"F10.wireOp",EDGE,"E2637"),sQuery(id+"F10.wireOp",EDGE,"E2638"),sQuery(id+"F10.wireOp",EDGE,"E2639"),sQuery(id+"F10.wireOp",EDGE,"E2640"),sQuery(id+"F10.wireOp",EDGE,"E2641"),sQuery(id+"F10.wireOp",EDGE,"E2642"),sQuery(id+"F10.wireOp",EDGE,"E2643"),sQuery(id+"F10.wireOp",EDGE,"E2644"),sQuery(id+"F10.wireOp",EDGE,"E2645"),sQuery(id+"F10.wireOp",EDGE,"E2646"),sQuery(id+"F10.wireOp",EDGE,"E2647"),sQuery(id+"F10.wireOp",EDGE,"E2648"),sQuery(id+"F10.wireOp",EDGE,"E2649"),sQuery(id+"F10.wireOp",EDGE,"E2650"),sQuery(id+"F10.wireOp",EDGE,"E2651"),sQuery(id+"F10.wireOp",EDGE,"E2652"),sQuery(id+"F10.wireOp",EDGE,"E2653"),sQuery(id+"F10.wireOp",EDGE,"E2654"),sQuery(id+"F10.wireOp",EDGE,"E2655"),sQuery(id+"F10.wireOp",EDGE,"E2656"),sQuery(id+"F10.wireOp",EDGE,"E2657"),sQuery(id+"F10.wireOp",EDGE,"E2658"),sQuery(id+"F10.wireOp",EDGE,"E2659"),sQuery(id+"F10.wireOp",EDGE,"E2660"),sQuery(id+"F10.wireOp",EDGE,"E2661"),sQuery(id+"F10.wireOp",EDGE,"E2662"),sQuery(id+"F10.wireOp",EDGE,"E2663"),sQuery(id+"F10.wireOp",EDGE,"E2664"),sQuery(id+"F10.wireOp",EDGE,"E2665"),sQuery(id+"F10.wireOp",EDGE,"E2666"),sQuery(id+"F10.wireOp",EDGE,"E2667"),sQuery(id+"F10.wireOp",EDGE,"E2668"),sQuery(id+"F10.wireOp",EDGE,"E2669"),sQuery(id+"F10.wireOp",EDGE,"E2670"),sQuery(id+"F10.wireOp",EDGE,"E2671"),sQuery(id+"F10.wireOp",EDGE,"E2672"),sQuery(id+"F10.wireOp",EDGE,"E2673"),sQuery(id+"F10.wireOp",EDGE,"E2674"),sQuery(id+"F10.wireOp",EDGE,"E2675"),sQuery(id+"F10.wireOp",EDGE,"E2676"),sQuery(id+"F10.wireOp",EDGE,"E2677"),sQuery(id+"F10.wireOp",EDGE,"E2678"),sQuery(id+"F10.wireOp",EDGE,"E2679"),sQuery(id+"F10.wireOp",EDGE,"E2680"),sQuery(id+"F10.wireOp",EDGE,"E2681"),sQuery(id+"F10.wireOp",EDGE,"E2682"),sQuery(id+"F10.wireOp",EDGE,"E2683"),sQuery(id+"F10.wireOp",EDGE,"E2684"),sQuery(id+"F10.wireOp",EDGE,"E2685"),sQuery(id+"F10.wireOp",EDGE,"E2686"),sQuery(id+"F10.wireOp",EDGE,"E2687"),sQuery(id+"F10.wireOp",EDGE,"E2688"),sQuery(id+"F10.wireOp",EDGE,"E2689"),sQuery(id+"F10.wireOp",EDGE,"E2690"),sQuery(id+"F10.wireOp",EDGE,"E2691"),sQuery(id+"F10.wireOp",EDGE,"E2692"),sQuery(id+"F10.wireOp",EDGE,"E2693"),sQuery(id+"F10.wireOp",EDGE,"E2694"),sQuery(id+"F10.wireOp",EDGE,"E2695"),sQuery(id+"F10.wireOp",EDGE,"E2696"),sQuery(id+"F10.wireOp",EDGE,"E2697"),sQuery(id+"F10.wireOp",EDGE,"E2698"),sQuery(id+"F10.wireOp",EDGE,"E2699"),sQuery(id+"F10.wireOp",EDGE,"E2700"),sQuery(id+"F10.wireOp",EDGE,"E2701"),sQuery(id+"F10.wireOp",EDGE,"E2702"),sQuery(id+"F10.wireOp",EDGE,"E2703"),sQuery(id+"F10.wireOp",EDGE,"E2704"),sQuery(id+"F10.wireOp",EDGE,"E2705"),sQuery(id+"F10.wireOp",EDGE,"E2706"),sQuery(id+"F10.wireOp",EDGE,"E2707"),sQuery(id+"F10.wireOp",EDGE,"E2708"),sQuery(id+"F10.wireOp",EDGE,"E2709"),sQuery(id+"F10.wireOp",EDGE,"E2710"),sQuery(id+"F10.wireOp",EDGE,"E2711"),sQuery(id+"F10.wireOp",EDGE,"E2712"),sQuery(id+"F10.wireOp",EDGE,"E2713"),sQuery(id+"F10.wireOp",EDGE,"E2714"),sQuery(id+"F10.wireOp",EDGE,"E2715"),sQuery(id+"F10.wireOp",EDGE,"E2716"),sQuery(id+"F10.wireOp",EDGE,"E2717"),sQuery(id+"F10.wireOp",EDGE,"E2718"),sQuery(id+"F10.wireOp",EDGE,"E2719"),sQuery(id+"F10.wireOp",EDGE,"E2720"),sQuery(id+"F10.wireOp",EDGE,"E2721"),sQuery(id+"F10.wireOp",EDGE,"E2722"),sQuery(id+"F10.wireOp",EDGE,"E2723"),sQuery(id+"F10.wireOp",EDGE,"E2724"),sQuery(id+"F10.wireOp",EDGE,"E2725"),sQuery(id+"F10.wireOp",EDGE,"E2726"),sQuery(id+"F10.wireOp",EDGE,"E2727"),sQuery(id+"F10.wireOp",EDGE,"E2728"),sQuery(id+"F10.wireOp",EDGE,"E2729"),sQuery(id+"F10.wireOp",EDGE,"E2730"),sQuery(id+"F10.wireOp",EDGE,"E2731"),sQuery(id+"F10.wireOp",EDGE,"E2732"),sQuery(id+"F10.wireOp",EDGE,"E2733"),sQuery(id+"F10.wireOp",EDGE,"E2734"),sQuery(id+"F10.wireOp",EDGE,"E2735"),sQuery(id+"F10.wireOp",EDGE,"E2736"),sQuery(id+"F10.wireOp",EDGE,"E2737"),sQuery(id+"F10.wireOp",EDGE,"E2738"),sQuery(id+"F10.wireOp",EDGE,"E2739"),sQuery(id+"F10.wireOp",EDGE,"E2740"),sQuery(id+"F10.wireOp",EDGE,"E2741"),sQuery(id+"F10.wireOp",EDGE,"E2742"),sQuery(id+"F10.wireOp",EDGE,"E2743"),sQuery(id+"F10.wireOp",EDGE,"E2744"),sQuery(id+"F10.wireOp",EDGE,"E2745"),sQuery(id+"F10.wireOp",EDGE,"E2746"),sQuery(id+"F10.wireOp",EDGE,"E2747"),sQuery(id+"F10.wireOp",EDGE,"E2748"),sQuery(id+"F10.wireOp",EDGE,"E2749"),sQuery(id+"F10.wireOp",EDGE,"E2750"),sQuery(id+"F10.wireOp",EDGE,"E2751"),sQuery(id+"F10.wireOp",EDGE,"E2752"),sQuery(id+"F10.wireOp",EDGE,"E2753"),sQuery(id+"F10.wireOp",EDGE,"E2754"),sQuery(id+"F10.wireOp",EDGE,"E2755"),sQuery(id+"F10.wireOp",EDGE,"E2756"),sQuery(id+"F10.wireOp",EDGE,"E2757"),sQuery(id+"F10.wireOp",EDGE,"E2758"),sQuery(id+"F10.wireOp",EDGE,"E2759"),sQuery(id+"F10.wireOp",EDGE,"E2760"),sQuery(id+"F10.wireOp",EDGE,"E2761"),sQuery(id+"F10.wireOp",EDGE,"E2762"),sQuery(id+"F10.wireOp",EDGE,"E2763"),sQuery(id+"F10.wireOp",EDGE,"E2764"),sQuery(id+"F10.wireOp",EDGE,"E2765"),sQuery(id+"F10.wireOp",EDGE,"E2766"),sQuery(id+"F10.wireOp",EDGE,"E2767"),sQuery(id+"F10.wireOp",EDGE,"E2768"),sQuery(id+"F10.wireOp",EDGE,"E2769"),sQuery(id+"F10.wireOp",EDGE,"E2770"),sQuery(id+"F10.wireOp",EDGE,"E2771"),sQuery(id+"F10.wireOp",EDGE,"E2772"),sQuery(id+"F10.wireOp",EDGE,"E2773"),sQuery(id+"F10.wireOp",EDGE,"E2774"),sQuery(id+"F10.wireOp",EDGE,"E2775"),sQuery(id+"F10.wireOp",EDGE,"E2776"),sQuery(id+"F10.wireOp",EDGE,"E2777"),sQuery(id+"F10.wireOp",EDGE,"E2778"),sQuery(id+"F10.wireOp",EDGE,"E2779"),sQuery(id+"F10.wireOp",EDGE,"E2780"),sQuery(id+"F10.wireOp",EDGE,"E2781"),sQuery(id+"F10.wireOp",EDGE,"E2782"),sQuery(id+"F10.wireOp",EDGE,"E2783"),sQuery(id+"F10.wireOp",EDGE,"E2784"),sQuery(id+"F10.wireOp",EDGE,"E2785"),sQuery(id+"F10.wireOp",EDGE,"E2786"),sQuery(id+"F10.wireOp",EDGE,"E2787"),sQuery(id+"F10.wireOp",EDGE,"E2788"),sQuery(id+"F10.wireOp",EDGE,"E2789"),sQuery(id+"F10.wireOp",EDGE,"E2790"),sQuery(id+"F10.wireOp",EDGE,"E2791"),sQuery(id+"F10.wireOp",EDGE,"E2792"),sQuery(id+"F10.wireOp",EDGE,"E2793"),sQuery(id+"F10.wireOp",EDGE,"E2794"),sQuery(id+"F10.wireOp",EDGE,"E2795"),sQuery(id+"F10.wireOp",EDGE,"E2796"),sQuery(id+"F10.wireOp",EDGE,"E2797"),sQuery(id+"F10.wireOp",EDGE,"E2798"),sQuery(id+"F10.wireOp",EDGE,"E2799"),sQuery(id+"F10.wireOp",EDGE,"E2800"),sQuery(id+"F10.wireOp",EDGE,"E2801"),sQuery(id+"F10.wireOp",EDGE,"E2802"),sQuery(id+"F10.wireOp",EDGE,"E2803"),sQuery(id+"F10.wireOp",EDGE,"E2804"),sQuery(id+"F10.wireOp",EDGE,"E2805"),sQuery(id+"F10.wireOp",EDGE,"E2806"),sQuery(id+"F10.wireOp",EDGE,"E2807"),sQuery(id+"F10.wireOp",EDGE,"E2808"),sQuery(id+"F10.wireOp",EDGE,"E2809"),sQuery(id+"F10.wireOp",EDGE,"E2810"),sQuery(id+"F10.wireOp",EDGE,"E2811"),sQuery(id+"F10.wireOp",EDGE,"E2812"),sQuery(id+"F10.wireOp",EDGE,"E2813"),sQuery(id+"F10.wireOp",EDGE,"E2814"),sQuery(id+"F10.wireOp",EDGE,"E2815"),sQuery(id+"F10.wireOp",EDGE,"E2816"),sQuery(id+"F10.wireOp",EDGE,"E2817"),sQuery(id+"F10.wireOp",EDGE,"E2818"),sQuery(id+"F10.wireOp",EDGE,"E2819"),sQuery(id+"F10.wireOp",EDGE,"E2820"),sQuery(id+"F10.wireOp",EDGE,"E2821"),sQuery(id+"F10.wireOp",EDGE,"E2822"),sQuery(id+"F10.wireOp",EDGE,"E2823"),sQuery(id+"F10.wireOp",EDGE,"E2824"),sQuery(id+"F10.wireOp",EDGE,"E2825"),sQuery(id+"F10.wireOp",EDGE,"E2826"),sQuery(id+"F10.wireOp",EDGE,"E2827"),sQuery(id+"F10.wireOp",EDGE,"E2828"),sQuery(id+"F10.wireOp",EDGE,"E2829"),sQuery(id+"F10.wireOp",EDGE,"E2830"),sQuery(id+"F10.wireOp",EDGE,"E2831"),sQuery(id+"F10.wireOp",EDGE,"E2832"),sQuery(id+"F10.wireOp",EDGE,"E2833"),sQuery(id+"F10.wireOp",EDGE,"E2834"),sQuery(id+"F10.wireOp",EDGE,"E2835"),sQuery(id+"F10.wireOp",EDGE,"E2836"),sQuery(id+"F10.wireOp",EDGE,"E2837"),sQuery(id+"F10.wireOp",EDGE,"E2838"),sQuery(id+"F10.wireOp",EDGE,"E2839"),sQuery(id+"F10.wireOp",EDGE,"E2840"),sQuery(id+"F10.wireOp",EDGE,"E2841"),sQuery(id+"F10.wireOp",EDGE,"E2842"),sQuery(id+"F10.wireOp",EDGE,"E2843"),sQuery(id+"F10.wireOp",EDGE,"E2844"),sQuery(id+"F10.wireOp",EDGE,"E2845"),sQuery(id+"F10.wireOp",EDGE,"E2846"),sQuery(id+"F10.wireOp",EDGE,"E2847"),sQuery(id+"F10.wireOp",EDGE,"E2848"),sQuery(id+"F10.wireOp",EDGE,"E2849"),sQuery(id+"F10.wireOp",EDGE,"E2850"),sQuery(id+"F10.wireOp",EDGE,"E2851"),sQuery(id+"F10.wireOp",EDGE,"E2852"),sQuery(id+"F10.wireOp",EDGE,"E2853"),sQuery(id+"F10.wireOp",EDGE,"E2854"),sQuery(id+"F10.wireOp",EDGE,"E2855"),sQuery(id+"F10.wireOp",EDGE,"E2856"),sQuery(id+"F10.wireOp",EDGE,"E2857"),sQuery(id+"F10.wireOp",EDGE,"E2858"),sQuery(id+"F10.wireOp",EDGE,"E2859"),sQuery(id+"F10.wireOp",EDGE,"E2860"),sQuery(id+"F10.wireOp",EDGE,"E2861"),sQuery(id+"F10.wireOp",EDGE,"E2862"),sQuery(id+"F10.wireOp",EDGE,"E2863"),sQuery(id+"F10.wireOp",EDGE,"E2864"),sQuery(id+"F10.wireOp",EDGE,"E2865"),sQuery(id+"F10.wireOp",EDGE,"E2866"),sQuery(id+"F10.wireOp",EDGE,"E2867"),sQuery(id+"F10.wireOp",EDGE,"E2868"),sQuery(id+"F10.wireOp",EDGE,"E2869"),sQuery(id+"F10.wireOp",EDGE,"E2870"),sQuery(id+"F10.wireOp",EDGE,"E2871"),sQuery(id+"F10.wireOp",EDGE,"E2872"),sQuery(id+"F10.wireOp",EDGE,"E2873"),sQuery(id+"F10.wireOp",EDGE,"E2874"),sQuery(id+"F10.wireOp",EDGE,"E2875"),sQuery(id+"F10.wireOp",EDGE,"E2876"),sQuery(id+"F10.wireOp",EDGE,"E2877"),sQuery(id+"F10.wireOp",EDGE,"E2878"),sQuery(id+"F10.wireOp",EDGE,"E2879"),sQuery(id+"F10.wireOp",EDGE,"E2880"),sQuery(id+"F10.wireOp",EDGE,"E2881"),sQuery(id+"F10.wireOp",EDGE,"E2882"),sQuery(id+"F10.wireOp",EDGE,"E2883"),sQuery(id+"F10.wireOp",EDGE,"E2884"),sQuery(id+"F10.wireOp",EDGE,"E2885"),sQuery(id+"F10.wireOp",EDGE,"E2886"),sQuery(id+"F10.wireOp",EDGE,"E2887"),sQuery(id+"F10.wireOp",EDGE,"E2888"),sQuery(id+"F10.wireOp",EDGE,"E2889"),sQuery(id+"F10.wireOp",EDGE,"E2890"),sQuery(id+"F10.wireOp",EDGE,"E2891"),sQuery(id+"F10.wireOp",EDGE,"E2892"),sQuery(id+"F10.wireOp",EDGE,"E2893"),sQuery(id+"F10.wireOp",EDGE,"E2894"),sQuery(id+"F10.wireOp",EDGE,"E2895"),sQuery(id+"F10.wireOp",EDGE,"E2896"),sQuery(id+"F10.wireOp",EDGE,"E2897"),sQuery(id+"F10.wireOp",EDGE,"E2898"),sQuery(id+"F10.wireOp",EDGE,"E2899"),sQuery(id+"F10.wireOp",EDGE,"E2900"),sQuery(id+"F10.wireOp",EDGE,"E2901"),sQuery(id+"F10.wireOp",EDGE,"E2902"),sQuery(id+"F10.wireOp",EDGE,"E2903"),sQuery(id+"F10.wireOp",EDGE,"E2904"),sQuery(id+"F10.wireOp",EDGE,"E2905"),sQuery(id+"F10.wireOp",EDGE,"E2906"),sQuery(id+"F10.wireOp",EDGE,"E2907"),sQuery(id+"F10.wireOp",EDGE,"E2908"),sQuery(id+"F10.wireOp",EDGE,"E2909"),sQuery(id+"F10.wireOp",EDGE,"E2910"),sQuery(id+"F10.wireOp",EDGE,"E2911"),sQuery(id+"F10.wireOp",EDGE,"E2912"),sQuery(id+"F10.wireOp",EDGE,"E2913"),sQuery(id+"F10.wireOp",EDGE,"E2914"),sQuery(id+"F10.wireOp",EDGE,"E2915"),sQuery(id+"F10.wireOp",EDGE,"E2916"),sQuery(id+"F10.wireOp",EDGE,"E2917"),sQuery(id+"F10.wireOp",EDGE,"E2918"),sQuery(id+"F10.wireOp",EDGE,"E2919"),sQuery(id+"F10.wireOp",EDGE,"E2920"),sQuery(id+"F10.wireOp",EDGE,"E2921"),sQuery(id+"F10.wireOp",EDGE,"E2922"),sQuery(id+"F10.wireOp",EDGE,"E2923"),sQuery(id+"F10.wireOp",EDGE,"E2924"),sQuery(id+"F10.wireOp",EDGE,"E2925"),sQuery(id+"F10.wireOp",EDGE,"E2926"),sQuery(id+"F10.wireOp",EDGE,"E2927"),sQuery(id+"F10.wireOp",EDGE,"E2928"),sQuery(id+"F10.wireOp",EDGE,"E2929"),sQuery(id+"F10.wireOp",EDGE,"E2930"),sQuery(id+"F10.wireOp",EDGE,"E2931"),sQuery(id+"F10.wireOp",EDGE,"E2932"),sQuery(id+"F10.wireOp",EDGE,"E2933"),sQuery(id+"F10.wireOp",EDGE,"E2934"),sQuery(id+"F10.wireOp",EDGE,"E2935"),sQuery(id+"F10.wireOp",EDGE,"E2936"),sQuery(id+"F10.wireOp",EDGE,"E2937"),sQuery(id+"F10.wireOp",EDGE,"E2938"),sQuery(id+"F10.wireOp",EDGE,"E2939"),sQuery(id+"F10.wireOp",EDGE,"E2940"),sQuery(id+"F10.wireOp",EDGE,"E2941"),sQuery(id+"F10.wireOp",EDGE,"E2942"),sQuery(id+"F10.wireOp",EDGE,"E2943"),sQuery(id+"F10.wireOp",EDGE,"E2944"),sQuery(id+"F10.wireOp",EDGE,"E2945"),sQuery(id+"F10.wireOp",EDGE,"E2946"),sQuery(id+"F10.wireOp",EDGE,"E2947"),sQuery(id+"F10.wireOp",EDGE,"E2948"),sQuery(id+"F10.wireOp",EDGE,"E2949"),sQuery(id+"F10.wireOp",EDGE,"E2950"),sQuery(id+"F10.wireOp",EDGE,"E2951"),sQuery(id+"F10.wireOp",EDGE,"E2952"),sQuery(id+"F10.wireOp",EDGE,"E2953"),sQuery(id+"F10.wireOp",EDGE,"E2954"),sQuery(id+"F10.wireOp",EDGE,"E2955"),sQuery(id+"F10.wireOp",EDGE,"E2956"),sQuery(id+"F10.wireOp",EDGE,"E2957"),sQuery(id+"F10.wireOp",EDGE,"E2958"),sQuery(id+"F10.wireOp",EDGE,"E2959"),sQuery(id+"F10.wireOp",EDGE,"E2960"),sQuery(id+"F10.wireOp",EDGE,"E2961"),sQuery(id+"F10.wireOp",EDGE,"E2962"),sQuery(id+"F10.wireOp",EDGE,"E2963"),sQuery(id+"F10.wireOp",EDGE,"E2964"),sQuery(id+"F10.wireOp",EDGE,"E2965"),sQuery(id+"F10.wireOp",EDGE,"E2966"),sQuery(id+"F10.wireOp",EDGE,"E2967"),sQuery(id+"F10.wireOp",EDGE,"E2968"),sQuery(id+"F10.wireOp",EDGE,"E2969"),sQuery(id+"F10.wireOp",EDGE,"E2970"),sQuery(id+"F10.wireOp",EDGE,"E2971"),sQuery(id+"F10.wireOp",EDGE,"E2972"),sQuery(id+"F10.wireOp",EDGE,"E2973"),sQuery(id+"F10.wireOp",EDGE,"E2974"),sQuery(id+"F10.wireOp",EDGE,"E2975"),sQuery(id+"F10.wireOp",EDGE,"E2976"),sQuery(id+"F10.wireOp",EDGE,"E2977"),sQuery(id+"F10.wireOp",EDGE,"E2978"),sQuery(id+"F10.wireOp",EDGE,"E2979"),sQuery(id+"F10.wireOp",EDGE,"E2980"),sQuery(id+"F10.wireOp",EDGE,"E2981"),sQuery(id+"F10.wireOp",EDGE,"E2982"),sQuery(id+"F10.wireOp",EDGE,"E2983"),sQuery(id+"F10.wireOp",EDGE,"E2984"),sQuery(id+"F10.wireOp",EDGE,"E2985"),sQuery(id+"F10.wireOp",EDGE,"E2986"),sQuery(id+"F10.wireOp",EDGE,"E2987"),sQuery(id+"F10.wireOp",EDGE,"E2988"),sQuery(id+"F10.wireOp",EDGE,"E2989"),sQuery(id+"F10.wireOp",EDGE,"E2990"),sQuery(id+"F10.wireOp",EDGE,"E2991"),sQuery(id+"F10.wireOp",EDGE,"E2992"),sQuery(id+"F10.wireOp",EDGE,"E2993"),sQuery(id+"F10.wireOp",EDGE,"E2994"),sQuery(id+"F10.wireOp",EDGE,"E2995"),sQuery(id+"F10.wireOp",EDGE,"E2996"),sQuery(id+"F10.wireOp",EDGE,"E2997"),sQuery(id+"F10.wireOp",EDGE,"E2998"),sQuery(id+"F10.wireOp",EDGE,"E2999"),sQuery(id+"F10.wireOp",EDGE,"E3000"),sQuery(id+"F10.wireOp",EDGE,"E3001"),sQuery(id+"F10.wireOp",EDGE,"E3002"),sQuery(id+"F10.wireOp",EDGE,"E3003"),sQuery(id+"F10.wireOp",EDGE,"E3004"),sQuery(id+"F10.wireOp",EDGE,"E3005"),sQuery(id+"F10.wireOp",EDGE,"E3006"),sQuery(id+"F10.wireOp",EDGE,"E3007"),sQuery(id+"F10.wireOp",EDGE,"E3008"),sQuery(id+"F10.wireOp",EDGE,"E3009"),sQuery(id+"F10.wireOp",EDGE,"E3010"),sQuery(id+"F10.wireOp",EDGE,"E3011"),sQuery(id+"F10.wireOp",EDGE,"E3012"),sQuery(id+"F10.wireOp",EDGE,"E3013"),sQuery(id+"F10.wireOp",EDGE,"E3014"),sQuery(id+"F10.wireOp",EDGE,"E3015"),sQuery(id+"F10.wireOp",EDGE,"E3016"),sQuery(id+"F10.wireOp",EDGE,"E3017"),sQuery(id+"F10.wireOp",EDGE,"E3018"),sQuery(id+"F10.wireOp",EDGE,"E3019"),sQuery(id+"F10.wireOp",EDGE,"E3020"),sQuery(id+"F10.wireOp",EDGE,"E3021"),sQuery(id+"F10.wireOp",EDGE,"E3022"),sQuery(id+"F10.wireOp",EDGE,"E3023"),sQuery(id+"F10.wireOp",EDGE,"E3024"),sQuery(id+"F10.wireOp",EDGE,"E3025"),sQuery(id+"F10.wireOp",EDGE,"E3026"),sQuery(id+"F10.wireOp",EDGE,"E3027"),sQuery(id+"F10.wireOp",EDGE,"E3028"),sQuery(id+"F10.wireOp",EDGE,"E3029"),sQuery(id+"F10.wireOp",EDGE,"E3030"),sQuery(id+"F10.wireOp",EDGE,"E3031"),sQuery(id+"F10.wireOp",EDGE,"E3032"),sQuery(id+"F10.wireOp",EDGE,"E3033"),sQuery(id+"F10.wireOp",EDGE,"E3034"),sQuery(id+"F10.wireOp",EDGE,"E3035"),sQuery(id+"F10.wireOp",EDGE,"E3036"),sQuery(id+"F10.wireOp",EDGE,"E3037"),sQuery(id+"F10.wireOp",EDGE,"E3038"),sQuery(id+"F10.wireOp",EDGE,"E3039"),sQuery(id+"F10.wireOp",EDGE,"E3040"),sQuery(id+"F10.wireOp",EDGE,"E3041"),sQuery(id+"F10.wireOp",EDGE,"E3042"),sQuery(id+"F10.wireOp",EDGE,"E3043"),sQuery(id+"F10.wireOp",EDGE,"E3044"),sQuery(id+"F10.wireOp",EDGE,"E3045"),sQuery(id+"F10.wireOp",EDGE,"E3046"),sQuery(id+"F10.wireOp",EDGE,"E3047"),sQuery(id+"F10.wireOp",EDGE,"E3048"),sQuery(id+"F10.wireOp",EDGE,"E3049"),sQuery(id+"F10.wireOp",EDGE,"E3050"),sQuery(id+"F10.wireOp",EDGE,"E3051"),sQuery(id+"F10.wireOp",EDGE,"E3052"),sQuery(id+"F10.wireOp",EDGE,"E3053"),sQuery(id+"F10.wireOp",EDGE,"E3054"),sQuery(id+"F10.wireOp",EDGE,"E3055"),sQuery(id+"F10.wireOp",EDGE,"E3056"),sQuery(id+"F10.wireOp",EDGE,"E3057"),sQuery(id+"F10.wireOp",EDGE,"E3058"),sQuery(id+"F10.wireOp",EDGE,"E3059"),sQuery(id+"F10.wireOp",EDGE,"E3060"),sQuery(id+"F10.wireOp",EDGE,"E3061"),sQuery(id+"F10.wireOp",EDGE,"E3062"),sQuery(id+"F10.wireOp",EDGE,"E3063"),sQuery(id+"F10.wireOp",EDGE,"E3064"),sQuery(id+"F10.wireOp",EDGE,"E3065"),sQuery(id+"F10.wireOp",EDGE,"E3066"),sQuery(id+"F10.wireOp",EDGE,"E3067"),sQuery(id+"F10.wireOp",EDGE,"E3068"),sQuery(id+"F10.wireOp",EDGE,"E3069"),sQuery(id+"F10.wireOp",EDGE,"E3070"),sQuery(id+"F10.wireOp",EDGE,"E3071"),sQuery(id+"F10.wireOp",EDGE,"E3072"),sQuery(id+"F10.wireOp",EDGE,"E3073"),sQuery(id+"F10.wireOp",EDGE,"E3074"),sQuery(id+"F10.wireOp",EDGE,"E3075"),sQuery(id+"F10.wireOp",EDGE,"E3076"),sQuery(id+"F10.wireOp",EDGE,"E3077"),sQuery(id+"F10.wireOp",EDGE,"E3078"),sQuery(id+"F10.wireOp",EDGE,"E3079"),sQuery(id+"F10.wireOp",EDGE,"E3080"),sQuery(id+"F10.wireOp",EDGE,"E3081"),sQuery(id+"F10.wireOp",EDGE,"E3082"),sQuery(id+"F10.wireOp",EDGE,"E3083"),sQuery(id+"F10.wireOp",EDGE,"E3084"),sQuery(id+"F10.wireOp",EDGE,"E3085"),sQuery(id+"F10.wireOp",EDGE,"E3086"),sQuery(id+"F10.wireOp",EDGE,"E3087"),sQuery(id+"F10.wireOp",EDGE,"E3088"),sQuery(id+"F10.wireOp",EDGE,"E3089"),sQuery(id+"F10.wireOp",EDGE,"E3090"),sQuery(id+"F10.wireOp",EDGE,"E3091"),sQuery(id+"F10.wireOp",EDGE,"E3092"),sQuery(id+"F10.wireOp",EDGE,"E3093"),sQuery(id+"F10.wireOp",EDGE,"E3094"),sQuery(id+"F10.wireOp",EDGE,"E3095"),sQuery(id+"F10.wireOp",EDGE,"E3096"),sQuery(id+"F10.wireOp",EDGE,"E3097"),sQuery(id+"F10.wireOp",EDGE,"E3098"),sQuery(id+"F10.wireOp",EDGE,"E3099"),sQuery(id+"F10.wireOp",EDGE,"E3100"),sQuery(id+"F10.wireOp",EDGE,"E3101"),sQuery(id+"F10.wireOp",EDGE,"E3102"),sQuery(id+"F10.wireOp",EDGE,"E3103"),sQuery(id+"F10.wireOp",EDGE,"E3104"),sQuery(id+"F10.wireOp",EDGE,"E3105"),sQuery(id+"F10.wireOp",EDGE,"E3106"),sQuery(id+"F10.wireOp",EDGE,"E3107"),sQuery(id+"F10.wireOp",EDGE,"E3108"),sQuery(id+"F10.wireOp",EDGE,"E3109"),sQuery(id+"F10.wireOp",EDGE,"E3110"),sQuery(id+"F10.wireOp",EDGE,"E3111"),sQuery(id+"F10.wireOp",EDGE,"E3112"),sQuery(id+"F10.wireOp",EDGE,"E3113"),sQuery(id+"F10.wireOp",EDGE,"E3114"),sQuery(id+"F10.wireOp",EDGE,"E3115"),sQuery(id+"F10.wireOp",EDGE,"E3116"),sQuery(id+"F10.wireOp",EDGE,"E3117"),sQuery(id+"F10.wireOp",EDGE,"E3118"),sQuery(id+"F10.wireOp",EDGE,"E3119"),sQuery(id+"F10.wireOp",EDGE,"E3120"),sQuery(id+"F10.wireOp",EDGE,"E3121"),sQuery(id+"F10.wireOp",EDGE,"E3122"),sQuery(id+"F10.wireOp",EDGE,"E3123"),sQuery(id+"F10.wireOp",EDGE,"E3124"),sQuery(id+"F10.wireOp",EDGE,"E3125"),sQuery(id+"F10.wireOp",EDGE,"E3126"),sQuery(id+"F10.wireOp",EDGE,"E3127"),sQuery(id+"F10.wireOp",EDGE,"E3128"),sQuery(id+"F10.wireOp",EDGE,"E3129"),sQuery(id+"F10.wireOp",EDGE,"E3130"),sQuery(id+"F10.wireOp",EDGE,"E3131"),sQuery(id+"F10.wireOp",EDGE,"E3132"),sQuery(id+"F10.wireOp",EDGE,"E3133"),sQuery(id+"F10.wireOp",EDGE,"E3134"),sQuery(id+"F10.wireOp",EDGE,"E3135"),sQuery(id+"F10.wireOp",EDGE,"E3136"),sQuery(id+"F10.wireOp",EDGE,"E3137"),sQuery(id+"F10.wireOp",EDGE,"E3138"),sQuery(id+"F10.wireOp",EDGE,"E3139"),sQuery(id+"F10.wireOp",EDGE,"E3140"),sQuery(id+"F10.wireOp",EDGE,"E3141"),sQuery(id+"F10.wireOp",EDGE,"E3142"),sQuery(id+"F10.wireOp",EDGE,"E3143"),sQuery(id+"F10.wireOp",EDGE,"E3144"),sQuery(id+"F10.wireOp",EDGE,"E3145"),sQuery(id+"F10.wireOp",EDGE,"E3146"),sQuery(id+"F10.wireOp",EDGE,"E3147"),sQuery(id+"F10.wireOp",EDGE,"E3148"),sQuery(id+"F10.wireOp",EDGE,"E3149"),sQuery(id+"F10.wireOp",EDGE,"E3150"),sQuery(id+"F10.wireOp",EDGE,"E3151"),sQuery(id+"F10.wireOp",EDGE,"E3152"),sQuery(id+"F10.wireOp",EDGE,"E3153"),sQuery(id+"F10.wireOp",EDGE,"E3154"),sQuery(id+"F10.wireOp",EDGE,"E3155"),sQuery(id+"F10.wireOp",EDGE,"E3156"),sQuery(id+"F10.wireOp",EDGE,"E3157"),sQuery(id+"F10.wireOp",EDGE,"E3158"),sQuery(id+"F10.wireOp",EDGE,"E3159"),sQuery(id+"F10.wireOp",EDGE,"E3160"),sQuery(id+"F10.wireOp",EDGE,"E3161"),sQuery(id+"F10.wireOp",EDGE,"E3162"),sQuery(id+"F10.wireOp",EDGE,"E3163"),sQuery(id+"F10.wireOp",EDGE,"E3164"),sQuery(id+"F10.wireOp",EDGE,"E3165"),sQuery(id+"F10.wireOp",EDGE,"E3166"),sQuery(id+"F10.wireOp",EDGE,"E3167"),sQuery(id+"F10.wireOp",EDGE,"E3168"),sQuery(id+"F10.wireOp",EDGE,"E3169"),sQuery(id+"F10.wireOp",EDGE,"E3170"),sQuery(id+"F10.wireOp",EDGE,"E3171"),sQuery(id+"F10.wireOp",EDGE,"E3172"),sQuery(id+"F10.wireOp",EDGE,"E3173"),sQuery(id+"F10.wireOp",EDGE,"E3174"),sQuery(id+"F10.wireOp",EDGE,"E3175"),sQuery(id+"F10.wireOp",EDGE,"E3176"),sQuery(id+"F10.wireOp",EDGE,"E3177"),sQuery(id+"F10.wireOp",EDGE,"E3178"),sQuery(id+"F10.wireOp",EDGE,"E3179"),sQuery(id+"F10.wireOp",EDGE,"E3180"),sQuery(id+"F10.wireOp",EDGE,"E3181"),sQuery(id+"F10.wireOp",EDGE,"E3182"),sQuery(id+"F10.wireOp",EDGE,"E3183"),sQuery(id+"F10.wireOp",EDGE,"E3184"),sQuery(id+"F10.wireOp",EDGE,"E3185"),sQuery(id+"F10.wireOp",EDGE,"E3186"),sQuery(id+"F10.wireOp",EDGE,"E3187"),sQuery(id+"F10.wireOp",EDGE,"E3188"),sQuery(id+"F10.wireOp",EDGE,"E3189"),sQuery(id+"F10.wireOp",EDGE,"E3190"),sQuery(id+"F10.wireOp",EDGE,"E3191"),sQuery(id+"F10.wireOp",EDGE,"E3192"),sQuery(id+"F10.wireOp",EDGE,"E3193"),sQuery(id+"F10.wireOp",EDGE,"E3194"),sQuery(id+"F10.wireOp",EDGE,"E3195"),sQuery(id+"F10.wireOp",EDGE,"E3196"),sQuery(id+"F10.wireOp",EDGE,"E3197"),sQuery(id+"F10.wireOp",EDGE,"E3198"),sQuery(id+"F10.wireOp",EDGE,"E3199"),sQuery(id+"F10.wireOp",EDGE,"E3200"),sQuery(id+"F10.wireOp",EDGE,"E3201"),sQuery(id+"F10.wireOp",EDGE,"E3202"),sQuery(id+"F10.wireOp",EDGE,"E3203"),sQuery(id+"F10.wireOp",EDGE,"E3204"),sQuery(id+"F10.wireOp",EDGE,"E3205"),sQuery(id+"F10.wireOp",EDGE,"E3206"),sQuery(id+"F10.wireOp",EDGE,"E3207"),sQuery(id+"F10.wireOp",EDGE,"E3208"),sQuery(id+"F10.wireOp",EDGE,"E3209"),sQuery(id+"F10.wireOp",EDGE,"E3210"),sQuery(id+"F10.wireOp",EDGE,"E3211"),sQuery(id+"F10.wireOp",EDGE,"E3212"),sQuery(id+"F10.wireOp",EDGE,"E3213"),sQuery(id+"F10.wireOp",EDGE,"E3214"),sQuery(id+"F10.wireOp",EDGE,"E3215"),sQuery(id+"F10.wireOp",EDGE,"E3216"),sQuery(id+"F10.wireOp",EDGE,"E3217"),sQuery(id+"F10.wireOp",EDGE,"E3218"),sQuery(id+"F10.wireOp",EDGE,"E3219"),sQuery(id+"F10.wireOp",EDGE,"E3220"),sQuery(id+"F10.wireOp",EDGE,"E3221"),sQuery(id+"F10.wireOp",EDGE,"E3222"),sQuery(id+"F10.wireOp",EDGE,"E3223"),sQuery(id+"F10.wireOp",EDGE,"E3224"),sQuery(id+"F10.wireOp",EDGE,"E3225"),sQuery(id+"F10.wireOp",EDGE,"E3226"),sQuery(id+"F10.wireOp",EDGE,"E3227"),sQuery(id+"F10.wireOp",EDGE,"E3228"),sQuery(id+"F10.wireOp",EDGE,"E3229"),sQuery(id+"F10.wireOp",EDGE,"E3230"),sQuery(id+"F10.wireOp",EDGE,"E3231"),sQuery(id+"F10.wireOp",EDGE,"E3232"),sQuery(id+"F10.wireOp",EDGE,"E3233"),sQuery(id+"F10.wireOp",EDGE,"E3234"),sQuery(id+"F10.wireOp",EDGE,"E3235"),sQuery(id+"F10.wireOp",EDGE,"E3236"),sQuery(id+"F10.wireOp",EDGE,"E3237"),sQuery(id+"F10.wireOp",EDGE,"E3238"),sQuery(id+"F10.wireOp",EDGE,"E3239"),sQuery(id+"F10.wireOp",EDGE,"E3240"),sQuery(id+"F10.wireOp",EDGE,"E3241"),sQuery(id+"F10.wireOp",EDGE,"E3242"),sQuery(id+"F10.wireOp",EDGE,"E3243"),sQuery(id+"F10.wireOp",EDGE,"E3244"),sQuery(id+"F10.wireOp",EDGE,"E3245"),sQuery(id+"F10.wireOp",EDGE,"E3246"),sQuery(id+"F10.wireOp",EDGE,"E3247"),sQuery(id+"F10.wireOp",EDGE,"E3248"),sQuery(id+"F10.wireOp",EDGE,"E3249"),sQuery(id+"F10.wireOp",EDGE,"E3250"),sQuery(id+"F10.wireOp",EDGE,"E3251"),sQuery(id+"F10.wireOp",EDGE,"E3252"),sQuery(id+"F10.wireOp",EDGE,"E3253"),sQuery(id+"F10.wireOp",EDGE,"E3254"),sQuery(id+"F10.wireOp",EDGE,"E3255"),sQuery(id+"F10.wireOp",EDGE,"E3256"),sQuery(id+"F10.wireOp",EDGE,"E3257"),sQuery(id+"F10.wireOp",EDGE,"E3258"),sQuery(id+"F10.wireOp",EDGE,"E3259"),sQuery(id+"F10.wireOp",EDGE,"E3260"),sQuery(id+"F10.wireOp",EDGE,"E3261"),sQuery(id+"F10.wireOp",EDGE,"E3262"),sQuery(id+"F10.wireOp",EDGE,"E3263"),sQuery(id+"F10.wireOp",EDGE,"E3264"),sQuery(id+"F10.wireOp",EDGE,"E3265"),sQuery(id+"F10.wireOp",EDGE,"E3266"),sQuery(id+"F10.wireOp",EDGE,"E3267"),sQuery(id+"F10.wireOp",EDGE,"E3268"),sQuery(id+"F10.wireOp",EDGE,"E3269"),sQuery(id+"F10.wireOp",EDGE,"E3270"),sQuery(id+"F10.wireOp",EDGE,"E3271"),sQuery(id+"F10.wireOp",EDGE,"E3272"),sQuery(id+"F10.wireOp",EDGE,"E3273"),sQuery(id+"F10.wireOp",EDGE,"E3274"),sQuery(id+"F10.wireOp",EDGE,"E3275"),sQuery(id+"F10.wireOp",EDGE,"E3276"),sQuery(id+"F10.wireOp",EDGE,"E3277"),sQuery(id+"F10.wireOp",EDGE,"E3278"),sQuery(id+"F10.wireOp",EDGE,"E3279"),sQuery(id+"F10.wireOp",EDGE,"E3280"),sQuery(id+"F10.wireOp",EDGE,"E3281"),sQuery(id+"F10.wireOp",EDGE,"E3282"),sQuery(id+"F10.wireOp",EDGE,"E3283"),sQuery(id+"F10.wireOp",EDGE,"E3284"),sQuery(id+"F10.wireOp",EDGE,"E3285"),sQuery(id+"F10.wireOp",EDGE,"E3286"),sQuery(id+"F10.wireOp",EDGE,"E3287"),sQuery(id+"F10.wireOp",EDGE,"E3288"),sQuery(id+"F10.wireOp",EDGE,"E3289"),sQuery(id+"F10.wireOp",EDGE,"E3290"),sQuery(id+"F10.wireOp",EDGE,"E3291"),sQuery(id+"F10.wireOp",EDGE,"E3292"),sQuery(id+"F10.wireOp",EDGE,"E3293"),sQuery(id+"F10.wireOp",EDGE,"E3294"),sQuery(id+"F10.wireOp",EDGE,"E3295"),sQuery(id+"F10.wireOp",EDGE,"E3296"),sQuery(id+"F10.wireOp",EDGE,"E3297"),sQuery(id+"F10.wireOp",EDGE,"E3298"),sQuery(id+"F10.wireOp",EDGE,"E3299"),sQuery(id+"F10.wireOp",EDGE,"E3300"),sQuery(id+"F10.wireOp",EDGE,"E3301"),sQuery(id+"F10.wireOp",EDGE,"E3302"),sQuery(id+"F10.wireOp",EDGE,"E3303"),sQuery(id+"F10.wireOp",EDGE,"E3304"),sQuery(id+"F10.wireOp",EDGE,"E3305"),sQuery(id+"F10.wireOp",EDGE,"E3306"),sQuery(id+"F10.wireOp",EDGE,"E3307"),sQuery(id+"F10.wireOp",EDGE,"E3308"),sQuery(id+"F10.wireOp",EDGE,"E3309"),sQuery(id+"F10.wireOp",EDGE,"E3310"),sQuery(id+"F10.wireOp",EDGE,"E3311"),sQuery(id+"F10.wireOp",EDGE,"E3312"),sQuery(id+"F10.wireOp",EDGE,"E3313"),sQuery(id+"F10.wireOp",EDGE,"E3314"),sQuery(id+"F10.wireOp",EDGE,"E3315"),sQuery(id+"F10.wireOp",EDGE,"E3316"),sQuery(id+"F10.wireOp",EDGE,"E3317"),sQuery(id+"F10.wireOp",EDGE,"E3318"),sQuery(id+"F10.wireOp",EDGE,"E3319"),sQuery(id+"F10.wireOp",EDGE,"E3320"),sQuery(id+"F10.wireOp",EDGE,"E3321"),sQuery(id+"F10.wireOp",EDGE,"E3322"),sQuery(id+"F10.wireOp",EDGE,"E3323"),sQuery(id+"F10.wireOp",EDGE,"E3324"),sQuery(id+"F10.wireOp",EDGE,"E3325"),sQuery(id+"F10.wireOp",EDGE,"E3326"),sQuery(id+"F10.wireOp",EDGE,"E3327"),sQuery(id+"F10.wireOp",EDGE,"E3328"),sQuery(id+"F10.wireOp",EDGE,"E3329"),sQuery(id+"F10.wireOp",EDGE,"E3330"),sQuery(id+"F10.wireOp",EDGE,"E3331"),sQuery(id+"F10.wireOp",EDGE,"E3332"),sQuery(id+"F10.wireOp",EDGE,"E3333"),sQuery(id+"F10.wireOp",EDGE,"E3334"),sQuery(id+"F10.wireOp",EDGE,"E3335"),sQuery(id+"F10.wireOp",EDGE,"E3336"),sQuery(id+"F10.wireOp",EDGE,"E3337"),sQuery(id+"F10.wireOp",EDGE,"E3338"),sQuery(id+"F10.wireOp",EDGE,"E3339"),sQuery(id+"F10.wireOp",EDGE,"E3340"),sQuery(id+"F10.wireOp",EDGE,"E3341"),sQuery(id+"F10.wireOp",EDGE,"E3342"),sQuery(id+"F10.wireOp",EDGE,"E3343"),sQuery(id+"F10.wireOp",EDGE,"E3344"),sQuery(id+"F10.wireOp",EDGE,"E3345"),sQuery(id+"F10.wireOp",EDGE,"E3346"),sQuery(id+"F10.wireOp",EDGE,"E3347"),sQuery(id+"F10.wireOp",EDGE,"E3348"),sQuery(id+"F10.wireOp",EDGE,"E3349"),sQuery(id+"F10.wireOp",EDGE,"E3350"),sQuery(id+"F10.wireOp",EDGE,"E3351"),sQuery(id+"F10.wireOp",EDGE,"E3352"),sQuery(id+"F10.wireOp",EDGE,"E3353"),sQuery(id+"F10.wireOp",EDGE,"E3354"),sQuery(id+"F10.wireOp",EDGE,"E3355"),sQuery(id+"F10.wireOp",EDGE,"E3356"),sQuery(id+"F10.wireOp",EDGE,"E3357"),sQuery(id+"F10.wireOp",EDGE,"E3358"),sQuery(id+"F10.wireOp",EDGE,"E3359"),sQuery(id+"F10.wireOp",EDGE,"E3360"),sQuery(id+"F10.wireOp",EDGE,"E3361"),sQuery(id+"F10.wireOp",EDGE,"E3362"),sQuery(id+"F10.wireOp",EDGE,"E3363"),sQuery(id+"F10.wireOp",EDGE,"E3364"),sQuery(id+"F10.wireOp",EDGE,"E3365"),sQuery(id+"F10.wireOp",EDGE,"E3366"),sQuery(id+"F10.wireOp",EDGE,"E3367"),sQuery(id+"F10.wireOp",EDGE,"E3368"),sQuery(id+"F10.wireOp",EDGE,"E3369"),sQuery(id+"F10.wireOp",EDGE,"E3370"),sQuery(id+"F10.wireOp",EDGE,"E3371"),sQuery(id+"F10.wireOp",EDGE,"E3372"),sQuery(id+"F10.wireOp",EDGE,"E3373"),sQuery(id+"F10.wireOp",EDGE,"E3374"),sQuery(id+"F10.wireOp",EDGE,"E3375"),sQuery(id+"F10.wireOp",EDGE,"E3376"),sQuery(id+"F10.wireOp",EDGE,"E3377"),sQuery(id+"F10.wireOp",EDGE,"E3378"),sQuery(id+"F10.wireOp",EDGE,"E3379"),sQuery(id+"F10.wireOp",EDGE,"E3380"),sQuery(id+"F10.wireOp",EDGE,"E3381"),sQuery(id+"F10.wireOp",EDGE,"E3382"),sQuery(id+"F10.wireOp",EDGE,"E3383"),sQuery(id+"F10.wireOp",EDGE,"E3384"),sQuery(id+"F10.wireOp",EDGE,"E3385"),sQuery(id+"F10.wireOp",EDGE,"E3386"),sQuery(id+"F10.wireOp",EDGE,"E3387"),sQuery(id+"F10.wireOp",EDGE,"E3388"),sQuery(id+"F10.wireOp",EDGE,"E3389"),sQuery(id+"F10.wireOp",EDGE,"E3390"),sQuery(id+"F10.wireOp",EDGE,"E3391"),sQuery(id+"F10.wireOp",EDGE,"E3392"),sQuery(id+"F10.wireOp",EDGE,"E3393"),sQuery(id+"F10.wireOp",EDGE,"E3394"),sQuery(id+"F10.wireOp",EDGE,"E3395"),sQuery(id+"F10.wireOp",EDGE,"E3396"),sQuery(id+"F10.wireOp",EDGE,"E3397"),sQuery(id+"F10.wireOp",EDGE,"E3398"),sQuery(id+"F10.wireOp",EDGE,"E3399"),sQuery(id+"F10.wireOp",EDGE,"E3400"),sQuery(id+"F10.wireOp",EDGE,"E3401"),sQuery(id+"F10.wireOp",EDGE,"E3402"),sQuery(id+"F10.wireOp",EDGE,"E3403"),sQuery(id+"F10.wireOp",EDGE,"E3404"),sQuery(id+"F10.wireOp",EDGE,"E3405"),sQuery(id+"F10.wireOp",EDGE,"E3406"),sQuery(id+"F10.wireOp",EDGE,"E3407"),sQuery(id+"F10.wireOp",EDGE,"E3408"),sQuery(id+"F10.wireOp",EDGE,"E3409"),sQuery(id+"F10.wireOp",EDGE,"E3410"),sQuery(id+"F10.wireOp",EDGE,"E3411"),sQuery(id+"F10.wireOp",EDGE,"E3412"),sQuery(id+"F10.wireOp",EDGE,"E3413"),sQuery(id+"F10.wireOp",EDGE,"E3414"),sQuery(id+"F10.wireOp",EDGE,"E3415"),sQuery(id+"F10.wireOp",EDGE,"E3416"),sQuery(id+"F10.wireOp",EDGE,"E3417"),sQuery(id+"F10.wireOp",EDGE,"E3418"),sQuery(id+"F10.wireOp",EDGE,"E3419"),sQuery(id+"F10.wireOp",EDGE,"E3420"),sQuery(id+"F10.wireOp",EDGE,"E3421"),sQuery(id+"F10.wireOp",EDGE,"E3422"),sQuery(id+"F10.wireOp",EDGE,"E3423"),sQuery(id+"F10.wireOp",EDGE,"E3424"),sQuery(id+"F10.wireOp",EDGE,"E3425"),sQuery(id+"F10.wireOp",EDGE,"E3426"),sQuery(id+"F10.wireOp",EDGE,"E3427"),sQuery(id+"F10.wireOp",EDGE,"E3428"),sQuery(id+"F10.wireOp",EDGE,"E3429"),sQuery(id+"F10.wireOp",EDGE,"E3430"),sQuery(id+"F10.wireOp",EDGE,"E3431"),sQuery(id+"F10.wireOp",EDGE,"E3432"),sQuery(id+"F10.wireOp",EDGE,"E3433"),sQuery(id+"F10.wireOp",EDGE,"E3434"),sQuery(id+"F10.wireOp",EDGE,"E3435"),sQuery(id+"F10.wireOp",EDGE,"E3436"),sQuery(id+"F10.wireOp",EDGE,"E3437"),sQuery(id+"F10.wireOp",EDGE,"E3438"),sQuery(id+"F10.wireOp",EDGE,"E3439"),sQuery(id+"F10.wireOp",EDGE,"E3440"),sQuery(id+"F10.wireOp",EDGE,"E3441"),sQuery(id+"F10.wireOp",EDGE,"E3442"),sQuery(id+"F10.wireOp",EDGE,"E3443"),sQuery(id+"F10.wireOp",EDGE,"E3444"),sQuery(id+"F10.wireOp",EDGE,"E3445"),sQuery(id+"F10.wireOp",EDGE,"E3446"),sQuery(id+"F10.wireOp",EDGE,"E3447"),sQuery(id+"F10.wireOp",EDGE,"E3448"),sQuery(id+"F10.wireOp",EDGE,"E3449"),sQuery(id+"F10.wireOp",EDGE,"E3450"),sQuery(id+"F10.wireOp",EDGE,"E3451"),sQuery(id+"F10.wireOp",EDGE,"E3452"),sQuery(id+"F10.wireOp",EDGE,"E3453"),sQuery(id+"F10.wireOp",EDGE,"E3454"),sQuery(id+"F10.wireOp",EDGE,"E3455"),sQuery(id+"F10.wireOp",EDGE,"E3456"),sQuery(id+"F10.wireOp",EDGE,"E3457"),sQuery(id+"F10.wireOp",EDGE,"E3458"),sQuery(id+"F10.wireOp",EDGE,"E3459"),sQuery(id+"F10.wireOp",EDGE,"E3460"),sQuery(id+"F10.wireOp",EDGE,"E3461"),sQuery(id+"F10.wireOp",EDGE,"E3462"),sQuery(id+"F10.wireOp",EDGE,"E3463"),sQuery(id+"F10.wireOp",EDGE,"E3464"),sQuery(id+"F10.wireOp",EDGE,"E3465"),sQuery(id+"F10.wireOp",EDGE,"E3466"),sQuery(id+"F10.wireOp",EDGE,"E3467"),sQuery(id+"F10.wireOp",EDGE,"E3468"),sQuery(id+"F10.wireOp",EDGE,"E3469"),sQuery(id+"F10.wireOp",EDGE,"E3470"),sQuery(id+"F10.wireOp",EDGE,"E3471"),sQuery(id+"F10.wireOp",EDGE,"E3472"),sQuery(id+"F10.wireOp",EDGE,"E3473"),sQuery(id+"F10.wireOp",EDGE,"E3474"),sQuery(id+"F10.wireOp",EDGE,"E3475"),sQuery(id+"F10.wireOp",EDGE,"E3476"),sQuery(id+"F10.wireOp",EDGE,"E3477"),sQuery(id+"F10.wireOp",EDGE,"E3478"),sQuery(id+"F10.wireOp",EDGE,"E3479"),sQuery(id+"F10.wireOp",EDGE,"E3480"),sQuery(id+"F10.wireOp",EDGE,"E3481"),sQuery(id+"F10.wireOp",EDGE,"E3482"),sQuery(id+"F10.wireOp",EDGE,"E3483"),sQuery(id+"F10.wireOp",EDGE,"E3484"),sQuery(id+"F10.wireOp",EDGE,"E3485"),sQuery(id+"F10.wireOp",EDGE,"E3486"),sQuery(id+"F10.wireOp",EDGE,"E3487"),sQuery(id+"F10.wireOp",EDGE,"E3488"),sQuery(id+"F10.wireOp",EDGE,"E3489"),sQuery(id+"F10.wireOp",EDGE,"E3490"),sQuery(id+"F10.wireOp",EDGE,"E3491"),sQuery(id+"F10.wireOp",EDGE,"E3492"),sQuery(id+"F10.wireOp",EDGE,"E3493"),sQuery(id+"F10.wireOp",EDGE,"E3494"),sQuery(id+"F10.wireOp",EDGE,"E3495"),sQuery(id+"F10.wireOp",EDGE,"E3496"),sQuery(id+"F10.wireOp",EDGE,"E3497"),sQuery(id+"F10.wireOp",EDGE,"E3498"),sQuery(id+"F10.wireOp",EDGE,"E3499"),sQuery(id+"F10.wireOp",EDGE,"E3500"),sQuery(id+"F10.wireOp",EDGE,"E3501"),sQuery(id+"F10.wireOp",EDGE,"E3502"),sQuery(id+"F10.wireOp",EDGE,"E3503"),sQuery(id+"F10.wireOp",EDGE,"E3504"),sQuery(id+"F10.wireOp",EDGE,"E3505"),sQuery(id+"F10.wireOp",EDGE,"E3506"),sQuery(id+"F10.wireOp",EDGE,"E3507"),sQuery(id+"F10.wireOp",EDGE,"E3508"),sQuery(id+"F10.wireOp",EDGE,"E3509"),sQuery(id+"F10.wireOp",EDGE,"E3510"),sQuery(id+"F10.wireOp",EDGE,"E3511"),sQuery(id+"F10.wireOp",EDGE,"E3512"),sQuery(id+"F10.wireOp",EDGE,"E3513"),sQuery(id+"F10.wireOp",EDGE,"E3514"),sQuery(id+"F10.wireOp",EDGE,"E3515"),sQuery(id+"F10.wireOp",EDGE,"E3516"),sQuery(id+"F10.wireOp",EDGE,"E3517"),sQuery(id+"F10.wireOp",EDGE,"E3518"),sQuery(id+"F10.wireOp",EDGE,"E3519"),sQuery(id+"F10.wireOp",EDGE,"E3520"),sQuery(id+"F10.wireOp",EDGE,"E3521"),sQuery(id+"F10.wireOp",EDGE,"E3522"),sQuery(id+"F10.wireOp",EDGE,"E3523"),sQuery(id+"F10.wireOp",EDGE,"E3524"),sQuery(id+"F10.wireOp",EDGE,"E3525"),sQuery(id+"F10.wireOp",EDGE,"E3526"),sQuery(id+"F10.wireOp",EDGE,"E3527"),sQuery(id+"F10.wireOp",EDGE,"E3528"),sQuery(id+"F10.wireOp",EDGE,"E3529"),sQuery(id+"F10.wireOp",EDGE,"E3530"),sQuery(id+"F10.wireOp",EDGE,"E3531"),sQuery(id+"F10.wireOp",EDGE,"E3532"),sQuery(id+"F10.wireOp",EDGE,"E3533"),sQuery(id+"F10.wireOp",EDGE,"E3534"),sQuery(id+"F10.wireOp",EDGE,"E3535"),sQuery(id+"F10.wireOp",EDGE,"E3536"),sQuery(id+"F10.wireOp",EDGE,"E3537"),sQuery(id+"F10.wireOp",EDGE,"E3538"),sQuery(id+"F10.wireOp",EDGE,"E3539"),sQuery(id+"F10.wireOp",EDGE,"E3540"),sQuery(id+"F10.wireOp",EDGE,"E3541"),sQuery(id+"F10.wireOp",EDGE,"E3542"),sQuery(id+"F10.wireOp",EDGE,"E3543"),sQuery(id+"F10.wireOp",EDGE,"E3544"),sQuery(id+"F10.wireOp",EDGE,"E3545"),sQuery(id+"F10.wireOp",EDGE,"E3546"),sQuery(id+"F10.wireOp",EDGE,"E3547"),sQuery(id+"F10.wireOp",EDGE,"E3548"),sQuery(id+"F10.wireOp",EDGE,"E3549"),sQuery(id+"F10.wireOp",EDGE,"E3550"),sQuery(id+"F10.wireOp",EDGE,"E3551"),sQuery(id+"F10.wireOp",EDGE,"E3552"),sQuery(id+"F10.wireOp",EDGE,"E3553"),sQuery(id+"F10.wireOp",EDGE,"E3554"),sQuery(id+"F10.wireOp",EDGE,"E3555"),sQuery(id+"F10.wireOp",EDGE,"E3556"),sQuery(id+"F10.wireOp",EDGE,"E3557"),sQuery(id+"F10.wireOp",EDGE,"E3558"),sQuery(id+"F10.wireOp",EDGE,"E3559"),sQuery(id+"F10.wireOp",EDGE,"E3560"),sQuery(id+"F10.wireOp",EDGE,"E3561"),sQuery(id+"F10.wireOp",EDGE,"E3562"),sQuery(id+"F10.wireOp",EDGE,"E3563"),sQuery(id+"F10.wireOp",EDGE,"E3564"),sQuery(id+"F10.wireOp",EDGE,"E3565"),sQuery(id+"F10.wireOp",EDGE,"E3566"),sQuery(id+"F10.wireOp",EDGE,"E3567"),sQuery(id+"F10.wireOp",EDGE,"E3568"),sQuery(id+"F10.wireOp",EDGE,"E3569"),sQuery(id+"F10.wireOp",EDGE,"E3570"),sQuery(id+"F10.wireOp",EDGE,"E3571"),sQuery(id+"F10.wireOp",EDGE,"E3572"),sQuery(id+"F10.wireOp",EDGE,"E3573"),sQuery(id+"F10.wireOp",EDGE,"E3574"),sQuery(id+"F10.wireOp",EDGE,"E3575"),sQuery(id+"F10.wireOp",EDGE,"E3576"),sQuery(id+"F10.wireOp",EDGE,"E3577"),sQuery(id+"F10.wireOp",EDGE,"E3578"),sQuery(id+"F10.wireOp",EDGE,"E3579"),sQuery(id+"F10.wireOp",EDGE,"E3580"),sQuery(id+"F10.wireOp",EDGE,"E3581"),sQuery(id+"F10.wireOp",EDGE,"E3582"),sQuery(id+"F10.wireOp",EDGE,"E3583"),sQuery(id+"F10.wireOp",EDGE,"E3584"),sQuery(id+"F10.wireOp",EDGE,"E3585"),sQuery(id+"F10.wireOp",EDGE,"E3586"),sQuery(id+"F10.wireOp",EDGE,"E3587"),sQuery(id+"F10.wireOp",EDGE,"E3588"),sQuery(id+"F10.wireOp",EDGE,"E3589"),sQuery(id+"F10.wireOp",EDGE,"E3590"),sQuery(id+"F10.wireOp",EDGE,"E3591"),sQuery(id+"F10.wireOp",EDGE,"E3592"),sQuery(id+"F10.wireOp",EDGE,"E3593"),sQuery(id+"F10.wireOp",EDGE,"E3594"),sQuery(id+"F10.wireOp",EDGE,"E3595"),sQuery(id+"F10.wireOp",EDGE,"E3596"),sQuery(id+"F10.wireOp",EDGE,"E3597"),sQuery(id+"F10.wireOp",EDGE,"E3598"),sQuery(id+"F10.wireOp",EDGE,"E3599"),sQuery(id+"F10.wireOp",EDGE,"E3600"),sQuery(id+"F10.wireOp",EDGE,"E3601"),sQuery(id+"F10.wireOp",EDGE,"E3602"),sQuery(id+"F10.wireOp",EDGE,"E3603"),sQuery(id+"F10.wireOp",EDGE,"E3604"),sQuery(id+"F10.wireOp",EDGE,"E3605"),sQuery(id+"F10.wireOp",EDGE,"E3606"),sQuery(id+"F10.wireOp",EDGE,"E3607"),sQuery(id+"F10.wireOp",EDGE,"E3608"),sQuery(id+"F10.wireOp",EDGE,"E3609"),sQuery(id+"F10.wireOp",EDGE,"E3610"),sQuery(id+"F10.wireOp",EDGE,"E3611"),sQuery(id+"F10.wireOp",EDGE,"E3612"),sQuery(id+"F10.wireOp",EDGE,"E3613"),sQuery(id+"F10.wireOp",EDGE,"E3614"),sQuery(id+"F10.wireOp",EDGE,"E3615"),sQuery(id+"F10.wireOp",EDGE,"E3616"),sQuery(id+"F10.wireOp",EDGE,"E3617"),sQuery(id+"F10.wireOp",EDGE,"E3618"),sQuery(id+"F10.wireOp",EDGE,"E3619"),sQuery(id+"F10.wireOp",EDGE,"E3620"),sQuery(id+"F10.wireOp",EDGE,"E3621"),sQuery(id+"F10.wireOp",EDGE,"E3622"),sQuery(id+"F10.wireOp",EDGE,"E3623"),sQuery(id+"F10.wireOp",EDGE,"E3624"),sQuery(id+"F10.wireOp",EDGE,"E3625"),sQuery(id+"F10.wireOp",EDGE,"E3626"),sQuery(id+"F10.wireOp",EDGE,"E3627"),sQuery(id+"F10.wireOp",EDGE,"E3628"),sQuery(id+"F10.wireOp",EDGE,"E3629"),sQuery(id+"F10.wireOp",EDGE,"E3630"),sQuery(id+"F10.wireOp",EDGE,"E3631"),sQuery(id+"F10.wireOp",EDGE,"E3632"),sQuery(id+"F10.wireOp",EDGE,"E3633"),sQuery(id+"F10.wireOp",EDGE,"E3634"),sQuery(id+"F10.wireOp",EDGE,"E3635"),sQuery(id+"F10.wireOp",EDGE,"E3636"),sQuery(id+"F10.wireOp",EDGE,"E3637"),sQuery(id+"F10.wireOp",EDGE,"E3638"),sQuery(id+"F10.wireOp",EDGE,"E3639"),sQuery(id+"F10.wireOp",EDGE,"E3640"),sQuery(id+"F10.wireOp",EDGE,"E3641"),sQuery(id+"F10.wireOp",EDGE,"E3642"),sQuery(id+"F10.wireOp",EDGE,"E3643"),sQuery(id+"F10.wireOp",EDGE,"E3644"),sQuery(id+"F10.wireOp",EDGE,"E3645"),sQuery(id+"F10.wireOp",EDGE,"E3646"),sQuery(id+"F10.wireOp",EDGE,"E3647"),sQuery(id+"F10.wireOp",EDGE,"E3648"),sQuery(id+"F10.wireOp",EDGE,"E3649"),sQuery(id+"F10.wireOp",EDGE,"E3650"),sQuery(id+"F10.wireOp",EDGE,"E3651"),sQuery(id+"F10.wireOp",EDGE,"E3652"),sQuery(id+"F10.wireOp",EDGE,"E3653"),sQuery(id+"F10.wireOp",EDGE,"E3654"),sQuery(id+"F10.wireOp",EDGE,"E3655"),sQuery(id+"F10.wireOp",EDGE,"E3656"),sQuery(id+"F10.wireOp",EDGE,"E3657"),sQuery(id+"F10.wireOp",EDGE,"E3658"),sQuery(id+"F10.wireOp",EDGE,"E3659"),sQuery(id+"F10.wireOp",EDGE,"E3660"),sQuery(id+"F10.wireOp",EDGE,"E3661"),sQuery(id+"F10.wireOp",EDGE,"E3662"),sQuery(id+"F10.wireOp",EDGE,"E3663"),sQuery(id+"F10.wireOp",EDGE,"E3664"),sQuery(id+"F10.wireOp",EDGE,"E3665"),sQuery(id+"F10.wireOp",EDGE,"E3666"),sQuery(id+"F10.wireOp",EDGE,"E3667"),sQuery(id+"F10.wireOp",EDGE,"E3668"),sQuery(id+"F10.wireOp",EDGE,"E3669"),sQuery(id+"F10.wireOp",EDGE,"E3670"),sQuery(id+"F10.wireOp",EDGE,"E3671"),sQuery(id+"F10.wireOp",EDGE,"E3672"),sQuery(id+"F10.wireOp",EDGE,"E3673"),sQuery(id+"F10.wireOp",EDGE,"E3674"),sQuery(id+"F10.wireOp",EDGE,"E3675"),sQuery(id+"F10.wireOp",EDGE,"E3676"),sQuery(id+"F10.wireOp",EDGE,"E3677"),sQuery(id+"F10.wireOp",EDGE,"E3678"),sQuery(id+"F10.wireOp",EDGE,"E3679"),sQuery(id+"F10.wireOp",EDGE,"E3680"),sQuery(id+"F10.wireOp",EDGE,"E3681"),sQuery(id+"F10.wireOp",EDGE,"E3682"),sQuery(id+"F10.wireOp",EDGE,"E3683"),sQuery(id+"F10.wireOp",EDGE,"E3684"),sQuery(id+"F10.wireOp",EDGE,"E3685"),sQuery(id+"F10.wireOp",EDGE,"E3686"),sQuery(id+"F10.wireOp",EDGE,"E3687"),sQuery(id+"F10.wireOp",EDGE,"E3688"),sQuery(id+"F10.wireOp",EDGE,"E3689"),sQuery(id+"F10.wireOp",EDGE,"E3690"),sQuery(id+"F10.wireOp",EDGE,"E3691"),sQuery(id+"F10.wireOp",EDGE,"E3692"),sQuery(id+"F10.wireOp",EDGE,"E3693"),sQuery(id+"F10.wireOp",EDGE,"E3694"),sQuery(id+"F10.wireOp",EDGE,"E3695"),sQuery(id+"F10.wireOp",EDGE,"E3696"),sQuery(id+"F10.wireOp",EDGE,"E3697"),sQuery(id+"F10.wireOp",EDGE,"E3698"),sQuery(id+"F10.wireOp",EDGE,"E3699"),sQuery(id+"F10.wireOp",EDGE,"E3700"),sQuery(id+"F10.wireOp",EDGE,"E3701"),sQuery(id+"F10.wireOp",EDGE,"E3702"),sQuery(id+"F10.wireOp",EDGE,"E3703"),sQuery(id+"F10.wireOp",EDGE,"E3704"),sQuery(id+"F10.wireOp",EDGE,"E3705"),sQuery(id+"F10.wireOp",EDGE,"E3706"),sQuery(id+"F10.wireOp",EDGE,"E3707"),sQuery(id+"F10.wireOp",EDGE,"E3708"),sQuery(id+"F10.wireOp",EDGE,"E3709"),sQuery(id+"F10.wireOp",EDGE,"E3710"),sQuery(id+"F10.wireOp",EDGE,"E3711"),sQuery(id+"F10.wireOp",EDGE,"E3712"),sQuery(id+"F10.wireOp",EDGE,"E3713"),sQuery(id+"F10.wireOp",EDGE,"E3714"),sQuery(id+"F10.wireOp",EDGE,"E3715"),sQuery(id+"F10.wireOp",EDGE,"E3716"),sQuery(id+"F10.wireOp",EDGE,"E3717"),sQuery(id+"F10.wireOp",EDGE,"E3718"),sQuery(id+"F10.wireOp",EDGE,"E3719"),sQuery(id+"F10.wireOp",EDGE,"E3720"),sQuery(id+"F10.wireOp",EDGE,"E3721"),sQuery(id+"F10.wireOp",EDGE,"E3722"),sQuery(id+"F10.wireOp",EDGE,"E3723"),sQuery(id+"F10.wireOp",EDGE,"E3724"),sQuery(id+"F10.wireOp",EDGE,"E3725"),sQuery(id+"F10.wireOp",EDGE,"E3726"),sQuery(id+"F10.wireOp",EDGE,"E3727"),sQuery(id+"F10.wireOp",EDGE,"E3728"),sQuery(id+"F10.wireOp",EDGE,"E3729"),sQuery(id+"F10.wireOp",EDGE,"E3730"),sQuery(id+"F10.wireOp",EDGE,"E3731"),sQuery(id+"F10.wireOp",EDGE,"E3732"),sQuery(id+"F10.wireOp",EDGE,"E3733"),sQuery(id+"F10.wireOp",EDGE,"E3734"),sQuery(id+"F10.wireOp",EDGE,"E3735"),sQuery(id+"F10.wireOp",EDGE,"E3736"),sQuery(id+"F10.wireOp",EDGE,"E3737"),sQuery(id+"F10.wireOp",EDGE,"E3738"),sQuery(id+"F10.wireOp",EDGE,"E3739"),sQuery(id+"F10.wireOp",EDGE,"E3740"),sQuery(id+"F10.wireOp",EDGE,"E3741"),sQuery(id+"F10.wireOp",EDGE,"E3742"),sQuery(id+"F10.wireOp",EDGE,"E3743"),sQuery(id+"F10.wireOp",EDGE,"E3744"),sQuery(id+"F10.wireOp",EDGE,"E3745"),sQuery(id+"F10.wireOp",EDGE,"E3746"),sQuery(id+"F10.wireOp",EDGE,"E3747")])]});
            var Q1;
            Q1=sQuery(id+"F0.wireOp",VERTEX,"E0.center");
            var Q2;
            Q2=sQuery(id+"F0.wireOp",VERTEX,"E2.start");
            transform(context, id + "F13", {"entities" : qUnion([Q0]), "transformType" : TransformType.TRANSLATION_ENTITY, "oppositeDirectionEntity" : false, "transformLine" : qUnion([Q1, Q2]), "makeCopy" : false});
        }
        {
            var Q0;
            Q0=qCreatedBy(makeId("Front.planeOp"),FACE);
            var sketch = newSketch(context, id + "F14", { "sketchPlane" : qUnion([Q0])});
            skLineSegment(sketch, "E3748", {"start": v(50.33, 0) * mm, "end": v(50.27, 2.52) * mm});
            skLineSegment(sketch, "E3749", {"start": v(50.27, 2.52) * mm, "end": v(50.08, 5.03) * mm});
            skLineSegment(sketch, "E3750", {"start": v(50.08, 5.03) * mm, "end": v(49.77, 7.53) * mm});
            skLineSegment(sketch, "E3751", {"start": v(49.77, 7.53) * mm, "end": v(49.33, 10) * mm});
            skLineSegment(sketch, "E3752", {"start": v(49.33, 10) * mm, "end": v(48.77, 12.46) * mm});
            skLineSegment(sketch, "E3753", {"start": v(48.77, 12.46) * mm, "end": v(48.09, 14.88) * mm});
            skLineSegment(sketch, "E3754", {"start": v(48.09, 14.88) * mm, "end": v(47.28, 17.26) * mm});
            skLineSegment(sketch, "E3755", {"start": v(47.28, 17.26) * mm, "end": v(46.36, 19.6) * mm});
            skLineSegment(sketch, "E3756", {"start": v(46.36, 19.6) * mm, "end": v(45.32, 21.9) * mm});
            skLineSegment(sketch, "E3757", {"start": v(45.32, 21.9) * mm, "end": v(44.17, 24.14) * mm});
            skLineSegment(sketch, "E3758", {"start": v(44.17, 24.14) * mm, "end": v(42.91, 26.31) * mm});
            skLineSegment(sketch, "E3759", {"start": v(42.91, 26.31) * mm, "end": v(41.54, 28.42) * mm});
            skLineSegment(sketch, "E3760", {"start": v(41.54, 28.42) * mm, "end": v(40.07, 30.47) * mm});
            skLineSegment(sketch, "E3761", {"start": v(40.07, 30.47) * mm, "end": v(38.5, 32.43) * mm});
            skLineSegment(sketch, "E3762", {"start": v(38.5, 32.43) * mm, "end": v(36.83, 34.31) * mm});
            skLineSegment(sketch, "E3763", {"start": v(36.83, 34.31) * mm, "end": v(35.07, 36.11) * mm});
            skLineSegment(sketch, "E3764", {"start": v(35.07, 36.11) * mm, "end": v(33.22, 37.82) * mm});
            skLineSegment(sketch, "E3765", {"start": v(33.22, 37.82) * mm, "end": v(31.29, 39.43) * mm});
            skLineSegment(sketch, "E3766", {"start": v(31.29, 39.43) * mm, "end": v(29.28, 40.95) * mm});
            skLineSegment(sketch, "E3767", {"start": v(29.28, 40.95) * mm, "end": v(27.2, 42.36) * mm});
            skLineSegment(sketch, "E3768", {"start": v(27.2, 42.36) * mm, "end": v(25.04, 43.66) * mm});
            skLineSegment(sketch, "E3769", {"start": v(25.04, 43.66) * mm, "end": v(22.83, 44.86) * mm});
            skLineSegment(sketch, "E3770", {"start": v(22.83, 44.86) * mm, "end": v(20.56, 45.95) * mm});
            skLineSegment(sketch, "E3771", {"start": v(20.56, 45.95) * mm, "end": v(18.24, 46.92) * mm});
            skLineSegment(sketch, "E3772", {"start": v(18.24, 46.92) * mm, "end": v(15.87, 47.77) * mm});
            skLineSegment(sketch, "E3773", {"start": v(15.87, 47.77) * mm, "end": v(13.46, 48.5) * mm});
            skLineSegment(sketch, "E3774", {"start": v(13.46, 48.5) * mm, "end": v(11.02, 49.12) * mm});
            skLineSegment(sketch, "E3775", {"start": v(11.02, 49.12) * mm, "end": v(8.55, 49.6) * mm});
            skLineSegment(sketch, "E3776", {"start": v(8.55, 49.6) * mm, "end": v(6.06, 49.97) * mm});
            skLineSegment(sketch, "E3777", {"start": v(6.06, 49.97) * mm, "end": v(3.56, 50.21) * mm});
            skLineSegment(sketch, "E3778", {"start": v(3.56, 50.21) * mm, "end": v(1.05, 50.33) * mm});
            skLineSegment(sketch, "E3779", {"start": v(1.05, 50.33) * mm, "end": v(-1.47, 50.32) * mm});
            skLineSegment(sketch, "E3780", {"start": v(-1.47, 50.32) * mm, "end": v(-3.98, 50.18) * mm});
            skLineSegment(sketch, "E3781", {"start": v(-3.98, 50.18) * mm, "end": v(-6.49, 49.92) * mm});
            skLineSegment(sketch, "E3782", {"start": v(-6.49, 49.92) * mm, "end": v(-8.97, 49.53) * mm});
            skLineSegment(sketch, "E3783", {"start": v(-8.97, 49.53) * mm, "end": v(-11.44, 49.02) * mm});
            skLineSegment(sketch, "E3784", {"start": v(-11.44, 49.02) * mm, "end": v(-13.87, 48.39) * mm});
            skLineSegment(sketch, "E3785", {"start": v(-13.87, 48.39) * mm, "end": v(-16.27, 47.63) * mm});
            skLineSegment(sketch, "E3786", {"start": v(-16.27, 47.63) * mm, "end": v(-18.63, 46.76) * mm});
            skLineSegment(sketch, "E3787", {"start": v(-18.63, 46.76) * mm, "end": v(-20.95, 45.77) * mm});
            skLineSegment(sketch, "E3788", {"start": v(-20.95, 45.77) * mm, "end": v(-23.2, 44.67) * mm});
            skLineSegment(sketch, "E3789", {"start": v(-23.2, 44.67) * mm, "end": v(-25.41, 43.45) * mm});
            skLineSegment(sketch, "E3790", {"start": v(-25.41, 43.45) * mm, "end": v(-27.55, 42.13) * mm});
            skLineSegment(sketch, "E3791", {"start": v(-27.55, 42.13) * mm, "end": v(-29.62, 40.7) * mm});
            skLineSegment(sketch, "E3792", {"start": v(-29.62, 40.7) * mm, "end": v(-31.62, 39.17) * mm});
            skLineSegment(sketch, "E3793", {"start": v(-31.62, 39.17) * mm, "end": v(-33.54, 37.54) * mm});
            skLineSegment(sketch, "E3794", {"start": v(-33.54, 37.54) * mm, "end": v(-35.37, 35.82) * mm});
            skLineSegment(sketch, "E3795", {"start": v(-35.37, 35.82) * mm, "end": v(-37.12, 34) * mm});
            skLineSegment(sketch, "E3796", {"start": v(-37.12, 34) * mm, "end": v(-38.77, 32.1) * mm});
            skLineSegment(sketch, "E3797", {"start": v(-38.77, 32.1) * mm, "end": v(-40.33, 30.13) * mm});
            skLineSegment(sketch, "E3798", {"start": v(-40.33, 30.13) * mm, "end": v(-41.78, 28.07) * mm});
            skLineSegment(sketch, "E3799", {"start": v(-41.78, 28.07) * mm, "end": v(-43.13, 25.95) * mm});
            skLineSegment(sketch, "E3800", {"start": v(-43.13, 25.95) * mm, "end": v(-44.37, 23.76) * mm});
            skLineSegment(sketch, "E3801", {"start": v(-44.37, 23.76) * mm, "end": v(-45.5, 21.52) * mm});
            skLineSegment(sketch, "E3802", {"start": v(-45.5, 21.52) * mm, "end": v(-46.53, 19.21) * mm});
            skLineSegment(sketch, "E3803", {"start": v(-46.53, 19.21) * mm, "end": v(-47.43, 16.86) * mm});
            skLineSegment(sketch, "E3804", {"start": v(-47.43, 16.86) * mm, "end": v(-48.21, 14.47) * mm});
            skLineSegment(sketch, "E3805", {"start": v(-48.21, 14.47) * mm, "end": v(-48.87, 12.05) * mm});
            skLineSegment(sketch, "E3806", {"start": v(-48.87, 12.05) * mm, "end": v(-49.41, 9.59) * mm});
            skLineSegment(sketch, "E3807", {"start": v(-49.41, 9.59) * mm, "end": v(-49.83, 7.1) * mm});
            skLineSegment(sketch, "E3808", {"start": v(-49.83, 7.1) * mm, "end": v(-50.12, 4.6) * mm});
            skLineSegment(sketch, "E3809", {"start": v(-50.12, 4.6) * mm, "end": v(-50.3, 2.1) * mm});
            skLineSegment(sketch, "E3810", {"start": v(-50.3, 2.1) * mm, "end": v(-50.33, -0.42) * mm});
            skLineSegment(sketch, "E3811", {"start": v(-50.33, -0.42) * mm, "end": v(-50.25, -2.93) * mm});
            skLineSegment(sketch, "E3812", {"start": v(-50.25, -2.93) * mm, "end": v(-50.04, -5.44) * mm});
            skLineSegment(sketch, "E3813", {"start": v(-50.04, -5.44) * mm, "end": v(-49.7, -7.94) * mm});
            skLineSegment(sketch, "E3814", {"start": v(-49.7, -7.94) * mm, "end": v(-49.25, -10.41) * mm});
            skLineSegment(sketch, "E3815", {"start": v(-49.25, -10.41) * mm, "end": v(-48.66, -12.86) * mm});
            skLineSegment(sketch, "E3816", {"start": v(-48.66, -12.86) * mm, "end": v(-47.96, -15.28) * mm});
            skLineSegment(sketch, "E3817", {"start": v(-47.96, -15.28) * mm, "end": v(-47.14, -17.65) * mm});
            skLineSegment(sketch, "E3818", {"start": v(-47.14, -17.65) * mm, "end": v(-46.2, -19.99) * mm});
            skLineSegment(sketch, "E3819", {"start": v(-46.2, -19.99) * mm, "end": v(-45.14, -22.27) * mm});
            skLineSegment(sketch, "E3820", {"start": v(-45.14, -22.27) * mm, "end": v(-43.97, -24.5) * mm});
            skLineSegment(sketch, "E3821", {"start": v(-43.97, -24.5) * mm, "end": v(-42.69, -26.67) * mm});
            skLineSegment(sketch, "E3822", {"start": v(-42.69, -26.67) * mm, "end": v(-41.3, -28.77) * mm});
            skLineSegment(sketch, "E3823", {"start": v(-41.3, -28.77) * mm, "end": v(-39.81, -30.8) * mm});
            skLineSegment(sketch, "E3824", {"start": v(-39.81, -30.8) * mm, "end": v(-38.22, -32.75) * mm});
            skLineSegment(sketch, "E3825", {"start": v(-38.22, -32.75) * mm, "end": v(-36.54, -34.61) * mm});
            skLineSegment(sketch, "E3826", {"start": v(-36.54, -34.61) * mm, "end": v(-34.76, -36.4) * mm});
            skLineSegment(sketch, "E3827", {"start": v(-34.76, -36.4) * mm, "end": v(-32.9, -38.09) * mm});
            skLineSegment(sketch, "E3828", {"start": v(-32.9, -38.09) * mm, "end": v(-30.96, -39.69) * mm});
            skLineSegment(sketch, "E3829", {"start": v(-30.96, -39.69) * mm, "end": v(-28.93, -41.18) * mm});
            skLineSegment(sketch, "E3830", {"start": v(-28.93, -41.18) * mm, "end": v(-26.84, -42.58) * mm});
            skLineSegment(sketch, "E3831", {"start": v(-26.84, -42.58) * mm, "end": v(-24.68, -43.87) * mm});
            skLineSegment(sketch, "E3832", {"start": v(-24.68, -43.87) * mm, "end": v(-22.45, -45.05) * mm});
            skLineSegment(sketch, "E3833", {"start": v(-22.45, -45.05) * mm, "end": v(-20.17, -46.11) * mm});
            skLineSegment(sketch, "E3834", {"start": v(-20.17, -46.11) * mm, "end": v(-17.84, -47.06) * mm});
            skLineSegment(sketch, "E3835", {"start": v(-17.84, -47.06) * mm, "end": v(-15.47, -47.9) * mm});
            skLineSegment(sketch, "E3836", {"start": v(-15.47, -47.9) * mm, "end": v(-13.06, -48.6) * mm});
            skLineSegment(sketch, "E3837", {"start": v(-13.06, -48.6) * mm, "end": v(-10.61, -49.2) * mm});
            skLineSegment(sketch, "E3838", {"start": v(-10.61, -49.2) * mm, "end": v(-8.14, -49.67) * mm});
            skLineSegment(sketch, "E3839", {"start": v(-8.14, -49.67) * mm, "end": v(-5.65, -50.01) * mm});
            skLineSegment(sketch, "E3840", {"start": v(-5.65, -50.01) * mm, "end": v(-3.14, -50.23) * mm});
            skLineSegment(sketch, "E3841", {"start": v(-3.14, -50.23) * mm, "end": v(-0.62, -50.33) * mm});
            skLineSegment(sketch, "E3842", {"start": v(-0.62, -50.33) * mm, "end": v(1.9, -50.3) * mm});
            skLineSegment(sketch, "E3843", {"start": v(1.9, -50.3) * mm, "end": v(4.4, -50.14) * mm});
            skLineSegment(sketch, "E3844", {"start": v(4.4, -50.14) * mm, "end": v(6.9, -49.85) * mm});
            skLineSegment(sketch, "E3845", {"start": v(6.9, -49.85) * mm, "end": v(9.39, -49.45) * mm});
            skLineSegment(sketch, "E3846", {"start": v(9.39, -49.45) * mm, "end": v(11.85, -48.92) * mm});
            skLineSegment(sketch, "E3847", {"start": v(11.85, -48.92) * mm, "end": v(14.28, -48.26) * mm});
            skLineSegment(sketch, "E3848", {"start": v(14.28, -48.26) * mm, "end": v(16.67, -47.49) * mm});
            skLineSegment(sketch, "E3849", {"start": v(16.67, -47.49) * mm, "end": v(19.02, -46.6) * mm});
            skLineSegment(sketch, "E3850", {"start": v(19.02, -46.6) * mm, "end": v(21.33, -45.59) * mm});
            skLineSegment(sketch, "E3851", {"start": v(21.33, -45.59) * mm, "end": v(23.58, -44.46) * mm});
            skLineSegment(sketch, "E3852", {"start": v(23.58, -44.46) * mm, "end": v(25.77, -43.23) * mm});
            skLineSegment(sketch, "E3853", {"start": v(25.77, -43.23) * mm, "end": v(27.9, -41.89) * mm});
            skLineSegment(sketch, "E3854", {"start": v(27.9, -41.89) * mm, "end": v(29.96, -40.44) * mm});
            skLineSegment(sketch, "E3855", {"start": v(29.96, -40.44) * mm, "end": v(31.95, -38.9) * mm});
            skLineSegment(sketch, "E3856", {"start": v(31.95, -38.9) * mm, "end": v(33.85, -37.25) * mm});
            skLineSegment(sketch, "E3857", {"start": v(33.85, -37.25) * mm, "end": v(35.67, -35.5) * mm});
            skLineSegment(sketch, "E3858", {"start": v(35.67, -35.5) * mm, "end": v(37.4, -33.68) * mm});
            skLineSegment(sketch, "E3859", {"start": v(37.4, -33.68) * mm, "end": v(39.04, -31.77) * mm});
            skLineSegment(sketch, "E3860", {"start": v(39.04, -31.77) * mm, "end": v(40.58, -29.78) * mm});
            skLineSegment(sketch, "E3861", {"start": v(40.58, -29.78) * mm, "end": v(42.01, -27.71) * mm});
            skLineSegment(sketch, "E3862", {"start": v(42.01, -27.71) * mm, "end": v(43.35, -25.58) * mm});
            skLineSegment(sketch, "E3863", {"start": v(43.35, -25.58) * mm, "end": v(44.57, -23.38) * mm});
            skLineSegment(sketch, "E3864", {"start": v(44.57, -23.38) * mm, "end": v(45.68, -21.13) * mm});
            skLineSegment(sketch, "E3865", {"start": v(45.68, -21.13) * mm, "end": v(46.68, -18.82) * mm});
            skLineSegment(sketch, "E3866", {"start": v(46.68, -18.82) * mm, "end": v(47.57, -16.46) * mm});
            skLineSegment(sketch, "E3867", {"start": v(47.57, -16.46) * mm, "end": v(48.33, -14.06) * mm});
            skLineSegment(sketch, "E3868", {"start": v(48.33, -14.06) * mm, "end": v(48.97, -11.63) * mm});
            skLineSegment(sketch, "E3869", {"start": v(48.97, -11.63) * mm, "end": v(49.5, -9.17) * mm});
            skLineSegment(sketch, "E3870", {"start": v(49.5, -9.17) * mm, "end": v(49.89, -6.68) * mm});
            skLineSegment(sketch, "E3871", {"start": v(49.89, -6.68) * mm, "end": v(50.16, -4.18) * mm});
            skLineSegment(sketch, "E3872", {"start": v(50.16, -4.18) * mm, "end": v(50.3, -1.67) * mm});
            skLineSegment(sketch, "E3873", {"start": v(50.3, -1.67) * mm, "end": v(50.33, 0) * mm});
            skLineSegment(sketch, "E3874", {"start": v(43.8, -1.04) * mm, "end": v(43.84, -1.03) * mm});
            skLineSegment(sketch, "E3875", {"start": v(43.84, -1.03) * mm, "end": v(43.95, -1) * mm});
            skLineSegment(sketch, "E3876", {"start": v(43.95, -1) * mm, "end": v(44.06, -0.97) * mm});
            skLineSegment(sketch, "E3877", {"start": v(44.06, -0.97) * mm, "end": v(44.17, -0.93) * mm});
            skLineSegment(sketch, "E3878", {"start": v(44.17, -0.93) * mm, "end": v(44.28, -0.9) * mm});
            skLineSegment(sketch, "E3879", {"start": v(44.28, -0.9) * mm, "end": v(44.4, -0.86) * mm});
            skLineSegment(sketch, "E3880", {"start": v(44.4, -0.86) * mm, "end": v(44.52, -0.82) * mm});
            skLineSegment(sketch, "E3881", {"start": v(44.52, -0.82) * mm, "end": v(44.64, -0.78) * mm});
            skLineSegment(sketch, "E3882", {"start": v(44.64, -0.78) * mm, "end": v(44.76, -0.74) * mm});
            skLineSegment(sketch, "E3883", {"start": v(44.76, -0.74) * mm, "end": v(44.87, -0.7) * mm});
            skLineSegment(sketch, "E3884", {"start": v(44.87, -0.7) * mm, "end": v(44.97, -0.67) * mm});
            skLineSegment(sketch, "E3885", {"start": v(44.97, -0.67) * mm, "end": v(45.08, -0.63) * mm});
            skLineSegment(sketch, "E3886", {"start": v(45.08, -0.63) * mm, "end": v(45.19, -0.59) * mm});
            skLineSegment(sketch, "E3887", {"start": v(45.19, -0.59) * mm, "end": v(45.3, -0.55) * mm});
            skLineSegment(sketch, "E3888", {"start": v(45.3, -0.55) * mm, "end": v(45.4, -0.5) * mm});
            skLineSegment(sketch, "E3889", {"start": v(45.4, -0.5) * mm, "end": v(45.52, -0.46) * mm});
            skLineSegment(sketch, "E3890", {"start": v(45.52, -0.46) * mm, "end": v(45.63, -0.41) * mm});
            skLineSegment(sketch, "E3891", {"start": v(45.63, -0.41) * mm, "end": v(45.75, -0.37) * mm});
            skLineSegment(sketch, "E3892", {"start": v(45.75, -0.37) * mm, "end": v(45.86, -0.32) * mm});
            skLineSegment(sketch, "E3893", {"start": v(45.86, -0.32) * mm, "end": v(45.95, -0.28) * mm});
            skLineSegment(sketch, "E3894", {"start": v(45.95, -0.28) * mm, "end": v(45.95, -0.16) * mm});
            skLineSegment(sketch, "E3895", {"start": v(45.95, -0.16) * mm, "end": v(45.95, -0.04) * mm});
            skLineSegment(sketch, "E3896", {"start": v(45.95, -0.04) * mm, "end": v(45.95, 0.07) * mm});
            skLineSegment(sketch, "E3897", {"start": v(45.95, 0.07) * mm, "end": v(45.95, 0.19) * mm});
            skLineSegment(sketch, "E3898", {"start": v(45.95, 0.19) * mm, "end": v(45.95, 0.29) * mm});
            skLineSegment(sketch, "E3899", {"start": v(45.95, 0.29) * mm, "end": v(45.84, 0.33) * mm});
            skLineSegment(sketch, "E3900", {"start": v(45.84, 0.33) * mm, "end": v(45.73, 0.38) * mm});
            skLineSegment(sketch, "E3901", {"start": v(45.73, 0.38) * mm, "end": v(45.62, 0.43) * mm});
            skLineSegment(sketch, "E3902", {"start": v(45.62, 0.43) * mm, "end": v(45.51, 0.47) * mm});
            skLineSegment(sketch, "E3903", {"start": v(45.51, 0.47) * mm, "end": v(45.4, 0.51) * mm});
            skLineSegment(sketch, "E3904", {"start": v(45.4, 0.51) * mm, "end": v(45.3, 0.56) * mm});
            skLineSegment(sketch, "E3905", {"start": v(45.3, 0.56) * mm, "end": v(45.18, 0.6) * mm});
            skLineSegment(sketch, "E3906", {"start": v(45.18, 0.6) * mm, "end": v(45.07, 0.64) * mm});
            skLineSegment(sketch, "E3907", {"start": v(45.07, 0.64) * mm, "end": v(44.95, 0.68) * mm});
            skLineSegment(sketch, "E3908", {"start": v(44.95, 0.68) * mm, "end": v(44.84, 0.72) * mm});
            skLineSegment(sketch, "E3909", {"start": v(44.84, 0.72) * mm, "end": v(44.72, 0.76) * mm});
            skLineSegment(sketch, "E3910", {"start": v(44.72, 0.76) * mm, "end": v(44.6, 0.8) * mm});
            skLineSegment(sketch, "E3911", {"start": v(44.6, 0.8) * mm, "end": v(44.5, 0.84) * mm});
            skLineSegment(sketch, "E3912", {"start": v(44.5, 0.84) * mm, "end": v(44.38, 0.87) * mm});
            skLineSegment(sketch, "E3913", {"start": v(44.38, 0.87) * mm, "end": v(44.27, 0.91) * mm});
            skLineSegment(sketch, "E3914", {"start": v(44.27, 0.91) * mm, "end": v(44.15, 0.94) * mm});
            skLineSegment(sketch, "E3915", {"start": v(44.15, 0.94) * mm, "end": v(44.04, 0.98) * mm});
            skLineSegment(sketch, "E3916", {"start": v(44.04, 0.98) * mm, "end": v(43.92, 1.01) * mm});
            skLineSegment(sketch, "E3917", {"start": v(43.92, 1.01) * mm, "end": v(43.8, 1.05) * mm});
            skLineSegment(sketch, "E3918", {"start": v(43.8, 1.05) * mm, "end": v(43.8, 1.16) * mm});
            skLineSegment(sketch, "E3919", {"start": v(43.8, 1.16) * mm, "end": v(43.8, 1.28) * mm});
            skLineSegment(sketch, "E3920", {"start": v(43.8, 1.28) * mm, "end": v(43.79, 1.4) * mm});
            skLineSegment(sketch, "E3921", {"start": v(43.79, 1.4) * mm, "end": v(43.78, 1.52) * mm});
            skLineSegment(sketch, "E3922", {"start": v(43.78, 1.52) * mm, "end": v(43.78, 1.64) * mm});
            skLineSegment(sketch, "E3923", {"start": v(43.78, 1.64) * mm, "end": v(43.77, 1.75) * mm});
            skLineSegment(sketch, "E3924", {"start": v(43.77, 1.75) * mm, "end": v(43.77, 1.87) * mm});
            skLineSegment(sketch, "E3925", {"start": v(43.77, 1.87) * mm, "end": v(43.77, 1.9) * mm});
            skLineSegment(sketch, "E3926", {"start": v(43.77, 1.9) * mm, "end": v(43.87, 1.93) * mm});
            skLineSegment(sketch, "E3927", {"start": v(43.87, 1.93) * mm, "end": v(43.98, 1.96) * mm});
            skLineSegment(sketch, "E3928", {"start": v(43.98, 1.96) * mm, "end": v(44.09, 2) * mm});
            skLineSegment(sketch, "E3929", {"start": v(44.09, 2) * mm, "end": v(44.2, 2.04) * mm});
            skLineSegment(sketch, "E3930", {"start": v(44.2, 2.04) * mm, "end": v(44.31, 2.09) * mm});
            skLineSegment(sketch, "E3931", {"start": v(44.31, 2.09) * mm, "end": v(44.43, 2.13) * mm});
            skLineSegment(sketch, "E3932", {"start": v(44.43, 2.13) * mm, "end": v(44.55, 2.18) * mm});
            skLineSegment(sketch, "E3933", {"start": v(44.55, 2.18) * mm, "end": v(44.67, 2.23) * mm});
            skLineSegment(sketch, "E3934", {"start": v(44.67, 2.23) * mm, "end": v(44.78, 2.28) * mm});
            skLineSegment(sketch, "E3935", {"start": v(44.78, 2.28) * mm, "end": v(44.9, 2.33) * mm});
            skLineSegment(sketch, "E3936", {"start": v(44.9, 2.33) * mm, "end": v(45, 2.37) * mm});
            skLineSegment(sketch, "E3937", {"start": v(45, 2.37) * mm, "end": v(45.1, 2.42) * mm});
            skLineSegment(sketch, "E3938", {"start": v(45.1, 2.42) * mm, "end": v(45.2, 2.47) * mm});
            skLineSegment(sketch, "E3939", {"start": v(45.2, 2.47) * mm, "end": v(45.31, 2.52) * mm});
            skLineSegment(sketch, "E3940", {"start": v(45.31, 2.52) * mm, "end": v(45.42, 2.57) * mm});
            skLineSegment(sketch, "E3941", {"start": v(45.42, 2.57) * mm, "end": v(45.53, 2.62) * mm});
            skLineSegment(sketch, "E3942", {"start": v(45.53, 2.62) * mm, "end": v(45.64, 2.68) * mm});
            skLineSegment(sketch, "E3943", {"start": v(45.64, 2.68) * mm, "end": v(45.75, 2.73) * mm});
            skLineSegment(sketch, "E3944", {"start": v(45.75, 2.73) * mm, "end": v(45.87, 2.8) * mm});
            skLineSegment(sketch, "E3945", {"start": v(45.87, 2.8) * mm, "end": v(45.87, 2.8) * mm});
            skLineSegment(sketch, "E3946", {"start": v(45.87, 2.8) * mm, "end": v(45.86, 2.91) * mm});
            skLineSegment(sketch, "E3947", {"start": v(45.86, 2.91) * mm, "end": v(45.85, 3.03) * mm});
            skLineSegment(sketch, "E3948", {"start": v(45.85, 3.03) * mm, "end": v(45.85, 3.14) * mm});
            skLineSegment(sketch, "E3949", {"start": v(45.85, 3.14) * mm, "end": v(45.84, 3.26) * mm});
            skLineSegment(sketch, "E3950", {"start": v(45.84, 3.26) * mm, "end": v(45.83, 3.35) * mm});
            skLineSegment(sketch, "E3951", {"start": v(45.83, 3.35) * mm, "end": v(45.72, 3.4) * mm});
            skLineSegment(sketch, "E3952", {"start": v(45.72, 3.4) * mm, "end": v(45.6, 3.43) * mm});
            skLineSegment(sketch, "E3953", {"start": v(45.6, 3.43) * mm, "end": v(45.49, 3.47) * mm});
            skLineSegment(sketch, "E3954", {"start": v(45.49, 3.47) * mm, "end": v(45.38, 3.5) * mm});
            skLineSegment(sketch, "E3955", {"start": v(45.38, 3.5) * mm, "end": v(45.27, 3.54) * mm});
            skLineSegment(sketch, "E3956", {"start": v(45.27, 3.54) * mm, "end": v(45.15, 3.58) * mm});
            skLineSegment(sketch, "E3957", {"start": v(45.15, 3.58) * mm, "end": v(45.04, 3.61) * mm});
            skLineSegment(sketch, "E3958", {"start": v(45.04, 3.61) * mm, "end": v(44.92, 3.65) * mm});
            skLineSegment(sketch, "E3959", {"start": v(44.92, 3.65) * mm, "end": v(44.8, 3.68) * mm});
            skLineSegment(sketch, "E3960", {"start": v(44.8, 3.68) * mm, "end": v(44.69, 3.72) * mm});
            skLineSegment(sketch, "E3961", {"start": v(44.69, 3.72) * mm, "end": v(44.57, 3.75) * mm});
            skLineSegment(sketch, "E3962", {"start": v(44.57, 3.75) * mm, "end": v(44.46, 3.78) * mm});
            skLineSegment(sketch, "E3963", {"start": v(44.46, 3.78) * mm, "end": v(44.34, 3.8) * mm});
            skLineSegment(sketch, "E3964", {"start": v(44.34, 3.8) * mm, "end": v(44.22, 3.84) * mm});
            skLineSegment(sketch, "E3965", {"start": v(44.22, 3.84) * mm, "end": v(44.1, 3.87) * mm});
            skLineSegment(sketch, "E3966", {"start": v(44.1, 3.87) * mm, "end": v(44, 3.9) * mm});
            skLineSegment(sketch, "E3967", {"start": v(44, 3.9) * mm, "end": v(43.87, 3.92) * mm});
            skLineSegment(sketch, "E3968", {"start": v(43.87, 3.92) * mm, "end": v(43.76, 3.94) * mm});
            skLineSegment(sketch, "E3969", {"start": v(43.76, 3.94) * mm, "end": v(43.63, 3.97) * mm});
            skLineSegment(sketch, "E3970", {"start": v(43.63, 3.97) * mm, "end": v(43.62, 4.09) * mm});
            skLineSegment(sketch, "E3971", {"start": v(43.62, 4.09) * mm, "end": v(43.6, 4.2) * mm});
            skLineSegment(sketch, "E3972", {"start": v(43.6, 4.2) * mm, "end": v(43.6, 4.32) * mm});
            skLineSegment(sketch, "E3973", {"start": v(43.6, 4.32) * mm, "end": v(43.58, 4.44) * mm});
            skLineSegment(sketch, "E3974", {"start": v(43.58, 4.44) * mm, "end": v(43.57, 4.56) * mm});
            skLineSegment(sketch, "E3975", {"start": v(43.57, 4.56) * mm, "end": v(43.56, 4.67) * mm});
            skLineSegment(sketch, "E3976", {"start": v(43.56, 4.67) * mm, "end": v(43.55, 4.8) * mm});
            skLineSegment(sketch, "E3977", {"start": v(43.55, 4.8) * mm, "end": v(43.55, 4.81) * mm});
            skLineSegment(sketch, "E3978", {"start": v(43.55, 4.81) * mm, "end": v(43.65, 4.85) * mm});
            skLineSegment(sketch, "E3979", {"start": v(43.65, 4.85) * mm, "end": v(43.75, 4.9) * mm});
            skLineSegment(sketch, "E3980", {"start": v(43.75, 4.9) * mm, "end": v(43.86, 4.94) * mm});
            skLineSegment(sketch, "E3981", {"start": v(43.86, 4.94) * mm, "end": v(43.96, 5) * mm});
            skLineSegment(sketch, "E3982", {"start": v(43.96, 5) * mm, "end": v(44.07, 5.04) * mm});
            skLineSegment(sketch, "E3983", {"start": v(44.07, 5.04) * mm, "end": v(44.19, 5.1) * mm});
            skLineSegment(sketch, "E3984", {"start": v(44.19, 5.1) * mm, "end": v(44.3, 5.15) * mm});
            skLineSegment(sketch, "E3985", {"start": v(44.3, 5.15) * mm, "end": v(44.42, 5.2) * mm});
            skLineSegment(sketch, "E3986", {"start": v(44.42, 5.2) * mm, "end": v(44.53, 5.26) * mm});
            skLineSegment(sketch, "E3987", {"start": v(44.53, 5.26) * mm, "end": v(44.64, 5.32) * mm});
            skLineSegment(sketch, "E3988", {"start": v(44.64, 5.32) * mm, "end": v(44.74, 5.37) * mm});
            skLineSegment(sketch, "E3989", {"start": v(44.74, 5.37) * mm, "end": v(44.84, 5.43) * mm});
            skLineSegment(sketch, "E3990", {"start": v(44.84, 5.43) * mm, "end": v(44.94, 5.48) * mm});
            skLineSegment(sketch, "E3991", {"start": v(44.94, 5.48) * mm, "end": v(45.04, 5.54) * mm});
            skLineSegment(sketch, "E3992", {"start": v(45.04, 5.54) * mm, "end": v(45.15, 5.6) * mm});
            skLineSegment(sketch, "E3993", {"start": v(45.15, 5.6) * mm, "end": v(45.25, 5.66) * mm});
            skLineSegment(sketch, "E3994", {"start": v(45.25, 5.66) * mm, "end": v(45.36, 5.72) * mm});
            skLineSegment(sketch, "E3995", {"start": v(45.36, 5.72) * mm, "end": v(45.47, 5.78) * mm});
            skLineSegment(sketch, "E3996", {"start": v(45.47, 5.78) * mm, "end": v(45.58, 5.85) * mm});
            skLineSegment(sketch, "E3997", {"start": v(45.58, 5.85) * mm, "end": v(45.58, 5.85) * mm});
            skLineSegment(sketch, "E3998", {"start": v(45.58, 5.85) * mm, "end": v(45.56, 5.97) * mm});
            skLineSegment(sketch, "E3999", {"start": v(45.56, 5.97) * mm, "end": v(45.55, 6.09) * mm});
            skLineSegment(sketch, "E4000", {"start": v(45.55, 6.09) * mm, "end": v(45.53, 6.2) * mm});
            skLineSegment(sketch, "E4001", {"start": v(45.53, 6.2) * mm, "end": v(45.52, 6.31) * mm});
            skLineSegment(sketch, "E4002", {"start": v(45.52, 6.31) * mm, "end": v(45.5, 6.4) * mm});
            skLineSegment(sketch, "E4003", {"start": v(45.5, 6.4) * mm, "end": v(45.39, 6.44) * mm});
            skLineSegment(sketch, "E4004", {"start": v(45.39, 6.44) * mm, "end": v(45.27, 6.47) * mm});
            skLineSegment(sketch, "E4005", {"start": v(45.27, 6.47) * mm, "end": v(45.16, 6.5) * mm});
            skLineSegment(sketch, "E4006", {"start": v(45.16, 6.5) * mm, "end": v(45.05, 6.53) * mm});
            skLineSegment(sketch, "E4007", {"start": v(45.05, 6.53) * mm, "end": v(44.93, 6.56) * mm});
            skLineSegment(sketch, "E4008", {"start": v(44.93, 6.56) * mm, "end": v(44.81, 6.59) * mm});
            skLineSegment(sketch, "E4009", {"start": v(44.81, 6.59) * mm, "end": v(44.7, 6.62) * mm});
            skLineSegment(sketch, "E4010", {"start": v(44.7, 6.62) * mm, "end": v(44.58, 6.64) * mm});
            skLineSegment(sketch, "E4011", {"start": v(44.58, 6.64) * mm, "end": v(44.46, 6.67) * mm});
            skLineSegment(sketch, "E4012", {"start": v(44.46, 6.67) * mm, "end": v(44.34, 6.7) * mm});
            skLineSegment(sketch, "E4013", {"start": v(44.34, 6.7) * mm, "end": v(44.22, 6.72) * mm});
            skLineSegment(sketch, "E4014", {"start": v(44.22, 6.72) * mm, "end": v(44.1, 6.74) * mm});
            skLineSegment(sketch, "E4015", {"start": v(44.1, 6.74) * mm, "end": v(43.99, 6.76) * mm});
            skLineSegment(sketch, "E4016", {"start": v(43.99, 6.76) * mm, "end": v(43.87, 6.78) * mm});
            skLineSegment(sketch, "E4017", {"start": v(43.87, 6.78) * mm, "end": v(43.75, 6.8) * mm});
            skLineSegment(sketch, "E4018", {"start": v(43.75, 6.8) * mm, "end": v(43.63, 6.82) * mm});
            skLineSegment(sketch, "E4019", {"start": v(43.63, 6.82) * mm, "end": v(43.52, 6.84) * mm});
            skLineSegment(sketch, "E4020", {"start": v(43.52, 6.84) * mm, "end": v(43.4, 6.86) * mm});
            skLineSegment(sketch, "E4021", {"start": v(43.4, 6.86) * mm, "end": v(43.27, 6.87) * mm});
            skLineSegment(sketch, "E4022", {"start": v(43.27, 6.87) * mm, "end": v(43.25, 7) * mm});
            skLineSegment(sketch, "E4023", {"start": v(43.25, 7) * mm, "end": v(43.23, 7.1) * mm});
            skLineSegment(sketch, "E4024", {"start": v(43.23, 7.1) * mm, "end": v(43.21, 7.23) * mm});
            skLineSegment(sketch, "E4025", {"start": v(43.21, 7.23) * mm, "end": v(43.2, 7.34) * mm});
            skLineSegment(sketch, "E4026", {"start": v(43.2, 7.34) * mm, "end": v(43.17, 7.46) * mm});
            skLineSegment(sketch, "E4027", {"start": v(43.17, 7.46) * mm, "end": v(43.15, 7.57) * mm});
            skLineSegment(sketch, "E4028", {"start": v(43.15, 7.57) * mm, "end": v(43.13, 7.7) * mm});
            skLineSegment(sketch, "E4029", {"start": v(43.13, 7.7) * mm, "end": v(43.13, 7.7) * mm});
            skLineSegment(sketch, "E4030", {"start": v(43.13, 7.7) * mm, "end": v(43.23, 7.76) * mm});
            skLineSegment(sketch, "E4031", {"start": v(43.23, 7.76) * mm, "end": v(43.33, 7.8) * mm});
            skLineSegment(sketch, "E4032", {"start": v(43.33, 7.8) * mm, "end": v(43.43, 7.86) * mm});
            skLineSegment(sketch, "E4033", {"start": v(43.43, 7.86) * mm, "end": v(43.53, 7.92) * mm});
            skLineSegment(sketch, "E4034", {"start": v(43.53, 7.92) * mm, "end": v(43.64, 7.98) * mm});
            skLineSegment(sketch, "E4035", {"start": v(43.64, 7.98) * mm, "end": v(43.75, 8.04) * mm});
            skLineSegment(sketch, "E4036", {"start": v(43.75, 8.04) * mm, "end": v(43.86, 8.1) * mm});
            skLineSegment(sketch, "E4037", {"start": v(43.86, 8.1) * mm, "end": v(43.97, 8.16) * mm});
            skLineSegment(sketch, "E4038", {"start": v(43.97, 8.16) * mm, "end": v(44.08, 8.23) * mm});
            skLineSegment(sketch, "E4039", {"start": v(44.08, 8.23) * mm, "end": v(44.18, 8.29) * mm});
            skLineSegment(sketch, "E4040", {"start": v(44.18, 8.29) * mm, "end": v(44.28, 8.35) * mm});
            skLineSegment(sketch, "E4041", {"start": v(44.28, 8.35) * mm, "end": v(44.37, 8.4) * mm});
            skLineSegment(sketch, "E4042", {"start": v(44.37, 8.4) * mm, "end": v(44.47, 8.47) * mm});
            skLineSegment(sketch, "E4043", {"start": v(44.47, 8.47) * mm, "end": v(44.57, 8.53) * mm});
            skLineSegment(sketch, "E4044", {"start": v(44.57, 8.53) * mm, "end": v(44.67, 8.6) * mm});
            skLineSegment(sketch, "E4045", {"start": v(44.67, 8.6) * mm, "end": v(44.77, 8.67) * mm});
            skLineSegment(sketch, "E4046", {"start": v(44.77, 8.67) * mm, "end": v(44.88, 8.74) * mm});
            skLineSegment(sketch, "E4047", {"start": v(44.88, 8.74) * mm, "end": v(44.98, 8.8) * mm});
            skLineSegment(sketch, "E4048", {"start": v(44.98, 8.8) * mm, "end": v(45.09, 8.88) * mm});
            skLineSegment(sketch, "E4049", {"start": v(45.09, 8.88) * mm, "end": v(45.09, 8.88) * mm});
            skLineSegment(sketch, "E4050", {"start": v(45.09, 8.88) * mm, "end": v(45.06, 9) * mm});
            skLineSegment(sketch, "E4051", {"start": v(45.06, 9) * mm, "end": v(45.04, 9.11) * mm});
            skLineSegment(sketch, "E4052", {"start": v(45.04, 9.11) * mm, "end": v(45.02, 9.22) * mm});
            skLineSegment(sketch, "E4053", {"start": v(45.02, 9.22) * mm, "end": v(45, 9.34) * mm});
            skLineSegment(sketch, "E4054", {"start": v(45, 9.34) * mm, "end": v(44.97, 9.43) * mm});
            skLineSegment(sketch, "E4055", {"start": v(44.97, 9.43) * mm, "end": v(44.86, 9.46) * mm});
            skLineSegment(sketch, "E4056", {"start": v(44.86, 9.46) * mm, "end": v(44.74, 9.48) * mm});
            skLineSegment(sketch, "E4057", {"start": v(44.74, 9.48) * mm, "end": v(44.62, 9.5) * mm});
            skLineSegment(sketch, "E4058", {"start": v(44.62, 9.5) * mm, "end": v(44.5, 9.52) * mm});
            skLineSegment(sketch, "E4059", {"start": v(44.5, 9.52) * mm, "end": v(44.4, 9.55) * mm});
            skLineSegment(sketch, "E4060", {"start": v(44.4, 9.55) * mm, "end": v(44.27, 9.57) * mm});
            skLineSegment(sketch, "E4061", {"start": v(44.27, 9.57) * mm, "end": v(44.15, 9.59) * mm});
            skLineSegment(sketch, "E4062", {"start": v(44.15, 9.59) * mm, "end": v(44.04, 9.6) * mm});
            skLineSegment(sketch, "E4063", {"start": v(44.04, 9.6) * mm, "end": v(43.92, 9.62) * mm});
            skLineSegment(sketch, "E4064", {"start": v(43.92, 9.62) * mm, "end": v(43.8, 9.64) * mm});
            skLineSegment(sketch, "E4065", {"start": v(43.8, 9.64) * mm, "end": v(43.68, 9.66) * mm});
            skLineSegment(sketch, "E4066", {"start": v(43.68, 9.66) * mm, "end": v(43.56, 9.67) * mm});
            skLineSegment(sketch, "E4067", {"start": v(43.56, 9.67) * mm, "end": v(43.44, 9.68) * mm});
            skLineSegment(sketch, "E4068", {"start": v(43.44, 9.68) * mm, "end": v(43.32, 9.7) * mm});
            skLineSegment(sketch, "E4069", {"start": v(43.32, 9.7) * mm, "end": v(43.2, 9.7) * mm});
            skLineSegment(sketch, "E4070", {"start": v(43.2, 9.7) * mm, "end": v(43.08, 9.72) * mm});
            skLineSegment(sketch, "E4071", {"start": v(43.08, 9.72) * mm, "end": v(42.96, 9.73) * mm});
            skLineSegment(sketch, "E4072", {"start": v(42.96, 9.73) * mm, "end": v(42.84, 9.74) * mm});
            skLineSegment(sketch, "E4073", {"start": v(42.84, 9.74) * mm, "end": v(42.71, 9.75) * mm});
            skLineSegment(sketch, "E4074", {"start": v(42.71, 9.75) * mm, "end": v(42.69, 9.86) * mm});
            skLineSegment(sketch, "E4075", {"start": v(42.69, 9.86) * mm, "end": v(42.66, 9.98) * mm});
            skLineSegment(sketch, "E4076", {"start": v(42.66, 9.98) * mm, "end": v(42.63, 10.1) * mm});
            skLineSegment(sketch, "E4077", {"start": v(42.63, 10.1) * mm, "end": v(42.6, 10.2) * mm});
            skLineSegment(sketch, "E4078", {"start": v(42.6, 10.2) * mm, "end": v(42.58, 10.33) * mm});
            skLineSegment(sketch, "E4079", {"start": v(42.58, 10.33) * mm, "end": v(42.55, 10.44) * mm});
            skLineSegment(sketch, "E4080", {"start": v(42.55, 10.44) * mm, "end": v(42.52, 10.56) * mm});
            skLineSegment(sketch, "E4081", {"start": v(42.52, 10.56) * mm, "end": v(42.52, 10.57) * mm});
            skLineSegment(sketch, "E4082", {"start": v(42.52, 10.57) * mm, "end": v(42.61, 10.63) * mm});
            skLineSegment(sketch, "E4083", {"start": v(42.61, 10.63) * mm, "end": v(42.7, 10.68) * mm});
            skLineSegment(sketch, "E4084", {"start": v(42.7, 10.68) * mm, "end": v(42.8, 10.74) * mm});
            skLineSegment(sketch, "E4085", {"start": v(42.8, 10.74) * mm, "end": v(42.9, 10.8) * mm});
            skLineSegment(sketch, "E4086", {"start": v(42.9, 10.8) * mm, "end": v(43, 10.87) * mm});
            skLineSegment(sketch, "E4087", {"start": v(43, 10.87) * mm, "end": v(43.11, 10.94) * mm});
            skLineSegment(sketch, "E4088", {"start": v(43.11, 10.94) * mm, "end": v(43.22, 11.01) * mm});
            skLineSegment(sketch, "E4089", {"start": v(43.22, 11.01) * mm, "end": v(43.33, 11.08) * mm});
            skLineSegment(sketch, "E4090", {"start": v(43.33, 11.08) * mm, "end": v(43.43, 11.15) * mm});
            skLineSegment(sketch, "E4091", {"start": v(43.43, 11.15) * mm, "end": v(43.53, 11.22) * mm});
            skLineSegment(sketch, "E4092", {"start": v(43.53, 11.22) * mm, "end": v(43.62, 11.29) * mm});
            skLineSegment(sketch, "E4093", {"start": v(43.62, 11.29) * mm, "end": v(43.71, 11.35) * mm});
            skLineSegment(sketch, "E4094", {"start": v(43.71, 11.35) * mm, "end": v(43.8, 11.42) * mm});
            skLineSegment(sketch, "E4095", {"start": v(43.8, 11.42) * mm, "end": v(43.9, 11.5) * mm});
            skLineSegment(sketch, "E4096", {"start": v(43.9, 11.5) * mm, "end": v(44, 11.56) * mm});
            skLineSegment(sketch, "E4097", {"start": v(44, 11.56) * mm, "end": v(44.1, 11.64) * mm});
            skLineSegment(sketch, "E4098", {"start": v(44.1, 11.64) * mm, "end": v(44.2, 11.71) * mm});
            skLineSegment(sketch, "E4099", {"start": v(44.2, 11.71) * mm, "end": v(44.3, 11.8) * mm});
            skLineSegment(sketch, "E4100", {"start": v(44.3, 11.8) * mm, "end": v(44.4, 11.87) * mm});
            skLineSegment(sketch, "E4101", {"start": v(44.4, 11.87) * mm, "end": v(44.4, 11.87) * mm});
            skLineSegment(sketch, "E4102", {"start": v(44.4, 11.87) * mm, "end": v(44.36, 11.99) * mm});
            skLineSegment(sketch, "E4103", {"start": v(44.36, 11.99) * mm, "end": v(44.33, 12.1) * mm});
            skLineSegment(sketch, "E4104", {"start": v(44.33, 12.1) * mm, "end": v(44.3, 12.2) * mm});
            skLineSegment(sketch, "E4105", {"start": v(44.3, 12.2) * mm, "end": v(44.27, 12.32) * mm});
            skLineSegment(sketch, "E4106", {"start": v(44.27, 12.32) * mm, "end": v(44.24, 12.42) * mm});
            skLineSegment(sketch, "E4107", {"start": v(44.24, 12.42) * mm, "end": v(44.13, 12.43) * mm});
            skLineSegment(sketch, "E4108", {"start": v(44.13, 12.43) * mm, "end": v(44, 12.45) * mm});
            skLineSegment(sketch, "E4109", {"start": v(44, 12.45) * mm, "end": v(43.89, 12.46) * mm});
            skLineSegment(sketch, "E4110", {"start": v(43.89, 12.46) * mm, "end": v(43.77, 12.48) * mm});
            skLineSegment(sketch, "E4111", {"start": v(43.77, 12.48) * mm, "end": v(43.65, 12.49) * mm});
            skLineSegment(sketch, "E4112", {"start": v(43.65, 12.49) * mm, "end": v(43.54, 12.5) * mm});
            skLineSegment(sketch, "E4113", {"start": v(43.54, 12.5) * mm, "end": v(43.42, 12.51) * mm});
            skLineSegment(sketch, "E4114", {"start": v(43.42, 12.51) * mm, "end": v(43.3, 12.52) * mm});
            skLineSegment(sketch, "E4115", {"start": v(43.3, 12.52) * mm, "end": v(43.18, 12.53) * mm});
            skLineSegment(sketch, "E4116", {"start": v(43.18, 12.53) * mm, "end": v(43.05, 12.54) * mm});
            skLineSegment(sketch, "E4117", {"start": v(43.05, 12.54) * mm, "end": v(42.93, 12.55) * mm});
            skLineSegment(sketch, "E4118", {"start": v(42.93, 12.55) * mm, "end": v(42.81, 12.56) * mm});
            skLineSegment(sketch, "E4119", {"start": v(42.81, 12.56) * mm, "end": v(42.7, 12.56) * mm});
            skLineSegment(sketch, "E4120", {"start": v(42.7, 12.56) * mm, "end": v(42.57, 12.57) * mm});
            skLineSegment(sketch, "E4121", {"start": v(42.57, 12.57) * mm, "end": v(42.45, 12.57) * mm});
            skLineSegment(sketch, "E4122", {"start": v(42.45, 12.57) * mm, "end": v(42.34, 12.58) * mm});
            skLineSegment(sketch, "E4123", {"start": v(42.34, 12.58) * mm, "end": v(42.22, 12.58) * mm});
            skLineSegment(sketch, "E4124", {"start": v(42.22, 12.58) * mm, "end": v(42.1, 12.58) * mm});
            skLineSegment(sketch, "E4125", {"start": v(42.1, 12.58) * mm, "end": v(42.06, 12.58) * mm});
            skLineSegment(sketch, "E4126", {"start": v(42.06, 12.58) * mm, "end": v(41.97, 12.58) * mm});
            skLineSegment(sketch, "E4127", {"start": v(41.97, 12.58) * mm, "end": v(41.93, 12.7) * mm});
            skLineSegment(sketch, "E4128", {"start": v(41.93, 12.7) * mm, "end": v(41.9, 12.8) * mm});
            skLineSegment(sketch, "E4129", {"start": v(41.9, 12.8) * mm, "end": v(41.86, 12.92) * mm});
            skLineSegment(sketch, "E4130", {"start": v(41.86, 12.92) * mm, "end": v(41.83, 13.03) * mm});
            skLineSegment(sketch, "E4131", {"start": v(41.83, 13.03) * mm, "end": v(41.8, 13.15) * mm});
            skLineSegment(sketch, "E4132", {"start": v(41.8, 13.15) * mm, "end": v(41.76, 13.26) * mm});
            skLineSegment(sketch, "E4133", {"start": v(41.76, 13.26) * mm, "end": v(41.72, 13.37) * mm});
            skLineSegment(sketch, "E4134", {"start": v(41.72, 13.37) * mm, "end": v(41.72, 13.39) * mm});
            skLineSegment(sketch, "E4135", {"start": v(41.72, 13.39) * mm, "end": v(41.8, 13.45) * mm});
            skLineSegment(sketch, "E4136", {"start": v(41.8, 13.45) * mm, "end": v(41.9, 13.51) * mm});
            skLineSegment(sketch, "E4137", {"start": v(41.9, 13.51) * mm, "end": v(42, 13.58) * mm});
            skLineSegment(sketch, "E4138", {"start": v(42, 13.58) * mm, "end": v(42.09, 13.65) * mm});
            skLineSegment(sketch, "E4139", {"start": v(42.09, 13.65) * mm, "end": v(42.19, 13.72) * mm});
            skLineSegment(sketch, "E4140", {"start": v(42.19, 13.72) * mm, "end": v(42.29, 13.8) * mm});
            skLineSegment(sketch, "E4141", {"start": v(42.29, 13.8) * mm, "end": v(42.39, 13.87) * mm});
            skLineSegment(sketch, "E4142", {"start": v(42.39, 13.87) * mm, "end": v(42.5, 13.95) * mm});
            skLineSegment(sketch, "E4143", {"start": v(42.5, 13.95) * mm, "end": v(42.59, 14.03) * mm});
            skLineSegment(sketch, "E4144", {"start": v(42.59, 14.03) * mm, "end": v(42.68, 14.1) * mm});
            skLineSegment(sketch, "E4145", {"start": v(42.68, 14.1) * mm, "end": v(42.77, 14.18) * mm});
            skLineSegment(sketch, "E4146", {"start": v(42.77, 14.18) * mm, "end": v(42.86, 14.25) * mm});
            skLineSegment(sketch, "E4147", {"start": v(42.86, 14.25) * mm, "end": v(42.95, 14.32) * mm});
            skLineSegment(sketch, "E4148", {"start": v(42.95, 14.32) * mm, "end": v(43.04, 14.4) * mm});
            skLineSegment(sketch, "E4149", {"start": v(43.04, 14.4) * mm, "end": v(43.13, 14.48) * mm});
            skLineSegment(sketch, "E4150", {"start": v(43.13, 14.48) * mm, "end": v(43.22, 14.56) * mm});
            skLineSegment(sketch, "E4151", {"start": v(43.22, 14.56) * mm, "end": v(43.31, 14.64) * mm});
            skLineSegment(sketch, "E4152", {"start": v(43.31, 14.64) * mm, "end": v(43.4, 14.72) * mm});
            skLineSegment(sketch, "E4153", {"start": v(43.4, 14.72) * mm, "end": v(43.5, 14.8) * mm});
            skLineSegment(sketch, "E4154", {"start": v(43.5, 14.8) * mm, "end": v(43.5, 14.81) * mm});
            skLineSegment(sketch, "E4155", {"start": v(43.5, 14.81) * mm, "end": v(43.46, 14.92) * mm});
            skLineSegment(sketch, "E4156", {"start": v(43.46, 14.92) * mm, "end": v(43.42, 15.04) * mm});
            skLineSegment(sketch, "E4157", {"start": v(43.42, 15.04) * mm, "end": v(43.39, 15.14) * mm});
            skLineSegment(sketch, "E4158", {"start": v(43.39, 15.14) * mm, "end": v(43.35, 15.25) * mm});
            skLineSegment(sketch, "E4159", {"start": v(43.35, 15.25) * mm, "end": v(43.32, 15.34) * mm});
            skLineSegment(sketch, "E4160", {"start": v(43.32, 15.34) * mm, "end": v(43.2, 15.35) * mm});
            skLineSegment(sketch, "E4161", {"start": v(43.2, 15.35) * mm, "end": v(43.08, 15.36) * mm});
            skLineSegment(sketch, "E4162", {"start": v(43.08, 15.36) * mm, "end": v(42.96, 15.37) * mm});
            skLineSegment(sketch, "E4163", {"start": v(42.96, 15.37) * mm, "end": v(42.84, 15.37) * mm});
            skLineSegment(sketch, "E4164", {"start": v(42.84, 15.37) * mm, "end": v(42.72, 15.38) * mm});
            skLineSegment(sketch, "E4165", {"start": v(42.72, 15.38) * mm, "end": v(42.6, 15.38) * mm});
            skLineSegment(sketch, "E4166", {"start": v(42.6, 15.38) * mm, "end": v(42.48, 15.39) * mm});
            skLineSegment(sketch, "E4167", {"start": v(42.48, 15.39) * mm, "end": v(42.36, 15.39) * mm});
            skLineSegment(sketch, "E4168", {"start": v(42.36, 15.39) * mm, "end": v(42.24, 15.4) * mm});
            skLineSegment(sketch, "E4169", {"start": v(42.24, 15.4) * mm, "end": v(42.12, 15.4) * mm});
            skLineSegment(sketch, "E4170", {"start": v(42.12, 15.4) * mm, "end": v(42.05, 15.4) * mm});
            skLineSegment(sketch, "E4171", {"start": v(42.05, 15.4) * mm, "end": v(41.93, 15.4) * mm});
            skLineSegment(sketch, "E4172", {"start": v(41.93, 15.4) * mm, "end": v(41.81, 15.39) * mm});
            skLineSegment(sketch, "E4173", {"start": v(41.81, 15.39) * mm, "end": v(41.7, 15.39) * mm});
            skLineSegment(sketch, "E4174", {"start": v(41.7, 15.39) * mm, "end": v(41.57, 15.38) * mm});
            skLineSegment(sketch, "E4175", {"start": v(41.57, 15.38) * mm, "end": v(41.45, 15.38) * mm});
            skLineSegment(sketch, "E4176", {"start": v(41.45, 15.38) * mm, "end": v(41.33, 15.37) * mm});
            skLineSegment(sketch, "E4177", {"start": v(41.33, 15.37) * mm, "end": v(41.21, 15.37) * mm});
            skLineSegment(sketch, "E4178", {"start": v(41.21, 15.37) * mm, "end": v(41.1, 15.36) * mm});
            skLineSegment(sketch, "E4179", {"start": v(41.1, 15.36) * mm, "end": v(41.03, 15.35) * mm});
            skLineSegment(sketch, "E4180", {"start": v(41.03, 15.35) * mm, "end": v(40.99, 15.47) * mm});
            skLineSegment(sketch, "E4181", {"start": v(40.99, 15.47) * mm, "end": v(40.95, 15.58) * mm});
            skLineSegment(sketch, "E4182", {"start": v(40.95, 15.58) * mm, "end": v(40.9, 15.69) * mm});
            skLineSegment(sketch, "E4183", {"start": v(40.9, 15.69) * mm, "end": v(40.86, 15.8) * mm});
            skLineSegment(sketch, "E4184", {"start": v(40.86, 15.8) * mm, "end": v(40.82, 15.9) * mm});
            skLineSegment(sketch, "E4185", {"start": v(40.82, 15.9) * mm, "end": v(40.78, 16.02) * mm});
            skLineSegment(sketch, "E4186", {"start": v(40.78, 16.02) * mm, "end": v(40.74, 16.13) * mm});
            skLineSegment(sketch, "E4187", {"start": v(40.74, 16.13) * mm, "end": v(40.73, 16.14) * mm});
            skLineSegment(sketch, "E4188", {"start": v(40.73, 16.14) * mm, "end": v(40.82, 16.21) * mm});
            skLineSegment(sketch, "E4189", {"start": v(40.82, 16.21) * mm, "end": v(40.9, 16.28) * mm});
            skLineSegment(sketch, "E4190", {"start": v(40.9, 16.28) * mm, "end": v(41, 16.35) * mm});
            skLineSegment(sketch, "E4191", {"start": v(41, 16.35) * mm, "end": v(41.08, 16.43) * mm});
            skLineSegment(sketch, "E4192", {"start": v(41.08, 16.43) * mm, "end": v(41.18, 16.5) * mm});
            skLineSegment(sketch, "E4193", {"start": v(41.18, 16.5) * mm, "end": v(41.27, 16.59) * mm});
            skLineSegment(sketch, "E4194", {"start": v(41.27, 16.59) * mm, "end": v(41.37, 16.67) * mm});
            skLineSegment(sketch, "E4195", {"start": v(41.37, 16.67) * mm, "end": v(41.47, 16.76) * mm});
            skLineSegment(sketch, "E4196", {"start": v(41.47, 16.76) * mm, "end": v(41.55, 16.84) * mm});
            skLineSegment(sketch, "E4197", {"start": v(41.55, 16.84) * mm, "end": v(41.65, 16.92) * mm});
            skLineSegment(sketch, "E4198", {"start": v(41.65, 16.92) * mm, "end": v(41.73, 17) * mm});
            skLineSegment(sketch, "E4199", {"start": v(41.73, 17) * mm, "end": v(41.81, 17.08) * mm});
            skLineSegment(sketch, "E4200", {"start": v(41.81, 17.08) * mm, "end": v(41.9, 17.16) * mm});
            skLineSegment(sketch, "E4201", {"start": v(41.9, 17.16) * mm, "end": v(41.98, 17.24) * mm});
            skLineSegment(sketch, "E4202", {"start": v(41.98, 17.24) * mm, "end": v(42.06, 17.32) * mm});
            skLineSegment(sketch, "E4203", {"start": v(42.06, 17.32) * mm, "end": v(42.15, 17.41) * mm});
            skLineSegment(sketch, "E4204", {"start": v(42.15, 17.41) * mm, "end": v(42.24, 17.5) * mm});
            skLineSegment(sketch, "E4205", {"start": v(42.24, 17.5) * mm, "end": v(42.33, 17.59) * mm});
            skLineSegment(sketch, "E4206", {"start": v(42.33, 17.59) * mm, "end": v(42.41, 17.68) * mm});
            skLineSegment(sketch, "E4207", {"start": v(42.41, 17.68) * mm, "end": v(42.42, 17.68) * mm});
            skLineSegment(sketch, "E4208", {"start": v(42.42, 17.68) * mm, "end": v(42.37, 17.8) * mm});
            skLineSegment(sketch, "E4209", {"start": v(42.37, 17.8) * mm, "end": v(42.32, 17.9) * mm});
            skLineSegment(sketch, "E4210", {"start": v(42.32, 17.9) * mm, "end": v(42.28, 18) * mm});
            skLineSegment(sketch, "E4211", {"start": v(42.28, 18) * mm, "end": v(42.23, 18.11) * mm});
            skLineSegment(sketch, "E4212", {"start": v(42.23, 18.11) * mm, "end": v(42.2, 18.2) * mm});
            skLineSegment(sketch, "E4213", {"start": v(42.2, 18.2) * mm, "end": v(42.08, 18.2) * mm});
            skLineSegment(sketch, "E4214", {"start": v(42.08, 18.2) * mm, "end": v(42.03, 18.2) * mm});
            skLineSegment(sketch, "E4215", {"start": v(42.03, 18.2) * mm, "end": v(41.91, 18.2) * mm});
            skLineSegment(sketch, "E4216", {"start": v(41.91, 18.2) * mm, "end": v(41.8, 18.2) * mm});
            skLineSegment(sketch, "E4217", {"start": v(41.8, 18.2) * mm, "end": v(41.68, 18.2) * mm});
            skLineSegment(sketch, "E4218", {"start": v(41.68, 18.2) * mm, "end": v(41.57, 18.2) * mm});
            skLineSegment(sketch, "E4219", {"start": v(41.57, 18.2) * mm, "end": v(41.45, 18.2) * mm});
            skLineSegment(sketch, "E4220", {"start": v(41.45, 18.2) * mm, "end": v(41.33, 18.19) * mm});
            skLineSegment(sketch, "E4221", {"start": v(41.33, 18.19) * mm, "end": v(41.2, 18.18) * mm});
            skLineSegment(sketch, "E4222", {"start": v(41.2, 18.18) * mm, "end": v(41.09, 18.18) * mm});
            skLineSegment(sketch, "E4223", {"start": v(41.09, 18.18) * mm, "end": v(40.97, 18.17) * mm});
            skLineSegment(sketch, "E4224", {"start": v(40.97, 18.17) * mm, "end": v(40.85, 18.16) * mm});
            skLineSegment(sketch, "E4225", {"start": v(40.85, 18.16) * mm, "end": v(40.73, 18.15) * mm});
            skLineSegment(sketch, "E4226", {"start": v(40.73, 18.15) * mm, "end": v(40.6, 18.14) * mm});
            skLineSegment(sketch, "E4227", {"start": v(40.6, 18.14) * mm, "end": v(40.48, 18.13) * mm});
            skLineSegment(sketch, "E4228", {"start": v(40.48, 18.13) * mm, "end": v(40.36, 18.12) * mm});
            skLineSegment(sketch, "E4229", {"start": v(40.36, 18.12) * mm, "end": v(40.24, 18.1) * mm});
            skLineSegment(sketch, "E4230", {"start": v(40.24, 18.1) * mm, "end": v(40.12, 18.09) * mm});
            skLineSegment(sketch, "E4231", {"start": v(40.12, 18.09) * mm, "end": v(40.01, 18.07) * mm});
            skLineSegment(sketch, "E4232", {"start": v(40.01, 18.07) * mm, "end": v(39.92, 18.06) * mm});
            skLineSegment(sketch, "E4233", {"start": v(39.92, 18.06) * mm, "end": v(39.87, 18.17) * mm});
            skLineSegment(sketch, "E4234", {"start": v(39.87, 18.17) * mm, "end": v(39.82, 18.28) * mm});
            skLineSegment(sketch, "E4235", {"start": v(39.82, 18.28) * mm, "end": v(39.77, 18.38) * mm});
            skLineSegment(sketch, "E4236", {"start": v(39.77, 18.38) * mm, "end": v(39.72, 18.5) * mm});
            skLineSegment(sketch, "E4237", {"start": v(39.72, 18.5) * mm, "end": v(39.67, 18.6) * mm});
            skLineSegment(sketch, "E4238", {"start": v(39.67, 18.6) * mm, "end": v(39.62, 18.7) * mm});
            skLineSegment(sketch, "E4239", {"start": v(39.62, 18.7) * mm, "end": v(39.57, 18.81) * mm});
            skLineSegment(sketch, "E4240", {"start": v(39.57, 18.81) * mm, "end": v(39.56, 18.83) * mm});
            skLineSegment(sketch, "E4241", {"start": v(39.56, 18.83) * mm, "end": v(39.64, 18.9) * mm});
            skLineSegment(sketch, "E4242", {"start": v(39.64, 18.9) * mm, "end": v(39.73, 18.98) * mm});
            skLineSegment(sketch, "E4243", {"start": v(39.73, 18.98) * mm, "end": v(39.8, 19.06) * mm});
            skLineSegment(sketch, "E4244", {"start": v(39.8, 19.06) * mm, "end": v(39.9, 19.14) * mm});
            skLineSegment(sketch, "E4245", {"start": v(39.9, 19.14) * mm, "end": v(39.98, 19.22) * mm});
            skLineSegment(sketch, "E4246", {"start": v(39.98, 19.22) * mm, "end": v(40.07, 19.3) * mm});
            skLineSegment(sketch, "E4247", {"start": v(40.07, 19.3) * mm, "end": v(40.16, 19.4) * mm});
            skLineSegment(sketch, "E4248", {"start": v(40.16, 19.4) * mm, "end": v(40.25, 19.5) * mm});
            skLineSegment(sketch, "E4249", {"start": v(40.25, 19.5) * mm, "end": v(40.34, 19.58) * mm});
            skLineSegment(sketch, "E4250", {"start": v(40.34, 19.58) * mm, "end": v(40.42, 19.67) * mm});
            skLineSegment(sketch, "E4251", {"start": v(40.42, 19.67) * mm, "end": v(40.5, 19.75) * mm});
            skLineSegment(sketch, "E4252", {"start": v(40.5, 19.75) * mm, "end": v(40.58, 19.83) * mm});
            skLineSegment(sketch, "E4253", {"start": v(40.58, 19.83) * mm, "end": v(40.65, 19.92) * mm});
            skLineSegment(sketch, "E4254", {"start": v(40.65, 19.92) * mm, "end": v(40.73, 20) * mm});
            skLineSegment(sketch, "E4255", {"start": v(40.73, 20) * mm, "end": v(40.81, 20.1) * mm});
            skLineSegment(sketch, "E4256", {"start": v(40.81, 20.1) * mm, "end": v(40.9, 20.19) * mm});
            skLineSegment(sketch, "E4257", {"start": v(40.9, 20.19) * mm, "end": v(40.97, 20.28) * mm});
            skLineSegment(sketch, "E4258", {"start": v(40.97, 20.28) * mm, "end": v(41.06, 20.38) * mm});
            skLineSegment(sketch, "E4259", {"start": v(41.06, 20.38) * mm, "end": v(41.14, 20.48) * mm});
            skLineSegment(sketch, "E4260", {"start": v(41.14, 20.48) * mm, "end": v(41.14, 20.48) * mm});
            skLineSegment(sketch, "E4261", {"start": v(41.14, 20.48) * mm, "end": v(41.09, 20.58) * mm});
            skLineSegment(sketch, "E4262", {"start": v(41.09, 20.58) * mm, "end": v(41.03, 20.7) * mm});
            skLineSegment(sketch, "E4263", {"start": v(41.03, 20.7) * mm, "end": v(40.98, 20.79) * mm});
            skLineSegment(sketch, "E4264", {"start": v(40.98, 20.79) * mm, "end": v(40.93, 20.9) * mm});
            skLineSegment(sketch, "E4265", {"start": v(40.93, 20.9) * mm, "end": v(40.89, 20.98) * mm});
            skLineSegment(sketch, "E4266", {"start": v(40.89, 20.98) * mm, "end": v(40.77, 20.97) * mm});
            skLineSegment(sketch, "E4267", {"start": v(40.77, 20.97) * mm, "end": v(40.64, 20.96) * mm});
            skLineSegment(sketch, "E4268", {"start": v(40.64, 20.96) * mm, "end": v(40.52, 20.96) * mm});
            skLineSegment(sketch, "E4269", {"start": v(40.52, 20.96) * mm, "end": v(40.41, 20.95) * mm});
            skLineSegment(sketch, "E4270", {"start": v(40.41, 20.95) * mm, "end": v(40.3, 20.93) * mm});
            skLineSegment(sketch, "E4271", {"start": v(40.3, 20.93) * mm, "end": v(40.17, 20.92) * mm});
            skLineSegment(sketch, "E4272", {"start": v(40.17, 20.92) * mm, "end": v(40.05, 20.91) * mm});
            skLineSegment(sketch, "E4273", {"start": v(40.05, 20.91) * mm, "end": v(39.94, 20.9) * mm});
            skLineSegment(sketch, "E4274", {"start": v(39.94, 20.9) * mm, "end": v(39.82, 20.88) * mm});
            skLineSegment(sketch, "E4275", {"start": v(39.82, 20.88) * mm, "end": v(39.7, 20.87) * mm});
            skLineSegment(sketch, "E4276", {"start": v(39.7, 20.87) * mm, "end": v(39.57, 20.85) * mm});
            skLineSegment(sketch, "E4277", {"start": v(39.57, 20.85) * mm, "end": v(39.45, 20.83) * mm});
            skLineSegment(sketch, "E4278", {"start": v(39.45, 20.83) * mm, "end": v(39.34, 20.82) * mm});
            skLineSegment(sketch, "E4279", {"start": v(39.34, 20.82) * mm, "end": v(39.22, 20.8) * mm});
            skLineSegment(sketch, "E4280", {"start": v(39.22, 20.8) * mm, "end": v(39.1, 20.78) * mm});
            skLineSegment(sketch, "E4281", {"start": v(39.1, 20.78) * mm, "end": v(38.98, 20.76) * mm});
            skLineSegment(sketch, "E4282", {"start": v(38.98, 20.76) * mm, "end": v(38.87, 20.74) * mm});
            skLineSegment(sketch, "E4283", {"start": v(38.87, 20.74) * mm, "end": v(38.75, 20.71) * mm});
            skLineSegment(sketch, "E4284", {"start": v(38.75, 20.71) * mm, "end": v(38.62, 20.69) * mm});
            skLineSegment(sketch, "E4285", {"start": v(38.62, 20.69) * mm, "end": v(38.56, 20.8) * mm});
            skLineSegment(sketch, "E4286", {"start": v(38.56, 20.8) * mm, "end": v(38.5, 20.9) * mm});
            skLineSegment(sketch, "E4287", {"start": v(38.5, 20.9) * mm, "end": v(38.45, 21) * mm});
            skLineSegment(sketch, "E4288", {"start": v(38.45, 21) * mm, "end": v(38.4, 21.1) * mm});
            skLineSegment(sketch, "E4289", {"start": v(38.4, 21.1) * mm, "end": v(38.34, 21.2) * mm});
            skLineSegment(sketch, "E4290", {"start": v(38.34, 21.2) * mm, "end": v(38.28, 21.3) * mm});
            skLineSegment(sketch, "E4291", {"start": v(38.28, 21.3) * mm, "end": v(38.22, 21.42) * mm});
            skLineSegment(sketch, "E4292", {"start": v(38.22, 21.42) * mm, "end": v(38.22, 21.43) * mm});
            skLineSegment(sketch, "E4293", {"start": v(38.22, 21.43) * mm, "end": v(38.3, 21.5) * mm});
            skLineSegment(sketch, "E4294", {"start": v(38.3, 21.5) * mm, "end": v(38.37, 21.59) * mm});
            skLineSegment(sketch, "E4295", {"start": v(38.37, 21.59) * mm, "end": v(38.45, 21.67) * mm});
            skLineSegment(sketch, "E4296", {"start": v(38.45, 21.67) * mm, "end": v(38.53, 21.76) * mm});
            skLineSegment(sketch, "E4297", {"start": v(38.53, 21.76) * mm, "end": v(38.6, 21.85) * mm});
            skLineSegment(sketch, "E4298", {"start": v(38.6, 21.85) * mm, "end": v(38.7, 21.94) * mm});
            skLineSegment(sketch, "E4299", {"start": v(38.7, 21.94) * mm, "end": v(38.78, 22.04) * mm});
            skLineSegment(sketch, "E4300", {"start": v(38.78, 22.04) * mm, "end": v(38.86, 22.14) * mm});
            skLineSegment(sketch, "E4301", {"start": v(38.86, 22.14) * mm, "end": v(38.94, 22.23) * mm});
            skLineSegment(sketch, "E4302", {"start": v(38.94, 22.23) * mm, "end": v(39.02, 22.32) * mm});
            skLineSegment(sketch, "E4303", {"start": v(39.02, 22.32) * mm, "end": v(39.1, 22.41) * mm});
            skLineSegment(sketch, "E4304", {"start": v(39.1, 22.41) * mm, "end": v(39.16, 22.5) * mm});
            skLineSegment(sketch, "E4305", {"start": v(39.16, 22.5) * mm, "end": v(39.23, 22.59) * mm});
            skLineSegment(sketch, "E4306", {"start": v(39.23, 22.59) * mm, "end": v(39.3, 22.68) * mm});
            skLineSegment(sketch, "E4307", {"start": v(39.3, 22.68) * mm, "end": v(39.38, 22.78) * mm});
            skLineSegment(sketch, "E4308", {"start": v(39.38, 22.78) * mm, "end": v(39.45, 22.87) * mm});
            skLineSegment(sketch, "E4309", {"start": v(39.45, 22.87) * mm, "end": v(39.53, 22.97) * mm});
            skLineSegment(sketch, "E4310", {"start": v(39.53, 22.97) * mm, "end": v(39.6, 23.07) * mm});
            skLineSegment(sketch, "E4311", {"start": v(39.6, 23.07) * mm, "end": v(39.68, 23.18) * mm});
            skLineSegment(sketch, "E4312", {"start": v(39.68, 23.18) * mm, "end": v(39.68, 23.18) * mm});
            skLineSegment(sketch, "E4313", {"start": v(39.68, 23.18) * mm, "end": v(39.62, 23.28) * mm});
            skLineSegment(sketch, "E4314", {"start": v(39.62, 23.28) * mm, "end": v(39.56, 23.39) * mm});
            skLineSegment(sketch, "E4315", {"start": v(39.56, 23.39) * mm, "end": v(39.5, 23.48) * mm});
            skLineSegment(sketch, "E4316", {"start": v(39.5, 23.48) * mm, "end": v(39.44, 23.58) * mm});
            skLineSegment(sketch, "E4317", {"start": v(39.44, 23.58) * mm, "end": v(39.4, 23.66) * mm});
            skLineSegment(sketch, "E4318", {"start": v(39.4, 23.66) * mm, "end": v(39.27, 23.65) * mm});
            skLineSegment(sketch, "E4319", {"start": v(39.27, 23.65) * mm, "end": v(39.15, 23.63) * mm});
            skLineSegment(sketch, "E4320", {"start": v(39.15, 23.63) * mm, "end": v(39.03, 23.62) * mm});
            skLineSegment(sketch, "E4321", {"start": v(39.03, 23.62) * mm, "end": v(38.92, 23.6) * mm});
            skLineSegment(sketch, "E4322", {"start": v(38.92, 23.6) * mm, "end": v(38.8, 23.58) * mm});
            skLineSegment(sketch, "E4323", {"start": v(38.8, 23.58) * mm, "end": v(38.69, 23.56) * mm});
            skLineSegment(sketch, "E4324", {"start": v(38.69, 23.56) * mm, "end": v(38.57, 23.54) * mm});
            skLineSegment(sketch, "E4325", {"start": v(38.57, 23.54) * mm, "end": v(38.45, 23.52) * mm});
            skLineSegment(sketch, "E4326", {"start": v(38.45, 23.52) * mm, "end": v(38.33, 23.5) * mm});
            skLineSegment(sketch, "E4327", {"start": v(38.33, 23.5) * mm, "end": v(38.2, 23.47) * mm});
            skLineSegment(sketch, "E4328", {"start": v(38.2, 23.47) * mm, "end": v(38.1, 23.45) * mm});
            skLineSegment(sketch, "E4329", {"start": v(38.1, 23.45) * mm, "end": v(37.98, 23.42) * mm});
            skLineSegment(sketch, "E4330", {"start": v(37.98, 23.42) * mm, "end": v(37.86, 23.4) * mm});
            skLineSegment(sketch, "E4331", {"start": v(37.86, 23.4) * mm, "end": v(37.74, 23.37) * mm});
            skLineSegment(sketch, "E4332", {"start": v(37.74, 23.37) * mm, "end": v(37.63, 23.34) * mm});
            skLineSegment(sketch, "E4333", {"start": v(37.63, 23.34) * mm, "end": v(37.5, 23.31) * mm});
            skLineSegment(sketch, "E4334", {"start": v(37.5, 23.31) * mm, "end": v(37.4, 23.29) * mm});
            skLineSegment(sketch, "E4335", {"start": v(37.4, 23.29) * mm, "end": v(37.28, 23.25) * mm});
            skLineSegment(sketch, "E4336", {"start": v(37.28, 23.25) * mm, "end": v(37.15, 23.22) * mm});
            skLineSegment(sketch, "E4337", {"start": v(37.15, 23.22) * mm, "end": v(37.09, 23.32) * mm});
            skLineSegment(sketch, "E4338", {"start": v(37.09, 23.32) * mm, "end": v(37.03, 23.42) * mm});
            skLineSegment(sketch, "E4339", {"start": v(37.03, 23.42) * mm, "end": v(36.96, 23.52) * mm});
            skLineSegment(sketch, "E4340", {"start": v(36.96, 23.52) * mm, "end": v(36.9, 23.62) * mm});
            skLineSegment(sketch, "E4341", {"start": v(36.9, 23.62) * mm, "end": v(36.83, 23.72) * mm});
            skLineSegment(sketch, "E4342", {"start": v(36.83, 23.72) * mm, "end": v(36.77, 23.82) * mm});
            skLineSegment(sketch, "E4343", {"start": v(36.77, 23.82) * mm, "end": v(36.7, 23.92) * mm});
            skLineSegment(sketch, "E4344", {"start": v(36.7, 23.92) * mm, "end": v(36.7, 23.93) * mm});
            skLineSegment(sketch, "E4345", {"start": v(36.7, 23.93) * mm, "end": v(36.77, 24.02) * mm});
            skLineSegment(sketch, "E4346", {"start": v(36.77, 24.02) * mm, "end": v(36.84, 24.1) * mm});
            skLineSegment(sketch, "E4347", {"start": v(36.84, 24.1) * mm, "end": v(36.91, 24.2) * mm});
            skLineSegment(sketch, "E4348", {"start": v(36.91, 24.2) * mm, "end": v(36.99, 24.28) * mm});
            skLineSegment(sketch, "E4349", {"start": v(36.99, 24.28) * mm, "end": v(37.06, 24.38) * mm});
            skLineSegment(sketch, "E4350", {"start": v(37.06, 24.38) * mm, "end": v(37.14, 24.48) * mm});
            skLineSegment(sketch, "E4351", {"start": v(37.14, 24.48) * mm, "end": v(37.22, 24.58) * mm});
            skLineSegment(sketch, "E4352", {"start": v(37.22, 24.58) * mm, "end": v(37.3, 24.68) * mm});
            skLineSegment(sketch, "E4353", {"start": v(37.3, 24.68) * mm, "end": v(37.37, 24.78) * mm});
            skLineSegment(sketch, "E4354", {"start": v(37.37, 24.78) * mm, "end": v(37.44, 24.88) * mm});
            skLineSegment(sketch, "E4355", {"start": v(37.44, 24.88) * mm, "end": v(37.5, 24.97) * mm});
            skLineSegment(sketch, "E4356", {"start": v(37.5, 24.97) * mm, "end": v(37.57, 25.06) * mm});
            skLineSegment(sketch, "E4357", {"start": v(37.57, 25.06) * mm, "end": v(37.64, 25.16) * mm});
            skLineSegment(sketch, "E4358", {"start": v(37.64, 25.16) * mm, "end": v(37.7, 25.26) * mm});
            skLineSegment(sketch, "E4359", {"start": v(37.7, 25.26) * mm, "end": v(37.77, 25.36) * mm});
            skLineSegment(sketch, "E4360", {"start": v(37.77, 25.36) * mm, "end": v(37.84, 25.46) * mm});
            skLineSegment(sketch, "E4361", {"start": v(37.84, 25.46) * mm, "end": v(37.9, 25.56) * mm});
            skLineSegment(sketch, "E4362", {"start": v(37.9, 25.56) * mm, "end": v(37.97, 25.67) * mm});
            skLineSegment(sketch, "E4363", {"start": v(37.97, 25.67) * mm, "end": v(38.04, 25.78) * mm});
            skLineSegment(sketch, "E4364", {"start": v(38.04, 25.78) * mm, "end": v(38.04, 25.78) * mm});
            skLineSegment(sketch, "E4365", {"start": v(38.04, 25.78) * mm, "end": v(37.98, 25.88) * mm});
            skLineSegment(sketch, "E4366", {"start": v(37.98, 25.88) * mm, "end": v(37.9, 25.98) * mm});
            skLineSegment(sketch, "E4367", {"start": v(37.9, 25.98) * mm, "end": v(37.85, 26.06) * mm});
            skLineSegment(sketch, "E4368", {"start": v(37.85, 26.06) * mm, "end": v(37.78, 26.16) * mm});
            skLineSegment(sketch, "E4369", {"start": v(37.78, 26.16) * mm, "end": v(37.72, 26.24) * mm});
            skLineSegment(sketch, "E4370", {"start": v(37.72, 26.24) * mm, "end": v(37.6, 26.22) * mm});
            skLineSegment(sketch, "E4371", {"start": v(37.6, 26.22) * mm, "end": v(37.49, 26.2) * mm});
            skLineSegment(sketch, "E4372", {"start": v(37.49, 26.2) * mm, "end": v(37.37, 26.17) * mm});
            skLineSegment(sketch, "E4373", {"start": v(37.37, 26.17) * mm, "end": v(37.26, 26.15) * mm});
            skLineSegment(sketch, "E4374", {"start": v(37.26, 26.15) * mm, "end": v(37.14, 26.12) * mm});
            skLineSegment(sketch, "E4375", {"start": v(37.14, 26.12) * mm, "end": v(37.03, 26.1) * mm});
            skLineSegment(sketch, "E4376", {"start": v(37.03, 26.1) * mm, "end": v(36.91, 26.06) * mm});
            skLineSegment(sketch, "E4377", {"start": v(36.91, 26.06) * mm, "end": v(36.8, 26.03) * mm});
            skLineSegment(sketch, "E4378", {"start": v(36.8, 26.03) * mm, "end": v(36.68, 26) * mm});
            skLineSegment(sketch, "E4379", {"start": v(36.68, 26) * mm, "end": v(36.56, 25.97) * mm});
            skLineSegment(sketch, "E4380", {"start": v(36.56, 25.97) * mm, "end": v(36.44, 25.94) * mm});
            skLineSegment(sketch, "E4381", {"start": v(36.44, 25.94) * mm, "end": v(36.33, 25.9) * mm});
            skLineSegment(sketch, "E4382", {"start": v(36.33, 25.9) * mm, "end": v(36.21, 25.87) * mm});
            skLineSegment(sketch, "E4383", {"start": v(36.21, 25.87) * mm, "end": v(36.1, 25.84) * mm});
            skLineSegment(sketch, "E4384", {"start": v(36.1, 25.84) * mm, "end": v(35.98, 25.8) * mm});
            skLineSegment(sketch, "E4385", {"start": v(35.98, 25.8) * mm, "end": v(35.87, 25.77) * mm});
            skLineSegment(sketch, "E4386", {"start": v(35.87, 25.77) * mm, "end": v(35.76, 25.73) * mm});
            skLineSegment(sketch, "E4387", {"start": v(35.76, 25.73) * mm, "end": v(35.64, 25.7) * mm});
            skLineSegment(sketch, "E4388", {"start": v(35.64, 25.7) * mm, "end": v(35.52, 25.65) * mm});
            skLineSegment(sketch, "E4389", {"start": v(35.52, 25.65) * mm, "end": v(35.45, 25.75) * mm});
            skLineSegment(sketch, "E4390", {"start": v(35.45, 25.75) * mm, "end": v(35.38, 25.84) * mm});
            skLineSegment(sketch, "E4391", {"start": v(35.38, 25.84) * mm, "end": v(35.3, 25.94) * mm});
            skLineSegment(sketch, "E4392", {"start": v(35.3, 25.94) * mm, "end": v(35.24, 26.03) * mm});
            skLineSegment(sketch, "E4393", {"start": v(35.24, 26.03) * mm, "end": v(35.17, 26.13) * mm});
            skLineSegment(sketch, "E4394", {"start": v(35.17, 26.13) * mm, "end": v(35.1, 26.22) * mm});
            skLineSegment(sketch, "E4395", {"start": v(35.1, 26.22) * mm, "end": v(35.03, 26.32) * mm});
            skLineSegment(sketch, "E4396", {"start": v(35.03, 26.32) * mm, "end": v(35.02, 26.33) * mm});
            skLineSegment(sketch, "E4397", {"start": v(35.02, 26.33) * mm, "end": v(35.08, 26.42) * mm});
            skLineSegment(sketch, "E4398", {"start": v(35.08, 26.42) * mm, "end": v(35.15, 26.51) * mm});
            skLineSegment(sketch, "E4399", {"start": v(35.15, 26.51) * mm, "end": v(35.22, 26.6) * mm});
            skLineSegment(sketch, "E4400", {"start": v(35.22, 26.6) * mm, "end": v(35.28, 26.7) * mm});
            skLineSegment(sketch, "E4401", {"start": v(35.28, 26.7) * mm, "end": v(35.35, 26.8) * mm});
            skLineSegment(sketch, "E4402", {"start": v(35.35, 26.8) * mm, "end": v(35.42, 26.9) * mm});
            skLineSegment(sketch, "E4403", {"start": v(35.42, 26.9) * mm, "end": v(35.5, 27.01) * mm});
            skLineSegment(sketch, "E4404", {"start": v(35.5, 27.01) * mm, "end": v(35.57, 27.12) * mm});
            skLineSegment(sketch, "E4405", {"start": v(35.57, 27.12) * mm, "end": v(35.63, 27.22) * mm});
            skLineSegment(sketch, "E4406", {"start": v(35.63, 27.22) * mm, "end": v(35.7, 27.33) * mm});
            skLineSegment(sketch, "E4407", {"start": v(35.7, 27.33) * mm, "end": v(35.75, 27.42) * mm});
            skLineSegment(sketch, "E4408", {"start": v(35.75, 27.42) * mm, "end": v(35.81, 27.52) * mm});
            skLineSegment(sketch, "E4409", {"start": v(35.81, 27.52) * mm, "end": v(35.87, 27.62) * mm});
            skLineSegment(sketch, "E4410", {"start": v(35.87, 27.62) * mm, "end": v(35.93, 27.72) * mm});
            skLineSegment(sketch, "E4411", {"start": v(35.93, 27.72) * mm, "end": v(36, 27.82) * mm});
            skLineSegment(sketch, "E4412", {"start": v(36, 27.82) * mm, "end": v(36.05, 27.93) * mm});
            skLineSegment(sketch, "E4413", {"start": v(36.05, 27.93) * mm, "end": v(36.11, 28.04) * mm});
            skLineSegment(sketch, "E4414", {"start": v(36.11, 28.04) * mm, "end": v(36.18, 28.15) * mm});
            skLineSegment(sketch, "E4415", {"start": v(36.18, 28.15) * mm, "end": v(36.24, 28.26) * mm});
            skLineSegment(sketch, "E4416", {"start": v(36.24, 28.26) * mm, "end": v(36.24, 28.26) * mm});
            skLineSegment(sketch, "E4417", {"start": v(36.24, 28.26) * mm, "end": v(36.16, 28.36) * mm});
            skLineSegment(sketch, "E4418", {"start": v(36.16, 28.36) * mm, "end": v(36.09, 28.45) * mm});
            skLineSegment(sketch, "E4419", {"start": v(36.09, 28.45) * mm, "end": v(36.02, 28.53) * mm});
            skLineSegment(sketch, "E4420", {"start": v(36.02, 28.53) * mm, "end": v(35.95, 28.63) * mm});
            skLineSegment(sketch, "E4421", {"start": v(35.95, 28.63) * mm, "end": v(35.89, 28.7) * mm});
            skLineSegment(sketch, "E4422", {"start": v(35.89, 28.7) * mm, "end": v(35.77, 28.67) * mm});
            skLineSegment(sketch, "E4423", {"start": v(35.77, 28.67) * mm, "end": v(35.65, 28.64) * mm});
            skLineSegment(sketch, "E4424", {"start": v(35.65, 28.64) * mm, "end": v(35.54, 28.6) * mm});
            skLineSegment(sketch, "E4425", {"start": v(35.54, 28.6) * mm, "end": v(35.43, 28.58) * mm});
            skLineSegment(sketch, "E4426", {"start": v(35.43, 28.58) * mm, "end": v(35.32, 28.54) * mm});
            skLineSegment(sketch, "E4427", {"start": v(35.32, 28.54) * mm, "end": v(35.2, 28.5) * mm});
            skLineSegment(sketch, "E4428", {"start": v(35.2, 28.5) * mm, "end": v(35.09, 28.47) * mm});
            skLineSegment(sketch, "E4429", {"start": v(35.09, 28.47) * mm, "end": v(34.97, 28.43) * mm});
            skLineSegment(sketch, "E4430", {"start": v(34.97, 28.43) * mm, "end": v(34.86, 28.4) * mm});
            skLineSegment(sketch, "E4431", {"start": v(34.86, 28.4) * mm, "end": v(34.74, 28.36) * mm});
            skLineSegment(sketch, "E4432", {"start": v(34.74, 28.36) * mm, "end": v(34.63, 28.32) * mm});
            skLineSegment(sketch, "E4433", {"start": v(34.63, 28.32) * mm, "end": v(34.51, 28.28) * mm});
            skLineSegment(sketch, "E4434", {"start": v(34.51, 28.28) * mm, "end": v(34.4, 28.24) * mm});
            skLineSegment(sketch, "E4435", {"start": v(34.4, 28.24) * mm, "end": v(34.3, 28.2) * mm});
            skLineSegment(sketch, "E4436", {"start": v(34.3, 28.2) * mm, "end": v(34.18, 28.15) * mm});
            skLineSegment(sketch, "E4437", {"start": v(34.18, 28.15) * mm, "end": v(34.07, 28.1) * mm});
            skLineSegment(sketch, "E4438", {"start": v(34.07, 28.1) * mm, "end": v(33.96, 28.06) * mm});
            skLineSegment(sketch, "E4439", {"start": v(33.96, 28.06) * mm, "end": v(33.85, 28.02) * mm});
            skLineSegment(sketch, "E4440", {"start": v(33.85, 28.02) * mm, "end": v(33.73, 27.96) * mm});
            skLineSegment(sketch, "E4441", {"start": v(33.73, 27.96) * mm, "end": v(33.65, 28.06) * mm});
            skLineSegment(sketch, "E4442", {"start": v(33.65, 28.06) * mm, "end": v(33.57, 28.15) * mm});
            skLineSegment(sketch, "E4443", {"start": v(33.57, 28.15) * mm, "end": v(33.5, 28.24) * mm});
            skLineSegment(sketch, "E4444", {"start": v(33.5, 28.24) * mm, "end": v(33.42, 28.33) * mm});
            skLineSegment(sketch, "E4445", {"start": v(33.42, 28.33) * mm, "end": v(33.34, 28.42) * mm});
            skLineSegment(sketch, "E4446", {"start": v(33.34, 28.42) * mm, "end": v(33.27, 28.5) * mm});
            skLineSegment(sketch, "E4447", {"start": v(33.27, 28.5) * mm, "end": v(33.2, 28.6) * mm});
            skLineSegment(sketch, "E4448", {"start": v(33.2, 28.6) * mm, "end": v(33.18, 28.61) * mm});
            skLineSegment(sketch, "E4449", {"start": v(33.18, 28.61) * mm, "end": v(33.24, 28.7) * mm});
            skLineSegment(sketch, "E4450", {"start": v(33.24, 28.7) * mm, "end": v(33.3, 28.8) * mm});
            skLineSegment(sketch, "E4451", {"start": v(33.3, 28.8) * mm, "end": v(33.36, 28.9) * mm});
            skLineSegment(sketch, "E4452", {"start": v(33.36, 28.9) * mm, "end": v(33.42, 29) * mm});
            skLineSegment(sketch, "E4453", {"start": v(33.42, 29) * mm, "end": v(33.48, 29.1) * mm});
            skLineSegment(sketch, "E4454", {"start": v(33.48, 29.1) * mm, "end": v(33.55, 29.2) * mm});
            skLineSegment(sketch, "E4455", {"start": v(33.55, 29.2) * mm, "end": v(33.61, 29.32) * mm});
            skLineSegment(sketch, "E4456", {"start": v(33.61, 29.32) * mm, "end": v(33.67, 29.43) * mm});
            skLineSegment(sketch, "E4457", {"start": v(33.67, 29.43) * mm, "end": v(33.73, 29.54) * mm});
            skLineSegment(sketch, "E4458", {"start": v(33.73, 29.54) * mm, "end": v(33.8, 29.65) * mm});
            skLineSegment(sketch, "E4459", {"start": v(33.8, 29.65) * mm, "end": v(33.84, 29.75) * mm});
            skLineSegment(sketch, "E4460", {"start": v(33.84, 29.75) * mm, "end": v(33.9, 29.85) * mm});
            skLineSegment(sketch, "E4461", {"start": v(33.9, 29.85) * mm, "end": v(33.95, 29.95) * mm});
            skLineSegment(sketch, "E4462", {"start": v(33.95, 29.95) * mm, "end": v(34, 30.06) * mm});
            skLineSegment(sketch, "E4463", {"start": v(34, 30.06) * mm, "end": v(34.05, 30.16) * mm});
            skLineSegment(sketch, "E4464", {"start": v(34.05, 30.16) * mm, "end": v(34.1, 30.27) * mm});
            skLineSegment(sketch, "E4465", {"start": v(34.1, 30.27) * mm, "end": v(34.16, 30.39) * mm});
            skLineSegment(sketch, "E4466", {"start": v(34.16, 30.39) * mm, "end": v(34.21, 30.5) * mm});
            skLineSegment(sketch, "E4467", {"start": v(34.21, 30.5) * mm, "end": v(34.27, 30.62) * mm});
            skLineSegment(sketch, "E4468", {"start": v(34.27, 30.62) * mm, "end": v(34.27, 30.62) * mm});
            skLineSegment(sketch, "E4469", {"start": v(34.27, 30.62) * mm, "end": v(34.19, 30.7) * mm});
            skLineSegment(sketch, "E4470", {"start": v(34.19, 30.7) * mm, "end": v(34.1, 30.8) * mm});
            skLineSegment(sketch, "E4471", {"start": v(34.1, 30.8) * mm, "end": v(34.04, 30.88) * mm});
            skLineSegment(sketch, "E4472", {"start": v(34.04, 30.88) * mm, "end": v(33.96, 30.96) * mm});
            skLineSegment(sketch, "E4473", {"start": v(33.96, 30.96) * mm, "end": v(33.9, 31.04) * mm});
            skLineSegment(sketch, "E4474", {"start": v(33.9, 31.04) * mm, "end": v(33.78, 31) * mm});
            skLineSegment(sketch, "E4475", {"start": v(33.78, 31) * mm, "end": v(33.66, 30.96) * mm});
            skLineSegment(sketch, "E4476", {"start": v(33.66, 30.96) * mm, "end": v(33.55, 30.92) * mm});
            skLineSegment(sketch, "E4477", {"start": v(33.55, 30.92) * mm, "end": v(33.44, 30.88) * mm});
            skLineSegment(sketch, "E4478", {"start": v(33.44, 30.88) * mm, "end": v(33.33, 30.84) * mm});
            skLineSegment(sketch, "E4479", {"start": v(33.33, 30.84) * mm, "end": v(33.22, 30.8) * mm});
            skLineSegment(sketch, "E4480", {"start": v(33.22, 30.8) * mm, "end": v(33.1, 30.75) * mm});
            skLineSegment(sketch, "E4481", {"start": v(33.1, 30.75) * mm, "end": v(33, 30.7) * mm});
            skLineSegment(sketch, "E4482", {"start": v(33, 30.7) * mm, "end": v(32.89, 30.66) * mm});
            skLineSegment(sketch, "E4483", {"start": v(32.89, 30.66) * mm, "end": v(32.77, 30.61) * mm});
            skLineSegment(sketch, "E4484", {"start": v(32.77, 30.61) * mm, "end": v(32.66, 30.57) * mm});
            skLineSegment(sketch, "E4485", {"start": v(32.66, 30.57) * mm, "end": v(32.55, 30.52) * mm});
            skLineSegment(sketch, "E4486", {"start": v(32.55, 30.52) * mm, "end": v(32.44, 30.47) * mm});
            skLineSegment(sketch, "E4487", {"start": v(32.44, 30.47) * mm, "end": v(32.33, 30.42) * mm});
            skLineSegment(sketch, "E4488", {"start": v(32.33, 30.42) * mm, "end": v(32.22, 30.37) * mm});
            skLineSegment(sketch, "E4489", {"start": v(32.22, 30.37) * mm, "end": v(32.11, 30.32) * mm});
            skLineSegment(sketch, "E4490", {"start": v(32.11, 30.32) * mm, "end": v(32, 30.27) * mm});
            skLineSegment(sketch, "E4491", {"start": v(32, 30.27) * mm, "end": v(31.9, 30.21) * mm});
            skLineSegment(sketch, "E4492", {"start": v(31.9, 30.21) * mm, "end": v(31.78, 30.16) * mm});
            skLineSegment(sketch, "E4493", {"start": v(31.78, 30.16) * mm, "end": v(31.7, 30.24) * mm});
            skLineSegment(sketch, "E4494", {"start": v(31.7, 30.24) * mm, "end": v(31.62, 30.33) * mm});
            skLineSegment(sketch, "E4495", {"start": v(31.62, 30.33) * mm, "end": v(31.54, 30.41) * mm});
            skLineSegment(sketch, "E4496", {"start": v(31.54, 30.41) * mm, "end": v(31.46, 30.5) * mm});
            skLineSegment(sketch, "E4497", {"start": v(31.46, 30.5) * mm, "end": v(31.37, 30.58) * mm});
            skLineSegment(sketch, "E4498", {"start": v(31.37, 30.58) * mm, "end": v(31.3, 30.67) * mm});
            skLineSegment(sketch, "E4499", {"start": v(31.3, 30.67) * mm, "end": v(31.2, 30.75) * mm});
            skLineSegment(sketch, "E4500", {"start": v(31.2, 30.75) * mm, "end": v(31.2, 30.77) * mm});
            skLineSegment(sketch, "E4501", {"start": v(31.2, 30.77) * mm, "end": v(31.25, 30.86) * mm});
            skLineSegment(sketch, "E4502", {"start": v(31.25, 30.86) * mm, "end": v(31.3, 30.96) * mm});
            skLineSegment(sketch, "E4503", {"start": v(31.3, 30.96) * mm, "end": v(31.36, 31.06) * mm});
            skLineSegment(sketch, "E4504", {"start": v(31.36, 31.06) * mm, "end": v(31.41, 31.17) * mm});
            skLineSegment(sketch, "E4505", {"start": v(31.41, 31.17) * mm, "end": v(31.47, 31.27) * mm});
            skLineSegment(sketch, "E4506", {"start": v(31.47, 31.27) * mm, "end": v(31.52, 31.39) * mm});
            skLineSegment(sketch, "E4507", {"start": v(31.52, 31.39) * mm, "end": v(31.58, 31.5) * mm});
            skLineSegment(sketch, "E4508", {"start": v(31.58, 31.5) * mm, "end": v(31.63, 31.62) * mm});
            skLineSegment(sketch, "E4509", {"start": v(31.63, 31.62) * mm, "end": v(31.68, 31.73) * mm});
            skLineSegment(sketch, "E4510", {"start": v(31.68, 31.73) * mm, "end": v(31.74, 31.84) * mm});
            skLineSegment(sketch, "E4511", {"start": v(31.74, 31.84) * mm, "end": v(31.78, 31.94) * mm});
            skLineSegment(sketch, "E4512", {"start": v(31.78, 31.94) * mm, "end": v(31.83, 32.05) * mm});
            skLineSegment(sketch, "E4513", {"start": v(31.83, 32.05) * mm, "end": v(31.87, 32.15) * mm});
            skLineSegment(sketch, "E4514", {"start": v(31.87, 32.15) * mm, "end": v(31.92, 32.26) * mm});
            skLineSegment(sketch, "E4515", {"start": v(31.92, 32.26) * mm, "end": v(31.96, 32.37) * mm});
            skLineSegment(sketch, "E4516", {"start": v(31.96, 32.37) * mm, "end": v(32.01, 32.49) * mm});
            skLineSegment(sketch, "E4517", {"start": v(32.01, 32.49) * mm, "end": v(32.06, 32.6) * mm});
            skLineSegment(sketch, "E4518", {"start": v(32.06, 32.6) * mm, "end": v(32.1, 32.72) * mm});
            skLineSegment(sketch, "E4519", {"start": v(32.1, 32.72) * mm, "end": v(32.15, 32.84) * mm});
            skLineSegment(sketch, "E4520", {"start": v(32.15, 32.84) * mm, "end": v(32.15, 32.84) * mm});
            skLineSegment(sketch, "E4521", {"start": v(32.15, 32.84) * mm, "end": v(32.06, 32.92) * mm});
            skLineSegment(sketch, "E4522", {"start": v(32.06, 32.92) * mm, "end": v(31.98, 33) * mm});
            skLineSegment(sketch, "E4523", {"start": v(31.98, 33) * mm, "end": v(31.9, 33.08) * mm});
            skLineSegment(sketch, "E4524", {"start": v(31.9, 33.08) * mm, "end": v(31.81, 33.16) * mm});
            skLineSegment(sketch, "E4525", {"start": v(31.81, 33.16) * mm, "end": v(31.74, 33.23) * mm});
            skLineSegment(sketch, "E4526", {"start": v(31.74, 33.23) * mm, "end": v(31.63, 33.18) * mm});
            skLineSegment(sketch, "E4527", {"start": v(31.63, 33.18) * mm, "end": v(31.52, 33.14) * mm});
            skLineSegment(sketch, "E4528", {"start": v(31.52, 33.14) * mm, "end": v(31.4, 33.09) * mm});
            skLineSegment(sketch, "E4529", {"start": v(31.4, 33.09) * mm, "end": v(31.3, 33.04) * mm});
            skLineSegment(sketch, "E4530", {"start": v(31.3, 33.04) * mm, "end": v(31.2, 33) * mm});
            skLineSegment(sketch, "E4531", {"start": v(31.2, 33) * mm, "end": v(31.09, 32.94) * mm});
            skLineSegment(sketch, "E4532", {"start": v(31.09, 32.94) * mm, "end": v(30.98, 32.9) * mm});
            skLineSegment(sketch, "E4533", {"start": v(30.98, 32.9) * mm, "end": v(30.87, 32.84) * mm});
            skLineSegment(sketch, "E4534", {"start": v(30.87, 32.84) * mm, "end": v(30.76, 32.79) * mm});
            skLineSegment(sketch, "E4535", {"start": v(30.76, 32.79) * mm, "end": v(30.65, 32.73) * mm});
            skLineSegment(sketch, "E4536", {"start": v(30.65, 32.73) * mm, "end": v(30.54, 32.68) * mm});
            skLineSegment(sketch, "E4537", {"start": v(30.54, 32.68) * mm, "end": v(30.44, 32.62) * mm});
            skLineSegment(sketch, "E4538", {"start": v(30.44, 32.62) * mm, "end": v(30.33, 32.57) * mm});
            skLineSegment(sketch, "E4539", {"start": v(30.33, 32.57) * mm, "end": v(30.23, 32.51) * mm});
            skLineSegment(sketch, "E4540", {"start": v(30.23, 32.51) * mm, "end": v(30.12, 32.46) * mm});
            skLineSegment(sketch, "E4541", {"start": v(30.12, 32.46) * mm, "end": v(30.02, 32.4) * mm});
            skLineSegment(sketch, "E4542", {"start": v(30.02, 32.4) * mm, "end": v(29.91, 32.34) * mm});
            skLineSegment(sketch, "E4543", {"start": v(29.91, 32.34) * mm, "end": v(29.81, 32.28) * mm});
            skLineSegment(sketch, "E4544", {"start": v(29.81, 32.28) * mm, "end": v(29.7, 32.21) * mm});
            skLineSegment(sketch, "E4545", {"start": v(29.7, 32.21) * mm, "end": v(29.61, 32.3) * mm});
            skLineSegment(sketch, "E4546", {"start": v(29.61, 32.3) * mm, "end": v(29.52, 32.37) * mm});
            skLineSegment(sketch, "E4547", {"start": v(29.52, 32.37) * mm, "end": v(29.44, 32.45) * mm});
            skLineSegment(sketch, "E4548", {"start": v(29.44, 32.45) * mm, "end": v(29.35, 32.53) * mm});
            skLineSegment(sketch, "E4549", {"start": v(29.35, 32.53) * mm, "end": v(29.26, 32.6) * mm});
            skLineSegment(sketch, "E4550", {"start": v(29.26, 32.6) * mm, "end": v(29.17, 32.69) * mm});
            skLineSegment(sketch, "E4551", {"start": v(29.17, 32.69) * mm, "end": v(29.09, 32.77) * mm});
            skLineSegment(sketch, "E4552", {"start": v(29.09, 32.77) * mm, "end": v(29.07, 32.78) * mm});
            skLineSegment(sketch, "E4553", {"start": v(29.07, 32.78) * mm, "end": v(29.12, 32.88) * mm});
            skLineSegment(sketch, "E4554", {"start": v(29.12, 32.88) * mm, "end": v(29.17, 32.98) * mm});
            skLineSegment(sketch, "E4555", {"start": v(29.17, 32.98) * mm, "end": v(29.21, 33.09) * mm});
            skLineSegment(sketch, "E4556", {"start": v(29.21, 33.09) * mm, "end": v(29.26, 33.2) * mm});
            skLineSegment(sketch, "E4557", {"start": v(29.26, 33.2) * mm, "end": v(29.3, 33.3) * mm});
            skLineSegment(sketch, "E4558", {"start": v(29.3, 33.3) * mm, "end": v(29.36, 33.42) * mm});
            skLineSegment(sketch, "E4559", {"start": v(29.36, 33.42) * mm, "end": v(29.4, 33.54) * mm});
            skLineSegment(sketch, "E4560", {"start": v(29.4, 33.54) * mm, "end": v(29.45, 33.66) * mm});
            skLineSegment(sketch, "E4561", {"start": v(29.45, 33.66) * mm, "end": v(29.5, 33.77) * mm});
            skLineSegment(sketch, "E4562", {"start": v(29.5, 33.77) * mm, "end": v(29.54, 33.89) * mm});
            skLineSegment(sketch, "E4563", {"start": v(29.54, 33.89) * mm, "end": v(29.58, 34) * mm});
            skLineSegment(sketch, "E4564", {"start": v(29.58, 34) * mm, "end": v(29.62, 34.1) * mm});
            skLineSegment(sketch, "E4565", {"start": v(29.62, 34.1) * mm, "end": v(29.65, 34.2) * mm});
            skLineSegment(sketch, "E4566", {"start": v(29.65, 34.2) * mm, "end": v(29.7, 34.32) * mm});
            skLineSegment(sketch, "E4567", {"start": v(29.7, 34.32) * mm, "end": v(29.73, 34.43) * mm});
            skLineSegment(sketch, "E4568", {"start": v(29.73, 34.43) * mm, "end": v(29.77, 34.55) * mm});
            skLineSegment(sketch, "E4569", {"start": v(29.77, 34.55) * mm, "end": v(29.8, 34.67) * mm});
            skLineSegment(sketch, "E4570", {"start": v(29.8, 34.67) * mm, "end": v(29.84, 34.79) * mm});
            skLineSegment(sketch, "E4571", {"start": v(29.84, 34.79) * mm, "end": v(29.88, 34.91) * mm});
            skLineSegment(sketch, "E4572", {"start": v(29.88, 34.91) * mm, "end": v(29.88, 34.91) * mm});
            skLineSegment(sketch, "E4573", {"start": v(29.88, 34.91) * mm, "end": v(29.8, 35) * mm});
            skLineSegment(sketch, "E4574", {"start": v(29.8, 35) * mm, "end": v(29.7, 35.07) * mm});
            skLineSegment(sketch, "E4575", {"start": v(29.7, 35.07) * mm, "end": v(29.62, 35.14) * mm});
            skLineSegment(sketch, "E4576", {"start": v(29.62, 35.14) * mm, "end": v(29.53, 35.21) * mm});
            skLineSegment(sketch, "E4577", {"start": v(29.53, 35.21) * mm, "end": v(29.45, 35.28) * mm});
            skLineSegment(sketch, "E4578", {"start": v(29.45, 35.28) * mm, "end": v(29.35, 35.22) * mm});
            skLineSegment(sketch, "E4579", {"start": v(29.35, 35.22) * mm, "end": v(29.24, 35.17) * mm});
            skLineSegment(sketch, "E4580", {"start": v(29.24, 35.17) * mm, "end": v(29.13, 35.11) * mm});
            skLineSegment(sketch, "E4581", {"start": v(29.13, 35.11) * mm, "end": v(29.03, 35.06) * mm});
            skLineSegment(sketch, "E4582", {"start": v(29.03, 35.06) * mm, "end": v(28.92, 35) * mm});
            skLineSegment(sketch, "E4583", {"start": v(28.92, 35) * mm, "end": v(28.82, 34.95) * mm});
            skLineSegment(sketch, "E4584", {"start": v(28.82, 34.95) * mm, "end": v(28.71, 34.89) * mm});
            skLineSegment(sketch, "E4585", {"start": v(28.71, 34.89) * mm, "end": v(28.6, 34.83) * mm});
            skLineSegment(sketch, "E4586", {"start": v(28.6, 34.83) * mm, "end": v(28.5, 34.77) * mm});
            skLineSegment(sketch, "E4587", {"start": v(28.5, 34.77) * mm, "end": v(28.4, 34.7) * mm});
            skLineSegment(sketch, "E4588", {"start": v(28.4, 34.7) * mm, "end": v(28.3, 34.65) * mm});
            skLineSegment(sketch, "E4589", {"start": v(28.3, 34.65) * mm, "end": v(28.2, 34.59) * mm});
            skLineSegment(sketch, "E4590", {"start": v(28.2, 34.59) * mm, "end": v(28.09, 34.52) * mm});
            skLineSegment(sketch, "E4591", {"start": v(28.09, 34.52) * mm, "end": v(27.99, 34.46) * mm});
            skLineSegment(sketch, "E4592", {"start": v(27.99, 34.46) * mm, "end": v(27.89, 34.4) * mm});
            skLineSegment(sketch, "E4593", {"start": v(27.89, 34.4) * mm, "end": v(27.79, 34.33) * mm});
            skLineSegment(sketch, "E4594", {"start": v(27.79, 34.33) * mm, "end": v(27.69, 34.26) * mm});
            skLineSegment(sketch, "E4595", {"start": v(27.69, 34.26) * mm, "end": v(27.59, 34.2) * mm});
            skLineSegment(sketch, "E4596", {"start": v(27.59, 34.2) * mm, "end": v(27.48, 34.12) * mm});
            skLineSegment(sketch, "E4597", {"start": v(27.48, 34.12) * mm, "end": v(27.39, 34.2) * mm});
            skLineSegment(sketch, "E4598", {"start": v(27.39, 34.2) * mm, "end": v(27.3, 34.27) * mm});
            skLineSegment(sketch, "E4599", {"start": v(27.3, 34.27) * mm, "end": v(27.2, 34.34) * mm});
            skLineSegment(sketch, "E4600", {"start": v(27.2, 34.34) * mm, "end": v(27.11, 34.42) * mm});
            skLineSegment(sketch, "E4601", {"start": v(27.11, 34.42) * mm, "end": v(27.02, 34.5) * mm});
            skLineSegment(sketch, "E4602", {"start": v(27.02, 34.5) * mm, "end": v(26.92, 34.56) * mm});
            skLineSegment(sketch, "E4603", {"start": v(26.92, 34.56) * mm, "end": v(26.83, 34.64) * mm});
            skLineSegment(sketch, "E4604", {"start": v(26.83, 34.64) * mm, "end": v(26.82, 34.65) * mm});
            skLineSegment(sketch, "E4605", {"start": v(26.82, 34.65) * mm, "end": v(26.86, 34.75) * mm});
            skLineSegment(sketch, "E4606", {"start": v(26.86, 34.75) * mm, "end": v(26.9, 34.85) * mm});
            skLineSegment(sketch, "E4607", {"start": v(26.9, 34.85) * mm, "end": v(26.94, 34.96) * mm});
            skLineSegment(sketch, "E4608", {"start": v(26.94, 34.96) * mm, "end": v(26.98, 35.07) * mm});
            skLineSegment(sketch, "E4609", {"start": v(26.98, 35.07) * mm, "end": v(27.02, 35.19) * mm});
            skLineSegment(sketch, "E4610", {"start": v(27.02, 35.19) * mm, "end": v(27.06, 35.3) * mm});
            skLineSegment(sketch, "E4611", {"start": v(27.06, 35.3) * mm, "end": v(27.1, 35.43) * mm});
            skLineSegment(sketch, "E4612", {"start": v(27.1, 35.43) * mm, "end": v(27.14, 35.55) * mm});
            skLineSegment(sketch, "E4613", {"start": v(27.14, 35.55) * mm, "end": v(27.17, 35.67) * mm});
            skLineSegment(sketch, "E4614", {"start": v(27.17, 35.67) * mm, "end": v(27.2, 35.79) * mm});
            skLineSegment(sketch, "E4615", {"start": v(27.2, 35.79) * mm, "end": v(27.24, 35.9) * mm});
            skLineSegment(sketch, "E4616", {"start": v(27.24, 35.9) * mm, "end": v(27.27, 36) * mm});
            skLineSegment(sketch, "E4617", {"start": v(27.27, 36) * mm, "end": v(27.3, 36.11) * mm});
            skLineSegment(sketch, "E4618", {"start": v(27.3, 36.11) * mm, "end": v(27.33, 36.23) * mm});
            skLineSegment(sketch, "E4619", {"start": v(27.33, 36.23) * mm, "end": v(27.36, 36.34) * mm});
            skLineSegment(sketch, "E4620", {"start": v(27.36, 36.34) * mm, "end": v(27.4, 36.46) * mm});
            skLineSegment(sketch, "E4621", {"start": v(27.4, 36.46) * mm, "end": v(27.43, 36.58) * mm});
            skLineSegment(sketch, "E4622", {"start": v(27.43, 36.58) * mm, "end": v(27.45, 36.7) * mm});
            skLineSegment(sketch, "E4623", {"start": v(27.45, 36.7) * mm, "end": v(27.48, 36.83) * mm});
            skLineSegment(sketch, "E4624", {"start": v(27.48, 36.83) * mm, "end": v(27.48, 36.83) * mm});
            skLineSegment(sketch, "E4625", {"start": v(27.48, 36.83) * mm, "end": v(27.39, 36.9) * mm});
            skLineSegment(sketch, "E4626", {"start": v(27.39, 36.9) * mm, "end": v(27.3, 36.97) * mm});
            skLineSegment(sketch, "E4627", {"start": v(27.3, 36.97) * mm, "end": v(27.2, 37.04) * mm});
            skLineSegment(sketch, "E4628", {"start": v(27.2, 37.04) * mm, "end": v(27.1, 37.1) * mm});
            skLineSegment(sketch, "E4629", {"start": v(27.1, 37.1) * mm, "end": v(27.03, 37.17) * mm});
            skLineSegment(sketch, "E4630", {"start": v(27.03, 37.17) * mm, "end": v(26.93, 37.1) * mm});
            skLineSegment(sketch, "E4631", {"start": v(26.93, 37.1) * mm, "end": v(26.82, 37.04) * mm});
            skLineSegment(sketch, "E4632", {"start": v(26.82, 37.04) * mm, "end": v(26.72, 36.98) * mm});
            skLineSegment(sketch, "E4633", {"start": v(26.72, 36.98) * mm, "end": v(26.62, 36.92) * mm});
            skLineSegment(sketch, "E4634", {"start": v(26.62, 36.92) * mm, "end": v(26.52, 36.86) * mm});
            skLineSegment(sketch, "E4635", {"start": v(26.52, 36.86) * mm, "end": v(26.42, 36.8) * mm});
            skLineSegment(sketch, "E4636", {"start": v(26.42, 36.8) * mm, "end": v(26.32, 36.73) * mm});
            skLineSegment(sketch, "E4637", {"start": v(26.32, 36.73) * mm, "end": v(26.22, 36.66) * mm});
            skLineSegment(sketch, "E4638", {"start": v(26.22, 36.66) * mm, "end": v(26.12, 36.6) * mm});
            skLineSegment(sketch, "E4639", {"start": v(26.12, 36.6) * mm, "end": v(26.02, 36.53) * mm});
            skLineSegment(sketch, "E4640", {"start": v(26.02, 36.53) * mm, "end": v(25.92, 36.46) * mm});
            skLineSegment(sketch, "E4641", {"start": v(25.92, 36.46) * mm, "end": v(25.82, 36.4) * mm});
            skLineSegment(sketch, "E4642", {"start": v(25.82, 36.4) * mm, "end": v(25.72, 36.32) * mm});
            skLineSegment(sketch, "E4643", {"start": v(25.72, 36.32) * mm, "end": v(25.62, 36.25) * mm});
            skLineSegment(sketch, "E4644", {"start": v(25.62, 36.25) * mm, "end": v(25.53, 36.18) * mm});
            skLineSegment(sketch, "E4645", {"start": v(25.53, 36.18) * mm, "end": v(25.43, 36.1) * mm});
            skLineSegment(sketch, "E4646", {"start": v(25.43, 36.1) * mm, "end": v(25.34, 36.04) * mm});
            skLineSegment(sketch, "E4647", {"start": v(25.34, 36.04) * mm, "end": v(25.24, 35.96) * mm});
            skLineSegment(sketch, "E4648", {"start": v(25.24, 35.96) * mm, "end": v(25.14, 35.88) * mm});
            skLineSegment(sketch, "E4649", {"start": v(25.14, 35.88) * mm, "end": v(25.04, 35.95) * mm});
            skLineSegment(sketch, "E4650", {"start": v(25.04, 35.95) * mm, "end": v(24.95, 36.02) * mm});
            skLineSegment(sketch, "E4651", {"start": v(24.95, 36.02) * mm, "end": v(24.85, 36.09) * mm});
            skLineSegment(sketch, "E4652", {"start": v(24.85, 36.09) * mm, "end": v(24.75, 36.15) * mm});
            skLineSegment(sketch, "E4653", {"start": v(24.75, 36.15) * mm, "end": v(24.65, 36.22) * mm});
            skLineSegment(sketch, "E4654", {"start": v(24.65, 36.22) * mm, "end": v(24.56, 36.28) * mm});
            skLineSegment(sketch, "E4655", {"start": v(24.56, 36.28) * mm, "end": v(24.46, 36.35) * mm});
            skLineSegment(sketch, "E4656", {"start": v(24.46, 36.35) * mm, "end": v(24.45, 36.36) * mm});
            skLineSegment(sketch, "E4657", {"start": v(24.45, 36.36) * mm, "end": v(24.48, 36.47) * mm});
            skLineSegment(sketch, "E4658", {"start": v(24.48, 36.47) * mm, "end": v(24.51, 36.57) * mm});
            skLineSegment(sketch, "E4659", {"start": v(24.51, 36.57) * mm, "end": v(24.54, 36.68) * mm});
            skLineSegment(sketch, "E4660", {"start": v(24.54, 36.68) * mm, "end": v(24.58, 36.8) * mm});
            skLineSegment(sketch, "E4661", {"start": v(24.58, 36.8) * mm, "end": v(24.6, 36.91) * mm});
            skLineSegment(sketch, "E4662", {"start": v(24.6, 36.91) * mm, "end": v(24.64, 37.04) * mm});
            skLineSegment(sketch, "E4663", {"start": v(24.64, 37.04) * mm, "end": v(24.67, 37.16) * mm});
            skLineSegment(sketch, "E4664", {"start": v(24.67, 37.16) * mm, "end": v(24.7, 37.29) * mm});
            skLineSegment(sketch, "E4665", {"start": v(24.7, 37.29) * mm, "end": v(24.73, 37.4) * mm});
            skLineSegment(sketch, "E4666", {"start": v(24.73, 37.4) * mm, "end": v(24.76, 37.52) * mm});
            skLineSegment(sketch, "E4667", {"start": v(24.76, 37.52) * mm, "end": v(24.78, 37.63) * mm});
            skLineSegment(sketch, "E4668", {"start": v(24.78, 37.63) * mm, "end": v(24.8, 37.74) * mm});
            skLineSegment(sketch, "E4669", {"start": v(24.8, 37.74) * mm, "end": v(24.83, 37.86) * mm});
            skLineSegment(sketch, "E4670", {"start": v(24.83, 37.86) * mm, "end": v(24.85, 37.97) * mm});
            skLineSegment(sketch, "E4671", {"start": v(24.85, 37.97) * mm, "end": v(24.88, 38.1) * mm});
            skLineSegment(sketch, "E4672", {"start": v(24.88, 38.1) * mm, "end": v(24.9, 38.21) * mm});
            skLineSegment(sketch, "E4673", {"start": v(24.9, 38.21) * mm, "end": v(24.92, 38.33) * mm});
            skLineSegment(sketch, "E4674", {"start": v(24.92, 38.33) * mm, "end": v(24.94, 38.46) * mm});
            skLineSegment(sketch, "E4675", {"start": v(24.94, 38.46) * mm, "end": v(24.96, 38.58) * mm});
            skLineSegment(sketch, "E4676", {"start": v(24.96, 38.58) * mm, "end": v(24.96, 38.58) * mm});
            skLineSegment(sketch, "E4677", {"start": v(24.96, 38.58) * mm, "end": v(24.86, 38.65) * mm});
            skLineSegment(sketch, "E4678", {"start": v(24.86, 38.65) * mm, "end": v(24.76, 38.71) * mm});
            skLineSegment(sketch, "E4679", {"start": v(24.76, 38.71) * mm, "end": v(24.67, 38.77) * mm});
            skLineSegment(sketch, "E4680", {"start": v(24.67, 38.77) * mm, "end": v(24.57, 38.84) * mm});
            skLineSegment(sketch, "E4681", {"start": v(24.57, 38.84) * mm, "end": v(24.49, 38.89) * mm});
            skLineSegment(sketch, "E4682", {"start": v(24.49, 38.89) * mm, "end": v(24.39, 38.82) * mm});
            skLineSegment(sketch, "E4683", {"start": v(24.39, 38.82) * mm, "end": v(24.29, 38.75) * mm});
            skLineSegment(sketch, "E4684", {"start": v(24.29, 38.75) * mm, "end": v(24.2, 38.68) * mm});
            skLineSegment(sketch, "E4685", {"start": v(24.2, 38.68) * mm, "end": v(24.1, 38.62) * mm});
            skLineSegment(sketch, "E4686", {"start": v(24.1, 38.62) * mm, "end": v(24, 38.55) * mm});
            skLineSegment(sketch, "E4687", {"start": v(24, 38.55) * mm, "end": v(23.9, 38.48) * mm});
            skLineSegment(sketch, "E4688", {"start": v(23.9, 38.48) * mm, "end": v(23.8, 38.4) * mm});
            skLineSegment(sketch, "E4689", {"start": v(23.8, 38.4) * mm, "end": v(23.71, 38.33) * mm});
            skLineSegment(sketch, "E4690", {"start": v(23.71, 38.33) * mm, "end": v(23.62, 38.26) * mm});
            skLineSegment(sketch, "E4691", {"start": v(23.62, 38.26) * mm, "end": v(23.52, 38.18) * mm});
            skLineSegment(sketch, "E4692", {"start": v(23.52, 38.18) * mm, "end": v(23.42, 38.1) * mm});
            skLineSegment(sketch, "E4693", {"start": v(23.42, 38.1) * mm, "end": v(23.33, 38.03) * mm});
            skLineSegment(sketch, "E4694", {"start": v(23.33, 38.03) * mm, "end": v(23.24, 37.96) * mm});
            skLineSegment(sketch, "E4695", {"start": v(23.24, 37.96) * mm, "end": v(23.15, 37.88) * mm});
            skLineSegment(sketch, "E4696", {"start": v(23.15, 37.88) * mm, "end": v(23.05, 37.8) * mm});
            skLineSegment(sketch, "E4697", {"start": v(23.05, 37.8) * mm, "end": v(22.96, 37.73) * mm});
            skLineSegment(sketch, "E4698", {"start": v(22.96, 37.73) * mm, "end": v(22.87, 37.65) * mm});
            skLineSegment(sketch, "E4699", {"start": v(22.87, 37.65) * mm, "end": v(22.78, 37.57) * mm});
            skLineSegment(sketch, "E4700", {"start": v(22.78, 37.57) * mm, "end": v(22.69, 37.48) * mm});
            skLineSegment(sketch, "E4701", {"start": v(22.69, 37.48) * mm, "end": v(22.59, 37.54) * mm});
            skLineSegment(sketch, "E4702", {"start": v(22.59, 37.54) * mm, "end": v(22.49, 37.6) * mm});
            skLineSegment(sketch, "E4703", {"start": v(22.49, 37.6) * mm, "end": v(22.38, 37.66) * mm});
            skLineSegment(sketch, "E4704", {"start": v(22.38, 37.66) * mm, "end": v(22.28, 37.72) * mm});
            skLineSegment(sketch, "E4705", {"start": v(22.28, 37.72) * mm, "end": v(22.18, 37.78) * mm});
            skLineSegment(sketch, "E4706", {"start": v(22.18, 37.78) * mm, "end": v(22.08, 37.84) * mm});
            skLineSegment(sketch, "E4707", {"start": v(22.08, 37.84) * mm, "end": v(21.98, 37.9) * mm});
            skLineSegment(sketch, "E4708", {"start": v(21.98, 37.9) * mm, "end": v(21.96, 37.91) * mm});
            skLineSegment(sketch, "E4709", {"start": v(21.96, 37.91) * mm, "end": v(21.99, 38.02) * mm});
            skLineSegment(sketch, "E4710", {"start": v(21.99, 38.02) * mm, "end": v(22.01, 38.13) * mm});
            skLineSegment(sketch, "E4711", {"start": v(22.01, 38.13) * mm, "end": v(22.04, 38.24) * mm});
            skLineSegment(sketch, "E4712", {"start": v(22.04, 38.24) * mm, "end": v(22.06, 38.36) * mm});
            skLineSegment(sketch, "E4713", {"start": v(22.06, 38.36) * mm, "end": v(22.09, 38.48) * mm});
            skLineSegment(sketch, "E4714", {"start": v(22.09, 38.48) * mm, "end": v(22.11, 38.6) * mm});
            skLineSegment(sketch, "E4715", {"start": v(22.11, 38.6) * mm, "end": v(22.13, 38.72) * mm});
            skLineSegment(sketch, "E4716", {"start": v(22.13, 38.72) * mm, "end": v(22.16, 38.85) * mm});
            skLineSegment(sketch, "E4717", {"start": v(22.16, 38.85) * mm, "end": v(22.18, 38.97) * mm});
            skLineSegment(sketch, "E4718", {"start": v(22.18, 38.97) * mm, "end": v(22.2, 39.1) * mm});
            skLineSegment(sketch, "E4719", {"start": v(22.2, 39.1) * mm, "end": v(22.21, 39.2) * mm});
            skLineSegment(sketch, "E4720", {"start": v(22.21, 39.2) * mm, "end": v(22.23, 39.32) * mm});
            skLineSegment(sketch, "E4721", {"start": v(22.23, 39.32) * mm, "end": v(22.25, 39.43) * mm});
            skLineSegment(sketch, "E4722", {"start": v(22.25, 39.43) * mm, "end": v(22.26, 39.55) * mm});
            skLineSegment(sketch, "E4723", {"start": v(22.26, 39.55) * mm, "end": v(22.28, 39.67) * mm});
            skLineSegment(sketch, "E4724", {"start": v(22.28, 39.67) * mm, "end": v(22.3, 39.79) * mm});
            skLineSegment(sketch, "E4725", {"start": v(22.3, 39.79) * mm, "end": v(22.3, 39.91) * mm});
            skLineSegment(sketch, "E4726", {"start": v(22.3, 39.91) * mm, "end": v(22.32, 40.04) * mm});
            skLineSegment(sketch, "E4727", {"start": v(22.32, 40.04) * mm, "end": v(22.33, 40.16) * mm});
            skLineSegment(sketch, "E4728", {"start": v(22.33, 40.16) * mm, "end": v(22.33, 40.17) * mm});
            skLineSegment(sketch, "E4729", {"start": v(22.33, 40.17) * mm, "end": v(22.23, 40.22) * mm});
            skLineSegment(sketch, "E4730", {"start": v(22.23, 40.22) * mm, "end": v(22.12, 40.28) * mm});
            skLineSegment(sketch, "E4731", {"start": v(22.12, 40.28) * mm, "end": v(22.03, 40.33) * mm});
            skLineSegment(sketch, "E4732", {"start": v(22.03, 40.33) * mm, "end": v(21.92, 40.4) * mm});
            skLineSegment(sketch, "E4733", {"start": v(21.92, 40.4) * mm, "end": v(21.84, 40.44) * mm});
            skLineSegment(sketch, "E4734", {"start": v(21.84, 40.44) * mm, "end": v(21.74, 40.36) * mm});
            skLineSegment(sketch, "E4735", {"start": v(21.74, 40.36) * mm, "end": v(21.65, 40.29) * mm});
            skLineSegment(sketch, "E4736", {"start": v(21.65, 40.29) * mm, "end": v(21.55, 40.21) * mm});
            skLineSegment(sketch, "E4737", {"start": v(21.55, 40.21) * mm, "end": v(21.46, 40.14) * mm});
            skLineSegment(sketch, "E4738", {"start": v(21.46, 40.14) * mm, "end": v(21.37, 40.06) * mm});
            skLineSegment(sketch, "E4739", {"start": v(21.37, 40.06) * mm, "end": v(21.28, 39.99) * mm});
            skLineSegment(sketch, "E4740", {"start": v(21.28, 39.99) * mm, "end": v(21.19, 39.9) * mm});
            skLineSegment(sketch, "E4741", {"start": v(21.19, 39.9) * mm, "end": v(21.1, 39.83) * mm});
            skLineSegment(sketch, "E4742", {"start": v(21.1, 39.83) * mm, "end": v(21, 39.75) * mm});
            skLineSegment(sketch, "E4743", {"start": v(21, 39.75) * mm, "end": v(20.92, 39.67) * mm});
            skLineSegment(sketch, "E4744", {"start": v(20.92, 39.67) * mm, "end": v(20.83, 39.59) * mm});
            skLineSegment(sketch, "E4745", {"start": v(20.83, 39.59) * mm, "end": v(20.74, 39.5) * mm});
            skLineSegment(sketch, "E4746", {"start": v(20.74, 39.5) * mm, "end": v(20.65, 39.43) * mm});
            skLineSegment(sketch, "E4747", {"start": v(20.65, 39.43) * mm, "end": v(20.56, 39.34) * mm});
            skLineSegment(sketch, "E4748", {"start": v(20.56, 39.34) * mm, "end": v(20.48, 39.26) * mm});
            skLineSegment(sketch, "E4749", {"start": v(20.48, 39.26) * mm, "end": v(20.4, 39.18) * mm});
            skLineSegment(sketch, "E4750", {"start": v(20.4, 39.18) * mm, "end": v(20.3, 39.1) * mm});
            skLineSegment(sketch, "E4751", {"start": v(20.3, 39.1) * mm, "end": v(20.22, 39) * mm});
            skLineSegment(sketch, "E4752", {"start": v(20.22, 39) * mm, "end": v(20.13, 38.91) * mm});
            skLineSegment(sketch, "E4753", {"start": v(20.13, 38.91) * mm, "end": v(20.03, 38.97) * mm});
            skLineSegment(sketch, "E4754", {"start": v(20.03, 38.97) * mm, "end": v(19.92, 39.02) * mm});
            skLineSegment(sketch, "E4755", {"start": v(19.92, 39.02) * mm, "end": v(19.82, 39.08) * mm});
            skLineSegment(sketch, "E4756", {"start": v(19.82, 39.08) * mm, "end": v(19.71, 39.13) * mm});
            skLineSegment(sketch, "E4757", {"start": v(19.71, 39.13) * mm, "end": v(19.6, 39.18) * mm});
            skLineSegment(sketch, "E4758", {"start": v(19.6, 39.18) * mm, "end": v(19.5, 39.23) * mm});
            skLineSegment(sketch, "E4759", {"start": v(19.5, 39.23) * mm, "end": v(19.4, 39.29) * mm});
            skLineSegment(sketch, "E4760", {"start": v(19.4, 39.29) * mm, "end": v(19.38, 39.3) * mm});
            skLineSegment(sketch, "E4761", {"start": v(19.38, 39.3) * mm, "end": v(19.4, 39.4) * mm});
            skLineSegment(sketch, "E4762", {"start": v(19.4, 39.4) * mm, "end": v(19.42, 39.51) * mm});
            skLineSegment(sketch, "E4763", {"start": v(19.42, 39.51) * mm, "end": v(19.43, 39.63) * mm});
            skLineSegment(sketch, "E4764", {"start": v(19.43, 39.63) * mm, "end": v(19.45, 39.75) * mm});
            skLineSegment(sketch, "E4765", {"start": v(19.45, 39.75) * mm, "end": v(19.47, 39.87) * mm});
            skLineSegment(sketch, "E4766", {"start": v(19.47, 39.87) * mm, "end": v(19.48, 39.99) * mm});
            skLineSegment(sketch, "E4767", {"start": v(19.48, 39.99) * mm, "end": v(19.5, 40.12) * mm});
            skLineSegment(sketch, "E4768", {"start": v(19.5, 40.12) * mm, "end": v(19.51, 40.25) * mm});
            skLineSegment(sketch, "E4769", {"start": v(19.51, 40.25) * mm, "end": v(19.52, 40.37) * mm});
            skLineSegment(sketch, "E4770", {"start": v(19.52, 40.37) * mm, "end": v(19.54, 40.49) * mm});
            skLineSegment(sketch, "E4771", {"start": v(19.54, 40.49) * mm, "end": v(19.55, 40.6) * mm});
            skLineSegment(sketch, "E4772", {"start": v(19.55, 40.6) * mm, "end": v(19.56, 40.71) * mm});
            skLineSegment(sketch, "E4773", {"start": v(19.56, 40.71) * mm, "end": v(19.56, 40.83) * mm});
            skLineSegment(sketch, "E4774", {"start": v(19.56, 40.83) * mm, "end": v(19.57, 40.95) * mm});
            skLineSegment(sketch, "E4775", {"start": v(19.57, 40.95) * mm, "end": v(19.58, 41.07) * mm});
            skLineSegment(sketch, "E4776", {"start": v(19.58, 41.07) * mm, "end": v(19.58, 41.19) * mm});
            skLineSegment(sketch, "E4777", {"start": v(19.58, 41.19) * mm, "end": v(19.59, 41.31) * mm});
            skLineSegment(sketch, "E4778", {"start": v(19.59, 41.31) * mm, "end": v(19.6, 41.44) * mm});
            skLineSegment(sketch, "E4779", {"start": v(19.6, 41.44) * mm, "end": v(19.6, 41.57) * mm});
            skLineSegment(sketch, "E4780", {"start": v(19.6, 41.57) * mm, "end": v(19.6, 41.57) * mm});
            skLineSegment(sketch, "E4781", {"start": v(19.6, 41.57) * mm, "end": v(19.49, 41.62) * mm});
            skLineSegment(sketch, "E4782", {"start": v(19.49, 41.62) * mm, "end": v(19.38, 41.67) * mm});
            skLineSegment(sketch, "E4783", {"start": v(19.38, 41.67) * mm, "end": v(19.28, 41.71) * mm});
            skLineSegment(sketch, "E4784", {"start": v(19.28, 41.71) * mm, "end": v(19.17, 41.76) * mm});
            skLineSegment(sketch, "E4785", {"start": v(19.17, 41.76) * mm, "end": v(19.09, 41.8) * mm});
            skLineSegment(sketch, "E4786", {"start": v(19.09, 41.8) * mm, "end": v(19, 41.73) * mm});
            skLineSegment(sketch, "E4787", {"start": v(19, 41.73) * mm, "end": v(18.9, 41.64) * mm});
            skLineSegment(sketch, "E4788", {"start": v(18.9, 41.64) * mm, "end": v(18.82, 41.56) * mm});
            skLineSegment(sketch, "E4789", {"start": v(18.82, 41.56) * mm, "end": v(18.74, 41.48) * mm});
            skLineSegment(sketch, "E4790", {"start": v(18.74, 41.48) * mm, "end": v(18.65, 41.4) * mm});
            skLineSegment(sketch, "E4791", {"start": v(18.65, 41.4) * mm, "end": v(18.56, 41.32) * mm});
            skLineSegment(sketch, "E4792", {"start": v(18.56, 41.32) * mm, "end": v(18.48, 41.24) * mm});
            skLineSegment(sketch, "E4793", {"start": v(18.48, 41.24) * mm, "end": v(18.4, 41.15) * mm});
            skLineSegment(sketch, "E4794", {"start": v(18.4, 41.15) * mm, "end": v(18.3, 41.07) * mm});
            skLineSegment(sketch, "E4795", {"start": v(18.3, 41.07) * mm, "end": v(18.22, 40.98) * mm});
            skLineSegment(sketch, "E4796", {"start": v(18.22, 40.98) * mm, "end": v(18.14, 40.9) * mm});
            skLineSegment(sketch, "E4797", {"start": v(18.14, 40.9) * mm, "end": v(18.05, 40.8) * mm});
            skLineSegment(sketch, "E4798", {"start": v(18.05, 40.8) * mm, "end": v(17.97, 40.72) * mm});
            skLineSegment(sketch, "E4799", {"start": v(17.97, 40.72) * mm, "end": v(17.9, 40.63) * mm});
            skLineSegment(sketch, "E4800", {"start": v(17.9, 40.63) * mm, "end": v(17.81, 40.54) * mm});
            skLineSegment(sketch, "E4801", {"start": v(17.81, 40.54) * mm, "end": v(17.73, 40.45) * mm});
            skLineSegment(sketch, "E4802", {"start": v(17.73, 40.45) * mm, "end": v(17.65, 40.36) * mm});
            skLineSegment(sketch, "E4803", {"start": v(17.65, 40.36) * mm, "end": v(17.57, 40.27) * mm});
            skLineSegment(sketch, "E4804", {"start": v(17.57, 40.27) * mm, "end": v(17.5, 40.17) * mm});
            skLineSegment(sketch, "E4805", {"start": v(17.5, 40.17) * mm, "end": v(17.38, 40.22) * mm});
            skLineSegment(sketch, "E4806", {"start": v(17.38, 40.22) * mm, "end": v(17.27, 40.26) * mm});
            skLineSegment(sketch, "E4807", {"start": v(17.27, 40.26) * mm, "end": v(17.16, 40.31) * mm});
            skLineSegment(sketch, "E4808", {"start": v(17.16, 40.31) * mm, "end": v(17.06, 40.36) * mm});
            skLineSegment(sketch, "E4809", {"start": v(17.06, 40.36) * mm, "end": v(16.95, 40.4) * mm});
            skLineSegment(sketch, "E4810", {"start": v(16.95, 40.4) * mm, "end": v(16.84, 40.45) * mm});
            skLineSegment(sketch, "E4811", {"start": v(16.84, 40.45) * mm, "end": v(16.73, 40.5) * mm});
            skLineSegment(sketch, "E4812", {"start": v(16.73, 40.5) * mm, "end": v(16.71, 40.5) * mm});
            skLineSegment(sketch, "E4813", {"start": v(16.71, 40.5) * mm, "end": v(16.72, 40.61) * mm});
            skLineSegment(sketch, "E4814", {"start": v(16.72, 40.61) * mm, "end": v(16.73, 40.72) * mm});
            skLineSegment(sketch, "E4815", {"start": v(16.73, 40.72) * mm, "end": v(16.74, 40.84) * mm});
            skLineSegment(sketch, "E4816", {"start": v(16.74, 40.84) * mm, "end": v(16.75, 40.96) * mm});
            skLineSegment(sketch, "E4817", {"start": v(16.75, 40.96) * mm, "end": v(16.76, 41.08) * mm});
            skLineSegment(sketch, "E4818", {"start": v(16.76, 41.08) * mm, "end": v(16.77, 41.2) * mm});
            skLineSegment(sketch, "E4819", {"start": v(16.77, 41.2) * mm, "end": v(16.78, 41.33) * mm});
            skLineSegment(sketch, "E4820", {"start": v(16.78, 41.33) * mm, "end": v(16.78, 41.46) * mm});
            skLineSegment(sketch, "E4821", {"start": v(16.78, 41.46) * mm, "end": v(16.79, 41.58) * mm});
            skLineSegment(sketch, "E4822", {"start": v(16.79, 41.58) * mm, "end": v(16.79, 41.7) * mm});
            skLineSegment(sketch, "E4823", {"start": v(16.79, 41.7) * mm, "end": v(16.8, 41.82) * mm});
            skLineSegment(sketch, "E4824", {"start": v(16.8, 41.82) * mm, "end": v(16.8, 41.93) * mm});
            skLineSegment(sketch, "E4825", {"start": v(16.8, 41.93) * mm, "end": v(16.8, 42.04) * mm});
            skLineSegment(sketch, "E4826", {"start": v(16.8, 42.04) * mm, "end": v(16.8, 42.16) * mm});
            skLineSegment(sketch, "E4827", {"start": v(16.8, 42.16) * mm, "end": v(16.8, 42.28) * mm});
            skLineSegment(sketch, "E4828", {"start": v(16.8, 42.28) * mm, "end": v(16.79, 42.4) * mm});
            skLineSegment(sketch, "E4829", {"start": v(16.79, 42.4) * mm, "end": v(16.79, 42.53) * mm});
            skLineSegment(sketch, "E4830", {"start": v(16.79, 42.53) * mm, "end": v(16.78, 42.65) * mm});
            skLineSegment(sketch, "E4831", {"start": v(16.78, 42.65) * mm, "end": v(16.78, 42.78) * mm});
            skLineSegment(sketch, "E4832", {"start": v(16.78, 42.78) * mm, "end": v(16.78, 42.78) * mm});
            skLineSegment(sketch, "E4833", {"start": v(16.78, 42.78) * mm, "end": v(16.67, 42.83) * mm});
            skLineSegment(sketch, "E4834", {"start": v(16.67, 42.83) * mm, "end": v(16.56, 42.87) * mm});
            skLineSegment(sketch, "E4835", {"start": v(16.56, 42.87) * mm, "end": v(16.45, 42.9) * mm});
            skLineSegment(sketch, "E4836", {"start": v(16.45, 42.9) * mm, "end": v(16.34, 42.95) * mm});
            skLineSegment(sketch, "E4837", {"start": v(16.34, 42.95) * mm, "end": v(16.25, 42.99) * mm});
            skLineSegment(sketch, "E4838", {"start": v(16.25, 42.99) * mm, "end": v(16.17, 42.9) * mm});
            skLineSegment(sketch, "E4839", {"start": v(16.17, 42.9) * mm, "end": v(16.08, 42.81) * mm});
            skLineSegment(sketch, "E4840", {"start": v(16.08, 42.81) * mm, "end": v(16, 42.73) * mm});
            skLineSegment(sketch, "E4841", {"start": v(16, 42.73) * mm, "end": v(15.92, 42.64) * mm});
            skLineSegment(sketch, "E4842", {"start": v(15.92, 42.64) * mm, "end": v(15.84, 42.56) * mm});
            skLineSegment(sketch, "E4843", {"start": v(15.84, 42.56) * mm, "end": v(15.76, 42.47) * mm});
            skLineSegment(sketch, "E4844", {"start": v(15.76, 42.47) * mm, "end": v(15.68, 42.38) * mm});
            skLineSegment(sketch, "E4845", {"start": v(15.68, 42.38) * mm, "end": v(15.6, 42.29) * mm});
            skLineSegment(sketch, "E4846", {"start": v(15.6, 42.29) * mm, "end": v(15.52, 42.2) * mm});
            skLineSegment(sketch, "E4847", {"start": v(15.52, 42.2) * mm, "end": v(15.44, 42.1) * mm});
            skLineSegment(sketch, "E4848", {"start": v(15.44, 42.1) * mm, "end": v(15.36, 42.01) * mm});
            skLineSegment(sketch, "E4849", {"start": v(15.36, 42.01) * mm, "end": v(15.29, 41.92) * mm});
            skLineSegment(sketch, "E4850", {"start": v(15.29, 41.92) * mm, "end": v(15.21, 41.83) * mm});
            skLineSegment(sketch, "E4851", {"start": v(15.21, 41.83) * mm, "end": v(15.14, 41.73) * mm});
            skLineSegment(sketch, "E4852", {"start": v(15.14, 41.73) * mm, "end": v(15.06, 41.64) * mm});
            skLineSegment(sketch, "E4853", {"start": v(15.06, 41.64) * mm, "end": v(14.99, 41.55) * mm});
            skLineSegment(sketch, "E4854", {"start": v(14.99, 41.55) * mm, "end": v(14.92, 41.45) * mm});
            skLineSegment(sketch, "E4855", {"start": v(14.92, 41.45) * mm, "end": v(14.85, 41.35) * mm});
            skLineSegment(sketch, "E4856", {"start": v(14.85, 41.35) * mm, "end": v(14.77, 41.25) * mm});
            skLineSegment(sketch, "E4857", {"start": v(14.77, 41.25) * mm, "end": v(14.66, 41.29) * mm});
            skLineSegment(sketch, "E4858", {"start": v(14.66, 41.29) * mm, "end": v(14.55, 41.33) * mm});
            skLineSegment(sketch, "E4859", {"start": v(14.55, 41.33) * mm, "end": v(14.43, 41.37) * mm});
            skLineSegment(sketch, "E4860", {"start": v(14.43, 41.37) * mm, "end": v(14.32, 41.4) * mm});
            skLineSegment(sketch, "E4861", {"start": v(14.32, 41.4) * mm, "end": v(14.2, 41.45) * mm});
            skLineSegment(sketch, "E4862", {"start": v(14.2, 41.45) * mm, "end": v(14.1, 41.48) * mm});
            skLineSegment(sketch, "E4863", {"start": v(14.1, 41.48) * mm, "end": v(13.99, 41.52) * mm});
            skLineSegment(sketch, "E4864", {"start": v(13.99, 41.52) * mm, "end": v(13.97, 41.53) * mm});
            skLineSegment(sketch, "E4865", {"start": v(13.97, 41.53) * mm, "end": v(13.97, 41.64) * mm});
            skLineSegment(sketch, "E4866", {"start": v(13.97, 41.64) * mm, "end": v(13.98, 41.75) * mm});
            skLineSegment(sketch, "E4867", {"start": v(13.98, 41.75) * mm, "end": v(13.98, 41.87) * mm});
            skLineSegment(sketch, "E4868", {"start": v(13.98, 41.87) * mm, "end": v(13.98, 41.98) * mm});
            skLineSegment(sketch, "E4869", {"start": v(13.98, 41.98) * mm, "end": v(13.98, 42.1) * mm});
            skLineSegment(sketch, "E4870", {"start": v(13.98, 42.1) * mm, "end": v(13.98, 42.23) * mm});
            skLineSegment(sketch, "E4871", {"start": v(13.98, 42.23) * mm, "end": v(13.98, 42.36) * mm});
            skLineSegment(sketch, "E4872", {"start": v(13.98, 42.36) * mm, "end": v(13.98, 42.49) * mm});
            skLineSegment(sketch, "E4873", {"start": v(13.98, 42.49) * mm, "end": v(13.97, 42.6) * mm});
            skLineSegment(sketch, "E4874", {"start": v(13.97, 42.6) * mm, "end": v(13.97, 42.73) * mm});
            skLineSegment(sketch, "E4875", {"start": v(13.97, 42.73) * mm, "end": v(13.96, 42.84) * mm});
            skLineSegment(sketch, "E4876", {"start": v(13.96, 42.84) * mm, "end": v(13.95, 42.96) * mm});
            skLineSegment(sketch, "E4877", {"start": v(13.95, 42.96) * mm, "end": v(13.95, 43.07) * mm});
            skLineSegment(sketch, "E4878", {"start": v(13.95, 43.07) * mm, "end": v(13.94, 43.2) * mm});
            skLineSegment(sketch, "E4879", {"start": v(13.94, 43.2) * mm, "end": v(13.93, 43.3) * mm});
            skLineSegment(sketch, "E4880", {"start": v(13.93, 43.3) * mm, "end": v(13.92, 43.43) * mm});
            skLineSegment(sketch, "E4881", {"start": v(13.92, 43.43) * mm, "end": v(13.9, 43.55) * mm});
            skLineSegment(sketch, "E4882", {"start": v(13.9, 43.55) * mm, "end": v(13.9, 43.68) * mm});
            skLineSegment(sketch, "E4883", {"start": v(13.9, 43.68) * mm, "end": v(13.88, 43.8) * mm});
            skLineSegment(sketch, "E4884", {"start": v(13.88, 43.8) * mm, "end": v(13.88, 43.8) * mm});
            skLineSegment(sketch, "E4885", {"start": v(13.88, 43.8) * mm, "end": v(13.77, 43.85) * mm});
            skLineSegment(sketch, "E4886", {"start": v(13.77, 43.85) * mm, "end": v(13.65, 43.88) * mm});
            skLineSegment(sketch, "E4887", {"start": v(13.65, 43.88) * mm, "end": v(13.55, 43.91) * mm});
            skLineSegment(sketch, "E4888", {"start": v(13.55, 43.91) * mm, "end": v(13.44, 43.95) * mm});
            skLineSegment(sketch, "E4889", {"start": v(13.44, 43.95) * mm, "end": v(13.34, 43.98) * mm});
            skLineSegment(sketch, "E4890", {"start": v(13.34, 43.98) * mm, "end": v(13.27, 43.89) * mm});
            skLineSegment(sketch, "E4891", {"start": v(13.27, 43.89) * mm, "end": v(13.19, 43.8) * mm});
            skLineSegment(sketch, "E4892", {"start": v(13.19, 43.8) * mm, "end": v(13.11, 43.7) * mm});
            skLineSegment(sketch, "E4893", {"start": v(13.11, 43.7) * mm, "end": v(13.04, 43.61) * mm});
            skLineSegment(sketch, "E4894", {"start": v(13.04, 43.61) * mm, "end": v(12.96, 43.52) * mm});
            skLineSegment(sketch, "E4895", {"start": v(12.96, 43.52) * mm, "end": v(12.9, 43.43) * mm});
            skLineSegment(sketch, "E4896", {"start": v(12.9, 43.43) * mm, "end": v(12.82, 43.33) * mm});
            skLineSegment(sketch, "E4897", {"start": v(12.82, 43.33) * mm, "end": v(12.74, 43.24) * mm});
            skLineSegment(sketch, "E4898", {"start": v(12.74, 43.24) * mm, "end": v(12.67, 43.14) * mm});
            skLineSegment(sketch, "E4899", {"start": v(12.67, 43.14) * mm, "end": v(12.6, 43.04) * mm});
            skLineSegment(sketch, "E4900", {"start": v(12.6, 43.04) * mm, "end": v(12.52, 42.94) * mm});
            skLineSegment(sketch, "E4901", {"start": v(12.52, 42.94) * mm, "end": v(12.45, 42.85) * mm});
            skLineSegment(sketch, "E4902", {"start": v(12.45, 42.85) * mm, "end": v(12.38, 42.75) * mm});
            skLineSegment(sketch, "E4903", {"start": v(12.38, 42.75) * mm, "end": v(12.32, 42.65) * mm});
            skLineSegment(sketch, "E4904", {"start": v(12.32, 42.65) * mm, "end": v(12.25, 42.55) * mm});
            skLineSegment(sketch, "E4905", {"start": v(12.25, 42.55) * mm, "end": v(12.18, 42.45) * mm});
            skLineSegment(sketch, "E4906", {"start": v(12.18, 42.45) * mm, "end": v(12.12, 42.35) * mm});
            skLineSegment(sketch, "E4907", {"start": v(12.12, 42.35) * mm, "end": v(12.05, 42.25) * mm});
            skLineSegment(sketch, "E4908", {"start": v(12.05, 42.25) * mm, "end": v(11.98, 42.14) * mm});
            skLineSegment(sketch, "E4909", {"start": v(11.98, 42.14) * mm, "end": v(11.87, 42.18) * mm});
            skLineSegment(sketch, "E4910", {"start": v(11.87, 42.18) * mm, "end": v(11.75, 42.2) * mm});
            skLineSegment(sketch, "E4911", {"start": v(11.75, 42.2) * mm, "end": v(11.64, 42.24) * mm});
            skLineSegment(sketch, "E4912", {"start": v(11.64, 42.24) * mm, "end": v(11.52, 42.27) * mm});
            skLineSegment(sketch, "E4913", {"start": v(11.52, 42.27) * mm, "end": v(11.4, 42.3) * mm});
            skLineSegment(sketch, "E4914", {"start": v(11.4, 42.3) * mm, "end": v(11.3, 42.33) * mm});
            skLineSegment(sketch, "E4915", {"start": v(11.3, 42.33) * mm, "end": v(11.18, 42.37) * mm});
            skLineSegment(sketch, "E4916", {"start": v(11.18, 42.37) * mm, "end": v(11.17, 42.37) * mm});
            skLineSegment(sketch, "E4917", {"start": v(11.17, 42.37) * mm, "end": v(11.16, 42.48) * mm});
            skLineSegment(sketch, "E4918", {"start": v(11.16, 42.48) * mm, "end": v(11.16, 42.6) * mm});
            skLineSegment(sketch, "E4919", {"start": v(11.16, 42.6) * mm, "end": v(11.15, 42.7) * mm});
            skLineSegment(sketch, "E4920", {"start": v(11.15, 42.7) * mm, "end": v(11.15, 42.82) * mm});
            skLineSegment(sketch, "E4921", {"start": v(11.15, 42.82) * mm, "end": v(11.14, 42.94) * mm});
            skLineSegment(sketch, "E4922", {"start": v(11.14, 42.94) * mm, "end": v(11.13, 43.07) * mm});
            skLineSegment(sketch, "E4923", {"start": v(11.13, 43.07) * mm, "end": v(11.12, 43.2) * mm});
            skLineSegment(sketch, "E4924", {"start": v(11.12, 43.2) * mm, "end": v(11.1, 43.33) * mm});
            skLineSegment(sketch, "E4925", {"start": v(11.1, 43.33) * mm, "end": v(11.1, 43.45) * mm});
            skLineSegment(sketch, "E4926", {"start": v(11.1, 43.45) * mm, "end": v(11.08, 43.57) * mm});
            skLineSegment(sketch, "E4927", {"start": v(11.08, 43.57) * mm, "end": v(11.07, 43.68) * mm});
            skLineSegment(sketch, "E4928", {"start": v(11.07, 43.68) * mm, "end": v(11.05, 43.8) * mm});
            skLineSegment(sketch, "E4929", {"start": v(11.05, 43.8) * mm, "end": v(11.04, 43.9) * mm});
            skLineSegment(sketch, "E4930", {"start": v(11.04, 43.9) * mm, "end": v(11.02, 44.02) * mm});
            skLineSegment(sketch, "E4931", {"start": v(11.02, 44.02) * mm, "end": v(11, 44.14) * mm});
            skLineSegment(sketch, "E4932", {"start": v(11, 44.14) * mm, "end": v(10.99, 44.26) * mm});
            skLineSegment(sketch, "E4933", {"start": v(10.99, 44.26) * mm, "end": v(10.97, 44.39) * mm});
            skLineSegment(sketch, "E4934", {"start": v(10.97, 44.39) * mm, "end": v(10.95, 44.51) * mm});
            skLineSegment(sketch, "E4935", {"start": v(10.95, 44.51) * mm, "end": v(10.93, 44.64) * mm});
            skLineSegment(sketch, "E4936", {"start": v(10.93, 44.64) * mm, "end": v(10.93, 44.64) * mm});
            skLineSegment(sketch, "E4937", {"start": v(10.93, 44.64) * mm, "end": v(10.8, 44.67) * mm});
            skLineSegment(sketch, "E4938", {"start": v(10.8, 44.67) * mm, "end": v(10.7, 44.7) * mm});
            skLineSegment(sketch, "E4939", {"start": v(10.7, 44.7) * mm, "end": v(10.59, 44.72) * mm});
            skLineSegment(sketch, "E4940", {"start": v(10.59, 44.72) * mm, "end": v(10.47, 44.75) * mm});
            skLineSegment(sketch, "E4941", {"start": v(10.47, 44.75) * mm, "end": v(10.38, 44.77) * mm});
            skLineSegment(sketch, "E4942", {"start": v(10.38, 44.77) * mm, "end": v(10.3, 44.67) * mm});
            skLineSegment(sketch, "E4943", {"start": v(10.3, 44.67) * mm, "end": v(10.23, 44.57) * mm});
            skLineSegment(sketch, "E4944", {"start": v(10.23, 44.57) * mm, "end": v(10.16, 44.48) * mm});
            skLineSegment(sketch, "E4945", {"start": v(10.16, 44.48) * mm, "end": v(10.1, 44.39) * mm});
            skLineSegment(sketch, "E4946", {"start": v(10.1, 44.39) * mm, "end": v(10.03, 44.29) * mm});
            skLineSegment(sketch, "E4947", {"start": v(10.03, 44.29) * mm, "end": v(9.96, 44.19) * mm});
            skLineSegment(sketch, "E4948", {"start": v(9.96, 44.19) * mm, "end": v(9.9, 44.1) * mm});
            skLineSegment(sketch, "E4949", {"start": v(9.9, 44.1) * mm, "end": v(9.83, 44) * mm});
            skLineSegment(sketch, "E4950", {"start": v(9.83, 44) * mm, "end": v(9.76, 43.9) * mm});
            skLineSegment(sketch, "E4951", {"start": v(9.76, 43.9) * mm, "end": v(9.7, 43.79) * mm});
            skLineSegment(sketch, "E4952", {"start": v(9.7, 43.79) * mm, "end": v(9.63, 43.68) * mm});
            skLineSegment(sketch, "E4953", {"start": v(9.63, 43.68) * mm, "end": v(9.56, 43.58) * mm});
            skLineSegment(sketch, "E4954", {"start": v(9.56, 43.58) * mm, "end": v(9.5, 43.48) * mm});
            skLineSegment(sketch, "E4955", {"start": v(9.5, 43.48) * mm, "end": v(9.44, 43.38) * mm});
            skLineSegment(sketch, "E4956", {"start": v(9.44, 43.38) * mm, "end": v(9.38, 43.28) * mm});
            skLineSegment(sketch, "E4957", {"start": v(9.38, 43.28) * mm, "end": v(9.32, 43.17) * mm});
            skLineSegment(sketch, "E4958", {"start": v(9.32, 43.17) * mm, "end": v(9.26, 43.07) * mm});
            skLineSegment(sketch, "E4959", {"start": v(9.26, 43.07) * mm, "end": v(9.2, 42.96) * mm});
            skLineSegment(sketch, "E4960", {"start": v(9.2, 42.96) * mm, "end": v(9.14, 42.85) * mm});
            skLineSegment(sketch, "E4961", {"start": v(9.14, 42.85) * mm, "end": v(9.02, 42.87) * mm});
            skLineSegment(sketch, "E4962", {"start": v(9.02, 42.87) * mm, "end": v(8.9, 42.9) * mm});
            skLineSegment(sketch, "E4963", {"start": v(8.9, 42.9) * mm, "end": v(8.8, 42.92) * mm});
            skLineSegment(sketch, "E4964", {"start": v(8.8, 42.92) * mm, "end": v(8.68, 42.95) * mm});
            skLineSegment(sketch, "E4965", {"start": v(8.68, 42.95) * mm, "end": v(8.56, 42.97) * mm});
            skLineSegment(sketch, "E4966", {"start": v(8.56, 42.97) * mm, "end": v(8.44, 43) * mm});
            skLineSegment(sketch, "E4967", {"start": v(8.44, 43) * mm, "end": v(8.33, 43.02) * mm});
            skLineSegment(sketch, "E4968", {"start": v(8.33, 43.02) * mm, "end": v(8.31, 43.02) * mm});
            skLineSegment(sketch, "E4969", {"start": v(8.31, 43.02) * mm, "end": v(8.3, 43.13) * mm});
            skLineSegment(sketch, "E4970", {"start": v(8.3, 43.13) * mm, "end": v(8.29, 43.24) * mm});
            skLineSegment(sketch, "E4971", {"start": v(8.29, 43.24) * mm, "end": v(8.28, 43.35) * mm});
            skLineSegment(sketch, "E4972", {"start": v(8.28, 43.35) * mm, "end": v(8.26, 43.47) * mm});
            skLineSegment(sketch, "E4973", {"start": v(8.26, 43.47) * mm, "end": v(8.24, 43.6) * mm});
            skLineSegment(sketch, "E4974", {"start": v(8.24, 43.6) * mm, "end": v(8.23, 43.72) * mm});
            skLineSegment(sketch, "E4975", {"start": v(8.23, 43.72) * mm, "end": v(8.2, 43.84) * mm});
            skLineSegment(sketch, "E4976", {"start": v(8.2, 43.84) * mm, "end": v(8.19, 43.97) * mm});
            skLineSegment(sketch, "E4977", {"start": v(8.19, 43.97) * mm, "end": v(8.17, 44.09) * mm});
            skLineSegment(sketch, "E4978", {"start": v(8.17, 44.09) * mm, "end": v(8.15, 44.21) * mm});
            skLineSegment(sketch, "E4979", {"start": v(8.15, 44.21) * mm, "end": v(8.13, 44.32) * mm});
            skLineSegment(sketch, "E4980", {"start": v(8.13, 44.32) * mm, "end": v(8.1, 44.43) * mm});
            skLineSegment(sketch, "E4981", {"start": v(8.1, 44.43) * mm, "end": v(8.08, 44.55) * mm});
            skLineSegment(sketch, "E4982", {"start": v(8.08, 44.55) * mm, "end": v(8.06, 44.66) * mm});
            skLineSegment(sketch, "E4983", {"start": v(8.06, 44.66) * mm, "end": v(8.03, 44.78) * mm});
            skLineSegment(sketch, "E4984", {"start": v(8.03, 44.78) * mm, "end": v(8, 44.9) * mm});
            skLineSegment(sketch, "E4985", {"start": v(8, 44.9) * mm, "end": v(7.98, 45.02) * mm});
            skLineSegment(sketch, "E4986", {"start": v(7.98, 45.02) * mm, "end": v(7.95, 45.14) * mm});
            skLineSegment(sketch, "E4987", {"start": v(7.95, 45.14) * mm, "end": v(7.92, 45.27) * mm});
            skLineSegment(sketch, "E4988", {"start": v(7.92, 45.27) * mm, "end": v(7.92, 45.27) * mm});
            skLineSegment(sketch, "E4989", {"start": v(7.92, 45.27) * mm, "end": v(7.8, 45.29) * mm});
            skLineSegment(sketch, "E4990", {"start": v(7.8, 45.29) * mm, "end": v(7.68, 45.3) * mm});
            skLineSegment(sketch, "E4991", {"start": v(7.68, 45.3) * mm, "end": v(7.58, 45.33) * mm});
            skLineSegment(sketch, "E4992", {"start": v(7.58, 45.33) * mm, "end": v(7.46, 45.35) * mm});
            skLineSegment(sketch, "E4993", {"start": v(7.46, 45.35) * mm, "end": v(7.36, 45.36) * mm});
            skLineSegment(sketch, "E4994", {"start": v(7.36, 45.36) * mm, "end": v(7.3, 45.26) * mm});
            skLineSegment(sketch, "E4995", {"start": v(7.3, 45.26) * mm, "end": v(7.23, 45.16) * mm});
            skLineSegment(sketch, "E4996", {"start": v(7.23, 45.16) * mm, "end": v(7.17, 45.06) * mm});
            skLineSegment(sketch, "E4997", {"start": v(7.17, 45.06) * mm, "end": v(7.11, 44.96) * mm});
            skLineSegment(sketch, "E4998", {"start": v(7.11, 44.96) * mm, "end": v(7.05, 44.86) * mm});
            skLineSegment(sketch, "E4999", {"start": v(7.05, 44.86) * mm, "end": v(6.99, 44.76) * mm});
            skLineSegment(sketch, "E5000", {"start": v(6.99, 44.76) * mm, "end": v(6.93, 44.65) * mm});
            skLineSegment(sketch, "E5001", {"start": v(6.93, 44.65) * mm, "end": v(6.87, 44.55) * mm});
            skLineSegment(sketch, "E5002", {"start": v(6.87, 44.55) * mm, "end": v(6.8, 44.45) * mm});
            skLineSegment(sketch, "E5003", {"start": v(6.8, 44.45) * mm, "end": v(6.75, 44.34) * mm});
            skLineSegment(sketch, "E5004", {"start": v(6.75, 44.34) * mm, "end": v(6.69, 44.23) * mm});
            skLineSegment(sketch, "E5005", {"start": v(6.69, 44.23) * mm, "end": v(6.63, 44.12) * mm});
            skLineSegment(sketch, "E5006", {"start": v(6.63, 44.12) * mm, "end": v(6.58, 44.02) * mm});
            skLineSegment(sketch, "E5007", {"start": v(6.58, 44.02) * mm, "end": v(6.52, 43.91) * mm});
            skLineSegment(sketch, "E5008", {"start": v(6.52, 43.91) * mm, "end": v(6.47, 43.8) * mm});
            skLineSegment(sketch, "E5009", {"start": v(6.47, 43.8) * mm, "end": v(6.41, 43.7) * mm});
            skLineSegment(sketch, "E5010", {"start": v(6.41, 43.7) * mm, "end": v(6.36, 43.6) * mm});
            skLineSegment(sketch, "E5011", {"start": v(6.36, 43.6) * mm, "end": v(6.31, 43.48) * mm});
            skLineSegment(sketch, "E5012", {"start": v(6.31, 43.48) * mm, "end": v(6.26, 43.36) * mm});
            skLineSegment(sketch, "E5013", {"start": v(6.26, 43.36) * mm, "end": v(6.14, 43.38) * mm});
            skLineSegment(sketch, "E5014", {"start": v(6.14, 43.38) * mm, "end": v(6.02, 43.4) * mm});
            skLineSegment(sketch, "E5015", {"start": v(6.02, 43.4) * mm, "end": v(5.9, 43.41) * mm});
            skLineSegment(sketch, "E5016", {"start": v(5.9, 43.41) * mm, "end": v(5.79, 43.43) * mm});
            skLineSegment(sketch, "E5017", {"start": v(5.79, 43.43) * mm, "end": v(5.67, 43.45) * mm});
            skLineSegment(sketch, "E5018", {"start": v(5.67, 43.45) * mm, "end": v(5.55, 43.46) * mm});
            skLineSegment(sketch, "E5019", {"start": v(5.55, 43.46) * mm, "end": v(5.44, 43.48) * mm});
            skLineSegment(sketch, "E5020", {"start": v(5.44, 43.48) * mm, "end": v(5.42, 43.48) * mm});
            skLineSegment(sketch, "E5021", {"start": v(5.42, 43.48) * mm, "end": v(5.4, 43.59) * mm});
            skLineSegment(sketch, "E5022", {"start": v(5.4, 43.59) * mm, "end": v(5.38, 43.7) * mm});
            skLineSegment(sketch, "E5023", {"start": v(5.38, 43.7) * mm, "end": v(5.36, 43.81) * mm});
            skLineSegment(sketch, "E5024", {"start": v(5.36, 43.81) * mm, "end": v(5.34, 43.93) * mm});
            skLineSegment(sketch, "E5025", {"start": v(5.34, 43.93) * mm, "end": v(5.32, 44.05) * mm});
            skLineSegment(sketch, "E5026", {"start": v(5.32, 44.05) * mm, "end": v(5.29, 44.17) * mm});
            skLineSegment(sketch, "E5027", {"start": v(5.29, 44.17) * mm, "end": v(5.26, 44.3) * mm});
            skLineSegment(sketch, "E5028", {"start": v(5.26, 44.3) * mm, "end": v(5.23, 44.42) * mm});
            skLineSegment(sketch, "E5029", {"start": v(5.23, 44.42) * mm, "end": v(5.2, 44.54) * mm});
            skLineSegment(sketch, "E5030", {"start": v(5.2, 44.54) * mm, "end": v(5.18, 44.66) * mm});
            skLineSegment(sketch, "E5031", {"start": v(5.18, 44.66) * mm, "end": v(5.15, 44.77) * mm});
            skLineSegment(sketch, "E5032", {"start": v(5.15, 44.77) * mm, "end": v(5.12, 44.88) * mm});
            skLineSegment(sketch, "E5033", {"start": v(5.12, 44.88) * mm, "end": v(5.09, 44.99) * mm});
            skLineSegment(sketch, "E5034", {"start": v(5.09, 44.99) * mm, "end": v(5.06, 45.1) * mm});
            skLineSegment(sketch, "E5035", {"start": v(5.06, 45.1) * mm, "end": v(5.02, 45.22) * mm});
            skLineSegment(sketch, "E5036", {"start": v(5.02, 45.22) * mm, "end": v(5, 45.33) * mm});
            skLineSegment(sketch, "E5037", {"start": v(5, 45.33) * mm, "end": v(4.96, 45.45) * mm});
            skLineSegment(sketch, "E5038", {"start": v(4.96, 45.45) * mm, "end": v(4.92, 45.57) * mm});
            skLineSegment(sketch, "E5039", {"start": v(4.92, 45.57) * mm, "end": v(4.88, 45.7) * mm});
            skLineSegment(sketch, "E5040", {"start": v(4.88, 45.7) * mm, "end": v(4.88, 45.7) * mm});
            skLineSegment(sketch, "E5041", {"start": v(4.88, 45.7) * mm, "end": v(4.76, 45.7) * mm});
            skLineSegment(sketch, "E5042", {"start": v(4.76, 45.7) * mm, "end": v(4.64, 45.72) * mm});
            skLineSegment(sketch, "E5043", {"start": v(4.64, 45.72) * mm, "end": v(4.53, 45.73) * mm});
            skLineSegment(sketch, "E5044", {"start": v(4.53, 45.73) * mm, "end": v(4.42, 45.74) * mm});
            skLineSegment(sketch, "E5045", {"start": v(4.42, 45.74) * mm, "end": v(4.32, 45.75) * mm});
            skLineSegment(sketch, "E5046", {"start": v(4.32, 45.75) * mm, "end": v(4.26, 45.65) * mm});
            skLineSegment(sketch, "E5047", {"start": v(4.26, 45.65) * mm, "end": v(4.2, 45.54) * mm});
            skLineSegment(sketch, "E5048", {"start": v(4.2, 45.54) * mm, "end": v(4.15, 45.44) * mm});
            skLineSegment(sketch, "E5049", {"start": v(4.15, 45.44) * mm, "end": v(4.1, 45.34) * mm});
            skLineSegment(sketch, "E5050", {"start": v(4.1, 45.34) * mm, "end": v(4.04, 45.23) * mm});
            skLineSegment(sketch, "E5051", {"start": v(4.04, 45.23) * mm, "end": v(3.98, 45.12) * mm});
            skLineSegment(sketch, "E5052", {"start": v(3.98, 45.12) * mm, "end": v(3.93, 45.02) * mm});
            skLineSegment(sketch, "E5053", {"start": v(3.93, 45.02) * mm, "end": v(3.88, 44.9) * mm});
            skLineSegment(sketch, "E5054", {"start": v(3.88, 44.9) * mm, "end": v(3.82, 44.8) * mm});
            skLineSegment(sketch, "E5055", {"start": v(3.82, 44.8) * mm, "end": v(3.77, 44.69) * mm});
            skLineSegment(sketch, "E5056", {"start": v(3.77, 44.69) * mm, "end": v(3.72, 44.58) * mm});
            skLineSegment(sketch, "E5057", {"start": v(3.72, 44.58) * mm, "end": v(3.67, 44.47) * mm});
            skLineSegment(sketch, "E5058", {"start": v(3.67, 44.47) * mm, "end": v(3.62, 44.36) * mm});
            skLineSegment(sketch, "E5059", {"start": v(3.62, 44.36) * mm, "end": v(3.57, 44.25) * mm});
            skLineSegment(sketch, "E5060", {"start": v(3.57, 44.25) * mm, "end": v(3.53, 44.14) * mm});
            skLineSegment(sketch, "E5061", {"start": v(3.53, 44.14) * mm, "end": v(3.48, 44.03) * mm});
            skLineSegment(sketch, "E5062", {"start": v(3.48, 44.03) * mm, "end": v(3.44, 43.92) * mm});
            skLineSegment(sketch, "E5063", {"start": v(3.44, 43.92) * mm, "end": v(3.4, 43.8) * mm});
            skLineSegment(sketch, "E5064", {"start": v(3.4, 43.8) * mm, "end": v(3.35, 43.69) * mm});
            skLineSegment(sketch, "E5065", {"start": v(3.35, 43.69) * mm, "end": v(3.23, 43.7) * mm});
            skLineSegment(sketch, "E5066", {"start": v(3.23, 43.7) * mm, "end": v(3.11, 43.7) * mm});
            skLineSegment(sketch, "E5067", {"start": v(3.11, 43.7) * mm, "end": v(3, 43.71) * mm});
            skLineSegment(sketch, "E5068", {"start": v(3, 43.71) * mm, "end": v(2.87, 43.72) * mm});
            skLineSegment(sketch, "E5069", {"start": v(2.87, 43.72) * mm, "end": v(2.76, 43.73) * mm});
            skLineSegment(sketch, "E5070", {"start": v(2.76, 43.73) * mm, "end": v(2.64, 43.73) * mm});
            skLineSegment(sketch, "E5071", {"start": v(2.64, 43.73) * mm, "end": v(2.52, 43.74) * mm});
            skLineSegment(sketch, "E5072", {"start": v(2.52, 43.74) * mm, "end": v(2.5, 43.75) * mm});
            skLineSegment(sketch, "E5073", {"start": v(2.5, 43.75) * mm, "end": v(2.48, 43.85) * mm});
            skLineSegment(sketch, "E5074", {"start": v(2.48, 43.85) * mm, "end": v(2.45, 43.96) * mm});
            skLineSegment(sketch, "E5075", {"start": v(2.45, 43.96) * mm, "end": v(2.42, 44.07) * mm});
            skLineSegment(sketch, "E5076", {"start": v(2.42, 44.07) * mm, "end": v(2.4, 44.19) * mm});
            skLineSegment(sketch, "E5077", {"start": v(2.4, 44.19) * mm, "end": v(2.36, 44.3) * mm});
            skLineSegment(sketch, "E5078", {"start": v(2.36, 44.3) * mm, "end": v(2.33, 44.42) * mm});
            skLineSegment(sketch, "E5079", {"start": v(2.33, 44.42) * mm, "end": v(2.3, 44.55) * mm});
            skLineSegment(sketch, "E5080", {"start": v(2.3, 44.55) * mm, "end": v(2.25, 44.67) * mm});
            skLineSegment(sketch, "E5081", {"start": v(2.25, 44.67) * mm, "end": v(2.22, 44.79) * mm});
            skLineSegment(sketch, "E5082", {"start": v(2.22, 44.79) * mm, "end": v(2.18, 44.9) * mm});
            skLineSegment(sketch, "E5083", {"start": v(2.18, 44.9) * mm, "end": v(2.15, 45) * mm});
            skLineSegment(sketch, "E5084", {"start": v(2.15, 45) * mm, "end": v(2.11, 45.12) * mm});
            skLineSegment(sketch, "E5085", {"start": v(2.11, 45.12) * mm, "end": v(2.07, 45.23) * mm});
            skLineSegment(sketch, "E5086", {"start": v(2.07, 45.23) * mm, "end": v(2.03, 45.34) * mm});
            skLineSegment(sketch, "E5087", {"start": v(2.03, 45.34) * mm, "end": v(2, 45.45) * mm});
            skLineSegment(sketch, "E5088", {"start": v(2, 45.45) * mm, "end": v(1.95, 45.57) * mm});
            skLineSegment(sketch, "E5089", {"start": v(1.95, 45.57) * mm, "end": v(1.9, 45.68) * mm});
            skLineSegment(sketch, "E5090", {"start": v(1.9, 45.68) * mm, "end": v(1.86, 45.8) * mm});
            skLineSegment(sketch, "E5091", {"start": v(1.86, 45.8) * mm, "end": v(1.82, 45.92) * mm});
            skLineSegment(sketch, "E5092", {"start": v(1.82, 45.92) * mm, "end": v(1.82, 45.92) * mm});
            skLineSegment(sketch, "E5093", {"start": v(1.82, 45.92) * mm, "end": v(1.7, 45.93) * mm});
            skLineSegment(sketch, "E5094", {"start": v(1.7, 45.93) * mm, "end": v(1.58, 45.93) * mm});
            skLineSegment(sketch, "E5095", {"start": v(1.58, 45.93) * mm, "end": v(1.47, 45.93) * mm});
            skLineSegment(sketch, "E5096", {"start": v(1.47, 45.93) * mm, "end": v(1.35, 45.94) * mm});
            skLineSegment(sketch, "E5097", {"start": v(1.35, 45.94) * mm, "end": v(1.25, 45.94) * mm});
            skLineSegment(sketch, "E5098", {"start": v(1.25, 45.94) * mm, "end": v(1.2, 45.83) * mm});
            skLineSegment(sketch, "E5099", {"start": v(1.2, 45.83) * mm, "end": v(1.15, 45.72) * mm});
            skLineSegment(sketch, "E5100", {"start": v(1.15, 45.72) * mm, "end": v(1.1, 45.61) * mm});
            skLineSegment(sketch, "E5101", {"start": v(1.1, 45.61) * mm, "end": v(1.06, 45.5) * mm});
            skLineSegment(sketch, "E5102", {"start": v(1.06, 45.5) * mm, "end": v(1, 45.4) * mm});
            skLineSegment(sketch, "E5103", {"start": v(1, 45.4) * mm, "end": v(0.96, 45.29) * mm});
            skLineSegment(sketch, "E5104", {"start": v(0.96, 45.29) * mm, "end": v(0.91, 45.18) * mm});
            skLineSegment(sketch, "E5105", {"start": v(0.91, 45.18) * mm, "end": v(0.87, 45.07) * mm});
            skLineSegment(sketch, "E5106", {"start": v(0.87, 45.07) * mm, "end": v(0.82, 44.96) * mm});
            skLineSegment(sketch, "E5107", {"start": v(0.82, 44.96) * mm, "end": v(0.78, 44.84) * mm});
            skLineSegment(sketch, "E5108", {"start": v(0.78, 44.84) * mm, "end": v(0.73, 44.73) * mm});
            skLineSegment(sketch, "E5109", {"start": v(0.73, 44.73) * mm, "end": v(0.7, 44.62) * mm});
            skLineSegment(sketch, "E5110", {"start": v(0.7, 44.62) * mm, "end": v(0.65, 44.5) * mm});
            skLineSegment(sketch, "E5111", {"start": v(0.65, 44.5) * mm, "end": v(0.61, 44.4) * mm});
            skLineSegment(sketch, "E5112", {"start": v(0.61, 44.4) * mm, "end": v(0.57, 44.28) * mm});
            skLineSegment(sketch, "E5113", {"start": v(0.57, 44.28) * mm, "end": v(0.53, 44.16) * mm});
            skLineSegment(sketch, "E5114", {"start": v(0.53, 44.16) * mm, "end": v(0.5, 44.05) * mm});
            skLineSegment(sketch, "E5115", {"start": v(0.5, 44.05) * mm, "end": v(0.46, 43.94) * mm});
            skLineSegment(sketch, "E5116", {"start": v(0.46, 43.94) * mm, "end": v(0.42, 43.81) * mm});
            skLineSegment(sketch, "E5117", {"start": v(0.42, 43.81) * mm, "end": v(0.3, 43.81) * mm});
            skLineSegment(sketch, "E5118", {"start": v(0.3, 43.81) * mm, "end": v(0.18, 43.81) * mm});
            skLineSegment(sketch, "E5119", {"start": v(0.18, 43.81) * mm, "end": v(0.07, 43.81) * mm});
            skLineSegment(sketch, "E5120", {"start": v(0.07, 43.81) * mm, "end": v(0.02, 43.81) * mm});
            skLineSegment(sketch, "E5121", {"start": v(0.02, 43.81) * mm, "end": v(-0.1, 43.81) * mm});
            skLineSegment(sketch, "E5122", {"start": v(-0.1, 43.81) * mm, "end": v(-0.22, 43.81) * mm});
            skLineSegment(sketch, "E5123", {"start": v(-0.22, 43.81) * mm, "end": v(-0.34, 43.81) * mm});
            skLineSegment(sketch, "E5124", {"start": v(-0.34, 43.81) * mm, "end": v(-0.39, 43.81) * mm});
            skLineSegment(sketch, "E5125", {"start": v(-0.39, 43.81) * mm, "end": v(-0.42, 43.82) * mm});
            skLineSegment(sketch, "E5126", {"start": v(-0.42, 43.82) * mm, "end": v(-0.46, 43.92) * mm});
            skLineSegment(sketch, "E5127", {"start": v(-0.46, 43.92) * mm, "end": v(-0.49, 44.03) * mm});
            skLineSegment(sketch, "E5128", {"start": v(-0.49, 44.03) * mm, "end": v(-0.53, 44.13) * mm});
            skLineSegment(sketch, "E5129", {"start": v(-0.53, 44.13) * mm, "end": v(-0.56, 44.25) * mm});
            skLineSegment(sketch, "E5130", {"start": v(-0.56, 44.25) * mm, "end": v(-0.6, 44.36) * mm});
            skLineSegment(sketch, "E5131", {"start": v(-0.6, 44.36) * mm, "end": v(-0.64, 44.48) * mm});
            skLineSegment(sketch, "E5132", {"start": v(-0.64, 44.48) * mm, "end": v(-0.69, 44.6) * mm});
            skLineSegment(sketch, "E5133", {"start": v(-0.69, 44.6) * mm, "end": v(-0.73, 44.72) * mm});
            skLineSegment(sketch, "E5134", {"start": v(-0.73, 44.72) * mm, "end": v(-0.78, 44.83) * mm});
            skLineSegment(sketch, "E5135", {"start": v(-0.78, 44.83) * mm, "end": v(-0.82, 44.95) * mm});
            skLineSegment(sketch, "E5136", {"start": v(-0.82, 44.95) * mm, "end": v(-0.86, 45.05) * mm});
            skLineSegment(sketch, "E5137", {"start": v(-0.86, 45.05) * mm, "end": v(-0.9, 45.16) * mm});
            skLineSegment(sketch, "E5138", {"start": v(-0.9, 45.16) * mm, "end": v(-0.95, 45.26) * mm});
            skLineSegment(sketch, "E5139", {"start": v(-0.95, 45.26) * mm, "end": v(-1, 45.37) * mm});
            skLineSegment(sketch, "E5140", {"start": v(-1, 45.37) * mm, "end": v(-1.05, 45.48) * mm});
            skLineSegment(sketch, "E5141", {"start": v(-1.05, 45.48) * mm, "end": v(-1.1, 45.6) * mm});
            skLineSegment(sketch, "E5142", {"start": v(-1.1, 45.6) * mm, "end": v(-1.15, 45.7) * mm});
            skLineSegment(sketch, "E5143", {"start": v(-1.15, 45.7) * mm, "end": v(-1.2, 45.82) * mm});
            skLineSegment(sketch, "E5144", {"start": v(-1.2, 45.82) * mm, "end": v(-1.25, 45.94) * mm});
            skLineSegment(sketch, "E5145", {"start": v(-1.25, 45.94) * mm, "end": v(-1.25, 45.94) * mm});
            skLineSegment(sketch, "E5146", {"start": v(-1.25, 45.94) * mm, "end": v(-1.37, 45.94) * mm});
            skLineSegment(sketch, "E5147", {"start": v(-1.37, 45.94) * mm, "end": v(-1.5, 45.93) * mm});
            skLineSegment(sketch, "E5148", {"start": v(-1.5, 45.93) * mm, "end": v(-1.6, 45.93) * mm});
            skLineSegment(sketch, "E5149", {"start": v(-1.6, 45.93) * mm, "end": v(-1.72, 45.92) * mm});
            skLineSegment(sketch, "E5150", {"start": v(-1.72, 45.92) * mm, "end": v(-1.82, 45.92) * mm});
            skLineSegment(sketch, "E5151", {"start": v(-1.82, 45.92) * mm, "end": v(-1.86, 45.8) * mm});
            skLineSegment(sketch, "E5152", {"start": v(-1.86, 45.8) * mm, "end": v(-1.9, 45.7) * mm});
            skLineSegment(sketch, "E5153", {"start": v(-1.9, 45.7) * mm, "end": v(-1.95, 45.58) * mm});
            skLineSegment(sketch, "E5154", {"start": v(-1.95, 45.58) * mm, "end": v(-1.99, 45.48) * mm});
            skLineSegment(sketch, "E5155", {"start": v(-1.99, 45.48) * mm, "end": v(-2.03, 45.36) * mm});
            skLineSegment(sketch, "E5156", {"start": v(-2.03, 45.36) * mm, "end": v(-2.07, 45.25) * mm});
            skLineSegment(sketch, "E5157", {"start": v(-2.07, 45.25) * mm, "end": v(-2.1, 45.14) * mm});
            skLineSegment(sketch, "E5158", {"start": v(-2.1, 45.14) * mm, "end": v(-2.14, 45.02) * mm});
            skLineSegment(sketch, "E5159", {"start": v(-2.14, 45.02) * mm, "end": v(-2.18, 44.91) * mm});
            skLineSegment(sketch, "E5160", {"start": v(-2.18, 44.91) * mm, "end": v(-2.22, 44.8) * mm});
            skLineSegment(sketch, "E5161", {"start": v(-2.22, 44.8) * mm, "end": v(-2.25, 44.68) * mm});
            skLineSegment(sketch, "E5162", {"start": v(-2.25, 44.68) * mm, "end": v(-2.29, 44.56) * mm});
            skLineSegment(sketch, "E5163", {"start": v(-2.29, 44.56) * mm, "end": v(-2.32, 44.45) * mm});
            skLineSegment(sketch, "E5164", {"start": v(-2.32, 44.45) * mm, "end": v(-2.35, 44.33) * mm});
            skLineSegment(sketch, "E5165", {"start": v(-2.35, 44.33) * mm, "end": v(-2.39, 44.22) * mm});
            skLineSegment(sketch, "E5166", {"start": v(-2.39, 44.22) * mm, "end": v(-2.42, 44.1) * mm});
            skLineSegment(sketch, "E5167", {"start": v(-2.42, 44.1) * mm, "end": v(-2.45, 43.99) * mm});
            skLineSegment(sketch, "E5168", {"start": v(-2.45, 43.99) * mm, "end": v(-2.48, 43.87) * mm});
            skLineSegment(sketch, "E5169", {"start": v(-2.48, 43.87) * mm, "end": v(-2.5, 43.74) * mm});
            skLineSegment(sketch, "E5170", {"start": v(-2.5, 43.74) * mm, "end": v(-2.62, 43.74) * mm});
            skLineSegment(sketch, "E5171", {"start": v(-2.62, 43.74) * mm, "end": v(-2.74, 43.73) * mm});
            skLineSegment(sketch, "E5172", {"start": v(-2.74, 43.73) * mm, "end": v(-2.86, 43.72) * mm});
            skLineSegment(sketch, "E5173", {"start": v(-2.86, 43.72) * mm, "end": v(-2.98, 43.71) * mm});
            skLineSegment(sketch, "E5174", {"start": v(-2.98, 43.71) * mm, "end": v(-3.1, 43.7) * mm});
            skLineSegment(sketch, "E5175", {"start": v(-3.1, 43.7) * mm, "end": v(-3.21, 43.7) * mm});
            skLineSegment(sketch, "E5176", {"start": v(-3.21, 43.7) * mm, "end": v(-3.31, 43.69) * mm});
            skLineSegment(sketch, "E5177", {"start": v(-3.31, 43.69) * mm, "end": v(-3.35, 43.69) * mm});
            skLineSegment(sketch, "E5178", {"start": v(-3.35, 43.69) * mm, "end": v(-3.39, 43.8) * mm});
            skLineSegment(sketch, "E5179", {"start": v(-3.39, 43.8) * mm, "end": v(-3.43, 43.9) * mm});
            skLineSegment(sketch, "E5180", {"start": v(-3.43, 43.9) * mm, "end": v(-3.47, 44) * mm});
            skLineSegment(sketch, "E5181", {"start": v(-3.47, 44) * mm, "end": v(-3.52, 44.11) * mm});
            skLineSegment(sketch, "E5182", {"start": v(-3.52, 44.11) * mm, "end": v(-3.56, 44.22) * mm});
            skLineSegment(sketch, "E5183", {"start": v(-3.56, 44.22) * mm, "end": v(-3.61, 44.34) * mm});
            skLineSegment(sketch, "E5184", {"start": v(-3.61, 44.34) * mm, "end": v(-3.67, 44.45) * mm});
            skLineSegment(sketch, "E5185", {"start": v(-3.67, 44.45) * mm, "end": v(-3.72, 44.57) * mm});
            skLineSegment(sketch, "E5186", {"start": v(-3.72, 44.57) * mm, "end": v(-3.77, 44.68) * mm});
            skLineSegment(sketch, "E5187", {"start": v(-3.77, 44.68) * mm, "end": v(-3.82, 44.8) * mm});
            skLineSegment(sketch, "E5188", {"start": v(-3.82, 44.8) * mm, "end": v(-3.87, 44.9) * mm});
            skLineSegment(sketch, "E5189", {"start": v(-3.87, 44.9) * mm, "end": v(-3.92, 45) * mm});
            skLineSegment(sketch, "E5190", {"start": v(-3.92, 45) * mm, "end": v(-3.97, 45.1) * mm});
            skLineSegment(sketch, "E5191", {"start": v(-3.97, 45.1) * mm, "end": v(-4.03, 45.2) * mm});
            skLineSegment(sketch, "E5192", {"start": v(-4.03, 45.2) * mm, "end": v(-4.08, 45.31) * mm});
            skLineSegment(sketch, "E5193", {"start": v(-4.08, 45.31) * mm, "end": v(-4.14, 45.42) * mm});
            skLineSegment(sketch, "E5194", {"start": v(-4.14, 45.42) * mm, "end": v(-4.2, 45.53) * mm});
            skLineSegment(sketch, "E5195", {"start": v(-4.2, 45.53) * mm, "end": v(-4.26, 45.64) * mm});
            skLineSegment(sketch, "E5196", {"start": v(-4.26, 45.64) * mm, "end": v(-4.32, 45.75) * mm});
            skLineSegment(sketch, "E5197", {"start": v(-4.32, 45.75) * mm, "end": v(-4.32, 45.75) * mm});
            skLineSegment(sketch, "E5198", {"start": v(-4.32, 45.75) * mm, "end": v(-4.44, 45.74) * mm});
            skLineSegment(sketch, "E5199", {"start": v(-4.44, 45.74) * mm, "end": v(-4.56, 45.73) * mm});
            skLineSegment(sketch, "E5200", {"start": v(-4.56, 45.73) * mm, "end": v(-4.67, 45.72) * mm});
            skLineSegment(sketch, "E5201", {"start": v(-4.67, 45.72) * mm, "end": v(-4.78, 45.7) * mm});
            skLineSegment(sketch, "E5202", {"start": v(-4.78, 45.7) * mm, "end": v(-4.88, 45.7) * mm});
            skLineSegment(sketch, "E5203", {"start": v(-4.88, 45.7) * mm, "end": v(-4.92, 45.58) * mm});
            skLineSegment(sketch, "E5204", {"start": v(-4.92, 45.58) * mm, "end": v(-4.95, 45.47) * mm});
            skLineSegment(sketch, "E5205", {"start": v(-4.95, 45.47) * mm, "end": v(-4.99, 45.35) * mm});
            skLineSegment(sketch, "E5206", {"start": v(-4.99, 45.35) * mm, "end": v(-5.02, 45.24) * mm});
            skLineSegment(sketch, "E5207", {"start": v(-5.02, 45.24) * mm, "end": v(-5.05, 45.13) * mm});
            skLineSegment(sketch, "E5208", {"start": v(-5.05, 45.13) * mm, "end": v(-5.08, 45.01) * mm});
            skLineSegment(sketch, "E5209", {"start": v(-5.08, 45.01) * mm, "end": v(-5.12, 44.9) * mm});
            skLineSegment(sketch, "E5210", {"start": v(-5.12, 44.9) * mm, "end": v(-5.15, 44.78) * mm});
            skLineSegment(sketch, "E5211", {"start": v(-5.15, 44.78) * mm, "end": v(-5.17, 44.67) * mm});
            skLineSegment(sketch, "E5212", {"start": v(-5.17, 44.67) * mm, "end": v(-5.2, 44.54) * mm});
            skLineSegment(sketch, "E5213", {"start": v(-5.2, 44.54) * mm, "end": v(-5.23, 44.43) * mm});
            skLineSegment(sketch, "E5214", {"start": v(-5.23, 44.43) * mm, "end": v(-5.26, 44.3) * mm});
            skLineSegment(sketch, "E5215", {"start": v(-5.26, 44.3) * mm, "end": v(-5.29, 44.2) * mm});
            skLineSegment(sketch, "E5216", {"start": v(-5.29, 44.2) * mm, "end": v(-5.31, 44.08) * mm});
            skLineSegment(sketch, "E5217", {"start": v(-5.31, 44.08) * mm, "end": v(-5.33, 43.96) * mm});
            skLineSegment(sketch, "E5218", {"start": v(-5.33, 43.96) * mm, "end": v(-5.36, 43.84) * mm});
            skLineSegment(sketch, "E5219", {"start": v(-5.36, 43.84) * mm, "end": v(-5.38, 43.72) * mm});
            skLineSegment(sketch, "E5220", {"start": v(-5.38, 43.72) * mm, "end": v(-5.4, 43.6) * mm});
            skLineSegment(sketch, "E5221", {"start": v(-5.4, 43.6) * mm, "end": v(-5.42, 43.48) * mm});
            skLineSegment(sketch, "E5222", {"start": v(-5.42, 43.48) * mm, "end": v(-5.54, 43.46) * mm});
            skLineSegment(sketch, "E5223", {"start": v(-5.54, 43.46) * mm, "end": v(-5.66, 43.45) * mm});
            skLineSegment(sketch, "E5224", {"start": v(-5.66, 43.45) * mm, "end": v(-5.77, 43.43) * mm});
            skLineSegment(sketch, "E5225", {"start": v(-5.77, 43.43) * mm, "end": v(-5.9, 43.42) * mm});
            skLineSegment(sketch, "E5226", {"start": v(-5.9, 43.42) * mm, "end": v(-6, 43.4) * mm});
            skLineSegment(sketch, "E5227", {"start": v(-6, 43.4) * mm, "end": v(-6.12, 43.38) * mm});
            skLineSegment(sketch, "E5228", {"start": v(-6.12, 43.38) * mm, "end": v(-6.24, 43.37) * mm});
            skLineSegment(sketch, "E5229", {"start": v(-6.24, 43.37) * mm, "end": v(-6.26, 43.37) * mm});
            skLineSegment(sketch, "E5230", {"start": v(-6.26, 43.37) * mm, "end": v(-6.3, 43.47) * mm});
            skLineSegment(sketch, "E5231", {"start": v(-6.3, 43.47) * mm, "end": v(-6.35, 43.57) * mm});
            skLineSegment(sketch, "E5232", {"start": v(-6.35, 43.57) * mm, "end": v(-6.4, 43.67) * mm});
            skLineSegment(sketch, "E5233", {"start": v(-6.4, 43.67) * mm, "end": v(-6.46, 43.78) * mm});
            skLineSegment(sketch, "E5234", {"start": v(-6.46, 43.78) * mm, "end": v(-6.5, 43.89) * mm});
            skLineSegment(sketch, "E5235", {"start": v(-6.5, 43.89) * mm, "end": v(-6.57, 44) * mm});
            skLineSegment(sketch, "E5236", {"start": v(-6.57, 44) * mm, "end": v(-6.63, 44.1) * mm});
            skLineSegment(sketch, "E5237", {"start": v(-6.63, 44.1) * mm, "end": v(-6.69, 44.23) * mm});
            skLineSegment(sketch, "E5238", {"start": v(-6.69, 44.23) * mm, "end": v(-6.75, 44.33) * mm});
            skLineSegment(sketch, "E5239", {"start": v(-6.75, 44.33) * mm, "end": v(-6.8, 44.44) * mm});
            skLineSegment(sketch, "E5240", {"start": v(-6.8, 44.44) * mm, "end": v(-6.86, 44.54) * mm});
            skLineSegment(sketch, "E5241", {"start": v(-6.86, 44.54) * mm, "end": v(-6.92, 44.63) * mm});
            skLineSegment(sketch, "E5242", {"start": v(-6.92, 44.63) * mm, "end": v(-6.98, 44.73) * mm});
            skLineSegment(sketch, "E5243", {"start": v(-6.98, 44.73) * mm, "end": v(-7.04, 44.84) * mm});
            skLineSegment(sketch, "E5244", {"start": v(-7.04, 44.84) * mm, "end": v(-7.1, 44.94) * mm});
            skLineSegment(sketch, "E5245", {"start": v(-7.1, 44.94) * mm, "end": v(-7.16, 45.04) * mm});
            skLineSegment(sketch, "E5246", {"start": v(-7.16, 45.04) * mm, "end": v(-7.23, 45.15) * mm});
            skLineSegment(sketch, "E5247", {"start": v(-7.23, 45.15) * mm, "end": v(-7.3, 45.25) * mm});
            skLineSegment(sketch, "E5248", {"start": v(-7.3, 45.25) * mm, "end": v(-7.37, 45.36) * mm});
            skLineSegment(sketch, "E5249", {"start": v(-7.37, 45.36) * mm, "end": v(-7.37, 45.36) * mm});
            skLineSegment(sketch, "E5250", {"start": v(-7.37, 45.36) * mm, "end": v(-7.48, 45.34) * mm});
            skLineSegment(sketch, "E5251", {"start": v(-7.48, 45.34) * mm, "end": v(-7.6, 45.32) * mm});
            skLineSegment(sketch, "E5252", {"start": v(-7.6, 45.32) * mm, "end": v(-7.7, 45.3) * mm});
            skLineSegment(sketch, "E5253", {"start": v(-7.7, 45.3) * mm, "end": v(-7.83, 45.29) * mm});
            skLineSegment(sketch, "E5254", {"start": v(-7.83, 45.29) * mm, "end": v(-7.92, 45.27) * mm});
            skLineSegment(sketch, "E5255", {"start": v(-7.92, 45.27) * mm, "end": v(-7.95, 45.15) * mm});
            skLineSegment(sketch, "E5256", {"start": v(-7.95, 45.15) * mm, "end": v(-7.98, 45.03) * mm});
            skLineSegment(sketch, "E5257", {"start": v(-7.98, 45.03) * mm, "end": v(-8, 44.92) * mm});
            skLineSegment(sketch, "E5258", {"start": v(-8, 44.92) * mm, "end": v(-8.03, 44.8) * mm});
            skLineSegment(sketch, "E5259", {"start": v(-8.03, 44.8) * mm, "end": v(-8.05, 44.69) * mm});
            skLineSegment(sketch, "E5260", {"start": v(-8.05, 44.69) * mm, "end": v(-8.08, 44.57) * mm});
            skLineSegment(sketch, "E5261", {"start": v(-8.08, 44.57) * mm, "end": v(-8.1, 44.45) * mm});
            skLineSegment(sketch, "E5262", {"start": v(-8.1, 44.45) * mm, "end": v(-8.12, 44.34) * mm});
            skLineSegment(sketch, "E5263", {"start": v(-8.12, 44.34) * mm, "end": v(-8.15, 44.22) * mm});
            skLineSegment(sketch, "E5264", {"start": v(-8.15, 44.22) * mm, "end": v(-8.17, 44.1) * mm});
            skLineSegment(sketch, "E5265", {"start": v(-8.17, 44.1) * mm, "end": v(-8.19, 43.98) * mm});
            skLineSegment(sketch, "E5266", {"start": v(-8.19, 43.98) * mm, "end": v(-8.2, 43.86) * mm});
            skLineSegment(sketch, "E5267", {"start": v(-8.2, 43.86) * mm, "end": v(-8.23, 43.74) * mm});
            skLineSegment(sketch, "E5268", {"start": v(-8.23, 43.74) * mm, "end": v(-8.24, 43.62) * mm});
            skLineSegment(sketch, "E5269", {"start": v(-8.24, 43.62) * mm, "end": v(-8.26, 43.5) * mm});
            skLineSegment(sketch, "E5270", {"start": v(-8.26, 43.5) * mm, "end": v(-8.27, 43.39) * mm});
            skLineSegment(sketch, "E5271", {"start": v(-8.27, 43.39) * mm, "end": v(-8.29, 43.27) * mm});
            skLineSegment(sketch, "E5272", {"start": v(-8.29, 43.27) * mm, "end": v(-8.3, 43.15) * mm});
            skLineSegment(sketch, "E5273", {"start": v(-8.3, 43.15) * mm, "end": v(-8.31, 43.02) * mm});
            skLineSegment(sketch, "E5274", {"start": v(-8.31, 43.02) * mm, "end": v(-8.43, 43) * mm});
            skLineSegment(sketch, "E5275", {"start": v(-8.43, 43) * mm, "end": v(-8.55, 42.97) * mm});
            skLineSegment(sketch, "E5276", {"start": v(-8.55, 42.97) * mm, "end": v(-8.66, 42.95) * mm});
            skLineSegment(sketch, "E5277", {"start": v(-8.66, 42.95) * mm, "end": v(-8.78, 42.93) * mm});
            skLineSegment(sketch, "E5278", {"start": v(-8.78, 42.93) * mm, "end": v(-8.9, 42.9) * mm});
            skLineSegment(sketch, "E5279", {"start": v(-8.9, 42.9) * mm, "end": v(-9, 42.88) * mm});
            skLineSegment(sketch, "E5280", {"start": v(-9, 42.88) * mm, "end": v(-9.13, 42.86) * mm});
            skLineSegment(sketch, "E5281", {"start": v(-9.13, 42.86) * mm, "end": v(-9.14, 42.85) * mm});
            skLineSegment(sketch, "E5282", {"start": v(-9.14, 42.85) * mm, "end": v(-9.2, 42.95) * mm});
            skLineSegment(sketch, "E5283", {"start": v(-9.2, 42.95) * mm, "end": v(-9.25, 43.05) * mm});
            skLineSegment(sketch, "E5284", {"start": v(-9.25, 43.05) * mm, "end": v(-9.3, 43.15) * mm});
            skLineSegment(sketch, "E5285", {"start": v(-9.3, 43.15) * mm, "end": v(-9.36, 43.25) * mm});
            skLineSegment(sketch, "E5286", {"start": v(-9.36, 43.25) * mm, "end": v(-9.43, 43.35) * mm});
            skLineSegment(sketch, "E5287", {"start": v(-9.43, 43.35) * mm, "end": v(-9.5, 43.46) * mm});
            skLineSegment(sketch, "E5288", {"start": v(-9.5, 43.46) * mm, "end": v(-9.56, 43.57) * mm});
            skLineSegment(sketch, "E5289", {"start": v(-9.56, 43.57) * mm, "end": v(-9.63, 43.68) * mm});
            skLineSegment(sketch, "E5290", {"start": v(-9.63, 43.68) * mm, "end": v(-9.7, 43.78) * mm});
            skLineSegment(sketch, "E5291", {"start": v(-9.7, 43.78) * mm, "end": v(-9.76, 43.88) * mm});
            skLineSegment(sketch, "E5292", {"start": v(-9.76, 43.88) * mm, "end": v(-9.82, 43.98) * mm});
            skLineSegment(sketch, "E5293", {"start": v(-9.82, 43.98) * mm, "end": v(-9.88, 44.07) * mm});
            skLineSegment(sketch, "E5294", {"start": v(-9.88, 44.07) * mm, "end": v(-9.95, 44.17) * mm});
            skLineSegment(sketch, "E5295", {"start": v(-9.95, 44.17) * mm, "end": v(-10.02, 44.27) * mm});
            skLineSegment(sketch, "E5296", {"start": v(-10.02, 44.27) * mm, "end": v(-10.08, 44.36) * mm});
            skLineSegment(sketch, "E5297", {"start": v(-10.08, 44.36) * mm, "end": v(-10.15, 44.46) * mm});
            skLineSegment(sketch, "E5298", {"start": v(-10.15, 44.46) * mm, "end": v(-10.23, 44.56) * mm});
            skLineSegment(sketch, "E5299", {"start": v(-10.23, 44.56) * mm, "end": v(-10.3, 44.67) * mm});
            skLineSegment(sketch, "E5300", {"start": v(-10.3, 44.67) * mm, "end": v(-10.38, 44.77) * mm});
            skLineSegment(sketch, "E5301", {"start": v(-10.38, 44.77) * mm, "end": v(-10.38, 44.77) * mm});
            skLineSegment(sketch, "E5302", {"start": v(-10.38, 44.77) * mm, "end": v(-10.5, 44.74) * mm});
            skLineSegment(sketch, "E5303", {"start": v(-10.5, 44.74) * mm, "end": v(-10.61, 44.71) * mm});
            skLineSegment(sketch, "E5304", {"start": v(-10.61, 44.71) * mm, "end": v(-10.72, 44.69) * mm});
            skLineSegment(sketch, "E5305", {"start": v(-10.72, 44.69) * mm, "end": v(-10.83, 44.66) * mm});
            skLineSegment(sketch, "E5306", {"start": v(-10.83, 44.66) * mm, "end": v(-10.93, 44.64) * mm});
            skLineSegment(sketch, "E5307", {"start": v(-10.93, 44.64) * mm, "end": v(-10.95, 44.52) * mm});
            skLineSegment(sketch, "E5308", {"start": v(-10.95, 44.52) * mm, "end": v(-10.97, 44.4) * mm});
            skLineSegment(sketch, "E5309", {"start": v(-10.97, 44.4) * mm, "end": v(-10.99, 44.28) * mm});
            skLineSegment(sketch, "E5310", {"start": v(-10.99, 44.28) * mm, "end": v(-11, 44.17) * mm});
            skLineSegment(sketch, "E5311", {"start": v(-11, 44.17) * mm, "end": v(-11.02, 44.05) * mm});
            skLineSegment(sketch, "E5312", {"start": v(-11.02, 44.05) * mm, "end": v(-11.04, 43.93) * mm});
            skLineSegment(sketch, "E5313", {"start": v(-11.04, 43.93) * mm, "end": v(-11.05, 43.81) * mm});
            skLineSegment(sketch, "E5314", {"start": v(-11.05, 43.81) * mm, "end": v(-11.07, 43.7) * mm});
            skLineSegment(sketch, "E5315", {"start": v(-11.07, 43.7) * mm, "end": v(-11.08, 43.58) * mm});
            skLineSegment(sketch, "E5316", {"start": v(-11.08, 43.58) * mm, "end": v(-11.1, 43.45) * mm});
            skLineSegment(sketch, "E5317", {"start": v(-11.1, 43.45) * mm, "end": v(-11.1, 43.33) * mm});
            skLineSegment(sketch, "E5318", {"start": v(-11.1, 43.33) * mm, "end": v(-11.12, 43.21) * mm});
            skLineSegment(sketch, "E5319", {"start": v(-11.12, 43.21) * mm, "end": v(-11.13, 43.1) * mm});
            skLineSegment(sketch, "E5320", {"start": v(-11.13, 43.1) * mm, "end": v(-11.14, 42.98) * mm});
            skLineSegment(sketch, "E5321", {"start": v(-11.14, 42.98) * mm, "end": v(-11.15, 42.86) * mm});
            skLineSegment(sketch, "E5322", {"start": v(-11.15, 42.86) * mm, "end": v(-11.15, 42.74) * mm});
            skLineSegment(sketch, "E5323", {"start": v(-11.15, 42.74) * mm, "end": v(-11.16, 42.62) * mm});
            skLineSegment(sketch, "E5324", {"start": v(-11.16, 42.62) * mm, "end": v(-11.16, 42.5) * mm});
            skLineSegment(sketch, "E5325", {"start": v(-11.16, 42.5) * mm, "end": v(-11.17, 42.37) * mm});
            skLineSegment(sketch, "E5326", {"start": v(-11.17, 42.37) * mm, "end": v(-11.28, 42.34) * mm});
            skLineSegment(sketch, "E5327", {"start": v(-11.28, 42.34) * mm, "end": v(-11.4, 42.3) * mm});
            skLineSegment(sketch, "E5328", {"start": v(-11.4, 42.3) * mm, "end": v(-11.51, 42.27) * mm});
            skLineSegment(sketch, "E5329", {"start": v(-11.51, 42.27) * mm, "end": v(-11.62, 42.24) * mm});
            skLineSegment(sketch, "E5330", {"start": v(-11.62, 42.24) * mm, "end": v(-11.74, 42.21) * mm});
            skLineSegment(sketch, "E5331", {"start": v(-11.74, 42.21) * mm, "end": v(-11.85, 42.18) * mm});
            skLineSegment(sketch, "E5332", {"start": v(-11.85, 42.18) * mm, "end": v(-11.97, 42.15) * mm});
            skLineSegment(sketch, "E5333", {"start": v(-11.97, 42.15) * mm, "end": v(-11.98, 42.15) * mm});
            skLineSegment(sketch, "E5334", {"start": v(-11.98, 42.15) * mm, "end": v(-12.04, 42.24) * mm});
            skLineSegment(sketch, "E5335", {"start": v(-12.04, 42.24) * mm, "end": v(-12.1, 42.33) * mm});
            skLineSegment(sketch, "E5336", {"start": v(-12.1, 42.33) * mm, "end": v(-12.17, 42.43) * mm});
            skLineSegment(sketch, "E5337", {"start": v(-12.17, 42.43) * mm, "end": v(-12.23, 42.53) * mm});
            skLineSegment(sketch, "E5338", {"start": v(-12.23, 42.53) * mm, "end": v(-12.3, 42.63) * mm});
            skLineSegment(sketch, "E5339", {"start": v(-12.3, 42.63) * mm, "end": v(-12.37, 42.73) * mm});
            skLineSegment(sketch, "E5340", {"start": v(-12.37, 42.73) * mm, "end": v(-12.45, 42.83) * mm});
            skLineSegment(sketch, "E5341", {"start": v(-12.45, 42.83) * mm, "end": v(-12.52, 42.94) * mm});
            skLineSegment(sketch, "E5342", {"start": v(-12.52, 42.94) * mm, "end": v(-12.6, 43.04) * mm});
            skLineSegment(sketch, "E5343", {"start": v(-12.6, 43.04) * mm, "end": v(-12.67, 43.14) * mm});
            skLineSegment(sketch, "E5344", {"start": v(-12.67, 43.14) * mm, "end": v(-12.74, 43.22) * mm});
            skLineSegment(sketch, "E5345", {"start": v(-12.74, 43.22) * mm, "end": v(-12.8, 43.31) * mm});
            skLineSegment(sketch, "E5346", {"start": v(-12.8, 43.31) * mm, "end": v(-12.88, 43.4) * mm});
            skLineSegment(sketch, "E5347", {"start": v(-12.88, 43.4) * mm, "end": v(-12.95, 43.5) * mm});
            skLineSegment(sketch, "E5348", {"start": v(-12.95, 43.5) * mm, "end": v(-13.02, 43.6) * mm});
            skLineSegment(sketch, "E5349", {"start": v(-13.02, 43.6) * mm, "end": v(-13.1, 43.69) * mm});
            skLineSegment(sketch, "E5350", {"start": v(-13.1, 43.69) * mm, "end": v(-13.18, 43.78) * mm});
            skLineSegment(sketch, "E5351", {"start": v(-13.18, 43.78) * mm, "end": v(-13.26, 43.88) * mm});
            skLineSegment(sketch, "E5352", {"start": v(-13.26, 43.88) * mm, "end": v(-13.35, 43.98) * mm});
            skLineSegment(sketch, "E5353", {"start": v(-13.35, 43.98) * mm, "end": v(-13.35, 43.98) * mm});
            skLineSegment(sketch, "E5354", {"start": v(-13.35, 43.98) * mm, "end": v(-13.46, 43.94) * mm});
            skLineSegment(sketch, "E5355", {"start": v(-13.46, 43.94) * mm, "end": v(-13.57, 43.9) * mm});
            skLineSegment(sketch, "E5356", {"start": v(-13.57, 43.9) * mm, "end": v(-13.68, 43.87) * mm});
            skLineSegment(sketch, "E5357", {"start": v(-13.68, 43.87) * mm, "end": v(-13.8, 43.84) * mm});
            skLineSegment(sketch, "E5358", {"start": v(-13.8, 43.84) * mm, "end": v(-13.88, 43.8) * mm});
            skLineSegment(sketch, "E5359", {"start": v(-13.88, 43.8) * mm, "end": v(-13.9, 43.7) * mm});
            skLineSegment(sketch, "E5360", {"start": v(-13.9, 43.7) * mm, "end": v(-13.9, 43.57) * mm});
            skLineSegment(sketch, "E5361", {"start": v(-13.9, 43.57) * mm, "end": v(-13.92, 43.45) * mm});
            skLineSegment(sketch, "E5362", {"start": v(-13.92, 43.45) * mm, "end": v(-13.93, 43.34) * mm});
            skLineSegment(sketch, "E5363", {"start": v(-13.93, 43.34) * mm, "end": v(-13.94, 43.22) * mm});
            skLineSegment(sketch, "E5364", {"start": v(-13.94, 43.22) * mm, "end": v(-13.95, 43.1) * mm});
            skLineSegment(sketch, "E5365", {"start": v(-13.95, 43.1) * mm, "end": v(-13.95, 42.98) * mm});
            skLineSegment(sketch, "E5366", {"start": v(-13.95, 42.98) * mm, "end": v(-13.96, 42.86) * mm});
            skLineSegment(sketch, "E5367", {"start": v(-13.96, 42.86) * mm, "end": v(-13.97, 42.74) * mm});
            skLineSegment(sketch, "E5368", {"start": v(-13.97, 42.74) * mm, "end": v(-13.97, 42.61) * mm});
            skLineSegment(sketch, "E5369", {"start": v(-13.97, 42.61) * mm, "end": v(-13.98, 42.5) * mm});
            skLineSegment(sketch, "E5370", {"start": v(-13.98, 42.5) * mm, "end": v(-13.98, 42.37) * mm});
            skLineSegment(sketch, "E5371", {"start": v(-13.98, 42.37) * mm, "end": v(-13.98, 42.25) * mm});
            skLineSegment(sketch, "E5372", {"start": v(-13.98, 42.25) * mm, "end": v(-13.98, 42.14) * mm});
            skLineSegment(sketch, "E5373", {"start": v(-13.98, 42.14) * mm, "end": v(-13.98, 42.02) * mm});
            skLineSegment(sketch, "E5374", {"start": v(-13.98, 42.02) * mm, "end": v(-13.98, 41.9) * mm});
            skLineSegment(sketch, "E5375", {"start": v(-13.98, 41.9) * mm, "end": v(-13.98, 41.78) * mm});
            skLineSegment(sketch, "E5376", {"start": v(-13.98, 41.78) * mm, "end": v(-13.98, 41.66) * mm});
            skLineSegment(sketch, "E5377", {"start": v(-13.98, 41.66) * mm, "end": v(-13.97, 41.53) * mm});
            skLineSegment(sketch, "E5378", {"start": v(-13.97, 41.53) * mm, "end": v(-14.09, 41.49) * mm});
            skLineSegment(sketch, "E5379", {"start": v(-14.09, 41.49) * mm, "end": v(-14.2, 41.45) * mm});
            skLineSegment(sketch, "E5380", {"start": v(-14.2, 41.45) * mm, "end": v(-14.3, 41.41) * mm});
            skLineSegment(sketch, "E5381", {"start": v(-14.3, 41.41) * mm, "end": v(-14.42, 41.37) * mm});
            skLineSegment(sketch, "E5382", {"start": v(-14.42, 41.37) * mm, "end": v(-14.53, 41.33) * mm});
            skLineSegment(sketch, "E5383", {"start": v(-14.53, 41.33) * mm, "end": v(-14.64, 41.3) * mm});
            skLineSegment(sketch, "E5384", {"start": v(-14.64, 41.3) * mm, "end": v(-14.76, 41.26) * mm});
            skLineSegment(sketch, "E5385", {"start": v(-14.76, 41.26) * mm, "end": v(-14.77, 41.25) * mm});
            skLineSegment(sketch, "E5386", {"start": v(-14.77, 41.25) * mm, "end": v(-14.84, 41.34) * mm});
            skLineSegment(sketch, "E5387", {"start": v(-14.84, 41.34) * mm, "end": v(-14.9, 41.43) * mm});
            skLineSegment(sketch, "E5388", {"start": v(-14.9, 41.43) * mm, "end": v(-14.97, 41.52) * mm});
            skLineSegment(sketch, "E5389", {"start": v(-14.97, 41.52) * mm, "end": v(-15.04, 41.61) * mm});
            skLineSegment(sketch, "E5390", {"start": v(-15.04, 41.61) * mm, "end": v(-15.12, 41.7) * mm});
            skLineSegment(sketch, "E5391", {"start": v(-15.12, 41.7) * mm, "end": v(-15.2, 41.8) * mm});
            skLineSegment(sketch, "E5392", {"start": v(-15.2, 41.8) * mm, "end": v(-15.28, 41.9) * mm});
            skLineSegment(sketch, "E5393", {"start": v(-15.28, 41.9) * mm, "end": v(-15.36, 42) * mm});
            skLineSegment(sketch, "E5394", {"start": v(-15.36, 42) * mm, "end": v(-15.44, 42.1) * mm});
            skLineSegment(sketch, "E5395", {"start": v(-15.44, 42.1) * mm, "end": v(-15.52, 42.2) * mm});
            skLineSegment(sketch, "E5396", {"start": v(-15.52, 42.2) * mm, "end": v(-15.6, 42.28) * mm});
            skLineSegment(sketch, "E5397", {"start": v(-15.6, 42.28) * mm, "end": v(-15.67, 42.36) * mm});
            skLineSegment(sketch, "E5398", {"start": v(-15.67, 42.36) * mm, "end": v(-15.75, 42.45) * mm});
            skLineSegment(sketch, "E5399", {"start": v(-15.75, 42.45) * mm, "end": v(-15.83, 42.54) * mm});
            skLineSegment(sketch, "E5400", {"start": v(-15.83, 42.54) * mm, "end": v(-15.9, 42.62) * mm});
            skLineSegment(sketch, "E5401", {"start": v(-15.9, 42.62) * mm, "end": v(-16, 42.71) * mm});
            skLineSegment(sketch, "E5402", {"start": v(-16, 42.71) * mm, "end": v(-16.08, 42.8) * mm});
            skLineSegment(sketch, "E5403", {"start": v(-16.08, 42.8) * mm, "end": v(-16.16, 42.9) * mm});
            skLineSegment(sketch, "E5404", {"start": v(-16.16, 42.9) * mm, "end": v(-16.25, 42.99) * mm});
            skLineSegment(sketch, "E5405", {"start": v(-16.25, 42.99) * mm, "end": v(-16.25, 42.99) * mm});
            skLineSegment(sketch, "E5406", {"start": v(-16.25, 42.99) * mm, "end": v(-16.37, 42.94) * mm});
            skLineSegment(sketch, "E5407", {"start": v(-16.37, 42.94) * mm, "end": v(-16.48, 42.9) * mm});
            skLineSegment(sketch, "E5408", {"start": v(-16.48, 42.9) * mm, "end": v(-16.58, 42.86) * mm});
            skLineSegment(sketch, "E5409", {"start": v(-16.58, 42.86) * mm, "end": v(-16.69, 42.82) * mm});
            skLineSegment(sketch, "E5410", {"start": v(-16.69, 42.82) * mm, "end": v(-16.78, 42.78) * mm});
            skLineSegment(sketch, "E5411", {"start": v(-16.78, 42.78) * mm, "end": v(-16.78, 42.66) * mm});
            skLineSegment(sketch, "E5412", {"start": v(-16.78, 42.66) * mm, "end": v(-16.79, 42.54) * mm});
            skLineSegment(sketch, "E5413", {"start": v(-16.79, 42.54) * mm, "end": v(-16.8, 42.42) * mm});
            skLineSegment(sketch, "E5414", {"start": v(-16.8, 42.42) * mm, "end": v(-16.8, 42.3) * mm});
            skLineSegment(sketch, "E5415", {"start": v(-16.8, 42.3) * mm, "end": v(-16.8, 42.19) * mm});
            skLineSegment(sketch, "E5416", {"start": v(-16.8, 42.19) * mm, "end": v(-16.8, 42.07) * mm});
            skLineSegment(sketch, "E5417", {"start": v(-16.8, 42.07) * mm, "end": v(-16.8, 41.95) * mm});
            skLineSegment(sketch, "E5418", {"start": v(-16.8, 41.95) * mm, "end": v(-16.8, 41.83) * mm});
            skLineSegment(sketch, "E5419", {"start": v(-16.8, 41.83) * mm, "end": v(-16.8, 41.71) * mm});
            skLineSegment(sketch, "E5420", {"start": v(-16.8, 41.71) * mm, "end": v(-16.79, 41.59) * mm});
            skLineSegment(sketch, "E5421", {"start": v(-16.79, 41.59) * mm, "end": v(-16.78, 41.47) * mm});
            skLineSegment(sketch, "E5422", {"start": v(-16.78, 41.47) * mm, "end": v(-16.78, 41.35) * mm});
            skLineSegment(sketch, "E5423", {"start": v(-16.78, 41.35) * mm, "end": v(-16.77, 41.23) * mm});
            skLineSegment(sketch, "E5424", {"start": v(-16.77, 41.23) * mm, "end": v(-16.77, 41.1) * mm});
            skLineSegment(sketch, "E5425", {"start": v(-16.77, 41.1) * mm, "end": v(-16.76, 40.99) * mm});
            skLineSegment(sketch, "E5426", {"start": v(-16.76, 40.99) * mm, "end": v(-16.75, 40.87) * mm});
            skLineSegment(sketch, "E5427", {"start": v(-16.75, 40.87) * mm, "end": v(-16.74, 40.75) * mm});
            skLineSegment(sketch, "E5428", {"start": v(-16.74, 40.75) * mm, "end": v(-16.73, 40.63) * mm});
            skLineSegment(sketch, "E5429", {"start": v(-16.73, 40.63) * mm, "end": v(-16.71, 40.5) * mm});
            skLineSegment(sketch, "E5430", {"start": v(-16.71, 40.5) * mm, "end": v(-16.82, 40.45) * mm});
            skLineSegment(sketch, "E5431", {"start": v(-16.82, 40.45) * mm, "end": v(-16.93, 40.4) * mm});
            skLineSegment(sketch, "E5432", {"start": v(-16.93, 40.4) * mm, "end": v(-17.04, 40.36) * mm});
            skLineSegment(sketch, "E5433", {"start": v(-17.04, 40.36) * mm, "end": v(-17.15, 40.32) * mm});
            skLineSegment(sketch, "E5434", {"start": v(-17.15, 40.32) * mm, "end": v(-17.26, 40.27) * mm});
            skLineSegment(sketch, "E5435", {"start": v(-17.26, 40.27) * mm, "end": v(-17.37, 40.22) * mm});
            skLineSegment(sketch, "E5436", {"start": v(-17.37, 40.22) * mm, "end": v(-17.48, 40.18) * mm});
            skLineSegment(sketch, "E5437", {"start": v(-17.48, 40.18) * mm, "end": v(-17.5, 40.17) * mm});
            skLineSegment(sketch, "E5438", {"start": v(-17.5, 40.17) * mm, "end": v(-17.56, 40.26) * mm});
            skLineSegment(sketch, "E5439", {"start": v(-17.56, 40.26) * mm, "end": v(-17.64, 40.34) * mm});
            skLineSegment(sketch, "E5440", {"start": v(-17.64, 40.34) * mm, "end": v(-17.71, 40.43) * mm});
            skLineSegment(sketch, "E5441", {"start": v(-17.71, 40.43) * mm, "end": v(-17.8, 40.52) * mm});
            skLineSegment(sketch, "E5442", {"start": v(-17.8, 40.52) * mm, "end": v(-17.87, 40.6) * mm});
            skLineSegment(sketch, "E5443", {"start": v(-17.87, 40.6) * mm, "end": v(-17.96, 40.7) * mm});
            skLineSegment(sketch, "E5444", {"start": v(-17.96, 40.7) * mm, "end": v(-18.04, 40.8) * mm});
            skLineSegment(sketch, "E5445", {"start": v(-18.04, 40.8) * mm, "end": v(-18.13, 40.89) * mm});
            skLineSegment(sketch, "E5446", {"start": v(-18.13, 40.89) * mm, "end": v(-18.22, 40.97) * mm});
            skLineSegment(sketch, "E5447", {"start": v(-18.22, 40.97) * mm, "end": v(-18.3, 41.06) * mm});
            skLineSegment(sketch, "E5448", {"start": v(-18.3, 41.06) * mm, "end": v(-18.38, 41.14) * mm});
            skLineSegment(sketch, "E5449", {"start": v(-18.38, 41.14) * mm, "end": v(-18.46, 41.22) * mm});
            skLineSegment(sketch, "E5450", {"start": v(-18.46, 41.22) * mm, "end": v(-18.55, 41.3) * mm});
            skLineSegment(sketch, "E5451", {"start": v(-18.55, 41.3) * mm, "end": v(-18.63, 41.38) * mm});
            skLineSegment(sketch, "E5452", {"start": v(-18.63, 41.38) * mm, "end": v(-18.72, 41.47) * mm});
            skLineSegment(sketch, "E5453", {"start": v(-18.72, 41.47) * mm, "end": v(-18.8, 41.55) * mm});
            skLineSegment(sketch, "E5454", {"start": v(-18.8, 41.55) * mm, "end": v(-18.9, 41.63) * mm});
            skLineSegment(sketch, "E5455", {"start": v(-18.9, 41.63) * mm, "end": v(-19, 41.72) * mm});
            skLineSegment(sketch, "E5456", {"start": v(-19, 41.72) * mm, "end": v(-19.09, 41.8) * mm});
            skLineSegment(sketch, "E5457", {"start": v(-19.09, 41.8) * mm, "end": v(-19.09, 41.8) * mm});
            skLineSegment(sketch, "E5458", {"start": v(-19.09, 41.8) * mm, "end": v(-19.2, 41.76) * mm});
            skLineSegment(sketch, "E5459", {"start": v(-19.2, 41.76) * mm, "end": v(-19.3, 41.7) * mm});
            skLineSegment(sketch, "E5460", {"start": v(-19.3, 41.7) * mm, "end": v(-19.4, 41.66) * mm});
            skLineSegment(sketch, "E5461", {"start": v(-19.4, 41.66) * mm, "end": v(-19.51, 41.6) * mm});
            skLineSegment(sketch, "E5462", {"start": v(-19.51, 41.6) * mm, "end": v(-19.6, 41.57) * mm});
            skLineSegment(sketch, "E5463", {"start": v(-19.6, 41.57) * mm, "end": v(-19.6, 41.45) * mm});
            skLineSegment(sketch, "E5464", {"start": v(-19.6, 41.45) * mm, "end": v(-19.6, 41.33) * mm});
            skLineSegment(sketch, "E5465", {"start": v(-19.6, 41.33) * mm, "end": v(-19.59, 41.2) * mm});
            skLineSegment(sketch, "E5466", {"start": v(-19.59, 41.2) * mm, "end": v(-19.58, 41.1) * mm});
            skLineSegment(sketch, "E5467", {"start": v(-19.58, 41.1) * mm, "end": v(-19.57, 40.97) * mm});
            skLineSegment(sketch, "E5468", {"start": v(-19.57, 40.97) * mm, "end": v(-19.57, 40.85) * mm});
            skLineSegment(sketch, "E5469", {"start": v(-19.57, 40.85) * mm, "end": v(-19.56, 40.74) * mm});
            skLineSegment(sketch, "E5470", {"start": v(-19.56, 40.74) * mm, "end": v(-19.55, 40.62) * mm});
            skLineSegment(sketch, "E5471", {"start": v(-19.55, 40.62) * mm, "end": v(-19.54, 40.5) * mm});
            skLineSegment(sketch, "E5472", {"start": v(-19.54, 40.5) * mm, "end": v(-19.53, 40.37) * mm});
            skLineSegment(sketch, "E5473", {"start": v(-19.53, 40.37) * mm, "end": v(-19.52, 40.25) * mm});
            skLineSegment(sketch, "E5474", {"start": v(-19.52, 40.25) * mm, "end": v(-19.5, 40.13) * mm});
            skLineSegment(sketch, "E5475", {"start": v(-19.5, 40.13) * mm, "end": v(-19.49, 40.01) * mm});
            skLineSegment(sketch, "E5476", {"start": v(-19.49, 40.01) * mm, "end": v(-19.47, 39.9) * mm});
            skLineSegment(sketch, "E5477", {"start": v(-19.47, 39.9) * mm, "end": v(-19.46, 39.78) * mm});
            skLineSegment(sketch, "E5478", {"start": v(-19.46, 39.78) * mm, "end": v(-19.44, 39.66) * mm});
            skLineSegment(sketch, "E5479", {"start": v(-19.44, 39.66) * mm, "end": v(-19.42, 39.54) * mm});
            skLineSegment(sketch, "E5480", {"start": v(-19.42, 39.54) * mm, "end": v(-19.4, 39.42) * mm});
            skLineSegment(sketch, "E5481", {"start": v(-19.4, 39.42) * mm, "end": v(-19.38, 39.3) * mm});
            skLineSegment(sketch, "E5482", {"start": v(-19.38, 39.3) * mm, "end": v(-19.49, 39.24) * mm});
            skLineSegment(sketch, "E5483", {"start": v(-19.49, 39.24) * mm, "end": v(-19.6, 39.19) * mm});
            skLineSegment(sketch, "E5484", {"start": v(-19.6, 39.19) * mm, "end": v(-19.7, 39.13) * mm});
            skLineSegment(sketch, "E5485", {"start": v(-19.7, 39.13) * mm, "end": v(-19.8, 39.08) * mm});
            skLineSegment(sketch, "E5486", {"start": v(-19.8, 39.08) * mm, "end": v(-19.91, 39.03) * mm});
            skLineSegment(sketch, "E5487", {"start": v(-19.91, 39.03) * mm, "end": v(-20.02, 38.97) * mm});
            skLineSegment(sketch, "E5488", {"start": v(-20.02, 38.97) * mm, "end": v(-20.12, 38.92) * mm});
            skLineSegment(sketch, "E5489", {"start": v(-20.12, 38.92) * mm, "end": v(-20.14, 38.92) * mm});
            skLineSegment(sketch, "E5490", {"start": v(-20.14, 38.92) * mm, "end": v(-20.21, 39) * mm});
            skLineSegment(sketch, "E5491", {"start": v(-20.21, 39) * mm, "end": v(-20.3, 39.07) * mm});
            skLineSegment(sketch, "E5492", {"start": v(-20.3, 39.07) * mm, "end": v(-20.37, 39.15) * mm});
            skLineSegment(sketch, "E5493", {"start": v(-20.37, 39.15) * mm, "end": v(-20.46, 39.24) * mm});
            skLineSegment(sketch, "E5494", {"start": v(-20.46, 39.24) * mm, "end": v(-20.54, 39.32) * mm});
            skLineSegment(sketch, "E5495", {"start": v(-20.54, 39.32) * mm, "end": v(-20.63, 39.4) * mm});
            skLineSegment(sketch, "E5496", {"start": v(-20.63, 39.4) * mm, "end": v(-20.73, 39.5) * mm});
            skLineSegment(sketch, "E5497", {"start": v(-20.73, 39.5) * mm, "end": v(-20.82, 39.58) * mm});
            skLineSegment(sketch, "E5498", {"start": v(-20.82, 39.58) * mm, "end": v(-20.91, 39.66) * mm});
            skLineSegment(sketch, "E5499", {"start": v(-20.91, 39.66) * mm, "end": v(-21, 39.75) * mm});
            skLineSegment(sketch, "E5500", {"start": v(-21, 39.75) * mm, "end": v(-21.09, 39.82) * mm});
            skLineSegment(sketch, "E5501", {"start": v(-21.09, 39.82) * mm, "end": v(-21.18, 39.9) * mm});
            skLineSegment(sketch, "E5502", {"start": v(-21.18, 39.9) * mm, "end": v(-21.26, 39.97) * mm});
            skLineSegment(sketch, "E5503", {"start": v(-21.26, 39.97) * mm, "end": v(-21.35, 40.05) * mm});
            skLineSegment(sketch, "E5504", {"start": v(-21.35, 40.05) * mm, "end": v(-21.45, 40.12) * mm});
            skLineSegment(sketch, "E5505", {"start": v(-21.45, 40.12) * mm, "end": v(-21.54, 40.2) * mm});
            skLineSegment(sketch, "E5506", {"start": v(-21.54, 40.2) * mm, "end": v(-21.64, 40.28) * mm});
            skLineSegment(sketch, "E5507", {"start": v(-21.64, 40.28) * mm, "end": v(-21.74, 40.36) * mm});
            skLineSegment(sketch, "E5508", {"start": v(-21.74, 40.36) * mm, "end": v(-21.84, 40.44) * mm});
            skLineSegment(sketch, "E5509", {"start": v(-21.84, 40.44) * mm, "end": v(-21.84, 40.44) * mm});
            skLineSegment(sketch, "E5510", {"start": v(-21.84, 40.44) * mm, "end": v(-21.94, 40.38) * mm});
            skLineSegment(sketch, "E5511", {"start": v(-21.94, 40.38) * mm, "end": v(-22.05, 40.32) * mm});
            skLineSegment(sketch, "E5512", {"start": v(-22.05, 40.32) * mm, "end": v(-22.14, 40.27) * mm});
            skLineSegment(sketch, "E5513", {"start": v(-22.14, 40.27) * mm, "end": v(-22.25, 40.21) * mm});
            skLineSegment(sketch, "E5514", {"start": v(-22.25, 40.21) * mm, "end": v(-22.33, 40.17) * mm});
            skLineSegment(sketch, "E5515", {"start": v(-22.33, 40.17) * mm, "end": v(-22.32, 40.05) * mm});
            skLineSegment(sketch, "E5516", {"start": v(-22.32, 40.05) * mm, "end": v(-22.3, 39.93) * mm});
            skLineSegment(sketch, "E5517", {"start": v(-22.3, 39.93) * mm, "end": v(-22.3, 39.8) * mm});
            skLineSegment(sketch, "E5518", {"start": v(-22.3, 39.8) * mm, "end": v(-22.28, 39.7) * mm});
            skLineSegment(sketch, "E5519", {"start": v(-22.28, 39.7) * mm, "end": v(-22.27, 39.57) * mm});
            skLineSegment(sketch, "E5520", {"start": v(-22.27, 39.57) * mm, "end": v(-22.25, 39.46) * mm});
            skLineSegment(sketch, "E5521", {"start": v(-22.25, 39.46) * mm, "end": v(-22.24, 39.34) * mm});
            skLineSegment(sketch, "E5522", {"start": v(-22.24, 39.34) * mm, "end": v(-22.22, 39.22) * mm});
            skLineSegment(sketch, "E5523", {"start": v(-22.22, 39.22) * mm, "end": v(-22.2, 39.1) * mm});
            skLineSegment(sketch, "E5524", {"start": v(-22.2, 39.1) * mm, "end": v(-22.18, 38.98) * mm});
            skLineSegment(sketch, "E5525", {"start": v(-22.18, 38.98) * mm, "end": v(-22.16, 38.86) * mm});
            skLineSegment(sketch, "E5526", {"start": v(-22.16, 38.86) * mm, "end": v(-22.14, 38.74) * mm});
            skLineSegment(sketch, "E5527", {"start": v(-22.14, 38.74) * mm, "end": v(-22.12, 38.62) * mm});
            skLineSegment(sketch, "E5528", {"start": v(-22.12, 38.62) * mm, "end": v(-22.1, 38.5) * mm});
            skLineSegment(sketch, "E5529", {"start": v(-22.1, 38.5) * mm, "end": v(-22.07, 38.39) * mm});
            skLineSegment(sketch, "E5530", {"start": v(-22.07, 38.39) * mm, "end": v(-22.05, 38.27) * mm});
            skLineSegment(sketch, "E5531", {"start": v(-22.05, 38.27) * mm, "end": v(-22.02, 38.16) * mm});
            skLineSegment(sketch, "E5532", {"start": v(-22.02, 38.16) * mm, "end": v(-22, 38.04) * mm});
            skLineSegment(sketch, "E5533", {"start": v(-22, 38.04) * mm, "end": v(-21.96, 37.91) * mm});
            skLineSegment(sketch, "E5534", {"start": v(-21.96, 37.91) * mm, "end": v(-22.07, 37.85) * mm});
            skLineSegment(sketch, "E5535", {"start": v(-22.07, 37.85) * mm, "end": v(-22.17, 37.8) * mm});
            skLineSegment(sketch, "E5536", {"start": v(-22.17, 37.8) * mm, "end": v(-22.27, 37.73) * mm});
            skLineSegment(sketch, "E5537", {"start": v(-22.27, 37.73) * mm, "end": v(-22.37, 37.67) * mm});
            skLineSegment(sketch, "E5538", {"start": v(-22.37, 37.67) * mm, "end": v(-22.47, 37.61) * mm});
            skLineSegment(sketch, "E5539", {"start": v(-22.47, 37.61) * mm, "end": v(-22.57, 37.55) * mm});
            skLineSegment(sketch, "E5540", {"start": v(-22.57, 37.55) * mm, "end": v(-22.68, 37.5) * mm});
            skLineSegment(sketch, "E5541", {"start": v(-22.68, 37.5) * mm, "end": v(-22.7, 37.48) * mm});
            skLineSegment(sketch, "E5542", {"start": v(-22.7, 37.48) * mm, "end": v(-22.77, 37.56) * mm});
            skLineSegment(sketch, "E5543", {"start": v(-22.77, 37.56) * mm, "end": v(-22.86, 37.63) * mm});
            skLineSegment(sketch, "E5544", {"start": v(-22.86, 37.63) * mm, "end": v(-22.94, 37.7) * mm});
            skLineSegment(sketch, "E5545", {"start": v(-22.94, 37.7) * mm, "end": v(-23.03, 37.78) * mm});
            skLineSegment(sketch, "E5546", {"start": v(-23.03, 37.78) * mm, "end": v(-23.12, 37.86) * mm});
            skLineSegment(sketch, "E5547", {"start": v(-23.12, 37.86) * mm, "end": v(-23.22, 37.94) * mm});
            skLineSegment(sketch, "E5548", {"start": v(-23.22, 37.94) * mm, "end": v(-23.32, 38.02) * mm});
            skLineSegment(sketch, "E5549", {"start": v(-23.32, 38.02) * mm, "end": v(-23.42, 38.1) * mm});
            skLineSegment(sketch, "E5550", {"start": v(-23.42, 38.1) * mm, "end": v(-23.51, 38.18) * mm});
            skLineSegment(sketch, "E5551", {"start": v(-23.51, 38.18) * mm, "end": v(-23.61, 38.26) * mm});
            skLineSegment(sketch, "E5552", {"start": v(-23.61, 38.26) * mm, "end": v(-23.7, 38.32) * mm});
            skLineSegment(sketch, "E5553", {"start": v(-23.7, 38.32) * mm, "end": v(-23.8, 38.4) * mm});
            skLineSegment(sketch, "E5554", {"start": v(-23.8, 38.4) * mm, "end": v(-23.89, 38.46) * mm});
            skLineSegment(sketch, "E5555", {"start": v(-23.89, 38.46) * mm, "end": v(-23.98, 38.53) * mm});
            skLineSegment(sketch, "E5556", {"start": v(-23.98, 38.53) * mm, "end": v(-24.08, 38.6) * mm});
            skLineSegment(sketch, "E5557", {"start": v(-24.08, 38.6) * mm, "end": v(-24.18, 38.67) * mm});
            skLineSegment(sketch, "E5558", {"start": v(-24.18, 38.67) * mm, "end": v(-24.28, 38.74) * mm});
            skLineSegment(sketch, "E5559", {"start": v(-24.28, 38.74) * mm, "end": v(-24.38, 38.82) * mm});
            skLineSegment(sketch, "E5560", {"start": v(-24.38, 38.82) * mm, "end": v(-24.49, 38.89) * mm});
            skLineSegment(sketch, "E5561", {"start": v(-24.49, 38.89) * mm, "end": v(-24.49, 38.89) * mm});
            skLineSegment(sketch, "E5562", {"start": v(-24.49, 38.89) * mm, "end": v(-24.6, 38.82) * mm});
            skLineSegment(sketch, "E5563", {"start": v(-24.6, 38.82) * mm, "end": v(-24.7, 38.76) * mm});
            skLineSegment(sketch, "E5564", {"start": v(-24.7, 38.76) * mm, "end": v(-24.78, 38.7) * mm});
            skLineSegment(sketch, "E5565", {"start": v(-24.78, 38.7) * mm, "end": v(-24.88, 38.64) * mm});
            skLineSegment(sketch, "E5566", {"start": v(-24.88, 38.64) * mm, "end": v(-24.96, 38.58) * mm});
            skLineSegment(sketch, "E5567", {"start": v(-24.96, 38.58) * mm, "end": v(-24.95, 38.47) * mm});
            skLineSegment(sketch, "E5568", {"start": v(-24.95, 38.47) * mm, "end": v(-24.92, 38.35) * mm});
            skLineSegment(sketch, "E5569", {"start": v(-24.92, 38.35) * mm, "end": v(-24.9, 38.23) * mm});
            skLineSegment(sketch, "E5570", {"start": v(-24.9, 38.23) * mm, "end": v(-24.88, 38.12) * mm});
            skLineSegment(sketch, "E5571", {"start": v(-24.88, 38.12) * mm, "end": v(-24.86, 38) * mm});
            skLineSegment(sketch, "E5572", {"start": v(-24.86, 38) * mm, "end": v(-24.84, 37.88) * mm});
            skLineSegment(sketch, "E5573", {"start": v(-24.84, 37.88) * mm, "end": v(-24.81, 37.76) * mm});
            skLineSegment(sketch, "E5574", {"start": v(-24.81, 37.76) * mm, "end": v(-24.79, 37.65) * mm});
            skLineSegment(sketch, "E5575", {"start": v(-24.79, 37.65) * mm, "end": v(-24.76, 37.53) * mm});
            skLineSegment(sketch, "E5576", {"start": v(-24.76, 37.53) * mm, "end": v(-24.73, 37.4) * mm});
            skLineSegment(sketch, "E5577", {"start": v(-24.73, 37.4) * mm, "end": v(-24.7, 37.3) * mm});
            skLineSegment(sketch, "E5578", {"start": v(-24.7, 37.3) * mm, "end": v(-24.68, 37.18) * mm});
            skLineSegment(sketch, "E5579", {"start": v(-24.68, 37.18) * mm, "end": v(-24.65, 37.06) * mm});
            skLineSegment(sketch, "E5580", {"start": v(-24.65, 37.06) * mm, "end": v(-24.62, 36.94) * mm});
            skLineSegment(sketch, "E5581", {"start": v(-24.62, 36.94) * mm, "end": v(-24.59, 36.83) * mm});
            skLineSegment(sketch, "E5582", {"start": v(-24.59, 36.83) * mm, "end": v(-24.55, 36.71) * mm});
            skLineSegment(sketch, "E5583", {"start": v(-24.55, 36.71) * mm, "end": v(-24.52, 36.6) * mm});
            skLineSegment(sketch, "E5584", {"start": v(-24.52, 36.6) * mm, "end": v(-24.48, 36.48) * mm});
            skLineSegment(sketch, "E5585", {"start": v(-24.48, 36.48) * mm, "end": v(-24.45, 36.36) * mm});
            skLineSegment(sketch, "E5586", {"start": v(-24.45, 36.36) * mm, "end": v(-24.54, 36.3) * mm});
            skLineSegment(sketch, "E5587", {"start": v(-24.54, 36.3) * mm, "end": v(-24.64, 36.23) * mm});
            skLineSegment(sketch, "E5588", {"start": v(-24.64, 36.23) * mm, "end": v(-24.74, 36.16) * mm});
            skLineSegment(sketch, "E5589", {"start": v(-24.74, 36.16) * mm, "end": v(-24.84, 36.1) * mm});
            skLineSegment(sketch, "E5590", {"start": v(-24.84, 36.1) * mm, "end": v(-24.94, 36.03) * mm});
            skLineSegment(sketch, "E5591", {"start": v(-24.94, 36.03) * mm, "end": v(-25.03, 35.96) * mm});
            skLineSegment(sketch, "E5592", {"start": v(-25.03, 35.96) * mm, "end": v(-25.13, 35.9) * mm});
            skLineSegment(sketch, "E5593", {"start": v(-25.13, 35.9) * mm, "end": v(-25.14, 35.88) * mm});
            skLineSegment(sketch, "E5594", {"start": v(-25.14, 35.88) * mm, "end": v(-25.23, 35.95) * mm});
            skLineSegment(sketch, "E5595", {"start": v(-25.23, 35.95) * mm, "end": v(-25.32, 36.02) * mm});
            skLineSegment(sketch, "E5596", {"start": v(-25.32, 36.02) * mm, "end": v(-25.4, 36.1) * mm});
            skLineSegment(sketch, "E5597", {"start": v(-25.4, 36.1) * mm, "end": v(-25.5, 36.16) * mm});
            skLineSegment(sketch, "E5598", {"start": v(-25.5, 36.16) * mm, "end": v(-25.6, 36.23) * mm});
            skLineSegment(sketch, "E5599", {"start": v(-25.6, 36.23) * mm, "end": v(-25.7, 36.3) * mm});
            skLineSegment(sketch, "E5600", {"start": v(-25.7, 36.3) * mm, "end": v(-25.8, 36.38) * mm});
            skLineSegment(sketch, "E5601", {"start": v(-25.8, 36.38) * mm, "end": v(-25.91, 36.46) * mm});
            skLineSegment(sketch, "E5602", {"start": v(-25.91, 36.46) * mm, "end": v(-26.01, 36.52) * mm});
            skLineSegment(sketch, "E5603", {"start": v(-26.01, 36.52) * mm, "end": v(-26.12, 36.6) * mm});
            skLineSegment(sketch, "E5604", {"start": v(-26.12, 36.6) * mm, "end": v(-26.2, 36.66) * mm});
            skLineSegment(sketch, "E5605", {"start": v(-26.2, 36.66) * mm, "end": v(-26.3, 36.72) * mm});
            skLineSegment(sketch, "E5606", {"start": v(-26.3, 36.72) * mm, "end": v(-26.4, 36.78) * mm});
            skLineSegment(sketch, "E5607", {"start": v(-26.4, 36.78) * mm, "end": v(-26.5, 36.84) * mm});
            skLineSegment(sketch, "E5608", {"start": v(-26.5, 36.84) * mm, "end": v(-26.6, 36.9) * mm});
            skLineSegment(sketch, "E5609", {"start": v(-26.6, 36.9) * mm, "end": v(-26.7, 36.97) * mm});
            skLineSegment(sketch, "E5610", {"start": v(-26.7, 36.97) * mm, "end": v(-26.81, 37.04) * mm});
            skLineSegment(sketch, "E5611", {"start": v(-26.81, 37.04) * mm, "end": v(-26.92, 37.1) * mm});
            skLineSegment(sketch, "E5612", {"start": v(-26.92, 37.1) * mm, "end": v(-27.03, 37.17) * mm});
            skLineSegment(sketch, "E5613", {"start": v(-27.03, 37.17) * mm, "end": v(-27.03, 37.17) * mm});
            skLineSegment(sketch, "E5614", {"start": v(-27.03, 37.17) * mm, "end": v(-27.13, 37.1) * mm});
            skLineSegment(sketch, "E5615", {"start": v(-27.13, 37.1) * mm, "end": v(-27.22, 37.02) * mm});
            skLineSegment(sketch, "E5616", {"start": v(-27.22, 37.02) * mm, "end": v(-27.31, 36.96) * mm});
            skLineSegment(sketch, "E5617", {"start": v(-27.31, 36.96) * mm, "end": v(-27.4, 36.89) * mm});
            skLineSegment(sketch, "E5618", {"start": v(-27.4, 36.89) * mm, "end": v(-27.49, 36.83) * mm});
            skLineSegment(sketch, "E5619", {"start": v(-27.49, 36.83) * mm, "end": v(-27.46, 36.71) * mm});
            skLineSegment(sketch, "E5620", {"start": v(-27.46, 36.71) * mm, "end": v(-27.43, 36.6) * mm});
            skLineSegment(sketch, "E5621", {"start": v(-27.43, 36.6) * mm, "end": v(-27.4, 36.48) * mm});
            skLineSegment(sketch, "E5622", {"start": v(-27.4, 36.48) * mm, "end": v(-27.37, 36.37) * mm});
            skLineSegment(sketch, "E5623", {"start": v(-27.37, 36.37) * mm, "end": v(-27.34, 36.25) * mm});
            skLineSegment(sketch, "E5624", {"start": v(-27.34, 36.25) * mm, "end": v(-27.31, 36.14) * mm});
            skLineSegment(sketch, "E5625", {"start": v(-27.31, 36.14) * mm, "end": v(-27.28, 36.02) * mm});
            skLineSegment(sketch, "E5626", {"start": v(-27.28, 36.02) * mm, "end": v(-27.25, 35.9) * mm});
            skLineSegment(sketch, "E5627", {"start": v(-27.25, 35.9) * mm, "end": v(-27.21, 35.8) * mm});
            skLineSegment(sketch, "E5628", {"start": v(-27.21, 35.8) * mm, "end": v(-27.18, 35.67) * mm});
            skLineSegment(sketch, "E5629", {"start": v(-27.18, 35.67) * mm, "end": v(-27.14, 35.56) * mm});
            skLineSegment(sketch, "E5630", {"start": v(-27.14, 35.56) * mm, "end": v(-27.1, 35.44) * mm});
            skLineSegment(sketch, "E5631", {"start": v(-27.1, 35.44) * mm, "end": v(-27.07, 35.33) * mm});
            skLineSegment(sketch, "E5632", {"start": v(-27.07, 35.33) * mm, "end": v(-27.03, 35.22) * mm});
            skLineSegment(sketch, "E5633", {"start": v(-27.03, 35.22) * mm, "end": v(-27, 35.1) * mm});
            skLineSegment(sketch, "E5634", {"start": v(-27, 35.1) * mm, "end": v(-26.95, 35) * mm});
            skLineSegment(sketch, "E5635", {"start": v(-26.95, 35) * mm, "end": v(-26.9, 34.88) * mm});
            skLineSegment(sketch, "E5636", {"start": v(-26.9, 34.88) * mm, "end": v(-26.87, 34.77) * mm});
            skLineSegment(sketch, "E5637", {"start": v(-26.87, 34.77) * mm, "end": v(-26.82, 34.65) * mm});
            skLineSegment(sketch, "E5638", {"start": v(-26.82, 34.65) * mm, "end": v(-26.91, 34.57) * mm});
            skLineSegment(sketch, "E5639", {"start": v(-26.91, 34.57) * mm, "end": v(-27, 34.5) * mm});
            skLineSegment(sketch, "E5640", {"start": v(-27, 34.5) * mm, "end": v(-27.1, 34.43) * mm});
            skLineSegment(sketch, "E5641", {"start": v(-27.1, 34.43) * mm, "end": v(-27.2, 34.35) * mm});
            skLineSegment(sketch, "E5642", {"start": v(-27.2, 34.35) * mm, "end": v(-27.29, 34.28) * mm});
            skLineSegment(sketch, "E5643", {"start": v(-27.29, 34.28) * mm, "end": v(-27.38, 34.2) * mm});
            skLineSegment(sketch, "E5644", {"start": v(-27.38, 34.2) * mm, "end": v(-27.47, 34.13) * mm});
            skLineSegment(sketch, "E5645", {"start": v(-27.47, 34.13) * mm, "end": v(-27.49, 34.12) * mm});
            skLineSegment(sketch, "E5646", {"start": v(-27.49, 34.12) * mm, "end": v(-27.57, 34.19) * mm});
            skLineSegment(sketch, "E5647", {"start": v(-27.57, 34.19) * mm, "end": v(-27.67, 34.25) * mm});
            skLineSegment(sketch, "E5648", {"start": v(-27.67, 34.25) * mm, "end": v(-27.76, 34.31) * mm});
            skLineSegment(sketch, "E5649", {"start": v(-27.76, 34.31) * mm, "end": v(-27.86, 34.38) * mm});
            skLineSegment(sketch, "E5650", {"start": v(-27.86, 34.38) * mm, "end": v(-27.96, 34.44) * mm});
            skLineSegment(sketch, "E5651", {"start": v(-27.96, 34.44) * mm, "end": v(-28.07, 34.5) * mm});
            skLineSegment(sketch, "E5652", {"start": v(-28.07, 34.5) * mm, "end": v(-28.18, 34.58) * mm});
            skLineSegment(sketch, "E5653", {"start": v(-28.18, 34.58) * mm, "end": v(-28.3, 34.64) * mm});
            skLineSegment(sketch, "E5654", {"start": v(-28.3, 34.64) * mm, "end": v(-28.4, 34.7) * mm});
            skLineSegment(sketch, "E5655", {"start": v(-28.4, 34.7) * mm, "end": v(-28.5, 34.77) * mm});
            skLineSegment(sketch, "E5656", {"start": v(-28.5, 34.77) * mm, "end": v(-28.6, 34.82) * mm});
            skLineSegment(sketch, "E5657", {"start": v(-28.6, 34.82) * mm, "end": v(-28.7, 34.88) * mm});
            skLineSegment(sketch, "E5658", {"start": v(-28.7, 34.88) * mm, "end": v(-28.8, 34.93) * mm});
            skLineSegment(sketch, "E5659", {"start": v(-28.8, 34.93) * mm, "end": v(-28.9, 35) * mm});
            skLineSegment(sketch, "E5660", {"start": v(-28.9, 35) * mm, "end": v(-29, 35.05) * mm});
            skLineSegment(sketch, "E5661", {"start": v(-29, 35.05) * mm, "end": v(-29.12, 35.1) * mm});
            skLineSegment(sketch, "E5662", {"start": v(-29.12, 35.1) * mm, "end": v(-29.23, 35.16) * mm});
            skLineSegment(sketch, "E5663", {"start": v(-29.23, 35.16) * mm, "end": v(-29.34, 35.22) * mm});
            skLineSegment(sketch, "E5664", {"start": v(-29.34, 35.22) * mm, "end": v(-29.45, 35.28) * mm});
            skLineSegment(sketch, "E5665", {"start": v(-29.45, 35.28) * mm, "end": v(-29.45, 35.28) * mm});
            skLineSegment(sketch, "E5666", {"start": v(-29.45, 35.28) * mm, "end": v(-29.55, 35.2) * mm});
            skLineSegment(sketch, "E5667", {"start": v(-29.55, 35.2) * mm, "end": v(-29.64, 35.12) * mm});
            skLineSegment(sketch, "E5668", {"start": v(-29.64, 35.12) * mm, "end": v(-29.72, 35.05) * mm});
            skLineSegment(sketch, "E5669", {"start": v(-29.72, 35.05) * mm, "end": v(-29.81, 34.98) * mm});
            skLineSegment(sketch, "E5670", {"start": v(-29.81, 34.98) * mm, "end": v(-29.88, 34.91) * mm});
            skLineSegment(sketch, "E5671", {"start": v(-29.88, 34.91) * mm, "end": v(-29.85, 34.8) * mm});
            skLineSegment(sketch, "E5672", {"start": v(-29.85, 34.8) * mm, "end": v(-29.81, 34.68) * mm});
            skLineSegment(sketch, "E5673", {"start": v(-29.81, 34.68) * mm, "end": v(-29.78, 34.57) * mm});
            skLineSegment(sketch, "E5674", {"start": v(-29.78, 34.57) * mm, "end": v(-29.74, 34.46) * mm});
            skLineSegment(sketch, "E5675", {"start": v(-29.74, 34.46) * mm, "end": v(-29.7, 34.35) * mm});
            skLineSegment(sketch, "E5676", {"start": v(-29.7, 34.35) * mm, "end": v(-29.66, 34.23) * mm});
            skLineSegment(sketch, "E5677", {"start": v(-29.66, 34.23) * mm, "end": v(-29.62, 34.12) * mm});
            skLineSegment(sketch, "E5678", {"start": v(-29.62, 34.12) * mm, "end": v(-29.58, 34) * mm});
            skLineSegment(sketch, "E5679", {"start": v(-29.58, 34) * mm, "end": v(-29.54, 33.9) * mm});
            skLineSegment(sketch, "E5680", {"start": v(-29.54, 33.9) * mm, "end": v(-29.5, 33.78) * mm});
            skLineSegment(sketch, "E5681", {"start": v(-29.5, 33.78) * mm, "end": v(-29.46, 33.67) * mm});
            skLineSegment(sketch, "E5682", {"start": v(-29.46, 33.67) * mm, "end": v(-29.41, 33.56) * mm});
            skLineSegment(sketch, "E5683", {"start": v(-29.41, 33.56) * mm, "end": v(-29.37, 33.44) * mm});
            skLineSegment(sketch, "E5684", {"start": v(-29.37, 33.44) * mm, "end": v(-29.32, 33.33) * mm});
            skLineSegment(sketch, "E5685", {"start": v(-29.32, 33.33) * mm, "end": v(-29.27, 33.22) * mm});
            skLineSegment(sketch, "E5686", {"start": v(-29.27, 33.22) * mm, "end": v(-29.23, 33.11) * mm});
            skLineSegment(sketch, "E5687", {"start": v(-29.23, 33.11) * mm, "end": v(-29.18, 33) * mm});
            skLineSegment(sketch, "E5688", {"start": v(-29.18, 33) * mm, "end": v(-29.13, 32.9) * mm});
            skLineSegment(sketch, "E5689", {"start": v(-29.13, 32.9) * mm, "end": v(-29.07, 32.78) * mm});
            skLineSegment(sketch, "E5690", {"start": v(-29.07, 32.78) * mm, "end": v(-29.16, 32.7) * mm});
            skLineSegment(sketch, "E5691", {"start": v(-29.16, 32.7) * mm, "end": v(-29.25, 32.62) * mm});
            skLineSegment(sketch, "E5692", {"start": v(-29.25, 32.62) * mm, "end": v(-29.34, 32.54) * mm});
            skLineSegment(sketch, "E5693", {"start": v(-29.34, 32.54) * mm, "end": v(-29.43, 32.46) * mm});
            skLineSegment(sketch, "E5694", {"start": v(-29.43, 32.46) * mm, "end": v(-29.51, 32.38) * mm});
            skLineSegment(sketch, "E5695", {"start": v(-29.51, 32.38) * mm, "end": v(-29.6, 32.3) * mm});
            skLineSegment(sketch, "E5696", {"start": v(-29.6, 32.3) * mm, "end": v(-29.7, 32.22) * mm});
            skLineSegment(sketch, "E5697", {"start": v(-29.7, 32.22) * mm, "end": v(-29.7, 32.21) * mm});
            skLineSegment(sketch, "E5698", {"start": v(-29.7, 32.21) * mm, "end": v(-29.8, 32.27) * mm});
            skLineSegment(sketch, "E5699", {"start": v(-29.8, 32.27) * mm, "end": v(-29.9, 32.32) * mm});
            skLineSegment(sketch, "E5700", {"start": v(-29.9, 32.32) * mm, "end": v(-30, 32.38) * mm});
            skLineSegment(sketch, "E5701", {"start": v(-30, 32.38) * mm, "end": v(-30.1, 32.44) * mm});
            skLineSegment(sketch, "E5702", {"start": v(-30.1, 32.44) * mm, "end": v(-30.2, 32.5) * mm});
            skLineSegment(sketch, "E5703", {"start": v(-30.2, 32.5) * mm, "end": v(-30.31, 32.56) * mm});
            skLineSegment(sketch, "E5704", {"start": v(-30.31, 32.56) * mm, "end": v(-30.42, 32.62) * mm});
            skLineSegment(sketch, "E5705", {"start": v(-30.42, 32.62) * mm, "end": v(-30.54, 32.68) * mm});
            skLineSegment(sketch, "E5706", {"start": v(-30.54, 32.68) * mm, "end": v(-30.65, 32.73) * mm});
            skLineSegment(sketch, "E5707", {"start": v(-30.65, 32.73) * mm, "end": v(-30.76, 32.79) * mm});
            skLineSegment(sketch, "E5708", {"start": v(-30.76, 32.79) * mm, "end": v(-30.86, 32.84) * mm});
            skLineSegment(sketch, "E5709", {"start": v(-30.86, 32.84) * mm, "end": v(-30.96, 32.88) * mm});
            skLineSegment(sketch, "E5710", {"start": v(-30.96, 32.88) * mm, "end": v(-31.07, 32.93) * mm});
            skLineSegment(sketch, "E5711", {"start": v(-31.07, 32.93) * mm, "end": v(-31.17, 32.98) * mm});
            skLineSegment(sketch, "E5712", {"start": v(-31.17, 32.98) * mm, "end": v(-31.28, 33.03) * mm});
            skLineSegment(sketch, "E5713", {"start": v(-31.28, 33.03) * mm, "end": v(-31.4, 33.08) * mm});
            skLineSegment(sketch, "E5714", {"start": v(-31.4, 33.08) * mm, "end": v(-31.5, 33.13) * mm});
            skLineSegment(sketch, "E5715", {"start": v(-31.5, 33.13) * mm, "end": v(-31.62, 33.18) * mm});
            skLineSegment(sketch, "E5716", {"start": v(-31.62, 33.18) * mm, "end": v(-31.74, 33.23) * mm});
            skLineSegment(sketch, "E5717", {"start": v(-31.74, 33.23) * mm, "end": v(-31.74, 33.23) * mm});
            skLineSegment(sketch, "E5718", {"start": v(-31.74, 33.23) * mm, "end": v(-31.83, 33.15) * mm});
            skLineSegment(sketch, "E5719", {"start": v(-31.83, 33.15) * mm, "end": v(-31.92, 33.07) * mm});
            skLineSegment(sketch, "E5720", {"start": v(-31.92, 33.07) * mm, "end": v(-32, 33) * mm});
            skLineSegment(sketch, "E5721", {"start": v(-32, 33) * mm, "end": v(-32.08, 32.9) * mm});
            skLineSegment(sketch, "E5722", {"start": v(-32.08, 32.9) * mm, "end": v(-32.15, 32.84) * mm});
            skLineSegment(sketch, "E5723", {"start": v(-32.15, 32.84) * mm, "end": v(-32.1, 32.73) * mm});
            skLineSegment(sketch, "E5724", {"start": v(-32.1, 32.73) * mm, "end": v(-32.06, 32.61) * mm});
            skLineSegment(sketch, "E5725", {"start": v(-32.06, 32.61) * mm, "end": v(-32.02, 32.5) * mm});
            skLineSegment(sketch, "E5726", {"start": v(-32.02, 32.5) * mm, "end": v(-31.98, 32.4) * mm});
            skLineSegment(sketch, "E5727", {"start": v(-31.98, 32.4) * mm, "end": v(-31.93, 32.29) * mm});
            skLineSegment(sketch, "E5728", {"start": v(-31.93, 32.29) * mm, "end": v(-31.88, 32.18) * mm});
            skLineSegment(sketch, "E5729", {"start": v(-31.88, 32.18) * mm, "end": v(-31.84, 32.07) * mm});
            skLineSegment(sketch, "E5730", {"start": v(-31.84, 32.07) * mm, "end": v(-31.79, 31.96) * mm});
            skLineSegment(sketch, "E5731", {"start": v(-31.79, 31.96) * mm, "end": v(-31.74, 31.85) * mm});
            skLineSegment(sketch, "E5732", {"start": v(-31.74, 31.85) * mm, "end": v(-31.69, 31.73) * mm});
            skLineSegment(sketch, "E5733", {"start": v(-31.69, 31.73) * mm, "end": v(-31.64, 31.62) * mm});
            skLineSegment(sketch, "E5734", {"start": v(-31.64, 31.62) * mm, "end": v(-31.59, 31.52) * mm});
            skLineSegment(sketch, "E5735", {"start": v(-31.59, 31.52) * mm, "end": v(-31.53, 31.4) * mm});
            skLineSegment(sketch, "E5736", {"start": v(-31.53, 31.4) * mm, "end": v(-31.48, 31.3) * mm});
            skLineSegment(sketch, "E5737", {"start": v(-31.48, 31.3) * mm, "end": v(-31.43, 31.2) * mm});
            skLineSegment(sketch, "E5738", {"start": v(-31.43, 31.2) * mm, "end": v(-31.37, 31.09) * mm});
            skLineSegment(sketch, "E5739", {"start": v(-31.37, 31.09) * mm, "end": v(-31.32, 30.98) * mm});
            skLineSegment(sketch, "E5740", {"start": v(-31.32, 30.98) * mm, "end": v(-31.26, 30.88) * mm});
            skLineSegment(sketch, "E5741", {"start": v(-31.26, 30.88) * mm, "end": v(-31.2, 30.76) * mm});
            skLineSegment(sketch, "E5742", {"start": v(-31.2, 30.76) * mm, "end": v(-31.28, 30.68) * mm});
            skLineSegment(sketch, "E5743", {"start": v(-31.28, 30.68) * mm, "end": v(-31.36, 30.6) * mm});
            skLineSegment(sketch, "E5744", {"start": v(-31.36, 30.6) * mm, "end": v(-31.45, 30.5) * mm});
            skLineSegment(sketch, "E5745", {"start": v(-31.45, 30.5) * mm, "end": v(-31.53, 30.42) * mm});
            skLineSegment(sketch, "E5746", {"start": v(-31.53, 30.42) * mm, "end": v(-31.61, 30.34) * mm});
            skLineSegment(sketch, "E5747", {"start": v(-31.61, 30.34) * mm, "end": v(-31.7, 30.25) * mm});
            skLineSegment(sketch, "E5748", {"start": v(-31.7, 30.25) * mm, "end": v(-31.78, 30.17) * mm});
            skLineSegment(sketch, "E5749", {"start": v(-31.78, 30.17) * mm, "end": v(-31.79, 30.16) * mm});
            skLineSegment(sketch, "E5750", {"start": v(-31.79, 30.16) * mm, "end": v(-31.88, 30.2) * mm});
            skLineSegment(sketch, "E5751", {"start": v(-31.88, 30.2) * mm, "end": v(-31.98, 30.26) * mm});
            skLineSegment(sketch, "E5752", {"start": v(-31.98, 30.26) * mm, "end": v(-32.09, 30.3) * mm});
            skLineSegment(sketch, "E5753", {"start": v(-32.09, 30.3) * mm, "end": v(-32.2, 30.36) * mm});
            skLineSegment(sketch, "E5754", {"start": v(-32.2, 30.36) * mm, "end": v(-32.3, 30.4) * mm});
            skLineSegment(sketch, "E5755", {"start": v(-32.3, 30.4) * mm, "end": v(-32.42, 30.46) * mm});
            skLineSegment(sketch, "E5756", {"start": v(-32.42, 30.46) * mm, "end": v(-32.54, 30.51) * mm});
            skLineSegment(sketch, "E5757", {"start": v(-32.54, 30.51) * mm, "end": v(-32.66, 30.56) * mm});
            skLineSegment(sketch, "E5758", {"start": v(-32.66, 30.56) * mm, "end": v(-32.77, 30.61) * mm});
            skLineSegment(sketch, "E5759", {"start": v(-32.77, 30.61) * mm, "end": v(-32.88, 30.66) * mm});
            skLineSegment(sketch, "E5760", {"start": v(-32.88, 30.66) * mm, "end": v(-32.98, 30.7) * mm});
            skLineSegment(sketch, "E5761", {"start": v(-32.98, 30.7) * mm, "end": v(-33.09, 30.74) * mm});
            skLineSegment(sketch, "E5762", {"start": v(-33.09, 30.74) * mm, "end": v(-33.2, 30.78) * mm});
            skLineSegment(sketch, "E5763", {"start": v(-33.2, 30.78) * mm, "end": v(-33.3, 30.83) * mm});
            skLineSegment(sketch, "E5764", {"start": v(-33.3, 30.83) * mm, "end": v(-33.42, 30.87) * mm});
            skLineSegment(sketch, "E5765", {"start": v(-33.42, 30.87) * mm, "end": v(-33.53, 30.91) * mm});
            skLineSegment(sketch, "E5766", {"start": v(-33.53, 30.91) * mm, "end": v(-33.65, 30.95) * mm});
            skLineSegment(sketch, "E5767", {"start": v(-33.65, 30.95) * mm, "end": v(-33.77, 31) * mm});
            skLineSegment(sketch, "E5768", {"start": v(-33.77, 31) * mm, "end": v(-33.9, 31.04) * mm});
            skLineSegment(sketch, "E5769", {"start": v(-33.9, 31.04) * mm, "end": v(-33.9, 31.04) * mm});
            skLineSegment(sketch, "E5770", {"start": v(-33.9, 31.04) * mm, "end": v(-33.97, 30.95) * mm});
            skLineSegment(sketch, "E5771", {"start": v(-33.97, 30.95) * mm, "end": v(-34.05, 30.86) * mm});
            skLineSegment(sketch, "E5772", {"start": v(-34.05, 30.86) * mm, "end": v(-34.13, 30.78) * mm});
            skLineSegment(sketch, "E5773", {"start": v(-34.13, 30.78) * mm, "end": v(-34.2, 30.7) * mm});
            skLineSegment(sketch, "E5774", {"start": v(-34.2, 30.7) * mm, "end": v(-34.27, 30.62) * mm});
            skLineSegment(sketch, "E5775", {"start": v(-34.27, 30.62) * mm, "end": v(-34.22, 30.5) * mm});
            skLineSegment(sketch, "E5776", {"start": v(-34.22, 30.5) * mm, "end": v(-34.17, 30.4) * mm});
            skLineSegment(sketch, "E5777", {"start": v(-34.17, 30.4) * mm, "end": v(-34.12, 30.3) * mm});
            skLineSegment(sketch, "E5778", {"start": v(-34.12, 30.3) * mm, "end": v(-34.07, 30.19) * mm});
            skLineSegment(sketch, "E5779", {"start": v(-34.07, 30.19) * mm, "end": v(-34.02, 30.08) * mm});
            skLineSegment(sketch, "E5780", {"start": v(-34.02, 30.08) * mm, "end": v(-33.96, 29.97) * mm});
            skLineSegment(sketch, "E5781", {"start": v(-33.96, 29.97) * mm, "end": v(-33.9, 29.87) * mm});
            skLineSegment(sketch, "E5782", {"start": v(-33.9, 29.87) * mm, "end": v(-33.85, 29.76) * mm});
            skLineSegment(sketch, "E5783", {"start": v(-33.85, 29.76) * mm, "end": v(-33.8, 29.66) * mm});
            skLineSegment(sketch, "E5784", {"start": v(-33.8, 29.66) * mm, "end": v(-33.74, 29.54) * mm});
            skLineSegment(sketch, "E5785", {"start": v(-33.74, 29.54) * mm, "end": v(-33.68, 29.44) * mm});
            skLineSegment(sketch, "E5786", {"start": v(-33.68, 29.44) * mm, "end": v(-33.62, 29.34) * mm});
            skLineSegment(sketch, "E5787", {"start": v(-33.62, 29.34) * mm, "end": v(-33.56, 29.23) * mm});
            skLineSegment(sketch, "E5788", {"start": v(-33.56, 29.23) * mm, "end": v(-33.5, 29.13) * mm});
            skLineSegment(sketch, "E5789", {"start": v(-33.5, 29.13) * mm, "end": v(-33.44, 29.03) * mm});
            skLineSegment(sketch, "E5790", {"start": v(-33.44, 29.03) * mm, "end": v(-33.38, 28.92) * mm});
            skLineSegment(sketch, "E5791", {"start": v(-33.38, 28.92) * mm, "end": v(-33.32, 28.82) * mm});
            skLineSegment(sketch, "E5792", {"start": v(-33.32, 28.82) * mm, "end": v(-33.25, 28.72) * mm});
            skLineSegment(sketch, "E5793", {"start": v(-33.25, 28.72) * mm, "end": v(-33.18, 28.6) * mm});
            skLineSegment(sketch, "E5794", {"start": v(-33.18, 28.6) * mm, "end": v(-33.26, 28.52) * mm});
            skLineSegment(sketch, "E5795", {"start": v(-33.26, 28.52) * mm, "end": v(-33.34, 28.43) * mm});
            skLineSegment(sketch, "E5796", {"start": v(-33.34, 28.43) * mm, "end": v(-33.41, 28.34) * mm});
            skLineSegment(sketch, "E5797", {"start": v(-33.41, 28.34) * mm, "end": v(-33.49, 28.25) * mm});
            skLineSegment(sketch, "E5798", {"start": v(-33.49, 28.25) * mm, "end": v(-33.57, 28.16) * mm});
            skLineSegment(sketch, "E5799", {"start": v(-33.57, 28.16) * mm, "end": v(-33.64, 28.07) * mm});
            skLineSegment(sketch, "E5800", {"start": v(-33.64, 28.07) * mm, "end": v(-33.72, 27.98) * mm});
            skLineSegment(sketch, "E5801", {"start": v(-33.72, 27.98) * mm, "end": v(-33.73, 27.97) * mm});
            skLineSegment(sketch, "E5802", {"start": v(-33.73, 27.97) * mm, "end": v(-33.83, 28) * mm});
            skLineSegment(sketch, "E5803", {"start": v(-33.83, 28) * mm, "end": v(-33.93, 28.05) * mm});
            skLineSegment(sketch, "E5804", {"start": v(-33.93, 28.05) * mm, "end": v(-34.04, 28.1) * mm});
            skLineSegment(sketch, "E5805", {"start": v(-34.04, 28.1) * mm, "end": v(-34.15, 28.14) * mm});
            skLineSegment(sketch, "E5806", {"start": v(-34.15, 28.14) * mm, "end": v(-34.26, 28.18) * mm});
            skLineSegment(sketch, "E5807", {"start": v(-34.26, 28.18) * mm, "end": v(-34.38, 28.23) * mm});
            skLineSegment(sketch, "E5808", {"start": v(-34.38, 28.23) * mm, "end": v(-34.5, 28.27) * mm});
            skLineSegment(sketch, "E5809", {"start": v(-34.5, 28.27) * mm, "end": v(-34.62, 28.31) * mm});
            skLineSegment(sketch, "E5810", {"start": v(-34.62, 28.31) * mm, "end": v(-34.74, 28.35) * mm});
            skLineSegment(sketch, "E5811", {"start": v(-34.74, 28.35) * mm, "end": v(-34.85, 28.4) * mm});
            skLineSegment(sketch, "E5812", {"start": v(-34.85, 28.4) * mm, "end": v(-34.96, 28.43) * mm});
            skLineSegment(sketch, "E5813", {"start": v(-34.96, 28.43) * mm, "end": v(-35.07, 28.46) * mm});
            skLineSegment(sketch, "E5814", {"start": v(-35.07, 28.46) * mm, "end": v(-35.18, 28.5) * mm});
            skLineSegment(sketch, "E5815", {"start": v(-35.18, 28.5) * mm, "end": v(-35.3, 28.53) * mm});
            skLineSegment(sketch, "E5816", {"start": v(-35.3, 28.53) * mm, "end": v(-35.4, 28.57) * mm});
            skLineSegment(sketch, "E5817", {"start": v(-35.4, 28.57) * mm, "end": v(-35.52, 28.6) * mm});
            skLineSegment(sketch, "E5818", {"start": v(-35.52, 28.6) * mm, "end": v(-35.64, 28.64) * mm});
            skLineSegment(sketch, "E5819", {"start": v(-35.64, 28.64) * mm, "end": v(-35.76, 28.67) * mm});
            skLineSegment(sketch, "E5820", {"start": v(-35.76, 28.67) * mm, "end": v(-35.89, 28.7) * mm});
            skLineSegment(sketch, "E5821", {"start": v(-35.89, 28.7) * mm, "end": v(-35.89, 28.7) * mm});
            skLineSegment(sketch, "E5822", {"start": v(-35.89, 28.7) * mm, "end": v(-35.96, 28.61) * mm});
            skLineSegment(sketch, "E5823", {"start": v(-35.96, 28.61) * mm, "end": v(-36.04, 28.52) * mm});
            skLineSegment(sketch, "E5824", {"start": v(-36.04, 28.52) * mm, "end": v(-36.1, 28.43) * mm});
            skLineSegment(sketch, "E5825", {"start": v(-36.1, 28.43) * mm, "end": v(-36.18, 28.34) * mm});
            skLineSegment(sketch, "E5826", {"start": v(-36.18, 28.34) * mm, "end": v(-36.24, 28.26) * mm});
            skLineSegment(sketch, "E5827", {"start": v(-36.24, 28.26) * mm, "end": v(-36.18, 28.16) * mm});
            skLineSegment(sketch, "E5828", {"start": v(-36.18, 28.16) * mm, "end": v(-36.12, 28.05) * mm});
            skLineSegment(sketch, "E5829", {"start": v(-36.12, 28.05) * mm, "end": v(-36.06, 27.94) * mm});
            skLineSegment(sketch, "E5830", {"start": v(-36.06, 27.94) * mm, "end": v(-36, 27.85) * mm});
            skLineSegment(sketch, "E5831", {"start": v(-36, 27.85) * mm, "end": v(-35.95, 27.74) * mm});
            skLineSegment(sketch, "E5832", {"start": v(-35.95, 27.74) * mm, "end": v(-35.89, 27.64) * mm});
            skLineSegment(sketch, "E5833", {"start": v(-35.89, 27.64) * mm, "end": v(-35.83, 27.54) * mm});
            skLineSegment(sketch, "E5834", {"start": v(-35.83, 27.54) * mm, "end": v(-35.76, 27.43) * mm});
            skLineSegment(sketch, "E5835", {"start": v(-35.76, 27.43) * mm, "end": v(-35.7, 27.33) * mm});
            skLineSegment(sketch, "E5836", {"start": v(-35.7, 27.33) * mm, "end": v(-35.63, 27.23) * mm});
            skLineSegment(sketch, "E5837", {"start": v(-35.63, 27.23) * mm, "end": v(-35.57, 27.12) * mm});
            skLineSegment(sketch, "E5838", {"start": v(-35.57, 27.12) * mm, "end": v(-35.5, 27.02) * mm});
            skLineSegment(sketch, "E5839", {"start": v(-35.5, 27.02) * mm, "end": v(-35.44, 26.92) * mm});
            skLineSegment(sketch, "E5840", {"start": v(-35.44, 26.92) * mm, "end": v(-35.37, 26.83) * mm});
            skLineSegment(sketch, "E5841", {"start": v(-35.37, 26.83) * mm, "end": v(-35.3, 26.73) * mm});
            skLineSegment(sketch, "E5842", {"start": v(-35.3, 26.73) * mm, "end": v(-35.24, 26.63) * mm});
            skLineSegment(sketch, "E5843", {"start": v(-35.24, 26.63) * mm, "end": v(-35.17, 26.53) * mm});
            skLineSegment(sketch, "E5844", {"start": v(-35.17, 26.53) * mm, "end": v(-35.1, 26.43) * mm});
            skLineSegment(sketch, "E5845", {"start": v(-35.1, 26.43) * mm, "end": v(-35.02, 26.33) * mm});
            skLineSegment(sketch, "E5846", {"start": v(-35.02, 26.33) * mm, "end": v(-35.1, 26.23) * mm});
            skLineSegment(sketch, "E5847", {"start": v(-35.1, 26.23) * mm, "end": v(-35.16, 26.14) * mm});
            skLineSegment(sketch, "E5848", {"start": v(-35.16, 26.14) * mm, "end": v(-35.23, 26.04) * mm});
            skLineSegment(sketch, "E5849", {"start": v(-35.23, 26.04) * mm, "end": v(-35.3, 25.95) * mm});
            skLineSegment(sketch, "E5850", {"start": v(-35.3, 25.95) * mm, "end": v(-35.37, 25.85) * mm});
            skLineSegment(sketch, "E5851", {"start": v(-35.37, 25.85) * mm, "end": v(-35.44, 25.76) * mm});
            skLineSegment(sketch, "E5852", {"start": v(-35.44, 25.76) * mm, "end": v(-35.51, 25.66) * mm});
            skLineSegment(sketch, "E5853", {"start": v(-35.51, 25.66) * mm, "end": v(-35.52, 25.65) * mm});
            skLineSegment(sketch, "E5854", {"start": v(-35.52, 25.65) * mm, "end": v(-35.63, 25.69) * mm});
            skLineSegment(sketch, "E5855", {"start": v(-35.63, 25.69) * mm, "end": v(-35.73, 25.72) * mm});
            skLineSegment(sketch, "E5856", {"start": v(-35.73, 25.72) * mm, "end": v(-35.84, 25.76) * mm});
            skLineSegment(sketch, "E5857", {"start": v(-35.84, 25.76) * mm, "end": v(-35.95, 25.8) * mm});
            skLineSegment(sketch, "E5858", {"start": v(-35.95, 25.8) * mm, "end": v(-36.07, 25.83) * mm});
            skLineSegment(sketch, "E5859", {"start": v(-36.07, 25.83) * mm, "end": v(-36.19, 25.87) * mm});
            skLineSegment(sketch, "E5860", {"start": v(-36.19, 25.87) * mm, "end": v(-36.31, 25.9) * mm});
            skLineSegment(sketch, "E5861", {"start": v(-36.31, 25.9) * mm, "end": v(-36.44, 25.94) * mm});
            skLineSegment(sketch, "E5862", {"start": v(-36.44, 25.94) * mm, "end": v(-36.55, 25.97) * mm});
            skLineSegment(sketch, "E5863", {"start": v(-36.55, 25.97) * mm, "end": v(-36.67, 26) * mm});
            skLineSegment(sketch, "E5864", {"start": v(-36.67, 26) * mm, "end": v(-36.78, 26.03) * mm});
            skLineSegment(sketch, "E5865", {"start": v(-36.78, 26.03) * mm, "end": v(-36.9, 26.06) * mm});
            skLineSegment(sketch, "E5866", {"start": v(-36.9, 26.06) * mm, "end": v(-37, 26.09) * mm});
            skLineSegment(sketch, "E5867", {"start": v(-37, 26.09) * mm, "end": v(-37.12, 26.11) * mm});
            skLineSegment(sketch, "E5868", {"start": v(-37.12, 26.11) * mm, "end": v(-37.24, 26.14) * mm});
            skLineSegment(sketch, "E5869", {"start": v(-37.24, 26.14) * mm, "end": v(-37.35, 26.17) * mm});
            skLineSegment(sketch, "E5870", {"start": v(-37.35, 26.17) * mm, "end": v(-37.48, 26.2) * mm});
            skLineSegment(sketch, "E5871", {"start": v(-37.48, 26.2) * mm, "end": v(-37.6, 26.22) * mm});
            skLineSegment(sketch, "E5872", {"start": v(-37.6, 26.22) * mm, "end": v(-37.72, 26.24) * mm});
            skLineSegment(sketch, "E5873", {"start": v(-37.72, 26.24) * mm, "end": v(-37.73, 26.24) * mm});
            skLineSegment(sketch, "E5874", {"start": v(-37.73, 26.24) * mm, "end": v(-37.8, 26.14) * mm});
            skLineSegment(sketch, "E5875", {"start": v(-37.8, 26.14) * mm, "end": v(-37.86, 26.05) * mm});
            skLineSegment(sketch, "E5876", {"start": v(-37.86, 26.05) * mm, "end": v(-37.92, 25.96) * mm});
            skLineSegment(sketch, "E5877", {"start": v(-37.92, 25.96) * mm, "end": v(-38, 25.86) * mm});
            skLineSegment(sketch, "E5878", {"start": v(-38, 25.86) * mm, "end": v(-38.05, 25.78) * mm});
            skLineSegment(sketch, "E5879", {"start": v(-38.05, 25.78) * mm, "end": v(-37.98, 25.68) * mm});
            skLineSegment(sketch, "E5880", {"start": v(-37.98, 25.68) * mm, "end": v(-37.92, 25.57) * mm});
            skLineSegment(sketch, "E5881", {"start": v(-37.92, 25.57) * mm, "end": v(-37.85, 25.47) * mm});
            skLineSegment(sketch, "E5882", {"start": v(-37.85, 25.47) * mm, "end": v(-37.79, 25.38) * mm});
            skLineSegment(sketch, "E5883", {"start": v(-37.79, 25.38) * mm, "end": v(-37.72, 25.28) * mm});
            skLineSegment(sketch, "E5884", {"start": v(-37.72, 25.28) * mm, "end": v(-37.65, 25.18) * mm});
            skLineSegment(sketch, "E5885", {"start": v(-37.65, 25.18) * mm, "end": v(-37.59, 25.08) * mm});
            skLineSegment(sketch, "E5886", {"start": v(-37.59, 25.08) * mm, "end": v(-37.52, 24.98) * mm});
            skLineSegment(sketch, "E5887", {"start": v(-37.52, 24.98) * mm, "end": v(-37.45, 24.89) * mm});
            skLineSegment(sketch, "E5888", {"start": v(-37.45, 24.89) * mm, "end": v(-37.37, 24.78) * mm});
            skLineSegment(sketch, "E5889", {"start": v(-37.37, 24.78) * mm, "end": v(-37.3, 24.69) * mm});
            skLineSegment(sketch, "E5890", {"start": v(-37.3, 24.69) * mm, "end": v(-37.23, 24.6) * mm});
            skLineSegment(sketch, "E5891", {"start": v(-37.23, 24.6) * mm, "end": v(-37.16, 24.5) * mm});
            skLineSegment(sketch, "E5892", {"start": v(-37.16, 24.5) * mm, "end": v(-37.08, 24.4) * mm});
            skLineSegment(sketch, "E5893", {"start": v(-37.08, 24.4) * mm, "end": v(-37.01, 24.3) * mm});
            skLineSegment(sketch, "E5894", {"start": v(-37.01, 24.3) * mm, "end": v(-36.94, 24.22) * mm});
            skLineSegment(sketch, "E5895", {"start": v(-36.94, 24.22) * mm, "end": v(-36.86, 24.12) * mm});
            skLineSegment(sketch, "E5896", {"start": v(-36.86, 24.12) * mm, "end": v(-36.78, 24.03) * mm});
            skLineSegment(sketch, "E5897", {"start": v(-36.78, 24.03) * mm, "end": v(-36.7, 23.93) * mm});
            skLineSegment(sketch, "E5898", {"start": v(-36.7, 23.93) * mm, "end": v(-36.76, 23.83) * mm});
            skLineSegment(sketch, "E5899", {"start": v(-36.76, 23.83) * mm, "end": v(-36.83, 23.73) * mm});
            skLineSegment(sketch, "E5900", {"start": v(-36.83, 23.73) * mm, "end": v(-36.9, 23.63) * mm});
            skLineSegment(sketch, "E5901", {"start": v(-36.9, 23.63) * mm, "end": v(-36.96, 23.53) * mm});
            skLineSegment(sketch, "E5902", {"start": v(-36.96, 23.53) * mm, "end": v(-37.02, 23.43) * mm});
            skLineSegment(sketch, "E5903", {"start": v(-37.02, 23.43) * mm, "end": v(-37.08, 23.33) * mm});
            skLineSegment(sketch, "E5904", {"start": v(-37.08, 23.33) * mm, "end": v(-37.15, 23.23) * mm});
            skLineSegment(sketch, "E5905", {"start": v(-37.15, 23.23) * mm, "end": v(-37.16, 23.22) * mm});
            skLineSegment(sketch, "E5906", {"start": v(-37.16, 23.22) * mm, "end": v(-37.26, 23.25) * mm});
            skLineSegment(sketch, "E5907", {"start": v(-37.26, 23.25) * mm, "end": v(-37.37, 23.28) * mm});
            skLineSegment(sketch, "E5908", {"start": v(-37.37, 23.28) * mm, "end": v(-37.48, 23.3) * mm});
            skLineSegment(sketch, "E5909", {"start": v(-37.48, 23.3) * mm, "end": v(-37.6, 23.34) * mm});
            skLineSegment(sketch, "E5910", {"start": v(-37.6, 23.34) * mm, "end": v(-37.71, 23.36) * mm});
            skLineSegment(sketch, "E5911", {"start": v(-37.71, 23.36) * mm, "end": v(-37.84, 23.4) * mm});
            skLineSegment(sketch, "E5912", {"start": v(-37.84, 23.4) * mm, "end": v(-37.96, 23.42) * mm});
            skLineSegment(sketch, "E5913", {"start": v(-37.96, 23.42) * mm, "end": v(-38.09, 23.45) * mm});
            skLineSegment(sketch, "E5914", {"start": v(-38.09, 23.45) * mm, "end": v(-38.2, 23.47) * mm});
            skLineSegment(sketch, "E5915", {"start": v(-38.2, 23.47) * mm, "end": v(-38.33, 23.5) * mm});
            skLineSegment(sketch, "E5916", {"start": v(-38.33, 23.5) * mm, "end": v(-38.44, 23.52) * mm});
            skLineSegment(sketch, "E5917", {"start": v(-38.44, 23.52) * mm, "end": v(-38.55, 23.54) * mm});
            skLineSegment(sketch, "E5918", {"start": v(-38.55, 23.54) * mm, "end": v(-38.66, 23.56) * mm});
            skLineSegment(sketch, "E5919", {"start": v(-38.66, 23.56) * mm, "end": v(-38.78, 23.58) * mm});
            skLineSegment(sketch, "E5920", {"start": v(-38.78, 23.58) * mm, "end": v(-38.9, 23.6) * mm});
            skLineSegment(sketch, "E5921", {"start": v(-38.9, 23.6) * mm, "end": v(-39.02, 23.61) * mm});
            skLineSegment(sketch, "E5922", {"start": v(-39.02, 23.61) * mm, "end": v(-39.14, 23.63) * mm});
            skLineSegment(sketch, "E5923", {"start": v(-39.14, 23.63) * mm, "end": v(-39.27, 23.65) * mm});
            skLineSegment(sketch, "E5924", {"start": v(-39.27, 23.65) * mm, "end": v(-39.4, 23.66) * mm});
            skLineSegment(sketch, "E5925", {"start": v(-39.4, 23.66) * mm, "end": v(-39.4, 23.66) * mm});
            skLineSegment(sketch, "E5926", {"start": v(-39.4, 23.66) * mm, "end": v(-39.46, 23.56) * mm});
            skLineSegment(sketch, "E5927", {"start": v(-39.46, 23.56) * mm, "end": v(-39.52, 23.46) * mm});
            skLineSegment(sketch, "E5928", {"start": v(-39.52, 23.46) * mm, "end": v(-39.57, 23.37) * mm});
            skLineSegment(sketch, "E5929", {"start": v(-39.57, 23.37) * mm, "end": v(-39.63, 23.26) * mm});
            skLineSegment(sketch, "E5930", {"start": v(-39.63, 23.26) * mm, "end": v(-39.68, 23.18) * mm});
            skLineSegment(sketch, "E5931", {"start": v(-39.68, 23.18) * mm, "end": v(-39.61, 23.08) * mm});
            skLineSegment(sketch, "E5932", {"start": v(-39.61, 23.08) * mm, "end": v(-39.54, 22.98) * mm});
            skLineSegment(sketch, "E5933", {"start": v(-39.54, 22.98) * mm, "end": v(-39.47, 22.89) * mm});
            skLineSegment(sketch, "E5934", {"start": v(-39.47, 22.89) * mm, "end": v(-39.4, 22.8) * mm});
            skLineSegment(sketch, "E5935", {"start": v(-39.4, 22.8) * mm, "end": v(-39.32, 22.7) * mm});
            skLineSegment(sketch, "E5936", {"start": v(-39.32, 22.7) * mm, "end": v(-39.25, 22.6) * mm});
            skLineSegment(sketch, "E5937", {"start": v(-39.25, 22.6) * mm, "end": v(-39.18, 22.52) * mm});
            skLineSegment(sketch, "E5938", {"start": v(-39.18, 22.52) * mm, "end": v(-39.1, 22.42) * mm});
            skLineSegment(sketch, "E5939", {"start": v(-39.1, 22.42) * mm, "end": v(-39.03, 22.33) * mm});
            skLineSegment(sketch, "E5940", {"start": v(-39.03, 22.33) * mm, "end": v(-38.95, 22.23) * mm});
            skLineSegment(sketch, "E5941", {"start": v(-38.95, 22.23) * mm, "end": v(-38.87, 22.14) * mm});
            skLineSegment(sketch, "E5942", {"start": v(-38.87, 22.14) * mm, "end": v(-38.79, 22.05) * mm});
            skLineSegment(sketch, "E5943", {"start": v(-38.79, 22.05) * mm, "end": v(-38.71, 21.96) * mm});
            skLineSegment(sketch, "E5944", {"start": v(-38.71, 21.96) * mm, "end": v(-38.63, 21.87) * mm});
            skLineSegment(sketch, "E5945", {"start": v(-38.63, 21.87) * mm, "end": v(-38.55, 21.78) * mm});
            skLineSegment(sketch, "E5946", {"start": v(-38.55, 21.78) * mm, "end": v(-38.47, 21.7) * mm});
            skLineSegment(sketch, "E5947", {"start": v(-38.47, 21.7) * mm, "end": v(-38.39, 21.6) * mm});
            skLineSegment(sketch, "E5948", {"start": v(-38.39, 21.6) * mm, "end": v(-38.3, 21.52) * mm});
            skLineSegment(sketch, "E5949", {"start": v(-38.3, 21.52) * mm, "end": v(-38.22, 21.43) * mm});
            skLineSegment(sketch, "E5950", {"start": v(-38.22, 21.43) * mm, "end": v(-38.27, 21.32) * mm});
            skLineSegment(sketch, "E5951", {"start": v(-38.27, 21.32) * mm, "end": v(-38.33, 21.22) * mm});
            skLineSegment(sketch, "E5952", {"start": v(-38.33, 21.22) * mm, "end": v(-38.39, 21.12) * mm});
            skLineSegment(sketch, "E5953", {"start": v(-38.39, 21.12) * mm, "end": v(-38.44, 21.01) * mm});
            skLineSegment(sketch, "E5954", {"start": v(-38.44, 21.01) * mm, "end": v(-38.5, 20.9) * mm});
            skLineSegment(sketch, "E5955", {"start": v(-38.5, 20.9) * mm, "end": v(-38.56, 20.8) * mm});
            skLineSegment(sketch, "E5956", {"start": v(-38.56, 20.8) * mm, "end": v(-38.62, 20.7) * mm});
            skLineSegment(sketch, "E5957", {"start": v(-38.62, 20.7) * mm, "end": v(-38.62, 20.69) * mm});
            skLineSegment(sketch, "E5958", {"start": v(-38.62, 20.69) * mm, "end": v(-38.73, 20.7) * mm});
            skLineSegment(sketch, "E5959", {"start": v(-38.73, 20.7) * mm, "end": v(-38.84, 20.73) * mm});
            skLineSegment(sketch, "E5960", {"start": v(-38.84, 20.73) * mm, "end": v(-38.95, 20.75) * mm});
            skLineSegment(sketch, "E5961", {"start": v(-38.95, 20.75) * mm, "end": v(-39.07, 20.77) * mm});
            skLineSegment(sketch, "E5962", {"start": v(-39.07, 20.77) * mm, "end": v(-39.19, 20.8) * mm});
            skLineSegment(sketch, "E5963", {"start": v(-39.19, 20.8) * mm, "end": v(-39.31, 20.81) * mm});
            skLineSegment(sketch, "E5964", {"start": v(-39.31, 20.81) * mm, "end": v(-39.44, 20.83) * mm});
            skLineSegment(sketch, "E5965", {"start": v(-39.44, 20.83) * mm, "end": v(-39.57, 20.85) * mm});
            skLineSegment(sketch, "E5966", {"start": v(-39.57, 20.85) * mm, "end": v(-39.69, 20.87) * mm});
            skLineSegment(sketch, "E5967", {"start": v(-39.69, 20.87) * mm, "end": v(-39.81, 20.88) * mm});
            skLineSegment(sketch, "E5968", {"start": v(-39.81, 20.88) * mm, "end": v(-39.92, 20.9) * mm});
            skLineSegment(sketch, "E5969", {"start": v(-39.92, 20.9) * mm, "end": v(-40.03, 20.9) * mm});
            skLineSegment(sketch, "E5970", {"start": v(-40.03, 20.9) * mm, "end": v(-40.15, 20.92) * mm});
            skLineSegment(sketch, "E5971", {"start": v(-40.15, 20.92) * mm, "end": v(-40.27, 20.93) * mm});
            skLineSegment(sketch, "E5972", {"start": v(-40.27, 20.93) * mm, "end": v(-40.39, 20.94) * mm});
            skLineSegment(sketch, "E5973", {"start": v(-40.39, 20.94) * mm, "end": v(-40.5, 20.95) * mm});
            skLineSegment(sketch, "E5974", {"start": v(-40.5, 20.95) * mm, "end": v(-40.63, 20.96) * mm});
            skLineSegment(sketch, "E5975", {"start": v(-40.63, 20.96) * mm, "end": v(-40.76, 20.97) * mm});
            skLineSegment(sketch, "E5976", {"start": v(-40.76, 20.97) * mm, "end": v(-40.89, 20.98) * mm});
            skLineSegment(sketch, "E5977", {"start": v(-40.89, 20.98) * mm, "end": v(-40.89, 20.98) * mm});
            skLineSegment(sketch, "E5978", {"start": v(-40.89, 20.98) * mm, "end": v(-40.94, 20.87) * mm});
            skLineSegment(sketch, "E5979", {"start": v(-40.94, 20.87) * mm, "end": v(-41, 20.77) * mm});
            skLineSegment(sketch, "E5980", {"start": v(-41, 20.77) * mm, "end": v(-41.04, 20.67) * mm});
            skLineSegment(sketch, "E5981", {"start": v(-41.04, 20.67) * mm, "end": v(-41.1, 20.56) * mm});
            skLineSegment(sketch, "E5982", {"start": v(-41.1, 20.56) * mm, "end": v(-41.14, 20.48) * mm});
            skLineSegment(sketch, "E5983", {"start": v(-41.14, 20.48) * mm, "end": v(-41.06, 20.39) * mm});
            skLineSegment(sketch, "E5984", {"start": v(-41.06, 20.39) * mm, "end": v(-40.99, 20.3) * mm});
            skLineSegment(sketch, "E5985", {"start": v(-40.99, 20.3) * mm, "end": v(-40.9, 20.2) * mm});
            skLineSegment(sketch, "E5986", {"start": v(-40.9, 20.2) * mm, "end": v(-40.83, 20.12) * mm});
            skLineSegment(sketch, "E5987", {"start": v(-40.83, 20.12) * mm, "end": v(-40.75, 20.03) * mm});
            skLineSegment(sketch, "E5988", {"start": v(-40.75, 20.03) * mm, "end": v(-40.67, 19.94) * mm});
            skLineSegment(sketch, "E5989", {"start": v(-40.67, 19.94) * mm, "end": v(-40.6, 19.85) * mm});
            skLineSegment(sketch, "E5990", {"start": v(-40.6, 19.85) * mm, "end": v(-40.51, 19.76) * mm});
            skLineSegment(sketch, "E5991", {"start": v(-40.51, 19.76) * mm, "end": v(-40.43, 19.67) * mm});
            skLineSegment(sketch, "E5992", {"start": v(-40.43, 19.67) * mm, "end": v(-40.34, 19.58) * mm});
            skLineSegment(sketch, "E5993", {"start": v(-40.34, 19.58) * mm, "end": v(-40.26, 19.5) * mm});
            skLineSegment(sketch, "E5994", {"start": v(-40.26, 19.5) * mm, "end": v(-40.18, 19.41) * mm});
            skLineSegment(sketch, "E5995", {"start": v(-40.18, 19.41) * mm, "end": v(-40.1, 19.33) * mm});
            skLineSegment(sketch, "E5996", {"start": v(-40.1, 19.33) * mm, "end": v(-40, 19.24) * mm});
            skLineSegment(sketch, "E5997", {"start": v(-40, 19.24) * mm, "end": v(-39.92, 19.16) * mm});
            skLineSegment(sketch, "E5998", {"start": v(-39.92, 19.16) * mm, "end": v(-39.83, 19.08) * mm});
            skLineSegment(sketch, "E5999", {"start": v(-39.83, 19.08) * mm, "end": v(-39.75, 19) * mm});
            skLineSegment(sketch, "E6000", {"start": v(-39.75, 19) * mm, "end": v(-39.66, 18.91) * mm});
            skLineSegment(sketch, "E6001", {"start": v(-39.66, 18.91) * mm, "end": v(-39.56, 18.83) * mm});
            skLineSegment(sketch, "E6002", {"start": v(-39.56, 18.83) * mm, "end": v(-39.61, 18.72) * mm});
            skLineSegment(sketch, "E6003", {"start": v(-39.61, 18.72) * mm, "end": v(-39.66, 18.61) * mm});
            skLineSegment(sketch, "E6004", {"start": v(-39.66, 18.61) * mm, "end": v(-39.71, 18.5) * mm});
            skLineSegment(sketch, "E6005", {"start": v(-39.71, 18.5) * mm, "end": v(-39.76, 18.4) * mm});
            skLineSegment(sketch, "E6006", {"start": v(-39.76, 18.4) * mm, "end": v(-39.81, 18.3) * mm});
            skLineSegment(sketch, "E6007", {"start": v(-39.81, 18.3) * mm, "end": v(-39.86, 18.18) * mm});
            skLineSegment(sketch, "E6008", {"start": v(-39.86, 18.18) * mm, "end": v(-39.91, 18.08) * mm});
            skLineSegment(sketch, "E6009", {"start": v(-39.91, 18.08) * mm, "end": v(-39.92, 18.06) * mm});
            skLineSegment(sketch, "E6010", {"start": v(-39.92, 18.06) * mm, "end": v(-40.03, 18.08) * mm});
            skLineSegment(sketch, "E6011", {"start": v(-40.03, 18.08) * mm, "end": v(-40.14, 18.1) * mm});
            skLineSegment(sketch, "E6012", {"start": v(-40.14, 18.1) * mm, "end": v(-40.25, 18.1) * mm});
            skLineSegment(sketch, "E6013", {"start": v(-40.25, 18.1) * mm, "end": v(-40.37, 18.12) * mm});
            skLineSegment(sketch, "E6014", {"start": v(-40.37, 18.12) * mm, "end": v(-40.5, 18.13) * mm});
            skLineSegment(sketch, "E6015", {"start": v(-40.5, 18.13) * mm, "end": v(-40.62, 18.14) * mm});
            skLineSegment(sketch, "E6016", {"start": v(-40.62, 18.14) * mm, "end": v(-40.74, 18.15) * mm});
            skLineSegment(sketch, "E6017", {"start": v(-40.74, 18.15) * mm, "end": v(-40.87, 18.16) * mm});
            skLineSegment(sketch, "E6018", {"start": v(-40.87, 18.16) * mm, "end": v(-41, 18.17) * mm});
            skLineSegment(sketch, "E6019", {"start": v(-41, 18.17) * mm, "end": v(-41.12, 18.18) * mm});
            skLineSegment(sketch, "E6020", {"start": v(-41.12, 18.18) * mm, "end": v(-41.23, 18.18) * mm});
            skLineSegment(sketch, "E6021", {"start": v(-41.23, 18.18) * mm, "end": v(-41.34, 18.19) * mm});
            skLineSegment(sketch, "E6022", {"start": v(-41.34, 18.19) * mm, "end": v(-41.46, 18.2) * mm});
            skLineSegment(sketch, "E6023", {"start": v(-41.46, 18.2) * mm, "end": v(-41.58, 18.2) * mm});
            skLineSegment(sketch, "E6024", {"start": v(-41.58, 18.2) * mm, "end": v(-41.7, 18.2) * mm});
            skLineSegment(sketch, "E6025", {"start": v(-41.7, 18.2) * mm, "end": v(-41.82, 18.2) * mm});
            skLineSegment(sketch, "E6026", {"start": v(-41.82, 18.2) * mm, "end": v(-41.94, 18.2) * mm});
            skLineSegment(sketch, "E6027", {"start": v(-41.94, 18.2) * mm, "end": v(-42.07, 18.2) * mm});
            skLineSegment(sketch, "E6028", {"start": v(-42.07, 18.2) * mm, "end": v(-42.2, 18.2) * mm});
            skLineSegment(sketch, "E6029", {"start": v(-42.2, 18.2) * mm, "end": v(-42.2, 18.2) * mm});
            skLineSegment(sketch, "E6030", {"start": v(-42.2, 18.2) * mm, "end": v(-42.24, 18.1) * mm});
            skLineSegment(sketch, "E6031", {"start": v(-42.24, 18.1) * mm, "end": v(-42.3, 17.98) * mm});
            skLineSegment(sketch, "E6032", {"start": v(-42.3, 17.98) * mm, "end": v(-42.33, 17.88) * mm});
            skLineSegment(sketch, "E6033", {"start": v(-42.33, 17.88) * mm, "end": v(-42.38, 17.77) * mm});
            skLineSegment(sketch, "E6034", {"start": v(-42.38, 17.77) * mm, "end": v(-42.42, 17.68) * mm});
            skLineSegment(sketch, "E6035", {"start": v(-42.42, 17.68) * mm, "end": v(-42.33, 17.6) * mm});
            skLineSegment(sketch, "E6036", {"start": v(-42.33, 17.6) * mm, "end": v(-42.25, 17.5) * mm});
            skLineSegment(sketch, "E6037", {"start": v(-42.25, 17.5) * mm, "end": v(-42.17, 17.42) * mm});
            skLineSegment(sketch, "E6038", {"start": v(-42.17, 17.42) * mm, "end": v(-42.08, 17.34) * mm});
            skLineSegment(sketch, "E6039", {"start": v(-42.08, 17.34) * mm, "end": v(-42, 17.26) * mm});
            skLineSegment(sketch, "E6040", {"start": v(-42, 17.26) * mm, "end": v(-41.91, 17.18) * mm});
            skLineSegment(sketch, "E6041", {"start": v(-41.91, 17.18) * mm, "end": v(-41.83, 17.1) * mm});
            skLineSegment(sketch, "E6042", {"start": v(-41.83, 17.1) * mm, "end": v(-41.74, 17.01) * mm});
            skLineSegment(sketch, "E6043", {"start": v(-41.74, 17.01) * mm, "end": v(-41.65, 16.93) * mm});
            skLineSegment(sketch, "E6044", {"start": v(-41.65, 16.93) * mm, "end": v(-41.56, 16.84) * mm});
            skLineSegment(sketch, "E6045", {"start": v(-41.56, 16.84) * mm, "end": v(-41.47, 16.76) * mm});
            skLineSegment(sketch, "E6046", {"start": v(-41.47, 16.76) * mm, "end": v(-41.38, 16.68) * mm});
            skLineSegment(sketch, "E6047", {"start": v(-41.38, 16.68) * mm, "end": v(-41.3, 16.6) * mm});
            skLineSegment(sketch, "E6048", {"start": v(-41.3, 16.6) * mm, "end": v(-41.2, 16.53) * mm});
            skLineSegment(sketch, "E6049", {"start": v(-41.2, 16.53) * mm, "end": v(-41.11, 16.45) * mm});
            skLineSegment(sketch, "E6050", {"start": v(-41.11, 16.45) * mm, "end": v(-41.02, 16.37) * mm});
            skLineSegment(sketch, "E6051", {"start": v(-41.02, 16.37) * mm, "end": v(-40.93, 16.3) * mm});
            skLineSegment(sketch, "E6052", {"start": v(-40.93, 16.3) * mm, "end": v(-40.83, 16.22) * mm});
            skLineSegment(sketch, "E6053", {"start": v(-40.83, 16.22) * mm, "end": v(-40.73, 16.14) * mm});
            skLineSegment(sketch, "E6054", {"start": v(-40.73, 16.14) * mm, "end": v(-40.77, 16.03) * mm});
            skLineSegment(sketch, "E6055", {"start": v(-40.77, 16.03) * mm, "end": v(-40.82, 15.92) * mm});
            skLineSegment(sketch, "E6056", {"start": v(-40.82, 15.92) * mm, "end": v(-40.86, 15.81) * mm});
            skLineSegment(sketch, "E6057", {"start": v(-40.86, 15.81) * mm, "end": v(-40.9, 15.7) * mm});
            skLineSegment(sketch, "E6058", {"start": v(-40.9, 15.7) * mm, "end": v(-40.94, 15.6) * mm});
            skLineSegment(sketch, "E6059", {"start": v(-40.94, 15.6) * mm, "end": v(-40.99, 15.48) * mm});
            skLineSegment(sketch, "E6060", {"start": v(-40.99, 15.48) * mm, "end": v(-41.03, 15.37) * mm});
            skLineSegment(sketch, "E6061", {"start": v(-41.03, 15.37) * mm, "end": v(-41.04, 15.35) * mm});
            skLineSegment(sketch, "E6062", {"start": v(-41.04, 15.35) * mm, "end": v(-41.15, 15.36) * mm});
            skLineSegment(sketch, "E6063", {"start": v(-41.15, 15.36) * mm, "end": v(-41.26, 15.37) * mm});
            skLineSegment(sketch, "E6064", {"start": v(-41.26, 15.37) * mm, "end": v(-41.37, 15.38) * mm});
            skLineSegment(sketch, "E6065", {"start": v(-41.37, 15.38) * mm, "end": v(-41.49, 15.38) * mm});
            skLineSegment(sketch, "E6066", {"start": v(-41.49, 15.38) * mm, "end": v(-41.61, 15.38) * mm});
            skLineSegment(sketch, "E6067", {"start": v(-41.61, 15.38) * mm, "end": v(-41.74, 15.39) * mm});
            skLineSegment(sketch, "E6068", {"start": v(-41.74, 15.39) * mm, "end": v(-41.86, 15.4) * mm});
            skLineSegment(sketch, "E6069", {"start": v(-41.86, 15.4) * mm, "end": v(-42, 15.4) * mm});
            skLineSegment(sketch, "E6070", {"start": v(-42, 15.4) * mm, "end": v(-42.07, 15.4) * mm});
            skLineSegment(sketch, "E6071", {"start": v(-42.07, 15.4) * mm, "end": v(-42.18, 15.4) * mm});
            skLineSegment(sketch, "E6072", {"start": v(-42.18, 15.4) * mm, "end": v(-42.3, 15.39) * mm});
            skLineSegment(sketch, "E6073", {"start": v(-42.3, 15.39) * mm, "end": v(-42.4, 15.39) * mm});
            skLineSegment(sketch, "E6074", {"start": v(-42.4, 15.39) * mm, "end": v(-42.52, 15.38) * mm});
            skLineSegment(sketch, "E6075", {"start": v(-42.52, 15.38) * mm, "end": v(-42.64, 15.38) * mm});
            skLineSegment(sketch, "E6076", {"start": v(-42.64, 15.38) * mm, "end": v(-42.76, 15.38) * mm});
            skLineSegment(sketch, "E6077", {"start": v(-42.76, 15.38) * mm, "end": v(-42.88, 15.37) * mm});
            skLineSegment(sketch, "E6078", {"start": v(-42.88, 15.37) * mm, "end": v(-43, 15.36) * mm});
            skLineSegment(sketch, "E6079", {"start": v(-43, 15.36) * mm, "end": v(-43.13, 15.36) * mm});
            skLineSegment(sketch, "E6080", {"start": v(-43.13, 15.36) * mm, "end": v(-43.25, 15.35) * mm});
            skLineSegment(sketch, "E6081", {"start": v(-43.25, 15.35) * mm, "end": v(-43.32, 15.34) * mm});
            skLineSegment(sketch, "E6082", {"start": v(-43.32, 15.34) * mm, "end": v(-43.36, 15.23) * mm});
            skLineSegment(sketch, "E6083", {"start": v(-43.36, 15.23) * mm, "end": v(-43.4, 15.12) * mm});
            skLineSegment(sketch, "E6084", {"start": v(-43.4, 15.12) * mm, "end": v(-43.43, 15.02) * mm});
            skLineSegment(sketch, "E6085", {"start": v(-43.43, 15.02) * mm, "end": v(-43.47, 14.9) * mm});
            skLineSegment(sketch, "E6086", {"start": v(-43.47, 14.9) * mm, "end": v(-43.5, 14.81) * mm});
            skLineSegment(sketch, "E6087", {"start": v(-43.5, 14.81) * mm, "end": v(-43.41, 14.73) * mm});
            skLineSegment(sketch, "E6088", {"start": v(-43.41, 14.73) * mm, "end": v(-43.32, 14.65) * mm});
            skLineSegment(sketch, "E6089", {"start": v(-43.32, 14.65) * mm, "end": v(-43.23, 14.57) * mm});
            skLineSegment(sketch, "E6090", {"start": v(-43.23, 14.57) * mm, "end": v(-43.15, 14.5) * mm});
            skLineSegment(sketch, "E6091", {"start": v(-43.15, 14.5) * mm, "end": v(-43.06, 14.42) * mm});
            skLineSegment(sketch, "E6092", {"start": v(-43.06, 14.42) * mm, "end": v(-42.97, 14.34) * mm});
            skLineSegment(sketch, "E6093", {"start": v(-42.97, 14.34) * mm, "end": v(-42.88, 14.26) * mm});
            skLineSegment(sketch, "E6094", {"start": v(-42.88, 14.26) * mm, "end": v(-42.78, 14.19) * mm});
            skLineSegment(sketch, "E6095", {"start": v(-42.78, 14.19) * mm, "end": v(-42.7, 14.1) * mm});
            skLineSegment(sketch, "E6096", {"start": v(-42.7, 14.1) * mm, "end": v(-42.6, 14.03) * mm});
            skLineSegment(sketch, "E6097", {"start": v(-42.6, 14.03) * mm, "end": v(-42.5, 13.96) * mm});
            skLineSegment(sketch, "E6098", {"start": v(-42.5, 13.96) * mm, "end": v(-42.4, 13.88) * mm});
            skLineSegment(sketch, "E6099", {"start": v(-42.4, 13.88) * mm, "end": v(-42.3, 13.81) * mm});
            skLineSegment(sketch, "E6100", {"start": v(-42.3, 13.81) * mm, "end": v(-42.21, 13.74) * mm});
            skLineSegment(sketch, "E6101", {"start": v(-42.21, 13.74) * mm, "end": v(-42.12, 13.67) * mm});
            skLineSegment(sketch, "E6102", {"start": v(-42.12, 13.67) * mm, "end": v(-42.02, 13.6) * mm});
            skLineSegment(sketch, "E6103", {"start": v(-42.02, 13.6) * mm, "end": v(-41.92, 13.53) * mm});
            skLineSegment(sketch, "E6104", {"start": v(-41.92, 13.53) * mm, "end": v(-41.82, 13.46) * mm});
            skLineSegment(sketch, "E6105", {"start": v(-41.82, 13.46) * mm, "end": v(-41.72, 13.39) * mm});
            skLineSegment(sketch, "E6106", {"start": v(-41.72, 13.39) * mm, "end": v(-41.75, 13.27) * mm});
            skLineSegment(sketch, "E6107", {"start": v(-41.75, 13.27) * mm, "end": v(-41.79, 13.16) * mm});
            skLineSegment(sketch, "E6108", {"start": v(-41.79, 13.16) * mm, "end": v(-41.82, 13.05) * mm});
            skLineSegment(sketch, "E6109", {"start": v(-41.82, 13.05) * mm, "end": v(-41.86, 12.94) * mm});
            skLineSegment(sketch, "E6110", {"start": v(-41.86, 12.94) * mm, "end": v(-41.9, 12.82) * mm});
            skLineSegment(sketch, "E6111", {"start": v(-41.9, 12.82) * mm, "end": v(-41.93, 12.7) * mm});
            skLineSegment(sketch, "E6112", {"start": v(-41.93, 12.7) * mm, "end": v(-41.97, 12.6) * mm});
            skLineSegment(sketch, "E6113", {"start": v(-41.97, 12.6) * mm, "end": v(-41.97, 12.58) * mm});
            skLineSegment(sketch, "E6114", {"start": v(-41.97, 12.58) * mm, "end": v(-42.06, 12.58) * mm});
            skLineSegment(sketch, "E6115", {"start": v(-42.06, 12.58) * mm, "end": v(-42.17, 12.58) * mm});
            skLineSegment(sketch, "E6116", {"start": v(-42.17, 12.58) * mm, "end": v(-42.28, 12.58) * mm});
            skLineSegment(sketch, "E6117", {"start": v(-42.28, 12.58) * mm, "end": v(-42.4, 12.58) * mm});
            skLineSegment(sketch, "E6118", {"start": v(-42.4, 12.58) * mm, "end": v(-42.52, 12.57) * mm});
            skLineSegment(sketch, "E6119", {"start": v(-42.52, 12.57) * mm, "end": v(-42.65, 12.57) * mm});
            skLineSegment(sketch, "E6120", {"start": v(-42.65, 12.57) * mm, "end": v(-42.77, 12.56) * mm});
            skLineSegment(sketch, "E6121", {"start": v(-42.77, 12.56) * mm, "end": v(-42.9, 12.55) * mm});
            skLineSegment(sketch, "E6122", {"start": v(-42.9, 12.55) * mm, "end": v(-43.02, 12.55) * mm});
            skLineSegment(sketch, "E6123", {"start": v(-43.02, 12.55) * mm, "end": v(-43.14, 12.54) * mm});
            skLineSegment(sketch, "E6124", {"start": v(-43.14, 12.54) * mm, "end": v(-43.26, 12.53) * mm});
            skLineSegment(sketch, "E6125", {"start": v(-43.26, 12.53) * mm, "end": v(-43.37, 12.52) * mm});
            skLineSegment(sketch, "E6126", {"start": v(-43.37, 12.52) * mm, "end": v(-43.48, 12.5) * mm});
            skLineSegment(sketch, "E6127", {"start": v(-43.48, 12.5) * mm, "end": v(-43.6, 12.5) * mm});
            skLineSegment(sketch, "E6128", {"start": v(-43.6, 12.5) * mm, "end": v(-43.72, 12.48) * mm});
            skLineSegment(sketch, "E6129", {"start": v(-43.72, 12.48) * mm, "end": v(-43.84, 12.47) * mm});
            skLineSegment(sketch, "E6130", {"start": v(-43.84, 12.47) * mm, "end": v(-43.96, 12.45) * mm});
            skLineSegment(sketch, "E6131", {"start": v(-43.96, 12.45) * mm, "end": v(-44.09, 12.44) * mm});
            skLineSegment(sketch, "E6132", {"start": v(-44.09, 12.44) * mm, "end": v(-44.21, 12.42) * mm});
            skLineSegment(sketch, "E6133", {"start": v(-44.21, 12.42) * mm, "end": v(-44.25, 12.42) * mm});
            skLineSegment(sketch, "E6134", {"start": v(-44.25, 12.42) * mm, "end": v(-44.28, 12.3) * mm});
            skLineSegment(sketch, "E6135", {"start": v(-44.28, 12.3) * mm, "end": v(-44.31, 12.19) * mm});
            skLineSegment(sketch, "E6136", {"start": v(-44.31, 12.19) * mm, "end": v(-44.34, 12.08) * mm});
            skLineSegment(sketch, "E6137", {"start": v(-44.34, 12.08) * mm, "end": v(-44.37, 11.97) * mm});
            skLineSegment(sketch, "E6138", {"start": v(-44.37, 11.97) * mm, "end": v(-44.4, 11.87) * mm});
            skLineSegment(sketch, "E6139", {"start": v(-44.4, 11.87) * mm, "end": v(-44.3, 11.8) * mm});
            skLineSegment(sketch, "E6140", {"start": v(-44.3, 11.8) * mm, "end": v(-44.2, 11.72) * mm});
            skLineSegment(sketch, "E6141", {"start": v(-44.2, 11.72) * mm, "end": v(-44.11, 11.65) * mm});
            skLineSegment(sketch, "E6142", {"start": v(-44.11, 11.65) * mm, "end": v(-44.02, 11.58) * mm});
            skLineSegment(sketch, "E6143", {"start": v(-44.02, 11.58) * mm, "end": v(-43.93, 11.5) * mm});
            skLineSegment(sketch, "E6144", {"start": v(-43.93, 11.5) * mm, "end": v(-43.83, 11.44) * mm});
            skLineSegment(sketch, "E6145", {"start": v(-43.83, 11.44) * mm, "end": v(-43.73, 11.37) * mm});
            skLineSegment(sketch, "E6146", {"start": v(-43.73, 11.37) * mm, "end": v(-43.64, 11.3) * mm});
            skLineSegment(sketch, "E6147", {"start": v(-43.64, 11.3) * mm, "end": v(-43.54, 11.23) * mm});
            skLineSegment(sketch, "E6148", {"start": v(-43.54, 11.23) * mm, "end": v(-43.43, 11.15) * mm});
            skLineSegment(sketch, "E6149", {"start": v(-43.43, 11.15) * mm, "end": v(-43.34, 11.09) * mm});
            skLineSegment(sketch, "E6150", {"start": v(-43.34, 11.09) * mm, "end": v(-43.24, 11.02) * mm});
            skLineSegment(sketch, "E6151", {"start": v(-43.24, 11.02) * mm, "end": v(-43.14, 10.95) * mm});
            skLineSegment(sketch, "E6152", {"start": v(-43.14, 10.95) * mm, "end": v(-43.04, 10.89) * mm});
            skLineSegment(sketch, "E6153", {"start": v(-43.04, 10.89) * mm, "end": v(-42.94, 10.82) * mm});
            skLineSegment(sketch, "E6154", {"start": v(-42.94, 10.82) * mm, "end": v(-42.83, 10.76) * mm});
            skLineSegment(sketch, "E6155", {"start": v(-42.83, 10.76) * mm, "end": v(-42.73, 10.7) * mm});
            skLineSegment(sketch, "E6156", {"start": v(-42.73, 10.7) * mm, "end": v(-42.63, 10.64) * mm});
            skLineSegment(sketch, "E6157", {"start": v(-42.63, 10.64) * mm, "end": v(-42.52, 10.57) * mm});
            skLineSegment(sketch, "E6158", {"start": v(-42.52, 10.57) * mm, "end": v(-42.55, 10.45) * mm});
            skLineSegment(sketch, "E6159", {"start": v(-42.55, 10.45) * mm, "end": v(-42.57, 10.34) * mm});
            skLineSegment(sketch, "E6160", {"start": v(-42.57, 10.34) * mm, "end": v(-42.6, 10.22) * mm});
            skLineSegment(sketch, "E6161", {"start": v(-42.6, 10.22) * mm, "end": v(-42.63, 10.11) * mm});
            skLineSegment(sketch, "E6162", {"start": v(-42.63, 10.11) * mm, "end": v(-42.66, 10) * mm});
            skLineSegment(sketch, "E6163", {"start": v(-42.66, 10) * mm, "end": v(-42.68, 9.88) * mm});
            skLineSegment(sketch, "E6164", {"start": v(-42.68, 9.88) * mm, "end": v(-42.71, 9.76) * mm});
            skLineSegment(sketch, "E6165", {"start": v(-42.71, 9.76) * mm, "end": v(-42.72, 9.75) * mm});
            skLineSegment(sketch, "E6166", {"start": v(-42.72, 9.75) * mm, "end": v(-42.83, 9.74) * mm});
            skLineSegment(sketch, "E6167", {"start": v(-42.83, 9.74) * mm, "end": v(-42.94, 9.73) * mm});
            skLineSegment(sketch, "E6168", {"start": v(-42.94, 9.73) * mm, "end": v(-43.05, 9.72) * mm});
            skLineSegment(sketch, "E6169", {"start": v(-43.05, 9.72) * mm, "end": v(-43.17, 9.71) * mm});
            skLineSegment(sketch, "E6170", {"start": v(-43.17, 9.71) * mm, "end": v(-43.3, 9.7) * mm});
            skLineSegment(sketch, "E6171", {"start": v(-43.3, 9.7) * mm, "end": v(-43.41, 9.69) * mm});
            skLineSegment(sketch, "E6172", {"start": v(-43.41, 9.69) * mm, "end": v(-43.54, 9.67) * mm});
            skLineSegment(sketch, "E6173", {"start": v(-43.54, 9.67) * mm, "end": v(-43.67, 9.66) * mm});
            skLineSegment(sketch, "E6174", {"start": v(-43.67, 9.66) * mm, "end": v(-43.79, 9.64) * mm});
            skLineSegment(sketch, "E6175", {"start": v(-43.79, 9.64) * mm, "end": v(-43.91, 9.62) * mm});
            skLineSegment(sketch, "E6176", {"start": v(-43.91, 9.62) * mm, "end": v(-44.02, 9.6) * mm});
            skLineSegment(sketch, "E6177", {"start": v(-44.02, 9.6) * mm, "end": v(-44.14, 9.59) * mm});
            skLineSegment(sketch, "E6178", {"start": v(-44.14, 9.59) * mm, "end": v(-44.25, 9.57) * mm});
            skLineSegment(sketch, "E6179", {"start": v(-44.25, 9.57) * mm, "end": v(-44.37, 9.55) * mm});
            skLineSegment(sketch, "E6180", {"start": v(-44.37, 9.55) * mm, "end": v(-44.48, 9.53) * mm});
            skLineSegment(sketch, "E6181", {"start": v(-44.48, 9.53) * mm, "end": v(-44.6, 9.5) * mm});
            skLineSegment(sketch, "E6182", {"start": v(-44.6, 9.5) * mm, "end": v(-44.73, 9.48) * mm});
            skLineSegment(sketch, "E6183", {"start": v(-44.73, 9.48) * mm, "end": v(-44.85, 9.46) * mm});
            skLineSegment(sketch, "E6184", {"start": v(-44.85, 9.46) * mm, "end": v(-44.97, 9.43) * mm});
            skLineSegment(sketch, "E6185", {"start": v(-44.97, 9.43) * mm, "end": v(-44.98, 9.43) * mm});
            skLineSegment(sketch, "E6186", {"start": v(-44.98, 9.43) * mm, "end": v(-45, 9.32) * mm});
            skLineSegment(sketch, "E6187", {"start": v(-45, 9.32) * mm, "end": v(-45.02, 9.2) * mm});
            skLineSegment(sketch, "E6188", {"start": v(-45.02, 9.2) * mm, "end": v(-45.05, 9.1) * mm});
            skLineSegment(sketch, "E6189", {"start": v(-45.05, 9.1) * mm, "end": v(-45.07, 8.98) * mm});
            skLineSegment(sketch, "E6190", {"start": v(-45.07, 8.98) * mm, "end": v(-45.09, 8.88) * mm});
            skLineSegment(sketch, "E6191", {"start": v(-45.09, 8.88) * mm, "end": v(-45, 8.81) * mm});
            skLineSegment(sketch, "E6192", {"start": v(-45, 8.81) * mm, "end": v(-44.89, 8.74) * mm});
            skLineSegment(sketch, "E6193", {"start": v(-44.89, 8.74) * mm, "end": v(-44.8, 8.68) * mm});
            skLineSegment(sketch, "E6194", {"start": v(-44.8, 8.68) * mm, "end": v(-44.7, 8.61) * mm});
            skLineSegment(sketch, "E6195", {"start": v(-44.7, 8.61) * mm, "end": v(-44.6, 8.55) * mm});
            skLineSegment(sketch, "E6196", {"start": v(-44.6, 8.55) * mm, "end": v(-44.5, 8.48) * mm});
            skLineSegment(sketch, "E6197", {"start": v(-44.5, 8.48) * mm, "end": v(-44.4, 8.42) * mm});
            skLineSegment(sketch, "E6198", {"start": v(-44.4, 8.42) * mm, "end": v(-44.3, 8.36) * mm});
            skLineSegment(sketch, "E6199", {"start": v(-44.3, 8.36) * mm, "end": v(-44.2, 8.3) * mm});
            skLineSegment(sketch, "E6200", {"start": v(-44.2, 8.3) * mm, "end": v(-44.08, 8.23) * mm});
            skLineSegment(sketch, "E6201", {"start": v(-44.08, 8.23) * mm, "end": v(-43.98, 8.17) * mm});
            skLineSegment(sketch, "E6202", {"start": v(-43.98, 8.17) * mm, "end": v(-43.88, 8.1) * mm});
            skLineSegment(sketch, "E6203", {"start": v(-43.88, 8.1) * mm, "end": v(-43.77, 8.05) * mm});
            skLineSegment(sketch, "E6204", {"start": v(-43.77, 8.05) * mm, "end": v(-43.67, 8) * mm});
            skLineSegment(sketch, "E6205", {"start": v(-43.67, 8) * mm, "end": v(-43.56, 7.93) * mm});
            skLineSegment(sketch, "E6206", {"start": v(-43.56, 7.93) * mm, "end": v(-43.46, 7.88) * mm});
            skLineSegment(sketch, "E6207", {"start": v(-43.46, 7.88) * mm, "end": v(-43.35, 7.82) * mm});
            skLineSegment(sketch, "E6208", {"start": v(-43.35, 7.82) * mm, "end": v(-43.25, 7.77) * mm});
            skLineSegment(sketch, "E6209", {"start": v(-43.25, 7.77) * mm, "end": v(-43.13, 7.7) * mm});
            skLineSegment(sketch, "E6210", {"start": v(-43.13, 7.7) * mm, "end": v(-43.15, 7.59) * mm});
            skLineSegment(sketch, "E6211", {"start": v(-43.15, 7.59) * mm, "end": v(-43.17, 7.47) * mm});
            skLineSegment(sketch, "E6212", {"start": v(-43.17, 7.47) * mm, "end": v(-43.19, 7.36) * mm});
            skLineSegment(sketch, "E6213", {"start": v(-43.19, 7.36) * mm, "end": v(-43.2, 7.24) * mm});
            skLineSegment(sketch, "E6214", {"start": v(-43.2, 7.24) * mm, "end": v(-43.23, 7.12) * mm});
            skLineSegment(sketch, "E6215", {"start": v(-43.23, 7.12) * mm, "end": v(-43.25, 7) * mm});
            skLineSegment(sketch, "E6216", {"start": v(-43.25, 7) * mm, "end": v(-43.27, 6.89) * mm});
            skLineSegment(sketch, "E6217", {"start": v(-43.27, 6.89) * mm, "end": v(-43.27, 6.87) * mm});
            skLineSegment(sketch, "E6218", {"start": v(-43.27, 6.87) * mm, "end": v(-43.38, 6.86) * mm});
            skLineSegment(sketch, "E6219", {"start": v(-43.38, 6.86) * mm, "end": v(-43.5, 6.84) * mm});
            skLineSegment(sketch, "E6220", {"start": v(-43.5, 6.84) * mm, "end": v(-43.6, 6.83) * mm});
            skLineSegment(sketch, "E6221", {"start": v(-43.6, 6.83) * mm, "end": v(-43.72, 6.8) * mm});
            skLineSegment(sketch, "E6222", {"start": v(-43.72, 6.8) * mm, "end": v(-43.84, 6.79) * mm});
            skLineSegment(sketch, "E6223", {"start": v(-43.84, 6.79) * mm, "end": v(-43.96, 6.77) * mm});
            skLineSegment(sketch, "E6224", {"start": v(-43.96, 6.77) * mm, "end": v(-44.09, 6.74) * mm});
            skLineSegment(sketch, "E6225", {"start": v(-44.09, 6.74) * mm, "end": v(-44.22, 6.72) * mm});
            skLineSegment(sketch, "E6226", {"start": v(-44.22, 6.72) * mm, "end": v(-44.34, 6.7) * mm});
            skLineSegment(sketch, "E6227", {"start": v(-44.34, 6.7) * mm, "end": v(-44.46, 6.67) * mm});
            skLineSegment(sketch, "E6228", {"start": v(-44.46, 6.67) * mm, "end": v(-44.57, 6.65) * mm});
            skLineSegment(sketch, "E6229", {"start": v(-44.57, 6.65) * mm, "end": v(-44.68, 6.62) * mm});
            skLineSegment(sketch, "E6230", {"start": v(-44.68, 6.62) * mm, "end": v(-44.79, 6.6) * mm});
            skLineSegment(sketch, "E6231", {"start": v(-44.79, 6.6) * mm, "end": v(-44.9, 6.57) * mm});
            skLineSegment(sketch, "E6232", {"start": v(-44.9, 6.57) * mm, "end": v(-45.02, 6.54) * mm});
            skLineSegment(sketch, "E6233", {"start": v(-45.02, 6.54) * mm, "end": v(-45.14, 6.5) * mm});
            skLineSegment(sketch, "E6234", {"start": v(-45.14, 6.5) * mm, "end": v(-45.26, 6.48) * mm});
            skLineSegment(sketch, "E6235", {"start": v(-45.26, 6.48) * mm, "end": v(-45.38, 6.44) * mm});
            skLineSegment(sketch, "E6236", {"start": v(-45.38, 6.44) * mm, "end": v(-45.5, 6.4) * mm});
            skLineSegment(sketch, "E6237", {"start": v(-45.5, 6.4) * mm, "end": v(-45.5, 6.4) * mm});
            skLineSegment(sketch, "E6238", {"start": v(-45.5, 6.4) * mm, "end": v(-45.52, 6.29) * mm});
            skLineSegment(sketch, "E6239", {"start": v(-45.52, 6.29) * mm, "end": v(-45.54, 6.17) * mm});
            skLineSegment(sketch, "E6240", {"start": v(-45.54, 6.17) * mm, "end": v(-45.55, 6.06) * mm});
            skLineSegment(sketch, "E6241", {"start": v(-45.55, 6.06) * mm, "end": v(-45.57, 5.95) * mm});
            skLineSegment(sketch, "E6242", {"start": v(-45.57, 5.95) * mm, "end": v(-45.58, 5.85) * mm});
            skLineSegment(sketch, "E6243", {"start": v(-45.58, 5.85) * mm, "end": v(-45.48, 5.79) * mm});
            skLineSegment(sketch, "E6244", {"start": v(-45.48, 5.79) * mm, "end": v(-45.37, 5.73) * mm});
            skLineSegment(sketch, "E6245", {"start": v(-45.37, 5.73) * mm, "end": v(-45.27, 5.67) * mm});
            skLineSegment(sketch, "E6246", {"start": v(-45.27, 5.67) * mm, "end": v(-45.17, 5.6) * mm});
            skLineSegment(sketch, "E6247", {"start": v(-45.17, 5.6) * mm, "end": v(-45.07, 5.55) * mm});
            skLineSegment(sketch, "E6248", {"start": v(-45.07, 5.55) * mm, "end": v(-44.96, 5.5) * mm});
            skLineSegment(sketch, "E6249", {"start": v(-44.96, 5.5) * mm, "end": v(-44.86, 5.44) * mm});
            skLineSegment(sketch, "E6250", {"start": v(-44.86, 5.44) * mm, "end": v(-44.75, 5.38) * mm});
            skLineSegment(sketch, "E6251", {"start": v(-44.75, 5.38) * mm, "end": v(-44.65, 5.32) * mm});
            skLineSegment(sketch, "E6252", {"start": v(-44.65, 5.32) * mm, "end": v(-44.53, 5.27) * mm});
            skLineSegment(sketch, "E6253", {"start": v(-44.53, 5.27) * mm, "end": v(-44.43, 5.21) * mm});
            skLineSegment(sketch, "E6254", {"start": v(-44.43, 5.21) * mm, "end": v(-44.32, 5.16) * mm});
            skLineSegment(sketch, "E6255", {"start": v(-44.32, 5.16) * mm, "end": v(-44.21, 5.1) * mm});
            skLineSegment(sketch, "E6256", {"start": v(-44.21, 5.1) * mm, "end": v(-44.1, 5.06) * mm});
            skLineSegment(sketch, "E6257", {"start": v(-44.1, 5.06) * mm, "end": v(-44, 5) * mm});
            skLineSegment(sketch, "E6258", {"start": v(-44, 5) * mm, "end": v(-43.89, 4.96) * mm});
            skLineSegment(sketch, "E6259", {"start": v(-43.89, 4.96) * mm, "end": v(-43.78, 4.9) * mm});
            skLineSegment(sketch, "E6260", {"start": v(-43.78, 4.9) * mm, "end": v(-43.67, 4.86) * mm});
            skLineSegment(sketch, "E6261", {"start": v(-43.67, 4.86) * mm, "end": v(-43.55, 4.8) * mm});
            skLineSegment(sketch, "E6262", {"start": v(-43.55, 4.8) * mm, "end": v(-43.56, 4.69) * mm});
            skLineSegment(sketch, "E6263", {"start": v(-43.56, 4.69) * mm, "end": v(-43.57, 4.57) * mm});
            skLineSegment(sketch, "E6264", {"start": v(-43.57, 4.57) * mm, "end": v(-43.58, 4.45) * mm});
            skLineSegment(sketch, "E6265", {"start": v(-43.58, 4.45) * mm, "end": v(-43.6, 4.34) * mm});
            skLineSegment(sketch, "E6266", {"start": v(-43.6, 4.34) * mm, "end": v(-43.6, 4.22) * mm});
            skLineSegment(sketch, "E6267", {"start": v(-43.6, 4.22) * mm, "end": v(-43.62, 4.1) * mm});
            skLineSegment(sketch, "E6268", {"start": v(-43.62, 4.1) * mm, "end": v(-43.63, 3.98) * mm});
            skLineSegment(sketch, "E6269", {"start": v(-43.63, 3.98) * mm, "end": v(-43.63, 3.97) * mm});
            skLineSegment(sketch, "E6270", {"start": v(-43.63, 3.97) * mm, "end": v(-43.74, 3.95) * mm});
            skLineSegment(sketch, "E6271", {"start": v(-43.74, 3.95) * mm, "end": v(-43.85, 3.92) * mm});
            skLineSegment(sketch, "E6272", {"start": v(-43.85, 3.92) * mm, "end": v(-43.96, 3.9) * mm});
            skLineSegment(sketch, "E6273", {"start": v(-43.96, 3.9) * mm, "end": v(-44.08, 3.87) * mm});
            skLineSegment(sketch, "E6274", {"start": v(-44.08, 3.87) * mm, "end": v(-44.2, 3.84) * mm});
            skLineSegment(sketch, "E6275", {"start": v(-44.2, 3.84) * mm, "end": v(-44.32, 3.82) * mm});
            skLineSegment(sketch, "E6276", {"start": v(-44.32, 3.82) * mm, "end": v(-44.44, 3.78) * mm});
            skLineSegment(sketch, "E6277", {"start": v(-44.44, 3.78) * mm, "end": v(-44.57, 3.75) * mm});
            skLineSegment(sketch, "E6278", {"start": v(-44.57, 3.75) * mm, "end": v(-44.68, 3.72) * mm});
            skLineSegment(sketch, "E6279", {"start": v(-44.68, 3.72) * mm, "end": v(-44.8, 3.68) * mm});
            skLineSegment(sketch, "E6280", {"start": v(-44.8, 3.68) * mm, "end": v(-44.91, 3.65) * mm});
            skLineSegment(sketch, "E6281", {"start": v(-44.91, 3.65) * mm, "end": v(-45.02, 3.62) * mm});
            skLineSegment(sketch, "E6282", {"start": v(-45.02, 3.62) * mm, "end": v(-45.13, 3.59) * mm});
            skLineSegment(sketch, "E6283", {"start": v(-45.13, 3.59) * mm, "end": v(-45.24, 3.55) * mm});
            skLineSegment(sketch, "E6284", {"start": v(-45.24, 3.55) * mm, "end": v(-45.36, 3.52) * mm});
            skLineSegment(sketch, "E6285", {"start": v(-45.36, 3.52) * mm, "end": v(-45.47, 3.48) * mm});
            skLineSegment(sketch, "E6286", {"start": v(-45.47, 3.48) * mm, "end": v(-45.6, 3.44) * mm});
            skLineSegment(sketch, "E6287", {"start": v(-45.6, 3.44) * mm, "end": v(-45.7, 3.4) * mm});
            skLineSegment(sketch, "E6288", {"start": v(-45.7, 3.4) * mm, "end": v(-45.83, 3.35) * mm});
            skLineSegment(sketch, "E6289", {"start": v(-45.83, 3.35) * mm, "end": v(-45.83, 3.35) * mm});
            skLineSegment(sketch, "E6290", {"start": v(-45.83, 3.35) * mm, "end": v(-45.84, 3.23) * mm});
            skLineSegment(sketch, "E6291", {"start": v(-45.84, 3.23) * mm, "end": v(-45.85, 3.12) * mm});
            skLineSegment(sketch, "E6292", {"start": v(-45.85, 3.12) * mm, "end": v(-45.86, 3) * mm});
            skLineSegment(sketch, "E6293", {"start": v(-45.86, 3) * mm, "end": v(-45.86, 2.89) * mm});
            skLineSegment(sketch, "E6294", {"start": v(-45.86, 2.89) * mm, "end": v(-45.87, 2.8) * mm});
            skLineSegment(sketch, "E6295", {"start": v(-45.87, 2.8) * mm, "end": v(-45.76, 2.74) * mm});
            skLineSegment(sketch, "E6296", {"start": v(-45.76, 2.74) * mm, "end": v(-45.65, 2.68) * mm});
            skLineSegment(sketch, "E6297", {"start": v(-45.65, 2.68) * mm, "end": v(-45.55, 2.63) * mm});
            skLineSegment(sketch, "E6298", {"start": v(-45.55, 2.63) * mm, "end": v(-45.44, 2.58) * mm});
            skLineSegment(sketch, "E6299", {"start": v(-45.44, 2.58) * mm, "end": v(-45.34, 2.53) * mm});
            skLineSegment(sketch, "E6300", {"start": v(-45.34, 2.53) * mm, "end": v(-45.23, 2.48) * mm});
            skLineSegment(sketch, "E6301", {"start": v(-45.23, 2.48) * mm, "end": v(-45.12, 2.43) * mm});
            skLineSegment(sketch, "E6302", {"start": v(-45.12, 2.43) * mm, "end": v(-45.01, 2.38) * mm});
            skLineSegment(sketch, "E6303", {"start": v(-45.01, 2.38) * mm, "end": v(-44.9, 2.33) * mm});
            skLineSegment(sketch, "E6304", {"start": v(-44.9, 2.33) * mm, "end": v(-44.79, 2.28) * mm});
            skLineSegment(sketch, "E6305", {"start": v(-44.79, 2.28) * mm, "end": v(-44.68, 2.23) * mm});
            skLineSegment(sketch, "E6306", {"start": v(-44.68, 2.23) * mm, "end": v(-44.56, 2.19) * mm});
            skLineSegment(sketch, "E6307", {"start": v(-44.56, 2.19) * mm, "end": v(-44.45, 2.14) * mm});
            skLineSegment(sketch, "E6308", {"start": v(-44.45, 2.14) * mm, "end": v(-44.34, 2.1) * mm});
            skLineSegment(sketch, "E6309", {"start": v(-44.34, 2.1) * mm, "end": v(-44.23, 2.06) * mm});
            skLineSegment(sketch, "E6310", {"start": v(-44.23, 2.06) * mm, "end": v(-44.12, 2.01) * mm});
            skLineSegment(sketch, "E6311", {"start": v(-44.12, 2.01) * mm, "end": v(-44, 1.97) * mm});
            skLineSegment(sketch, "E6312", {"start": v(-44, 1.97) * mm, "end": v(-43.9, 1.93) * mm});
            skLineSegment(sketch, "E6313", {"start": v(-43.9, 1.93) * mm, "end": v(-43.77, 1.89) * mm});
            skLineSegment(sketch, "E6314", {"start": v(-43.77, 1.89) * mm, "end": v(-43.78, 1.77) * mm});
            skLineSegment(sketch, "E6315", {"start": v(-43.78, 1.77) * mm, "end": v(-43.78, 1.65) * mm});
            skLineSegment(sketch, "E6316", {"start": v(-43.78, 1.65) * mm, "end": v(-43.78, 1.53) * mm});
            skLineSegment(sketch, "E6317", {"start": v(-43.78, 1.53) * mm, "end": v(-43.79, 1.42) * mm});
            skLineSegment(sketch, "E6318", {"start": v(-43.79, 1.42) * mm, "end": v(-43.8, 1.3) * mm});
            skLineSegment(sketch, "E6319", {"start": v(-43.8, 1.3) * mm, "end": v(-43.8, 1.18) * mm});
            skLineSegment(sketch, "E6320", {"start": v(-43.8, 1.18) * mm, "end": v(-43.8, 1.06) * mm});
            skLineSegment(sketch, "E6321", {"start": v(-43.8, 1.06) * mm, "end": v(-43.8, 1.04) * mm});
            skLineSegment(sketch, "E6322", {"start": v(-43.8, 1.04) * mm, "end": v(-43.9, 1.02) * mm});
            skLineSegment(sketch, "E6323", {"start": v(-43.9, 1.02) * mm, "end": v(-44.01, 0.99) * mm});
            skLineSegment(sketch, "E6324", {"start": v(-44.01, 0.99) * mm, "end": v(-44.13, 0.95) * mm});
            skLineSegment(sketch, "E6325", {"start": v(-44.13, 0.95) * mm, "end": v(-44.24, 0.92) * mm});
            skLineSegment(sketch, "E6326", {"start": v(-44.24, 0.92) * mm, "end": v(-44.35, 0.88) * mm});
            skLineSegment(sketch, "E6327", {"start": v(-44.35, 0.88) * mm, "end": v(-44.47, 0.85) * mm});
            skLineSegment(sketch, "E6328", {"start": v(-44.47, 0.85) * mm, "end": v(-44.6, 0.8) * mm});
            skLineSegment(sketch, "E6329", {"start": v(-44.6, 0.8) * mm, "end": v(-44.72, 0.76) * mm});
            skLineSegment(sketch, "E6330", {"start": v(-44.72, 0.76) * mm, "end": v(-44.83, 0.73) * mm});
            skLineSegment(sketch, "E6331", {"start": v(-44.83, 0.73) * mm, "end": v(-44.95, 0.68) * mm});
            skLineSegment(sketch, "E6332", {"start": v(-44.95, 0.68) * mm, "end": v(-45.05, 0.65) * mm});
            skLineSegment(sketch, "E6333", {"start": v(-45.05, 0.65) * mm, "end": v(-45.16, 0.6) * mm});
            skLineSegment(sketch, "E6334", {"start": v(-45.16, 0.6) * mm, "end": v(-45.27, 0.57) * mm});
            skLineSegment(sketch, "E6335", {"start": v(-45.27, 0.57) * mm, "end": v(-45.38, 0.52) * mm});
            skLineSegment(sketch, "E6336", {"start": v(-45.38, 0.52) * mm, "end": v(-45.5, 0.48) * mm});
            skLineSegment(sketch, "E6337", {"start": v(-45.5, 0.48) * mm, "end": v(-45.6, 0.43) * mm});
            skLineSegment(sketch, "E6338", {"start": v(-45.6, 0.43) * mm, "end": v(-45.72, 0.39) * mm});
            skLineSegment(sketch, "E6339", {"start": v(-45.72, 0.39) * mm, "end": v(-45.83, 0.34) * mm});
            skLineSegment(sketch, "E6340", {"start": v(-45.83, 0.34) * mm, "end": v(-45.95, 0.29) * mm});
            skLineSegment(sketch, "E6341", {"start": v(-45.95, 0.29) * mm, "end": v(-45.95, 0.29) * mm});
            skLineSegment(sketch, "E6342", {"start": v(-45.95, 0.29) * mm, "end": v(-45.95, 0.17) * mm});
            skLineSegment(sketch, "E6343", {"start": v(-45.95, 0.17) * mm, "end": v(-45.95, 0.05) * mm});
            skLineSegment(sketch, "E6344", {"start": v(-45.95, 0.05) * mm, "end": v(-45.95, -0.06) * mm});
            skLineSegment(sketch, "E6345", {"start": v(-45.95, -0.06) * mm, "end": v(-45.95, -0.18) * mm});
            skLineSegment(sketch, "E6346", {"start": v(-45.95, -0.18) * mm, "end": v(-45.95, -0.28) * mm});
            skLineSegment(sketch, "E6347", {"start": v(-45.95, -0.28) * mm, "end": v(-45.84, -0.33) * mm});
            skLineSegment(sketch, "E6348", {"start": v(-45.84, -0.33) * mm, "end": v(-45.73, -0.37) * mm});
            skLineSegment(sketch, "E6349", {"start": v(-45.73, -0.37) * mm, "end": v(-45.62, -0.42) * mm});
            skLineSegment(sketch, "E6350", {"start": v(-45.62, -0.42) * mm, "end": v(-45.51, -0.46) * mm});
            skLineSegment(sketch, "E6351", {"start": v(-45.51, -0.46) * mm, "end": v(-45.4, -0.5) * mm});
            skLineSegment(sketch, "E6352", {"start": v(-45.4, -0.5) * mm, "end": v(-45.3, -0.55) * mm});
            skLineSegment(sketch, "E6353", {"start": v(-45.3, -0.55) * mm, "end": v(-45.18, -0.6) * mm});
            skLineSegment(sketch, "E6354", {"start": v(-45.18, -0.6) * mm, "end": v(-45.07, -0.63) * mm});
            skLineSegment(sketch, "E6355", {"start": v(-45.07, -0.63) * mm, "end": v(-44.96, -0.67) * mm});
            skLineSegment(sketch, "E6356", {"start": v(-44.96, -0.67) * mm, "end": v(-44.84, -0.72) * mm});
            skLineSegment(sketch, "E6357", {"start": v(-44.84, -0.72) * mm, "end": v(-44.72, -0.76) * mm});
            skLineSegment(sketch, "E6358", {"start": v(-44.72, -0.76) * mm, "end": v(-44.61, -0.8) * mm});
            skLineSegment(sketch, "E6359", {"start": v(-44.61, -0.8) * mm, "end": v(-44.5, -0.83) * mm});
            skLineSegment(sketch, "E6360", {"start": v(-44.5, -0.83) * mm, "end": v(-44.38, -0.87) * mm});
            skLineSegment(sketch, "E6361", {"start": v(-44.38, -0.87) * mm, "end": v(-44.27, -0.9) * mm});
            skLineSegment(sketch, "E6362", {"start": v(-44.27, -0.9) * mm, "end": v(-44.15, -0.94) * mm});
            skLineSegment(sketch, "E6363", {"start": v(-44.15, -0.94) * mm, "end": v(-44.04, -0.97) * mm});
            skLineSegment(sketch, "E6364", {"start": v(-44.04, -0.97) * mm, "end": v(-43.92, -1) * mm});
            skLineSegment(sketch, "E6365", {"start": v(-43.92, -1) * mm, "end": v(-43.8, -1.04) * mm});
            skLineSegment(sketch, "E6366", {"start": v(-43.8, -1.04) * mm, "end": v(-43.8, -1.16) * mm});
            skLineSegment(sketch, "E6367", {"start": v(-43.8, -1.16) * mm, "end": v(-43.8, -1.27) * mm});
            skLineSegment(sketch, "E6368", {"start": v(-43.8, -1.27) * mm, "end": v(-43.79, -1.4) * mm});
            skLineSegment(sketch, "E6369", {"start": v(-43.79, -1.4) * mm, "end": v(-43.79, -1.51) * mm});
            skLineSegment(sketch, "E6370", {"start": v(-43.79, -1.51) * mm, "end": v(-43.78, -1.63) * mm});
            skLineSegment(sketch, "E6371", {"start": v(-43.78, -1.63) * mm, "end": v(-43.78, -1.75) * mm});
            skLineSegment(sketch, "E6372", {"start": v(-43.78, -1.75) * mm, "end": v(-43.77, -1.87) * mm});
            skLineSegment(sketch, "E6373", {"start": v(-43.77, -1.87) * mm, "end": v(-43.77, -1.88) * mm});
            skLineSegment(sketch, "E6374", {"start": v(-43.77, -1.88) * mm, "end": v(-43.88, -1.92) * mm});
            skLineSegment(sketch, "E6375", {"start": v(-43.88, -1.92) * mm, "end": v(-43.98, -1.96) * mm});
            skLineSegment(sketch, "E6376", {"start": v(-43.98, -1.96) * mm, "end": v(-44.1, -2) * mm});
            skLineSegment(sketch, "E6377", {"start": v(-44.1, -2) * mm, "end": v(-44.2, -2.04) * mm});
            skLineSegment(sketch, "E6378", {"start": v(-44.2, -2.04) * mm, "end": v(-44.31, -2.08) * mm});
            skLineSegment(sketch, "E6379", {"start": v(-44.31, -2.08) * mm, "end": v(-44.43, -2.13) * mm});
            skLineSegment(sketch, "E6380", {"start": v(-44.43, -2.13) * mm, "end": v(-44.55, -2.17) * mm});
            skLineSegment(sketch, "E6381", {"start": v(-44.55, -2.17) * mm, "end": v(-44.67, -2.22) * mm});
            skLineSegment(sketch, "E6382", {"start": v(-44.67, -2.22) * mm, "end": v(-44.78, -2.27) * mm});
            skLineSegment(sketch, "E6383", {"start": v(-44.78, -2.27) * mm, "end": v(-44.9, -2.32) * mm});
            skLineSegment(sketch, "E6384", {"start": v(-44.9, -2.32) * mm, "end": v(-45, -2.36) * mm});
            skLineSegment(sketch, "E6385", {"start": v(-45, -2.36) * mm, "end": v(-45.1, -2.41) * mm});
            skLineSegment(sketch, "E6386", {"start": v(-45.1, -2.41) * mm, "end": v(-45.2, -2.46) * mm});
            skLineSegment(sketch, "E6387", {"start": v(-45.2, -2.46) * mm, "end": v(-45.31, -2.5) * mm});
            skLineSegment(sketch, "E6388", {"start": v(-45.31, -2.5) * mm, "end": v(-45.42, -2.56) * mm});
            skLineSegment(sketch, "E6389", {"start": v(-45.42, -2.56) * mm, "end": v(-45.53, -2.61) * mm});
            skLineSegment(sketch, "E6390", {"start": v(-45.53, -2.61) * mm, "end": v(-45.64, -2.67) * mm});
            skLineSegment(sketch, "E6391", {"start": v(-45.64, -2.67) * mm, "end": v(-45.75, -2.73) * mm});
            skLineSegment(sketch, "E6392", {"start": v(-45.75, -2.73) * mm, "end": v(-45.87, -2.78) * mm});
            skLineSegment(sketch, "E6393", {"start": v(-45.87, -2.78) * mm, "end": v(-45.87, -2.78) * mm});
            skLineSegment(sketch, "E6394", {"start": v(-45.87, -2.78) * mm, "end": v(-45.86, -2.9) * mm});
            skLineSegment(sketch, "E6395", {"start": v(-45.86, -2.9) * mm, "end": v(-45.85, -3.02) * mm});
            skLineSegment(sketch, "E6396", {"start": v(-45.85, -3.02) * mm, "end": v(-45.85, -3.13) * mm});
            skLineSegment(sketch, "E6397", {"start": v(-45.85, -3.13) * mm, "end": v(-45.84, -3.25) * mm});
            skLineSegment(sketch, "E6398", {"start": v(-45.84, -3.25) * mm, "end": v(-45.83, -3.35) * mm});
            skLineSegment(sketch, "E6399", {"start": v(-45.83, -3.35) * mm, "end": v(-45.72, -3.39) * mm});
            skLineSegment(sketch, "E6400", {"start": v(-45.72, -3.39) * mm, "end": v(-45.6, -3.43) * mm});
            skLineSegment(sketch, "E6401", {"start": v(-45.6, -3.43) * mm, "end": v(-45.5, -3.46) * mm});
            skLineSegment(sketch, "E6402", {"start": v(-45.5, -3.46) * mm, "end": v(-45.38, -3.5) * mm});
            skLineSegment(sketch, "E6403", {"start": v(-45.38, -3.5) * mm, "end": v(-45.27, -3.54) * mm});
            skLineSegment(sketch, "E6404", {"start": v(-45.27, -3.54) * mm, "end": v(-45.15, -3.57) * mm});
            skLineSegment(sketch, "E6405", {"start": v(-45.15, -3.57) * mm, "end": v(-45.04, -3.6) * mm});
            skLineSegment(sketch, "E6406", {"start": v(-45.04, -3.6) * mm, "end": v(-44.93, -3.64) * mm});
            skLineSegment(sketch, "E6407", {"start": v(-44.93, -3.64) * mm, "end": v(-44.81, -3.68) * mm});
            skLineSegment(sketch, "E6408", {"start": v(-44.81, -3.68) * mm, "end": v(-44.69, -3.7) * mm});
            skLineSegment(sketch, "E6409", {"start": v(-44.69, -3.7) * mm, "end": v(-44.57, -3.74) * mm});
            skLineSegment(sketch, "E6410", {"start": v(-44.57, -3.74) * mm, "end": v(-44.46, -3.77) * mm});
            skLineSegment(sketch, "E6411", {"start": v(-44.46, -3.77) * mm, "end": v(-44.34, -3.8) * mm});
            skLineSegment(sketch, "E6412", {"start": v(-44.34, -3.8) * mm, "end": v(-44.23, -3.83) * mm});
            skLineSegment(sketch, "E6413", {"start": v(-44.23, -3.83) * mm, "end": v(-44.1, -3.86) * mm});
            skLineSegment(sketch, "E6414", {"start": v(-44.1, -3.86) * mm, "end": v(-44, -3.88) * mm});
            skLineSegment(sketch, "E6415", {"start": v(-44, -3.88) * mm, "end": v(-43.88, -3.91) * mm});
            skLineSegment(sketch, "E6416", {"start": v(-43.88, -3.91) * mm, "end": v(-43.76, -3.94) * mm});
            skLineSegment(sketch, "E6417", {"start": v(-43.76, -3.94) * mm, "end": v(-43.63, -3.96) * mm});
            skLineSegment(sketch, "E6418", {"start": v(-43.63, -3.96) * mm, "end": v(-43.62, -4.08) * mm});
            skLineSegment(sketch, "E6419", {"start": v(-43.62, -4.08) * mm, "end": v(-43.6, -4.2) * mm});
            skLineSegment(sketch, "E6420", {"start": v(-43.6, -4.2) * mm, "end": v(-43.6, -4.32) * mm});
            skLineSegment(sketch, "E6421", {"start": v(-43.6, -4.32) * mm, "end": v(-43.59, -4.43) * mm});
            skLineSegment(sketch, "E6422", {"start": v(-43.59, -4.43) * mm, "end": v(-43.57, -4.55) * mm});
            skLineSegment(sketch, "E6423", {"start": v(-43.57, -4.55) * mm, "end": v(-43.56, -4.67) * mm});
            skLineSegment(sketch, "E6424", {"start": v(-43.56, -4.67) * mm, "end": v(-43.55, -4.79) * mm});
            skLineSegment(sketch, "E6425", {"start": v(-43.55, -4.79) * mm, "end": v(-43.55, -4.8) * mm});
            skLineSegment(sketch, "E6426", {"start": v(-43.55, -4.8) * mm, "end": v(-43.65, -4.85) * mm});
            skLineSegment(sketch, "E6427", {"start": v(-43.65, -4.85) * mm, "end": v(-43.75, -4.89) * mm});
            skLineSegment(sketch, "E6428", {"start": v(-43.75, -4.89) * mm, "end": v(-43.86, -4.94) * mm});
            skLineSegment(sketch, "E6429", {"start": v(-43.86, -4.94) * mm, "end": v(-43.97, -4.98) * mm});
            skLineSegment(sketch, "E6430", {"start": v(-43.97, -4.98) * mm, "end": v(-44.08, -5.04) * mm});
            skLineSegment(sketch, "E6431", {"start": v(-44.08, -5.04) * mm, "end": v(-44.19, -5.09) * mm});
            skLineSegment(sketch, "E6432", {"start": v(-44.19, -5.09) * mm, "end": v(-44.3, -5.14) * mm});
            skLineSegment(sketch, "E6433", {"start": v(-44.3, -5.14) * mm, "end": v(-44.42, -5.2) * mm});
            skLineSegment(sketch, "E6434", {"start": v(-44.42, -5.2) * mm, "end": v(-44.53, -5.26) * mm});
            skLineSegment(sketch, "E6435", {"start": v(-44.53, -5.26) * mm, "end": v(-44.64, -5.31) * mm});
            skLineSegment(sketch, "E6436", {"start": v(-44.64, -5.31) * mm, "end": v(-44.74, -5.36) * mm});
            skLineSegment(sketch, "E6437", {"start": v(-44.74, -5.36) * mm, "end": v(-44.84, -5.42) * mm});
            skLineSegment(sketch, "E6438", {"start": v(-44.84, -5.42) * mm, "end": v(-44.94, -5.47) * mm});
            skLineSegment(sketch, "E6439", {"start": v(-44.94, -5.47) * mm, "end": v(-45.04, -5.53) * mm});
            skLineSegment(sketch, "E6440", {"start": v(-45.04, -5.53) * mm, "end": v(-45.15, -5.59) * mm});
            skLineSegment(sketch, "E6441", {"start": v(-45.15, -5.59) * mm, "end": v(-45.25, -5.65) * mm});
            skLineSegment(sketch, "E6442", {"start": v(-45.25, -5.65) * mm, "end": v(-45.36, -5.71) * mm});
            skLineSegment(sketch, "E6443", {"start": v(-45.36, -5.71) * mm, "end": v(-45.47, -5.78) * mm});
            skLineSegment(sketch, "E6444", {"start": v(-45.47, -5.78) * mm, "end": v(-45.58, -5.84) * mm});
            skLineSegment(sketch, "E6445", {"start": v(-45.58, -5.84) * mm, "end": v(-45.58, -5.84) * mm});
            skLineSegment(sketch, "E6446", {"start": v(-45.58, -5.84) * mm, "end": v(-45.57, -5.96) * mm});
            skLineSegment(sketch, "E6447", {"start": v(-45.57, -5.96) * mm, "end": v(-45.55, -6.08) * mm});
            skLineSegment(sketch, "E6448", {"start": v(-45.55, -6.08) * mm, "end": v(-45.54, -6.19) * mm});
            skLineSegment(sketch, "E6449", {"start": v(-45.54, -6.19) * mm, "end": v(-45.52, -6.3) * mm});
            skLineSegment(sketch, "E6450", {"start": v(-45.52, -6.3) * mm, "end": v(-45.5, -6.4) * mm});
            skLineSegment(sketch, "E6451", {"start": v(-45.5, -6.4) * mm, "end": v(-45.4, -6.43) * mm});
            skLineSegment(sketch, "E6452", {"start": v(-45.4, -6.43) * mm, "end": v(-45.27, -6.46) * mm});
            skLineSegment(sketch, "E6453", {"start": v(-45.27, -6.46) * mm, "end": v(-45.16, -6.5) * mm});
            skLineSegment(sketch, "E6454", {"start": v(-45.16, -6.5) * mm, "end": v(-45.05, -6.52) * mm});
            skLineSegment(sketch, "E6455", {"start": v(-45.05, -6.52) * mm, "end": v(-44.93, -6.55) * mm});
            skLineSegment(sketch, "E6456", {"start": v(-44.93, -6.55) * mm, "end": v(-44.81, -6.58) * mm});
            skLineSegment(sketch, "E6457", {"start": v(-44.81, -6.58) * mm, "end": v(-44.7, -6.6) * mm});
            skLineSegment(sketch, "E6458", {"start": v(-44.7, -6.6) * mm, "end": v(-44.58, -6.63) * mm});
            skLineSegment(sketch, "E6459", {"start": v(-44.58, -6.63) * mm, "end": v(-44.46, -6.66) * mm});
            skLineSegment(sketch, "E6460", {"start": v(-44.46, -6.66) * mm, "end": v(-44.34, -6.69) * mm});
            skLineSegment(sketch, "E6461", {"start": v(-44.34, -6.69) * mm, "end": v(-44.22, -6.71) * mm});
            skLineSegment(sketch, "E6462", {"start": v(-44.22, -6.71) * mm, "end": v(-44.1, -6.73) * mm});
            skLineSegment(sketch, "E6463", {"start": v(-44.1, -6.73) * mm, "end": v(-43.99, -6.75) * mm});
            skLineSegment(sketch, "E6464", {"start": v(-43.99, -6.75) * mm, "end": v(-43.87, -6.78) * mm});
            skLineSegment(sketch, "E6465", {"start": v(-43.87, -6.78) * mm, "end": v(-43.75, -6.8) * mm});
            skLineSegment(sketch, "E6466", {"start": v(-43.75, -6.8) * mm, "end": v(-43.64, -6.81) * mm});
            skLineSegment(sketch, "E6467", {"start": v(-43.64, -6.81) * mm, "end": v(-43.52, -6.83) * mm});
            skLineSegment(sketch, "E6468", {"start": v(-43.52, -6.83) * mm, "end": v(-43.4, -6.85) * mm});
            skLineSegment(sketch, "E6469", {"start": v(-43.4, -6.85) * mm, "end": v(-43.27, -6.87) * mm});
            skLineSegment(sketch, "E6470", {"start": v(-43.27, -6.87) * mm, "end": v(-43.25, -6.98) * mm});
            skLineSegment(sketch, "E6471", {"start": v(-43.25, -6.98) * mm, "end": v(-43.23, -7.1) * mm});
            skLineSegment(sketch, "E6472", {"start": v(-43.23, -7.1) * mm, "end": v(-43.21, -7.22) * mm});
            skLineSegment(sketch, "E6473", {"start": v(-43.21, -7.22) * mm, "end": v(-43.2, -7.33) * mm});
            skLineSegment(sketch, "E6474", {"start": v(-43.2, -7.33) * mm, "end": v(-43.17, -7.45) * mm});
            skLineSegment(sketch, "E6475", {"start": v(-43.17, -7.45) * mm, "end": v(-43.15, -7.57) * mm});
            skLineSegment(sketch, "E6476", {"start": v(-43.15, -7.57) * mm, "end": v(-43.13, -7.68) * mm});
            skLineSegment(sketch, "E6477", {"start": v(-43.13, -7.68) * mm, "end": v(-43.13, -7.7) * mm});
            skLineSegment(sketch, "E6478", {"start": v(-43.13, -7.7) * mm, "end": v(-43.23, -7.75) * mm});
            skLineSegment(sketch, "E6479", {"start": v(-43.23, -7.75) * mm, "end": v(-43.33, -7.8) * mm});
            skLineSegment(sketch, "E6480", {"start": v(-43.33, -7.8) * mm, "end": v(-43.43, -7.85) * mm});
            skLineSegment(sketch, "E6481", {"start": v(-43.43, -7.85) * mm, "end": v(-43.53, -7.9) * mm});
            skLineSegment(sketch, "E6482", {"start": v(-43.53, -7.9) * mm, "end": v(-43.64, -7.97) * mm});
            skLineSegment(sketch, "E6483", {"start": v(-43.64, -7.97) * mm, "end": v(-43.75, -8.03) * mm});
            skLineSegment(sketch, "E6484", {"start": v(-43.75, -8.03) * mm, "end": v(-43.86, -8.1) * mm});
            skLineSegment(sketch, "E6485", {"start": v(-43.86, -8.1) * mm, "end": v(-43.97, -8.16) * mm});
            skLineSegment(sketch, "E6486", {"start": v(-43.97, -8.16) * mm, "end": v(-44.08, -8.22) * mm});
            skLineSegment(sketch, "E6487", {"start": v(-44.08, -8.22) * mm, "end": v(-44.18, -8.28) * mm});
            skLineSegment(sketch, "E6488", {"start": v(-44.18, -8.28) * mm, "end": v(-44.28, -8.34) * mm});
            skLineSegment(sketch, "E6489", {"start": v(-44.28, -8.34) * mm, "end": v(-44.38, -8.4) * mm});
            skLineSegment(sketch, "E6490", {"start": v(-44.38, -8.4) * mm, "end": v(-44.47, -8.46) * mm});
            skLineSegment(sketch, "E6491", {"start": v(-44.47, -8.46) * mm, "end": v(-44.57, -8.53) * mm});
            skLineSegment(sketch, "E6492", {"start": v(-44.57, -8.53) * mm, "end": v(-44.67, -8.6) * mm});
            skLineSegment(sketch, "E6493", {"start": v(-44.67, -8.6) * mm, "end": v(-44.77, -8.66) * mm});
            skLineSegment(sketch, "E6494", {"start": v(-44.77, -8.66) * mm, "end": v(-44.88, -8.73) * mm});
            skLineSegment(sketch, "E6495", {"start": v(-44.88, -8.73) * mm, "end": v(-44.98, -8.8) * mm});
            skLineSegment(sketch, "E6496", {"start": v(-44.98, -8.8) * mm, "end": v(-45.09, -8.87) * mm});
            skLineSegment(sketch, "E6497", {"start": v(-45.09, -8.87) * mm, "end": v(-45.09, -8.87) * mm});
            skLineSegment(sketch, "E6498", {"start": v(-45.09, -8.87) * mm, "end": v(-45.07, -9) * mm});
            skLineSegment(sketch, "E6499", {"start": v(-45.07, -9) * mm, "end": v(-45.04, -9.1) * mm});
            skLineSegment(sketch, "E6500", {"start": v(-45.04, -9.1) * mm, "end": v(-45.02, -9.21) * mm});
            skLineSegment(sketch, "E6501", {"start": v(-45.02, -9.21) * mm, "end": v(-45, -9.33) * mm});
            skLineSegment(sketch, "E6502", {"start": v(-45, -9.33) * mm, "end": v(-44.98, -9.43) * mm});
            skLineSegment(sketch, "E6503", {"start": v(-44.98, -9.43) * mm, "end": v(-44.86, -9.45) * mm});
            skLineSegment(sketch, "E6504", {"start": v(-44.86, -9.45) * mm, "end": v(-44.74, -9.47) * mm});
            skLineSegment(sketch, "E6505", {"start": v(-44.74, -9.47) * mm, "end": v(-44.62, -9.5) * mm});
            skLineSegment(sketch, "E6506", {"start": v(-44.62, -9.5) * mm, "end": v(-44.51, -9.52) * mm});
            skLineSegment(sketch, "E6507", {"start": v(-44.51, -9.52) * mm, "end": v(-44.4, -9.54) * mm});
            skLineSegment(sketch, "E6508", {"start": v(-44.4, -9.54) * mm, "end": v(-44.27, -9.56) * mm});
            skLineSegment(sketch, "E6509", {"start": v(-44.27, -9.56) * mm, "end": v(-44.16, -9.58) * mm});
            skLineSegment(sketch, "E6510", {"start": v(-44.16, -9.58) * mm, "end": v(-44.04, -9.6) * mm});
            skLineSegment(sketch, "E6511", {"start": v(-44.04, -9.6) * mm, "end": v(-43.92, -9.61) * mm});
            skLineSegment(sketch, "E6512", {"start": v(-43.92, -9.61) * mm, "end": v(-43.8, -9.63) * mm});
            skLineSegment(sketch, "E6513", {"start": v(-43.8, -9.63) * mm, "end": v(-43.68, -9.65) * mm});
            skLineSegment(sketch, "E6514", {"start": v(-43.68, -9.65) * mm, "end": v(-43.56, -9.66) * mm});
            skLineSegment(sketch, "E6515", {"start": v(-43.56, -9.66) * mm, "end": v(-43.44, -9.68) * mm});
            skLineSegment(sketch, "E6516", {"start": v(-43.44, -9.68) * mm, "end": v(-43.32, -9.7) * mm});
            skLineSegment(sketch, "E6517", {"start": v(-43.32, -9.7) * mm, "end": v(-43.2, -9.7) * mm});
            skLineSegment(sketch, "E6518", {"start": v(-43.2, -9.7) * mm, "end": v(-43.08, -9.71) * mm});
            skLineSegment(sketch, "E6519", {"start": v(-43.08, -9.71) * mm, "end": v(-42.96, -9.72) * mm});
            skLineSegment(sketch, "E6520", {"start": v(-42.96, -9.72) * mm, "end": v(-42.84, -9.73) * mm});
            skLineSegment(sketch, "E6521", {"start": v(-42.84, -9.73) * mm, "end": v(-42.71, -9.74) * mm});
            skLineSegment(sketch, "E6522", {"start": v(-42.71, -9.74) * mm, "end": v(-42.69, -9.86) * mm});
            skLineSegment(sketch, "E6523", {"start": v(-42.69, -9.86) * mm, "end": v(-42.66, -9.97) * mm});
            skLineSegment(sketch, "E6524", {"start": v(-42.66, -9.97) * mm, "end": v(-42.63, -10.09) * mm});
            skLineSegment(sketch, "E6525", {"start": v(-42.63, -10.09) * mm, "end": v(-42.6, -10.2) * mm});
            skLineSegment(sketch, "E6526", {"start": v(-42.6, -10.2) * mm, "end": v(-42.58, -10.32) * mm});
            skLineSegment(sketch, "E6527", {"start": v(-42.58, -10.32) * mm, "end": v(-42.55, -10.43) * mm});
            skLineSegment(sketch, "E6528", {"start": v(-42.55, -10.43) * mm, "end": v(-42.52, -10.55) * mm});
            skLineSegment(sketch, "E6529", {"start": v(-42.52, -10.55) * mm, "end": v(-42.52, -10.56) * mm});
            skLineSegment(sketch, "E6530", {"start": v(-42.52, -10.56) * mm, "end": v(-42.61, -10.62) * mm});
            skLineSegment(sketch, "E6531", {"start": v(-42.61, -10.62) * mm, "end": v(-42.71, -10.68) * mm});
            skLineSegment(sketch, "E6532", {"start": v(-42.71, -10.68) * mm, "end": v(-42.8, -10.74) * mm});
            skLineSegment(sketch, "E6533", {"start": v(-42.8, -10.74) * mm, "end": v(-42.9, -10.8) * mm});
            skLineSegment(sketch, "E6534", {"start": v(-42.9, -10.8) * mm, "end": v(-43.01, -10.87) * mm});
            skLineSegment(sketch, "E6535", {"start": v(-43.01, -10.87) * mm, "end": v(-43.12, -10.93) * mm});
            skLineSegment(sketch, "E6536", {"start": v(-43.12, -10.93) * mm, "end": v(-43.22, -11) * mm});
            skLineSegment(sketch, "E6537", {"start": v(-43.22, -11) * mm, "end": v(-43.33, -11.08) * mm});
            skLineSegment(sketch, "E6538", {"start": v(-43.33, -11.08) * mm, "end": v(-43.43, -11.14) * mm});
            skLineSegment(sketch, "E6539", {"start": v(-43.43, -11.14) * mm, "end": v(-43.53, -11.22) * mm});
            skLineSegment(sketch, "E6540", {"start": v(-43.53, -11.22) * mm, "end": v(-43.62, -11.28) * mm});
            skLineSegment(sketch, "E6541", {"start": v(-43.62, -11.28) * mm, "end": v(-43.72, -11.35) * mm});
            skLineSegment(sketch, "E6542", {"start": v(-43.72, -11.35) * mm, "end": v(-43.8, -11.41) * mm});
            skLineSegment(sketch, "E6543", {"start": v(-43.8, -11.41) * mm, "end": v(-43.9, -11.48) * mm});
            skLineSegment(sketch, "E6544", {"start": v(-43.9, -11.48) * mm, "end": v(-44, -11.56) * mm});
            skLineSegment(sketch, "E6545", {"start": v(-44, -11.56) * mm, "end": v(-44.1, -11.63) * mm});
            skLineSegment(sketch, "E6546", {"start": v(-44.1, -11.63) * mm, "end": v(-44.2, -11.7) * mm});
            skLineSegment(sketch, "E6547", {"start": v(-44.2, -11.7) * mm, "end": v(-44.3, -11.78) * mm});
            skLineSegment(sketch, "E6548", {"start": v(-44.3, -11.78) * mm, "end": v(-44.4, -11.86) * mm});
            skLineSegment(sketch, "E6549", {"start": v(-44.4, -11.86) * mm, "end": v(-44.4, -11.86) * mm});
            skLineSegment(sketch, "E6550", {"start": v(-44.4, -11.86) * mm, "end": v(-44.36, -11.98) * mm});
            skLineSegment(sketch, "E6551", {"start": v(-44.36, -11.98) * mm, "end": v(-44.33, -12.1) * mm});
            skLineSegment(sketch, "E6552", {"start": v(-44.33, -12.1) * mm, "end": v(-44.3, -12.2) * mm});
            skLineSegment(sketch, "E6553", {"start": v(-44.3, -12.2) * mm, "end": v(-44.27, -12.31) * mm});
            skLineSegment(sketch, "E6554", {"start": v(-44.27, -12.31) * mm, "end": v(-44.25, -12.4) * mm});
            skLineSegment(sketch, "E6555", {"start": v(-44.25, -12.4) * mm, "end": v(-44.13, -12.43) * mm});
            skLineSegment(sketch, "E6556", {"start": v(-44.13, -12.43) * mm, "end": v(-44, -12.44) * mm});
            skLineSegment(sketch, "E6557", {"start": v(-44, -12.44) * mm, "end": v(-43.89, -12.46) * mm});
            skLineSegment(sketch, "E6558", {"start": v(-43.89, -12.46) * mm, "end": v(-43.77, -12.47) * mm});
            skLineSegment(sketch, "E6559", {"start": v(-43.77, -12.47) * mm, "end": v(-43.66, -12.48) * mm});
            skLineSegment(sketch, "E6560", {"start": v(-43.66, -12.48) * mm, "end": v(-43.54, -12.5) * mm});
            skLineSegment(sketch, "E6561", {"start": v(-43.54, -12.5) * mm, "end": v(-43.42, -12.5) * mm});
            skLineSegment(sketch, "E6562", {"start": v(-43.42, -12.5) * mm, "end": v(-43.3, -12.52) * mm});
            skLineSegment(sketch, "E6563", {"start": v(-43.3, -12.52) * mm, "end": v(-43.18, -12.53) * mm});
            skLineSegment(sketch, "E6564", {"start": v(-43.18, -12.53) * mm, "end": v(-43.05, -12.54) * mm});
            skLineSegment(sketch, "E6565", {"start": v(-43.05, -12.54) * mm, "end": v(-42.93, -12.54) * mm});
            skLineSegment(sketch, "E6566", {"start": v(-42.93, -12.54) * mm, "end": v(-42.82, -12.55) * mm});
            skLineSegment(sketch, "E6567", {"start": v(-42.82, -12.55) * mm, "end": v(-42.7, -12.56) * mm});
            skLineSegment(sketch, "E6568", {"start": v(-42.7, -12.56) * mm, "end": v(-42.58, -12.56) * mm});
            skLineSegment(sketch, "E6569", {"start": v(-42.58, -12.56) * mm, "end": v(-42.46, -12.57) * mm});
            skLineSegment(sketch, "E6570", {"start": v(-42.46, -12.57) * mm, "end": v(-42.34, -12.57) * mm});
            skLineSegment(sketch, "E6571", {"start": v(-42.34, -12.57) * mm, "end": v(-42.22, -12.57) * mm});
            skLineSegment(sketch, "E6572", {"start": v(-42.22, -12.57) * mm, "end": v(-42.1, -12.57) * mm});
            skLineSegment(sketch, "E6573", {"start": v(-42.1, -12.57) * mm, "end": v(-41.97, -12.57) * mm});
            skLineSegment(sketch, "E6574", {"start": v(-41.97, -12.57) * mm, "end": v(-41.93, -12.69) * mm});
            skLineSegment(sketch, "E6575", {"start": v(-41.93, -12.69) * mm, "end": v(-41.9, -12.8) * mm});
            skLineSegment(sketch, "E6576", {"start": v(-41.9, -12.8) * mm, "end": v(-41.86, -12.91) * mm});
            skLineSegment(sketch, "E6577", {"start": v(-41.86, -12.91) * mm, "end": v(-41.83, -13.02) * mm});
            skLineSegment(sketch, "E6578", {"start": v(-41.83, -13.02) * mm, "end": v(-41.8, -13.14) * mm});
            skLineSegment(sketch, "E6579", {"start": v(-41.8, -13.14) * mm, "end": v(-41.76, -13.25) * mm});
            skLineSegment(sketch, "E6580", {"start": v(-41.76, -13.25) * mm, "end": v(-41.72, -13.37) * mm});
            skLineSegment(sketch, "E6581", {"start": v(-41.72, -13.37) * mm, "end": v(-41.72, -13.38) * mm});
            skLineSegment(sketch, "E6582", {"start": v(-41.72, -13.38) * mm, "end": v(-41.8, -13.44) * mm});
            skLineSegment(sketch, "E6583", {"start": v(-41.8, -13.44) * mm, "end": v(-41.9, -13.5) * mm});
            skLineSegment(sketch, "E6584", {"start": v(-41.9, -13.5) * mm, "end": v(-42, -13.57) * mm});
            skLineSegment(sketch, "E6585", {"start": v(-42, -13.57) * mm, "end": v(-42.1, -13.64) * mm});
            skLineSegment(sketch, "E6586", {"start": v(-42.1, -13.64) * mm, "end": v(-42.19, -13.71) * mm});
            skLineSegment(sketch, "E6587", {"start": v(-42.19, -13.71) * mm, "end": v(-42.29, -13.79) * mm});
            skLineSegment(sketch, "E6588", {"start": v(-42.29, -13.79) * mm, "end": v(-42.4, -13.87) * mm});
            skLineSegment(sketch, "E6589", {"start": v(-42.4, -13.87) * mm, "end": v(-42.5, -13.95) * mm});
            skLineSegment(sketch, "E6590", {"start": v(-42.5, -13.95) * mm, "end": v(-42.59, -14.02) * mm});
            skLineSegment(sketch, "E6591", {"start": v(-42.59, -14.02) * mm, "end": v(-42.69, -14.1) * mm});
            skLineSegment(sketch, "E6592", {"start": v(-42.69, -14.1) * mm, "end": v(-42.77, -14.17) * mm});
            skLineSegment(sketch, "E6593", {"start": v(-42.77, -14.17) * mm, "end": v(-42.86, -14.24) * mm});
            skLineSegment(sketch, "E6594", {"start": v(-42.86, -14.24) * mm, "end": v(-42.95, -14.31) * mm});
            skLineSegment(sketch, "E6595", {"start": v(-42.95, -14.31) * mm, "end": v(-43.04, -14.4) * mm});
            skLineSegment(sketch, "E6596", {"start": v(-43.04, -14.4) * mm, "end": v(-43.13, -14.47) * mm});
            skLineSegment(sketch, "E6597", {"start": v(-43.13, -14.47) * mm, "end": v(-43.22, -14.55) * mm});
            skLineSegment(sketch, "E6598", {"start": v(-43.22, -14.55) * mm, "end": v(-43.31, -14.63) * mm});
            skLineSegment(sketch, "E6599", {"start": v(-43.31, -14.63) * mm, "end": v(-43.4, -14.72) * mm});
            skLineSegment(sketch, "E6600", {"start": v(-43.4, -14.72) * mm, "end": v(-43.5, -14.8) * mm});
            skLineSegment(sketch, "E6601", {"start": v(-43.5, -14.8) * mm, "end": v(-43.5, -14.8) * mm});
            skLineSegment(sketch, "E6602", {"start": v(-43.5, -14.8) * mm, "end": v(-43.46, -14.92) * mm});
            skLineSegment(sketch, "E6603", {"start": v(-43.46, -14.92) * mm, "end": v(-43.43, -15.03) * mm});
            skLineSegment(sketch, "E6604", {"start": v(-43.43, -15.03) * mm, "end": v(-43.4, -15.13) * mm});
            skLineSegment(sketch, "E6605", {"start": v(-43.4, -15.13) * mm, "end": v(-43.35, -15.24) * mm});
            skLineSegment(sketch, "E6606", {"start": v(-43.35, -15.24) * mm, "end": v(-43.32, -15.34) * mm});
            skLineSegment(sketch, "E6607", {"start": v(-43.32, -15.34) * mm, "end": v(-43.2, -15.34) * mm});
            skLineSegment(sketch, "E6608", {"start": v(-43.2, -15.34) * mm, "end": v(-43.08, -15.35) * mm});
            skLineSegment(sketch, "E6609", {"start": v(-43.08, -15.35) * mm, "end": v(-42.96, -15.36) * mm});
            skLineSegment(sketch, "E6610", {"start": v(-42.96, -15.36) * mm, "end": v(-42.84, -15.37) * mm});
            skLineSegment(sketch, "E6611", {"start": v(-42.84, -15.37) * mm, "end": v(-42.72, -15.37) * mm});
            skLineSegment(sketch, "E6612", {"start": v(-42.72, -15.37) * mm, "end": v(-42.6, -15.37) * mm});
            skLineSegment(sketch, "E6613", {"start": v(-42.6, -15.37) * mm, "end": v(-42.49, -15.38) * mm});
            skLineSegment(sketch, "E6614", {"start": v(-42.49, -15.38) * mm, "end": v(-42.37, -15.38) * mm});
            skLineSegment(sketch, "E6615", {"start": v(-42.37, -15.38) * mm, "end": v(-42.25, -15.38) * mm});
            skLineSegment(sketch, "E6616", {"start": v(-42.25, -15.38) * mm, "end": v(-42.12, -15.38) * mm});
            skLineSegment(sketch, "E6617", {"start": v(-42.12, -15.38) * mm, "end": v(-42, -15.38) * mm});
            skLineSegment(sketch, "E6618", {"start": v(-42, -15.38) * mm, "end": v(-41.88, -15.38) * mm});
            skLineSegment(sketch, "E6619", {"start": v(-41.88, -15.38) * mm, "end": v(-41.76, -15.38) * mm});
            skLineSegment(sketch, "E6620", {"start": v(-41.76, -15.38) * mm, "end": v(-41.64, -15.38) * mm});
            skLineSegment(sketch, "E6621", {"start": v(-41.64, -15.38) * mm, "end": v(-41.52, -15.37) * mm});
            skLineSegment(sketch, "E6622", {"start": v(-41.52, -15.37) * mm, "end": v(-41.4, -15.37) * mm});
            skLineSegment(sketch, "E6623", {"start": v(-41.4, -15.37) * mm, "end": v(-41.28, -15.36) * mm});
            skLineSegment(sketch, "E6624", {"start": v(-41.28, -15.36) * mm, "end": v(-41.16, -15.36) * mm});
            skLineSegment(sketch, "E6625", {"start": v(-41.16, -15.36) * mm, "end": v(-41.03, -15.35) * mm});
            skLineSegment(sketch, "E6626", {"start": v(-41.03, -15.35) * mm, "end": v(-41, -15.46) * mm});
            skLineSegment(sketch, "E6627", {"start": v(-41, -15.46) * mm, "end": v(-40.95, -15.57) * mm});
            skLineSegment(sketch, "E6628", {"start": v(-40.95, -15.57) * mm, "end": v(-40.9, -15.68) * mm});
            skLineSegment(sketch, "E6629", {"start": v(-40.9, -15.68) * mm, "end": v(-40.87, -15.79) * mm});
            skLineSegment(sketch, "E6630", {"start": v(-40.87, -15.79) * mm, "end": v(-40.82, -15.9) * mm});
            skLineSegment(sketch, "E6631", {"start": v(-40.82, -15.9) * mm, "end": v(-40.78, -16.01) * mm});
            skLineSegment(sketch, "E6632", {"start": v(-40.78, -16.01) * mm, "end": v(-40.74, -16.12) * mm});
            skLineSegment(sketch, "E6633", {"start": v(-40.74, -16.12) * mm, "end": v(-40.73, -16.14) * mm});
            skLineSegment(sketch, "E6634", {"start": v(-40.73, -16.14) * mm, "end": v(-40.82, -16.2) * mm});
            skLineSegment(sketch, "E6635", {"start": v(-40.82, -16.2) * mm, "end": v(-40.9, -16.27) * mm});
            skLineSegment(sketch, "E6636", {"start": v(-40.9, -16.27) * mm, "end": v(-41, -16.35) * mm});
            skLineSegment(sketch, "E6637", {"start": v(-41, -16.35) * mm, "end": v(-41.09, -16.42) * mm});
            skLineSegment(sketch, "E6638", {"start": v(-41.09, -16.42) * mm, "end": v(-41.18, -16.5) * mm});
            skLineSegment(sketch, "E6639", {"start": v(-41.18, -16.5) * mm, "end": v(-41.27, -16.58) * mm});
            skLineSegment(sketch, "E6640", {"start": v(-41.27, -16.58) * mm, "end": v(-41.37, -16.67) * mm});
            skLineSegment(sketch, "E6641", {"start": v(-41.37, -16.67) * mm, "end": v(-41.47, -16.75) * mm});
            skLineSegment(sketch, "E6642", {"start": v(-41.47, -16.75) * mm, "end": v(-41.56, -16.83) * mm});
            skLineSegment(sketch, "E6643", {"start": v(-41.56, -16.83) * mm, "end": v(-41.65, -16.92) * mm});
            skLineSegment(sketch, "E6644", {"start": v(-41.65, -16.92) * mm, "end": v(-41.73, -17) * mm});
            skLineSegment(sketch, "E6645", {"start": v(-41.73, -17) * mm, "end": v(-41.81, -17.07) * mm});
            skLineSegment(sketch, "E6646", {"start": v(-41.81, -17.07) * mm, "end": v(-41.9, -17.15) * mm});
            skLineSegment(sketch, "E6647", {"start": v(-41.9, -17.15) * mm, "end": v(-41.98, -17.23) * mm});
            skLineSegment(sketch, "E6648", {"start": v(-41.98, -17.23) * mm, "end": v(-42.07, -17.32) * mm});
            skLineSegment(sketch, "E6649", {"start": v(-42.07, -17.32) * mm, "end": v(-42.15, -17.4) * mm});
            skLineSegment(sketch, "E6650", {"start": v(-42.15, -17.4) * mm, "end": v(-42.24, -17.5) * mm});
            skLineSegment(sketch, "E6651", {"start": v(-42.24, -17.5) * mm, "end": v(-42.33, -17.58) * mm});
            skLineSegment(sketch, "E6652", {"start": v(-42.33, -17.58) * mm, "end": v(-42.42, -17.68) * mm});
            skLineSegment(sketch, "E6653", {"start": v(-42.42, -17.68) * mm, "end": v(-42.42, -17.68) * mm});
            skLineSegment(sketch, "E6654", {"start": v(-42.42, -17.68) * mm, "end": v(-42.37, -17.79) * mm});
            skLineSegment(sketch, "E6655", {"start": v(-42.37, -17.79) * mm, "end": v(-42.32, -17.9) * mm});
            skLineSegment(sketch, "E6656", {"start": v(-42.32, -17.9) * mm, "end": v(-42.28, -18) * mm});
            skLineSegment(sketch, "E6657", {"start": v(-42.28, -18) * mm, "end": v(-42.24, -18.1) * mm});
            skLineSegment(sketch, "E6658", {"start": v(-42.24, -18.1) * mm, "end": v(-42.2, -18.2) * mm});
            skLineSegment(sketch, "E6659", {"start": v(-42.2, -18.2) * mm, "end": v(-42.08, -18.2) * mm});
            skLineSegment(sketch, "E6660", {"start": v(-42.08, -18.2) * mm, "end": v(-41.95, -18.2) * mm});
            skLineSegment(sketch, "E6661", {"start": v(-41.95, -18.2) * mm, "end": v(-41.84, -18.2) * mm});
            skLineSegment(sketch, "E6662", {"start": v(-41.84, -18.2) * mm, "end": v(-41.72, -18.2) * mm});
            skLineSegment(sketch, "E6663", {"start": v(-41.72, -18.2) * mm, "end": v(-41.6, -18.19) * mm});
            skLineSegment(sketch, "E6664", {"start": v(-41.6, -18.19) * mm, "end": v(-41.48, -18.19) * mm});
            skLineSegment(sketch, "E6665", {"start": v(-41.48, -18.19) * mm, "end": v(-41.36, -18.18) * mm});
            skLineSegment(sketch, "E6666", {"start": v(-41.36, -18.18) * mm, "end": v(-41.24, -18.18) * mm});
            skLineSegment(sketch, "E6667", {"start": v(-41.24, -18.18) * mm, "end": v(-41.12, -18.17) * mm});
            skLineSegment(sketch, "E6668", {"start": v(-41.12, -18.17) * mm, "end": v(-41, -18.16) * mm});
            skLineSegment(sketch, "E6669", {"start": v(-41, -18.16) * mm, "end": v(-40.88, -18.16) * mm});
            skLineSegment(sketch, "E6670", {"start": v(-40.88, -18.16) * mm, "end": v(-40.76, -18.15) * mm});
            skLineSegment(sketch, "E6671", {"start": v(-40.76, -18.15) * mm, "end": v(-40.64, -18.14) * mm});
            skLineSegment(sketch, "E6672", {"start": v(-40.64, -18.14) * mm, "end": v(-40.52, -18.13) * mm});
            skLineSegment(sketch, "E6673", {"start": v(-40.52, -18.13) * mm, "end": v(-40.4, -18.11) * mm});
            skLineSegment(sketch, "E6674", {"start": v(-40.4, -18.11) * mm, "end": v(-40.28, -18.1) * mm});
            skLineSegment(sketch, "E6675", {"start": v(-40.28, -18.1) * mm, "end": v(-40.16, -18.09) * mm});
            skLineSegment(sketch, "E6676", {"start": v(-40.16, -18.09) * mm, "end": v(-40.05, -18.07) * mm});
            skLineSegment(sketch, "E6677", {"start": v(-40.05, -18.07) * mm, "end": v(-39.92, -18.05) * mm});
            skLineSegment(sketch, "E6678", {"start": v(-39.92, -18.05) * mm, "end": v(-39.87, -18.16) * mm});
            skLineSegment(sketch, "E6679", {"start": v(-39.87, -18.16) * mm, "end": v(-39.82, -18.27) * mm});
            skLineSegment(sketch, "E6680", {"start": v(-39.82, -18.27) * mm, "end": v(-39.77, -18.38) * mm});
            skLineSegment(sketch, "E6681", {"start": v(-39.77, -18.38) * mm, "end": v(-39.72, -18.48) * mm});
            skLineSegment(sketch, "E6682", {"start": v(-39.72, -18.48) * mm, "end": v(-39.67, -18.6) * mm});
            skLineSegment(sketch, "E6683", {"start": v(-39.67, -18.6) * mm, "end": v(-39.62, -18.7) * mm});
            skLineSegment(sketch, "E6684", {"start": v(-39.62, -18.7) * mm, "end": v(-39.57, -18.8) * mm});
            skLineSegment(sketch, "E6685", {"start": v(-39.57, -18.8) * mm, "end": v(-39.56, -18.82) * mm});
            skLineSegment(sketch, "E6686", {"start": v(-39.56, -18.82) * mm, "end": v(-39.64, -18.9) * mm});
            skLineSegment(sketch, "E6687", {"start": v(-39.64, -18.9) * mm, "end": v(-39.73, -18.97) * mm});
            skLineSegment(sketch, "E6688", {"start": v(-39.73, -18.97) * mm, "end": v(-39.81, -19.05) * mm});
            skLineSegment(sketch, "E6689", {"start": v(-39.81, -19.05) * mm, "end": v(-39.9, -19.13) * mm});
            skLineSegment(sketch, "E6690", {"start": v(-39.9, -19.13) * mm, "end": v(-39.98, -19.21) * mm});
            skLineSegment(sketch, "E6691", {"start": v(-39.98, -19.21) * mm, "end": v(-40.07, -19.3) * mm});
            skLineSegment(sketch, "E6692", {"start": v(-40.07, -19.3) * mm, "end": v(-40.16, -19.4) * mm});
            skLineSegment(sketch, "E6693", {"start": v(-40.16, -19.4) * mm, "end": v(-40.26, -19.49) * mm});
            skLineSegment(sketch, "E6694", {"start": v(-40.26, -19.49) * mm, "end": v(-40.34, -19.57) * mm});
            skLineSegment(sketch, "E6695", {"start": v(-40.34, -19.57) * mm, "end": v(-40.42, -19.66) * mm});
            skLineSegment(sketch, "E6696", {"start": v(-40.42, -19.66) * mm, "end": v(-40.5, -19.74) * mm});
            skLineSegment(sketch, "E6697", {"start": v(-40.5, -19.74) * mm, "end": v(-40.58, -19.83) * mm});
            skLineSegment(sketch, "E6698", {"start": v(-40.58, -19.83) * mm, "end": v(-40.66, -19.91) * mm});
            skLineSegment(sketch, "E6699", {"start": v(-40.66, -19.91) * mm, "end": v(-40.74, -20) * mm});
            skLineSegment(sketch, "E6700", {"start": v(-40.74, -20) * mm, "end": v(-40.82, -20.09) * mm});
            skLineSegment(sketch, "E6701", {"start": v(-40.82, -20.09) * mm, "end": v(-40.9, -20.18) * mm});
            skLineSegment(sketch, "E6702", {"start": v(-40.9, -20.18) * mm, "end": v(-40.98, -20.27) * mm});
            skLineSegment(sketch, "E6703", {"start": v(-40.98, -20.27) * mm, "end": v(-41.06, -20.37) * mm});
            skLineSegment(sketch, "E6704", {"start": v(-41.06, -20.37) * mm, "end": v(-41.14, -20.47) * mm});
            skLineSegment(sketch, "E6705", {"start": v(-41.14, -20.47) * mm, "end": v(-41.14, -20.47) * mm});
            skLineSegment(sketch, "E6706", {"start": v(-41.14, -20.47) * mm, "end": v(-41.09, -20.58) * mm});
            skLineSegment(sketch, "E6707", {"start": v(-41.09, -20.58) * mm, "end": v(-41.03, -20.68) * mm});
            skLineSegment(sketch, "E6708", {"start": v(-41.03, -20.68) * mm, "end": v(-40.99, -20.78) * mm});
            skLineSegment(sketch, "E6709", {"start": v(-40.99, -20.78) * mm, "end": v(-40.93, -20.89) * mm});
            skLineSegment(sketch, "E6710", {"start": v(-40.93, -20.89) * mm, "end": v(-40.89, -20.97) * mm});
            skLineSegment(sketch, "E6711", {"start": v(-40.89, -20.97) * mm, "end": v(-40.77, -20.97) * mm});
            skLineSegment(sketch, "E6712", {"start": v(-40.77, -20.97) * mm, "end": v(-40.65, -20.96) * mm});
            skLineSegment(sketch, "E6713", {"start": v(-40.65, -20.96) * mm, "end": v(-40.53, -20.95) * mm});
            skLineSegment(sketch, "E6714", {"start": v(-40.53, -20.95) * mm, "end": v(-40.41, -20.94) * mm});
            skLineSegment(sketch, "E6715", {"start": v(-40.41, -20.94) * mm, "end": v(-40.3, -20.93) * mm});
            skLineSegment(sketch, "E6716", {"start": v(-40.3, -20.93) * mm, "end": v(-40.18, -20.92) * mm});
            skLineSegment(sketch, "E6717", {"start": v(-40.18, -20.92) * mm, "end": v(-40.06, -20.9) * mm});
            skLineSegment(sketch, "E6718", {"start": v(-40.06, -20.9) * mm, "end": v(-39.94, -20.9) * mm});
            skLineSegment(sketch, "E6719", {"start": v(-39.94, -20.9) * mm, "end": v(-39.82, -20.88) * mm});
            skLineSegment(sketch, "E6720", {"start": v(-39.82, -20.88) * mm, "end": v(-39.7, -20.86) * mm});
            skLineSegment(sketch, "E6721", {"start": v(-39.7, -20.86) * mm, "end": v(-39.57, -20.84) * mm});
            skLineSegment(sketch, "E6722", {"start": v(-39.57, -20.84) * mm, "end": v(-39.46, -20.83) * mm});
            skLineSegment(sketch, "E6723", {"start": v(-39.46, -20.83) * mm, "end": v(-39.34, -20.81) * mm});
            skLineSegment(sketch, "E6724", {"start": v(-39.34, -20.81) * mm, "end": v(-39.22, -20.8) * mm});
            skLineSegment(sketch, "E6725", {"start": v(-39.22, -20.8) * mm, "end": v(-39.1, -20.77) * mm});
            skLineSegment(sketch, "E6726", {"start": v(-39.1, -20.77) * mm, "end": v(-38.98, -20.75) * mm});
            skLineSegment(sketch, "E6727", {"start": v(-38.98, -20.75) * mm, "end": v(-38.87, -20.73) * mm});
            skLineSegment(sketch, "E6728", {"start": v(-38.87, -20.73) * mm, "end": v(-38.75, -20.7) * mm});
            skLineSegment(sketch, "E6729", {"start": v(-38.75, -20.7) * mm, "end": v(-38.62, -20.68) * mm});
            skLineSegment(sketch, "E6730", {"start": v(-38.62, -20.68) * mm, "end": v(-38.57, -20.78) * mm});
            skLineSegment(sketch, "E6731", {"start": v(-38.57, -20.78) * mm, "end": v(-38.5, -20.89) * mm});
            skLineSegment(sketch, "E6732", {"start": v(-38.5, -20.89) * mm, "end": v(-38.45, -21) * mm});
            skLineSegment(sketch, "E6733", {"start": v(-38.45, -21) * mm, "end": v(-38.4, -21.1) * mm});
            skLineSegment(sketch, "E6734", {"start": v(-38.4, -21.1) * mm, "end": v(-38.34, -21.2) * mm});
            skLineSegment(sketch, "E6735", {"start": v(-38.34, -21.2) * mm, "end": v(-38.28, -21.3) * mm});
            skLineSegment(sketch, "E6736", {"start": v(-38.28, -21.3) * mm, "end": v(-38.23, -21.4) * mm});
            skLineSegment(sketch, "E6737", {"start": v(-38.23, -21.4) * mm, "end": v(-38.22, -21.42) * mm});
            skLineSegment(sketch, "E6738", {"start": v(-38.22, -21.42) * mm, "end": v(-38.3, -21.5) * mm});
            skLineSegment(sketch, "E6739", {"start": v(-38.3, -21.5) * mm, "end": v(-38.37, -21.58) * mm});
            skLineSegment(sketch, "E6740", {"start": v(-38.37, -21.58) * mm, "end": v(-38.45, -21.67) * mm});
            skLineSegment(sketch, "E6741", {"start": v(-38.45, -21.67) * mm, "end": v(-38.53, -21.75) * mm});
            skLineSegment(sketch, "E6742", {"start": v(-38.53, -21.75) * mm, "end": v(-38.61, -21.84) * mm});
            skLineSegment(sketch, "E6743", {"start": v(-38.61, -21.84) * mm, "end": v(-38.7, -21.93) * mm});
            skLineSegment(sketch, "E6744", {"start": v(-38.7, -21.93) * mm, "end": v(-38.78, -22.03) * mm});
            skLineSegment(sketch, "E6745", {"start": v(-38.78, -22.03) * mm, "end": v(-38.86, -22.13) * mm});
            skLineSegment(sketch, "E6746", {"start": v(-38.86, -22.13) * mm, "end": v(-38.94, -22.22) * mm});
            skLineSegment(sketch, "E6747", {"start": v(-38.94, -22.22) * mm, "end": v(-39.02, -22.32) * mm});
            skLineSegment(sketch, "E6748", {"start": v(-39.02, -22.32) * mm, "end": v(-39.1, -22.4) * mm});
            skLineSegment(sketch, "E6749", {"start": v(-39.1, -22.4) * mm, "end": v(-39.16, -22.5) * mm});
            skLineSegment(sketch, "E6750", {"start": v(-39.16, -22.5) * mm, "end": v(-39.24, -22.58) * mm});
            skLineSegment(sketch, "E6751", {"start": v(-39.24, -22.58) * mm, "end": v(-39.3, -22.68) * mm});
            skLineSegment(sketch, "E6752", {"start": v(-39.3, -22.68) * mm, "end": v(-39.38, -22.77) * mm});
            skLineSegment(sketch, "E6753", {"start": v(-39.38, -22.77) * mm, "end": v(-39.46, -22.87) * mm});
            skLineSegment(sketch, "E6754", {"start": v(-39.46, -22.87) * mm, "end": v(-39.53, -22.97) * mm});
            skLineSegment(sketch, "E6755", {"start": v(-39.53, -22.97) * mm, "end": v(-39.6, -23.07) * mm});
            skLineSegment(sketch, "E6756", {"start": v(-39.6, -23.07) * mm, "end": v(-39.68, -23.17) * mm});
            skLineSegment(sketch, "E6757", {"start": v(-39.68, -23.17) * mm, "end": v(-39.68, -23.17) * mm});
            skLineSegment(sketch, "E6758", {"start": v(-39.68, -23.17) * mm, "end": v(-39.62, -23.28) * mm});
            skLineSegment(sketch, "E6759", {"start": v(-39.62, -23.28) * mm, "end": v(-39.56, -23.38) * mm});
            skLineSegment(sketch, "E6760", {"start": v(-39.56, -23.38) * mm, "end": v(-39.5, -23.47) * mm});
            skLineSegment(sketch, "E6761", {"start": v(-39.5, -23.47) * mm, "end": v(-39.44, -23.57) * mm});
            skLineSegment(sketch, "E6762", {"start": v(-39.44, -23.57) * mm, "end": v(-39.4, -23.66) * mm});
            skLineSegment(sketch, "E6763", {"start": v(-39.4, -23.66) * mm, "end": v(-39.28, -23.64) * mm});
            skLineSegment(sketch, "E6764", {"start": v(-39.28, -23.64) * mm, "end": v(-39.15, -23.63) * mm});
            skLineSegment(sketch, "E6765", {"start": v(-39.15, -23.63) * mm, "end": v(-39.04, -23.6) * mm});
            skLineSegment(sketch, "E6766", {"start": v(-39.04, -23.6) * mm, "end": v(-38.92, -23.6) * mm});
            skLineSegment(sketch, "E6767", {"start": v(-38.92, -23.6) * mm, "end": v(-38.8, -23.57) * mm});
            skLineSegment(sketch, "E6768", {"start": v(-38.8, -23.57) * mm, "end": v(-38.69, -23.55) * mm});
            skLineSegment(sketch, "E6769", {"start": v(-38.69, -23.55) * mm, "end": v(-38.57, -23.53) * mm});
            skLineSegment(sketch, "E6770", {"start": v(-38.57, -23.53) * mm, "end": v(-38.45, -23.51) * mm});
            skLineSegment(sketch, "E6771", {"start": v(-38.45, -23.51) * mm, "end": v(-38.34, -23.49) * mm});
            skLineSegment(sketch, "E6772", {"start": v(-38.34, -23.49) * mm, "end": v(-38.21, -23.47) * mm});
            skLineSegment(sketch, "E6773", {"start": v(-38.21, -23.47) * mm, "end": v(-38.1, -23.44) * mm});
            skLineSegment(sketch, "E6774", {"start": v(-38.1, -23.44) * mm, "end": v(-37.98, -23.42) * mm});
            skLineSegment(sketch, "E6775", {"start": v(-37.98, -23.42) * mm, "end": v(-37.86, -23.4) * mm});
            skLineSegment(sketch, "E6776", {"start": v(-37.86, -23.4) * mm, "end": v(-37.74, -23.36) * mm});
            skLineSegment(sketch, "E6777", {"start": v(-37.74, -23.36) * mm, "end": v(-37.63, -23.34) * mm});
            skLineSegment(sketch, "E6778", {"start": v(-37.63, -23.34) * mm, "end": v(-37.51, -23.3) * mm});
            skLineSegment(sketch, "E6779", {"start": v(-37.51, -23.3) * mm, "end": v(-37.4, -23.28) * mm});
            skLineSegment(sketch, "E6780", {"start": v(-37.4, -23.28) * mm, "end": v(-37.28, -23.25) * mm});
            skLineSegment(sketch, "E6781", {"start": v(-37.28, -23.25) * mm, "end": v(-37.15, -23.21) * mm});
            skLineSegment(sketch, "E6782", {"start": v(-37.15, -23.21) * mm, "end": v(-37.1, -23.31) * mm});
            skLineSegment(sketch, "E6783", {"start": v(-37.1, -23.31) * mm, "end": v(-37.03, -23.41) * mm});
            skLineSegment(sketch, "E6784", {"start": v(-37.03, -23.41) * mm, "end": v(-36.96, -23.51) * mm});
            skLineSegment(sketch, "E6785", {"start": v(-36.96, -23.51) * mm, "end": v(-36.9, -23.61) * mm});
            skLineSegment(sketch, "E6786", {"start": v(-36.9, -23.61) * mm, "end": v(-36.84, -23.71) * mm});
            skLineSegment(sketch, "E6787", {"start": v(-36.84, -23.71) * mm, "end": v(-36.77, -23.81) * mm});
            skLineSegment(sketch, "E6788", {"start": v(-36.77, -23.81) * mm, "end": v(-36.71, -23.91) * mm});
            skLineSegment(sketch, "E6789", {"start": v(-36.71, -23.91) * mm, "end": v(-36.7, -23.93) * mm});
            skLineSegment(sketch, "E6790", {"start": v(-36.7, -23.93) * mm, "end": v(-36.77, -24.01) * mm});
            skLineSegment(sketch, "E6791", {"start": v(-36.77, -24.01) * mm, "end": v(-36.84, -24.1) * mm});
            skLineSegment(sketch, "E6792", {"start": v(-36.84, -24.1) * mm, "end": v(-36.92, -24.18) * mm});
            skLineSegment(sketch, "E6793", {"start": v(-36.92, -24.18) * mm, "end": v(-37, -24.28) * mm});
            skLineSegment(sketch, "E6794", {"start": v(-37, -24.28) * mm, "end": v(-37.07, -24.37) * mm});
            skLineSegment(sketch, "E6795", {"start": v(-37.07, -24.37) * mm, "end": v(-37.14, -24.47) * mm});
            skLineSegment(sketch, "E6796", {"start": v(-37.14, -24.47) * mm, "end": v(-37.22, -24.57) * mm});
            skLineSegment(sketch, "E6797", {"start": v(-37.22, -24.57) * mm, "end": v(-37.3, -24.68) * mm});
            skLineSegment(sketch, "E6798", {"start": v(-37.3, -24.68) * mm, "end": v(-37.37, -24.77) * mm});
            skLineSegment(sketch, "E6799", {"start": v(-37.37, -24.77) * mm, "end": v(-37.44, -24.87) * mm});
            skLineSegment(sketch, "E6800", {"start": v(-37.44, -24.87) * mm, "end": v(-37.5, -24.96) * mm});
            skLineSegment(sketch, "E6801", {"start": v(-37.5, -24.96) * mm, "end": v(-37.57, -25.06) * mm});
            skLineSegment(sketch, "E6802", {"start": v(-37.57, -25.06) * mm, "end": v(-37.64, -25.15) * mm});
            skLineSegment(sketch, "E6803", {"start": v(-37.64, -25.15) * mm, "end": v(-37.7, -25.25) * mm});
            skLineSegment(sketch, "E6804", {"start": v(-37.7, -25.25) * mm, "end": v(-37.77, -25.35) * mm});
            skLineSegment(sketch, "E6805", {"start": v(-37.77, -25.35) * mm, "end": v(-37.84, -25.45) * mm});
            skLineSegment(sketch, "E6806", {"start": v(-37.84, -25.45) * mm, "end": v(-37.9, -25.56) * mm});
            skLineSegment(sketch, "E6807", {"start": v(-37.9, -25.56) * mm, "end": v(-37.98, -25.66) * mm});
            skLineSegment(sketch, "E6808", {"start": v(-37.98, -25.66) * mm, "end": v(-38.04, -25.77) * mm});
            skLineSegment(sketch, "E6809", {"start": v(-38.04, -25.77) * mm, "end": v(-38.05, -25.77) * mm});
            skLineSegment(sketch, "E6810", {"start": v(-38.05, -25.77) * mm, "end": v(-37.98, -25.87) * mm});
            skLineSegment(sketch, "E6811", {"start": v(-37.98, -25.87) * mm, "end": v(-37.91, -25.97) * mm});
            skLineSegment(sketch, "E6812", {"start": v(-37.91, -25.97) * mm, "end": v(-37.85, -26.06) * mm});
            skLineSegment(sketch, "E6813", {"start": v(-37.85, -26.06) * mm, "end": v(-37.78, -26.16) * mm});
            skLineSegment(sketch, "E6814", {"start": v(-37.78, -26.16) * mm, "end": v(-37.73, -26.24) * mm});
            skLineSegment(sketch, "E6815", {"start": v(-37.73, -26.24) * mm, "end": v(-37.6, -26.21) * mm});
            skLineSegment(sketch, "E6816", {"start": v(-37.6, -26.21) * mm, "end": v(-37.49, -26.19) * mm});
            skLineSegment(sketch, "E6817", {"start": v(-37.49, -26.19) * mm, "end": v(-37.37, -26.16) * mm});
            skLineSegment(sketch, "E6818", {"start": v(-37.37, -26.16) * mm, "end": v(-37.26, -26.14) * mm});
            skLineSegment(sketch, "E6819", {"start": v(-37.26, -26.14) * mm, "end": v(-37.14, -26.11) * mm});
            skLineSegment(sketch, "E6820", {"start": v(-37.14, -26.11) * mm, "end": v(-37.03, -26.08) * mm});
            skLineSegment(sketch, "E6821", {"start": v(-37.03, -26.08) * mm, "end": v(-36.91, -26.06) * mm});
            skLineSegment(sketch, "E6822", {"start": v(-36.91, -26.06) * mm, "end": v(-36.8, -26.03) * mm});
            skLineSegment(sketch, "E6823", {"start": v(-36.8, -26.03) * mm, "end": v(-36.68, -26) * mm});
            skLineSegment(sketch, "E6824", {"start": v(-36.68, -26) * mm, "end": v(-36.56, -25.97) * mm});
            skLineSegment(sketch, "E6825", {"start": v(-36.56, -25.97) * mm, "end": v(-36.44, -25.93) * mm});
            skLineSegment(sketch, "E6826", {"start": v(-36.44, -25.93) * mm, "end": v(-36.33, -25.9) * mm});
            skLineSegment(sketch, "E6827", {"start": v(-36.33, -25.9) * mm, "end": v(-36.21, -25.87) * mm});
            skLineSegment(sketch, "E6828", {"start": v(-36.21, -25.87) * mm, "end": v(-36.1, -25.83) * mm});
            skLineSegment(sketch, "E6829", {"start": v(-36.1, -25.83) * mm, "end": v(-35.98, -25.8) * mm});
            skLineSegment(sketch, "E6830", {"start": v(-35.98, -25.8) * mm, "end": v(-35.87, -25.76) * mm});
            skLineSegment(sketch, "E6831", {"start": v(-35.87, -25.76) * mm, "end": v(-35.76, -25.72) * mm});
            skLineSegment(sketch, "E6832", {"start": v(-35.76, -25.72) * mm, "end": v(-35.64, -25.69) * mm});
            skLineSegment(sketch, "E6833", {"start": v(-35.64, -25.69) * mm, "end": v(-35.52, -25.64) * mm});
            skLineSegment(sketch, "E6834", {"start": v(-35.52, -25.64) * mm, "end": v(-35.45, -25.74) * mm});
            skLineSegment(sketch, "E6835", {"start": v(-35.45, -25.74) * mm, "end": v(-35.38, -25.83) * mm});
            skLineSegment(sketch, "E6836", {"start": v(-35.38, -25.83) * mm, "end": v(-35.31, -25.93) * mm});
            skLineSegment(sketch, "E6837", {"start": v(-35.31, -25.93) * mm, "end": v(-35.24, -26.02) * mm});
            skLineSegment(sketch, "E6838", {"start": v(-35.24, -26.02) * mm, "end": v(-35.17, -26.12) * mm});
            skLineSegment(sketch, "E6839", {"start": v(-35.17, -26.12) * mm, "end": v(-35.1, -26.21) * mm});
            skLineSegment(sketch, "E6840", {"start": v(-35.1, -26.21) * mm, "end": v(-35.03, -26.31) * mm});
            skLineSegment(sketch, "E6841", {"start": v(-35.03, -26.31) * mm, "end": v(-35.02, -26.33) * mm});
            skLineSegment(sketch, "E6842", {"start": v(-35.02, -26.33) * mm, "end": v(-35.09, -26.41) * mm});
            skLineSegment(sketch, "E6843", {"start": v(-35.09, -26.41) * mm, "end": v(-35.15, -26.5) * mm});
            skLineSegment(sketch, "E6844", {"start": v(-35.15, -26.5) * mm, "end": v(-35.22, -26.6) * mm});
            skLineSegment(sketch, "E6845", {"start": v(-35.22, -26.6) * mm, "end": v(-35.29, -26.7) * mm});
            skLineSegment(sketch, "E6846", {"start": v(-35.29, -26.7) * mm, "end": v(-35.36, -26.8) * mm});
            skLineSegment(sketch, "E6847", {"start": v(-35.36, -26.8) * mm, "end": v(-35.43, -26.9) * mm});
            skLineSegment(sketch, "E6848", {"start": v(-35.43, -26.9) * mm, "end": v(-35.5, -27) * mm});
            skLineSegment(sketch, "E6849", {"start": v(-35.5, -27) * mm, "end": v(-35.57, -27.11) * mm});
            skLineSegment(sketch, "E6850", {"start": v(-35.57, -27.11) * mm, "end": v(-35.63, -27.21) * mm});
            skLineSegment(sketch, "E6851", {"start": v(-35.63, -27.21) * mm, "end": v(-35.7, -27.32) * mm});
            skLineSegment(sketch, "E6852", {"start": v(-35.7, -27.32) * mm, "end": v(-35.76, -27.41) * mm});
            skLineSegment(sketch, "E6853", {"start": v(-35.76, -27.41) * mm, "end": v(-35.82, -27.51) * mm});
            skLineSegment(sketch, "E6854", {"start": v(-35.82, -27.51) * mm, "end": v(-35.88, -27.61) * mm});
            skLineSegment(sketch, "E6855", {"start": v(-35.88, -27.61) * mm, "end": v(-35.93, -27.71) * mm});
            skLineSegment(sketch, "E6856", {"start": v(-35.93, -27.71) * mm, "end": v(-36, -27.82) * mm});
            skLineSegment(sketch, "E6857", {"start": v(-36, -27.82) * mm, "end": v(-36.06, -27.92) * mm});
            skLineSegment(sketch, "E6858", {"start": v(-36.06, -27.92) * mm, "end": v(-36.12, -28.03) * mm});
            skLineSegment(sketch, "E6859", {"start": v(-36.12, -28.03) * mm, "end": v(-36.18, -28.14) * mm});
            skLineSegment(sketch, "E6860", {"start": v(-36.18, -28.14) * mm, "end": v(-36.24, -28.25) * mm});
            skLineSegment(sketch, "E6861", {"start": v(-36.24, -28.25) * mm, "end": v(-36.24, -28.25) * mm});
            skLineSegment(sketch, "E6862", {"start": v(-36.24, -28.25) * mm, "end": v(-36.17, -28.35) * mm});
            skLineSegment(sketch, "E6863", {"start": v(-36.17, -28.35) * mm, "end": v(-36.1, -28.44) * mm});
            skLineSegment(sketch, "E6864", {"start": v(-36.1, -28.44) * mm, "end": v(-36.02, -28.53) * mm});
            skLineSegment(sketch, "E6865", {"start": v(-36.02, -28.53) * mm, "end": v(-35.95, -28.62) * mm});
            skLineSegment(sketch, "E6866", {"start": v(-35.95, -28.62) * mm, "end": v(-35.89, -28.7) * mm});
            skLineSegment(sketch, "E6867", {"start": v(-35.89, -28.7) * mm, "end": v(-35.77, -28.67) * mm});
            skLineSegment(sketch, "E6868", {"start": v(-35.77, -28.67) * mm, "end": v(-35.66, -28.63) * mm});
            skLineSegment(sketch, "E6869", {"start": v(-35.66, -28.63) * mm, "end": v(-35.54, -28.6) * mm});
            skLineSegment(sketch, "E6870", {"start": v(-35.54, -28.6) * mm, "end": v(-35.43, -28.57) * mm});
            skLineSegment(sketch, "E6871", {"start": v(-35.43, -28.57) * mm, "end": v(-35.32, -28.53) * mm});
            skLineSegment(sketch, "E6872", {"start": v(-35.32, -28.53) * mm, "end": v(-35.2, -28.5) * mm});
            skLineSegment(sketch, "E6873", {"start": v(-35.2, -28.5) * mm, "end": v(-35.09, -28.46) * mm});
            skLineSegment(sketch, "E6874", {"start": v(-35.09, -28.46) * mm, "end": v(-34.98, -28.43) * mm});
            skLineSegment(sketch, "E6875", {"start": v(-34.98, -28.43) * mm, "end": v(-34.86, -28.39) * mm});
            skLineSegment(sketch, "E6876", {"start": v(-34.86, -28.39) * mm, "end": v(-34.74, -28.35) * mm});
            skLineSegment(sketch, "E6877", {"start": v(-34.74, -28.35) * mm, "end": v(-34.63, -28.3) * mm});
            skLineSegment(sketch, "E6878", {"start": v(-34.63, -28.3) * mm, "end": v(-34.52, -28.27) * mm});
            skLineSegment(sketch, "E6879", {"start": v(-34.52, -28.27) * mm, "end": v(-34.4, -28.23) * mm});
            skLineSegment(sketch, "E6880", {"start": v(-34.4, -28.23) * mm, "end": v(-34.3, -28.19) * mm});
            skLineSegment(sketch, "E6881", {"start": v(-34.3, -28.19) * mm, "end": v(-34.18, -28.14) * mm});
            skLineSegment(sketch, "E6882", {"start": v(-34.18, -28.14) * mm, "end": v(-34.07, -28.1) * mm});
            skLineSegment(sketch, "E6883", {"start": v(-34.07, -28.1) * mm, "end": v(-33.96, -28.05) * mm});
            skLineSegment(sketch, "E6884", {"start": v(-33.96, -28.05) * mm, "end": v(-33.85, -28) * mm});
            skLineSegment(sketch, "E6885", {"start": v(-33.85, -28) * mm, "end": v(-33.73, -27.96) * mm});
            skLineSegment(sketch, "E6886", {"start": v(-33.73, -27.96) * mm, "end": v(-33.65, -28.05) * mm});
            skLineSegment(sketch, "E6887", {"start": v(-33.65, -28.05) * mm, "end": v(-33.58, -28.14) * mm});
            skLineSegment(sketch, "E6888", {"start": v(-33.58, -28.14) * mm, "end": v(-33.5, -28.23) * mm});
            skLineSegment(sketch, "E6889", {"start": v(-33.5, -28.23) * mm, "end": v(-33.42, -28.32) * mm});
            skLineSegment(sketch, "E6890", {"start": v(-33.42, -28.32) * mm, "end": v(-33.35, -28.41) * mm});
            skLineSegment(sketch, "E6891", {"start": v(-33.35, -28.41) * mm, "end": v(-33.27, -28.5) * mm});
            skLineSegment(sketch, "E6892", {"start": v(-33.27, -28.5) * mm, "end": v(-33.2, -28.6) * mm});
            skLineSegment(sketch, "E6893", {"start": v(-33.2, -28.6) * mm, "end": v(-33.18, -28.6) * mm});
            skLineSegment(sketch, "E6894", {"start": v(-33.18, -28.6) * mm, "end": v(-33.24, -28.7) * mm});
            skLineSegment(sketch, "E6895", {"start": v(-33.24, -28.7) * mm, "end": v(-33.3, -28.8) * mm});
            skLineSegment(sketch, "E6896", {"start": v(-33.3, -28.8) * mm, "end": v(-33.36, -28.89) * mm});
            skLineSegment(sketch, "E6897", {"start": v(-33.36, -28.89) * mm, "end": v(-33.42, -29) * mm});
            skLineSegment(sketch, "E6898", {"start": v(-33.42, -29) * mm, "end": v(-33.49, -29.1) * mm});
            skLineSegment(sketch, "E6899", {"start": v(-33.49, -29.1) * mm, "end": v(-33.55, -29.2) * mm});
            skLineSegment(sketch, "E6900", {"start": v(-33.55, -29.2) * mm, "end": v(-33.61, -29.31) * mm});
            skLineSegment(sketch, "E6901", {"start": v(-33.61, -29.31) * mm, "end": v(-33.68, -29.43) * mm});
            skLineSegment(sketch, "E6902", {"start": v(-33.68, -29.43) * mm, "end": v(-33.73, -29.53) * mm});
            skLineSegment(sketch, "E6903", {"start": v(-33.73, -29.53) * mm, "end": v(-33.8, -29.64) * mm});
            skLineSegment(sketch, "E6904", {"start": v(-33.8, -29.64) * mm, "end": v(-33.85, -29.74) * mm});
            skLineSegment(sketch, "E6905", {"start": v(-33.85, -29.74) * mm, "end": v(-33.9, -29.84) * mm});
            skLineSegment(sketch, "E6906", {"start": v(-33.9, -29.84) * mm, "end": v(-33.95, -29.94) * mm});
            skLineSegment(sketch, "E6907", {"start": v(-33.95, -29.94) * mm, "end": v(-34, -30.05) * mm});
            skLineSegment(sketch, "E6908", {"start": v(-34, -30.05) * mm, "end": v(-34.06, -30.16) * mm});
            skLineSegment(sketch, "E6909", {"start": v(-34.06, -30.16) * mm, "end": v(-34.1, -30.27) * mm});
            skLineSegment(sketch, "E6910", {"start": v(-34.1, -30.27) * mm, "end": v(-34.16, -30.38) * mm});
            skLineSegment(sketch, "E6911", {"start": v(-34.16, -30.38) * mm, "end": v(-34.22, -30.5) * mm});
            skLineSegment(sketch, "E6912", {"start": v(-34.22, -30.5) * mm, "end": v(-34.27, -30.61) * mm});
            skLineSegment(sketch, "E6913", {"start": v(-34.27, -30.61) * mm, "end": v(-34.27, -30.61) * mm});
            skLineSegment(sketch, "E6914", {"start": v(-34.27, -30.61) * mm, "end": v(-34.2, -30.7) * mm});
            skLineSegment(sketch, "E6915", {"start": v(-34.2, -30.7) * mm, "end": v(-34.11, -30.79) * mm});
            skLineSegment(sketch, "E6916", {"start": v(-34.11, -30.79) * mm, "end": v(-34.04, -30.87) * mm});
            skLineSegment(sketch, "E6917", {"start": v(-34.04, -30.87) * mm, "end": v(-33.96, -30.96) * mm});
            skLineSegment(sketch, "E6918", {"start": v(-33.96, -30.96) * mm, "end": v(-33.9, -31.03) * mm});
            skLineSegment(sketch, "E6919", {"start": v(-33.9, -31.03) * mm, "end": v(-33.78, -31) * mm});
            skLineSegment(sketch, "E6920", {"start": v(-33.78, -31) * mm, "end": v(-33.66, -30.95) * mm});
            skLineSegment(sketch, "E6921", {"start": v(-33.66, -30.95) * mm, "end": v(-33.55, -30.91) * mm});
            skLineSegment(sketch, "E6922", {"start": v(-33.55, -30.91) * mm, "end": v(-33.44, -30.87) * mm});
            skLineSegment(sketch, "E6923", {"start": v(-33.44, -30.87) * mm, "end": v(-33.33, -30.83) * mm});
            skLineSegment(sketch, "E6924", {"start": v(-33.33, -30.83) * mm, "end": v(-33.22, -30.79) * mm});
            skLineSegment(sketch, "E6925", {"start": v(-33.22, -30.79) * mm, "end": v(-33.1, -30.74) * mm});
            skLineSegment(sketch, "E6926", {"start": v(-33.1, -30.74) * mm, "end": v(-33, -30.7) * mm});
            skLineSegment(sketch, "E6927", {"start": v(-33, -30.7) * mm, "end": v(-32.89, -30.65) * mm});
            skLineSegment(sketch, "E6928", {"start": v(-32.89, -30.65) * mm, "end": v(-32.77, -30.6) * mm});
            skLineSegment(sketch, "E6929", {"start": v(-32.77, -30.6) * mm, "end": v(-32.66, -30.56) * mm});
            skLineSegment(sketch, "E6930", {"start": v(-32.66, -30.56) * mm, "end": v(-32.55, -30.51) * mm});
            skLineSegment(sketch, "E6931", {"start": v(-32.55, -30.51) * mm, "end": v(-32.44, -30.46) * mm});
            skLineSegment(sketch, "E6932", {"start": v(-32.44, -30.46) * mm, "end": v(-32.33, -30.41) * mm});
            skLineSegment(sketch, "E6933", {"start": v(-32.33, -30.41) * mm, "end": v(-32.22, -30.36) * mm});
            skLineSegment(sketch, "E6934", {"start": v(-32.22, -30.36) * mm, "end": v(-32.12, -30.31) * mm});
            skLineSegment(sketch, "E6935", {"start": v(-32.12, -30.31) * mm, "end": v(-32, -30.26) * mm});
            skLineSegment(sketch, "E6936", {"start": v(-32, -30.26) * mm, "end": v(-31.9, -30.2) * mm});
            skLineSegment(sketch, "E6937", {"start": v(-31.9, -30.2) * mm, "end": v(-31.79, -30.15) * mm});
            skLineSegment(sketch, "E6938", {"start": v(-31.79, -30.15) * mm, "end": v(-31.7, -30.23) * mm});
            skLineSegment(sketch, "E6939", {"start": v(-31.7, -30.23) * mm, "end": v(-31.62, -30.32) * mm});
            skLineSegment(sketch, "E6940", {"start": v(-31.62, -30.32) * mm, "end": v(-31.54, -30.4) * mm});
            skLineSegment(sketch, "E6941", {"start": v(-31.54, -30.4) * mm, "end": v(-31.46, -30.49) * mm});
            skLineSegment(sketch, "E6942", {"start": v(-31.46, -30.49) * mm, "end": v(-31.37, -30.58) * mm});
            skLineSegment(sketch, "E6943", {"start": v(-31.37, -30.58) * mm, "end": v(-31.3, -30.66) * mm});
            skLineSegment(sketch, "E6944", {"start": v(-31.3, -30.66) * mm, "end": v(-31.21, -30.75) * mm});
            skLineSegment(sketch, "E6945", {"start": v(-31.21, -30.75) * mm, "end": v(-31.2, -30.76) * mm});
            skLineSegment(sketch, "E6946", {"start": v(-31.2, -30.76) * mm, "end": v(-31.25, -30.85) * mm});
            skLineSegment(sketch, "E6947", {"start": v(-31.25, -30.85) * mm, "end": v(-31.3, -30.95) * mm});
            skLineSegment(sketch, "E6948", {"start": v(-31.3, -30.95) * mm, "end": v(-31.36, -31.05) * mm});
            skLineSegment(sketch, "E6949", {"start": v(-31.36, -31.05) * mm, "end": v(-31.41, -31.16) * mm});
            skLineSegment(sketch, "E6950", {"start": v(-31.41, -31.16) * mm, "end": v(-31.47, -31.27) * mm});
            skLineSegment(sketch, "E6951", {"start": v(-31.47, -31.27) * mm, "end": v(-31.52, -31.38) * mm});
            skLineSegment(sketch, "E6952", {"start": v(-31.52, -31.38) * mm, "end": v(-31.58, -31.5) * mm});
            skLineSegment(sketch, "E6953", {"start": v(-31.58, -31.5) * mm, "end": v(-31.64, -31.61) * mm});
            skLineSegment(sketch, "E6954", {"start": v(-31.64, -31.61) * mm, "end": v(-31.69, -31.72) * mm});
            skLineSegment(sketch, "E6955", {"start": v(-31.69, -31.72) * mm, "end": v(-31.74, -31.83) * mm});
            skLineSegment(sketch, "E6956", {"start": v(-31.74, -31.83) * mm, "end": v(-31.78, -31.94) * mm});
            skLineSegment(sketch, "E6957", {"start": v(-31.78, -31.94) * mm, "end": v(-31.83, -32.04) * mm});
            skLineSegment(sketch, "E6958", {"start": v(-31.83, -32.04) * mm, "end": v(-31.87, -32.15) * mm});
            skLineSegment(sketch, "E6959", {"start": v(-31.87, -32.15) * mm, "end": v(-31.92, -32.25) * mm});
            skLineSegment(sketch, "E6960", {"start": v(-31.92, -32.25) * mm, "end": v(-31.97, -32.37) * mm});
            skLineSegment(sketch, "E6961", {"start": v(-31.97, -32.37) * mm, "end": v(-32.01, -32.48) * mm});
            skLineSegment(sketch, "E6962", {"start": v(-32.01, -32.48) * mm, "end": v(-32.06, -32.6) * mm});
            skLineSegment(sketch, "E6963", {"start": v(-32.06, -32.6) * mm, "end": v(-32.1, -32.71) * mm});
            skLineSegment(sketch, "E6964", {"start": v(-32.1, -32.71) * mm, "end": v(-32.15, -32.83) * mm});
            skLineSegment(sketch, "E6965", {"start": v(-32.15, -32.83) * mm, "end": v(-32.15, -32.83) * mm});
            skLineSegment(sketch, "E6966", {"start": v(-32.15, -32.83) * mm, "end": v(-32.06, -32.92) * mm});
            skLineSegment(sketch, "E6967", {"start": v(-32.06, -32.92) * mm, "end": v(-31.98, -33) * mm});
            skLineSegment(sketch, "E6968", {"start": v(-31.98, -33) * mm, "end": v(-31.9, -33.07) * mm});
            skLineSegment(sketch, "E6969", {"start": v(-31.9, -33.07) * mm, "end": v(-31.81, -33.16) * mm});
            skLineSegment(sketch, "E6970", {"start": v(-31.81, -33.16) * mm, "end": v(-31.74, -33.22) * mm});
            skLineSegment(sketch, "E6971", {"start": v(-31.74, -33.22) * mm, "end": v(-31.63, -33.18) * mm});
            skLineSegment(sketch, "E6972", {"start": v(-31.63, -33.18) * mm, "end": v(-31.52, -33.13) * mm});
            skLineSegment(sketch, "E6973", {"start": v(-31.52, -33.13) * mm, "end": v(-31.41, -33.08) * mm});
            skLineSegment(sketch, "E6974", {"start": v(-31.41, -33.08) * mm, "end": v(-31.3, -33.04) * mm});
            skLineSegment(sketch, "E6975", {"start": v(-31.3, -33.04) * mm, "end": v(-31.2, -32.99) * mm});
            skLineSegment(sketch, "E6976", {"start": v(-31.2, -32.99) * mm, "end": v(-31.1, -32.94) * mm});
            skLineSegment(sketch, "E6977", {"start": v(-31.1, -32.94) * mm, "end": v(-30.98, -32.89) * mm});
            skLineSegment(sketch, "E6978", {"start": v(-30.98, -32.89) * mm, "end": v(-30.87, -32.83) * mm});
            skLineSegment(sketch, "E6979", {"start": v(-30.87, -32.83) * mm, "end": v(-30.77, -32.78) * mm});
            skLineSegment(sketch, "E6980", {"start": v(-30.77, -32.78) * mm, "end": v(-30.65, -32.73) * mm});
            skLineSegment(sketch, "E6981", {"start": v(-30.65, -32.73) * mm, "end": v(-30.55, -32.67) * mm});
            skLineSegment(sketch, "E6982", {"start": v(-30.55, -32.67) * mm, "end": v(-30.44, -32.62) * mm});
            skLineSegment(sketch, "E6983", {"start": v(-30.44, -32.62) * mm, "end": v(-30.33, -32.56) * mm});
            skLineSegment(sketch, "E6984", {"start": v(-30.33, -32.56) * mm, "end": v(-30.23, -32.5) * mm});
            skLineSegment(sketch, "E6985", {"start": v(-30.23, -32.5) * mm, "end": v(-30.12, -32.45) * mm});
            skLineSegment(sketch, "E6986", {"start": v(-30.12, -32.45) * mm, "end": v(-30.02, -32.39) * mm});
            skLineSegment(sketch, "E6987", {"start": v(-30.02, -32.39) * mm, "end": v(-29.92, -32.33) * mm});
            skLineSegment(sketch, "E6988", {"start": v(-29.92, -32.33) * mm, "end": v(-29.81, -32.27) * mm});
            skLineSegment(sketch, "E6989", {"start": v(-29.81, -32.27) * mm, "end": v(-29.7, -32.2) * mm});
            skLineSegment(sketch, "E6990", {"start": v(-29.7, -32.2) * mm, "end": v(-29.61, -32.28) * mm});
            skLineSegment(sketch, "E6991", {"start": v(-29.61, -32.28) * mm, "end": v(-29.53, -32.36) * mm});
            skLineSegment(sketch, "E6992", {"start": v(-29.53, -32.36) * mm, "end": v(-29.44, -32.44) * mm});
            skLineSegment(sketch, "E6993", {"start": v(-29.44, -32.44) * mm, "end": v(-29.35, -32.52) * mm});
            skLineSegment(sketch, "E6994", {"start": v(-29.35, -32.52) * mm, "end": v(-29.26, -32.6) * mm});
            skLineSegment(sketch, "E6995", {"start": v(-29.26, -32.6) * mm, "end": v(-29.17, -32.68) * mm});
            skLineSegment(sketch, "E6996", {"start": v(-29.17, -32.68) * mm, "end": v(-29.09, -32.76) * mm});
            skLineSegment(sketch, "E6997", {"start": v(-29.09, -32.76) * mm, "end": v(-29.08, -32.77) * mm});
            skLineSegment(sketch, "E6998", {"start": v(-29.08, -32.77) * mm, "end": v(-29.12, -32.87) * mm});
            skLineSegment(sketch, "E6999", {"start": v(-29.12, -32.87) * mm, "end": v(-29.17, -32.97) * mm});
            skLineSegment(sketch, "E7000", {"start": v(-29.17, -32.97) * mm, "end": v(-29.21, -33.08) * mm});
            skLineSegment(sketch, "E7001", {"start": v(-29.21, -33.08) * mm, "end": v(-29.26, -33.19) * mm});
            skLineSegment(sketch, "E7002", {"start": v(-29.26, -33.19) * mm, "end": v(-29.3, -33.3) * mm});
            skLineSegment(sketch, "E7003", {"start": v(-29.3, -33.3) * mm, "end": v(-29.36, -33.41) * mm});
            skLineSegment(sketch, "E7004", {"start": v(-29.36, -33.41) * mm, "end": v(-29.4, -33.53) * mm});
            skLineSegment(sketch, "E7005", {"start": v(-29.4, -33.53) * mm, "end": v(-29.45, -33.65) * mm});
            skLineSegment(sketch, "E7006", {"start": v(-29.45, -33.65) * mm, "end": v(-29.5, -33.77) * mm});
            skLineSegment(sketch, "E7007", {"start": v(-29.5, -33.77) * mm, "end": v(-29.54, -33.88) * mm});
            skLineSegment(sketch, "E7008", {"start": v(-29.54, -33.88) * mm, "end": v(-29.58, -33.99) * mm});
            skLineSegment(sketch, "E7009", {"start": v(-29.58, -33.99) * mm, "end": v(-29.62, -34.1) * mm});
            skLineSegment(sketch, "E7010", {"start": v(-29.62, -34.1) * mm, "end": v(-29.66, -34.2) * mm});
            skLineSegment(sketch, "E7011", {"start": v(-29.66, -34.2) * mm, "end": v(-29.7, -34.31) * mm});
            skLineSegment(sketch, "E7012", {"start": v(-29.7, -34.31) * mm, "end": v(-29.73, -34.43) * mm});
            skLineSegment(sketch, "E7013", {"start": v(-29.73, -34.43) * mm, "end": v(-29.77, -34.54) * mm});
            skLineSegment(sketch, "E7014", {"start": v(-29.77, -34.54) * mm, "end": v(-29.8, -34.66) * mm});
            skLineSegment(sketch, "E7015", {"start": v(-29.8, -34.66) * mm, "end": v(-29.85, -34.78) * mm});
            skLineSegment(sketch, "E7016", {"start": v(-29.85, -34.78) * mm, "end": v(-29.88, -34.9) * mm});
            skLineSegment(sketch, "E7017", {"start": v(-29.88, -34.9) * mm, "end": v(-29.88, -34.9) * mm});
            skLineSegment(sketch, "E7018", {"start": v(-29.88, -34.9) * mm, "end": v(-29.8, -34.98) * mm});
            skLineSegment(sketch, "E7019", {"start": v(-29.8, -34.98) * mm, "end": v(-29.7, -35.06) * mm});
            skLineSegment(sketch, "E7020", {"start": v(-29.7, -35.06) * mm, "end": v(-29.62, -35.13) * mm});
            skLineSegment(sketch, "E7021", {"start": v(-29.62, -35.13) * mm, "end": v(-29.53, -35.2) * mm});
            skLineSegment(sketch, "E7022", {"start": v(-29.53, -35.2) * mm, "end": v(-29.45, -35.27) * mm});
            skLineSegment(sketch, "E7023", {"start": v(-29.45, -35.27) * mm, "end": v(-29.35, -35.22) * mm});
            skLineSegment(sketch, "E7024", {"start": v(-29.35, -35.22) * mm, "end": v(-29.24, -35.16) * mm});
            skLineSegment(sketch, "E7025", {"start": v(-29.24, -35.16) * mm, "end": v(-29.13, -35.1) * mm});
            skLineSegment(sketch, "E7026", {"start": v(-29.13, -35.1) * mm, "end": v(-29.03, -35.05) * mm});
            skLineSegment(sketch, "E7027", {"start": v(-29.03, -35.05) * mm, "end": v(-28.93, -35) * mm});
            skLineSegment(sketch, "E7028", {"start": v(-28.93, -35) * mm, "end": v(-28.82, -34.94) * mm});
            skLineSegment(sketch, "E7029", {"start": v(-28.82, -34.94) * mm, "end": v(-28.72, -34.88) * mm});
            skLineSegment(sketch, "E7030", {"start": v(-28.72, -34.88) * mm, "end": v(-28.61, -34.82) * mm});
            skLineSegment(sketch, "E7031", {"start": v(-28.61, -34.82) * mm, "end": v(-28.5, -34.76) * mm});
            skLineSegment(sketch, "E7032", {"start": v(-28.5, -34.76) * mm, "end": v(-28.4, -34.7) * mm});
            skLineSegment(sketch, "E7033", {"start": v(-28.4, -34.7) * mm, "end": v(-28.3, -34.64) * mm});
            skLineSegment(sketch, "E7034", {"start": v(-28.3, -34.64) * mm, "end": v(-28.2, -34.58) * mm});
            skLineSegment(sketch, "E7035", {"start": v(-28.2, -34.58) * mm, "end": v(-28.1, -34.52) * mm});
            skLineSegment(sketch, "E7036", {"start": v(-28.1, -34.52) * mm, "end": v(-28, -34.45) * mm});
            skLineSegment(sketch, "E7037", {"start": v(-28, -34.45) * mm, "end": v(-27.89, -34.39) * mm});
            skLineSegment(sketch, "E7038", {"start": v(-27.89, -34.39) * mm, "end": v(-27.79, -34.32) * mm});
            skLineSegment(sketch, "E7039", {"start": v(-27.79, -34.32) * mm, "end": v(-27.69, -34.26) * mm});
            skLineSegment(sketch, "E7040", {"start": v(-27.69, -34.26) * mm, "end": v(-27.6, -34.19) * mm});
            skLineSegment(sketch, "E7041", {"start": v(-27.6, -34.19) * mm, "end": v(-27.48, -34.12) * mm});
            skLineSegment(sketch, "E7042", {"start": v(-27.48, -34.12) * mm, "end": v(-27.39, -34.2) * mm});
            skLineSegment(sketch, "E7043", {"start": v(-27.39, -34.2) * mm, "end": v(-27.3, -34.26) * mm});
            skLineSegment(sketch, "E7044", {"start": v(-27.3, -34.26) * mm, "end": v(-27.2, -34.34) * mm});
            skLineSegment(sketch, "E7045", {"start": v(-27.2, -34.34) * mm, "end": v(-27.11, -34.41) * mm});
            skLineSegment(sketch, "E7046", {"start": v(-27.11, -34.41) * mm, "end": v(-27.02, -34.48) * mm});
            skLineSegment(sketch, "E7047", {"start": v(-27.02, -34.48) * mm, "end": v(-26.93, -34.56) * mm});
            skLineSegment(sketch, "E7048", {"start": v(-26.93, -34.56) * mm, "end": v(-26.83, -34.63) * mm});
            skLineSegment(sketch, "E7049", {"start": v(-26.83, -34.63) * mm, "end": v(-26.82, -34.64) * mm});
            skLineSegment(sketch, "E7050", {"start": v(-26.82, -34.64) * mm, "end": v(-26.86, -34.74) * mm});
            skLineSegment(sketch, "E7051", {"start": v(-26.86, -34.74) * mm, "end": v(-26.9, -34.85) * mm});
            skLineSegment(sketch, "E7052", {"start": v(-26.9, -34.85) * mm, "end": v(-26.94, -34.96) * mm});
            skLineSegment(sketch, "E7053", {"start": v(-26.94, -34.96) * mm, "end": v(-26.98, -35.07) * mm});
            skLineSegment(sketch, "E7054", {"start": v(-26.98, -35.07) * mm, "end": v(-27.02, -35.18) * mm});
            skLineSegment(sketch, "E7055", {"start": v(-27.02, -35.18) * mm, "end": v(-27.06, -35.3) * mm});
            skLineSegment(sketch, "E7056", {"start": v(-27.06, -35.3) * mm, "end": v(-27.1, -35.42) * mm});
            skLineSegment(sketch, "E7057", {"start": v(-27.1, -35.42) * mm, "end": v(-27.14, -35.55) * mm});
            skLineSegment(sketch, "E7058", {"start": v(-27.14, -35.55) * mm, "end": v(-27.17, -35.66) * mm});
            skLineSegment(sketch, "E7059", {"start": v(-27.17, -35.66) * mm, "end": v(-27.21, -35.78) * mm});
            skLineSegment(sketch, "E7060", {"start": v(-27.21, -35.78) * mm, "end": v(-27.24, -35.89) * mm});
            skLineSegment(sketch, "E7061", {"start": v(-27.24, -35.89) * mm, "end": v(-27.27, -36) * mm});
            skLineSegment(sketch, "E7062", {"start": v(-27.27, -36) * mm, "end": v(-27.3, -36.1) * mm});
            skLineSegment(sketch, "E7063", {"start": v(-27.3, -36.1) * mm, "end": v(-27.34, -36.22) * mm});
            skLineSegment(sketch, "E7064", {"start": v(-27.34, -36.22) * mm, "end": v(-27.37, -36.34) * mm});
            skLineSegment(sketch, "E7065", {"start": v(-27.37, -36.34) * mm, "end": v(-27.4, -36.46) * mm});
            skLineSegment(sketch, "E7066", {"start": v(-27.4, -36.46) * mm, "end": v(-27.43, -36.58) * mm});
            skLineSegment(sketch, "E7067", {"start": v(-27.43, -36.58) * mm, "end": v(-27.46, -36.7) * mm});
            skLineSegment(sketch, "E7068", {"start": v(-27.46, -36.7) * mm, "end": v(-27.49, -36.82) * mm});
            skLineSegment(sketch, "E7069", {"start": v(-27.49, -36.82) * mm, "end": v(-27.49, -36.82) * mm});
            skLineSegment(sketch, "E7070", {"start": v(-27.49, -36.82) * mm, "end": v(-27.4, -36.9) * mm});
            skLineSegment(sketch, "E7071", {"start": v(-27.4, -36.9) * mm, "end": v(-27.3, -36.97) * mm});
            skLineSegment(sketch, "E7072", {"start": v(-27.3, -36.97) * mm, "end": v(-27.2, -37.03) * mm});
            skLineSegment(sketch, "E7073", {"start": v(-27.2, -37.03) * mm, "end": v(-27.11, -37.1) * mm});
            skLineSegment(sketch, "E7074", {"start": v(-27.11, -37.1) * mm, "end": v(-27.03, -37.16) * mm});
            skLineSegment(sketch, "E7075", {"start": v(-27.03, -37.16) * mm, "end": v(-26.93, -37.1) * mm});
            skLineSegment(sketch, "E7076", {"start": v(-26.93, -37.1) * mm, "end": v(-26.82, -37.04) * mm});
            skLineSegment(sketch, "E7077", {"start": v(-26.82, -37.04) * mm, "end": v(-26.72, -36.97) * mm});
            skLineSegment(sketch, "E7078", {"start": v(-26.72, -36.97) * mm, "end": v(-26.62, -36.91) * mm});
            skLineSegment(sketch, "E7079", {"start": v(-26.62, -36.91) * mm, "end": v(-26.52, -36.85) * mm});
            skLineSegment(sketch, "E7080", {"start": v(-26.52, -36.85) * mm, "end": v(-26.42, -36.79) * mm});
            skLineSegment(sketch, "E7081", {"start": v(-26.42, -36.79) * mm, "end": v(-26.32, -36.72) * mm});
            skLineSegment(sketch, "E7082", {"start": v(-26.32, -36.72) * mm, "end": v(-26.22, -36.66) * mm});
            skLineSegment(sketch, "E7083", {"start": v(-26.22, -36.66) * mm, "end": v(-26.12, -36.6) * mm});
            skLineSegment(sketch, "E7084", {"start": v(-26.12, -36.6) * mm, "end": v(-26.02, -36.52) * mm});
            skLineSegment(sketch, "E7085", {"start": v(-26.02, -36.52) * mm, "end": v(-25.92, -36.45) * mm});
            skLineSegment(sketch, "E7086", {"start": v(-25.92, -36.45) * mm, "end": v(-25.82, -36.38) * mm});
            skLineSegment(sketch, "E7087", {"start": v(-25.82, -36.38) * mm, "end": v(-25.72, -36.31) * mm});
            skLineSegment(sketch, "E7088", {"start": v(-25.72, -36.31) * mm, "end": v(-25.63, -36.24) * mm});
            skLineSegment(sketch, "E7089", {"start": v(-25.63, -36.24) * mm, "end": v(-25.53, -36.17) * mm});
            skLineSegment(sketch, "E7090", {"start": v(-25.53, -36.17) * mm, "end": v(-25.43, -36.1) * mm});
            skLineSegment(sketch, "E7091", {"start": v(-25.43, -36.1) * mm, "end": v(-25.34, -36.03) * mm});
            skLineSegment(sketch, "E7092", {"start": v(-25.34, -36.03) * mm, "end": v(-25.24, -35.96) * mm});
            skLineSegment(sketch, "E7093", {"start": v(-25.24, -35.96) * mm, "end": v(-25.14, -35.87) * mm});
            skLineSegment(sketch, "E7094", {"start": v(-25.14, -35.87) * mm, "end": v(-25.04, -35.94) * mm});
            skLineSegment(sketch, "E7095", {"start": v(-25.04, -35.94) * mm, "end": v(-24.95, -36.01) * mm});
            skLineSegment(sketch, "E7096", {"start": v(-24.95, -36.01) * mm, "end": v(-24.85, -36.08) * mm});
            skLineSegment(sketch, "E7097", {"start": v(-24.85, -36.08) * mm, "end": v(-24.75, -36.14) * mm});
            skLineSegment(sketch, "E7098", {"start": v(-24.75, -36.14) * mm, "end": v(-24.65, -36.21) * mm});
            skLineSegment(sketch, "E7099", {"start": v(-24.65, -36.21) * mm, "end": v(-24.56, -36.28) * mm});
            skLineSegment(sketch, "E7100", {"start": v(-24.56, -36.28) * mm, "end": v(-24.46, -36.35) * mm});
            skLineSegment(sketch, "E7101", {"start": v(-24.46, -36.35) * mm, "end": v(-24.45, -36.36) * mm});
            skLineSegment(sketch, "E7102", {"start": v(-24.45, -36.36) * mm, "end": v(-24.48, -36.46) * mm});
            skLineSegment(sketch, "E7103", {"start": v(-24.48, -36.46) * mm, "end": v(-24.51, -36.57) * mm});
            skLineSegment(sketch, "E7104", {"start": v(-24.51, -36.57) * mm, "end": v(-24.54, -36.68) * mm});
            skLineSegment(sketch, "E7105", {"start": v(-24.54, -36.68) * mm, "end": v(-24.58, -36.8) * mm});
            skLineSegment(sketch, "E7106", {"start": v(-24.58, -36.8) * mm, "end": v(-24.6, -36.9) * mm});
            skLineSegment(sketch, "E7107", {"start": v(-24.6, -36.9) * mm, "end": v(-24.64, -37.03) * mm});
            skLineSegment(sketch, "E7108", {"start": v(-24.64, -37.03) * mm, "end": v(-24.67, -37.15) * mm});
            skLineSegment(sketch, "E7109", {"start": v(-24.67, -37.15) * mm, "end": v(-24.7, -37.28) * mm});
            skLineSegment(sketch, "E7110", {"start": v(-24.7, -37.28) * mm, "end": v(-24.73, -37.4) * mm});
            skLineSegment(sketch, "E7111", {"start": v(-24.73, -37.4) * mm, "end": v(-24.76, -37.52) * mm});
            skLineSegment(sketch, "E7112", {"start": v(-24.76, -37.52) * mm, "end": v(-24.78, -37.63) * mm});
            skLineSegment(sketch, "E7113", {"start": v(-24.78, -37.63) * mm, "end": v(-24.8, -37.74) * mm});
            skLineSegment(sketch, "E7114", {"start": v(-24.8, -37.74) * mm, "end": v(-24.83, -37.85) * mm});
            skLineSegment(sketch, "E7115", {"start": v(-24.83, -37.85) * mm, "end": v(-24.86, -37.97) * mm});
            skLineSegment(sketch, "E7116", {"start": v(-24.86, -37.97) * mm, "end": v(-24.88, -38.08) * mm});
            skLineSegment(sketch, "E7117", {"start": v(-24.88, -38.08) * mm, "end": v(-24.9, -38.2) * mm});
            skLineSegment(sketch, "E7118", {"start": v(-24.9, -38.2) * mm, "end": v(-24.92, -38.33) * mm});
            skLineSegment(sketch, "E7119", {"start": v(-24.92, -38.33) * mm, "end": v(-24.94, -38.45) * mm});
            skLineSegment(sketch, "E7120", {"start": v(-24.94, -38.45) * mm, "end": v(-24.96, -38.58) * mm});
            skLineSegment(sketch, "E7121", {"start": v(-24.96, -38.58) * mm, "end": v(-24.96, -38.58) * mm});
            skLineSegment(sketch, "E7122", {"start": v(-24.96, -38.58) * mm, "end": v(-24.86, -38.64) * mm});
            skLineSegment(sketch, "E7123", {"start": v(-24.86, -38.64) * mm, "end": v(-24.76, -38.7) * mm});
            skLineSegment(sketch, "E7124", {"start": v(-24.76, -38.7) * mm, "end": v(-24.67, -38.77) * mm});
            skLineSegment(sketch, "E7125", {"start": v(-24.67, -38.77) * mm, "end": v(-24.57, -38.83) * mm});
            skLineSegment(sketch, "E7126", {"start": v(-24.57, -38.83) * mm, "end": v(-24.49, -38.88) * mm});
            skLineSegment(sketch, "E7127", {"start": v(-24.49, -38.88) * mm, "end": v(-24.4, -38.81) * mm});
            skLineSegment(sketch, "E7128", {"start": v(-24.4, -38.81) * mm, "end": v(-24.29, -38.74) * mm});
            skLineSegment(sketch, "E7129", {"start": v(-24.29, -38.74) * mm, "end": v(-24.2, -38.68) * mm});
            skLineSegment(sketch, "E7130", {"start": v(-24.2, -38.68) * mm, "end": v(-24.1, -38.61) * mm});
            skLineSegment(sketch, "E7131", {"start": v(-24.1, -38.61) * mm, "end": v(-24, -38.54) * mm});
            skLineSegment(sketch, "E7132", {"start": v(-24, -38.54) * mm, "end": v(-23.9, -38.47) * mm});
            skLineSegment(sketch, "E7133", {"start": v(-23.9, -38.47) * mm, "end": v(-23.8, -38.4) * mm});
            skLineSegment(sketch, "E7134", {"start": v(-23.8, -38.4) * mm, "end": v(-23.71, -38.33) * mm});
            skLineSegment(sketch, "E7135", {"start": v(-23.71, -38.33) * mm, "end": v(-23.62, -38.25) * mm});
            skLineSegment(sketch, "E7136", {"start": v(-23.62, -38.25) * mm, "end": v(-23.52, -38.18) * mm});
            skLineSegment(sketch, "E7137", {"start": v(-23.52, -38.18) * mm, "end": v(-23.43, -38.1) * mm});
            skLineSegment(sketch, "E7138", {"start": v(-23.43, -38.1) * mm, "end": v(-23.33, -38.03) * mm});
            skLineSegment(sketch, "E7139", {"start": v(-23.33, -38.03) * mm, "end": v(-23.24, -37.95) * mm});
            skLineSegment(sketch, "E7140", {"start": v(-23.24, -37.95) * mm, "end": v(-23.15, -37.88) * mm});
            skLineSegment(sketch, "E7141", {"start": v(-23.15, -37.88) * mm, "end": v(-23.06, -37.8) * mm});
            skLineSegment(sketch, "E7142", {"start": v(-23.06, -37.8) * mm, "end": v(-22.97, -37.72) * mm});
            skLineSegment(sketch, "E7143", {"start": v(-22.97, -37.72) * mm, "end": v(-22.88, -37.64) * mm});
            skLineSegment(sketch, "E7144", {"start": v(-22.88, -37.64) * mm, "end": v(-22.79, -37.56) * mm});
            skLineSegment(sketch, "E7145", {"start": v(-22.79, -37.56) * mm, "end": v(-22.69, -37.47) * mm});
            skLineSegment(sketch, "E7146", {"start": v(-22.69, -37.47) * mm, "end": v(-22.59, -37.54) * mm});
            skLineSegment(sketch, "E7147", {"start": v(-22.59, -37.54) * mm, "end": v(-22.49, -37.6) * mm});
            skLineSegment(sketch, "E7148", {"start": v(-22.49, -37.6) * mm, "end": v(-22.38, -37.66) * mm});
            skLineSegment(sketch, "E7149", {"start": v(-22.38, -37.66) * mm, "end": v(-22.28, -37.72) * mm});
            skLineSegment(sketch, "E7150", {"start": v(-22.28, -37.72) * mm, "end": v(-22.18, -37.78) * mm});
            skLineSegment(sketch, "E7151", {"start": v(-22.18, -37.78) * mm, "end": v(-22.08, -37.84) * mm});
            skLineSegment(sketch, "E7152", {"start": v(-22.08, -37.84) * mm, "end": v(-21.98, -37.9) * mm});
            skLineSegment(sketch, "E7153", {"start": v(-21.98, -37.9) * mm, "end": v(-21.96, -37.9) * mm});
            skLineSegment(sketch, "E7154", {"start": v(-21.96, -37.9) * mm, "end": v(-21.99, -38.01) * mm});
            skLineSegment(sketch, "E7155", {"start": v(-21.99, -38.01) * mm, "end": v(-22.01, -38.12) * mm});
            skLineSegment(sketch, "E7156", {"start": v(-22.01, -38.12) * mm, "end": v(-22.04, -38.23) * mm});
            skLineSegment(sketch, "E7157", {"start": v(-22.04, -38.23) * mm, "end": v(-22.06, -38.35) * mm});
            skLineSegment(sketch, "E7158", {"start": v(-22.06, -38.35) * mm, "end": v(-22.09, -38.47) * mm});
            skLineSegment(sketch, "E7159", {"start": v(-22.09, -38.47) * mm, "end": v(-22.11, -38.6) * mm});
            skLineSegment(sketch, "E7160", {"start": v(-22.11, -38.6) * mm, "end": v(-22.14, -38.72) * mm});
            skLineSegment(sketch, "E7161", {"start": v(-22.14, -38.72) * mm, "end": v(-22.16, -38.85) * mm});
            skLineSegment(sketch, "E7162", {"start": v(-22.16, -38.85) * mm, "end": v(-22.18, -38.96) * mm});
            skLineSegment(sketch, "E7163", {"start": v(-22.18, -38.96) * mm, "end": v(-22.2, -39.09) * mm});
            skLineSegment(sketch, "E7164", {"start": v(-22.2, -39.09) * mm, "end": v(-22.22, -39.2) * mm});
            skLineSegment(sketch, "E7165", {"start": v(-22.22, -39.2) * mm, "end": v(-22.23, -39.3) * mm});
            skLineSegment(sketch, "E7166", {"start": v(-22.23, -39.3) * mm, "end": v(-22.25, -39.42) * mm});
            skLineSegment(sketch, "E7167", {"start": v(-22.25, -39.42) * mm, "end": v(-22.26, -39.54) * mm});
            skLineSegment(sketch, "E7168", {"start": v(-22.26, -39.54) * mm, "end": v(-22.28, -39.66) * mm});
            skLineSegment(sketch, "E7169", {"start": v(-22.28, -39.66) * mm, "end": v(-22.3, -39.78) * mm});
            skLineSegment(sketch, "E7170", {"start": v(-22.3, -39.78) * mm, "end": v(-22.3, -39.9) * mm});
            skLineSegment(sketch, "E7171", {"start": v(-22.3, -39.9) * mm, "end": v(-22.32, -40.03) * mm});
            skLineSegment(sketch, "E7172", {"start": v(-22.32, -40.03) * mm, "end": v(-22.33, -40.16) * mm});
            skLineSegment(sketch, "E7173", {"start": v(-22.33, -40.16) * mm, "end": v(-22.33, -40.16) * mm});
            skLineSegment(sketch, "E7174", {"start": v(-22.33, -40.16) * mm, "end": v(-22.23, -40.22) * mm});
            skLineSegment(sketch, "E7175", {"start": v(-22.23, -40.22) * mm, "end": v(-22.12, -40.27) * mm});
            skLineSegment(sketch, "E7176", {"start": v(-22.12, -40.27) * mm, "end": v(-22.03, -40.33) * mm});
            skLineSegment(sketch, "E7177", {"start": v(-22.03, -40.33) * mm, "end": v(-21.92, -40.38) * mm});
            skLineSegment(sketch, "E7178", {"start": v(-21.92, -40.38) * mm, "end": v(-21.84, -40.43) * mm});
            skLineSegment(sketch, "E7179", {"start": v(-21.84, -40.43) * mm, "end": v(-21.74, -40.36) * mm});
            skLineSegment(sketch, "E7180", {"start": v(-21.74, -40.36) * mm, "end": v(-21.65, -40.28) * mm});
            skLineSegment(sketch, "E7181", {"start": v(-21.65, -40.28) * mm, "end": v(-21.55, -40.2) * mm});
            skLineSegment(sketch, "E7182", {"start": v(-21.55, -40.2) * mm, "end": v(-21.47, -40.13) * mm});
            skLineSegment(sketch, "E7183", {"start": v(-21.47, -40.13) * mm, "end": v(-21.37, -40.06) * mm});
            skLineSegment(sketch, "E7184", {"start": v(-21.37, -40.06) * mm, "end": v(-21.28, -39.98) * mm});
            skLineSegment(sketch, "E7185", {"start": v(-21.28, -39.98) * mm, "end": v(-21.2, -39.9) * mm});
            skLineSegment(sketch, "E7186", {"start": v(-21.2, -39.9) * mm, "end": v(-21.1, -39.82) * mm});
            skLineSegment(sketch, "E7187", {"start": v(-21.1, -39.82) * mm, "end": v(-21.01, -39.75) * mm});
            skLineSegment(sketch, "E7188", {"start": v(-21.01, -39.75) * mm, "end": v(-20.92, -39.66) * mm});
            skLineSegment(sketch, "E7189", {"start": v(-20.92, -39.66) * mm, "end": v(-20.83, -39.58) * mm});
            skLineSegment(sketch, "E7190", {"start": v(-20.83, -39.58) * mm, "end": v(-20.74, -39.5) * mm});
            skLineSegment(sketch, "E7191", {"start": v(-20.74, -39.5) * mm, "end": v(-20.65, -39.42) * mm});
            skLineSegment(sketch, "E7192", {"start": v(-20.65, -39.42) * mm, "end": v(-20.57, -39.34) * mm});
            skLineSegment(sketch, "E7193", {"start": v(-20.57, -39.34) * mm, "end": v(-20.48, -39.25) * mm});
            skLineSegment(sketch, "E7194", {"start": v(-20.48, -39.25) * mm, "end": v(-20.4, -39.17) * mm});
            skLineSegment(sketch, "E7195", {"start": v(-20.4, -39.17) * mm, "end": v(-20.31, -39.08) * mm});
            skLineSegment(sketch, "E7196", {"start": v(-20.31, -39.08) * mm, "end": v(-20.23, -39) * mm});
            skLineSegment(sketch, "E7197", {"start": v(-20.23, -39) * mm, "end": v(-20.14, -38.9) * mm});
            skLineSegment(sketch, "E7198", {"start": v(-20.14, -38.9) * mm, "end": v(-20.03, -38.96) * mm});
            skLineSegment(sketch, "E7199", {"start": v(-20.03, -38.96) * mm, "end": v(-19.93, -39.01) * mm});
            skLineSegment(sketch, "E7200", {"start": v(-19.93, -39.01) * mm, "end": v(-19.82, -39.07) * mm});
            skLineSegment(sketch, "E7201", {"start": v(-19.82, -39.07) * mm, "end": v(-19.71, -39.12) * mm});
            skLineSegment(sketch, "E7202", {"start": v(-19.71, -39.12) * mm, "end": v(-19.6, -39.17) * mm});
            skLineSegment(sketch, "E7203", {"start": v(-19.6, -39.17) * mm, "end": v(-19.5, -39.23) * mm});
            skLineSegment(sketch, "E7204", {"start": v(-19.5, -39.23) * mm, "end": v(-19.4, -39.28) * mm});
            skLineSegment(sketch, "E7205", {"start": v(-19.4, -39.28) * mm, "end": v(-19.38, -39.3) * mm});
            skLineSegment(sketch, "E7206", {"start": v(-19.38, -39.3) * mm, "end": v(-19.4, -39.4) * mm});
            skLineSegment(sketch, "E7207", {"start": v(-19.4, -39.4) * mm, "end": v(-19.42, -39.5) * mm});
            skLineSegment(sketch, "E7208", {"start": v(-19.42, -39.5) * mm, "end": v(-19.44, -39.62) * mm});
            skLineSegment(sketch, "E7209", {"start": v(-19.44, -39.62) * mm, "end": v(-19.45, -39.74) * mm});
            skLineSegment(sketch, "E7210", {"start": v(-19.45, -39.74) * mm, "end": v(-19.47, -39.86) * mm});
            skLineSegment(sketch, "E7211", {"start": v(-19.47, -39.86) * mm, "end": v(-19.49, -39.98) * mm});
            skLineSegment(sketch, "E7212", {"start": v(-19.49, -39.98) * mm, "end": v(-19.5, -40.1) * mm});
            skLineSegment(sketch, "E7213", {"start": v(-19.5, -40.1) * mm, "end": v(-19.51, -40.24) * mm});
            skLineSegment(sketch, "E7214", {"start": v(-19.51, -40.24) * mm, "end": v(-19.53, -40.36) * mm});
            skLineSegment(sketch, "E7215", {"start": v(-19.53, -40.36) * mm, "end": v(-19.54, -40.48) * mm});
            skLineSegment(sketch, "E7216", {"start": v(-19.54, -40.48) * mm, "end": v(-19.55, -40.6) * mm});
            skLineSegment(sketch, "E7217", {"start": v(-19.55, -40.6) * mm, "end": v(-19.56, -40.7) * mm});
            skLineSegment(sketch, "E7218", {"start": v(-19.56, -40.7) * mm, "end": v(-19.57, -40.82) * mm});
            skLineSegment(sketch, "E7219", {"start": v(-19.57, -40.82) * mm, "end": v(-19.57, -40.94) * mm});
            skLineSegment(sketch, "E7220", {"start": v(-19.57, -40.94) * mm, "end": v(-19.58, -41.06) * mm});
            skLineSegment(sketch, "E7221", {"start": v(-19.58, -41.06) * mm, "end": v(-19.59, -41.18) * mm});
            skLineSegment(sketch, "E7222", {"start": v(-19.59, -41.18) * mm, "end": v(-19.6, -41.3) * mm});
            skLineSegment(sketch, "E7223", {"start": v(-19.6, -41.3) * mm, "end": v(-19.6, -41.43) * mm});
            skLineSegment(sketch, "E7224", {"start": v(-19.6, -41.43) * mm, "end": v(-19.6, -41.56) * mm});
            skLineSegment(sketch, "E7225", {"start": v(-19.6, -41.56) * mm, "end": v(-19.6, -41.56) * mm});
            skLineSegment(sketch, "E7226", {"start": v(-19.6, -41.56) * mm, "end": v(-19.5, -41.61) * mm});
            skLineSegment(sketch, "E7227", {"start": v(-19.5, -41.61) * mm, "end": v(-19.38, -41.66) * mm});
            skLineSegment(sketch, "E7228", {"start": v(-19.38, -41.66) * mm, "end": v(-19.29, -41.7) * mm});
            skLineSegment(sketch, "E7229", {"start": v(-19.29, -41.7) * mm, "end": v(-19.18, -41.76) * mm});
            skLineSegment(sketch, "E7230", {"start": v(-19.18, -41.76) * mm, "end": v(-19.09, -41.8) * mm});
            skLineSegment(sketch, "E7231", {"start": v(-19.09, -41.8) * mm, "end": v(-19, -41.72) * mm});
            skLineSegment(sketch, "E7232", {"start": v(-19, -41.72) * mm, "end": v(-18.9, -41.64) * mm});
            skLineSegment(sketch, "E7233", {"start": v(-18.9, -41.64) * mm, "end": v(-18.82, -41.55) * mm});
            skLineSegment(sketch, "E7234", {"start": v(-18.82, -41.55) * mm, "end": v(-18.74, -41.48) * mm});
            skLineSegment(sketch, "E7235", {"start": v(-18.74, -41.48) * mm, "end": v(-18.65, -41.4) * mm});
            skLineSegment(sketch, "E7236", {"start": v(-18.65, -41.4) * mm, "end": v(-18.56, -41.31) * mm});
            skLineSegment(sketch, "E7237", {"start": v(-18.56, -41.31) * mm, "end": v(-18.48, -41.23) * mm});
            skLineSegment(sketch, "E7238", {"start": v(-18.48, -41.23) * mm, "end": v(-18.4, -41.14) * mm});
            skLineSegment(sketch, "E7239", {"start": v(-18.4, -41.14) * mm, "end": v(-18.3, -41.06) * mm});
            skLineSegment(sketch, "E7240", {"start": v(-18.3, -41.06) * mm, "end": v(-18.22, -40.97) * mm});
            skLineSegment(sketch, "E7241", {"start": v(-18.22, -40.97) * mm, "end": v(-18.14, -40.88) * mm});
            skLineSegment(sketch, "E7242", {"start": v(-18.14, -40.88) * mm, "end": v(-18.06, -40.8) * mm});
            skLineSegment(sketch, "E7243", {"start": v(-18.06, -40.8) * mm, "end": v(-17.97, -40.71) * mm});
            skLineSegment(sketch, "E7244", {"start": v(-17.97, -40.71) * mm, "end": v(-17.9, -40.62) * mm});
            skLineSegment(sketch, "E7245", {"start": v(-17.9, -40.62) * mm, "end": v(-17.81, -40.53) * mm});
            skLineSegment(sketch, "E7246", {"start": v(-17.81, -40.53) * mm, "end": v(-17.73, -40.44) * mm});
            skLineSegment(sketch, "E7247", {"start": v(-17.73, -40.44) * mm, "end": v(-17.65, -40.35) * mm});
            skLineSegment(sketch, "E7248", {"start": v(-17.65, -40.35) * mm, "end": v(-17.58, -40.26) * mm});
            skLineSegment(sketch, "E7249", {"start": v(-17.58, -40.26) * mm, "end": v(-17.5, -40.16) * mm});
            skLineSegment(sketch, "E7250", {"start": v(-17.5, -40.16) * mm, "end": v(-17.38, -40.21) * mm});
            skLineSegment(sketch, "E7251", {"start": v(-17.38, -40.21) * mm, "end": v(-17.27, -40.26) * mm});
            skLineSegment(sketch, "E7252", {"start": v(-17.27, -40.26) * mm, "end": v(-17.16, -40.3) * mm});
            skLineSegment(sketch, "E7253", {"start": v(-17.16, -40.3) * mm, "end": v(-17.06, -40.35) * mm});
            skLineSegment(sketch, "E7254", {"start": v(-17.06, -40.35) * mm, "end": v(-16.95, -40.4) * mm});
            skLineSegment(sketch, "E7255", {"start": v(-16.95, -40.4) * mm, "end": v(-16.84, -40.44) * mm});
            skLineSegment(sketch, "E7256", {"start": v(-16.84, -40.44) * mm, "end": v(-16.73, -40.5) * mm});
            skLineSegment(sketch, "E7257", {"start": v(-16.73, -40.5) * mm, "end": v(-16.71, -40.5) * mm});
            skLineSegment(sketch, "E7258", {"start": v(-16.71, -40.5) * mm, "end": v(-16.73, -40.6) * mm});
            skLineSegment(sketch, "E7259", {"start": v(-16.73, -40.6) * mm, "end": v(-16.74, -40.72) * mm});
            skLineSegment(sketch, "E7260", {"start": v(-16.74, -40.72) * mm, "end": v(-16.75, -40.83) * mm});
            skLineSegment(sketch, "E7261", {"start": v(-16.75, -40.83) * mm, "end": v(-16.76, -40.95) * mm});
            skLineSegment(sketch, "E7262", {"start": v(-16.76, -40.95) * mm, "end": v(-16.76, -41.07) * mm});
            skLineSegment(sketch, "E7263", {"start": v(-16.76, -41.07) * mm, "end": v(-16.77, -41.2) * mm});
            skLineSegment(sketch, "E7264", {"start": v(-16.77, -41.2) * mm, "end": v(-16.78, -41.32) * mm});
            skLineSegment(sketch, "E7265", {"start": v(-16.78, -41.32) * mm, "end": v(-16.78, -41.45) * mm});
            skLineSegment(sketch, "E7266", {"start": v(-16.78, -41.45) * mm, "end": v(-16.79, -41.57) * mm});
            skLineSegment(sketch, "E7267", {"start": v(-16.79, -41.57) * mm, "end": v(-16.8, -41.7) * mm});
            skLineSegment(sketch, "E7268", {"start": v(-16.8, -41.7) * mm, "end": v(-16.8, -41.8) * mm});
            skLineSegment(sketch, "E7269", {"start": v(-16.8, -41.8) * mm, "end": v(-16.8, -41.92) * mm});
            skLineSegment(sketch, "E7270", {"start": v(-16.8, -41.92) * mm, "end": v(-16.8, -42.04) * mm});
            skLineSegment(sketch, "E7271", {"start": v(-16.8, -42.04) * mm, "end": v(-16.8, -42.16) * mm});
            skLineSegment(sketch, "E7272", {"start": v(-16.8, -42.16) * mm, "end": v(-16.8, -42.28) * mm});
            skLineSegment(sketch, "E7273", {"start": v(-16.8, -42.28) * mm, "end": v(-16.8, -42.4) * mm});
            skLineSegment(sketch, "E7274", {"start": v(-16.8, -42.4) * mm, "end": v(-16.79, -42.52) * mm});
            skLineSegment(sketch, "E7275", {"start": v(-16.79, -42.52) * mm, "end": v(-16.78, -42.65) * mm});
            skLineSegment(sketch, "E7276", {"start": v(-16.78, -42.65) * mm, "end": v(-16.78, -42.78) * mm});
            skLineSegment(sketch, "E7277", {"start": v(-16.78, -42.78) * mm, "end": v(-16.78, -42.78) * mm});
            skLineSegment(sketch, "E7278", {"start": v(-16.78, -42.78) * mm, "end": v(-16.67, -42.82) * mm});
            skLineSegment(sketch, "E7279", {"start": v(-16.67, -42.82) * mm, "end": v(-16.56, -42.86) * mm});
            skLineSegment(sketch, "E7280", {"start": v(-16.56, -42.86) * mm, "end": v(-16.46, -42.9) * mm});
            skLineSegment(sketch, "E7281", {"start": v(-16.46, -42.9) * mm, "end": v(-16.34, -42.95) * mm});
            skLineSegment(sketch, "E7282", {"start": v(-16.34, -42.95) * mm, "end": v(-16.25, -42.98) * mm});
            skLineSegment(sketch, "E7283", {"start": v(-16.25, -42.98) * mm, "end": v(-16.17, -42.9) * mm});
            skLineSegment(sketch, "E7284", {"start": v(-16.17, -42.9) * mm, "end": v(-16.09, -42.8) * mm});
            skLineSegment(sketch, "E7285", {"start": v(-16.09, -42.8) * mm, "end": v(-16, -42.72) * mm});
            skLineSegment(sketch, "E7286", {"start": v(-16, -42.72) * mm, "end": v(-15.93, -42.64) * mm});
            skLineSegment(sketch, "E7287", {"start": v(-15.93, -42.64) * mm, "end": v(-15.84, -42.55) * mm});
            skLineSegment(sketch, "E7288", {"start": v(-15.84, -42.55) * mm, "end": v(-15.76, -42.46) * mm});
            skLineSegment(sketch, "E7289", {"start": v(-15.76, -42.46) * mm, "end": v(-15.68, -42.37) * mm});
            skLineSegment(sketch, "E7290", {"start": v(-15.68, -42.37) * mm, "end": v(-15.6, -42.28) * mm});
            skLineSegment(sketch, "E7291", {"start": v(-15.6, -42.28) * mm, "end": v(-15.53, -42.2) * mm});
            skLineSegment(sketch, "E7292", {"start": v(-15.53, -42.2) * mm, "end": v(-15.44, -42.1) * mm});
            skLineSegment(sketch, "E7293", {"start": v(-15.44, -42.1) * mm, "end": v(-15.37, -42) * mm});
            skLineSegment(sketch, "E7294", {"start": v(-15.37, -42) * mm, "end": v(-15.29, -41.91) * mm});
            skLineSegment(sketch, "E7295", {"start": v(-15.29, -41.91) * mm, "end": v(-15.21, -41.82) * mm});
            skLineSegment(sketch, "E7296", {"start": v(-15.21, -41.82) * mm, "end": v(-15.14, -41.73) * mm});
            skLineSegment(sketch, "E7297", {"start": v(-15.14, -41.73) * mm, "end": v(-15.07, -41.63) * mm});
            skLineSegment(sketch, "E7298", {"start": v(-15.07, -41.63) * mm, "end": v(-15, -41.54) * mm});
            skLineSegment(sketch, "E7299", {"start": v(-15, -41.54) * mm, "end": v(-14.92, -41.44) * mm});
            skLineSegment(sketch, "E7300", {"start": v(-14.92, -41.44) * mm, "end": v(-14.85, -41.35) * mm});
            skLineSegment(sketch, "E7301", {"start": v(-14.85, -41.35) * mm, "end": v(-14.77, -41.24) * mm});
            skLineSegment(sketch, "E7302", {"start": v(-14.77, -41.24) * mm, "end": v(-14.66, -41.28) * mm});
            skLineSegment(sketch, "E7303", {"start": v(-14.66, -41.28) * mm, "end": v(-14.55, -41.32) * mm});
            skLineSegment(sketch, "E7304", {"start": v(-14.55, -41.32) * mm, "end": v(-14.43, -41.36) * mm});
            skLineSegment(sketch, "E7305", {"start": v(-14.43, -41.36) * mm, "end": v(-14.32, -41.4) * mm});
            skLineSegment(sketch, "E7306", {"start": v(-14.32, -41.4) * mm, "end": v(-14.21, -41.44) * mm});
            skLineSegment(sketch, "E7307", {"start": v(-14.21, -41.44) * mm, "end": v(-14.1, -41.48) * mm});
            skLineSegment(sketch, "E7308", {"start": v(-14.1, -41.48) * mm, "end": v(-13.99, -41.52) * mm});
            skLineSegment(sketch, "E7309", {"start": v(-13.99, -41.52) * mm, "end": v(-13.97, -41.52) * mm});
            skLineSegment(sketch, "E7310", {"start": v(-13.97, -41.52) * mm, "end": v(-13.98, -41.63) * mm});
            skLineSegment(sketch, "E7311", {"start": v(-13.98, -41.63) * mm, "end": v(-13.98, -41.74) * mm});
            skLineSegment(sketch, "E7312", {"start": v(-13.98, -41.74) * mm, "end": v(-13.98, -41.86) * mm});
            skLineSegment(sketch, "E7313", {"start": v(-13.98, -41.86) * mm, "end": v(-13.98, -41.98) * mm});
            skLineSegment(sketch, "E7314", {"start": v(-13.98, -41.98) * mm, "end": v(-13.98, -42.1) * mm});
            skLineSegment(sketch, "E7315", {"start": v(-13.98, -42.1) * mm, "end": v(-13.98, -42.22) * mm});
            skLineSegment(sketch, "E7316", {"start": v(-13.98, -42.22) * mm, "end": v(-13.98, -42.35) * mm});
            skLineSegment(sketch, "E7317", {"start": v(-13.98, -42.35) * mm, "end": v(-13.98, -42.48) * mm});
            skLineSegment(sketch, "E7318", {"start": v(-13.98, -42.48) * mm, "end": v(-13.97, -42.6) * mm});
            skLineSegment(sketch, "E7319", {"start": v(-13.97, -42.6) * mm, "end": v(-13.97, -42.72) * mm});
            skLineSegment(sketch, "E7320", {"start": v(-13.97, -42.72) * mm, "end": v(-13.96, -42.84) * mm});
            skLineSegment(sketch, "E7321", {"start": v(-13.96, -42.84) * mm, "end": v(-13.96, -42.95) * mm});
            skLineSegment(sketch, "E7322", {"start": v(-13.96, -42.95) * mm, "end": v(-13.95, -43.07) * mm});
            skLineSegment(sketch, "E7323", {"start": v(-13.95, -43.07) * mm, "end": v(-13.94, -43.18) * mm});
            skLineSegment(sketch, "E7324", {"start": v(-13.94, -43.18) * mm, "end": v(-13.93, -43.3) * mm});
            skLineSegment(sketch, "E7325", {"start": v(-13.93, -43.3) * mm, "end": v(-13.92, -43.42) * mm});
            skLineSegment(sketch, "E7326", {"start": v(-13.92, -43.42) * mm, "end": v(-13.91, -43.55) * mm});
            skLineSegment(sketch, "E7327", {"start": v(-13.91, -43.55) * mm, "end": v(-13.9, -43.67) * mm});
            skLineSegment(sketch, "E7328", {"start": v(-13.9, -43.67) * mm, "end": v(-13.89, -43.8) * mm});
            skLineSegment(sketch, "E7329", {"start": v(-13.89, -43.8) * mm, "end": v(-13.88, -43.8) * mm});
            skLineSegment(sketch, "E7330", {"start": v(-13.88, -43.8) * mm, "end": v(-13.77, -43.84) * mm});
            skLineSegment(sketch, "E7331", {"start": v(-13.77, -43.84) * mm, "end": v(-13.66, -43.87) * mm});
            skLineSegment(sketch, "E7332", {"start": v(-13.66, -43.87) * mm, "end": v(-13.55, -43.9) * mm});
            skLineSegment(sketch, "E7333", {"start": v(-13.55, -43.9) * mm, "end": v(-13.44, -43.94) * mm});
            skLineSegment(sketch, "E7334", {"start": v(-13.44, -43.94) * mm, "end": v(-13.35, -43.97) * mm});
            skLineSegment(sketch, "E7335", {"start": v(-13.35, -43.97) * mm, "end": v(-13.27, -43.88) * mm});
            skLineSegment(sketch, "E7336", {"start": v(-13.27, -43.88) * mm, "end": v(-13.19, -43.78) * mm});
            skLineSegment(sketch, "E7337", {"start": v(-13.19, -43.78) * mm, "end": v(-13.11, -43.7) * mm});
            skLineSegment(sketch, "E7338", {"start": v(-13.11, -43.7) * mm, "end": v(-13.04, -43.6) * mm});
            skLineSegment(sketch, "E7339", {"start": v(-13.04, -43.6) * mm, "end": v(-12.97, -43.51) * mm});
            skLineSegment(sketch, "E7340", {"start": v(-12.97, -43.51) * mm, "end": v(-12.9, -43.42) * mm});
            skLineSegment(sketch, "E7341", {"start": v(-12.9, -43.42) * mm, "end": v(-12.82, -43.32) * mm});
            skLineSegment(sketch, "E7342", {"start": v(-12.82, -43.32) * mm, "end": v(-12.75, -43.23) * mm});
            skLineSegment(sketch, "E7343", {"start": v(-12.75, -43.23) * mm, "end": v(-12.67, -43.13) * mm});
            skLineSegment(sketch, "E7344", {"start": v(-12.67, -43.13) * mm, "end": v(-12.6, -43.03) * mm});
            skLineSegment(sketch, "E7345", {"start": v(-12.6, -43.03) * mm, "end": v(-12.53, -42.94) * mm});
            skLineSegment(sketch, "E7346", {"start": v(-12.53, -42.94) * mm, "end": v(-12.46, -42.84) * mm});
            skLineSegment(sketch, "E7347", {"start": v(-12.46, -42.84) * mm, "end": v(-12.39, -42.74) * mm});
            skLineSegment(sketch, "E7348", {"start": v(-12.39, -42.74) * mm, "end": v(-12.32, -42.64) * mm});
            skLineSegment(sketch, "E7349", {"start": v(-12.32, -42.64) * mm, "end": v(-12.25, -42.55) * mm});
            skLineSegment(sketch, "E7350", {"start": v(-12.25, -42.55) * mm, "end": v(-12.18, -42.45) * mm});
            skLineSegment(sketch, "E7351", {"start": v(-12.18, -42.45) * mm, "end": v(-12.12, -42.35) * mm});
            skLineSegment(sketch, "E7352", {"start": v(-12.12, -42.35) * mm, "end": v(-12.05, -42.25) * mm});
            skLineSegment(sketch, "E7353", {"start": v(-12.05, -42.25) * mm, "end": v(-11.98, -42.14) * mm});
            skLineSegment(sketch, "E7354", {"start": v(-11.98, -42.14) * mm, "end": v(-11.87, -42.17) * mm});
            skLineSegment(sketch, "E7355", {"start": v(-11.87, -42.17) * mm, "end": v(-11.75, -42.2) * mm});
            skLineSegment(sketch, "E7356", {"start": v(-11.75, -42.2) * mm, "end": v(-11.64, -42.23) * mm});
            skLineSegment(sketch, "E7357", {"start": v(-11.64, -42.23) * mm, "end": v(-11.53, -42.26) * mm});
            skLineSegment(sketch, "E7358", {"start": v(-11.53, -42.26) * mm, "end": v(-11.41, -42.3) * mm});
            skLineSegment(sketch, "E7359", {"start": v(-11.41, -42.3) * mm, "end": v(-11.3, -42.33) * mm});
            skLineSegment(sketch, "E7360", {"start": v(-11.3, -42.33) * mm, "end": v(-11.18, -42.36) * mm});
            skLineSegment(sketch, "E7361", {"start": v(-11.18, -42.36) * mm, "end": v(-11.17, -42.36) * mm});
            skLineSegment(sketch, "E7362", {"start": v(-11.17, -42.36) * mm, "end": v(-11.16, -42.47) * mm});
            skLineSegment(sketch, "E7363", {"start": v(-11.16, -42.47) * mm, "end": v(-11.16, -42.58) * mm});
            skLineSegment(sketch, "E7364", {"start": v(-11.16, -42.58) * mm, "end": v(-11.15, -42.7) * mm});
            skLineSegment(sketch, "E7365", {"start": v(-11.15, -42.7) * mm, "end": v(-11.15, -42.82) * mm});
            skLineSegment(sketch, "E7366", {"start": v(-11.15, -42.82) * mm, "end": v(-11.14, -42.94) * mm});
            skLineSegment(sketch, "E7367", {"start": v(-11.14, -42.94) * mm, "end": v(-11.13, -43.06) * mm});
            skLineSegment(sketch, "E7368", {"start": v(-11.13, -43.06) * mm, "end": v(-11.12, -43.19) * mm});
            skLineSegment(sketch, "E7369", {"start": v(-11.12, -43.19) * mm, "end": v(-11.1, -43.32) * mm});
            skLineSegment(sketch, "E7370", {"start": v(-11.1, -43.32) * mm, "end": v(-11.1, -43.44) * mm});
            skLineSegment(sketch, "E7371", {"start": v(-11.1, -43.44) * mm, "end": v(-11.08, -43.56) * mm});
            skLineSegment(sketch, "E7372", {"start": v(-11.08, -43.56) * mm, "end": v(-11.07, -43.67) * mm});
            skLineSegment(sketch, "E7373", {"start": v(-11.07, -43.67) * mm, "end": v(-11.06, -43.79) * mm});
            skLineSegment(sketch, "E7374", {"start": v(-11.06, -43.79) * mm, "end": v(-11.04, -43.9) * mm});
            skLineSegment(sketch, "E7375", {"start": v(-11.04, -43.9) * mm, "end": v(-11.03, -44.02) * mm});
            skLineSegment(sketch, "E7376", {"start": v(-11.03, -44.02) * mm, "end": v(-11, -44.14) * mm});
            skLineSegment(sketch, "E7377", {"start": v(-11, -44.14) * mm, "end": v(-10.99, -44.26) * mm});
            skLineSegment(sketch, "E7378", {"start": v(-10.99, -44.26) * mm, "end": v(-10.97, -44.38) * mm});
            skLineSegment(sketch, "E7379", {"start": v(-10.97, -44.38) * mm, "end": v(-10.95, -44.5) * mm});
            skLineSegment(sketch, "E7380", {"start": v(-10.95, -44.5) * mm, "end": v(-10.93, -44.63) * mm});
            skLineSegment(sketch, "E7381", {"start": v(-10.93, -44.63) * mm, "end": v(-10.93, -44.63) * mm});
            skLineSegment(sketch, "E7382", {"start": v(-10.93, -44.63) * mm, "end": v(-10.81, -44.66) * mm});
            skLineSegment(sketch, "E7383", {"start": v(-10.81, -44.66) * mm, "end": v(-10.7, -44.69) * mm});
            skLineSegment(sketch, "E7384", {"start": v(-10.7, -44.69) * mm, "end": v(-10.6, -44.71) * mm});
            skLineSegment(sketch, "E7385", {"start": v(-10.6, -44.71) * mm, "end": v(-10.47, -44.74) * mm});
            skLineSegment(sketch, "E7386", {"start": v(-10.47, -44.74) * mm, "end": v(-10.38, -44.76) * mm});
            skLineSegment(sketch, "E7387", {"start": v(-10.38, -44.76) * mm, "end": v(-10.3, -44.67) * mm});
            skLineSegment(sketch, "E7388", {"start": v(-10.3, -44.67) * mm, "end": v(-10.24, -44.57) * mm});
            skLineSegment(sketch, "E7389", {"start": v(-10.24, -44.57) * mm, "end": v(-10.17, -44.47) * mm});
            skLineSegment(sketch, "E7390", {"start": v(-10.17, -44.47) * mm, "end": v(-10.1, -44.38) * mm});
            skLineSegment(sketch, "E7391", {"start": v(-10.1, -44.38) * mm, "end": v(-10.03, -44.28) * mm});
            skLineSegment(sketch, "E7392", {"start": v(-10.03, -44.28) * mm, "end": v(-9.96, -44.18) * mm});
            skLineSegment(sketch, "E7393", {"start": v(-9.96, -44.18) * mm, "end": v(-9.9, -44.08) * mm});
            skLineSegment(sketch, "E7394", {"start": v(-9.9, -44.08) * mm, "end": v(-9.83, -43.98) * mm});
            skLineSegment(sketch, "E7395", {"start": v(-9.83, -43.98) * mm, "end": v(-9.76, -43.88) * mm});
            skLineSegment(sketch, "E7396", {"start": v(-9.76, -43.88) * mm, "end": v(-9.7, -43.78) * mm});
            skLineSegment(sketch, "E7397", {"start": v(-9.7, -43.78) * mm, "end": v(-9.63, -43.68) * mm});
            skLineSegment(sketch, "E7398", {"start": v(-9.63, -43.68) * mm, "end": v(-9.57, -43.58) * mm});
            skLineSegment(sketch, "E7399", {"start": v(-9.57, -43.58) * mm, "end": v(-9.5, -43.47) * mm});
            skLineSegment(sketch, "E7400", {"start": v(-9.5, -43.47) * mm, "end": v(-9.44, -43.37) * mm});
            skLineSegment(sketch, "E7401", {"start": v(-9.44, -43.37) * mm, "end": v(-9.38, -43.27) * mm});
            skLineSegment(sketch, "E7402", {"start": v(-9.38, -43.27) * mm, "end": v(-9.32, -43.17) * mm});
            skLineSegment(sketch, "E7403", {"start": v(-9.32, -43.17) * mm, "end": v(-9.26, -43.06) * mm});
            skLineSegment(sketch, "E7404", {"start": v(-9.26, -43.06) * mm, "end": v(-9.2, -42.96) * mm});
            skLineSegment(sketch, "E7405", {"start": v(-9.2, -42.96) * mm, "end": v(-9.14, -42.84) * mm});
            skLineSegment(sketch, "E7406", {"start": v(-9.14, -42.84) * mm, "end": v(-9.02, -42.87) * mm});
            skLineSegment(sketch, "E7407", {"start": v(-9.02, -42.87) * mm, "end": v(-8.9, -42.9) * mm});
            skLineSegment(sketch, "E7408", {"start": v(-8.9, -42.9) * mm, "end": v(-8.8, -42.92) * mm});
            skLineSegment(sketch, "E7409", {"start": v(-8.8, -42.92) * mm, "end": v(-8.68, -42.94) * mm});
            skLineSegment(sketch, "E7410", {"start": v(-8.68, -42.94) * mm, "end": v(-8.56, -42.96) * mm});
            skLineSegment(sketch, "E7411", {"start": v(-8.56, -42.96) * mm, "end": v(-8.45, -42.99) * mm});
            skLineSegment(sketch, "E7412", {"start": v(-8.45, -42.99) * mm, "end": v(-8.33, -43.01) * mm});
            skLineSegment(sketch, "E7413", {"start": v(-8.33, -43.01) * mm, "end": v(-8.31, -43.01) * mm});
            skLineSegment(sketch, "E7414", {"start": v(-8.31, -43.01) * mm, "end": v(-8.3, -43.12) * mm});
            skLineSegment(sketch, "E7415", {"start": v(-8.3, -43.12) * mm, "end": v(-8.3, -43.23) * mm});
            skLineSegment(sketch, "E7416", {"start": v(-8.3, -43.23) * mm, "end": v(-8.28, -43.35) * mm});
            skLineSegment(sketch, "E7417", {"start": v(-8.28, -43.35) * mm, "end": v(-8.26, -43.47) * mm});
            skLineSegment(sketch, "E7418", {"start": v(-8.26, -43.47) * mm, "end": v(-8.25, -43.59) * mm});
            skLineSegment(sketch, "E7419", {"start": v(-8.25, -43.59) * mm, "end": v(-8.23, -43.7) * mm});
            skLineSegment(sketch, "E7420", {"start": v(-8.23, -43.7) * mm, "end": v(-8.21, -43.84) * mm});
            skLineSegment(sketch, "E7421", {"start": v(-8.21, -43.84) * mm, "end": v(-8.19, -43.96) * mm});
            skLineSegment(sketch, "E7422", {"start": v(-8.19, -43.96) * mm, "end": v(-8.17, -44.08) * mm});
            skLineSegment(sketch, "E7423", {"start": v(-8.17, -44.08) * mm, "end": v(-8.15, -44.2) * mm});
            skLineSegment(sketch, "E7424", {"start": v(-8.15, -44.2) * mm, "end": v(-8.13, -44.31) * mm});
            skLineSegment(sketch, "E7425", {"start": v(-8.13, -44.31) * mm, "end": v(-8.1, -44.43) * mm});
            skLineSegment(sketch, "E7426", {"start": v(-8.1, -44.43) * mm, "end": v(-8.08, -44.54) * mm});
            skLineSegment(sketch, "E7427", {"start": v(-8.08, -44.54) * mm, "end": v(-8.06, -44.66) * mm});
            skLineSegment(sketch, "E7428", {"start": v(-8.06, -44.66) * mm, "end": v(-8.04, -44.77) * mm});
            skLineSegment(sketch, "E7429", {"start": v(-8.04, -44.77) * mm, "end": v(-8, -44.9) * mm});
            skLineSegment(sketch, "E7430", {"start": v(-8, -44.9) * mm, "end": v(-7.98, -45.01) * mm});
            skLineSegment(sketch, "E7431", {"start": v(-7.98, -45.01) * mm, "end": v(-7.95, -45.14) * mm});
            skLineSegment(sketch, "E7432", {"start": v(-7.95, -45.14) * mm, "end": v(-7.92, -45.26) * mm});
            skLineSegment(sketch, "E7433", {"start": v(-7.92, -45.26) * mm, "end": v(-7.92, -45.26) * mm});
            skLineSegment(sketch, "E7434", {"start": v(-7.92, -45.26) * mm, "end": v(-7.8, -45.28) * mm});
            skLineSegment(sketch, "E7435", {"start": v(-7.8, -45.28) * mm, "end": v(-7.69, -45.3) * mm});
            skLineSegment(sketch, "E7436", {"start": v(-7.69, -45.3) * mm, "end": v(-7.58, -45.32) * mm});
            skLineSegment(sketch, "E7437", {"start": v(-7.58, -45.32) * mm, "end": v(-7.46, -45.34) * mm});
            skLineSegment(sketch, "E7438", {"start": v(-7.46, -45.34) * mm, "end": v(-7.37, -45.36) * mm});
            skLineSegment(sketch, "E7439", {"start": v(-7.37, -45.36) * mm, "end": v(-7.3, -45.26) * mm});
            skLineSegment(sketch, "E7440", {"start": v(-7.3, -45.26) * mm, "end": v(-7.24, -45.15) * mm});
            skLineSegment(sketch, "E7441", {"start": v(-7.24, -45.15) * mm, "end": v(-7.17, -45.05) * mm});
            skLineSegment(sketch, "E7442", {"start": v(-7.17, -45.05) * mm, "end": v(-7.11, -44.95) * mm});
            skLineSegment(sketch, "E7443", {"start": v(-7.11, -44.95) * mm, "end": v(-7.05, -44.85) * mm});
            skLineSegment(sketch, "E7444", {"start": v(-7.05, -44.85) * mm, "end": v(-6.99, -44.75) * mm});
            skLineSegment(sketch, "E7445", {"start": v(-6.99, -44.75) * mm, "end": v(-6.93, -44.65) * mm});
            skLineSegment(sketch, "E7446", {"start": v(-6.93, -44.65) * mm, "end": v(-6.87, -44.54) * mm});
            skLineSegment(sketch, "E7447", {"start": v(-6.87, -44.54) * mm, "end": v(-6.81, -44.44) * mm});
            skLineSegment(sketch, "E7448", {"start": v(-6.81, -44.44) * mm, "end": v(-6.75, -44.33) * mm});
            skLineSegment(sketch, "E7449", {"start": v(-6.75, -44.33) * mm, "end": v(-6.7, -44.22) * mm});
            skLineSegment(sketch, "E7450", {"start": v(-6.7, -44.22) * mm, "end": v(-6.63, -44.12) * mm});
            skLineSegment(sketch, "E7451", {"start": v(-6.63, -44.12) * mm, "end": v(-6.58, -44.01) * mm});
            skLineSegment(sketch, "E7452", {"start": v(-6.58, -44.01) * mm, "end": v(-6.52, -43.9) * mm});
            skLineSegment(sketch, "E7453", {"start": v(-6.52, -43.9) * mm, "end": v(-6.47, -43.8) * mm});
            skLineSegment(sketch, "E7454", {"start": v(-6.47, -43.8) * mm, "end": v(-6.42, -43.7) * mm});
            skLineSegment(sketch, "E7455", {"start": v(-6.42, -43.7) * mm, "end": v(-6.36, -43.58) * mm});
            skLineSegment(sketch, "E7456", {"start": v(-6.36, -43.58) * mm, "end": v(-6.31, -43.48) * mm});
            skLineSegment(sketch, "E7457", {"start": v(-6.31, -43.48) * mm, "end": v(-6.26, -43.36) * mm});
            skLineSegment(sketch, "E7458", {"start": v(-6.26, -43.36) * mm, "end": v(-6.14, -43.37) * mm});
            skLineSegment(sketch, "E7459", {"start": v(-6.14, -43.37) * mm, "end": v(-6.02, -43.4) * mm});
            skLineSegment(sketch, "E7460", {"start": v(-6.02, -43.4) * mm, "end": v(-5.9, -43.4) * mm});
            skLineSegment(sketch, "E7461", {"start": v(-5.9, -43.4) * mm, "end": v(-5.8, -43.42) * mm});
            skLineSegment(sketch, "E7462", {"start": v(-5.8, -43.42) * mm, "end": v(-5.67, -43.44) * mm});
            skLineSegment(sketch, "E7463", {"start": v(-5.67, -43.44) * mm, "end": v(-5.56, -43.45) * mm});
            skLineSegment(sketch, "E7464", {"start": v(-5.56, -43.45) * mm, "end": v(-5.44, -43.47) * mm});
            skLineSegment(sketch, "E7465", {"start": v(-5.44, -43.47) * mm, "end": v(-5.42, -43.47) * mm});
            skLineSegment(sketch, "E7466", {"start": v(-5.42, -43.47) * mm, "end": v(-5.4, -43.58) * mm});
            skLineSegment(sketch, "E7467", {"start": v(-5.4, -43.58) * mm, "end": v(-5.38, -43.7) * mm});
            skLineSegment(sketch, "E7468", {"start": v(-5.38, -43.7) * mm, "end": v(-5.36, -43.8) * mm});
            skLineSegment(sketch, "E7469", {"start": v(-5.36, -43.8) * mm, "end": v(-5.34, -43.92) * mm});
            skLineSegment(sketch, "E7470", {"start": v(-5.34, -43.92) * mm, "end": v(-5.32, -44.04) * mm});
            skLineSegment(sketch, "E7471", {"start": v(-5.32, -44.04) * mm, "end": v(-5.3, -44.16) * mm});
            skLineSegment(sketch, "E7472", {"start": v(-5.3, -44.16) * mm, "end": v(-5.26, -44.29) * mm});
            skLineSegment(sketch, "E7473", {"start": v(-5.26, -44.29) * mm, "end": v(-5.23, -44.41) * mm});
            skLineSegment(sketch, "E7474", {"start": v(-5.23, -44.41) * mm, "end": v(-5.2, -44.53) * mm});
            skLineSegment(sketch, "E7475", {"start": v(-5.2, -44.53) * mm, "end": v(-5.18, -44.65) * mm});
            skLineSegment(sketch, "E7476", {"start": v(-5.18, -44.65) * mm, "end": v(-5.15, -44.76) * mm});
            skLineSegment(sketch, "E7477", {"start": v(-5.15, -44.76) * mm, "end": v(-5.12, -44.87) * mm});
            skLineSegment(sketch, "E7478", {"start": v(-5.12, -44.87) * mm, "end": v(-5.1, -44.98) * mm});
            skLineSegment(sketch, "E7479", {"start": v(-5.1, -44.98) * mm, "end": v(-5.06, -45.1) * mm});
            skLineSegment(sketch, "E7480", {"start": v(-5.06, -45.1) * mm, "end": v(-5.03, -45.2) * mm});
            skLineSegment(sketch, "E7481", {"start": v(-5.03, -45.2) * mm, "end": v(-5, -45.33) * mm});
            skLineSegment(sketch, "E7482", {"start": v(-5, -45.33) * mm, "end": v(-4.96, -45.45) * mm});
            skLineSegment(sketch, "E7483", {"start": v(-4.96, -45.45) * mm, "end": v(-4.92, -45.57) * mm});
            skLineSegment(sketch, "E7484", {"start": v(-4.92, -45.57) * mm, "end": v(-4.88, -45.69) * mm});
            skLineSegment(sketch, "E7485", {"start": v(-4.88, -45.69) * mm, "end": v(-4.88, -45.69) * mm});
            skLineSegment(sketch, "E7486", {"start": v(-4.88, -45.69) * mm, "end": v(-4.76, -45.7) * mm});
            skLineSegment(sketch, "E7487", {"start": v(-4.76, -45.7) * mm, "end": v(-4.64, -45.71) * mm});
            skLineSegment(sketch, "E7488", {"start": v(-4.64, -45.71) * mm, "end": v(-4.54, -45.73) * mm});
            skLineSegment(sketch, "E7489", {"start": v(-4.54, -45.73) * mm, "end": v(-4.42, -45.74) * mm});
            skLineSegment(sketch, "E7490", {"start": v(-4.42, -45.74) * mm, "end": v(-4.32, -45.75) * mm});
            skLineSegment(sketch, "E7491", {"start": v(-4.32, -45.75) * mm, "end": v(-4.26, -45.64) * mm});
            skLineSegment(sketch, "E7492", {"start": v(-4.26, -45.64) * mm, "end": v(-4.2, -45.53) * mm});
            skLineSegment(sketch, "E7493", {"start": v(-4.2, -45.53) * mm, "end": v(-4.15, -45.43) * mm});
            skLineSegment(sketch, "E7494", {"start": v(-4.15, -45.43) * mm, "end": v(-4.1, -45.33) * mm});
            skLineSegment(sketch, "E7495", {"start": v(-4.1, -45.33) * mm, "end": v(-4.04, -45.22) * mm});
            skLineSegment(sketch, "E7496", {"start": v(-4.04, -45.22) * mm, "end": v(-3.98, -45.12) * mm});
            skLineSegment(sketch, "E7497", {"start": v(-3.98, -45.12) * mm, "end": v(-3.93, -45) * mm});
            skLineSegment(sketch, "E7498", {"start": v(-3.93, -45) * mm, "end": v(-3.88, -44.9) * mm});
            skLineSegment(sketch, "E7499", {"start": v(-3.88, -44.9) * mm, "end": v(-3.83, -44.8) * mm});
            skLineSegment(sketch, "E7500", {"start": v(-3.83, -44.8) * mm, "end": v(-3.77, -44.68) * mm});
            skLineSegment(sketch, "E7501", {"start": v(-3.77, -44.68) * mm, "end": v(-3.72, -44.57) * mm});
            skLineSegment(sketch, "E7502", {"start": v(-3.72, -44.57) * mm, "end": v(-3.67, -44.46) * mm});
            skLineSegment(sketch, "E7503", {"start": v(-3.67, -44.46) * mm, "end": v(-3.62, -44.35) * mm});
            skLineSegment(sketch, "E7504", {"start": v(-3.62, -44.35) * mm, "end": v(-3.58, -44.24) * mm});
            skLineSegment(sketch, "E7505", {"start": v(-3.58, -44.24) * mm, "end": v(-3.53, -44.13) * mm});
            skLineSegment(sketch, "E7506", {"start": v(-3.53, -44.13) * mm, "end": v(-3.48, -44.02) * mm});
            skLineSegment(sketch, "E7507", {"start": v(-3.48, -44.02) * mm, "end": v(-3.44, -43.91) * mm});
            skLineSegment(sketch, "E7508", {"start": v(-3.44, -43.91) * mm, "end": v(-3.4, -43.8) * mm});
            skLineSegment(sketch, "E7509", {"start": v(-3.4, -43.8) * mm, "end": v(-3.35, -43.68) * mm});
            skLineSegment(sketch, "E7510", {"start": v(-3.35, -43.68) * mm, "end": v(-3.23, -43.69) * mm});
            skLineSegment(sketch, "E7511", {"start": v(-3.23, -43.69) * mm, "end": v(-3.11, -43.7) * mm});
            skLineSegment(sketch, "E7512", {"start": v(-3.11, -43.7) * mm, "end": v(-3, -43.7) * mm});
            skLineSegment(sketch, "E7513", {"start": v(-3, -43.7) * mm, "end": v(-2.88, -43.71) * mm});
            skLineSegment(sketch, "E7514", {"start": v(-2.88, -43.71) * mm, "end": v(-2.76, -43.72) * mm});
            skLineSegment(sketch, "E7515", {"start": v(-2.76, -43.72) * mm, "end": v(-2.64, -43.73) * mm});
            skLineSegment(sketch, "E7516", {"start": v(-2.64, -43.73) * mm, "end": v(-2.52, -43.74) * mm});
            skLineSegment(sketch, "E7517", {"start": v(-2.52, -43.74) * mm, "end": v(-2.5, -43.74) * mm});
            skLineSegment(sketch, "E7518", {"start": v(-2.5, -43.74) * mm, "end": v(-2.48, -43.84) * mm});
            skLineSegment(sketch, "E7519", {"start": v(-2.48, -43.84) * mm, "end": v(-2.45, -43.95) * mm});
            skLineSegment(sketch, "E7520", {"start": v(-2.45, -43.95) * mm, "end": v(-2.43, -44.06) * mm});
            skLineSegment(sketch, "E7521", {"start": v(-2.43, -44.06) * mm, "end": v(-2.4, -44.18) * mm});
            skLineSegment(sketch, "E7522", {"start": v(-2.4, -44.18) * mm, "end": v(-2.36, -44.3) * mm});
            skLineSegment(sketch, "E7523", {"start": v(-2.36, -44.3) * mm, "end": v(-2.33, -44.42) * mm});
            skLineSegment(sketch, "E7524", {"start": v(-2.33, -44.42) * mm, "end": v(-2.3, -44.54) * mm});
            skLineSegment(sketch, "E7525", {"start": v(-2.3, -44.54) * mm, "end": v(-2.26, -44.66) * mm});
            skLineSegment(sketch, "E7526", {"start": v(-2.26, -44.66) * mm, "end": v(-2.22, -44.78) * mm});
            skLineSegment(sketch, "E7527", {"start": v(-2.22, -44.78) * mm, "end": v(-2.18, -44.9) * mm});
            skLineSegment(sketch, "E7528", {"start": v(-2.18, -44.9) * mm, "end": v(-2.15, -45) * mm});
            skLineSegment(sketch, "E7529", {"start": v(-2.15, -45) * mm, "end": v(-2.11, -45.11) * mm});
            skLineSegment(sketch, "E7530", {"start": v(-2.11, -45.11) * mm, "end": v(-2.07, -45.22) * mm});
            skLineSegment(sketch, "E7531", {"start": v(-2.07, -45.22) * mm, "end": v(-2.04, -45.33) * mm});
            skLineSegment(sketch, "E7532", {"start": v(-2.04, -45.33) * mm, "end": v(-2, -45.44) * mm});
            skLineSegment(sketch, "E7533", {"start": v(-2, -45.44) * mm, "end": v(-1.95, -45.56) * mm});
            skLineSegment(sketch, "E7534", {"start": v(-1.95, -45.56) * mm, "end": v(-1.91, -45.68) * mm});
            skLineSegment(sketch, "E7535", {"start": v(-1.91, -45.68) * mm, "end": v(-1.87, -45.8) * mm});
            skLineSegment(sketch, "E7536", {"start": v(-1.87, -45.8) * mm, "end": v(-1.82, -45.91) * mm});
            skLineSegment(sketch, "E7537", {"start": v(-1.82, -45.91) * mm, "end": v(-1.82, -45.91) * mm});
            skLineSegment(sketch, "E7538", {"start": v(-1.82, -45.91) * mm, "end": v(-1.7, -45.92) * mm});
            skLineSegment(sketch, "E7539", {"start": v(-1.7, -45.92) * mm, "end": v(-1.58, -45.92) * mm});
            skLineSegment(sketch, "E7540", {"start": v(-1.58, -45.92) * mm, "end": v(-1.47, -45.93) * mm});
            skLineSegment(sketch, "E7541", {"start": v(-1.47, -45.93) * mm, "end": v(-1.35, -45.93) * mm});
            skLineSegment(sketch, "E7542", {"start": v(-1.35, -45.93) * mm, "end": v(-1.25, -45.93) * mm});
            skLineSegment(sketch, "E7543", {"start": v(-1.25, -45.93) * mm, "end": v(-1.2, -45.82) * mm});
            skLineSegment(sketch, "E7544", {"start": v(-1.2, -45.82) * mm, "end": v(-1.15, -45.71) * mm});
            skLineSegment(sketch, "E7545", {"start": v(-1.15, -45.71) * mm, "end": v(-1.1, -45.6) * mm});
            skLineSegment(sketch, "E7546", {"start": v(-1.1, -45.6) * mm, "end": v(-1.06, -45.5) * mm});
            skLineSegment(sketch, "E7547", {"start": v(-1.06, -45.5) * mm, "end": v(-1, -45.4) * mm});
            skLineSegment(sketch, "E7548", {"start": v(-1, -45.4) * mm, "end": v(-0.96, -45.28) * mm});
            skLineSegment(sketch, "E7549", {"start": v(-0.96, -45.28) * mm, "end": v(-0.92, -45.17) * mm});
            skLineSegment(sketch, "E7550", {"start": v(-0.92, -45.17) * mm, "end": v(-0.87, -45.06) * mm});
            skLineSegment(sketch, "E7551", {"start": v(-0.87, -45.06) * mm, "end": v(-0.83, -44.95) * mm});
            skLineSegment(sketch, "E7552", {"start": v(-0.83, -44.95) * mm, "end": v(-0.78, -44.83) * mm});
            skLineSegment(sketch, "E7553", {"start": v(-0.78, -44.83) * mm, "end": v(-0.74, -44.72) * mm});
            skLineSegment(sketch, "E7554", {"start": v(-0.74, -44.72) * mm, "end": v(-0.7, -44.6) * mm});
            skLineSegment(sketch, "E7555", {"start": v(-0.7, -44.6) * mm, "end": v(-0.65, -44.5) * mm});
            skLineSegment(sketch, "E7556", {"start": v(-0.65, -44.5) * mm, "end": v(-0.61, -44.38) * mm});
            skLineSegment(sketch, "E7557", {"start": v(-0.61, -44.38) * mm, "end": v(-0.57, -44.27) * mm});
            skLineSegment(sketch, "E7558", {"start": v(-0.57, -44.27) * mm, "end": v(-0.54, -44.16) * mm});
            skLineSegment(sketch, "E7559", {"start": v(-0.54, -44.16) * mm, "end": v(-0.5, -44.04) * mm});
            skLineSegment(sketch, "E7560", {"start": v(-0.5, -44.04) * mm, "end": v(-0.46, -43.93) * mm});
            skLineSegment(sketch, "E7561", {"start": v(-0.46, -43.93) * mm, "end": v(-0.42, -43.8) * mm});
            skLineSegment(sketch, "E7562", {"start": v(-0.42, -43.8) * mm, "end": v(-0.3, -43.8) * mm});
            skLineSegment(sketch, "E7563", {"start": v(-0.3, -43.8) * mm, "end": v(-0.19, -43.8) * mm});
            skLineSegment(sketch, "E7564", {"start": v(-0.19, -43.8) * mm, "end": v(-0.07, -43.8) * mm});
            skLineSegment(sketch, "E7565", {"start": v(-0.07, -43.8) * mm, "end": v(0.05, -43.8) * mm});
            skLineSegment(sketch, "E7566", {"start": v(0.05, -43.8) * mm, "end": v(0.17, -43.8) * mm});
            skLineSegment(sketch, "E7567", {"start": v(0.17, -43.8) * mm, "end": v(0.29, -43.8) * mm});
            skLineSegment(sketch, "E7568", {"start": v(0.29, -43.8) * mm, "end": v(0.4, -43.8) * mm});
            skLineSegment(sketch, "E7569", {"start": v(0.4, -43.8) * mm, "end": v(0.42, -43.8) * mm});
            skLineSegment(sketch, "E7570", {"start": v(0.42, -43.8) * mm, "end": v(0.45, -43.91) * mm});
            skLineSegment(sketch, "E7571", {"start": v(0.45, -43.91) * mm, "end": v(0.49, -44.02) * mm});
            skLineSegment(sketch, "E7572", {"start": v(0.49, -44.02) * mm, "end": v(0.52, -44.13) * mm});
            skLineSegment(sketch, "E7573", {"start": v(0.52, -44.13) * mm, "end": v(0.56, -44.24) * mm});
            skLineSegment(sketch, "E7574", {"start": v(0.56, -44.24) * mm, "end": v(0.6, -44.35) * mm});
            skLineSegment(sketch, "E7575", {"start": v(0.6, -44.35) * mm, "end": v(0.64, -44.47) * mm});
            skLineSegment(sketch, "E7576", {"start": v(0.64, -44.47) * mm, "end": v(0.69, -44.6) * mm});
            skLineSegment(sketch, "E7577", {"start": v(0.69, -44.6) * mm, "end": v(0.73, -44.71) * mm});
            skLineSegment(sketch, "E7578", {"start": v(0.73, -44.71) * mm, "end": v(0.78, -44.83) * mm});
            skLineSegment(sketch, "E7579", {"start": v(0.78, -44.83) * mm, "end": v(0.82, -44.94) * mm});
            skLineSegment(sketch, "E7580", {"start": v(0.82, -44.94) * mm, "end": v(0.86, -45.05) * mm});
            skLineSegment(sketch, "E7581", {"start": v(0.86, -45.05) * mm, "end": v(0.9, -45.15) * mm});
            skLineSegment(sketch, "E7582", {"start": v(0.9, -45.15) * mm, "end": v(0.95, -45.26) * mm});
            skLineSegment(sketch, "E7583", {"start": v(0.95, -45.26) * mm, "end": v(1, -45.37) * mm});
            skLineSegment(sketch, "E7584", {"start": v(1, -45.37) * mm, "end": v(1.04, -45.48) * mm});
            skLineSegment(sketch, "E7585", {"start": v(1.04, -45.48) * mm, "end": v(1.1, -45.59) * mm});
            skLineSegment(sketch, "E7586", {"start": v(1.1, -45.59) * mm, "end": v(1.15, -45.7) * mm});
            skLineSegment(sketch, "E7587", {"start": v(1.15, -45.7) * mm, "end": v(1.2, -45.82) * mm});
            skLineSegment(sketch, "E7588", {"start": v(1.2, -45.82) * mm, "end": v(1.25, -45.93) * mm});
            skLineSegment(sketch, "E7589", {"start": v(1.25, -45.93) * mm, "end": v(1.25, -45.93) * mm});
            skLineSegment(sketch, "E7590", {"start": v(1.25, -45.93) * mm, "end": v(1.37, -45.93) * mm});
            skLineSegment(sketch, "E7591", {"start": v(1.37, -45.93) * mm, "end": v(1.5, -45.93) * mm});
            skLineSegment(sketch, "E7592", {"start": v(1.5, -45.93) * mm, "end": v(1.6, -45.92) * mm});
            skLineSegment(sketch, "E7593", {"start": v(1.6, -45.92) * mm, "end": v(1.72, -45.92) * mm});
            skLineSegment(sketch, "E7594", {"start": v(1.72, -45.92) * mm, "end": v(1.82, -45.91) * mm});
            skLineSegment(sketch, "E7595", {"start": v(1.82, -45.91) * mm, "end": v(1.86, -45.8) * mm});
            skLineSegment(sketch, "E7596", {"start": v(1.86, -45.8) * mm, "end": v(1.9, -45.69) * mm});
            skLineSegment(sketch, "E7597", {"start": v(1.9, -45.69) * mm, "end": v(1.95, -45.58) * mm});
            skLineSegment(sketch, "E7598", {"start": v(1.95, -45.58) * mm, "end": v(1.98, -45.47) * mm});
            skLineSegment(sketch, "E7599", {"start": v(1.98, -45.47) * mm, "end": v(2.02, -45.36) * mm});
            skLineSegment(sketch, "E7600", {"start": v(2.02, -45.36) * mm, "end": v(2.06, -45.24) * mm});
            skLineSegment(sketch, "E7601", {"start": v(2.06, -45.24) * mm, "end": v(2.1, -45.13) * mm});
            skLineSegment(sketch, "E7602", {"start": v(2.1, -45.13) * mm, "end": v(2.14, -45.02) * mm});
            skLineSegment(sketch, "E7603", {"start": v(2.14, -45.02) * mm, "end": v(2.18, -44.9) * mm});
            skLineSegment(sketch, "E7604", {"start": v(2.18, -44.9) * mm, "end": v(2.22, -44.78) * mm});
            skLineSegment(sketch, "E7605", {"start": v(2.22, -44.78) * mm, "end": v(2.25, -44.67) * mm});
            skLineSegment(sketch, "E7606", {"start": v(2.25, -44.67) * mm, "end": v(2.29, -44.56) * mm});
            skLineSegment(sketch, "E7607", {"start": v(2.29, -44.56) * mm, "end": v(2.32, -44.44) * mm});
            skLineSegment(sketch, "E7608", {"start": v(2.32, -44.44) * mm, "end": v(2.35, -44.33) * mm});
            skLineSegment(sketch, "E7609", {"start": v(2.35, -44.33) * mm, "end": v(2.38, -44.2) * mm});
            skLineSegment(sketch, "E7610", {"start": v(2.38, -44.2) * mm, "end": v(2.42, -44.1) * mm});
            skLineSegment(sketch, "E7611", {"start": v(2.42, -44.1) * mm, "end": v(2.44, -43.98) * mm});
            skLineSegment(sketch, "E7612", {"start": v(2.44, -43.98) * mm, "end": v(2.47, -43.86) * mm});
            skLineSegment(sketch, "E7613", {"start": v(2.47, -43.86) * mm, "end": v(2.5, -43.74) * mm});
            skLineSegment(sketch, "E7614", {"start": v(2.5, -43.74) * mm, "end": v(2.62, -43.73) * mm});
            skLineSegment(sketch, "E7615", {"start": v(2.62, -43.73) * mm, "end": v(2.74, -43.72) * mm});
            skLineSegment(sketch, "E7616", {"start": v(2.74, -43.72) * mm, "end": v(2.86, -43.71) * mm});
            skLineSegment(sketch, "E7617", {"start": v(2.86, -43.71) * mm, "end": v(2.98, -43.7) * mm});
            skLineSegment(sketch, "E7618", {"start": v(2.98, -43.7) * mm, "end": v(3.1, -43.7) * mm});
            skLineSegment(sketch, "E7619", {"start": v(3.1, -43.7) * mm, "end": v(3.21, -43.69) * mm});
            skLineSegment(sketch, "E7620", {"start": v(3.21, -43.69) * mm, "end": v(3.33, -43.68) * mm});
            skLineSegment(sketch, "E7621", {"start": v(3.33, -43.68) * mm, "end": v(3.35, -43.68) * mm});
            skLineSegment(sketch, "E7622", {"start": v(3.35, -43.68) * mm, "end": v(3.39, -43.78) * mm});
            skLineSegment(sketch, "E7623", {"start": v(3.39, -43.78) * mm, "end": v(3.43, -43.89) * mm});
            skLineSegment(sketch, "E7624", {"start": v(3.43, -43.89) * mm, "end": v(3.47, -44) * mm});
            skLineSegment(sketch, "E7625", {"start": v(3.47, -44) * mm, "end": v(3.52, -44.1) * mm});
            skLineSegment(sketch, "E7626", {"start": v(3.52, -44.1) * mm, "end": v(3.56, -44.22) * mm});
            skLineSegment(sketch, "E7627", {"start": v(3.56, -44.22) * mm, "end": v(3.61, -44.33) * mm});
            skLineSegment(sketch, "E7628", {"start": v(3.61, -44.33) * mm, "end": v(3.66, -44.45) * mm});
            skLineSegment(sketch, "E7629", {"start": v(3.66, -44.45) * mm, "end": v(3.72, -44.57) * mm});
            skLineSegment(sketch, "E7630", {"start": v(3.72, -44.57) * mm, "end": v(3.77, -44.67) * mm});
            skLineSegment(sketch, "E7631", {"start": v(3.77, -44.67) * mm, "end": v(3.82, -44.79) * mm});
            skLineSegment(sketch, "E7632", {"start": v(3.82, -44.79) * mm, "end": v(3.87, -44.89) * mm});
            skLineSegment(sketch, "E7633", {"start": v(3.87, -44.89) * mm, "end": v(3.92, -44.99) * mm});
            skLineSegment(sketch, "E7634", {"start": v(3.92, -44.99) * mm, "end": v(3.97, -45.1) * mm});
            skLineSegment(sketch, "E7635", {"start": v(3.97, -45.1) * mm, "end": v(4.02, -45.2) * mm});
            skLineSegment(sketch, "E7636", {"start": v(4.02, -45.2) * mm, "end": v(4.08, -45.3) * mm});
            skLineSegment(sketch, "E7637", {"start": v(4.08, -45.3) * mm, "end": v(4.14, -45.41) * mm});
            skLineSegment(sketch, "E7638", {"start": v(4.14, -45.41) * mm, "end": v(4.2, -45.52) * mm});
            skLineSegment(sketch, "E7639", {"start": v(4.2, -45.52) * mm, "end": v(4.26, -45.63) * mm});
            skLineSegment(sketch, "E7640", {"start": v(4.26, -45.63) * mm, "end": v(4.32, -45.75) * mm});
            skLineSegment(sketch, "E7641", {"start": v(4.32, -45.75) * mm, "end": v(4.32, -45.75) * mm});
            skLineSegment(sketch, "E7642", {"start": v(4.32, -45.75) * mm, "end": v(4.44, -45.73) * mm});
            skLineSegment(sketch, "E7643", {"start": v(4.44, -45.73) * mm, "end": v(4.56, -45.72) * mm});
            skLineSegment(sketch, "E7644", {"start": v(4.56, -45.72) * mm, "end": v(4.66, -45.71) * mm});
            skLineSegment(sketch, "E7645", {"start": v(4.66, -45.71) * mm, "end": v(4.78, -45.7) * mm});
            skLineSegment(sketch, "E7646", {"start": v(4.78, -45.7) * mm, "end": v(4.88, -45.69) * mm});
            skLineSegment(sketch, "E7647", {"start": v(4.88, -45.69) * mm, "end": v(4.92, -45.58) * mm});
            skLineSegment(sketch, "E7648", {"start": v(4.92, -45.58) * mm, "end": v(4.95, -45.46) * mm});
            skLineSegment(sketch, "E7649", {"start": v(4.95, -45.46) * mm, "end": v(4.99, -45.34) * mm});
            skLineSegment(sketch, "E7650", {"start": v(4.99, -45.34) * mm, "end": v(5.02, -45.24) * mm});
            skLineSegment(sketch, "E7651", {"start": v(5.02, -45.24) * mm, "end": v(5.05, -45.12) * mm});
            skLineSegment(sketch, "E7652", {"start": v(5.05, -45.12) * mm, "end": v(5.08, -45) * mm});
            skLineSegment(sketch, "E7653", {"start": v(5.08, -45) * mm, "end": v(5.11, -44.89) * mm});
            skLineSegment(sketch, "E7654", {"start": v(5.11, -44.89) * mm, "end": v(5.14, -44.77) * mm});
            skLineSegment(sketch, "E7655", {"start": v(5.14, -44.77) * mm, "end": v(5.17, -44.66) * mm});
            skLineSegment(sketch, "E7656", {"start": v(5.17, -44.66) * mm, "end": v(5.2, -44.54) * mm});
            skLineSegment(sketch, "E7657", {"start": v(5.2, -44.54) * mm, "end": v(5.23, -44.42) * mm});
            skLineSegment(sketch, "E7658", {"start": v(5.23, -44.42) * mm, "end": v(5.26, -44.3) * mm});
            skLineSegment(sketch, "E7659", {"start": v(5.26, -44.3) * mm, "end": v(5.28, -44.19) * mm});
            skLineSegment(sketch, "E7660", {"start": v(5.28, -44.19) * mm, "end": v(5.3, -44.07) * mm});
            skLineSegment(sketch, "E7661", {"start": v(5.3, -44.07) * mm, "end": v(5.33, -43.95) * mm});
            skLineSegment(sketch, "E7662", {"start": v(5.33, -43.95) * mm, "end": v(5.36, -43.83) * mm});
            skLineSegment(sketch, "E7663", {"start": v(5.36, -43.83) * mm, "end": v(5.38, -43.72) * mm});
            skLineSegment(sketch, "E7664", {"start": v(5.38, -43.72) * mm, "end": v(5.4, -43.6) * mm});
            skLineSegment(sketch, "E7665", {"start": v(5.4, -43.6) * mm, "end": v(5.42, -43.47) * mm});
            skLineSegment(sketch, "E7666", {"start": v(5.42, -43.47) * mm, "end": v(5.54, -43.46) * mm});
            skLineSegment(sketch, "E7667", {"start": v(5.54, -43.46) * mm, "end": v(5.65, -43.44) * mm});
            skLineSegment(sketch, "E7668", {"start": v(5.65, -43.44) * mm, "end": v(5.77, -43.42) * mm});
            skLineSegment(sketch, "E7669", {"start": v(5.77, -43.42) * mm, "end": v(5.89, -43.4) * mm});
            skLineSegment(sketch, "E7670", {"start": v(5.89, -43.4) * mm, "end": v(6, -43.4) * mm});
            skLineSegment(sketch, "E7671", {"start": v(6, -43.4) * mm, "end": v(6.12, -43.38) * mm});
            skLineSegment(sketch, "E7672", {"start": v(6.12, -43.38) * mm, "end": v(6.24, -43.36) * mm});
            skLineSegment(sketch, "E7673", {"start": v(6.24, -43.36) * mm, "end": v(6.26, -43.36) * mm});
            skLineSegment(sketch, "E7674", {"start": v(6.26, -43.36) * mm, "end": v(6.3, -43.46) * mm});
            skLineSegment(sketch, "E7675", {"start": v(6.3, -43.46) * mm, "end": v(6.35, -43.56) * mm});
            skLineSegment(sketch, "E7676", {"start": v(6.35, -43.56) * mm, "end": v(6.4, -43.66) * mm});
            skLineSegment(sketch, "E7677", {"start": v(6.4, -43.66) * mm, "end": v(6.45, -43.77) * mm});
            skLineSegment(sketch, "E7678", {"start": v(6.45, -43.77) * mm, "end": v(6.5, -43.88) * mm});
            skLineSegment(sketch, "E7679", {"start": v(6.5, -43.88) * mm, "end": v(6.56, -43.99) * mm});
            skLineSegment(sketch, "E7680", {"start": v(6.56, -43.99) * mm, "end": v(6.62, -44.1) * mm});
            skLineSegment(sketch, "E7681", {"start": v(6.62, -44.1) * mm, "end": v(6.69, -44.22) * mm});
            skLineSegment(sketch, "E7682", {"start": v(6.69, -44.22) * mm, "end": v(6.74, -44.32) * mm});
            skLineSegment(sketch, "E7683", {"start": v(6.74, -44.32) * mm, "end": v(6.8, -44.43) * mm});
            skLineSegment(sketch, "E7684", {"start": v(6.8, -44.43) * mm, "end": v(6.86, -44.53) * mm});
            skLineSegment(sketch, "E7685", {"start": v(6.86, -44.53) * mm, "end": v(6.92, -44.63) * mm});
            skLineSegment(sketch, "E7686", {"start": v(6.92, -44.63) * mm, "end": v(6.97, -44.73) * mm});
            skLineSegment(sketch, "E7687", {"start": v(6.97, -44.73) * mm, "end": v(7.04, -44.83) * mm});
            skLineSegment(sketch, "E7688", {"start": v(7.04, -44.83) * mm, "end": v(7.1, -44.93) * mm});
            skLineSegment(sketch, "E7689", {"start": v(7.1, -44.93) * mm, "end": v(7.16, -45.04) * mm});
            skLineSegment(sketch, "E7690", {"start": v(7.16, -45.04) * mm, "end": v(7.23, -45.14) * mm});
            skLineSegment(sketch, "E7691", {"start": v(7.23, -45.14) * mm, "end": v(7.3, -45.25) * mm});
            skLineSegment(sketch, "E7692", {"start": v(7.3, -45.25) * mm, "end": v(7.36, -45.35) * mm});
            skLineSegment(sketch, "E7693", {"start": v(7.36, -45.35) * mm, "end": v(7.36, -45.36) * mm});
            skLineSegment(sketch, "E7694", {"start": v(7.36, -45.36) * mm, "end": v(7.48, -45.34) * mm});
            skLineSegment(sketch, "E7695", {"start": v(7.48, -45.34) * mm, "end": v(7.6, -45.32) * mm});
            skLineSegment(sketch, "E7696", {"start": v(7.6, -45.32) * mm, "end": v(7.7, -45.3) * mm});
            skLineSegment(sketch, "E7697", {"start": v(7.7, -45.3) * mm, "end": v(7.82, -45.28) * mm});
            skLineSegment(sketch, "E7698", {"start": v(7.82, -45.28) * mm, "end": v(7.92, -45.26) * mm});
            skLineSegment(sketch, "E7699", {"start": v(7.92, -45.26) * mm, "end": v(7.95, -45.15) * mm});
            skLineSegment(sketch, "E7700", {"start": v(7.95, -45.15) * mm, "end": v(7.98, -45.03) * mm});
            skLineSegment(sketch, "E7701", {"start": v(7.98, -45.03) * mm, "end": v(8, -44.91) * mm});
            skLineSegment(sketch, "E7702", {"start": v(8, -44.91) * mm, "end": v(8.03, -44.8) * mm});
            skLineSegment(sketch, "E7703", {"start": v(8.03, -44.8) * mm, "end": v(8.05, -44.68) * mm});
            skLineSegment(sketch, "E7704", {"start": v(8.05, -44.68) * mm, "end": v(8.08, -44.57) * mm});
            skLineSegment(sketch, "E7705", {"start": v(8.08, -44.57) * mm, "end": v(8.1, -44.45) * mm});
            skLineSegment(sketch, "E7706", {"start": v(8.1, -44.45) * mm, "end": v(8.12, -44.33) * mm});
            skLineSegment(sketch, "E7707", {"start": v(8.12, -44.33) * mm, "end": v(8.14, -44.21) * mm});
            skLineSegment(sketch, "E7708", {"start": v(8.14, -44.21) * mm, "end": v(8.17, -44.09) * mm});
            skLineSegment(sketch, "E7709", {"start": v(8.17, -44.09) * mm, "end": v(8.19, -43.97) * mm});
            skLineSegment(sketch, "E7710", {"start": v(8.19, -43.97) * mm, "end": v(8.2, -43.85) * mm});
            skLineSegment(sketch, "E7711", {"start": v(8.2, -43.85) * mm, "end": v(8.22, -43.73) * mm});
            skLineSegment(sketch, "E7712", {"start": v(8.22, -43.73) * mm, "end": v(8.24, -43.62) * mm});
            skLineSegment(sketch, "E7713", {"start": v(8.24, -43.62) * mm, "end": v(8.26, -43.5) * mm});
            skLineSegment(sketch, "E7714", {"start": v(8.26, -43.5) * mm, "end": v(8.27, -43.38) * mm});
            skLineSegment(sketch, "E7715", {"start": v(8.27, -43.38) * mm, "end": v(8.29, -43.26) * mm});
            skLineSegment(sketch, "E7716", {"start": v(8.29, -43.26) * mm, "end": v(8.3, -43.14) * mm});
            skLineSegment(sketch, "E7717", {"start": v(8.3, -43.14) * mm, "end": v(8.31, -43.01) * mm});
            skLineSegment(sketch, "E7718", {"start": v(8.31, -43.01) * mm, "end": v(8.43, -42.99) * mm});
            skLineSegment(sketch, "E7719", {"start": v(8.43, -42.99) * mm, "end": v(8.54, -42.97) * mm});
            skLineSegment(sketch, "E7720", {"start": v(8.54, -42.97) * mm, "end": v(8.66, -42.94) * mm});
            skLineSegment(sketch, "E7721", {"start": v(8.66, -42.94) * mm, "end": v(8.78, -42.92) * mm});
            skLineSegment(sketch, "E7722", {"start": v(8.78, -42.92) * mm, "end": v(8.9, -42.9) * mm});
            skLineSegment(sketch, "E7723", {"start": v(8.9, -42.9) * mm, "end": v(9, -42.87) * mm});
            skLineSegment(sketch, "E7724", {"start": v(9, -42.87) * mm, "end": v(9.12, -42.85) * mm});
            skLineSegment(sketch, "E7725", {"start": v(9.12, -42.85) * mm, "end": v(9.14, -42.85) * mm});
            skLineSegment(sketch, "E7726", {"start": v(9.14, -42.85) * mm, "end": v(9.2, -42.94) * mm});
            skLineSegment(sketch, "E7727", {"start": v(9.2, -42.94) * mm, "end": v(9.25, -43.04) * mm});
            skLineSegment(sketch, "E7728", {"start": v(9.25, -43.04) * mm, "end": v(9.3, -43.14) * mm});
            skLineSegment(sketch, "E7729", {"start": v(9.3, -43.14) * mm, "end": v(9.36, -43.24) * mm});
            skLineSegment(sketch, "E7730", {"start": v(9.36, -43.24) * mm, "end": v(9.42, -43.35) * mm});
            skLineSegment(sketch, "E7731", {"start": v(9.42, -43.35) * mm, "end": v(9.49, -43.45) * mm});
            skLineSegment(sketch, "E7732", {"start": v(9.49, -43.45) * mm, "end": v(9.56, -43.56) * mm});
            skLineSegment(sketch, "E7733", {"start": v(9.56, -43.56) * mm, "end": v(9.63, -43.67) * mm});
            skLineSegment(sketch, "E7734", {"start": v(9.63, -43.67) * mm, "end": v(9.69, -43.77) * mm});
            skLineSegment(sketch, "E7735", {"start": v(9.69, -43.77) * mm, "end": v(9.76, -43.88) * mm});
            skLineSegment(sketch, "E7736", {"start": v(9.76, -43.88) * mm, "end": v(9.82, -43.97) * mm});
            skLineSegment(sketch, "E7737", {"start": v(9.82, -43.97) * mm, "end": v(9.88, -44.07) * mm});
            skLineSegment(sketch, "E7738", {"start": v(9.88, -44.07) * mm, "end": v(9.95, -44.16) * mm});
            skLineSegment(sketch, "E7739", {"start": v(9.95, -44.16) * mm, "end": v(10.01, -44.26) * mm});
            skLineSegment(sketch, "E7740", {"start": v(10.01, -44.26) * mm, "end": v(10.08, -44.36) * mm});
            skLineSegment(sketch, "E7741", {"start": v(10.08, -44.36) * mm, "end": v(10.15, -44.46) * mm});
            skLineSegment(sketch, "E7742", {"start": v(10.15, -44.46) * mm, "end": v(10.23, -44.56) * mm});
            skLineSegment(sketch, "E7743", {"start": v(10.23, -44.56) * mm, "end": v(10.3, -44.66) * mm});
            skLineSegment(sketch, "E7744", {"start": v(10.3, -44.66) * mm, "end": v(10.38, -44.76) * mm});
            skLineSegment(sketch, "E7745", {"start": v(10.38, -44.76) * mm, "end": v(10.38, -44.76) * mm});
            skLineSegment(sketch, "E7746", {"start": v(10.38, -44.76) * mm, "end": v(10.5, -44.74) * mm});
            skLineSegment(sketch, "E7747", {"start": v(10.5, -44.74) * mm, "end": v(10.61, -44.7) * mm});
            skLineSegment(sketch, "E7748", {"start": v(10.61, -44.7) * mm, "end": v(10.72, -44.68) * mm});
            skLineSegment(sketch, "E7749", {"start": v(10.72, -44.68) * mm, "end": v(10.83, -44.65) * mm});
            skLineSegment(sketch, "E7750", {"start": v(10.83, -44.65) * mm, "end": v(10.93, -44.63) * mm});
            skLineSegment(sketch, "E7751", {"start": v(10.93, -44.63) * mm, "end": v(10.95, -44.51) * mm});
            skLineSegment(sketch, "E7752", {"start": v(10.95, -44.51) * mm, "end": v(10.97, -44.4) * mm});
            skLineSegment(sketch, "E7753", {"start": v(10.97, -44.4) * mm, "end": v(10.99, -44.28) * mm});
            skLineSegment(sketch, "E7754", {"start": v(10.99, -44.28) * mm, "end": v(11, -44.16) * mm});
            skLineSegment(sketch, "E7755", {"start": v(11, -44.16) * mm, "end": v(11.02, -44.04) * mm});
            skLineSegment(sketch, "E7756", {"start": v(11.02, -44.04) * mm, "end": v(11.04, -43.93) * mm});
            skLineSegment(sketch, "E7757", {"start": v(11.04, -43.93) * mm, "end": v(11.05, -43.8) * mm});
            skLineSegment(sketch, "E7758", {"start": v(11.05, -43.8) * mm, "end": v(11.07, -43.69) * mm});
            skLineSegment(sketch, "E7759", {"start": v(11.07, -43.69) * mm, "end": v(11.08, -43.57) * mm});
            skLineSegment(sketch, "E7760", {"start": v(11.08, -43.57) * mm, "end": v(11.1, -43.44) * mm});
            skLineSegment(sketch, "E7761", {"start": v(11.1, -43.44) * mm, "end": v(11.1, -43.33) * mm});
            skLineSegment(sketch, "E7762", {"start": v(11.1, -43.33) * mm, "end": v(11.12, -43.2) * mm});
            skLineSegment(sketch, "E7763", {"start": v(11.12, -43.2) * mm, "end": v(11.13, -43.09) * mm});
            skLineSegment(sketch, "E7764", {"start": v(11.13, -43.09) * mm, "end": v(11.14, -42.97) * mm});
            skLineSegment(sketch, "E7765", {"start": v(11.14, -42.97) * mm, "end": v(11.14, -42.85) * mm});
            skLineSegment(sketch, "E7766", {"start": v(11.14, -42.85) * mm, "end": v(11.15, -42.73) * mm});
            skLineSegment(sketch, "E7767", {"start": v(11.15, -42.73) * mm, "end": v(11.16, -42.6) * mm});
            skLineSegment(sketch, "E7768", {"start": v(11.16, -42.6) * mm, "end": v(11.16, -42.5) * mm});
            skLineSegment(sketch, "E7769", {"start": v(11.16, -42.5) * mm, "end": v(11.17, -42.36) * mm});
            skLineSegment(sketch, "E7770", {"start": v(11.17, -42.36) * mm, "end": v(11.28, -42.33) * mm});
            skLineSegment(sketch, "E7771", {"start": v(11.28, -42.33) * mm, "end": v(11.4, -42.3) * mm});
            skLineSegment(sketch, "E7772", {"start": v(11.4, -42.3) * mm, "end": v(11.5, -42.27) * mm});
            skLineSegment(sketch, "E7773", {"start": v(11.5, -42.27) * mm, "end": v(11.62, -42.24) * mm});
            skLineSegment(sketch, "E7774", {"start": v(11.62, -42.24) * mm, "end": v(11.74, -42.2) * mm});
            skLineSegment(sketch, "E7775", {"start": v(11.74, -42.2) * mm, "end": v(11.85, -42.17) * mm});
            skLineSegment(sketch, "E7776", {"start": v(11.85, -42.17) * mm, "end": v(11.97, -42.14) * mm});
            skLineSegment(sketch, "E7777", {"start": v(11.97, -42.14) * mm, "end": v(11.98, -42.14) * mm});
            skLineSegment(sketch, "E7778", {"start": v(11.98, -42.14) * mm, "end": v(12.04, -42.23) * mm});
            skLineSegment(sketch, "E7779", {"start": v(12.04, -42.23) * mm, "end": v(12.1, -42.33) * mm});
            skLineSegment(sketch, "E7780", {"start": v(12.1, -42.33) * mm, "end": v(12.16, -42.42) * mm});
            skLineSegment(sketch, "E7781", {"start": v(12.16, -42.42) * mm, "end": v(12.23, -42.52) * mm});
            skLineSegment(sketch, "E7782", {"start": v(12.23, -42.52) * mm, "end": v(12.3, -42.62) * mm});
            skLineSegment(sketch, "E7783", {"start": v(12.3, -42.62) * mm, "end": v(12.37, -42.72) * mm});
            skLineSegment(sketch, "E7784", {"start": v(12.37, -42.72) * mm, "end": v(12.44, -42.83) * mm});
            skLineSegment(sketch, "E7785", {"start": v(12.44, -42.83) * mm, "end": v(12.52, -42.93) * mm});
            skLineSegment(sketch, "E7786", {"start": v(12.52, -42.93) * mm, "end": v(12.6, -43.03) * mm});
            skLineSegment(sketch, "E7787", {"start": v(12.6, -43.03) * mm, "end": v(12.67, -43.13) * mm});
            skLineSegment(sketch, "E7788", {"start": v(12.67, -43.13) * mm, "end": v(12.73, -43.22) * mm});
            skLineSegment(sketch, "E7789", {"start": v(12.73, -43.22) * mm, "end": v(12.8, -43.3) * mm});
            skLineSegment(sketch, "E7790", {"start": v(12.8, -43.3) * mm, "end": v(12.87, -43.4) * mm});
            skLineSegment(sketch, "E7791", {"start": v(12.87, -43.4) * mm, "end": v(12.95, -43.5) * mm});
            skLineSegment(sketch, "E7792", {"start": v(12.95, -43.5) * mm, "end": v(13.02, -43.58) * mm});
            skLineSegment(sketch, "E7793", {"start": v(13.02, -43.58) * mm, "end": v(13.1, -43.68) * mm});
            skLineSegment(sketch, "E7794", {"start": v(13.1, -43.68) * mm, "end": v(13.18, -43.77) * mm});
            skLineSegment(sketch, "E7795", {"start": v(13.18, -43.77) * mm, "end": v(13.26, -43.87) * mm});
            skLineSegment(sketch, "E7796", {"start": v(13.26, -43.87) * mm, "end": v(13.34, -43.97) * mm});
            skLineSegment(sketch, "E7797", {"start": v(13.34, -43.97) * mm, "end": v(13.34, -43.97) * mm});
            skLineSegment(sketch, "E7798", {"start": v(13.34, -43.97) * mm, "end": v(13.46, -43.93) * mm});
            skLineSegment(sketch, "E7799", {"start": v(13.46, -43.93) * mm, "end": v(13.57, -43.9) * mm});
            skLineSegment(sketch, "E7800", {"start": v(13.57, -43.9) * mm, "end": v(13.68, -43.87) * mm});
            skLineSegment(sketch, "E7801", {"start": v(13.68, -43.87) * mm, "end": v(13.8, -43.83) * mm});
            skLineSegment(sketch, "E7802", {"start": v(13.8, -43.83) * mm, "end": v(13.88, -43.8) * mm});
            skLineSegment(sketch, "E7803", {"start": v(13.88, -43.8) * mm, "end": v(13.9, -43.68) * mm});
            skLineSegment(sketch, "E7804", {"start": v(13.9, -43.68) * mm, "end": v(13.9, -43.56) * mm});
            skLineSegment(sketch, "E7805", {"start": v(13.9, -43.56) * mm, "end": v(13.92, -43.44) * mm});
            skLineSegment(sketch, "E7806", {"start": v(13.92, -43.44) * mm, "end": v(13.93, -43.33) * mm});
            skLineSegment(sketch, "E7807", {"start": v(13.93, -43.33) * mm, "end": v(13.94, -43.21) * mm});
            skLineSegment(sketch, "E7808", {"start": v(13.94, -43.21) * mm, "end": v(13.95, -43.1) * mm});
            skLineSegment(sketch, "E7809", {"start": v(13.95, -43.1) * mm, "end": v(13.95, -42.97) * mm});
            skLineSegment(sketch, "E7810", {"start": v(13.95, -42.97) * mm, "end": v(13.96, -42.85) * mm});
            skLineSegment(sketch, "E7811", {"start": v(13.96, -42.85) * mm, "end": v(13.97, -42.73) * mm});
            skLineSegment(sketch, "E7812", {"start": v(13.97, -42.73) * mm, "end": v(13.97, -42.6) * mm});
            skLineSegment(sketch, "E7813", {"start": v(13.97, -42.6) * mm, "end": v(13.97, -42.49) * mm});
            skLineSegment(sketch, "E7814", {"start": v(13.97, -42.49) * mm, "end": v(13.98, -42.37) * mm});
            skLineSegment(sketch, "E7815", {"start": v(13.98, -42.37) * mm, "end": v(13.98, -42.25) * mm});
            skLineSegment(sketch, "E7816", {"start": v(13.98, -42.25) * mm, "end": v(13.98, -42.13) * mm});
            skLineSegment(sketch, "E7817", {"start": v(13.98, -42.13) * mm, "end": v(13.98, -42) * mm});
            skLineSegment(sketch, "E7818", {"start": v(13.98, -42) * mm, "end": v(13.98, -41.89) * mm});
            skLineSegment(sketch, "E7819", {"start": v(13.98, -41.89) * mm, "end": v(13.98, -41.77) * mm});
            skLineSegment(sketch, "E7820", {"start": v(13.98, -41.77) * mm, "end": v(13.97, -41.65) * mm});
            skLineSegment(sketch, "E7821", {"start": v(13.97, -41.65) * mm, "end": v(13.97, -41.52) * mm});
            skLineSegment(sketch, "E7822", {"start": v(13.97, -41.52) * mm, "end": v(14.08, -41.48) * mm});
            skLineSegment(sketch, "E7823", {"start": v(14.08, -41.48) * mm, "end": v(14.2, -41.44) * mm});
            skLineSegment(sketch, "E7824", {"start": v(14.2, -41.44) * mm, "end": v(14.3, -41.4) * mm});
            skLineSegment(sketch, "E7825", {"start": v(14.3, -41.4) * mm, "end": v(14.42, -41.37) * mm});
            skLineSegment(sketch, "E7826", {"start": v(14.42, -41.37) * mm, "end": v(14.53, -41.33) * mm});
            skLineSegment(sketch, "E7827", {"start": v(14.53, -41.33) * mm, "end": v(14.64, -41.29) * mm});
            skLineSegment(sketch, "E7828", {"start": v(14.64, -41.29) * mm, "end": v(14.75, -41.25) * mm});
            skLineSegment(sketch, "E7829", {"start": v(14.75, -41.25) * mm, "end": v(14.77, -41.25) * mm});
            skLineSegment(sketch, "E7830", {"start": v(14.77, -41.25) * mm, "end": v(14.83, -41.33) * mm});
            skLineSegment(sketch, "E7831", {"start": v(14.83, -41.33) * mm, "end": v(14.9, -41.42) * mm});
            skLineSegment(sketch, "E7832", {"start": v(14.9, -41.42) * mm, "end": v(14.97, -41.51) * mm});
            skLineSegment(sketch, "E7833", {"start": v(14.97, -41.51) * mm, "end": v(15.04, -41.6) * mm});
            skLineSegment(sketch, "E7834", {"start": v(15.04, -41.6) * mm, "end": v(15.12, -41.7) * mm});
            skLineSegment(sketch, "E7835", {"start": v(15.12, -41.7) * mm, "end": v(15.2, -41.8) * mm});
            skLineSegment(sketch, "E7836", {"start": v(15.2, -41.8) * mm, "end": v(15.28, -41.9) * mm});
            skLineSegment(sketch, "E7837", {"start": v(15.28, -41.9) * mm, "end": v(15.36, -42) * mm});
            skLineSegment(sketch, "E7838", {"start": v(15.36, -42) * mm, "end": v(15.44, -42.1) * mm});
            skLineSegment(sketch, "E7839", {"start": v(15.44, -42.1) * mm, "end": v(15.52, -42.19) * mm});
            skLineSegment(sketch, "E7840", {"start": v(15.52, -42.19) * mm, "end": v(15.6, -42.27) * mm});
            skLineSegment(sketch, "E7841", {"start": v(15.6, -42.27) * mm, "end": v(15.67, -42.36) * mm});
            skLineSegment(sketch, "E7842", {"start": v(15.67, -42.36) * mm, "end": v(15.74, -42.44) * mm});
            skLineSegment(sketch, "E7843", {"start": v(15.74, -42.44) * mm, "end": v(15.82, -42.53) * mm});
            skLineSegment(sketch, "E7844", {"start": v(15.82, -42.53) * mm, "end": v(15.9, -42.62) * mm});
            skLineSegment(sketch, "E7845", {"start": v(15.9, -42.62) * mm, "end": v(15.99, -42.7) * mm});
            skLineSegment(sketch, "E7846", {"start": v(15.99, -42.7) * mm, "end": v(16.07, -42.8) * mm});
            skLineSegment(sketch, "E7847", {"start": v(16.07, -42.8) * mm, "end": v(16.16, -42.89) * mm});
            skLineSegment(sketch, "E7848", {"start": v(16.16, -42.89) * mm, "end": v(16.25, -42.98) * mm});
            skLineSegment(sketch, "E7849", {"start": v(16.25, -42.98) * mm, "end": v(16.25, -42.98) * mm});
            skLineSegment(sketch, "E7850", {"start": v(16.25, -42.98) * mm, "end": v(16.36, -42.94) * mm});
            skLineSegment(sketch, "E7851", {"start": v(16.36, -42.94) * mm, "end": v(16.48, -42.9) * mm});
            skLineSegment(sketch, "E7852", {"start": v(16.48, -42.9) * mm, "end": v(16.58, -42.86) * mm});
            skLineSegment(sketch, "E7853", {"start": v(16.58, -42.86) * mm, "end": v(16.69, -42.81) * mm});
            skLineSegment(sketch, "E7854", {"start": v(16.69, -42.81) * mm, "end": v(16.78, -42.78) * mm});
            skLineSegment(sketch, "E7855", {"start": v(16.78, -42.78) * mm, "end": v(16.78, -42.66) * mm});
            skLineSegment(sketch, "E7856", {"start": v(16.78, -42.66) * mm, "end": v(16.79, -42.54) * mm});
            skLineSegment(sketch, "E7857", {"start": v(16.79, -42.54) * mm, "end": v(16.79, -42.42) * mm});
            skLineSegment(sketch, "E7858", {"start": v(16.79, -42.42) * mm, "end": v(16.8, -42.3) * mm});
            skLineSegment(sketch, "E7859", {"start": v(16.8, -42.3) * mm, "end": v(16.8, -42.18) * mm});
            skLineSegment(sketch, "E7860", {"start": v(16.8, -42.18) * mm, "end": v(16.8, -42.06) * mm});
            skLineSegment(sketch, "E7861", {"start": v(16.8, -42.06) * mm, "end": v(16.8, -41.94) * mm});
            skLineSegment(sketch, "E7862", {"start": v(16.8, -41.94) * mm, "end": v(16.8, -41.82) * mm});
            skLineSegment(sketch, "E7863", {"start": v(16.8, -41.82) * mm, "end": v(16.79, -41.7) * mm});
            skLineSegment(sketch, "E7864", {"start": v(16.79, -41.7) * mm, "end": v(16.79, -41.58) * mm});
            skLineSegment(sketch, "E7865", {"start": v(16.79, -41.58) * mm, "end": v(16.78, -41.46) * mm});
            skLineSegment(sketch, "E7866", {"start": v(16.78, -41.46) * mm, "end": v(16.78, -41.34) * mm});
            skLineSegment(sketch, "E7867", {"start": v(16.78, -41.34) * mm, "end": v(16.77, -41.22) * mm});
            skLineSegment(sketch, "E7868", {"start": v(16.77, -41.22) * mm, "end": v(16.76, -41.1) * mm});
            skLineSegment(sketch, "E7869", {"start": v(16.76, -41.1) * mm, "end": v(16.76, -40.98) * mm});
            skLineSegment(sketch, "E7870", {"start": v(16.76, -40.98) * mm, "end": v(16.75, -40.86) * mm});
            skLineSegment(sketch, "E7871", {"start": v(16.75, -40.86) * mm, "end": v(16.74, -40.74) * mm});
            skLineSegment(sketch, "E7872", {"start": v(16.74, -40.74) * mm, "end": v(16.73, -40.62) * mm});
            skLineSegment(sketch, "E7873", {"start": v(16.73, -40.62) * mm, "end": v(16.71, -40.5) * mm});
            skLineSegment(sketch, "E7874", {"start": v(16.71, -40.5) * mm, "end": v(16.82, -40.45) * mm});
            skLineSegment(sketch, "E7875", {"start": v(16.82, -40.45) * mm, "end": v(16.93, -40.4) * mm});
            skLineSegment(sketch, "E7876", {"start": v(16.93, -40.4) * mm, "end": v(17.04, -40.36) * mm});
            skLineSegment(sketch, "E7877", {"start": v(17.04, -40.36) * mm, "end": v(17.15, -40.31) * mm});
            skLineSegment(sketch, "E7878", {"start": v(17.15, -40.31) * mm, "end": v(17.26, -40.26) * mm});
            skLineSegment(sketch, "E7879", {"start": v(17.26, -40.26) * mm, "end": v(17.37, -40.22) * mm});
            skLineSegment(sketch, "E7880", {"start": v(17.37, -40.22) * mm, "end": v(17.48, -40.17) * mm});
            skLineSegment(sketch, "E7881", {"start": v(17.48, -40.17) * mm, "end": v(17.5, -40.17) * mm});
            skLineSegment(sketch, "E7882", {"start": v(17.5, -40.17) * mm, "end": v(17.56, -40.25) * mm});
            skLineSegment(sketch, "E7883", {"start": v(17.56, -40.25) * mm, "end": v(17.63, -40.33) * mm});
            skLineSegment(sketch, "E7884", {"start": v(17.63, -40.33) * mm, "end": v(17.71, -40.42) * mm});
            skLineSegment(sketch, "E7885", {"start": v(17.71, -40.42) * mm, "end": v(17.79, -40.5) * mm});
            skLineSegment(sketch, "E7886", {"start": v(17.79, -40.5) * mm, "end": v(17.87, -40.6) * mm});
            skLineSegment(sketch, "E7887", {"start": v(17.87, -40.6) * mm, "end": v(17.95, -40.7) * mm});
            skLineSegment(sketch, "E7888", {"start": v(17.95, -40.7) * mm, "end": v(18.04, -40.79) * mm});
            skLineSegment(sketch, "E7889", {"start": v(18.04, -40.79) * mm, "end": v(18.13, -40.88) * mm});
            skLineSegment(sketch, "E7890", {"start": v(18.13, -40.88) * mm, "end": v(18.21, -40.97) * mm});
            skLineSegment(sketch, "E7891", {"start": v(18.21, -40.97) * mm, "end": v(18.3, -41.05) * mm});
            skLineSegment(sketch, "E7892", {"start": v(18.3, -41.05) * mm, "end": v(18.38, -41.13) * mm});
            skLineSegment(sketch, "E7893", {"start": v(18.38, -41.13) * mm, "end": v(18.46, -41.21) * mm});
            skLineSegment(sketch, "E7894", {"start": v(18.46, -41.21) * mm, "end": v(18.54, -41.3) * mm});
            skLineSegment(sketch, "E7895", {"start": v(18.54, -41.3) * mm, "end": v(18.63, -41.38) * mm});
            skLineSegment(sketch, "E7896", {"start": v(18.63, -41.38) * mm, "end": v(18.72, -41.46) * mm});
            skLineSegment(sketch, "E7897", {"start": v(18.72, -41.46) * mm, "end": v(18.8, -41.54) * mm});
            skLineSegment(sketch, "E7898", {"start": v(18.8, -41.54) * mm, "end": v(18.9, -41.63) * mm});
            skLineSegment(sketch, "E7899", {"start": v(18.9, -41.63) * mm, "end": v(18.99, -41.71) * mm});
            skLineSegment(sketch, "E7900", {"start": v(18.99, -41.71) * mm, "end": v(19.09, -41.8) * mm});
            skLineSegment(sketch, "E7901", {"start": v(19.09, -41.8) * mm, "end": v(19.09, -41.8) * mm});
            skLineSegment(sketch, "E7902", {"start": v(19.09, -41.8) * mm, "end": v(19.2, -41.75) * mm});
            skLineSegment(sketch, "E7903", {"start": v(19.2, -41.75) * mm, "end": v(19.3, -41.7) * mm});
            skLineSegment(sketch, "E7904", {"start": v(19.3, -41.7) * mm, "end": v(19.4, -41.65) * mm});
            skLineSegment(sketch, "E7905", {"start": v(19.4, -41.65) * mm, "end": v(19.5, -41.6) * mm});
            skLineSegment(sketch, "E7906", {"start": v(19.5, -41.6) * mm, "end": v(19.6, -41.56) * mm});
            skLineSegment(sketch, "E7907", {"start": v(19.6, -41.56) * mm, "end": v(19.6, -41.44) * mm});
            skLineSegment(sketch, "E7908", {"start": v(19.6, -41.44) * mm, "end": v(19.6, -41.32) * mm});
            skLineSegment(sketch, "E7909", {"start": v(19.6, -41.32) * mm, "end": v(19.58, -41.2) * mm});
            skLineSegment(sketch, "E7910", {"start": v(19.58, -41.2) * mm, "end": v(19.58, -41.09) * mm});
            skLineSegment(sketch, "E7911", {"start": v(19.58, -41.09) * mm, "end": v(19.57, -40.97) * mm});
            skLineSegment(sketch, "E7912", {"start": v(19.57, -40.97) * mm, "end": v(19.56, -40.85) * mm});
            skLineSegment(sketch, "E7913", {"start": v(19.56, -40.85) * mm, "end": v(19.56, -40.73) * mm});
            skLineSegment(sketch, "E7914", {"start": v(19.56, -40.73) * mm, "end": v(19.55, -40.6) * mm});
            skLineSegment(sketch, "E7915", {"start": v(19.55, -40.6) * mm, "end": v(19.54, -40.49) * mm});
            skLineSegment(sketch, "E7916", {"start": v(19.54, -40.49) * mm, "end": v(19.53, -40.36) * mm});
            skLineSegment(sketch, "E7917", {"start": v(19.53, -40.36) * mm, "end": v(19.51, -40.25) * mm});
            skLineSegment(sketch, "E7918", {"start": v(19.51, -40.25) * mm, "end": v(19.5, -40.13) * mm});
            skLineSegment(sketch, "E7919", {"start": v(19.5, -40.13) * mm, "end": v(19.49, -40) * mm});
            skLineSegment(sketch, "E7920", {"start": v(19.49, -40) * mm, "end": v(19.47, -39.89) * mm});
            skLineSegment(sketch, "E7921", {"start": v(19.47, -39.89) * mm, "end": v(19.46, -39.77) * mm});
            skLineSegment(sketch, "E7922", {"start": v(19.46, -39.77) * mm, "end": v(19.44, -39.65) * mm});
            skLineSegment(sketch, "E7923", {"start": v(19.44, -39.65) * mm, "end": v(19.42, -39.53) * mm});
            skLineSegment(sketch, "E7924", {"start": v(19.42, -39.53) * mm, "end": v(19.4, -39.42) * mm});
            skLineSegment(sketch, "E7925", {"start": v(19.4, -39.42) * mm, "end": v(19.38, -39.29) * mm});
            skLineSegment(sketch, "E7926", {"start": v(19.38, -39.29) * mm, "end": v(19.49, -39.23) * mm});
            skLineSegment(sketch, "E7927", {"start": v(19.49, -39.23) * mm, "end": v(19.6, -39.18) * mm});
            skLineSegment(sketch, "E7928", {"start": v(19.6, -39.18) * mm, "end": v(19.7, -39.13) * mm});
            skLineSegment(sketch, "E7929", {"start": v(19.7, -39.13) * mm, "end": v(19.8, -39.08) * mm});
            skLineSegment(sketch, "E7930", {"start": v(19.8, -39.08) * mm, "end": v(19.9, -39.02) * mm});
            skLineSegment(sketch, "E7931", {"start": v(19.9, -39.02) * mm, "end": v(20.01, -38.97) * mm});
            skLineSegment(sketch, "E7932", {"start": v(20.01, -38.97) * mm, "end": v(20.12, -38.92) * mm});
            skLineSegment(sketch, "E7933", {"start": v(20.12, -38.92) * mm, "end": v(20.14, -38.9) * mm});
            skLineSegment(sketch, "E7934", {"start": v(20.14, -38.9) * mm, "end": v(20.21, -38.99) * mm});
            skLineSegment(sketch, "E7935", {"start": v(20.21, -38.99) * mm, "end": v(20.29, -39.07) * mm});
            skLineSegment(sketch, "E7936", {"start": v(20.29, -39.07) * mm, "end": v(20.37, -39.15) * mm});
            skLineSegment(sketch, "E7937", {"start": v(20.37, -39.15) * mm, "end": v(20.46, -39.23) * mm});
            skLineSegment(sketch, "E7938", {"start": v(20.46, -39.23) * mm, "end": v(20.54, -39.32) * mm});
            skLineSegment(sketch, "E7939", {"start": v(20.54, -39.32) * mm, "end": v(20.63, -39.4) * mm});
            skLineSegment(sketch, "E7940", {"start": v(20.63, -39.4) * mm, "end": v(20.73, -39.49) * mm});
            skLineSegment(sketch, "E7941", {"start": v(20.73, -39.49) * mm, "end": v(20.82, -39.58) * mm});
            skLineSegment(sketch, "E7942", {"start": v(20.82, -39.58) * mm, "end": v(20.91, -39.66) * mm});
            skLineSegment(sketch, "E7943", {"start": v(20.91, -39.66) * mm, "end": v(21, -39.74) * mm});
            skLineSegment(sketch, "E7944", {"start": v(21, -39.74) * mm, "end": v(21.09, -39.81) * mm});
            skLineSegment(sketch, "E7945", {"start": v(21.09, -39.81) * mm, "end": v(21.17, -39.89) * mm});
            skLineSegment(sketch, "E7946", {"start": v(21.17, -39.89) * mm, "end": v(21.26, -39.96) * mm});
            skLineSegment(sketch, "E7947", {"start": v(21.26, -39.96) * mm, "end": v(21.35, -40.04) * mm});
            skLineSegment(sketch, "E7948", {"start": v(21.35, -40.04) * mm, "end": v(21.44, -40.12) * mm});
            skLineSegment(sketch, "E7949", {"start": v(21.44, -40.12) * mm, "end": v(21.54, -40.2) * mm});
            skLineSegment(sketch, "E7950", {"start": v(21.54, -40.2) * mm, "end": v(21.63, -40.27) * mm});
            skLineSegment(sketch, "E7951", {"start": v(21.63, -40.27) * mm, "end": v(21.73, -40.35) * mm});
            skLineSegment(sketch, "E7952", {"start": v(21.73, -40.35) * mm, "end": v(21.83, -40.43) * mm});
            skLineSegment(sketch, "E7953", {"start": v(21.83, -40.43) * mm, "end": v(21.84, -40.43) * mm});
            skLineSegment(sketch, "E7954", {"start": v(21.84, -40.43) * mm, "end": v(21.94, -40.37) * mm});
            skLineSegment(sketch, "E7955", {"start": v(21.94, -40.37) * mm, "end": v(22.05, -40.32) * mm});
            skLineSegment(sketch, "E7956", {"start": v(22.05, -40.32) * mm, "end": v(22.14, -40.26) * mm});
            skLineSegment(sketch, "E7957", {"start": v(22.14, -40.26) * mm, "end": v(22.25, -40.2) * mm});
            skLineSegment(sketch, "E7958", {"start": v(22.25, -40.2) * mm, "end": v(22.33, -40.16) * mm});
            skLineSegment(sketch, "E7959", {"start": v(22.33, -40.16) * mm, "end": v(22.32, -40.04) * mm});
            skLineSegment(sketch, "E7960", {"start": v(22.32, -40.04) * mm, "end": v(22.3, -39.92) * mm});
            skLineSegment(sketch, "E7961", {"start": v(22.3, -39.92) * mm, "end": v(22.3, -39.8) * mm});
            skLineSegment(sketch, "E7962", {"start": v(22.3, -39.8) * mm, "end": v(22.28, -39.69) * mm});
            skLineSegment(sketch, "E7963", {"start": v(22.28, -39.69) * mm, "end": v(22.27, -39.57) * mm});
            skLineSegment(sketch, "E7964", {"start": v(22.27, -39.57) * mm, "end": v(22.25, -39.45) * mm});
            skLineSegment(sketch, "E7965", {"start": v(22.25, -39.45) * mm, "end": v(22.23, -39.33) * mm});
            skLineSegment(sketch, "E7966", {"start": v(22.23, -39.33) * mm, "end": v(22.22, -39.21) * mm});
            skLineSegment(sketch, "E7967", {"start": v(22.22, -39.21) * mm, "end": v(22.2, -39.1) * mm});
            skLineSegment(sketch, "E7968", {"start": v(22.2, -39.1) * mm, "end": v(22.18, -38.97) * mm});
            skLineSegment(sketch, "E7969", {"start": v(22.18, -38.97) * mm, "end": v(22.16, -38.85) * mm});
            skLineSegment(sketch, "E7970", {"start": v(22.16, -38.85) * mm, "end": v(22.14, -38.73) * mm});
            skLineSegment(sketch, "E7971", {"start": v(22.14, -38.73) * mm, "end": v(22.12, -38.62) * mm});
            skLineSegment(sketch, "E7972", {"start": v(22.12, -38.62) * mm, "end": v(22.1, -38.5) * mm});
            skLineSegment(sketch, "E7973", {"start": v(22.1, -38.5) * mm, "end": v(22.07, -38.38) * mm});
            skLineSegment(sketch, "E7974", {"start": v(22.07, -38.38) * mm, "end": v(22.04, -38.26) * mm});
            skLineSegment(sketch, "E7975", {"start": v(22.04, -38.26) * mm, "end": v(22.02, -38.15) * mm});
            skLineSegment(sketch, "E7976", {"start": v(22.02, -38.15) * mm, "end": v(22, -38.03) * mm});
            skLineSegment(sketch, "E7977", {"start": v(22, -38.03) * mm, "end": v(21.96, -37.9) * mm});
            skLineSegment(sketch, "E7978", {"start": v(21.96, -37.9) * mm, "end": v(22.06, -37.84) * mm});
            skLineSegment(sketch, "E7979", {"start": v(22.06, -37.84) * mm, "end": v(22.17, -37.79) * mm});
            skLineSegment(sketch, "E7980", {"start": v(22.17, -37.79) * mm, "end": v(22.27, -37.72) * mm});
            skLineSegment(sketch, "E7981", {"start": v(22.27, -37.72) * mm, "end": v(22.37, -37.67) * mm});
            skLineSegment(sketch, "E7982", {"start": v(22.37, -37.67) * mm, "end": v(22.47, -37.6) * mm});
            skLineSegment(sketch, "E7983", {"start": v(22.47, -37.6) * mm, "end": v(22.57, -37.54) * mm});
            skLineSegment(sketch, "E7984", {"start": v(22.57, -37.54) * mm, "end": v(22.68, -37.48) * mm});
            skLineSegment(sketch, "E7985", {"start": v(22.68, -37.48) * mm, "end": v(22.7, -37.48) * mm});
            skLineSegment(sketch, "E7986", {"start": v(22.7, -37.48) * mm, "end": v(22.77, -37.55) * mm});
            skLineSegment(sketch, "E7987", {"start": v(22.77, -37.55) * mm, "end": v(22.85, -37.62) * mm});
            skLineSegment(sketch, "E7988", {"start": v(22.85, -37.62) * mm, "end": v(22.94, -37.7) * mm});
            skLineSegment(sketch, "E7989", {"start": v(22.94, -37.7) * mm, "end": v(23.03, -37.78) * mm});
            skLineSegment(sketch, "E7990", {"start": v(23.03, -37.78) * mm, "end": v(23.12, -37.86) * mm});
            skLineSegment(sketch, "E7991", {"start": v(23.12, -37.86) * mm, "end": v(23.22, -37.94) * mm});
            skLineSegment(sketch, "E7992", {"start": v(23.22, -37.94) * mm, "end": v(23.32, -38.02) * mm});
            skLineSegment(sketch, "E7993", {"start": v(23.32, -38.02) * mm, "end": v(23.42, -38.1) * mm});
            skLineSegment(sketch, "E7994", {"start": v(23.42, -38.1) * mm, "end": v(23.51, -38.17) * mm});
            skLineSegment(sketch, "E7995", {"start": v(23.51, -38.17) * mm, "end": v(23.61, -38.25) * mm});
            skLineSegment(sketch, "E7996", {"start": v(23.61, -38.25) * mm, "end": v(23.7, -38.32) * mm});
            skLineSegment(sketch, "E7997", {"start": v(23.7, -38.32) * mm, "end": v(23.8, -38.39) * mm});
            skLineSegment(sketch, "E7998", {"start": v(23.8, -38.39) * mm, "end": v(23.88, -38.45) * mm});
            skLineSegment(sketch, "E7999", {"start": v(23.88, -38.45) * mm, "end": v(23.98, -38.52) * mm});
            skLineSegment(sketch, "E8000", {"start": v(23.98, -38.52) * mm, "end": v(24.08, -38.6) * mm});
            skLineSegment(sketch, "E8001", {"start": v(24.08, -38.6) * mm, "end": v(24.18, -38.67) * mm});
            skLineSegment(sketch, "E8002", {"start": v(24.18, -38.67) * mm, "end": v(24.28, -38.74) * mm});
            skLineSegment(sketch, "E8003", {"start": v(24.28, -38.74) * mm, "end": v(24.38, -38.8) * mm});
            skLineSegment(sketch, "E8004", {"start": v(24.38, -38.8) * mm, "end": v(24.49, -38.88) * mm});
            skLineSegment(sketch, "E8005", {"start": v(24.49, -38.88) * mm, "end": v(24.49, -38.88) * mm});
            skLineSegment(sketch, "E8006", {"start": v(24.49, -38.88) * mm, "end": v(24.59, -38.82) * mm});
            skLineSegment(sketch, "E8007", {"start": v(24.59, -38.82) * mm, "end": v(24.69, -38.75) * mm});
            skLineSegment(sketch, "E8008", {"start": v(24.69, -38.75) * mm, "end": v(24.78, -38.7) * mm});
            skLineSegment(sketch, "E8009", {"start": v(24.78, -38.7) * mm, "end": v(24.88, -38.63) * mm});
            skLineSegment(sketch, "E8010", {"start": v(24.88, -38.63) * mm, "end": v(24.96, -38.58) * mm});
            skLineSegment(sketch, "E8011", {"start": v(24.96, -38.58) * mm, "end": v(24.94, -38.46) * mm});
            skLineSegment(sketch, "E8012", {"start": v(24.94, -38.46) * mm, "end": v(24.92, -38.34) * mm});
            skLineSegment(sketch, "E8013", {"start": v(24.92, -38.34) * mm, "end": v(24.9, -38.22) * mm});
            skLineSegment(sketch, "E8014", {"start": v(24.9, -38.22) * mm, "end": v(24.88, -38.1) * mm});
            skLineSegment(sketch, "E8015", {"start": v(24.88, -38.1) * mm, "end": v(24.86, -38) * mm});
            skLineSegment(sketch, "E8016", {"start": v(24.86, -38) * mm, "end": v(24.84, -37.88) * mm});
            skLineSegment(sketch, "E8017", {"start": v(24.84, -37.88) * mm, "end": v(24.81, -37.76) * mm});
            skLineSegment(sketch, "E8018", {"start": v(24.81, -37.76) * mm, "end": v(24.79, -37.64) * mm});
            skLineSegment(sketch, "E8019", {"start": v(24.79, -37.64) * mm, "end": v(24.76, -37.52) * mm});
            skLineSegment(sketch, "E8020", {"start": v(24.76, -37.52) * mm, "end": v(24.73, -37.4) * mm});
            skLineSegment(sketch, "E8021", {"start": v(24.73, -37.4) * mm, "end": v(24.7, -37.28) * mm});
            skLineSegment(sketch, "E8022", {"start": v(24.7, -37.28) * mm, "end": v(24.68, -37.17) * mm});
            skLineSegment(sketch, "E8023", {"start": v(24.68, -37.17) * mm, "end": v(24.65, -37.05) * mm});
            skLineSegment(sketch, "E8024", {"start": v(24.65, -37.05) * mm, "end": v(24.62, -36.94) * mm});
            skLineSegment(sketch, "E8025", {"start": v(24.62, -36.94) * mm, "end": v(24.58, -36.82) * mm});
            skLineSegment(sketch, "E8026", {"start": v(24.58, -36.82) * mm, "end": v(24.55, -36.7) * mm});
            skLineSegment(sketch, "E8027", {"start": v(24.55, -36.7) * mm, "end": v(24.52, -36.6) * mm});
            skLineSegment(sketch, "E8028", {"start": v(24.52, -36.6) * mm, "end": v(24.48, -36.48) * mm});
            skLineSegment(sketch, "E8029", {"start": v(24.48, -36.48) * mm, "end": v(24.44, -36.35) * mm});
            skLineSegment(sketch, "E8030", {"start": v(24.44, -36.35) * mm, "end": v(24.54, -36.29) * mm});
            skLineSegment(sketch, "E8031", {"start": v(24.54, -36.29) * mm, "end": v(24.64, -36.22) * mm});
            skLineSegment(sketch, "E8032", {"start": v(24.64, -36.22) * mm, "end": v(24.74, -36.15) * mm});
            skLineSegment(sketch, "E8033", {"start": v(24.74, -36.15) * mm, "end": v(24.84, -36.09) * mm});
            skLineSegment(sketch, "E8034", {"start": v(24.84, -36.09) * mm, "end": v(24.93, -36.02) * mm});
            skLineSegment(sketch, "E8035", {"start": v(24.93, -36.02) * mm, "end": v(25.03, -35.95) * mm});
            skLineSegment(sketch, "E8036", {"start": v(25.03, -35.95) * mm, "end": v(25.13, -35.89) * mm});
            skLineSegment(sketch, "E8037", {"start": v(25.13, -35.89) * mm, "end": v(25.14, -35.88) * mm});
            skLineSegment(sketch, "E8038", {"start": v(25.14, -35.88) * mm, "end": v(25.23, -35.94) * mm});
            skLineSegment(sketch, "E8039", {"start": v(25.23, -35.94) * mm, "end": v(25.32, -36.01) * mm});
            skLineSegment(sketch, "E8040", {"start": v(25.32, -36.01) * mm, "end": v(25.4, -36.08) * mm});
            skLineSegment(sketch, "E8041", {"start": v(25.4, -36.08) * mm, "end": v(25.5, -36.15) * mm});
            skLineSegment(sketch, "E8042", {"start": v(25.5, -36.15) * mm, "end": v(25.6, -36.23) * mm});
            skLineSegment(sketch, "E8043", {"start": v(25.6, -36.23) * mm, "end": v(25.7, -36.3) * mm});
            skLineSegment(sketch, "E8044", {"start": v(25.7, -36.3) * mm, "end": v(25.8, -36.37) * mm});
            skLineSegment(sketch, "E8045", {"start": v(25.8, -36.37) * mm, "end": v(25.91, -36.45) * mm});
            skLineSegment(sketch, "E8046", {"start": v(25.91, -36.45) * mm, "end": v(26.01, -36.52) * mm});
            skLineSegment(sketch, "E8047", {"start": v(26.01, -36.52) * mm, "end": v(26.11, -36.59) * mm});
            skLineSegment(sketch, "E8048", {"start": v(26.11, -36.59) * mm, "end": v(26.2, -36.65) * mm});
            skLineSegment(sketch, "E8049", {"start": v(26.2, -36.65) * mm, "end": v(26.3, -36.71) * mm});
            skLineSegment(sketch, "E8050", {"start": v(26.3, -36.71) * mm, "end": v(26.4, -36.77) * mm});
            skLineSegment(sketch, "E8051", {"start": v(26.4, -36.77) * mm, "end": v(26.5, -36.84) * mm});
            skLineSegment(sketch, "E8052", {"start": v(26.5, -36.84) * mm, "end": v(26.6, -36.9) * mm});
            skLineSegment(sketch, "E8053", {"start": v(26.6, -36.9) * mm, "end": v(26.7, -36.96) * mm});
            skLineSegment(sketch, "E8054", {"start": v(26.7, -36.96) * mm, "end": v(26.81, -37.03) * mm});
            skLineSegment(sketch, "E8055", {"start": v(26.81, -37.03) * mm, "end": v(26.92, -37.1) * mm});
            skLineSegment(sketch, "E8056", {"start": v(26.92, -37.1) * mm, "end": v(27.03, -37.16) * mm});
            skLineSegment(sketch, "E8057", {"start": v(27.03, -37.16) * mm, "end": v(27.03, -37.16) * mm});
            skLineSegment(sketch, "E8058", {"start": v(27.03, -37.16) * mm, "end": v(27.13, -37.09) * mm});
            skLineSegment(sketch, "E8059", {"start": v(27.13, -37.09) * mm, "end": v(27.22, -37.02) * mm});
            skLineSegment(sketch, "E8060", {"start": v(27.22, -37.02) * mm, "end": v(27.3, -36.95) * mm});
            skLineSegment(sketch, "E8061", {"start": v(27.3, -36.95) * mm, "end": v(27.4, -36.88) * mm});
            skLineSegment(sketch, "E8062", {"start": v(27.4, -36.88) * mm, "end": v(27.48, -36.82) * mm});
            skLineSegment(sketch, "E8063", {"start": v(27.48, -36.82) * mm, "end": v(27.46, -36.7) * mm});
            skLineSegment(sketch, "E8064", {"start": v(27.46, -36.7) * mm, "end": v(27.43, -36.59) * mm});
            skLineSegment(sketch, "E8065", {"start": v(27.43, -36.59) * mm, "end": v(27.4, -36.47) * mm});
            skLineSegment(sketch, "E8066", {"start": v(27.4, -36.47) * mm, "end": v(27.37, -36.36) * mm});
            skLineSegment(sketch, "E8067", {"start": v(27.37, -36.36) * mm, "end": v(27.34, -36.25) * mm});
            skLineSegment(sketch, "E8068", {"start": v(27.34, -36.25) * mm, "end": v(27.3, -36.13) * mm});
            skLineSegment(sketch, "E8069", {"start": v(27.3, -36.13) * mm, "end": v(27.28, -36.02) * mm});
            skLineSegment(sketch, "E8070", {"start": v(27.28, -36.02) * mm, "end": v(27.24, -35.9) * mm});
            skLineSegment(sketch, "E8071", {"start": v(27.24, -35.9) * mm, "end": v(27.21, -35.79) * mm});
            skLineSegment(sketch, "E8072", {"start": v(27.21, -35.79) * mm, "end": v(27.17, -35.67) * mm});
            skLineSegment(sketch, "E8073", {"start": v(27.17, -35.67) * mm, "end": v(27.14, -35.55) * mm});
            skLineSegment(sketch, "E8074", {"start": v(27.14, -35.55) * mm, "end": v(27.1, -35.44) * mm});
            skLineSegment(sketch, "E8075", {"start": v(27.1, -35.44) * mm, "end": v(27.07, -35.32) * mm});
            skLineSegment(sketch, "E8076", {"start": v(27.07, -35.32) * mm, "end": v(27.03, -35.21) * mm});
            skLineSegment(sketch, "E8077", {"start": v(27.03, -35.21) * mm, "end": v(26.99, -35.1) * mm});
            skLineSegment(sketch, "E8078", {"start": v(26.99, -35.1) * mm, "end": v(26.95, -34.99) * mm});
            skLineSegment(sketch, "E8079", {"start": v(26.95, -34.99) * mm, "end": v(26.9, -34.87) * mm});
            skLineSegment(sketch, "E8080", {"start": v(26.9, -34.87) * mm, "end": v(26.86, -34.76) * mm});
            skLineSegment(sketch, "E8081", {"start": v(26.86, -34.76) * mm, "end": v(26.82, -34.64) * mm});
            skLineSegment(sketch, "E8082", {"start": v(26.82, -34.64) * mm, "end": v(26.91, -34.57) * mm});
            skLineSegment(sketch, "E8083", {"start": v(26.91, -34.57) * mm, "end": v(27, -34.5) * mm});
            skLineSegment(sketch, "E8084", {"start": v(27, -34.5) * mm, "end": v(27.1, -34.42) * mm});
            skLineSegment(sketch, "E8085", {"start": v(27.1, -34.42) * mm, "end": v(27.2, -34.35) * mm});
            skLineSegment(sketch, "E8086", {"start": v(27.2, -34.35) * mm, "end": v(27.28, -34.27) * mm});
            skLineSegment(sketch, "E8087", {"start": v(27.28, -34.27) * mm, "end": v(27.38, -34.2) * mm});
            skLineSegment(sketch, "E8088", {"start": v(27.38, -34.2) * mm, "end": v(27.47, -34.13) * mm});
            skLineSegment(sketch, "E8089", {"start": v(27.47, -34.13) * mm, "end": v(27.48, -34.12) * mm});
            skLineSegment(sketch, "E8090", {"start": v(27.48, -34.12) * mm, "end": v(27.57, -34.18) * mm});
            skLineSegment(sketch, "E8091", {"start": v(27.57, -34.18) * mm, "end": v(27.67, -34.24) * mm});
            skLineSegment(sketch, "E8092", {"start": v(27.67, -34.24) * mm, "end": v(27.76, -34.3) * mm});
            skLineSegment(sketch, "E8093", {"start": v(27.76, -34.3) * mm, "end": v(27.86, -34.37) * mm});
            skLineSegment(sketch, "E8094", {"start": v(27.86, -34.37) * mm, "end": v(27.96, -34.44) * mm});
            skLineSegment(sketch, "E8095", {"start": v(27.96, -34.44) * mm, "end": v(28.07, -34.5) * mm});
            skLineSegment(sketch, "E8096", {"start": v(28.07, -34.5) * mm, "end": v(28.18, -34.57) * mm});
            skLineSegment(sketch, "E8097", {"start": v(28.18, -34.57) * mm, "end": v(28.29, -34.64) * mm});
            skLineSegment(sketch, "E8098", {"start": v(28.29, -34.64) * mm, "end": v(28.4, -34.7) * mm});
            skLineSegment(sketch, "E8099", {"start": v(28.4, -34.7) * mm, "end": v(28.5, -34.76) * mm});
            skLineSegment(sketch, "E8100", {"start": v(28.5, -34.76) * mm, "end": v(28.6, -34.82) * mm});
            skLineSegment(sketch, "E8101", {"start": v(28.6, -34.82) * mm, "end": v(28.7, -34.87) * mm});
            skLineSegment(sketch, "E8102", {"start": v(28.7, -34.87) * mm, "end": v(28.8, -34.93) * mm});
            skLineSegment(sketch, "E8103", {"start": v(28.8, -34.93) * mm, "end": v(28.9, -34.98) * mm});
            skLineSegment(sketch, "E8104", {"start": v(28.9, -34.98) * mm, "end": v(29, -35.04) * mm});
            skLineSegment(sketch, "E8105", {"start": v(29, -35.04) * mm, "end": v(29.11, -35.1) * mm});
            skLineSegment(sketch, "E8106", {"start": v(29.11, -35.1) * mm, "end": v(29.22, -35.16) * mm});
            skLineSegment(sketch, "E8107", {"start": v(29.22, -35.16) * mm, "end": v(29.34, -35.21) * mm});
            skLineSegment(sketch, "E8108", {"start": v(29.34, -35.21) * mm, "end": v(29.45, -35.27) * mm});
            skLineSegment(sketch, "E8109", {"start": v(29.45, -35.27) * mm, "end": v(29.45, -35.27) * mm});
            skLineSegment(sketch, "E8110", {"start": v(29.45, -35.27) * mm, "end": v(29.54, -35.2) * mm});
            skLineSegment(sketch, "E8111", {"start": v(29.54, -35.2) * mm, "end": v(29.64, -35.12) * mm});
            skLineSegment(sketch, "E8112", {"start": v(29.64, -35.12) * mm, "end": v(29.72, -35.05) * mm});
            skLineSegment(sketch, "E8113", {"start": v(29.72, -35.05) * mm, "end": v(29.8, -34.97) * mm});
            skLineSegment(sketch, "E8114", {"start": v(29.8, -34.97) * mm, "end": v(29.88, -34.9) * mm});
            skLineSegment(sketch, "E8115", {"start": v(29.88, -34.9) * mm, "end": v(29.85, -34.8) * mm});
            skLineSegment(sketch, "E8116", {"start": v(29.85, -34.8) * mm, "end": v(29.81, -34.67) * mm});
            skLineSegment(sketch, "E8117", {"start": v(29.81, -34.67) * mm, "end": v(29.77, -34.56) * mm});
            skLineSegment(sketch, "E8118", {"start": v(29.77, -34.56) * mm, "end": v(29.74, -34.45) * mm});
            skLineSegment(sketch, "E8119", {"start": v(29.74, -34.45) * mm, "end": v(29.7, -34.34) * mm});
            skLineSegment(sketch, "E8120", {"start": v(29.7, -34.34) * mm, "end": v(29.66, -34.23) * mm});
            skLineSegment(sketch, "E8121", {"start": v(29.66, -34.23) * mm, "end": v(29.62, -34.11) * mm});
            skLineSegment(sketch, "E8122", {"start": v(29.62, -34.11) * mm, "end": v(29.58, -34) * mm});
            skLineSegment(sketch, "E8123", {"start": v(29.58, -34) * mm, "end": v(29.54, -33.89) * mm});
            skLineSegment(sketch, "E8124", {"start": v(29.54, -33.89) * mm, "end": v(29.5, -33.77) * mm});
            skLineSegment(sketch, "E8125", {"start": v(29.5, -33.77) * mm, "end": v(29.45, -33.66) * mm});
            skLineSegment(sketch, "E8126", {"start": v(29.45, -33.66) * mm, "end": v(29.4, -33.55) * mm});
            skLineSegment(sketch, "E8127", {"start": v(29.4, -33.55) * mm, "end": v(29.36, -33.44) * mm});
            skLineSegment(sketch, "E8128", {"start": v(29.36, -33.44) * mm, "end": v(29.32, -33.33) * mm});
            skLineSegment(sketch, "E8129", {"start": v(29.32, -33.33) * mm, "end": v(29.27, -33.22) * mm});
            skLineSegment(sketch, "E8130", {"start": v(29.27, -33.22) * mm, "end": v(29.22, -33.1) * mm});
            skLineSegment(sketch, "E8131", {"start": v(29.22, -33.1) * mm, "end": v(29.18, -33) * mm});
            skLineSegment(sketch, "E8132", {"start": v(29.18, -33) * mm, "end": v(29.13, -32.89) * mm});
            skLineSegment(sketch, "E8133", {"start": v(29.13, -32.89) * mm, "end": v(29.07, -32.77) * mm});
            skLineSegment(sketch, "E8134", {"start": v(29.07, -32.77) * mm, "end": v(29.16, -32.7) * mm});
            skLineSegment(sketch, "E8135", {"start": v(29.16, -32.7) * mm, "end": v(29.25, -32.61) * mm});
            skLineSegment(sketch, "E8136", {"start": v(29.25, -32.61) * mm, "end": v(29.34, -32.53) * mm});
            skLineSegment(sketch, "E8137", {"start": v(29.34, -32.53) * mm, "end": v(29.42, -32.45) * mm});
            skLineSegment(sketch, "E8138", {"start": v(29.42, -32.45) * mm, "end": v(29.51, -32.37) * mm});
            skLineSegment(sketch, "E8139", {"start": v(29.51, -32.37) * mm, "end": v(29.6, -32.3) * mm});
            skLineSegment(sketch, "E8140", {"start": v(29.6, -32.3) * mm, "end": v(29.69, -32.22) * mm});
            skLineSegment(sketch, "E8141", {"start": v(29.69, -32.22) * mm, "end": v(29.7, -32.2) * mm});
            skLineSegment(sketch, "E8142", {"start": v(29.7, -32.2) * mm, "end": v(29.8, -32.26) * mm});
            skLineSegment(sketch, "E8143", {"start": v(29.8, -32.26) * mm, "end": v(29.9, -32.32) * mm});
            skLineSegment(sketch, "E8144", {"start": v(29.9, -32.32) * mm, "end": v(30, -32.37) * mm});
            skLineSegment(sketch, "E8145", {"start": v(30, -32.37) * mm, "end": v(30.1, -32.43) * mm});
            skLineSegment(sketch, "E8146", {"start": v(30.1, -32.43) * mm, "end": v(30.2, -32.5) * mm});
            skLineSegment(sketch, "E8147", {"start": v(30.2, -32.5) * mm, "end": v(30.3, -32.55) * mm});
            skLineSegment(sketch, "E8148", {"start": v(30.3, -32.55) * mm, "end": v(30.42, -32.6) * mm});
            skLineSegment(sketch, "E8149", {"start": v(30.42, -32.6) * mm, "end": v(30.54, -32.67) * mm});
            skLineSegment(sketch, "E8150", {"start": v(30.54, -32.67) * mm, "end": v(30.65, -32.72) * mm});
            skLineSegment(sketch, "E8151", {"start": v(30.65, -32.72) * mm, "end": v(30.76, -32.78) * mm});
            skLineSegment(sketch, "E8152", {"start": v(30.76, -32.78) * mm, "end": v(30.86, -32.83) * mm});
            skLineSegment(sketch, "E8153", {"start": v(30.86, -32.83) * mm, "end": v(30.96, -32.88) * mm});
            skLineSegment(sketch, "E8154", {"start": v(30.96, -32.88) * mm, "end": v(31.07, -32.93) * mm});
            skLineSegment(sketch, "E8155", {"start": v(31.07, -32.93) * mm, "end": v(31.17, -32.98) * mm});
            skLineSegment(sketch, "E8156", {"start": v(31.17, -32.98) * mm, "end": v(31.28, -33.03) * mm});
            skLineSegment(sketch, "E8157", {"start": v(31.28, -33.03) * mm, "end": v(31.4, -33.07) * mm});
            skLineSegment(sketch, "E8158", {"start": v(31.4, -33.07) * mm, "end": v(31.5, -33.12) * mm});
            skLineSegment(sketch, "E8159", {"start": v(31.5, -33.12) * mm, "end": v(31.62, -33.17) * mm});
            skLineSegment(sketch, "E8160", {"start": v(31.62, -33.17) * mm, "end": v(31.74, -33.22) * mm});
            skLineSegment(sketch, "E8161", {"start": v(31.74, -33.22) * mm, "end": v(31.74, -33.22) * mm});
            skLineSegment(sketch, "E8162", {"start": v(31.74, -33.22) * mm, "end": v(31.83, -33.14) * mm});
            skLineSegment(sketch, "E8163", {"start": v(31.83, -33.14) * mm, "end": v(31.91, -33.06) * mm});
            skLineSegment(sketch, "E8164", {"start": v(31.91, -33.06) * mm, "end": v(32, -32.98) * mm});
            skLineSegment(sketch, "E8165", {"start": v(32, -32.98) * mm, "end": v(32.08, -32.9) * mm});
            skLineSegment(sketch, "E8166", {"start": v(32.08, -32.9) * mm, "end": v(32.15, -32.83) * mm});
            skLineSegment(sketch, "E8167", {"start": v(32.15, -32.83) * mm, "end": v(32.1, -32.72) * mm});
            skLineSegment(sketch, "E8168", {"start": v(32.1, -32.72) * mm, "end": v(32.06, -32.6) * mm});
            skLineSegment(sketch, "E8169", {"start": v(32.06, -32.6) * mm, "end": v(32.02, -32.5) * mm});
            skLineSegment(sketch, "E8170", {"start": v(32.02, -32.5) * mm, "end": v(31.97, -32.39) * mm});
            skLineSegment(sketch, "E8171", {"start": v(31.97, -32.39) * mm, "end": v(31.93, -32.28) * mm});
            skLineSegment(sketch, "E8172", {"start": v(31.93, -32.28) * mm, "end": v(31.88, -32.17) * mm});
            skLineSegment(sketch, "E8173", {"start": v(31.88, -32.17) * mm, "end": v(31.84, -32.06) * mm});
            skLineSegment(sketch, "E8174", {"start": v(31.84, -32.06) * mm, "end": v(31.79, -31.95) * mm});
            skLineSegment(sketch, "E8175", {"start": v(31.79, -31.95) * mm, "end": v(31.74, -31.84) * mm});
            skLineSegment(sketch, "E8176", {"start": v(31.74, -31.84) * mm, "end": v(31.69, -31.73) * mm});
            skLineSegment(sketch, "E8177", {"start": v(31.69, -31.73) * mm, "end": v(31.64, -31.62) * mm});
            skLineSegment(sketch, "E8178", {"start": v(31.64, -31.62) * mm, "end": v(31.59, -31.5) * mm});
            skLineSegment(sketch, "E8179", {"start": v(31.59, -31.5) * mm, "end": v(31.53, -31.4) * mm});
            skLineSegment(sketch, "E8180", {"start": v(31.53, -31.4) * mm, "end": v(31.48, -31.3) * mm});
            skLineSegment(sketch, "E8181", {"start": v(31.48, -31.3) * mm, "end": v(31.43, -31.19) * mm});
            skLineSegment(sketch, "E8182", {"start": v(31.43, -31.19) * mm, "end": v(31.37, -31.08) * mm});
            skLineSegment(sketch, "E8183", {"start": v(31.37, -31.08) * mm, "end": v(31.32, -30.98) * mm});
            skLineSegment(sketch, "E8184", {"start": v(31.32, -30.98) * mm, "end": v(31.26, -30.87) * mm});
            skLineSegment(sketch, "E8185", {"start": v(31.26, -30.87) * mm, "end": v(31.2, -30.76) * mm});
            skLineSegment(sketch, "E8186", {"start": v(31.2, -30.76) * mm, "end": v(31.28, -30.67) * mm});
            skLineSegment(sketch, "E8187", {"start": v(31.28, -30.67) * mm, "end": v(31.36, -30.59) * mm});
            skLineSegment(sketch, "E8188", {"start": v(31.36, -30.59) * mm, "end": v(31.44, -30.5) * mm});
            skLineSegment(sketch, "E8189", {"start": v(31.44, -30.5) * mm, "end": v(31.53, -30.42) * mm});
            skLineSegment(sketch, "E8190", {"start": v(31.53, -30.42) * mm, "end": v(31.6, -30.33) * mm});
            skLineSegment(sketch, "E8191", {"start": v(31.6, -30.33) * mm, "end": v(31.7, -30.25) * mm});
            skLineSegment(sketch, "E8192", {"start": v(31.7, -30.25) * mm, "end": v(31.77, -30.16) * mm});
            skLineSegment(sketch, "E8193", {"start": v(31.77, -30.16) * mm, "end": v(31.79, -30.15) * mm});
            skLineSegment(sketch, "E8194", {"start": v(31.79, -30.15) * mm, "end": v(31.88, -30.2) * mm});
            skLineSegment(sketch, "E8195", {"start": v(31.88, -30.2) * mm, "end": v(31.98, -30.25) * mm});
            skLineSegment(sketch, "E8196", {"start": v(31.98, -30.25) * mm, "end": v(32.09, -30.3) * mm});
            skLineSegment(sketch, "E8197", {"start": v(32.09, -30.3) * mm, "end": v(32.2, -30.35) * mm});
            skLineSegment(sketch, "E8198", {"start": v(32.2, -30.35) * mm, "end": v(32.3, -30.4) * mm});
            skLineSegment(sketch, "E8199", {"start": v(32.3, -30.4) * mm, "end": v(32.42, -30.45) * mm});
            skLineSegment(sketch, "E8200", {"start": v(32.42, -30.45) * mm, "end": v(32.53, -30.5) * mm});
            skLineSegment(sketch, "E8201", {"start": v(32.53, -30.5) * mm, "end": v(32.65, -30.56) * mm});
            skLineSegment(sketch, "E8202", {"start": v(32.65, -30.56) * mm, "end": v(32.76, -30.6) * mm});
            skLineSegment(sketch, "E8203", {"start": v(32.76, -30.6) * mm, "end": v(32.88, -30.65) * mm});
            skLineSegment(sketch, "E8204", {"start": v(32.88, -30.65) * mm, "end": v(32.98, -30.7) * mm});
            skLineSegment(sketch, "E8205", {"start": v(32.98, -30.7) * mm, "end": v(33.09, -30.74) * mm});
            skLineSegment(sketch, "E8206", {"start": v(33.09, -30.74) * mm, "end": v(33.2, -30.78) * mm});
            skLineSegment(sketch, "E8207", {"start": v(33.2, -30.78) * mm, "end": v(33.3, -30.82) * mm});
            skLineSegment(sketch, "E8208", {"start": v(33.3, -30.82) * mm, "end": v(33.42, -30.86) * mm});
            skLineSegment(sketch, "E8209", {"start": v(33.42, -30.86) * mm, "end": v(33.53, -30.9) * mm});
            skLineSegment(sketch, "E8210", {"start": v(33.53, -30.9) * mm, "end": v(33.65, -30.95) * mm});
            skLineSegment(sketch, "E8211", {"start": v(33.65, -30.95) * mm, "end": v(33.77, -30.99) * mm});
            skLineSegment(sketch, "E8212", {"start": v(33.77, -30.99) * mm, "end": v(33.89, -31.03) * mm});
            skLineSegment(sketch, "E8213", {"start": v(33.89, -31.03) * mm, "end": v(33.9, -31.03) * mm});
            skLineSegment(sketch, "E8214", {"start": v(33.9, -31.03) * mm, "end": v(33.97, -30.94) * mm});
            skLineSegment(sketch, "E8215", {"start": v(33.97, -30.94) * mm, "end": v(34.05, -30.85) * mm});
            skLineSegment(sketch, "E8216", {"start": v(34.05, -30.85) * mm, "end": v(34.12, -30.77) * mm});
            skLineSegment(sketch, "E8217", {"start": v(34.12, -30.77) * mm, "end": v(34.2, -30.68) * mm});
            skLineSegment(sketch, "E8218", {"start": v(34.2, -30.68) * mm, "end": v(34.27, -30.61) * mm});
            skLineSegment(sketch, "E8219", {"start": v(34.27, -30.61) * mm, "end": v(34.22, -30.5) * mm});
            skLineSegment(sketch, "E8220", {"start": v(34.22, -30.5) * mm, "end": v(34.17, -30.4) * mm});
            skLineSegment(sketch, "E8221", {"start": v(34.17, -30.4) * mm, "end": v(34.12, -30.28) * mm});
            skLineSegment(sketch, "E8222", {"start": v(34.12, -30.28) * mm, "end": v(34.07, -30.18) * mm});
            skLineSegment(sketch, "E8223", {"start": v(34.07, -30.18) * mm, "end": v(34.01, -30.07) * mm});
            skLineSegment(sketch, "E8224", {"start": v(34.01, -30.07) * mm, "end": v(33.96, -29.97) * mm});
            skLineSegment(sketch, "E8225", {"start": v(33.96, -29.97) * mm, "end": v(33.9, -29.86) * mm});
            skLineSegment(sketch, "E8226", {"start": v(33.9, -29.86) * mm, "end": v(33.85, -29.75) * mm});
            skLineSegment(sketch, "E8227", {"start": v(33.85, -29.75) * mm, "end": v(33.8, -29.65) * mm});
            skLineSegment(sketch, "E8228", {"start": v(33.8, -29.65) * mm, "end": v(33.74, -29.54) * mm});
            skLineSegment(sketch, "E8229", {"start": v(33.74, -29.54) * mm, "end": v(33.68, -29.43) * mm});
            skLineSegment(sketch, "E8230", {"start": v(33.68, -29.43) * mm, "end": v(33.62, -29.33) * mm});
            skLineSegment(sketch, "E8231", {"start": v(33.62, -29.33) * mm, "end": v(33.56, -29.22) * mm});
            skLineSegment(sketch, "E8232", {"start": v(33.56, -29.22) * mm, "end": v(33.5, -29.12) * mm});
            skLineSegment(sketch, "E8233", {"start": v(33.5, -29.12) * mm, "end": v(33.44, -29.02) * mm});
            skLineSegment(sketch, "E8234", {"start": v(33.44, -29.02) * mm, "end": v(33.38, -28.92) * mm});
            skLineSegment(sketch, "E8235", {"start": v(33.38, -28.92) * mm, "end": v(33.31, -28.81) * mm});
            skLineSegment(sketch, "E8236", {"start": v(33.31, -28.81) * mm, "end": v(33.25, -28.71) * mm});
            skLineSegment(sketch, "E8237", {"start": v(33.25, -28.71) * mm, "end": v(33.18, -28.6) * mm});
            skLineSegment(sketch, "E8238", {"start": v(33.18, -28.6) * mm, "end": v(33.26, -28.51) * mm});
            skLineSegment(sketch, "E8239", {"start": v(33.26, -28.51) * mm, "end": v(33.33, -28.42) * mm});
            skLineSegment(sketch, "E8240", {"start": v(33.33, -28.42) * mm, "end": v(33.41, -28.33) * mm});
            skLineSegment(sketch, "E8241", {"start": v(33.41, -28.33) * mm, "end": v(33.49, -28.24) * mm});
            skLineSegment(sketch, "E8242", {"start": v(33.49, -28.24) * mm, "end": v(33.56, -28.15) * mm});
            skLineSegment(sketch, "E8243", {"start": v(33.56, -28.15) * mm, "end": v(33.64, -28.06) * mm});
            skLineSegment(sketch, "E8244", {"start": v(33.64, -28.06) * mm, "end": v(33.72, -27.97) * mm});
            skLineSegment(sketch, "E8245", {"start": v(33.72, -27.97) * mm, "end": v(33.73, -27.96) * mm});
            skLineSegment(sketch, "E8246", {"start": v(33.73, -27.96) * mm, "end": v(33.83, -28) * mm});
            skLineSegment(sketch, "E8247", {"start": v(33.83, -28) * mm, "end": v(33.93, -28.04) * mm});
            skLineSegment(sketch, "E8248", {"start": v(33.93, -28.04) * mm, "end": v(34.04, -28.09) * mm});
            skLineSegment(sketch, "E8249", {"start": v(34.04, -28.09) * mm, "end": v(34.15, -28.13) * mm});
            skLineSegment(sketch, "E8250", {"start": v(34.15, -28.13) * mm, "end": v(34.26, -28.18) * mm});
            skLineSegment(sketch, "E8251", {"start": v(34.26, -28.18) * mm, "end": v(34.38, -28.22) * mm});
            skLineSegment(sketch, "E8252", {"start": v(34.38, -28.22) * mm, "end": v(34.5, -28.26) * mm});
            skLineSegment(sketch, "E8253", {"start": v(34.5, -28.26) * mm, "end": v(34.62, -28.3) * mm});
            skLineSegment(sketch, "E8254", {"start": v(34.62, -28.3) * mm, "end": v(34.73, -28.35) * mm});
            skLineSegment(sketch, "E8255", {"start": v(34.73, -28.35) * mm, "end": v(34.85, -28.39) * mm});
            skLineSegment(sketch, "E8256", {"start": v(34.85, -28.39) * mm, "end": v(34.96, -28.42) * mm});
            skLineSegment(sketch, "E8257", {"start": v(34.96, -28.42) * mm, "end": v(35.07, -28.46) * mm});
            skLineSegment(sketch, "E8258", {"start": v(35.07, -28.46) * mm, "end": v(35.18, -28.5) * mm});
            skLineSegment(sketch, "E8259", {"start": v(35.18, -28.5) * mm, "end": v(35.29, -28.53) * mm});
            skLineSegment(sketch, "E8260", {"start": v(35.29, -28.53) * mm, "end": v(35.4, -28.56) * mm});
            skLineSegment(sketch, "E8261", {"start": v(35.4, -28.56) * mm, "end": v(35.52, -28.6) * mm});
            skLineSegment(sketch, "E8262", {"start": v(35.52, -28.6) * mm, "end": v(35.64, -28.63) * mm});
            skLineSegment(sketch, "E8263", {"start": v(35.64, -28.63) * mm, "end": v(35.76, -28.66) * mm});
            skLineSegment(sketch, "E8264", {"start": v(35.76, -28.66) * mm, "end": v(35.89, -28.7) * mm});
            skLineSegment(sketch, "E8265", {"start": v(35.89, -28.7) * mm, "end": v(35.89, -28.7) * mm});
            skLineSegment(sketch, "E8266", {"start": v(35.89, -28.7) * mm, "end": v(35.96, -28.6) * mm});
            skLineSegment(sketch, "E8267", {"start": v(35.96, -28.6) * mm, "end": v(36.04, -28.5) * mm});
            skLineSegment(sketch, "E8268", {"start": v(36.04, -28.5) * mm, "end": v(36.1, -28.43) * mm});
            skLineSegment(sketch, "E8269", {"start": v(36.1, -28.43) * mm, "end": v(36.18, -28.33) * mm});
            skLineSegment(sketch, "E8270", {"start": v(36.18, -28.33) * mm, "end": v(36.24, -28.25) * mm});
            skLineSegment(sketch, "E8271", {"start": v(36.24, -28.25) * mm, "end": v(36.18, -28.15) * mm});
            skLineSegment(sketch, "E8272", {"start": v(36.18, -28.15) * mm, "end": v(36.12, -28.04) * mm});
            skLineSegment(sketch, "E8273", {"start": v(36.12, -28.04) * mm, "end": v(36.06, -27.94) * mm});
            skLineSegment(sketch, "E8274", {"start": v(36.06, -27.94) * mm, "end": v(36, -27.84) * mm});
            skLineSegment(sketch, "E8275", {"start": v(36, -27.84) * mm, "end": v(35.95, -27.74) * mm});
            skLineSegment(sketch, "E8276", {"start": v(35.95, -27.74) * mm, "end": v(35.89, -27.63) * mm});
            skLineSegment(sketch, "E8277", {"start": v(35.89, -27.63) * mm, "end": v(35.82, -27.53) * mm});
            skLineSegment(sketch, "E8278", {"start": v(35.82, -27.53) * mm, "end": v(35.76, -27.43) * mm});
            skLineSegment(sketch, "E8279", {"start": v(35.76, -27.43) * mm, "end": v(35.7, -27.33) * mm});
            skLineSegment(sketch, "E8280", {"start": v(35.7, -27.33) * mm, "end": v(35.63, -27.22) * mm});
            skLineSegment(sketch, "E8281", {"start": v(35.63, -27.22) * mm, "end": v(35.57, -27.12) * mm});
            skLineSegment(sketch, "E8282", {"start": v(35.57, -27.12) * mm, "end": v(35.5, -27.02) * mm});
            skLineSegment(sketch, "E8283", {"start": v(35.5, -27.02) * mm, "end": v(35.44, -26.92) * mm});
            skLineSegment(sketch, "E8284", {"start": v(35.44, -26.92) * mm, "end": v(35.37, -26.82) * mm});
            skLineSegment(sketch, "E8285", {"start": v(35.37, -26.82) * mm, "end": v(35.3, -26.72) * mm});
            skLineSegment(sketch, "E8286", {"start": v(35.3, -26.72) * mm, "end": v(35.23, -26.62) * mm});
            skLineSegment(sketch, "E8287", {"start": v(35.23, -26.62) * mm, "end": v(35.17, -26.52) * mm});
            skLineSegment(sketch, "E8288", {"start": v(35.17, -26.52) * mm, "end": v(35.1, -26.43) * mm});
            skLineSegment(sketch, "E8289", {"start": v(35.1, -26.43) * mm, "end": v(35.02, -26.32) * mm});
            skLineSegment(sketch, "E8290", {"start": v(35.02, -26.32) * mm, "end": v(35.09, -26.23) * mm});
            skLineSegment(sketch, "E8291", {"start": v(35.09, -26.23) * mm, "end": v(35.16, -26.13) * mm});
            skLineSegment(sketch, "E8292", {"start": v(35.16, -26.13) * mm, "end": v(35.23, -26.04) * mm});
            skLineSegment(sketch, "E8293", {"start": v(35.23, -26.04) * mm, "end": v(35.3, -25.94) * mm});
            skLineSegment(sketch, "E8294", {"start": v(35.3, -25.94) * mm, "end": v(35.37, -25.85) * mm});
            skLineSegment(sketch, "E8295", {"start": v(35.37, -25.85) * mm, "end": v(35.44, -25.75) * mm});
            skLineSegment(sketch, "E8296", {"start": v(35.44, -25.75) * mm, "end": v(35.51, -25.66) * mm});
            skLineSegment(sketch, "E8297", {"start": v(35.51, -25.66) * mm, "end": v(35.52, -25.64) * mm});
            skLineSegment(sketch, "E8298", {"start": v(35.52, -25.64) * mm, "end": v(35.62, -25.68) * mm});
            skLineSegment(sketch, "E8299", {"start": v(35.62, -25.68) * mm, "end": v(35.73, -25.72) * mm});
            skLineSegment(sketch, "E8300", {"start": v(35.73, -25.72) * mm, "end": v(35.84, -25.75) * mm});
            skLineSegment(sketch, "E8301", {"start": v(35.84, -25.75) * mm, "end": v(35.95, -25.79) * mm});
            skLineSegment(sketch, "E8302", {"start": v(35.95, -25.79) * mm, "end": v(36.07, -25.82) * mm});
            skLineSegment(sketch, "E8303", {"start": v(36.07, -25.82) * mm, "end": v(36.19, -25.86) * mm});
            skLineSegment(sketch, "E8304", {"start": v(36.19, -25.86) * mm, "end": v(36.3, -25.9) * mm});
            skLineSegment(sketch, "E8305", {"start": v(36.3, -25.9) * mm, "end": v(36.44, -25.93) * mm});
            skLineSegment(sketch, "E8306", {"start": v(36.44, -25.93) * mm, "end": v(36.55, -25.96) * mm});
            skLineSegment(sketch, "E8307", {"start": v(36.55, -25.96) * mm, "end": v(36.67, -26) * mm});
            skLineSegment(sketch, "E8308", {"start": v(36.67, -26) * mm, "end": v(36.78, -26.02) * mm});
            skLineSegment(sketch, "E8309", {"start": v(36.78, -26.02) * mm, "end": v(36.89, -26.05) * mm});
            skLineSegment(sketch, "E8310", {"start": v(36.89, -26.05) * mm, "end": v(37, -26.08) * mm});
            skLineSegment(sketch, "E8311", {"start": v(37, -26.08) * mm, "end": v(37.12, -26.1) * mm});
            skLineSegment(sketch, "E8312", {"start": v(37.12, -26.1) * mm, "end": v(37.23, -26.13) * mm});
            skLineSegment(sketch, "E8313", {"start": v(37.23, -26.13) * mm, "end": v(37.35, -26.16) * mm});
            skLineSegment(sketch, "E8314", {"start": v(37.35, -26.16) * mm, "end": v(37.47, -26.18) * mm});
            skLineSegment(sketch, "E8315", {"start": v(37.47, -26.18) * mm, "end": v(37.6, -26.21) * mm});
            skLineSegment(sketch, "E8316", {"start": v(37.6, -26.21) * mm, "end": v(37.72, -26.24) * mm});
            skLineSegment(sketch, "E8317", {"start": v(37.72, -26.24) * mm, "end": v(37.72, -26.24) * mm});
            skLineSegment(sketch, "E8318", {"start": v(37.72, -26.24) * mm, "end": v(37.8, -26.14) * mm});
            skLineSegment(sketch, "E8319", {"start": v(37.8, -26.14) * mm, "end": v(37.86, -26.04) * mm});
            skLineSegment(sketch, "E8320", {"start": v(37.86, -26.04) * mm, "end": v(37.92, -25.95) * mm});
            skLineSegment(sketch, "E8321", {"start": v(37.92, -25.95) * mm, "end": v(37.99, -25.85) * mm});
            skLineSegment(sketch, "E8322", {"start": v(37.99, -25.85) * mm, "end": v(38.04, -25.77) * mm});
            skLineSegment(sketch, "E8323", {"start": v(38.04, -25.77) * mm, "end": v(37.98, -25.67) * mm});
            skLineSegment(sketch, "E8324", {"start": v(37.98, -25.67) * mm, "end": v(37.91, -25.57) * mm});
            skLineSegment(sketch, "E8325", {"start": v(37.91, -25.57) * mm, "end": v(37.85, -25.47) * mm});
            skLineSegment(sketch, "E8326", {"start": v(37.85, -25.47) * mm, "end": v(37.79, -25.37) * mm});
            skLineSegment(sketch, "E8327", {"start": v(37.79, -25.37) * mm, "end": v(37.72, -25.27) * mm});
            skLineSegment(sketch, "E8328", {"start": v(37.72, -25.27) * mm, "end": v(37.65, -25.17) * mm});
            skLineSegment(sketch, "E8329", {"start": v(37.65, -25.17) * mm, "end": v(37.58, -25.08) * mm});
            skLineSegment(sketch, "E8330", {"start": v(37.58, -25.08) * mm, "end": v(37.52, -24.98) * mm});
            skLineSegment(sketch, "E8331", {"start": v(37.52, -24.98) * mm, "end": v(37.45, -24.88) * mm});
            skLineSegment(sketch, "E8332", {"start": v(37.45, -24.88) * mm, "end": v(37.37, -24.78) * mm});
            skLineSegment(sketch, "E8333", {"start": v(37.37, -24.78) * mm, "end": v(37.3, -24.68) * mm});
            skLineSegment(sketch, "E8334", {"start": v(37.3, -24.68) * mm, "end": v(37.23, -24.59) * mm});
            skLineSegment(sketch, "E8335", {"start": v(37.23, -24.59) * mm, "end": v(37.16, -24.5) * mm});
            skLineSegment(sketch, "E8336", {"start": v(37.16, -24.5) * mm, "end": v(37.08, -24.4) * mm});
            skLineSegment(sketch, "E8337", {"start": v(37.08, -24.4) * mm, "end": v(37, -24.3) * mm});
            skLineSegment(sketch, "E8338", {"start": v(37, -24.3) * mm, "end": v(36.93, -24.2) * mm});
            skLineSegment(sketch, "E8339", {"start": v(36.93, -24.2) * mm, "end": v(36.86, -24.12) * mm});
            skLineSegment(sketch, "E8340", {"start": v(36.86, -24.12) * mm, "end": v(36.78, -24.02) * mm});
            skLineSegment(sketch, "E8341", {"start": v(36.78, -24.02) * mm, "end": v(36.7, -23.93) * mm});
            skLineSegment(sketch, "E8342", {"start": v(36.7, -23.93) * mm, "end": v(36.76, -23.82) * mm});
            skLineSegment(sketch, "E8343", {"start": v(36.76, -23.82) * mm, "end": v(36.83, -23.73) * mm});
            skLineSegment(sketch, "E8344", {"start": v(36.83, -23.73) * mm, "end": v(36.9, -23.63) * mm});
            skLineSegment(sketch, "E8345", {"start": v(36.9, -23.63) * mm, "end": v(36.95, -23.53) * mm});
            skLineSegment(sketch, "E8346", {"start": v(36.95, -23.53) * mm, "end": v(37.02, -23.43) * mm});
            skLineSegment(sketch, "E8347", {"start": v(37.02, -23.43) * mm, "end": v(37.08, -23.33) * mm});
            skLineSegment(sketch, "E8348", {"start": v(37.08, -23.33) * mm, "end": v(37.15, -23.23) * mm});
            skLineSegment(sketch, "E8349", {"start": v(37.15, -23.23) * mm, "end": v(37.16, -23.21) * mm});
            skLineSegment(sketch, "E8350", {"start": v(37.16, -23.21) * mm, "end": v(37.26, -23.24) * mm});
            skLineSegment(sketch, "E8351", {"start": v(37.26, -23.24) * mm, "end": v(37.37, -23.27) * mm});
            skLineSegment(sketch, "E8352", {"start": v(37.37, -23.27) * mm, "end": v(37.48, -23.3) * mm});
            skLineSegment(sketch, "E8353", {"start": v(37.48, -23.3) * mm, "end": v(37.6, -23.33) * mm});
            skLineSegment(sketch, "E8354", {"start": v(37.6, -23.33) * mm, "end": v(37.71, -23.36) * mm});
            skLineSegment(sketch, "E8355", {"start": v(37.71, -23.36) * mm, "end": v(37.83, -23.39) * mm});
            skLineSegment(sketch, "E8356", {"start": v(37.83, -23.39) * mm, "end": v(37.96, -23.41) * mm});
            skLineSegment(sketch, "E8357", {"start": v(37.96, -23.41) * mm, "end": v(38.09, -23.44) * mm});
            skLineSegment(sketch, "E8358", {"start": v(38.09, -23.44) * mm, "end": v(38.2, -23.46) * mm});
            skLineSegment(sketch, "E8359", {"start": v(38.2, -23.46) * mm, "end": v(38.33, -23.49) * mm});
            skLineSegment(sketch, "E8360", {"start": v(38.33, -23.49) * mm, "end": v(38.44, -23.5) * mm});
            skLineSegment(sketch, "E8361", {"start": v(38.44, -23.5) * mm, "end": v(38.55, -23.53) * mm});
            skLineSegment(sketch, "E8362", {"start": v(38.55, -23.53) * mm, "end": v(38.66, -23.55) * mm});
            skLineSegment(sketch, "E8363", {"start": v(38.66, -23.55) * mm, "end": v(38.78, -23.57) * mm});
            skLineSegment(sketch, "E8364", {"start": v(38.78, -23.57) * mm, "end": v(38.9, -23.59) * mm});
            skLineSegment(sketch, "E8365", {"start": v(38.9, -23.59) * mm, "end": v(39.02, -23.6) * mm});
            skLineSegment(sketch, "E8366", {"start": v(39.02, -23.6) * mm, "end": v(39.14, -23.62) * mm});
            skLineSegment(sketch, "E8367", {"start": v(39.14, -23.62) * mm, "end": v(39.26, -23.64) * mm});
            skLineSegment(sketch, "E8368", {"start": v(39.26, -23.64) * mm, "end": v(39.4, -23.66) * mm});
            skLineSegment(sketch, "E8369", {"start": v(39.4, -23.66) * mm, "end": v(39.4, -23.66) * mm});
            skLineSegment(sketch, "E8370", {"start": v(39.4, -23.66) * mm, "end": v(39.45, -23.55) * mm});
            skLineSegment(sketch, "E8371", {"start": v(39.45, -23.55) * mm, "end": v(39.52, -23.45) * mm});
            skLineSegment(sketch, "E8372", {"start": v(39.52, -23.45) * mm, "end": v(39.57, -23.36) * mm});
            skLineSegment(sketch, "E8373", {"start": v(39.57, -23.36) * mm, "end": v(39.63, -23.26) * mm});
            skLineSegment(sketch, "E8374", {"start": v(39.63, -23.26) * mm, "end": v(39.68, -23.17) * mm});
            skLineSegment(sketch, "E8375", {"start": v(39.68, -23.17) * mm, "end": v(39.6, -23.08) * mm});
            skLineSegment(sketch, "E8376", {"start": v(39.6, -23.08) * mm, "end": v(39.54, -22.98) * mm});
            skLineSegment(sketch, "E8377", {"start": v(39.54, -22.98) * mm, "end": v(39.47, -22.88) * mm});
            skLineSegment(sketch, "E8378", {"start": v(39.47, -22.88) * mm, "end": v(39.4, -22.8) * mm});
            skLineSegment(sketch, "E8379", {"start": v(39.4, -22.8) * mm, "end": v(39.32, -22.7) * mm});
            skLineSegment(sketch, "E8380", {"start": v(39.32, -22.7) * mm, "end": v(39.25, -22.6) * mm});
            skLineSegment(sketch, "E8381", {"start": v(39.25, -22.6) * mm, "end": v(39.18, -22.5) * mm});
            skLineSegment(sketch, "E8382", {"start": v(39.18, -22.5) * mm, "end": v(39.1, -22.42) * mm});
            skLineSegment(sketch, "E8383", {"start": v(39.1, -22.42) * mm, "end": v(39.02, -22.32) * mm});
            skLineSegment(sketch, "E8384", {"start": v(39.02, -22.32) * mm, "end": v(38.94, -22.23) * mm});
            skLineSegment(sketch, "E8385", {"start": v(38.94, -22.23) * mm, "end": v(38.87, -22.13) * mm});
            skLineSegment(sketch, "E8386", {"start": v(38.87, -22.13) * mm, "end": v(38.79, -22.04) * mm});
            skLineSegment(sketch, "E8387", {"start": v(38.79, -22.04) * mm, "end": v(38.7, -21.95) * mm});
            skLineSegment(sketch, "E8388", {"start": v(38.7, -21.95) * mm, "end": v(38.63, -21.86) * mm});
            skLineSegment(sketch, "E8389", {"start": v(38.63, -21.86) * mm, "end": v(38.55, -21.78) * mm});
            skLineSegment(sketch, "E8390", {"start": v(38.55, -21.78) * mm, "end": v(38.47, -21.69) * mm});
            skLineSegment(sketch, "E8391", {"start": v(38.47, -21.69) * mm, "end": v(38.39, -21.6) * mm});
            skLineSegment(sketch, "E8392", {"start": v(38.39, -21.6) * mm, "end": v(38.3, -21.51) * mm});
            skLineSegment(sketch, "E8393", {"start": v(38.3, -21.51) * mm, "end": v(38.21, -21.42) * mm});
            skLineSegment(sketch, "E8394", {"start": v(38.21, -21.42) * mm, "end": v(38.27, -21.32) * mm});
            skLineSegment(sketch, "E8395", {"start": v(38.27, -21.32) * mm, "end": v(38.33, -21.21) * mm});
            skLineSegment(sketch, "E8396", {"start": v(38.33, -21.21) * mm, "end": v(38.39, -21.1) * mm});
            skLineSegment(sketch, "E8397", {"start": v(38.39, -21.1) * mm, "end": v(38.44, -21) * mm});
            skLineSegment(sketch, "E8398", {"start": v(38.44, -21) * mm, "end": v(38.5, -20.9) * mm});
            skLineSegment(sketch, "E8399", {"start": v(38.5, -20.9) * mm, "end": v(38.56, -20.8) * mm});
            skLineSegment(sketch, "E8400", {"start": v(38.56, -20.8) * mm, "end": v(38.61, -20.7) * mm});
            skLineSegment(sketch, "E8401", {"start": v(38.61, -20.7) * mm, "end": v(38.62, -20.68) * mm});
            skLineSegment(sketch, "E8402", {"start": v(38.62, -20.68) * mm, "end": v(38.73, -20.7) * mm});
            skLineSegment(sketch, "E8403", {"start": v(38.73, -20.7) * mm, "end": v(38.84, -20.72) * mm});
            skLineSegment(sketch, "E8404", {"start": v(38.84, -20.72) * mm, "end": v(38.95, -20.75) * mm});
            skLineSegment(sketch, "E8405", {"start": v(38.95, -20.75) * mm, "end": v(39.07, -20.77) * mm});
            skLineSegment(sketch, "E8406", {"start": v(39.07, -20.77) * mm, "end": v(39.19, -20.79) * mm});
            skLineSegment(sketch, "E8407", {"start": v(39.19, -20.79) * mm, "end": v(39.31, -20.8) * mm});
            skLineSegment(sketch, "E8408", {"start": v(39.31, -20.8) * mm, "end": v(39.44, -20.83) * mm});
            skLineSegment(sketch, "E8409", {"start": v(39.44, -20.83) * mm, "end": v(39.57, -20.84) * mm});
            skLineSegment(sketch, "E8410", {"start": v(39.57, -20.84) * mm, "end": v(39.69, -20.86) * mm});
            skLineSegment(sketch, "E8411", {"start": v(39.69, -20.86) * mm, "end": v(39.8, -20.88) * mm});
            skLineSegment(sketch, "E8412", {"start": v(39.8, -20.88) * mm, "end": v(39.92, -20.89) * mm});
            skLineSegment(sketch, "E8413", {"start": v(39.92, -20.89) * mm, "end": v(40.03, -20.9) * mm});
            skLineSegment(sketch, "E8414", {"start": v(40.03, -20.9) * mm, "end": v(40.15, -20.91) * mm});
            skLineSegment(sketch, "E8415", {"start": v(40.15, -20.91) * mm, "end": v(40.27, -20.93) * mm});
            skLineSegment(sketch, "E8416", {"start": v(40.27, -20.93) * mm, "end": v(40.39, -20.94) * mm});
            skLineSegment(sketch, "E8417", {"start": v(40.39, -20.94) * mm, "end": v(40.5, -20.95) * mm});
            skLineSegment(sketch, "E8418", {"start": v(40.5, -20.95) * mm, "end": v(40.63, -20.96) * mm});
            skLineSegment(sketch, "E8419", {"start": v(40.63, -20.96) * mm, "end": v(40.76, -20.97) * mm});
            skLineSegment(sketch, "E8420", {"start": v(40.76, -20.97) * mm, "end": v(40.88, -20.97) * mm});
            skLineSegment(sketch, "E8421", {"start": v(40.88, -20.97) * mm, "end": v(40.89, -20.97) * mm});
            skLineSegment(sketch, "E8422", {"start": v(40.89, -20.97) * mm, "end": v(40.94, -20.87) * mm});
            skLineSegment(sketch, "E8423", {"start": v(40.94, -20.87) * mm, "end": v(41, -20.76) * mm});
            skLineSegment(sketch, "E8424", {"start": v(41, -20.76) * mm, "end": v(41.04, -20.66) * mm});
            skLineSegment(sketch, "E8425", {"start": v(41.04, -20.66) * mm, "end": v(41.1, -20.56) * mm});
            skLineSegment(sketch, "E8426", {"start": v(41.1, -20.56) * mm, "end": v(41.14, -20.47) * mm});
            skLineSegment(sketch, "E8427", {"start": v(41.14, -20.47) * mm, "end": v(41.06, -20.38) * mm});
            skLineSegment(sketch, "E8428", {"start": v(41.06, -20.38) * mm, "end": v(40.98, -20.28) * mm});
            skLineSegment(sketch, "E8429", {"start": v(40.98, -20.28) * mm, "end": v(40.9, -20.2) * mm});
            skLineSegment(sketch, "E8430", {"start": v(40.9, -20.2) * mm, "end": v(40.83, -20.1) * mm});
            skLineSegment(sketch, "E8431", {"start": v(40.83, -20.1) * mm, "end": v(40.75, -20.02) * mm});
            skLineSegment(sketch, "E8432", {"start": v(40.75, -20.02) * mm, "end": v(40.67, -19.93) * mm});
            skLineSegment(sketch, "E8433", {"start": v(40.67, -19.93) * mm, "end": v(40.6, -19.84) * mm});
            skLineSegment(sketch, "E8434", {"start": v(40.6, -19.84) * mm, "end": v(40.5, -19.75) * mm});
            skLineSegment(sketch, "E8435", {"start": v(40.5, -19.75) * mm, "end": v(40.43, -19.67) * mm});
            skLineSegment(sketch, "E8436", {"start": v(40.43, -19.67) * mm, "end": v(40.34, -19.58) * mm});
            skLineSegment(sketch, "E8437", {"start": v(40.34, -19.58) * mm, "end": v(40.26, -19.49) * mm});
            skLineSegment(sketch, "E8438", {"start": v(40.26, -19.49) * mm, "end": v(40.17, -19.4) * mm});
            skLineSegment(sketch, "E8439", {"start": v(40.17, -19.4) * mm, "end": v(40.09, -19.32) * mm});
            skLineSegment(sketch, "E8440", {"start": v(40.09, -19.32) * mm, "end": v(40, -19.24) * mm});
            skLineSegment(sketch, "E8441", {"start": v(40, -19.24) * mm, "end": v(39.92, -19.15) * mm});
            skLineSegment(sketch, "E8442", {"start": v(39.92, -19.15) * mm, "end": v(39.83, -19.07) * mm});
            skLineSegment(sketch, "E8443", {"start": v(39.83, -19.07) * mm, "end": v(39.74, -18.99) * mm});
            skLineSegment(sketch, "E8444", {"start": v(39.74, -18.99) * mm, "end": v(39.66, -18.9) * mm});
            skLineSegment(sketch, "E8445", {"start": v(39.66, -18.9) * mm, "end": v(39.56, -18.82) * mm});
            skLineSegment(sketch, "E8446", {"start": v(39.56, -18.82) * mm, "end": v(39.61, -18.71) * mm});
            skLineSegment(sketch, "E8447", {"start": v(39.61, -18.71) * mm, "end": v(39.66, -18.6) * mm});
            skLineSegment(sketch, "E8448", {"start": v(39.66, -18.6) * mm, "end": v(39.71, -18.5) * mm});
            skLineSegment(sketch, "E8449", {"start": v(39.71, -18.5) * mm, "end": v(39.76, -18.4) * mm});
            skLineSegment(sketch, "E8450", {"start": v(39.76, -18.4) * mm, "end": v(39.81, -18.28) * mm});
            skLineSegment(sketch, "E8451", {"start": v(39.81, -18.28) * mm, "end": v(39.86, -18.18) * mm});
            skLineSegment(sketch, "E8452", {"start": v(39.86, -18.18) * mm, "end": v(39.91, -18.07) * mm});
            skLineSegment(sketch, "E8453", {"start": v(39.91, -18.07) * mm, "end": v(39.92, -18.05) * mm});
            skLineSegment(sketch, "E8454", {"start": v(39.92, -18.05) * mm, "end": v(40.03, -18.07) * mm});
            skLineSegment(sketch, "E8455", {"start": v(40.03, -18.07) * mm, "end": v(40.14, -18.08) * mm});
            skLineSegment(sketch, "E8456", {"start": v(40.14, -18.08) * mm, "end": v(40.25, -18.1) * mm});
            skLineSegment(sketch, "E8457", {"start": v(40.25, -18.1) * mm, "end": v(40.37, -18.11) * mm});
            skLineSegment(sketch, "E8458", {"start": v(40.37, -18.11) * mm, "end": v(40.49, -18.12) * mm});
            skLineSegment(sketch, "E8459", {"start": v(40.49, -18.12) * mm, "end": v(40.61, -18.13) * mm});
            skLineSegment(sketch, "E8460", {"start": v(40.61, -18.13) * mm, "end": v(40.74, -18.14) * mm});
            skLineSegment(sketch, "E8461", {"start": v(40.74, -18.14) * mm, "end": v(40.87, -18.15) * mm});
            skLineSegment(sketch, "E8462", {"start": v(40.87, -18.15) * mm, "end": v(41, -18.16) * mm});
            skLineSegment(sketch, "E8463", {"start": v(41, -18.16) * mm, "end": v(41.11, -18.17) * mm});
            skLineSegment(sketch, "E8464", {"start": v(41.11, -18.17) * mm, "end": v(41.23, -18.18) * mm});
            skLineSegment(sketch, "E8465", {"start": v(41.23, -18.18) * mm, "end": v(41.34, -18.18) * mm});
            skLineSegment(sketch, "E8466", {"start": v(41.34, -18.18) * mm, "end": v(41.46, -18.19) * mm});
            skLineSegment(sketch, "E8467", {"start": v(41.46, -18.19) * mm, "end": v(41.57, -18.19) * mm});
            skLineSegment(sketch, "E8468", {"start": v(41.57, -18.19) * mm, "end": v(41.7, -18.2) * mm});
            skLineSegment(sketch, "E8469", {"start": v(41.7, -18.2) * mm, "end": v(41.82, -18.2) * mm});
            skLineSegment(sketch, "E8470", {"start": v(41.82, -18.2) * mm, "end": v(41.94, -18.2) * mm});
            skLineSegment(sketch, "E8471", {"start": v(41.94, -18.2) * mm, "end": v(42.07, -18.2) * mm});
            skLineSegment(sketch, "E8472", {"start": v(42.07, -18.2) * mm, "end": v(42.2, -18.2) * mm});
            skLineSegment(sketch, "E8473", {"start": v(42.2, -18.2) * mm, "end": v(42.2, -18.2) * mm});
            skLineSegment(sketch, "E8474", {"start": v(42.2, -18.2) * mm, "end": v(42.24, -18.09) * mm});
            skLineSegment(sketch, "E8475", {"start": v(42.24, -18.09) * mm, "end": v(42.29, -17.98) * mm});
            skLineSegment(sketch, "E8476", {"start": v(42.29, -17.98) * mm, "end": v(42.33, -17.88) * mm});
            skLineSegment(sketch, "E8477", {"start": v(42.33, -17.88) * mm, "end": v(42.38, -17.77) * mm});
            skLineSegment(sketch, "E8478", {"start": v(42.38, -17.77) * mm, "end": v(42.42, -17.68) * mm});
            skLineSegment(sketch, "E8479", {"start": v(42.42, -17.68) * mm, "end": v(42.33, -17.59) * mm});
            skLineSegment(sketch, "E8480", {"start": v(42.33, -17.59) * mm, "end": v(42.25, -17.5) * mm});
            skLineSegment(sketch, "E8481", {"start": v(42.25, -17.5) * mm, "end": v(42.16, -17.42) * mm});
            skLineSegment(sketch, "E8482", {"start": v(42.16, -17.42) * mm, "end": v(42.08, -17.34) * mm});
            skLineSegment(sketch, "E8483", {"start": v(42.08, -17.34) * mm, "end": v(42, -17.25) * mm});
            skLineSegment(sketch, "E8484", {"start": v(42, -17.25) * mm, "end": v(41.91, -17.17) * mm});
            skLineSegment(sketch, "E8485", {"start": v(41.91, -17.17) * mm, "end": v(41.83, -17.09) * mm});
            skLineSegment(sketch, "E8486", {"start": v(41.83, -17.09) * mm, "end": v(41.74, -17) * mm});
            skLineSegment(sketch, "E8487", {"start": v(41.74, -17) * mm, "end": v(41.65, -16.92) * mm});
            skLineSegment(sketch, "E8488", {"start": v(41.65, -16.92) * mm, "end": v(41.56, -16.84) * mm});
            skLineSegment(sketch, "E8489", {"start": v(41.56, -16.84) * mm, "end": v(41.47, -16.76) * mm});
            skLineSegment(sketch, "E8490", {"start": v(41.47, -16.76) * mm, "end": v(41.38, -16.68) * mm});
            skLineSegment(sketch, "E8491", {"start": v(41.38, -16.68) * mm, "end": v(41.3, -16.6) * mm});
            skLineSegment(sketch, "E8492", {"start": v(41.3, -16.6) * mm, "end": v(41.2, -16.52) * mm});
            skLineSegment(sketch, "E8493", {"start": v(41.2, -16.52) * mm, "end": v(41.1, -16.44) * mm});
            skLineSegment(sketch, "E8494", {"start": v(41.1, -16.44) * mm, "end": v(41.02, -16.37) * mm});
            skLineSegment(sketch, "E8495", {"start": v(41.02, -16.37) * mm, "end": v(40.92, -16.3) * mm});
            skLineSegment(sketch, "E8496", {"start": v(40.92, -16.3) * mm, "end": v(40.83, -16.22) * mm});
            skLineSegment(sketch, "E8497", {"start": v(40.83, -16.22) * mm, "end": v(40.73, -16.14) * mm});
            skLineSegment(sketch, "E8498", {"start": v(40.73, -16.14) * mm, "end": v(40.77, -16.02) * mm});
            skLineSegment(sketch, "E8499", {"start": v(40.77, -16.02) * mm, "end": v(40.81, -15.92) * mm});
            skLineSegment(sketch, "E8500", {"start": v(40.81, -15.92) * mm, "end": v(40.86, -15.8) * mm});
            skLineSegment(sketch, "E8501", {"start": v(40.86, -15.8) * mm, "end": v(40.9, -15.7) * mm});
            skLineSegment(sketch, "E8502", {"start": v(40.9, -15.7) * mm, "end": v(40.94, -15.58) * mm});
            skLineSegment(sketch, "E8503", {"start": v(40.94, -15.58) * mm, "end": v(40.98, -15.47) * mm});
            skLineSegment(sketch, "E8504", {"start": v(40.98, -15.47) * mm, "end": v(41.03, -15.36) * mm});
            skLineSegment(sketch, "E8505", {"start": v(41.03, -15.36) * mm, "end": v(41.04, -15.35) * mm});
            skLineSegment(sketch, "E8506", {"start": v(41.04, -15.35) * mm, "end": v(41.14, -15.36) * mm});
            skLineSegment(sketch, "E8507", {"start": v(41.14, -15.36) * mm, "end": v(41.26, -15.36) * mm});
            skLineSegment(sketch, "E8508", {"start": v(41.26, -15.36) * mm, "end": v(41.37, -15.37) * mm});
            skLineSegment(sketch, "E8509", {"start": v(41.37, -15.37) * mm, "end": v(41.49, -15.37) * mm});
            skLineSegment(sketch, "E8510", {"start": v(41.49, -15.37) * mm, "end": v(41.6, -15.38) * mm});
            skLineSegment(sketch, "E8511", {"start": v(41.6, -15.38) * mm, "end": v(41.73, -15.38) * mm});
            skLineSegment(sketch, "E8512", {"start": v(41.73, -15.38) * mm, "end": v(41.86, -15.38) * mm});
            skLineSegment(sketch, "E8513", {"start": v(41.86, -15.38) * mm, "end": v(42, -15.38) * mm});
            skLineSegment(sketch, "E8514", {"start": v(42, -15.38) * mm, "end": v(42.11, -15.38) * mm});
            skLineSegment(sketch, "E8515", {"start": v(42.11, -15.38) * mm, "end": v(42.24, -15.38) * mm});
            skLineSegment(sketch, "E8516", {"start": v(42.24, -15.38) * mm, "end": v(42.35, -15.38) * mm});
            skLineSegment(sketch, "E8517", {"start": v(42.35, -15.38) * mm, "end": v(42.46, -15.38) * mm});
            skLineSegment(sketch, "E8518", {"start": v(42.46, -15.38) * mm, "end": v(42.58, -15.38) * mm});
            skLineSegment(sketch, "E8519", {"start": v(42.58, -15.38) * mm, "end": v(42.7, -15.37) * mm});
            skLineSegment(sketch, "E8520", {"start": v(42.7, -15.37) * mm, "end": v(42.82, -15.37) * mm});
            skLineSegment(sketch, "E8521", {"start": v(42.82, -15.37) * mm, "end": v(42.94, -15.36) * mm});
            skLineSegment(sketch, "E8522", {"start": v(42.94, -15.36) * mm, "end": v(43.06, -15.35) * mm});
            skLineSegment(sketch, "E8523", {"start": v(43.06, -15.35) * mm, "end": v(43.19, -15.35) * mm});
            skLineSegment(sketch, "E8524", {"start": v(43.19, -15.35) * mm, "end": v(43.31, -15.34) * mm});
            skLineSegment(sketch, "E8525", {"start": v(43.31, -15.34) * mm, "end": v(43.32, -15.34) * mm});
            skLineSegment(sketch, "E8526", {"start": v(43.32, -15.34) * mm, "end": v(43.36, -15.22) * mm});
            skLineSegment(sketch, "E8527", {"start": v(43.36, -15.22) * mm, "end": v(43.4, -15.11) * mm});
            skLineSegment(sketch, "E8528", {"start": v(43.4, -15.11) * mm, "end": v(43.43, -15) * mm});
            skLineSegment(sketch, "E8529", {"start": v(43.43, -15) * mm, "end": v(43.47, -14.9) * mm});
            skLineSegment(sketch, "E8530", {"start": v(43.47, -14.9) * mm, "end": v(43.5, -14.8) * mm});
            skLineSegment(sketch, "E8531", {"start": v(43.5, -14.8) * mm, "end": v(43.41, -14.72) * mm});
            skLineSegment(sketch, "E8532", {"start": v(43.41, -14.72) * mm, "end": v(43.32, -14.64) * mm});
            skLineSegment(sketch, "E8533", {"start": v(43.32, -14.64) * mm, "end": v(43.23, -14.56) * mm});
            skLineSegment(sketch, "E8534", {"start": v(43.23, -14.56) * mm, "end": v(43.15, -14.49) * mm});
            skLineSegment(sketch, "E8535", {"start": v(43.15, -14.49) * mm, "end": v(43.06, -14.4) * mm});
            skLineSegment(sketch, "E8536", {"start": v(43.06, -14.4) * mm, "end": v(42.97, -14.33) * mm});
            skLineSegment(sketch, "E8537", {"start": v(42.97, -14.33) * mm, "end": v(42.87, -14.25) * mm});
            skLineSegment(sketch, "E8538", {"start": v(42.87, -14.25) * mm, "end": v(42.78, -14.18) * mm});
            skLineSegment(sketch, "E8539", {"start": v(42.78, -14.18) * mm, "end": v(42.69, -14.1) * mm});
            skLineSegment(sketch, "E8540", {"start": v(42.69, -14.1) * mm, "end": v(42.6, -14.02) * mm});
            skLineSegment(sketch, "E8541", {"start": v(42.6, -14.02) * mm, "end": v(42.5, -13.95) * mm});
            skLineSegment(sketch, "E8542", {"start": v(42.5, -13.95) * mm, "end": v(42.4, -13.88) * mm});
            skLineSegment(sketch, "E8543", {"start": v(42.4, -13.88) * mm, "end": v(42.3, -13.8) * mm});
            skLineSegment(sketch, "E8544", {"start": v(42.3, -13.8) * mm, "end": v(42.21, -13.73) * mm});
            skLineSegment(sketch, "E8545", {"start": v(42.21, -13.73) * mm, "end": v(42.12, -13.66) * mm});
            skLineSegment(sketch, "E8546", {"start": v(42.12, -13.66) * mm, "end": v(42.02, -13.6) * mm});
            skLineSegment(sketch, "E8547", {"start": v(42.02, -13.6) * mm, "end": v(41.92, -13.52) * mm});
            skLineSegment(sketch, "E8548", {"start": v(41.92, -13.52) * mm, "end": v(41.82, -13.45) * mm});
            skLineSegment(sketch, "E8549", {"start": v(41.82, -13.45) * mm, "end": v(41.72, -13.38) * mm});
            skLineSegment(sketch, "E8550", {"start": v(41.72, -13.38) * mm, "end": v(41.75, -13.27) * mm});
            skLineSegment(sketch, "E8551", {"start": v(41.75, -13.27) * mm, "end": v(41.79, -13.15) * mm});
            skLineSegment(sketch, "E8552", {"start": v(41.79, -13.15) * mm, "end": v(41.82, -13.04) * mm});
            skLineSegment(sketch, "E8553", {"start": v(41.82, -13.04) * mm, "end": v(41.86, -12.93) * mm});
            skLineSegment(sketch, "E8554", {"start": v(41.86, -12.93) * mm, "end": v(41.9, -12.81) * mm});
            skLineSegment(sketch, "E8555", {"start": v(41.9, -12.81) * mm, "end": v(41.93, -12.7) * mm});
            skLineSegment(sketch, "E8556", {"start": v(41.93, -12.7) * mm, "end": v(41.96, -12.59) * mm});
            skLineSegment(sketch, "E8557", {"start": v(41.96, -12.59) * mm, "end": v(41.97, -12.57) * mm});
            skLineSegment(sketch, "E8558", {"start": v(41.97, -12.57) * mm, "end": v(42.08, -12.57) * mm});
            skLineSegment(sketch, "E8559", {"start": v(42.08, -12.57) * mm, "end": v(42.19, -12.57) * mm});
            skLineSegment(sketch, "E8560", {"start": v(42.19, -12.57) * mm, "end": v(42.3, -12.57) * mm});
            skLineSegment(sketch, "E8561", {"start": v(42.3, -12.57) * mm, "end": v(42.42, -12.57) * mm});
            skLineSegment(sketch, "E8562", {"start": v(42.42, -12.57) * mm, "end": v(42.54, -12.56) * mm});
            skLineSegment(sketch, "E8563", {"start": v(42.54, -12.56) * mm, "end": v(42.67, -12.56) * mm});
            skLineSegment(sketch, "E8564", {"start": v(42.67, -12.56) * mm, "end": v(42.8, -12.55) * mm});
            skLineSegment(sketch, "E8565", {"start": v(42.8, -12.55) * mm, "end": v(42.93, -12.54) * mm});
            skLineSegment(sketch, "E8566", {"start": v(42.93, -12.54) * mm, "end": v(43.05, -12.54) * mm});
            skLineSegment(sketch, "E8567", {"start": v(43.05, -12.54) * mm, "end": v(43.17, -12.53) * mm});
            skLineSegment(sketch, "E8568", {"start": v(43.17, -12.53) * mm, "end": v(43.28, -12.52) * mm});
            skLineSegment(sketch, "E8569", {"start": v(43.28, -12.52) * mm, "end": v(43.4, -12.5) * mm});
            skLineSegment(sketch, "E8570", {"start": v(43.4, -12.5) * mm, "end": v(43.51, -12.5) * mm});
            skLineSegment(sketch, "E8571", {"start": v(43.51, -12.5) * mm, "end": v(43.63, -12.49) * mm});
            skLineSegment(sketch, "E8572", {"start": v(43.63, -12.49) * mm, "end": v(43.75, -12.47) * mm});
            skLineSegment(sketch, "E8573", {"start": v(43.75, -12.47) * mm, "end": v(43.87, -12.46) * mm});
            skLineSegment(sketch, "E8574", {"start": v(43.87, -12.46) * mm, "end": v(44, -12.44) * mm});
            skLineSegment(sketch, "E8575", {"start": v(44, -12.44) * mm, "end": v(44.12, -12.43) * mm});
            skLineSegment(sketch, "E8576", {"start": v(44.12, -12.43) * mm, "end": v(44.24, -12.4) * mm});
            skLineSegment(sketch, "E8577", {"start": v(44.24, -12.4) * mm, "end": v(44.24, -12.4) * mm});
            skLineSegment(sketch, "E8578", {"start": v(44.24, -12.4) * mm, "end": v(44.28, -12.3) * mm});
            skLineSegment(sketch, "E8579", {"start": v(44.28, -12.3) * mm, "end": v(44.3, -12.18) * mm});
            skLineSegment(sketch, "E8580", {"start": v(44.3, -12.18) * mm, "end": v(44.34, -12.07) * mm});
            skLineSegment(sketch, "E8581", {"start": v(44.34, -12.07) * mm, "end": v(44.37, -11.96) * mm});
            skLineSegment(sketch, "E8582", {"start": v(44.37, -11.96) * mm, "end": v(44.4, -11.86) * mm});
            skLineSegment(sketch, "E8583", {"start": v(44.4, -11.86) * mm, "end": v(44.3, -11.8) * mm});
            skLineSegment(sketch, "E8584", {"start": v(44.3, -11.8) * mm, "end": v(44.2, -11.71) * mm});
            skLineSegment(sketch, "E8585", {"start": v(44.2, -11.71) * mm, "end": v(44.1, -11.64) * mm});
            skLineSegment(sketch, "E8586", {"start": v(44.1, -11.64) * mm, "end": v(44.02, -11.57) * mm});
            skLineSegment(sketch, "E8587", {"start": v(44.02, -11.57) * mm, "end": v(43.92, -11.5) * mm});
            skLineSegment(sketch, "E8588", {"start": v(43.92, -11.5) * mm, "end": v(43.83, -11.43) * mm});
            skLineSegment(sketch, "E8589", {"start": v(43.83, -11.43) * mm, "end": v(43.73, -11.36) * mm});
            skLineSegment(sketch, "E8590", {"start": v(43.73, -11.36) * mm, "end": v(43.63, -11.29) * mm});
            skLineSegment(sketch, "E8591", {"start": v(43.63, -11.29) * mm, "end": v(43.54, -11.22) * mm});
            skLineSegment(sketch, "E8592", {"start": v(43.54, -11.22) * mm, "end": v(43.43, -11.15) * mm});
            skLineSegment(sketch, "E8593", {"start": v(43.43, -11.15) * mm, "end": v(43.33, -11.08) * mm});
            skLineSegment(sketch, "E8594", {"start": v(43.33, -11.08) * mm, "end": v(43.23, -11.01) * mm});
            skLineSegment(sketch, "E8595", {"start": v(43.23, -11.01) * mm, "end": v(43.14, -10.95) * mm});
            skLineSegment(sketch, "E8596", {"start": v(43.14, -10.95) * mm, "end": v(43.03, -10.88) * mm});
            skLineSegment(sketch, "E8597", {"start": v(43.03, -10.88) * mm, "end": v(42.93, -10.82) * mm});
            skLineSegment(sketch, "E8598", {"start": v(42.93, -10.82) * mm, "end": v(42.83, -10.75) * mm});
            skLineSegment(sketch, "E8599", {"start": v(42.83, -10.75) * mm, "end": v(42.73, -10.7) * mm});
            skLineSegment(sketch, "E8600", {"start": v(42.73, -10.7) * mm, "end": v(42.63, -10.63) * mm});
            skLineSegment(sketch, "E8601", {"start": v(42.63, -10.63) * mm, "end": v(42.52, -10.56) * mm});
            skLineSegment(sketch, "E8602", {"start": v(42.52, -10.56) * mm, "end": v(42.54, -10.45) * mm});
            skLineSegment(sketch, "E8603", {"start": v(42.54, -10.45) * mm, "end": v(42.57, -10.33) * mm});
            skLineSegment(sketch, "E8604", {"start": v(42.57, -10.33) * mm, "end": v(42.6, -10.22) * mm});
            skLineSegment(sketch, "E8605", {"start": v(42.6, -10.22) * mm, "end": v(42.63, -10.1) * mm});
            skLineSegment(sketch, "E8606", {"start": v(42.63, -10.1) * mm, "end": v(42.66, -9.99) * mm});
            skLineSegment(sketch, "E8607", {"start": v(42.66, -9.99) * mm, "end": v(42.68, -9.87) * mm});
            skLineSegment(sketch, "E8608", {"start": v(42.68, -9.87) * mm, "end": v(42.71, -9.76) * mm});
            skLineSegment(sketch, "E8609", {"start": v(42.71, -9.76) * mm, "end": v(42.72, -9.74) * mm});
            skLineSegment(sketch, "E8610", {"start": v(42.72, -9.74) * mm, "end": v(42.82, -9.73) * mm});
            skLineSegment(sketch, "E8611", {"start": v(42.82, -9.73) * mm, "end": v(42.94, -9.73) * mm});
            skLineSegment(sketch, "E8612", {"start": v(42.94, -9.73) * mm, "end": v(43.05, -9.72) * mm});
            skLineSegment(sketch, "E8613", {"start": v(43.05, -9.72) * mm, "end": v(43.17, -9.7) * mm});
            skLineSegment(sketch, "E8614", {"start": v(43.17, -9.7) * mm, "end": v(43.29, -9.7) * mm});
            skLineSegment(sketch, "E8615", {"start": v(43.29, -9.7) * mm, "end": v(43.41, -9.68) * mm});
            skLineSegment(sketch, "E8616", {"start": v(43.41, -9.68) * mm, "end": v(43.54, -9.67) * mm});
            skLineSegment(sketch, "E8617", {"start": v(43.54, -9.67) * mm, "end": v(43.67, -9.65) * mm});
            skLineSegment(sketch, "E8618", {"start": v(43.67, -9.65) * mm, "end": v(43.79, -9.63) * mm});
            skLineSegment(sketch, "E8619", {"start": v(43.79, -9.63) * mm, "end": v(43.91, -9.62) * mm});
            skLineSegment(sketch, "E8620", {"start": v(43.91, -9.62) * mm, "end": v(44.02, -9.6) * mm});
            skLineSegment(sketch, "E8621", {"start": v(44.02, -9.6) * mm, "end": v(44.13, -9.58) * mm});
            skLineSegment(sketch, "E8622", {"start": v(44.13, -9.58) * mm, "end": v(44.25, -9.56) * mm});
            skLineSegment(sketch, "E8623", {"start": v(44.25, -9.56) * mm, "end": v(44.36, -9.54) * mm});
            skLineSegment(sketch, "E8624", {"start": v(44.36, -9.54) * mm, "end": v(44.48, -9.52) * mm});
            skLineSegment(sketch, "E8625", {"start": v(44.48, -9.52) * mm, "end": v(44.6, -9.5) * mm});
            skLineSegment(sketch, "E8626", {"start": v(44.6, -9.5) * mm, "end": v(44.72, -9.48) * mm});
            skLineSegment(sketch, "E8627", {"start": v(44.72, -9.48) * mm, "end": v(44.85, -9.45) * mm});
            skLineSegment(sketch, "E8628", {"start": v(44.85, -9.45) * mm, "end": v(44.97, -9.43) * mm});
            skLineSegment(sketch, "E8629", {"start": v(44.97, -9.43) * mm, "end": v(44.97, -9.43) * mm});
            skLineSegment(sketch, "E8630", {"start": v(44.97, -9.43) * mm, "end": v(45, -9.3) * mm});
            skLineSegment(sketch, "E8631", {"start": v(45, -9.3) * mm, "end": v(45.02, -9.2) * mm});
            skLineSegment(sketch, "E8632", {"start": v(45.02, -9.2) * mm, "end": v(45.04, -9.09) * mm});
            skLineSegment(sketch, "E8633", {"start": v(45.04, -9.09) * mm, "end": v(45.07, -8.97) * mm});
            skLineSegment(sketch, "E8634", {"start": v(45.07, -8.97) * mm, "end": v(45.09, -8.87) * mm});
            skLineSegment(sketch, "E8635", {"start": v(45.09, -8.87) * mm, "end": v(44.99, -8.8) * mm});
            skLineSegment(sketch, "E8636", {"start": v(44.99, -8.8) * mm, "end": v(44.89, -8.74) * mm});
            skLineSegment(sketch, "E8637", {"start": v(44.89, -8.74) * mm, "end": v(44.79, -8.67) * mm});
            skLineSegment(sketch, "E8638", {"start": v(44.79, -8.67) * mm, "end": v(44.7, -8.6) * mm});
            skLineSegment(sketch, "E8639", {"start": v(44.7, -8.6) * mm, "end": v(44.6, -8.54) * mm});
            skLineSegment(sketch, "E8640", {"start": v(44.6, -8.54) * mm, "end": v(44.5, -8.48) * mm});
            skLineSegment(sketch, "E8641", {"start": v(44.5, -8.48) * mm, "end": v(44.4, -8.41) * mm});
            skLineSegment(sketch, "E8642", {"start": v(44.4, -8.41) * mm, "end": v(44.3, -8.35) * mm});
            skLineSegment(sketch, "E8643", {"start": v(44.3, -8.35) * mm, "end": v(44.19, -8.29) * mm});
            skLineSegment(sketch, "E8644", {"start": v(44.19, -8.29) * mm, "end": v(44.08, -8.22) * mm});
            skLineSegment(sketch, "E8645", {"start": v(44.08, -8.22) * mm, "end": v(43.98, -8.16) * mm});
            skLineSegment(sketch, "E8646", {"start": v(43.98, -8.16) * mm, "end": v(43.87, -8.1) * mm});
            skLineSegment(sketch, "E8647", {"start": v(43.87, -8.1) * mm, "end": v(43.77, -8.04) * mm});
            skLineSegment(sketch, "E8648", {"start": v(43.77, -8.04) * mm, "end": v(43.67, -7.98) * mm});
            skLineSegment(sketch, "E8649", {"start": v(43.67, -7.98) * mm, "end": v(43.56, -7.93) * mm});
            skLineSegment(sketch, "E8650", {"start": v(43.56, -7.93) * mm, "end": v(43.46, -7.87) * mm});
            skLineSegment(sketch, "E8651", {"start": v(43.46, -7.87) * mm, "end": v(43.35, -7.81) * mm});
            skLineSegment(sketch, "E8652", {"start": v(43.35, -7.81) * mm, "end": v(43.24, -7.76) * mm});
            skLineSegment(sketch, "E8653", {"start": v(43.24, -7.76) * mm, "end": v(43.13, -7.7) * mm});
            skLineSegment(sketch, "E8654", {"start": v(43.13, -7.7) * mm, "end": v(43.15, -7.58) * mm});
            skLineSegment(sketch, "E8655", {"start": v(43.15, -7.58) * mm, "end": v(43.17, -7.47) * mm});
            skLineSegment(sketch, "E8656", {"start": v(43.17, -7.47) * mm, "end": v(43.19, -7.35) * mm});
            skLineSegment(sketch, "E8657", {"start": v(43.19, -7.35) * mm, "end": v(43.2, -7.23) * mm});
            skLineSegment(sketch, "E8658", {"start": v(43.2, -7.23) * mm, "end": v(43.23, -7.12) * mm});
            skLineSegment(sketch, "E8659", {"start": v(43.23, -7.12) * mm, "end": v(43.25, -7) * mm});
            skLineSegment(sketch, "E8660", {"start": v(43.25, -7) * mm, "end": v(43.27, -6.88) * mm});
            skLineSegment(sketch, "E8661", {"start": v(43.27, -6.88) * mm, "end": v(43.27, -6.87) * mm});
            skLineSegment(sketch, "E8662", {"start": v(43.27, -6.87) * mm, "end": v(43.38, -6.85) * mm});
            skLineSegment(sketch, "E8663", {"start": v(43.38, -6.85) * mm, "end": v(43.49, -6.84) * mm});
            skLineSegment(sketch, "E8664", {"start": v(43.49, -6.84) * mm, "end": v(43.6, -6.82) * mm});
            skLineSegment(sketch, "E8665", {"start": v(43.6, -6.82) * mm, "end": v(43.72, -6.8) * mm});
            skLineSegment(sketch, "E8666", {"start": v(43.72, -6.8) * mm, "end": v(43.84, -6.78) * mm});
            skLineSegment(sketch, "E8667", {"start": v(43.84, -6.78) * mm, "end": v(43.96, -6.76) * mm});
            skLineSegment(sketch, "E8668", {"start": v(43.96, -6.76) * mm, "end": v(44.09, -6.74) * mm});
            skLineSegment(sketch, "E8669", {"start": v(44.09, -6.74) * mm, "end": v(44.22, -6.71) * mm});
            skLineSegment(sketch, "E8670", {"start": v(44.22, -6.71) * mm, "end": v(44.33, -6.69) * mm});
            skLineSegment(sketch, "E8671", {"start": v(44.33, -6.69) * mm, "end": v(44.46, -6.66) * mm});
            skLineSegment(sketch, "E8672", {"start": v(44.46, -6.66) * mm, "end": v(44.56, -6.64) * mm});
            skLineSegment(sketch, "E8673", {"start": v(44.56, -6.64) * mm, "end": v(44.68, -6.61) * mm});
            skLineSegment(sketch, "E8674", {"start": v(44.68, -6.61) * mm, "end": v(44.79, -6.59) * mm});
            skLineSegment(sketch, "E8675", {"start": v(44.79, -6.59) * mm, "end": v(44.9, -6.56) * mm});
            skLineSegment(sketch, "E8676", {"start": v(44.9, -6.56) * mm, "end": v(45.02, -6.53) * mm});
            skLineSegment(sketch, "E8677", {"start": v(45.02, -6.53) * mm, "end": v(45.14, -6.5) * mm});
            skLineSegment(sketch, "E8678", {"start": v(45.14, -6.5) * mm, "end": v(45.26, -6.47) * mm});
            skLineSegment(sketch, "E8679", {"start": v(45.26, -6.47) * mm, "end": v(45.38, -6.44) * mm});
            skLineSegment(sketch, "E8680", {"start": v(45.38, -6.44) * mm, "end": v(45.5, -6.4) * mm});
            skLineSegment(sketch, "E8681", {"start": v(45.5, -6.4) * mm, "end": v(45.5, -6.4) * mm});
            skLineSegment(sketch, "E8682", {"start": v(45.5, -6.4) * mm, "end": v(45.52, -6.28) * mm});
            skLineSegment(sketch, "E8683", {"start": v(45.52, -6.28) * mm, "end": v(45.54, -6.16) * mm});
            skLineSegment(sketch, "E8684", {"start": v(45.54, -6.16) * mm, "end": v(45.55, -6.06) * mm});
            skLineSegment(sketch, "E8685", {"start": v(45.55, -6.06) * mm, "end": v(45.57, -5.94) * mm});
            skLineSegment(sketch, "E8686", {"start": v(45.57, -5.94) * mm, "end": v(45.58, -5.84) * mm});
            skLineSegment(sketch, "E8687", {"start": v(45.58, -5.84) * mm, "end": v(45.48, -5.78) * mm});
            skLineSegment(sketch, "E8688", {"start": v(45.48, -5.78) * mm, "end": v(45.37, -5.72) * mm});
            skLineSegment(sketch, "E8689", {"start": v(45.37, -5.72) * mm, "end": v(45.27, -5.66) * mm});
            skLineSegment(sketch, "E8690", {"start": v(45.27, -5.66) * mm, "end": v(45.17, -5.6) * mm});
            skLineSegment(sketch, "E8691", {"start": v(45.17, -5.6) * mm, "end": v(45.06, -5.54) * mm});
            skLineSegment(sketch, "E8692", {"start": v(45.06, -5.54) * mm, "end": v(44.96, -5.49) * mm});
            skLineSegment(sketch, "E8693", {"start": v(44.96, -5.49) * mm, "end": v(44.85, -5.43) * mm});
            skLineSegment(sketch, "E8694", {"start": v(44.85, -5.43) * mm, "end": v(44.75, -5.37) * mm});
            skLineSegment(sketch, "E8695", {"start": v(44.75, -5.37) * mm, "end": v(44.64, -5.32) * mm});
            skLineSegment(sketch, "E8696", {"start": v(44.64, -5.32) * mm, "end": v(44.53, -5.26) * mm});
            skLineSegment(sketch, "E8697", {"start": v(44.53, -5.26) * mm, "end": v(44.42, -5.2) * mm});
            skLineSegment(sketch, "E8698", {"start": v(44.42, -5.2) * mm, "end": v(44.32, -5.15) * mm});
            skLineSegment(sketch, "E8699", {"start": v(44.32, -5.15) * mm, "end": v(44.2, -5.1) * mm});
            skLineSegment(sketch, "E8700", {"start": v(44.2, -5.1) * mm, "end": v(44.1, -5.05) * mm});
            skLineSegment(sketch, "E8701", {"start": v(44.1, -5.05) * mm, "end": v(44, -5) * mm});
            skLineSegment(sketch, "E8702", {"start": v(44, -5) * mm, "end": v(43.88, -4.95) * mm});
            skLineSegment(sketch, "E8703", {"start": v(43.88, -4.95) * mm, "end": v(43.78, -4.9) * mm});
            skLineSegment(sketch, "E8704", {"start": v(43.78, -4.9) * mm, "end": v(43.67, -4.85) * mm});
            skLineSegment(sketch, "E8705", {"start": v(43.67, -4.85) * mm, "end": v(43.55, -4.8) * mm});
            skLineSegment(sketch, "E8706", {"start": v(43.55, -4.8) * mm, "end": v(43.56, -4.68) * mm});
            skLineSegment(sketch, "E8707", {"start": v(43.56, -4.68) * mm, "end": v(43.57, -4.57) * mm});
            skLineSegment(sketch, "E8708", {"start": v(43.57, -4.57) * mm, "end": v(43.58, -4.45) * mm});
            skLineSegment(sketch, "E8709", {"start": v(43.58, -4.45) * mm, "end": v(43.6, -4.33) * mm});
            skLineSegment(sketch, "E8710", {"start": v(43.6, -4.33) * mm, "end": v(43.6, -4.21) * mm});
            skLineSegment(sketch, "E8711", {"start": v(43.6, -4.21) * mm, "end": v(43.62, -4.1) * mm});
            skLineSegment(sketch, "E8712", {"start": v(43.62, -4.1) * mm, "end": v(43.63, -3.98) * mm});
            skLineSegment(sketch, "E8713", {"start": v(43.63, -3.98) * mm, "end": v(43.63, -3.96) * mm});
            skLineSegment(sketch, "E8714", {"start": v(43.63, -3.96) * mm, "end": v(43.74, -3.94) * mm});
            skLineSegment(sketch, "E8715", {"start": v(43.74, -3.94) * mm, "end": v(43.85, -3.92) * mm});
            skLineSegment(sketch, "E8716", {"start": v(43.85, -3.92) * mm, "end": v(43.96, -3.9) * mm});
            skLineSegment(sketch, "E8717", {"start": v(43.96, -3.9) * mm, "end": v(44.08, -3.87) * mm});
            skLineSegment(sketch, "E8718", {"start": v(44.08, -3.87) * mm, "end": v(44.2, -3.84) * mm});
            skLineSegment(sketch, "E8719", {"start": v(44.2, -3.84) * mm, "end": v(44.32, -3.8) * mm});
            skLineSegment(sketch, "E8720", {"start": v(44.32, -3.8) * mm, "end": v(44.44, -3.78) * mm});
            skLineSegment(sketch, "E8721", {"start": v(44.44, -3.78) * mm, "end": v(44.57, -3.74) * mm});
            skLineSegment(sketch, "E8722", {"start": v(44.57, -3.74) * mm, "end": v(44.68, -3.71) * mm});
            skLineSegment(sketch, "E8723", {"start": v(44.68, -3.71) * mm, "end": v(44.8, -3.68) * mm});
            skLineSegment(sketch, "E8724", {"start": v(44.8, -3.68) * mm, "end": v(44.9, -3.65) * mm});
            skLineSegment(sketch, "E8725", {"start": v(44.9, -3.65) * mm, "end": v(45.02, -3.61) * mm});
            skLineSegment(sketch, "E8726", {"start": v(45.02, -3.61) * mm, "end": v(45.13, -3.58) * mm});
            skLineSegment(sketch, "E8727", {"start": v(45.13, -3.58) * mm, "end": v(45.24, -3.55) * mm});
            skLineSegment(sketch, "E8728", {"start": v(45.24, -3.55) * mm, "end": v(45.36, -3.5) * mm});
            skLineSegment(sketch, "E8729", {"start": v(45.36, -3.5) * mm, "end": v(45.47, -3.47) * mm});
            skLineSegment(sketch, "E8730", {"start": v(45.47, -3.47) * mm, "end": v(45.59, -3.43) * mm});
            skLineSegment(sketch, "E8731", {"start": v(45.59, -3.43) * mm, "end": v(45.7, -3.4) * mm});
            skLineSegment(sketch, "E8732", {"start": v(45.7, -3.4) * mm, "end": v(45.83, -3.35) * mm});
            skLineSegment(sketch, "E8733", {"start": v(45.83, -3.35) * mm, "end": v(45.83, -3.35) * mm});
            skLineSegment(sketch, "E8734", {"start": v(45.83, -3.35) * mm, "end": v(45.84, -3.23) * mm});
            skLineSegment(sketch, "E8735", {"start": v(45.84, -3.23) * mm, "end": v(45.85, -3.1) * mm});
            skLineSegment(sketch, "E8736", {"start": v(45.85, -3.1) * mm, "end": v(45.85, -3) * mm});
            skLineSegment(sketch, "E8737", {"start": v(45.85, -3) * mm, "end": v(45.86, -2.88) * mm});
            skLineSegment(sketch, "E8738", {"start": v(45.86, -2.88) * mm, "end": v(45.87, -2.78) * mm});
            skLineSegment(sketch, "E8739", {"start": v(45.87, -2.78) * mm, "end": v(45.76, -2.73) * mm});
            skLineSegment(sketch, "E8740", {"start": v(45.76, -2.73) * mm, "end": v(45.65, -2.68) * mm});
            skLineSegment(sketch, "E8741", {"start": v(45.65, -2.68) * mm, "end": v(45.54, -2.62) * mm});
            skLineSegment(sketch, "E8742", {"start": v(45.54, -2.62) * mm, "end": v(45.44, -2.57) * mm});
            skLineSegment(sketch, "E8743", {"start": v(45.44, -2.57) * mm, "end": v(45.33, -2.52) * mm});
            skLineSegment(sketch, "E8744", {"start": v(45.33, -2.52) * mm, "end": v(45.23, -2.47) * mm});
            skLineSegment(sketch, "E8745", {"start": v(45.23, -2.47) * mm, "end": v(45.12, -2.42) * mm});
            skLineSegment(sketch, "E8746", {"start": v(45.12, -2.42) * mm, "end": v(45, -2.37) * mm});
            skLineSegment(sketch, "E8747", {"start": v(45, -2.37) * mm, "end": v(44.9, -2.32) * mm});
            skLineSegment(sketch, "E8748", {"start": v(44.9, -2.32) * mm, "end": v(44.78, -2.27) * mm});
            skLineSegment(sketch, "E8749", {"start": v(44.78, -2.27) * mm, "end": v(44.67, -2.23) * mm});
            skLineSegment(sketch, "E8750", {"start": v(44.67, -2.23) * mm, "end": v(44.56, -2.18) * mm});
            skLineSegment(sketch, "E8751", {"start": v(44.56, -2.18) * mm, "end": v(44.45, -2.14) * mm});
            skLineSegment(sketch, "E8752", {"start": v(44.45, -2.14) * mm, "end": v(44.34, -2.1) * mm});
            skLineSegment(sketch, "E8753", {"start": v(44.34, -2.1) * mm, "end": v(44.23, -2.05) * mm});
            skLineSegment(sketch, "E8754", {"start": v(44.23, -2.05) * mm, "end": v(44.12, -2) * mm});
            skLineSegment(sketch, "E8755", {"start": v(44.12, -2) * mm, "end": v(44, -1.97) * mm});
            skLineSegment(sketch, "E8756", {"start": v(44, -1.97) * mm, "end": v(43.9, -1.93) * mm});
            skLineSegment(sketch, "E8757", {"start": v(43.9, -1.93) * mm, "end": v(43.77, -1.88) * mm});
            skLineSegment(sketch, "E8758", {"start": v(43.77, -1.88) * mm, "end": v(43.77, -1.76) * mm});
            skLineSegment(sketch, "E8759", {"start": v(43.77, -1.76) * mm, "end": v(43.78, -1.65) * mm});
            skLineSegment(sketch, "E8760", {"start": v(43.78, -1.65) * mm, "end": v(43.78, -1.53) * mm});
            skLineSegment(sketch, "E8761", {"start": v(43.78, -1.53) * mm, "end": v(43.79, -1.4) * mm});
            skLineSegment(sketch, "E8762", {"start": v(43.79, -1.4) * mm, "end": v(43.8, -1.3) * mm});
            skLineSegment(sketch, "E8763", {"start": v(43.8, -1.3) * mm, "end": v(43.8, -1.17) * mm});
            skLineSegment(sketch, "E8764", {"start": v(43.8, -1.17) * mm, "end": v(43.8, -1.05) * mm});
            skLineSegment(sketch, "E8765", {"start": v(43.8, -1.05) * mm, "end": v(43.8, -1.04) * mm});
            skSolve(sketch);
        }
        {
            var Q0;
            Q0=qSketchRegion(id+"F14",true);
            extrude(context, id + "F15", {"entities" : qUnion([Q0]), "endBound" : BoundingType.SYMMETRIC, "depth" : 5 * mm, "offsetDistance" : 25 * mm});
        }
        {
            var Q0;
            Q0=makeQuery(id+"F15.opExtrude","SWEPT_BODY",BODY,{"disambiguationData":[OSD([sQuery(id+"F14.wireOp",EDGE,"E3748"),sQuery(id+"F14.wireOp",EDGE,"E3749"),sQuery(id+"F14.wireOp",EDGE,"E3750"),sQuery(id+"F14.wireOp",EDGE,"E3751"),sQuery(id+"F14.wireOp",EDGE,"E3752"),sQuery(id+"F14.wireOp",EDGE,"E3753"),sQuery(id+"F14.wireOp",EDGE,"E3754"),sQuery(id+"F14.wireOp",EDGE,"E3755"),sQuery(id+"F14.wireOp",EDGE,"E3756"),sQuery(id+"F14.wireOp",EDGE,"E3757"),sQuery(id+"F14.wireOp",EDGE,"E3758"),sQuery(id+"F14.wireOp",EDGE,"E3759"),sQuery(id+"F14.wireOp",EDGE,"E3760"),sQuery(id+"F14.wireOp",EDGE,"E3761"),sQuery(id+"F14.wireOp",EDGE,"E3762"),sQuery(id+"F14.wireOp",EDGE,"E3763"),sQuery(id+"F14.wireOp",EDGE,"E3764"),sQuery(id+"F14.wireOp",EDGE,"E3765"),sQuery(id+"F14.wireOp",EDGE,"E3766"),sQuery(id+"F14.wireOp",EDGE,"E3767"),sQuery(id+"F14.wireOp",EDGE,"E3768"),sQuery(id+"F14.wireOp",EDGE,"E3769"),sQuery(id+"F14.wireOp",EDGE,"E3770"),sQuery(id+"F14.wireOp",EDGE,"E3771"),sQuery(id+"F14.wireOp",EDGE,"E3772"),sQuery(id+"F14.wireOp",EDGE,"E3773"),sQuery(id+"F14.wireOp",EDGE,"E3774"),sQuery(id+"F14.wireOp",EDGE,"E3775"),sQuery(id+"F14.wireOp",EDGE,"E3776"),sQuery(id+"F14.wireOp",EDGE,"E3777"),sQuery(id+"F14.wireOp",EDGE,"E3778"),sQuery(id+"F14.wireOp",EDGE,"E3779"),sQuery(id+"F14.wireOp",EDGE,"E3780"),sQuery(id+"F14.wireOp",EDGE,"E3781"),sQuery(id+"F14.wireOp",EDGE,"E3782"),sQuery(id+"F14.wireOp",EDGE,"E3783"),sQuery(id+"F14.wireOp",EDGE,"E3784"),sQuery(id+"F14.wireOp",EDGE,"E3785"),sQuery(id+"F14.wireOp",EDGE,"E3786"),sQuery(id+"F14.wireOp",EDGE,"E3787"),sQuery(id+"F14.wireOp",EDGE,"E3788"),sQuery(id+"F14.wireOp",EDGE,"E3789"),sQuery(id+"F14.wireOp",EDGE,"E3790"),sQuery(id+"F14.wireOp",EDGE,"E3791"),sQuery(id+"F14.wireOp",EDGE,"E3792"),sQuery(id+"F14.wireOp",EDGE,"E3793"),sQuery(id+"F14.wireOp",EDGE,"E3794"),sQuery(id+"F14.wireOp",EDGE,"E3795"),sQuery(id+"F14.wireOp",EDGE,"E3796"),sQuery(id+"F14.wireOp",EDGE,"E3797"),sQuery(id+"F14.wireOp",EDGE,"E3798"),sQuery(id+"F14.wireOp",EDGE,"E3799"),sQuery(id+"F14.wireOp",EDGE,"E3800"),sQuery(id+"F14.wireOp",EDGE,"E3801"),sQuery(id+"F14.wireOp",EDGE,"E3802"),sQuery(id+"F14.wireOp",EDGE,"E3803"),sQuery(id+"F14.wireOp",EDGE,"E3804"),sQuery(id+"F14.wireOp",EDGE,"E3805"),sQuery(id+"F14.wireOp",EDGE,"E3806"),sQuery(id+"F14.wireOp",EDGE,"E3807"),sQuery(id+"F14.wireOp",EDGE,"E3808"),sQuery(id+"F14.wireOp",EDGE,"E3809"),sQuery(id+"F14.wireOp",EDGE,"E3810"),sQuery(id+"F14.wireOp",EDGE,"E3811"),sQuery(id+"F14.wireOp",EDGE,"E3812"),sQuery(id+"F14.wireOp",EDGE,"E3813"),sQuery(id+"F14.wireOp",EDGE,"E3814"),sQuery(id+"F14.wireOp",EDGE,"E3815"),sQuery(id+"F14.wireOp",EDGE,"E3816"),sQuery(id+"F14.wireOp",EDGE,"E3817"),sQuery(id+"F14.wireOp",EDGE,"E3818"),sQuery(id+"F14.wireOp",EDGE,"E3819"),sQuery(id+"F14.wireOp",EDGE,"E3820"),sQuery(id+"F14.wireOp",EDGE,"E3821"),sQuery(id+"F14.wireOp",EDGE,"E3822"),sQuery(id+"F14.wireOp",EDGE,"E3823"),sQuery(id+"F14.wireOp",EDGE,"E3824"),sQuery(id+"F14.wireOp",EDGE,"E3825"),sQuery(id+"F14.wireOp",EDGE,"E3826"),sQuery(id+"F14.wireOp",EDGE,"E3827"),sQuery(id+"F14.wireOp",EDGE,"E3828"),sQuery(id+"F14.wireOp",EDGE,"E3829"),sQuery(id+"F14.wireOp",EDGE,"E3830"),sQuery(id+"F14.wireOp",EDGE,"E3831"),sQuery(id+"F14.wireOp",EDGE,"E3832"),sQuery(id+"F14.wireOp",EDGE,"E3833"),sQuery(id+"F14.wireOp",EDGE,"E3834"),sQuery(id+"F14.wireOp",EDGE,"E3835"),sQuery(id+"F14.wireOp",EDGE,"E3836"),sQuery(id+"F14.wireOp",EDGE,"E3837"),sQuery(id+"F14.wireOp",EDGE,"E3838"),sQuery(id+"F14.wireOp",EDGE,"E3839"),sQuery(id+"F14.wireOp",EDGE,"E3840"),sQuery(id+"F14.wireOp",EDGE,"E3841"),sQuery(id+"F14.wireOp",EDGE,"E3842"),sQuery(id+"F14.wireOp",EDGE,"E3843"),sQuery(id+"F14.wireOp",EDGE,"E3844"),sQuery(id+"F14.wireOp",EDGE,"E3845"),sQuery(id+"F14.wireOp",EDGE,"E3846"),sQuery(id+"F14.wireOp",EDGE,"E3847"),sQuery(id+"F14.wireOp",EDGE,"E3848"),sQuery(id+"F14.wireOp",EDGE,"E3849"),sQuery(id+"F14.wireOp",EDGE,"E3850"),sQuery(id+"F14.wireOp",EDGE,"E3851"),sQuery(id+"F14.wireOp",EDGE,"E3852"),sQuery(id+"F14.wireOp",EDGE,"E3853"),sQuery(id+"F14.wireOp",EDGE,"E3854"),sQuery(id+"F14.wireOp",EDGE,"E3855"),sQuery(id+"F14.wireOp",EDGE,"E3856"),sQuery(id+"F14.wireOp",EDGE,"E3857"),sQuery(id+"F14.wireOp",EDGE,"E3858"),sQuery(id+"F14.wireOp",EDGE,"E3859"),sQuery(id+"F14.wireOp",EDGE,"E3860"),sQuery(id+"F14.wireOp",EDGE,"E3861"),sQuery(id+"F14.wireOp",EDGE,"E3862"),sQuery(id+"F14.wireOp",EDGE,"E3863"),sQuery(id+"F14.wireOp",EDGE,"E3864"),sQuery(id+"F14.wireOp",EDGE,"E3865"),sQuery(id+"F14.wireOp",EDGE,"E3866"),sQuery(id+"F14.wireOp",EDGE,"E3867"),sQuery(id+"F14.wireOp",EDGE,"E3868"),sQuery(id+"F14.wireOp",EDGE,"E3869"),sQuery(id+"F14.wireOp",EDGE,"E3870"),sQuery(id+"F14.wireOp",EDGE,"E3871"),sQuery(id+"F14.wireOp",EDGE,"E3872"),sQuery(id+"F14.wireOp",EDGE,"E3873"),sQuery(id+"F14.wireOp",EDGE,"E3874"),sQuery(id+"F14.wireOp",EDGE,"E3875"),sQuery(id+"F14.wireOp",EDGE,"E3876"),sQuery(id+"F14.wireOp",EDGE,"E3877"),sQuery(id+"F14.wireOp",EDGE,"E3878"),sQuery(id+"F14.wireOp",EDGE,"E3879"),sQuery(id+"F14.wireOp",EDGE,"E3880"),sQuery(id+"F14.wireOp",EDGE,"E3881"),sQuery(id+"F14.wireOp",EDGE,"E3882"),sQuery(id+"F14.wireOp",EDGE,"E3883"),sQuery(id+"F14.wireOp",EDGE,"E3884"),sQuery(id+"F14.wireOp",EDGE,"E3885"),sQuery(id+"F14.wireOp",EDGE,"E3886"),sQuery(id+"F14.wireOp",EDGE,"E3887"),sQuery(id+"F14.wireOp",EDGE,"E3888"),sQuery(id+"F14.wireOp",EDGE,"E3889"),sQuery(id+"F14.wireOp",EDGE,"E3890"),sQuery(id+"F14.wireOp",EDGE,"E3891"),sQuery(id+"F14.wireOp",EDGE,"E3892"),sQuery(id+"F14.wireOp",EDGE,"E3893"),sQuery(id+"F14.wireOp",EDGE,"E3894"),sQuery(id+"F14.wireOp",EDGE,"E3895"),sQuery(id+"F14.wireOp",EDGE,"E3896"),sQuery(id+"F14.wireOp",EDGE,"E3897"),sQuery(id+"F14.wireOp",EDGE,"E3898"),sQuery(id+"F14.wireOp",EDGE,"E3899"),sQuery(id+"F14.wireOp",EDGE,"E3900"),sQuery(id+"F14.wireOp",EDGE,"E3901"),sQuery(id+"F14.wireOp",EDGE,"E3902"),sQuery(id+"F14.wireOp",EDGE,"E3903"),sQuery(id+"F14.wireOp",EDGE,"E3904"),sQuery(id+"F14.wireOp",EDGE,"E3905"),sQuery(id+"F14.wireOp",EDGE,"E3906"),sQuery(id+"F14.wireOp",EDGE,"E3907"),sQuery(id+"F14.wireOp",EDGE,"E3908"),sQuery(id+"F14.wireOp",EDGE,"E3909"),sQuery(id+"F14.wireOp",EDGE,"E3910"),sQuery(id+"F14.wireOp",EDGE,"E3911"),sQuery(id+"F14.wireOp",EDGE,"E3912"),sQuery(id+"F14.wireOp",EDGE,"E3913"),sQuery(id+"F14.wireOp",EDGE,"E3914"),sQuery(id+"F14.wireOp",EDGE,"E3915"),sQuery(id+"F14.wireOp",EDGE,"E3916"),sQuery(id+"F14.wireOp",EDGE,"E3917"),sQuery(id+"F14.wireOp",EDGE,"E3918"),sQuery(id+"F14.wireOp",EDGE,"E3919"),sQuery(id+"F14.wireOp",EDGE,"E3920"),sQuery(id+"F14.wireOp",EDGE,"E3921"),sQuery(id+"F14.wireOp",EDGE,"E3922"),sQuery(id+"F14.wireOp",EDGE,"E3923"),sQuery(id+"F14.wireOp",EDGE,"E3924"),sQuery(id+"F14.wireOp",EDGE,"E3925"),sQuery(id+"F14.wireOp",EDGE,"E3926"),sQuery(id+"F14.wireOp",EDGE,"E3927"),sQuery(id+"F14.wireOp",EDGE,"E3928"),sQuery(id+"F14.wireOp",EDGE,"E3929"),sQuery(id+"F14.wireOp",EDGE,"E3930"),sQuery(id+"F14.wireOp",EDGE,"E3931"),sQuery(id+"F14.wireOp",EDGE,"E3932"),sQuery(id+"F14.wireOp",EDGE,"E3933"),sQuery(id+"F14.wireOp",EDGE,"E3934"),sQuery(id+"F14.wireOp",EDGE,"E3935"),sQuery(id+"F14.wireOp",EDGE,"E3936"),sQuery(id+"F14.wireOp",EDGE,"E3937"),sQuery(id+"F14.wireOp",EDGE,"E3938"),sQuery(id+"F14.wireOp",EDGE,"E3939"),sQuery(id+"F14.wireOp",EDGE,"E3940"),sQuery(id+"F14.wireOp",EDGE,"E3941"),sQuery(id+"F14.wireOp",EDGE,"E3942"),sQuery(id+"F14.wireOp",EDGE,"E3943"),sQuery(id+"F14.wireOp",EDGE,"E3944"),sQuery(id+"F14.wireOp",EDGE,"E3945"),sQuery(id+"F14.wireOp",EDGE,"E3946"),sQuery(id+"F14.wireOp",EDGE,"E3947"),sQuery(id+"F14.wireOp",EDGE,"E3948"),sQuery(id+"F14.wireOp",EDGE,"E3949"),sQuery(id+"F14.wireOp",EDGE,"E3950"),sQuery(id+"F14.wireOp",EDGE,"E3951"),sQuery(id+"F14.wireOp",EDGE,"E3952"),sQuery(id+"F14.wireOp",EDGE,"E3953"),sQuery(id+"F14.wireOp",EDGE,"E3954"),sQuery(id+"F14.wireOp",EDGE,"E3955"),sQuery(id+"F14.wireOp",EDGE,"E3956"),sQuery(id+"F14.wireOp",EDGE,"E3957"),sQuery(id+"F14.wireOp",EDGE,"E3958"),sQuery(id+"F14.wireOp",EDGE,"E3959"),sQuery(id+"F14.wireOp",EDGE,"E3960"),sQuery(id+"F14.wireOp",EDGE,"E3961"),sQuery(id+"F14.wireOp",EDGE,"E3962"),sQuery(id+"F14.wireOp",EDGE,"E3963"),sQuery(id+"F14.wireOp",EDGE,"E3964"),sQuery(id+"F14.wireOp",EDGE,"E3965"),sQuery(id+"F14.wireOp",EDGE,"E3966"),sQuery(id+"F14.wireOp",EDGE,"E3967"),sQuery(id+"F14.wireOp",EDGE,"E3968"),sQuery(id+"F14.wireOp",EDGE,"E3969"),sQuery(id+"F14.wireOp",EDGE,"E3970"),sQuery(id+"F14.wireOp",EDGE,"E3971"),sQuery(id+"F14.wireOp",EDGE,"E3972"),sQuery(id+"F14.wireOp",EDGE,"E3973"),sQuery(id+"F14.wireOp",EDGE,"E3974"),sQuery(id+"F14.wireOp",EDGE,"E3975"),sQuery(id+"F14.wireOp",EDGE,"E3976"),sQuery(id+"F14.wireOp",EDGE,"E3977"),sQuery(id+"F14.wireOp",EDGE,"E3978"),sQuery(id+"F14.wireOp",EDGE,"E3979"),sQuery(id+"F14.wireOp",EDGE,"E3980"),sQuery(id+"F14.wireOp",EDGE,"E3981"),sQuery(id+"F14.wireOp",EDGE,"E3982"),sQuery(id+"F14.wireOp",EDGE,"E3983"),sQuery(id+"F14.wireOp",EDGE,"E3984"),sQuery(id+"F14.wireOp",EDGE,"E3985"),sQuery(id+"F14.wireOp",EDGE,"E3986"),sQuery(id+"F14.wireOp",EDGE,"E3987"),sQuery(id+"F14.wireOp",EDGE,"E3988"),sQuery(id+"F14.wireOp",EDGE,"E3989"),sQuery(id+"F14.wireOp",EDGE,"E3990"),sQuery(id+"F14.wireOp",EDGE,"E3991"),sQuery(id+"F14.wireOp",EDGE,"E3992"),sQuery(id+"F14.wireOp",EDGE,"E3993"),sQuery(id+"F14.wireOp",EDGE,"E3994"),sQuery(id+"F14.wireOp",EDGE,"E3995"),sQuery(id+"F14.wireOp",EDGE,"E3996"),sQuery(id+"F14.wireOp",EDGE,"E3997"),sQuery(id+"F14.wireOp",EDGE,"E3998"),sQuery(id+"F14.wireOp",EDGE,"E3999"),sQuery(id+"F14.wireOp",EDGE,"E4000"),sQuery(id+"F14.wireOp",EDGE,"E4001"),sQuery(id+"F14.wireOp",EDGE,"E4002"),sQuery(id+"F14.wireOp",EDGE,"E4003"),sQuery(id+"F14.wireOp",EDGE,"E4004"),sQuery(id+"F14.wireOp",EDGE,"E4005"),sQuery(id+"F14.wireOp",EDGE,"E4006"),sQuery(id+"F14.wireOp",EDGE,"E4007"),sQuery(id+"F14.wireOp",EDGE,"E4008"),sQuery(id+"F14.wireOp",EDGE,"E4009"),sQuery(id+"F14.wireOp",EDGE,"E4010"),sQuery(id+"F14.wireOp",EDGE,"E4011"),sQuery(id+"F14.wireOp",EDGE,"E4012"),sQuery(id+"F14.wireOp",EDGE,"E4013"),sQuery(id+"F14.wireOp",EDGE,"E4014"),sQuery(id+"F14.wireOp",EDGE,"E4015"),sQuery(id+"F14.wireOp",EDGE,"E4016"),sQuery(id+"F14.wireOp",EDGE,"E4017"),sQuery(id+"F14.wireOp",EDGE,"E4018"),sQuery(id+"F14.wireOp",EDGE,"E4019"),sQuery(id+"F14.wireOp",EDGE,"E4020"),sQuery(id+"F14.wireOp",EDGE,"E4021"),sQuery(id+"F14.wireOp",EDGE,"E4022"),sQuery(id+"F14.wireOp",EDGE,"E4023"),sQuery(id+"F14.wireOp",EDGE,"E4024"),sQuery(id+"F14.wireOp",EDGE,"E4025"),sQuery(id+"F14.wireOp",EDGE,"E4026"),sQuery(id+"F14.wireOp",EDGE,"E4027"),sQuery(id+"F14.wireOp",EDGE,"E4028"),sQuery(id+"F14.wireOp",EDGE,"E4029"),sQuery(id+"F14.wireOp",EDGE,"E4030"),sQuery(id+"F14.wireOp",EDGE,"E4031"),sQuery(id+"F14.wireOp",EDGE,"E4032"),sQuery(id+"F14.wireOp",EDGE,"E4033"),sQuery(id+"F14.wireOp",EDGE,"E4034"),sQuery(id+"F14.wireOp",EDGE,"E4035"),sQuery(id+"F14.wireOp",EDGE,"E4036"),sQuery(id+"F14.wireOp",EDGE,"E4037"),sQuery(id+"F14.wireOp",EDGE,"E4038"),sQuery(id+"F14.wireOp",EDGE,"E4039"),sQuery(id+"F14.wireOp",EDGE,"E4040"),sQuery(id+"F14.wireOp",EDGE,"E4041"),sQuery(id+"F14.wireOp",EDGE,"E4042"),sQuery(id+"F14.wireOp",EDGE,"E4043"),sQuery(id+"F14.wireOp",EDGE,"E4044"),sQuery(id+"F14.wireOp",EDGE,"E4045"),sQuery(id+"F14.wireOp",EDGE,"E4046"),sQuery(id+"F14.wireOp",EDGE,"E4047"),sQuery(id+"F14.wireOp",EDGE,"E4048"),sQuery(id+"F14.wireOp",EDGE,"E4049"),sQuery(id+"F14.wireOp",EDGE,"E4050"),sQuery(id+"F14.wireOp",EDGE,"E4051"),sQuery(id+"F14.wireOp",EDGE,"E4052"),sQuery(id+"F14.wireOp",EDGE,"E4053"),sQuery(id+"F14.wireOp",EDGE,"E4054"),sQuery(id+"F14.wireOp",EDGE,"E4055"),sQuery(id+"F14.wireOp",EDGE,"E4056"),sQuery(id+"F14.wireOp",EDGE,"E4057"),sQuery(id+"F14.wireOp",EDGE,"E4058"),sQuery(id+"F14.wireOp",EDGE,"E4059"),sQuery(id+"F14.wireOp",EDGE,"E4060"),sQuery(id+"F14.wireOp",EDGE,"E4061"),sQuery(id+"F14.wireOp",EDGE,"E4062"),sQuery(id+"F14.wireOp",EDGE,"E4063"),sQuery(id+"F14.wireOp",EDGE,"E4064"),sQuery(id+"F14.wireOp",EDGE,"E4065"),sQuery(id+"F14.wireOp",EDGE,"E4066"),sQuery(id+"F14.wireOp",EDGE,"E4067"),sQuery(id+"F14.wireOp",EDGE,"E4068"),sQuery(id+"F14.wireOp",EDGE,"E4069"),sQuery(id+"F14.wireOp",EDGE,"E4070"),sQuery(id+"F14.wireOp",EDGE,"E4071"),sQuery(id+"F14.wireOp",EDGE,"E4072"),sQuery(id+"F14.wireOp",EDGE,"E4073"),sQuery(id+"F14.wireOp",EDGE,"E4074"),sQuery(id+"F14.wireOp",EDGE,"E4075"),sQuery(id+"F14.wireOp",EDGE,"E4076"),sQuery(id+"F14.wireOp",EDGE,"E4077"),sQuery(id+"F14.wireOp",EDGE,"E4078"),sQuery(id+"F14.wireOp",EDGE,"E4079"),sQuery(id+"F14.wireOp",EDGE,"E4080"),sQuery(id+"F14.wireOp",EDGE,"E4081"),sQuery(id+"F14.wireOp",EDGE,"E4082"),sQuery(id+"F14.wireOp",EDGE,"E4083"),sQuery(id+"F14.wireOp",EDGE,"E4084"),sQuery(id+"F14.wireOp",EDGE,"E4085"),sQuery(id+"F14.wireOp",EDGE,"E4086"),sQuery(id+"F14.wireOp",EDGE,"E4087"),sQuery(id+"F14.wireOp",EDGE,"E4088"),sQuery(id+"F14.wireOp",EDGE,"E4089"),sQuery(id+"F14.wireOp",EDGE,"E4090"),sQuery(id+"F14.wireOp",EDGE,"E4091"),sQuery(id+"F14.wireOp",EDGE,"E4092"),sQuery(id+"F14.wireOp",EDGE,"E4093"),sQuery(id+"F14.wireOp",EDGE,"E4094"),sQuery(id+"F14.wireOp",EDGE,"E4095"),sQuery(id+"F14.wireOp",EDGE,"E4096"),sQuery(id+"F14.wireOp",EDGE,"E4097"),sQuery(id+"F14.wireOp",EDGE,"E4098"),sQuery(id+"F14.wireOp",EDGE,"E4099"),sQuery(id+"F14.wireOp",EDGE,"E4100"),sQuery(id+"F14.wireOp",EDGE,"E4101"),sQuery(id+"F14.wireOp",EDGE,"E4102"),sQuery(id+"F14.wireOp",EDGE,"E4103"),sQuery(id+"F14.wireOp",EDGE,"E4104"),sQuery(id+"F14.wireOp",EDGE,"E4105"),sQuery(id+"F14.wireOp",EDGE,"E4106"),sQuery(id+"F14.wireOp",EDGE,"E4107"),sQuery(id+"F14.wireOp",EDGE,"E4108"),sQuery(id+"F14.wireOp",EDGE,"E4109"),sQuery(id+"F14.wireOp",EDGE,"E4110"),sQuery(id+"F14.wireOp",EDGE,"E4111"),sQuery(id+"F14.wireOp",EDGE,"E4112"),sQuery(id+"F14.wireOp",EDGE,"E4113"),sQuery(id+"F14.wireOp",EDGE,"E4114"),sQuery(id+"F14.wireOp",EDGE,"E4115"),sQuery(id+"F14.wireOp",EDGE,"E4116"),sQuery(id+"F14.wireOp",EDGE,"E4117"),sQuery(id+"F14.wireOp",EDGE,"E4118"),sQuery(id+"F14.wireOp",EDGE,"E4119"),sQuery(id+"F14.wireOp",EDGE,"E4120"),sQuery(id+"F14.wireOp",EDGE,"E4121"),sQuery(id+"F14.wireOp",EDGE,"E4122"),sQuery(id+"F14.wireOp",EDGE,"E4123"),sQuery(id+"F14.wireOp",EDGE,"E4124"),sQuery(id+"F14.wireOp",EDGE,"E4125"),sQuery(id+"F14.wireOp",EDGE,"E4126"),sQuery(id+"F14.wireOp",EDGE,"E4127"),sQuery(id+"F14.wireOp",EDGE,"E4128"),sQuery(id+"F14.wireOp",EDGE,"E4129"),sQuery(id+"F14.wireOp",EDGE,"E4130"),sQuery(id+"F14.wireOp",EDGE,"E4131"),sQuery(id+"F14.wireOp",EDGE,"E4132"),sQuery(id+"F14.wireOp",EDGE,"E4133"),sQuery(id+"F14.wireOp",EDGE,"E4134"),sQuery(id+"F14.wireOp",EDGE,"E4135"),sQuery(id+"F14.wireOp",EDGE,"E4136"),sQuery(id+"F14.wireOp",EDGE,"E4137"),sQuery(id+"F14.wireOp",EDGE,"E4138"),sQuery(id+"F14.wireOp",EDGE,"E4139"),sQuery(id+"F14.wireOp",EDGE,"E4140"),sQuery(id+"F14.wireOp",EDGE,"E4141"),sQuery(id+"F14.wireOp",EDGE,"E4142"),sQuery(id+"F14.wireOp",EDGE,"E4143"),sQuery(id+"F14.wireOp",EDGE,"E4144"),sQuery(id+"F14.wireOp",EDGE,"E4145"),sQuery(id+"F14.wireOp",EDGE,"E4146"),sQuery(id+"F14.wireOp",EDGE,"E4147"),sQuery(id+"F14.wireOp",EDGE,"E4148"),sQuery(id+"F14.wireOp",EDGE,"E4149"),sQuery(id+"F14.wireOp",EDGE,"E4150"),sQuery(id+"F14.wireOp",EDGE,"E4151"),sQuery(id+"F14.wireOp",EDGE,"E4152"),sQuery(id+"F14.wireOp",EDGE,"E4153"),sQuery(id+"F14.wireOp",EDGE,"E4154"),sQuery(id+"F14.wireOp",EDGE,"E4155"),sQuery(id+"F14.wireOp",EDGE,"E4156"),sQuery(id+"F14.wireOp",EDGE,"E4157"),sQuery(id+"F14.wireOp",EDGE,"E4158"),sQuery(id+"F14.wireOp",EDGE,"E4159"),sQuery(id+"F14.wireOp",EDGE,"E4160"),sQuery(id+"F14.wireOp",EDGE,"E4161"),sQuery(id+"F14.wireOp",EDGE,"E4162"),sQuery(id+"F14.wireOp",EDGE,"E4163"),sQuery(id+"F14.wireOp",EDGE,"E4164"),sQuery(id+"F14.wireOp",EDGE,"E4165"),sQuery(id+"F14.wireOp",EDGE,"E4166"),sQuery(id+"F14.wireOp",EDGE,"E4167"),sQuery(id+"F14.wireOp",EDGE,"E4168"),sQuery(id+"F14.wireOp",EDGE,"E4169"),sQuery(id+"F14.wireOp",EDGE,"E4170"),sQuery(id+"F14.wireOp",EDGE,"E4171"),sQuery(id+"F14.wireOp",EDGE,"E4172"),sQuery(id+"F14.wireOp",EDGE,"E4173"),sQuery(id+"F14.wireOp",EDGE,"E4174"),sQuery(id+"F14.wireOp",EDGE,"E4175"),sQuery(id+"F14.wireOp",EDGE,"E4176"),sQuery(id+"F14.wireOp",EDGE,"E4177"),sQuery(id+"F14.wireOp",EDGE,"E4178"),sQuery(id+"F14.wireOp",EDGE,"E4179"),sQuery(id+"F14.wireOp",EDGE,"E4180"),sQuery(id+"F14.wireOp",EDGE,"E4181"),sQuery(id+"F14.wireOp",EDGE,"E4182"),sQuery(id+"F14.wireOp",EDGE,"E4183"),sQuery(id+"F14.wireOp",EDGE,"E4184"),sQuery(id+"F14.wireOp",EDGE,"E4185"),sQuery(id+"F14.wireOp",EDGE,"E4186"),sQuery(id+"F14.wireOp",EDGE,"E4187"),sQuery(id+"F14.wireOp",EDGE,"E4188"),sQuery(id+"F14.wireOp",EDGE,"E4189"),sQuery(id+"F14.wireOp",EDGE,"E4190"),sQuery(id+"F14.wireOp",EDGE,"E4191"),sQuery(id+"F14.wireOp",EDGE,"E4192"),sQuery(id+"F14.wireOp",EDGE,"E4193"),sQuery(id+"F14.wireOp",EDGE,"E4194"),sQuery(id+"F14.wireOp",EDGE,"E4195"),sQuery(id+"F14.wireOp",EDGE,"E4196"),sQuery(id+"F14.wireOp",EDGE,"E4197"),sQuery(id+"F14.wireOp",EDGE,"E4198"),sQuery(id+"F14.wireOp",EDGE,"E4199"),sQuery(id+"F14.wireOp",EDGE,"E4200"),sQuery(id+"F14.wireOp",EDGE,"E4201"),sQuery(id+"F14.wireOp",EDGE,"E4202"),sQuery(id+"F14.wireOp",EDGE,"E4203"),sQuery(id+"F14.wireOp",EDGE,"E4204"),sQuery(id+"F14.wireOp",EDGE,"E4205"),sQuery(id+"F14.wireOp",EDGE,"E4206"),sQuery(id+"F14.wireOp",EDGE,"E4207"),sQuery(id+"F14.wireOp",EDGE,"E4208"),sQuery(id+"F14.wireOp",EDGE,"E4209"),sQuery(id+"F14.wireOp",EDGE,"E4210"),sQuery(id+"F14.wireOp",EDGE,"E4211"),sQuery(id+"F14.wireOp",EDGE,"E4212"),sQuery(id+"F14.wireOp",EDGE,"E4213"),sQuery(id+"F14.wireOp",EDGE,"E4214"),sQuery(id+"F14.wireOp",EDGE,"E4215"),sQuery(id+"F14.wireOp",EDGE,"E4216"),sQuery(id+"F14.wireOp",EDGE,"E4217"),sQuery(id+"F14.wireOp",EDGE,"E4218"),sQuery(id+"F14.wireOp",EDGE,"E4219"),sQuery(id+"F14.wireOp",EDGE,"E4220"),sQuery(id+"F14.wireOp",EDGE,"E4221"),sQuery(id+"F14.wireOp",EDGE,"E4222"),sQuery(id+"F14.wireOp",EDGE,"E4223"),sQuery(id+"F14.wireOp",EDGE,"E4224"),sQuery(id+"F14.wireOp",EDGE,"E4225"),sQuery(id+"F14.wireOp",EDGE,"E4226"),sQuery(id+"F14.wireOp",EDGE,"E4227"),sQuery(id+"F14.wireOp",EDGE,"E4228"),sQuery(id+"F14.wireOp",EDGE,"E4229"),sQuery(id+"F14.wireOp",EDGE,"E4230"),sQuery(id+"F14.wireOp",EDGE,"E4231"),sQuery(id+"F14.wireOp",EDGE,"E4232"),sQuery(id+"F14.wireOp",EDGE,"E4233"),sQuery(id+"F14.wireOp",EDGE,"E4234"),sQuery(id+"F14.wireOp",EDGE,"E4235"),sQuery(id+"F14.wireOp",EDGE,"E4236"),sQuery(id+"F14.wireOp",EDGE,"E4237"),sQuery(id+"F14.wireOp",EDGE,"E4238"),sQuery(id+"F14.wireOp",EDGE,"E4239"),sQuery(id+"F14.wireOp",EDGE,"E4240"),sQuery(id+"F14.wireOp",EDGE,"E4241"),sQuery(id+"F14.wireOp",EDGE,"E4242"),sQuery(id+"F14.wireOp",EDGE,"E4243"),sQuery(id+"F14.wireOp",EDGE,"E4244"),sQuery(id+"F14.wireOp",EDGE,"E4245"),sQuery(id+"F14.wireOp",EDGE,"E4246"),sQuery(id+"F14.wireOp",EDGE,"E4247"),sQuery(id+"F14.wireOp",EDGE,"E4248"),sQuery(id+"F14.wireOp",EDGE,"E4249"),sQuery(id+"F14.wireOp",EDGE,"E4250"),sQuery(id+"F14.wireOp",EDGE,"E4251"),sQuery(id+"F14.wireOp",EDGE,"E4252"),sQuery(id+"F14.wireOp",EDGE,"E4253"),sQuery(id+"F14.wireOp",EDGE,"E4254"),sQuery(id+"F14.wireOp",EDGE,"E4255"),sQuery(id+"F14.wireOp",EDGE,"E4256"),sQuery(id+"F14.wireOp",EDGE,"E4257"),sQuery(id+"F14.wireOp",EDGE,"E4258"),sQuery(id+"F14.wireOp",EDGE,"E4259"),sQuery(id+"F14.wireOp",EDGE,"E4260"),sQuery(id+"F14.wireOp",EDGE,"E4261"),sQuery(id+"F14.wireOp",EDGE,"E4262"),sQuery(id+"F14.wireOp",EDGE,"E4263"),sQuery(id+"F14.wireOp",EDGE,"E4264"),sQuery(id+"F14.wireOp",EDGE,"E4265"),sQuery(id+"F14.wireOp",EDGE,"E4266"),sQuery(id+"F14.wireOp",EDGE,"E4267"),sQuery(id+"F14.wireOp",EDGE,"E4268"),sQuery(id+"F14.wireOp",EDGE,"E4269"),sQuery(id+"F14.wireOp",EDGE,"E4270"),sQuery(id+"F14.wireOp",EDGE,"E4271"),sQuery(id+"F14.wireOp",EDGE,"E4272"),sQuery(id+"F14.wireOp",EDGE,"E4273"),sQuery(id+"F14.wireOp",EDGE,"E4274"),sQuery(id+"F14.wireOp",EDGE,"E4275"),sQuery(id+"F14.wireOp",EDGE,"E4276"),sQuery(id+"F14.wireOp",EDGE,"E4277"),sQuery(id+"F14.wireOp",EDGE,"E4278"),sQuery(id+"F14.wireOp",EDGE,"E4279"),sQuery(id+"F14.wireOp",EDGE,"E4280"),sQuery(id+"F14.wireOp",EDGE,"E4281"),sQuery(id+"F14.wireOp",EDGE,"E4282"),sQuery(id+"F14.wireOp",EDGE,"E4283"),sQuery(id+"F14.wireOp",EDGE,"E4284"),sQuery(id+"F14.wireOp",EDGE,"E4285"),sQuery(id+"F14.wireOp",EDGE,"E4286"),sQuery(id+"F14.wireOp",EDGE,"E4287"),sQuery(id+"F14.wireOp",EDGE,"E4288"),sQuery(id+"F14.wireOp",EDGE,"E4289"),sQuery(id+"F14.wireOp",EDGE,"E4290"),sQuery(id+"F14.wireOp",EDGE,"E4291"),sQuery(id+"F14.wireOp",EDGE,"E4292"),sQuery(id+"F14.wireOp",EDGE,"E4293"),sQuery(id+"F14.wireOp",EDGE,"E4294"),sQuery(id+"F14.wireOp",EDGE,"E4295"),sQuery(id+"F14.wireOp",EDGE,"E4296"),sQuery(id+"F14.wireOp",EDGE,"E4297"),sQuery(id+"F14.wireOp",EDGE,"E4298"),sQuery(id+"F14.wireOp",EDGE,"E4299"),sQuery(id+"F14.wireOp",EDGE,"E4300"),sQuery(id+"F14.wireOp",EDGE,"E4301"),sQuery(id+"F14.wireOp",EDGE,"E4302"),sQuery(id+"F14.wireOp",EDGE,"E4303"),sQuery(id+"F14.wireOp",EDGE,"E4304"),sQuery(id+"F14.wireOp",EDGE,"E4305"),sQuery(id+"F14.wireOp",EDGE,"E4306"),sQuery(id+"F14.wireOp",EDGE,"E4307"),sQuery(id+"F14.wireOp",EDGE,"E4308"),sQuery(id+"F14.wireOp",EDGE,"E4309"),sQuery(id+"F14.wireOp",EDGE,"E4310"),sQuery(id+"F14.wireOp",EDGE,"E4311"),sQuery(id+"F14.wireOp",EDGE,"E4312"),sQuery(id+"F14.wireOp",EDGE,"E4313"),sQuery(id+"F14.wireOp",EDGE,"E4314"),sQuery(id+"F14.wireOp",EDGE,"E4315"),sQuery(id+"F14.wireOp",EDGE,"E4316"),sQuery(id+"F14.wireOp",EDGE,"E4317"),sQuery(id+"F14.wireOp",EDGE,"E4318"),sQuery(id+"F14.wireOp",EDGE,"E4319"),sQuery(id+"F14.wireOp",EDGE,"E4320"),sQuery(id+"F14.wireOp",EDGE,"E4321"),sQuery(id+"F14.wireOp",EDGE,"E4322"),sQuery(id+"F14.wireOp",EDGE,"E4323"),sQuery(id+"F14.wireOp",EDGE,"E4324"),sQuery(id+"F14.wireOp",EDGE,"E4325"),sQuery(id+"F14.wireOp",EDGE,"E4326"),sQuery(id+"F14.wireOp",EDGE,"E4327"),sQuery(id+"F14.wireOp",EDGE,"E4328"),sQuery(id+"F14.wireOp",EDGE,"E4329"),sQuery(id+"F14.wireOp",EDGE,"E4330"),sQuery(id+"F14.wireOp",EDGE,"E4331"),sQuery(id+"F14.wireOp",EDGE,"E4332"),sQuery(id+"F14.wireOp",EDGE,"E4333"),sQuery(id+"F14.wireOp",EDGE,"E4334"),sQuery(id+"F14.wireOp",EDGE,"E4335"),sQuery(id+"F14.wireOp",EDGE,"E4336"),sQuery(id+"F14.wireOp",EDGE,"E4337"),sQuery(id+"F14.wireOp",EDGE,"E4338"),sQuery(id+"F14.wireOp",EDGE,"E4339"),sQuery(id+"F14.wireOp",EDGE,"E4340"),sQuery(id+"F14.wireOp",EDGE,"E4341"),sQuery(id+"F14.wireOp",EDGE,"E4342"),sQuery(id+"F14.wireOp",EDGE,"E4343"),sQuery(id+"F14.wireOp",EDGE,"E4344"),sQuery(id+"F14.wireOp",EDGE,"E4345"),sQuery(id+"F14.wireOp",EDGE,"E4346"),sQuery(id+"F14.wireOp",EDGE,"E4347"),sQuery(id+"F14.wireOp",EDGE,"E4348"),sQuery(id+"F14.wireOp",EDGE,"E4349"),sQuery(id+"F14.wireOp",EDGE,"E4350"),sQuery(id+"F14.wireOp",EDGE,"E4351"),sQuery(id+"F14.wireOp",EDGE,"E4352"),sQuery(id+"F14.wireOp",EDGE,"E4353"),sQuery(id+"F14.wireOp",EDGE,"E4354"),sQuery(id+"F14.wireOp",EDGE,"E4355"),sQuery(id+"F14.wireOp",EDGE,"E4356"),sQuery(id+"F14.wireOp",EDGE,"E4357"),sQuery(id+"F14.wireOp",EDGE,"E4358"),sQuery(id+"F14.wireOp",EDGE,"E4359"),sQuery(id+"F14.wireOp",EDGE,"E4360"),sQuery(id+"F14.wireOp",EDGE,"E4361"),sQuery(id+"F14.wireOp",EDGE,"E4362"),sQuery(id+"F14.wireOp",EDGE,"E4363"),sQuery(id+"F14.wireOp",EDGE,"E4364"),sQuery(id+"F14.wireOp",EDGE,"E4365"),sQuery(id+"F14.wireOp",EDGE,"E4366"),sQuery(id+"F14.wireOp",EDGE,"E4367"),sQuery(id+"F14.wireOp",EDGE,"E4368"),sQuery(id+"F14.wireOp",EDGE,"E4369"),sQuery(id+"F14.wireOp",EDGE,"E4370"),sQuery(id+"F14.wireOp",EDGE,"E4371"),sQuery(id+"F14.wireOp",EDGE,"E4372"),sQuery(id+"F14.wireOp",EDGE,"E4373"),sQuery(id+"F14.wireOp",EDGE,"E4374"),sQuery(id+"F14.wireOp",EDGE,"E4375"),sQuery(id+"F14.wireOp",EDGE,"E4376"),sQuery(id+"F14.wireOp",EDGE,"E4377"),sQuery(id+"F14.wireOp",EDGE,"E4378"),sQuery(id+"F14.wireOp",EDGE,"E4379"),sQuery(id+"F14.wireOp",EDGE,"E4380"),sQuery(id+"F14.wireOp",EDGE,"E4381"),sQuery(id+"F14.wireOp",EDGE,"E4382"),sQuery(id+"F14.wireOp",EDGE,"E4383"),sQuery(id+"F14.wireOp",EDGE,"E4384"),sQuery(id+"F14.wireOp",EDGE,"E4385"),sQuery(id+"F14.wireOp",EDGE,"E4386"),sQuery(id+"F14.wireOp",EDGE,"E4387"),sQuery(id+"F14.wireOp",EDGE,"E4388"),sQuery(id+"F14.wireOp",EDGE,"E4389"),sQuery(id+"F14.wireOp",EDGE,"E4390"),sQuery(id+"F14.wireOp",EDGE,"E4391"),sQuery(id+"F14.wireOp",EDGE,"E4392"),sQuery(id+"F14.wireOp",EDGE,"E4393"),sQuery(id+"F14.wireOp",EDGE,"E4394"),sQuery(id+"F14.wireOp",EDGE,"E4395"),sQuery(id+"F14.wireOp",EDGE,"E4396"),sQuery(id+"F14.wireOp",EDGE,"E4397"),sQuery(id+"F14.wireOp",EDGE,"E4398"),sQuery(id+"F14.wireOp",EDGE,"E4399"),sQuery(id+"F14.wireOp",EDGE,"E4400"),sQuery(id+"F14.wireOp",EDGE,"E4401"),sQuery(id+"F14.wireOp",EDGE,"E4402"),sQuery(id+"F14.wireOp",EDGE,"E4403"),sQuery(id+"F14.wireOp",EDGE,"E4404"),sQuery(id+"F14.wireOp",EDGE,"E4405"),sQuery(id+"F14.wireOp",EDGE,"E4406"),sQuery(id+"F14.wireOp",EDGE,"E4407"),sQuery(id+"F14.wireOp",EDGE,"E4408"),sQuery(id+"F14.wireOp",EDGE,"E4409"),sQuery(id+"F14.wireOp",EDGE,"E4410"),sQuery(id+"F14.wireOp",EDGE,"E4411"),sQuery(id+"F14.wireOp",EDGE,"E4412"),sQuery(id+"F14.wireOp",EDGE,"E4413"),sQuery(id+"F14.wireOp",EDGE,"E4414"),sQuery(id+"F14.wireOp",EDGE,"E4415"),sQuery(id+"F14.wireOp",EDGE,"E4416"),sQuery(id+"F14.wireOp",EDGE,"E4417"),sQuery(id+"F14.wireOp",EDGE,"E4418"),sQuery(id+"F14.wireOp",EDGE,"E4419"),sQuery(id+"F14.wireOp",EDGE,"E4420"),sQuery(id+"F14.wireOp",EDGE,"E4421"),sQuery(id+"F14.wireOp",EDGE,"E4422"),sQuery(id+"F14.wireOp",EDGE,"E4423"),sQuery(id+"F14.wireOp",EDGE,"E4424"),sQuery(id+"F14.wireOp",EDGE,"E4425"),sQuery(id+"F14.wireOp",EDGE,"E4426"),sQuery(id+"F14.wireOp",EDGE,"E4427"),sQuery(id+"F14.wireOp",EDGE,"E4428"),sQuery(id+"F14.wireOp",EDGE,"E4429"),sQuery(id+"F14.wireOp",EDGE,"E4430"),sQuery(id+"F14.wireOp",EDGE,"E4431"),sQuery(id+"F14.wireOp",EDGE,"E4432"),sQuery(id+"F14.wireOp",EDGE,"E4433"),sQuery(id+"F14.wireOp",EDGE,"E4434"),sQuery(id+"F14.wireOp",EDGE,"E4435"),sQuery(id+"F14.wireOp",EDGE,"E4436"),sQuery(id+"F14.wireOp",EDGE,"E4437"),sQuery(id+"F14.wireOp",EDGE,"E4438"),sQuery(id+"F14.wireOp",EDGE,"E4439"),sQuery(id+"F14.wireOp",EDGE,"E4440"),sQuery(id+"F14.wireOp",EDGE,"E4441"),sQuery(id+"F14.wireOp",EDGE,"E4442"),sQuery(id+"F14.wireOp",EDGE,"E4443"),sQuery(id+"F14.wireOp",EDGE,"E4444"),sQuery(id+"F14.wireOp",EDGE,"E4445"),sQuery(id+"F14.wireOp",EDGE,"E4446"),sQuery(id+"F14.wireOp",EDGE,"E4447"),sQuery(id+"F14.wireOp",EDGE,"E4448"),sQuery(id+"F14.wireOp",EDGE,"E4449"),sQuery(id+"F14.wireOp",EDGE,"E4450"),sQuery(id+"F14.wireOp",EDGE,"E4451"),sQuery(id+"F14.wireOp",EDGE,"E4452"),sQuery(id+"F14.wireOp",EDGE,"E4453"),sQuery(id+"F14.wireOp",EDGE,"E4454"),sQuery(id+"F14.wireOp",EDGE,"E4455"),sQuery(id+"F14.wireOp",EDGE,"E4456"),sQuery(id+"F14.wireOp",EDGE,"E4457"),sQuery(id+"F14.wireOp",EDGE,"E4458"),sQuery(id+"F14.wireOp",EDGE,"E4459"),sQuery(id+"F14.wireOp",EDGE,"E4460"),sQuery(id+"F14.wireOp",EDGE,"E4461"),sQuery(id+"F14.wireOp",EDGE,"E4462"),sQuery(id+"F14.wireOp",EDGE,"E4463"),sQuery(id+"F14.wireOp",EDGE,"E4464"),sQuery(id+"F14.wireOp",EDGE,"E4465"),sQuery(id+"F14.wireOp",EDGE,"E4466"),sQuery(id+"F14.wireOp",EDGE,"E4467"),sQuery(id+"F14.wireOp",EDGE,"E4468"),sQuery(id+"F14.wireOp",EDGE,"E4469"),sQuery(id+"F14.wireOp",EDGE,"E4470"),sQuery(id+"F14.wireOp",EDGE,"E4471"),sQuery(id+"F14.wireOp",EDGE,"E4472"),sQuery(id+"F14.wireOp",EDGE,"E4473"),sQuery(id+"F14.wireOp",EDGE,"E4474"),sQuery(id+"F14.wireOp",EDGE,"E4475"),sQuery(id+"F14.wireOp",EDGE,"E4476"),sQuery(id+"F14.wireOp",EDGE,"E4477"),sQuery(id+"F14.wireOp",EDGE,"E4478"),sQuery(id+"F14.wireOp",EDGE,"E4479"),sQuery(id+"F14.wireOp",EDGE,"E4480"),sQuery(id+"F14.wireOp",EDGE,"E4481"),sQuery(id+"F14.wireOp",EDGE,"E4482"),sQuery(id+"F14.wireOp",EDGE,"E4483"),sQuery(id+"F14.wireOp",EDGE,"E4484"),sQuery(id+"F14.wireOp",EDGE,"E4485"),sQuery(id+"F14.wireOp",EDGE,"E4486"),sQuery(id+"F14.wireOp",EDGE,"E4487"),sQuery(id+"F14.wireOp",EDGE,"E4488"),sQuery(id+"F14.wireOp",EDGE,"E4489"),sQuery(id+"F14.wireOp",EDGE,"E4490"),sQuery(id+"F14.wireOp",EDGE,"E4491"),sQuery(id+"F14.wireOp",EDGE,"E4492"),sQuery(id+"F14.wireOp",EDGE,"E4493"),sQuery(id+"F14.wireOp",EDGE,"E4494"),sQuery(id+"F14.wireOp",EDGE,"E4495"),sQuery(id+"F14.wireOp",EDGE,"E4496"),sQuery(id+"F14.wireOp",EDGE,"E4497"),sQuery(id+"F14.wireOp",EDGE,"E4498"),sQuery(id+"F14.wireOp",EDGE,"E4499"),sQuery(id+"F14.wireOp",EDGE,"E4500"),sQuery(id+"F14.wireOp",EDGE,"E4501"),sQuery(id+"F14.wireOp",EDGE,"E4502"),sQuery(id+"F14.wireOp",EDGE,"E4503"),sQuery(id+"F14.wireOp",EDGE,"E4504"),sQuery(id+"F14.wireOp",EDGE,"E4505"),sQuery(id+"F14.wireOp",EDGE,"E4506"),sQuery(id+"F14.wireOp",EDGE,"E4507"),sQuery(id+"F14.wireOp",EDGE,"E4508"),sQuery(id+"F14.wireOp",EDGE,"E4509"),sQuery(id+"F14.wireOp",EDGE,"E4510"),sQuery(id+"F14.wireOp",EDGE,"E4511"),sQuery(id+"F14.wireOp",EDGE,"E4512"),sQuery(id+"F14.wireOp",EDGE,"E4513"),sQuery(id+"F14.wireOp",EDGE,"E4514"),sQuery(id+"F14.wireOp",EDGE,"E4515"),sQuery(id+"F14.wireOp",EDGE,"E4516"),sQuery(id+"F14.wireOp",EDGE,"E4517"),sQuery(id+"F14.wireOp",EDGE,"E4518"),sQuery(id+"F14.wireOp",EDGE,"E4519"),sQuery(id+"F14.wireOp",EDGE,"E4520"),sQuery(id+"F14.wireOp",EDGE,"E4521"),sQuery(id+"F14.wireOp",EDGE,"E4522"),sQuery(id+"F14.wireOp",EDGE,"E4523"),sQuery(id+"F14.wireOp",EDGE,"E4524"),sQuery(id+"F14.wireOp",EDGE,"E4525"),sQuery(id+"F14.wireOp",EDGE,"E4526"),sQuery(id+"F14.wireOp",EDGE,"E4527"),sQuery(id+"F14.wireOp",EDGE,"E4528"),sQuery(id+"F14.wireOp",EDGE,"E4529"),sQuery(id+"F14.wireOp",EDGE,"E4530"),sQuery(id+"F14.wireOp",EDGE,"E4531"),sQuery(id+"F14.wireOp",EDGE,"E4532"),sQuery(id+"F14.wireOp",EDGE,"E4533"),sQuery(id+"F14.wireOp",EDGE,"E4534"),sQuery(id+"F14.wireOp",EDGE,"E4535"),sQuery(id+"F14.wireOp",EDGE,"E4536"),sQuery(id+"F14.wireOp",EDGE,"E4537"),sQuery(id+"F14.wireOp",EDGE,"E4538"),sQuery(id+"F14.wireOp",EDGE,"E4539"),sQuery(id+"F14.wireOp",EDGE,"E4540"),sQuery(id+"F14.wireOp",EDGE,"E4541"),sQuery(id+"F14.wireOp",EDGE,"E4542"),sQuery(id+"F14.wireOp",EDGE,"E4543"),sQuery(id+"F14.wireOp",EDGE,"E4544"),sQuery(id+"F14.wireOp",EDGE,"E4545"),sQuery(id+"F14.wireOp",EDGE,"E4546"),sQuery(id+"F14.wireOp",EDGE,"E4547"),sQuery(id+"F14.wireOp",EDGE,"E4548"),sQuery(id+"F14.wireOp",EDGE,"E4549"),sQuery(id+"F14.wireOp",EDGE,"E4550"),sQuery(id+"F14.wireOp",EDGE,"E4551"),sQuery(id+"F14.wireOp",EDGE,"E4552"),sQuery(id+"F14.wireOp",EDGE,"E4553"),sQuery(id+"F14.wireOp",EDGE,"E4554"),sQuery(id+"F14.wireOp",EDGE,"E4555"),sQuery(id+"F14.wireOp",EDGE,"E4556"),sQuery(id+"F14.wireOp",EDGE,"E4557"),sQuery(id+"F14.wireOp",EDGE,"E4558"),sQuery(id+"F14.wireOp",EDGE,"E4559"),sQuery(id+"F14.wireOp",EDGE,"E4560"),sQuery(id+"F14.wireOp",EDGE,"E4561"),sQuery(id+"F14.wireOp",EDGE,"E4562"),sQuery(id+"F14.wireOp",EDGE,"E4563"),sQuery(id+"F14.wireOp",EDGE,"E4564"),sQuery(id+"F14.wireOp",EDGE,"E4565"),sQuery(id+"F14.wireOp",EDGE,"E4566"),sQuery(id+"F14.wireOp",EDGE,"E4567"),sQuery(id+"F14.wireOp",EDGE,"E4568"),sQuery(id+"F14.wireOp",EDGE,"E4569"),sQuery(id+"F14.wireOp",EDGE,"E4570"),sQuery(id+"F14.wireOp",EDGE,"E4571"),sQuery(id+"F14.wireOp",EDGE,"E4572"),sQuery(id+"F14.wireOp",EDGE,"E4573"),sQuery(id+"F14.wireOp",EDGE,"E4574"),sQuery(id+"F14.wireOp",EDGE,"E4575"),sQuery(id+"F14.wireOp",EDGE,"E4576"),sQuery(id+"F14.wireOp",EDGE,"E4577"),sQuery(id+"F14.wireOp",EDGE,"E4578"),sQuery(id+"F14.wireOp",EDGE,"E4579"),sQuery(id+"F14.wireOp",EDGE,"E4580"),sQuery(id+"F14.wireOp",EDGE,"E4581"),sQuery(id+"F14.wireOp",EDGE,"E4582"),sQuery(id+"F14.wireOp",EDGE,"E4583"),sQuery(id+"F14.wireOp",EDGE,"E4584"),sQuery(id+"F14.wireOp",EDGE,"E4585"),sQuery(id+"F14.wireOp",EDGE,"E4586"),sQuery(id+"F14.wireOp",EDGE,"E4587"),sQuery(id+"F14.wireOp",EDGE,"E4588"),sQuery(id+"F14.wireOp",EDGE,"E4589"),sQuery(id+"F14.wireOp",EDGE,"E4590"),sQuery(id+"F14.wireOp",EDGE,"E4591"),sQuery(id+"F14.wireOp",EDGE,"E4592"),sQuery(id+"F14.wireOp",EDGE,"E4593"),sQuery(id+"F14.wireOp",EDGE,"E4594"),sQuery(id+"F14.wireOp",EDGE,"E4595"),sQuery(id+"F14.wireOp",EDGE,"E4596"),sQuery(id+"F14.wireOp",EDGE,"E4597"),sQuery(id+"F14.wireOp",EDGE,"E4598"),sQuery(id+"F14.wireOp",EDGE,"E4599"),sQuery(id+"F14.wireOp",EDGE,"E4600"),sQuery(id+"F14.wireOp",EDGE,"E4601"),sQuery(id+"F14.wireOp",EDGE,"E4602"),sQuery(id+"F14.wireOp",EDGE,"E4603"),sQuery(id+"F14.wireOp",EDGE,"E4604"),sQuery(id+"F14.wireOp",EDGE,"E4605"),sQuery(id+"F14.wireOp",EDGE,"E4606"),sQuery(id+"F14.wireOp",EDGE,"E4607"),sQuery(id+"F14.wireOp",EDGE,"E4608"),sQuery(id+"F14.wireOp",EDGE,"E4609"),sQuery(id+"F14.wireOp",EDGE,"E4610"),sQuery(id+"F14.wireOp",EDGE,"E4611"),sQuery(id+"F14.wireOp",EDGE,"E4612"),sQuery(id+"F14.wireOp",EDGE,"E4613"),sQuery(id+"F14.wireOp",EDGE,"E4614"),sQuery(id+"F14.wireOp",EDGE,"E4615"),sQuery(id+"F14.wireOp",EDGE,"E4616"),sQuery(id+"F14.wireOp",EDGE,"E4617"),sQuery(id+"F14.wireOp",EDGE,"E4618"),sQuery(id+"F14.wireOp",EDGE,"E4619"),sQuery(id+"F14.wireOp",EDGE,"E4620"),sQuery(id+"F14.wireOp",EDGE,"E4621"),sQuery(id+"F14.wireOp",EDGE,"E4622"),sQuery(id+"F14.wireOp",EDGE,"E4623"),sQuery(id+"F14.wireOp",EDGE,"E4624"),sQuery(id+"F14.wireOp",EDGE,"E4625"),sQuery(id+"F14.wireOp",EDGE,"E4626"),sQuery(id+"F14.wireOp",EDGE,"E4627"),sQuery(id+"F14.wireOp",EDGE,"E4628"),sQuery(id+"F14.wireOp",EDGE,"E4629"),sQuery(id+"F14.wireOp",EDGE,"E4630"),sQuery(id+"F14.wireOp",EDGE,"E4631"),sQuery(id+"F14.wireOp",EDGE,"E4632"),sQuery(id+"F14.wireOp",EDGE,"E4633"),sQuery(id+"F14.wireOp",EDGE,"E4634"),sQuery(id+"F14.wireOp",EDGE,"E4635"),sQuery(id+"F14.wireOp",EDGE,"E4636"),sQuery(id+"F14.wireOp",EDGE,"E4637"),sQuery(id+"F14.wireOp",EDGE,"E4638"),sQuery(id+"F14.wireOp",EDGE,"E4639"),sQuery(id+"F14.wireOp",EDGE,"E4640"),sQuery(id+"F14.wireOp",EDGE,"E4641"),sQuery(id+"F14.wireOp",EDGE,"E4642"),sQuery(id+"F14.wireOp",EDGE,"E4643"),sQuery(id+"F14.wireOp",EDGE,"E4644"),sQuery(id+"F14.wireOp",EDGE,"E4645"),sQuery(id+"F14.wireOp",EDGE,"E4646"),sQuery(id+"F14.wireOp",EDGE,"E4647"),sQuery(id+"F14.wireOp",EDGE,"E4648"),sQuery(id+"F14.wireOp",EDGE,"E4649"),sQuery(id+"F14.wireOp",EDGE,"E4650"),sQuery(id+"F14.wireOp",EDGE,"E4651"),sQuery(id+"F14.wireOp",EDGE,"E4652"),sQuery(id+"F14.wireOp",EDGE,"E4653"),sQuery(id+"F14.wireOp",EDGE,"E4654"),sQuery(id+"F14.wireOp",EDGE,"E4655"),sQuery(id+"F14.wireOp",EDGE,"E4656"),sQuery(id+"F14.wireOp",EDGE,"E4657"),sQuery(id+"F14.wireOp",EDGE,"E4658"),sQuery(id+"F14.wireOp",EDGE,"E4659"),sQuery(id+"F14.wireOp",EDGE,"E4660"),sQuery(id+"F14.wireOp",EDGE,"E4661"),sQuery(id+"F14.wireOp",EDGE,"E4662"),sQuery(id+"F14.wireOp",EDGE,"E4663"),sQuery(id+"F14.wireOp",EDGE,"E4664"),sQuery(id+"F14.wireOp",EDGE,"E4665"),sQuery(id+"F14.wireOp",EDGE,"E4666"),sQuery(id+"F14.wireOp",EDGE,"E4667"),sQuery(id+"F14.wireOp",EDGE,"E4668"),sQuery(id+"F14.wireOp",EDGE,"E4669"),sQuery(id+"F14.wireOp",EDGE,"E4670"),sQuery(id+"F14.wireOp",EDGE,"E4671"),sQuery(id+"F14.wireOp",EDGE,"E4672"),sQuery(id+"F14.wireOp",EDGE,"E4673"),sQuery(id+"F14.wireOp",EDGE,"E4674"),sQuery(id+"F14.wireOp",EDGE,"E4675"),sQuery(id+"F14.wireOp",EDGE,"E4676"),sQuery(id+"F14.wireOp",EDGE,"E4677"),sQuery(id+"F14.wireOp",EDGE,"E4678"),sQuery(id+"F14.wireOp",EDGE,"E4679"),sQuery(id+"F14.wireOp",EDGE,"E4680"),sQuery(id+"F14.wireOp",EDGE,"E4681"),sQuery(id+"F14.wireOp",EDGE,"E4682"),sQuery(id+"F14.wireOp",EDGE,"E4683"),sQuery(id+"F14.wireOp",EDGE,"E4684"),sQuery(id+"F14.wireOp",EDGE,"E4685"),sQuery(id+"F14.wireOp",EDGE,"E4686"),sQuery(id+"F14.wireOp",EDGE,"E4687"),sQuery(id+"F14.wireOp",EDGE,"E4688"),sQuery(id+"F14.wireOp",EDGE,"E4689"),sQuery(id+"F14.wireOp",EDGE,"E4690"),sQuery(id+"F14.wireOp",EDGE,"E4691"),sQuery(id+"F14.wireOp",EDGE,"E4692"),sQuery(id+"F14.wireOp",EDGE,"E4693"),sQuery(id+"F14.wireOp",EDGE,"E4694"),sQuery(id+"F14.wireOp",EDGE,"E4695"),sQuery(id+"F14.wireOp",EDGE,"E4696"),sQuery(id+"F14.wireOp",EDGE,"E4697"),sQuery(id+"F14.wireOp",EDGE,"E4698"),sQuery(id+"F14.wireOp",EDGE,"E4699"),sQuery(id+"F14.wireOp",EDGE,"E4700"),sQuery(id+"F14.wireOp",EDGE,"E4701"),sQuery(id+"F14.wireOp",EDGE,"E4702"),sQuery(id+"F14.wireOp",EDGE,"E4703"),sQuery(id+"F14.wireOp",EDGE,"E4704"),sQuery(id+"F14.wireOp",EDGE,"E4705"),sQuery(id+"F14.wireOp",EDGE,"E4706"),sQuery(id+"F14.wireOp",EDGE,"E4707"),sQuery(id+"F14.wireOp",EDGE,"E4708"),sQuery(id+"F14.wireOp",EDGE,"E4709"),sQuery(id+"F14.wireOp",EDGE,"E4710"),sQuery(id+"F14.wireOp",EDGE,"E4711"),sQuery(id+"F14.wireOp",EDGE,"E4712"),sQuery(id+"F14.wireOp",EDGE,"E4713"),sQuery(id+"F14.wireOp",EDGE,"E4714"),sQuery(id+"F14.wireOp",EDGE,"E4715"),sQuery(id+"F14.wireOp",EDGE,"E4716"),sQuery(id+"F14.wireOp",EDGE,"E4717"),sQuery(id+"F14.wireOp",EDGE,"E4718"),sQuery(id+"F14.wireOp",EDGE,"E4719"),sQuery(id+"F14.wireOp",EDGE,"E4720"),sQuery(id+"F14.wireOp",EDGE,"E4721"),sQuery(id+"F14.wireOp",EDGE,"E4722"),sQuery(id+"F14.wireOp",EDGE,"E4723"),sQuery(id+"F14.wireOp",EDGE,"E4724"),sQuery(id+"F14.wireOp",EDGE,"E4725"),sQuery(id+"F14.wireOp",EDGE,"E4726"),sQuery(id+"F14.wireOp",EDGE,"E4727"),sQuery(id+"F14.wireOp",EDGE,"E4728"),sQuery(id+"F14.wireOp",EDGE,"E4729"),sQuery(id+"F14.wireOp",EDGE,"E4730"),sQuery(id+"F14.wireOp",EDGE,"E4731"),sQuery(id+"F14.wireOp",EDGE,"E4732"),sQuery(id+"F14.wireOp",EDGE,"E4733"),sQuery(id+"F14.wireOp",EDGE,"E4734"),sQuery(id+"F14.wireOp",EDGE,"E4735"),sQuery(id+"F14.wireOp",EDGE,"E4736"),sQuery(id+"F14.wireOp",EDGE,"E4737"),sQuery(id+"F14.wireOp",EDGE,"E4738"),sQuery(id+"F14.wireOp",EDGE,"E4739"),sQuery(id+"F14.wireOp",EDGE,"E4740"),sQuery(id+"F14.wireOp",EDGE,"E4741"),sQuery(id+"F14.wireOp",EDGE,"E4742"),sQuery(id+"F14.wireOp",EDGE,"E4743"),sQuery(id+"F14.wireOp",EDGE,"E4744"),sQuery(id+"F14.wireOp",EDGE,"E4745"),sQuery(id+"F14.wireOp",EDGE,"E4746"),sQuery(id+"F14.wireOp",EDGE,"E4747"),sQuery(id+"F14.wireOp",EDGE,"E4748"),sQuery(id+"F14.wireOp",EDGE,"E4749"),sQuery(id+"F14.wireOp",EDGE,"E4750"),sQuery(id+"F14.wireOp",EDGE,"E4751"),sQuery(id+"F14.wireOp",EDGE,"E4752"),sQuery(id+"F14.wireOp",EDGE,"E4753"),sQuery(id+"F14.wireOp",EDGE,"E4754"),sQuery(id+"F14.wireOp",EDGE,"E4755"),sQuery(id+"F14.wireOp",EDGE,"E4756"),sQuery(id+"F14.wireOp",EDGE,"E4757"),sQuery(id+"F14.wireOp",EDGE,"E4758"),sQuery(id+"F14.wireOp",EDGE,"E4759"),sQuery(id+"F14.wireOp",EDGE,"E4760"),sQuery(id+"F14.wireOp",EDGE,"E4761"),sQuery(id+"F14.wireOp",EDGE,"E4762"),sQuery(id+"F14.wireOp",EDGE,"E4763"),sQuery(id+"F14.wireOp",EDGE,"E4764"),sQuery(id+"F14.wireOp",EDGE,"E4765"),sQuery(id+"F14.wireOp",EDGE,"E4766"),sQuery(id+"F14.wireOp",EDGE,"E4767"),sQuery(id+"F14.wireOp",EDGE,"E4768"),sQuery(id+"F14.wireOp",EDGE,"E4769"),sQuery(id+"F14.wireOp",EDGE,"E4770"),sQuery(id+"F14.wireOp",EDGE,"E4771"),sQuery(id+"F14.wireOp",EDGE,"E4772"),sQuery(id+"F14.wireOp",EDGE,"E4773"),sQuery(id+"F14.wireOp",EDGE,"E4774"),sQuery(id+"F14.wireOp",EDGE,"E4775"),sQuery(id+"F14.wireOp",EDGE,"E4776"),sQuery(id+"F14.wireOp",EDGE,"E4777"),sQuery(id+"F14.wireOp",EDGE,"E4778"),sQuery(id+"F14.wireOp",EDGE,"E4779"),sQuery(id+"F14.wireOp",EDGE,"E4780"),sQuery(id+"F14.wireOp",EDGE,"E4781"),sQuery(id+"F14.wireOp",EDGE,"E4782"),sQuery(id+"F14.wireOp",EDGE,"E4783"),sQuery(id+"F14.wireOp",EDGE,"E4784"),sQuery(id+"F14.wireOp",EDGE,"E4785"),sQuery(id+"F14.wireOp",EDGE,"E4786"),sQuery(id+"F14.wireOp",EDGE,"E4787"),sQuery(id+"F14.wireOp",EDGE,"E4788"),sQuery(id+"F14.wireOp",EDGE,"E4789"),sQuery(id+"F14.wireOp",EDGE,"E4790"),sQuery(id+"F14.wireOp",EDGE,"E4791"),sQuery(id+"F14.wireOp",EDGE,"E4792"),sQuery(id+"F14.wireOp",EDGE,"E4793"),sQuery(id+"F14.wireOp",EDGE,"E4794"),sQuery(id+"F14.wireOp",EDGE,"E4795"),sQuery(id+"F14.wireOp",EDGE,"E4796"),sQuery(id+"F14.wireOp",EDGE,"E4797"),sQuery(id+"F14.wireOp",EDGE,"E4798"),sQuery(id+"F14.wireOp",EDGE,"E4799"),sQuery(id+"F14.wireOp",EDGE,"E4800"),sQuery(id+"F14.wireOp",EDGE,"E4801"),sQuery(id+"F14.wireOp",EDGE,"E4802"),sQuery(id+"F14.wireOp",EDGE,"E4803"),sQuery(id+"F14.wireOp",EDGE,"E4804"),sQuery(id+"F14.wireOp",EDGE,"E4805"),sQuery(id+"F14.wireOp",EDGE,"E4806"),sQuery(id+"F14.wireOp",EDGE,"E4807"),sQuery(id+"F14.wireOp",EDGE,"E4808"),sQuery(id+"F14.wireOp",EDGE,"E4809"),sQuery(id+"F14.wireOp",EDGE,"E4810"),sQuery(id+"F14.wireOp",EDGE,"E4811"),sQuery(id+"F14.wireOp",EDGE,"E4812"),sQuery(id+"F14.wireOp",EDGE,"E4813"),sQuery(id+"F14.wireOp",EDGE,"E4814"),sQuery(id+"F14.wireOp",EDGE,"E4815"),sQuery(id+"F14.wireOp",EDGE,"E4816"),sQuery(id+"F14.wireOp",EDGE,"E4817"),sQuery(id+"F14.wireOp",EDGE,"E4818"),sQuery(id+"F14.wireOp",EDGE,"E4819"),sQuery(id+"F14.wireOp",EDGE,"E4820"),sQuery(id+"F14.wireOp",EDGE,"E4821"),sQuery(id+"F14.wireOp",EDGE,"E4822"),sQuery(id+"F14.wireOp",EDGE,"E4823"),sQuery(id+"F14.wireOp",EDGE,"E4824"),sQuery(id+"F14.wireOp",EDGE,"E4825"),sQuery(id+"F14.wireOp",EDGE,"E4826"),sQuery(id+"F14.wireOp",EDGE,"E4827"),sQuery(id+"F14.wireOp",EDGE,"E4828"),sQuery(id+"F14.wireOp",EDGE,"E4829"),sQuery(id+"F14.wireOp",EDGE,"E4830"),sQuery(id+"F14.wireOp",EDGE,"E4831"),sQuery(id+"F14.wireOp",EDGE,"E4832"),sQuery(id+"F14.wireOp",EDGE,"E4833"),sQuery(id+"F14.wireOp",EDGE,"E4834"),sQuery(id+"F14.wireOp",EDGE,"E4835"),sQuery(id+"F14.wireOp",EDGE,"E4836"),sQuery(id+"F14.wireOp",EDGE,"E4837"),sQuery(id+"F14.wireOp",EDGE,"E4838"),sQuery(id+"F14.wireOp",EDGE,"E4839"),sQuery(id+"F14.wireOp",EDGE,"E4840"),sQuery(id+"F14.wireOp",EDGE,"E4841"),sQuery(id+"F14.wireOp",EDGE,"E4842"),sQuery(id+"F14.wireOp",EDGE,"E4843"),sQuery(id+"F14.wireOp",EDGE,"E4844"),sQuery(id+"F14.wireOp",EDGE,"E4845"),sQuery(id+"F14.wireOp",EDGE,"E4846"),sQuery(id+"F14.wireOp",EDGE,"E4847"),sQuery(id+"F14.wireOp",EDGE,"E4848"),sQuery(id+"F14.wireOp",EDGE,"E4849"),sQuery(id+"F14.wireOp",EDGE,"E4850"),sQuery(id+"F14.wireOp",EDGE,"E4851"),sQuery(id+"F14.wireOp",EDGE,"E4852"),sQuery(id+"F14.wireOp",EDGE,"E4853"),sQuery(id+"F14.wireOp",EDGE,"E4854"),sQuery(id+"F14.wireOp",EDGE,"E4855"),sQuery(id+"F14.wireOp",EDGE,"E4856"),sQuery(id+"F14.wireOp",EDGE,"E4857"),sQuery(id+"F14.wireOp",EDGE,"E4858"),sQuery(id+"F14.wireOp",EDGE,"E4859"),sQuery(id+"F14.wireOp",EDGE,"E4860"),sQuery(id+"F14.wireOp",EDGE,"E4861"),sQuery(id+"F14.wireOp",EDGE,"E4862"),sQuery(id+"F14.wireOp",EDGE,"E4863"),sQuery(id+"F14.wireOp",EDGE,"E4864"),sQuery(id+"F14.wireOp",EDGE,"E4865"),sQuery(id+"F14.wireOp",EDGE,"E4866"),sQuery(id+"F14.wireOp",EDGE,"E4867"),sQuery(id+"F14.wireOp",EDGE,"E4868"),sQuery(id+"F14.wireOp",EDGE,"E4869"),sQuery(id+"F14.wireOp",EDGE,"E4870"),sQuery(id+"F14.wireOp",EDGE,"E4871"),sQuery(id+"F14.wireOp",EDGE,"E4872"),sQuery(id+"F14.wireOp",EDGE,"E4873"),sQuery(id+"F14.wireOp",EDGE,"E4874"),sQuery(id+"F14.wireOp",EDGE,"E4875"),sQuery(id+"F14.wireOp",EDGE,"E4876"),sQuery(id+"F14.wireOp",EDGE,"E4877"),sQuery(id+"F14.wireOp",EDGE,"E4878"),sQuery(id+"F14.wireOp",EDGE,"E4879"),sQuery(id+"F14.wireOp",EDGE,"E4880"),sQuery(id+"F14.wireOp",EDGE,"E4881"),sQuery(id+"F14.wireOp",EDGE,"E4882"),sQuery(id+"F14.wireOp",EDGE,"E4883"),sQuery(id+"F14.wireOp",EDGE,"E4884"),sQuery(id+"F14.wireOp",EDGE,"E4885"),sQuery(id+"F14.wireOp",EDGE,"E4886"),sQuery(id+"F14.wireOp",EDGE,"E4887"),sQuery(id+"F14.wireOp",EDGE,"E4888"),sQuery(id+"F14.wireOp",EDGE,"E4889"),sQuery(id+"F14.wireOp",EDGE,"E4890"),sQuery(id+"F14.wireOp",EDGE,"E4891"),sQuery(id+"F14.wireOp",EDGE,"E4892"),sQuery(id+"F14.wireOp",EDGE,"E4893"),sQuery(id+"F14.wireOp",EDGE,"E4894"),sQuery(id+"F14.wireOp",EDGE,"E4895"),sQuery(id+"F14.wireOp",EDGE,"E4896"),sQuery(id+"F14.wireOp",EDGE,"E4897"),sQuery(id+"F14.wireOp",EDGE,"E4898"),sQuery(id+"F14.wireOp",EDGE,"E4899"),sQuery(id+"F14.wireOp",EDGE,"E4900"),sQuery(id+"F14.wireOp",EDGE,"E4901"),sQuery(id+"F14.wireOp",EDGE,"E4902"),sQuery(id+"F14.wireOp",EDGE,"E4903"),sQuery(id+"F14.wireOp",EDGE,"E4904"),sQuery(id+"F14.wireOp",EDGE,"E4905"),sQuery(id+"F14.wireOp",EDGE,"E4906"),sQuery(id+"F14.wireOp",EDGE,"E4907"),sQuery(id+"F14.wireOp",EDGE,"E4908"),sQuery(id+"F14.wireOp",EDGE,"E4909"),sQuery(id+"F14.wireOp",EDGE,"E4910"),sQuery(id+"F14.wireOp",EDGE,"E4911"),sQuery(id+"F14.wireOp",EDGE,"E4912"),sQuery(id+"F14.wireOp",EDGE,"E4913"),sQuery(id+"F14.wireOp",EDGE,"E4914"),sQuery(id+"F14.wireOp",EDGE,"E4915"),sQuery(id+"F14.wireOp",EDGE,"E4916"),sQuery(id+"F14.wireOp",EDGE,"E4917"),sQuery(id+"F14.wireOp",EDGE,"E4918"),sQuery(id+"F14.wireOp",EDGE,"E4919"),sQuery(id+"F14.wireOp",EDGE,"E4920"),sQuery(id+"F14.wireOp",EDGE,"E4921"),sQuery(id+"F14.wireOp",EDGE,"E4922"),sQuery(id+"F14.wireOp",EDGE,"E4923"),sQuery(id+"F14.wireOp",EDGE,"E4924"),sQuery(id+"F14.wireOp",EDGE,"E4925"),sQuery(id+"F14.wireOp",EDGE,"E4926"),sQuery(id+"F14.wireOp",EDGE,"E4927"),sQuery(id+"F14.wireOp",EDGE,"E4928"),sQuery(id+"F14.wireOp",EDGE,"E4929"),sQuery(id+"F14.wireOp",EDGE,"E4930"),sQuery(id+"F14.wireOp",EDGE,"E4931"),sQuery(id+"F14.wireOp",EDGE,"E4932"),sQuery(id+"F14.wireOp",EDGE,"E4933"),sQuery(id+"F14.wireOp",EDGE,"E4934"),sQuery(id+"F14.wireOp",EDGE,"E4935"),sQuery(id+"F14.wireOp",EDGE,"E4936"),sQuery(id+"F14.wireOp",EDGE,"E4937"),sQuery(id+"F14.wireOp",EDGE,"E4938"),sQuery(id+"F14.wireOp",EDGE,"E4939"),sQuery(id+"F14.wireOp",EDGE,"E4940"),sQuery(id+"F14.wireOp",EDGE,"E4941"),sQuery(id+"F14.wireOp",EDGE,"E4942"),sQuery(id+"F14.wireOp",EDGE,"E4943"),sQuery(id+"F14.wireOp",EDGE,"E4944"),sQuery(id+"F14.wireOp",EDGE,"E4945"),sQuery(id+"F14.wireOp",EDGE,"E4946"),sQuery(id+"F14.wireOp",EDGE,"E4947"),sQuery(id+"F14.wireOp",EDGE,"E4948"),sQuery(id+"F14.wireOp",EDGE,"E4949"),sQuery(id+"F14.wireOp",EDGE,"E4950"),sQuery(id+"F14.wireOp",EDGE,"E4951"),sQuery(id+"F14.wireOp",EDGE,"E4952"),sQuery(id+"F14.wireOp",EDGE,"E4953"),sQuery(id+"F14.wireOp",EDGE,"E4954"),sQuery(id+"F14.wireOp",EDGE,"E4955"),sQuery(id+"F14.wireOp",EDGE,"E4956"),sQuery(id+"F14.wireOp",EDGE,"E4957"),sQuery(id+"F14.wireOp",EDGE,"E4958"),sQuery(id+"F14.wireOp",EDGE,"E4959"),sQuery(id+"F14.wireOp",EDGE,"E4960"),sQuery(id+"F14.wireOp",EDGE,"E4961"),sQuery(id+"F14.wireOp",EDGE,"E4962"),sQuery(id+"F14.wireOp",EDGE,"E4963"),sQuery(id+"F14.wireOp",EDGE,"E4964"),sQuery(id+"F14.wireOp",EDGE,"E4965"),sQuery(id+"F14.wireOp",EDGE,"E4966"),sQuery(id+"F14.wireOp",EDGE,"E4967"),sQuery(id+"F14.wireOp",EDGE,"E4968"),sQuery(id+"F14.wireOp",EDGE,"E4969"),sQuery(id+"F14.wireOp",EDGE,"E4970"),sQuery(id+"F14.wireOp",EDGE,"E4971"),sQuery(id+"F14.wireOp",EDGE,"E4972"),sQuery(id+"F14.wireOp",EDGE,"E4973"),sQuery(id+"F14.wireOp",EDGE,"E4974"),sQuery(id+"F14.wireOp",EDGE,"E4975"),sQuery(id+"F14.wireOp",EDGE,"E4976"),sQuery(id+"F14.wireOp",EDGE,"E4977"),sQuery(id+"F14.wireOp",EDGE,"E4978"),sQuery(id+"F14.wireOp",EDGE,"E4979"),sQuery(id+"F14.wireOp",EDGE,"E4980"),sQuery(id+"F14.wireOp",EDGE,"E4981"),sQuery(id+"F14.wireOp",EDGE,"E4982"),sQuery(id+"F14.wireOp",EDGE,"E4983"),sQuery(id+"F14.wireOp",EDGE,"E4984"),sQuery(id+"F14.wireOp",EDGE,"E4985"),sQuery(id+"F14.wireOp",EDGE,"E4986"),sQuery(id+"F14.wireOp",EDGE,"E4987"),sQuery(id+"F14.wireOp",EDGE,"E4988"),sQuery(id+"F14.wireOp",EDGE,"E4989"),sQuery(id+"F14.wireOp",EDGE,"E4990"),sQuery(id+"F14.wireOp",EDGE,"E4991"),sQuery(id+"F14.wireOp",EDGE,"E4992"),sQuery(id+"F14.wireOp",EDGE,"E4993"),sQuery(id+"F14.wireOp",EDGE,"E4994"),sQuery(id+"F14.wireOp",EDGE,"E4995"),sQuery(id+"F14.wireOp",EDGE,"E4996"),sQuery(id+"F14.wireOp",EDGE,"E4997"),sQuery(id+"F14.wireOp",EDGE,"E4998"),sQuery(id+"F14.wireOp",EDGE,"E4999"),sQuery(id+"F14.wireOp",EDGE,"E5000"),sQuery(id+"F14.wireOp",EDGE,"E5001"),sQuery(id+"F14.wireOp",EDGE,"E5002"),sQuery(id+"F14.wireOp",EDGE,"E5003"),sQuery(id+"F14.wireOp",EDGE,"E5004"),sQuery(id+"F14.wireOp",EDGE,"E5005"),sQuery(id+"F14.wireOp",EDGE,"E5006"),sQuery(id+"F14.wireOp",EDGE,"E5007"),sQuery(id+"F14.wireOp",EDGE,"E5008"),sQuery(id+"F14.wireOp",EDGE,"E5009"),sQuery(id+"F14.wireOp",EDGE,"E5010"),sQuery(id+"F14.wireOp",EDGE,"E5011"),sQuery(id+"F14.wireOp",EDGE,"E5012"),sQuery(id+"F14.wireOp",EDGE,"E5013"),sQuery(id+"F14.wireOp",EDGE,"E5014"),sQuery(id+"F14.wireOp",EDGE,"E5015"),sQuery(id+"F14.wireOp",EDGE,"E5016"),sQuery(id+"F14.wireOp",EDGE,"E5017"),sQuery(id+"F14.wireOp",EDGE,"E5018"),sQuery(id+"F14.wireOp",EDGE,"E5019"),sQuery(id+"F14.wireOp",EDGE,"E5020"),sQuery(id+"F14.wireOp",EDGE,"E5021"),sQuery(id+"F14.wireOp",EDGE,"E5022"),sQuery(id+"F14.wireOp",EDGE,"E5023"),sQuery(id+"F14.wireOp",EDGE,"E5024"),sQuery(id+"F14.wireOp",EDGE,"E5025"),sQuery(id+"F14.wireOp",EDGE,"E5026"),sQuery(id+"F14.wireOp",EDGE,"E5027"),sQuery(id+"F14.wireOp",EDGE,"E5028"),sQuery(id+"F14.wireOp",EDGE,"E5029"),sQuery(id+"F14.wireOp",EDGE,"E5030"),sQuery(id+"F14.wireOp",EDGE,"E5031"),sQuery(id+"F14.wireOp",EDGE,"E5032"),sQuery(id+"F14.wireOp",EDGE,"E5033"),sQuery(id+"F14.wireOp",EDGE,"E5034"),sQuery(id+"F14.wireOp",EDGE,"E5035"),sQuery(id+"F14.wireOp",EDGE,"E5036"),sQuery(id+"F14.wireOp",EDGE,"E5037"),sQuery(id+"F14.wireOp",EDGE,"E5038"),sQuery(id+"F14.wireOp",EDGE,"E5039"),sQuery(id+"F14.wireOp",EDGE,"E5040"),sQuery(id+"F14.wireOp",EDGE,"E5041"),sQuery(id+"F14.wireOp",EDGE,"E5042"),sQuery(id+"F14.wireOp",EDGE,"E5043"),sQuery(id+"F14.wireOp",EDGE,"E5044"),sQuery(id+"F14.wireOp",EDGE,"E5045"),sQuery(id+"F14.wireOp",EDGE,"E5046"),sQuery(id+"F14.wireOp",EDGE,"E5047"),sQuery(id+"F14.wireOp",EDGE,"E5048"),sQuery(id+"F14.wireOp",EDGE,"E5049"),sQuery(id+"F14.wireOp",EDGE,"E5050"),sQuery(id+"F14.wireOp",EDGE,"E5051"),sQuery(id+"F14.wireOp",EDGE,"E5052"),sQuery(id+"F14.wireOp",EDGE,"E5053"),sQuery(id+"F14.wireOp",EDGE,"E5054"),sQuery(id+"F14.wireOp",EDGE,"E5055"),sQuery(id+"F14.wireOp",EDGE,"E5056"),sQuery(id+"F14.wireOp",EDGE,"E5057"),sQuery(id+"F14.wireOp",EDGE,"E5058"),sQuery(id+"F14.wireOp",EDGE,"E5059"),sQuery(id+"F14.wireOp",EDGE,"E5060"),sQuery(id+"F14.wireOp",EDGE,"E5061"),sQuery(id+"F14.wireOp",EDGE,"E5062"),sQuery(id+"F14.wireOp",EDGE,"E5063"),sQuery(id+"F14.wireOp",EDGE,"E5064"),sQuery(id+"F14.wireOp",EDGE,"E5065"),sQuery(id+"F14.wireOp",EDGE,"E5066"),sQuery(id+"F14.wireOp",EDGE,"E5067"),sQuery(id+"F14.wireOp",EDGE,"E5068"),sQuery(id+"F14.wireOp",EDGE,"E5069"),sQuery(id+"F14.wireOp",EDGE,"E5070"),sQuery(id+"F14.wireOp",EDGE,"E5071"),sQuery(id+"F14.wireOp",EDGE,"E5072"),sQuery(id+"F14.wireOp",EDGE,"E5073"),sQuery(id+"F14.wireOp",EDGE,"E5074"),sQuery(id+"F14.wireOp",EDGE,"E5075"),sQuery(id+"F14.wireOp",EDGE,"E5076"),sQuery(id+"F14.wireOp",EDGE,"E5077"),sQuery(id+"F14.wireOp",EDGE,"E5078"),sQuery(id+"F14.wireOp",EDGE,"E5079"),sQuery(id+"F14.wireOp",EDGE,"E5080"),sQuery(id+"F14.wireOp",EDGE,"E5081"),sQuery(id+"F14.wireOp",EDGE,"E5082"),sQuery(id+"F14.wireOp",EDGE,"E5083"),sQuery(id+"F14.wireOp",EDGE,"E5084"),sQuery(id+"F14.wireOp",EDGE,"E5085"),sQuery(id+"F14.wireOp",EDGE,"E5086"),sQuery(id+"F14.wireOp",EDGE,"E5087"),sQuery(id+"F14.wireOp",EDGE,"E5088"),sQuery(id+"F14.wireOp",EDGE,"E5089"),sQuery(id+"F14.wireOp",EDGE,"E5090"),sQuery(id+"F14.wireOp",EDGE,"E5091"),sQuery(id+"F14.wireOp",EDGE,"E5092"),sQuery(id+"F14.wireOp",EDGE,"E5093"),sQuery(id+"F14.wireOp",EDGE,"E5094"),sQuery(id+"F14.wireOp",EDGE,"E5095"),sQuery(id+"F14.wireOp",EDGE,"E5096"),sQuery(id+"F14.wireOp",EDGE,"E5097"),sQuery(id+"F14.wireOp",EDGE,"E5098"),sQuery(id+"F14.wireOp",EDGE,"E5099"),sQuery(id+"F14.wireOp",EDGE,"E5100"),sQuery(id+"F14.wireOp",EDGE,"E5101"),sQuery(id+"F14.wireOp",EDGE,"E5102"),sQuery(id+"F14.wireOp",EDGE,"E5103"),sQuery(id+"F14.wireOp",EDGE,"E5104"),sQuery(id+"F14.wireOp",EDGE,"E5105"),sQuery(id+"F14.wireOp",EDGE,"E5106"),sQuery(id+"F14.wireOp",EDGE,"E5107"),sQuery(id+"F14.wireOp",EDGE,"E5108"),sQuery(id+"F14.wireOp",EDGE,"E5109"),sQuery(id+"F14.wireOp",EDGE,"E5110"),sQuery(id+"F14.wireOp",EDGE,"E5111"),sQuery(id+"F14.wireOp",EDGE,"E5112"),sQuery(id+"F14.wireOp",EDGE,"E5113"),sQuery(id+"F14.wireOp",EDGE,"E5114"),sQuery(id+"F14.wireOp",EDGE,"E5115"),sQuery(id+"F14.wireOp",EDGE,"E5116"),sQuery(id+"F14.wireOp",EDGE,"E5117"),sQuery(id+"F14.wireOp",EDGE,"E5118"),sQuery(id+"F14.wireOp",EDGE,"E5119"),sQuery(id+"F14.wireOp",EDGE,"E5120"),sQuery(id+"F14.wireOp",EDGE,"E5121"),sQuery(id+"F14.wireOp",EDGE,"E5122"),sQuery(id+"F14.wireOp",EDGE,"E5123"),sQuery(id+"F14.wireOp",EDGE,"E5124"),sQuery(id+"F14.wireOp",EDGE,"E5125"),sQuery(id+"F14.wireOp",EDGE,"E5126"),sQuery(id+"F14.wireOp",EDGE,"E5127"),sQuery(id+"F14.wireOp",EDGE,"E5128"),sQuery(id+"F14.wireOp",EDGE,"E5129"),sQuery(id+"F14.wireOp",EDGE,"E5130"),sQuery(id+"F14.wireOp",EDGE,"E5131"),sQuery(id+"F14.wireOp",EDGE,"E5132"),sQuery(id+"F14.wireOp",EDGE,"E5133"),sQuery(id+"F14.wireOp",EDGE,"E5134"),sQuery(id+"F14.wireOp",EDGE,"E5135"),sQuery(id+"F14.wireOp",EDGE,"E5136"),sQuery(id+"F14.wireOp",EDGE,"E5137"),sQuery(id+"F14.wireOp",EDGE,"E5138"),sQuery(id+"F14.wireOp",EDGE,"E5139"),sQuery(id+"F14.wireOp",EDGE,"E5140"),sQuery(id+"F14.wireOp",EDGE,"E5141"),sQuery(id+"F14.wireOp",EDGE,"E5142"),sQuery(id+"F14.wireOp",EDGE,"E5143"),sQuery(id+"F14.wireOp",EDGE,"E5144"),sQuery(id+"F14.wireOp",EDGE,"E5145"),sQuery(id+"F14.wireOp",EDGE,"E5146"),sQuery(id+"F14.wireOp",EDGE,"E5147"),sQuery(id+"F14.wireOp",EDGE,"E5148"),sQuery(id+"F14.wireOp",EDGE,"E5149"),sQuery(id+"F14.wireOp",EDGE,"E5150"),sQuery(id+"F14.wireOp",EDGE,"E5151"),sQuery(id+"F14.wireOp",EDGE,"E5152"),sQuery(id+"F14.wireOp",EDGE,"E5153"),sQuery(id+"F14.wireOp",EDGE,"E5154"),sQuery(id+"F14.wireOp",EDGE,"E5155"),sQuery(id+"F14.wireOp",EDGE,"E5156"),sQuery(id+"F14.wireOp",EDGE,"E5157"),sQuery(id+"F14.wireOp",EDGE,"E5158"),sQuery(id+"F14.wireOp",EDGE,"E5159"),sQuery(id+"F14.wireOp",EDGE,"E5160"),sQuery(id+"F14.wireOp",EDGE,"E5161"),sQuery(id+"F14.wireOp",EDGE,"E5162"),sQuery(id+"F14.wireOp",EDGE,"E5163"),sQuery(id+"F14.wireOp",EDGE,"E5164"),sQuery(id+"F14.wireOp",EDGE,"E5165"),sQuery(id+"F14.wireOp",EDGE,"E5166"),sQuery(id+"F14.wireOp",EDGE,"E5167"),sQuery(id+"F14.wireOp",EDGE,"E5168"),sQuery(id+"F14.wireOp",EDGE,"E5169"),sQuery(id+"F14.wireOp",EDGE,"E5170"),sQuery(id+"F14.wireOp",EDGE,"E5171"),sQuery(id+"F14.wireOp",EDGE,"E5172"),sQuery(id+"F14.wireOp",EDGE,"E5173"),sQuery(id+"F14.wireOp",EDGE,"E5174"),sQuery(id+"F14.wireOp",EDGE,"E5175"),sQuery(id+"F14.wireOp",EDGE,"E5176"),sQuery(id+"F14.wireOp",EDGE,"E5177"),sQuery(id+"F14.wireOp",EDGE,"E5178"),sQuery(id+"F14.wireOp",EDGE,"E5179"),sQuery(id+"F14.wireOp",EDGE,"E5180"),sQuery(id+"F14.wireOp",EDGE,"E5181"),sQuery(id+"F14.wireOp",EDGE,"E5182"),sQuery(id+"F14.wireOp",EDGE,"E5183"),sQuery(id+"F14.wireOp",EDGE,"E5184"),sQuery(id+"F14.wireOp",EDGE,"E5185"),sQuery(id+"F14.wireOp",EDGE,"E5186"),sQuery(id+"F14.wireOp",EDGE,"E5187"),sQuery(id+"F14.wireOp",EDGE,"E5188"),sQuery(id+"F14.wireOp",EDGE,"E5189"),sQuery(id+"F14.wireOp",EDGE,"E5190"),sQuery(id+"F14.wireOp",EDGE,"E5191"),sQuery(id+"F14.wireOp",EDGE,"E5192"),sQuery(id+"F14.wireOp",EDGE,"E5193"),sQuery(id+"F14.wireOp",EDGE,"E5194"),sQuery(id+"F14.wireOp",EDGE,"E5195"),sQuery(id+"F14.wireOp",EDGE,"E5196"),sQuery(id+"F14.wireOp",EDGE,"E5197"),sQuery(id+"F14.wireOp",EDGE,"E5198"),sQuery(id+"F14.wireOp",EDGE,"E5199"),sQuery(id+"F14.wireOp",EDGE,"E5200"),sQuery(id+"F14.wireOp",EDGE,"E5201"),sQuery(id+"F14.wireOp",EDGE,"E5202"),sQuery(id+"F14.wireOp",EDGE,"E5203"),sQuery(id+"F14.wireOp",EDGE,"E5204"),sQuery(id+"F14.wireOp",EDGE,"E5205"),sQuery(id+"F14.wireOp",EDGE,"E5206"),sQuery(id+"F14.wireOp",EDGE,"E5207"),sQuery(id+"F14.wireOp",EDGE,"E5208"),sQuery(id+"F14.wireOp",EDGE,"E5209"),sQuery(id+"F14.wireOp",EDGE,"E5210"),sQuery(id+"F14.wireOp",EDGE,"E5211"),sQuery(id+"F14.wireOp",EDGE,"E5212"),sQuery(id+"F14.wireOp",EDGE,"E5213"),sQuery(id+"F14.wireOp",EDGE,"E5214"),sQuery(id+"F14.wireOp",EDGE,"E5215"),sQuery(id+"F14.wireOp",EDGE,"E5216"),sQuery(id+"F14.wireOp",EDGE,"E5217"),sQuery(id+"F14.wireOp",EDGE,"E5218"),sQuery(id+"F14.wireOp",EDGE,"E5219"),sQuery(id+"F14.wireOp",EDGE,"E5220"),sQuery(id+"F14.wireOp",EDGE,"E5221"),sQuery(id+"F14.wireOp",EDGE,"E5222"),sQuery(id+"F14.wireOp",EDGE,"E5223"),sQuery(id+"F14.wireOp",EDGE,"E5224"),sQuery(id+"F14.wireOp",EDGE,"E5225"),sQuery(id+"F14.wireOp",EDGE,"E5226"),sQuery(id+"F14.wireOp",EDGE,"E5227"),sQuery(id+"F14.wireOp",EDGE,"E5228"),sQuery(id+"F14.wireOp",EDGE,"E5229"),sQuery(id+"F14.wireOp",EDGE,"E5230"),sQuery(id+"F14.wireOp",EDGE,"E5231"),sQuery(id+"F14.wireOp",EDGE,"E5232"),sQuery(id+"F14.wireOp",EDGE,"E5233"),sQuery(id+"F14.wireOp",EDGE,"E5234"),sQuery(id+"F14.wireOp",EDGE,"E5235"),sQuery(id+"F14.wireOp",EDGE,"E5236"),sQuery(id+"F14.wireOp",EDGE,"E5237"),sQuery(id+"F14.wireOp",EDGE,"E5238"),sQuery(id+"F14.wireOp",EDGE,"E5239"),sQuery(id+"F14.wireOp",EDGE,"E5240"),sQuery(id+"F14.wireOp",EDGE,"E5241"),sQuery(id+"F14.wireOp",EDGE,"E5242"),sQuery(id+"F14.wireOp",EDGE,"E5243"),sQuery(id+"F14.wireOp",EDGE,"E5244"),sQuery(id+"F14.wireOp",EDGE,"E5245"),sQuery(id+"F14.wireOp",EDGE,"E5246"),sQuery(id+"F14.wireOp",EDGE,"E5247"),sQuery(id+"F14.wireOp",EDGE,"E5248"),sQuery(id+"F14.wireOp",EDGE,"E5249"),sQuery(id+"F14.wireOp",EDGE,"E5250"),sQuery(id+"F14.wireOp",EDGE,"E5251"),sQuery(id+"F14.wireOp",EDGE,"E5252"),sQuery(id+"F14.wireOp",EDGE,"E5253"),sQuery(id+"F14.wireOp",EDGE,"E5254"),sQuery(id+"F14.wireOp",EDGE,"E5255"),sQuery(id+"F14.wireOp",EDGE,"E5256"),sQuery(id+"F14.wireOp",EDGE,"E5257"),sQuery(id+"F14.wireOp",EDGE,"E5258"),sQuery(id+"F14.wireOp",EDGE,"E5259"),sQuery(id+"F14.wireOp",EDGE,"E5260"),sQuery(id+"F14.wireOp",EDGE,"E5261"),sQuery(id+"F14.wireOp",EDGE,"E5262"),sQuery(id+"F14.wireOp",EDGE,"E5263"),sQuery(id+"F14.wireOp",EDGE,"E5264"),sQuery(id+"F14.wireOp",EDGE,"E5265"),sQuery(id+"F14.wireOp",EDGE,"E5266"),sQuery(id+"F14.wireOp",EDGE,"E5267"),sQuery(id+"F14.wireOp",EDGE,"E5268"),sQuery(id+"F14.wireOp",EDGE,"E5269"),sQuery(id+"F14.wireOp",EDGE,"E5270"),sQuery(id+"F14.wireOp",EDGE,"E5271"),sQuery(id+"F14.wireOp",EDGE,"E5272"),sQuery(id+"F14.wireOp",EDGE,"E5273"),sQuery(id+"F14.wireOp",EDGE,"E5274"),sQuery(id+"F14.wireOp",EDGE,"E5275"),sQuery(id+"F14.wireOp",EDGE,"E5276"),sQuery(id+"F14.wireOp",EDGE,"E5277"),sQuery(id+"F14.wireOp",EDGE,"E5278"),sQuery(id+"F14.wireOp",EDGE,"E5279"),sQuery(id+"F14.wireOp",EDGE,"E5280"),sQuery(id+"F14.wireOp",EDGE,"E5281"),sQuery(id+"F14.wireOp",EDGE,"E5282"),sQuery(id+"F14.wireOp",EDGE,"E5283"),sQuery(id+"F14.wireOp",EDGE,"E5284"),sQuery(id+"F14.wireOp",EDGE,"E5285"),sQuery(id+"F14.wireOp",EDGE,"E5286"),sQuery(id+"F14.wireOp",EDGE,"E5287"),sQuery(id+"F14.wireOp",EDGE,"E5288"),sQuery(id+"F14.wireOp",EDGE,"E5289"),sQuery(id+"F14.wireOp",EDGE,"E5290"),sQuery(id+"F14.wireOp",EDGE,"E5291"),sQuery(id+"F14.wireOp",EDGE,"E5292"),sQuery(id+"F14.wireOp",EDGE,"E5293"),sQuery(id+"F14.wireOp",EDGE,"E5294"),sQuery(id+"F14.wireOp",EDGE,"E5295"),sQuery(id+"F14.wireOp",EDGE,"E5296"),sQuery(id+"F14.wireOp",EDGE,"E5297"),sQuery(id+"F14.wireOp",EDGE,"E5298"),sQuery(id+"F14.wireOp",EDGE,"E5299"),sQuery(id+"F14.wireOp",EDGE,"E5300"),sQuery(id+"F14.wireOp",EDGE,"E5301"),sQuery(id+"F14.wireOp",EDGE,"E5302"),sQuery(id+"F14.wireOp",EDGE,"E5303"),sQuery(id+"F14.wireOp",EDGE,"E5304"),sQuery(id+"F14.wireOp",EDGE,"E5305"),sQuery(id+"F14.wireOp",EDGE,"E5306"),sQuery(id+"F14.wireOp",EDGE,"E5307"),sQuery(id+"F14.wireOp",EDGE,"E5308"),sQuery(id+"F14.wireOp",EDGE,"E5309"),sQuery(id+"F14.wireOp",EDGE,"E5310"),sQuery(id+"F14.wireOp",EDGE,"E5311"),sQuery(id+"F14.wireOp",EDGE,"E5312"),sQuery(id+"F14.wireOp",EDGE,"E5313"),sQuery(id+"F14.wireOp",EDGE,"E5314"),sQuery(id+"F14.wireOp",EDGE,"E5315"),sQuery(id+"F14.wireOp",EDGE,"E5316"),sQuery(id+"F14.wireOp",EDGE,"E5317"),sQuery(id+"F14.wireOp",EDGE,"E5318"),sQuery(id+"F14.wireOp",EDGE,"E5319"),sQuery(id+"F14.wireOp",EDGE,"E5320"),sQuery(id+"F14.wireOp",EDGE,"E5321"),sQuery(id+"F14.wireOp",EDGE,"E5322"),sQuery(id+"F14.wireOp",EDGE,"E5323"),sQuery(id+"F14.wireOp",EDGE,"E5324"),sQuery(id+"F14.wireOp",EDGE,"E5325"),sQuery(id+"F14.wireOp",EDGE,"E5326"),sQuery(id+"F14.wireOp",EDGE,"E5327"),sQuery(id+"F14.wireOp",EDGE,"E5328"),sQuery(id+"F14.wireOp",EDGE,"E5329"),sQuery(id+"F14.wireOp",EDGE,"E5330"),sQuery(id+"F14.wireOp",EDGE,"E5331"),sQuery(id+"F14.wireOp",EDGE,"E5332"),sQuery(id+"F14.wireOp",EDGE,"E5333"),sQuery(id+"F14.wireOp",EDGE,"E5334"),sQuery(id+"F14.wireOp",EDGE,"E5335"),sQuery(id+"F14.wireOp",EDGE,"E5336"),sQuery(id+"F14.wireOp",EDGE,"E5337"),sQuery(id+"F14.wireOp",EDGE,"E5338"),sQuery(id+"F14.wireOp",EDGE,"E5339"),sQuery(id+"F14.wireOp",EDGE,"E5340"),sQuery(id+"F14.wireOp",EDGE,"E5341"),sQuery(id+"F14.wireOp",EDGE,"E5342"),sQuery(id+"F14.wireOp",EDGE,"E5343"),sQuery(id+"F14.wireOp",EDGE,"E5344"),sQuery(id+"F14.wireOp",EDGE,"E5345"),sQuery(id+"F14.wireOp",EDGE,"E5346"),sQuery(id+"F14.wireOp",EDGE,"E5347"),sQuery(id+"F14.wireOp",EDGE,"E5348"),sQuery(id+"F14.wireOp",EDGE,"E5349"),sQuery(id+"F14.wireOp",EDGE,"E5350"),sQuery(id+"F14.wireOp",EDGE,"E5351"),sQuery(id+"F14.wireOp",EDGE,"E5352"),sQuery(id+"F14.wireOp",EDGE,"E5353"),sQuery(id+"F14.wireOp",EDGE,"E5354"),sQuery(id+"F14.wireOp",EDGE,"E5355"),sQuery(id+"F14.wireOp",EDGE,"E5356"),sQuery(id+"F14.wireOp",EDGE,"E5357"),sQuery(id+"F14.wireOp",EDGE,"E5358"),sQuery(id+"F14.wireOp",EDGE,"E5359"),sQuery(id+"F14.wireOp",EDGE,"E5360"),sQuery(id+"F14.wireOp",EDGE,"E5361"),sQuery(id+"F14.wireOp",EDGE,"E5362"),sQuery(id+"F14.wireOp",EDGE,"E5363"),sQuery(id+"F14.wireOp",EDGE,"E5364"),sQuery(id+"F14.wireOp",EDGE,"E5365"),sQuery(id+"F14.wireOp",EDGE,"E5366"),sQuery(id+"F14.wireOp",EDGE,"E5367"),sQuery(id+"F14.wireOp",EDGE,"E5368"),sQuery(id+"F14.wireOp",EDGE,"E5369"),sQuery(id+"F14.wireOp",EDGE,"E5370"),sQuery(id+"F14.wireOp",EDGE,"E5371"),sQuery(id+"F14.wireOp",EDGE,"E5372"),sQuery(id+"F14.wireOp",EDGE,"E5373"),sQuery(id+"F14.wireOp",EDGE,"E5374"),sQuery(id+"F14.wireOp",EDGE,"E5375"),sQuery(id+"F14.wireOp",EDGE,"E5376"),sQuery(id+"F14.wireOp",EDGE,"E5377"),sQuery(id+"F14.wireOp",EDGE,"E5378"),sQuery(id+"F14.wireOp",EDGE,"E5379"),sQuery(id+"F14.wireOp",EDGE,"E5380"),sQuery(id+"F14.wireOp",EDGE,"E5381"),sQuery(id+"F14.wireOp",EDGE,"E5382"),sQuery(id+"F14.wireOp",EDGE,"E5383"),sQuery(id+"F14.wireOp",EDGE,"E5384"),sQuery(id+"F14.wireOp",EDGE,"E5385"),sQuery(id+"F14.wireOp",EDGE,"E5386"),sQuery(id+"F14.wireOp",EDGE,"E5387"),sQuery(id+"F14.wireOp",EDGE,"E5388"),sQuery(id+"F14.wireOp",EDGE,"E5389"),sQuery(id+"F14.wireOp",EDGE,"E5390"),sQuery(id+"F14.wireOp",EDGE,"E5391"),sQuery(id+"F14.wireOp",EDGE,"E5392"),sQuery(id+"F14.wireOp",EDGE,"E5393"),sQuery(id+"F14.wireOp",EDGE,"E5394"),sQuery(id+"F14.wireOp",EDGE,"E5395"),sQuery(id+"F14.wireOp",EDGE,"E5396"),sQuery(id+"F14.wireOp",EDGE,"E5397"),sQuery(id+"F14.wireOp",EDGE,"E5398"),sQuery(id+"F14.wireOp",EDGE,"E5399"),sQuery(id+"F14.wireOp",EDGE,"E5400"),sQuery(id+"F14.wireOp",EDGE,"E5401"),sQuery(id+"F14.wireOp",EDGE,"E5402"),sQuery(id+"F14.wireOp",EDGE,"E5403"),sQuery(id+"F14.wireOp",EDGE,"E5404"),sQuery(id+"F14.wireOp",EDGE,"E5405"),sQuery(id+"F14.wireOp",EDGE,"E5406"),sQuery(id+"F14.wireOp",EDGE,"E5407"),sQuery(id+"F14.wireOp",EDGE,"E5408"),sQuery(id+"F14.wireOp",EDGE,"E5409"),sQuery(id+"F14.wireOp",EDGE,"E5410"),sQuery(id+"F14.wireOp",EDGE,"E5411"),sQuery(id+"F14.wireOp",EDGE,"E5412"),sQuery(id+"F14.wireOp",EDGE,"E5413"),sQuery(id+"F14.wireOp",EDGE,"E5414"),sQuery(id+"F14.wireOp",EDGE,"E5415"),sQuery(id+"F14.wireOp",EDGE,"E5416"),sQuery(id+"F14.wireOp",EDGE,"E5417"),sQuery(id+"F14.wireOp",EDGE,"E5418"),sQuery(id+"F14.wireOp",EDGE,"E5419"),sQuery(id+"F14.wireOp",EDGE,"E5420"),sQuery(id+"F14.wireOp",EDGE,"E5421"),sQuery(id+"F14.wireOp",EDGE,"E5422"),sQuery(id+"F14.wireOp",EDGE,"E5423"),sQuery(id+"F14.wireOp",EDGE,"E5424"),sQuery(id+"F14.wireOp",EDGE,"E5425"),sQuery(id+"F14.wireOp",EDGE,"E5426"),sQuery(id+"F14.wireOp",EDGE,"E5427"),sQuery(id+"F14.wireOp",EDGE,"E5428"),sQuery(id+"F14.wireOp",EDGE,"E5429"),sQuery(id+"F14.wireOp",EDGE,"E5430"),sQuery(id+"F14.wireOp",EDGE,"E5431"),sQuery(id+"F14.wireOp",EDGE,"E5432"),sQuery(id+"F14.wireOp",EDGE,"E5433"),sQuery(id+"F14.wireOp",EDGE,"E5434"),sQuery(id+"F14.wireOp",EDGE,"E5435"),sQuery(id+"F14.wireOp",EDGE,"E5436"),sQuery(id+"F14.wireOp",EDGE,"E5437"),sQuery(id+"F14.wireOp",EDGE,"E5438"),sQuery(id+"F14.wireOp",EDGE,"E5439"),sQuery(id+"F14.wireOp",EDGE,"E5440"),sQuery(id+"F14.wireOp",EDGE,"E5441"),sQuery(id+"F14.wireOp",EDGE,"E5442"),sQuery(id+"F14.wireOp",EDGE,"E5443"),sQuery(id+"F14.wireOp",EDGE,"E5444"),sQuery(id+"F14.wireOp",EDGE,"E5445"),sQuery(id+"F14.wireOp",EDGE,"E5446"),sQuery(id+"F14.wireOp",EDGE,"E5447"),sQuery(id+"F14.wireOp",EDGE,"E5448"),sQuery(id+"F14.wireOp",EDGE,"E5449"),sQuery(id+"F14.wireOp",EDGE,"E5450"),sQuery(id+"F14.wireOp",EDGE,"E5451"),sQuery(id+"F14.wireOp",EDGE,"E5452"),sQuery(id+"F14.wireOp",EDGE,"E5453"),sQuery(id+"F14.wireOp",EDGE,"E5454"),sQuery(id+"F14.wireOp",EDGE,"E5455"),sQuery(id+"F14.wireOp",EDGE,"E5456"),sQuery(id+"F14.wireOp",EDGE,"E5457"),sQuery(id+"F14.wireOp",EDGE,"E5458"),sQuery(id+"F14.wireOp",EDGE,"E5459"),sQuery(id+"F14.wireOp",EDGE,"E5460"),sQuery(id+"F14.wireOp",EDGE,"E5461"),sQuery(id+"F14.wireOp",EDGE,"E5462"),sQuery(id+"F14.wireOp",EDGE,"E5463"),sQuery(id+"F14.wireOp",EDGE,"E5464"),sQuery(id+"F14.wireOp",EDGE,"E5465"),sQuery(id+"F14.wireOp",EDGE,"E5466"),sQuery(id+"F14.wireOp",EDGE,"E5467"),sQuery(id+"F14.wireOp",EDGE,"E5468"),sQuery(id+"F14.wireOp",EDGE,"E5469"),sQuery(id+"F14.wireOp",EDGE,"E5470"),sQuery(id+"F14.wireOp",EDGE,"E5471"),sQuery(id+"F14.wireOp",EDGE,"E5472"),sQuery(id+"F14.wireOp",EDGE,"E5473"),sQuery(id+"F14.wireOp",EDGE,"E5474"),sQuery(id+"F14.wireOp",EDGE,"E5475"),sQuery(id+"F14.wireOp",EDGE,"E5476"),sQuery(id+"F14.wireOp",EDGE,"E5477"),sQuery(id+"F14.wireOp",EDGE,"E5478"),sQuery(id+"F14.wireOp",EDGE,"E5479"),sQuery(id+"F14.wireOp",EDGE,"E5480"),sQuery(id+"F14.wireOp",EDGE,"E5481"),sQuery(id+"F14.wireOp",EDGE,"E5482"),sQuery(id+"F14.wireOp",EDGE,"E5483"),sQuery(id+"F14.wireOp",EDGE,"E5484"),sQuery(id+"F14.wireOp",EDGE,"E5485"),sQuery(id+"F14.wireOp",EDGE,"E5486"),sQuery(id+"F14.wireOp",EDGE,"E5487"),sQuery(id+"F14.wireOp",EDGE,"E5488"),sQuery(id+"F14.wireOp",EDGE,"E5489"),sQuery(id+"F14.wireOp",EDGE,"E5490"),sQuery(id+"F14.wireOp",EDGE,"E5491"),sQuery(id+"F14.wireOp",EDGE,"E5492"),sQuery(id+"F14.wireOp",EDGE,"E5493"),sQuery(id+"F14.wireOp",EDGE,"E5494"),sQuery(id+"F14.wireOp",EDGE,"E5495"),sQuery(id+"F14.wireOp",EDGE,"E5496"),sQuery(id+"F14.wireOp",EDGE,"E5497"),sQuery(id+"F14.wireOp",EDGE,"E5498"),sQuery(id+"F14.wireOp",EDGE,"E5499"),sQuery(id+"F14.wireOp",EDGE,"E5500"),sQuery(id+"F14.wireOp",EDGE,"E5501"),sQuery(id+"F14.wireOp",EDGE,"E5502"),sQuery(id+"F14.wireOp",EDGE,"E5503"),sQuery(id+"F14.wireOp",EDGE,"E5504"),sQuery(id+"F14.wireOp",EDGE,"E5505"),sQuery(id+"F14.wireOp",EDGE,"E5506"),sQuery(id+"F14.wireOp",EDGE,"E5507"),sQuery(id+"F14.wireOp",EDGE,"E5508"),sQuery(id+"F14.wireOp",EDGE,"E5509"),sQuery(id+"F14.wireOp",EDGE,"E5510"),sQuery(id+"F14.wireOp",EDGE,"E5511"),sQuery(id+"F14.wireOp",EDGE,"E5512"),sQuery(id+"F14.wireOp",EDGE,"E5513"),sQuery(id+"F14.wireOp",EDGE,"E5514"),sQuery(id+"F14.wireOp",EDGE,"E5515"),sQuery(id+"F14.wireOp",EDGE,"E5516"),sQuery(id+"F14.wireOp",EDGE,"E5517"),sQuery(id+"F14.wireOp",EDGE,"E5518"),sQuery(id+"F14.wireOp",EDGE,"E5519"),sQuery(id+"F14.wireOp",EDGE,"E5520"),sQuery(id+"F14.wireOp",EDGE,"E5521"),sQuery(id+"F14.wireOp",EDGE,"E5522"),sQuery(id+"F14.wireOp",EDGE,"E5523"),sQuery(id+"F14.wireOp",EDGE,"E5524"),sQuery(id+"F14.wireOp",EDGE,"E5525"),sQuery(id+"F14.wireOp",EDGE,"E5526"),sQuery(id+"F14.wireOp",EDGE,"E5527"),sQuery(id+"F14.wireOp",EDGE,"E5528"),sQuery(id+"F14.wireOp",EDGE,"E5529"),sQuery(id+"F14.wireOp",EDGE,"E5530"),sQuery(id+"F14.wireOp",EDGE,"E5531"),sQuery(id+"F14.wireOp",EDGE,"E5532"),sQuery(id+"F14.wireOp",EDGE,"E5533"),sQuery(id+"F14.wireOp",EDGE,"E5534"),sQuery(id+"F14.wireOp",EDGE,"E5535"),sQuery(id+"F14.wireOp",EDGE,"E5536"),sQuery(id+"F14.wireOp",EDGE,"E5537"),sQuery(id+"F14.wireOp",EDGE,"E5538"),sQuery(id+"F14.wireOp",EDGE,"E5539"),sQuery(id+"F14.wireOp",EDGE,"E5540"),sQuery(id+"F14.wireOp",EDGE,"E5541"),sQuery(id+"F14.wireOp",EDGE,"E5542"),sQuery(id+"F14.wireOp",EDGE,"E5543"),sQuery(id+"F14.wireOp",EDGE,"E5544"),sQuery(id+"F14.wireOp",EDGE,"E5545"),sQuery(id+"F14.wireOp",EDGE,"E5546"),sQuery(id+"F14.wireOp",EDGE,"E5547"),sQuery(id+"F14.wireOp",EDGE,"E5548"),sQuery(id+"F14.wireOp",EDGE,"E5549"),sQuery(id+"F14.wireOp",EDGE,"E5550"),sQuery(id+"F14.wireOp",EDGE,"E5551"),sQuery(id+"F14.wireOp",EDGE,"E5552"),sQuery(id+"F14.wireOp",EDGE,"E5553"),sQuery(id+"F14.wireOp",EDGE,"E5554"),sQuery(id+"F14.wireOp",EDGE,"E5555"),sQuery(id+"F14.wireOp",EDGE,"E5556"),sQuery(id+"F14.wireOp",EDGE,"E5557"),sQuery(id+"F14.wireOp",EDGE,"E5558"),sQuery(id+"F14.wireOp",EDGE,"E5559"),sQuery(id+"F14.wireOp",EDGE,"E5560"),sQuery(id+"F14.wireOp",EDGE,"E5561"),sQuery(id+"F14.wireOp",EDGE,"E5562"),sQuery(id+"F14.wireOp",EDGE,"E5563"),sQuery(id+"F14.wireOp",EDGE,"E5564"),sQuery(id+"F14.wireOp",EDGE,"E5565"),sQuery(id+"F14.wireOp",EDGE,"E5566"),sQuery(id+"F14.wireOp",EDGE,"E5567"),sQuery(id+"F14.wireOp",EDGE,"E5568"),sQuery(id+"F14.wireOp",EDGE,"E5569"),sQuery(id+"F14.wireOp",EDGE,"E5570"),sQuery(id+"F14.wireOp",EDGE,"E5571"),sQuery(id+"F14.wireOp",EDGE,"E5572"),sQuery(id+"F14.wireOp",EDGE,"E5573"),sQuery(id+"F14.wireOp",EDGE,"E5574"),sQuery(id+"F14.wireOp",EDGE,"E5575"),sQuery(id+"F14.wireOp",EDGE,"E5576"),sQuery(id+"F14.wireOp",EDGE,"E5577"),sQuery(id+"F14.wireOp",EDGE,"E5578"),sQuery(id+"F14.wireOp",EDGE,"E5579"),sQuery(id+"F14.wireOp",EDGE,"E5580"),sQuery(id+"F14.wireOp",EDGE,"E5581"),sQuery(id+"F14.wireOp",EDGE,"E5582"),sQuery(id+"F14.wireOp",EDGE,"E5583"),sQuery(id+"F14.wireOp",EDGE,"E5584"),sQuery(id+"F14.wireOp",EDGE,"E5585"),sQuery(id+"F14.wireOp",EDGE,"E5586"),sQuery(id+"F14.wireOp",EDGE,"E5587"),sQuery(id+"F14.wireOp",EDGE,"E5588"),sQuery(id+"F14.wireOp",EDGE,"E5589"),sQuery(id+"F14.wireOp",EDGE,"E5590"),sQuery(id+"F14.wireOp",EDGE,"E5591"),sQuery(id+"F14.wireOp",EDGE,"E5592"),sQuery(id+"F14.wireOp",EDGE,"E5593"),sQuery(id+"F14.wireOp",EDGE,"E5594"),sQuery(id+"F14.wireOp",EDGE,"E5595"),sQuery(id+"F14.wireOp",EDGE,"E5596"),sQuery(id+"F14.wireOp",EDGE,"E5597"),sQuery(id+"F14.wireOp",EDGE,"E5598"),sQuery(id+"F14.wireOp",EDGE,"E5599"),sQuery(id+"F14.wireOp",EDGE,"E5600"),sQuery(id+"F14.wireOp",EDGE,"E5601"),sQuery(id+"F14.wireOp",EDGE,"E5602"),sQuery(id+"F14.wireOp",EDGE,"E5603"),sQuery(id+"F14.wireOp",EDGE,"E5604"),sQuery(id+"F14.wireOp",EDGE,"E5605"),sQuery(id+"F14.wireOp",EDGE,"E5606"),sQuery(id+"F14.wireOp",EDGE,"E5607"),sQuery(id+"F14.wireOp",EDGE,"E5608"),sQuery(id+"F14.wireOp",EDGE,"E5609"),sQuery(id+"F14.wireOp",EDGE,"E5610"),sQuery(id+"F14.wireOp",EDGE,"E5611"),sQuery(id+"F14.wireOp",EDGE,"E5612"),sQuery(id+"F14.wireOp",EDGE,"E5613"),sQuery(id+"F14.wireOp",EDGE,"E5614"),sQuery(id+"F14.wireOp",EDGE,"E5615"),sQuery(id+"F14.wireOp",EDGE,"E5616"),sQuery(id+"F14.wireOp",EDGE,"E5617"),sQuery(id+"F14.wireOp",EDGE,"E5618"),sQuery(id+"F14.wireOp",EDGE,"E5619"),sQuery(id+"F14.wireOp",EDGE,"E5620"),sQuery(id+"F14.wireOp",EDGE,"E5621"),sQuery(id+"F14.wireOp",EDGE,"E5622"),sQuery(id+"F14.wireOp",EDGE,"E5623"),sQuery(id+"F14.wireOp",EDGE,"E5624"),sQuery(id+"F14.wireOp",EDGE,"E5625"),sQuery(id+"F14.wireOp",EDGE,"E5626"),sQuery(id+"F14.wireOp",EDGE,"E5627"),sQuery(id+"F14.wireOp",EDGE,"E5628"),sQuery(id+"F14.wireOp",EDGE,"E5629"),sQuery(id+"F14.wireOp",EDGE,"E5630"),sQuery(id+"F14.wireOp",EDGE,"E5631"),sQuery(id+"F14.wireOp",EDGE,"E5632"),sQuery(id+"F14.wireOp",EDGE,"E5633"),sQuery(id+"F14.wireOp",EDGE,"E5634"),sQuery(id+"F14.wireOp",EDGE,"E5635"),sQuery(id+"F14.wireOp",EDGE,"E5636"),sQuery(id+"F14.wireOp",EDGE,"E5637"),sQuery(id+"F14.wireOp",EDGE,"E5638"),sQuery(id+"F14.wireOp",EDGE,"E5639"),sQuery(id+"F14.wireOp",EDGE,"E5640"),sQuery(id+"F14.wireOp",EDGE,"E5641"),sQuery(id+"F14.wireOp",EDGE,"E5642"),sQuery(id+"F14.wireOp",EDGE,"E5643"),sQuery(id+"F14.wireOp",EDGE,"E5644"),sQuery(id+"F14.wireOp",EDGE,"E5645"),sQuery(id+"F14.wireOp",EDGE,"E5646"),sQuery(id+"F14.wireOp",EDGE,"E5647"),sQuery(id+"F14.wireOp",EDGE,"E5648"),sQuery(id+"F14.wireOp",EDGE,"E5649"),sQuery(id+"F14.wireOp",EDGE,"E5650"),sQuery(id+"F14.wireOp",EDGE,"E5651"),sQuery(id+"F14.wireOp",EDGE,"E5652"),sQuery(id+"F14.wireOp",EDGE,"E5653"),sQuery(id+"F14.wireOp",EDGE,"E5654"),sQuery(id+"F14.wireOp",EDGE,"E5655"),sQuery(id+"F14.wireOp",EDGE,"E5656"),sQuery(id+"F14.wireOp",EDGE,"E5657"),sQuery(id+"F14.wireOp",EDGE,"E5658"),sQuery(id+"F14.wireOp",EDGE,"E5659"),sQuery(id+"F14.wireOp",EDGE,"E5660"),sQuery(id+"F14.wireOp",EDGE,"E5661"),sQuery(id+"F14.wireOp",EDGE,"E5662"),sQuery(id+"F14.wireOp",EDGE,"E5663"),sQuery(id+"F14.wireOp",EDGE,"E5664"),sQuery(id+"F14.wireOp",EDGE,"E5665"),sQuery(id+"F14.wireOp",EDGE,"E5666"),sQuery(id+"F14.wireOp",EDGE,"E5667"),sQuery(id+"F14.wireOp",EDGE,"E5668"),sQuery(id+"F14.wireOp",EDGE,"E5669"),sQuery(id+"F14.wireOp",EDGE,"E5670"),sQuery(id+"F14.wireOp",EDGE,"E5671"),sQuery(id+"F14.wireOp",EDGE,"E5672"),sQuery(id+"F14.wireOp",EDGE,"E5673"),sQuery(id+"F14.wireOp",EDGE,"E5674"),sQuery(id+"F14.wireOp",EDGE,"E5675"),sQuery(id+"F14.wireOp",EDGE,"E5676"),sQuery(id+"F14.wireOp",EDGE,"E5677"),sQuery(id+"F14.wireOp",EDGE,"E5678"),sQuery(id+"F14.wireOp",EDGE,"E5679"),sQuery(id+"F14.wireOp",EDGE,"E5680"),sQuery(id+"F14.wireOp",EDGE,"E5681"),sQuery(id+"F14.wireOp",EDGE,"E5682"),sQuery(id+"F14.wireOp",EDGE,"E5683"),sQuery(id+"F14.wireOp",EDGE,"E5684"),sQuery(id+"F14.wireOp",EDGE,"E5685"),sQuery(id+"F14.wireOp",EDGE,"E5686"),sQuery(id+"F14.wireOp",EDGE,"E5687"),sQuery(id+"F14.wireOp",EDGE,"E5688"),sQuery(id+"F14.wireOp",EDGE,"E5689"),sQuery(id+"F14.wireOp",EDGE,"E5690"),sQuery(id+"F14.wireOp",EDGE,"E5691"),sQuery(id+"F14.wireOp",EDGE,"E5692"),sQuery(id+"F14.wireOp",EDGE,"E5693"),sQuery(id+"F14.wireOp",EDGE,"E5694"),sQuery(id+"F14.wireOp",EDGE,"E5695"),sQuery(id+"F14.wireOp",EDGE,"E5696"),sQuery(id+"F14.wireOp",EDGE,"E5697"),sQuery(id+"F14.wireOp",EDGE,"E5698"),sQuery(id+"F14.wireOp",EDGE,"E5699"),sQuery(id+"F14.wireOp",EDGE,"E5700"),sQuery(id+"F14.wireOp",EDGE,"E5701"),sQuery(id+"F14.wireOp",EDGE,"E5702"),sQuery(id+"F14.wireOp",EDGE,"E5703"),sQuery(id+"F14.wireOp",EDGE,"E5704"),sQuery(id+"F14.wireOp",EDGE,"E5705"),sQuery(id+"F14.wireOp",EDGE,"E5706"),sQuery(id+"F14.wireOp",EDGE,"E5707"),sQuery(id+"F14.wireOp",EDGE,"E5708"),sQuery(id+"F14.wireOp",EDGE,"E5709"),sQuery(id+"F14.wireOp",EDGE,"E5710"),sQuery(id+"F14.wireOp",EDGE,"E5711"),sQuery(id+"F14.wireOp",EDGE,"E5712"),sQuery(id+"F14.wireOp",EDGE,"E5713"),sQuery(id+"F14.wireOp",EDGE,"E5714"),sQuery(id+"F14.wireOp",EDGE,"E5715"),sQuery(id+"F14.wireOp",EDGE,"E5716"),sQuery(id+"F14.wireOp",EDGE,"E5717"),sQuery(id+"F14.wireOp",EDGE,"E5718"),sQuery(id+"F14.wireOp",EDGE,"E5719"),sQuery(id+"F14.wireOp",EDGE,"E5720"),sQuery(id+"F14.wireOp",EDGE,"E5721"),sQuery(id+"F14.wireOp",EDGE,"E5722"),sQuery(id+"F14.wireOp",EDGE,"E5723"),sQuery(id+"F14.wireOp",EDGE,"E5724"),sQuery(id+"F14.wireOp",EDGE,"E5725"),sQuery(id+"F14.wireOp",EDGE,"E5726"),sQuery(id+"F14.wireOp",EDGE,"E5727"),sQuery(id+"F14.wireOp",EDGE,"E5728"),sQuery(id+"F14.wireOp",EDGE,"E5729"),sQuery(id+"F14.wireOp",EDGE,"E5730"),sQuery(id+"F14.wireOp",EDGE,"E5731"),sQuery(id+"F14.wireOp",EDGE,"E5732"),sQuery(id+"F14.wireOp",EDGE,"E5733"),sQuery(id+"F14.wireOp",EDGE,"E5734"),sQuery(id+"F14.wireOp",EDGE,"E5735"),sQuery(id+"F14.wireOp",EDGE,"E5736"),sQuery(id+"F14.wireOp",EDGE,"E5737"),sQuery(id+"F14.wireOp",EDGE,"E5738"),sQuery(id+"F14.wireOp",EDGE,"E5739"),sQuery(id+"F14.wireOp",EDGE,"E5740"),sQuery(id+"F14.wireOp",EDGE,"E5741"),sQuery(id+"F14.wireOp",EDGE,"E5742"),sQuery(id+"F14.wireOp",EDGE,"E5743"),sQuery(id+"F14.wireOp",EDGE,"E5744"),sQuery(id+"F14.wireOp",EDGE,"E5745"),sQuery(id+"F14.wireOp",EDGE,"E5746"),sQuery(id+"F14.wireOp",EDGE,"E5747"),sQuery(id+"F14.wireOp",EDGE,"E5748"),sQuery(id+"F14.wireOp",EDGE,"E5749"),sQuery(id+"F14.wireOp",EDGE,"E5750"),sQuery(id+"F14.wireOp",EDGE,"E5751"),sQuery(id+"F14.wireOp",EDGE,"E5752"),sQuery(id+"F14.wireOp",EDGE,"E5753"),sQuery(id+"F14.wireOp",EDGE,"E5754"),sQuery(id+"F14.wireOp",EDGE,"E5755"),sQuery(id+"F14.wireOp",EDGE,"E5756"),sQuery(id+"F14.wireOp",EDGE,"E5757"),sQuery(id+"F14.wireOp",EDGE,"E5758"),sQuery(id+"F14.wireOp",EDGE,"E5759"),sQuery(id+"F14.wireOp",EDGE,"E5760"),sQuery(id+"F14.wireOp",EDGE,"E5761"),sQuery(id+"F14.wireOp",EDGE,"E5762"),sQuery(id+"F14.wireOp",EDGE,"E5763"),sQuery(id+"F14.wireOp",EDGE,"E5764"),sQuery(id+"F14.wireOp",EDGE,"E5765"),sQuery(id+"F14.wireOp",EDGE,"E5766"),sQuery(id+"F14.wireOp",EDGE,"E5767"),sQuery(id+"F14.wireOp",EDGE,"E5768"),sQuery(id+"F14.wireOp",EDGE,"E5769"),sQuery(id+"F14.wireOp",EDGE,"E5770"),sQuery(id+"F14.wireOp",EDGE,"E5771"),sQuery(id+"F14.wireOp",EDGE,"E5772"),sQuery(id+"F14.wireOp",EDGE,"E5773"),sQuery(id+"F14.wireOp",EDGE,"E5774"),sQuery(id+"F14.wireOp",EDGE,"E5775"),sQuery(id+"F14.wireOp",EDGE,"E5776"),sQuery(id+"F14.wireOp",EDGE,"E5777"),sQuery(id+"F14.wireOp",EDGE,"E5778"),sQuery(id+"F14.wireOp",EDGE,"E5779"),sQuery(id+"F14.wireOp",EDGE,"E5780"),sQuery(id+"F14.wireOp",EDGE,"E5781"),sQuery(id+"F14.wireOp",EDGE,"E5782"),sQuery(id+"F14.wireOp",EDGE,"E5783"),sQuery(id+"F14.wireOp",EDGE,"E5784"),sQuery(id+"F14.wireOp",EDGE,"E5785"),sQuery(id+"F14.wireOp",EDGE,"E5786"),sQuery(id+"F14.wireOp",EDGE,"E5787"),sQuery(id+"F14.wireOp",EDGE,"E5788"),sQuery(id+"F14.wireOp",EDGE,"E5789"),sQuery(id+"F14.wireOp",EDGE,"E5790"),sQuery(id+"F14.wireOp",EDGE,"E5791"),sQuery(id+"F14.wireOp",EDGE,"E5792"),sQuery(id+"F14.wireOp",EDGE,"E5793"),sQuery(id+"F14.wireOp",EDGE,"E5794"),sQuery(id+"F14.wireOp",EDGE,"E5795"),sQuery(id+"F14.wireOp",EDGE,"E5796"),sQuery(id+"F14.wireOp",EDGE,"E5797"),sQuery(id+"F14.wireOp",EDGE,"E5798"),sQuery(id+"F14.wireOp",EDGE,"E5799"),sQuery(id+"F14.wireOp",EDGE,"E5800"),sQuery(id+"F14.wireOp",EDGE,"E5801"),sQuery(id+"F14.wireOp",EDGE,"E5802"),sQuery(id+"F14.wireOp",EDGE,"E5803"),sQuery(id+"F14.wireOp",EDGE,"E5804"),sQuery(id+"F14.wireOp",EDGE,"E5805"),sQuery(id+"F14.wireOp",EDGE,"E5806"),sQuery(id+"F14.wireOp",EDGE,"E5807"),sQuery(id+"F14.wireOp",EDGE,"E5808"),sQuery(id+"F14.wireOp",EDGE,"E5809"),sQuery(id+"F14.wireOp",EDGE,"E5810"),sQuery(id+"F14.wireOp",EDGE,"E5811"),sQuery(id+"F14.wireOp",EDGE,"E5812"),sQuery(id+"F14.wireOp",EDGE,"E5813"),sQuery(id+"F14.wireOp",EDGE,"E5814"),sQuery(id+"F14.wireOp",EDGE,"E5815"),sQuery(id+"F14.wireOp",EDGE,"E5816"),sQuery(id+"F14.wireOp",EDGE,"E5817"),sQuery(id+"F14.wireOp",EDGE,"E5818"),sQuery(id+"F14.wireOp",EDGE,"E5819"),sQuery(id+"F14.wireOp",EDGE,"E5820"),sQuery(id+"F14.wireOp",EDGE,"E5821"),sQuery(id+"F14.wireOp",EDGE,"E5822"),sQuery(id+"F14.wireOp",EDGE,"E5823"),sQuery(id+"F14.wireOp",EDGE,"E5824"),sQuery(id+"F14.wireOp",EDGE,"E5825"),sQuery(id+"F14.wireOp",EDGE,"E5826"),sQuery(id+"F14.wireOp",EDGE,"E5827"),sQuery(id+"F14.wireOp",EDGE,"E5828"),sQuery(id+"F14.wireOp",EDGE,"E5829"),sQuery(id+"F14.wireOp",EDGE,"E5830"),sQuery(id+"F14.wireOp",EDGE,"E5831"),sQuery(id+"F14.wireOp",EDGE,"E5832"),sQuery(id+"F14.wireOp",EDGE,"E5833"),sQuery(id+"F14.wireOp",EDGE,"E5834"),sQuery(id+"F14.wireOp",EDGE,"E5835"),sQuery(id+"F14.wireOp",EDGE,"E5836"),sQuery(id+"F14.wireOp",EDGE,"E5837"),sQuery(id+"F14.wireOp",EDGE,"E5838"),sQuery(id+"F14.wireOp",EDGE,"E5839"),sQuery(id+"F14.wireOp",EDGE,"E5840"),sQuery(id+"F14.wireOp",EDGE,"E5841"),sQuery(id+"F14.wireOp",EDGE,"E5842"),sQuery(id+"F14.wireOp",EDGE,"E5843"),sQuery(id+"F14.wireOp",EDGE,"E5844"),sQuery(id+"F14.wireOp",EDGE,"E5845"),sQuery(id+"F14.wireOp",EDGE,"E5846"),sQuery(id+"F14.wireOp",EDGE,"E5847"),sQuery(id+"F14.wireOp",EDGE,"E5848"),sQuery(id+"F14.wireOp",EDGE,"E5849"),sQuery(id+"F14.wireOp",EDGE,"E5850"),sQuery(id+"F14.wireOp",EDGE,"E5851"),sQuery(id+"F14.wireOp",EDGE,"E5852"),sQuery(id+"F14.wireOp",EDGE,"E5853"),sQuery(id+"F14.wireOp",EDGE,"E5854"),sQuery(id+"F14.wireOp",EDGE,"E5855"),sQuery(id+"F14.wireOp",EDGE,"E5856"),sQuery(id+"F14.wireOp",EDGE,"E5857"),sQuery(id+"F14.wireOp",EDGE,"E5858"),sQuery(id+"F14.wireOp",EDGE,"E5859"),sQuery(id+"F14.wireOp",EDGE,"E5860"),sQuery(id+"F14.wireOp",EDGE,"E5861"),sQuery(id+"F14.wireOp",EDGE,"E5862"),sQuery(id+"F14.wireOp",EDGE,"E5863"),sQuery(id+"F14.wireOp",EDGE,"E5864"),sQuery(id+"F14.wireOp",EDGE,"E5865"),sQuery(id+"F14.wireOp",EDGE,"E5866"),sQuery(id+"F14.wireOp",EDGE,"E5867"),sQuery(id+"F14.wireOp",EDGE,"E5868"),sQuery(id+"F14.wireOp",EDGE,"E5869"),sQuery(id+"F14.wireOp",EDGE,"E5870"),sQuery(id+"F14.wireOp",EDGE,"E5871"),sQuery(id+"F14.wireOp",EDGE,"E5872"),sQuery(id+"F14.wireOp",EDGE,"E5873"),sQuery(id+"F14.wireOp",EDGE,"E5874"),sQuery(id+"F14.wireOp",EDGE,"E5875"),sQuery(id+"F14.wireOp",EDGE,"E5876"),sQuery(id+"F14.wireOp",EDGE,"E5877"),sQuery(id+"F14.wireOp",EDGE,"E5878"),sQuery(id+"F14.wireOp",EDGE,"E5879"),sQuery(id+"F14.wireOp",EDGE,"E5880"),sQuery(id+"F14.wireOp",EDGE,"E5881"),sQuery(id+"F14.wireOp",EDGE,"E5882"),sQuery(id+"F14.wireOp",EDGE,"E5883"),sQuery(id+"F14.wireOp",EDGE,"E5884"),sQuery(id+"F14.wireOp",EDGE,"E5885"),sQuery(id+"F14.wireOp",EDGE,"E5886"),sQuery(id+"F14.wireOp",EDGE,"E5887"),sQuery(id+"F14.wireOp",EDGE,"E5888"),sQuery(id+"F14.wireOp",EDGE,"E5889"),sQuery(id+"F14.wireOp",EDGE,"E5890"),sQuery(id+"F14.wireOp",EDGE,"E5891"),sQuery(id+"F14.wireOp",EDGE,"E5892"),sQuery(id+"F14.wireOp",EDGE,"E5893"),sQuery(id+"F14.wireOp",EDGE,"E5894"),sQuery(id+"F14.wireOp",EDGE,"E5895"),sQuery(id+"F14.wireOp",EDGE,"E5896"),sQuery(id+"F14.wireOp",EDGE,"E5897"),sQuery(id+"F14.wireOp",EDGE,"E5898"),sQuery(id+"F14.wireOp",EDGE,"E5899"),sQuery(id+"F14.wireOp",EDGE,"E5900"),sQuery(id+"F14.wireOp",EDGE,"E5901"),sQuery(id+"F14.wireOp",EDGE,"E5902"),sQuery(id+"F14.wireOp",EDGE,"E5903"),sQuery(id+"F14.wireOp",EDGE,"E5904"),sQuery(id+"F14.wireOp",EDGE,"E5905"),sQuery(id+"F14.wireOp",EDGE,"E5906"),sQuery(id+"F14.wireOp",EDGE,"E5907"),sQuery(id+"F14.wireOp",EDGE,"E5908"),sQuery(id+"F14.wireOp",EDGE,"E5909"),sQuery(id+"F14.wireOp",EDGE,"E5910"),sQuery(id+"F14.wireOp",EDGE,"E5911"),sQuery(id+"F14.wireOp",EDGE,"E5912"),sQuery(id+"F14.wireOp",EDGE,"E5913"),sQuery(id+"F14.wireOp",EDGE,"E5914"),sQuery(id+"F14.wireOp",EDGE,"E5915"),sQuery(id+"F14.wireOp",EDGE,"E5916"),sQuery(id+"F14.wireOp",EDGE,"E5917"),sQuery(id+"F14.wireOp",EDGE,"E5918"),sQuery(id+"F14.wireOp",EDGE,"E5919"),sQuery(id+"F14.wireOp",EDGE,"E5920"),sQuery(id+"F14.wireOp",EDGE,"E5921"),sQuery(id+"F14.wireOp",EDGE,"E5922"),sQuery(id+"F14.wireOp",EDGE,"E5923"),sQuery(id+"F14.wireOp",EDGE,"E5924"),sQuery(id+"F14.wireOp",EDGE,"E5925"),sQuery(id+"F14.wireOp",EDGE,"E5926"),sQuery(id+"F14.wireOp",EDGE,"E5927"),sQuery(id+"F14.wireOp",EDGE,"E5928"),sQuery(id+"F14.wireOp",EDGE,"E5929"),sQuery(id+"F14.wireOp",EDGE,"E5930"),sQuery(id+"F14.wireOp",EDGE,"E5931"),sQuery(id+"F14.wireOp",EDGE,"E5932"),sQuery(id+"F14.wireOp",EDGE,"E5933"),sQuery(id+"F14.wireOp",EDGE,"E5934"),sQuery(id+"F14.wireOp",EDGE,"E5935"),sQuery(id+"F14.wireOp",EDGE,"E5936"),sQuery(id+"F14.wireOp",EDGE,"E5937"),sQuery(id+"F14.wireOp",EDGE,"E5938"),sQuery(id+"F14.wireOp",EDGE,"E5939"),sQuery(id+"F14.wireOp",EDGE,"E5940"),sQuery(id+"F14.wireOp",EDGE,"E5941"),sQuery(id+"F14.wireOp",EDGE,"E5942"),sQuery(id+"F14.wireOp",EDGE,"E5943"),sQuery(id+"F14.wireOp",EDGE,"E5944"),sQuery(id+"F14.wireOp",EDGE,"E5945"),sQuery(id+"F14.wireOp",EDGE,"E5946"),sQuery(id+"F14.wireOp",EDGE,"E5947"),sQuery(id+"F14.wireOp",EDGE,"E5948"),sQuery(id+"F14.wireOp",EDGE,"E5949"),sQuery(id+"F14.wireOp",EDGE,"E5950"),sQuery(id+"F14.wireOp",EDGE,"E5951"),sQuery(id+"F14.wireOp",EDGE,"E5952"),sQuery(id+"F14.wireOp",EDGE,"E5953"),sQuery(id+"F14.wireOp",EDGE,"E5954"),sQuery(id+"F14.wireOp",EDGE,"E5955"),sQuery(id+"F14.wireOp",EDGE,"E5956"),sQuery(id+"F14.wireOp",EDGE,"E5957"),sQuery(id+"F14.wireOp",EDGE,"E5958"),sQuery(id+"F14.wireOp",EDGE,"E5959"),sQuery(id+"F14.wireOp",EDGE,"E5960"),sQuery(id+"F14.wireOp",EDGE,"E5961"),sQuery(id+"F14.wireOp",EDGE,"E5962"),sQuery(id+"F14.wireOp",EDGE,"E5963"),sQuery(id+"F14.wireOp",EDGE,"E5964"),sQuery(id+"F14.wireOp",EDGE,"E5965"),sQuery(id+"F14.wireOp",EDGE,"E5966"),sQuery(id+"F14.wireOp",EDGE,"E5967"),sQuery(id+"F14.wireOp",EDGE,"E5968"),sQuery(id+"F14.wireOp",EDGE,"E5969"),sQuery(id+"F14.wireOp",EDGE,"E5970"),sQuery(id+"F14.wireOp",EDGE,"E5971"),sQuery(id+"F14.wireOp",EDGE,"E5972"),sQuery(id+"F14.wireOp",EDGE,"E5973"),sQuery(id+"F14.wireOp",EDGE,"E5974"),sQuery(id+"F14.wireOp",EDGE,"E5975"),sQuery(id+"F14.wireOp",EDGE,"E5976"),sQuery(id+"F14.wireOp",EDGE,"E5977"),sQuery(id+"F14.wireOp",EDGE,"E5978"),sQuery(id+"F14.wireOp",EDGE,"E5979"),sQuery(id+"F14.wireOp",EDGE,"E5980"),sQuery(id+"F14.wireOp",EDGE,"E5981"),sQuery(id+"F14.wireOp",EDGE,"E5982"),sQuery(id+"F14.wireOp",EDGE,"E5983"),sQuery(id+"F14.wireOp",EDGE,"E5984"),sQuery(id+"F14.wireOp",EDGE,"E5985"),sQuery(id+"F14.wireOp",EDGE,"E5986"),sQuery(id+"F14.wireOp",EDGE,"E5987"),sQuery(id+"F14.wireOp",EDGE,"E5988"),sQuery(id+"F14.wireOp",EDGE,"E5989"),sQuery(id+"F14.wireOp",EDGE,"E5990"),sQuery(id+"F14.wireOp",EDGE,"E5991"),sQuery(id+"F14.wireOp",EDGE,"E5992"),sQuery(id+"F14.wireOp",EDGE,"E5993"),sQuery(id+"F14.wireOp",EDGE,"E5994"),sQuery(id+"F14.wireOp",EDGE,"E5995"),sQuery(id+"F14.wireOp",EDGE,"E5996"),sQuery(id+"F14.wireOp",EDGE,"E5997"),sQuery(id+"F14.wireOp",EDGE,"E5998"),sQuery(id+"F14.wireOp",EDGE,"E5999"),sQuery(id+"F14.wireOp",EDGE,"E6000"),sQuery(id+"F14.wireOp",EDGE,"E6001"),sQuery(id+"F14.wireOp",EDGE,"E6002"),sQuery(id+"F14.wireOp",EDGE,"E6003"),sQuery(id+"F14.wireOp",EDGE,"E6004"),sQuery(id+"F14.wireOp",EDGE,"E6005"),sQuery(id+"F14.wireOp",EDGE,"E6006"),sQuery(id+"F14.wireOp",EDGE,"E6007"),sQuery(id+"F14.wireOp",EDGE,"E6008"),sQuery(id+"F14.wireOp",EDGE,"E6009"),sQuery(id+"F14.wireOp",EDGE,"E6010"),sQuery(id+"F14.wireOp",EDGE,"E6011"),sQuery(id+"F14.wireOp",EDGE,"E6012"),sQuery(id+"F14.wireOp",EDGE,"E6013"),sQuery(id+"F14.wireOp",EDGE,"E6014"),sQuery(id+"F14.wireOp",EDGE,"E6015"),sQuery(id+"F14.wireOp",EDGE,"E6016"),sQuery(id+"F14.wireOp",EDGE,"E6017"),sQuery(id+"F14.wireOp",EDGE,"E6018"),sQuery(id+"F14.wireOp",EDGE,"E6019"),sQuery(id+"F14.wireOp",EDGE,"E6020"),sQuery(id+"F14.wireOp",EDGE,"E6021"),sQuery(id+"F14.wireOp",EDGE,"E6022"),sQuery(id+"F14.wireOp",EDGE,"E6023"),sQuery(id+"F14.wireOp",EDGE,"E6024"),sQuery(id+"F14.wireOp",EDGE,"E6025"),sQuery(id+"F14.wireOp",EDGE,"E6026"),sQuery(id+"F14.wireOp",EDGE,"E6027"),sQuery(id+"F14.wireOp",EDGE,"E6028"),sQuery(id+"F14.wireOp",EDGE,"E6029"),sQuery(id+"F14.wireOp",EDGE,"E6030"),sQuery(id+"F14.wireOp",EDGE,"E6031"),sQuery(id+"F14.wireOp",EDGE,"E6032"),sQuery(id+"F14.wireOp",EDGE,"E6033"),sQuery(id+"F14.wireOp",EDGE,"E6034"),sQuery(id+"F14.wireOp",EDGE,"E6035"),sQuery(id+"F14.wireOp",EDGE,"E6036"),sQuery(id+"F14.wireOp",EDGE,"E6037"),sQuery(id+"F14.wireOp",EDGE,"E6038"),sQuery(id+"F14.wireOp",EDGE,"E6039"),sQuery(id+"F14.wireOp",EDGE,"E6040"),sQuery(id+"F14.wireOp",EDGE,"E6041"),sQuery(id+"F14.wireOp",EDGE,"E6042"),sQuery(id+"F14.wireOp",EDGE,"E6043"),sQuery(id+"F14.wireOp",EDGE,"E6044"),sQuery(id+"F14.wireOp",EDGE,"E6045"),sQuery(id+"F14.wireOp",EDGE,"E6046"),sQuery(id+"F14.wireOp",EDGE,"E6047"),sQuery(id+"F14.wireOp",EDGE,"E6048"),sQuery(id+"F14.wireOp",EDGE,"E6049"),sQuery(id+"F14.wireOp",EDGE,"E6050"),sQuery(id+"F14.wireOp",EDGE,"E6051"),sQuery(id+"F14.wireOp",EDGE,"E6052"),sQuery(id+"F14.wireOp",EDGE,"E6053"),sQuery(id+"F14.wireOp",EDGE,"E6054"),sQuery(id+"F14.wireOp",EDGE,"E6055"),sQuery(id+"F14.wireOp",EDGE,"E6056"),sQuery(id+"F14.wireOp",EDGE,"E6057"),sQuery(id+"F14.wireOp",EDGE,"E6058"),sQuery(id+"F14.wireOp",EDGE,"E6059"),sQuery(id+"F14.wireOp",EDGE,"E6060"),sQuery(id+"F14.wireOp",EDGE,"E6061"),sQuery(id+"F14.wireOp",EDGE,"E6062"),sQuery(id+"F14.wireOp",EDGE,"E6063"),sQuery(id+"F14.wireOp",EDGE,"E6064"),sQuery(id+"F14.wireOp",EDGE,"E6065"),sQuery(id+"F14.wireOp",EDGE,"E6066"),sQuery(id+"F14.wireOp",EDGE,"E6067"),sQuery(id+"F14.wireOp",EDGE,"E6068"),sQuery(id+"F14.wireOp",EDGE,"E6069"),sQuery(id+"F14.wireOp",EDGE,"E6070"),sQuery(id+"F14.wireOp",EDGE,"E6071"),sQuery(id+"F14.wireOp",EDGE,"E6072"),sQuery(id+"F14.wireOp",EDGE,"E6073"),sQuery(id+"F14.wireOp",EDGE,"E6074"),sQuery(id+"F14.wireOp",EDGE,"E6075"),sQuery(id+"F14.wireOp",EDGE,"E6076"),sQuery(id+"F14.wireOp",EDGE,"E6077"),sQuery(id+"F14.wireOp",EDGE,"E6078"),sQuery(id+"F14.wireOp",EDGE,"E6079"),sQuery(id+"F14.wireOp",EDGE,"E6080"),sQuery(id+"F14.wireOp",EDGE,"E6081"),sQuery(id+"F14.wireOp",EDGE,"E6082"),sQuery(id+"F14.wireOp",EDGE,"E6083"),sQuery(id+"F14.wireOp",EDGE,"E6084"),sQuery(id+"F14.wireOp",EDGE,"E6085"),sQuery(id+"F14.wireOp",EDGE,"E6086"),sQuery(id+"F14.wireOp",EDGE,"E6087"),sQuery(id+"F14.wireOp",EDGE,"E6088"),sQuery(id+"F14.wireOp",EDGE,"E6089"),sQuery(id+"F14.wireOp",EDGE,"E6090"),sQuery(id+"F14.wireOp",EDGE,"E6091"),sQuery(id+"F14.wireOp",EDGE,"E6092"),sQuery(id+"F14.wireOp",EDGE,"E6093"),sQuery(id+"F14.wireOp",EDGE,"E6094"),sQuery(id+"F14.wireOp",EDGE,"E6095"),sQuery(id+"F14.wireOp",EDGE,"E6096"),sQuery(id+"F14.wireOp",EDGE,"E6097"),sQuery(id+"F14.wireOp",EDGE,"E6098"),sQuery(id+"F14.wireOp",EDGE,"E6099"),sQuery(id+"F14.wireOp",EDGE,"E6100"),sQuery(id+"F14.wireOp",EDGE,"E6101"),sQuery(id+"F14.wireOp",EDGE,"E6102"),sQuery(id+"F14.wireOp",EDGE,"E6103"),sQuery(id+"F14.wireOp",EDGE,"E6104"),sQuery(id+"F14.wireOp",EDGE,"E6105"),sQuery(id+"F14.wireOp",EDGE,"E6106"),sQuery(id+"F14.wireOp",EDGE,"E6107"),sQuery(id+"F14.wireOp",EDGE,"E6108"),sQuery(id+"F14.wireOp",EDGE,"E6109"),sQuery(id+"F14.wireOp",EDGE,"E6110"),sQuery(id+"F14.wireOp",EDGE,"E6111"),sQuery(id+"F14.wireOp",EDGE,"E6112"),sQuery(id+"F14.wireOp",EDGE,"E6113"),sQuery(id+"F14.wireOp",EDGE,"E6114"),sQuery(id+"F14.wireOp",EDGE,"E6115"),sQuery(id+"F14.wireOp",EDGE,"E6116"),sQuery(id+"F14.wireOp",EDGE,"E6117"),sQuery(id+"F14.wireOp",EDGE,"E6118"),sQuery(id+"F14.wireOp",EDGE,"E6119"),sQuery(id+"F14.wireOp",EDGE,"E6120"),sQuery(id+"F14.wireOp",EDGE,"E6121"),sQuery(id+"F14.wireOp",EDGE,"E6122"),sQuery(id+"F14.wireOp",EDGE,"E6123"),sQuery(id+"F14.wireOp",EDGE,"E6124"),sQuery(id+"F14.wireOp",EDGE,"E6125"),sQuery(id+"F14.wireOp",EDGE,"E6126"),sQuery(id+"F14.wireOp",EDGE,"E6127"),sQuery(id+"F14.wireOp",EDGE,"E6128"),sQuery(id+"F14.wireOp",EDGE,"E6129"),sQuery(id+"F14.wireOp",EDGE,"E6130"),sQuery(id+"F14.wireOp",EDGE,"E6131"),sQuery(id+"F14.wireOp",EDGE,"E6132"),sQuery(id+"F14.wireOp",EDGE,"E6133"),sQuery(id+"F14.wireOp",EDGE,"E6134"),sQuery(id+"F14.wireOp",EDGE,"E6135"),sQuery(id+"F14.wireOp",EDGE,"E6136"),sQuery(id+"F14.wireOp",EDGE,"E6137"),sQuery(id+"F14.wireOp",EDGE,"E6138"),sQuery(id+"F14.wireOp",EDGE,"E6139"),sQuery(id+"F14.wireOp",EDGE,"E6140"),sQuery(id+"F14.wireOp",EDGE,"E6141"),sQuery(id+"F14.wireOp",EDGE,"E6142"),sQuery(id+"F14.wireOp",EDGE,"E6143"),sQuery(id+"F14.wireOp",EDGE,"E6144"),sQuery(id+"F14.wireOp",EDGE,"E6145"),sQuery(id+"F14.wireOp",EDGE,"E6146"),sQuery(id+"F14.wireOp",EDGE,"E6147"),sQuery(id+"F14.wireOp",EDGE,"E6148"),sQuery(id+"F14.wireOp",EDGE,"E6149"),sQuery(id+"F14.wireOp",EDGE,"E6150"),sQuery(id+"F14.wireOp",EDGE,"E6151"),sQuery(id+"F14.wireOp",EDGE,"E6152"),sQuery(id+"F14.wireOp",EDGE,"E6153"),sQuery(id+"F14.wireOp",EDGE,"E6154"),sQuery(id+"F14.wireOp",EDGE,"E6155"),sQuery(id+"F14.wireOp",EDGE,"E6156"),sQuery(id+"F14.wireOp",EDGE,"E6157"),sQuery(id+"F14.wireOp",EDGE,"E6158"),sQuery(id+"F14.wireOp",EDGE,"E6159"),sQuery(id+"F14.wireOp",EDGE,"E6160"),sQuery(id+"F14.wireOp",EDGE,"E6161"),sQuery(id+"F14.wireOp",EDGE,"E6162"),sQuery(id+"F14.wireOp",EDGE,"E6163"),sQuery(id+"F14.wireOp",EDGE,"E6164"),sQuery(id+"F14.wireOp",EDGE,"E6165"),sQuery(id+"F14.wireOp",EDGE,"E6166"),sQuery(id+"F14.wireOp",EDGE,"E6167"),sQuery(id+"F14.wireOp",EDGE,"E6168"),sQuery(id+"F14.wireOp",EDGE,"E6169"),sQuery(id+"F14.wireOp",EDGE,"E6170"),sQuery(id+"F14.wireOp",EDGE,"E6171"),sQuery(id+"F14.wireOp",EDGE,"E6172"),sQuery(id+"F14.wireOp",EDGE,"E6173"),sQuery(id+"F14.wireOp",EDGE,"E6174"),sQuery(id+"F14.wireOp",EDGE,"E6175"),sQuery(id+"F14.wireOp",EDGE,"E6176"),sQuery(id+"F14.wireOp",EDGE,"E6177"),sQuery(id+"F14.wireOp",EDGE,"E6178"),sQuery(id+"F14.wireOp",EDGE,"E6179"),sQuery(id+"F14.wireOp",EDGE,"E6180"),sQuery(id+"F14.wireOp",EDGE,"E6181"),sQuery(id+"F14.wireOp",EDGE,"E6182"),sQuery(id+"F14.wireOp",EDGE,"E6183"),sQuery(id+"F14.wireOp",EDGE,"E6184"),sQuery(id+"F14.wireOp",EDGE,"E6185"),sQuery(id+"F14.wireOp",EDGE,"E6186"),sQuery(id+"F14.wireOp",EDGE,"E6187"),sQuery(id+"F14.wireOp",EDGE,"E6188"),sQuery(id+"F14.wireOp",EDGE,"E6189"),sQuery(id+"F14.wireOp",EDGE,"E6190"),sQuery(id+"F14.wireOp",EDGE,"E6191"),sQuery(id+"F14.wireOp",EDGE,"E6192"),sQuery(id+"F14.wireOp",EDGE,"E6193"),sQuery(id+"F14.wireOp",EDGE,"E6194"),sQuery(id+"F14.wireOp",EDGE,"E6195"),sQuery(id+"F14.wireOp",EDGE,"E6196"),sQuery(id+"F14.wireOp",EDGE,"E6197"),sQuery(id+"F14.wireOp",EDGE,"E6198"),sQuery(id+"F14.wireOp",EDGE,"E6199"),sQuery(id+"F14.wireOp",EDGE,"E6200"),sQuery(id+"F14.wireOp",EDGE,"E6201"),sQuery(id+"F14.wireOp",EDGE,"E6202"),sQuery(id+"F14.wireOp",EDGE,"E6203"),sQuery(id+"F14.wireOp",EDGE,"E6204"),sQuery(id+"F14.wireOp",EDGE,"E6205"),sQuery(id+"F14.wireOp",EDGE,"E6206"),sQuery(id+"F14.wireOp",EDGE,"E6207"),sQuery(id+"F14.wireOp",EDGE,"E6208"),sQuery(id+"F14.wireOp",EDGE,"E6209"),sQuery(id+"F14.wireOp",EDGE,"E6210"),sQuery(id+"F14.wireOp",EDGE,"E6211"),sQuery(id+"F14.wireOp",EDGE,"E6212"),sQuery(id+"F14.wireOp",EDGE,"E6213"),sQuery(id+"F14.wireOp",EDGE,"E6214"),sQuery(id+"F14.wireOp",EDGE,"E6215"),sQuery(id+"F14.wireOp",EDGE,"E6216"),sQuery(id+"F14.wireOp",EDGE,"E6217"),sQuery(id+"F14.wireOp",EDGE,"E6218"),sQuery(id+"F14.wireOp",EDGE,"E6219"),sQuery(id+"F14.wireOp",EDGE,"E6220"),sQuery(id+"F14.wireOp",EDGE,"E6221"),sQuery(id+"F14.wireOp",EDGE,"E6222"),sQuery(id+"F14.wireOp",EDGE,"E6223"),sQuery(id+"F14.wireOp",EDGE,"E6224"),sQuery(id+"F14.wireOp",EDGE,"E6225"),sQuery(id+"F14.wireOp",EDGE,"E6226"),sQuery(id+"F14.wireOp",EDGE,"E6227"),sQuery(id+"F14.wireOp",EDGE,"E6228"),sQuery(id+"F14.wireOp",EDGE,"E6229"),sQuery(id+"F14.wireOp",EDGE,"E6230"),sQuery(id+"F14.wireOp",EDGE,"E6231"),sQuery(id+"F14.wireOp",EDGE,"E6232"),sQuery(id+"F14.wireOp",EDGE,"E6233"),sQuery(id+"F14.wireOp",EDGE,"E6234"),sQuery(id+"F14.wireOp",EDGE,"E6235"),sQuery(id+"F14.wireOp",EDGE,"E6236"),sQuery(id+"F14.wireOp",EDGE,"E6237"),sQuery(id+"F14.wireOp",EDGE,"E6238"),sQuery(id+"F14.wireOp",EDGE,"E6239"),sQuery(id+"F14.wireOp",EDGE,"E6240"),sQuery(id+"F14.wireOp",EDGE,"E6241"),sQuery(id+"F14.wireOp",EDGE,"E6242"),sQuery(id+"F14.wireOp",EDGE,"E6243"),sQuery(id+"F14.wireOp",EDGE,"E6244"),sQuery(id+"F14.wireOp",EDGE,"E6245"),sQuery(id+"F14.wireOp",EDGE,"E6246"),sQuery(id+"F14.wireOp",EDGE,"E6247"),sQuery(id+"F14.wireOp",EDGE,"E6248"),sQuery(id+"F14.wireOp",EDGE,"E6249"),sQuery(id+"F14.wireOp",EDGE,"E6250"),sQuery(id+"F14.wireOp",EDGE,"E6251"),sQuery(id+"F14.wireOp",EDGE,"E6252"),sQuery(id+"F14.wireOp",EDGE,"E6253"),sQuery(id+"F14.wireOp",EDGE,"E6254"),sQuery(id+"F14.wireOp",EDGE,"E6255"),sQuery(id+"F14.wireOp",EDGE,"E6256"),sQuery(id+"F14.wireOp",EDGE,"E6257"),sQuery(id+"F14.wireOp",EDGE,"E6258"),sQuery(id+"F14.wireOp",EDGE,"E6259"),sQuery(id+"F14.wireOp",EDGE,"E6260"),sQuery(id+"F14.wireOp",EDGE,"E6261"),sQuery(id+"F14.wireOp",EDGE,"E6262"),sQuery(id+"F14.wireOp",EDGE,"E6263"),sQuery(id+"F14.wireOp",EDGE,"E6264"),sQuery(id+"F14.wireOp",EDGE,"E6265"),sQuery(id+"F14.wireOp",EDGE,"E6266"),sQuery(id+"F14.wireOp",EDGE,"E6267"),sQuery(id+"F14.wireOp",EDGE,"E6268"),sQuery(id+"F14.wireOp",EDGE,"E6269"),sQuery(id+"F14.wireOp",EDGE,"E6270"),sQuery(id+"F14.wireOp",EDGE,"E6271"),sQuery(id+"F14.wireOp",EDGE,"E6272"),sQuery(id+"F14.wireOp",EDGE,"E6273"),sQuery(id+"F14.wireOp",EDGE,"E6274"),sQuery(id+"F14.wireOp",EDGE,"E6275"),sQuery(id+"F14.wireOp",EDGE,"E6276"),sQuery(id+"F14.wireOp",EDGE,"E6277"),sQuery(id+"F14.wireOp",EDGE,"E6278"),sQuery(id+"F14.wireOp",EDGE,"E6279"),sQuery(id+"F14.wireOp",EDGE,"E6280"),sQuery(id+"F14.wireOp",EDGE,"E6281"),sQuery(id+"F14.wireOp",EDGE,"E6282"),sQuery(id+"F14.wireOp",EDGE,"E6283"),sQuery(id+"F14.wireOp",EDGE,"E6284"),sQuery(id+"F14.wireOp",EDGE,"E6285"),sQuery(id+"F14.wireOp",EDGE,"E6286"),sQuery(id+"F14.wireOp",EDGE,"E6287"),sQuery(id+"F14.wireOp",EDGE,"E6288"),sQuery(id+"F14.wireOp",EDGE,"E6289"),sQuery(id+"F14.wireOp",EDGE,"E6290"),sQuery(id+"F14.wireOp",EDGE,"E6291"),sQuery(id+"F14.wireOp",EDGE,"E6292"),sQuery(id+"F14.wireOp",EDGE,"E6293"),sQuery(id+"F14.wireOp",EDGE,"E6294"),sQuery(id+"F14.wireOp",EDGE,"E6295"),sQuery(id+"F14.wireOp",EDGE,"E6296"),sQuery(id+"F14.wireOp",EDGE,"E6297"),sQuery(id+"F14.wireOp",EDGE,"E6298"),sQuery(id+"F14.wireOp",EDGE,"E6299"),sQuery(id+"F14.wireOp",EDGE,"E6300"),sQuery(id+"F14.wireOp",EDGE,"E6301"),sQuery(id+"F14.wireOp",EDGE,"E6302"),sQuery(id+"F14.wireOp",EDGE,"E6303"),sQuery(id+"F14.wireOp",EDGE,"E6304"),sQuery(id+"F14.wireOp",EDGE,"E6305"),sQuery(id+"F14.wireOp",EDGE,"E6306"),sQuery(id+"F14.wireOp",EDGE,"E6307"),sQuery(id+"F14.wireOp",EDGE,"E6308"),sQuery(id+"F14.wireOp",EDGE,"E6309"),sQuery(id+"F14.wireOp",EDGE,"E6310"),sQuery(id+"F14.wireOp",EDGE,"E6311"),sQuery(id+"F14.wireOp",EDGE,"E6312"),sQuery(id+"F14.wireOp",EDGE,"E6313"),sQuery(id+"F14.wireOp",EDGE,"E6314"),sQuery(id+"F14.wireOp",EDGE,"E6315"),sQuery(id+"F14.wireOp",EDGE,"E6316"),sQuery(id+"F14.wireOp",EDGE,"E6317"),sQuery(id+"F14.wireOp",EDGE,"E6318"),sQuery(id+"F14.wireOp",EDGE,"E6319"),sQuery(id+"F14.wireOp",EDGE,"E6320"),sQuery(id+"F14.wireOp",EDGE,"E6321"),sQuery(id+"F14.wireOp",EDGE,"E6322"),sQuery(id+"F14.wireOp",EDGE,"E6323"),sQuery(id+"F14.wireOp",EDGE,"E6324"),sQuery(id+"F14.wireOp",EDGE,"E6325"),sQuery(id+"F14.wireOp",EDGE,"E6326"),sQuery(id+"F14.wireOp",EDGE,"E6327"),sQuery(id+"F14.wireOp",EDGE,"E6328"),sQuery(id+"F14.wireOp",EDGE,"E6329"),sQuery(id+"F14.wireOp",EDGE,"E6330"),sQuery(id+"F14.wireOp",EDGE,"E6331"),sQuery(id+"F14.wireOp",EDGE,"E6332"),sQuery(id+"F14.wireOp",EDGE,"E6333"),sQuery(id+"F14.wireOp",EDGE,"E6334"),sQuery(id+"F14.wireOp",EDGE,"E6335"),sQuery(id+"F14.wireOp",EDGE,"E6336"),sQuery(id+"F14.wireOp",EDGE,"E6337"),sQuery(id+"F14.wireOp",EDGE,"E6338"),sQuery(id+"F14.wireOp",EDGE,"E6339"),sQuery(id+"F14.wireOp",EDGE,"E6340"),sQuery(id+"F14.wireOp",EDGE,"E6341"),sQuery(id+"F14.wireOp",EDGE,"E6342"),sQuery(id+"F14.wireOp",EDGE,"E6343"),sQuery(id+"F14.wireOp",EDGE,"E6344"),sQuery(id+"F14.wireOp",EDGE,"E6345"),sQuery(id+"F14.wireOp",EDGE,"E6346"),sQuery(id+"F14.wireOp",EDGE,"E6347"),sQuery(id+"F14.wireOp",EDGE,"E6348"),sQuery(id+"F14.wireOp",EDGE,"E6349"),sQuery(id+"F14.wireOp",EDGE,"E6350"),sQuery(id+"F14.wireOp",EDGE,"E6351"),sQuery(id+"F14.wireOp",EDGE,"E6352"),sQuery(id+"F14.wireOp",EDGE,"E6353"),sQuery(id+"F14.wireOp",EDGE,"E6354"),sQuery(id+"F14.wireOp",EDGE,"E6355"),sQuery(id+"F14.wireOp",EDGE,"E6356"),sQuery(id+"F14.wireOp",EDGE,"E6357"),sQuery(id+"F14.wireOp",EDGE,"E6358"),sQuery(id+"F14.wireOp",EDGE,"E6359"),sQuery(id+"F14.wireOp",EDGE,"E6360"),sQuery(id+"F14.wireOp",EDGE,"E6361"),sQuery(id+"F14.wireOp",EDGE,"E6362"),sQuery(id+"F14.wireOp",EDGE,"E6363"),sQuery(id+"F14.wireOp",EDGE,"E6364"),sQuery(id+"F14.wireOp",EDGE,"E6365"),sQuery(id+"F14.wireOp",EDGE,"E6366"),sQuery(id+"F14.wireOp",EDGE,"E6367"),sQuery(id+"F14.wireOp",EDGE,"E6368"),sQuery(id+"F14.wireOp",EDGE,"E6369"),sQuery(id+"F14.wireOp",EDGE,"E6370"),sQuery(id+"F14.wireOp",EDGE,"E6371"),sQuery(id+"F14.wireOp",EDGE,"E6372"),sQuery(id+"F14.wireOp",EDGE,"E6373"),sQuery(id+"F14.wireOp",EDGE,"E6374"),sQuery(id+"F14.wireOp",EDGE,"E6375"),sQuery(id+"F14.wireOp",EDGE,"E6376"),sQuery(id+"F14.wireOp",EDGE,"E6377"),sQuery(id+"F14.wireOp",EDGE,"E6378"),sQuery(id+"F14.wireOp",EDGE,"E6379"),sQuery(id+"F14.wireOp",EDGE,"E6380"),sQuery(id+"F14.wireOp",EDGE,"E6381"),sQuery(id+"F14.wireOp",EDGE,"E6382"),sQuery(id+"F14.wireOp",EDGE,"E6383"),sQuery(id+"F14.wireOp",EDGE,"E6384"),sQuery(id+"F14.wireOp",EDGE,"E6385"),sQuery(id+"F14.wireOp",EDGE,"E6386"),sQuery(id+"F14.wireOp",EDGE,"E6387"),sQuery(id+"F14.wireOp",EDGE,"E6388"),sQuery(id+"F14.wireOp",EDGE,"E6389"),sQuery(id+"F14.wireOp",EDGE,"E6390"),sQuery(id+"F14.wireOp",EDGE,"E6391"),sQuery(id+"F14.wireOp",EDGE,"E6392"),sQuery(id+"F14.wireOp",EDGE,"E6393"),sQuery(id+"F14.wireOp",EDGE,"E6394"),sQuery(id+"F14.wireOp",EDGE,"E6395"),sQuery(id+"F14.wireOp",EDGE,"E6396"),sQuery(id+"F14.wireOp",EDGE,"E6397"),sQuery(id+"F14.wireOp",EDGE,"E6398"),sQuery(id+"F14.wireOp",EDGE,"E6399"),sQuery(id+"F14.wireOp",EDGE,"E6400"),sQuery(id+"F14.wireOp",EDGE,"E6401"),sQuery(id+"F14.wireOp",EDGE,"E6402"),sQuery(id+"F14.wireOp",EDGE,"E6403"),sQuery(id+"F14.wireOp",EDGE,"E6404"),sQuery(id+"F14.wireOp",EDGE,"E6405"),sQuery(id+"F14.wireOp",EDGE,"E6406"),sQuery(id+"F14.wireOp",EDGE,"E6407"),sQuery(id+"F14.wireOp",EDGE,"E6408"),sQuery(id+"F14.wireOp",EDGE,"E6409"),sQuery(id+"F14.wireOp",EDGE,"E6410"),sQuery(id+"F14.wireOp",EDGE,"E6411"),sQuery(id+"F14.wireOp",EDGE,"E6412"),sQuery(id+"F14.wireOp",EDGE,"E6413"),sQuery(id+"F14.wireOp",EDGE,"E6414"),sQuery(id+"F14.wireOp",EDGE,"E6415"),sQuery(id+"F14.wireOp",EDGE,"E6416"),sQuery(id+"F14.wireOp",EDGE,"E6417"),sQuery(id+"F14.wireOp",EDGE,"E6418"),sQuery(id+"F14.wireOp",EDGE,"E6419"),sQuery(id+"F14.wireOp",EDGE,"E6420"),sQuery(id+"F14.wireOp",EDGE,"E6421"),sQuery(id+"F14.wireOp",EDGE,"E6422"),sQuery(id+"F14.wireOp",EDGE,"E6423"),sQuery(id+"F14.wireOp",EDGE,"E6424"),sQuery(id+"F14.wireOp",EDGE,"E6425"),sQuery(id+"F14.wireOp",EDGE,"E6426"),sQuery(id+"F14.wireOp",EDGE,"E6427"),sQuery(id+"F14.wireOp",EDGE,"E6428"),sQuery(id+"F14.wireOp",EDGE,"E6429"),sQuery(id+"F14.wireOp",EDGE,"E6430"),sQuery(id+"F14.wireOp",EDGE,"E6431"),sQuery(id+"F14.wireOp",EDGE,"E6432"),sQuery(id+"F14.wireOp",EDGE,"E6433"),sQuery(id+"F14.wireOp",EDGE,"E6434"),sQuery(id+"F14.wireOp",EDGE,"E6435"),sQuery(id+"F14.wireOp",EDGE,"E6436"),sQuery(id+"F14.wireOp",EDGE,"E6437"),sQuery(id+"F14.wireOp",EDGE,"E6438"),sQuery(id+"F14.wireOp",EDGE,"E6439"),sQuery(id+"F14.wireOp",EDGE,"E6440"),sQuery(id+"F14.wireOp",EDGE,"E6441"),sQuery(id+"F14.wireOp",EDGE,"E6442"),sQuery(id+"F14.wireOp",EDGE,"E6443"),sQuery(id+"F14.wireOp",EDGE,"E6444"),sQuery(id+"F14.wireOp",EDGE,"E6445"),sQuery(id+"F14.wireOp",EDGE,"E6446"),sQuery(id+"F14.wireOp",EDGE,"E6447"),sQuery(id+"F14.wireOp",EDGE,"E6448"),sQuery(id+"F14.wireOp",EDGE,"E6449"),sQuery(id+"F14.wireOp",EDGE,"E6450"),sQuery(id+"F14.wireOp",EDGE,"E6451"),sQuery(id+"F14.wireOp",EDGE,"E6452"),sQuery(id+"F14.wireOp",EDGE,"E6453"),sQuery(id+"F14.wireOp",EDGE,"E6454"),sQuery(id+"F14.wireOp",EDGE,"E6455"),sQuery(id+"F14.wireOp",EDGE,"E6456"),sQuery(id+"F14.wireOp",EDGE,"E6457"),sQuery(id+"F14.wireOp",EDGE,"E6458"),sQuery(id+"F14.wireOp",EDGE,"E6459"),sQuery(id+"F14.wireOp",EDGE,"E6460"),sQuery(id+"F14.wireOp",EDGE,"E6461"),sQuery(id+"F14.wireOp",EDGE,"E6462"),sQuery(id+"F14.wireOp",EDGE,"E6463"),sQuery(id+"F14.wireOp",EDGE,"E6464"),sQuery(id+"F14.wireOp",EDGE,"E6465"),sQuery(id+"F14.wireOp",EDGE,"E6466"),sQuery(id+"F14.wireOp",EDGE,"E6467"),sQuery(id+"F14.wireOp",EDGE,"E6468"),sQuery(id+"F14.wireOp",EDGE,"E6469"),sQuery(id+"F14.wireOp",EDGE,"E6470"),sQuery(id+"F14.wireOp",EDGE,"E6471"),sQuery(id+"F14.wireOp",EDGE,"E6472"),sQuery(id+"F14.wireOp",EDGE,"E6473"),sQuery(id+"F14.wireOp",EDGE,"E6474"),sQuery(id+"F14.wireOp",EDGE,"E6475"),sQuery(id+"F14.wireOp",EDGE,"E6476"),sQuery(id+"F14.wireOp",EDGE,"E6477"),sQuery(id+"F14.wireOp",EDGE,"E6478"),sQuery(id+"F14.wireOp",EDGE,"E6479"),sQuery(id+"F14.wireOp",EDGE,"E6480"),sQuery(id+"F14.wireOp",EDGE,"E6481"),sQuery(id+"F14.wireOp",EDGE,"E6482"),sQuery(id+"F14.wireOp",EDGE,"E6483"),sQuery(id+"F14.wireOp",EDGE,"E6484"),sQuery(id+"F14.wireOp",EDGE,"E6485"),sQuery(id+"F14.wireOp",EDGE,"E6486"),sQuery(id+"F14.wireOp",EDGE,"E6487"),sQuery(id+"F14.wireOp",EDGE,"E6488"),sQuery(id+"F14.wireOp",EDGE,"E6489"),sQuery(id+"F14.wireOp",EDGE,"E6490"),sQuery(id+"F14.wireOp",EDGE,"E6491"),sQuery(id+"F14.wireOp",EDGE,"E6492"),sQuery(id+"F14.wireOp",EDGE,"E6493"),sQuery(id+"F14.wireOp",EDGE,"E6494"),sQuery(id+"F14.wireOp",EDGE,"E6495"),sQuery(id+"F14.wireOp",EDGE,"E6496"),sQuery(id+"F14.wireOp",EDGE,"E6497"),sQuery(id+"F14.wireOp",EDGE,"E6498"),sQuery(id+"F14.wireOp",EDGE,"E6499"),sQuery(id+"F14.wireOp",EDGE,"E6500"),sQuery(id+"F14.wireOp",EDGE,"E6501"),sQuery(id+"F14.wireOp",EDGE,"E6502"),sQuery(id+"F14.wireOp",EDGE,"E6503"),sQuery(id+"F14.wireOp",EDGE,"E6504"),sQuery(id+"F14.wireOp",EDGE,"E6505"),sQuery(id+"F14.wireOp",EDGE,"E6506"),sQuery(id+"F14.wireOp",EDGE,"E6507"),sQuery(id+"F14.wireOp",EDGE,"E6508"),sQuery(id+"F14.wireOp",EDGE,"E6509"),sQuery(id+"F14.wireOp",EDGE,"E6510"),sQuery(id+"F14.wireOp",EDGE,"E6511"),sQuery(id+"F14.wireOp",EDGE,"E6512"),sQuery(id+"F14.wireOp",EDGE,"E6513"),sQuery(id+"F14.wireOp",EDGE,"E6514"),sQuery(id+"F14.wireOp",EDGE,"E6515"),sQuery(id+"F14.wireOp",EDGE,"E6516"),sQuery(id+"F14.wireOp",EDGE,"E6517"),sQuery(id+"F14.wireOp",EDGE,"E6518"),sQuery(id+"F14.wireOp",EDGE,"E6519"),sQuery(id+"F14.wireOp",EDGE,"E6520"),sQuery(id+"F14.wireOp",EDGE,"E6521"),sQuery(id+"F14.wireOp",EDGE,"E6522"),sQuery(id+"F14.wireOp",EDGE,"E6523"),sQuery(id+"F14.wireOp",EDGE,"E6524"),sQuery(id+"F14.wireOp",EDGE,"E6525"),sQuery(id+"F14.wireOp",EDGE,"E6526"),sQuery(id+"F14.wireOp",EDGE,"E6527"),sQuery(id+"F14.wireOp",EDGE,"E6528"),sQuery(id+"F14.wireOp",EDGE,"E6529"),sQuery(id+"F14.wireOp",EDGE,"E6530"),sQuery(id+"F14.wireOp",EDGE,"E6531"),sQuery(id+"F14.wireOp",EDGE,"E6532"),sQuery(id+"F14.wireOp",EDGE,"E6533"),sQuery(id+"F14.wireOp",EDGE,"E6534"),sQuery(id+"F14.wireOp",EDGE,"E6535"),sQuery(id+"F14.wireOp",EDGE,"E6536"),sQuery(id+"F14.wireOp",EDGE,"E6537"),sQuery(id+"F14.wireOp",EDGE,"E6538"),sQuery(id+"F14.wireOp",EDGE,"E6539"),sQuery(id+"F14.wireOp",EDGE,"E6540"),sQuery(id+"F14.wireOp",EDGE,"E6541"),sQuery(id+"F14.wireOp",EDGE,"E6542"),sQuery(id+"F14.wireOp",EDGE,"E6543"),sQuery(id+"F14.wireOp",EDGE,"E6544"),sQuery(id+"F14.wireOp",EDGE,"E6545"),sQuery(id+"F14.wireOp",EDGE,"E6546"),sQuery(id+"F14.wireOp",EDGE,"E6547"),sQuery(id+"F14.wireOp",EDGE,"E6548"),sQuery(id+"F14.wireOp",EDGE,"E6549"),sQuery(id+"F14.wireOp",EDGE,"E6550"),sQuery(id+"F14.wireOp",EDGE,"E6551"),sQuery(id+"F14.wireOp",EDGE,"E6552"),sQuery(id+"F14.wireOp",EDGE,"E6553"),sQuery(id+"F14.wireOp",EDGE,"E6554"),sQuery(id+"F14.wireOp",EDGE,"E6555"),sQuery(id+"F14.wireOp",EDGE,"E6556"),sQuery(id+"F14.wireOp",EDGE,"E6557"),sQuery(id+"F14.wireOp",EDGE,"E6558"),sQuery(id+"F14.wireOp",EDGE,"E6559"),sQuery(id+"F14.wireOp",EDGE,"E6560"),sQuery(id+"F14.wireOp",EDGE,"E6561"),sQuery(id+"F14.wireOp",EDGE,"E6562"),sQuery(id+"F14.wireOp",EDGE,"E6563"),sQuery(id+"F14.wireOp",EDGE,"E6564"),sQuery(id+"F14.wireOp",EDGE,"E6565"),sQuery(id+"F14.wireOp",EDGE,"E6566"),sQuery(id+"F14.wireOp",EDGE,"E6567"),sQuery(id+"F14.wireOp",EDGE,"E6568"),sQuery(id+"F14.wireOp",EDGE,"E6569"),sQuery(id+"F14.wireOp",EDGE,"E6570"),sQuery(id+"F14.wireOp",EDGE,"E6571"),sQuery(id+"F14.wireOp",EDGE,"E6572"),sQuery(id+"F14.wireOp",EDGE,"E6573"),sQuery(id+"F14.wireOp",EDGE,"E6574"),sQuery(id+"F14.wireOp",EDGE,"E6575"),sQuery(id+"F14.wireOp",EDGE,"E6576"),sQuery(id+"F14.wireOp",EDGE,"E6577"),sQuery(id+"F14.wireOp",EDGE,"E6578"),sQuery(id+"F14.wireOp",EDGE,"E6579"),sQuery(id+"F14.wireOp",EDGE,"E6580"),sQuery(id+"F14.wireOp",EDGE,"E6581"),sQuery(id+"F14.wireOp",EDGE,"E6582"),sQuery(id+"F14.wireOp",EDGE,"E6583"),sQuery(id+"F14.wireOp",EDGE,"E6584"),sQuery(id+"F14.wireOp",EDGE,"E6585"),sQuery(id+"F14.wireOp",EDGE,"E6586"),sQuery(id+"F14.wireOp",EDGE,"E6587"),sQuery(id+"F14.wireOp",EDGE,"E6588"),sQuery(id+"F14.wireOp",EDGE,"E6589"),sQuery(id+"F14.wireOp",EDGE,"E6590"),sQuery(id+"F14.wireOp",EDGE,"E6591"),sQuery(id+"F14.wireOp",EDGE,"E6592"),sQuery(id+"F14.wireOp",EDGE,"E6593"),sQuery(id+"F14.wireOp",EDGE,"E6594"),sQuery(id+"F14.wireOp",EDGE,"E6595"),sQuery(id+"F14.wireOp",EDGE,"E6596"),sQuery(id+"F14.wireOp",EDGE,"E6597"),sQuery(id+"F14.wireOp",EDGE,"E6598"),sQuery(id+"F14.wireOp",EDGE,"E6599"),sQuery(id+"F14.wireOp",EDGE,"E6600"),sQuery(id+"F14.wireOp",EDGE,"E6601"),sQuery(id+"F14.wireOp",EDGE,"E6602"),sQuery(id+"F14.wireOp",EDGE,"E6603"),sQuery(id+"F14.wireOp",EDGE,"E6604"),sQuery(id+"F14.wireOp",EDGE,"E6605"),sQuery(id+"F14.wireOp",EDGE,"E6606"),sQuery(id+"F14.wireOp",EDGE,"E6607"),sQuery(id+"F14.wireOp",EDGE,"E6608"),sQuery(id+"F14.wireOp",EDGE,"E6609"),sQuery(id+"F14.wireOp",EDGE,"E6610"),sQuery(id+"F14.wireOp",EDGE,"E6611"),sQuery(id+"F14.wireOp",EDGE,"E6612"),sQuery(id+"F14.wireOp",EDGE,"E6613"),sQuery(id+"F14.wireOp",EDGE,"E6614"),sQuery(id+"F14.wireOp",EDGE,"E6615"),sQuery(id+"F14.wireOp",EDGE,"E6616"),sQuery(id+"F14.wireOp",EDGE,"E6617"),sQuery(id+"F14.wireOp",EDGE,"E6618"),sQuery(id+"F14.wireOp",EDGE,"E6619"),sQuery(id+"F14.wireOp",EDGE,"E6620"),sQuery(id+"F14.wireOp",EDGE,"E6621"),sQuery(id+"F14.wireOp",EDGE,"E6622"),sQuery(id+"F14.wireOp",EDGE,"E6623"),sQuery(id+"F14.wireOp",EDGE,"E6624"),sQuery(id+"F14.wireOp",EDGE,"E6625"),sQuery(id+"F14.wireOp",EDGE,"E6626"),sQuery(id+"F14.wireOp",EDGE,"E6627"),sQuery(id+"F14.wireOp",EDGE,"E6628"),sQuery(id+"F14.wireOp",EDGE,"E6629"),sQuery(id+"F14.wireOp",EDGE,"E6630"),sQuery(id+"F14.wireOp",EDGE,"E6631"),sQuery(id+"F14.wireOp",EDGE,"E6632"),sQuery(id+"F14.wireOp",EDGE,"E6633"),sQuery(id+"F14.wireOp",EDGE,"E6634"),sQuery(id+"F14.wireOp",EDGE,"E6635"),sQuery(id+"F14.wireOp",EDGE,"E6636"),sQuery(id+"F14.wireOp",EDGE,"E6637"),sQuery(id+"F14.wireOp",EDGE,"E6638"),sQuery(id+"F14.wireOp",EDGE,"E6639"),sQuery(id+"F14.wireOp",EDGE,"E6640"),sQuery(id+"F14.wireOp",EDGE,"E6641"),sQuery(id+"F14.wireOp",EDGE,"E6642"),sQuery(id+"F14.wireOp",EDGE,"E6643"),sQuery(id+"F14.wireOp",EDGE,"E6644"),sQuery(id+"F14.wireOp",EDGE,"E6645"),sQuery(id+"F14.wireOp",EDGE,"E6646"),sQuery(id+"F14.wireOp",EDGE,"E6647"),sQuery(id+"F14.wireOp",EDGE,"E6648"),sQuery(id+"F14.wireOp",EDGE,"E6649"),sQuery(id+"F14.wireOp",EDGE,"E6650"),sQuery(id+"F14.wireOp",EDGE,"E6651"),sQuery(id+"F14.wireOp",EDGE,"E6652"),sQuery(id+"F14.wireOp",EDGE,"E6653"),sQuery(id+"F14.wireOp",EDGE,"E6654"),sQuery(id+"F14.wireOp",EDGE,"E6655"),sQuery(id+"F14.wireOp",EDGE,"E6656"),sQuery(id+"F14.wireOp",EDGE,"E6657"),sQuery(id+"F14.wireOp",EDGE,"E6658"),sQuery(id+"F14.wireOp",EDGE,"E6659"),sQuery(id+"F14.wireOp",EDGE,"E6660"),sQuery(id+"F14.wireOp",EDGE,"E6661"),sQuery(id+"F14.wireOp",EDGE,"E6662"),sQuery(id+"F14.wireOp",EDGE,"E6663"),sQuery(id+"F14.wireOp",EDGE,"E6664"),sQuery(id+"F14.wireOp",EDGE,"E6665"),sQuery(id+"F14.wireOp",EDGE,"E6666"),sQuery(id+"F14.wireOp",EDGE,"E6667"),sQuery(id+"F14.wireOp",EDGE,"E6668"),sQuery(id+"F14.wireOp",EDGE,"E6669"),sQuery(id+"F14.wireOp",EDGE,"E6670"),sQuery(id+"F14.wireOp",EDGE,"E6671"),sQuery(id+"F14.wireOp",EDGE,"E6672"),sQuery(id+"F14.wireOp",EDGE,"E6673"),sQuery(id+"F14.wireOp",EDGE,"E6674"),sQuery(id+"F14.wireOp",EDGE,"E6675"),sQuery(id+"F14.wireOp",EDGE,"E6676"),sQuery(id+"F14.wireOp",EDGE,"E6677"),sQuery(id+"F14.wireOp",EDGE,"E6678"),sQuery(id+"F14.wireOp",EDGE,"E6679"),sQuery(id+"F14.wireOp",EDGE,"E6680"),sQuery(id+"F14.wireOp",EDGE,"E6681"),sQuery(id+"F14.wireOp",EDGE,"E6682"),sQuery(id+"F14.wireOp",EDGE,"E6683"),sQuery(id+"F14.wireOp",EDGE,"E6684"),sQuery(id+"F14.wireOp",EDGE,"E6685"),sQuery(id+"F14.wireOp",EDGE,"E6686"),sQuery(id+"F14.wireOp",EDGE,"E6687"),sQuery(id+"F14.wireOp",EDGE,"E6688"),sQuery(id+"F14.wireOp",EDGE,"E6689"),sQuery(id+"F14.wireOp",EDGE,"E6690"),sQuery(id+"F14.wireOp",EDGE,"E6691"),sQuery(id+"F14.wireOp",EDGE,"E6692"),sQuery(id+"F14.wireOp",EDGE,"E6693"),sQuery(id+"F14.wireOp",EDGE,"E6694"),sQuery(id+"F14.wireOp",EDGE,"E6695"),sQuery(id+"F14.wireOp",EDGE,"E6696"),sQuery(id+"F14.wireOp",EDGE,"E6697"),sQuery(id+"F14.wireOp",EDGE,"E6698"),sQuery(id+"F14.wireOp",EDGE,"E6699"),sQuery(id+"F14.wireOp",EDGE,"E6700"),sQuery(id+"F14.wireOp",EDGE,"E6701"),sQuery(id+"F14.wireOp",EDGE,"E6702"),sQuery(id+"F14.wireOp",EDGE,"E6703"),sQuery(id+"F14.wireOp",EDGE,"E6704"),sQuery(id+"F14.wireOp",EDGE,"E6705"),sQuery(id+"F14.wireOp",EDGE,"E6706"),sQuery(id+"F14.wireOp",EDGE,"E6707"),sQuery(id+"F14.wireOp",EDGE,"E6708"),sQuery(id+"F14.wireOp",EDGE,"E6709"),sQuery(id+"F14.wireOp",EDGE,"E6710"),sQuery(id+"F14.wireOp",EDGE,"E6711"),sQuery(id+"F14.wireOp",EDGE,"E6712"),sQuery(id+"F14.wireOp",EDGE,"E6713"),sQuery(id+"F14.wireOp",EDGE,"E6714"),sQuery(id+"F14.wireOp",EDGE,"E6715"),sQuery(id+"F14.wireOp",EDGE,"E6716"),sQuery(id+"F14.wireOp",EDGE,"E6717"),sQuery(id+"F14.wireOp",EDGE,"E6718"),sQuery(id+"F14.wireOp",EDGE,"E6719"),sQuery(id+"F14.wireOp",EDGE,"E6720"),sQuery(id+"F14.wireOp",EDGE,"E6721"),sQuery(id+"F14.wireOp",EDGE,"E6722"),sQuery(id+"F14.wireOp",EDGE,"E6723"),sQuery(id+"F14.wireOp",EDGE,"E6724"),sQuery(id+"F14.wireOp",EDGE,"E6725"),sQuery(id+"F14.wireOp",EDGE,"E6726"),sQuery(id+"F14.wireOp",EDGE,"E6727"),sQuery(id+"F14.wireOp",EDGE,"E6728"),sQuery(id+"F14.wireOp",EDGE,"E6729"),sQuery(id+"F14.wireOp",EDGE,"E6730"),sQuery(id+"F14.wireOp",EDGE,"E6731"),sQuery(id+"F14.wireOp",EDGE,"E6732"),sQuery(id+"F14.wireOp",EDGE,"E6733"),sQuery(id+"F14.wireOp",EDGE,"E6734"),sQuery(id+"F14.wireOp",EDGE,"E6735"),sQuery(id+"F14.wireOp",EDGE,"E6736"),sQuery(id+"F14.wireOp",EDGE,"E6737"),sQuery(id+"F14.wireOp",EDGE,"E6738"),sQuery(id+"F14.wireOp",EDGE,"E6739"),sQuery(id+"F14.wireOp",EDGE,"E6740"),sQuery(id+"F14.wireOp",EDGE,"E6741"),sQuery(id+"F14.wireOp",EDGE,"E6742"),sQuery(id+"F14.wireOp",EDGE,"E6743"),sQuery(id+"F14.wireOp",EDGE,"E6744"),sQuery(id+"F14.wireOp",EDGE,"E6745"),sQuery(id+"F14.wireOp",EDGE,"E6746"),sQuery(id+"F14.wireOp",EDGE,"E6747"),sQuery(id+"F14.wireOp",EDGE,"E6748"),sQuery(id+"F14.wireOp",EDGE,"E6749"),sQuery(id+"F14.wireOp",EDGE,"E6750"),sQuery(id+"F14.wireOp",EDGE,"E6751"),sQuery(id+"F14.wireOp",EDGE,"E6752"),sQuery(id+"F14.wireOp",EDGE,"E6753"),sQuery(id+"F14.wireOp",EDGE,"E6754"),sQuery(id+"F14.wireOp",EDGE,"E6755"),sQuery(id+"F14.wireOp",EDGE,"E6756"),sQuery(id+"F14.wireOp",EDGE,"E6757"),sQuery(id+"F14.wireOp",EDGE,"E6758"),sQuery(id+"F14.wireOp",EDGE,"E6759"),sQuery(id+"F14.wireOp",EDGE,"E6760"),sQuery(id+"F14.wireOp",EDGE,"E6761"),sQuery(id+"F14.wireOp",EDGE,"E6762"),sQuery(id+"F14.wireOp",EDGE,"E6763"),sQuery(id+"F14.wireOp",EDGE,"E6764"),sQuery(id+"F14.wireOp",EDGE,"E6765"),sQuery(id+"F14.wireOp",EDGE,"E6766"),sQuery(id+"F14.wireOp",EDGE,"E6767"),sQuery(id+"F14.wireOp",EDGE,"E6768"),sQuery(id+"F14.wireOp",EDGE,"E6769"),sQuery(id+"F14.wireOp",EDGE,"E6770"),sQuery(id+"F14.wireOp",EDGE,"E6771"),sQuery(id+"F14.wireOp",EDGE,"E6772"),sQuery(id+"F14.wireOp",EDGE,"E6773"),sQuery(id+"F14.wireOp",EDGE,"E6774"),sQuery(id+"F14.wireOp",EDGE,"E6775"),sQuery(id+"F14.wireOp",EDGE,"E6776"),sQuery(id+"F14.wireOp",EDGE,"E6777"),sQuery(id+"F14.wireOp",EDGE,"E6778"),sQuery(id+"F14.wireOp",EDGE,"E6779"),sQuery(id+"F14.wireOp",EDGE,"E6780"),sQuery(id+"F14.wireOp",EDGE,"E6781"),sQuery(id+"F14.wireOp",EDGE,"E6782"),sQuery(id+"F14.wireOp",EDGE,"E6783"),sQuery(id+"F14.wireOp",EDGE,"E6784"),sQuery(id+"F14.wireOp",EDGE,"E6785"),sQuery(id+"F14.wireOp",EDGE,"E6786"),sQuery(id+"F14.wireOp",EDGE,"E6787"),sQuery(id+"F14.wireOp",EDGE,"E6788"),sQuery(id+"F14.wireOp",EDGE,"E6789"),sQuery(id+"F14.wireOp",EDGE,"E6790"),sQuery(id+"F14.wireOp",EDGE,"E6791"),sQuery(id+"F14.wireOp",EDGE,"E6792"),sQuery(id+"F14.wireOp",EDGE,"E6793"),sQuery(id+"F14.wireOp",EDGE,"E6794"),sQuery(id+"F14.wireOp",EDGE,"E6795"),sQuery(id+"F14.wireOp",EDGE,"E6796"),sQuery(id+"F14.wireOp",EDGE,"E6797"),sQuery(id+"F14.wireOp",EDGE,"E6798"),sQuery(id+"F14.wireOp",EDGE,"E6799"),sQuery(id+"F14.wireOp",EDGE,"E6800"),sQuery(id+"F14.wireOp",EDGE,"E6801"),sQuery(id+"F14.wireOp",EDGE,"E6802"),sQuery(id+"F14.wireOp",EDGE,"E6803"),sQuery(id+"F14.wireOp",EDGE,"E6804"),sQuery(id+"F14.wireOp",EDGE,"E6805"),sQuery(id+"F14.wireOp",EDGE,"E6806"),sQuery(id+"F14.wireOp",EDGE,"E6807"),sQuery(id+"F14.wireOp",EDGE,"E6808"),sQuery(id+"F14.wireOp",EDGE,"E6809"),sQuery(id+"F14.wireOp",EDGE,"E6810"),sQuery(id+"F14.wireOp",EDGE,"E6811"),sQuery(id+"F14.wireOp",EDGE,"E6812"),sQuery(id+"F14.wireOp",EDGE,"E6813"),sQuery(id+"F14.wireOp",EDGE,"E6814"),sQuery(id+"F14.wireOp",EDGE,"E6815"),sQuery(id+"F14.wireOp",EDGE,"E6816"),sQuery(id+"F14.wireOp",EDGE,"E6817"),sQuery(id+"F14.wireOp",EDGE,"E6818"),sQuery(id+"F14.wireOp",EDGE,"E6819"),sQuery(id+"F14.wireOp",EDGE,"E6820"),sQuery(id+"F14.wireOp",EDGE,"E6821"),sQuery(id+"F14.wireOp",EDGE,"E6822"),sQuery(id+"F14.wireOp",EDGE,"E6823"),sQuery(id+"F14.wireOp",EDGE,"E6824"),sQuery(id+"F14.wireOp",EDGE,"E6825"),sQuery(id+"F14.wireOp",EDGE,"E6826"),sQuery(id+"F14.wireOp",EDGE,"E6827"),sQuery(id+"F14.wireOp",EDGE,"E6828"),sQuery(id+"F14.wireOp",EDGE,"E6829"),sQuery(id+"F14.wireOp",EDGE,"E6830"),sQuery(id+"F14.wireOp",EDGE,"E6831"),sQuery(id+"F14.wireOp",EDGE,"E6832"),sQuery(id+"F14.wireOp",EDGE,"E6833"),sQuery(id+"F14.wireOp",EDGE,"E6834"),sQuery(id+"F14.wireOp",EDGE,"E6835"),sQuery(id+"F14.wireOp",EDGE,"E6836"),sQuery(id+"F14.wireOp",EDGE,"E6837"),sQuery(id+"F14.wireOp",EDGE,"E6838"),sQuery(id+"F14.wireOp",EDGE,"E6839"),sQuery(id+"F14.wireOp",EDGE,"E6840"),sQuery(id+"F14.wireOp",EDGE,"E6841"),sQuery(id+"F14.wireOp",EDGE,"E6842"),sQuery(id+"F14.wireOp",EDGE,"E6843"),sQuery(id+"F14.wireOp",EDGE,"E6844"),sQuery(id+"F14.wireOp",EDGE,"E6845"),sQuery(id+"F14.wireOp",EDGE,"E6846"),sQuery(id+"F14.wireOp",EDGE,"E6847"),sQuery(id+"F14.wireOp",EDGE,"E6848"),sQuery(id+"F14.wireOp",EDGE,"E6849"),sQuery(id+"F14.wireOp",EDGE,"E6850"),sQuery(id+"F14.wireOp",EDGE,"E6851"),sQuery(id+"F14.wireOp",EDGE,"E6852"),sQuery(id+"F14.wireOp",EDGE,"E6853"),sQuery(id+"F14.wireOp",EDGE,"E6854"),sQuery(id+"F14.wireOp",EDGE,"E6855"),sQuery(id+"F14.wireOp",EDGE,"E6856"),sQuery(id+"F14.wireOp",EDGE,"E6857"),sQuery(id+"F14.wireOp",EDGE,"E6858"),sQuery(id+"F14.wireOp",EDGE,"E6859"),sQuery(id+"F14.wireOp",EDGE,"E6860"),sQuery(id+"F14.wireOp",EDGE,"E6861"),sQuery(id+"F14.wireOp",EDGE,"E6862"),sQuery(id+"F14.wireOp",EDGE,"E6863"),sQuery(id+"F14.wireOp",EDGE,"E6864"),sQuery(id+"F14.wireOp",EDGE,"E6865"),sQuery(id+"F14.wireOp",EDGE,"E6866"),sQuery(id+"F14.wireOp",EDGE,"E6867"),sQuery(id+"F14.wireOp",EDGE,"E6868"),sQuery(id+"F14.wireOp",EDGE,"E6869"),sQuery(id+"F14.wireOp",EDGE,"E6870"),sQuery(id+"F14.wireOp",EDGE,"E6871"),sQuery(id+"F14.wireOp",EDGE,"E6872"),sQuery(id+"F14.wireOp",EDGE,"E6873"),sQuery(id+"F14.wireOp",EDGE,"E6874"),sQuery(id+"F14.wireOp",EDGE,"E6875"),sQuery(id+"F14.wireOp",EDGE,"E6876"),sQuery(id+"F14.wireOp",EDGE,"E6877"),sQuery(id+"F14.wireOp",EDGE,"E6878"),sQuery(id+"F14.wireOp",EDGE,"E6879"),sQuery(id+"F14.wireOp",EDGE,"E6880"),sQuery(id+"F14.wireOp",EDGE,"E6881"),sQuery(id+"F14.wireOp",EDGE,"E6882"),sQuery(id+"F14.wireOp",EDGE,"E6883"),sQuery(id+"F14.wireOp",EDGE,"E6884"),sQuery(id+"F14.wireOp",EDGE,"E6885"),sQuery(id+"F14.wireOp",EDGE,"E6886"),sQuery(id+"F14.wireOp",EDGE,"E6887"),sQuery(id+"F14.wireOp",EDGE,"E6888"),sQuery(id+"F14.wireOp",EDGE,"E6889"),sQuery(id+"F14.wireOp",EDGE,"E6890"),sQuery(id+"F14.wireOp",EDGE,"E6891"),sQuery(id+"F14.wireOp",EDGE,"E6892"),sQuery(id+"F14.wireOp",EDGE,"E6893"),sQuery(id+"F14.wireOp",EDGE,"E6894"),sQuery(id+"F14.wireOp",EDGE,"E6895"),sQuery(id+"F14.wireOp",EDGE,"E6896"),sQuery(id+"F14.wireOp",EDGE,"E6897"),sQuery(id+"F14.wireOp",EDGE,"E6898"),sQuery(id+"F14.wireOp",EDGE,"E6899"),sQuery(id+"F14.wireOp",EDGE,"E6900"),sQuery(id+"F14.wireOp",EDGE,"E6901"),sQuery(id+"F14.wireOp",EDGE,"E6902"),sQuery(id+"F14.wireOp",EDGE,"E6903"),sQuery(id+"F14.wireOp",EDGE,"E6904"),sQuery(id+"F14.wireOp",EDGE,"E6905"),sQuery(id+"F14.wireOp",EDGE,"E6906"),sQuery(id+"F14.wireOp",EDGE,"E6907"),sQuery(id+"F14.wireOp",EDGE,"E6908"),sQuery(id+"F14.wireOp",EDGE,"E6909"),sQuery(id+"F14.wireOp",EDGE,"E6910"),sQuery(id+"F14.wireOp",EDGE,"E6911"),sQuery(id+"F14.wireOp",EDGE,"E6912"),sQuery(id+"F14.wireOp",EDGE,"E6913"),sQuery(id+"F14.wireOp",EDGE,"E6914"),sQuery(id+"F14.wireOp",EDGE,"E6915"),sQuery(id+"F14.wireOp",EDGE,"E6916"),sQuery(id+"F14.wireOp",EDGE,"E6917"),sQuery(id+"F14.wireOp",EDGE,"E6918"),sQuery(id+"F14.wireOp",EDGE,"E6919"),sQuery(id+"F14.wireOp",EDGE,"E6920"),sQuery(id+"F14.wireOp",EDGE,"E6921"),sQuery(id+"F14.wireOp",EDGE,"E6922"),sQuery(id+"F14.wireOp",EDGE,"E6923"),sQuery(id+"F14.wireOp",EDGE,"E6924"),sQuery(id+"F14.wireOp",EDGE,"E6925"),sQuery(id+"F14.wireOp",EDGE,"E6926"),sQuery(id+"F14.wireOp",EDGE,"E6927"),sQuery(id+"F14.wireOp",EDGE,"E6928"),sQuery(id+"F14.wireOp",EDGE,"E6929"),sQuery(id+"F14.wireOp",EDGE,"E6930"),sQuery(id+"F14.wireOp",EDGE,"E6931"),sQuery(id+"F14.wireOp",EDGE,"E6932"),sQuery(id+"F14.wireOp",EDGE,"E6933"),sQuery(id+"F14.wireOp",EDGE,"E6934"),sQuery(id+"F14.wireOp",EDGE,"E6935"),sQuery(id+"F14.wireOp",EDGE,"E6936"),sQuery(id+"F14.wireOp",EDGE,"E6937"),sQuery(id+"F14.wireOp",EDGE,"E6938"),sQuery(id+"F14.wireOp",EDGE,"E6939"),sQuery(id+"F14.wireOp",EDGE,"E6940"),sQuery(id+"F14.wireOp",EDGE,"E6941"),sQuery(id+"F14.wireOp",EDGE,"E6942"),sQuery(id+"F14.wireOp",EDGE,"E6943"),sQuery(id+"F14.wireOp",EDGE,"E6944"),sQuery(id+"F14.wireOp",EDGE,"E6945"),sQuery(id+"F14.wireOp",EDGE,"E6946"),sQuery(id+"F14.wireOp",EDGE,"E6947"),sQuery(id+"F14.wireOp",EDGE,"E6948"),sQuery(id+"F14.wireOp",EDGE,"E6949"),sQuery(id+"F14.wireOp",EDGE,"E6950"),sQuery(id+"F14.wireOp",EDGE,"E6951"),sQuery(id+"F14.wireOp",EDGE,"E6952"),sQuery(id+"F14.wireOp",EDGE,"E6953"),sQuery(id+"F14.wireOp",EDGE,"E6954"),sQuery(id+"F14.wireOp",EDGE,"E6955"),sQuery(id+"F14.wireOp",EDGE,"E6956"),sQuery(id+"F14.wireOp",EDGE,"E6957"),sQuery(id+"F14.wireOp",EDGE,"E6958"),sQuery(id+"F14.wireOp",EDGE,"E6959"),sQuery(id+"F14.wireOp",EDGE,"E6960"),sQuery(id+"F14.wireOp",EDGE,"E6961"),sQuery(id+"F14.wireOp",EDGE,"E6962"),sQuery(id+"F14.wireOp",EDGE,"E6963"),sQuery(id+"F14.wireOp",EDGE,"E6964"),sQuery(id+"F14.wireOp",EDGE,"E6965"),sQuery(id+"F14.wireOp",EDGE,"E6966"),sQuery(id+"F14.wireOp",EDGE,"E6967"),sQuery(id+"F14.wireOp",EDGE,"E6968"),sQuery(id+"F14.wireOp",EDGE,"E6969"),sQuery(id+"F14.wireOp",EDGE,"E6970"),sQuery(id+"F14.wireOp",EDGE,"E6971"),sQuery(id+"F14.wireOp",EDGE,"E6972"),sQuery(id+"F14.wireOp",EDGE,"E6973"),sQuery(id+"F14.wireOp",EDGE,"E6974"),sQuery(id+"F14.wireOp",EDGE,"E6975"),sQuery(id+"F14.wireOp",EDGE,"E6976"),sQuery(id+"F14.wireOp",EDGE,"E6977"),sQuery(id+"F14.wireOp",EDGE,"E6978"),sQuery(id+"F14.wireOp",EDGE,"E6979"),sQuery(id+"F14.wireOp",EDGE,"E6980"),sQuery(id+"F14.wireOp",EDGE,"E6981"),sQuery(id+"F14.wireOp",EDGE,"E6982"),sQuery(id+"F14.wireOp",EDGE,"E6983"),sQuery(id+"F14.wireOp",EDGE,"E6984"),sQuery(id+"F14.wireOp",EDGE,"E6985"),sQuery(id+"F14.wireOp",EDGE,"E6986"),sQuery(id+"F14.wireOp",EDGE,"E6987"),sQuery(id+"F14.wireOp",EDGE,"E6988"),sQuery(id+"F14.wireOp",EDGE,"E6989"),sQuery(id+"F14.wireOp",EDGE,"E6990"),sQuery(id+"F14.wireOp",EDGE,"E6991"),sQuery(id+"F14.wireOp",EDGE,"E6992"),sQuery(id+"F14.wireOp",EDGE,"E6993"),sQuery(id+"F14.wireOp",EDGE,"E6994"),sQuery(id+"F14.wireOp",EDGE,"E6995"),sQuery(id+"F14.wireOp",EDGE,"E6996"),sQuery(id+"F14.wireOp",EDGE,"E6997"),sQuery(id+"F14.wireOp",EDGE,"E6998"),sQuery(id+"F14.wireOp",EDGE,"E6999"),sQuery(id+"F14.wireOp",EDGE,"E7000"),sQuery(id+"F14.wireOp",EDGE,"E7001"),sQuery(id+"F14.wireOp",EDGE,"E7002"),sQuery(id+"F14.wireOp",EDGE,"E7003"),sQuery(id+"F14.wireOp",EDGE,"E7004"),sQuery(id+"F14.wireOp",EDGE,"E7005"),sQuery(id+"F14.wireOp",EDGE,"E7006"),sQuery(id+"F14.wireOp",EDGE,"E7007"),sQuery(id+"F14.wireOp",EDGE,"E7008"),sQuery(id+"F14.wireOp",EDGE,"E7009"),sQuery(id+"F14.wireOp",EDGE,"E7010"),sQuery(id+"F14.wireOp",EDGE,"E7011"),sQuery(id+"F14.wireOp",EDGE,"E7012"),sQuery(id+"F14.wireOp",EDGE,"E7013"),sQuery(id+"F14.wireOp",EDGE,"E7014"),sQuery(id+"F14.wireOp",EDGE,"E7015"),sQuery(id+"F14.wireOp",EDGE,"E7016"),sQuery(id+"F14.wireOp",EDGE,"E7017"),sQuery(id+"F14.wireOp",EDGE,"E7018"),sQuery(id+"F14.wireOp",EDGE,"E7019"),sQuery(id+"F14.wireOp",EDGE,"E7020"),sQuery(id+"F14.wireOp",EDGE,"E7021"),sQuery(id+"F14.wireOp",EDGE,"E7022"),sQuery(id+"F14.wireOp",EDGE,"E7023"),sQuery(id+"F14.wireOp",EDGE,"E7024"),sQuery(id+"F14.wireOp",EDGE,"E7025"),sQuery(id+"F14.wireOp",EDGE,"E7026"),sQuery(id+"F14.wireOp",EDGE,"E7027"),sQuery(id+"F14.wireOp",EDGE,"E7028"),sQuery(id+"F14.wireOp",EDGE,"E7029"),sQuery(id+"F14.wireOp",EDGE,"E7030"),sQuery(id+"F14.wireOp",EDGE,"E7031"),sQuery(id+"F14.wireOp",EDGE,"E7032"),sQuery(id+"F14.wireOp",EDGE,"E7033"),sQuery(id+"F14.wireOp",EDGE,"E7034"),sQuery(id+"F14.wireOp",EDGE,"E7035"),sQuery(id+"F14.wireOp",EDGE,"E7036"),sQuery(id+"F14.wireOp",EDGE,"E7037"),sQuery(id+"F14.wireOp",EDGE,"E7038"),sQuery(id+"F14.wireOp",EDGE,"E7039"),sQuery(id+"F14.wireOp",EDGE,"E7040"),sQuery(id+"F14.wireOp",EDGE,"E7041"),sQuery(id+"F14.wireOp",EDGE,"E7042"),sQuery(id+"F14.wireOp",EDGE,"E7043"),sQuery(id+"F14.wireOp",EDGE,"E7044"),sQuery(id+"F14.wireOp",EDGE,"E7045"),sQuery(id+"F14.wireOp",EDGE,"E7046"),sQuery(id+"F14.wireOp",EDGE,"E7047"),sQuery(id+"F14.wireOp",EDGE,"E7048"),sQuery(id+"F14.wireOp",EDGE,"E7049"),sQuery(id+"F14.wireOp",EDGE,"E7050"),sQuery(id+"F14.wireOp",EDGE,"E7051"),sQuery(id+"F14.wireOp",EDGE,"E7052"),sQuery(id+"F14.wireOp",EDGE,"E7053"),sQuery(id+"F14.wireOp",EDGE,"E7054"),sQuery(id+"F14.wireOp",EDGE,"E7055"),sQuery(id+"F14.wireOp",EDGE,"E7056"),sQuery(id+"F14.wireOp",EDGE,"E7057"),sQuery(id+"F14.wireOp",EDGE,"E7058"),sQuery(id+"F14.wireOp",EDGE,"E7059"),sQuery(id+"F14.wireOp",EDGE,"E7060"),sQuery(id+"F14.wireOp",EDGE,"E7061"),sQuery(id+"F14.wireOp",EDGE,"E7062"),sQuery(id+"F14.wireOp",EDGE,"E7063"),sQuery(id+"F14.wireOp",EDGE,"E7064"),sQuery(id+"F14.wireOp",EDGE,"E7065"),sQuery(id+"F14.wireOp",EDGE,"E7066"),sQuery(id+"F14.wireOp",EDGE,"E7067"),sQuery(id+"F14.wireOp",EDGE,"E7068"),sQuery(id+"F14.wireOp",EDGE,"E7069"),sQuery(id+"F14.wireOp",EDGE,"E7070"),sQuery(id+"F14.wireOp",EDGE,"E7071"),sQuery(id+"F14.wireOp",EDGE,"E7072"),sQuery(id+"F14.wireOp",EDGE,"E7073"),sQuery(id+"F14.wireOp",EDGE,"E7074"),sQuery(id+"F14.wireOp",EDGE,"E7075"),sQuery(id+"F14.wireOp",EDGE,"E7076"),sQuery(id+"F14.wireOp",EDGE,"E7077"),sQuery(id+"F14.wireOp",EDGE,"E7078"),sQuery(id+"F14.wireOp",EDGE,"E7079"),sQuery(id+"F14.wireOp",EDGE,"E7080"),sQuery(id+"F14.wireOp",EDGE,"E7081"),sQuery(id+"F14.wireOp",EDGE,"E7082"),sQuery(id+"F14.wireOp",EDGE,"E7083"),sQuery(id+"F14.wireOp",EDGE,"E7084"),sQuery(id+"F14.wireOp",EDGE,"E7085"),sQuery(id+"F14.wireOp",EDGE,"E7086"),sQuery(id+"F14.wireOp",EDGE,"E7087"),sQuery(id+"F14.wireOp",EDGE,"E7088"),sQuery(id+"F14.wireOp",EDGE,"E7089"),sQuery(id+"F14.wireOp",EDGE,"E7090"),sQuery(id+"F14.wireOp",EDGE,"E7091"),sQuery(id+"F14.wireOp",EDGE,"E7092"),sQuery(id+"F14.wireOp",EDGE,"E7093"),sQuery(id+"F14.wireOp",EDGE,"E7094"),sQuery(id+"F14.wireOp",EDGE,"E7095"),sQuery(id+"F14.wireOp",EDGE,"E7096"),sQuery(id+"F14.wireOp",EDGE,"E7097"),sQuery(id+"F14.wireOp",EDGE,"E7098"),sQuery(id+"F14.wireOp",EDGE,"E7099"),sQuery(id+"F14.wireOp",EDGE,"E7100"),sQuery(id+"F14.wireOp",EDGE,"E7101"),sQuery(id+"F14.wireOp",EDGE,"E7102"),sQuery(id+"F14.wireOp",EDGE,"E7103"),sQuery(id+"F14.wireOp",EDGE,"E7104"),sQuery(id+"F14.wireOp",EDGE,"E7105"),sQuery(id+"F14.wireOp",EDGE,"E7106"),sQuery(id+"F14.wireOp",EDGE,"E7107"),sQuery(id+"F14.wireOp",EDGE,"E7108"),sQuery(id+"F14.wireOp",EDGE,"E7109"),sQuery(id+"F14.wireOp",EDGE,"E7110"),sQuery(id+"F14.wireOp",EDGE,"E7111"),sQuery(id+"F14.wireOp",EDGE,"E7112"),sQuery(id+"F14.wireOp",EDGE,"E7113"),sQuery(id+"F14.wireOp",EDGE,"E7114"),sQuery(id+"F14.wireOp",EDGE,"E7115"),sQuery(id+"F14.wireOp",EDGE,"E7116"),sQuery(id+"F14.wireOp",EDGE,"E7117"),sQuery(id+"F14.wireOp",EDGE,"E7118"),sQuery(id+"F14.wireOp",EDGE,"E7119"),sQuery(id+"F14.wireOp",EDGE,"E7120"),sQuery(id+"F14.wireOp",EDGE,"E7121"),sQuery(id+"F14.wireOp",EDGE,"E7122"),sQuery(id+"F14.wireOp",EDGE,"E7123"),sQuery(id+"F14.wireOp",EDGE,"E7124"),sQuery(id+"F14.wireOp",EDGE,"E7125"),sQuery(id+"F14.wireOp",EDGE,"E7126"),sQuery(id+"F14.wireOp",EDGE,"E7127"),sQuery(id+"F14.wireOp",EDGE,"E7128"),sQuery(id+"F14.wireOp",EDGE,"E7129"),sQuery(id+"F14.wireOp",EDGE,"E7130"),sQuery(id+"F14.wireOp",EDGE,"E7131"),sQuery(id+"F14.wireOp",EDGE,"E7132"),sQuery(id+"F14.wireOp",EDGE,"E7133"),sQuery(id+"F14.wireOp",EDGE,"E7134"),sQuery(id+"F14.wireOp",EDGE,"E7135"),sQuery(id+"F14.wireOp",EDGE,"E7136"),sQuery(id+"F14.wireOp",EDGE,"E7137"),sQuery(id+"F14.wireOp",EDGE,"E7138"),sQuery(id+"F14.wireOp",EDGE,"E7139"),sQuery(id+"F14.wireOp",EDGE,"E7140"),sQuery(id+"F14.wireOp",EDGE,"E7141"),sQuery(id+"F14.wireOp",EDGE,"E7142"),sQuery(id+"F14.wireOp",EDGE,"E7143"),sQuery(id+"F14.wireOp",EDGE,"E7144"),sQuery(id+"F14.wireOp",EDGE,"E7145"),sQuery(id+"F14.wireOp",EDGE,"E7146"),sQuery(id+"F14.wireOp",EDGE,"E7147"),sQuery(id+"F14.wireOp",EDGE,"E7148"),sQuery(id+"F14.wireOp",EDGE,"E7149"),sQuery(id+"F14.wireOp",EDGE,"E7150"),sQuery(id+"F14.wireOp",EDGE,"E7151"),sQuery(id+"F14.wireOp",EDGE,"E7152"),sQuery(id+"F14.wireOp",EDGE,"E7153"),sQuery(id+"F14.wireOp",EDGE,"E7154"),sQuery(id+"F14.wireOp",EDGE,"E7155"),sQuery(id+"F14.wireOp",EDGE,"E7156"),sQuery(id+"F14.wireOp",EDGE,"E7157"),sQuery(id+"F14.wireOp",EDGE,"E7158"),sQuery(id+"F14.wireOp",EDGE,"E7159"),sQuery(id+"F14.wireOp",EDGE,"E7160"),sQuery(id+"F14.wireOp",EDGE,"E7161"),sQuery(id+"F14.wireOp",EDGE,"E7162"),sQuery(id+"F14.wireOp",EDGE,"E7163"),sQuery(id+"F14.wireOp",EDGE,"E7164"),sQuery(id+"F14.wireOp",EDGE,"E7165"),sQuery(id+"F14.wireOp",EDGE,"E7166"),sQuery(id+"F14.wireOp",EDGE,"E7167"),sQuery(id+"F14.wireOp",EDGE,"E7168"),sQuery(id+"F14.wireOp",EDGE,"E7169"),sQuery(id+"F14.wireOp",EDGE,"E7170"),sQuery(id+"F14.wireOp",EDGE,"E7171"),sQuery(id+"F14.wireOp",EDGE,"E7172"),sQuery(id+"F14.wireOp",EDGE,"E7173"),sQuery(id+"F14.wireOp",EDGE,"E7174"),sQuery(id+"F14.wireOp",EDGE,"E7175"),sQuery(id+"F14.wireOp",EDGE,"E7176"),sQuery(id+"F14.wireOp",EDGE,"E7177"),sQuery(id+"F14.wireOp",EDGE,"E7178"),sQuery(id+"F14.wireOp",EDGE,"E7179"),sQuery(id+"F14.wireOp",EDGE,"E7180"),sQuery(id+"F14.wireOp",EDGE,"E7181"),sQuery(id+"F14.wireOp",EDGE,"E7182"),sQuery(id+"F14.wireOp",EDGE,"E7183"),sQuery(id+"F14.wireOp",EDGE,"E7184"),sQuery(id+"F14.wireOp",EDGE,"E7185"),sQuery(id+"F14.wireOp",EDGE,"E7186"),sQuery(id+"F14.wireOp",EDGE,"E7187"),sQuery(id+"F14.wireOp",EDGE,"E7188"),sQuery(id+"F14.wireOp",EDGE,"E7189"),sQuery(id+"F14.wireOp",EDGE,"E7190"),sQuery(id+"F14.wireOp",EDGE,"E7191"),sQuery(id+"F14.wireOp",EDGE,"E7192"),sQuery(id+"F14.wireOp",EDGE,"E7193"),sQuery(id+"F14.wireOp",EDGE,"E7194"),sQuery(id+"F14.wireOp",EDGE,"E7195"),sQuery(id+"F14.wireOp",EDGE,"E7196"),sQuery(id+"F14.wireOp",EDGE,"E7197"),sQuery(id+"F14.wireOp",EDGE,"E7198"),sQuery(id+"F14.wireOp",EDGE,"E7199"),sQuery(id+"F14.wireOp",EDGE,"E7200"),sQuery(id+"F14.wireOp",EDGE,"E7201"),sQuery(id+"F14.wireOp",EDGE,"E7202"),sQuery(id+"F14.wireOp",EDGE,"E7203"),sQuery(id+"F14.wireOp",EDGE,"E7204"),sQuery(id+"F14.wireOp",EDGE,"E7205"),sQuery(id+"F14.wireOp",EDGE,"E7206"),sQuery(id+"F14.wireOp",EDGE,"E7207"),sQuery(id+"F14.wireOp",EDGE,"E7208"),sQuery(id+"F14.wireOp",EDGE,"E7209"),sQuery(id+"F14.wireOp",EDGE,"E7210"),sQuery(id+"F14.wireOp",EDGE,"E7211"),sQuery(id+"F14.wireOp",EDGE,"E7212"),sQuery(id+"F14.wireOp",EDGE,"E7213"),sQuery(id+"F14.wireOp",EDGE,"E7214"),sQuery(id+"F14.wireOp",EDGE,"E7215"),sQuery(id+"F14.wireOp",EDGE,"E7216"),sQuery(id+"F14.wireOp",EDGE,"E7217"),sQuery(id+"F14.wireOp",EDGE,"E7218"),sQuery(id+"F14.wireOp",EDGE,"E7219"),sQuery(id+"F14.wireOp",EDGE,"E7220"),sQuery(id+"F14.wireOp",EDGE,"E7221"),sQuery(id+"F14.wireOp",EDGE,"E7222"),sQuery(id+"F14.wireOp",EDGE,"E7223"),sQuery(id+"F14.wireOp",EDGE,"E7224"),sQuery(id+"F14.wireOp",EDGE,"E7225"),sQuery(id+"F14.wireOp",EDGE,"E7226"),sQuery(id+"F14.wireOp",EDGE,"E7227"),sQuery(id+"F14.wireOp",EDGE,"E7228"),sQuery(id+"F14.wireOp",EDGE,"E7229"),sQuery(id+"F14.wireOp",EDGE,"E7230"),sQuery(id+"F14.wireOp",EDGE,"E7231"),sQuery(id+"F14.wireOp",EDGE,"E7232"),sQuery(id+"F14.wireOp",EDGE,"E7233"),sQuery(id+"F14.wireOp",EDGE,"E7234"),sQuery(id+"F14.wireOp",EDGE,"E7235"),sQuery(id+"F14.wireOp",EDGE,"E7236"),sQuery(id+"F14.wireOp",EDGE,"E7237"),sQuery(id+"F14.wireOp",EDGE,"E7238"),sQuery(id+"F14.wireOp",EDGE,"E7239"),sQuery(id+"F14.wireOp",EDGE,"E7240"),sQuery(id+"F14.wireOp",EDGE,"E7241"),sQuery(id+"F14.wireOp",EDGE,"E7242"),sQuery(id+"F14.wireOp",EDGE,"E7243"),sQuery(id+"F14.wireOp",EDGE,"E7244"),sQuery(id+"F14.wireOp",EDGE,"E7245"),sQuery(id+"F14.wireOp",EDGE,"E7246"),sQuery(id+"F14.wireOp",EDGE,"E7247"),sQuery(id+"F14.wireOp",EDGE,"E7248"),sQuery(id+"F14.wireOp",EDGE,"E7249"),sQuery(id+"F14.wireOp",EDGE,"E7250"),sQuery(id+"F14.wireOp",EDGE,"E7251"),sQuery(id+"F14.wireOp",EDGE,"E7252"),sQuery(id+"F14.wireOp",EDGE,"E7253"),sQuery(id+"F14.wireOp",EDGE,"E7254"),sQuery(id+"F14.wireOp",EDGE,"E7255"),sQuery(id+"F14.wireOp",EDGE,"E7256"),sQuery(id+"F14.wireOp",EDGE,"E7257"),sQuery(id+"F14.wireOp",EDGE,"E7258"),sQuery(id+"F14.wireOp",EDGE,"E7259"),sQuery(id+"F14.wireOp",EDGE,"E7260"),sQuery(id+"F14.wireOp",EDGE,"E7261"),sQuery(id+"F14.wireOp",EDGE,"E7262"),sQuery(id+"F14.wireOp",EDGE,"E7263"),sQuery(id+"F14.wireOp",EDGE,"E7264"),sQuery(id+"F14.wireOp",EDGE,"E7265"),sQuery(id+"F14.wireOp",EDGE,"E7266"),sQuery(id+"F14.wireOp",EDGE,"E7267"),sQuery(id+"F14.wireOp",EDGE,"E7268"),sQuery(id+"F14.wireOp",EDGE,"E7269"),sQuery(id+"F14.wireOp",EDGE,"E7270"),sQuery(id+"F14.wireOp",EDGE,"E7271"),sQuery(id+"F14.wireOp",EDGE,"E7272"),sQuery(id+"F14.wireOp",EDGE,"E7273"),sQuery(id+"F14.wireOp",EDGE,"E7274"),sQuery(id+"F14.wireOp",EDGE,"E7275"),sQuery(id+"F14.wireOp",EDGE,"E7276"),sQuery(id+"F14.wireOp",EDGE,"E7277"),sQuery(id+"F14.wireOp",EDGE,"E7278"),sQuery(id+"F14.wireOp",EDGE,"E7279"),sQuery(id+"F14.wireOp",EDGE,"E7280"),sQuery(id+"F14.wireOp",EDGE,"E7281"),sQuery(id+"F14.wireOp",EDGE,"E7282"),sQuery(id+"F14.wireOp",EDGE,"E7283"),sQuery(id+"F14.wireOp",EDGE,"E7284"),sQuery(id+"F14.wireOp",EDGE,"E7285"),sQuery(id+"F14.wireOp",EDGE,"E7286"),sQuery(id+"F14.wireOp",EDGE,"E7287"),sQuery(id+"F14.wireOp",EDGE,"E7288"),sQuery(id+"F14.wireOp",EDGE,"E7289"),sQuery(id+"F14.wireOp",EDGE,"E7290"),sQuery(id+"F14.wireOp",EDGE,"E7291"),sQuery(id+"F14.wireOp",EDGE,"E7292"),sQuery(id+"F14.wireOp",EDGE,"E7293"),sQuery(id+"F14.wireOp",EDGE,"E7294"),sQuery(id+"F14.wireOp",EDGE,"E7295"),sQuery(id+"F14.wireOp",EDGE,"E7296"),sQuery(id+"F14.wireOp",EDGE,"E7297"),sQuery(id+"F14.wireOp",EDGE,"E7298"),sQuery(id+"F14.wireOp",EDGE,"E7299"),sQuery(id+"F14.wireOp",EDGE,"E7300"),sQuery(id+"F14.wireOp",EDGE,"E7301"),sQuery(id+"F14.wireOp",EDGE,"E7302"),sQuery(id+"F14.wireOp",EDGE,"E7303"),sQuery(id+"F14.wireOp",EDGE,"E7304"),sQuery(id+"F14.wireOp",EDGE,"E7305"),sQuery(id+"F14.wireOp",EDGE,"E7306"),sQuery(id+"F14.wireOp",EDGE,"E7307"),sQuery(id+"F14.wireOp",EDGE,"E7308"),sQuery(id+"F14.wireOp",EDGE,"E7309"),sQuery(id+"F14.wireOp",EDGE,"E7310"),sQuery(id+"F14.wireOp",EDGE,"E7311"),sQuery(id+"F14.wireOp",EDGE,"E7312"),sQuery(id+"F14.wireOp",EDGE,"E7313"),sQuery(id+"F14.wireOp",EDGE,"E7314"),sQuery(id+"F14.wireOp",EDGE,"E7315"),sQuery(id+"F14.wireOp",EDGE,"E7316"),sQuery(id+"F14.wireOp",EDGE,"E7317"),sQuery(id+"F14.wireOp",EDGE,"E7318"),sQuery(id+"F14.wireOp",EDGE,"E7319"),sQuery(id+"F14.wireOp",EDGE,"E7320"),sQuery(id+"F14.wireOp",EDGE,"E7321"),sQuery(id+"F14.wireOp",EDGE,"E7322"),sQuery(id+"F14.wireOp",EDGE,"E7323"),sQuery(id+"F14.wireOp",EDGE,"E7324"),sQuery(id+"F14.wireOp",EDGE,"E7325"),sQuery(id+"F14.wireOp",EDGE,"E7326"),sQuery(id+"F14.wireOp",EDGE,"E7327"),sQuery(id+"F14.wireOp",EDGE,"E7328"),sQuery(id+"F14.wireOp",EDGE,"E7329"),sQuery(id+"F14.wireOp",EDGE,"E7330"),sQuery(id+"F14.wireOp",EDGE,"E7331"),sQuery(id+"F14.wireOp",EDGE,"E7332"),sQuery(id+"F14.wireOp",EDGE,"E7333"),sQuery(id+"F14.wireOp",EDGE,"E7334"),sQuery(id+"F14.wireOp",EDGE,"E7335"),sQuery(id+"F14.wireOp",EDGE,"E7336"),sQuery(id+"F14.wireOp",EDGE,"E7337"),sQuery(id+"F14.wireOp",EDGE,"E7338"),sQuery(id+"F14.wireOp",EDGE,"E7339"),sQuery(id+"F14.wireOp",EDGE,"E7340"),sQuery(id+"F14.wireOp",EDGE,"E7341"),sQuery(id+"F14.wireOp",EDGE,"E7342"),sQuery(id+"F14.wireOp",EDGE,"E7343"),sQuery(id+"F14.wireOp",EDGE,"E7344"),sQuery(id+"F14.wireOp",EDGE,"E7345"),sQuery(id+"F14.wireOp",EDGE,"E7346"),sQuery(id+"F14.wireOp",EDGE,"E7347"),sQuery(id+"F14.wireOp",EDGE,"E7348"),sQuery(id+"F14.wireOp",EDGE,"E7349"),sQuery(id+"F14.wireOp",EDGE,"E7350"),sQuery(id+"F14.wireOp",EDGE,"E7351"),sQuery(id+"F14.wireOp",EDGE,"E7352"),sQuery(id+"F14.wireOp",EDGE,"E7353"),sQuery(id+"F14.wireOp",EDGE,"E7354"),sQuery(id+"F14.wireOp",EDGE,"E7355"),sQuery(id+"F14.wireOp",EDGE,"E7356"),sQuery(id+"F14.wireOp",EDGE,"E7357"),sQuery(id+"F14.wireOp",EDGE,"E7358"),sQuery(id+"F14.wireOp",EDGE,"E7359"),sQuery(id+"F14.wireOp",EDGE,"E7360"),sQuery(id+"F14.wireOp",EDGE,"E7361"),sQuery(id+"F14.wireOp",EDGE,"E7362"),sQuery(id+"F14.wireOp",EDGE,"E7363"),sQuery(id+"F14.wireOp",EDGE,"E7364"),sQuery(id+"F14.wireOp",EDGE,"E7365"),sQuery(id+"F14.wireOp",EDGE,"E7366"),sQuery(id+"F14.wireOp",EDGE,"E7367"),sQuery(id+"F14.wireOp",EDGE,"E7368"),sQuery(id+"F14.wireOp",EDGE,"E7369"),sQuery(id+"F14.wireOp",EDGE,"E7370"),sQuery(id+"F14.wireOp",EDGE,"E7371"),sQuery(id+"F14.wireOp",EDGE,"E7372"),sQuery(id+"F14.wireOp",EDGE,"E7373"),sQuery(id+"F14.wireOp",EDGE,"E7374"),sQuery(id+"F14.wireOp",EDGE,"E7375"),sQuery(id+"F14.wireOp",EDGE,"E7376"),sQuery(id+"F14.wireOp",EDGE,"E7377"),sQuery(id+"F14.wireOp",EDGE,"E7378"),sQuery(id+"F14.wireOp",EDGE,"E7379"),sQuery(id+"F14.wireOp",EDGE,"E7380"),sQuery(id+"F14.wireOp",EDGE,"E7381"),sQuery(id+"F14.wireOp",EDGE,"E7382"),sQuery(id+"F14.wireOp",EDGE,"E7383"),sQuery(id+"F14.wireOp",EDGE,"E7384"),sQuery(id+"F14.wireOp",EDGE,"E7385"),sQuery(id+"F14.wireOp",EDGE,"E7386"),sQuery(id+"F14.wireOp",EDGE,"E7387"),sQuery(id+"F14.wireOp",EDGE,"E7388"),sQuery(id+"F14.wireOp",EDGE,"E7389"),sQuery(id+"F14.wireOp",EDGE,"E7390"),sQuery(id+"F14.wireOp",EDGE,"E7391"),sQuery(id+"F14.wireOp",EDGE,"E7392"),sQuery(id+"F14.wireOp",EDGE,"E7393"),sQuery(id+"F14.wireOp",EDGE,"E7394"),sQuery(id+"F14.wireOp",EDGE,"E7395"),sQuery(id+"F14.wireOp",EDGE,"E7396"),sQuery(id+"F14.wireOp",EDGE,"E7397"),sQuery(id+"F14.wireOp",EDGE,"E7398"),sQuery(id+"F14.wireOp",EDGE,"E7399"),sQuery(id+"F14.wireOp",EDGE,"E7400"),sQuery(id+"F14.wireOp",EDGE,"E7401"),sQuery(id+"F14.wireOp",EDGE,"E7402"),sQuery(id+"F14.wireOp",EDGE,"E7403"),sQuery(id+"F14.wireOp",EDGE,"E7404"),sQuery(id+"F14.wireOp",EDGE,"E7405"),sQuery(id+"F14.wireOp",EDGE,"E7406"),sQuery(id+"F14.wireOp",EDGE,"E7407"),sQuery(id+"F14.wireOp",EDGE,"E7408"),sQuery(id+"F14.wireOp",EDGE,"E7409"),sQuery(id+"F14.wireOp",EDGE,"E7410"),sQuery(id+"F14.wireOp",EDGE,"E7411"),sQuery(id+"F14.wireOp",EDGE,"E7412"),sQuery(id+"F14.wireOp",EDGE,"E7413"),sQuery(id+"F14.wireOp",EDGE,"E7414"),sQuery(id+"F14.wireOp",EDGE,"E7415"),sQuery(id+"F14.wireOp",EDGE,"E7416"),sQuery(id+"F14.wireOp",EDGE,"E7417"),sQuery(id+"F14.wireOp",EDGE,"E7418"),sQuery(id+"F14.wireOp",EDGE,"E7419"),sQuery(id+"F14.wireOp",EDGE,"E7420"),sQuery(id+"F14.wireOp",EDGE,"E7421"),sQuery(id+"F14.wireOp",EDGE,"E7422"),sQuery(id+"F14.wireOp",EDGE,"E7423"),sQuery(id+"F14.wireOp",EDGE,"E7424"),sQuery(id+"F14.wireOp",EDGE,"E7425"),sQuery(id+"F14.wireOp",EDGE,"E7426"),sQuery(id+"F14.wireOp",EDGE,"E7427"),sQuery(id+"F14.wireOp",EDGE,"E7428"),sQuery(id+"F14.wireOp",EDGE,"E7429"),sQuery(id+"F14.wireOp",EDGE,"E7430"),sQuery(id+"F14.wireOp",EDGE,"E7431"),sQuery(id+"F14.wireOp",EDGE,"E7432"),sQuery(id+"F14.wireOp",EDGE,"E7433"),sQuery(id+"F14.wireOp",EDGE,"E7434"),sQuery(id+"F14.wireOp",EDGE,"E7435"),sQuery(id+"F14.wireOp",EDGE,"E7436"),sQuery(id+"F14.wireOp",EDGE,"E7437"),sQuery(id+"F14.wireOp",EDGE,"E7438"),sQuery(id+"F14.wireOp",EDGE,"E7439"),sQuery(id+"F14.wireOp",EDGE,"E7440"),sQuery(id+"F14.wireOp",EDGE,"E7441"),sQuery(id+"F14.wireOp",EDGE,"E7442"),sQuery(id+"F14.wireOp",EDGE,"E7443"),sQuery(id+"F14.wireOp",EDGE,"E7444"),sQuery(id+"F14.wireOp",EDGE,"E7445"),sQuery(id+"F14.wireOp",EDGE,"E7446"),sQuery(id+"F14.wireOp",EDGE,"E7447"),sQuery(id+"F14.wireOp",EDGE,"E7448"),sQuery(id+"F14.wireOp",EDGE,"E7449"),sQuery(id+"F14.wireOp",EDGE,"E7450"),sQuery(id+"F14.wireOp",EDGE,"E7451"),sQuery(id+"F14.wireOp",EDGE,"E7452"),sQuery(id+"F14.wireOp",EDGE,"E7453"),sQuery(id+"F14.wireOp",EDGE,"E7454"),sQuery(id+"F14.wireOp",EDGE,"E7455"),sQuery(id+"F14.wireOp",EDGE,"E7456"),sQuery(id+"F14.wireOp",EDGE,"E7457"),sQuery(id+"F14.wireOp",EDGE,"E7458"),sQuery(id+"F14.wireOp",EDGE,"E7459"),sQuery(id+"F14.wireOp",EDGE,"E7460"),sQuery(id+"F14.wireOp",EDGE,"E7461"),sQuery(id+"F14.wireOp",EDGE,"E7462"),sQuery(id+"F14.wireOp",EDGE,"E7463"),sQuery(id+"F14.wireOp",EDGE,"E7464"),sQuery(id+"F14.wireOp",EDGE,"E7465"),sQuery(id+"F14.wireOp",EDGE,"E7466"),sQuery(id+"F14.wireOp",EDGE,"E7467"),sQuery(id+"F14.wireOp",EDGE,"E7468"),sQuery(id+"F14.wireOp",EDGE,"E7469"),sQuery(id+"F14.wireOp",EDGE,"E7470"),sQuery(id+"F14.wireOp",EDGE,"E7471"),sQuery(id+"F14.wireOp",EDGE,"E7472"),sQuery(id+"F14.wireOp",EDGE,"E7473"),sQuery(id+"F14.wireOp",EDGE,"E7474"),sQuery(id+"F14.wireOp",EDGE,"E7475"),sQuery(id+"F14.wireOp",EDGE,"E7476"),sQuery(id+"F14.wireOp",EDGE,"E7477"),sQuery(id+"F14.wireOp",EDGE,"E7478"),sQuery(id+"F14.wireOp",EDGE,"E7479"),sQuery(id+"F14.wireOp",EDGE,"E7480"),sQuery(id+"F14.wireOp",EDGE,"E7481"),sQuery(id+"F14.wireOp",EDGE,"E7482"),sQuery(id+"F14.wireOp",EDGE,"E7483"),sQuery(id+"F14.wireOp",EDGE,"E7484"),sQuery(id+"F14.wireOp",EDGE,"E7485"),sQuery(id+"F14.wireOp",EDGE,"E7486"),sQuery(id+"F14.wireOp",EDGE,"E7487"),sQuery(id+"F14.wireOp",EDGE,"E7488"),sQuery(id+"F14.wireOp",EDGE,"E7489"),sQuery(id+"F14.wireOp",EDGE,"E7490"),sQuery(id+"F14.wireOp",EDGE,"E7491"),sQuery(id+"F14.wireOp",EDGE,"E7492"),sQuery(id+"F14.wireOp",EDGE,"E7493"),sQuery(id+"F14.wireOp",EDGE,"E7494"),sQuery(id+"F14.wireOp",EDGE,"E7495"),sQuery(id+"F14.wireOp",EDGE,"E7496"),sQuery(id+"F14.wireOp",EDGE,"E7497"),sQuery(id+"F14.wireOp",EDGE,"E7498"),sQuery(id+"F14.wireOp",EDGE,"E7499"),sQuery(id+"F14.wireOp",EDGE,"E7500"),sQuery(id+"F14.wireOp",EDGE,"E7501"),sQuery(id+"F14.wireOp",EDGE,"E7502"),sQuery(id+"F14.wireOp",EDGE,"E7503"),sQuery(id+"F14.wireOp",EDGE,"E7504"),sQuery(id+"F14.wireOp",EDGE,"E7505"),sQuery(id+"F14.wireOp",EDGE,"E7506"),sQuery(id+"F14.wireOp",EDGE,"E7507"),sQuery(id+"F14.wireOp",EDGE,"E7508"),sQuery(id+"F14.wireOp",EDGE,"E7509"),sQuery(id+"F14.wireOp",EDGE,"E7510"),sQuery(id+"F14.wireOp",EDGE,"E7511"),sQuery(id+"F14.wireOp",EDGE,"E7512"),sQuery(id+"F14.wireOp",EDGE,"E7513"),sQuery(id+"F14.wireOp",EDGE,"E7514"),sQuery(id+"F14.wireOp",EDGE,"E7515"),sQuery(id+"F14.wireOp",EDGE,"E7516"),sQuery(id+"F14.wireOp",EDGE,"E7517"),sQuery(id+"F14.wireOp",EDGE,"E7518"),sQuery(id+"F14.wireOp",EDGE,"E7519"),sQuery(id+"F14.wireOp",EDGE,"E7520"),sQuery(id+"F14.wireOp",EDGE,"E7521"),sQuery(id+"F14.wireOp",EDGE,"E7522"),sQuery(id+"F14.wireOp",EDGE,"E7523"),sQuery(id+"F14.wireOp",EDGE,"E7524"),sQuery(id+"F14.wireOp",EDGE,"E7525"),sQuery(id+"F14.wireOp",EDGE,"E7526"),sQuery(id+"F14.wireOp",EDGE,"E7527"),sQuery(id+"F14.wireOp",EDGE,"E7528"),sQuery(id+"F14.wireOp",EDGE,"E7529"),sQuery(id+"F14.wireOp",EDGE,"E7530"),sQuery(id+"F14.wireOp",EDGE,"E7531"),sQuery(id+"F14.wireOp",EDGE,"E7532"),sQuery(id+"F14.wireOp",EDGE,"E7533"),sQuery(id+"F14.wireOp",EDGE,"E7534"),sQuery(id+"F14.wireOp",EDGE,"E7535"),sQuery(id+"F14.wireOp",EDGE,"E7536"),sQuery(id+"F14.wireOp",EDGE,"E7537"),sQuery(id+"F14.wireOp",EDGE,"E7538"),sQuery(id+"F14.wireOp",EDGE,"E7539"),sQuery(id+"F14.wireOp",EDGE,"E7540"),sQuery(id+"F14.wireOp",EDGE,"E7541"),sQuery(id+"F14.wireOp",EDGE,"E7542"),sQuery(id+"F14.wireOp",EDGE,"E7543"),sQuery(id+"F14.wireOp",EDGE,"E7544"),sQuery(id+"F14.wireOp",EDGE,"E7545"),sQuery(id+"F14.wireOp",EDGE,"E7546"),sQuery(id+"F14.wireOp",EDGE,"E7547"),sQuery(id+"F14.wireOp",EDGE,"E7548"),sQuery(id+"F14.wireOp",EDGE,"E7549"),sQuery(id+"F14.wireOp",EDGE,"E7550"),sQuery(id+"F14.wireOp",EDGE,"E7551"),sQuery(id+"F14.wireOp",EDGE,"E7552"),sQuery(id+"F14.wireOp",EDGE,"E7553"),sQuery(id+"F14.wireOp",EDGE,"E7554"),sQuery(id+"F14.wireOp",EDGE,"E7555"),sQuery(id+"F14.wireOp",EDGE,"E7556"),sQuery(id+"F14.wireOp",EDGE,"E7557"),sQuery(id+"F14.wireOp",EDGE,"E7558"),sQuery(id+"F14.wireOp",EDGE,"E7559"),sQuery(id+"F14.wireOp",EDGE,"E7560"),sQuery(id+"F14.wireOp",EDGE,"E7561"),sQuery(id+"F14.wireOp",EDGE,"E7562"),sQuery(id+"F14.wireOp",EDGE,"E7563"),sQuery(id+"F14.wireOp",EDGE,"E7564"),sQuery(id+"F14.wireOp",EDGE,"E7565"),sQuery(id+"F14.wireOp",EDGE,"E7566"),sQuery(id+"F14.wireOp",EDGE,"E7567"),sQuery(id+"F14.wireOp",EDGE,"E7568"),sQuery(id+"F14.wireOp",EDGE,"E7569"),sQuery(id+"F14.wireOp",EDGE,"E7570"),sQuery(id+"F14.wireOp",EDGE,"E7571"),sQuery(id+"F14.wireOp",EDGE,"E7572"),sQuery(id+"F14.wireOp",EDGE,"E7573"),sQuery(id+"F14.wireOp",EDGE,"E7574"),sQuery(id+"F14.wireOp",EDGE,"E7575"),sQuery(id+"F14.wireOp",EDGE,"E7576"),sQuery(id+"F14.wireOp",EDGE,"E7577"),sQuery(id+"F14.wireOp",EDGE,"E7578"),sQuery(id+"F14.wireOp",EDGE,"E7579"),sQuery(id+"F14.wireOp",EDGE,"E7580"),sQuery(id+"F14.wireOp",EDGE,"E7581"),sQuery(id+"F14.wireOp",EDGE,"E7582"),sQuery(id+"F14.wireOp",EDGE,"E7583"),sQuery(id+"F14.wireOp",EDGE,"E7584"),sQuery(id+"F14.wireOp",EDGE,"E7585"),sQuery(id+"F14.wireOp",EDGE,"E7586"),sQuery(id+"F14.wireOp",EDGE,"E7587"),sQuery(id+"F14.wireOp",EDGE,"E7588"),sQuery(id+"F14.wireOp",EDGE,"E7589"),sQuery(id+"F14.wireOp",EDGE,"E7590"),sQuery(id+"F14.wireOp",EDGE,"E7591"),sQuery(id+"F14.wireOp",EDGE,"E7592"),sQuery(id+"F14.wireOp",EDGE,"E7593"),sQuery(id+"F14.wireOp",EDGE,"E7594"),sQuery(id+"F14.wireOp",EDGE,"E7595"),sQuery(id+"F14.wireOp",EDGE,"E7596"),sQuery(id+"F14.wireOp",EDGE,"E7597"),sQuery(id+"F14.wireOp",EDGE,"E7598"),sQuery(id+"F14.wireOp",EDGE,"E7599"),sQuery(id+"F14.wireOp",EDGE,"E7600"),sQuery(id+"F14.wireOp",EDGE,"E7601"),sQuery(id+"F14.wireOp",EDGE,"E7602"),sQuery(id+"F14.wireOp",EDGE,"E7603"),sQuery(id+"F14.wireOp",EDGE,"E7604"),sQuery(id+"F14.wireOp",EDGE,"E7605"),sQuery(id+"F14.wireOp",EDGE,"E7606"),sQuery(id+"F14.wireOp",EDGE,"E7607"),sQuery(id+"F14.wireOp",EDGE,"E7608"),sQuery(id+"F14.wireOp",EDGE,"E7609"),sQuery(id+"F14.wireOp",EDGE,"E7610"),sQuery(id+"F14.wireOp",EDGE,"E7611"),sQuery(id+"F14.wireOp",EDGE,"E7612"),sQuery(id+"F14.wireOp",EDGE,"E7613"),sQuery(id+"F14.wireOp",EDGE,"E7614"),sQuery(id+"F14.wireOp",EDGE,"E7615"),sQuery(id+"F14.wireOp",EDGE,"E7616"),sQuery(id+"F14.wireOp",EDGE,"E7617"),sQuery(id+"F14.wireOp",EDGE,"E7618"),sQuery(id+"F14.wireOp",EDGE,"E7619"),sQuery(id+"F14.wireOp",EDGE,"E7620"),sQuery(id+"F14.wireOp",EDGE,"E7621"),sQuery(id+"F14.wireOp",EDGE,"E7622"),sQuery(id+"F14.wireOp",EDGE,"E7623"),sQuery(id+"F14.wireOp",EDGE,"E7624"),sQuery(id+"F14.wireOp",EDGE,"E7625"),sQuery(id+"F14.wireOp",EDGE,"E7626"),sQuery(id+"F14.wireOp",EDGE,"E7627"),sQuery(id+"F14.wireOp",EDGE,"E7628"),sQuery(id+"F14.wireOp",EDGE,"E7629"),sQuery(id+"F14.wireOp",EDGE,"E7630"),sQuery(id+"F14.wireOp",EDGE,"E7631"),sQuery(id+"F14.wireOp",EDGE,"E7632"),sQuery(id+"F14.wireOp",EDGE,"E7633"),sQuery(id+"F14.wireOp",EDGE,"E7634"),sQuery(id+"F14.wireOp",EDGE,"E7635"),sQuery(id+"F14.wireOp",EDGE,"E7636"),sQuery(id+"F14.wireOp",EDGE,"E7637"),sQuery(id+"F14.wireOp",EDGE,"E7638"),sQuery(id+"F14.wireOp",EDGE,"E7639"),sQuery(id+"F14.wireOp",EDGE,"E7640"),sQuery(id+"F14.wireOp",EDGE,"E7641"),sQuery(id+"F14.wireOp",EDGE,"E7642"),sQuery(id+"F14.wireOp",EDGE,"E7643"),sQuery(id+"F14.wireOp",EDGE,"E7644"),sQuery(id+"F14.wireOp",EDGE,"E7645"),sQuery(id+"F14.wireOp",EDGE,"E7646"),sQuery(id+"F14.wireOp",EDGE,"E7647"),sQuery(id+"F14.wireOp",EDGE,"E7648"),sQuery(id+"F14.wireOp",EDGE,"E7649"),sQuery(id+"F14.wireOp",EDGE,"E7650"),sQuery(id+"F14.wireOp",EDGE,"E7651"),sQuery(id+"F14.wireOp",EDGE,"E7652"),sQuery(id+"F14.wireOp",EDGE,"E7653"),sQuery(id+"F14.wireOp",EDGE,"E7654"),sQuery(id+"F14.wireOp",EDGE,"E7655"),sQuery(id+"F14.wireOp",EDGE,"E7656"),sQuery(id+"F14.wireOp",EDGE,"E7657"),sQuery(id+"F14.wireOp",EDGE,"E7658"),sQuery(id+"F14.wireOp",EDGE,"E7659"),sQuery(id+"F14.wireOp",EDGE,"E7660"),sQuery(id+"F14.wireOp",EDGE,"E7661"),sQuery(id+"F14.wireOp",EDGE,"E7662"),sQuery(id+"F14.wireOp",EDGE,"E7663"),sQuery(id+"F14.wireOp",EDGE,"E7664"),sQuery(id+"F14.wireOp",EDGE,"E7665"),sQuery(id+"F14.wireOp",EDGE,"E7666"),sQuery(id+"F14.wireOp",EDGE,"E7667"),sQuery(id+"F14.wireOp",EDGE,"E7668"),sQuery(id+"F14.wireOp",EDGE,"E7669"),sQuery(id+"F14.wireOp",EDGE,"E7670"),sQuery(id+"F14.wireOp",EDGE,"E7671"),sQuery(id+"F14.wireOp",EDGE,"E7672"),sQuery(id+"F14.wireOp",EDGE,"E7673"),sQuery(id+"F14.wireOp",EDGE,"E7674"),sQuery(id+"F14.wireOp",EDGE,"E7675"),sQuery(id+"F14.wireOp",EDGE,"E7676"),sQuery(id+"F14.wireOp",EDGE,"E7677"),sQuery(id+"F14.wireOp",EDGE,"E7678"),sQuery(id+"F14.wireOp",EDGE,"E7679"),sQuery(id+"F14.wireOp",EDGE,"E7680"),sQuery(id+"F14.wireOp",EDGE,"E7681"),sQuery(id+"F14.wireOp",EDGE,"E7682"),sQuery(id+"F14.wireOp",EDGE,"E7683"),sQuery(id+"F14.wireOp",EDGE,"E7684"),sQuery(id+"F14.wireOp",EDGE,"E7685"),sQuery(id+"F14.wireOp",EDGE,"E7686"),sQuery(id+"F14.wireOp",EDGE,"E7687"),sQuery(id+"F14.wireOp",EDGE,"E7688"),sQuery(id+"F14.wireOp",EDGE,"E7689"),sQuery(id+"F14.wireOp",EDGE,"E7690"),sQuery(id+"F14.wireOp",EDGE,"E7691"),sQuery(id+"F14.wireOp",EDGE,"E7692"),sQuery(id+"F14.wireOp",EDGE,"E7693"),sQuery(id+"F14.wireOp",EDGE,"E7694"),sQuery(id+"F14.wireOp",EDGE,"E7695"),sQuery(id+"F14.wireOp",EDGE,"E7696"),sQuery(id+"F14.wireOp",EDGE,"E7697"),sQuery(id+"F14.wireOp",EDGE,"E7698"),sQuery(id+"F14.wireOp",EDGE,"E7699"),sQuery(id+"F14.wireOp",EDGE,"E7700"),sQuery(id+"F14.wireOp",EDGE,"E7701"),sQuery(id+"F14.wireOp",EDGE,"E7702"),sQuery(id+"F14.wireOp",EDGE,"E7703"),sQuery(id+"F14.wireOp",EDGE,"E7704"),sQuery(id+"F14.wireOp",EDGE,"E7705"),sQuery(id+"F14.wireOp",EDGE,"E7706"),sQuery(id+"F14.wireOp",EDGE,"E7707"),sQuery(id+"F14.wireOp",EDGE,"E7708"),sQuery(id+"F14.wireOp",EDGE,"E7709"),sQuery(id+"F14.wireOp",EDGE,"E7710"),sQuery(id+"F14.wireOp",EDGE,"E7711"),sQuery(id+"F14.wireOp",EDGE,"E7712"),sQuery(id+"F14.wireOp",EDGE,"E7713"),sQuery(id+"F14.wireOp",EDGE,"E7714"),sQuery(id+"F14.wireOp",EDGE,"E7715"),sQuery(id+"F14.wireOp",EDGE,"E7716"),sQuery(id+"F14.wireOp",EDGE,"E7717"),sQuery(id+"F14.wireOp",EDGE,"E7718"),sQuery(id+"F14.wireOp",EDGE,"E7719"),sQuery(id+"F14.wireOp",EDGE,"E7720"),sQuery(id+"F14.wireOp",EDGE,"E7721"),sQuery(id+"F14.wireOp",EDGE,"E7722"),sQuery(id+"F14.wireOp",EDGE,"E7723"),sQuery(id+"F14.wireOp",EDGE,"E7724"),sQuery(id+"F14.wireOp",EDGE,"E7725"),sQuery(id+"F14.wireOp",EDGE,"E7726"),sQuery(id+"F14.wireOp",EDGE,"E7727"),sQuery(id+"F14.wireOp",EDGE,"E7728"),sQuery(id+"F14.wireOp",EDGE,"E7729"),sQuery(id+"F14.wireOp",EDGE,"E7730"),sQuery(id+"F14.wireOp",EDGE,"E7731"),sQuery(id+"F14.wireOp",EDGE,"E7732"),sQuery(id+"F14.wireOp",EDGE,"E7733"),sQuery(id+"F14.wireOp",EDGE,"E7734"),sQuery(id+"F14.wireOp",EDGE,"E7735"),sQuery(id+"F14.wireOp",EDGE,"E7736"),sQuery(id+"F14.wireOp",EDGE,"E7737"),sQuery(id+"F14.wireOp",EDGE,"E7738"),sQuery(id+"F14.wireOp",EDGE,"E7739"),sQuery(id+"F14.wireOp",EDGE,"E7740"),sQuery(id+"F14.wireOp",EDGE,"E7741"),sQuery(id+"F14.wireOp",EDGE,"E7742"),sQuery(id+"F14.wireOp",EDGE,"E7743"),sQuery(id+"F14.wireOp",EDGE,"E7744"),sQuery(id+"F14.wireOp",EDGE,"E7745"),sQuery(id+"F14.wireOp",EDGE,"E7746"),sQuery(id+"F14.wireOp",EDGE,"E7747"),sQuery(id+"F14.wireOp",EDGE,"E7748"),sQuery(id+"F14.wireOp",EDGE,"E7749"),sQuery(id+"F14.wireOp",EDGE,"E7750"),sQuery(id+"F14.wireOp",EDGE,"E7751"),sQuery(id+"F14.wireOp",EDGE,"E7752"),sQuery(id+"F14.wireOp",EDGE,"E7753"),sQuery(id+"F14.wireOp",EDGE,"E7754"),sQuery(id+"F14.wireOp",EDGE,"E7755"),sQuery(id+"F14.wireOp",EDGE,"E7756"),sQuery(id+"F14.wireOp",EDGE,"E7757"),sQuery(id+"F14.wireOp",EDGE,"E7758"),sQuery(id+"F14.wireOp",EDGE,"E7759"),sQuery(id+"F14.wireOp",EDGE,"E7760"),sQuery(id+"F14.wireOp",EDGE,"E7761"),sQuery(id+"F14.wireOp",EDGE,"E7762"),sQuery(id+"F14.wireOp",EDGE,"E7763"),sQuery(id+"F14.wireOp",EDGE,"E7764"),sQuery(id+"F14.wireOp",EDGE,"E7765"),sQuery(id+"F14.wireOp",EDGE,"E7766"),sQuery(id+"F14.wireOp",EDGE,"E7767"),sQuery(id+"F14.wireOp",EDGE,"E7768"),sQuery(id+"F14.wireOp",EDGE,"E7769"),sQuery(id+"F14.wireOp",EDGE,"E7770"),sQuery(id+"F14.wireOp",EDGE,"E7771"),sQuery(id+"F14.wireOp",EDGE,"E7772"),sQuery(id+"F14.wireOp",EDGE,"E7773"),sQuery(id+"F14.wireOp",EDGE,"E7774"),sQuery(id+"F14.wireOp",EDGE,"E7775"),sQuery(id+"F14.wireOp",EDGE,"E7776"),sQuery(id+"F14.wireOp",EDGE,"E7777"),sQuery(id+"F14.wireOp",EDGE,"E7778"),sQuery(id+"F14.wireOp",EDGE,"E7779"),sQuery(id+"F14.wireOp",EDGE,"E7780"),sQuery(id+"F14.wireOp",EDGE,"E7781"),sQuery(id+"F14.wireOp",EDGE,"E7782"),sQuery(id+"F14.wireOp",EDGE,"E7783"),sQuery(id+"F14.wireOp",EDGE,"E7784"),sQuery(id+"F14.wireOp",EDGE,"E7785"),sQuery(id+"F14.wireOp",EDGE,"E7786"),sQuery(id+"F14.wireOp",EDGE,"E7787"),sQuery(id+"F14.wireOp",EDGE,"E7788"),sQuery(id+"F14.wireOp",EDGE,"E7789"),sQuery(id+"F14.wireOp",EDGE,"E7790"),sQuery(id+"F14.wireOp",EDGE,"E7791"),sQuery(id+"F14.wireOp",EDGE,"E7792"),sQuery(id+"F14.wireOp",EDGE,"E7793"),sQuery(id+"F14.wireOp",EDGE,"E7794"),sQuery(id+"F14.wireOp",EDGE,"E7795"),sQuery(id+"F14.wireOp",EDGE,"E7796"),sQuery(id+"F14.wireOp",EDGE,"E7797"),sQuery(id+"F14.wireOp",EDGE,"E7798"),sQuery(id+"F14.wireOp",EDGE,"E7799"),sQuery(id+"F14.wireOp",EDGE,"E7800"),sQuery(id+"F14.wireOp",EDGE,"E7801"),sQuery(id+"F14.wireOp",EDGE,"E7802"),sQuery(id+"F14.wireOp",EDGE,"E7803"),sQuery(id+"F14.wireOp",EDGE,"E7804"),sQuery(id+"F14.wireOp",EDGE,"E7805"),sQuery(id+"F14.wireOp",EDGE,"E7806"),sQuery(id+"F14.wireOp",EDGE,"E7807"),sQuery(id+"F14.wireOp",EDGE,"E7808"),sQuery(id+"F14.wireOp",EDGE,"E7809"),sQuery(id+"F14.wireOp",EDGE,"E7810"),sQuery(id+"F14.wireOp",EDGE,"E7811"),sQuery(id+"F14.wireOp",EDGE,"E7812"),sQuery(id+"F14.wireOp",EDGE,"E7813"),sQuery(id+"F14.wireOp",EDGE,"E7814"),sQuery(id+"F14.wireOp",EDGE,"E7815"),sQuery(id+"F14.wireOp",EDGE,"E7816"),sQuery(id+"F14.wireOp",EDGE,"E7817"),sQuery(id+"F14.wireOp",EDGE,"E7818"),sQuery(id+"F14.wireOp",EDGE,"E7819"),sQuery(id+"F14.wireOp",EDGE,"E7820"),sQuery(id+"F14.wireOp",EDGE,"E7821"),sQuery(id+"F14.wireOp",EDGE,"E7822"),sQuery(id+"F14.wireOp",EDGE,"E7823"),sQuery(id+"F14.wireOp",EDGE,"E7824"),sQuery(id+"F14.wireOp",EDGE,"E7825"),sQuery(id+"F14.wireOp",EDGE,"E7826"),sQuery(id+"F14.wireOp",EDGE,"E7827"),sQuery(id+"F14.wireOp",EDGE,"E7828"),sQuery(id+"F14.wireOp",EDGE,"E7829"),sQuery(id+"F14.wireOp",EDGE,"E7830"),sQuery(id+"F14.wireOp",EDGE,"E7831"),sQuery(id+"F14.wireOp",EDGE,"E7832"),sQuery(id+"F14.wireOp",EDGE,"E7833"),sQuery(id+"F14.wireOp",EDGE,"E7834"),sQuery(id+"F14.wireOp",EDGE,"E7835"),sQuery(id+"F14.wireOp",EDGE,"E7836"),sQuery(id+"F14.wireOp",EDGE,"E7837"),sQuery(id+"F14.wireOp",EDGE,"E7838"),sQuery(id+"F14.wireOp",EDGE,"E7839"),sQuery(id+"F14.wireOp",EDGE,"E7840"),sQuery(id+"F14.wireOp",EDGE,"E7841"),sQuery(id+"F14.wireOp",EDGE,"E7842"),sQuery(id+"F14.wireOp",EDGE,"E7843"),sQuery(id+"F14.wireOp",EDGE,"E7844"),sQuery(id+"F14.wireOp",EDGE,"E7845"),sQuery(id+"F14.wireOp",EDGE,"E7846"),sQuery(id+"F14.wireOp",EDGE,"E7847"),sQuery(id+"F14.wireOp",EDGE,"E7848"),sQuery(id+"F14.wireOp",EDGE,"E7849"),sQuery(id+"F14.wireOp",EDGE,"E7850"),sQuery(id+"F14.wireOp",EDGE,"E7851"),sQuery(id+"F14.wireOp",EDGE,"E7852"),sQuery(id+"F14.wireOp",EDGE,"E7853"),sQuery(id+"F14.wireOp",EDGE,"E7854"),sQuery(id+"F14.wireOp",EDGE,"E7855"),sQuery(id+"F14.wireOp",EDGE,"E7856"),sQuery(id+"F14.wireOp",EDGE,"E7857"),sQuery(id+"F14.wireOp",EDGE,"E7858"),sQuery(id+"F14.wireOp",EDGE,"E7859"),sQuery(id+"F14.wireOp",EDGE,"E7860"),sQuery(id+"F14.wireOp",EDGE,"E7861"),sQuery(id+"F14.wireOp",EDGE,"E7862"),sQuery(id+"F14.wireOp",EDGE,"E7863"),sQuery(id+"F14.wireOp",EDGE,"E7864"),sQuery(id+"F14.wireOp",EDGE,"E7865"),sQuery(id+"F14.wireOp",EDGE,"E7866"),sQuery(id+"F14.wireOp",EDGE,"E7867"),sQuery(id+"F14.wireOp",EDGE,"E7868"),sQuery(id+"F14.wireOp",EDGE,"E7869"),sQuery(id+"F14.wireOp",EDGE,"E7870"),sQuery(id+"F14.wireOp",EDGE,"E7871"),sQuery(id+"F14.wireOp",EDGE,"E7872"),sQuery(id+"F14.wireOp",EDGE,"E7873"),sQuery(id+"F14.wireOp",EDGE,"E7874"),sQuery(id+"F14.wireOp",EDGE,"E7875"),sQuery(id+"F14.wireOp",EDGE,"E7876"),sQuery(id+"F14.wireOp",EDGE,"E7877"),sQuery(id+"F14.wireOp",EDGE,"E7878"),sQuery(id+"F14.wireOp",EDGE,"E7879"),sQuery(id+"F14.wireOp",EDGE,"E7880"),sQuery(id+"F14.wireOp",EDGE,"E7881"),sQuery(id+"F14.wireOp",EDGE,"E7882"),sQuery(id+"F14.wireOp",EDGE,"E7883"),sQuery(id+"F14.wireOp",EDGE,"E7884"),sQuery(id+"F14.wireOp",EDGE,"E7885"),sQuery(id+"F14.wireOp",EDGE,"E7886"),sQuery(id+"F14.wireOp",EDGE,"E7887"),sQuery(id+"F14.wireOp",EDGE,"E7888"),sQuery(id+"F14.wireOp",EDGE,"E7889"),sQuery(id+"F14.wireOp",EDGE,"E7890"),sQuery(id+"F14.wireOp",EDGE,"E7891"),sQuery(id+"F14.wireOp",EDGE,"E7892"),sQuery(id+"F14.wireOp",EDGE,"E7893"),sQuery(id+"F14.wireOp",EDGE,"E7894"),sQuery(id+"F14.wireOp",EDGE,"E7895"),sQuery(id+"F14.wireOp",EDGE,"E7896"),sQuery(id+"F14.wireOp",EDGE,"E7897"),sQuery(id+"F14.wireOp",EDGE,"E7898"),sQuery(id+"F14.wireOp",EDGE,"E7899"),sQuery(id+"F14.wireOp",EDGE,"E7900"),sQuery(id+"F14.wireOp",EDGE,"E7901"),sQuery(id+"F14.wireOp",EDGE,"E7902"),sQuery(id+"F14.wireOp",EDGE,"E7903"),sQuery(id+"F14.wireOp",EDGE,"E7904"),sQuery(id+"F14.wireOp",EDGE,"E7905"),sQuery(id+"F14.wireOp",EDGE,"E7906"),sQuery(id+"F14.wireOp",EDGE,"E7907"),sQuery(id+"F14.wireOp",EDGE,"E7908"),sQuery(id+"F14.wireOp",EDGE,"E7909"),sQuery(id+"F14.wireOp",EDGE,"E7910"),sQuery(id+"F14.wireOp",EDGE,"E7911"),sQuery(id+"F14.wireOp",EDGE,"E7912"),sQuery(id+"F14.wireOp",EDGE,"E7913"),sQuery(id+"F14.wireOp",EDGE,"E7914"),sQuery(id+"F14.wireOp",EDGE,"E7915"),sQuery(id+"F14.wireOp",EDGE,"E7916"),sQuery(id+"F14.wireOp",EDGE,"E7917"),sQuery(id+"F14.wireOp",EDGE,"E7918"),sQuery(id+"F14.wireOp",EDGE,"E7919"),sQuery(id+"F14.wireOp",EDGE,"E7920"),sQuery(id+"F14.wireOp",EDGE,"E7921"),sQuery(id+"F14.wireOp",EDGE,"E7922"),sQuery(id+"F14.wireOp",EDGE,"E7923"),sQuery(id+"F14.wireOp",EDGE,"E7924"),sQuery(id+"F14.wireOp",EDGE,"E7925"),sQuery(id+"F14.wireOp",EDGE,"E7926"),sQuery(id+"F14.wireOp",EDGE,"E7927"),sQuery(id+"F14.wireOp",EDGE,"E7928"),sQuery(id+"F14.wireOp",EDGE,"E7929"),sQuery(id+"F14.wireOp",EDGE,"E7930"),sQuery(id+"F14.wireOp",EDGE,"E7931"),sQuery(id+"F14.wireOp",EDGE,"E7932"),sQuery(id+"F14.wireOp",EDGE,"E7933"),sQuery(id+"F14.wireOp",EDGE,"E7934"),sQuery(id+"F14.wireOp",EDGE,"E7935"),sQuery(id+"F14.wireOp",EDGE,"E7936"),sQuery(id+"F14.wireOp",EDGE,"E7937"),sQuery(id+"F14.wireOp",EDGE,"E7938"),sQuery(id+"F14.wireOp",EDGE,"E7939"),sQuery(id+"F14.wireOp",EDGE,"E7940"),sQuery(id+"F14.wireOp",EDGE,"E7941"),sQuery(id+"F14.wireOp",EDGE,"E7942"),sQuery(id+"F14.wireOp",EDGE,"E7943"),sQuery(id+"F14.wireOp",EDGE,"E7944"),sQuery(id+"F14.wireOp",EDGE,"E7945"),sQuery(id+"F14.wireOp",EDGE,"E7946"),sQuery(id+"F14.wireOp",EDGE,"E7947"),sQuery(id+"F14.wireOp",EDGE,"E7948"),sQuery(id+"F14.wireOp",EDGE,"E7949"),sQuery(id+"F14.wireOp",EDGE,"E7950"),sQuery(id+"F14.wireOp",EDGE,"E7951"),sQuery(id+"F14.wireOp",EDGE,"E7952"),sQuery(id+"F14.wireOp",EDGE,"E7953"),sQuery(id+"F14.wireOp",EDGE,"E7954"),sQuery(id+"F14.wireOp",EDGE,"E7955"),sQuery(id+"F14.wireOp",EDGE,"E7956"),sQuery(id+"F14.wireOp",EDGE,"E7957"),sQuery(id+"F14.wireOp",EDGE,"E7958"),sQuery(id+"F14.wireOp",EDGE,"E7959"),sQuery(id+"F14.wireOp",EDGE,"E7960"),sQuery(id+"F14.wireOp",EDGE,"E7961"),sQuery(id+"F14.wireOp",EDGE,"E7962"),sQuery(id+"F14.wireOp",EDGE,"E7963"),sQuery(id+"F14.wireOp",EDGE,"E7964"),sQuery(id+"F14.wireOp",EDGE,"E7965"),sQuery(id+"F14.wireOp",EDGE,"E7966"),sQuery(id+"F14.wireOp",EDGE,"E7967"),sQuery(id+"F14.wireOp",EDGE,"E7968"),sQuery(id+"F14.wireOp",EDGE,"E7969"),sQuery(id+"F14.wireOp",EDGE,"E7970"),sQuery(id+"F14.wireOp",EDGE,"E7971"),sQuery(id+"F14.wireOp",EDGE,"E7972"),sQuery(id+"F14.wireOp",EDGE,"E7973"),sQuery(id+"F14.wireOp",EDGE,"E7974"),sQuery(id+"F14.wireOp",EDGE,"E7975"),sQuery(id+"F14.wireOp",EDGE,"E7976"),sQuery(id+"F14.wireOp",EDGE,"E7977"),sQuery(id+"F14.wireOp",EDGE,"E7978"),sQuery(id+"F14.wireOp",EDGE,"E7979"),sQuery(id+"F14.wireOp",EDGE,"E7980"),sQuery(id+"F14.wireOp",EDGE,"E7981"),sQuery(id+"F14.wireOp",EDGE,"E7982"),sQuery(id+"F14.wireOp",EDGE,"E7983"),sQuery(id+"F14.wireOp",EDGE,"E7984"),sQuery(id+"F14.wireOp",EDGE,"E7985"),sQuery(id+"F14.wireOp",EDGE,"E7986"),sQuery(id+"F14.wireOp",EDGE,"E7987"),sQuery(id+"F14.wireOp",EDGE,"E7988"),sQuery(id+"F14.wireOp",EDGE,"E7989"),sQuery(id+"F14.wireOp",EDGE,"E7990"),sQuery(id+"F14.wireOp",EDGE,"E7991"),sQuery(id+"F14.wireOp",EDGE,"E7992"),sQuery(id+"F14.wireOp",EDGE,"E7993"),sQuery(id+"F14.wireOp",EDGE,"E7994"),sQuery(id+"F14.wireOp",EDGE,"E7995"),sQuery(id+"F14.wireOp",EDGE,"E7996"),sQuery(id+"F14.wireOp",EDGE,"E7997"),sQuery(id+"F14.wireOp",EDGE,"E7998"),sQuery(id+"F14.wireOp",EDGE,"E7999"),sQuery(id+"F14.wireOp",EDGE,"E8000"),sQuery(id+"F14.wireOp",EDGE,"E8001"),sQuery(id+"F14.wireOp",EDGE,"E8002"),sQuery(id+"F14.wireOp",EDGE,"E8003"),sQuery(id+"F14.wireOp",EDGE,"E8004"),sQuery(id+"F14.wireOp",EDGE,"E8005"),sQuery(id+"F14.wireOp",EDGE,"E8006"),sQuery(id+"F14.wireOp",EDGE,"E8007"),sQuery(id+"F14.wireOp",EDGE,"E8008"),sQuery(id+"F14.wireOp",EDGE,"E8009"),sQuery(id+"F14.wireOp",EDGE,"E8010"),sQuery(id+"F14.wireOp",EDGE,"E8011"),sQuery(id+"F14.wireOp",EDGE,"E8012"),sQuery(id+"F14.wireOp",EDGE,"E8013"),sQuery(id+"F14.wireOp",EDGE,"E8014"),sQuery(id+"F14.wireOp",EDGE,"E8015"),sQuery(id+"F14.wireOp",EDGE,"E8016"),sQuery(id+"F14.wireOp",EDGE,"E8017"),sQuery(id+"F14.wireOp",EDGE,"E8018"),sQuery(id+"F14.wireOp",EDGE,"E8019"),sQuery(id+"F14.wireOp",EDGE,"E8020"),sQuery(id+"F14.wireOp",EDGE,"E8021"),sQuery(id+"F14.wireOp",EDGE,"E8022"),sQuery(id+"F14.wireOp",EDGE,"E8023"),sQuery(id+"F14.wireOp",EDGE,"E8024"),sQuery(id+"F14.wireOp",EDGE,"E8025"),sQuery(id+"F14.wireOp",EDGE,"E8026"),sQuery(id+"F14.wireOp",EDGE,"E8027"),sQuery(id+"F14.wireOp",EDGE,"E8028"),sQuery(id+"F14.wireOp",EDGE,"E8029"),sQuery(id+"F14.wireOp",EDGE,"E8030"),sQuery(id+"F14.wireOp",EDGE,"E8031"),sQuery(id+"F14.wireOp",EDGE,"E8032"),sQuery(id+"F14.wireOp",EDGE,"E8033"),sQuery(id+"F14.wireOp",EDGE,"E8034"),sQuery(id+"F14.wireOp",EDGE,"E8035"),sQuery(id+"F14.wireOp",EDGE,"E8036"),sQuery(id+"F14.wireOp",EDGE,"E8037"),sQuery(id+"F14.wireOp",EDGE,"E8038"),sQuery(id+"F14.wireOp",EDGE,"E8039"),sQuery(id+"F14.wireOp",EDGE,"E8040"),sQuery(id+"F14.wireOp",EDGE,"E8041"),sQuery(id+"F14.wireOp",EDGE,"E8042"),sQuery(id+"F14.wireOp",EDGE,"E8043"),sQuery(id+"F14.wireOp",EDGE,"E8044"),sQuery(id+"F14.wireOp",EDGE,"E8045"),sQuery(id+"F14.wireOp",EDGE,"E8046"),sQuery(id+"F14.wireOp",EDGE,"E8047"),sQuery(id+"F14.wireOp",EDGE,"E8048"),sQuery(id+"F14.wireOp",EDGE,"E8049"),sQuery(id+"F14.wireOp",EDGE,"E8050"),sQuery(id+"F14.wireOp",EDGE,"E8051"),sQuery(id+"F14.wireOp",EDGE,"E8052"),sQuery(id+"F14.wireOp",EDGE,"E8053"),sQuery(id+"F14.wireOp",EDGE,"E8054"),sQuery(id+"F14.wireOp",EDGE,"E8055"),sQuery(id+"F14.wireOp",EDGE,"E8056"),sQuery(id+"F14.wireOp",EDGE,"E8057"),sQuery(id+"F14.wireOp",EDGE,"E8058"),sQuery(id+"F14.wireOp",EDGE,"E8059"),sQuery(id+"F14.wireOp",EDGE,"E8060"),sQuery(id+"F14.wireOp",EDGE,"E8061"),sQuery(id+"F14.wireOp",EDGE,"E8062"),sQuery(id+"F14.wireOp",EDGE,"E8063"),sQuery(id+"F14.wireOp",EDGE,"E8064"),sQuery(id+"F14.wireOp",EDGE,"E8065"),sQuery(id+"F14.wireOp",EDGE,"E8066"),sQuery(id+"F14.wireOp",EDGE,"E8067"),sQuery(id+"F14.wireOp",EDGE,"E8068"),sQuery(id+"F14.wireOp",EDGE,"E8069"),sQuery(id+"F14.wireOp",EDGE,"E8070"),sQuery(id+"F14.wireOp",EDGE,"E8071"),sQuery(id+"F14.wireOp",EDGE,"E8072"),sQuery(id+"F14.wireOp",EDGE,"E8073"),sQuery(id+"F14.wireOp",EDGE,"E8074"),sQuery(id+"F14.wireOp",EDGE,"E8075"),sQuery(id+"F14.wireOp",EDGE,"E8076"),sQuery(id+"F14.wireOp",EDGE,"E8077"),sQuery(id+"F14.wireOp",EDGE,"E8078"),sQuery(id+"F14.wireOp",EDGE,"E8079"),sQuery(id+"F14.wireOp",EDGE,"E8080"),sQuery(id+"F14.wireOp",EDGE,"E8081"),sQuery(id+"F14.wireOp",EDGE,"E8082"),sQuery(id+"F14.wireOp",EDGE,"E8083"),sQuery(id+"F14.wireOp",EDGE,"E8084"),sQuery(id+"F14.wireOp",EDGE,"E8085"),sQuery(id+"F14.wireOp",EDGE,"E8086"),sQuery(id+"F14.wireOp",EDGE,"E8087"),sQuery(id+"F14.wireOp",EDGE,"E8088"),sQuery(id+"F14.wireOp",EDGE,"E8089"),sQuery(id+"F14.wireOp",EDGE,"E8090"),sQuery(id+"F14.wireOp",EDGE,"E8091"),sQuery(id+"F14.wireOp",EDGE,"E8092"),sQuery(id+"F14.wireOp",EDGE,"E8093"),sQuery(id+"F14.wireOp",EDGE,"E8094"),sQuery(id+"F14.wireOp",EDGE,"E8095"),sQuery(id+"F14.wireOp",EDGE,"E8096"),sQuery(id+"F14.wireOp",EDGE,"E8097"),sQuery(id+"F14.wireOp",EDGE,"E8098"),sQuery(id+"F14.wireOp",EDGE,"E8099"),sQuery(id+"F14.wireOp",EDGE,"E8100"),sQuery(id+"F14.wireOp",EDGE,"E8101"),sQuery(id+"F14.wireOp",EDGE,"E8102"),sQuery(id+"F14.wireOp",EDGE,"E8103"),sQuery(id+"F14.wireOp",EDGE,"E8104"),sQuery(id+"F14.wireOp",EDGE,"E8105"),sQuery(id+"F14.wireOp",EDGE,"E8106"),sQuery(id+"F14.wireOp",EDGE,"E8107"),sQuery(id+"F14.wireOp",EDGE,"E8108"),sQuery(id+"F14.wireOp",EDGE,"E8109"),sQuery(id+"F14.wireOp",EDGE,"E8110"),sQuery(id+"F14.wireOp",EDGE,"E8111"),sQuery(id+"F14.wireOp",EDGE,"E8112"),sQuery(id+"F14.wireOp",EDGE,"E8113"),sQuery(id+"F14.wireOp",EDGE,"E8114"),sQuery(id+"F14.wireOp",EDGE,"E8115"),sQuery(id+"F14.wireOp",EDGE,"E8116"),sQuery(id+"F14.wireOp",EDGE,"E8117"),sQuery(id+"F14.wireOp",EDGE,"E8118"),sQuery(id+"F14.wireOp",EDGE,"E8119"),sQuery(id+"F14.wireOp",EDGE,"E8120"),sQuery(id+"F14.wireOp",EDGE,"E8121"),sQuery(id+"F14.wireOp",EDGE,"E8122"),sQuery(id+"F14.wireOp",EDGE,"E8123"),sQuery(id+"F14.wireOp",EDGE,"E8124"),sQuery(id+"F14.wireOp",EDGE,"E8125"),sQuery(id+"F14.wireOp",EDGE,"E8126"),sQuery(id+"F14.wireOp",EDGE,"E8127"),sQuery(id+"F14.wireOp",EDGE,"E8128"),sQuery(id+"F14.wireOp",EDGE,"E8129"),sQuery(id+"F14.wireOp",EDGE,"E8130"),sQuery(id+"F14.wireOp",EDGE,"E8131"),sQuery(id+"F14.wireOp",EDGE,"E8132"),sQuery(id+"F14.wireOp",EDGE,"E8133"),sQuery(id+"F14.wireOp",EDGE,"E8134"),sQuery(id+"F14.wireOp",EDGE,"E8135"),sQuery(id+"F14.wireOp",EDGE,"E8136"),sQuery(id+"F14.wireOp",EDGE,"E8137"),sQuery(id+"F14.wireOp",EDGE,"E8138"),sQuery(id+"F14.wireOp",EDGE,"E8139"),sQuery(id+"F14.wireOp",EDGE,"E8140"),sQuery(id+"F14.wireOp",EDGE,"E8141"),sQuery(id+"F14.wireOp",EDGE,"E8142"),sQuery(id+"F14.wireOp",EDGE,"E8143"),sQuery(id+"F14.wireOp",EDGE,"E8144"),sQuery(id+"F14.wireOp",EDGE,"E8145"),sQuery(id+"F14.wireOp",EDGE,"E8146"),sQuery(id+"F14.wireOp",EDGE,"E8147"),sQuery(id+"F14.wireOp",EDGE,"E8148"),sQuery(id+"F14.wireOp",EDGE,"E8149"),sQuery(id+"F14.wireOp",EDGE,"E8150"),sQuery(id+"F14.wireOp",EDGE,"E8151"),sQuery(id+"F14.wireOp",EDGE,"E8152"),sQuery(id+"F14.wireOp",EDGE,"E8153"),sQuery(id+"F14.wireOp",EDGE,"E8154"),sQuery(id+"F14.wireOp",EDGE,"E8155"),sQuery(id+"F14.wireOp",EDGE,"E8156"),sQuery(id+"F14.wireOp",EDGE,"E8157"),sQuery(id+"F14.wireOp",EDGE,"E8158"),sQuery(id+"F14.wireOp",EDGE,"E8159"),sQuery(id+"F14.wireOp",EDGE,"E8160"),sQuery(id+"F14.wireOp",EDGE,"E8161"),sQuery(id+"F14.wireOp",EDGE,"E8162"),sQuery(id+"F14.wireOp",EDGE,"E8163"),sQuery(id+"F14.wireOp",EDGE,"E8164"),sQuery(id+"F14.wireOp",EDGE,"E8165"),sQuery(id+"F14.wireOp",EDGE,"E8166"),sQuery(id+"F14.wireOp",EDGE,"E8167"),sQuery(id+"F14.wireOp",EDGE,"E8168"),sQuery(id+"F14.wireOp",EDGE,"E8169"),sQuery(id+"F14.wireOp",EDGE,"E8170"),sQuery(id+"F14.wireOp",EDGE,"E8171"),sQuery(id+"F14.wireOp",EDGE,"E8172"),sQuery(id+"F14.wireOp",EDGE,"E8173"),sQuery(id+"F14.wireOp",EDGE,"E8174"),sQuery(id+"F14.wireOp",EDGE,"E8175"),sQuery(id+"F14.wireOp",EDGE,"E8176"),sQuery(id+"F14.wireOp",EDGE,"E8177"),sQuery(id+"F14.wireOp",EDGE,"E8178"),sQuery(id+"F14.wireOp",EDGE,"E8179"),sQuery(id+"F14.wireOp",EDGE,"E8180"),sQuery(id+"F14.wireOp",EDGE,"E8181"),sQuery(id+"F14.wireOp",EDGE,"E8182"),sQuery(id+"F14.wireOp",EDGE,"E8183"),sQuery(id+"F14.wireOp",EDGE,"E8184"),sQuery(id+"F14.wireOp",EDGE,"E8185"),sQuery(id+"F14.wireOp",EDGE,"E8186"),sQuery(id+"F14.wireOp",EDGE,"E8187"),sQuery(id+"F14.wireOp",EDGE,"E8188"),sQuery(id+"F14.wireOp",EDGE,"E8189"),sQuery(id+"F14.wireOp",EDGE,"E8190"),sQuery(id+"F14.wireOp",EDGE,"E8191"),sQuery(id+"F14.wireOp",EDGE,"E8192"),sQuery(id+"F14.wireOp",EDGE,"E8193"),sQuery(id+"F14.wireOp",EDGE,"E8194"),sQuery(id+"F14.wireOp",EDGE,"E8195"),sQuery(id+"F14.wireOp",EDGE,"E8196"),sQuery(id+"F14.wireOp",EDGE,"E8197"),sQuery(id+"F14.wireOp",EDGE,"E8198"),sQuery(id+"F14.wireOp",EDGE,"E8199"),sQuery(id+"F14.wireOp",EDGE,"E8200"),sQuery(id+"F14.wireOp",EDGE,"E8201"),sQuery(id+"F14.wireOp",EDGE,"E8202"),sQuery(id+"F14.wireOp",EDGE,"E8203"),sQuery(id+"F14.wireOp",EDGE,"E8204"),sQuery(id+"F14.wireOp",EDGE,"E8205"),sQuery(id+"F14.wireOp",EDGE,"E8206"),sQuery(id+"F14.wireOp",EDGE,"E8207"),sQuery(id+"F14.wireOp",EDGE,"E8208"),sQuery(id+"F14.wireOp",EDGE,"E8209"),sQuery(id+"F14.wireOp",EDGE,"E8210"),sQuery(id+"F14.wireOp",EDGE,"E8211"),sQuery(id+"F14.wireOp",EDGE,"E8212"),sQuery(id+"F14.wireOp",EDGE,"E8213"),sQuery(id+"F14.wireOp",EDGE,"E8214"),sQuery(id+"F14.wireOp",EDGE,"E8215"),sQuery(id+"F14.wireOp",EDGE,"E8216"),sQuery(id+"F14.wireOp",EDGE,"E8217"),sQuery(id+"F14.wireOp",EDGE,"E8218"),sQuery(id+"F14.wireOp",EDGE,"E8219"),sQuery(id+"F14.wireOp",EDGE,"E8220"),sQuery(id+"F14.wireOp",EDGE,"E8221"),sQuery(id+"F14.wireOp",EDGE,"E8222"),sQuery(id+"F14.wireOp",EDGE,"E8223"),sQuery(id+"F14.wireOp",EDGE,"E8224"),sQuery(id+"F14.wireOp",EDGE,"E8225"),sQuery(id+"F14.wireOp",EDGE,"E8226"),sQuery(id+"F14.wireOp",EDGE,"E8227"),sQuery(id+"F14.wireOp",EDGE,"E8228"),sQuery(id+"F14.wireOp",EDGE,"E8229"),sQuery(id+"F14.wireOp",EDGE,"E8230"),sQuery(id+"F14.wireOp",EDGE,"E8231"),sQuery(id+"F14.wireOp",EDGE,"E8232"),sQuery(id+"F14.wireOp",EDGE,"E8233"),sQuery(id+"F14.wireOp",EDGE,"E8234"),sQuery(id+"F14.wireOp",EDGE,"E8235"),sQuery(id+"F14.wireOp",EDGE,"E8236"),sQuery(id+"F14.wireOp",EDGE,"E8237"),sQuery(id+"F14.wireOp",EDGE,"E8238"),sQuery(id+"F14.wireOp",EDGE,"E8239"),sQuery(id+"F14.wireOp",EDGE,"E8240"),sQuery(id+"F14.wireOp",EDGE,"E8241"),sQuery(id+"F14.wireOp",EDGE,"E8242"),sQuery(id+"F14.wireOp",EDGE,"E8243"),sQuery(id+"F14.wireOp",EDGE,"E8244"),sQuery(id+"F14.wireOp",EDGE,"E8245"),sQuery(id+"F14.wireOp",EDGE,"E8246"),sQuery(id+"F14.wireOp",EDGE,"E8247"),sQuery(id+"F14.wireOp",EDGE,"E8248"),sQuery(id+"F14.wireOp",EDGE,"E8249"),sQuery(id+"F14.wireOp",EDGE,"E8250"),sQuery(id+"F14.wireOp",EDGE,"E8251"),sQuery(id+"F14.wireOp",EDGE,"E8252"),sQuery(id+"F14.wireOp",EDGE,"E8253"),sQuery(id+"F14.wireOp",EDGE,"E8254"),sQuery(id+"F14.wireOp",EDGE,"E8255"),sQuery(id+"F14.wireOp",EDGE,"E8256"),sQuery(id+"F14.wireOp",EDGE,"E8257"),sQuery(id+"F14.wireOp",EDGE,"E8258"),sQuery(id+"F14.wireOp",EDGE,"E8259"),sQuery(id+"F14.wireOp",EDGE,"E8260"),sQuery(id+"F14.wireOp",EDGE,"E8261"),sQuery(id+"F14.wireOp",EDGE,"E8262"),sQuery(id+"F14.wireOp",EDGE,"E8263"),sQuery(id+"F14.wireOp",EDGE,"E8264"),sQuery(id+"F14.wireOp",EDGE,"E8265"),sQuery(id+"F14.wireOp",EDGE,"E8266"),sQuery(id+"F14.wireOp",EDGE,"E8267"),sQuery(id+"F14.wireOp",EDGE,"E8268"),sQuery(id+"F14.wireOp",EDGE,"E8269"),sQuery(id+"F14.wireOp",EDGE,"E8270"),sQuery(id+"F14.wireOp",EDGE,"E8271"),sQuery(id+"F14.wireOp",EDGE,"E8272"),sQuery(id+"F14.wireOp",EDGE,"E8273"),sQuery(id+"F14.wireOp",EDGE,"E8274"),sQuery(id+"F14.wireOp",EDGE,"E8275"),sQuery(id+"F14.wireOp",EDGE,"E8276"),sQuery(id+"F14.wireOp",EDGE,"E8277"),sQuery(id+"F14.wireOp",EDGE,"E8278"),sQuery(id+"F14.wireOp",EDGE,"E8279"),sQuery(id+"F14.wireOp",EDGE,"E8280"),sQuery(id+"F14.wireOp",EDGE,"E8281"),sQuery(id+"F14.wireOp",EDGE,"E8282"),sQuery(id+"F14.wireOp",EDGE,"E8283"),sQuery(id+"F14.wireOp",EDGE,"E8284"),sQuery(id+"F14.wireOp",EDGE,"E8285"),sQuery(id+"F14.wireOp",EDGE,"E8286"),sQuery(id+"F14.wireOp",EDGE,"E8287"),sQuery(id+"F14.wireOp",EDGE,"E8288"),sQuery(id+"F14.wireOp",EDGE,"E8289"),sQuery(id+"F14.wireOp",EDGE,"E8290"),sQuery(id+"F14.wireOp",EDGE,"E8291"),sQuery(id+"F14.wireOp",EDGE,"E8292"),sQuery(id+"F14.wireOp",EDGE,"E8293"),sQuery(id+"F14.wireOp",EDGE,"E8294"),sQuery(id+"F14.wireOp",EDGE,"E8295"),sQuery(id+"F14.wireOp",EDGE,"E8296"),sQuery(id+"F14.wireOp",EDGE,"E8297"),sQuery(id+"F14.wireOp",EDGE,"E8298"),sQuery(id+"F14.wireOp",EDGE,"E8299"),sQuery(id+"F14.wireOp",EDGE,"E8300"),sQuery(id+"F14.wireOp",EDGE,"E8301"),sQuery(id+"F14.wireOp",EDGE,"E8302"),sQuery(id+"F14.wireOp",EDGE,"E8303"),sQuery(id+"F14.wireOp",EDGE,"E8304"),sQuery(id+"F14.wireOp",EDGE,"E8305"),sQuery(id+"F14.wireOp",EDGE,"E8306"),sQuery(id+"F14.wireOp",EDGE,"E8307"),sQuery(id+"F14.wireOp",EDGE,"E8308"),sQuery(id+"F14.wireOp",EDGE,"E8309"),sQuery(id+"F14.wireOp",EDGE,"E8310"),sQuery(id+"F14.wireOp",EDGE,"E8311"),sQuery(id+"F14.wireOp",EDGE,"E8312"),sQuery(id+"F14.wireOp",EDGE,"E8313"),sQuery(id+"F14.wireOp",EDGE,"E8314"),sQuery(id+"F14.wireOp",EDGE,"E8315"),sQuery(id+"F14.wireOp",EDGE,"E8316"),sQuery(id+"F14.wireOp",EDGE,"E8317"),sQuery(id+"F14.wireOp",EDGE,"E8318"),sQuery(id+"F14.wireOp",EDGE,"E8319"),sQuery(id+"F14.wireOp",EDGE,"E8320"),sQuery(id+"F14.wireOp",EDGE,"E8321"),sQuery(id+"F14.wireOp",EDGE,"E8322"),sQuery(id+"F14.wireOp",EDGE,"E8323"),sQuery(id+"F14.wireOp",EDGE,"E8324"),sQuery(id+"F14.wireOp",EDGE,"E8325"),sQuery(id+"F14.wireOp",EDGE,"E8326"),sQuery(id+"F14.wireOp",EDGE,"E8327"),sQuery(id+"F14.wireOp",EDGE,"E8328"),sQuery(id+"F14.wireOp",EDGE,"E8329"),sQuery(id+"F14.wireOp",EDGE,"E8330"),sQuery(id+"F14.wireOp",EDGE,"E8331"),sQuery(id+"F14.wireOp",EDGE,"E8332"),sQuery(id+"F14.wireOp",EDGE,"E8333"),sQuery(id+"F14.wireOp",EDGE,"E8334"),sQuery(id+"F14.wireOp",EDGE,"E8335"),sQuery(id+"F14.wireOp",EDGE,"E8336"),sQuery(id+"F14.wireOp",EDGE,"E8337"),sQuery(id+"F14.wireOp",EDGE,"E8338"),sQuery(id+"F14.wireOp",EDGE,"E8339"),sQuery(id+"F14.wireOp",EDGE,"E8340"),sQuery(id+"F14.wireOp",EDGE,"E8341"),sQuery(id+"F14.wireOp",EDGE,"E8342"),sQuery(id+"F14.wireOp",EDGE,"E8343"),sQuery(id+"F14.wireOp",EDGE,"E8344"),sQuery(id+"F14.wireOp",EDGE,"E8345"),sQuery(id+"F14.wireOp",EDGE,"E8346"),sQuery(id+"F14.wireOp",EDGE,"E8347"),sQuery(id+"F14.wireOp",EDGE,"E8348"),sQuery(id+"F14.wireOp",EDGE,"E8349"),sQuery(id+"F14.wireOp",EDGE,"E8350"),sQuery(id+"F14.wireOp",EDGE,"E8351"),sQuery(id+"F14.wireOp",EDGE,"E8352"),sQuery(id+"F14.wireOp",EDGE,"E8353"),sQuery(id+"F14.wireOp",EDGE,"E8354"),sQuery(id+"F14.wireOp",EDGE,"E8355"),sQuery(id+"F14.wireOp",EDGE,"E8356"),sQuery(id+"F14.wireOp",EDGE,"E8357"),sQuery(id+"F14.wireOp",EDGE,"E8358"),sQuery(id+"F14.wireOp",EDGE,"E8359"),sQuery(id+"F14.wireOp",EDGE,"E8360"),sQuery(id+"F14.wireOp",EDGE,"E8361"),sQuery(id+"F14.wireOp",EDGE,"E8362"),sQuery(id+"F14.wireOp",EDGE,"E8363"),sQuery(id+"F14.wireOp",EDGE,"E8364"),sQuery(id+"F14.wireOp",EDGE,"E8365"),sQuery(id+"F14.wireOp",EDGE,"E8366"),sQuery(id+"F14.wireOp",EDGE,"E8367"),sQuery(id+"F14.wireOp",EDGE,"E8368"),sQuery(id+"F14.wireOp",EDGE,"E8369"),sQuery(id+"F14.wireOp",EDGE,"E8370"),sQuery(id+"F14.wireOp",EDGE,"E8371"),sQuery(id+"F14.wireOp",EDGE,"E8372"),sQuery(id+"F14.wireOp",EDGE,"E8373"),sQuery(id+"F14.wireOp",EDGE,"E8374"),sQuery(id+"F14.wireOp",EDGE,"E8375"),sQuery(id+"F14.wireOp",EDGE,"E8376"),sQuery(id+"F14.wireOp",EDGE,"E8377"),sQuery(id+"F14.wireOp",EDGE,"E8378"),sQuery(id+"F14.wireOp",EDGE,"E8379"),sQuery(id+"F14.wireOp",EDGE,"E8380"),sQuery(id+"F14.wireOp",EDGE,"E8381"),sQuery(id+"F14.wireOp",EDGE,"E8382"),sQuery(id+"F14.wireOp",EDGE,"E8383"),sQuery(id+"F14.wireOp",EDGE,"E8384"),sQuery(id+"F14.wireOp",EDGE,"E8385"),sQuery(id+"F14.wireOp",EDGE,"E8386"),sQuery(id+"F14.wireOp",EDGE,"E8387"),sQuery(id+"F14.wireOp",EDGE,"E8388"),sQuery(id+"F14.wireOp",EDGE,"E8389"),sQuery(id+"F14.wireOp",EDGE,"E8390"),sQuery(id+"F14.wireOp",EDGE,"E8391"),sQuery(id+"F14.wireOp",EDGE,"E8392"),sQuery(id+"F14.wireOp",EDGE,"E8393"),sQuery(id+"F14.wireOp",EDGE,"E8394"),sQuery(id+"F14.wireOp",EDGE,"E8395"),sQuery(id+"F14.wireOp",EDGE,"E8396"),sQuery(id+"F14.wireOp",EDGE,"E8397"),sQuery(id+"F14.wireOp",EDGE,"E8398"),sQuery(id+"F14.wireOp",EDGE,"E8399"),sQuery(id+"F14.wireOp",EDGE,"E8400"),sQuery(id+"F14.wireOp",EDGE,"E8401"),sQuery(id+"F14.wireOp",EDGE,"E8402"),sQuery(id+"F14.wireOp",EDGE,"E8403"),sQuery(id+"F14.wireOp",EDGE,"E8404"),sQuery(id+"F14.wireOp",EDGE,"E8405"),sQuery(id+"F14.wireOp",EDGE,"E8406"),sQuery(id+"F14.wireOp",EDGE,"E8407"),sQuery(id+"F14.wireOp",EDGE,"E8408"),sQuery(id+"F14.wireOp",EDGE,"E8409"),sQuery(id+"F14.wireOp",EDGE,"E8410"),sQuery(id+"F14.wireOp",EDGE,"E8411"),sQuery(id+"F14.wireOp",EDGE,"E8412"),sQuery(id+"F14.wireOp",EDGE,"E8413"),sQuery(id+"F14.wireOp",EDGE,"E8414"),sQuery(id+"F14.wireOp",EDGE,"E8415"),sQuery(id+"F14.wireOp",EDGE,"E8416"),sQuery(id+"F14.wireOp",EDGE,"E8417"),sQuery(id+"F14.wireOp",EDGE,"E8418"),sQuery(id+"F14.wireOp",EDGE,"E8419"),sQuery(id+"F14.wireOp",EDGE,"E8420"),sQuery(id+"F14.wireOp",EDGE,"E8421"),sQuery(id+"F14.wireOp",EDGE,"E8422"),sQuery(id+"F14.wireOp",EDGE,"E8423"),sQuery(id+"F14.wireOp",EDGE,"E8424"),sQuery(id+"F14.wireOp",EDGE,"E8425"),sQuery(id+"F14.wireOp",EDGE,"E8426"),sQuery(id+"F14.wireOp",EDGE,"E8427"),sQuery(id+"F14.wireOp",EDGE,"E8428"),sQuery(id+"F14.wireOp",EDGE,"E8429"),sQuery(id+"F14.wireOp",EDGE,"E8430"),sQuery(id+"F14.wireOp",EDGE,"E8431"),sQuery(id+"F14.wireOp",EDGE,"E8432"),sQuery(id+"F14.wireOp",EDGE,"E8433"),sQuery(id+"F14.wireOp",EDGE,"E8434"),sQuery(id+"F14.wireOp",EDGE,"E8435"),sQuery(id+"F14.wireOp",EDGE,"E8436"),sQuery(id+"F14.wireOp",EDGE,"E8437"),sQuery(id+"F14.wireOp",EDGE,"E8438"),sQuery(id+"F14.wireOp",EDGE,"E8439"),sQuery(id+"F14.wireOp",EDGE,"E8440"),sQuery(id+"F14.wireOp",EDGE,"E8441"),sQuery(id+"F14.wireOp",EDGE,"E8442"),sQuery(id+"F14.wireOp",EDGE,"E8443"),sQuery(id+"F14.wireOp",EDGE,"E8444"),sQuery(id+"F14.wireOp",EDGE,"E8445"),sQuery(id+"F14.wireOp",EDGE,"E8446"),sQuery(id+"F14.wireOp",EDGE,"E8447"),sQuery(id+"F14.wireOp",EDGE,"E8448"),sQuery(id+"F14.wireOp",EDGE,"E8449"),sQuery(id+"F14.wireOp",EDGE,"E8450"),sQuery(id+"F14.wireOp",EDGE,"E8451"),sQuery(id+"F14.wireOp",EDGE,"E8452"),sQuery(id+"F14.wireOp",EDGE,"E8453"),sQuery(id+"F14.wireOp",EDGE,"E8454"),sQuery(id+"F14.wireOp",EDGE,"E8455"),sQuery(id+"F14.wireOp",EDGE,"E8456"),sQuery(id+"F14.wireOp",EDGE,"E8457"),sQuery(id+"F14.wireOp",EDGE,"E8458"),sQuery(id+"F14.wireOp",EDGE,"E8459"),sQuery(id+"F14.wireOp",EDGE,"E8460"),sQuery(id+"F14.wireOp",EDGE,"E8461"),sQuery(id+"F14.wireOp",EDGE,"E8462"),sQuery(id+"F14.wireOp",EDGE,"E8463"),sQuery(id+"F14.wireOp",EDGE,"E8464"),sQuery(id+"F14.wireOp",EDGE,"E8465"),sQuery(id+"F14.wireOp",EDGE,"E8466"),sQuery(id+"F14.wireOp",EDGE,"E8467"),sQuery(id+"F14.wireOp",EDGE,"E8468"),sQuery(id+"F14.wireOp",EDGE,"E8469"),sQuery(id+"F14.wireOp",EDGE,"E8470"),sQuery(id+"F14.wireOp",EDGE,"E8471"),sQuery(id+"F14.wireOp",EDGE,"E8472"),sQuery(id+"F14.wireOp",EDGE,"E8473"),sQuery(id+"F14.wireOp",EDGE,"E8474"),sQuery(id+"F14.wireOp",EDGE,"E8475"),sQuery(id+"F14.wireOp",EDGE,"E8476"),sQuery(id+"F14.wireOp",EDGE,"E8477"),sQuery(id+"F14.wireOp",EDGE,"E8478"),sQuery(id+"F14.wireOp",EDGE,"E8479"),sQuery(id+"F14.wireOp",EDGE,"E8480"),sQuery(id+"F14.wireOp",EDGE,"E8481"),sQuery(id+"F14.wireOp",EDGE,"E8482"),sQuery(id+"F14.wireOp",EDGE,"E8483"),sQuery(id+"F14.wireOp",EDGE,"E8484"),sQuery(id+"F14.wireOp",EDGE,"E8485"),sQuery(id+"F14.wireOp",EDGE,"E8486"),sQuery(id+"F14.wireOp",EDGE,"E8487"),sQuery(id+"F14.wireOp",EDGE,"E8488"),sQuery(id+"F14.wireOp",EDGE,"E8489"),sQuery(id+"F14.wireOp",EDGE,"E8490"),sQuery(id+"F14.wireOp",EDGE,"E8491"),sQuery(id+"F14.wireOp",EDGE,"E8492"),sQuery(id+"F14.wireOp",EDGE,"E8493"),sQuery(id+"F14.wireOp",EDGE,"E8494"),sQuery(id+"F14.wireOp",EDGE,"E8495"),sQuery(id+"F14.wireOp",EDGE,"E8496"),sQuery(id+"F14.wireOp",EDGE,"E8497"),sQuery(id+"F14.wireOp",EDGE,"E8498"),sQuery(id+"F14.wireOp",EDGE,"E8499"),sQuery(id+"F14.wireOp",EDGE,"E8500"),sQuery(id+"F14.wireOp",EDGE,"E8501"),sQuery(id+"F14.wireOp",EDGE,"E8502"),sQuery(id+"F14.wireOp",EDGE,"E8503"),sQuery(id+"F14.wireOp",EDGE,"E8504"),sQuery(id+"F14.wireOp",EDGE,"E8505"),sQuery(id+"F14.wireOp",EDGE,"E8506"),sQuery(id+"F14.wireOp",EDGE,"E8507"),sQuery(id+"F14.wireOp",EDGE,"E8508"),sQuery(id+"F14.wireOp",EDGE,"E8509"),sQuery(id+"F14.wireOp",EDGE,"E8510"),sQuery(id+"F14.wireOp",EDGE,"E8511"),sQuery(id+"F14.wireOp",EDGE,"E8512"),sQuery(id+"F14.wireOp",EDGE,"E8513"),sQuery(id+"F14.wireOp",EDGE,"E8514"),sQuery(id+"F14.wireOp",EDGE,"E8515"),sQuery(id+"F14.wireOp",EDGE,"E8516"),sQuery(id+"F14.wireOp",EDGE,"E8517"),sQuery(id+"F14.wireOp",EDGE,"E8518"),sQuery(id+"F14.wireOp",EDGE,"E8519"),sQuery(id+"F14.wireOp",EDGE,"E8520"),sQuery(id+"F14.wireOp",EDGE,"E8521"),sQuery(id+"F14.wireOp",EDGE,"E8522"),sQuery(id+"F14.wireOp",EDGE,"E8523"),sQuery(id+"F14.wireOp",EDGE,"E8524"),sQuery(id+"F14.wireOp",EDGE,"E8525"),sQuery(id+"F14.wireOp",EDGE,"E8526"),sQuery(id+"F14.wireOp",EDGE,"E8527"),sQuery(id+"F14.wireOp",EDGE,"E8528"),sQuery(id+"F14.wireOp",EDGE,"E8529"),sQuery(id+"F14.wireOp",EDGE,"E8530"),sQuery(id+"F14.wireOp",EDGE,"E8531"),sQuery(id+"F14.wireOp",EDGE,"E8532"),sQuery(id+"F14.wireOp",EDGE,"E8533"),sQuery(id+"F14.wireOp",EDGE,"E8534"),sQuery(id+"F14.wireOp",EDGE,"E8535"),sQuery(id+"F14.wireOp",EDGE,"E8536"),sQuery(id+"F14.wireOp",EDGE,"E8537"),sQuery(id+"F14.wireOp",EDGE,"E8538"),sQuery(id+"F14.wireOp",EDGE,"E8539"),sQuery(id+"F14.wireOp",EDGE,"E8540"),sQuery(id+"F14.wireOp",EDGE,"E8541"),sQuery(id+"F14.wireOp",EDGE,"E8542"),sQuery(id+"F14.wireOp",EDGE,"E8543"),sQuery(id+"F14.wireOp",EDGE,"E8544"),sQuery(id+"F14.wireOp",EDGE,"E8545"),sQuery(id+"F14.wireOp",EDGE,"E8546"),sQuery(id+"F14.wireOp",EDGE,"E8547"),sQuery(id+"F14.wireOp",EDGE,"E8548"),sQuery(id+"F14.wireOp",EDGE,"E8549"),sQuery(id+"F14.wireOp",EDGE,"E8550"),sQuery(id+"F14.wireOp",EDGE,"E8551"),sQuery(id+"F14.wireOp",EDGE,"E8552"),sQuery(id+"F14.wireOp",EDGE,"E8553"),sQuery(id+"F14.wireOp",EDGE,"E8554"),sQuery(id+"F14.wireOp",EDGE,"E8555"),sQuery(id+"F14.wireOp",EDGE,"E8556"),sQuery(id+"F14.wireOp",EDGE,"E8557"),sQuery(id+"F14.wireOp",EDGE,"E8558"),sQuery(id+"F14.wireOp",EDGE,"E8559"),sQuery(id+"F14.wireOp",EDGE,"E8560"),sQuery(id+"F14.wireOp",EDGE,"E8561"),sQuery(id+"F14.wireOp",EDGE,"E8562"),sQuery(id+"F14.wireOp",EDGE,"E8563"),sQuery(id+"F14.wireOp",EDGE,"E8564"),sQuery(id+"F14.wireOp",EDGE,"E8565"),sQuery(id+"F14.wireOp",EDGE,"E8566"),sQuery(id+"F14.wireOp",EDGE,"E8567"),sQuery(id+"F14.wireOp",EDGE,"E8568"),sQuery(id+"F14.wireOp",EDGE,"E8569"),sQuery(id+"F14.wireOp",EDGE,"E8570"),sQuery(id+"F14.wireOp",EDGE,"E8571"),sQuery(id+"F14.wireOp",EDGE,"E8572"),sQuery(id+"F14.wireOp",EDGE,"E8573"),sQuery(id+"F14.wireOp",EDGE,"E8574"),sQuery(id+"F14.wireOp",EDGE,"E8575"),sQuery(id+"F14.wireOp",EDGE,"E8576"),sQuery(id+"F14.wireOp",EDGE,"E8577"),sQuery(id+"F14.wireOp",EDGE,"E8578"),sQuery(id+"F14.wireOp",EDGE,"E8579"),sQuery(id+"F14.wireOp",EDGE,"E8580"),sQuery(id+"F14.wireOp",EDGE,"E8581"),sQuery(id+"F14.wireOp",EDGE,"E8582"),sQuery(id+"F14.wireOp",EDGE,"E8583"),sQuery(id+"F14.wireOp",EDGE,"E8584"),sQuery(id+"F14.wireOp",EDGE,"E8585"),sQuery(id+"F14.wireOp",EDGE,"E8586"),sQuery(id+"F14.wireOp",EDGE,"E8587"),sQuery(id+"F14.wireOp",EDGE,"E8588"),sQuery(id+"F14.wireOp",EDGE,"E8589"),sQuery(id+"F14.wireOp",EDGE,"E8590"),sQuery(id+"F14.wireOp",EDGE,"E8591"),sQuery(id+"F14.wireOp",EDGE,"E8592"),sQuery(id+"F14.wireOp",EDGE,"E8593"),sQuery(id+"F14.wireOp",EDGE,"E8594"),sQuery(id+"F14.wireOp",EDGE,"E8595"),sQuery(id+"F14.wireOp",EDGE,"E8596"),sQuery(id+"F14.wireOp",EDGE,"E8597"),sQuery(id+"F14.wireOp",EDGE,"E8598"),sQuery(id+"F14.wireOp",EDGE,"E8599"),sQuery(id+"F14.wireOp",EDGE,"E8600"),sQuery(id+"F14.wireOp",EDGE,"E8601"),sQuery(id+"F14.wireOp",EDGE,"E8602"),sQuery(id+"F14.wireOp",EDGE,"E8603"),sQuery(id+"F14.wireOp",EDGE,"E8604"),sQuery(id+"F14.wireOp",EDGE,"E8605"),sQuery(id+"F14.wireOp",EDGE,"E8606"),sQuery(id+"F14.wireOp",EDGE,"E8607"),sQuery(id+"F14.wireOp",EDGE,"E8608"),sQuery(id+"F14.wireOp",EDGE,"E8609"),sQuery(id+"F14.wireOp",EDGE,"E8610"),sQuery(id+"F14.wireOp",EDGE,"E8611"),sQuery(id+"F14.wireOp",EDGE,"E8612"),sQuery(id+"F14.wireOp",EDGE,"E8613"),sQuery(id+"F14.wireOp",EDGE,"E8614"),sQuery(id+"F14.wireOp",EDGE,"E8615"),sQuery(id+"F14.wireOp",EDGE,"E8616"),sQuery(id+"F14.wireOp",EDGE,"E8617"),sQuery(id+"F14.wireOp",EDGE,"E8618"),sQuery(id+"F14.wireOp",EDGE,"E8619"),sQuery(id+"F14.wireOp",EDGE,"E8620"),sQuery(id+"F14.wireOp",EDGE,"E8621"),sQuery(id+"F14.wireOp",EDGE,"E8622"),sQuery(id+"F14.wireOp",EDGE,"E8623"),sQuery(id+"F14.wireOp",EDGE,"E8624"),sQuery(id+"F14.wireOp",EDGE,"E8625"),sQuery(id+"F14.wireOp",EDGE,"E8626"),sQuery(id+"F14.wireOp",EDGE,"E8627"),sQuery(id+"F14.wireOp",EDGE,"E8628"),sQuery(id+"F14.wireOp",EDGE,"E8629"),sQuery(id+"F14.wireOp",EDGE,"E8630"),sQuery(id+"F14.wireOp",EDGE,"E8631"),sQuery(id+"F14.wireOp",EDGE,"E8632"),sQuery(id+"F14.wireOp",EDGE,"E8633"),sQuery(id+"F14.wireOp",EDGE,"E8634"),sQuery(id+"F14.wireOp",EDGE,"E8635"),sQuery(id+"F14.wireOp",EDGE,"E8636"),sQuery(id+"F14.wireOp",EDGE,"E8637"),sQuery(id+"F14.wireOp",EDGE,"E8638"),sQuery(id+"F14.wireOp",EDGE,"E8639"),sQuery(id+"F14.wireOp",EDGE,"E8640"),sQuery(id+"F14.wireOp",EDGE,"E8641"),sQuery(id+"F14.wireOp",EDGE,"E8642"),sQuery(id+"F14.wireOp",EDGE,"E8643"),sQuery(id+"F14.wireOp",EDGE,"E8644"),sQuery(id+"F14.wireOp",EDGE,"E8645"),sQuery(id+"F14.wireOp",EDGE,"E8646"),sQuery(id+"F14.wireOp",EDGE,"E8647"),sQuery(id+"F14.wireOp",EDGE,"E8648"),sQuery(id+"F14.wireOp",EDGE,"E8649"),sQuery(id+"F14.wireOp",EDGE,"E8650"),sQuery(id+"F14.wireOp",EDGE,"E8651"),sQuery(id+"F14.wireOp",EDGE,"E8652"),sQuery(id+"F14.wireOp",EDGE,"E8653"),sQuery(id+"F14.wireOp",EDGE,"E8654"),sQuery(id+"F14.wireOp",EDGE,"E8655"),sQuery(id+"F14.wireOp",EDGE,"E8656"),sQuery(id+"F14.wireOp",EDGE,"E8657"),sQuery(id+"F14.wireOp",EDGE,"E8658"),sQuery(id+"F14.wireOp",EDGE,"E8659"),sQuery(id+"F14.wireOp",EDGE,"E8660"),sQuery(id+"F14.wireOp",EDGE,"E8661"),sQuery(id+"F14.wireOp",EDGE,"E8662"),sQuery(id+"F14.wireOp",EDGE,"E8663"),sQuery(id+"F14.wireOp",EDGE,"E8664"),sQuery(id+"F14.wireOp",EDGE,"E8665"),sQuery(id+"F14.wireOp",EDGE,"E8666"),sQuery(id+"F14.wireOp",EDGE,"E8667"),sQuery(id+"F14.wireOp",EDGE,"E8668"),sQuery(id+"F14.wireOp",EDGE,"E8669"),sQuery(id+"F14.wireOp",EDGE,"E8670"),sQuery(id+"F14.wireOp",EDGE,"E8671"),sQuery(id+"F14.wireOp",EDGE,"E8672"),sQuery(id+"F14.wireOp",EDGE,"E8673"),sQuery(id+"F14.wireOp",EDGE,"E8674"),sQuery(id+"F14.wireOp",EDGE,"E8675"),sQuery(id+"F14.wireOp",EDGE,"E8676"),sQuery(id+"F14.wireOp",EDGE,"E8677"),sQuery(id+"F14.wireOp",EDGE,"E8678"),sQuery(id+"F14.wireOp",EDGE,"E8679"),sQuery(id+"F14.wireOp",EDGE,"E8680"),sQuery(id+"F14.wireOp",EDGE,"E8681"),sQuery(id+"F14.wireOp",EDGE,"E8682"),sQuery(id+"F14.wireOp",EDGE,"E8683"),sQuery(id+"F14.wireOp",EDGE,"E8684"),sQuery(id+"F14.wireOp",EDGE,"E8685"),sQuery(id+"F14.wireOp",EDGE,"E8686"),sQuery(id+"F14.wireOp",EDGE,"E8687"),sQuery(id+"F14.wireOp",EDGE,"E8688"),sQuery(id+"F14.wireOp",EDGE,"E8689"),sQuery(id+"F14.wireOp",EDGE,"E8690"),sQuery(id+"F14.wireOp",EDGE,"E8691"),sQuery(id+"F14.wireOp",EDGE,"E8692"),sQuery(id+"F14.wireOp",EDGE,"E8693"),sQuery(id+"F14.wireOp",EDGE,"E8694"),sQuery(id+"F14.wireOp",EDGE,"E8695"),sQuery(id+"F14.wireOp",EDGE,"E8696"),sQuery(id+"F14.wireOp",EDGE,"E8697"),sQuery(id+"F14.wireOp",EDGE,"E8698"),sQuery(id+"F14.wireOp",EDGE,"E8699"),sQuery(id+"F14.wireOp",EDGE,"E8700"),sQuery(id+"F14.wireOp",EDGE,"E8701"),sQuery(id+"F14.wireOp",EDGE,"E8702"),sQuery(id+"F14.wireOp",EDGE,"E8703"),sQuery(id+"F14.wireOp",EDGE,"E8704"),sQuery(id+"F14.wireOp",EDGE,"E8705"),sQuery(id+"F14.wireOp",EDGE,"E8706"),sQuery(id+"F14.wireOp",EDGE,"E8707"),sQuery(id+"F14.wireOp",EDGE,"E8708"),sQuery(id+"F14.wireOp",EDGE,"E8709"),sQuery(id+"F14.wireOp",EDGE,"E8710"),sQuery(id+"F14.wireOp",EDGE,"E8711"),sQuery(id+"F14.wireOp",EDGE,"E8712"),sQuery(id+"F14.wireOp",EDGE,"E8713"),sQuery(id+"F14.wireOp",EDGE,"E8714"),sQuery(id+"F14.wireOp",EDGE,"E8715"),sQuery(id+"F14.wireOp",EDGE,"E8716"),sQuery(id+"F14.wireOp",EDGE,"E8717"),sQuery(id+"F14.wireOp",EDGE,"E8718"),sQuery(id+"F14.wireOp",EDGE,"E8719"),sQuery(id+"F14.wireOp",EDGE,"E8720"),sQuery(id+"F14.wireOp",EDGE,"E8721"),sQuery(id+"F14.wireOp",EDGE,"E8722"),sQuery(id+"F14.wireOp",EDGE,"E8723"),sQuery(id+"F14.wireOp",EDGE,"E8724"),sQuery(id+"F14.wireOp",EDGE,"E8725"),sQuery(id+"F14.wireOp",EDGE,"E8726"),sQuery(id+"F14.wireOp",EDGE,"E8727"),sQuery(id+"F14.wireOp",EDGE,"E8728"),sQuery(id+"F14.wireOp",EDGE,"E8729"),sQuery(id+"F14.wireOp",EDGE,"E8730"),sQuery(id+"F14.wireOp",EDGE,"E8731"),sQuery(id+"F14.wireOp",EDGE,"E8732"),sQuery(id+"F14.wireOp",EDGE,"E8733"),sQuery(id+"F14.wireOp",EDGE,"E8734"),sQuery(id+"F14.wireOp",EDGE,"E8735"),sQuery(id+"F14.wireOp",EDGE,"E8736"),sQuery(id+"F14.wireOp",EDGE,"E8737"),sQuery(id+"F14.wireOp",EDGE,"E8738"),sQuery(id+"F14.wireOp",EDGE,"E8739"),sQuery(id+"F14.wireOp",EDGE,"E8740"),sQuery(id+"F14.wireOp",EDGE,"E8741"),sQuery(id+"F14.wireOp",EDGE,"E8742"),sQuery(id+"F14.wireOp",EDGE,"E8743"),sQuery(id+"F14.wireOp",EDGE,"E8744"),sQuery(id+"F14.wireOp",EDGE,"E8745"),sQuery(id+"F14.wireOp",EDGE,"E8746"),sQuery(id+"F14.wireOp",EDGE,"E8747"),sQuery(id+"F14.wireOp",EDGE,"E8748"),sQuery(id+"F14.wireOp",EDGE,"E8749"),sQuery(id+"F14.wireOp",EDGE,"E8750"),sQuery(id+"F14.wireOp",EDGE,"E8751"),sQuery(id+"F14.wireOp",EDGE,"E8752"),sQuery(id+"F14.wireOp",EDGE,"E8753"),sQuery(id+"F14.wireOp",EDGE,"E8754"),sQuery(id+"F14.wireOp",EDGE,"E8755"),sQuery(id+"F14.wireOp",EDGE,"E8756"),sQuery(id+"F14.wireOp",EDGE,"E8757"),sQuery(id+"F14.wireOp",EDGE,"E8758"),sQuery(id+"F14.wireOp",EDGE,"E8759"),sQuery(id+"F14.wireOp",EDGE,"E8760"),sQuery(id+"F14.wireOp",EDGE,"E8761"),sQuery(id+"F14.wireOp",EDGE,"E8762"),sQuery(id+"F14.wireOp",EDGE,"E8763"),sQuery(id+"F14.wireOp",EDGE,"E8764"),sQuery(id+"F14.wireOp",EDGE,"E8765")])]});
            var Q1;
            Q1=sQuery(id+"F5.wireOp",EDGE,"E2623");
            transform(context, id + "F16", {"entities" : qUnion([Q0]), "transformType" : TransformType.ROTATION, "transformAxis" : qUnion([Q1]), "angle" : 90 * degree, "oppositeDirection" : true, "makeCopy" : false});
        }
    });
